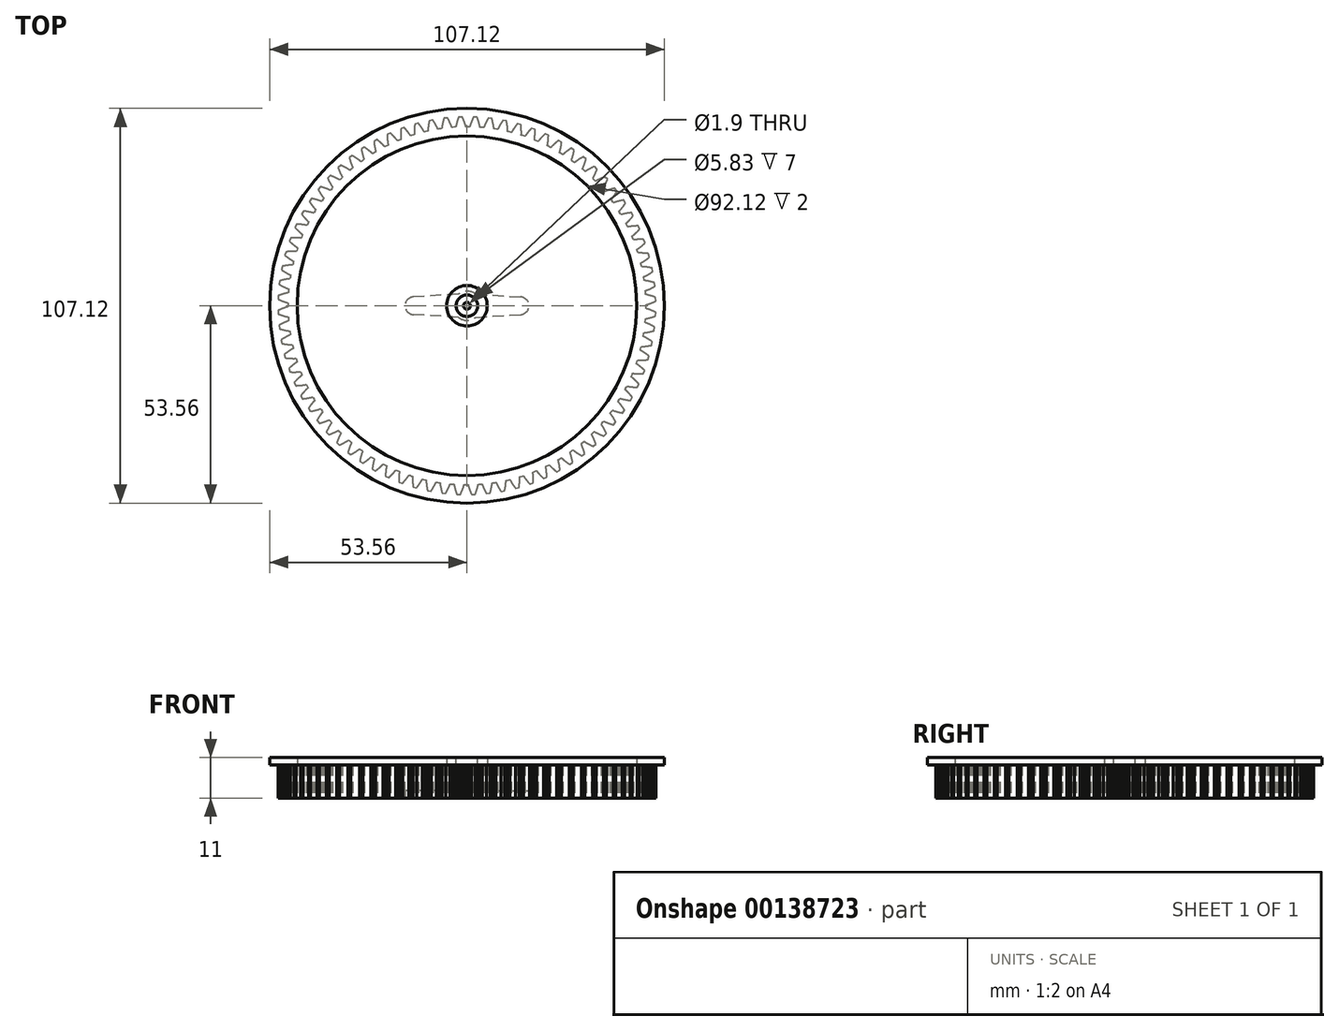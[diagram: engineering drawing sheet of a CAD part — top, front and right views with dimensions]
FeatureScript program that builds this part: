
annotation { "Feature Type Name" : "Feature", "Feature Type Description" : "" }
export const myFeature = defineFeature(function(context is Context, id is Id, definition is map)
    precondition{}
    {
        {
            var Q0;
            Q0=qCreatedBy(makeId("Top.planeOp"),FACE);
            var sketch = newSketch(context, id + "F0", { "sketchPlane" : qUnion([Q0])});
            skLineSegment(sketch, "E0", {"start": v(48.56, 0) * mm, "end": v(48.57, 0.28) * mm});
            skLineSegment(sketch, "E1", {"start": v(48.57, 0.28) * mm, "end": v(48.62, 0.3) * mm});
            skLineSegment(sketch, "E2", {"start": v(48.62, 0.3) * mm, "end": v(48.67, 0.3) * mm});
            skLineSegment(sketch, "E3", {"start": v(48.67, 0.3) * mm, "end": v(48.73, 0.32) * mm});
            skLineSegment(sketch, "E4", {"start": v(48.73, 0.32) * mm, "end": v(48.78, 0.34) * mm});
            skLineSegment(sketch, "E5", {"start": v(48.78, 0.34) * mm, "end": v(48.84, 0.35) * mm});
            skLineSegment(sketch, "E6", {"start": v(48.84, 0.35) * mm, "end": v(48.9, 0.37) * mm});
            skLineSegment(sketch, "E7", {"start": v(48.9, 0.37) * mm, "end": v(48.95, 0.39) * mm});
            skLineSegment(sketch, "E8", {"start": v(48.95, 0.39) * mm, "end": v(49, 0.4) * mm});
            skLineSegment(sketch, "E9", {"start": v(49, 0.4) * mm, "end": v(49.07, 0.42) * mm});
            skLineSegment(sketch, "E10", {"start": v(49.07, 0.42) * mm, "end": v(49.13, 0.44) * mm});
            skLineSegment(sketch, "E11", {"start": v(49.13, 0.44) * mm, "end": v(49.19, 0.46) * mm});
            skLineSegment(sketch, "E12", {"start": v(49.19, 0.46) * mm, "end": v(49.25, 0.48) * mm});
            skLineSegment(sketch, "E13", {"start": v(49.25, 0.48) * mm, "end": v(49.3, 0.5) * mm});
            skLineSegment(sketch, "E14", {"start": v(49.3, 0.5) * mm, "end": v(49.37, 0.52) * mm});
            skLineSegment(sketch, "E15", {"start": v(49.37, 0.52) * mm, "end": v(49.43, 0.54) * mm});
            skLineSegment(sketch, "E16", {"start": v(49.43, 0.54) * mm, "end": v(49.5, 0.56) * mm});
            skLineSegment(sketch, "E17", {"start": v(49.5, 0.56) * mm, "end": v(49.56, 0.59) * mm});
            skLineSegment(sketch, "E18", {"start": v(49.56, 0.59) * mm, "end": v(49.63, 0.61) * mm});
            skLineSegment(sketch, "E19", {"start": v(49.63, 0.61) * mm, "end": v(49.7, 0.63) * mm});
            skLineSegment(sketch, "E20", {"start": v(49.7, 0.63) * mm, "end": v(49.76, 0.66) * mm});
            skLineSegment(sketch, "E21", {"start": v(49.76, 0.66) * mm, "end": v(49.83, 0.68) * mm});
            skLineSegment(sketch, "E22", {"start": v(49.83, 0.68) * mm, "end": v(49.9, 0.7) * mm});
            skLineSegment(sketch, "E23", {"start": v(49.9, 0.7) * mm, "end": v(49.97, 0.73) * mm});
            skLineSegment(sketch, "E24", {"start": v(49.97, 0.73) * mm, "end": v(50.04, 0.76) * mm});
            skLineSegment(sketch, "E25", {"start": v(50.04, 0.76) * mm, "end": v(50.1, 0.79) * mm});
            skLineSegment(sketch, "E26", {"start": v(50.1, 0.79) * mm, "end": v(50.18, 0.82) * mm});
            skLineSegment(sketch, "E27", {"start": v(50.18, 0.82) * mm, "end": v(50.25, 0.84) * mm});
            skLineSegment(sketch, "E28", {"start": v(50.25, 0.84) * mm, "end": v(50.32, 0.87) * mm});
            skLineSegment(sketch, "E29", {"start": v(50.32, 0.87) * mm, "end": v(50.4, 0.9) * mm});
            skLineSegment(sketch, "E30", {"start": v(50.4, 0.9) * mm, "end": v(50.47, 0.93) * mm});
            skLineSegment(sketch, "E31", {"start": v(50.47, 0.93) * mm, "end": v(50.54, 0.97) * mm});
            skLineSegment(sketch, "E32", {"start": v(50.54, 0.97) * mm, "end": v(50.62, 1) * mm});
            skLineSegment(sketch, "E33", {"start": v(50.62, 1) * mm, "end": v(50.7, 1.03) * mm});
            skLineSegment(sketch, "E34", {"start": v(50.7, 1.03) * mm, "end": v(50.77, 1.06) * mm});
            skLineSegment(sketch, "E35", {"start": v(50.77, 1.06) * mm, "end": v(50.85, 1.1) * mm});
            skLineSegment(sketch, "E36", {"start": v(50.85, 1.1) * mm, "end": v(50.93, 1.13) * mm});
            skLineSegment(sketch, "E37", {"start": v(50.93, 1.13) * mm, "end": v(51, 1.17) * mm});
            skLineSegment(sketch, "E38", {"start": v(51, 1.17) * mm, "end": v(51.09, 1.2) * mm});
            skLineSegment(sketch, "E39", {"start": v(51.09, 1.2) * mm, "end": v(51.17, 1.24) * mm});
            skLineSegment(sketch, "E40", {"start": v(51.17, 1.24) * mm, "end": v(51.23, 1.28) * mm});
            skLineSegment(sketch, "E41", {"start": v(51.23, 1.28) * mm, "end": v(51.2, 2.24) * mm});
            skLineSegment(sketch, "E42", {"start": v(51.2, 2.24) * mm, "end": v(51.13, 2.27) * mm});
            skLineSegment(sketch, "E43", {"start": v(51.13, 2.27) * mm, "end": v(51.05, 2.3) * mm});
            skLineSegment(sketch, "E44", {"start": v(51.05, 2.3) * mm, "end": v(50.97, 2.34) * mm});
            skLineSegment(sketch, "E45", {"start": v(50.97, 2.34) * mm, "end": v(50.89, 2.37) * mm});
            skLineSegment(sketch, "E46", {"start": v(50.89, 2.37) * mm, "end": v(50.8, 2.4) * mm});
            skLineSegment(sketch, "E47", {"start": v(50.8, 2.4) * mm, "end": v(50.73, 2.42) * mm});
            skLineSegment(sketch, "E48", {"start": v(50.73, 2.42) * mm, "end": v(50.65, 2.45) * mm});
            skLineSegment(sketch, "E49", {"start": v(50.65, 2.45) * mm, "end": v(50.57, 2.48) * mm});
            skLineSegment(sketch, "E50", {"start": v(50.57, 2.48) * mm, "end": v(50.5, 2.5) * mm});
            skLineSegment(sketch, "E51", {"start": v(50.5, 2.5) * mm, "end": v(50.41, 2.53) * mm});
            skLineSegment(sketch, "E52", {"start": v(50.41, 2.53) * mm, "end": v(50.34, 2.56) * mm});
            skLineSegment(sketch, "E53", {"start": v(50.34, 2.56) * mm, "end": v(50.26, 2.58) * mm});
            skLineSegment(sketch, "E54", {"start": v(50.26, 2.58) * mm, "end": v(50.19, 2.6) * mm});
            skLineSegment(sketch, "E55", {"start": v(50.19, 2.6) * mm, "end": v(50.11, 2.63) * mm});
            skLineSegment(sketch, "E56", {"start": v(50.11, 2.63) * mm, "end": v(50.04, 2.65) * mm});
            skLineSegment(sketch, "E57", {"start": v(50.04, 2.65) * mm, "end": v(49.97, 2.67) * mm});
            skLineSegment(sketch, "E58", {"start": v(49.97, 2.67) * mm, "end": v(49.9, 2.7) * mm});
            skLineSegment(sketch, "E59", {"start": v(49.9, 2.7) * mm, "end": v(49.83, 2.72) * mm});
            skLineSegment(sketch, "E60", {"start": v(49.83, 2.72) * mm, "end": v(49.76, 2.74) * mm});
            skLineSegment(sketch, "E61", {"start": v(49.76, 2.74) * mm, "end": v(49.69, 2.76) * mm});
            skLineSegment(sketch, "E62", {"start": v(49.69, 2.76) * mm, "end": v(49.62, 2.78) * mm});
            skLineSegment(sketch, "E63", {"start": v(49.62, 2.78) * mm, "end": v(49.55, 2.8) * mm});
            skLineSegment(sketch, "E64", {"start": v(49.55, 2.8) * mm, "end": v(49.49, 2.81) * mm});
            skLineSegment(sketch, "E65", {"start": v(49.49, 2.81) * mm, "end": v(49.42, 2.83) * mm});
            skLineSegment(sketch, "E66", {"start": v(49.42, 2.83) * mm, "end": v(49.35, 2.85) * mm});
            skLineSegment(sketch, "E67", {"start": v(49.35, 2.85) * mm, "end": v(49.29, 2.87) * mm});
            skLineSegment(sketch, "E68", {"start": v(49.29, 2.87) * mm, "end": v(49.23, 2.88) * mm});
            skLineSegment(sketch, "E69", {"start": v(49.23, 2.88) * mm, "end": v(49.16, 2.9) * mm});
            skLineSegment(sketch, "E70", {"start": v(49.16, 2.9) * mm, "end": v(49.1, 2.91) * mm});
            skLineSegment(sketch, "E71", {"start": v(49.1, 2.91) * mm, "end": v(49.04, 2.93) * mm});
            skLineSegment(sketch, "E72", {"start": v(49.04, 2.93) * mm, "end": v(48.98, 2.94) * mm});
            skLineSegment(sketch, "E73", {"start": v(48.98, 2.94) * mm, "end": v(48.92, 2.96) * mm});
            skLineSegment(sketch, "E74", {"start": v(48.92, 2.96) * mm, "end": v(48.86, 2.97) * mm});
            skLineSegment(sketch, "E75", {"start": v(48.86, 2.97) * mm, "end": v(48.8, 2.98) * mm});
            skLineSegment(sketch, "E76", {"start": v(48.8, 2.98) * mm, "end": v(48.75, 3) * mm});
            skLineSegment(sketch, "E77", {"start": v(48.75, 3) * mm, "end": v(48.69, 3) * mm});
            skLineSegment(sketch, "E78", {"start": v(48.69, 3) * mm, "end": v(48.63, 3.02) * mm});
            skLineSegment(sketch, "E79", {"start": v(48.63, 3.02) * mm, "end": v(48.58, 3.03) * mm});
            skLineSegment(sketch, "E80", {"start": v(48.58, 3.03) * mm, "end": v(48.53, 3.04) * mm});
            skLineSegment(sketch, "E81", {"start": v(48.53, 3.04) * mm, "end": v(48.47, 3.05) * mm});
            skLineSegment(sketch, "E82", {"start": v(48.47, 3.05) * mm, "end": v(48.45, 3.33) * mm});
            skLineSegment(sketch, "E83", {"start": v(48.45, 3.33) * mm, "end": v(48.41, 3.81) * mm});
            skLineSegment(sketch, "E84", {"start": v(48.41, 3.81) * mm, "end": v(48.4, 4.09) * mm});
            skLineSegment(sketch, "E85", {"start": v(48.4, 4.09) * mm, "end": v(48.45, 4.1) * mm});
            skLineSegment(sketch, "E86", {"start": v(48.45, 4.1) * mm, "end": v(48.5, 4.13) * mm});
            skLineSegment(sketch, "E87", {"start": v(48.5, 4.13) * mm, "end": v(48.55, 4.14) * mm});
            skLineSegment(sketch, "E88", {"start": v(48.55, 4.14) * mm, "end": v(48.6, 4.16) * mm});
            skLineSegment(sketch, "E89", {"start": v(48.6, 4.16) * mm, "end": v(48.66, 4.19) * mm});
            skLineSegment(sketch, "E90", {"start": v(48.66, 4.19) * mm, "end": v(48.71, 4.2) * mm});
            skLineSegment(sketch, "E91", {"start": v(48.71, 4.2) * mm, "end": v(48.77, 4.23) * mm});
            skLineSegment(sketch, "E92", {"start": v(48.77, 4.23) * mm, "end": v(48.82, 4.25) * mm});
            skLineSegment(sketch, "E93", {"start": v(48.82, 4.25) * mm, "end": v(48.88, 4.27) * mm});
            skLineSegment(sketch, "E94", {"start": v(48.88, 4.27) * mm, "end": v(48.94, 4.3) * mm});
            skLineSegment(sketch, "E95", {"start": v(48.94, 4.3) * mm, "end": v(49, 4.32) * mm});
            skLineSegment(sketch, "E96", {"start": v(49, 4.32) * mm, "end": v(49.06, 4.34) * mm});
            skLineSegment(sketch, "E97", {"start": v(49.06, 4.34) * mm, "end": v(49.12, 4.37) * mm});
            skLineSegment(sketch, "E98", {"start": v(49.12, 4.37) * mm, "end": v(49.18, 4.4) * mm});
            skLineSegment(sketch, "E99", {"start": v(49.18, 4.4) * mm, "end": v(49.24, 4.42) * mm});
            skLineSegment(sketch, "E100", {"start": v(49.24, 4.42) * mm, "end": v(49.3, 4.45) * mm});
            skLineSegment(sketch, "E101", {"start": v(49.3, 4.45) * mm, "end": v(49.36, 4.47) * mm});
            skLineSegment(sketch, "E102", {"start": v(49.36, 4.47) * mm, "end": v(49.43, 4.5) * mm});
            skLineSegment(sketch, "E103", {"start": v(49.43, 4.5) * mm, "end": v(49.5, 4.53) * mm});
            skLineSegment(sketch, "E104", {"start": v(49.5, 4.53) * mm, "end": v(49.56, 4.56) * mm});
            skLineSegment(sketch, "E105", {"start": v(49.56, 4.56) * mm, "end": v(49.62, 4.6) * mm});
            skLineSegment(sketch, "E106", {"start": v(49.62, 4.6) * mm, "end": v(49.69, 4.62) * mm});
            skLineSegment(sketch, "E107", {"start": v(49.69, 4.62) * mm, "end": v(49.75, 4.65) * mm});
            skLineSegment(sketch, "E108", {"start": v(49.75, 4.65) * mm, "end": v(49.82, 4.68) * mm});
            skLineSegment(sketch, "E109", {"start": v(49.82, 4.68) * mm, "end": v(49.89, 4.72) * mm});
            skLineSegment(sketch, "E110", {"start": v(49.89, 4.72) * mm, "end": v(49.96, 4.75) * mm});
            skLineSegment(sketch, "E111", {"start": v(49.96, 4.75) * mm, "end": v(50.03, 4.78) * mm});
            skLineSegment(sketch, "E112", {"start": v(50.03, 4.78) * mm, "end": v(50.1, 4.82) * mm});
            skLineSegment(sketch, "E113", {"start": v(50.1, 4.82) * mm, "end": v(50.17, 4.85) * mm});
            skLineSegment(sketch, "E114", {"start": v(50.17, 4.85) * mm, "end": v(50.24, 4.9) * mm});
            skLineSegment(sketch, "E115", {"start": v(50.24, 4.9) * mm, "end": v(50.31, 4.93) * mm});
            skLineSegment(sketch, "E116", {"start": v(50.31, 4.93) * mm, "end": v(50.38, 4.97) * mm});
            skLineSegment(sketch, "E117", {"start": v(50.38, 4.97) * mm, "end": v(50.46, 5) * mm});
            skLineSegment(sketch, "E118", {"start": v(50.46, 5) * mm, "end": v(50.53, 5.04) * mm});
            skLineSegment(sketch, "E119", {"start": v(50.53, 5.04) * mm, "end": v(50.6, 5.08) * mm});
            skLineSegment(sketch, "E120", {"start": v(50.6, 5.08) * mm, "end": v(50.68, 5.12) * mm});
            skLineSegment(sketch, "E121", {"start": v(50.68, 5.12) * mm, "end": v(50.76, 5.16) * mm});
            skLineSegment(sketch, "E122", {"start": v(50.76, 5.16) * mm, "end": v(50.83, 5.2) * mm});
            skLineSegment(sketch, "E123", {"start": v(50.83, 5.2) * mm, "end": v(50.91, 5.25) * mm});
            skLineSegment(sketch, "E124", {"start": v(50.91, 5.25) * mm, "end": v(50.98, 5.3) * mm});
            skLineSegment(sketch, "E125", {"start": v(50.98, 5.3) * mm, "end": v(50.87, 6.25) * mm});
            skLineSegment(sketch, "E126", {"start": v(50.87, 6.25) * mm, "end": v(50.8, 6.28) * mm});
            skLineSegment(sketch, "E127", {"start": v(50.8, 6.28) * mm, "end": v(50.7, 6.3) * mm});
            skLineSegment(sketch, "E128", {"start": v(50.7, 6.3) * mm, "end": v(50.63, 6.33) * mm});
            skLineSegment(sketch, "E129", {"start": v(50.63, 6.33) * mm, "end": v(50.54, 6.35) * mm});
            skLineSegment(sketch, "E130", {"start": v(50.54, 6.35) * mm, "end": v(50.46, 6.37) * mm});
            skLineSegment(sketch, "E131", {"start": v(50.46, 6.37) * mm, "end": v(50.38, 6.4) * mm});
            skLineSegment(sketch, "E132", {"start": v(50.38, 6.4) * mm, "end": v(50.3, 6.42) * mm});
            skLineSegment(sketch, "E133", {"start": v(50.3, 6.42) * mm, "end": v(50.22, 6.44) * mm});
            skLineSegment(sketch, "E134", {"start": v(50.22, 6.44) * mm, "end": v(50.14, 6.46) * mm});
            skLineSegment(sketch, "E135", {"start": v(50.14, 6.46) * mm, "end": v(50.06, 6.48) * mm});
            skLineSegment(sketch, "E136", {"start": v(50.06, 6.48) * mm, "end": v(49.98, 6.5) * mm});
            skLineSegment(sketch, "E137", {"start": v(49.98, 6.5) * mm, "end": v(49.9, 6.52) * mm});
            skLineSegment(sketch, "E138", {"start": v(49.9, 6.52) * mm, "end": v(49.83, 6.53) * mm});
            skLineSegment(sketch, "E139", {"start": v(49.83, 6.53) * mm, "end": v(49.75, 6.55) * mm});
            skLineSegment(sketch, "E140", {"start": v(49.75, 6.55) * mm, "end": v(49.68, 6.57) * mm});
            skLineSegment(sketch, "E141", {"start": v(49.68, 6.57) * mm, "end": v(49.6, 6.59) * mm});
            skLineSegment(sketch, "E142", {"start": v(49.6, 6.59) * mm, "end": v(49.53, 6.6) * mm});
            skLineSegment(sketch, "E143", {"start": v(49.53, 6.6) * mm, "end": v(49.46, 6.62) * mm});
            skLineSegment(sketch, "E144", {"start": v(49.46, 6.62) * mm, "end": v(49.39, 6.63) * mm});
            skLineSegment(sketch, "E145", {"start": v(49.39, 6.63) * mm, "end": v(49.32, 6.65) * mm});
            skLineSegment(sketch, "E146", {"start": v(49.32, 6.65) * mm, "end": v(49.25, 6.66) * mm});
            skLineSegment(sketch, "E147", {"start": v(49.25, 6.66) * mm, "end": v(49.18, 6.67) * mm});
            skLineSegment(sketch, "E148", {"start": v(49.18, 6.67) * mm, "end": v(49.11, 6.69) * mm});
            skLineSegment(sketch, "E149", {"start": v(49.11, 6.69) * mm, "end": v(49.05, 6.7) * mm});
            skLineSegment(sketch, "E150", {"start": v(49.05, 6.7) * mm, "end": v(48.98, 6.71) * mm});
            skLineSegment(sketch, "E151", {"start": v(48.98, 6.71) * mm, "end": v(48.91, 6.72) * mm});
            skLineSegment(sketch, "E152", {"start": v(48.91, 6.72) * mm, "end": v(48.85, 6.74) * mm});
            skLineSegment(sketch, "E153", {"start": v(48.85, 6.74) * mm, "end": v(48.78, 6.75) * mm});
            skLineSegment(sketch, "E154", {"start": v(48.78, 6.75) * mm, "end": v(48.72, 6.76) * mm});
            skLineSegment(sketch, "E155", {"start": v(48.72, 6.76) * mm, "end": v(48.66, 6.77) * mm});
            skLineSegment(sketch, "E156", {"start": v(48.66, 6.77) * mm, "end": v(48.6, 6.78) * mm});
            skLineSegment(sketch, "E157", {"start": v(48.6, 6.78) * mm, "end": v(48.54, 6.79) * mm});
            skLineSegment(sketch, "E158", {"start": v(48.54, 6.79) * mm, "end": v(48.48, 6.8) * mm});
            skLineSegment(sketch, "E159", {"start": v(48.48, 6.8) * mm, "end": v(48.42, 6.8) * mm});
            skLineSegment(sketch, "E160", {"start": v(48.42, 6.8) * mm, "end": v(48.36, 6.81) * mm});
            skLineSegment(sketch, "E161", {"start": v(48.36, 6.81) * mm, "end": v(48.3, 6.82) * mm});
            skLineSegment(sketch, "E162", {"start": v(48.3, 6.82) * mm, "end": v(48.25, 6.83) * mm});
            skLineSegment(sketch, "E163", {"start": v(48.25, 6.83) * mm, "end": v(48.2, 6.83) * mm});
            skLineSegment(sketch, "E164", {"start": v(48.2, 6.83) * mm, "end": v(48.14, 6.84) * mm});
            skLineSegment(sketch, "E165", {"start": v(48.14, 6.84) * mm, "end": v(48.08, 6.85) * mm});
            skLineSegment(sketch, "E166", {"start": v(48.08, 6.85) * mm, "end": v(48.04, 7.12) * mm});
            skLineSegment(sketch, "E167", {"start": v(48.04, 7.12) * mm, "end": v(47.96, 7.6) * mm});
            skLineSegment(sketch, "E168", {"start": v(47.96, 7.6) * mm, "end": v(47.93, 7.87) * mm});
            skLineSegment(sketch, "E169", {"start": v(47.93, 7.87) * mm, "end": v(47.98, 7.9) * mm});
            skLineSegment(sketch, "E170", {"start": v(47.98, 7.9) * mm, "end": v(48.03, 7.92) * mm});
            skLineSegment(sketch, "E171", {"start": v(48.03, 7.92) * mm, "end": v(48.08, 7.94) * mm});
            skLineSegment(sketch, "E172", {"start": v(48.08, 7.94) * mm, "end": v(48.13, 7.97) * mm});
            skLineSegment(sketch, "E173", {"start": v(48.13, 7.97) * mm, "end": v(48.18, 7.99) * mm});
            skLineSegment(sketch, "E174", {"start": v(48.18, 7.99) * mm, "end": v(48.23, 8.01) * mm});
            skLineSegment(sketch, "E175", {"start": v(48.23, 8.01) * mm, "end": v(48.29, 8.04) * mm});
            skLineSegment(sketch, "E176", {"start": v(48.29, 8.04) * mm, "end": v(48.34, 8.07) * mm});
            skLineSegment(sketch, "E177", {"start": v(48.34, 8.07) * mm, "end": v(48.4, 8.1) * mm});
            skLineSegment(sketch, "E178", {"start": v(48.4, 8.1) * mm, "end": v(48.45, 8.12) * mm});
            skLineSegment(sketch, "E179", {"start": v(48.45, 8.12) * mm, "end": v(48.5, 8.15) * mm});
            skLineSegment(sketch, "E180", {"start": v(48.5, 8.15) * mm, "end": v(48.56, 8.18) * mm});
            skLineSegment(sketch, "E181", {"start": v(48.56, 8.18) * mm, "end": v(48.62, 8.2) * mm});
            skLineSegment(sketch, "E182", {"start": v(48.62, 8.2) * mm, "end": v(48.68, 8.24) * mm});
            skLineSegment(sketch, "E183", {"start": v(48.68, 8.24) * mm, "end": v(48.74, 8.27) * mm});
            skLineSegment(sketch, "E184", {"start": v(48.74, 8.27) * mm, "end": v(48.8, 8.3) * mm});
            skLineSegment(sketch, "E185", {"start": v(48.8, 8.3) * mm, "end": v(48.86, 8.33) * mm});
            skLineSegment(sketch, "E186", {"start": v(48.86, 8.33) * mm, "end": v(48.92, 8.37) * mm});
            skLineSegment(sketch, "E187", {"start": v(48.92, 8.37) * mm, "end": v(48.98, 8.4) * mm});
            skLineSegment(sketch, "E188", {"start": v(48.98, 8.4) * mm, "end": v(49.04, 8.43) * mm});
            skLineSegment(sketch, "E189", {"start": v(49.04, 8.43) * mm, "end": v(49.1, 8.47) * mm});
            skLineSegment(sketch, "E190", {"start": v(49.1, 8.47) * mm, "end": v(49.17, 8.5) * mm});
            skLineSegment(sketch, "E191", {"start": v(49.17, 8.5) * mm, "end": v(49.24, 8.54) * mm});
            skLineSegment(sketch, "E192", {"start": v(49.24, 8.54) * mm, "end": v(49.3, 8.58) * mm});
            skLineSegment(sketch, "E193", {"start": v(49.3, 8.58) * mm, "end": v(49.37, 8.62) * mm});
            skLineSegment(sketch, "E194", {"start": v(49.37, 8.62) * mm, "end": v(49.43, 8.66) * mm});
            skLineSegment(sketch, "E195", {"start": v(49.43, 8.66) * mm, "end": v(49.5, 8.7) * mm});
            skLineSegment(sketch, "E196", {"start": v(49.5, 8.7) * mm, "end": v(49.57, 8.73) * mm});
            skLineSegment(sketch, "E197", {"start": v(49.57, 8.73) * mm, "end": v(49.63, 8.78) * mm});
            skLineSegment(sketch, "E198", {"start": v(49.63, 8.78) * mm, "end": v(49.7, 8.82) * mm});
            skLineSegment(sketch, "E199", {"start": v(49.7, 8.82) * mm, "end": v(49.77, 8.86) * mm});
            skLineSegment(sketch, "E200", {"start": v(49.77, 8.86) * mm, "end": v(49.84, 8.9) * mm});
            skLineSegment(sketch, "E201", {"start": v(49.84, 8.9) * mm, "end": v(49.91, 8.95) * mm});
            skLineSegment(sketch, "E202", {"start": v(49.91, 8.95) * mm, "end": v(49.98, 9) * mm});
            skLineSegment(sketch, "E203", {"start": v(49.98, 9) * mm, "end": v(50.05, 9.04) * mm});
            skLineSegment(sketch, "E204", {"start": v(50.05, 9.04) * mm, "end": v(50.12, 9.08) * mm});
            skLineSegment(sketch, "E205", {"start": v(50.12, 9.08) * mm, "end": v(50.2, 9.13) * mm});
            skLineSegment(sketch, "E206", {"start": v(50.2, 9.13) * mm, "end": v(50.27, 9.18) * mm});
            skLineSegment(sketch, "E207", {"start": v(50.27, 9.18) * mm, "end": v(50.34, 9.23) * mm});
            skLineSegment(sketch, "E208", {"start": v(50.34, 9.23) * mm, "end": v(50.4, 9.28) * mm});
            skLineSegment(sketch, "E209", {"start": v(50.4, 9.28) * mm, "end": v(50.22, 10.22) * mm});
            skLineSegment(sketch, "E210", {"start": v(50.22, 10.22) * mm, "end": v(50.15, 10.24) * mm});
            skLineSegment(sketch, "E211", {"start": v(50.15, 10.24) * mm, "end": v(50.06, 10.26) * mm});
            skLineSegment(sketch, "E212", {"start": v(50.06, 10.26) * mm, "end": v(49.97, 10.28) * mm});
            skLineSegment(sketch, "E213", {"start": v(49.97, 10.28) * mm, "end": v(49.89, 10.3) * mm});
            skLineSegment(sketch, "E214", {"start": v(49.89, 10.3) * mm, "end": v(49.8, 10.31) * mm});
            skLineSegment(sketch, "E215", {"start": v(49.8, 10.31) * mm, "end": v(49.72, 10.33) * mm});
            skLineSegment(sketch, "E216", {"start": v(49.72, 10.33) * mm, "end": v(49.64, 10.34) * mm});
            skLineSegment(sketch, "E217", {"start": v(49.64, 10.34) * mm, "end": v(49.56, 10.36) * mm});
            skLineSegment(sketch, "E218", {"start": v(49.56, 10.36) * mm, "end": v(49.48, 10.37) * mm});
            skLineSegment(sketch, "E219", {"start": v(49.48, 10.37) * mm, "end": v(49.4, 10.39) * mm});
            skLineSegment(sketch, "E220", {"start": v(49.4, 10.39) * mm, "end": v(49.32, 10.4) * mm});
            skLineSegment(sketch, "E221", {"start": v(49.32, 10.4) * mm, "end": v(49.24, 10.41) * mm});
            skLineSegment(sketch, "E222", {"start": v(49.24, 10.41) * mm, "end": v(49.16, 10.42) * mm});
            skLineSegment(sketch, "E223", {"start": v(49.16, 10.42) * mm, "end": v(49.09, 10.44) * mm});
            skLineSegment(sketch, "E224", {"start": v(49.09, 10.44) * mm, "end": v(49.01, 10.45) * mm});
            skLineSegment(sketch, "E225", {"start": v(49.01, 10.45) * mm, "end": v(48.94, 10.46) * mm});
            skLineSegment(sketch, "E226", {"start": v(48.94, 10.46) * mm, "end": v(48.86, 10.47) * mm});
            skLineSegment(sketch, "E227", {"start": v(48.86, 10.47) * mm, "end": v(48.79, 10.48) * mm});
            skLineSegment(sketch, "E228", {"start": v(48.79, 10.48) * mm, "end": v(48.72, 10.49) * mm});
            skLineSegment(sketch, "E229", {"start": v(48.72, 10.49) * mm, "end": v(48.65, 10.5) * mm});
            skLineSegment(sketch, "E230", {"start": v(48.65, 10.5) * mm, "end": v(48.57, 10.5) * mm});
            skLineSegment(sketch, "E231", {"start": v(48.57, 10.5) * mm, "end": v(48.5, 10.51) * mm});
            skLineSegment(sketch, "E232", {"start": v(48.5, 10.51) * mm, "end": v(48.44, 10.52) * mm});
            skLineSegment(sketch, "E233", {"start": v(48.44, 10.52) * mm, "end": v(48.37, 10.53) * mm});
            skLineSegment(sketch, "E234", {"start": v(48.37, 10.53) * mm, "end": v(48.3, 10.54) * mm});
            skLineSegment(sketch, "E235", {"start": v(48.3, 10.54) * mm, "end": v(48.23, 10.54) * mm});
            skLineSegment(sketch, "E236", {"start": v(48.23, 10.54) * mm, "end": v(48.17, 10.55) * mm});
            skLineSegment(sketch, "E237", {"start": v(48.17, 10.55) * mm, "end": v(48.1, 10.55) * mm});
            skLineSegment(sketch, "E238", {"start": v(48.1, 10.55) * mm, "end": v(48.04, 10.56) * mm});
            skLineSegment(sketch, "E239", {"start": v(48.04, 10.56) * mm, "end": v(47.98, 10.56) * mm});
            skLineSegment(sketch, "E240", {"start": v(47.98, 10.56) * mm, "end": v(47.92, 10.57) * mm});
            skLineSegment(sketch, "E241", {"start": v(47.92, 10.57) * mm, "end": v(47.85, 10.57) * mm});
            skLineSegment(sketch, "E242", {"start": v(47.85, 10.57) * mm, "end": v(47.8, 10.58) * mm});
            skLineSegment(sketch, "E243", {"start": v(47.8, 10.58) * mm, "end": v(47.74, 10.58) * mm});
            skLineSegment(sketch, "E244", {"start": v(47.74, 10.58) * mm, "end": v(47.68, 10.59) * mm});
            skLineSegment(sketch, "E245", {"start": v(47.68, 10.59) * mm, "end": v(47.62, 10.59) * mm});
            skLineSegment(sketch, "E246", {"start": v(47.62, 10.59) * mm, "end": v(47.56, 10.6) * mm});
            skLineSegment(sketch, "E247", {"start": v(47.56, 10.6) * mm, "end": v(47.5, 10.6) * mm});
            skLineSegment(sketch, "E248", {"start": v(47.5, 10.6) * mm, "end": v(47.45, 10.6) * mm});
            skLineSegment(sketch, "E249", {"start": v(47.45, 10.6) * mm, "end": v(47.4, 10.6) * mm});
            skLineSegment(sketch, "E250", {"start": v(47.4, 10.6) * mm, "end": v(47.33, 10.87) * mm});
            skLineSegment(sketch, "E251", {"start": v(47.33, 10.87) * mm, "end": v(47.22, 11.34) * mm});
            skLineSegment(sketch, "E252", {"start": v(47.22, 11.34) * mm, "end": v(47.16, 11.6) * mm});
            skLineSegment(sketch, "E253", {"start": v(47.16, 11.6) * mm, "end": v(47.2, 11.64) * mm});
            skLineSegment(sketch, "E254", {"start": v(47.2, 11.64) * mm, "end": v(47.26, 11.66) * mm});
            skLineSegment(sketch, "E255", {"start": v(47.26, 11.66) * mm, "end": v(47.3, 11.69) * mm});
            skLineSegment(sketch, "E256", {"start": v(47.3, 11.69) * mm, "end": v(47.35, 11.72) * mm});
            skLineSegment(sketch, "E257", {"start": v(47.35, 11.72) * mm, "end": v(47.4, 11.75) * mm});
            skLineSegment(sketch, "E258", {"start": v(47.4, 11.75) * mm, "end": v(47.46, 11.77) * mm});
            skLineSegment(sketch, "E259", {"start": v(47.46, 11.77) * mm, "end": v(47.5, 11.8) * mm});
            skLineSegment(sketch, "E260", {"start": v(47.5, 11.8) * mm, "end": v(47.56, 11.83) * mm});
            skLineSegment(sketch, "E261", {"start": v(47.56, 11.83) * mm, "end": v(47.61, 11.87) * mm});
            skLineSegment(sketch, "E262", {"start": v(47.61, 11.87) * mm, "end": v(47.66, 11.9) * mm});
            skLineSegment(sketch, "E263", {"start": v(47.66, 11.9) * mm, "end": v(47.72, 11.93) * mm});
            skLineSegment(sketch, "E264", {"start": v(47.72, 11.93) * mm, "end": v(47.77, 11.96) * mm});
            skLineSegment(sketch, "E265", {"start": v(47.77, 11.96) * mm, "end": v(47.83, 12) * mm});
            skLineSegment(sketch, "E266", {"start": v(47.83, 12) * mm, "end": v(47.88, 12.03) * mm});
            skLineSegment(sketch, "E267", {"start": v(47.88, 12.03) * mm, "end": v(47.94, 12.07) * mm});
            skLineSegment(sketch, "E268", {"start": v(47.94, 12.07) * mm, "end": v(48, 12.1) * mm});
            skLineSegment(sketch, "E269", {"start": v(48, 12.1) * mm, "end": v(48.06, 12.14) * mm});
            skLineSegment(sketch, "E270", {"start": v(48.06, 12.14) * mm, "end": v(48.11, 12.18) * mm});
            skLineSegment(sketch, "E271", {"start": v(48.11, 12.18) * mm, "end": v(48.17, 12.22) * mm});
            skLineSegment(sketch, "E272", {"start": v(48.17, 12.22) * mm, "end": v(48.23, 12.26) * mm});
            skLineSegment(sketch, "E273", {"start": v(48.23, 12.26) * mm, "end": v(48.3, 12.3) * mm});
            skLineSegment(sketch, "E274", {"start": v(48.3, 12.3) * mm, "end": v(48.35, 12.34) * mm});
            skLineSegment(sketch, "E275", {"start": v(48.35, 12.34) * mm, "end": v(48.41, 12.38) * mm});
            skLineSegment(sketch, "E276", {"start": v(48.41, 12.38) * mm, "end": v(48.48, 12.42) * mm});
            skLineSegment(sketch, "E277", {"start": v(48.48, 12.42) * mm, "end": v(48.54, 12.46) * mm});
            skLineSegment(sketch, "E278", {"start": v(48.54, 12.46) * mm, "end": v(48.6, 12.5) * mm});
            skLineSegment(sketch, "E279", {"start": v(48.6, 12.5) * mm, "end": v(48.66, 12.55) * mm});
            skLineSegment(sketch, "E280", {"start": v(48.66, 12.55) * mm, "end": v(48.73, 12.6) * mm});
            skLineSegment(sketch, "E281", {"start": v(48.73, 12.6) * mm, "end": v(48.8, 12.64) * mm});
            skLineSegment(sketch, "E282", {"start": v(48.8, 12.64) * mm, "end": v(48.86, 12.69) * mm});
            skLineSegment(sketch, "E283", {"start": v(48.86, 12.69) * mm, "end": v(48.92, 12.74) * mm});
            skLineSegment(sketch, "E284", {"start": v(48.92, 12.74) * mm, "end": v(48.99, 12.79) * mm});
            skLineSegment(sketch, "E285", {"start": v(48.99, 12.79) * mm, "end": v(49.05, 12.84) * mm});
            skLineSegment(sketch, "E286", {"start": v(49.05, 12.84) * mm, "end": v(49.12, 12.89) * mm});
            skLineSegment(sketch, "E287", {"start": v(49.12, 12.89) * mm, "end": v(49.19, 12.94) * mm});
            skLineSegment(sketch, "E288", {"start": v(49.19, 12.94) * mm, "end": v(49.26, 12.99) * mm});
            skLineSegment(sketch, "E289", {"start": v(49.26, 12.99) * mm, "end": v(49.32, 13.04) * mm});
            skLineSegment(sketch, "E290", {"start": v(49.32, 13.04) * mm, "end": v(49.4, 13.1) * mm});
            skLineSegment(sketch, "E291", {"start": v(49.4, 13.1) * mm, "end": v(49.46, 13.15) * mm});
            skLineSegment(sketch, "E292", {"start": v(49.46, 13.15) * mm, "end": v(49.52, 13.2) * mm});
            skLineSegment(sketch, "E293", {"start": v(49.52, 13.2) * mm, "end": v(49.26, 14.13) * mm});
            skLineSegment(sketch, "E294", {"start": v(49.26, 14.13) * mm, "end": v(49.19, 14.15) * mm});
            skLineSegment(sketch, "E295", {"start": v(49.19, 14.15) * mm, "end": v(49.1, 14.16) * mm});
            skLineSegment(sketch, "E296", {"start": v(49.1, 14.16) * mm, "end": v(49.01, 14.17) * mm});
            skLineSegment(sketch, "E297", {"start": v(49.01, 14.17) * mm, "end": v(48.93, 14.18) * mm});
            skLineSegment(sketch, "E298", {"start": v(48.93, 14.18) * mm, "end": v(48.84, 14.19) * mm});
            skLineSegment(sketch, "E299", {"start": v(48.84, 14.19) * mm, "end": v(48.76, 14.2) * mm});
            skLineSegment(sketch, "E300", {"start": v(48.76, 14.2) * mm, "end": v(48.67, 14.2) * mm});
            skLineSegment(sketch, "E301", {"start": v(48.67, 14.2) * mm, "end": v(48.6, 14.21) * mm});
            skLineSegment(sketch, "E302", {"start": v(48.6, 14.21) * mm, "end": v(48.51, 14.22) * mm});
            skLineSegment(sketch, "E303", {"start": v(48.51, 14.22) * mm, "end": v(48.43, 14.23) * mm});
            skLineSegment(sketch, "E304", {"start": v(48.43, 14.23) * mm, "end": v(48.35, 14.24) * mm});
            skLineSegment(sketch, "E305", {"start": v(48.35, 14.24) * mm, "end": v(48.27, 14.24) * mm});
            skLineSegment(sketch, "E306", {"start": v(48.27, 14.24) * mm, "end": v(48.2, 14.25) * mm});
            skLineSegment(sketch, "E307", {"start": v(48.2, 14.25) * mm, "end": v(48.12, 14.25) * mm});
            skLineSegment(sketch, "E308", {"start": v(48.12, 14.25) * mm, "end": v(48.04, 14.26) * mm});
            skLineSegment(sketch, "E309", {"start": v(48.04, 14.26) * mm, "end": v(47.96, 14.26) * mm});
            skLineSegment(sketch, "E310", {"start": v(47.96, 14.26) * mm, "end": v(47.9, 14.27) * mm});
            skLineSegment(sketch, "E311", {"start": v(47.9, 14.27) * mm, "end": v(47.82, 14.27) * mm});
            skLineSegment(sketch, "E312", {"start": v(47.82, 14.27) * mm, "end": v(47.74, 14.28) * mm});
            skLineSegment(sketch, "E313", {"start": v(47.74, 14.28) * mm, "end": v(47.67, 14.28) * mm});
            skLineSegment(sketch, "E314", {"start": v(47.67, 14.28) * mm, "end": v(47.6, 14.28) * mm});
            skLineSegment(sketch, "E315", {"start": v(47.6, 14.28) * mm, "end": v(47.53, 14.29) * mm});
            skLineSegment(sketch, "E316", {"start": v(47.53, 14.29) * mm, "end": v(47.46, 14.29) * mm});
            skLineSegment(sketch, "E317", {"start": v(47.46, 14.29) * mm, "end": v(47.4, 14.3) * mm});
            skLineSegment(sketch, "E318", {"start": v(47.4, 14.3) * mm, "end": v(47.33, 14.3) * mm});
            skLineSegment(sketch, "E319", {"start": v(47.33, 14.3) * mm, "end": v(47.26, 14.3) * mm});
            skLineSegment(sketch, "E320", {"start": v(47.26, 14.3) * mm, "end": v(47.2, 14.3) * mm});
            skLineSegment(sketch, "E321", {"start": v(47.2, 14.3) * mm, "end": v(47.13, 14.3) * mm});
            skLineSegment(sketch, "E322", {"start": v(47.13, 14.3) * mm, "end": v(47.06, 14.3) * mm});
            skLineSegment(sketch, "E323", {"start": v(47.06, 14.3) * mm, "end": v(47, 14.3) * mm});
            skLineSegment(sketch, "E324", {"start": v(47, 14.3) * mm, "end": v(46.94, 14.3) * mm});
            skLineSegment(sketch, "E325", {"start": v(46.94, 14.3) * mm, "end": v(46.88, 14.3) * mm});
            skLineSegment(sketch, "E326", {"start": v(46.88, 14.3) * mm, "end": v(46.82, 14.3) * mm});
            skLineSegment(sketch, "E327", {"start": v(46.82, 14.3) * mm, "end": v(46.76, 14.3) * mm});
            skLineSegment(sketch, "E328", {"start": v(46.76, 14.3) * mm, "end": v(46.7, 14.3) * mm});
            skLineSegment(sketch, "E329", {"start": v(46.7, 14.3) * mm, "end": v(46.64, 14.3) * mm});
            skLineSegment(sketch, "E330", {"start": v(46.64, 14.3) * mm, "end": v(46.58, 14.3) * mm});
            skLineSegment(sketch, "E331", {"start": v(46.58, 14.3) * mm, "end": v(46.53, 14.29) * mm});
            skLineSegment(sketch, "E332", {"start": v(46.53, 14.29) * mm, "end": v(46.47, 14.29) * mm});
            skLineSegment(sketch, "E333", {"start": v(46.47, 14.29) * mm, "end": v(46.42, 14.28) * mm});
            skLineSegment(sketch, "E334", {"start": v(46.42, 14.28) * mm, "end": v(46.33, 14.55) * mm});
            skLineSegment(sketch, "E335", {"start": v(46.33, 14.55) * mm, "end": v(46.19, 15) * mm});
            skLineSegment(sketch, "E336", {"start": v(46.19, 15) * mm, "end": v(46.1, 15.27) * mm});
            skLineSegment(sketch, "E337", {"start": v(46.1, 15.27) * mm, "end": v(46.15, 15.3) * mm});
            skLineSegment(sketch, "E338", {"start": v(46.15, 15.3) * mm, "end": v(46.2, 15.33) * mm});
            skLineSegment(sketch, "E339", {"start": v(46.2, 15.33) * mm, "end": v(46.24, 15.36) * mm});
            skLineSegment(sketch, "E340", {"start": v(46.24, 15.36) * mm, "end": v(46.29, 15.4) * mm});
            skLineSegment(sketch, "E341", {"start": v(46.29, 15.4) * mm, "end": v(46.34, 15.43) * mm});
            skLineSegment(sketch, "E342", {"start": v(46.34, 15.43) * mm, "end": v(46.39, 15.46) * mm});
            skLineSegment(sketch, "E343", {"start": v(46.39, 15.46) * mm, "end": v(46.43, 15.5) * mm});
            skLineSegment(sketch, "E344", {"start": v(46.43, 15.5) * mm, "end": v(46.48, 15.53) * mm});
            skLineSegment(sketch, "E345", {"start": v(46.48, 15.53) * mm, "end": v(46.53, 15.57) * mm});
            skLineSegment(sketch, "E346", {"start": v(46.53, 15.57) * mm, "end": v(46.58, 15.6) * mm});
            skLineSegment(sketch, "E347", {"start": v(46.58, 15.6) * mm, "end": v(46.64, 15.64) * mm});
            skLineSegment(sketch, "E348", {"start": v(46.64, 15.64) * mm, "end": v(46.69, 15.68) * mm});
            skLineSegment(sketch, "E349", {"start": v(46.69, 15.68) * mm, "end": v(46.74, 15.71) * mm});
            skLineSegment(sketch, "E350", {"start": v(46.74, 15.71) * mm, "end": v(46.8, 15.75) * mm});
            skLineSegment(sketch, "E351", {"start": v(46.8, 15.75) * mm, "end": v(46.85, 15.8) * mm});
            skLineSegment(sketch, "E352", {"start": v(46.85, 15.8) * mm, "end": v(46.9, 15.83) * mm});
            skLineSegment(sketch, "E353", {"start": v(46.9, 15.83) * mm, "end": v(46.95, 15.87) * mm});
            skLineSegment(sketch, "E354", {"start": v(46.95, 15.87) * mm, "end": v(47.01, 15.92) * mm});
            skLineSegment(sketch, "E355", {"start": v(47.01, 15.92) * mm, "end": v(47.07, 15.96) * mm});
            skLineSegment(sketch, "E356", {"start": v(47.07, 15.96) * mm, "end": v(47.12, 16) * mm});
            skLineSegment(sketch, "E357", {"start": v(47.12, 16) * mm, "end": v(47.18, 16.05) * mm});
            skLineSegment(sketch, "E358", {"start": v(47.18, 16.05) * mm, "end": v(47.24, 16.1) * mm});
            skLineSegment(sketch, "E359", {"start": v(47.24, 16.1) * mm, "end": v(47.3, 16.14) * mm});
            skLineSegment(sketch, "E360", {"start": v(47.3, 16.14) * mm, "end": v(47.35, 16.19) * mm});
            skLineSegment(sketch, "E361", {"start": v(47.35, 16.19) * mm, "end": v(47.41, 16.23) * mm});
            skLineSegment(sketch, "E362", {"start": v(47.41, 16.23) * mm, "end": v(47.47, 16.28) * mm});
            skLineSegment(sketch, "E363", {"start": v(47.47, 16.28) * mm, "end": v(47.53, 16.33) * mm});
            skLineSegment(sketch, "E364", {"start": v(47.53, 16.33) * mm, "end": v(47.59, 16.38) * mm});
            skLineSegment(sketch, "E365", {"start": v(47.59, 16.38) * mm, "end": v(47.65, 16.43) * mm});
            skLineSegment(sketch, "E366", {"start": v(47.65, 16.43) * mm, "end": v(47.71, 16.48) * mm});
            skLineSegment(sketch, "E367", {"start": v(47.71, 16.48) * mm, "end": v(47.77, 16.54) * mm});
            skLineSegment(sketch, "E368", {"start": v(47.77, 16.54) * mm, "end": v(47.83, 16.6) * mm});
            skLineSegment(sketch, "E369", {"start": v(47.83, 16.6) * mm, "end": v(47.9, 16.64) * mm});
            skLineSegment(sketch, "E370", {"start": v(47.9, 16.64) * mm, "end": v(47.96, 16.7) * mm});
            skLineSegment(sketch, "E371", {"start": v(47.96, 16.7) * mm, "end": v(48.02, 16.76) * mm});
            skLineSegment(sketch, "E372", {"start": v(48.02, 16.76) * mm, "end": v(48.09, 16.81) * mm});
            skLineSegment(sketch, "E373", {"start": v(48.09, 16.81) * mm, "end": v(48.15, 16.87) * mm});
            skLineSegment(sketch, "E374", {"start": v(48.15, 16.87) * mm, "end": v(48.21, 16.93) * mm});
            skLineSegment(sketch, "E375", {"start": v(48.21, 16.93) * mm, "end": v(48.28, 16.99) * mm});
            skLineSegment(sketch, "E376", {"start": v(48.28, 16.99) * mm, "end": v(48.33, 17.05) * mm});
            skLineSegment(sketch, "E377", {"start": v(48.33, 17.05) * mm, "end": v(48, 17.95) * mm});
            skLineSegment(sketch, "E378", {"start": v(48, 17.95) * mm, "end": v(47.93, 17.96) * mm});
            skLineSegment(sketch, "E379", {"start": v(47.93, 17.96) * mm, "end": v(47.84, 17.97) * mm});
            skLineSegment(sketch, "E380", {"start": v(47.84, 17.97) * mm, "end": v(47.75, 17.97) * mm});
            skLineSegment(sketch, "E381", {"start": v(47.75, 17.97) * mm, "end": v(47.66, 17.97) * mm});
            skLineSegment(sketch, "E382", {"start": v(47.66, 17.97) * mm, "end": v(47.58, 17.98) * mm});
            skLineSegment(sketch, "E383", {"start": v(47.58, 17.98) * mm, "end": v(47.5, 17.98) * mm});
            skLineSegment(sketch, "E384", {"start": v(47.5, 17.98) * mm, "end": v(47.41, 17.98) * mm});
            skLineSegment(sketch, "E385", {"start": v(47.41, 17.98) * mm, "end": v(47.33, 17.98) * mm});
            skLineSegment(sketch, "E386", {"start": v(47.33, 17.98) * mm, "end": v(47.25, 17.98) * mm});
            skLineSegment(sketch, "E387", {"start": v(47.25, 17.98) * mm, "end": v(47.16, 17.99) * mm});
            skLineSegment(sketch, "E388", {"start": v(47.16, 17.99) * mm, "end": v(47.08, 17.99) * mm});
            skLineSegment(sketch, "E389", {"start": v(47.08, 17.99) * mm, "end": v(47, 17.99) * mm});
            skLineSegment(sketch, "E390", {"start": v(47, 17.99) * mm, "end": v(46.93, 17.99) * mm});
            skLineSegment(sketch, "E391", {"start": v(46.93, 17.99) * mm, "end": v(46.85, 17.99) * mm});
            skLineSegment(sketch, "E392", {"start": v(46.85, 17.99) * mm, "end": v(46.77, 17.99) * mm});
            skLineSegment(sketch, "E393", {"start": v(46.77, 17.99) * mm, "end": v(46.7, 17.98) * mm});
            skLineSegment(sketch, "E394", {"start": v(46.7, 17.98) * mm, "end": v(46.62, 17.98) * mm});
            skLineSegment(sketch, "E395", {"start": v(46.62, 17.98) * mm, "end": v(46.55, 17.98) * mm});
            skLineSegment(sketch, "E396", {"start": v(46.55, 17.98) * mm, "end": v(46.48, 17.98) * mm});
            skLineSegment(sketch, "E397", {"start": v(46.48, 17.98) * mm, "end": v(46.4, 17.98) * mm});
            skLineSegment(sketch, "E398", {"start": v(46.4, 17.98) * mm, "end": v(46.33, 17.97) * mm});
            skLineSegment(sketch, "E399", {"start": v(46.33, 17.97) * mm, "end": v(46.26, 17.97) * mm});
            skLineSegment(sketch, "E400", {"start": v(46.26, 17.97) * mm, "end": v(46.2, 17.97) * mm});
            skLineSegment(sketch, "E401", {"start": v(46.2, 17.97) * mm, "end": v(46.13, 17.96) * mm});
            skLineSegment(sketch, "E402", {"start": v(46.13, 17.96) * mm, "end": v(46.06, 17.96) * mm});
            skLineSegment(sketch, "E403", {"start": v(46.06, 17.96) * mm, "end": v(46, 17.96) * mm});
            skLineSegment(sketch, "E404", {"start": v(46, 17.96) * mm, "end": v(45.93, 17.95) * mm});
            skLineSegment(sketch, "E405", {"start": v(45.93, 17.95) * mm, "end": v(45.86, 17.95) * mm});
            skLineSegment(sketch, "E406", {"start": v(45.86, 17.95) * mm, "end": v(45.8, 17.94) * mm});
            skLineSegment(sketch, "E407", {"start": v(45.8, 17.94) * mm, "end": v(45.73, 17.94) * mm});
            skLineSegment(sketch, "E408", {"start": v(45.73, 17.94) * mm, "end": v(45.67, 17.93) * mm});
            skLineSegment(sketch, "E409", {"start": v(45.67, 17.93) * mm, "end": v(45.61, 17.93) * mm});
            skLineSegment(sketch, "E410", {"start": v(45.61, 17.93) * mm, "end": v(45.55, 17.92) * mm});
            skLineSegment(sketch, "E411", {"start": v(45.55, 17.92) * mm, "end": v(45.5, 17.92) * mm});
            skLineSegment(sketch, "E412", {"start": v(45.5, 17.92) * mm, "end": v(45.43, 17.91) * mm});
            skLineSegment(sketch, "E413", {"start": v(45.43, 17.91) * mm, "end": v(45.38, 17.9) * mm});
            skLineSegment(sketch, "E414", {"start": v(45.38, 17.9) * mm, "end": v(45.32, 17.9) * mm});
            skLineSegment(sketch, "E415", {"start": v(45.32, 17.9) * mm, "end": v(45.26, 17.9) * mm});
            skLineSegment(sketch, "E416", {"start": v(45.26, 17.9) * mm, "end": v(45.2, 17.89) * mm});
            skLineSegment(sketch, "E417", {"start": v(45.2, 17.89) * mm, "end": v(45.16, 17.88) * mm});
            skLineSegment(sketch, "E418", {"start": v(45.16, 17.88) * mm, "end": v(45.05, 18.14) * mm});
            skLineSegment(sketch, "E419", {"start": v(45.05, 18.14) * mm, "end": v(44.87, 18.58) * mm});
            skLineSegment(sketch, "E420", {"start": v(44.87, 18.58) * mm, "end": v(44.76, 18.84) * mm});
            skLineSegment(sketch, "E421", {"start": v(44.76, 18.84) * mm, "end": v(44.8, 18.88) * mm});
            skLineSegment(sketch, "E422", {"start": v(44.8, 18.88) * mm, "end": v(44.85, 18.91) * mm});
            skLineSegment(sketch, "E423", {"start": v(44.85, 18.91) * mm, "end": v(44.9, 18.95) * mm});
            skLineSegment(sketch, "E424", {"start": v(44.9, 18.95) * mm, "end": v(44.94, 18.98) * mm});
            skLineSegment(sketch, "E425", {"start": v(44.94, 18.98) * mm, "end": v(44.98, 19.02) * mm});
            skLineSegment(sketch, "E426", {"start": v(44.98, 19.02) * mm, "end": v(45.03, 19.05) * mm});
            skLineSegment(sketch, "E427", {"start": v(45.03, 19.05) * mm, "end": v(45.08, 19.1) * mm});
            skLineSegment(sketch, "E428", {"start": v(45.08, 19.1) * mm, "end": v(45.12, 19.13) * mm});
            skLineSegment(sketch, "E429", {"start": v(45.12, 19.13) * mm, "end": v(45.17, 19.17) * mm});
            skLineSegment(sketch, "E430", {"start": v(45.17, 19.17) * mm, "end": v(45.22, 19.2) * mm});
            skLineSegment(sketch, "E431", {"start": v(45.22, 19.2) * mm, "end": v(45.27, 19.25) * mm});
            skLineSegment(sketch, "E432", {"start": v(45.27, 19.25) * mm, "end": v(45.31, 19.3) * mm});
            skLineSegment(sketch, "E433", {"start": v(45.31, 19.3) * mm, "end": v(45.36, 19.33) * mm});
            skLineSegment(sketch, "E434", {"start": v(45.36, 19.33) * mm, "end": v(45.41, 19.38) * mm});
            skLineSegment(sketch, "E435", {"start": v(45.41, 19.38) * mm, "end": v(45.46, 19.42) * mm});
            skLineSegment(sketch, "E436", {"start": v(45.46, 19.42) * mm, "end": v(45.51, 19.46) * mm});
            skLineSegment(sketch, "E437", {"start": v(45.51, 19.46) * mm, "end": v(45.56, 19.5) * mm});
            skLineSegment(sketch, "E438", {"start": v(45.56, 19.5) * mm, "end": v(45.62, 19.56) * mm});
            skLineSegment(sketch, "E439", {"start": v(45.62, 19.56) * mm, "end": v(45.67, 19.6) * mm});
            skLineSegment(sketch, "E440", {"start": v(45.67, 19.6) * mm, "end": v(45.72, 19.65) * mm});
            skLineSegment(sketch, "E441", {"start": v(45.72, 19.65) * mm, "end": v(45.77, 19.7) * mm});
            skLineSegment(sketch, "E442", {"start": v(45.77, 19.7) * mm, "end": v(45.83, 19.75) * mm});
            skLineSegment(sketch, "E443", {"start": v(45.83, 19.75) * mm, "end": v(45.88, 19.8) * mm});
            skLineSegment(sketch, "E444", {"start": v(45.88, 19.8) * mm, "end": v(45.94, 19.85) * mm});
            skLineSegment(sketch, "E445", {"start": v(45.94, 19.85) * mm, "end": v(46, 19.9) * mm});
            skLineSegment(sketch, "E446", {"start": v(46, 19.9) * mm, "end": v(46.05, 19.96) * mm});
            skLineSegment(sketch, "E447", {"start": v(46.05, 19.96) * mm, "end": v(46.1, 20) * mm});
            skLineSegment(sketch, "E448", {"start": v(46.1, 20) * mm, "end": v(46.16, 20.06) * mm});
            skLineSegment(sketch, "E449", {"start": v(46.16, 20.06) * mm, "end": v(46.21, 20.12) * mm});
            skLineSegment(sketch, "E450", {"start": v(46.21, 20.12) * mm, "end": v(46.27, 20.18) * mm});
            skLineSegment(sketch, "E451", {"start": v(46.27, 20.18) * mm, "end": v(46.33, 20.23) * mm});
            skLineSegment(sketch, "E452", {"start": v(46.33, 20.23) * mm, "end": v(46.38, 20.3) * mm});
            skLineSegment(sketch, "E453", {"start": v(46.38, 20.3) * mm, "end": v(46.44, 20.35) * mm});
            skLineSegment(sketch, "E454", {"start": v(46.44, 20.35) * mm, "end": v(46.5, 20.41) * mm});
            skLineSegment(sketch, "E455", {"start": v(46.5, 20.41) * mm, "end": v(46.56, 20.47) * mm});
            skLineSegment(sketch, "E456", {"start": v(46.56, 20.47) * mm, "end": v(46.62, 20.53) * mm});
            skLineSegment(sketch, "E457", {"start": v(46.62, 20.53) * mm, "end": v(46.68, 20.6) * mm});
            skLineSegment(sketch, "E458", {"start": v(46.68, 20.6) * mm, "end": v(46.74, 20.66) * mm});
            skLineSegment(sketch, "E459", {"start": v(46.74, 20.66) * mm, "end": v(46.8, 20.73) * mm});
            skLineSegment(sketch, "E460", {"start": v(46.8, 20.73) * mm, "end": v(46.85, 20.79) * mm});
            skLineSegment(sketch, "E461", {"start": v(46.85, 20.79) * mm, "end": v(46.45, 21.66) * mm});
            skLineSegment(sketch, "E462", {"start": v(46.45, 21.66) * mm, "end": v(46.37, 21.67) * mm});
            skLineSegment(sketch, "E463", {"start": v(46.37, 21.67) * mm, "end": v(46.28, 21.66) * mm});
            skLineSegment(sketch, "E464", {"start": v(46.28, 21.66) * mm, "end": v(46.2, 21.66) * mm});
            skLineSegment(sketch, "E465", {"start": v(46.2, 21.66) * mm, "end": v(46.1, 21.66) * mm});
            skLineSegment(sketch, "E466", {"start": v(46.1, 21.66) * mm, "end": v(46.02, 21.65) * mm});
            skLineSegment(sketch, "E467", {"start": v(46.02, 21.65) * mm, "end": v(45.94, 21.65) * mm});
            skLineSegment(sketch, "E468", {"start": v(45.94, 21.65) * mm, "end": v(45.85, 21.65) * mm});
            skLineSegment(sketch, "E469", {"start": v(45.85, 21.65) * mm, "end": v(45.77, 21.64) * mm});
            skLineSegment(sketch, "E470", {"start": v(45.77, 21.64) * mm, "end": v(45.69, 21.64) * mm});
            skLineSegment(sketch, "E471", {"start": v(45.69, 21.64) * mm, "end": v(45.6, 21.63) * mm});
            skLineSegment(sketch, "E472", {"start": v(45.6, 21.63) * mm, "end": v(45.53, 21.62) * mm});
            skLineSegment(sketch, "E473", {"start": v(45.53, 21.62) * mm, "end": v(45.45, 21.62) * mm});
            skLineSegment(sketch, "E474", {"start": v(45.45, 21.62) * mm, "end": v(45.37, 21.61) * mm});
            skLineSegment(sketch, "E475", {"start": v(45.37, 21.61) * mm, "end": v(45.3, 21.6) * mm});
            skLineSegment(sketch, "E476", {"start": v(45.3, 21.6) * mm, "end": v(45.22, 21.6) * mm});
            skLineSegment(sketch, "E477", {"start": v(45.22, 21.6) * mm, "end": v(45.14, 21.6) * mm});
            skLineSegment(sketch, "E478", {"start": v(45.14, 21.6) * mm, "end": v(45.07, 21.59) * mm});
            skLineSegment(sketch, "E479", {"start": v(45.07, 21.59) * mm, "end": v(45, 21.58) * mm});
            skLineSegment(sketch, "E480", {"start": v(45, 21.58) * mm, "end": v(44.92, 21.57) * mm});
            skLineSegment(sketch, "E481", {"start": v(44.92, 21.57) * mm, "end": v(44.85, 21.56) * mm});
            skLineSegment(sketch, "E482", {"start": v(44.85, 21.56) * mm, "end": v(44.78, 21.55) * mm});
            skLineSegment(sketch, "E483", {"start": v(44.78, 21.55) * mm, "end": v(44.71, 21.55) * mm});
            skLineSegment(sketch, "E484", {"start": v(44.71, 21.55) * mm, "end": v(44.64, 21.54) * mm});
            skLineSegment(sketch, "E485", {"start": v(44.64, 21.54) * mm, "end": v(44.57, 21.53) * mm});
            skLineSegment(sketch, "E486", {"start": v(44.57, 21.53) * mm, "end": v(44.5, 21.52) * mm});
            skLineSegment(sketch, "E487", {"start": v(44.5, 21.52) * mm, "end": v(44.44, 21.51) * mm});
            skLineSegment(sketch, "E488", {"start": v(44.44, 21.51) * mm, "end": v(44.38, 21.5) * mm});
            skLineSegment(sketch, "E489", {"start": v(44.38, 21.5) * mm, "end": v(44.31, 21.5) * mm});
            skLineSegment(sketch, "E490", {"start": v(44.31, 21.5) * mm, "end": v(44.25, 21.48) * mm});
            skLineSegment(sketch, "E491", {"start": v(44.25, 21.48) * mm, "end": v(44.19, 21.47) * mm});
            skLineSegment(sketch, "E492", {"start": v(44.19, 21.47) * mm, "end": v(44.12, 21.46) * mm});
            skLineSegment(sketch, "E493", {"start": v(44.12, 21.46) * mm, "end": v(44.06, 21.45) * mm});
            skLineSegment(sketch, "E494", {"start": v(44.06, 21.45) * mm, "end": v(44, 21.44) * mm});
            skLineSegment(sketch, "E495", {"start": v(44, 21.44) * mm, "end": v(43.95, 21.43) * mm});
            skLineSegment(sketch, "E496", {"start": v(43.95, 21.43) * mm, "end": v(43.89, 21.42) * mm});
            skLineSegment(sketch, "E497", {"start": v(43.89, 21.42) * mm, "end": v(43.83, 21.41) * mm});
            skLineSegment(sketch, "E498", {"start": v(43.83, 21.41) * mm, "end": v(43.78, 21.4) * mm});
            skLineSegment(sketch, "E499", {"start": v(43.78, 21.4) * mm, "end": v(43.72, 21.4) * mm});
            skLineSegment(sketch, "E500", {"start": v(43.72, 21.4) * mm, "end": v(43.67, 21.38) * mm});
            skLineSegment(sketch, "E501", {"start": v(43.67, 21.38) * mm, "end": v(43.61, 21.37) * mm});
            skLineSegment(sketch, "E502", {"start": v(43.61, 21.37) * mm, "end": v(43.49, 21.62) * mm});
            skLineSegment(sketch, "E503", {"start": v(43.49, 21.62) * mm, "end": v(43.27, 22.05) * mm});
            skLineSegment(sketch, "E504", {"start": v(43.27, 22.05) * mm, "end": v(43.15, 22.3) * mm});
            skLineSegment(sketch, "E505", {"start": v(43.15, 22.3) * mm, "end": v(43.19, 22.33) * mm});
            skLineSegment(sketch, "E506", {"start": v(43.19, 22.33) * mm, "end": v(43.23, 22.37) * mm});
            skLineSegment(sketch, "E507", {"start": v(43.23, 22.37) * mm, "end": v(43.27, 22.4) * mm});
            skLineSegment(sketch, "E508", {"start": v(43.27, 22.4) * mm, "end": v(43.31, 22.45) * mm});
            skLineSegment(sketch, "E509", {"start": v(43.31, 22.45) * mm, "end": v(43.35, 22.49) * mm});
            skLineSegment(sketch, "E510", {"start": v(43.35, 22.49) * mm, "end": v(43.4, 22.53) * mm});
            skLineSegment(sketch, "E511", {"start": v(43.4, 22.53) * mm, "end": v(43.44, 22.57) * mm});
            skLineSegment(sketch, "E512", {"start": v(43.44, 22.57) * mm, "end": v(43.48, 22.61) * mm});
            skLineSegment(sketch, "E513", {"start": v(43.48, 22.61) * mm, "end": v(43.53, 22.65) * mm});
            skLineSegment(sketch, "E514", {"start": v(43.53, 22.65) * mm, "end": v(43.57, 22.7) * mm});
            skLineSegment(sketch, "E515", {"start": v(43.57, 22.7) * mm, "end": v(43.62, 22.74) * mm});
            skLineSegment(sketch, "E516", {"start": v(43.62, 22.74) * mm, "end": v(43.66, 22.79) * mm});
            skLineSegment(sketch, "E517", {"start": v(43.66, 22.79) * mm, "end": v(43.7, 22.83) * mm});
            skLineSegment(sketch, "E518", {"start": v(43.7, 22.83) * mm, "end": v(43.75, 22.88) * mm});
            skLineSegment(sketch, "E519", {"start": v(43.75, 22.88) * mm, "end": v(43.8, 22.93) * mm});
            skLineSegment(sketch, "E520", {"start": v(43.8, 22.93) * mm, "end": v(43.85, 22.97) * mm});
            skLineSegment(sketch, "E521", {"start": v(43.85, 22.97) * mm, "end": v(43.9, 23.02) * mm});
            skLineSegment(sketch, "E522", {"start": v(43.9, 23.02) * mm, "end": v(43.94, 23.07) * mm});
            skLineSegment(sketch, "E523", {"start": v(43.94, 23.07) * mm, "end": v(43.99, 23.13) * mm});
            skLineSegment(sketch, "E524", {"start": v(43.99, 23.13) * mm, "end": v(44.04, 23.18) * mm});
            skLineSegment(sketch, "E525", {"start": v(44.04, 23.18) * mm, "end": v(44.09, 23.23) * mm});
            skLineSegment(sketch, "E526", {"start": v(44.09, 23.23) * mm, "end": v(44.14, 23.28) * mm});
            skLineSegment(sketch, "E527", {"start": v(44.14, 23.28) * mm, "end": v(44.19, 23.34) * mm});
            skLineSegment(sketch, "E528", {"start": v(44.19, 23.34) * mm, "end": v(44.24, 23.4) * mm});
            skLineSegment(sketch, "E529", {"start": v(44.24, 23.4) * mm, "end": v(44.29, 23.45) * mm});
            skLineSegment(sketch, "E530", {"start": v(44.29, 23.45) * mm, "end": v(44.34, 23.5) * mm});
            skLineSegment(sketch, "E531", {"start": v(44.34, 23.5) * mm, "end": v(44.39, 23.56) * mm});
            skLineSegment(sketch, "E532", {"start": v(44.39, 23.56) * mm, "end": v(44.44, 23.62) * mm});
            skLineSegment(sketch, "E533", {"start": v(44.44, 23.62) * mm, "end": v(44.5, 23.68) * mm});
            skLineSegment(sketch, "E534", {"start": v(44.5, 23.68) * mm, "end": v(44.54, 23.74) * mm});
            skLineSegment(sketch, "E535", {"start": v(44.54, 23.74) * mm, "end": v(44.6, 23.8) * mm});
            skLineSegment(sketch, "E536", {"start": v(44.6, 23.8) * mm, "end": v(44.65, 23.87) * mm});
            skLineSegment(sketch, "E537", {"start": v(44.65, 23.87) * mm, "end": v(44.7, 23.93) * mm});
            skLineSegment(sketch, "E538", {"start": v(44.7, 23.93) * mm, "end": v(44.76, 24) * mm});
            skLineSegment(sketch, "E539", {"start": v(44.76, 24) * mm, "end": v(44.8, 24.06) * mm});
            skLineSegment(sketch, "E540", {"start": v(44.8, 24.06) * mm, "end": v(44.86, 24.13) * mm});
            skLineSegment(sketch, "E541", {"start": v(44.86, 24.13) * mm, "end": v(44.92, 24.2) * mm});
            skLineSegment(sketch, "E542", {"start": v(44.92, 24.2) * mm, "end": v(44.97, 24.26) * mm});
            skLineSegment(sketch, "E543", {"start": v(44.97, 24.26) * mm, "end": v(45.03, 24.33) * mm});
            skLineSegment(sketch, "E544", {"start": v(45.03, 24.33) * mm, "end": v(45.07, 24.4) * mm});
            skLineSegment(sketch, "E545", {"start": v(45.07, 24.4) * mm, "end": v(44.6, 25.24) * mm});
            skLineSegment(sketch, "E546", {"start": v(44.6, 25.24) * mm, "end": v(44.53, 25.24) * mm});
            skLineSegment(sketch, "E547", {"start": v(44.53, 25.24) * mm, "end": v(44.44, 25.23) * mm});
            skLineSegment(sketch, "E548", {"start": v(44.44, 25.23) * mm, "end": v(44.35, 25.22) * mm});
            skLineSegment(sketch, "E549", {"start": v(44.35, 25.22) * mm, "end": v(44.27, 25.2) * mm});
            skLineSegment(sketch, "E550", {"start": v(44.27, 25.2) * mm, "end": v(44.18, 25.2) * mm});
            skLineSegment(sketch, "E551", {"start": v(44.18, 25.2) * mm, "end": v(44.1, 25.19) * mm});
            skLineSegment(sketch, "E552", {"start": v(44.1, 25.19) * mm, "end": v(44.01, 25.18) * mm});
            skLineSegment(sketch, "E553", {"start": v(44.01, 25.18) * mm, "end": v(43.93, 25.17) * mm});
            skLineSegment(sketch, "E554", {"start": v(43.93, 25.17) * mm, "end": v(43.85, 25.15) * mm});
            skLineSegment(sketch, "E555", {"start": v(43.85, 25.15) * mm, "end": v(43.77, 25.14) * mm});
            skLineSegment(sketch, "E556", {"start": v(43.77, 25.14) * mm, "end": v(43.7, 25.13) * mm});
            skLineSegment(sketch, "E557", {"start": v(43.7, 25.13) * mm, "end": v(43.61, 25.12) * mm});
            skLineSegment(sketch, "E558", {"start": v(43.61, 25.12) * mm, "end": v(43.54, 25.1) * mm});
            skLineSegment(sketch, "E559", {"start": v(43.54, 25.1) * mm, "end": v(43.46, 25.1) * mm});
            skLineSegment(sketch, "E560", {"start": v(43.46, 25.1) * mm, "end": v(43.38, 25.08) * mm});
            skLineSegment(sketch, "E561", {"start": v(43.38, 25.08) * mm, "end": v(43.3, 25.07) * mm});
            skLineSegment(sketch, "E562", {"start": v(43.3, 25.07) * mm, "end": v(43.24, 25.05) * mm});
            skLineSegment(sketch, "E563", {"start": v(43.24, 25.05) * mm, "end": v(43.16, 25.04) * mm});
            skLineSegment(sketch, "E564", {"start": v(43.16, 25.04) * mm, "end": v(43.1, 25.03) * mm});
            skLineSegment(sketch, "E565", {"start": v(43.1, 25.03) * mm, "end": v(43.02, 25.01) * mm});
            skLineSegment(sketch, "E566", {"start": v(43.02, 25.01) * mm, "end": v(42.95, 25) * mm});
            skLineSegment(sketch, "E567", {"start": v(42.95, 25) * mm, "end": v(42.88, 24.99) * mm});
            skLineSegment(sketch, "E568", {"start": v(42.88, 24.99) * mm, "end": v(42.81, 24.97) * mm});
            skLineSegment(sketch, "E569", {"start": v(42.81, 24.97) * mm, "end": v(42.75, 24.96) * mm});
            skLineSegment(sketch, "E570", {"start": v(42.75, 24.96) * mm, "end": v(42.68, 24.95) * mm});
            skLineSegment(sketch, "E571", {"start": v(42.68, 24.95) * mm, "end": v(42.62, 24.93) * mm});
            skLineSegment(sketch, "E572", {"start": v(42.62, 24.93) * mm, "end": v(42.55, 24.92) * mm});
            skLineSegment(sketch, "E573", {"start": v(42.55, 24.92) * mm, "end": v(42.49, 24.9) * mm});
            skLineSegment(sketch, "E574", {"start": v(42.49, 24.9) * mm, "end": v(42.43, 24.89) * mm});
            skLineSegment(sketch, "E575", {"start": v(42.43, 24.89) * mm, "end": v(42.37, 24.87) * mm});
            skLineSegment(sketch, "E576", {"start": v(42.37, 24.87) * mm, "end": v(42.3, 24.86) * mm});
            skLineSegment(sketch, "E577", {"start": v(42.3, 24.86) * mm, "end": v(42.25, 24.84) * mm});
            skLineSegment(sketch, "E578", {"start": v(42.25, 24.84) * mm, "end": v(42.19, 24.83) * mm});
            skLineSegment(sketch, "E579", {"start": v(42.19, 24.83) * mm, "end": v(42.13, 24.81) * mm});
            skLineSegment(sketch, "E580", {"start": v(42.13, 24.81) * mm, "end": v(42.07, 24.8) * mm});
            skLineSegment(sketch, "E581", {"start": v(42.07, 24.8) * mm, "end": v(42.02, 24.79) * mm});
            skLineSegment(sketch, "E582", {"start": v(42.02, 24.79) * mm, "end": v(41.96, 24.77) * mm});
            skLineSegment(sketch, "E583", {"start": v(41.96, 24.77) * mm, "end": v(41.9, 24.76) * mm});
            skLineSegment(sketch, "E584", {"start": v(41.9, 24.76) * mm, "end": v(41.85, 24.74) * mm});
            skLineSegment(sketch, "E585", {"start": v(41.85, 24.74) * mm, "end": v(41.8, 24.73) * mm});
            skLineSegment(sketch, "E586", {"start": v(41.8, 24.73) * mm, "end": v(41.66, 24.96) * mm});
            skLineSegment(sketch, "E587", {"start": v(41.66, 24.96) * mm, "end": v(41.4, 25.37) * mm});
            skLineSegment(sketch, "E588", {"start": v(41.4, 25.37) * mm, "end": v(41.26, 25.61) * mm});
            skLineSegment(sketch, "E589", {"start": v(41.26, 25.61) * mm, "end": v(41.3, 25.65) * mm});
            skLineSegment(sketch, "E590", {"start": v(41.3, 25.65) * mm, "end": v(41.34, 25.7) * mm});
            skLineSegment(sketch, "E591", {"start": v(41.34, 25.7) * mm, "end": v(41.38, 25.73) * mm});
            skLineSegment(sketch, "E592", {"start": v(41.38, 25.73) * mm, "end": v(41.42, 25.78) * mm});
            skLineSegment(sketch, "E593", {"start": v(41.42, 25.78) * mm, "end": v(41.45, 25.82) * mm});
            skLineSegment(sketch, "E594", {"start": v(41.45, 25.82) * mm, "end": v(41.5, 25.86) * mm});
            skLineSegment(sketch, "E595", {"start": v(41.5, 25.86) * mm, "end": v(41.53, 25.9) * mm});
            skLineSegment(sketch, "E596", {"start": v(41.53, 25.9) * mm, "end": v(41.57, 25.95) * mm});
            skLineSegment(sketch, "E597", {"start": v(41.57, 25.95) * mm, "end": v(41.61, 26) * mm});
            skLineSegment(sketch, "E598", {"start": v(41.61, 26) * mm, "end": v(41.66, 26.04) * mm});
            skLineSegment(sketch, "E599", {"start": v(41.66, 26.04) * mm, "end": v(41.7, 26.1) * mm});
            skLineSegment(sketch, "E600", {"start": v(41.7, 26.1) * mm, "end": v(41.74, 26.14) * mm});
            skLineSegment(sketch, "E601", {"start": v(41.74, 26.14) * mm, "end": v(41.78, 26.2) * mm});
            skLineSegment(sketch, "E602", {"start": v(41.78, 26.2) * mm, "end": v(41.82, 26.24) * mm});
            skLineSegment(sketch, "E603", {"start": v(41.82, 26.24) * mm, "end": v(41.87, 26.3) * mm});
            skLineSegment(sketch, "E604", {"start": v(41.87, 26.3) * mm, "end": v(41.9, 26.34) * mm});
            skLineSegment(sketch, "E605", {"start": v(41.9, 26.34) * mm, "end": v(41.95, 26.4) * mm});
            skLineSegment(sketch, "E606", {"start": v(41.95, 26.4) * mm, "end": v(42, 26.45) * mm});
            skLineSegment(sketch, "E607", {"start": v(42, 26.45) * mm, "end": v(42.04, 26.5) * mm});
            skLineSegment(sketch, "E608", {"start": v(42.04, 26.5) * mm, "end": v(42.08, 26.56) * mm});
            skLineSegment(sketch, "E609", {"start": v(42.08, 26.56) * mm, "end": v(42.13, 26.62) * mm});
            skLineSegment(sketch, "E610", {"start": v(42.13, 26.62) * mm, "end": v(42.17, 26.67) * mm});
            skLineSegment(sketch, "E611", {"start": v(42.17, 26.67) * mm, "end": v(42.22, 26.73) * mm});
            skLineSegment(sketch, "E612", {"start": v(42.22, 26.73) * mm, "end": v(42.26, 26.8) * mm});
            skLineSegment(sketch, "E613", {"start": v(42.26, 26.8) * mm, "end": v(42.31, 26.85) * mm});
            skLineSegment(sketch, "E614", {"start": v(42.31, 26.85) * mm, "end": v(42.36, 26.91) * mm});
            skLineSegment(sketch, "E615", {"start": v(42.36, 26.91) * mm, "end": v(42.4, 26.98) * mm});
            skLineSegment(sketch, "E616", {"start": v(42.4, 26.98) * mm, "end": v(42.45, 27.04) * mm});
            skLineSegment(sketch, "E617", {"start": v(42.45, 27.04) * mm, "end": v(42.5, 27.1) * mm});
            skLineSegment(sketch, "E618", {"start": v(42.5, 27.1) * mm, "end": v(42.54, 27.17) * mm});
            skLineSegment(sketch, "E619", {"start": v(42.54, 27.17) * mm, "end": v(42.6, 27.23) * mm});
            skLineSegment(sketch, "E620", {"start": v(42.6, 27.23) * mm, "end": v(42.64, 27.3) * mm});
            skLineSegment(sketch, "E621", {"start": v(42.64, 27.3) * mm, "end": v(42.69, 27.37) * mm});
            skLineSegment(sketch, "E622", {"start": v(42.69, 27.37) * mm, "end": v(42.74, 27.43) * mm});
            skLineSegment(sketch, "E623", {"start": v(42.74, 27.43) * mm, "end": v(42.78, 27.5) * mm});
            skLineSegment(sketch, "E624", {"start": v(42.78, 27.5) * mm, "end": v(42.83, 27.57) * mm});
            skLineSegment(sketch, "E625", {"start": v(42.83, 27.57) * mm, "end": v(42.88, 27.65) * mm});
            skLineSegment(sketch, "E626", {"start": v(42.88, 27.65) * mm, "end": v(42.93, 27.72) * mm});
            skLineSegment(sketch, "E627", {"start": v(42.93, 27.72) * mm, "end": v(42.98, 27.8) * mm});
            skLineSegment(sketch, "E628", {"start": v(42.98, 27.8) * mm, "end": v(43.02, 27.86) * mm});
            skLineSegment(sketch, "E629", {"start": v(43.02, 27.86) * mm, "end": v(42.48, 28.66) * mm});
            skLineSegment(sketch, "E630", {"start": v(42.48, 28.66) * mm, "end": v(42.4, 28.65) * mm});
            skLineSegment(sketch, "E631", {"start": v(42.4, 28.65) * mm, "end": v(42.32, 28.64) * mm});
            skLineSegment(sketch, "E632", {"start": v(42.32, 28.64) * mm, "end": v(42.24, 28.62) * mm});
            skLineSegment(sketch, "E633", {"start": v(42.24, 28.62) * mm, "end": v(42.15, 28.6) * mm});
            skLineSegment(sketch, "E634", {"start": v(42.15, 28.6) * mm, "end": v(42.07, 28.59) * mm});
            skLineSegment(sketch, "E635", {"start": v(42.07, 28.59) * mm, "end": v(41.98, 28.57) * mm});
            skLineSegment(sketch, "E636", {"start": v(41.98, 28.57) * mm, "end": v(41.9, 28.55) * mm});
            skLineSegment(sketch, "E637", {"start": v(41.9, 28.55) * mm, "end": v(41.82, 28.53) * mm});
            skLineSegment(sketch, "E638", {"start": v(41.82, 28.53) * mm, "end": v(41.74, 28.52) * mm});
            skLineSegment(sketch, "E639", {"start": v(41.74, 28.52) * mm, "end": v(41.66, 28.5) * mm});
            skLineSegment(sketch, "E640", {"start": v(41.66, 28.5) * mm, "end": v(41.58, 28.48) * mm});
            skLineSegment(sketch, "E641", {"start": v(41.58, 28.48) * mm, "end": v(41.5, 28.46) * mm});
            skLineSegment(sketch, "E642", {"start": v(41.5, 28.46) * mm, "end": v(41.43, 28.44) * mm});
            skLineSegment(sketch, "E643", {"start": v(41.43, 28.44) * mm, "end": v(41.36, 28.43) * mm});
            skLineSegment(sketch, "E644", {"start": v(41.36, 28.43) * mm, "end": v(41.28, 28.4) * mm});
            skLineSegment(sketch, "E645", {"start": v(41.28, 28.4) * mm, "end": v(41.2, 28.39) * mm});
            skLineSegment(sketch, "E646", {"start": v(41.2, 28.39) * mm, "end": v(41.14, 28.37) * mm});
            skLineSegment(sketch, "E647", {"start": v(41.14, 28.37) * mm, "end": v(41.07, 28.35) * mm});
            skLineSegment(sketch, "E648", {"start": v(41.07, 28.35) * mm, "end": v(41, 28.33) * mm});
            skLineSegment(sketch, "E649", {"start": v(41, 28.33) * mm, "end": v(40.93, 28.31) * mm});
            skLineSegment(sketch, "E650", {"start": v(40.93, 28.31) * mm, "end": v(40.86, 28.3) * mm});
            skLineSegment(sketch, "E651", {"start": v(40.86, 28.3) * mm, "end": v(40.79, 28.27) * mm});
            skLineSegment(sketch, "E652", {"start": v(40.79, 28.27) * mm, "end": v(40.72, 28.26) * mm});
            skLineSegment(sketch, "E653", {"start": v(40.72, 28.26) * mm, "end": v(40.66, 28.24) * mm});
            skLineSegment(sketch, "E654", {"start": v(40.66, 28.24) * mm, "end": v(40.6, 28.22) * mm});
            skLineSegment(sketch, "E655", {"start": v(40.6, 28.22) * mm, "end": v(40.53, 28.2) * mm});
            skLineSegment(sketch, "E656", {"start": v(40.53, 28.2) * mm, "end": v(40.47, 28.18) * mm});
            skLineSegment(sketch, "E657", {"start": v(40.47, 28.18) * mm, "end": v(40.4, 28.16) * mm});
            skLineSegment(sketch, "E658", {"start": v(40.4, 28.16) * mm, "end": v(40.34, 28.14) * mm});
            skLineSegment(sketch, "E659", {"start": v(40.34, 28.14) * mm, "end": v(40.28, 28.12) * mm});
            skLineSegment(sketch, "E660", {"start": v(40.28, 28.12) * mm, "end": v(40.22, 28.1) * mm});
            skLineSegment(sketch, "E661", {"start": v(40.22, 28.1) * mm, "end": v(40.17, 28.08) * mm});
            skLineSegment(sketch, "E662", {"start": v(40.17, 28.08) * mm, "end": v(40.1, 28.06) * mm});
            skLineSegment(sketch, "E663", {"start": v(40.1, 28.06) * mm, "end": v(40.05, 28.04) * mm});
            skLineSegment(sketch, "E664", {"start": v(40.05, 28.04) * mm, "end": v(40, 28.02) * mm});
            skLineSegment(sketch, "E665", {"start": v(40, 28.02) * mm, "end": v(39.94, 28) * mm});
            skLineSegment(sketch, "E666", {"start": v(39.94, 28) * mm, "end": v(39.89, 27.99) * mm});
            skLineSegment(sketch, "E667", {"start": v(39.89, 27.99) * mm, "end": v(39.84, 27.97) * mm});
            skLineSegment(sketch, "E668", {"start": v(39.84, 27.97) * mm, "end": v(39.78, 27.95) * mm});
            skLineSegment(sketch, "E669", {"start": v(39.78, 27.95) * mm, "end": v(39.73, 27.93) * mm});
            skLineSegment(sketch, "E670", {"start": v(39.73, 27.93) * mm, "end": v(39.57, 28.15) * mm});
            skLineSegment(sketch, "E671", {"start": v(39.57, 28.15) * mm, "end": v(39.29, 28.54) * mm});
            skLineSegment(sketch, "E672", {"start": v(39.29, 28.54) * mm, "end": v(39.13, 28.77) * mm});
            skLineSegment(sketch, "E673", {"start": v(39.13, 28.77) * mm, "end": v(39.16, 28.82) * mm});
            skLineSegment(sketch, "E674", {"start": v(39.16, 28.82) * mm, "end": v(39.2, 28.86) * mm});
            skLineSegment(sketch, "E675", {"start": v(39.2, 28.86) * mm, "end": v(39.23, 28.9) * mm});
            skLineSegment(sketch, "E676", {"start": v(39.23, 28.9) * mm, "end": v(39.27, 28.95) * mm});
            skLineSegment(sketch, "E677", {"start": v(39.27, 28.95) * mm, "end": v(39.3, 29) * mm});
            skLineSegment(sketch, "E678", {"start": v(39.3, 29) * mm, "end": v(39.34, 29.04) * mm});
            skLineSegment(sketch, "E679", {"start": v(39.34, 29.04) * mm, "end": v(39.37, 29.09) * mm});
            skLineSegment(sketch, "E680", {"start": v(39.37, 29.09) * mm, "end": v(39.4, 29.13) * mm});
            skLineSegment(sketch, "E681", {"start": v(39.4, 29.13) * mm, "end": v(39.45, 29.18) * mm});
            skLineSegment(sketch, "E682", {"start": v(39.45, 29.18) * mm, "end": v(39.48, 29.23) * mm});
            skLineSegment(sketch, "E683", {"start": v(39.48, 29.23) * mm, "end": v(39.52, 29.28) * mm});
            skLineSegment(sketch, "E684", {"start": v(39.52, 29.28) * mm, "end": v(39.56, 29.34) * mm});
            skLineSegment(sketch, "E685", {"start": v(39.56, 29.34) * mm, "end": v(39.6, 29.39) * mm});
            skLineSegment(sketch, "E686", {"start": v(39.6, 29.39) * mm, "end": v(39.63, 29.44) * mm});
            skLineSegment(sketch, "E687", {"start": v(39.63, 29.44) * mm, "end": v(39.67, 29.5) * mm});
            skLineSegment(sketch, "E688", {"start": v(39.67, 29.5) * mm, "end": v(39.71, 29.55) * mm});
            skLineSegment(sketch, "E689", {"start": v(39.71, 29.55) * mm, "end": v(39.75, 29.6) * mm});
            skLineSegment(sketch, "E690", {"start": v(39.75, 29.6) * mm, "end": v(39.8, 29.66) * mm});
            skLineSegment(sketch, "E691", {"start": v(39.8, 29.66) * mm, "end": v(39.83, 29.72) * mm});
            skLineSegment(sketch, "E692", {"start": v(39.83, 29.72) * mm, "end": v(39.87, 29.78) * mm});
            skLineSegment(sketch, "E693", {"start": v(39.87, 29.78) * mm, "end": v(39.91, 29.84) * mm});
            skLineSegment(sketch, "E694", {"start": v(39.91, 29.84) * mm, "end": v(39.95, 29.9) * mm});
            skLineSegment(sketch, "E695", {"start": v(39.95, 29.9) * mm, "end": v(40, 29.96) * mm});
            skLineSegment(sketch, "E696", {"start": v(40, 29.96) * mm, "end": v(40.03, 30.03) * mm});
            skLineSegment(sketch, "E697", {"start": v(40.03, 30.03) * mm, "end": v(40.07, 30.09) * mm});
            skLineSegment(sketch, "E698", {"start": v(40.07, 30.09) * mm, "end": v(40.11, 30.15) * mm});
            skLineSegment(sketch, "E699", {"start": v(40.11, 30.15) * mm, "end": v(40.16, 30.22) * mm});
            skLineSegment(sketch, "E700", {"start": v(40.16, 30.22) * mm, "end": v(40.2, 30.29) * mm});
            skLineSegment(sketch, "E701", {"start": v(40.2, 30.29) * mm, "end": v(40.24, 30.35) * mm});
            skLineSegment(sketch, "E702", {"start": v(40.24, 30.35) * mm, "end": v(40.28, 30.42) * mm});
            skLineSegment(sketch, "E703", {"start": v(40.28, 30.42) * mm, "end": v(40.32, 30.49) * mm});
            skLineSegment(sketch, "E704", {"start": v(40.32, 30.49) * mm, "end": v(40.37, 30.56) * mm});
            skLineSegment(sketch, "E705", {"start": v(40.37, 30.56) * mm, "end": v(40.4, 30.63) * mm});
            skLineSegment(sketch, "E706", {"start": v(40.4, 30.63) * mm, "end": v(40.45, 30.7) * mm});
            skLineSegment(sketch, "E707", {"start": v(40.45, 30.7) * mm, "end": v(40.5, 30.78) * mm});
            skLineSegment(sketch, "E708", {"start": v(40.5, 30.78) * mm, "end": v(40.54, 30.85) * mm});
            skLineSegment(sketch, "E709", {"start": v(40.54, 30.85) * mm, "end": v(40.58, 30.92) * mm});
            skLineSegment(sketch, "E710", {"start": v(40.58, 30.92) * mm, "end": v(40.62, 31) * mm});
            skLineSegment(sketch, "E711", {"start": v(40.62, 31) * mm, "end": v(40.67, 31.08) * mm});
            skLineSegment(sketch, "E712", {"start": v(40.67, 31.08) * mm, "end": v(40.7, 31.15) * mm});
            skLineSegment(sketch, "E713", {"start": v(40.7, 31.15) * mm, "end": v(40.1, 31.9) * mm});
            skLineSegment(sketch, "E714", {"start": v(40.1, 31.9) * mm, "end": v(40.03, 31.9) * mm});
            skLineSegment(sketch, "E715", {"start": v(40.03, 31.9) * mm, "end": v(39.94, 31.87) * mm});
            skLineSegment(sketch, "E716", {"start": v(39.94, 31.87) * mm, "end": v(39.86, 31.85) * mm});
            skLineSegment(sketch, "E717", {"start": v(39.86, 31.85) * mm, "end": v(39.78, 31.82) * mm});
            skLineSegment(sketch, "E718", {"start": v(39.78, 31.82) * mm, "end": v(39.7, 31.8) * mm});
            skLineSegment(sketch, "E719", {"start": v(39.7, 31.8) * mm, "end": v(39.61, 31.78) * mm});
            skLineSegment(sketch, "E720", {"start": v(39.61, 31.78) * mm, "end": v(39.53, 31.75) * mm});
            skLineSegment(sketch, "E721", {"start": v(39.53, 31.75) * mm, "end": v(39.45, 31.73) * mm});
            skLineSegment(sketch, "E722", {"start": v(39.45, 31.73) * mm, "end": v(39.38, 31.7) * mm});
            skLineSegment(sketch, "E723", {"start": v(39.38, 31.7) * mm, "end": v(39.3, 31.68) * mm});
            skLineSegment(sketch, "E724", {"start": v(39.3, 31.68) * mm, "end": v(39.22, 31.66) * mm});
            skLineSegment(sketch, "E725", {"start": v(39.22, 31.66) * mm, "end": v(39.15, 31.63) * mm});
            skLineSegment(sketch, "E726", {"start": v(39.15, 31.63) * mm, "end": v(39.07, 31.6) * mm});
            skLineSegment(sketch, "E727", {"start": v(39.07, 31.6) * mm, "end": v(39, 31.58) * mm});
            skLineSegment(sketch, "E728", {"start": v(39, 31.58) * mm, "end": v(38.93, 31.56) * mm});
            skLineSegment(sketch, "E729", {"start": v(38.93, 31.56) * mm, "end": v(38.85, 31.53) * mm});
            skLineSegment(sketch, "E730", {"start": v(38.85, 31.53) * mm, "end": v(38.78, 31.5) * mm});
            skLineSegment(sketch, "E731", {"start": v(38.78, 31.5) * mm, "end": v(38.71, 31.49) * mm});
            skLineSegment(sketch, "E732", {"start": v(38.71, 31.49) * mm, "end": v(38.65, 31.46) * mm});
            skLineSegment(sketch, "E733", {"start": v(38.65, 31.46) * mm, "end": v(38.58, 31.44) * mm});
            skLineSegment(sketch, "E734", {"start": v(38.58, 31.44) * mm, "end": v(38.51, 31.41) * mm});
            skLineSegment(sketch, "E735", {"start": v(38.51, 31.41) * mm, "end": v(38.45, 31.39) * mm});
            skLineSegment(sketch, "E736", {"start": v(38.45, 31.39) * mm, "end": v(38.38, 31.36) * mm});
            skLineSegment(sketch, "E737", {"start": v(38.38, 31.36) * mm, "end": v(38.32, 31.34) * mm});
            skLineSegment(sketch, "E738", {"start": v(38.32, 31.34) * mm, "end": v(38.25, 31.32) * mm});
            skLineSegment(sketch, "E739", {"start": v(38.25, 31.32) * mm, "end": v(38.2, 31.3) * mm});
            skLineSegment(sketch, "E740", {"start": v(38.2, 31.3) * mm, "end": v(38.13, 31.27) * mm});
            skLineSegment(sketch, "E741", {"start": v(38.13, 31.27) * mm, "end": v(38.07, 31.24) * mm});
            skLineSegment(sketch, "E742", {"start": v(38.07, 31.24) * mm, "end": v(38.01, 31.22) * mm});
            skLineSegment(sketch, "E743", {"start": v(38.01, 31.22) * mm, "end": v(37.95, 31.2) * mm});
            skLineSegment(sketch, "E744", {"start": v(37.95, 31.2) * mm, "end": v(37.9, 31.17) * mm});
            skLineSegment(sketch, "E745", {"start": v(37.9, 31.17) * mm, "end": v(37.84, 31.15) * mm});
            skLineSegment(sketch, "E746", {"start": v(37.84, 31.15) * mm, "end": v(37.78, 31.12) * mm});
            skLineSegment(sketch, "E747", {"start": v(37.78, 31.12) * mm, "end": v(37.73, 31.1) * mm});
            skLineSegment(sketch, "E748", {"start": v(37.73, 31.1) * mm, "end": v(37.67, 31.08) * mm});
            skLineSegment(sketch, "E749", {"start": v(37.67, 31.08) * mm, "end": v(37.62, 31.05) * mm});
            skLineSegment(sketch, "E750", {"start": v(37.62, 31.05) * mm, "end": v(37.57, 31.03) * mm});
            skLineSegment(sketch, "E751", {"start": v(37.57, 31.03) * mm, "end": v(37.52, 31) * mm});
            skLineSegment(sketch, "E752", {"start": v(37.52, 31) * mm, "end": v(37.47, 30.98) * mm});
            skLineSegment(sketch, "E753", {"start": v(37.47, 30.98) * mm, "end": v(37.42, 30.96) * mm});
            skLineSegment(sketch, "E754", {"start": v(37.42, 30.96) * mm, "end": v(37.24, 31.17) * mm});
            skLineSegment(sketch, "E755", {"start": v(37.24, 31.17) * mm, "end": v(36.93, 31.54) * mm});
            skLineSegment(sketch, "E756", {"start": v(36.93, 31.54) * mm, "end": v(36.75, 31.75) * mm});
            skLineSegment(sketch, "E757", {"start": v(36.75, 31.75) * mm, "end": v(36.78, 31.8) * mm});
            skLineSegment(sketch, "E758", {"start": v(36.78, 31.8) * mm, "end": v(36.81, 31.84) * mm});
            skLineSegment(sketch, "E759", {"start": v(36.81, 31.84) * mm, "end": v(36.84, 31.9) * mm});
            skLineSegment(sketch, "E760", {"start": v(36.84, 31.9) * mm, "end": v(36.87, 31.94) * mm});
            skLineSegment(sketch, "E761", {"start": v(36.87, 31.94) * mm, "end": v(36.9, 31.99) * mm});
            skLineSegment(sketch, "E762", {"start": v(36.9, 31.99) * mm, "end": v(36.94, 32.04) * mm});
            skLineSegment(sketch, "E763", {"start": v(36.94, 32.04) * mm, "end": v(36.97, 32.09) * mm});
            skLineSegment(sketch, "E764", {"start": v(36.97, 32.09) * mm, "end": v(37, 32.14) * mm});
            skLineSegment(sketch, "E765", {"start": v(37, 32.14) * mm, "end": v(37.04, 32.19) * mm});
            skLineSegment(sketch, "E766", {"start": v(37.04, 32.19) * mm, "end": v(37.07, 32.24) * mm});
            skLineSegment(sketch, "E767", {"start": v(37.07, 32.24) * mm, "end": v(37.1, 32.3) * mm});
            skLineSegment(sketch, "E768", {"start": v(37.1, 32.3) * mm, "end": v(37.13, 32.35) * mm});
            skLineSegment(sketch, "E769", {"start": v(37.13, 32.35) * mm, "end": v(37.17, 32.4) * mm});
            skLineSegment(sketch, "E770", {"start": v(37.17, 32.4) * mm, "end": v(37.2, 32.46) * mm});
            skLineSegment(sketch, "E771", {"start": v(37.2, 32.46) * mm, "end": v(37.24, 32.52) * mm});
            skLineSegment(sketch, "E772", {"start": v(37.24, 32.52) * mm, "end": v(37.27, 32.58) * mm});
            skLineSegment(sketch, "E773", {"start": v(37.27, 32.58) * mm, "end": v(37.3, 32.63) * mm});
            skLineSegment(sketch, "E774", {"start": v(37.3, 32.63) * mm, "end": v(37.34, 32.7) * mm});
            skLineSegment(sketch, "E775", {"start": v(37.34, 32.7) * mm, "end": v(37.38, 32.76) * mm});
            skLineSegment(sketch, "E776", {"start": v(37.38, 32.76) * mm, "end": v(37.41, 32.82) * mm});
            skLineSegment(sketch, "E777", {"start": v(37.41, 32.82) * mm, "end": v(37.45, 32.88) * mm});
            skLineSegment(sketch, "E778", {"start": v(37.45, 32.88) * mm, "end": v(37.48, 32.94) * mm});
            skLineSegment(sketch, "E779", {"start": v(37.48, 32.94) * mm, "end": v(37.52, 33) * mm});
            skLineSegment(sketch, "E780", {"start": v(37.52, 33) * mm, "end": v(37.55, 33.07) * mm});
            skLineSegment(sketch, "E781", {"start": v(37.55, 33.07) * mm, "end": v(37.59, 33.14) * mm});
            skLineSegment(sketch, "E782", {"start": v(37.59, 33.14) * mm, "end": v(37.63, 33.2) * mm});
            skLineSegment(sketch, "E783", {"start": v(37.63, 33.2) * mm, "end": v(37.66, 33.28) * mm});
            skLineSegment(sketch, "E784", {"start": v(37.66, 33.28) * mm, "end": v(37.7, 33.35) * mm});
            skLineSegment(sketch, "E785", {"start": v(37.7, 33.35) * mm, "end": v(37.73, 33.42) * mm});
            skLineSegment(sketch, "E786", {"start": v(37.73, 33.42) * mm, "end": v(37.77, 33.49) * mm});
            skLineSegment(sketch, "E787", {"start": v(37.77, 33.49) * mm, "end": v(37.8, 33.56) * mm});
            skLineSegment(sketch, "E788", {"start": v(37.8, 33.56) * mm, "end": v(37.84, 33.63) * mm});
            skLineSegment(sketch, "E789", {"start": v(37.84, 33.63) * mm, "end": v(37.88, 33.7) * mm});
            skLineSegment(sketch, "E790", {"start": v(37.88, 33.7) * mm, "end": v(37.92, 33.78) * mm});
            skLineSegment(sketch, "E791", {"start": v(37.92, 33.78) * mm, "end": v(37.95, 33.86) * mm});
            skLineSegment(sketch, "E792", {"start": v(37.95, 33.86) * mm, "end": v(38, 33.93) * mm});
            skLineSegment(sketch, "E793", {"start": v(38, 33.93) * mm, "end": v(38.03, 34.01) * mm});
            skLineSegment(sketch, "E794", {"start": v(38.03, 34.01) * mm, "end": v(38.07, 34.1) * mm});
            skLineSegment(sketch, "E795", {"start": v(38.07, 34.1) * mm, "end": v(38.1, 34.17) * mm});
            skLineSegment(sketch, "E796", {"start": v(38.1, 34.17) * mm, "end": v(38.13, 34.24) * mm});
            skLineSegment(sketch, "E797", {"start": v(38.13, 34.24) * mm, "end": v(37.48, 34.96) * mm});
            skLineSegment(sketch, "E798", {"start": v(37.48, 34.96) * mm, "end": v(37.4, 34.94) * mm});
            skLineSegment(sketch, "E799", {"start": v(37.4, 34.94) * mm, "end": v(37.32, 34.9) * mm});
            skLineSegment(sketch, "E800", {"start": v(37.32, 34.9) * mm, "end": v(37.24, 34.88) * mm});
            skLineSegment(sketch, "E801", {"start": v(37.24, 34.88) * mm, "end": v(37.16, 34.85) * mm});
            skLineSegment(sketch, "E802", {"start": v(37.16, 34.85) * mm, "end": v(37.08, 34.82) * mm});
            skLineSegment(sketch, "E803", {"start": v(37.08, 34.82) * mm, "end": v(37, 34.79) * mm});
            skLineSegment(sketch, "E804", {"start": v(37, 34.79) * mm, "end": v(36.92, 34.76) * mm});
            skLineSegment(sketch, "E805", {"start": v(36.92, 34.76) * mm, "end": v(36.84, 34.73) * mm});
            skLineSegment(sketch, "E806", {"start": v(36.84, 34.73) * mm, "end": v(36.77, 34.7) * mm});
            skLineSegment(sketch, "E807", {"start": v(36.77, 34.7) * mm, "end": v(36.7, 34.67) * mm});
            skLineSegment(sketch, "E808", {"start": v(36.7, 34.67) * mm, "end": v(36.62, 34.64) * mm});
            skLineSegment(sketch, "E809", {"start": v(36.62, 34.64) * mm, "end": v(36.54, 34.6) * mm});
            skLineSegment(sketch, "E810", {"start": v(36.54, 34.6) * mm, "end": v(36.47, 34.58) * mm});
            skLineSegment(sketch, "E811", {"start": v(36.47, 34.58) * mm, "end": v(36.4, 34.55) * mm});
            skLineSegment(sketch, "E812", {"start": v(36.4, 34.55) * mm, "end": v(36.33, 34.52) * mm});
            skLineSegment(sketch, "E813", {"start": v(36.33, 34.52) * mm, "end": v(36.26, 34.49) * mm});
            skLineSegment(sketch, "E814", {"start": v(36.26, 34.49) * mm, "end": v(36.2, 34.46) * mm});
            skLineSegment(sketch, "E815", {"start": v(36.2, 34.46) * mm, "end": v(36.12, 34.43) * mm});
            skLineSegment(sketch, "E816", {"start": v(36.12, 34.43) * mm, "end": v(36.06, 34.4) * mm});
            skLineSegment(sketch, "E817", {"start": v(36.06, 34.4) * mm, "end": v(36, 34.37) * mm});
            skLineSegment(sketch, "E818", {"start": v(36, 34.37) * mm, "end": v(35.93, 34.34) * mm});
            skLineSegment(sketch, "E819", {"start": v(35.93, 34.34) * mm, "end": v(35.86, 34.3) * mm});
            skLineSegment(sketch, "E820", {"start": v(35.86, 34.3) * mm, "end": v(35.8, 34.28) * mm});
            skLineSegment(sketch, "E821", {"start": v(35.8, 34.28) * mm, "end": v(35.74, 34.25) * mm});
            skLineSegment(sketch, "E822", {"start": v(35.74, 34.25) * mm, "end": v(35.68, 34.22) * mm});
            skLineSegment(sketch, "E823", {"start": v(35.68, 34.22) * mm, "end": v(35.62, 34.2) * mm});
            skLineSegment(sketch, "E824", {"start": v(35.62, 34.2) * mm, "end": v(35.56, 34.16) * mm});
            skLineSegment(sketch, "E825", {"start": v(35.56, 34.16) * mm, "end": v(35.5, 34.13) * mm});
            skLineSegment(sketch, "E826", {"start": v(35.5, 34.13) * mm, "end": v(35.44, 34.1) * mm});
            skLineSegment(sketch, "E827", {"start": v(35.44, 34.1) * mm, "end": v(35.39, 34.08) * mm});
            skLineSegment(sketch, "E828", {"start": v(35.39, 34.08) * mm, "end": v(35.33, 34.05) * mm});
            skLineSegment(sketch, "E829", {"start": v(35.33, 34.05) * mm, "end": v(35.28, 34.02) * mm});
            skLineSegment(sketch, "E830", {"start": v(35.28, 34.02) * mm, "end": v(35.22, 34) * mm});
            skLineSegment(sketch, "E831", {"start": v(35.22, 34) * mm, "end": v(35.17, 33.96) * mm});
            skLineSegment(sketch, "E832", {"start": v(35.17, 33.96) * mm, "end": v(35.12, 33.94) * mm});
            skLineSegment(sketch, "E833", {"start": v(35.12, 33.94) * mm, "end": v(35.07, 33.9) * mm});
            skLineSegment(sketch, "E834", {"start": v(35.07, 33.9) * mm, "end": v(35.02, 33.88) * mm});
            skLineSegment(sketch, "E835", {"start": v(35.02, 33.88) * mm, "end": v(34.97, 33.86) * mm});
            skLineSegment(sketch, "E836", {"start": v(34.97, 33.86) * mm, "end": v(34.92, 33.83) * mm});
            skLineSegment(sketch, "E837", {"start": v(34.92, 33.83) * mm, "end": v(34.88, 33.8) * mm});
            skLineSegment(sketch, "E838", {"start": v(34.88, 33.8) * mm, "end": v(34.68, 34) * mm});
            skLineSegment(sketch, "E839", {"start": v(34.68, 34) * mm, "end": v(34.34, 34.34) * mm});
            skLineSegment(sketch, "E840", {"start": v(34.34, 34.34) * mm, "end": v(34.14, 34.54) * mm});
            skLineSegment(sketch, "E841", {"start": v(34.14, 34.54) * mm, "end": v(34.17, 34.59) * mm});
            skLineSegment(sketch, "E842", {"start": v(34.17, 34.59) * mm, "end": v(34.2, 34.63) * mm});
            skLineSegment(sketch, "E843", {"start": v(34.2, 34.63) * mm, "end": v(34.23, 34.68) * mm});
            skLineSegment(sketch, "E844", {"start": v(34.23, 34.68) * mm, "end": v(34.25, 34.73) * mm});
            skLineSegment(sketch, "E845", {"start": v(34.25, 34.73) * mm, "end": v(34.28, 34.78) * mm});
            skLineSegment(sketch, "E846", {"start": v(34.28, 34.78) * mm, "end": v(34.31, 34.83) * mm});
            skLineSegment(sketch, "E847", {"start": v(34.31, 34.83) * mm, "end": v(34.34, 34.89) * mm});
            skLineSegment(sketch, "E848", {"start": v(34.34, 34.89) * mm, "end": v(34.37, 34.94) * mm});
            skLineSegment(sketch, "E849", {"start": v(34.37, 34.94) * mm, "end": v(34.4, 35) * mm});
            skLineSegment(sketch, "E850", {"start": v(34.4, 35) * mm, "end": v(34.42, 35.05) * mm});
            skLineSegment(sketch, "E851", {"start": v(34.42, 35.05) * mm, "end": v(34.45, 35.1) * mm});
            skLineSegment(sketch, "E852", {"start": v(34.45, 35.1) * mm, "end": v(34.48, 35.16) * mm});
            skLineSegment(sketch, "E853", {"start": v(34.48, 35.16) * mm, "end": v(34.51, 35.22) * mm});
            skLineSegment(sketch, "E854", {"start": v(34.51, 35.22) * mm, "end": v(34.54, 35.28) * mm});
            skLineSegment(sketch, "E855", {"start": v(34.54, 35.28) * mm, "end": v(34.57, 35.34) * mm});
            skLineSegment(sketch, "E856", {"start": v(34.57, 35.34) * mm, "end": v(34.6, 35.4) * mm});
            skLineSegment(sketch, "E857", {"start": v(34.6, 35.4) * mm, "end": v(34.63, 35.46) * mm});
            skLineSegment(sketch, "E858", {"start": v(34.63, 35.46) * mm, "end": v(34.66, 35.52) * mm});
            skLineSegment(sketch, "E859", {"start": v(34.66, 35.52) * mm, "end": v(34.7, 35.59) * mm});
            skLineSegment(sketch, "E860", {"start": v(34.7, 35.59) * mm, "end": v(34.72, 35.65) * mm});
            skLineSegment(sketch, "E861", {"start": v(34.72, 35.65) * mm, "end": v(34.75, 35.72) * mm});
            skLineSegment(sketch, "E862", {"start": v(34.75, 35.72) * mm, "end": v(34.78, 35.78) * mm});
            skLineSegment(sketch, "E863", {"start": v(34.78, 35.78) * mm, "end": v(34.81, 35.85) * mm});
            skLineSegment(sketch, "E864", {"start": v(34.81, 35.85) * mm, "end": v(34.84, 35.92) * mm});
            skLineSegment(sketch, "E865", {"start": v(34.84, 35.92) * mm, "end": v(34.87, 35.99) * mm});
            skLineSegment(sketch, "E866", {"start": v(34.87, 35.99) * mm, "end": v(34.9, 36.06) * mm});
            skLineSegment(sketch, "E867", {"start": v(34.9, 36.06) * mm, "end": v(34.93, 36.13) * mm});
            skLineSegment(sketch, "E868", {"start": v(34.93, 36.13) * mm, "end": v(34.97, 36.2) * mm});
            skLineSegment(sketch, "E869", {"start": v(34.97, 36.2) * mm, "end": v(35, 36.27) * mm});
            skLineSegment(sketch, "E870", {"start": v(35, 36.27) * mm, "end": v(35.03, 36.35) * mm});
            skLineSegment(sketch, "E871", {"start": v(35.03, 36.35) * mm, "end": v(35.06, 36.42) * mm});
            skLineSegment(sketch, "E872", {"start": v(35.06, 36.42) * mm, "end": v(35.09, 36.5) * mm});
            skLineSegment(sketch, "E873", {"start": v(35.09, 36.5) * mm, "end": v(35.12, 36.57) * mm});
            skLineSegment(sketch, "E874", {"start": v(35.12, 36.57) * mm, "end": v(35.15, 36.65) * mm});
            skLineSegment(sketch, "E875", {"start": v(35.15, 36.65) * mm, "end": v(35.18, 36.73) * mm});
            skLineSegment(sketch, "E876", {"start": v(35.18, 36.73) * mm, "end": v(35.21, 36.81) * mm});
            skLineSegment(sketch, "E877", {"start": v(35.21, 36.81) * mm, "end": v(35.24, 36.9) * mm});
            skLineSegment(sketch, "E878", {"start": v(35.24, 36.9) * mm, "end": v(35.27, 36.97) * mm});
            skLineSegment(sketch, "E879", {"start": v(35.27, 36.97) * mm, "end": v(35.3, 37.06) * mm});
            skLineSegment(sketch, "E880", {"start": v(35.3, 37.06) * mm, "end": v(35.33, 37.13) * mm});
            skLineSegment(sketch, "E881", {"start": v(35.33, 37.13) * mm, "end": v(34.62, 37.79) * mm});
            skLineSegment(sketch, "E882", {"start": v(34.62, 37.79) * mm, "end": v(34.55, 37.76) * mm});
            skLineSegment(sketch, "E883", {"start": v(34.55, 37.76) * mm, "end": v(34.47, 37.73) * mm});
            skLineSegment(sketch, "E884", {"start": v(34.47, 37.73) * mm, "end": v(34.39, 37.7) * mm});
            skLineSegment(sketch, "E885", {"start": v(34.39, 37.7) * mm, "end": v(34.3, 37.65) * mm});
            skLineSegment(sketch, "E886", {"start": v(34.3, 37.65) * mm, "end": v(34.23, 37.62) * mm});
            skLineSegment(sketch, "E887", {"start": v(34.23, 37.62) * mm, "end": v(34.15, 37.58) * mm});
            skLineSegment(sketch, "E888", {"start": v(34.15, 37.58) * mm, "end": v(34.08, 37.55) * mm});
            skLineSegment(sketch, "E889", {"start": v(34.08, 37.55) * mm, "end": v(34, 37.5) * mm});
            skLineSegment(sketch, "E890", {"start": v(34, 37.5) * mm, "end": v(33.93, 37.47) * mm});
            skLineSegment(sketch, "E891", {"start": v(33.93, 37.47) * mm, "end": v(33.86, 37.44) * mm});
            skLineSegment(sketch, "E892", {"start": v(33.86, 37.44) * mm, "end": v(33.79, 37.4) * mm});
            skLineSegment(sketch, "E893", {"start": v(33.79, 37.4) * mm, "end": v(33.72, 37.37) * mm});
            skLineSegment(sketch, "E894", {"start": v(33.72, 37.37) * mm, "end": v(33.65, 37.33) * mm});
            skLineSegment(sketch, "E895", {"start": v(33.65, 37.33) * mm, "end": v(33.58, 37.3) * mm});
            skLineSegment(sketch, "E896", {"start": v(33.58, 37.3) * mm, "end": v(33.51, 37.26) * mm});
            skLineSegment(sketch, "E897", {"start": v(33.51, 37.26) * mm, "end": v(33.44, 37.22) * mm});
            skLineSegment(sketch, "E898", {"start": v(33.44, 37.22) * mm, "end": v(33.38, 37.19) * mm});
            skLineSegment(sketch, "E899", {"start": v(33.38, 37.19) * mm, "end": v(33.31, 37.15) * mm});
            skLineSegment(sketch, "E900", {"start": v(33.31, 37.15) * mm, "end": v(33.25, 37.12) * mm});
            skLineSegment(sketch, "E901", {"start": v(33.25, 37.12) * mm, "end": v(33.19, 37.08) * mm});
            skLineSegment(sketch, "E902", {"start": v(33.19, 37.08) * mm, "end": v(33.12, 37.05) * mm});
            skLineSegment(sketch, "E903", {"start": v(33.12, 37.05) * mm, "end": v(33.06, 37.02) * mm});
            skLineSegment(sketch, "E904", {"start": v(33.06, 37.02) * mm, "end": v(33, 36.98) * mm});
            skLineSegment(sketch, "E905", {"start": v(33, 36.98) * mm, "end": v(32.94, 36.95) * mm});
            skLineSegment(sketch, "E906", {"start": v(32.94, 36.95) * mm, "end": v(32.88, 36.91) * mm});
            skLineSegment(sketch, "E907", {"start": v(32.88, 36.91) * mm, "end": v(32.83, 36.88) * mm});
            skLineSegment(sketch, "E908", {"start": v(32.83, 36.88) * mm, "end": v(32.77, 36.85) * mm});
            skLineSegment(sketch, "E909", {"start": v(32.77, 36.85) * mm, "end": v(32.71, 36.81) * mm});
            skLineSegment(sketch, "E910", {"start": v(32.71, 36.81) * mm, "end": v(32.66, 36.78) * mm});
            skLineSegment(sketch, "E911", {"start": v(32.66, 36.78) * mm, "end": v(32.6, 36.75) * mm});
            skLineSegment(sketch, "E912", {"start": v(32.6, 36.75) * mm, "end": v(32.55, 36.72) * mm});
            skLineSegment(sketch, "E913", {"start": v(32.55, 36.72) * mm, "end": v(32.5, 36.68) * mm});
            skLineSegment(sketch, "E914", {"start": v(32.5, 36.68) * mm, "end": v(32.45, 36.65) * mm});
            skLineSegment(sketch, "E915", {"start": v(32.45, 36.65) * mm, "end": v(32.4, 36.62) * mm});
            skLineSegment(sketch, "E916", {"start": v(32.4, 36.62) * mm, "end": v(32.35, 36.59) * mm});
            skLineSegment(sketch, "E917", {"start": v(32.35, 36.59) * mm, "end": v(32.3, 36.56) * mm});
            skLineSegment(sketch, "E918", {"start": v(32.3, 36.56) * mm, "end": v(32.25, 36.53) * mm});
            skLineSegment(sketch, "E919", {"start": v(32.25, 36.53) * mm, "end": v(32.2, 36.5) * mm});
            skLineSegment(sketch, "E920", {"start": v(32.2, 36.5) * mm, "end": v(32.16, 36.46) * mm});
            skLineSegment(sketch, "E921", {"start": v(32.16, 36.46) * mm, "end": v(32.12, 36.43) * mm});
            skLineSegment(sketch, "E922", {"start": v(32.12, 36.43) * mm, "end": v(31.9, 36.61) * mm});
            skLineSegment(sketch, "E923", {"start": v(31.9, 36.61) * mm, "end": v(31.54, 36.93) * mm});
            skLineSegment(sketch, "E924", {"start": v(31.54, 36.93) * mm, "end": v(31.33, 37.11) * mm});
            skLineSegment(sketch, "E925", {"start": v(31.33, 37.11) * mm, "end": v(31.35, 37.16) * mm});
            skLineSegment(sketch, "E926", {"start": v(31.35, 37.16) * mm, "end": v(31.38, 37.21) * mm});
            skLineSegment(sketch, "E927", {"start": v(31.38, 37.21) * mm, "end": v(31.4, 37.26) * mm});
            skLineSegment(sketch, "E928", {"start": v(31.4, 37.26) * mm, "end": v(31.42, 37.31) * mm});
            skLineSegment(sketch, "E929", {"start": v(31.42, 37.31) * mm, "end": v(31.45, 37.37) * mm});
            skLineSegment(sketch, "E930", {"start": v(31.45, 37.37) * mm, "end": v(31.47, 37.42) * mm});
            skLineSegment(sketch, "E931", {"start": v(31.47, 37.42) * mm, "end": v(31.5, 37.47) * mm});
            skLineSegment(sketch, "E932", {"start": v(31.5, 37.47) * mm, "end": v(31.52, 37.53) * mm});
            skLineSegment(sketch, "E933", {"start": v(31.52, 37.53) * mm, "end": v(31.54, 37.59) * mm});
            skLineSegment(sketch, "E934", {"start": v(31.54, 37.59) * mm, "end": v(31.57, 37.64) * mm});
            skLineSegment(sketch, "E935", {"start": v(31.57, 37.64) * mm, "end": v(31.6, 37.7) * mm});
            skLineSegment(sketch, "E936", {"start": v(31.6, 37.7) * mm, "end": v(31.62, 37.76) * mm});
            skLineSegment(sketch, "E937", {"start": v(31.62, 37.76) * mm, "end": v(31.64, 37.82) * mm});
            skLineSegment(sketch, "E938", {"start": v(31.64, 37.82) * mm, "end": v(31.67, 37.88) * mm});
            skLineSegment(sketch, "E939", {"start": v(31.67, 37.88) * mm, "end": v(31.7, 37.94) * mm});
            skLineSegment(sketch, "E940", {"start": v(31.7, 37.94) * mm, "end": v(31.72, 38) * mm});
            skLineSegment(sketch, "E941", {"start": v(31.72, 38) * mm, "end": v(31.74, 38.07) * mm});
            skLineSegment(sketch, "E942", {"start": v(31.74, 38.07) * mm, "end": v(31.77, 38.13) * mm});
            skLineSegment(sketch, "E943", {"start": v(31.77, 38.13) * mm, "end": v(31.8, 38.2) * mm});
            skLineSegment(sketch, "E944", {"start": v(31.8, 38.2) * mm, "end": v(31.82, 38.27) * mm});
            skLineSegment(sketch, "E945", {"start": v(31.82, 38.27) * mm, "end": v(31.84, 38.33) * mm});
            skLineSegment(sketch, "E946", {"start": v(31.84, 38.33) * mm, "end": v(31.87, 38.4) * mm});
            skLineSegment(sketch, "E947", {"start": v(31.87, 38.4) * mm, "end": v(31.9, 38.47) * mm});
            skLineSegment(sketch, "E948", {"start": v(31.9, 38.47) * mm, "end": v(31.92, 38.54) * mm});
            skLineSegment(sketch, "E949", {"start": v(31.92, 38.54) * mm, "end": v(31.94, 38.61) * mm});
            skLineSegment(sketch, "E950", {"start": v(31.94, 38.61) * mm, "end": v(31.97, 38.68) * mm});
            skLineSegment(sketch, "E951", {"start": v(31.97, 38.68) * mm, "end": v(32, 38.76) * mm});
            skLineSegment(sketch, "E952", {"start": v(32, 38.76) * mm, "end": v(32.02, 38.83) * mm});
            skLineSegment(sketch, "E953", {"start": v(32.02, 38.83) * mm, "end": v(32.04, 38.9) * mm});
            skLineSegment(sketch, "E954", {"start": v(32.04, 38.9) * mm, "end": v(32.07, 38.98) * mm});
            skLineSegment(sketch, "E955", {"start": v(32.07, 38.98) * mm, "end": v(32.1, 39.06) * mm});
            skLineSegment(sketch, "E956", {"start": v(32.1, 39.06) * mm, "end": v(32.12, 39.14) * mm});
            skLineSegment(sketch, "E957", {"start": v(32.12, 39.14) * mm, "end": v(32.14, 39.22) * mm});
            skLineSegment(sketch, "E958", {"start": v(32.14, 39.22) * mm, "end": v(32.17, 39.3) * mm});
            skLineSegment(sketch, "E959", {"start": v(32.17, 39.3) * mm, "end": v(32.2, 39.38) * mm});
            skLineSegment(sketch, "E960", {"start": v(32.2, 39.38) * mm, "end": v(32.21, 39.46) * mm});
            skLineSegment(sketch, "E961", {"start": v(32.21, 39.46) * mm, "end": v(32.24, 39.54) * mm});
            skLineSegment(sketch, "E962", {"start": v(32.24, 39.54) * mm, "end": v(32.26, 39.63) * mm});
            skLineSegment(sketch, "E963", {"start": v(32.26, 39.63) * mm, "end": v(32.29, 39.71) * mm});
            skLineSegment(sketch, "E964", {"start": v(32.29, 39.71) * mm, "end": v(32.3, 39.79) * mm});
            skLineSegment(sketch, "E965", {"start": v(32.3, 39.79) * mm, "end": v(31.55, 40.39) * mm});
            skLineSegment(sketch, "E966", {"start": v(31.55, 40.39) * mm, "end": v(31.48, 40.36) * mm});
            skLineSegment(sketch, "E967", {"start": v(31.48, 40.36) * mm, "end": v(31.4, 40.31) * mm});
            skLineSegment(sketch, "E968", {"start": v(31.4, 40.31) * mm, "end": v(31.32, 40.27) * mm});
            skLineSegment(sketch, "E969", {"start": v(31.32, 40.27) * mm, "end": v(31.25, 40.23) * mm});
            skLineSegment(sketch, "E970", {"start": v(31.25, 40.23) * mm, "end": v(31.17, 40.19) * mm});
            skLineSegment(sketch, "E971", {"start": v(31.17, 40.19) * mm, "end": v(31.1, 40.15) * mm});
            skLineSegment(sketch, "E972", {"start": v(31.1, 40.15) * mm, "end": v(31.03, 40.1) * mm});
            skLineSegment(sketch, "E973", {"start": v(31.03, 40.1) * mm, "end": v(30.96, 40.06) * mm});
            skLineSegment(sketch, "E974", {"start": v(30.96, 40.06) * mm, "end": v(30.89, 40.02) * mm});
            skLineSegment(sketch, "E975", {"start": v(30.89, 40.02) * mm, "end": v(30.82, 39.98) * mm});
            skLineSegment(sketch, "E976", {"start": v(30.82, 39.98) * mm, "end": v(30.75, 39.94) * mm});
            skLineSegment(sketch, "E977", {"start": v(30.75, 39.94) * mm, "end": v(30.68, 39.9) * mm});
            skLineSegment(sketch, "E978", {"start": v(30.68, 39.9) * mm, "end": v(30.61, 39.86) * mm});
            skLineSegment(sketch, "E979", {"start": v(30.61, 39.86) * mm, "end": v(30.55, 39.81) * mm});
            skLineSegment(sketch, "E980", {"start": v(30.55, 39.81) * mm, "end": v(30.48, 39.77) * mm});
            skLineSegment(sketch, "E981", {"start": v(30.48, 39.77) * mm, "end": v(30.42, 39.73) * mm});
            skLineSegment(sketch, "E982", {"start": v(30.42, 39.73) * mm, "end": v(30.36, 39.7) * mm});
            skLineSegment(sketch, "E983", {"start": v(30.36, 39.7) * mm, "end": v(30.3, 39.65) * mm});
            skLineSegment(sketch, "E984", {"start": v(30.3, 39.65) * mm, "end": v(30.23, 39.61) * mm});
            skLineSegment(sketch, "E985", {"start": v(30.23, 39.61) * mm, "end": v(30.17, 39.57) * mm});
            skLineSegment(sketch, "E986", {"start": v(30.17, 39.57) * mm, "end": v(30.11, 39.53) * mm});
            skLineSegment(sketch, "E987", {"start": v(30.11, 39.53) * mm, "end": v(30.06, 39.5) * mm});
            skLineSegment(sketch, "E988", {"start": v(30.06, 39.5) * mm, "end": v(30, 39.46) * mm});
            skLineSegment(sketch, "E989", {"start": v(30, 39.46) * mm, "end": v(29.94, 39.42) * mm});
            skLineSegment(sketch, "E990", {"start": v(29.94, 39.42) * mm, "end": v(29.89, 39.38) * mm});
            skLineSegment(sketch, "E991", {"start": v(29.89, 39.38) * mm, "end": v(29.83, 39.34) * mm});
            skLineSegment(sketch, "E992", {"start": v(29.83, 39.34) * mm, "end": v(29.78, 39.3) * mm});
            skLineSegment(sketch, "E993", {"start": v(29.78, 39.3) * mm, "end": v(29.72, 39.27) * mm});
            skLineSegment(sketch, "E994", {"start": v(29.72, 39.27) * mm, "end": v(29.67, 39.23) * mm});
            skLineSegment(sketch, "E995", {"start": v(29.67, 39.23) * mm, "end": v(29.62, 39.2) * mm});
            skLineSegment(sketch, "E996", {"start": v(29.62, 39.2) * mm, "end": v(29.57, 39.16) * mm});
            skLineSegment(sketch, "E997", {"start": v(29.57, 39.16) * mm, "end": v(29.52, 39.12) * mm});
            skLineSegment(sketch, "E998", {"start": v(29.52, 39.12) * mm, "end": v(29.47, 39.08) * mm});
            skLineSegment(sketch, "E999", {"start": v(29.47, 39.08) * mm, "end": v(29.43, 39.05) * mm});
            skLineSegment(sketch, "E1000", {"start": v(29.43, 39.05) * mm, "end": v(29.38, 39.01) * mm});
            skLineSegment(sketch, "E1001", {"start": v(29.38, 39.01) * mm, "end": v(29.33, 38.98) * mm});
            skLineSegment(sketch, "E1002", {"start": v(29.33, 38.98) * mm, "end": v(29.29, 38.94) * mm});
            skLineSegment(sketch, "E1003", {"start": v(29.29, 38.94) * mm, "end": v(29.24, 38.9) * mm});
            skLineSegment(sketch, "E1004", {"start": v(29.24, 38.9) * mm, "end": v(29.2, 38.88) * mm});
            skLineSegment(sketch, "E1005", {"start": v(29.2, 38.88) * mm, "end": v(29.16, 38.84) * mm});
            skLineSegment(sketch, "E1006", {"start": v(29.16, 38.84) * mm, "end": v(28.93, 39) * mm});
            skLineSegment(sketch, "E1007", {"start": v(28.93, 39) * mm, "end": v(28.54, 39.29) * mm});
            skLineSegment(sketch, "E1008", {"start": v(28.54, 39.29) * mm, "end": v(28.32, 39.46) * mm});
            skLineSegment(sketch, "E1009", {"start": v(28.32, 39.46) * mm, "end": v(28.34, 39.5) * mm});
            skLineSegment(sketch, "E1010", {"start": v(28.34, 39.5) * mm, "end": v(28.36, 39.56) * mm});
            skLineSegment(sketch, "E1011", {"start": v(28.36, 39.56) * mm, "end": v(28.38, 39.61) * mm});
            skLineSegment(sketch, "E1012", {"start": v(28.38, 39.61) * mm, "end": v(28.4, 39.66) * mm});
            skLineSegment(sketch, "E1013", {"start": v(28.4, 39.66) * mm, "end": v(28.42, 39.72) * mm});
            skLineSegment(sketch, "E1014", {"start": v(28.42, 39.72) * mm, "end": v(28.44, 39.77) * mm});
            skLineSegment(sketch, "E1015", {"start": v(28.44, 39.77) * mm, "end": v(28.46, 39.83) * mm});
            skLineSegment(sketch, "E1016", {"start": v(28.46, 39.83) * mm, "end": v(28.48, 39.89) * mm});
            skLineSegment(sketch, "E1017", {"start": v(28.48, 39.89) * mm, "end": v(28.5, 39.94) * mm});
            skLineSegment(sketch, "E1018", {"start": v(28.5, 39.94) * mm, "end": v(28.52, 40) * mm});
            skLineSegment(sketch, "E1019", {"start": v(28.52, 40) * mm, "end": v(28.54, 40.06) * mm});
            skLineSegment(sketch, "E1020", {"start": v(28.54, 40.06) * mm, "end": v(28.56, 40.12) * mm});
            skLineSegment(sketch, "E1021", {"start": v(28.56, 40.12) * mm, "end": v(28.58, 40.19) * mm});
            skLineSegment(sketch, "E1022", {"start": v(28.58, 40.19) * mm, "end": v(28.6, 40.25) * mm});
            skLineSegment(sketch, "E1023", {"start": v(28.6, 40.25) * mm, "end": v(28.62, 40.31) * mm});
            skLineSegment(sketch, "E1024", {"start": v(28.62, 40.31) * mm, "end": v(28.64, 40.38) * mm});
            skLineSegment(sketch, "E1025", {"start": v(28.64, 40.38) * mm, "end": v(28.66, 40.44) * mm});
            skLineSegment(sketch, "E1026", {"start": v(28.66, 40.44) * mm, "end": v(28.68, 40.5) * mm});
            skLineSegment(sketch, "E1027", {"start": v(28.68, 40.5) * mm, "end": v(28.7, 40.58) * mm});
            skLineSegment(sketch, "E1028", {"start": v(28.7, 40.58) * mm, "end": v(28.72, 40.64) * mm});
            skLineSegment(sketch, "E1029", {"start": v(28.72, 40.64) * mm, "end": v(28.74, 40.71) * mm});
            skLineSegment(sketch, "E1030", {"start": v(28.74, 40.71) * mm, "end": v(28.76, 40.78) * mm});
            skLineSegment(sketch, "E1031", {"start": v(28.76, 40.78) * mm, "end": v(28.78, 40.85) * mm});
            skLineSegment(sketch, "E1032", {"start": v(28.78, 40.85) * mm, "end": v(28.8, 40.93) * mm});
            skLineSegment(sketch, "E1033", {"start": v(28.8, 40.93) * mm, "end": v(28.81, 41) * mm});
            skLineSegment(sketch, "E1034", {"start": v(28.81, 41) * mm, "end": v(28.83, 41.07) * mm});
            skLineSegment(sketch, "E1035", {"start": v(28.83, 41.07) * mm, "end": v(28.85, 41.15) * mm});
            skLineSegment(sketch, "E1036", {"start": v(28.85, 41.15) * mm, "end": v(28.87, 41.22) * mm});
            skLineSegment(sketch, "E1037", {"start": v(28.87, 41.22) * mm, "end": v(28.9, 41.3) * mm});
            skLineSegment(sketch, "E1038", {"start": v(28.9, 41.3) * mm, "end": v(28.9, 41.38) * mm});
            skLineSegment(sketch, "E1039", {"start": v(28.9, 41.38) * mm, "end": v(28.93, 41.46) * mm});
            skLineSegment(sketch, "E1040", {"start": v(28.93, 41.46) * mm, "end": v(28.95, 41.54) * mm});
            skLineSegment(sketch, "E1041", {"start": v(28.95, 41.54) * mm, "end": v(28.97, 41.62) * mm});
            skLineSegment(sketch, "E1042", {"start": v(28.97, 41.62) * mm, "end": v(28.98, 41.7) * mm});
            skLineSegment(sketch, "E1043", {"start": v(28.98, 41.7) * mm, "end": v(29, 41.78) * mm});
            skLineSegment(sketch, "E1044", {"start": v(29, 41.78) * mm, "end": v(29.02, 41.87) * mm});
            skLineSegment(sketch, "E1045", {"start": v(29.02, 41.87) * mm, "end": v(29.04, 41.95) * mm});
            skLineSegment(sketch, "E1046", {"start": v(29.04, 41.95) * mm, "end": v(29.05, 42.04) * mm});
            skLineSegment(sketch, "E1047", {"start": v(29.05, 42.04) * mm, "end": v(29.07, 42.12) * mm});
            skLineSegment(sketch, "E1048", {"start": v(29.07, 42.12) * mm, "end": v(29.08, 42.2) * mm});
            skLineSegment(sketch, "E1049", {"start": v(29.08, 42.2) * mm, "end": v(28.28, 42.74) * mm});
            skLineSegment(sketch, "E1050", {"start": v(28.28, 42.74) * mm, "end": v(28.21, 42.7) * mm});
            skLineSegment(sketch, "E1051", {"start": v(28.21, 42.7) * mm, "end": v(28.14, 42.65) * mm});
            skLineSegment(sketch, "E1052", {"start": v(28.14, 42.65) * mm, "end": v(28.07, 42.6) * mm});
            skLineSegment(sketch, "E1053", {"start": v(28.07, 42.6) * mm, "end": v(28, 42.56) * mm});
            skLineSegment(sketch, "E1054", {"start": v(28, 42.56) * mm, "end": v(27.93, 42.5) * mm});
            skLineSegment(sketch, "E1055", {"start": v(27.93, 42.5) * mm, "end": v(27.86, 42.46) * mm});
            skLineSegment(sketch, "E1056", {"start": v(27.86, 42.46) * mm, "end": v(27.79, 42.41) * mm});
            skLineSegment(sketch, "E1057", {"start": v(27.79, 42.41) * mm, "end": v(27.72, 42.37) * mm});
            skLineSegment(sketch, "E1058", {"start": v(27.72, 42.37) * mm, "end": v(27.65, 42.32) * mm});
            skLineSegment(sketch, "E1059", {"start": v(27.65, 42.32) * mm, "end": v(27.59, 42.27) * mm});
            skLineSegment(sketch, "E1060", {"start": v(27.59, 42.27) * mm, "end": v(27.52, 42.23) * mm});
            skLineSegment(sketch, "E1061", {"start": v(27.52, 42.23) * mm, "end": v(27.46, 42.18) * mm});
            skLineSegment(sketch, "E1062", {"start": v(27.46, 42.18) * mm, "end": v(27.4, 42.13) * mm});
            skLineSegment(sketch, "E1063", {"start": v(27.4, 42.13) * mm, "end": v(27.33, 42.09) * mm});
            skLineSegment(sketch, "E1064", {"start": v(27.33, 42.09) * mm, "end": v(27.27, 42.04) * mm});
            skLineSegment(sketch, "E1065", {"start": v(27.27, 42.04) * mm, "end": v(27.2, 42) * mm});
            skLineSegment(sketch, "E1066", {"start": v(27.2, 42) * mm, "end": v(27.15, 41.95) * mm});
            skLineSegment(sketch, "E1067", {"start": v(27.15, 41.95) * mm, "end": v(27.1, 41.9) * mm});
            skLineSegment(sketch, "E1068", {"start": v(27.1, 41.9) * mm, "end": v(27.03, 41.86) * mm});
            skLineSegment(sketch, "E1069", {"start": v(27.03, 41.86) * mm, "end": v(26.98, 41.82) * mm});
            skLineSegment(sketch, "E1070", {"start": v(26.98, 41.82) * mm, "end": v(26.92, 41.78) * mm});
            skLineSegment(sketch, "E1071", {"start": v(26.92, 41.78) * mm, "end": v(26.86, 41.73) * mm});
            skLineSegment(sketch, "E1072", {"start": v(26.86, 41.73) * mm, "end": v(26.81, 41.69) * mm});
            skLineSegment(sketch, "E1073", {"start": v(26.81, 41.69) * mm, "end": v(26.76, 41.65) * mm});
            skLineSegment(sketch, "E1074", {"start": v(26.76, 41.65) * mm, "end": v(26.7, 41.6) * mm});
            skLineSegment(sketch, "E1075", {"start": v(26.7, 41.6) * mm, "end": v(26.65, 41.56) * mm});
            skLineSegment(sketch, "E1076", {"start": v(26.65, 41.56) * mm, "end": v(26.6, 41.52) * mm});
            skLineSegment(sketch, "E1077", {"start": v(26.6, 41.52) * mm, "end": v(26.55, 41.48) * mm});
            skLineSegment(sketch, "E1078", {"start": v(26.55, 41.48) * mm, "end": v(26.5, 41.44) * mm});
            skLineSegment(sketch, "E1079", {"start": v(26.5, 41.44) * mm, "end": v(26.46, 41.4) * mm});
            skLineSegment(sketch, "E1080", {"start": v(26.46, 41.4) * mm, "end": v(26.4, 41.36) * mm});
            skLineSegment(sketch, "E1081", {"start": v(26.4, 41.36) * mm, "end": v(26.36, 41.32) * mm});
            skLineSegment(sketch, "E1082", {"start": v(26.36, 41.32) * mm, "end": v(26.32, 41.28) * mm});
            skLineSegment(sketch, "E1083", {"start": v(26.32, 41.28) * mm, "end": v(26.27, 41.24) * mm});
            skLineSegment(sketch, "E1084", {"start": v(26.27, 41.24) * mm, "end": v(26.23, 41.2) * mm});
            skLineSegment(sketch, "E1085", {"start": v(26.23, 41.2) * mm, "end": v(26.18, 41.16) * mm});
            skLineSegment(sketch, "E1086", {"start": v(26.18, 41.16) * mm, "end": v(26.14, 41.12) * mm});
            skLineSegment(sketch, "E1087", {"start": v(26.14, 41.12) * mm, "end": v(26.1, 41.08) * mm});
            skLineSegment(sketch, "E1088", {"start": v(26.1, 41.08) * mm, "end": v(26.06, 41.05) * mm});
            skLineSegment(sketch, "E1089", {"start": v(26.06, 41.05) * mm, "end": v(26.02, 41) * mm});
            skLineSegment(sketch, "E1090", {"start": v(26.02, 41) * mm, "end": v(25.78, 41.15) * mm});
            skLineSegment(sketch, "E1091", {"start": v(25.78, 41.15) * mm, "end": v(25.37, 41.4) * mm});
            skLineSegment(sketch, "E1092", {"start": v(25.37, 41.4) * mm, "end": v(25.14, 41.56) * mm});
            skLineSegment(sketch, "E1093", {"start": v(25.14, 41.56) * mm, "end": v(25.15, 41.6) * mm});
            skLineSegment(sketch, "E1094", {"start": v(25.15, 41.6) * mm, "end": v(25.17, 41.66) * mm});
            skLineSegment(sketch, "E1095", {"start": v(25.17, 41.66) * mm, "end": v(25.18, 41.71) * mm});
            skLineSegment(sketch, "E1096", {"start": v(25.18, 41.71) * mm, "end": v(25.2, 41.77) * mm});
            skLineSegment(sketch, "E1097", {"start": v(25.2, 41.77) * mm, "end": v(25.21, 41.83) * mm});
            skLineSegment(sketch, "E1098", {"start": v(25.21, 41.83) * mm, "end": v(25.23, 41.88) * mm});
            skLineSegment(sketch, "E1099", {"start": v(25.23, 41.88) * mm, "end": v(25.25, 41.94) * mm});
            skLineSegment(sketch, "E1100", {"start": v(25.25, 41.94) * mm, "end": v(25.26, 42) * mm});
            skLineSegment(sketch, "E1101", {"start": v(25.26, 42) * mm, "end": v(25.28, 42.06) * mm});
            skLineSegment(sketch, "E1102", {"start": v(25.28, 42.06) * mm, "end": v(25.3, 42.12) * mm});
            skLineSegment(sketch, "E1103", {"start": v(25.3, 42.12) * mm, "end": v(25.3, 42.18) * mm});
            skLineSegment(sketch, "E1104", {"start": v(25.3, 42.18) * mm, "end": v(25.32, 42.24) * mm});
            skLineSegment(sketch, "E1105", {"start": v(25.32, 42.24) * mm, "end": v(25.34, 42.3) * mm});
            skLineSegment(sketch, "E1106", {"start": v(25.34, 42.3) * mm, "end": v(25.35, 42.37) * mm});
            skLineSegment(sketch, "E1107", {"start": v(25.35, 42.37) * mm, "end": v(25.37, 42.43) * mm});
            skLineSegment(sketch, "E1108", {"start": v(25.37, 42.43) * mm, "end": v(25.38, 42.5) * mm});
            skLineSegment(sketch, "E1109", {"start": v(25.38, 42.5) * mm, "end": v(25.4, 42.57) * mm});
            skLineSegment(sketch, "E1110", {"start": v(25.4, 42.57) * mm, "end": v(25.4, 42.63) * mm});
            skLineSegment(sketch, "E1111", {"start": v(25.4, 42.63) * mm, "end": v(25.42, 42.7) * mm});
            skLineSegment(sketch, "E1112", {"start": v(25.42, 42.7) * mm, "end": v(25.44, 42.77) * mm});
            skLineSegment(sketch, "E1113", {"start": v(25.44, 42.77) * mm, "end": v(25.45, 42.84) * mm});
            skLineSegment(sketch, "E1114", {"start": v(25.45, 42.84) * mm, "end": v(25.47, 42.91) * mm});
            skLineSegment(sketch, "E1115", {"start": v(25.47, 42.91) * mm, "end": v(25.48, 42.99) * mm});
            skLineSegment(sketch, "E1116", {"start": v(25.48, 42.99) * mm, "end": v(25.5, 43.06) * mm});
            skLineSegment(sketch, "E1117", {"start": v(25.5, 43.06) * mm, "end": v(25.5, 43.13) * mm});
            skLineSegment(sketch, "E1118", {"start": v(25.5, 43.13) * mm, "end": v(25.52, 43.2) * mm});
            skLineSegment(sketch, "E1119", {"start": v(25.52, 43.2) * mm, "end": v(25.54, 43.29) * mm});
            skLineSegment(sketch, "E1120", {"start": v(25.54, 43.29) * mm, "end": v(25.55, 43.36) * mm});
            skLineSegment(sketch, "E1121", {"start": v(25.55, 43.36) * mm, "end": v(25.56, 43.44) * mm});
            skLineSegment(sketch, "E1122", {"start": v(25.56, 43.44) * mm, "end": v(25.57, 43.52) * mm});
            skLineSegment(sketch, "E1123", {"start": v(25.57, 43.52) * mm, "end": v(25.59, 43.6) * mm});
            skLineSegment(sketch, "E1124", {"start": v(25.59, 43.6) * mm, "end": v(25.6, 43.68) * mm});
            skLineSegment(sketch, "E1125", {"start": v(25.6, 43.68) * mm, "end": v(25.61, 43.76) * mm});
            skLineSegment(sketch, "E1126", {"start": v(25.61, 43.76) * mm, "end": v(25.62, 43.85) * mm});
            skLineSegment(sketch, "E1127", {"start": v(25.62, 43.85) * mm, "end": v(25.63, 43.93) * mm});
            skLineSegment(sketch, "E1128", {"start": v(25.63, 43.93) * mm, "end": v(25.65, 44.01) * mm});
            skLineSegment(sketch, "E1129", {"start": v(25.65, 44.01) * mm, "end": v(25.66, 44.1) * mm});
            skLineSegment(sketch, "E1130", {"start": v(25.66, 44.1) * mm, "end": v(25.67, 44.19) * mm});
            skLineSegment(sketch, "E1131", {"start": v(25.67, 44.19) * mm, "end": v(25.68, 44.27) * mm});
            skLineSegment(sketch, "E1132", {"start": v(25.68, 44.27) * mm, "end": v(25.68, 44.35) * mm});
            skLineSegment(sketch, "E1133", {"start": v(25.68, 44.35) * mm, "end": v(24.84, 44.83) * mm});
            skLineSegment(sketch, "E1134", {"start": v(24.84, 44.83) * mm, "end": v(24.78, 44.78) * mm});
            skLineSegment(sketch, "E1135", {"start": v(24.78, 44.78) * mm, "end": v(24.7, 44.73) * mm});
            skLineSegment(sketch, "E1136", {"start": v(24.7, 44.73) * mm, "end": v(24.64, 44.68) * mm});
            skLineSegment(sketch, "E1137", {"start": v(24.64, 44.68) * mm, "end": v(24.57, 44.62) * mm});
            skLineSegment(sketch, "E1138", {"start": v(24.57, 44.62) * mm, "end": v(24.5, 44.57) * mm});
            skLineSegment(sketch, "E1139", {"start": v(24.5, 44.57) * mm, "end": v(24.44, 44.52) * mm});
            skLineSegment(sketch, "E1140", {"start": v(24.44, 44.52) * mm, "end": v(24.37, 44.46) * mm});
            skLineSegment(sketch, "E1141", {"start": v(24.37, 44.46) * mm, "end": v(24.3, 44.41) * mm});
            skLineSegment(sketch, "E1142", {"start": v(24.3, 44.41) * mm, "end": v(24.25, 44.36) * mm});
            skLineSegment(sketch, "E1143", {"start": v(24.25, 44.36) * mm, "end": v(24.18, 44.3) * mm});
            skLineSegment(sketch, "E1144", {"start": v(24.18, 44.3) * mm, "end": v(24.12, 44.26) * mm});
            skLineSegment(sketch, "E1145", {"start": v(24.12, 44.26) * mm, "end": v(24.06, 44.2) * mm});
            skLineSegment(sketch, "E1146", {"start": v(24.06, 44.2) * mm, "end": v(24, 44.15) * mm});
            skLineSegment(sketch, "E1147", {"start": v(24, 44.15) * mm, "end": v(23.94, 44.1) * mm});
            skLineSegment(sketch, "E1148", {"start": v(23.94, 44.1) * mm, "end": v(23.89, 44.05) * mm});
            skLineSegment(sketch, "E1149", {"start": v(23.89, 44.05) * mm, "end": v(23.83, 44) * mm});
            skLineSegment(sketch, "E1150", {"start": v(23.83, 44) * mm, "end": v(23.77, 43.95) * mm});
            skLineSegment(sketch, "E1151", {"start": v(23.77, 43.95) * mm, "end": v(23.72, 43.9) * mm});
            skLineSegment(sketch, "E1152", {"start": v(23.72, 43.9) * mm, "end": v(23.66, 43.86) * mm});
            skLineSegment(sketch, "E1153", {"start": v(23.66, 43.86) * mm, "end": v(23.61, 43.8) * mm});
            skLineSegment(sketch, "E1154", {"start": v(23.61, 43.8) * mm, "end": v(23.56, 43.76) * mm});
            skLineSegment(sketch, "E1155", {"start": v(23.56, 43.76) * mm, "end": v(23.5, 43.71) * mm});
            skLineSegment(sketch, "E1156", {"start": v(23.5, 43.71) * mm, "end": v(23.46, 43.66) * mm});
            skLineSegment(sketch, "E1157", {"start": v(23.46, 43.66) * mm, "end": v(23.4, 43.62) * mm});
            skLineSegment(sketch, "E1158", {"start": v(23.4, 43.62) * mm, "end": v(23.36, 43.57) * mm});
            skLineSegment(sketch, "E1159", {"start": v(23.36, 43.57) * mm, "end": v(23.3, 43.52) * mm});
            skLineSegment(sketch, "E1160", {"start": v(23.3, 43.52) * mm, "end": v(23.26, 43.48) * mm});
            skLineSegment(sketch, "E1161", {"start": v(23.26, 43.48) * mm, "end": v(23.22, 43.43) * mm});
            skLineSegment(sketch, "E1162", {"start": v(23.22, 43.43) * mm, "end": v(23.17, 43.39) * mm});
            skLineSegment(sketch, "E1163", {"start": v(23.17, 43.39) * mm, "end": v(23.13, 43.34) * mm});
            skLineSegment(sketch, "E1164", {"start": v(23.13, 43.34) * mm, "end": v(23.08, 43.3) * mm});
            skLineSegment(sketch, "E1165", {"start": v(23.08, 43.3) * mm, "end": v(23.04, 43.26) * mm});
            skLineSegment(sketch, "E1166", {"start": v(23.04, 43.26) * mm, "end": v(23, 43.21) * mm});
            skLineSegment(sketch, "E1167", {"start": v(23, 43.21) * mm, "end": v(22.96, 43.17) * mm});
            skLineSegment(sketch, "E1168", {"start": v(22.96, 43.17) * mm, "end": v(22.91, 43.13) * mm});
            skLineSegment(sketch, "E1169", {"start": v(22.91, 43.13) * mm, "end": v(22.87, 43.09) * mm});
            skLineSegment(sketch, "E1170", {"start": v(22.87, 43.09) * mm, "end": v(22.84, 43.05) * mm});
            skLineSegment(sketch, "E1171", {"start": v(22.84, 43.05) * mm, "end": v(22.8, 43) * mm});
            skLineSegment(sketch, "E1172", {"start": v(22.8, 43) * mm, "end": v(22.76, 42.96) * mm});
            skLineSegment(sketch, "E1173", {"start": v(22.76, 42.96) * mm, "end": v(22.72, 42.92) * mm});
            skLineSegment(sketch, "E1174", {"start": v(22.72, 42.92) * mm, "end": v(22.47, 43.05) * mm});
            skLineSegment(sketch, "E1175", {"start": v(22.47, 43.05) * mm, "end": v(22.05, 43.27) * mm});
            skLineSegment(sketch, "E1176", {"start": v(22.05, 43.27) * mm, "end": v(21.8, 43.4) * mm});
            skLineSegment(sketch, "E1177", {"start": v(21.8, 43.4) * mm, "end": v(21.81, 43.45) * mm});
            skLineSegment(sketch, "E1178", {"start": v(21.81, 43.45) * mm, "end": v(21.82, 43.5) * mm});
            skLineSegment(sketch, "E1179", {"start": v(21.82, 43.5) * mm, "end": v(21.83, 43.56) * mm});
            skLineSegment(sketch, "E1180", {"start": v(21.83, 43.56) * mm, "end": v(21.84, 43.62) * mm});
            skLineSegment(sketch, "E1181", {"start": v(21.84, 43.62) * mm, "end": v(21.86, 43.67) * mm});
            skLineSegment(sketch, "E1182", {"start": v(21.86, 43.67) * mm, "end": v(21.87, 43.73) * mm});
            skLineSegment(sketch, "E1183", {"start": v(21.87, 43.73) * mm, "end": v(21.88, 43.8) * mm});
            skLineSegment(sketch, "E1184", {"start": v(21.88, 43.8) * mm, "end": v(21.89, 43.85) * mm});
            skLineSegment(sketch, "E1185", {"start": v(21.89, 43.85) * mm, "end": v(21.9, 43.91) * mm});
            skLineSegment(sketch, "E1186", {"start": v(21.9, 43.91) * mm, "end": v(21.9, 43.97) * mm});
            skLineSegment(sketch, "E1187", {"start": v(21.9, 43.97) * mm, "end": v(21.92, 44.03) * mm});
            skLineSegment(sketch, "E1188", {"start": v(21.92, 44.03) * mm, "end": v(21.93, 44.1) * mm});
            skLineSegment(sketch, "E1189", {"start": v(21.93, 44.1) * mm, "end": v(21.94, 44.16) * mm});
            skLineSegment(sketch, "E1190", {"start": v(21.94, 44.16) * mm, "end": v(21.95, 44.23) * mm});
            skLineSegment(sketch, "E1191", {"start": v(21.95, 44.23) * mm, "end": v(21.96, 44.3) * mm});
            skLineSegment(sketch, "E1192", {"start": v(21.96, 44.3) * mm, "end": v(21.97, 44.36) * mm});
            skLineSegment(sketch, "E1193", {"start": v(21.97, 44.36) * mm, "end": v(21.98, 44.43) * mm});
            skLineSegment(sketch, "E1194", {"start": v(21.98, 44.43) * mm, "end": v(21.99, 44.5) * mm});
            skLineSegment(sketch, "E1195", {"start": v(21.99, 44.5) * mm, "end": v(22, 44.57) * mm});
            skLineSegment(sketch, "E1196", {"start": v(22, 44.57) * mm, "end": v(22, 44.64) * mm});
            skLineSegment(sketch, "E1197", {"start": v(22, 44.64) * mm, "end": v(22.01, 44.7) * mm});
            skLineSegment(sketch, "E1198", {"start": v(22.01, 44.7) * mm, "end": v(22.02, 44.78) * mm});
            skLineSegment(sketch, "E1199", {"start": v(22.02, 44.78) * mm, "end": v(22.03, 44.85) * mm});
            skLineSegment(sketch, "E1200", {"start": v(22.03, 44.85) * mm, "end": v(22.04, 44.93) * mm});
            skLineSegment(sketch, "E1201", {"start": v(22.04, 44.93) * mm, "end": v(22.05, 45) * mm});
            skLineSegment(sketch, "E1202", {"start": v(22.05, 45) * mm, "end": v(22.05, 45.08) * mm});
            skLineSegment(sketch, "E1203", {"start": v(22.05, 45.08) * mm, "end": v(22.06, 45.16) * mm});
            skLineSegment(sketch, "E1204", {"start": v(22.06, 45.16) * mm, "end": v(22.07, 45.23) * mm});
            skLineSegment(sketch, "E1205", {"start": v(22.07, 45.23) * mm, "end": v(22.07, 45.31) * mm});
            skLineSegment(sketch, "E1206", {"start": v(22.07, 45.31) * mm, "end": v(22.08, 45.4) * mm});
            skLineSegment(sketch, "E1207", {"start": v(22.08, 45.4) * mm, "end": v(22.09, 45.47) * mm});
            skLineSegment(sketch, "E1208", {"start": v(22.09, 45.47) * mm, "end": v(22.1, 45.55) * mm});
            skLineSegment(sketch, "E1209", {"start": v(22.1, 45.55) * mm, "end": v(22.1, 45.64) * mm});
            skLineSegment(sketch, "E1210", {"start": v(22.1, 45.64) * mm, "end": v(22.1, 45.72) * mm});
            skLineSegment(sketch, "E1211", {"start": v(22.1, 45.72) * mm, "end": v(22.1, 45.8) * mm});
            skLineSegment(sketch, "E1212", {"start": v(22.1, 45.8) * mm, "end": v(22.11, 45.9) * mm});
            skLineSegment(sketch, "E1213", {"start": v(22.11, 45.9) * mm, "end": v(22.12, 45.98) * mm});
            skLineSegment(sketch, "E1214", {"start": v(22.12, 45.98) * mm, "end": v(22.12, 46.06) * mm});
            skLineSegment(sketch, "E1215", {"start": v(22.12, 46.06) * mm, "end": v(22.12, 46.15) * mm});
            skLineSegment(sketch, "E1216", {"start": v(22.12, 46.15) * mm, "end": v(22.12, 46.23) * mm});
            skLineSegment(sketch, "E1217", {"start": v(22.12, 46.23) * mm, "end": v(21.25, 46.64) * mm});
            skLineSegment(sketch, "E1218", {"start": v(21.25, 46.64) * mm, "end": v(21.19, 46.59) * mm});
            skLineSegment(sketch, "E1219", {"start": v(21.19, 46.59) * mm, "end": v(21.12, 46.53) * mm});
            skLineSegment(sketch, "E1220", {"start": v(21.12, 46.53) * mm, "end": v(21.06, 46.47) * mm});
            skLineSegment(sketch, "E1221", {"start": v(21.06, 46.47) * mm, "end": v(21, 46.41) * mm});
            skLineSegment(sketch, "E1222", {"start": v(21, 46.41) * mm, "end": v(20.93, 46.35) * mm});
            skLineSegment(sketch, "E1223", {"start": v(20.93, 46.35) * mm, "end": v(20.87, 46.3) * mm});
            skLineSegment(sketch, "E1224", {"start": v(20.87, 46.3) * mm, "end": v(20.8, 46.24) * mm});
            skLineSegment(sketch, "E1225", {"start": v(20.8, 46.24) * mm, "end": v(20.75, 46.18) * mm});
            skLineSegment(sketch, "E1226", {"start": v(20.75, 46.18) * mm, "end": v(20.7, 46.12) * mm});
            skLineSegment(sketch, "E1227", {"start": v(20.7, 46.12) * mm, "end": v(20.63, 46.07) * mm});
            skLineSegment(sketch, "E1228", {"start": v(20.63, 46.07) * mm, "end": v(20.58, 46.01) * mm});
            skLineSegment(sketch, "E1229", {"start": v(20.58, 46.01) * mm, "end": v(20.52, 45.96) * mm});
            skLineSegment(sketch, "E1230", {"start": v(20.52, 45.96) * mm, "end": v(20.46, 45.9) * mm});
            skLineSegment(sketch, "E1231", {"start": v(20.46, 45.9) * mm, "end": v(20.4, 45.85) * mm});
            skLineSegment(sketch, "E1232", {"start": v(20.4, 45.85) * mm, "end": v(20.36, 45.8) * mm});
            skLineSegment(sketch, "E1233", {"start": v(20.36, 45.8) * mm, "end": v(20.3, 45.74) * mm});
            skLineSegment(sketch, "E1234", {"start": v(20.3, 45.74) * mm, "end": v(20.25, 45.68) * mm});
            skLineSegment(sketch, "E1235", {"start": v(20.25, 45.68) * mm, "end": v(20.2, 45.63) * mm});
            skLineSegment(sketch, "E1236", {"start": v(20.2, 45.63) * mm, "end": v(20.15, 45.58) * mm});
            skLineSegment(sketch, "E1237", {"start": v(20.15, 45.58) * mm, "end": v(20.1, 45.52) * mm});
            skLineSegment(sketch, "E1238", {"start": v(20.1, 45.52) * mm, "end": v(20.05, 45.47) * mm});
            skLineSegment(sketch, "E1239", {"start": v(20.05, 45.47) * mm, "end": v(20, 45.42) * mm});
            skLineSegment(sketch, "E1240", {"start": v(20, 45.42) * mm, "end": v(19.96, 45.37) * mm});
            skLineSegment(sketch, "E1241", {"start": v(19.96, 45.37) * mm, "end": v(19.91, 45.32) * mm});
            skLineSegment(sketch, "E1242", {"start": v(19.91, 45.32) * mm, "end": v(19.87, 45.27) * mm});
            skLineSegment(sketch, "E1243", {"start": v(19.87, 45.27) * mm, "end": v(19.82, 45.22) * mm});
            skLineSegment(sketch, "E1244", {"start": v(19.82, 45.22) * mm, "end": v(19.78, 45.17) * mm});
            skLineSegment(sketch, "E1245", {"start": v(19.78, 45.17) * mm, "end": v(19.74, 45.12) * mm});
            skLineSegment(sketch, "E1246", {"start": v(19.74, 45.12) * mm, "end": v(19.7, 45.07) * mm});
            skLineSegment(sketch, "E1247", {"start": v(19.7, 45.07) * mm, "end": v(19.65, 45.02) * mm});
            skLineSegment(sketch, "E1248", {"start": v(19.65, 45.02) * mm, "end": v(19.61, 44.98) * mm});
            skLineSegment(sketch, "E1249", {"start": v(19.61, 44.98) * mm, "end": v(19.57, 44.93) * mm});
            skLineSegment(sketch, "E1250", {"start": v(19.57, 44.93) * mm, "end": v(19.54, 44.88) * mm});
            skLineSegment(sketch, "E1251", {"start": v(19.54, 44.88) * mm, "end": v(19.5, 44.84) * mm});
            skLineSegment(sketch, "E1252", {"start": v(19.5, 44.84) * mm, "end": v(19.46, 44.8) * mm});
            skLineSegment(sketch, "E1253", {"start": v(19.46, 44.8) * mm, "end": v(19.42, 44.75) * mm});
            skLineSegment(sketch, "E1254", {"start": v(19.42, 44.75) * mm, "end": v(19.39, 44.7) * mm});
            skLineSegment(sketch, "E1255", {"start": v(19.39, 44.7) * mm, "end": v(19.35, 44.66) * mm});
            skLineSegment(sketch, "E1256", {"start": v(19.35, 44.66) * mm, "end": v(19.32, 44.62) * mm});
            skLineSegment(sketch, "E1257", {"start": v(19.32, 44.62) * mm, "end": v(19.29, 44.58) * mm});
            skLineSegment(sketch, "E1258", {"start": v(19.29, 44.58) * mm, "end": v(19.03, 44.68) * mm});
            skLineSegment(sketch, "E1259", {"start": v(19.03, 44.68) * mm, "end": v(18.58, 44.87) * mm});
            skLineSegment(sketch, "E1260", {"start": v(18.58, 44.87) * mm, "end": v(18.33, 44.98) * mm});
            skLineSegment(sketch, "E1261", {"start": v(18.33, 44.98) * mm, "end": v(18.34, 45.03) * mm});
            skLineSegment(sketch, "E1262", {"start": v(18.34, 45.03) * mm, "end": v(18.34, 45.09) * mm});
            skLineSegment(sketch, "E1263", {"start": v(18.34, 45.09) * mm, "end": v(18.35, 45.14) * mm});
            skLineSegment(sketch, "E1264", {"start": v(18.35, 45.14) * mm, "end": v(18.36, 45.2) * mm});
            skLineSegment(sketch, "E1265", {"start": v(18.36, 45.2) * mm, "end": v(18.36, 45.25) * mm});
            skLineSegment(sketch, "E1266", {"start": v(18.36, 45.25) * mm, "end": v(18.37, 45.31) * mm});
            skLineSegment(sketch, "E1267", {"start": v(18.37, 45.31) * mm, "end": v(18.37, 45.37) * mm});
            skLineSegment(sketch, "E1268", {"start": v(18.37, 45.37) * mm, "end": v(18.38, 45.43) * mm});
            skLineSegment(sketch, "E1269", {"start": v(18.38, 45.43) * mm, "end": v(18.39, 45.5) * mm});
            skLineSegment(sketch, "E1270", {"start": v(18.39, 45.5) * mm, "end": v(18.4, 45.56) * mm});
            skLineSegment(sketch, "E1271", {"start": v(18.4, 45.56) * mm, "end": v(18.4, 45.62) * mm});
            skLineSegment(sketch, "E1272", {"start": v(18.4, 45.62) * mm, "end": v(18.4, 45.68) * mm});
            skLineSegment(sketch, "E1273", {"start": v(18.4, 45.68) * mm, "end": v(18.4, 45.75) * mm});
            skLineSegment(sketch, "E1274", {"start": v(18.4, 45.75) * mm, "end": v(18.41, 45.81) * mm});
            skLineSegment(sketch, "E1275", {"start": v(18.41, 45.81) * mm, "end": v(18.42, 45.88) * mm});
            skLineSegment(sketch, "E1276", {"start": v(18.42, 45.88) * mm, "end": v(18.42, 45.95) * mm});
            skLineSegment(sketch, "E1277", {"start": v(18.42, 45.95) * mm, "end": v(18.42, 46.01) * mm});
            skLineSegment(sketch, "E1278", {"start": v(18.42, 46.01) * mm, "end": v(18.43, 46.08) * mm});
            skLineSegment(sketch, "E1279", {"start": v(18.43, 46.08) * mm, "end": v(18.43, 46.15) * mm});
            skLineSegment(sketch, "E1280", {"start": v(18.43, 46.15) * mm, "end": v(18.43, 46.22) * mm});
            skLineSegment(sketch, "E1281", {"start": v(18.43, 46.22) * mm, "end": v(18.44, 46.3) * mm});
            skLineSegment(sketch, "E1282", {"start": v(18.44, 46.3) * mm, "end": v(18.44, 46.37) * mm});
            skLineSegment(sketch, "E1283", {"start": v(18.44, 46.37) * mm, "end": v(18.44, 46.44) * mm});
            skLineSegment(sketch, "E1284", {"start": v(18.44, 46.44) * mm, "end": v(18.44, 46.52) * mm});
            skLineSegment(sketch, "E1285", {"start": v(18.44, 46.52) * mm, "end": v(18.45, 46.6) * mm});
            skLineSegment(sketch, "E1286", {"start": v(18.45, 46.6) * mm, "end": v(18.45, 46.67) * mm});
            skLineSegment(sketch, "E1287", {"start": v(18.45, 46.67) * mm, "end": v(18.45, 46.75) * mm});
            skLineSegment(sketch, "E1288", {"start": v(18.45, 46.75) * mm, "end": v(18.45, 46.83) * mm});
            skLineSegment(sketch, "E1289", {"start": v(18.45, 46.83) * mm, "end": v(18.45, 46.9) * mm});
            skLineSegment(sketch, "E1290", {"start": v(18.45, 46.9) * mm, "end": v(18.45, 46.98) * mm});
            skLineSegment(sketch, "E1291", {"start": v(18.45, 46.98) * mm, "end": v(18.45, 47.07) * mm});
            skLineSegment(sketch, "E1292", {"start": v(18.45, 47.07) * mm, "end": v(18.45, 47.15) * mm});
            skLineSegment(sketch, "E1293", {"start": v(18.45, 47.15) * mm, "end": v(18.45, 47.23) * mm});
            skLineSegment(sketch, "E1294", {"start": v(18.45, 47.23) * mm, "end": v(18.45, 47.31) * mm});
            skLineSegment(sketch, "E1295", {"start": v(18.45, 47.31) * mm, "end": v(18.45, 47.4) * mm});
            skLineSegment(sketch, "E1296", {"start": v(18.45, 47.4) * mm, "end": v(18.44, 47.48) * mm});
            skLineSegment(sketch, "E1297", {"start": v(18.44, 47.48) * mm, "end": v(18.44, 47.57) * mm});
            skLineSegment(sketch, "E1298", {"start": v(18.44, 47.57) * mm, "end": v(18.44, 47.66) * mm});
            skLineSegment(sketch, "E1299", {"start": v(18.44, 47.66) * mm, "end": v(18.44, 47.75) * mm});
            skLineSegment(sketch, "E1300", {"start": v(18.44, 47.75) * mm, "end": v(18.43, 47.82) * mm});
            skLineSegment(sketch, "E1301", {"start": v(18.43, 47.82) * mm, "end": v(17.52, 48.16) * mm});
            skLineSegment(sketch, "E1302", {"start": v(17.52, 48.16) * mm, "end": v(17.47, 48.1) * mm});
            skLineSegment(sketch, "E1303", {"start": v(17.47, 48.1) * mm, "end": v(17.4, 48.04) * mm});
            skLineSegment(sketch, "E1304", {"start": v(17.4, 48.04) * mm, "end": v(17.35, 47.98) * mm});
            skLineSegment(sketch, "E1305", {"start": v(17.35, 47.98) * mm, "end": v(17.29, 47.92) * mm});
            skLineSegment(sketch, "E1306", {"start": v(17.29, 47.92) * mm, "end": v(17.23, 47.85) * mm});
            skLineSegment(sketch, "E1307", {"start": v(17.23, 47.85) * mm, "end": v(17.17, 47.8) * mm});
            skLineSegment(sketch, "E1308", {"start": v(17.17, 47.8) * mm, "end": v(17.12, 47.73) * mm});
            skLineSegment(sketch, "E1309", {"start": v(17.12, 47.73) * mm, "end": v(17.06, 47.67) * mm});
            skLineSegment(sketch, "E1310", {"start": v(17.06, 47.67) * mm, "end": v(17, 47.6) * mm});
            skLineSegment(sketch, "E1311", {"start": v(17, 47.6) * mm, "end": v(16.95, 47.55) * mm});
            skLineSegment(sketch, "E1312", {"start": v(16.95, 47.55) * mm, "end": v(16.9, 47.48) * mm});
            skLineSegment(sketch, "E1313", {"start": v(16.9, 47.48) * mm, "end": v(16.85, 47.42) * mm});
            skLineSegment(sketch, "E1314", {"start": v(16.85, 47.42) * mm, "end": v(16.8, 47.36) * mm});
            skLineSegment(sketch, "E1315", {"start": v(16.8, 47.36) * mm, "end": v(16.75, 47.3) * mm});
            skLineSegment(sketch, "E1316", {"start": v(16.75, 47.3) * mm, "end": v(16.7, 47.25) * mm});
            skLineSegment(sketch, "E1317", {"start": v(16.7, 47.25) * mm, "end": v(16.65, 47.19) * mm});
            skLineSegment(sketch, "E1318", {"start": v(16.65, 47.19) * mm, "end": v(16.6, 47.13) * mm});
            skLineSegment(sketch, "E1319", {"start": v(16.6, 47.13) * mm, "end": v(16.56, 47.07) * mm});
            skLineSegment(sketch, "E1320", {"start": v(16.56, 47.07) * mm, "end": v(16.51, 47.02) * mm});
            skLineSegment(sketch, "E1321", {"start": v(16.51, 47.02) * mm, "end": v(16.47, 46.96) * mm});
            skLineSegment(sketch, "E1322", {"start": v(16.47, 46.96) * mm, "end": v(16.42, 46.9) * mm});
            skLineSegment(sketch, "E1323", {"start": v(16.42, 46.9) * mm, "end": v(16.38, 46.85) * mm});
            skLineSegment(sketch, "E1324", {"start": v(16.38, 46.85) * mm, "end": v(16.34, 46.8) * mm});
            skLineSegment(sketch, "E1325", {"start": v(16.34, 46.8) * mm, "end": v(16.3, 46.74) * mm});
            skLineSegment(sketch, "E1326", {"start": v(16.3, 46.74) * mm, "end": v(16.25, 46.69) * mm});
            skLineSegment(sketch, "E1327", {"start": v(16.25, 46.69) * mm, "end": v(16.21, 46.63) * mm});
            skLineSegment(sketch, "E1328", {"start": v(16.21, 46.63) * mm, "end": v(16.17, 46.58) * mm});
            skLineSegment(sketch, "E1329", {"start": v(16.17, 46.58) * mm, "end": v(16.14, 46.53) * mm});
            skLineSegment(sketch, "E1330", {"start": v(16.14, 46.53) * mm, "end": v(16.1, 46.48) * mm});
            skLineSegment(sketch, "E1331", {"start": v(16.1, 46.48) * mm, "end": v(16.06, 46.43) * mm});
            skLineSegment(sketch, "E1332", {"start": v(16.06, 46.43) * mm, "end": v(16.02, 46.38) * mm});
            skLineSegment(sketch, "E1333", {"start": v(16.02, 46.38) * mm, "end": v(15.99, 46.33) * mm});
            skLineSegment(sketch, "E1334", {"start": v(15.99, 46.33) * mm, "end": v(15.95, 46.28) * mm});
            skLineSegment(sketch, "E1335", {"start": v(15.95, 46.28) * mm, "end": v(15.92, 46.23) * mm});
            skLineSegment(sketch, "E1336", {"start": v(15.92, 46.23) * mm, "end": v(15.89, 46.18) * mm});
            skLineSegment(sketch, "E1337", {"start": v(15.89, 46.18) * mm, "end": v(15.85, 46.13) * mm});
            skLineSegment(sketch, "E1338", {"start": v(15.85, 46.13) * mm, "end": v(15.82, 46.09) * mm});
            skLineSegment(sketch, "E1339", {"start": v(15.82, 46.09) * mm, "end": v(15.79, 46.04) * mm});
            skLineSegment(sketch, "E1340", {"start": v(15.79, 46.04) * mm, "end": v(15.76, 46) * mm});
            skLineSegment(sketch, "E1341", {"start": v(15.76, 46) * mm, "end": v(15.73, 45.95) * mm});
            skLineSegment(sketch, "E1342", {"start": v(15.73, 45.95) * mm, "end": v(15.46, 46.04) * mm});
            skLineSegment(sketch, "E1343", {"start": v(15.46, 46.04) * mm, "end": v(15, 46.19) * mm});
            skLineSegment(sketch, "E1344", {"start": v(15, 46.19) * mm, "end": v(14.74, 46.28) * mm});
            skLineSegment(sketch, "E1345", {"start": v(14.74, 46.28) * mm, "end": v(14.75, 46.33) * mm});
            skLineSegment(sketch, "E1346", {"start": v(14.75, 46.33) * mm, "end": v(14.75, 46.39) * mm});
            skLineSegment(sketch, "E1347", {"start": v(14.75, 46.39) * mm, "end": v(14.75, 46.44) * mm});
            skLineSegment(sketch, "E1348", {"start": v(14.75, 46.44) * mm, "end": v(14.75, 46.5) * mm});
            skLineSegment(sketch, "E1349", {"start": v(14.75, 46.5) * mm, "end": v(14.75, 46.56) * mm});
            skLineSegment(sketch, "E1350", {"start": v(14.75, 46.56) * mm, "end": v(14.76, 46.61) * mm});
            skLineSegment(sketch, "E1351", {"start": v(14.76, 46.61) * mm, "end": v(14.76, 46.67) * mm});
            skLineSegment(sketch, "E1352", {"start": v(14.76, 46.67) * mm, "end": v(14.76, 46.73) * mm});
            skLineSegment(sketch, "E1353", {"start": v(14.76, 46.73) * mm, "end": v(14.76, 46.8) * mm});
            skLineSegment(sketch, "E1354", {"start": v(14.76, 46.8) * mm, "end": v(14.76, 46.86) * mm});
            skLineSegment(sketch, "E1355", {"start": v(14.76, 46.86) * mm, "end": v(14.76, 46.92) * mm});
            skLineSegment(sketch, "E1356", {"start": v(14.76, 46.92) * mm, "end": v(14.76, 46.98) * mm});
            skLineSegment(sketch, "E1357", {"start": v(14.76, 46.98) * mm, "end": v(14.76, 47.05) * mm});
            skLineSegment(sketch, "E1358", {"start": v(14.76, 47.05) * mm, "end": v(14.76, 47.12) * mm});
            skLineSegment(sketch, "E1359", {"start": v(14.76, 47.12) * mm, "end": v(14.76, 47.18) * mm});
            skLineSegment(sketch, "E1360", {"start": v(14.76, 47.18) * mm, "end": v(14.76, 47.25) * mm});
            skLineSegment(sketch, "E1361", {"start": v(14.76, 47.25) * mm, "end": v(14.76, 47.32) * mm});
            skLineSegment(sketch, "E1362", {"start": v(14.76, 47.32) * mm, "end": v(14.76, 47.39) * mm});
            skLineSegment(sketch, "E1363", {"start": v(14.76, 47.39) * mm, "end": v(14.75, 47.46) * mm});
            skLineSegment(sketch, "E1364", {"start": v(14.75, 47.46) * mm, "end": v(14.75, 47.53) * mm});
            skLineSegment(sketch, "E1365", {"start": v(14.75, 47.53) * mm, "end": v(14.75, 47.6) * mm});
            skLineSegment(sketch, "E1366", {"start": v(14.75, 47.6) * mm, "end": v(14.75, 47.67) * mm});
            skLineSegment(sketch, "E1367", {"start": v(14.75, 47.67) * mm, "end": v(14.74, 47.75) * mm});
            skLineSegment(sketch, "E1368", {"start": v(14.74, 47.75) * mm, "end": v(14.74, 47.82) * mm});
            skLineSegment(sketch, "E1369", {"start": v(14.74, 47.82) * mm, "end": v(14.73, 47.9) * mm});
            skLineSegment(sketch, "E1370", {"start": v(14.73, 47.9) * mm, "end": v(14.73, 47.97) * mm});
            skLineSegment(sketch, "E1371", {"start": v(14.73, 47.97) * mm, "end": v(14.72, 48.05) * mm});
            skLineSegment(sketch, "E1372", {"start": v(14.72, 48.05) * mm, "end": v(14.72, 48.13) * mm});
            skLineSegment(sketch, "E1373", {"start": v(14.72, 48.13) * mm, "end": v(14.71, 48.2) * mm});
            skLineSegment(sketch, "E1374", {"start": v(14.71, 48.2) * mm, "end": v(14.7, 48.29) * mm});
            skLineSegment(sketch, "E1375", {"start": v(14.7, 48.29) * mm, "end": v(14.7, 48.37) * mm});
            skLineSegment(sketch, "E1376", {"start": v(14.7, 48.37) * mm, "end": v(14.7, 48.45) * mm});
            skLineSegment(sketch, "E1377", {"start": v(14.7, 48.45) * mm, "end": v(14.69, 48.53) * mm});
            skLineSegment(sketch, "E1378", {"start": v(14.69, 48.53) * mm, "end": v(14.68, 48.62) * mm});
            skLineSegment(sketch, "E1379", {"start": v(14.68, 48.62) * mm, "end": v(14.67, 48.7) * mm});
            skLineSegment(sketch, "E1380", {"start": v(14.67, 48.7) * mm, "end": v(14.66, 48.78) * mm});
            skLineSegment(sketch, "E1381", {"start": v(14.66, 48.78) * mm, "end": v(14.65, 48.87) * mm});
            skLineSegment(sketch, "E1382", {"start": v(14.65, 48.87) * mm, "end": v(14.64, 48.96) * mm});
            skLineSegment(sketch, "E1383", {"start": v(14.64, 48.96) * mm, "end": v(14.63, 49.04) * mm});
            skLineSegment(sketch, "E1384", {"start": v(14.63, 49.04) * mm, "end": v(14.62, 49.12) * mm});
            skLineSegment(sketch, "E1385", {"start": v(14.62, 49.12) * mm, "end": v(13.7, 49.39) * mm});
            skLineSegment(sketch, "E1386", {"start": v(13.7, 49.39) * mm, "end": v(13.64, 49.33) * mm});
            skLineSegment(sketch, "E1387", {"start": v(13.64, 49.33) * mm, "end": v(13.58, 49.26) * mm});
            skLineSegment(sketch, "E1388", {"start": v(13.58, 49.26) * mm, "end": v(13.53, 49.2) * mm});
            skLineSegment(sketch, "E1389", {"start": v(13.53, 49.2) * mm, "end": v(13.47, 49.13) * mm});
            skLineSegment(sketch, "E1390", {"start": v(13.47, 49.13) * mm, "end": v(13.42, 49.06) * mm});
            skLineSegment(sketch, "E1391", {"start": v(13.42, 49.06) * mm, "end": v(13.37, 49) * mm});
            skLineSegment(sketch, "E1392", {"start": v(13.37, 49) * mm, "end": v(13.32, 48.92) * mm});
            skLineSegment(sketch, "E1393", {"start": v(13.32, 48.92) * mm, "end": v(13.27, 48.86) * mm});
            skLineSegment(sketch, "E1394", {"start": v(13.27, 48.86) * mm, "end": v(13.22, 48.8) * mm});
            skLineSegment(sketch, "E1395", {"start": v(13.22, 48.8) * mm, "end": v(13.17, 48.73) * mm});
            skLineSegment(sketch, "E1396", {"start": v(13.17, 48.73) * mm, "end": v(13.12, 48.66) * mm});
            skLineSegment(sketch, "E1397", {"start": v(13.12, 48.66) * mm, "end": v(13.08, 48.6) * mm});
            skLineSegment(sketch, "E1398", {"start": v(13.08, 48.6) * mm, "end": v(13.03, 48.54) * mm});
            skLineSegment(sketch, "E1399", {"start": v(13.03, 48.54) * mm, "end": v(12.99, 48.47) * mm});
            skLineSegment(sketch, "E1400", {"start": v(12.99, 48.47) * mm, "end": v(12.94, 48.41) * mm});
            skLineSegment(sketch, "E1401", {"start": v(12.94, 48.41) * mm, "end": v(12.9, 48.35) * mm});
            skLineSegment(sketch, "E1402", {"start": v(12.9, 48.35) * mm, "end": v(12.86, 48.29) * mm});
            skLineSegment(sketch, "E1403", {"start": v(12.86, 48.29) * mm, "end": v(12.81, 48.23) * mm});
            skLineSegment(sketch, "E1404", {"start": v(12.81, 48.23) * mm, "end": v(12.77, 48.17) * mm});
            skLineSegment(sketch, "E1405", {"start": v(12.77, 48.17) * mm, "end": v(12.73, 48.1) * mm});
            skLineSegment(sketch, "E1406", {"start": v(12.73, 48.1) * mm, "end": v(12.7, 48.05) * mm});
            skLineSegment(sketch, "E1407", {"start": v(12.7, 48.05) * mm, "end": v(12.65, 48) * mm});
            skLineSegment(sketch, "E1408", {"start": v(12.65, 48) * mm, "end": v(12.62, 47.93) * mm});
            skLineSegment(sketch, "E1409", {"start": v(12.62, 47.93) * mm, "end": v(12.58, 47.88) * mm});
            skLineSegment(sketch, "E1410", {"start": v(12.58, 47.88) * mm, "end": v(12.54, 47.82) * mm});
            skLineSegment(sketch, "E1411", {"start": v(12.54, 47.82) * mm, "end": v(12.5, 47.76) * mm});
            skLineSegment(sketch, "E1412", {"start": v(12.5, 47.76) * mm, "end": v(12.47, 47.7) * mm});
            skLineSegment(sketch, "E1413", {"start": v(12.47, 47.7) * mm, "end": v(12.44, 47.65) * mm});
            skLineSegment(sketch, "E1414", {"start": v(12.44, 47.65) * mm, "end": v(12.4, 47.6) * mm});
            skLineSegment(sketch, "E1415", {"start": v(12.4, 47.6) * mm, "end": v(12.37, 47.54) * mm});
            skLineSegment(sketch, "E1416", {"start": v(12.37, 47.54) * mm, "end": v(12.34, 47.5) * mm});
            skLineSegment(sketch, "E1417", {"start": v(12.34, 47.5) * mm, "end": v(12.3, 47.44) * mm});
            skLineSegment(sketch, "E1418", {"start": v(12.3, 47.44) * mm, "end": v(12.27, 47.39) * mm});
            skLineSegment(sketch, "E1419", {"start": v(12.27, 47.39) * mm, "end": v(12.24, 47.34) * mm});
            skLineSegment(sketch, "E1420", {"start": v(12.24, 47.34) * mm, "end": v(12.21, 47.29) * mm});
            skLineSegment(sketch, "E1421", {"start": v(12.21, 47.29) * mm, "end": v(12.18, 47.24) * mm});
            skLineSegment(sketch, "E1422", {"start": v(12.18, 47.24) * mm, "end": v(12.16, 47.19) * mm});
            skLineSegment(sketch, "E1423", {"start": v(12.16, 47.19) * mm, "end": v(12.13, 47.14) * mm});
            skLineSegment(sketch, "E1424", {"start": v(12.13, 47.14) * mm, "end": v(12.1, 47.1) * mm});
            skLineSegment(sketch, "E1425", {"start": v(12.1, 47.1) * mm, "end": v(12.07, 47.04) * mm});
            skLineSegment(sketch, "E1426", {"start": v(12.07, 47.04) * mm, "end": v(11.8, 47.1) * mm});
            skLineSegment(sketch, "E1427", {"start": v(11.8, 47.1) * mm, "end": v(11.34, 47.22) * mm});
            skLineSegment(sketch, "E1428", {"start": v(11.34, 47.22) * mm, "end": v(11.07, 47.3) * mm});
            skLineSegment(sketch, "E1429", {"start": v(11.07, 47.3) * mm, "end": v(11.06, 47.34) * mm});
            skLineSegment(sketch, "E1430", {"start": v(11.06, 47.34) * mm, "end": v(11.06, 47.4) * mm});
            skLineSegment(sketch, "E1431", {"start": v(11.06, 47.4) * mm, "end": v(11.06, 47.46) * mm});
            skLineSegment(sketch, "E1432", {"start": v(11.06, 47.46) * mm, "end": v(11.06, 47.51) * mm});
            skLineSegment(sketch, "E1433", {"start": v(11.06, 47.51) * mm, "end": v(11.06, 47.57) * mm});
            skLineSegment(sketch, "E1434", {"start": v(11.06, 47.57) * mm, "end": v(11.05, 47.63) * mm});
            skLineSegment(sketch, "E1435", {"start": v(11.05, 47.63) * mm, "end": v(11.05, 47.69) * mm});
            skLineSegment(sketch, "E1436", {"start": v(11.05, 47.69) * mm, "end": v(11.05, 47.75) * mm});
            skLineSegment(sketch, "E1437", {"start": v(11.05, 47.75) * mm, "end": v(11.04, 47.8) * mm});
            skLineSegment(sketch, "E1438", {"start": v(11.04, 47.8) * mm, "end": v(11.04, 47.87) * mm});
            skLineSegment(sketch, "E1439", {"start": v(11.04, 47.87) * mm, "end": v(11.03, 47.93) * mm});
            skLineSegment(sketch, "E1440", {"start": v(11.03, 47.93) * mm, "end": v(11.03, 48) * mm});
            skLineSegment(sketch, "E1441", {"start": v(11.03, 48) * mm, "end": v(11.02, 48.06) * mm});
            skLineSegment(sketch, "E1442", {"start": v(11.02, 48.06) * mm, "end": v(11.02, 48.13) * mm});
            skLineSegment(sketch, "E1443", {"start": v(11.02, 48.13) * mm, "end": v(11.01, 48.2) * mm});
            skLineSegment(sketch, "E1444", {"start": v(11.01, 48.2) * mm, "end": v(11, 48.26) * mm});
            skLineSegment(sketch, "E1445", {"start": v(11, 48.26) * mm, "end": v(11, 48.33) * mm});
            skLineSegment(sketch, "E1446", {"start": v(11, 48.33) * mm, "end": v(11, 48.4) * mm});
            skLineSegment(sketch, "E1447", {"start": v(11, 48.4) * mm, "end": v(10.98, 48.47) * mm});
            skLineSegment(sketch, "E1448", {"start": v(10.98, 48.47) * mm, "end": v(10.98, 48.54) * mm});
            skLineSegment(sketch, "E1449", {"start": v(10.98, 48.54) * mm, "end": v(10.97, 48.61) * mm});
            skLineSegment(sketch, "E1450", {"start": v(10.97, 48.61) * mm, "end": v(10.96, 48.68) * mm});
            skLineSegment(sketch, "E1451", {"start": v(10.96, 48.68) * mm, "end": v(10.95, 48.76) * mm});
            skLineSegment(sketch, "E1452", {"start": v(10.95, 48.76) * mm, "end": v(10.94, 48.83) * mm});
            skLineSegment(sketch, "E1453", {"start": v(10.94, 48.83) * mm, "end": v(10.93, 48.9) * mm});
            skLineSegment(sketch, "E1454", {"start": v(10.93, 48.9) * mm, "end": v(10.92, 48.98) * mm});
            skLineSegment(sketch, "E1455", {"start": v(10.92, 48.98) * mm, "end": v(10.9, 49.06) * mm});
            skLineSegment(sketch, "E1456", {"start": v(10.9, 49.06) * mm, "end": v(10.9, 49.14) * mm});
            skLineSegment(sketch, "E1457", {"start": v(10.9, 49.14) * mm, "end": v(10.89, 49.21) * mm});
            skLineSegment(sketch, "E1458", {"start": v(10.89, 49.21) * mm, "end": v(10.87, 49.3) * mm});
            skLineSegment(sketch, "E1459", {"start": v(10.87, 49.3) * mm, "end": v(10.86, 49.37) * mm});
            skLineSegment(sketch, "E1460", {"start": v(10.86, 49.37) * mm, "end": v(10.85, 49.45) * mm});
            skLineSegment(sketch, "E1461", {"start": v(10.85, 49.45) * mm, "end": v(10.83, 49.53) * mm});
            skLineSegment(sketch, "E1462", {"start": v(10.83, 49.53) * mm, "end": v(10.82, 49.62) * mm});
            skLineSegment(sketch, "E1463", {"start": v(10.82, 49.62) * mm, "end": v(10.8, 49.7) * mm});
            skLineSegment(sketch, "E1464", {"start": v(10.8, 49.7) * mm, "end": v(10.79, 49.78) * mm});
            skLineSegment(sketch, "E1465", {"start": v(10.79, 49.78) * mm, "end": v(10.77, 49.87) * mm});
            skLineSegment(sketch, "E1466", {"start": v(10.77, 49.87) * mm, "end": v(10.76, 49.95) * mm});
            skLineSegment(sketch, "E1467", {"start": v(10.76, 49.95) * mm, "end": v(10.74, 50.04) * mm});
            skLineSegment(sketch, "E1468", {"start": v(10.74, 50.04) * mm, "end": v(10.72, 50.12) * mm});
            skLineSegment(sketch, "E1469", {"start": v(10.72, 50.12) * mm, "end": v(9.77, 50.3) * mm});
            skLineSegment(sketch, "E1470", {"start": v(9.77, 50.3) * mm, "end": v(9.72, 50.25) * mm});
            skLineSegment(sketch, "E1471", {"start": v(9.72, 50.25) * mm, "end": v(9.68, 50.18) * mm});
            skLineSegment(sketch, "E1472", {"start": v(9.68, 50.18) * mm, "end": v(9.63, 50.1) * mm});
            skLineSegment(sketch, "E1473", {"start": v(9.63, 50.1) * mm, "end": v(9.58, 50.03) * mm});
            skLineSegment(sketch, "E1474", {"start": v(9.58, 50.03) * mm, "end": v(9.53, 49.96) * mm});
            skLineSegment(sketch, "E1475", {"start": v(9.53, 49.96) * mm, "end": v(9.49, 49.89) * mm});
            skLineSegment(sketch, "E1476", {"start": v(9.49, 49.89) * mm, "end": v(9.44, 49.82) * mm});
            skLineSegment(sketch, "E1477", {"start": v(9.44, 49.82) * mm, "end": v(9.4, 49.75) * mm});
            skLineSegment(sketch, "E1478", {"start": v(9.4, 49.75) * mm, "end": v(9.35, 49.68) * mm});
            skLineSegment(sketch, "E1479", {"start": v(9.35, 49.68) * mm, "end": v(9.3, 49.61) * mm});
            skLineSegment(sketch, "E1480", {"start": v(9.3, 49.61) * mm, "end": v(9.27, 49.54) * mm});
            skLineSegment(sketch, "E1481", {"start": v(9.27, 49.54) * mm, "end": v(9.22, 49.48) * mm});
            skLineSegment(sketch, "E1482", {"start": v(9.22, 49.48) * mm, "end": v(9.18, 49.4) * mm});
            skLineSegment(sketch, "E1483", {"start": v(9.18, 49.4) * mm, "end": v(9.14, 49.34) * mm});
            skLineSegment(sketch, "E1484", {"start": v(9.14, 49.34) * mm, "end": v(9.1, 49.28) * mm});
            skLineSegment(sketch, "E1485", {"start": v(9.1, 49.28) * mm, "end": v(9.07, 49.21) * mm});
            skLineSegment(sketch, "E1486", {"start": v(9.07, 49.21) * mm, "end": v(9.03, 49.15) * mm});
            skLineSegment(sketch, "E1487", {"start": v(9.03, 49.15) * mm, "end": v(9, 49.08) * mm});
            skLineSegment(sketch, "E1488", {"start": v(9, 49.08) * mm, "end": v(8.95, 49.02) * mm});
            skLineSegment(sketch, "E1489", {"start": v(8.95, 49.02) * mm, "end": v(8.92, 48.96) * mm});
            skLineSegment(sketch, "E1490", {"start": v(8.92, 48.96) * mm, "end": v(8.88, 48.9) * mm});
            skLineSegment(sketch, "E1491", {"start": v(8.88, 48.9) * mm, "end": v(8.85, 48.84) * mm});
            skLineSegment(sketch, "E1492", {"start": v(8.85, 48.84) * mm, "end": v(8.82, 48.78) * mm});
            skLineSegment(sketch, "E1493", {"start": v(8.82, 48.78) * mm, "end": v(8.78, 48.72) * mm});
            skLineSegment(sketch, "E1494", {"start": v(8.78, 48.72) * mm, "end": v(8.75, 48.66) * mm});
            skLineSegment(sketch, "E1495", {"start": v(8.75, 48.66) * mm, "end": v(8.72, 48.6) * mm});
            skLineSegment(sketch, "E1496", {"start": v(8.72, 48.6) * mm, "end": v(8.69, 48.54) * mm});
            skLineSegment(sketch, "E1497", {"start": v(8.69, 48.54) * mm, "end": v(8.66, 48.48) * mm});
            skLineSegment(sketch, "E1498", {"start": v(8.66, 48.48) * mm, "end": v(8.63, 48.42) * mm});
            skLineSegment(sketch, "E1499", {"start": v(8.63, 48.42) * mm, "end": v(8.6, 48.37) * mm});
            skLineSegment(sketch, "E1500", {"start": v(8.6, 48.37) * mm, "end": v(8.57, 48.31) * mm});
            skLineSegment(sketch, "E1501", {"start": v(8.57, 48.31) * mm, "end": v(8.54, 48.26) * mm});
            skLineSegment(sketch, "E1502", {"start": v(8.54, 48.26) * mm, "end": v(8.52, 48.2) * mm});
            skLineSegment(sketch, "E1503", {"start": v(8.52, 48.2) * mm, "end": v(8.5, 48.15) * mm});
            skLineSegment(sketch, "E1504", {"start": v(8.5, 48.15) * mm, "end": v(8.47, 48.1) * mm});
            skLineSegment(sketch, "E1505", {"start": v(8.47, 48.1) * mm, "end": v(8.44, 48.05) * mm});
            skLineSegment(sketch, "E1506", {"start": v(8.44, 48.05) * mm, "end": v(8.42, 48) * mm});
            skLineSegment(sketch, "E1507", {"start": v(8.42, 48) * mm, "end": v(8.4, 47.94) * mm});
            skLineSegment(sketch, "E1508", {"start": v(8.4, 47.94) * mm, "end": v(8.37, 47.9) * mm});
            skLineSegment(sketch, "E1509", {"start": v(8.37, 47.9) * mm, "end": v(8.35, 47.85) * mm});
            skLineSegment(sketch, "E1510", {"start": v(8.35, 47.85) * mm, "end": v(8.07, 47.89) * mm});
            skLineSegment(sketch, "E1511", {"start": v(8.07, 47.89) * mm, "end": v(7.6, 47.96) * mm});
            skLineSegment(sketch, "E1512", {"start": v(7.6, 47.96) * mm, "end": v(7.32, 48.01) * mm});
            skLineSegment(sketch, "E1513", {"start": v(7.32, 48.01) * mm, "end": v(7.32, 48.07) * mm});
            skLineSegment(sketch, "E1514", {"start": v(7.32, 48.07) * mm, "end": v(7.31, 48.12) * mm});
            skLineSegment(sketch, "E1515", {"start": v(7.31, 48.12) * mm, "end": v(7.3, 48.18) * mm});
            skLineSegment(sketch, "E1516", {"start": v(7.3, 48.18) * mm, "end": v(7.3, 48.23) * mm});
            skLineSegment(sketch, "E1517", {"start": v(7.3, 48.23) * mm, "end": v(7.29, 48.3) * mm});
            skLineSegment(sketch, "E1518", {"start": v(7.29, 48.3) * mm, "end": v(7.28, 48.35) * mm});
            skLineSegment(sketch, "E1519", {"start": v(7.28, 48.35) * mm, "end": v(7.27, 48.4) * mm});
            skLineSegment(sketch, "E1520", {"start": v(7.27, 48.4) * mm, "end": v(7.27, 48.47) * mm});
            skLineSegment(sketch, "E1521", {"start": v(7.27, 48.47) * mm, "end": v(7.26, 48.53) * mm});
            skLineSegment(sketch, "E1522", {"start": v(7.26, 48.53) * mm, "end": v(7.25, 48.59) * mm});
            skLineSegment(sketch, "E1523", {"start": v(7.25, 48.59) * mm, "end": v(7.24, 48.65) * mm});
            skLineSegment(sketch, "E1524", {"start": v(7.24, 48.65) * mm, "end": v(7.23, 48.72) * mm});
            skLineSegment(sketch, "E1525", {"start": v(7.23, 48.72) * mm, "end": v(7.22, 48.78) * mm});
            skLineSegment(sketch, "E1526", {"start": v(7.22, 48.78) * mm, "end": v(7.2, 48.84) * mm});
            skLineSegment(sketch, "E1527", {"start": v(7.2, 48.84) * mm, "end": v(7.2, 48.9) * mm});
            skLineSegment(sketch, "E1528", {"start": v(7.2, 48.9) * mm, "end": v(7.19, 48.98) * mm});
            skLineSegment(sketch, "E1529", {"start": v(7.19, 48.98) * mm, "end": v(7.17, 49.04) * mm});
            skLineSegment(sketch, "E1530", {"start": v(7.17, 49.04) * mm, "end": v(7.16, 49.11) * mm});
            skLineSegment(sketch, "E1531", {"start": v(7.16, 49.11) * mm, "end": v(7.15, 49.18) * mm});
            skLineSegment(sketch, "E1532", {"start": v(7.15, 49.18) * mm, "end": v(7.13, 49.25) * mm});
            skLineSegment(sketch, "E1533", {"start": v(7.13, 49.25) * mm, "end": v(7.12, 49.32) * mm});
            skLineSegment(sketch, "E1534", {"start": v(7.12, 49.32) * mm, "end": v(7.1, 49.4) * mm});
            skLineSegment(sketch, "E1535", {"start": v(7.1, 49.4) * mm, "end": v(7.1, 49.47) * mm});
            skLineSegment(sketch, "E1536", {"start": v(7.1, 49.47) * mm, "end": v(7.08, 49.54) * mm});
            skLineSegment(sketch, "E1537", {"start": v(7.08, 49.54) * mm, "end": v(7.06, 49.61) * mm});
            skLineSegment(sketch, "E1538", {"start": v(7.06, 49.61) * mm, "end": v(7.04, 49.69) * mm});
            skLineSegment(sketch, "E1539", {"start": v(7.04, 49.69) * mm, "end": v(7.03, 49.76) * mm});
            skLineSegment(sketch, "E1540", {"start": v(7.03, 49.76) * mm, "end": v(7, 49.84) * mm});
            skLineSegment(sketch, "E1541", {"start": v(7, 49.84) * mm, "end": v(7, 49.92) * mm});
            skLineSegment(sketch, "E1542", {"start": v(7, 49.92) * mm, "end": v(6.97, 50) * mm});
            skLineSegment(sketch, "E1543", {"start": v(6.97, 50) * mm, "end": v(6.95, 50.07) * mm});
            skLineSegment(sketch, "E1544", {"start": v(6.95, 50.07) * mm, "end": v(6.93, 50.15) * mm});
            skLineSegment(sketch, "E1545", {"start": v(6.93, 50.15) * mm, "end": v(6.91, 50.23) * mm});
            skLineSegment(sketch, "E1546", {"start": v(6.91, 50.23) * mm, "end": v(6.9, 50.31) * mm});
            skLineSegment(sketch, "E1547", {"start": v(6.9, 50.31) * mm, "end": v(6.87, 50.4) * mm});
            skLineSegment(sketch, "E1548", {"start": v(6.87, 50.4) * mm, "end": v(6.85, 50.48) * mm});
            skLineSegment(sketch, "E1549", {"start": v(6.85, 50.48) * mm, "end": v(6.83, 50.56) * mm});
            skLineSegment(sketch, "E1550", {"start": v(6.83, 50.56) * mm, "end": v(6.8, 50.64) * mm});
            skLineSegment(sketch, "E1551", {"start": v(6.8, 50.64) * mm, "end": v(6.78, 50.73) * mm});
            skLineSegment(sketch, "E1552", {"start": v(6.78, 50.73) * mm, "end": v(6.75, 50.8) * mm});
            skLineSegment(sketch, "E1553", {"start": v(6.75, 50.8) * mm, "end": v(5.8, 50.92) * mm});
            skLineSegment(sketch, "E1554", {"start": v(5.8, 50.92) * mm, "end": v(5.75, 50.86) * mm});
            skLineSegment(sketch, "E1555", {"start": v(5.75, 50.86) * mm, "end": v(5.7, 50.78) * mm});
            skLineSegment(sketch, "E1556", {"start": v(5.7, 50.78) * mm, "end": v(5.67, 50.7) * mm});
            skLineSegment(sketch, "E1557", {"start": v(5.67, 50.7) * mm, "end": v(5.62, 50.63) * mm});
            skLineSegment(sketch, "E1558", {"start": v(5.62, 50.63) * mm, "end": v(5.58, 50.55) * mm});
            skLineSegment(sketch, "E1559", {"start": v(5.58, 50.55) * mm, "end": v(5.54, 50.48) * mm});
            skLineSegment(sketch, "E1560", {"start": v(5.54, 50.48) * mm, "end": v(5.5, 50.4) * mm});
            skLineSegment(sketch, "E1561", {"start": v(5.5, 50.4) * mm, "end": v(5.46, 50.33) * mm});
            skLineSegment(sketch, "E1562", {"start": v(5.46, 50.33) * mm, "end": v(5.42, 50.26) * mm});
            skLineSegment(sketch, "E1563", {"start": v(5.42, 50.26) * mm, "end": v(5.39, 50.19) * mm});
            skLineSegment(sketch, "E1564", {"start": v(5.39, 50.19) * mm, "end": v(5.35, 50.12) * mm});
            skLineSegment(sketch, "E1565", {"start": v(5.35, 50.12) * mm, "end": v(5.31, 50.05) * mm});
            skLineSegment(sketch, "E1566", {"start": v(5.31, 50.05) * mm, "end": v(5.28, 49.98) * mm});
            skLineSegment(sketch, "E1567", {"start": v(5.28, 49.98) * mm, "end": v(5.24, 49.9) * mm});
            skLineSegment(sketch, "E1568", {"start": v(5.24, 49.9) * mm, "end": v(5.2, 49.84) * mm});
            skLineSegment(sketch, "E1569", {"start": v(5.2, 49.84) * mm, "end": v(5.18, 49.77) * mm});
            skLineSegment(sketch, "E1570", {"start": v(5.18, 49.77) * mm, "end": v(5.14, 49.7) * mm});
            skLineSegment(sketch, "E1571", {"start": v(5.14, 49.7) * mm, "end": v(5.11, 49.64) * mm});
            skLineSegment(sketch, "E1572", {"start": v(5.11, 49.64) * mm, "end": v(5.08, 49.57) * mm});
            skLineSegment(sketch, "E1573", {"start": v(5.08, 49.57) * mm, "end": v(5.05, 49.5) * mm});
            skLineSegment(sketch, "E1574", {"start": v(5.05, 49.5) * mm, "end": v(5.02, 49.44) * mm});
            skLineSegment(sketch, "E1575", {"start": v(5.02, 49.44) * mm, "end": v(5, 49.38) * mm});
            skLineSegment(sketch, "E1576", {"start": v(5, 49.38) * mm, "end": v(4.96, 49.32) * mm});
            skLineSegment(sketch, "E1577", {"start": v(4.96, 49.32) * mm, "end": v(4.93, 49.25) * mm});
            skLineSegment(sketch, "E1578", {"start": v(4.93, 49.25) * mm, "end": v(4.9, 49.2) * mm});
            skLineSegment(sketch, "E1579", {"start": v(4.9, 49.2) * mm, "end": v(4.88, 49.13) * mm});
            skLineSegment(sketch, "E1580", {"start": v(4.88, 49.13) * mm, "end": v(4.85, 49.07) * mm});
            skLineSegment(sketch, "E1581", {"start": v(4.85, 49.07) * mm, "end": v(4.83, 49.01) * mm});
            skLineSegment(sketch, "E1582", {"start": v(4.83, 49.01) * mm, "end": v(4.8, 48.95) * mm});
            skLineSegment(sketch, "E1583", {"start": v(4.8, 48.95) * mm, "end": v(4.78, 48.9) * mm});
            skLineSegment(sketch, "E1584", {"start": v(4.78, 48.9) * mm, "end": v(4.75, 48.84) * mm});
            skLineSegment(sketch, "E1585", {"start": v(4.75, 48.84) * mm, "end": v(4.73, 48.78) * mm});
            skLineSegment(sketch, "E1586", {"start": v(4.73, 48.78) * mm, "end": v(4.7, 48.72) * mm});
            skLineSegment(sketch, "E1587", {"start": v(4.7, 48.72) * mm, "end": v(4.69, 48.67) * mm});
            skLineSegment(sketch, "E1588", {"start": v(4.69, 48.67) * mm, "end": v(4.67, 48.61) * mm});
            skLineSegment(sketch, "E1589", {"start": v(4.67, 48.61) * mm, "end": v(4.64, 48.56) * mm});
            skLineSegment(sketch, "E1590", {"start": v(4.64, 48.56) * mm, "end": v(4.62, 48.5) * mm});
            skLineSegment(sketch, "E1591", {"start": v(4.62, 48.5) * mm, "end": v(4.6, 48.46) * mm});
            skLineSegment(sketch, "E1592", {"start": v(4.6, 48.46) * mm, "end": v(4.59, 48.4) * mm});
            skLineSegment(sketch, "E1593", {"start": v(4.59, 48.4) * mm, "end": v(4.57, 48.35) * mm});
            skLineSegment(sketch, "E1594", {"start": v(4.57, 48.35) * mm, "end": v(4.29, 48.37) * mm});
            skLineSegment(sketch, "E1595", {"start": v(4.29, 48.37) * mm, "end": v(3.81, 48.41) * mm});
            skLineSegment(sketch, "E1596", {"start": v(3.81, 48.41) * mm, "end": v(3.53, 48.44) * mm});
            skLineSegment(sketch, "E1597", {"start": v(3.53, 48.44) * mm, "end": v(3.52, 48.5) * mm});
            skLineSegment(sketch, "E1598", {"start": v(3.52, 48.5) * mm, "end": v(3.51, 48.55) * mm});
            skLineSegment(sketch, "E1599", {"start": v(3.51, 48.55) * mm, "end": v(3.5, 48.6) * mm});
            skLineSegment(sketch, "E1600", {"start": v(3.5, 48.6) * mm, "end": v(3.49, 48.66) * mm});
            skLineSegment(sketch, "E1601", {"start": v(3.49, 48.66) * mm, "end": v(3.48, 48.71) * mm});
            skLineSegment(sketch, "E1602", {"start": v(3.48, 48.71) * mm, "end": v(3.47, 48.77) * mm});
            skLineSegment(sketch, "E1603", {"start": v(3.47, 48.77) * mm, "end": v(3.45, 48.83) * mm});
            skLineSegment(sketch, "E1604", {"start": v(3.45, 48.83) * mm, "end": v(3.44, 48.89) * mm});
            skLineSegment(sketch, "E1605", {"start": v(3.44, 48.89) * mm, "end": v(3.43, 48.95) * mm});
            skLineSegment(sketch, "E1606", {"start": v(3.43, 48.95) * mm, "end": v(3.41, 49) * mm});
            skLineSegment(sketch, "E1607", {"start": v(3.41, 49) * mm, "end": v(3.4, 49.07) * mm});
            skLineSegment(sketch, "E1608", {"start": v(3.4, 49.07) * mm, "end": v(3.38, 49.13) * mm});
            skLineSegment(sketch, "E1609", {"start": v(3.38, 49.13) * mm, "end": v(3.37, 49.2) * mm});
            skLineSegment(sketch, "E1610", {"start": v(3.37, 49.2) * mm, "end": v(3.35, 49.26) * mm});
            skLineSegment(sketch, "E1611", {"start": v(3.35, 49.26) * mm, "end": v(3.34, 49.32) * mm});
            skLineSegment(sketch, "E1612", {"start": v(3.34, 49.32) * mm, "end": v(3.32, 49.39) * mm});
            skLineSegment(sketch, "E1613", {"start": v(3.32, 49.39) * mm, "end": v(3.3, 49.46) * mm});
            skLineSegment(sketch, "E1614", {"start": v(3.3, 49.46) * mm, "end": v(3.29, 49.52) * mm});
            skLineSegment(sketch, "E1615", {"start": v(3.29, 49.52) * mm, "end": v(3.27, 49.6) * mm});
            skLineSegment(sketch, "E1616", {"start": v(3.27, 49.6) * mm, "end": v(3.25, 49.66) * mm});
            skLineSegment(sketch, "E1617", {"start": v(3.25, 49.66) * mm, "end": v(3.23, 49.73) * mm});
            skLineSegment(sketch, "E1618", {"start": v(3.23, 49.73) * mm, "end": v(3.2, 49.8) * mm});
            skLineSegment(sketch, "E1619", {"start": v(3.2, 49.8) * mm, "end": v(3.19, 49.87) * mm});
            skLineSegment(sketch, "E1620", {"start": v(3.19, 49.87) * mm, "end": v(3.17, 49.94) * mm});
            skLineSegment(sketch, "E1621", {"start": v(3.17, 49.94) * mm, "end": v(3.15, 50.01) * mm});
            skLineSegment(sketch, "E1622", {"start": v(3.15, 50.01) * mm, "end": v(3.12, 50.09) * mm});
            skLineSegment(sketch, "E1623", {"start": v(3.12, 50.09) * mm, "end": v(3.1, 50.16) * mm});
            skLineSegment(sketch, "E1624", {"start": v(3.1, 50.16) * mm, "end": v(3.08, 50.24) * mm});
            skLineSegment(sketch, "E1625", {"start": v(3.08, 50.24) * mm, "end": v(3.05, 50.31) * mm});
            skLineSegment(sketch, "E1626", {"start": v(3.05, 50.31) * mm, "end": v(3.03, 50.39) * mm});
            skLineSegment(sketch, "E1627", {"start": v(3.03, 50.39) * mm, "end": v(3, 50.46) * mm});
            skLineSegment(sketch, "E1628", {"start": v(3, 50.46) * mm, "end": v(2.98, 50.54) * mm});
            skLineSegment(sketch, "E1629", {"start": v(2.98, 50.54) * mm, "end": v(2.95, 50.62) * mm});
            skLineSegment(sketch, "E1630", {"start": v(2.95, 50.62) * mm, "end": v(2.92, 50.7) * mm});
            skLineSegment(sketch, "E1631", {"start": v(2.92, 50.7) * mm, "end": v(2.9, 50.78) * mm});
            skLineSegment(sketch, "E1632", {"start": v(2.9, 50.78) * mm, "end": v(2.87, 50.86) * mm});
            skLineSegment(sketch, "E1633", {"start": v(2.87, 50.86) * mm, "end": v(2.84, 50.94) * mm});
            skLineSegment(sketch, "E1634", {"start": v(2.84, 50.94) * mm, "end": v(2.8, 51.02) * mm});
            skLineSegment(sketch, "E1635", {"start": v(2.8, 51.02) * mm, "end": v(2.78, 51.1) * mm});
            skLineSegment(sketch, "E1636", {"start": v(2.78, 51.1) * mm, "end": v(2.75, 51.18) * mm});
            skLineSegment(sketch, "E1637", {"start": v(2.75, 51.18) * mm, "end": v(1.78, 51.22) * mm});
            skLineSegment(sketch, "E1638", {"start": v(1.78, 51.22) * mm, "end": v(1.74, 51.15) * mm});
            skLineSegment(sketch, "E1639", {"start": v(1.74, 51.15) * mm, "end": v(1.7, 51.07) * mm});
            skLineSegment(sketch, "E1640", {"start": v(1.7, 51.07) * mm, "end": v(1.67, 51) * mm});
            skLineSegment(sketch, "E1641", {"start": v(1.67, 51) * mm, "end": v(1.63, 50.91) * mm});
            skLineSegment(sketch, "E1642", {"start": v(1.63, 50.91) * mm, "end": v(1.6, 50.84) * mm});
            skLineSegment(sketch, "E1643", {"start": v(1.6, 50.84) * mm, "end": v(1.56, 50.76) * mm});
            skLineSegment(sketch, "E1644", {"start": v(1.56, 50.76) * mm, "end": v(1.53, 50.68) * mm});
            skLineSegment(sketch, "E1645", {"start": v(1.53, 50.68) * mm, "end": v(1.5, 50.6) * mm});
            skLineSegment(sketch, "E1646", {"start": v(1.5, 50.6) * mm, "end": v(1.46, 50.53) * mm});
            skLineSegment(sketch, "E1647", {"start": v(1.46, 50.53) * mm, "end": v(1.43, 50.46) * mm});
            skLineSegment(sketch, "E1648", {"start": v(1.43, 50.46) * mm, "end": v(1.4, 50.38) * mm});
            skLineSegment(sketch, "E1649", {"start": v(1.4, 50.38) * mm, "end": v(1.37, 50.31) * mm});
            skLineSegment(sketch, "E1650", {"start": v(1.37, 50.31) * mm, "end": v(1.34, 50.24) * mm});
            skLineSegment(sketch, "E1651", {"start": v(1.34, 50.24) * mm, "end": v(1.31, 50.17) * mm});
            skLineSegment(sketch, "E1652", {"start": v(1.31, 50.17) * mm, "end": v(1.28, 50.1) * mm});
            skLineSegment(sketch, "E1653", {"start": v(1.28, 50.1) * mm, "end": v(1.26, 50.03) * mm});
            skLineSegment(sketch, "E1654", {"start": v(1.26, 50.03) * mm, "end": v(1.23, 49.96) * mm});
            skLineSegment(sketch, "E1655", {"start": v(1.23, 49.96) * mm, "end": v(1.2, 49.89) * mm});
            skLineSegment(sketch, "E1656", {"start": v(1.2, 49.89) * mm, "end": v(1.18, 49.82) * mm});
            skLineSegment(sketch, "E1657", {"start": v(1.18, 49.82) * mm, "end": v(1.15, 49.75) * mm});
            skLineSegment(sketch, "E1658", {"start": v(1.15, 49.75) * mm, "end": v(1.12, 49.68) * mm});
            skLineSegment(sketch, "E1659", {"start": v(1.12, 49.68) * mm, "end": v(1.1, 49.62) * mm});
            skLineSegment(sketch, "E1660", {"start": v(1.1, 49.62) * mm, "end": v(1.08, 49.55) * mm});
            skLineSegment(sketch, "E1661", {"start": v(1.08, 49.55) * mm, "end": v(1.05, 49.49) * mm});
            skLineSegment(sketch, "E1662", {"start": v(1.05, 49.49) * mm, "end": v(1.03, 49.43) * mm});
            skLineSegment(sketch, "E1663", {"start": v(1.03, 49.43) * mm, "end": v(1, 49.36) * mm});
            skLineSegment(sketch, "E1664", {"start": v(1, 49.36) * mm, "end": v(0.99, 49.3) * mm});
            skLineSegment(sketch, "E1665", {"start": v(0.99, 49.3) * mm, "end": v(0.97, 49.24) * mm});
            skLineSegment(sketch, "E1666", {"start": v(0.97, 49.24) * mm, "end": v(0.95, 49.18) * mm});
            skLineSegment(sketch, "E1667", {"start": v(0.95, 49.18) * mm, "end": v(0.93, 49.12) * mm});
            skLineSegment(sketch, "E1668", {"start": v(0.93, 49.12) * mm, "end": v(0.9, 49.06) * mm});
            skLineSegment(sketch, "E1669", {"start": v(0.9, 49.06) * mm, "end": v(0.89, 49) * mm});
            skLineSegment(sketch, "E1670", {"start": v(0.89, 49) * mm, "end": v(0.87, 48.94) * mm});
            skLineSegment(sketch, "E1671", {"start": v(0.87, 48.94) * mm, "end": v(0.85, 48.89) * mm});
            skLineSegment(sketch, "E1672", {"start": v(0.85, 48.89) * mm, "end": v(0.84, 48.83) * mm});
            skLineSegment(sketch, "E1673", {"start": v(0.84, 48.83) * mm, "end": v(0.82, 48.78) * mm});
            skLineSegment(sketch, "E1674", {"start": v(0.82, 48.78) * mm, "end": v(0.8, 48.72) * mm});
            skLineSegment(sketch, "E1675", {"start": v(0.8, 48.72) * mm, "end": v(0.79, 48.67) * mm});
            skLineSegment(sketch, "E1676", {"start": v(0.79, 48.67) * mm, "end": v(0.77, 48.61) * mm});
            skLineSegment(sketch, "E1677", {"start": v(0.77, 48.61) * mm, "end": v(0.76, 48.56) * mm});
            skLineSegment(sketch, "E1678", {"start": v(0.76, 48.56) * mm, "end": v(0.48, 48.56) * mm});
            skLineSegment(sketch, "E1679", {"start": v(0.48, 48.56) * mm, "end": v(0, 48.56) * mm});
            skLineSegment(sketch, "E1680", {"start": v(0, 48.56) * mm, "end": v(-0.28, 48.57) * mm});
            skLineSegment(sketch, "E1681", {"start": v(-0.28, 48.57) * mm, "end": v(-0.3, 48.62) * mm});
            skLineSegment(sketch, "E1682", {"start": v(-0.3, 48.62) * mm, "end": v(-0.3, 48.67) * mm});
            skLineSegment(sketch, "E1683", {"start": v(-0.3, 48.67) * mm, "end": v(-0.32, 48.73) * mm});
            skLineSegment(sketch, "E1684", {"start": v(-0.32, 48.73) * mm, "end": v(-0.34, 48.78) * mm});
            skLineSegment(sketch, "E1685", {"start": v(-0.34, 48.78) * mm, "end": v(-0.35, 48.84) * mm});
            skLineSegment(sketch, "E1686", {"start": v(-0.35, 48.84) * mm, "end": v(-0.37, 48.9) * mm});
            skLineSegment(sketch, "E1687", {"start": v(-0.37, 48.9) * mm, "end": v(-0.39, 48.95) * mm});
            skLineSegment(sketch, "E1688", {"start": v(-0.39, 48.95) * mm, "end": v(-0.4, 49) * mm});
            skLineSegment(sketch, "E1689", {"start": v(-0.4, 49) * mm, "end": v(-0.42, 49.07) * mm});
            skLineSegment(sketch, "E1690", {"start": v(-0.42, 49.07) * mm, "end": v(-0.44, 49.13) * mm});
            skLineSegment(sketch, "E1691", {"start": v(-0.44, 49.13) * mm, "end": v(-0.46, 49.19) * mm});
            skLineSegment(sketch, "E1692", {"start": v(-0.46, 49.19) * mm, "end": v(-0.48, 49.25) * mm});
            skLineSegment(sketch, "E1693", {"start": v(-0.48, 49.25) * mm, "end": v(-0.5, 49.3) * mm});
            skLineSegment(sketch, "E1694", {"start": v(-0.5, 49.3) * mm, "end": v(-0.52, 49.37) * mm});
            skLineSegment(sketch, "E1695", {"start": v(-0.52, 49.37) * mm, "end": v(-0.54, 49.43) * mm});
            skLineSegment(sketch, "E1696", {"start": v(-0.54, 49.43) * mm, "end": v(-0.56, 49.5) * mm});
            skLineSegment(sketch, "E1697", {"start": v(-0.56, 49.5) * mm, "end": v(-0.59, 49.56) * mm});
            skLineSegment(sketch, "E1698", {"start": v(-0.59, 49.56) * mm, "end": v(-0.61, 49.63) * mm});
            skLineSegment(sketch, "E1699", {"start": v(-0.61, 49.63) * mm, "end": v(-0.63, 49.7) * mm});
            skLineSegment(sketch, "E1700", {"start": v(-0.63, 49.7) * mm, "end": v(-0.66, 49.76) * mm});
            skLineSegment(sketch, "E1701", {"start": v(-0.66, 49.76) * mm, "end": v(-0.68, 49.83) * mm});
            skLineSegment(sketch, "E1702", {"start": v(-0.68, 49.83) * mm, "end": v(-0.7, 49.9) * mm});
            skLineSegment(sketch, "E1703", {"start": v(-0.7, 49.9) * mm, "end": v(-0.73, 49.97) * mm});
            skLineSegment(sketch, "E1704", {"start": v(-0.73, 49.97) * mm, "end": v(-0.76, 50.04) * mm});
            skLineSegment(sketch, "E1705", {"start": v(-0.76, 50.04) * mm, "end": v(-0.79, 50.1) * mm});
            skLineSegment(sketch, "E1706", {"start": v(-0.79, 50.1) * mm, "end": v(-0.82, 50.18) * mm});
            skLineSegment(sketch, "E1707", {"start": v(-0.82, 50.18) * mm, "end": v(-0.84, 50.25) * mm});
            skLineSegment(sketch, "E1708", {"start": v(-0.84, 50.25) * mm, "end": v(-0.87, 50.32) * mm});
            skLineSegment(sketch, "E1709", {"start": v(-0.87, 50.32) * mm, "end": v(-0.9, 50.4) * mm});
            skLineSegment(sketch, "E1710", {"start": v(-0.9, 50.4) * mm, "end": v(-0.93, 50.47) * mm});
            skLineSegment(sketch, "E1711", {"start": v(-0.93, 50.47) * mm, "end": v(-0.97, 50.54) * mm});
            skLineSegment(sketch, "E1712", {"start": v(-0.97, 50.54) * mm, "end": v(-1, 50.62) * mm});
            skLineSegment(sketch, "E1713", {"start": v(-1, 50.62) * mm, "end": v(-1.03, 50.7) * mm});
            skLineSegment(sketch, "E1714", {"start": v(-1.03, 50.7) * mm, "end": v(-1.06, 50.77) * mm});
            skLineSegment(sketch, "E1715", {"start": v(-1.06, 50.77) * mm, "end": v(-1.1, 50.85) * mm});
            skLineSegment(sketch, "E1716", {"start": v(-1.1, 50.85) * mm, "end": v(-1.13, 50.93) * mm});
            skLineSegment(sketch, "E1717", {"start": v(-1.13, 50.93) * mm, "end": v(-1.17, 51) * mm});
            skLineSegment(sketch, "E1718", {"start": v(-1.17, 51) * mm, "end": v(-1.2, 51.09) * mm});
            skLineSegment(sketch, "E1719", {"start": v(-1.2, 51.09) * mm, "end": v(-1.24, 51.17) * mm});
            skLineSegment(sketch, "E1720", {"start": v(-1.24, 51.17) * mm, "end": v(-1.28, 51.23) * mm});
            skLineSegment(sketch, "E1721", {"start": v(-1.28, 51.23) * mm, "end": v(-2.24, 51.2) * mm});
            skLineSegment(sketch, "E1722", {"start": v(-2.24, 51.2) * mm, "end": v(-2.27, 51.13) * mm});
            skLineSegment(sketch, "E1723", {"start": v(-2.27, 51.13) * mm, "end": v(-2.3, 51.05) * mm});
            skLineSegment(sketch, "E1724", {"start": v(-2.3, 51.05) * mm, "end": v(-2.34, 50.97) * mm});
            skLineSegment(sketch, "E1725", {"start": v(-2.34, 50.97) * mm, "end": v(-2.37, 50.89) * mm});
            skLineSegment(sketch, "E1726", {"start": v(-2.37, 50.89) * mm, "end": v(-2.4, 50.8) * mm});
            skLineSegment(sketch, "E1727", {"start": v(-2.4, 50.8) * mm, "end": v(-2.42, 50.73) * mm});
            skLineSegment(sketch, "E1728", {"start": v(-2.42, 50.73) * mm, "end": v(-2.45, 50.65) * mm});
            skLineSegment(sketch, "E1729", {"start": v(-2.45, 50.65) * mm, "end": v(-2.48, 50.57) * mm});
            skLineSegment(sketch, "E1730", {"start": v(-2.48, 50.57) * mm, "end": v(-2.5, 50.5) * mm});
            skLineSegment(sketch, "E1731", {"start": v(-2.5, 50.5) * mm, "end": v(-2.53, 50.41) * mm});
            skLineSegment(sketch, "E1732", {"start": v(-2.53, 50.41) * mm, "end": v(-2.56, 50.34) * mm});
            skLineSegment(sketch, "E1733", {"start": v(-2.56, 50.34) * mm, "end": v(-2.58, 50.26) * mm});
            skLineSegment(sketch, "E1734", {"start": v(-2.58, 50.26) * mm, "end": v(-2.6, 50.19) * mm});
            skLineSegment(sketch, "E1735", {"start": v(-2.6, 50.19) * mm, "end": v(-2.63, 50.11) * mm});
            skLineSegment(sketch, "E1736", {"start": v(-2.63, 50.11) * mm, "end": v(-2.65, 50.04) * mm});
            skLineSegment(sketch, "E1737", {"start": v(-2.65, 50.04) * mm, "end": v(-2.67, 49.97) * mm});
            skLineSegment(sketch, "E1738", {"start": v(-2.67, 49.97) * mm, "end": v(-2.7, 49.9) * mm});
            skLineSegment(sketch, "E1739", {"start": v(-2.7, 49.9) * mm, "end": v(-2.72, 49.83) * mm});
            skLineSegment(sketch, "E1740", {"start": v(-2.72, 49.83) * mm, "end": v(-2.74, 49.76) * mm});
            skLineSegment(sketch, "E1741", {"start": v(-2.74, 49.76) * mm, "end": v(-2.76, 49.69) * mm});
            skLineSegment(sketch, "E1742", {"start": v(-2.76, 49.69) * mm, "end": v(-2.78, 49.62) * mm});
            skLineSegment(sketch, "E1743", {"start": v(-2.78, 49.62) * mm, "end": v(-2.8, 49.55) * mm});
            skLineSegment(sketch, "E1744", {"start": v(-2.8, 49.55) * mm, "end": v(-2.81, 49.49) * mm});
            skLineSegment(sketch, "E1745", {"start": v(-2.81, 49.49) * mm, "end": v(-2.83, 49.42) * mm});
            skLineSegment(sketch, "E1746", {"start": v(-2.83, 49.42) * mm, "end": v(-2.85, 49.35) * mm});
            skLineSegment(sketch, "E1747", {"start": v(-2.85, 49.35) * mm, "end": v(-2.87, 49.29) * mm});
            skLineSegment(sketch, "E1748", {"start": v(-2.87, 49.29) * mm, "end": v(-2.88, 49.23) * mm});
            skLineSegment(sketch, "E1749", {"start": v(-2.88, 49.23) * mm, "end": v(-2.9, 49.16) * mm});
            skLineSegment(sketch, "E1750", {"start": v(-2.9, 49.16) * mm, "end": v(-2.91, 49.1) * mm});
            skLineSegment(sketch, "E1751", {"start": v(-2.91, 49.1) * mm, "end": v(-2.93, 49.04) * mm});
            skLineSegment(sketch, "E1752", {"start": v(-2.93, 49.04) * mm, "end": v(-2.94, 48.98) * mm});
            skLineSegment(sketch, "E1753", {"start": v(-2.94, 48.98) * mm, "end": v(-2.96, 48.92) * mm});
            skLineSegment(sketch, "E1754", {"start": v(-2.96, 48.92) * mm, "end": v(-2.97, 48.86) * mm});
            skLineSegment(sketch, "E1755", {"start": v(-2.97, 48.86) * mm, "end": v(-2.98, 48.8) * mm});
            skLineSegment(sketch, "E1756", {"start": v(-2.98, 48.8) * mm, "end": v(-3, 48.75) * mm});
            skLineSegment(sketch, "E1757", {"start": v(-3, 48.75) * mm, "end": v(-3, 48.69) * mm});
            skLineSegment(sketch, "E1758", {"start": v(-3, 48.69) * mm, "end": v(-3.02, 48.63) * mm});
            skLineSegment(sketch, "E1759", {"start": v(-3.02, 48.63) * mm, "end": v(-3.03, 48.58) * mm});
            skLineSegment(sketch, "E1760", {"start": v(-3.03, 48.58) * mm, "end": v(-3.04, 48.53) * mm});
            skLineSegment(sketch, "E1761", {"start": v(-3.04, 48.53) * mm, "end": v(-3.05, 48.47) * mm});
            skLineSegment(sketch, "E1762", {"start": v(-3.05, 48.47) * mm, "end": v(-3.33, 48.45) * mm});
            skLineSegment(sketch, "E1763", {"start": v(-3.33, 48.45) * mm, "end": v(-3.81, 48.41) * mm});
            skLineSegment(sketch, "E1764", {"start": v(-3.81, 48.41) * mm, "end": v(-4.09, 48.4) * mm});
            skLineSegment(sketch, "E1765", {"start": v(-4.09, 48.4) * mm, "end": v(-4.1, 48.45) * mm});
            skLineSegment(sketch, "E1766", {"start": v(-4.1, 48.45) * mm, "end": v(-4.13, 48.5) * mm});
            skLineSegment(sketch, "E1767", {"start": v(-4.13, 48.5) * mm, "end": v(-4.14, 48.55) * mm});
            skLineSegment(sketch, "E1768", {"start": v(-4.14, 48.55) * mm, "end": v(-4.16, 48.6) * mm});
            skLineSegment(sketch, "E1769", {"start": v(-4.16, 48.6) * mm, "end": v(-4.19, 48.66) * mm});
            skLineSegment(sketch, "E1770", {"start": v(-4.19, 48.66) * mm, "end": v(-4.2, 48.71) * mm});
            skLineSegment(sketch, "E1771", {"start": v(-4.2, 48.71) * mm, "end": v(-4.23, 48.77) * mm});
            skLineSegment(sketch, "E1772", {"start": v(-4.23, 48.77) * mm, "end": v(-4.25, 48.82) * mm});
            skLineSegment(sketch, "E1773", {"start": v(-4.25, 48.82) * mm, "end": v(-4.27, 48.88) * mm});
            skLineSegment(sketch, "E1774", {"start": v(-4.27, 48.88) * mm, "end": v(-4.3, 48.94) * mm});
            skLineSegment(sketch, "E1775", {"start": v(-4.3, 48.94) * mm, "end": v(-4.32, 49) * mm});
            skLineSegment(sketch, "E1776", {"start": v(-4.32, 49) * mm, "end": v(-4.34, 49.06) * mm});
            skLineSegment(sketch, "E1777", {"start": v(-4.34, 49.06) * mm, "end": v(-4.37, 49.12) * mm});
            skLineSegment(sketch, "E1778", {"start": v(-4.37, 49.12) * mm, "end": v(-4.4, 49.18) * mm});
            skLineSegment(sketch, "E1779", {"start": v(-4.4, 49.18) * mm, "end": v(-4.42, 49.24) * mm});
            skLineSegment(sketch, "E1780", {"start": v(-4.42, 49.24) * mm, "end": v(-4.45, 49.3) * mm});
            skLineSegment(sketch, "E1781", {"start": v(-4.45, 49.3) * mm, "end": v(-4.47, 49.36) * mm});
            skLineSegment(sketch, "E1782", {"start": v(-4.47, 49.36) * mm, "end": v(-4.5, 49.43) * mm});
            skLineSegment(sketch, "E1783", {"start": v(-4.5, 49.43) * mm, "end": v(-4.53, 49.5) * mm});
            skLineSegment(sketch, "E1784", {"start": v(-4.53, 49.5) * mm, "end": v(-4.56, 49.56) * mm});
            skLineSegment(sketch, "E1785", {"start": v(-4.56, 49.56) * mm, "end": v(-4.6, 49.62) * mm});
            skLineSegment(sketch, "E1786", {"start": v(-4.6, 49.62) * mm, "end": v(-4.62, 49.69) * mm});
            skLineSegment(sketch, "E1787", {"start": v(-4.62, 49.69) * mm, "end": v(-4.65, 49.75) * mm});
            skLineSegment(sketch, "E1788", {"start": v(-4.65, 49.75) * mm, "end": v(-4.68, 49.82) * mm});
            skLineSegment(sketch, "E1789", {"start": v(-4.68, 49.82) * mm, "end": v(-4.72, 49.89) * mm});
            skLineSegment(sketch, "E1790", {"start": v(-4.72, 49.89) * mm, "end": v(-4.75, 49.96) * mm});
            skLineSegment(sketch, "E1791", {"start": v(-4.75, 49.96) * mm, "end": v(-4.78, 50.03) * mm});
            skLineSegment(sketch, "E1792", {"start": v(-4.78, 50.03) * mm, "end": v(-4.82, 50.1) * mm});
            skLineSegment(sketch, "E1793", {"start": v(-4.82, 50.1) * mm, "end": v(-4.85, 50.17) * mm});
            skLineSegment(sketch, "E1794", {"start": v(-4.85, 50.17) * mm, "end": v(-4.9, 50.24) * mm});
            skLineSegment(sketch, "E1795", {"start": v(-4.9, 50.24) * mm, "end": v(-4.93, 50.31) * mm});
            skLineSegment(sketch, "E1796", {"start": v(-4.93, 50.31) * mm, "end": v(-4.97, 50.38) * mm});
            skLineSegment(sketch, "E1797", {"start": v(-4.97, 50.38) * mm, "end": v(-5, 50.46) * mm});
            skLineSegment(sketch, "E1798", {"start": v(-5, 50.46) * mm, "end": v(-5.04, 50.53) * mm});
            skLineSegment(sketch, "E1799", {"start": v(-5.04, 50.53) * mm, "end": v(-5.08, 50.6) * mm});
            skLineSegment(sketch, "E1800", {"start": v(-5.08, 50.6) * mm, "end": v(-5.12, 50.68) * mm});
            skLineSegment(sketch, "E1801", {"start": v(-5.12, 50.68) * mm, "end": v(-5.16, 50.76) * mm});
            skLineSegment(sketch, "E1802", {"start": v(-5.16, 50.76) * mm, "end": v(-5.2, 50.83) * mm});
            skLineSegment(sketch, "E1803", {"start": v(-5.2, 50.83) * mm, "end": v(-5.25, 50.91) * mm});
            skLineSegment(sketch, "E1804", {"start": v(-5.25, 50.91) * mm, "end": v(-5.3, 50.98) * mm});
            skLineSegment(sketch, "E1805", {"start": v(-5.3, 50.98) * mm, "end": v(-6.25, 50.87) * mm});
            skLineSegment(sketch, "E1806", {"start": v(-6.25, 50.87) * mm, "end": v(-6.28, 50.8) * mm});
            skLineSegment(sketch, "E1807", {"start": v(-6.28, 50.8) * mm, "end": v(-6.3, 50.7) * mm});
            skLineSegment(sketch, "E1808", {"start": v(-6.3, 50.7) * mm, "end": v(-6.33, 50.63) * mm});
            skLineSegment(sketch, "E1809", {"start": v(-6.33, 50.63) * mm, "end": v(-6.35, 50.54) * mm});
            skLineSegment(sketch, "E1810", {"start": v(-6.35, 50.54) * mm, "end": v(-6.37, 50.46) * mm});
            skLineSegment(sketch, "E1811", {"start": v(-6.37, 50.46) * mm, "end": v(-6.4, 50.38) * mm});
            skLineSegment(sketch, "E1812", {"start": v(-6.4, 50.38) * mm, "end": v(-6.42, 50.3) * mm});
            skLineSegment(sketch, "E1813", {"start": v(-6.42, 50.3) * mm, "end": v(-6.44, 50.22) * mm});
            skLineSegment(sketch, "E1814", {"start": v(-6.44, 50.22) * mm, "end": v(-6.46, 50.14) * mm});
            skLineSegment(sketch, "E1815", {"start": v(-6.46, 50.14) * mm, "end": v(-6.48, 50.06) * mm});
            skLineSegment(sketch, "E1816", {"start": v(-6.48, 50.06) * mm, "end": v(-6.5, 49.98) * mm});
            skLineSegment(sketch, "E1817", {"start": v(-6.5, 49.98) * mm, "end": v(-6.52, 49.9) * mm});
            skLineSegment(sketch, "E1818", {"start": v(-6.52, 49.9) * mm, "end": v(-6.53, 49.83) * mm});
            skLineSegment(sketch, "E1819", {"start": v(-6.53, 49.83) * mm, "end": v(-6.55, 49.75) * mm});
            skLineSegment(sketch, "E1820", {"start": v(-6.55, 49.75) * mm, "end": v(-6.57, 49.68) * mm});
            skLineSegment(sketch, "E1821", {"start": v(-6.57, 49.68) * mm, "end": v(-6.59, 49.6) * mm});
            skLineSegment(sketch, "E1822", {"start": v(-6.59, 49.6) * mm, "end": v(-6.6, 49.53) * mm});
            skLineSegment(sketch, "E1823", {"start": v(-6.6, 49.53) * mm, "end": v(-6.62, 49.46) * mm});
            skLineSegment(sketch, "E1824", {"start": v(-6.62, 49.46) * mm, "end": v(-6.63, 49.39) * mm});
            skLineSegment(sketch, "E1825", {"start": v(-6.63, 49.39) * mm, "end": v(-6.65, 49.32) * mm});
            skLineSegment(sketch, "E1826", {"start": v(-6.65, 49.32) * mm, "end": v(-6.66, 49.25) * mm});
            skLineSegment(sketch, "E1827", {"start": v(-6.66, 49.25) * mm, "end": v(-6.67, 49.18) * mm});
            skLineSegment(sketch, "E1828", {"start": v(-6.67, 49.18) * mm, "end": v(-6.69, 49.11) * mm});
            skLineSegment(sketch, "E1829", {"start": v(-6.69, 49.11) * mm, "end": v(-6.7, 49.05) * mm});
            skLineSegment(sketch, "E1830", {"start": v(-6.7, 49.05) * mm, "end": v(-6.71, 48.98) * mm});
            skLineSegment(sketch, "E1831", {"start": v(-6.71, 48.98) * mm, "end": v(-6.72, 48.91) * mm});
            skLineSegment(sketch, "E1832", {"start": v(-6.72, 48.91) * mm, "end": v(-6.74, 48.85) * mm});
            skLineSegment(sketch, "E1833", {"start": v(-6.74, 48.85) * mm, "end": v(-6.75, 48.78) * mm});
            skLineSegment(sketch, "E1834", {"start": v(-6.75, 48.78) * mm, "end": v(-6.76, 48.72) * mm});
            skLineSegment(sketch, "E1835", {"start": v(-6.76, 48.72) * mm, "end": v(-6.77, 48.66) * mm});
            skLineSegment(sketch, "E1836", {"start": v(-6.77, 48.66) * mm, "end": v(-6.78, 48.6) * mm});
            skLineSegment(sketch, "E1837", {"start": v(-6.78, 48.6) * mm, "end": v(-6.79, 48.54) * mm});
            skLineSegment(sketch, "E1838", {"start": v(-6.79, 48.54) * mm, "end": v(-6.8, 48.48) * mm});
            skLineSegment(sketch, "E1839", {"start": v(-6.8, 48.48) * mm, "end": v(-6.8, 48.42) * mm});
            skLineSegment(sketch, "E1840", {"start": v(-6.8, 48.42) * mm, "end": v(-6.81, 48.36) * mm});
            skLineSegment(sketch, "E1841", {"start": v(-6.81, 48.36) * mm, "end": v(-6.82, 48.3) * mm});
            skLineSegment(sketch, "E1842", {"start": v(-6.82, 48.3) * mm, "end": v(-6.83, 48.25) * mm});
            skLineSegment(sketch, "E1843", {"start": v(-6.83, 48.25) * mm, "end": v(-6.83, 48.2) * mm});
            skLineSegment(sketch, "E1844", {"start": v(-6.83, 48.2) * mm, "end": v(-6.84, 48.14) * mm});
            skLineSegment(sketch, "E1845", {"start": v(-6.84, 48.14) * mm, "end": v(-6.85, 48.08) * mm});
            skLineSegment(sketch, "E1846", {"start": v(-6.85, 48.08) * mm, "end": v(-7.12, 48.04) * mm});
            skLineSegment(sketch, "E1847", {"start": v(-7.12, 48.04) * mm, "end": v(-7.6, 47.96) * mm});
            skLineSegment(sketch, "E1848", {"start": v(-7.6, 47.96) * mm, "end": v(-7.87, 47.93) * mm});
            skLineSegment(sketch, "E1849", {"start": v(-7.87, 47.93) * mm, "end": v(-7.9, 47.98) * mm});
            skLineSegment(sketch, "E1850", {"start": v(-7.9, 47.98) * mm, "end": v(-7.92, 48.03) * mm});
            skLineSegment(sketch, "E1851", {"start": v(-7.92, 48.03) * mm, "end": v(-7.94, 48.08) * mm});
            skLineSegment(sketch, "E1852", {"start": v(-7.94, 48.08) * mm, "end": v(-7.97, 48.13) * mm});
            skLineSegment(sketch, "E1853", {"start": v(-7.97, 48.13) * mm, "end": v(-7.99, 48.18) * mm});
            skLineSegment(sketch, "E1854", {"start": v(-7.99, 48.18) * mm, "end": v(-8.01, 48.23) * mm});
            skLineSegment(sketch, "E1855", {"start": v(-8.01, 48.23) * mm, "end": v(-8.04, 48.29) * mm});
            skLineSegment(sketch, "E1856", {"start": v(-8.04, 48.29) * mm, "end": v(-8.07, 48.34) * mm});
            skLineSegment(sketch, "E1857", {"start": v(-8.07, 48.34) * mm, "end": v(-8.1, 48.4) * mm});
            skLineSegment(sketch, "E1858", {"start": v(-8.1, 48.4) * mm, "end": v(-8.12, 48.45) * mm});
            skLineSegment(sketch, "E1859", {"start": v(-8.12, 48.45) * mm, "end": v(-8.15, 48.5) * mm});
            skLineSegment(sketch, "E1860", {"start": v(-8.15, 48.5) * mm, "end": v(-8.18, 48.56) * mm});
            skLineSegment(sketch, "E1861", {"start": v(-8.18, 48.56) * mm, "end": v(-8.2, 48.62) * mm});
            skLineSegment(sketch, "E1862", {"start": v(-8.2, 48.62) * mm, "end": v(-8.24, 48.68) * mm});
            skLineSegment(sketch, "E1863", {"start": v(-8.24, 48.68) * mm, "end": v(-8.27, 48.74) * mm});
            skLineSegment(sketch, "E1864", {"start": v(-8.27, 48.74) * mm, "end": v(-8.3, 48.8) * mm});
            skLineSegment(sketch, "E1865", {"start": v(-8.3, 48.8) * mm, "end": v(-8.33, 48.86) * mm});
            skLineSegment(sketch, "E1866", {"start": v(-8.33, 48.86) * mm, "end": v(-8.37, 48.92) * mm});
            skLineSegment(sketch, "E1867", {"start": v(-8.37, 48.92) * mm, "end": v(-8.4, 48.98) * mm});
            skLineSegment(sketch, "E1868", {"start": v(-8.4, 48.98) * mm, "end": v(-8.43, 49.04) * mm});
            skLineSegment(sketch, "E1869", {"start": v(-8.43, 49.04) * mm, "end": v(-8.47, 49.1) * mm});
            skLineSegment(sketch, "E1870", {"start": v(-8.47, 49.1) * mm, "end": v(-8.5, 49.17) * mm});
            skLineSegment(sketch, "E1871", {"start": v(-8.5, 49.17) * mm, "end": v(-8.54, 49.24) * mm});
            skLineSegment(sketch, "E1872", {"start": v(-8.54, 49.24) * mm, "end": v(-8.58, 49.3) * mm});
            skLineSegment(sketch, "E1873", {"start": v(-8.58, 49.3) * mm, "end": v(-8.62, 49.37) * mm});
            skLineSegment(sketch, "E1874", {"start": v(-8.62, 49.37) * mm, "end": v(-8.66, 49.43) * mm});
            skLineSegment(sketch, "E1875", {"start": v(-8.66, 49.43) * mm, "end": v(-8.7, 49.5) * mm});
            skLineSegment(sketch, "E1876", {"start": v(-8.7, 49.5) * mm, "end": v(-8.73, 49.57) * mm});
            skLineSegment(sketch, "E1877", {"start": v(-8.73, 49.57) * mm, "end": v(-8.78, 49.63) * mm});
            skLineSegment(sketch, "E1878", {"start": v(-8.78, 49.63) * mm, "end": v(-8.82, 49.7) * mm});
            skLineSegment(sketch, "E1879", {"start": v(-8.82, 49.7) * mm, "end": v(-8.86, 49.77) * mm});
            skLineSegment(sketch, "E1880", {"start": v(-8.86, 49.77) * mm, "end": v(-8.9, 49.84) * mm});
            skLineSegment(sketch, "E1881", {"start": v(-8.9, 49.84) * mm, "end": v(-8.95, 49.91) * mm});
            skLineSegment(sketch, "E1882", {"start": v(-8.95, 49.91) * mm, "end": v(-9, 49.98) * mm});
            skLineSegment(sketch, "E1883", {"start": v(-9, 49.98) * mm, "end": v(-9.04, 50.05) * mm});
            skLineSegment(sketch, "E1884", {"start": v(-9.04, 50.05) * mm, "end": v(-9.08, 50.12) * mm});
            skLineSegment(sketch, "E1885", {"start": v(-9.08, 50.12) * mm, "end": v(-9.13, 50.2) * mm});
            skLineSegment(sketch, "E1886", {"start": v(-9.13, 50.2) * mm, "end": v(-9.18, 50.27) * mm});
            skLineSegment(sketch, "E1887", {"start": v(-9.18, 50.27) * mm, "end": v(-9.23, 50.34) * mm});
            skLineSegment(sketch, "E1888", {"start": v(-9.23, 50.34) * mm, "end": v(-9.28, 50.4) * mm});
            skLineSegment(sketch, "E1889", {"start": v(-9.28, 50.4) * mm, "end": v(-10.22, 50.22) * mm});
            skLineSegment(sketch, "E1890", {"start": v(-10.22, 50.22) * mm, "end": v(-10.24, 50.15) * mm});
            skLineSegment(sketch, "E1891", {"start": v(-10.24, 50.15) * mm, "end": v(-10.26, 50.06) * mm});
            skLineSegment(sketch, "E1892", {"start": v(-10.26, 50.06) * mm, "end": v(-10.28, 49.97) * mm});
            skLineSegment(sketch, "E1893", {"start": v(-10.28, 49.97) * mm, "end": v(-10.3, 49.89) * mm});
            skLineSegment(sketch, "E1894", {"start": v(-10.3, 49.89) * mm, "end": v(-10.31, 49.8) * mm});
            skLineSegment(sketch, "E1895", {"start": v(-10.31, 49.8) * mm, "end": v(-10.33, 49.72) * mm});
            skLineSegment(sketch, "E1896", {"start": v(-10.33, 49.72) * mm, "end": v(-10.34, 49.64) * mm});
            skLineSegment(sketch, "E1897", {"start": v(-10.34, 49.64) * mm, "end": v(-10.36, 49.56) * mm});
            skLineSegment(sketch, "E1898", {"start": v(-10.36, 49.56) * mm, "end": v(-10.37, 49.48) * mm});
            skLineSegment(sketch, "E1899", {"start": v(-10.37, 49.48) * mm, "end": v(-10.39, 49.4) * mm});
            skLineSegment(sketch, "E1900", {"start": v(-10.39, 49.4) * mm, "end": v(-10.4, 49.32) * mm});
            skLineSegment(sketch, "E1901", {"start": v(-10.4, 49.32) * mm, "end": v(-10.41, 49.24) * mm});
            skLineSegment(sketch, "E1902", {"start": v(-10.41, 49.24) * mm, "end": v(-10.42, 49.16) * mm});
            skLineSegment(sketch, "E1903", {"start": v(-10.42, 49.16) * mm, "end": v(-10.44, 49.09) * mm});
            skLineSegment(sketch, "E1904", {"start": v(-10.44, 49.09) * mm, "end": v(-10.45, 49.01) * mm});
            skLineSegment(sketch, "E1905", {"start": v(-10.45, 49.01) * mm, "end": v(-10.46, 48.94) * mm});
            skLineSegment(sketch, "E1906", {"start": v(-10.46, 48.94) * mm, "end": v(-10.47, 48.86) * mm});
            skLineSegment(sketch, "E1907", {"start": v(-10.47, 48.86) * mm, "end": v(-10.48, 48.79) * mm});
            skLineSegment(sketch, "E1908", {"start": v(-10.48, 48.79) * mm, "end": v(-10.49, 48.72) * mm});
            skLineSegment(sketch, "E1909", {"start": v(-10.49, 48.72) * mm, "end": v(-10.5, 48.65) * mm});
            skLineSegment(sketch, "E1910", {"start": v(-10.5, 48.65) * mm, "end": v(-10.5, 48.57) * mm});
            skLineSegment(sketch, "E1911", {"start": v(-10.5, 48.57) * mm, "end": v(-10.51, 48.5) * mm});
            skLineSegment(sketch, "E1912", {"start": v(-10.51, 48.5) * mm, "end": v(-10.52, 48.44) * mm});
            skLineSegment(sketch, "E1913", {"start": v(-10.52, 48.44) * mm, "end": v(-10.53, 48.37) * mm});
            skLineSegment(sketch, "E1914", {"start": v(-10.53, 48.37) * mm, "end": v(-10.54, 48.3) * mm});
            skLineSegment(sketch, "E1915", {"start": v(-10.54, 48.3) * mm, "end": v(-10.54, 48.23) * mm});
            skLineSegment(sketch, "E1916", {"start": v(-10.54, 48.23) * mm, "end": v(-10.55, 48.17) * mm});
            skLineSegment(sketch, "E1917", {"start": v(-10.55, 48.17) * mm, "end": v(-10.55, 48.1) * mm});
            skLineSegment(sketch, "E1918", {"start": v(-10.55, 48.1) * mm, "end": v(-10.56, 48.04) * mm});
            skLineSegment(sketch, "E1919", {"start": v(-10.56, 48.04) * mm, "end": v(-10.56, 47.98) * mm});
            skLineSegment(sketch, "E1920", {"start": v(-10.56, 47.98) * mm, "end": v(-10.57, 47.92) * mm});
            skLineSegment(sketch, "E1921", {"start": v(-10.57, 47.92) * mm, "end": v(-10.57, 47.85) * mm});
            skLineSegment(sketch, "E1922", {"start": v(-10.57, 47.85) * mm, "end": v(-10.58, 47.8) * mm});
            skLineSegment(sketch, "E1923", {"start": v(-10.58, 47.8) * mm, "end": v(-10.58, 47.74) * mm});
            skLineSegment(sketch, "E1924", {"start": v(-10.58, 47.74) * mm, "end": v(-10.59, 47.68) * mm});
            skLineSegment(sketch, "E1925", {"start": v(-10.59, 47.68) * mm, "end": v(-10.59, 47.62) * mm});
            skLineSegment(sketch, "E1926", {"start": v(-10.59, 47.62) * mm, "end": v(-10.6, 47.56) * mm});
            skLineSegment(sketch, "E1927", {"start": v(-10.6, 47.56) * mm, "end": v(-10.6, 47.5) * mm});
            skLineSegment(sketch, "E1928", {"start": v(-10.6, 47.5) * mm, "end": v(-10.6, 47.45) * mm});
            skLineSegment(sketch, "E1929", {"start": v(-10.6, 47.45) * mm, "end": v(-10.6, 47.4) * mm});
            skLineSegment(sketch, "E1930", {"start": v(-10.6, 47.4) * mm, "end": v(-10.87, 47.33) * mm});
            skLineSegment(sketch, "E1931", {"start": v(-10.87, 47.33) * mm, "end": v(-11.34, 47.22) * mm});
            skLineSegment(sketch, "E1932", {"start": v(-11.34, 47.22) * mm, "end": v(-11.6, 47.16) * mm});
            skLineSegment(sketch, "E1933", {"start": v(-11.6, 47.16) * mm, "end": v(-11.64, 47.2) * mm});
            skLineSegment(sketch, "E1934", {"start": v(-11.64, 47.2) * mm, "end": v(-11.66, 47.26) * mm});
            skLineSegment(sketch, "E1935", {"start": v(-11.66, 47.26) * mm, "end": v(-11.69, 47.3) * mm});
            skLineSegment(sketch, "E1936", {"start": v(-11.69, 47.3) * mm, "end": v(-11.72, 47.35) * mm});
            skLineSegment(sketch, "E1937", {"start": v(-11.72, 47.35) * mm, "end": v(-11.75, 47.4) * mm});
            skLineSegment(sketch, "E1938", {"start": v(-11.75, 47.4) * mm, "end": v(-11.77, 47.46) * mm});
            skLineSegment(sketch, "E1939", {"start": v(-11.77, 47.46) * mm, "end": v(-11.8, 47.5) * mm});
            skLineSegment(sketch, "E1940", {"start": v(-11.8, 47.5) * mm, "end": v(-11.83, 47.56) * mm});
            skLineSegment(sketch, "E1941", {"start": v(-11.83, 47.56) * mm, "end": v(-11.87, 47.61) * mm});
            skLineSegment(sketch, "E1942", {"start": v(-11.87, 47.61) * mm, "end": v(-11.9, 47.66) * mm});
            skLineSegment(sketch, "E1943", {"start": v(-11.9, 47.66) * mm, "end": v(-11.93, 47.72) * mm});
            skLineSegment(sketch, "E1944", {"start": v(-11.93, 47.72) * mm, "end": v(-11.96, 47.77) * mm});
            skLineSegment(sketch, "E1945", {"start": v(-11.96, 47.77) * mm, "end": v(-12, 47.83) * mm});
            skLineSegment(sketch, "E1946", {"start": v(-12, 47.83) * mm, "end": v(-12.03, 47.88) * mm});
            skLineSegment(sketch, "E1947", {"start": v(-12.03, 47.88) * mm, "end": v(-12.07, 47.94) * mm});
            skLineSegment(sketch, "E1948", {"start": v(-12.07, 47.94) * mm, "end": v(-12.1, 48) * mm});
            skLineSegment(sketch, "E1949", {"start": v(-12.1, 48) * mm, "end": v(-12.14, 48.06) * mm});
            skLineSegment(sketch, "E1950", {"start": v(-12.14, 48.06) * mm, "end": v(-12.18, 48.11) * mm});
            skLineSegment(sketch, "E1951", {"start": v(-12.18, 48.11) * mm, "end": v(-12.22, 48.17) * mm});
            skLineSegment(sketch, "E1952", {"start": v(-12.22, 48.17) * mm, "end": v(-12.26, 48.23) * mm});
            skLineSegment(sketch, "E1953", {"start": v(-12.26, 48.23) * mm, "end": v(-12.3, 48.3) * mm});
            skLineSegment(sketch, "E1954", {"start": v(-12.3, 48.3) * mm, "end": v(-12.34, 48.35) * mm});
            skLineSegment(sketch, "E1955", {"start": v(-12.34, 48.35) * mm, "end": v(-12.38, 48.41) * mm});
            skLineSegment(sketch, "E1956", {"start": v(-12.38, 48.41) * mm, "end": v(-12.42, 48.48) * mm});
            skLineSegment(sketch, "E1957", {"start": v(-12.42, 48.48) * mm, "end": v(-12.46, 48.54) * mm});
            skLineSegment(sketch, "E1958", {"start": v(-12.46, 48.54) * mm, "end": v(-12.5, 48.6) * mm});
            skLineSegment(sketch, "E1959", {"start": v(-12.5, 48.6) * mm, "end": v(-12.55, 48.66) * mm});
            skLineSegment(sketch, "E1960", {"start": v(-12.55, 48.66) * mm, "end": v(-12.6, 48.73) * mm});
            skLineSegment(sketch, "E1961", {"start": v(-12.6, 48.73) * mm, "end": v(-12.64, 48.8) * mm});
            skLineSegment(sketch, "E1962", {"start": v(-12.64, 48.8) * mm, "end": v(-12.69, 48.86) * mm});
            skLineSegment(sketch, "E1963", {"start": v(-12.69, 48.86) * mm, "end": v(-12.74, 48.92) * mm});
            skLineSegment(sketch, "E1964", {"start": v(-12.74, 48.92) * mm, "end": v(-12.79, 48.99) * mm});
            skLineSegment(sketch, "E1965", {"start": v(-12.79, 48.99) * mm, "end": v(-12.84, 49.05) * mm});
            skLineSegment(sketch, "E1966", {"start": v(-12.84, 49.05) * mm, "end": v(-12.89, 49.12) * mm});
            skLineSegment(sketch, "E1967", {"start": v(-12.89, 49.12) * mm, "end": v(-12.94, 49.19) * mm});
            skLineSegment(sketch, "E1968", {"start": v(-12.94, 49.19) * mm, "end": v(-12.99, 49.26) * mm});
            skLineSegment(sketch, "E1969", {"start": v(-12.99, 49.26) * mm, "end": v(-13.04, 49.32) * mm});
            skLineSegment(sketch, "E1970", {"start": v(-13.04, 49.32) * mm, "end": v(-13.1, 49.4) * mm});
            skLineSegment(sketch, "E1971", {"start": v(-13.1, 49.4) * mm, "end": v(-13.15, 49.46) * mm});
            skLineSegment(sketch, "E1972", {"start": v(-13.15, 49.46) * mm, "end": v(-13.2, 49.52) * mm});
            skLineSegment(sketch, "E1973", {"start": v(-13.2, 49.52) * mm, "end": v(-14.13, 49.26) * mm});
            skLineSegment(sketch, "E1974", {"start": v(-14.13, 49.26) * mm, "end": v(-14.15, 49.19) * mm});
            skLineSegment(sketch, "E1975", {"start": v(-14.15, 49.19) * mm, "end": v(-14.16, 49.1) * mm});
            skLineSegment(sketch, "E1976", {"start": v(-14.16, 49.1) * mm, "end": v(-14.17, 49.01) * mm});
            skLineSegment(sketch, "E1977", {"start": v(-14.17, 49.01) * mm, "end": v(-14.18, 48.93) * mm});
            skLineSegment(sketch, "E1978", {"start": v(-14.18, 48.93) * mm, "end": v(-14.19, 48.84) * mm});
            skLineSegment(sketch, "E1979", {"start": v(-14.19, 48.84) * mm, "end": v(-14.2, 48.76) * mm});
            skLineSegment(sketch, "E1980", {"start": v(-14.2, 48.76) * mm, "end": v(-14.2, 48.67) * mm});
            skLineSegment(sketch, "E1981", {"start": v(-14.2, 48.67) * mm, "end": v(-14.21, 48.6) * mm});
            skLineSegment(sketch, "E1982", {"start": v(-14.21, 48.6) * mm, "end": v(-14.22, 48.51) * mm});
            skLineSegment(sketch, "E1983", {"start": v(-14.22, 48.51) * mm, "end": v(-14.23, 48.43) * mm});
            skLineSegment(sketch, "E1984", {"start": v(-14.23, 48.43) * mm, "end": v(-14.24, 48.35) * mm});
            skLineSegment(sketch, "E1985", {"start": v(-14.24, 48.35) * mm, "end": v(-14.24, 48.27) * mm});
            skLineSegment(sketch, "E1986", {"start": v(-14.24, 48.27) * mm, "end": v(-14.25, 48.2) * mm});
            skLineSegment(sketch, "E1987", {"start": v(-14.25, 48.2) * mm, "end": v(-14.25, 48.12) * mm});
            skLineSegment(sketch, "E1988", {"start": v(-14.25, 48.12) * mm, "end": v(-14.26, 48.04) * mm});
            skLineSegment(sketch, "E1989", {"start": v(-14.26, 48.04) * mm, "end": v(-14.26, 47.96) * mm});
            skLineSegment(sketch, "E1990", {"start": v(-14.26, 47.96) * mm, "end": v(-14.27, 47.9) * mm});
            skLineSegment(sketch, "E1991", {"start": v(-14.27, 47.9) * mm, "end": v(-14.27, 47.82) * mm});
            skLineSegment(sketch, "E1992", {"start": v(-14.27, 47.82) * mm, "end": v(-14.28, 47.74) * mm});
            skLineSegment(sketch, "E1993", {"start": v(-14.28, 47.74) * mm, "end": v(-14.28, 47.67) * mm});
            skLineSegment(sketch, "E1994", {"start": v(-14.28, 47.67) * mm, "end": v(-14.28, 47.6) * mm});
            skLineSegment(sketch, "E1995", {"start": v(-14.28, 47.6) * mm, "end": v(-14.29, 47.53) * mm});
            skLineSegment(sketch, "E1996", {"start": v(-14.29, 47.53) * mm, "end": v(-14.29, 47.46) * mm});
            skLineSegment(sketch, "E1997", {"start": v(-14.29, 47.46) * mm, "end": v(-14.3, 47.4) * mm});
            skLineSegment(sketch, "E1998", {"start": v(-14.3, 47.4) * mm, "end": v(-14.3, 47.33) * mm});
            skLineSegment(sketch, "E1999", {"start": v(-14.3, 47.33) * mm, "end": v(-14.3, 47.26) * mm});
            skLineSegment(sketch, "E2000", {"start": v(-14.3, 47.26) * mm, "end": v(-14.3, 47.2) * mm});
            skLineSegment(sketch, "E2001", {"start": v(-14.3, 47.2) * mm, "end": v(-14.3, 47.13) * mm});
            skLineSegment(sketch, "E2002", {"start": v(-14.3, 47.13) * mm, "end": v(-14.3, 47.06) * mm});
            skLineSegment(sketch, "E2003", {"start": v(-14.3, 47.06) * mm, "end": v(-14.3, 47) * mm});
            skLineSegment(sketch, "E2004", {"start": v(-14.3, 47) * mm, "end": v(-14.3, 46.94) * mm});
            skLineSegment(sketch, "E2005", {"start": v(-14.3, 46.94) * mm, "end": v(-14.3, 46.88) * mm});
            skLineSegment(sketch, "E2006", {"start": v(-14.3, 46.88) * mm, "end": v(-14.3, 46.82) * mm});
            skLineSegment(sketch, "E2007", {"start": v(-14.3, 46.82) * mm, "end": v(-14.3, 46.76) * mm});
            skLineSegment(sketch, "E2008", {"start": v(-14.3, 46.76) * mm, "end": v(-14.3, 46.7) * mm});
            skLineSegment(sketch, "E2009", {"start": v(-14.3, 46.7) * mm, "end": v(-14.3, 46.64) * mm});
            skLineSegment(sketch, "E2010", {"start": v(-14.3, 46.64) * mm, "end": v(-14.3, 46.58) * mm});
            skLineSegment(sketch, "E2011", {"start": v(-14.3, 46.58) * mm, "end": v(-14.29, 46.53) * mm});
            skLineSegment(sketch, "E2012", {"start": v(-14.29, 46.53) * mm, "end": v(-14.29, 46.47) * mm});
            skLineSegment(sketch, "E2013", {"start": v(-14.29, 46.47) * mm, "end": v(-14.28, 46.42) * mm});
            skLineSegment(sketch, "E2014", {"start": v(-14.28, 46.42) * mm, "end": v(-14.55, 46.33) * mm});
            skLineSegment(sketch, "E2015", {"start": v(-14.55, 46.33) * mm, "end": v(-15, 46.19) * mm});
            skLineSegment(sketch, "E2016", {"start": v(-15, 46.19) * mm, "end": v(-15.27, 46.1) * mm});
            skLineSegment(sketch, "E2017", {"start": v(-15.27, 46.1) * mm, "end": v(-15.3, 46.15) * mm});
            skLineSegment(sketch, "E2018", {"start": v(-15.3, 46.15) * mm, "end": v(-15.33, 46.2) * mm});
            skLineSegment(sketch, "E2019", {"start": v(-15.33, 46.2) * mm, "end": v(-15.36, 46.24) * mm});
            skLineSegment(sketch, "E2020", {"start": v(-15.36, 46.24) * mm, "end": v(-15.4, 46.29) * mm});
            skLineSegment(sketch, "E2021", {"start": v(-15.4, 46.29) * mm, "end": v(-15.43, 46.34) * mm});
            skLineSegment(sketch, "E2022", {"start": v(-15.43, 46.34) * mm, "end": v(-15.46, 46.39) * mm});
            skLineSegment(sketch, "E2023", {"start": v(-15.46, 46.39) * mm, "end": v(-15.5, 46.43) * mm});
            skLineSegment(sketch, "E2024", {"start": v(-15.5, 46.43) * mm, "end": v(-15.53, 46.48) * mm});
            skLineSegment(sketch, "E2025", {"start": v(-15.53, 46.48) * mm, "end": v(-15.57, 46.53) * mm});
            skLineSegment(sketch, "E2026", {"start": v(-15.57, 46.53) * mm, "end": v(-15.6, 46.58) * mm});
            skLineSegment(sketch, "E2027", {"start": v(-15.6, 46.58) * mm, "end": v(-15.64, 46.64) * mm});
            skLineSegment(sketch, "E2028", {"start": v(-15.64, 46.64) * mm, "end": v(-15.68, 46.69) * mm});
            skLineSegment(sketch, "E2029", {"start": v(-15.68, 46.69) * mm, "end": v(-15.71, 46.74) * mm});
            skLineSegment(sketch, "E2030", {"start": v(-15.71, 46.74) * mm, "end": v(-15.75, 46.8) * mm});
            skLineSegment(sketch, "E2031", {"start": v(-15.75, 46.8) * mm, "end": v(-15.8, 46.85) * mm});
            skLineSegment(sketch, "E2032", {"start": v(-15.8, 46.85) * mm, "end": v(-15.83, 46.9) * mm});
            skLineSegment(sketch, "E2033", {"start": v(-15.83, 46.9) * mm, "end": v(-15.87, 46.95) * mm});
            skLineSegment(sketch, "E2034", {"start": v(-15.87, 46.95) * mm, "end": v(-15.92, 47.01) * mm});
            skLineSegment(sketch, "E2035", {"start": v(-15.92, 47.01) * mm, "end": v(-15.96, 47.07) * mm});
            skLineSegment(sketch, "E2036", {"start": v(-15.96, 47.07) * mm, "end": v(-16, 47.12) * mm});
            skLineSegment(sketch, "E2037", {"start": v(-16, 47.12) * mm, "end": v(-16.05, 47.18) * mm});
            skLineSegment(sketch, "E2038", {"start": v(-16.05, 47.18) * mm, "end": v(-16.1, 47.24) * mm});
            skLineSegment(sketch, "E2039", {"start": v(-16.1, 47.24) * mm, "end": v(-16.14, 47.3) * mm});
            skLineSegment(sketch, "E2040", {"start": v(-16.14, 47.3) * mm, "end": v(-16.19, 47.35) * mm});
            skLineSegment(sketch, "E2041", {"start": v(-16.19, 47.35) * mm, "end": v(-16.23, 47.41) * mm});
            skLineSegment(sketch, "E2042", {"start": v(-16.23, 47.41) * mm, "end": v(-16.28, 47.47) * mm});
            skLineSegment(sketch, "E2043", {"start": v(-16.28, 47.47) * mm, "end": v(-16.33, 47.53) * mm});
            skLineSegment(sketch, "E2044", {"start": v(-16.33, 47.53) * mm, "end": v(-16.38, 47.59) * mm});
            skLineSegment(sketch, "E2045", {"start": v(-16.38, 47.59) * mm, "end": v(-16.43, 47.65) * mm});
            skLineSegment(sketch, "E2046", {"start": v(-16.43, 47.65) * mm, "end": v(-16.48, 47.71) * mm});
            skLineSegment(sketch, "E2047", {"start": v(-16.48, 47.71) * mm, "end": v(-16.54, 47.77) * mm});
            skLineSegment(sketch, "E2048", {"start": v(-16.54, 47.77) * mm, "end": v(-16.6, 47.83) * mm});
            skLineSegment(sketch, "E2049", {"start": v(-16.6, 47.83) * mm, "end": v(-16.64, 47.9) * mm});
            skLineSegment(sketch, "E2050", {"start": v(-16.64, 47.9) * mm, "end": v(-16.7, 47.96) * mm});
            skLineSegment(sketch, "E2051", {"start": v(-16.7, 47.96) * mm, "end": v(-16.76, 48.02) * mm});
            skLineSegment(sketch, "E2052", {"start": v(-16.76, 48.02) * mm, "end": v(-16.81, 48.09) * mm});
            skLineSegment(sketch, "E2053", {"start": v(-16.81, 48.09) * mm, "end": v(-16.87, 48.15) * mm});
            skLineSegment(sketch, "E2054", {"start": v(-16.87, 48.15) * mm, "end": v(-16.93, 48.21) * mm});
            skLineSegment(sketch, "E2055", {"start": v(-16.93, 48.21) * mm, "end": v(-16.99, 48.28) * mm});
            skLineSegment(sketch, "E2056", {"start": v(-16.99, 48.28) * mm, "end": v(-17.05, 48.33) * mm});
            skLineSegment(sketch, "E2057", {"start": v(-17.05, 48.33) * mm, "end": v(-17.95, 48) * mm});
            skLineSegment(sketch, "E2058", {"start": v(-17.95, 48) * mm, "end": v(-17.96, 47.93) * mm});
            skLineSegment(sketch, "E2059", {"start": v(-17.96, 47.93) * mm, "end": v(-17.97, 47.84) * mm});
            skLineSegment(sketch, "E2060", {"start": v(-17.97, 47.84) * mm, "end": v(-17.97, 47.75) * mm});
            skLineSegment(sketch, "E2061", {"start": v(-17.97, 47.75) * mm, "end": v(-17.97, 47.66) * mm});
            skLineSegment(sketch, "E2062", {"start": v(-17.97, 47.66) * mm, "end": v(-17.98, 47.58) * mm});
            skLineSegment(sketch, "E2063", {"start": v(-17.98, 47.58) * mm, "end": v(-17.98, 47.5) * mm});
            skLineSegment(sketch, "E2064", {"start": v(-17.98, 47.5) * mm, "end": v(-17.98, 47.41) * mm});
            skLineSegment(sketch, "E2065", {"start": v(-17.98, 47.41) * mm, "end": v(-17.98, 47.33) * mm});
            skLineSegment(sketch, "E2066", {"start": v(-17.98, 47.33) * mm, "end": v(-17.98, 47.25) * mm});
            skLineSegment(sketch, "E2067", {"start": v(-17.98, 47.25) * mm, "end": v(-17.99, 47.16) * mm});
            skLineSegment(sketch, "E2068", {"start": v(-17.99, 47.16) * mm, "end": v(-17.99, 47.08) * mm});
            skLineSegment(sketch, "E2069", {"start": v(-17.99, 47.08) * mm, "end": v(-17.99, 47) * mm});
            skLineSegment(sketch, "E2070", {"start": v(-17.99, 47) * mm, "end": v(-17.99, 46.93) * mm});
            skLineSegment(sketch, "E2071", {"start": v(-17.99, 46.93) * mm, "end": v(-17.99, 46.85) * mm});
            skLineSegment(sketch, "E2072", {"start": v(-17.99, 46.85) * mm, "end": v(-17.99, 46.77) * mm});
            skLineSegment(sketch, "E2073", {"start": v(-17.99, 46.77) * mm, "end": v(-17.98, 46.7) * mm});
            skLineSegment(sketch, "E2074", {"start": v(-17.98, 46.7) * mm, "end": v(-17.98, 46.62) * mm});
            skLineSegment(sketch, "E2075", {"start": v(-17.98, 46.62) * mm, "end": v(-17.98, 46.55) * mm});
            skLineSegment(sketch, "E2076", {"start": v(-17.98, 46.55) * mm, "end": v(-17.98, 46.48) * mm});
            skLineSegment(sketch, "E2077", {"start": v(-17.98, 46.48) * mm, "end": v(-17.98, 46.4) * mm});
            skLineSegment(sketch, "E2078", {"start": v(-17.98, 46.4) * mm, "end": v(-17.97, 46.33) * mm});
            skLineSegment(sketch, "E2079", {"start": v(-17.97, 46.33) * mm, "end": v(-17.97, 46.26) * mm});
            skLineSegment(sketch, "E2080", {"start": v(-17.97, 46.26) * mm, "end": v(-17.97, 46.2) * mm});
            skLineSegment(sketch, "E2081", {"start": v(-17.97, 46.2) * mm, "end": v(-17.96, 46.13) * mm});
            skLineSegment(sketch, "E2082", {"start": v(-17.96, 46.13) * mm, "end": v(-17.96, 46.06) * mm});
            skLineSegment(sketch, "E2083", {"start": v(-17.96, 46.06) * mm, "end": v(-17.96, 46) * mm});
            skLineSegment(sketch, "E2084", {"start": v(-17.96, 46) * mm, "end": v(-17.95, 45.93) * mm});
            skLineSegment(sketch, "E2085", {"start": v(-17.95, 45.93) * mm, "end": v(-17.95, 45.86) * mm});
            skLineSegment(sketch, "E2086", {"start": v(-17.95, 45.86) * mm, "end": v(-17.94, 45.8) * mm});
            skLineSegment(sketch, "E2087", {"start": v(-17.94, 45.8) * mm, "end": v(-17.94, 45.73) * mm});
            skLineSegment(sketch, "E2088", {"start": v(-17.94, 45.73) * mm, "end": v(-17.93, 45.67) * mm});
            skLineSegment(sketch, "E2089", {"start": v(-17.93, 45.67) * mm, "end": v(-17.93, 45.61) * mm});
            skLineSegment(sketch, "E2090", {"start": v(-17.93, 45.61) * mm, "end": v(-17.92, 45.55) * mm});
            skLineSegment(sketch, "E2091", {"start": v(-17.92, 45.55) * mm, "end": v(-17.92, 45.5) * mm});
            skLineSegment(sketch, "E2092", {"start": v(-17.92, 45.5) * mm, "end": v(-17.91, 45.43) * mm});
            skLineSegment(sketch, "E2093", {"start": v(-17.91, 45.43) * mm, "end": v(-17.9, 45.38) * mm});
            skLineSegment(sketch, "E2094", {"start": v(-17.9, 45.38) * mm, "end": v(-17.9, 45.32) * mm});
            skLineSegment(sketch, "E2095", {"start": v(-17.9, 45.32) * mm, "end": v(-17.9, 45.26) * mm});
            skLineSegment(sketch, "E2096", {"start": v(-17.9, 45.26) * mm, "end": v(-17.89, 45.2) * mm});
            skLineSegment(sketch, "E2097", {"start": v(-17.89, 45.2) * mm, "end": v(-17.88, 45.16) * mm});
            skLineSegment(sketch, "E2098", {"start": v(-17.88, 45.16) * mm, "end": v(-18.14, 45.05) * mm});
            skLineSegment(sketch, "E2099", {"start": v(-18.14, 45.05) * mm, "end": v(-18.58, 44.87) * mm});
            skLineSegment(sketch, "E2100", {"start": v(-18.58, 44.87) * mm, "end": v(-18.84, 44.76) * mm});
            skLineSegment(sketch, "E2101", {"start": v(-18.84, 44.76) * mm, "end": v(-18.88, 44.8) * mm});
            skLineSegment(sketch, "E2102", {"start": v(-18.88, 44.8) * mm, "end": v(-18.91, 44.85) * mm});
            skLineSegment(sketch, "E2103", {"start": v(-18.91, 44.85) * mm, "end": v(-18.95, 44.9) * mm});
            skLineSegment(sketch, "E2104", {"start": v(-18.95, 44.9) * mm, "end": v(-18.98, 44.94) * mm});
            skLineSegment(sketch, "E2105", {"start": v(-18.98, 44.94) * mm, "end": v(-19.02, 44.98) * mm});
            skLineSegment(sketch, "E2106", {"start": v(-19.02, 44.98) * mm, "end": v(-19.05, 45.03) * mm});
            skLineSegment(sketch, "E2107", {"start": v(-19.05, 45.03) * mm, "end": v(-19.1, 45.08) * mm});
            skLineSegment(sketch, "E2108", {"start": v(-19.1, 45.08) * mm, "end": v(-19.13, 45.12) * mm});
            skLineSegment(sketch, "E2109", {"start": v(-19.13, 45.12) * mm, "end": v(-19.17, 45.17) * mm});
            skLineSegment(sketch, "E2110", {"start": v(-19.17, 45.17) * mm, "end": v(-19.2, 45.22) * mm});
            skLineSegment(sketch, "E2111", {"start": v(-19.2, 45.22) * mm, "end": v(-19.25, 45.27) * mm});
            skLineSegment(sketch, "E2112", {"start": v(-19.25, 45.27) * mm, "end": v(-19.3, 45.31) * mm});
            skLineSegment(sketch, "E2113", {"start": v(-19.3, 45.31) * mm, "end": v(-19.33, 45.36) * mm});
            skLineSegment(sketch, "E2114", {"start": v(-19.33, 45.36) * mm, "end": v(-19.38, 45.41) * mm});
            skLineSegment(sketch, "E2115", {"start": v(-19.38, 45.41) * mm, "end": v(-19.42, 45.46) * mm});
            skLineSegment(sketch, "E2116", {"start": v(-19.42, 45.46) * mm, "end": v(-19.46, 45.51) * mm});
            skLineSegment(sketch, "E2117", {"start": v(-19.46, 45.51) * mm, "end": v(-19.5, 45.56) * mm});
            skLineSegment(sketch, "E2118", {"start": v(-19.5, 45.56) * mm, "end": v(-19.56, 45.62) * mm});
            skLineSegment(sketch, "E2119", {"start": v(-19.56, 45.62) * mm, "end": v(-19.6, 45.67) * mm});
            skLineSegment(sketch, "E2120", {"start": v(-19.6, 45.67) * mm, "end": v(-19.65, 45.72) * mm});
            skLineSegment(sketch, "E2121", {"start": v(-19.65, 45.72) * mm, "end": v(-19.7, 45.77) * mm});
            skLineSegment(sketch, "E2122", {"start": v(-19.7, 45.77) * mm, "end": v(-19.75, 45.83) * mm});
            skLineSegment(sketch, "E2123", {"start": v(-19.75, 45.83) * mm, "end": v(-19.8, 45.88) * mm});
            skLineSegment(sketch, "E2124", {"start": v(-19.8, 45.88) * mm, "end": v(-19.85, 45.94) * mm});
            skLineSegment(sketch, "E2125", {"start": v(-19.85, 45.94) * mm, "end": v(-19.9, 46) * mm});
            skLineSegment(sketch, "E2126", {"start": v(-19.9, 46) * mm, "end": v(-19.96, 46.05) * mm});
            skLineSegment(sketch, "E2127", {"start": v(-19.96, 46.05) * mm, "end": v(-20, 46.1) * mm});
            skLineSegment(sketch, "E2128", {"start": v(-20, 46.1) * mm, "end": v(-20.06, 46.16) * mm});
            skLineSegment(sketch, "E2129", {"start": v(-20.06, 46.16) * mm, "end": v(-20.12, 46.21) * mm});
            skLineSegment(sketch, "E2130", {"start": v(-20.12, 46.21) * mm, "end": v(-20.18, 46.27) * mm});
            skLineSegment(sketch, "E2131", {"start": v(-20.18, 46.27) * mm, "end": v(-20.23, 46.33) * mm});
            skLineSegment(sketch, "E2132", {"start": v(-20.23, 46.33) * mm, "end": v(-20.3, 46.38) * mm});
            skLineSegment(sketch, "E2133", {"start": v(-20.3, 46.38) * mm, "end": v(-20.35, 46.44) * mm});
            skLineSegment(sketch, "E2134", {"start": v(-20.35, 46.44) * mm, "end": v(-20.41, 46.5) * mm});
            skLineSegment(sketch, "E2135", {"start": v(-20.41, 46.5) * mm, "end": v(-20.47, 46.56) * mm});
            skLineSegment(sketch, "E2136", {"start": v(-20.47, 46.56) * mm, "end": v(-20.53, 46.62) * mm});
            skLineSegment(sketch, "E2137", {"start": v(-20.53, 46.62) * mm, "end": v(-20.6, 46.68) * mm});
            skLineSegment(sketch, "E2138", {"start": v(-20.6, 46.68) * mm, "end": v(-20.66, 46.74) * mm});
            skLineSegment(sketch, "E2139", {"start": v(-20.66, 46.74) * mm, "end": v(-20.73, 46.8) * mm});
            skLineSegment(sketch, "E2140", {"start": v(-20.73, 46.8) * mm, "end": v(-20.79, 46.85) * mm});
            skLineSegment(sketch, "E2141", {"start": v(-20.79, 46.85) * mm, "end": v(-21.66, 46.45) * mm});
            skLineSegment(sketch, "E2142", {"start": v(-21.66, 46.45) * mm, "end": v(-21.67, 46.37) * mm});
            skLineSegment(sketch, "E2143", {"start": v(-21.67, 46.37) * mm, "end": v(-21.66, 46.28) * mm});
            skLineSegment(sketch, "E2144", {"start": v(-21.66, 46.28) * mm, "end": v(-21.66, 46.2) * mm});
            skLineSegment(sketch, "E2145", {"start": v(-21.66, 46.2) * mm, "end": v(-21.66, 46.1) * mm});
            skLineSegment(sketch, "E2146", {"start": v(-21.66, 46.1) * mm, "end": v(-21.65, 46.02) * mm});
            skLineSegment(sketch, "E2147", {"start": v(-21.65, 46.02) * mm, "end": v(-21.65, 45.94) * mm});
            skLineSegment(sketch, "E2148", {"start": v(-21.65, 45.94) * mm, "end": v(-21.65, 45.85) * mm});
            skLineSegment(sketch, "E2149", {"start": v(-21.65, 45.85) * mm, "end": v(-21.64, 45.77) * mm});
            skLineSegment(sketch, "E2150", {"start": v(-21.64, 45.77) * mm, "end": v(-21.64, 45.69) * mm});
            skLineSegment(sketch, "E2151", {"start": v(-21.64, 45.69) * mm, "end": v(-21.63, 45.6) * mm});
            skLineSegment(sketch, "E2152", {"start": v(-21.63, 45.6) * mm, "end": v(-21.62, 45.53) * mm});
            skLineSegment(sketch, "E2153", {"start": v(-21.62, 45.53) * mm, "end": v(-21.62, 45.45) * mm});
            skLineSegment(sketch, "E2154", {"start": v(-21.62, 45.45) * mm, "end": v(-21.61, 45.37) * mm});
            skLineSegment(sketch, "E2155", {"start": v(-21.61, 45.37) * mm, "end": v(-21.6, 45.3) * mm});
            skLineSegment(sketch, "E2156", {"start": v(-21.6, 45.3) * mm, "end": v(-21.6, 45.22) * mm});
            skLineSegment(sketch, "E2157", {"start": v(-21.6, 45.22) * mm, "end": v(-21.6, 45.14) * mm});
            skLineSegment(sketch, "E2158", {"start": v(-21.6, 45.14) * mm, "end": v(-21.59, 45.07) * mm});
            skLineSegment(sketch, "E2159", {"start": v(-21.59, 45.07) * mm, "end": v(-21.58, 45) * mm});
            skLineSegment(sketch, "E2160", {"start": v(-21.58, 45) * mm, "end": v(-21.57, 44.92) * mm});
            skLineSegment(sketch, "E2161", {"start": v(-21.57, 44.92) * mm, "end": v(-21.56, 44.85) * mm});
            skLineSegment(sketch, "E2162", {"start": v(-21.56, 44.85) * mm, "end": v(-21.55, 44.78) * mm});
            skLineSegment(sketch, "E2163", {"start": v(-21.55, 44.78) * mm, "end": v(-21.55, 44.71) * mm});
            skLineSegment(sketch, "E2164", {"start": v(-21.55, 44.71) * mm, "end": v(-21.54, 44.64) * mm});
            skLineSegment(sketch, "E2165", {"start": v(-21.54, 44.64) * mm, "end": v(-21.53, 44.57) * mm});
            skLineSegment(sketch, "E2166", {"start": v(-21.53, 44.57) * mm, "end": v(-21.52, 44.5) * mm});
            skLineSegment(sketch, "E2167", {"start": v(-21.52, 44.5) * mm, "end": v(-21.51, 44.44) * mm});
            skLineSegment(sketch, "E2168", {"start": v(-21.51, 44.44) * mm, "end": v(-21.5, 44.38) * mm});
            skLineSegment(sketch, "E2169", {"start": v(-21.5, 44.38) * mm, "end": v(-21.5, 44.31) * mm});
            skLineSegment(sketch, "E2170", {"start": v(-21.5, 44.31) * mm, "end": v(-21.48, 44.25) * mm});
            skLineSegment(sketch, "E2171", {"start": v(-21.48, 44.25) * mm, "end": v(-21.47, 44.19) * mm});
            skLineSegment(sketch, "E2172", {"start": v(-21.47, 44.19) * mm, "end": v(-21.46, 44.12) * mm});
            skLineSegment(sketch, "E2173", {"start": v(-21.46, 44.12) * mm, "end": v(-21.45, 44.06) * mm});
            skLineSegment(sketch, "E2174", {"start": v(-21.45, 44.06) * mm, "end": v(-21.44, 44) * mm});
            skLineSegment(sketch, "E2175", {"start": v(-21.44, 44) * mm, "end": v(-21.43, 43.95) * mm});
            skLineSegment(sketch, "E2176", {"start": v(-21.43, 43.95) * mm, "end": v(-21.42, 43.89) * mm});
            skLineSegment(sketch, "E2177", {"start": v(-21.42, 43.89) * mm, "end": v(-21.41, 43.83) * mm});
            skLineSegment(sketch, "E2178", {"start": v(-21.41, 43.83) * mm, "end": v(-21.4, 43.78) * mm});
            skLineSegment(sketch, "E2179", {"start": v(-21.4, 43.78) * mm, "end": v(-21.4, 43.72) * mm});
            skLineSegment(sketch, "E2180", {"start": v(-21.4, 43.72) * mm, "end": v(-21.38, 43.67) * mm});
            skLineSegment(sketch, "E2181", {"start": v(-21.38, 43.67) * mm, "end": v(-21.37, 43.61) * mm});
            skLineSegment(sketch, "E2182", {"start": v(-21.37, 43.61) * mm, "end": v(-21.62, 43.49) * mm});
            skLineSegment(sketch, "E2183", {"start": v(-21.62, 43.49) * mm, "end": v(-22.05, 43.27) * mm});
            skLineSegment(sketch, "E2184", {"start": v(-22.05, 43.27) * mm, "end": v(-22.3, 43.15) * mm});
            skLineSegment(sketch, "E2185", {"start": v(-22.3, 43.15) * mm, "end": v(-22.33, 43.19) * mm});
            skLineSegment(sketch, "E2186", {"start": v(-22.33, 43.19) * mm, "end": v(-22.37, 43.23) * mm});
            skLineSegment(sketch, "E2187", {"start": v(-22.37, 43.23) * mm, "end": v(-22.4, 43.27) * mm});
            skLineSegment(sketch, "E2188", {"start": v(-22.4, 43.27) * mm, "end": v(-22.45, 43.31) * mm});
            skLineSegment(sketch, "E2189", {"start": v(-22.45, 43.31) * mm, "end": v(-22.49, 43.35) * mm});
            skLineSegment(sketch, "E2190", {"start": v(-22.49, 43.35) * mm, "end": v(-22.53, 43.4) * mm});
            skLineSegment(sketch, "E2191", {"start": v(-22.53, 43.4) * mm, "end": v(-22.57, 43.44) * mm});
            skLineSegment(sketch, "E2192", {"start": v(-22.57, 43.44) * mm, "end": v(-22.61, 43.48) * mm});
            skLineSegment(sketch, "E2193", {"start": v(-22.61, 43.48) * mm, "end": v(-22.65, 43.53) * mm});
            skLineSegment(sketch, "E2194", {"start": v(-22.65, 43.53) * mm, "end": v(-22.7, 43.57) * mm});
            skLineSegment(sketch, "E2195", {"start": v(-22.7, 43.57) * mm, "end": v(-22.74, 43.62) * mm});
            skLineSegment(sketch, "E2196", {"start": v(-22.74, 43.62) * mm, "end": v(-22.79, 43.66) * mm});
            skLineSegment(sketch, "E2197", {"start": v(-22.79, 43.66) * mm, "end": v(-22.83, 43.7) * mm});
            skLineSegment(sketch, "E2198", {"start": v(-22.83, 43.7) * mm, "end": v(-22.88, 43.75) * mm});
            skLineSegment(sketch, "E2199", {"start": v(-22.88, 43.75) * mm, "end": v(-22.93, 43.8) * mm});
            skLineSegment(sketch, "E2200", {"start": v(-22.93, 43.8) * mm, "end": v(-22.97, 43.85) * mm});
            skLineSegment(sketch, "E2201", {"start": v(-22.97, 43.85) * mm, "end": v(-23.02, 43.9) * mm});
            skLineSegment(sketch, "E2202", {"start": v(-23.02, 43.9) * mm, "end": v(-23.07, 43.94) * mm});
            skLineSegment(sketch, "E2203", {"start": v(-23.07, 43.94) * mm, "end": v(-23.13, 43.99) * mm});
            skLineSegment(sketch, "E2204", {"start": v(-23.13, 43.99) * mm, "end": v(-23.18, 44.04) * mm});
            skLineSegment(sketch, "E2205", {"start": v(-23.18, 44.04) * mm, "end": v(-23.23, 44.09) * mm});
            skLineSegment(sketch, "E2206", {"start": v(-23.23, 44.09) * mm, "end": v(-23.28, 44.14) * mm});
            skLineSegment(sketch, "E2207", {"start": v(-23.28, 44.14) * mm, "end": v(-23.34, 44.19) * mm});
            skLineSegment(sketch, "E2208", {"start": v(-23.34, 44.19) * mm, "end": v(-23.4, 44.24) * mm});
            skLineSegment(sketch, "E2209", {"start": v(-23.4, 44.24) * mm, "end": v(-23.45, 44.29) * mm});
            skLineSegment(sketch, "E2210", {"start": v(-23.45, 44.29) * mm, "end": v(-23.5, 44.34) * mm});
            skLineSegment(sketch, "E2211", {"start": v(-23.5, 44.34) * mm, "end": v(-23.56, 44.39) * mm});
            skLineSegment(sketch, "E2212", {"start": v(-23.56, 44.39) * mm, "end": v(-23.62, 44.44) * mm});
            skLineSegment(sketch, "E2213", {"start": v(-23.62, 44.44) * mm, "end": v(-23.68, 44.5) * mm});
            skLineSegment(sketch, "E2214", {"start": v(-23.68, 44.5) * mm, "end": v(-23.74, 44.54) * mm});
            skLineSegment(sketch, "E2215", {"start": v(-23.74, 44.54) * mm, "end": v(-23.8, 44.6) * mm});
            skLineSegment(sketch, "E2216", {"start": v(-23.8, 44.6) * mm, "end": v(-23.87, 44.65) * mm});
            skLineSegment(sketch, "E2217", {"start": v(-23.87, 44.65) * mm, "end": v(-23.93, 44.7) * mm});
            skLineSegment(sketch, "E2218", {"start": v(-23.93, 44.7) * mm, "end": v(-24, 44.76) * mm});
            skLineSegment(sketch, "E2219", {"start": v(-24, 44.76) * mm, "end": v(-24.06, 44.8) * mm});
            skLineSegment(sketch, "E2220", {"start": v(-24.06, 44.8) * mm, "end": v(-24.13, 44.86) * mm});
            skLineSegment(sketch, "E2221", {"start": v(-24.13, 44.86) * mm, "end": v(-24.2, 44.92) * mm});
            skLineSegment(sketch, "E2222", {"start": v(-24.2, 44.92) * mm, "end": v(-24.26, 44.97) * mm});
            skLineSegment(sketch, "E2223", {"start": v(-24.26, 44.97) * mm, "end": v(-24.33, 45.03) * mm});
            skLineSegment(sketch, "E2224", {"start": v(-24.33, 45.03) * mm, "end": v(-24.4, 45.07) * mm});
            skLineSegment(sketch, "E2225", {"start": v(-24.4, 45.07) * mm, "end": v(-25.24, 44.6) * mm});
            skLineSegment(sketch, "E2226", {"start": v(-25.24, 44.6) * mm, "end": v(-25.24, 44.53) * mm});
            skLineSegment(sketch, "E2227", {"start": v(-25.24, 44.53) * mm, "end": v(-25.23, 44.44) * mm});
            skLineSegment(sketch, "E2228", {"start": v(-25.23, 44.44) * mm, "end": v(-25.22, 44.35) * mm});
            skLineSegment(sketch, "E2229", {"start": v(-25.22, 44.35) * mm, "end": v(-25.2, 44.27) * mm});
            skLineSegment(sketch, "E2230", {"start": v(-25.2, 44.27) * mm, "end": v(-25.2, 44.18) * mm});
            skLineSegment(sketch, "E2231", {"start": v(-25.2, 44.18) * mm, "end": v(-25.19, 44.1) * mm});
            skLineSegment(sketch, "E2232", {"start": v(-25.19, 44.1) * mm, "end": v(-25.18, 44.01) * mm});
            skLineSegment(sketch, "E2233", {"start": v(-25.18, 44.01) * mm, "end": v(-25.17, 43.93) * mm});
            skLineSegment(sketch, "E2234", {"start": v(-25.17, 43.93) * mm, "end": v(-25.15, 43.85) * mm});
            skLineSegment(sketch, "E2235", {"start": v(-25.15, 43.85) * mm, "end": v(-25.14, 43.77) * mm});
            skLineSegment(sketch, "E2236", {"start": v(-25.14, 43.77) * mm, "end": v(-25.13, 43.7) * mm});
            skLineSegment(sketch, "E2237", {"start": v(-25.13, 43.7) * mm, "end": v(-25.12, 43.61) * mm});
            skLineSegment(sketch, "E2238", {"start": v(-25.12, 43.61) * mm, "end": v(-25.1, 43.54) * mm});
            skLineSegment(sketch, "E2239", {"start": v(-25.1, 43.54) * mm, "end": v(-25.1, 43.46) * mm});
            skLineSegment(sketch, "E2240", {"start": v(-25.1, 43.46) * mm, "end": v(-25.08, 43.38) * mm});
            skLineSegment(sketch, "E2241", {"start": v(-25.08, 43.38) * mm, "end": v(-25.07, 43.3) * mm});
            skLineSegment(sketch, "E2242", {"start": v(-25.07, 43.3) * mm, "end": v(-25.05, 43.24) * mm});
            skLineSegment(sketch, "E2243", {"start": v(-25.05, 43.24) * mm, "end": v(-25.04, 43.16) * mm});
            skLineSegment(sketch, "E2244", {"start": v(-25.04, 43.16) * mm, "end": v(-25.03, 43.1) * mm});
            skLineSegment(sketch, "E2245", {"start": v(-25.03, 43.1) * mm, "end": v(-25.01, 43.02) * mm});
            skLineSegment(sketch, "E2246", {"start": v(-25.01, 43.02) * mm, "end": v(-25, 42.95) * mm});
            skLineSegment(sketch, "E2247", {"start": v(-25, 42.95) * mm, "end": v(-24.99, 42.88) * mm});
            skLineSegment(sketch, "E2248", {"start": v(-24.99, 42.88) * mm, "end": v(-24.97, 42.81) * mm});
            skLineSegment(sketch, "E2249", {"start": v(-24.97, 42.81) * mm, "end": v(-24.96, 42.75) * mm});
            skLineSegment(sketch, "E2250", {"start": v(-24.96, 42.75) * mm, "end": v(-24.95, 42.68) * mm});
            skLineSegment(sketch, "E2251", {"start": v(-24.95, 42.68) * mm, "end": v(-24.93, 42.62) * mm});
            skLineSegment(sketch, "E2252", {"start": v(-24.93, 42.62) * mm, "end": v(-24.92, 42.55) * mm});
            skLineSegment(sketch, "E2253", {"start": v(-24.92, 42.55) * mm, "end": v(-24.9, 42.49) * mm});
            skLineSegment(sketch, "E2254", {"start": v(-24.9, 42.49) * mm, "end": v(-24.89, 42.43) * mm});
            skLineSegment(sketch, "E2255", {"start": v(-24.89, 42.43) * mm, "end": v(-24.87, 42.37) * mm});
            skLineSegment(sketch, "E2256", {"start": v(-24.87, 42.37) * mm, "end": v(-24.86, 42.3) * mm});
            skLineSegment(sketch, "E2257", {"start": v(-24.86, 42.3) * mm, "end": v(-24.84, 42.25) * mm});
            skLineSegment(sketch, "E2258", {"start": v(-24.84, 42.25) * mm, "end": v(-24.83, 42.19) * mm});
            skLineSegment(sketch, "E2259", {"start": v(-24.83, 42.19) * mm, "end": v(-24.81, 42.13) * mm});
            skLineSegment(sketch, "E2260", {"start": v(-24.81, 42.13) * mm, "end": v(-24.8, 42.07) * mm});
            skLineSegment(sketch, "E2261", {"start": v(-24.8, 42.07) * mm, "end": v(-24.79, 42.02) * mm});
            skLineSegment(sketch, "E2262", {"start": v(-24.79, 42.02) * mm, "end": v(-24.77, 41.96) * mm});
            skLineSegment(sketch, "E2263", {"start": v(-24.77, 41.96) * mm, "end": v(-24.76, 41.9) * mm});
            skLineSegment(sketch, "E2264", {"start": v(-24.76, 41.9) * mm, "end": v(-24.74, 41.85) * mm});
            skLineSegment(sketch, "E2265", {"start": v(-24.74, 41.85) * mm, "end": v(-24.73, 41.8) * mm});
            skLineSegment(sketch, "E2266", {"start": v(-24.73, 41.8) * mm, "end": v(-24.96, 41.66) * mm});
            skLineSegment(sketch, "E2267", {"start": v(-24.96, 41.66) * mm, "end": v(-25.37, 41.4) * mm});
            skLineSegment(sketch, "E2268", {"start": v(-25.37, 41.4) * mm, "end": v(-25.61, 41.26) * mm});
            skLineSegment(sketch, "E2269", {"start": v(-25.61, 41.26) * mm, "end": v(-25.65, 41.3) * mm});
            skLineSegment(sketch, "E2270", {"start": v(-25.65, 41.3) * mm, "end": v(-25.7, 41.34) * mm});
            skLineSegment(sketch, "E2271", {"start": v(-25.7, 41.34) * mm, "end": v(-25.73, 41.38) * mm});
            skLineSegment(sketch, "E2272", {"start": v(-25.73, 41.38) * mm, "end": v(-25.78, 41.42) * mm});
            skLineSegment(sketch, "E2273", {"start": v(-25.78, 41.42) * mm, "end": v(-25.82, 41.45) * mm});
            skLineSegment(sketch, "E2274", {"start": v(-25.82, 41.45) * mm, "end": v(-25.86, 41.5) * mm});
            skLineSegment(sketch, "E2275", {"start": v(-25.86, 41.5) * mm, "end": v(-25.9, 41.53) * mm});
            skLineSegment(sketch, "E2276", {"start": v(-25.9, 41.53) * mm, "end": v(-25.95, 41.57) * mm});
            skLineSegment(sketch, "E2277", {"start": v(-25.95, 41.57) * mm, "end": v(-26, 41.61) * mm});
            skLineSegment(sketch, "E2278", {"start": v(-26, 41.61) * mm, "end": v(-26.04, 41.66) * mm});
            skLineSegment(sketch, "E2279", {"start": v(-26.04, 41.66) * mm, "end": v(-26.1, 41.7) * mm});
            skLineSegment(sketch, "E2280", {"start": v(-26.1, 41.7) * mm, "end": v(-26.14, 41.74) * mm});
            skLineSegment(sketch, "E2281", {"start": v(-26.14, 41.74) * mm, "end": v(-26.2, 41.78) * mm});
            skLineSegment(sketch, "E2282", {"start": v(-26.2, 41.78) * mm, "end": v(-26.24, 41.82) * mm});
            skLineSegment(sketch, "E2283", {"start": v(-26.24, 41.82) * mm, "end": v(-26.3, 41.87) * mm});
            skLineSegment(sketch, "E2284", {"start": v(-26.3, 41.87) * mm, "end": v(-26.34, 41.9) * mm});
            skLineSegment(sketch, "E2285", {"start": v(-26.34, 41.9) * mm, "end": v(-26.4, 41.95) * mm});
            skLineSegment(sketch, "E2286", {"start": v(-26.4, 41.95) * mm, "end": v(-26.45, 42) * mm});
            skLineSegment(sketch, "E2287", {"start": v(-26.45, 42) * mm, "end": v(-26.5, 42.04) * mm});
            skLineSegment(sketch, "E2288", {"start": v(-26.5, 42.04) * mm, "end": v(-26.56, 42.08) * mm});
            skLineSegment(sketch, "E2289", {"start": v(-26.56, 42.08) * mm, "end": v(-26.62, 42.13) * mm});
            skLineSegment(sketch, "E2290", {"start": v(-26.62, 42.13) * mm, "end": v(-26.67, 42.17) * mm});
            skLineSegment(sketch, "E2291", {"start": v(-26.67, 42.17) * mm, "end": v(-26.73, 42.22) * mm});
            skLineSegment(sketch, "E2292", {"start": v(-26.73, 42.22) * mm, "end": v(-26.8, 42.26) * mm});
            skLineSegment(sketch, "E2293", {"start": v(-26.8, 42.26) * mm, "end": v(-26.85, 42.31) * mm});
            skLineSegment(sketch, "E2294", {"start": v(-26.85, 42.31) * mm, "end": v(-26.91, 42.36) * mm});
            skLineSegment(sketch, "E2295", {"start": v(-26.91, 42.36) * mm, "end": v(-26.98, 42.4) * mm});
            skLineSegment(sketch, "E2296", {"start": v(-26.98, 42.4) * mm, "end": v(-27.04, 42.45) * mm});
            skLineSegment(sketch, "E2297", {"start": v(-27.04, 42.45) * mm, "end": v(-27.1, 42.5) * mm});
            skLineSegment(sketch, "E2298", {"start": v(-27.1, 42.5) * mm, "end": v(-27.17, 42.54) * mm});
            skLineSegment(sketch, "E2299", {"start": v(-27.17, 42.54) * mm, "end": v(-27.23, 42.6) * mm});
            skLineSegment(sketch, "E2300", {"start": v(-27.23, 42.6) * mm, "end": v(-27.3, 42.64) * mm});
            skLineSegment(sketch, "E2301", {"start": v(-27.3, 42.64) * mm, "end": v(-27.37, 42.69) * mm});
            skLineSegment(sketch, "E2302", {"start": v(-27.37, 42.69) * mm, "end": v(-27.43, 42.74) * mm});
            skLineSegment(sketch, "E2303", {"start": v(-27.43, 42.74) * mm, "end": v(-27.5, 42.78) * mm});
            skLineSegment(sketch, "E2304", {"start": v(-27.5, 42.78) * mm, "end": v(-27.57, 42.83) * mm});
            skLineSegment(sketch, "E2305", {"start": v(-27.57, 42.83) * mm, "end": v(-27.65, 42.88) * mm});
            skLineSegment(sketch, "E2306", {"start": v(-27.65, 42.88) * mm, "end": v(-27.72, 42.93) * mm});
            skLineSegment(sketch, "E2307", {"start": v(-27.72, 42.93) * mm, "end": v(-27.8, 42.98) * mm});
            skLineSegment(sketch, "E2308", {"start": v(-27.8, 42.98) * mm, "end": v(-27.86, 43.02) * mm});
            skLineSegment(sketch, "E2309", {"start": v(-27.86, 43.02) * mm, "end": v(-28.66, 42.48) * mm});
            skLineSegment(sketch, "E2310", {"start": v(-28.66, 42.48) * mm, "end": v(-28.65, 42.4) * mm});
            skLineSegment(sketch, "E2311", {"start": v(-28.65, 42.4) * mm, "end": v(-28.64, 42.32) * mm});
            skLineSegment(sketch, "E2312", {"start": v(-28.64, 42.32) * mm, "end": v(-28.62, 42.24) * mm});
            skLineSegment(sketch, "E2313", {"start": v(-28.62, 42.24) * mm, "end": v(-28.6, 42.15) * mm});
            skLineSegment(sketch, "E2314", {"start": v(-28.6, 42.15) * mm, "end": v(-28.59, 42.07) * mm});
            skLineSegment(sketch, "E2315", {"start": v(-28.59, 42.07) * mm, "end": v(-28.57, 41.98) * mm});
            skLineSegment(sketch, "E2316", {"start": v(-28.57, 41.98) * mm, "end": v(-28.55, 41.9) * mm});
            skLineSegment(sketch, "E2317", {"start": v(-28.55, 41.9) * mm, "end": v(-28.53, 41.82) * mm});
            skLineSegment(sketch, "E2318", {"start": v(-28.53, 41.82) * mm, "end": v(-28.52, 41.74) * mm});
            skLineSegment(sketch, "E2319", {"start": v(-28.52, 41.74) * mm, "end": v(-28.5, 41.66) * mm});
            skLineSegment(sketch, "E2320", {"start": v(-28.5, 41.66) * mm, "end": v(-28.48, 41.58) * mm});
            skLineSegment(sketch, "E2321", {"start": v(-28.48, 41.58) * mm, "end": v(-28.46, 41.5) * mm});
            skLineSegment(sketch, "E2322", {"start": v(-28.46, 41.5) * mm, "end": v(-28.44, 41.43) * mm});
            skLineSegment(sketch, "E2323", {"start": v(-28.44, 41.43) * mm, "end": v(-28.43, 41.36) * mm});
            skLineSegment(sketch, "E2324", {"start": v(-28.43, 41.36) * mm, "end": v(-28.4, 41.28) * mm});
            skLineSegment(sketch, "E2325", {"start": v(-28.4, 41.28) * mm, "end": v(-28.39, 41.2) * mm});
            skLineSegment(sketch, "E2326", {"start": v(-28.39, 41.2) * mm, "end": v(-28.37, 41.14) * mm});
            skLineSegment(sketch, "E2327", {"start": v(-28.37, 41.14) * mm, "end": v(-28.35, 41.07) * mm});
            skLineSegment(sketch, "E2328", {"start": v(-28.35, 41.07) * mm, "end": v(-28.33, 41) * mm});
            skLineSegment(sketch, "E2329", {"start": v(-28.33, 41) * mm, "end": v(-28.31, 40.93) * mm});
            skLineSegment(sketch, "E2330", {"start": v(-28.31, 40.93) * mm, "end": v(-28.3, 40.86) * mm});
            skLineSegment(sketch, "E2331", {"start": v(-28.3, 40.86) * mm, "end": v(-28.27, 40.79) * mm});
            skLineSegment(sketch, "E2332", {"start": v(-28.27, 40.79) * mm, "end": v(-28.26, 40.72) * mm});
            skLineSegment(sketch, "E2333", {"start": v(-28.26, 40.72) * mm, "end": v(-28.24, 40.66) * mm});
            skLineSegment(sketch, "E2334", {"start": v(-28.24, 40.66) * mm, "end": v(-28.22, 40.6) * mm});
            skLineSegment(sketch, "E2335", {"start": v(-28.22, 40.6) * mm, "end": v(-28.2, 40.53) * mm});
            skLineSegment(sketch, "E2336", {"start": v(-28.2, 40.53) * mm, "end": v(-28.18, 40.47) * mm});
            skLineSegment(sketch, "E2337", {"start": v(-28.18, 40.47) * mm, "end": v(-28.16, 40.4) * mm});
            skLineSegment(sketch, "E2338", {"start": v(-28.16, 40.4) * mm, "end": v(-28.14, 40.34) * mm});
            skLineSegment(sketch, "E2339", {"start": v(-28.14, 40.34) * mm, "end": v(-28.12, 40.28) * mm});
            skLineSegment(sketch, "E2340", {"start": v(-28.12, 40.28) * mm, "end": v(-28.1, 40.22) * mm});
            skLineSegment(sketch, "E2341", {"start": v(-28.1, 40.22) * mm, "end": v(-28.08, 40.17) * mm});
            skLineSegment(sketch, "E2342", {"start": v(-28.08, 40.17) * mm, "end": v(-28.06, 40.1) * mm});
            skLineSegment(sketch, "E2343", {"start": v(-28.06, 40.1) * mm, "end": v(-28.04, 40.05) * mm});
            skLineSegment(sketch, "E2344", {"start": v(-28.04, 40.05) * mm, "end": v(-28.02, 40) * mm});
            skLineSegment(sketch, "E2345", {"start": v(-28.02, 40) * mm, "end": v(-28, 39.94) * mm});
            skLineSegment(sketch, "E2346", {"start": v(-28, 39.94) * mm, "end": v(-27.99, 39.89) * mm});
            skLineSegment(sketch, "E2347", {"start": v(-27.99, 39.89) * mm, "end": v(-27.97, 39.84) * mm});
            skLineSegment(sketch, "E2348", {"start": v(-27.97, 39.84) * mm, "end": v(-27.95, 39.78) * mm});
            skLineSegment(sketch, "E2349", {"start": v(-27.95, 39.78) * mm, "end": v(-27.93, 39.73) * mm});
            skLineSegment(sketch, "E2350", {"start": v(-27.93, 39.73) * mm, "end": v(-28.15, 39.57) * mm});
            skLineSegment(sketch, "E2351", {"start": v(-28.15, 39.57) * mm, "end": v(-28.54, 39.29) * mm});
            skLineSegment(sketch, "E2352", {"start": v(-28.54, 39.29) * mm, "end": v(-28.77, 39.13) * mm});
            skLineSegment(sketch, "E2353", {"start": v(-28.77, 39.13) * mm, "end": v(-28.82, 39.16) * mm});
            skLineSegment(sketch, "E2354", {"start": v(-28.82, 39.16) * mm, "end": v(-28.86, 39.2) * mm});
            skLineSegment(sketch, "E2355", {"start": v(-28.86, 39.2) * mm, "end": v(-28.9, 39.23) * mm});
            skLineSegment(sketch, "E2356", {"start": v(-28.9, 39.23) * mm, "end": v(-28.95, 39.27) * mm});
            skLineSegment(sketch, "E2357", {"start": v(-28.95, 39.27) * mm, "end": v(-29, 39.3) * mm});
            skLineSegment(sketch, "E2358", {"start": v(-29, 39.3) * mm, "end": v(-29.04, 39.34) * mm});
            skLineSegment(sketch, "E2359", {"start": v(-29.04, 39.34) * mm, "end": v(-29.09, 39.37) * mm});
            skLineSegment(sketch, "E2360", {"start": v(-29.09, 39.37) * mm, "end": v(-29.13, 39.4) * mm});
            skLineSegment(sketch, "E2361", {"start": v(-29.13, 39.4) * mm, "end": v(-29.18, 39.45) * mm});
            skLineSegment(sketch, "E2362", {"start": v(-29.18, 39.45) * mm, "end": v(-29.23, 39.48) * mm});
            skLineSegment(sketch, "E2363", {"start": v(-29.23, 39.48) * mm, "end": v(-29.28, 39.52) * mm});
            skLineSegment(sketch, "E2364", {"start": v(-29.28, 39.52) * mm, "end": v(-29.34, 39.56) * mm});
            skLineSegment(sketch, "E2365", {"start": v(-29.34, 39.56) * mm, "end": v(-29.39, 39.6) * mm});
            skLineSegment(sketch, "E2366", {"start": v(-29.39, 39.6) * mm, "end": v(-29.44, 39.63) * mm});
            skLineSegment(sketch, "E2367", {"start": v(-29.44, 39.63) * mm, "end": v(-29.5, 39.67) * mm});
            skLineSegment(sketch, "E2368", {"start": v(-29.5, 39.67) * mm, "end": v(-29.55, 39.71) * mm});
            skLineSegment(sketch, "E2369", {"start": v(-29.55, 39.71) * mm, "end": v(-29.6, 39.75) * mm});
            skLineSegment(sketch, "E2370", {"start": v(-29.6, 39.75) * mm, "end": v(-29.66, 39.8) * mm});
            skLineSegment(sketch, "E2371", {"start": v(-29.66, 39.8) * mm, "end": v(-29.72, 39.83) * mm});
            skLineSegment(sketch, "E2372", {"start": v(-29.72, 39.83) * mm, "end": v(-29.78, 39.87) * mm});
            skLineSegment(sketch, "E2373", {"start": v(-29.78, 39.87) * mm, "end": v(-29.84, 39.91) * mm});
            skLineSegment(sketch, "E2374", {"start": v(-29.84, 39.91) * mm, "end": v(-29.9, 39.95) * mm});
            skLineSegment(sketch, "E2375", {"start": v(-29.9, 39.95) * mm, "end": v(-29.96, 40) * mm});
            skLineSegment(sketch, "E2376", {"start": v(-29.96, 40) * mm, "end": v(-30.03, 40.03) * mm});
            skLineSegment(sketch, "E2377", {"start": v(-30.03, 40.03) * mm, "end": v(-30.09, 40.07) * mm});
            skLineSegment(sketch, "E2378", {"start": v(-30.09, 40.07) * mm, "end": v(-30.15, 40.11) * mm});
            skLineSegment(sketch, "E2379", {"start": v(-30.15, 40.11) * mm, "end": v(-30.22, 40.16) * mm});
            skLineSegment(sketch, "E2380", {"start": v(-30.22, 40.16) * mm, "end": v(-30.29, 40.2) * mm});
            skLineSegment(sketch, "E2381", {"start": v(-30.29, 40.2) * mm, "end": v(-30.35, 40.24) * mm});
            skLineSegment(sketch, "E2382", {"start": v(-30.35, 40.24) * mm, "end": v(-30.42, 40.28) * mm});
            skLineSegment(sketch, "E2383", {"start": v(-30.42, 40.28) * mm, "end": v(-30.49, 40.32) * mm});
            skLineSegment(sketch, "E2384", {"start": v(-30.49, 40.32) * mm, "end": v(-30.56, 40.37) * mm});
            skLineSegment(sketch, "E2385", {"start": v(-30.56, 40.37) * mm, "end": v(-30.63, 40.4) * mm});
            skLineSegment(sketch, "E2386", {"start": v(-30.63, 40.4) * mm, "end": v(-30.7, 40.45) * mm});
            skLineSegment(sketch, "E2387", {"start": v(-30.7, 40.45) * mm, "end": v(-30.78, 40.5) * mm});
            skLineSegment(sketch, "E2388", {"start": v(-30.78, 40.5) * mm, "end": v(-30.85, 40.54) * mm});
            skLineSegment(sketch, "E2389", {"start": v(-30.85, 40.54) * mm, "end": v(-30.92, 40.58) * mm});
            skLineSegment(sketch, "E2390", {"start": v(-30.92, 40.58) * mm, "end": v(-31, 40.62) * mm});
            skLineSegment(sketch, "E2391", {"start": v(-31, 40.62) * mm, "end": v(-31.08, 40.67) * mm});
            skLineSegment(sketch, "E2392", {"start": v(-31.08, 40.67) * mm, "end": v(-31.15, 40.7) * mm});
            skLineSegment(sketch, "E2393", {"start": v(-31.15, 40.7) * mm, "end": v(-31.9, 40.1) * mm});
            skLineSegment(sketch, "E2394", {"start": v(-31.9, 40.1) * mm, "end": v(-31.9, 40.03) * mm});
            skLineSegment(sketch, "E2395", {"start": v(-31.9, 40.03) * mm, "end": v(-31.87, 39.94) * mm});
            skLineSegment(sketch, "E2396", {"start": v(-31.87, 39.94) * mm, "end": v(-31.85, 39.86) * mm});
            skLineSegment(sketch, "E2397", {"start": v(-31.85, 39.86) * mm, "end": v(-31.82, 39.78) * mm});
            skLineSegment(sketch, "E2398", {"start": v(-31.82, 39.78) * mm, "end": v(-31.8, 39.7) * mm});
            skLineSegment(sketch, "E2399", {"start": v(-31.8, 39.7) * mm, "end": v(-31.78, 39.61) * mm});
            skLineSegment(sketch, "E2400", {"start": v(-31.78, 39.61) * mm, "end": v(-31.75, 39.53) * mm});
            skLineSegment(sketch, "E2401", {"start": v(-31.75, 39.53) * mm, "end": v(-31.73, 39.45) * mm});
            skLineSegment(sketch, "E2402", {"start": v(-31.73, 39.45) * mm, "end": v(-31.7, 39.38) * mm});
            skLineSegment(sketch, "E2403", {"start": v(-31.7, 39.38) * mm, "end": v(-31.68, 39.3) * mm});
            skLineSegment(sketch, "E2404", {"start": v(-31.68, 39.3) * mm, "end": v(-31.66, 39.22) * mm});
            skLineSegment(sketch, "E2405", {"start": v(-31.66, 39.22) * mm, "end": v(-31.63, 39.15) * mm});
            skLineSegment(sketch, "E2406", {"start": v(-31.63, 39.15) * mm, "end": v(-31.6, 39.07) * mm});
            skLineSegment(sketch, "E2407", {"start": v(-31.6, 39.07) * mm, "end": v(-31.58, 39) * mm});
            skLineSegment(sketch, "E2408", {"start": v(-31.58, 39) * mm, "end": v(-31.56, 38.93) * mm});
            skLineSegment(sketch, "E2409", {"start": v(-31.56, 38.93) * mm, "end": v(-31.53, 38.85) * mm});
            skLineSegment(sketch, "E2410", {"start": v(-31.53, 38.85) * mm, "end": v(-31.5, 38.78) * mm});
            skLineSegment(sketch, "E2411", {"start": v(-31.5, 38.78) * mm, "end": v(-31.49, 38.71) * mm});
            skLineSegment(sketch, "E2412", {"start": v(-31.49, 38.71) * mm, "end": v(-31.46, 38.65) * mm});
            skLineSegment(sketch, "E2413", {"start": v(-31.46, 38.65) * mm, "end": v(-31.44, 38.58) * mm});
            skLineSegment(sketch, "E2414", {"start": v(-31.44, 38.58) * mm, "end": v(-31.41, 38.51) * mm});
            skLineSegment(sketch, "E2415", {"start": v(-31.41, 38.51) * mm, "end": v(-31.39, 38.45) * mm});
            skLineSegment(sketch, "E2416", {"start": v(-31.39, 38.45) * mm, "end": v(-31.36, 38.38) * mm});
            skLineSegment(sketch, "E2417", {"start": v(-31.36, 38.38) * mm, "end": v(-31.34, 38.32) * mm});
            skLineSegment(sketch, "E2418", {"start": v(-31.34, 38.32) * mm, "end": v(-31.32, 38.25) * mm});
            skLineSegment(sketch, "E2419", {"start": v(-31.32, 38.25) * mm, "end": v(-31.3, 38.2) * mm});
            skLineSegment(sketch, "E2420", {"start": v(-31.3, 38.2) * mm, "end": v(-31.27, 38.13) * mm});
            skLineSegment(sketch, "E2421", {"start": v(-31.27, 38.13) * mm, "end": v(-31.24, 38.07) * mm});
            skLineSegment(sketch, "E2422", {"start": v(-31.24, 38.07) * mm, "end": v(-31.22, 38.01) * mm});
            skLineSegment(sketch, "E2423", {"start": v(-31.22, 38.01) * mm, "end": v(-31.2, 37.95) * mm});
            skLineSegment(sketch, "E2424", {"start": v(-31.2, 37.95) * mm, "end": v(-31.17, 37.9) * mm});
            skLineSegment(sketch, "E2425", {"start": v(-31.17, 37.9) * mm, "end": v(-31.15, 37.84) * mm});
            skLineSegment(sketch, "E2426", {"start": v(-31.15, 37.84) * mm, "end": v(-31.12, 37.78) * mm});
            skLineSegment(sketch, "E2427", {"start": v(-31.12, 37.78) * mm, "end": v(-31.1, 37.73) * mm});
            skLineSegment(sketch, "E2428", {"start": v(-31.1, 37.73) * mm, "end": v(-31.08, 37.67) * mm});
            skLineSegment(sketch, "E2429", {"start": v(-31.08, 37.67) * mm, "end": v(-31.05, 37.62) * mm});
            skLineSegment(sketch, "E2430", {"start": v(-31.05, 37.62) * mm, "end": v(-31.03, 37.57) * mm});
            skLineSegment(sketch, "E2431", {"start": v(-31.03, 37.57) * mm, "end": v(-31, 37.52) * mm});
            skLineSegment(sketch, "E2432", {"start": v(-31, 37.52) * mm, "end": v(-30.98, 37.47) * mm});
            skLineSegment(sketch, "E2433", {"start": v(-30.98, 37.47) * mm, "end": v(-30.96, 37.42) * mm});
            skLineSegment(sketch, "E2434", {"start": v(-30.96, 37.42) * mm, "end": v(-31.17, 37.24) * mm});
            skLineSegment(sketch, "E2435", {"start": v(-31.17, 37.24) * mm, "end": v(-31.54, 36.93) * mm});
            skLineSegment(sketch, "E2436", {"start": v(-31.54, 36.93) * mm, "end": v(-31.75, 36.75) * mm});
            skLineSegment(sketch, "E2437", {"start": v(-31.75, 36.75) * mm, "end": v(-31.8, 36.78) * mm});
            skLineSegment(sketch, "E2438", {"start": v(-31.8, 36.78) * mm, "end": v(-31.84, 36.81) * mm});
            skLineSegment(sketch, "E2439", {"start": v(-31.84, 36.81) * mm, "end": v(-31.9, 36.84) * mm});
            skLineSegment(sketch, "E2440", {"start": v(-31.9, 36.84) * mm, "end": v(-31.94, 36.87) * mm});
            skLineSegment(sketch, "E2441", {"start": v(-31.94, 36.87) * mm, "end": v(-31.99, 36.9) * mm});
            skLineSegment(sketch, "E2442", {"start": v(-31.99, 36.9) * mm, "end": v(-32.04, 36.94) * mm});
            skLineSegment(sketch, "E2443", {"start": v(-32.04, 36.94) * mm, "end": v(-32.09, 36.97) * mm});
            skLineSegment(sketch, "E2444", {"start": v(-32.09, 36.97) * mm, "end": v(-32.14, 37) * mm});
            skLineSegment(sketch, "E2445", {"start": v(-32.14, 37) * mm, "end": v(-32.19, 37.04) * mm});
            skLineSegment(sketch, "E2446", {"start": v(-32.19, 37.04) * mm, "end": v(-32.24, 37.07) * mm});
            skLineSegment(sketch, "E2447", {"start": v(-32.24, 37.07) * mm, "end": v(-32.3, 37.1) * mm});
            skLineSegment(sketch, "E2448", {"start": v(-32.3, 37.1) * mm, "end": v(-32.35, 37.13) * mm});
            skLineSegment(sketch, "E2449", {"start": v(-32.35, 37.13) * mm, "end": v(-32.4, 37.17) * mm});
            skLineSegment(sketch, "E2450", {"start": v(-32.4, 37.17) * mm, "end": v(-32.46, 37.2) * mm});
            skLineSegment(sketch, "E2451", {"start": v(-32.46, 37.2) * mm, "end": v(-32.52, 37.24) * mm});
            skLineSegment(sketch, "E2452", {"start": v(-32.52, 37.24) * mm, "end": v(-32.58, 37.27) * mm});
            skLineSegment(sketch, "E2453", {"start": v(-32.58, 37.27) * mm, "end": v(-32.63, 37.3) * mm});
            skLineSegment(sketch, "E2454", {"start": v(-32.63, 37.3) * mm, "end": v(-32.7, 37.34) * mm});
            skLineSegment(sketch, "E2455", {"start": v(-32.7, 37.34) * mm, "end": v(-32.76, 37.38) * mm});
            skLineSegment(sketch, "E2456", {"start": v(-32.76, 37.38) * mm, "end": v(-32.82, 37.41) * mm});
            skLineSegment(sketch, "E2457", {"start": v(-32.82, 37.41) * mm, "end": v(-32.88, 37.45) * mm});
            skLineSegment(sketch, "E2458", {"start": v(-32.88, 37.45) * mm, "end": v(-32.94, 37.48) * mm});
            skLineSegment(sketch, "E2459", {"start": v(-32.94, 37.48) * mm, "end": v(-33, 37.52) * mm});
            skLineSegment(sketch, "E2460", {"start": v(-33, 37.52) * mm, "end": v(-33.07, 37.55) * mm});
            skLineSegment(sketch, "E2461", {"start": v(-33.07, 37.55) * mm, "end": v(-33.14, 37.59) * mm});
            skLineSegment(sketch, "E2462", {"start": v(-33.14, 37.59) * mm, "end": v(-33.2, 37.63) * mm});
            skLineSegment(sketch, "E2463", {"start": v(-33.2, 37.63) * mm, "end": v(-33.28, 37.66) * mm});
            skLineSegment(sketch, "E2464", {"start": v(-33.28, 37.66) * mm, "end": v(-33.35, 37.7) * mm});
            skLineSegment(sketch, "E2465", {"start": v(-33.35, 37.7) * mm, "end": v(-33.42, 37.73) * mm});
            skLineSegment(sketch, "E2466", {"start": v(-33.42, 37.73) * mm, "end": v(-33.49, 37.77) * mm});
            skLineSegment(sketch, "E2467", {"start": v(-33.49, 37.77) * mm, "end": v(-33.56, 37.8) * mm});
            skLineSegment(sketch, "E2468", {"start": v(-33.56, 37.8) * mm, "end": v(-33.63, 37.84) * mm});
            skLineSegment(sketch, "E2469", {"start": v(-33.63, 37.84) * mm, "end": v(-33.7, 37.88) * mm});
            skLineSegment(sketch, "E2470", {"start": v(-33.7, 37.88) * mm, "end": v(-33.78, 37.92) * mm});
            skLineSegment(sketch, "E2471", {"start": v(-33.78, 37.92) * mm, "end": v(-33.86, 37.95) * mm});
            skLineSegment(sketch, "E2472", {"start": v(-33.86, 37.95) * mm, "end": v(-33.93, 38) * mm});
            skLineSegment(sketch, "E2473", {"start": v(-33.93, 38) * mm, "end": v(-34.01, 38.03) * mm});
            skLineSegment(sketch, "E2474", {"start": v(-34.01, 38.03) * mm, "end": v(-34.1, 38.07) * mm});
            skLineSegment(sketch, "E2475", {"start": v(-34.1, 38.07) * mm, "end": v(-34.17, 38.1) * mm});
            skLineSegment(sketch, "E2476", {"start": v(-34.17, 38.1) * mm, "end": v(-34.24, 38.13) * mm});
            skLineSegment(sketch, "E2477", {"start": v(-34.24, 38.13) * mm, "end": v(-34.96, 37.48) * mm});
            skLineSegment(sketch, "E2478", {"start": v(-34.96, 37.48) * mm, "end": v(-34.94, 37.4) * mm});
            skLineSegment(sketch, "E2479", {"start": v(-34.94, 37.4) * mm, "end": v(-34.9, 37.32) * mm});
            skLineSegment(sketch, "E2480", {"start": v(-34.9, 37.32) * mm, "end": v(-34.88, 37.24) * mm});
            skLineSegment(sketch, "E2481", {"start": v(-34.88, 37.24) * mm, "end": v(-34.85, 37.16) * mm});
            skLineSegment(sketch, "E2482", {"start": v(-34.85, 37.16) * mm, "end": v(-34.82, 37.08) * mm});
            skLineSegment(sketch, "E2483", {"start": v(-34.82, 37.08) * mm, "end": v(-34.79, 37) * mm});
            skLineSegment(sketch, "E2484", {"start": v(-34.79, 37) * mm, "end": v(-34.76, 36.92) * mm});
            skLineSegment(sketch, "E2485", {"start": v(-34.76, 36.92) * mm, "end": v(-34.73, 36.84) * mm});
            skLineSegment(sketch, "E2486", {"start": v(-34.73, 36.84) * mm, "end": v(-34.7, 36.77) * mm});
            skLineSegment(sketch, "E2487", {"start": v(-34.7, 36.77) * mm, "end": v(-34.67, 36.7) * mm});
            skLineSegment(sketch, "E2488", {"start": v(-34.67, 36.7) * mm, "end": v(-34.64, 36.62) * mm});
            skLineSegment(sketch, "E2489", {"start": v(-34.64, 36.62) * mm, "end": v(-34.6, 36.54) * mm});
            skLineSegment(sketch, "E2490", {"start": v(-34.6, 36.54) * mm, "end": v(-34.58, 36.47) * mm});
            skLineSegment(sketch, "E2491", {"start": v(-34.58, 36.47) * mm, "end": v(-34.55, 36.4) * mm});
            skLineSegment(sketch, "E2492", {"start": v(-34.55, 36.4) * mm, "end": v(-34.52, 36.33) * mm});
            skLineSegment(sketch, "E2493", {"start": v(-34.52, 36.33) * mm, "end": v(-34.49, 36.26) * mm});
            skLineSegment(sketch, "E2494", {"start": v(-34.49, 36.26) * mm, "end": v(-34.46, 36.2) * mm});
            skLineSegment(sketch, "E2495", {"start": v(-34.46, 36.2) * mm, "end": v(-34.43, 36.12) * mm});
            skLineSegment(sketch, "E2496", {"start": v(-34.43, 36.12) * mm, "end": v(-34.4, 36.06) * mm});
            skLineSegment(sketch, "E2497", {"start": v(-34.4, 36.06) * mm, "end": v(-34.37, 36) * mm});
            skLineSegment(sketch, "E2498", {"start": v(-34.37, 36) * mm, "end": v(-34.34, 35.93) * mm});
            skLineSegment(sketch, "E2499", {"start": v(-34.34, 35.93) * mm, "end": v(-34.3, 35.86) * mm});
            skLineSegment(sketch, "E2500", {"start": v(-34.3, 35.86) * mm, "end": v(-34.28, 35.8) * mm});
            skLineSegment(sketch, "E2501", {"start": v(-34.28, 35.8) * mm, "end": v(-34.25, 35.74) * mm});
            skLineSegment(sketch, "E2502", {"start": v(-34.25, 35.74) * mm, "end": v(-34.22, 35.68) * mm});
            skLineSegment(sketch, "E2503", {"start": v(-34.22, 35.68) * mm, "end": v(-34.2, 35.62) * mm});
            skLineSegment(sketch, "E2504", {"start": v(-34.2, 35.62) * mm, "end": v(-34.16, 35.56) * mm});
            skLineSegment(sketch, "E2505", {"start": v(-34.16, 35.56) * mm, "end": v(-34.13, 35.5) * mm});
            skLineSegment(sketch, "E2506", {"start": v(-34.13, 35.5) * mm, "end": v(-34.1, 35.44) * mm});
            skLineSegment(sketch, "E2507", {"start": v(-34.1, 35.44) * mm, "end": v(-34.08, 35.39) * mm});
            skLineSegment(sketch, "E2508", {"start": v(-34.08, 35.39) * mm, "end": v(-34.05, 35.33) * mm});
            skLineSegment(sketch, "E2509", {"start": v(-34.05, 35.33) * mm, "end": v(-34.02, 35.28) * mm});
            skLineSegment(sketch, "E2510", {"start": v(-34.02, 35.28) * mm, "end": v(-34, 35.22) * mm});
            skLineSegment(sketch, "E2511", {"start": v(-34, 35.22) * mm, "end": v(-33.96, 35.17) * mm});
            skLineSegment(sketch, "E2512", {"start": v(-33.96, 35.17) * mm, "end": v(-33.94, 35.12) * mm});
            skLineSegment(sketch, "E2513", {"start": v(-33.94, 35.12) * mm, "end": v(-33.9, 35.07) * mm});
            skLineSegment(sketch, "E2514", {"start": v(-33.9, 35.07) * mm, "end": v(-33.88, 35.02) * mm});
            skLineSegment(sketch, "E2515", {"start": v(-33.88, 35.02) * mm, "end": v(-33.86, 34.97) * mm});
            skLineSegment(sketch, "E2516", {"start": v(-33.86, 34.97) * mm, "end": v(-33.83, 34.92) * mm});
            skLineSegment(sketch, "E2517", {"start": v(-33.83, 34.92) * mm, "end": v(-33.8, 34.88) * mm});
            skLineSegment(sketch, "E2518", {"start": v(-33.8, 34.88) * mm, "end": v(-34, 34.68) * mm});
            skLineSegment(sketch, "E2519", {"start": v(-34, 34.68) * mm, "end": v(-34.34, 34.34) * mm});
            skLineSegment(sketch, "E2520", {"start": v(-34.34, 34.34) * mm, "end": v(-34.54, 34.14) * mm});
            skLineSegment(sketch, "E2521", {"start": v(-34.54, 34.14) * mm, "end": v(-34.59, 34.17) * mm});
            skLineSegment(sketch, "E2522", {"start": v(-34.59, 34.17) * mm, "end": v(-34.63, 34.2) * mm});
            skLineSegment(sketch, "E2523", {"start": v(-34.63, 34.2) * mm, "end": v(-34.68, 34.23) * mm});
            skLineSegment(sketch, "E2524", {"start": v(-34.68, 34.23) * mm, "end": v(-34.73, 34.25) * mm});
            skLineSegment(sketch, "E2525", {"start": v(-34.73, 34.25) * mm, "end": v(-34.78, 34.28) * mm});
            skLineSegment(sketch, "E2526", {"start": v(-34.78, 34.28) * mm, "end": v(-34.83, 34.31) * mm});
            skLineSegment(sketch, "E2527", {"start": v(-34.83, 34.31) * mm, "end": v(-34.89, 34.34) * mm});
            skLineSegment(sketch, "E2528", {"start": v(-34.89, 34.34) * mm, "end": v(-34.94, 34.37) * mm});
            skLineSegment(sketch, "E2529", {"start": v(-34.94, 34.37) * mm, "end": v(-35, 34.4) * mm});
            skLineSegment(sketch, "E2530", {"start": v(-35, 34.4) * mm, "end": v(-35.05, 34.42) * mm});
            skLineSegment(sketch, "E2531", {"start": v(-35.05, 34.42) * mm, "end": v(-35.1, 34.45) * mm});
            skLineSegment(sketch, "E2532", {"start": v(-35.1, 34.45) * mm, "end": v(-35.16, 34.48) * mm});
            skLineSegment(sketch, "E2533", {"start": v(-35.16, 34.48) * mm, "end": v(-35.22, 34.51) * mm});
            skLineSegment(sketch, "E2534", {"start": v(-35.22, 34.51) * mm, "end": v(-35.28, 34.54) * mm});
            skLineSegment(sketch, "E2535", {"start": v(-35.28, 34.54) * mm, "end": v(-35.34, 34.57) * mm});
            skLineSegment(sketch, "E2536", {"start": v(-35.34, 34.57) * mm, "end": v(-35.4, 34.6) * mm});
            skLineSegment(sketch, "E2537", {"start": v(-35.4, 34.6) * mm, "end": v(-35.46, 34.63) * mm});
            skLineSegment(sketch, "E2538", {"start": v(-35.46, 34.63) * mm, "end": v(-35.52, 34.66) * mm});
            skLineSegment(sketch, "E2539", {"start": v(-35.52, 34.66) * mm, "end": v(-35.59, 34.7) * mm});
            skLineSegment(sketch, "E2540", {"start": v(-35.59, 34.7) * mm, "end": v(-35.65, 34.72) * mm});
            skLineSegment(sketch, "E2541", {"start": v(-35.65, 34.72) * mm, "end": v(-35.72, 34.75) * mm});
            skLineSegment(sketch, "E2542", {"start": v(-35.72, 34.75) * mm, "end": v(-35.78, 34.78) * mm});
            skLineSegment(sketch, "E2543", {"start": v(-35.78, 34.78) * mm, "end": v(-35.85, 34.81) * mm});
            skLineSegment(sketch, "E2544", {"start": v(-35.85, 34.81) * mm, "end": v(-35.92, 34.84) * mm});
            skLineSegment(sketch, "E2545", {"start": v(-35.92, 34.84) * mm, "end": v(-35.99, 34.87) * mm});
            skLineSegment(sketch, "E2546", {"start": v(-35.99, 34.87) * mm, "end": v(-36.06, 34.9) * mm});
            skLineSegment(sketch, "E2547", {"start": v(-36.06, 34.9) * mm, "end": v(-36.13, 34.93) * mm});
            skLineSegment(sketch, "E2548", {"start": v(-36.13, 34.93) * mm, "end": v(-36.2, 34.97) * mm});
            skLineSegment(sketch, "E2549", {"start": v(-36.2, 34.97) * mm, "end": v(-36.27, 35) * mm});
            skLineSegment(sketch, "E2550", {"start": v(-36.27, 35) * mm, "end": v(-36.35, 35.03) * mm});
            skLineSegment(sketch, "E2551", {"start": v(-36.35, 35.03) * mm, "end": v(-36.42, 35.06) * mm});
            skLineSegment(sketch, "E2552", {"start": v(-36.42, 35.06) * mm, "end": v(-36.5, 35.09) * mm});
            skLineSegment(sketch, "E2553", {"start": v(-36.5, 35.09) * mm, "end": v(-36.57, 35.12) * mm});
            skLineSegment(sketch, "E2554", {"start": v(-36.57, 35.12) * mm, "end": v(-36.65, 35.15) * mm});
            skLineSegment(sketch, "E2555", {"start": v(-36.65, 35.15) * mm, "end": v(-36.73, 35.18) * mm});
            skLineSegment(sketch, "E2556", {"start": v(-36.73, 35.18) * mm, "end": v(-36.81, 35.21) * mm});
            skLineSegment(sketch, "E2557", {"start": v(-36.81, 35.21) * mm, "end": v(-36.9, 35.24) * mm});
            skLineSegment(sketch, "E2558", {"start": v(-36.9, 35.24) * mm, "end": v(-36.97, 35.27) * mm});
            skLineSegment(sketch, "E2559", {"start": v(-36.97, 35.27) * mm, "end": v(-37.06, 35.3) * mm});
            skLineSegment(sketch, "E2560", {"start": v(-37.06, 35.3) * mm, "end": v(-37.13, 35.33) * mm});
            skLineSegment(sketch, "E2561", {"start": v(-37.13, 35.33) * mm, "end": v(-37.79, 34.62) * mm});
            skLineSegment(sketch, "E2562", {"start": v(-37.79, 34.62) * mm, "end": v(-37.76, 34.55) * mm});
            skLineSegment(sketch, "E2563", {"start": v(-37.76, 34.55) * mm, "end": v(-37.73, 34.47) * mm});
            skLineSegment(sketch, "E2564", {"start": v(-37.73, 34.47) * mm, "end": v(-37.7, 34.39) * mm});
            skLineSegment(sketch, "E2565", {"start": v(-37.7, 34.39) * mm, "end": v(-37.65, 34.3) * mm});
            skLineSegment(sketch, "E2566", {"start": v(-37.65, 34.3) * mm, "end": v(-37.62, 34.23) * mm});
            skLineSegment(sketch, "E2567", {"start": v(-37.62, 34.23) * mm, "end": v(-37.58, 34.15) * mm});
            skLineSegment(sketch, "E2568", {"start": v(-37.58, 34.15) * mm, "end": v(-37.55, 34.08) * mm});
            skLineSegment(sketch, "E2569", {"start": v(-37.55, 34.08) * mm, "end": v(-37.5, 34) * mm});
            skLineSegment(sketch, "E2570", {"start": v(-37.5, 34) * mm, "end": v(-37.47, 33.93) * mm});
            skLineSegment(sketch, "E2571", {"start": v(-37.47, 33.93) * mm, "end": v(-37.44, 33.86) * mm});
            skLineSegment(sketch, "E2572", {"start": v(-37.44, 33.86) * mm, "end": v(-37.4, 33.79) * mm});
            skLineSegment(sketch, "E2573", {"start": v(-37.4, 33.79) * mm, "end": v(-37.37, 33.72) * mm});
            skLineSegment(sketch, "E2574", {"start": v(-37.37, 33.72) * mm, "end": v(-37.33, 33.65) * mm});
            skLineSegment(sketch, "E2575", {"start": v(-37.33, 33.65) * mm, "end": v(-37.3, 33.58) * mm});
            skLineSegment(sketch, "E2576", {"start": v(-37.3, 33.58) * mm, "end": v(-37.26, 33.51) * mm});
            skLineSegment(sketch, "E2577", {"start": v(-37.26, 33.51) * mm, "end": v(-37.22, 33.44) * mm});
            skLineSegment(sketch, "E2578", {"start": v(-37.22, 33.44) * mm, "end": v(-37.19, 33.38) * mm});
            skLineSegment(sketch, "E2579", {"start": v(-37.19, 33.38) * mm, "end": v(-37.15, 33.31) * mm});
            skLineSegment(sketch, "E2580", {"start": v(-37.15, 33.31) * mm, "end": v(-37.12, 33.25) * mm});
            skLineSegment(sketch, "E2581", {"start": v(-37.12, 33.25) * mm, "end": v(-37.08, 33.19) * mm});
            skLineSegment(sketch, "E2582", {"start": v(-37.08, 33.19) * mm, "end": v(-37.05, 33.12) * mm});
            skLineSegment(sketch, "E2583", {"start": v(-37.05, 33.12) * mm, "end": v(-37.02, 33.06) * mm});
            skLineSegment(sketch, "E2584", {"start": v(-37.02, 33.06) * mm, "end": v(-36.98, 33) * mm});
            skLineSegment(sketch, "E2585", {"start": v(-36.98, 33) * mm, "end": v(-36.95, 32.94) * mm});
            skLineSegment(sketch, "E2586", {"start": v(-36.95, 32.94) * mm, "end": v(-36.91, 32.88) * mm});
            skLineSegment(sketch, "E2587", {"start": v(-36.91, 32.88) * mm, "end": v(-36.88, 32.83) * mm});
            skLineSegment(sketch, "E2588", {"start": v(-36.88, 32.83) * mm, "end": v(-36.85, 32.77) * mm});
            skLineSegment(sketch, "E2589", {"start": v(-36.85, 32.77) * mm, "end": v(-36.81, 32.71) * mm});
            skLineSegment(sketch, "E2590", {"start": v(-36.81, 32.71) * mm, "end": v(-36.78, 32.66) * mm});
            skLineSegment(sketch, "E2591", {"start": v(-36.78, 32.66) * mm, "end": v(-36.75, 32.6) * mm});
            skLineSegment(sketch, "E2592", {"start": v(-36.75, 32.6) * mm, "end": v(-36.72, 32.55) * mm});
            skLineSegment(sketch, "E2593", {"start": v(-36.72, 32.55) * mm, "end": v(-36.68, 32.5) * mm});
            skLineSegment(sketch, "E2594", {"start": v(-36.68, 32.5) * mm, "end": v(-36.65, 32.45) * mm});
            skLineSegment(sketch, "E2595", {"start": v(-36.65, 32.45) * mm, "end": v(-36.62, 32.4) * mm});
            skLineSegment(sketch, "E2596", {"start": v(-36.62, 32.4) * mm, "end": v(-36.59, 32.35) * mm});
            skLineSegment(sketch, "E2597", {"start": v(-36.59, 32.35) * mm, "end": v(-36.56, 32.3) * mm});
            skLineSegment(sketch, "E2598", {"start": v(-36.56, 32.3) * mm, "end": v(-36.53, 32.25) * mm});
            skLineSegment(sketch, "E2599", {"start": v(-36.53, 32.25) * mm, "end": v(-36.5, 32.2) * mm});
            skLineSegment(sketch, "E2600", {"start": v(-36.5, 32.2) * mm, "end": v(-36.46, 32.16) * mm});
            skLineSegment(sketch, "E2601", {"start": v(-36.46, 32.16) * mm, "end": v(-36.43, 32.12) * mm});
            skLineSegment(sketch, "E2602", {"start": v(-36.43, 32.12) * mm, "end": v(-36.61, 31.9) * mm});
            skLineSegment(sketch, "E2603", {"start": v(-36.61, 31.9) * mm, "end": v(-36.93, 31.54) * mm});
            skLineSegment(sketch, "E2604", {"start": v(-36.93, 31.54) * mm, "end": v(-37.11, 31.33) * mm});
            skLineSegment(sketch, "E2605", {"start": v(-37.11, 31.33) * mm, "end": v(-37.16, 31.35) * mm});
            skLineSegment(sketch, "E2606", {"start": v(-37.16, 31.35) * mm, "end": v(-37.21, 31.38) * mm});
            skLineSegment(sketch, "E2607", {"start": v(-37.21, 31.38) * mm, "end": v(-37.26, 31.4) * mm});
            skLineSegment(sketch, "E2608", {"start": v(-37.26, 31.4) * mm, "end": v(-37.31, 31.42) * mm});
            skLineSegment(sketch, "E2609", {"start": v(-37.31, 31.42) * mm, "end": v(-37.37, 31.45) * mm});
            skLineSegment(sketch, "E2610", {"start": v(-37.37, 31.45) * mm, "end": v(-37.42, 31.47) * mm});
            skLineSegment(sketch, "E2611", {"start": v(-37.42, 31.47) * mm, "end": v(-37.47, 31.5) * mm});
            skLineSegment(sketch, "E2612", {"start": v(-37.47, 31.5) * mm, "end": v(-37.53, 31.52) * mm});
            skLineSegment(sketch, "E2613", {"start": v(-37.53, 31.52) * mm, "end": v(-37.59, 31.54) * mm});
            skLineSegment(sketch, "E2614", {"start": v(-37.59, 31.54) * mm, "end": v(-37.64, 31.57) * mm});
            skLineSegment(sketch, "E2615", {"start": v(-37.64, 31.57) * mm, "end": v(-37.7, 31.6) * mm});
            skLineSegment(sketch, "E2616", {"start": v(-37.7, 31.6) * mm, "end": v(-37.76, 31.62) * mm});
            skLineSegment(sketch, "E2617", {"start": v(-37.76, 31.62) * mm, "end": v(-37.82, 31.64) * mm});
            skLineSegment(sketch, "E2618", {"start": v(-37.82, 31.64) * mm, "end": v(-37.88, 31.67) * mm});
            skLineSegment(sketch, "E2619", {"start": v(-37.88, 31.67) * mm, "end": v(-37.94, 31.7) * mm});
            skLineSegment(sketch, "E2620", {"start": v(-37.94, 31.7) * mm, "end": v(-38, 31.72) * mm});
            skLineSegment(sketch, "E2621", {"start": v(-38, 31.72) * mm, "end": v(-38.07, 31.74) * mm});
            skLineSegment(sketch, "E2622", {"start": v(-38.07, 31.74) * mm, "end": v(-38.13, 31.77) * mm});
            skLineSegment(sketch, "E2623", {"start": v(-38.13, 31.77) * mm, "end": v(-38.2, 31.8) * mm});
            skLineSegment(sketch, "E2624", {"start": v(-38.2, 31.8) * mm, "end": v(-38.27, 31.82) * mm});
            skLineSegment(sketch, "E2625", {"start": v(-38.27, 31.82) * mm, "end": v(-38.33, 31.84) * mm});
            skLineSegment(sketch, "E2626", {"start": v(-38.33, 31.84) * mm, "end": v(-38.4, 31.87) * mm});
            skLineSegment(sketch, "E2627", {"start": v(-38.4, 31.87) * mm, "end": v(-38.47, 31.9) * mm});
            skLineSegment(sketch, "E2628", {"start": v(-38.47, 31.9) * mm, "end": v(-38.54, 31.92) * mm});
            skLineSegment(sketch, "E2629", {"start": v(-38.54, 31.92) * mm, "end": v(-38.61, 31.94) * mm});
            skLineSegment(sketch, "E2630", {"start": v(-38.61, 31.94) * mm, "end": v(-38.68, 31.97) * mm});
            skLineSegment(sketch, "E2631", {"start": v(-38.68, 31.97) * mm, "end": v(-38.76, 32) * mm});
            skLineSegment(sketch, "E2632", {"start": v(-38.76, 32) * mm, "end": v(-38.83, 32.02) * mm});
            skLineSegment(sketch, "E2633", {"start": v(-38.83, 32.02) * mm, "end": v(-38.9, 32.04) * mm});
            skLineSegment(sketch, "E2634", {"start": v(-38.9, 32.04) * mm, "end": v(-38.98, 32.07) * mm});
            skLineSegment(sketch, "E2635", {"start": v(-38.98, 32.07) * mm, "end": v(-39.06, 32.1) * mm});
            skLineSegment(sketch, "E2636", {"start": v(-39.06, 32.1) * mm, "end": v(-39.14, 32.12) * mm});
            skLineSegment(sketch, "E2637", {"start": v(-39.14, 32.12) * mm, "end": v(-39.22, 32.14) * mm});
            skLineSegment(sketch, "E2638", {"start": v(-39.22, 32.14) * mm, "end": v(-39.3, 32.17) * mm});
            skLineSegment(sketch, "E2639", {"start": v(-39.3, 32.17) * mm, "end": v(-39.38, 32.2) * mm});
            skLineSegment(sketch, "E2640", {"start": v(-39.38, 32.2) * mm, "end": v(-39.46, 32.21) * mm});
            skLineSegment(sketch, "E2641", {"start": v(-39.46, 32.21) * mm, "end": v(-39.54, 32.24) * mm});
            skLineSegment(sketch, "E2642", {"start": v(-39.54, 32.24) * mm, "end": v(-39.63, 32.26) * mm});
            skLineSegment(sketch, "E2643", {"start": v(-39.63, 32.26) * mm, "end": v(-39.71, 32.29) * mm});
            skLineSegment(sketch, "E2644", {"start": v(-39.71, 32.29) * mm, "end": v(-39.79, 32.3) * mm});
            skLineSegment(sketch, "E2645", {"start": v(-39.79, 32.3) * mm, "end": v(-40.39, 31.55) * mm});
            skLineSegment(sketch, "E2646", {"start": v(-40.39, 31.55) * mm, "end": v(-40.36, 31.48) * mm});
            skLineSegment(sketch, "E2647", {"start": v(-40.36, 31.48) * mm, "end": v(-40.31, 31.4) * mm});
            skLineSegment(sketch, "E2648", {"start": v(-40.31, 31.4) * mm, "end": v(-40.27, 31.32) * mm});
            skLineSegment(sketch, "E2649", {"start": v(-40.27, 31.32) * mm, "end": v(-40.23, 31.25) * mm});
            skLineSegment(sketch, "E2650", {"start": v(-40.23, 31.25) * mm, "end": v(-40.19, 31.17) * mm});
            skLineSegment(sketch, "E2651", {"start": v(-40.19, 31.17) * mm, "end": v(-40.15, 31.1) * mm});
            skLineSegment(sketch, "E2652", {"start": v(-40.15, 31.1) * mm, "end": v(-40.1, 31.03) * mm});
            skLineSegment(sketch, "E2653", {"start": v(-40.1, 31.03) * mm, "end": v(-40.06, 30.96) * mm});
            skLineSegment(sketch, "E2654", {"start": v(-40.06, 30.96) * mm, "end": v(-40.02, 30.89) * mm});
            skLineSegment(sketch, "E2655", {"start": v(-40.02, 30.89) * mm, "end": v(-39.98, 30.82) * mm});
            skLineSegment(sketch, "E2656", {"start": v(-39.98, 30.82) * mm, "end": v(-39.94, 30.75) * mm});
            skLineSegment(sketch, "E2657", {"start": v(-39.94, 30.75) * mm, "end": v(-39.9, 30.68) * mm});
            skLineSegment(sketch, "E2658", {"start": v(-39.9, 30.68) * mm, "end": v(-39.86, 30.61) * mm});
            skLineSegment(sketch, "E2659", {"start": v(-39.86, 30.61) * mm, "end": v(-39.81, 30.55) * mm});
            skLineSegment(sketch, "E2660", {"start": v(-39.81, 30.55) * mm, "end": v(-39.77, 30.48) * mm});
            skLineSegment(sketch, "E2661", {"start": v(-39.77, 30.48) * mm, "end": v(-39.73, 30.42) * mm});
            skLineSegment(sketch, "E2662", {"start": v(-39.73, 30.42) * mm, "end": v(-39.7, 30.36) * mm});
            skLineSegment(sketch, "E2663", {"start": v(-39.7, 30.36) * mm, "end": v(-39.65, 30.3) * mm});
            skLineSegment(sketch, "E2664", {"start": v(-39.65, 30.3) * mm, "end": v(-39.61, 30.23) * mm});
            skLineSegment(sketch, "E2665", {"start": v(-39.61, 30.23) * mm, "end": v(-39.57, 30.17) * mm});
            skLineSegment(sketch, "E2666", {"start": v(-39.57, 30.17) * mm, "end": v(-39.53, 30.11) * mm});
            skLineSegment(sketch, "E2667", {"start": v(-39.53, 30.11) * mm, "end": v(-39.5, 30.06) * mm});
            skLineSegment(sketch, "E2668", {"start": v(-39.5, 30.06) * mm, "end": v(-39.46, 30) * mm});
            skLineSegment(sketch, "E2669", {"start": v(-39.46, 30) * mm, "end": v(-39.42, 29.94) * mm});
            skLineSegment(sketch, "E2670", {"start": v(-39.42, 29.94) * mm, "end": v(-39.38, 29.89) * mm});
            skLineSegment(sketch, "E2671", {"start": v(-39.38, 29.89) * mm, "end": v(-39.34, 29.83) * mm});
            skLineSegment(sketch, "E2672", {"start": v(-39.34, 29.83) * mm, "end": v(-39.3, 29.78) * mm});
            skLineSegment(sketch, "E2673", {"start": v(-39.3, 29.78) * mm, "end": v(-39.27, 29.72) * mm});
            skLineSegment(sketch, "E2674", {"start": v(-39.27, 29.72) * mm, "end": v(-39.23, 29.67) * mm});
            skLineSegment(sketch, "E2675", {"start": v(-39.23, 29.67) * mm, "end": v(-39.2, 29.62) * mm});
            skLineSegment(sketch, "E2676", {"start": v(-39.2, 29.62) * mm, "end": v(-39.16, 29.57) * mm});
            skLineSegment(sketch, "E2677", {"start": v(-39.16, 29.57) * mm, "end": v(-39.12, 29.52) * mm});
            skLineSegment(sketch, "E2678", {"start": v(-39.12, 29.52) * mm, "end": v(-39.08, 29.47) * mm});
            skLineSegment(sketch, "E2679", {"start": v(-39.08, 29.47) * mm, "end": v(-39.05, 29.43) * mm});
            skLineSegment(sketch, "E2680", {"start": v(-39.05, 29.43) * mm, "end": v(-39.01, 29.38) * mm});
            skLineSegment(sketch, "E2681", {"start": v(-39.01, 29.38) * mm, "end": v(-38.98, 29.33) * mm});
            skLineSegment(sketch, "E2682", {"start": v(-38.98, 29.33) * mm, "end": v(-38.94, 29.29) * mm});
            skLineSegment(sketch, "E2683", {"start": v(-38.94, 29.29) * mm, "end": v(-38.9, 29.24) * mm});
            skLineSegment(sketch, "E2684", {"start": v(-38.9, 29.24) * mm, "end": v(-38.88, 29.2) * mm});
            skLineSegment(sketch, "E2685", {"start": v(-38.88, 29.2) * mm, "end": v(-38.84, 29.16) * mm});
            skLineSegment(sketch, "E2686", {"start": v(-38.84, 29.16) * mm, "end": v(-39, 28.93) * mm});
            skLineSegment(sketch, "E2687", {"start": v(-39, 28.93) * mm, "end": v(-39.29, 28.54) * mm});
            skLineSegment(sketch, "E2688", {"start": v(-39.29, 28.54) * mm, "end": v(-39.46, 28.32) * mm});
            skLineSegment(sketch, "E2689", {"start": v(-39.46, 28.32) * mm, "end": v(-39.5, 28.34) * mm});
            skLineSegment(sketch, "E2690", {"start": v(-39.5, 28.34) * mm, "end": v(-39.56, 28.36) * mm});
            skLineSegment(sketch, "E2691", {"start": v(-39.56, 28.36) * mm, "end": v(-39.61, 28.38) * mm});
            skLineSegment(sketch, "E2692", {"start": v(-39.61, 28.38) * mm, "end": v(-39.66, 28.4) * mm});
            skLineSegment(sketch, "E2693", {"start": v(-39.66, 28.4) * mm, "end": v(-39.72, 28.42) * mm});
            skLineSegment(sketch, "E2694", {"start": v(-39.72, 28.42) * mm, "end": v(-39.77, 28.44) * mm});
            skLineSegment(sketch, "E2695", {"start": v(-39.77, 28.44) * mm, "end": v(-39.83, 28.46) * mm});
            skLineSegment(sketch, "E2696", {"start": v(-39.83, 28.46) * mm, "end": v(-39.89, 28.48) * mm});
            skLineSegment(sketch, "E2697", {"start": v(-39.89, 28.48) * mm, "end": v(-39.94, 28.5) * mm});
            skLineSegment(sketch, "E2698", {"start": v(-39.94, 28.5) * mm, "end": v(-40, 28.52) * mm});
            skLineSegment(sketch, "E2699", {"start": v(-40, 28.52) * mm, "end": v(-40.06, 28.54) * mm});
            skLineSegment(sketch, "E2700", {"start": v(-40.06, 28.54) * mm, "end": v(-40.12, 28.56) * mm});
            skLineSegment(sketch, "E2701", {"start": v(-40.12, 28.56) * mm, "end": v(-40.19, 28.58) * mm});
            skLineSegment(sketch, "E2702", {"start": v(-40.19, 28.58) * mm, "end": v(-40.25, 28.6) * mm});
            skLineSegment(sketch, "E2703", {"start": v(-40.25, 28.6) * mm, "end": v(-40.31, 28.62) * mm});
            skLineSegment(sketch, "E2704", {"start": v(-40.31, 28.62) * mm, "end": v(-40.38, 28.64) * mm});
            skLineSegment(sketch, "E2705", {"start": v(-40.38, 28.64) * mm, "end": v(-40.44, 28.66) * mm});
            skLineSegment(sketch, "E2706", {"start": v(-40.44, 28.66) * mm, "end": v(-40.5, 28.68) * mm});
            skLineSegment(sketch, "E2707", {"start": v(-40.5, 28.68) * mm, "end": v(-40.58, 28.7) * mm});
            skLineSegment(sketch, "E2708", {"start": v(-40.58, 28.7) * mm, "end": v(-40.64, 28.72) * mm});
            skLineSegment(sketch, "E2709", {"start": v(-40.64, 28.72) * mm, "end": v(-40.71, 28.74) * mm});
            skLineSegment(sketch, "E2710", {"start": v(-40.71, 28.74) * mm, "end": v(-40.78, 28.76) * mm});
            skLineSegment(sketch, "E2711", {"start": v(-40.78, 28.76) * mm, "end": v(-40.85, 28.78) * mm});
            skLineSegment(sketch, "E2712", {"start": v(-40.85, 28.78) * mm, "end": v(-40.93, 28.8) * mm});
            skLineSegment(sketch, "E2713", {"start": v(-40.93, 28.8) * mm, "end": v(-41, 28.81) * mm});
            skLineSegment(sketch, "E2714", {"start": v(-41, 28.81) * mm, "end": v(-41.07, 28.83) * mm});
            skLineSegment(sketch, "E2715", {"start": v(-41.07, 28.83) * mm, "end": v(-41.15, 28.85) * mm});
            skLineSegment(sketch, "E2716", {"start": v(-41.15, 28.85) * mm, "end": v(-41.22, 28.87) * mm});
            skLineSegment(sketch, "E2717", {"start": v(-41.22, 28.87) * mm, "end": v(-41.3, 28.9) * mm});
            skLineSegment(sketch, "E2718", {"start": v(-41.3, 28.9) * mm, "end": v(-41.38, 28.9) * mm});
            skLineSegment(sketch, "E2719", {"start": v(-41.38, 28.9) * mm, "end": v(-41.46, 28.93) * mm});
            skLineSegment(sketch, "E2720", {"start": v(-41.46, 28.93) * mm, "end": v(-41.54, 28.95) * mm});
            skLineSegment(sketch, "E2721", {"start": v(-41.54, 28.95) * mm, "end": v(-41.62, 28.97) * mm});
            skLineSegment(sketch, "E2722", {"start": v(-41.62, 28.97) * mm, "end": v(-41.7, 28.98) * mm});
            skLineSegment(sketch, "E2723", {"start": v(-41.7, 28.98) * mm, "end": v(-41.78, 29) * mm});
            skLineSegment(sketch, "E2724", {"start": v(-41.78, 29) * mm, "end": v(-41.87, 29.02) * mm});
            skLineSegment(sketch, "E2725", {"start": v(-41.87, 29.02) * mm, "end": v(-41.95, 29.04) * mm});
            skLineSegment(sketch, "E2726", {"start": v(-41.95, 29.04) * mm, "end": v(-42.04, 29.05) * mm});
            skLineSegment(sketch, "E2727", {"start": v(-42.04, 29.05) * mm, "end": v(-42.12, 29.07) * mm});
            skLineSegment(sketch, "E2728", {"start": v(-42.12, 29.07) * mm, "end": v(-42.2, 29.08) * mm});
            skLineSegment(sketch, "E2729", {"start": v(-42.2, 29.08) * mm, "end": v(-42.74, 28.28) * mm});
            skLineSegment(sketch, "E2730", {"start": v(-42.74, 28.28) * mm, "end": v(-42.7, 28.21) * mm});
            skLineSegment(sketch, "E2731", {"start": v(-42.7, 28.21) * mm, "end": v(-42.65, 28.14) * mm});
            skLineSegment(sketch, "E2732", {"start": v(-42.65, 28.14) * mm, "end": v(-42.6, 28.07) * mm});
            skLineSegment(sketch, "E2733", {"start": v(-42.6, 28.07) * mm, "end": v(-42.56, 28) * mm});
            skLineSegment(sketch, "E2734", {"start": v(-42.56, 28) * mm, "end": v(-42.5, 27.93) * mm});
            skLineSegment(sketch, "E2735", {"start": v(-42.5, 27.93) * mm, "end": v(-42.46, 27.86) * mm});
            skLineSegment(sketch, "E2736", {"start": v(-42.46, 27.86) * mm, "end": v(-42.41, 27.79) * mm});
            skLineSegment(sketch, "E2737", {"start": v(-42.41, 27.79) * mm, "end": v(-42.37, 27.72) * mm});
            skLineSegment(sketch, "E2738", {"start": v(-42.37, 27.72) * mm, "end": v(-42.32, 27.65) * mm});
            skLineSegment(sketch, "E2739", {"start": v(-42.32, 27.65) * mm, "end": v(-42.27, 27.59) * mm});
            skLineSegment(sketch, "E2740", {"start": v(-42.27, 27.59) * mm, "end": v(-42.23, 27.52) * mm});
            skLineSegment(sketch, "E2741", {"start": v(-42.23, 27.52) * mm, "end": v(-42.18, 27.46) * mm});
            skLineSegment(sketch, "E2742", {"start": v(-42.18, 27.46) * mm, "end": v(-42.13, 27.4) * mm});
            skLineSegment(sketch, "E2743", {"start": v(-42.13, 27.4) * mm, "end": v(-42.09, 27.33) * mm});
            skLineSegment(sketch, "E2744", {"start": v(-42.09, 27.33) * mm, "end": v(-42.04, 27.27) * mm});
            skLineSegment(sketch, "E2745", {"start": v(-42.04, 27.27) * mm, "end": v(-42, 27.2) * mm});
            skLineSegment(sketch, "E2746", {"start": v(-42, 27.2) * mm, "end": v(-41.95, 27.15) * mm});
            skLineSegment(sketch, "E2747", {"start": v(-41.95, 27.15) * mm, "end": v(-41.9, 27.1) * mm});
            skLineSegment(sketch, "E2748", {"start": v(-41.9, 27.1) * mm, "end": v(-41.86, 27.03) * mm});
            skLineSegment(sketch, "E2749", {"start": v(-41.86, 27.03) * mm, "end": v(-41.82, 26.98) * mm});
            skLineSegment(sketch, "E2750", {"start": v(-41.82, 26.98) * mm, "end": v(-41.78, 26.92) * mm});
            skLineSegment(sketch, "E2751", {"start": v(-41.78, 26.92) * mm, "end": v(-41.73, 26.86) * mm});
            skLineSegment(sketch, "E2752", {"start": v(-41.73, 26.86) * mm, "end": v(-41.69, 26.81) * mm});
            skLineSegment(sketch, "E2753", {"start": v(-41.69, 26.81) * mm, "end": v(-41.65, 26.76) * mm});
            skLineSegment(sketch, "E2754", {"start": v(-41.65, 26.76) * mm, "end": v(-41.6, 26.7) * mm});
            skLineSegment(sketch, "E2755", {"start": v(-41.6, 26.7) * mm, "end": v(-41.56, 26.65) * mm});
            skLineSegment(sketch, "E2756", {"start": v(-41.56, 26.65) * mm, "end": v(-41.52, 26.6) * mm});
            skLineSegment(sketch, "E2757", {"start": v(-41.52, 26.6) * mm, "end": v(-41.48, 26.55) * mm});
            skLineSegment(sketch, "E2758", {"start": v(-41.48, 26.55) * mm, "end": v(-41.44, 26.5) * mm});
            skLineSegment(sketch, "E2759", {"start": v(-41.44, 26.5) * mm, "end": v(-41.4, 26.46) * mm});
            skLineSegment(sketch, "E2760", {"start": v(-41.4, 26.46) * mm, "end": v(-41.36, 26.4) * mm});
            skLineSegment(sketch, "E2761", {"start": v(-41.36, 26.4) * mm, "end": v(-41.32, 26.36) * mm});
            skLineSegment(sketch, "E2762", {"start": v(-41.32, 26.36) * mm, "end": v(-41.28, 26.32) * mm});
            skLineSegment(sketch, "E2763", {"start": v(-41.28, 26.32) * mm, "end": v(-41.24, 26.27) * mm});
            skLineSegment(sketch, "E2764", {"start": v(-41.24, 26.27) * mm, "end": v(-41.2, 26.23) * mm});
            skLineSegment(sketch, "E2765", {"start": v(-41.2, 26.23) * mm, "end": v(-41.16, 26.18) * mm});
            skLineSegment(sketch, "E2766", {"start": v(-41.16, 26.18) * mm, "end": v(-41.12, 26.14) * mm});
            skLineSegment(sketch, "E2767", {"start": v(-41.12, 26.14) * mm, "end": v(-41.08, 26.1) * mm});
            skLineSegment(sketch, "E2768", {"start": v(-41.08, 26.1) * mm, "end": v(-41.05, 26.06) * mm});
            skLineSegment(sketch, "E2769", {"start": v(-41.05, 26.06) * mm, "end": v(-41, 26.02) * mm});
            skLineSegment(sketch, "E2770", {"start": v(-41, 26.02) * mm, "end": v(-41.15, 25.78) * mm});
            skLineSegment(sketch, "E2771", {"start": v(-41.15, 25.78) * mm, "end": v(-41.4, 25.37) * mm});
            skLineSegment(sketch, "E2772", {"start": v(-41.4, 25.37) * mm, "end": v(-41.56, 25.14) * mm});
            skLineSegment(sketch, "E2773", {"start": v(-41.56, 25.14) * mm, "end": v(-41.6, 25.15) * mm});
            skLineSegment(sketch, "E2774", {"start": v(-41.6, 25.15) * mm, "end": v(-41.66, 25.17) * mm});
            skLineSegment(sketch, "E2775", {"start": v(-41.66, 25.17) * mm, "end": v(-41.71, 25.18) * mm});
            skLineSegment(sketch, "E2776", {"start": v(-41.71, 25.18) * mm, "end": v(-41.77, 25.2) * mm});
            skLineSegment(sketch, "E2777", {"start": v(-41.77, 25.2) * mm, "end": v(-41.83, 25.21) * mm});
            skLineSegment(sketch, "E2778", {"start": v(-41.83, 25.21) * mm, "end": v(-41.88, 25.23) * mm});
            skLineSegment(sketch, "E2779", {"start": v(-41.88, 25.23) * mm, "end": v(-41.94, 25.25) * mm});
            skLineSegment(sketch, "E2780", {"start": v(-41.94, 25.25) * mm, "end": v(-42, 25.26) * mm});
            skLineSegment(sketch, "E2781", {"start": v(-42, 25.26) * mm, "end": v(-42.06, 25.28) * mm});
            skLineSegment(sketch, "E2782", {"start": v(-42.06, 25.28) * mm, "end": v(-42.12, 25.3) * mm});
            skLineSegment(sketch, "E2783", {"start": v(-42.12, 25.3) * mm, "end": v(-42.18, 25.3) * mm});
            skLineSegment(sketch, "E2784", {"start": v(-42.18, 25.3) * mm, "end": v(-42.24, 25.32) * mm});
            skLineSegment(sketch, "E2785", {"start": v(-42.24, 25.32) * mm, "end": v(-42.3, 25.34) * mm});
            skLineSegment(sketch, "E2786", {"start": v(-42.3, 25.34) * mm, "end": v(-42.37, 25.35) * mm});
            skLineSegment(sketch, "E2787", {"start": v(-42.37, 25.35) * mm, "end": v(-42.43, 25.37) * mm});
            skLineSegment(sketch, "E2788", {"start": v(-42.43, 25.37) * mm, "end": v(-42.5, 25.38) * mm});
            skLineSegment(sketch, "E2789", {"start": v(-42.5, 25.38) * mm, "end": v(-42.57, 25.4) * mm});
            skLineSegment(sketch, "E2790", {"start": v(-42.57, 25.4) * mm, "end": v(-42.63, 25.4) * mm});
            skLineSegment(sketch, "E2791", {"start": v(-42.63, 25.4) * mm, "end": v(-42.7, 25.42) * mm});
            skLineSegment(sketch, "E2792", {"start": v(-42.7, 25.42) * mm, "end": v(-42.77, 25.44) * mm});
            skLineSegment(sketch, "E2793", {"start": v(-42.77, 25.44) * mm, "end": v(-42.84, 25.45) * mm});
            skLineSegment(sketch, "E2794", {"start": v(-42.84, 25.45) * mm, "end": v(-42.91, 25.47) * mm});
            skLineSegment(sketch, "E2795", {"start": v(-42.91, 25.47) * mm, "end": v(-42.99, 25.48) * mm});
            skLineSegment(sketch, "E2796", {"start": v(-42.99, 25.48) * mm, "end": v(-43.06, 25.5) * mm});
            skLineSegment(sketch, "E2797", {"start": v(-43.06, 25.5) * mm, "end": v(-43.13, 25.5) * mm});
            skLineSegment(sketch, "E2798", {"start": v(-43.13, 25.5) * mm, "end": v(-43.2, 25.52) * mm});
            skLineSegment(sketch, "E2799", {"start": v(-43.2, 25.52) * mm, "end": v(-43.29, 25.54) * mm});
            skLineSegment(sketch, "E2800", {"start": v(-43.29, 25.54) * mm, "end": v(-43.36, 25.55) * mm});
            skLineSegment(sketch, "E2801", {"start": v(-43.36, 25.55) * mm, "end": v(-43.44, 25.56) * mm});
            skLineSegment(sketch, "E2802", {"start": v(-43.44, 25.56) * mm, "end": v(-43.52, 25.57) * mm});
            skLineSegment(sketch, "E2803", {"start": v(-43.52, 25.57) * mm, "end": v(-43.6, 25.59) * mm});
            skLineSegment(sketch, "E2804", {"start": v(-43.6, 25.59) * mm, "end": v(-43.68, 25.6) * mm});
            skLineSegment(sketch, "E2805", {"start": v(-43.68, 25.6) * mm, "end": v(-43.76, 25.61) * mm});
            skLineSegment(sketch, "E2806", {"start": v(-43.76, 25.61) * mm, "end": v(-43.85, 25.62) * mm});
            skLineSegment(sketch, "E2807", {"start": v(-43.85, 25.62) * mm, "end": v(-43.93, 25.63) * mm});
            skLineSegment(sketch, "E2808", {"start": v(-43.93, 25.63) * mm, "end": v(-44.01, 25.65) * mm});
            skLineSegment(sketch, "E2809", {"start": v(-44.01, 25.65) * mm, "end": v(-44.1, 25.66) * mm});
            skLineSegment(sketch, "E2810", {"start": v(-44.1, 25.66) * mm, "end": v(-44.19, 25.67) * mm});
            skLineSegment(sketch, "E2811", {"start": v(-44.19, 25.67) * mm, "end": v(-44.27, 25.68) * mm});
            skLineSegment(sketch, "E2812", {"start": v(-44.27, 25.68) * mm, "end": v(-44.35, 25.68) * mm});
            skLineSegment(sketch, "E2813", {"start": v(-44.35, 25.68) * mm, "end": v(-44.83, 24.84) * mm});
            skLineSegment(sketch, "E2814", {"start": v(-44.83, 24.84) * mm, "end": v(-44.78, 24.78) * mm});
            skLineSegment(sketch, "E2815", {"start": v(-44.78, 24.78) * mm, "end": v(-44.73, 24.7) * mm});
            skLineSegment(sketch, "E2816", {"start": v(-44.73, 24.7) * mm, "end": v(-44.68, 24.64) * mm});
            skLineSegment(sketch, "E2817", {"start": v(-44.68, 24.64) * mm, "end": v(-44.62, 24.57) * mm});
            skLineSegment(sketch, "E2818", {"start": v(-44.62, 24.57) * mm, "end": v(-44.57, 24.5) * mm});
            skLineSegment(sketch, "E2819", {"start": v(-44.57, 24.5) * mm, "end": v(-44.52, 24.44) * mm});
            skLineSegment(sketch, "E2820", {"start": v(-44.52, 24.44) * mm, "end": v(-44.46, 24.37) * mm});
            skLineSegment(sketch, "E2821", {"start": v(-44.46, 24.37) * mm, "end": v(-44.41, 24.3) * mm});
            skLineSegment(sketch, "E2822", {"start": v(-44.41, 24.3) * mm, "end": v(-44.36, 24.25) * mm});
            skLineSegment(sketch, "E2823", {"start": v(-44.36, 24.25) * mm, "end": v(-44.3, 24.18) * mm});
            skLineSegment(sketch, "E2824", {"start": v(-44.3, 24.18) * mm, "end": v(-44.26, 24.12) * mm});
            skLineSegment(sketch, "E2825", {"start": v(-44.26, 24.12) * mm, "end": v(-44.2, 24.06) * mm});
            skLineSegment(sketch, "E2826", {"start": v(-44.2, 24.06) * mm, "end": v(-44.15, 24) * mm});
            skLineSegment(sketch, "E2827", {"start": v(-44.15, 24) * mm, "end": v(-44.1, 23.94) * mm});
            skLineSegment(sketch, "E2828", {"start": v(-44.1, 23.94) * mm, "end": v(-44.05, 23.89) * mm});
            skLineSegment(sketch, "E2829", {"start": v(-44.05, 23.89) * mm, "end": v(-44, 23.83) * mm});
            skLineSegment(sketch, "E2830", {"start": v(-44, 23.83) * mm, "end": v(-43.95, 23.77) * mm});
            skLineSegment(sketch, "E2831", {"start": v(-43.95, 23.77) * mm, "end": v(-43.9, 23.72) * mm});
            skLineSegment(sketch, "E2832", {"start": v(-43.9, 23.72) * mm, "end": v(-43.86, 23.66) * mm});
            skLineSegment(sketch, "E2833", {"start": v(-43.86, 23.66) * mm, "end": v(-43.8, 23.61) * mm});
            skLineSegment(sketch, "E2834", {"start": v(-43.8, 23.61) * mm, "end": v(-43.76, 23.56) * mm});
            skLineSegment(sketch, "E2835", {"start": v(-43.76, 23.56) * mm, "end": v(-43.71, 23.5) * mm});
            skLineSegment(sketch, "E2836", {"start": v(-43.71, 23.5) * mm, "end": v(-43.66, 23.46) * mm});
            skLineSegment(sketch, "E2837", {"start": v(-43.66, 23.46) * mm, "end": v(-43.62, 23.4) * mm});
            skLineSegment(sketch, "E2838", {"start": v(-43.62, 23.4) * mm, "end": v(-43.57, 23.36) * mm});
            skLineSegment(sketch, "E2839", {"start": v(-43.57, 23.36) * mm, "end": v(-43.52, 23.3) * mm});
            skLineSegment(sketch, "E2840", {"start": v(-43.52, 23.3) * mm, "end": v(-43.48, 23.26) * mm});
            skLineSegment(sketch, "E2841", {"start": v(-43.48, 23.26) * mm, "end": v(-43.43, 23.22) * mm});
            skLineSegment(sketch, "E2842", {"start": v(-43.43, 23.22) * mm, "end": v(-43.39, 23.17) * mm});
            skLineSegment(sketch, "E2843", {"start": v(-43.39, 23.17) * mm, "end": v(-43.34, 23.13) * mm});
            skLineSegment(sketch, "E2844", {"start": v(-43.34, 23.13) * mm, "end": v(-43.3, 23.08) * mm});
            skLineSegment(sketch, "E2845", {"start": v(-43.3, 23.08) * mm, "end": v(-43.26, 23.04) * mm});
            skLineSegment(sketch, "E2846", {"start": v(-43.26, 23.04) * mm, "end": v(-43.21, 23) * mm});
            skLineSegment(sketch, "E2847", {"start": v(-43.21, 23) * mm, "end": v(-43.17, 22.96) * mm});
            skLineSegment(sketch, "E2848", {"start": v(-43.17, 22.96) * mm, "end": v(-43.13, 22.91) * mm});
            skLineSegment(sketch, "E2849", {"start": v(-43.13, 22.91) * mm, "end": v(-43.09, 22.87) * mm});
            skLineSegment(sketch, "E2850", {"start": v(-43.09, 22.87) * mm, "end": v(-43.05, 22.84) * mm});
            skLineSegment(sketch, "E2851", {"start": v(-43.05, 22.84) * mm, "end": v(-43, 22.8) * mm});
            skLineSegment(sketch, "E2852", {"start": v(-43, 22.8) * mm, "end": v(-42.96, 22.76) * mm});
            skLineSegment(sketch, "E2853", {"start": v(-42.96, 22.76) * mm, "end": v(-42.92, 22.72) * mm});
            skLineSegment(sketch, "E2854", {"start": v(-42.92, 22.72) * mm, "end": v(-43.05, 22.47) * mm});
            skLineSegment(sketch, "E2855", {"start": v(-43.05, 22.47) * mm, "end": v(-43.27, 22.05) * mm});
            skLineSegment(sketch, "E2856", {"start": v(-43.27, 22.05) * mm, "end": v(-43.4, 21.8) * mm});
            skLineSegment(sketch, "E2857", {"start": v(-43.4, 21.8) * mm, "end": v(-43.45, 21.81) * mm});
            skLineSegment(sketch, "E2858", {"start": v(-43.45, 21.81) * mm, "end": v(-43.5, 21.82) * mm});
            skLineSegment(sketch, "E2859", {"start": v(-43.5, 21.82) * mm, "end": v(-43.56, 21.83) * mm});
            skLineSegment(sketch, "E2860", {"start": v(-43.56, 21.83) * mm, "end": v(-43.62, 21.84) * mm});
            skLineSegment(sketch, "E2861", {"start": v(-43.62, 21.84) * mm, "end": v(-43.67, 21.86) * mm});
            skLineSegment(sketch, "E2862", {"start": v(-43.67, 21.86) * mm, "end": v(-43.73, 21.87) * mm});
            skLineSegment(sketch, "E2863", {"start": v(-43.73, 21.87) * mm, "end": v(-43.8, 21.88) * mm});
            skLineSegment(sketch, "E2864", {"start": v(-43.8, 21.88) * mm, "end": v(-43.85, 21.89) * mm});
            skLineSegment(sketch, "E2865", {"start": v(-43.85, 21.89) * mm, "end": v(-43.91, 21.9) * mm});
            skLineSegment(sketch, "E2866", {"start": v(-43.91, 21.9) * mm, "end": v(-43.97, 21.9) * mm});
            skLineSegment(sketch, "E2867", {"start": v(-43.97, 21.9) * mm, "end": v(-44.03, 21.92) * mm});
            skLineSegment(sketch, "E2868", {"start": v(-44.03, 21.92) * mm, "end": v(-44.1, 21.93) * mm});
            skLineSegment(sketch, "E2869", {"start": v(-44.1, 21.93) * mm, "end": v(-44.16, 21.94) * mm});
            skLineSegment(sketch, "E2870", {"start": v(-44.16, 21.94) * mm, "end": v(-44.23, 21.95) * mm});
            skLineSegment(sketch, "E2871", {"start": v(-44.23, 21.95) * mm, "end": v(-44.3, 21.96) * mm});
            skLineSegment(sketch, "E2872", {"start": v(-44.3, 21.96) * mm, "end": v(-44.36, 21.97) * mm});
            skLineSegment(sketch, "E2873", {"start": v(-44.36, 21.97) * mm, "end": v(-44.43, 21.98) * mm});
            skLineSegment(sketch, "E2874", {"start": v(-44.43, 21.98) * mm, "end": v(-44.5, 21.99) * mm});
            skLineSegment(sketch, "E2875", {"start": v(-44.5, 21.99) * mm, "end": v(-44.57, 22) * mm});
            skLineSegment(sketch, "E2876", {"start": v(-44.57, 22) * mm, "end": v(-44.64, 22) * mm});
            skLineSegment(sketch, "E2877", {"start": v(-44.64, 22) * mm, "end": v(-44.7, 22.01) * mm});
            skLineSegment(sketch, "E2878", {"start": v(-44.7, 22.01) * mm, "end": v(-44.78, 22.02) * mm});
            skLineSegment(sketch, "E2879", {"start": v(-44.78, 22.02) * mm, "end": v(-44.85, 22.03) * mm});
            skLineSegment(sketch, "E2880", {"start": v(-44.85, 22.03) * mm, "end": v(-44.93, 22.04) * mm});
            skLineSegment(sketch, "E2881", {"start": v(-44.93, 22.04) * mm, "end": v(-45, 22.05) * mm});
            skLineSegment(sketch, "E2882", {"start": v(-45, 22.05) * mm, "end": v(-45.08, 22.05) * mm});
            skLineSegment(sketch, "E2883", {"start": v(-45.08, 22.05) * mm, "end": v(-45.16, 22.06) * mm});
            skLineSegment(sketch, "E2884", {"start": v(-45.16, 22.06) * mm, "end": v(-45.23, 22.07) * mm});
            skLineSegment(sketch, "E2885", {"start": v(-45.23, 22.07) * mm, "end": v(-45.31, 22.07) * mm});
            skLineSegment(sketch, "E2886", {"start": v(-45.31, 22.07) * mm, "end": v(-45.4, 22.08) * mm});
            skLineSegment(sketch, "E2887", {"start": v(-45.4, 22.08) * mm, "end": v(-45.47, 22.09) * mm});
            skLineSegment(sketch, "E2888", {"start": v(-45.47, 22.09) * mm, "end": v(-45.55, 22.1) * mm});
            skLineSegment(sketch, "E2889", {"start": v(-45.55, 22.1) * mm, "end": v(-45.64, 22.1) * mm});
            skLineSegment(sketch, "E2890", {"start": v(-45.64, 22.1) * mm, "end": v(-45.72, 22.1) * mm});
            skLineSegment(sketch, "E2891", {"start": v(-45.72, 22.1) * mm, "end": v(-45.8, 22.1) * mm});
            skLineSegment(sketch, "E2892", {"start": v(-45.8, 22.1) * mm, "end": v(-45.9, 22.11) * mm});
            skLineSegment(sketch, "E2893", {"start": v(-45.9, 22.11) * mm, "end": v(-45.98, 22.12) * mm});
            skLineSegment(sketch, "E2894", {"start": v(-45.98, 22.12) * mm, "end": v(-46.06, 22.12) * mm});
            skLineSegment(sketch, "E2895", {"start": v(-46.06, 22.12) * mm, "end": v(-46.15, 22.12) * mm});
            skLineSegment(sketch, "E2896", {"start": v(-46.15, 22.12) * mm, "end": v(-46.23, 22.12) * mm});
            skLineSegment(sketch, "E2897", {"start": v(-46.23, 22.12) * mm, "end": v(-46.64, 21.25) * mm});
            skLineSegment(sketch, "E2898", {"start": v(-46.64, 21.25) * mm, "end": v(-46.59, 21.19) * mm});
            skLineSegment(sketch, "E2899", {"start": v(-46.59, 21.19) * mm, "end": v(-46.53, 21.12) * mm});
            skLineSegment(sketch, "E2900", {"start": v(-46.53, 21.12) * mm, "end": v(-46.47, 21.06) * mm});
            skLineSegment(sketch, "E2901", {"start": v(-46.47, 21.06) * mm, "end": v(-46.41, 21) * mm});
            skLineSegment(sketch, "E2902", {"start": v(-46.41, 21) * mm, "end": v(-46.35, 20.93) * mm});
            skLineSegment(sketch, "E2903", {"start": v(-46.35, 20.93) * mm, "end": v(-46.3, 20.87) * mm});
            skLineSegment(sketch, "E2904", {"start": v(-46.3, 20.87) * mm, "end": v(-46.24, 20.8) * mm});
            skLineSegment(sketch, "E2905", {"start": v(-46.24, 20.8) * mm, "end": v(-46.18, 20.75) * mm});
            skLineSegment(sketch, "E2906", {"start": v(-46.18, 20.75) * mm, "end": v(-46.12, 20.7) * mm});
            skLineSegment(sketch, "E2907", {"start": v(-46.12, 20.7) * mm, "end": v(-46.07, 20.63) * mm});
            skLineSegment(sketch, "E2908", {"start": v(-46.07, 20.63) * mm, "end": v(-46.01, 20.58) * mm});
            skLineSegment(sketch, "E2909", {"start": v(-46.01, 20.58) * mm, "end": v(-45.96, 20.52) * mm});
            skLineSegment(sketch, "E2910", {"start": v(-45.96, 20.52) * mm, "end": v(-45.9, 20.46) * mm});
            skLineSegment(sketch, "E2911", {"start": v(-45.9, 20.46) * mm, "end": v(-45.85, 20.4) * mm});
            skLineSegment(sketch, "E2912", {"start": v(-45.85, 20.4) * mm, "end": v(-45.8, 20.36) * mm});
            skLineSegment(sketch, "E2913", {"start": v(-45.8, 20.36) * mm, "end": v(-45.74, 20.3) * mm});
            skLineSegment(sketch, "E2914", {"start": v(-45.74, 20.3) * mm, "end": v(-45.68, 20.25) * mm});
            skLineSegment(sketch, "E2915", {"start": v(-45.68, 20.25) * mm, "end": v(-45.63, 20.2) * mm});
            skLineSegment(sketch, "E2916", {"start": v(-45.63, 20.2) * mm, "end": v(-45.58, 20.15) * mm});
            skLineSegment(sketch, "E2917", {"start": v(-45.58, 20.15) * mm, "end": v(-45.52, 20.1) * mm});
            skLineSegment(sketch, "E2918", {"start": v(-45.52, 20.1) * mm, "end": v(-45.47, 20.05) * mm});
            skLineSegment(sketch, "E2919", {"start": v(-45.47, 20.05) * mm, "end": v(-45.42, 20) * mm});
            skLineSegment(sketch, "E2920", {"start": v(-45.42, 20) * mm, "end": v(-45.37, 19.96) * mm});
            skLineSegment(sketch, "E2921", {"start": v(-45.37, 19.96) * mm, "end": v(-45.32, 19.91) * mm});
            skLineSegment(sketch, "E2922", {"start": v(-45.32, 19.91) * mm, "end": v(-45.27, 19.87) * mm});
            skLineSegment(sketch, "E2923", {"start": v(-45.27, 19.87) * mm, "end": v(-45.22, 19.82) * mm});
            skLineSegment(sketch, "E2924", {"start": v(-45.22, 19.82) * mm, "end": v(-45.17, 19.78) * mm});
            skLineSegment(sketch, "E2925", {"start": v(-45.17, 19.78) * mm, "end": v(-45.12, 19.74) * mm});
            skLineSegment(sketch, "E2926", {"start": v(-45.12, 19.74) * mm, "end": v(-45.07, 19.7) * mm});
            skLineSegment(sketch, "E2927", {"start": v(-45.07, 19.7) * mm, "end": v(-45.02, 19.65) * mm});
            skLineSegment(sketch, "E2928", {"start": v(-45.02, 19.65) * mm, "end": v(-44.98, 19.61) * mm});
            skLineSegment(sketch, "E2929", {"start": v(-44.98, 19.61) * mm, "end": v(-44.93, 19.57) * mm});
            skLineSegment(sketch, "E2930", {"start": v(-44.93, 19.57) * mm, "end": v(-44.88, 19.54) * mm});
            skLineSegment(sketch, "E2931", {"start": v(-44.88, 19.54) * mm, "end": v(-44.84, 19.5) * mm});
            skLineSegment(sketch, "E2932", {"start": v(-44.84, 19.5) * mm, "end": v(-44.8, 19.46) * mm});
            skLineSegment(sketch, "E2933", {"start": v(-44.8, 19.46) * mm, "end": v(-44.75, 19.42) * mm});
            skLineSegment(sketch, "E2934", {"start": v(-44.75, 19.42) * mm, "end": v(-44.7, 19.39) * mm});
            skLineSegment(sketch, "E2935", {"start": v(-44.7, 19.39) * mm, "end": v(-44.66, 19.35) * mm});
            skLineSegment(sketch, "E2936", {"start": v(-44.66, 19.35) * mm, "end": v(-44.62, 19.32) * mm});
            skLineSegment(sketch, "E2937", {"start": v(-44.62, 19.32) * mm, "end": v(-44.58, 19.29) * mm});
            skLineSegment(sketch, "E2938", {"start": v(-44.58, 19.29) * mm, "end": v(-44.68, 19.03) * mm});
            skLineSegment(sketch, "E2939", {"start": v(-44.68, 19.03) * mm, "end": v(-44.87, 18.58) * mm});
            skLineSegment(sketch, "E2940", {"start": v(-44.87, 18.58) * mm, "end": v(-44.98, 18.33) * mm});
            skLineSegment(sketch, "E2941", {"start": v(-44.98, 18.33) * mm, "end": v(-45.03, 18.34) * mm});
            skLineSegment(sketch, "E2942", {"start": v(-45.03, 18.34) * mm, "end": v(-45.09, 18.34) * mm});
            skLineSegment(sketch, "E2943", {"start": v(-45.09, 18.34) * mm, "end": v(-45.14, 18.35) * mm});
            skLineSegment(sketch, "E2944", {"start": v(-45.14, 18.35) * mm, "end": v(-45.2, 18.36) * mm});
            skLineSegment(sketch, "E2945", {"start": v(-45.2, 18.36) * mm, "end": v(-45.25, 18.36) * mm});
            skLineSegment(sketch, "E2946", {"start": v(-45.25, 18.36) * mm, "end": v(-45.31, 18.37) * mm});
            skLineSegment(sketch, "E2947", {"start": v(-45.31, 18.37) * mm, "end": v(-45.37, 18.37) * mm});
            skLineSegment(sketch, "E2948", {"start": v(-45.37, 18.37) * mm, "end": v(-45.43, 18.38) * mm});
            skLineSegment(sketch, "E2949", {"start": v(-45.43, 18.38) * mm, "end": v(-45.5, 18.39) * mm});
            skLineSegment(sketch, "E2950", {"start": v(-45.5, 18.39) * mm, "end": v(-45.56, 18.4) * mm});
            skLineSegment(sketch, "E2951", {"start": v(-45.56, 18.4) * mm, "end": v(-45.62, 18.4) * mm});
            skLineSegment(sketch, "E2952", {"start": v(-45.62, 18.4) * mm, "end": v(-45.68, 18.4) * mm});
            skLineSegment(sketch, "E2953", {"start": v(-45.68, 18.4) * mm, "end": v(-45.75, 18.4) * mm});
            skLineSegment(sketch, "E2954", {"start": v(-45.75, 18.4) * mm, "end": v(-45.81, 18.41) * mm});
            skLineSegment(sketch, "E2955", {"start": v(-45.81, 18.41) * mm, "end": v(-45.88, 18.42) * mm});
            skLineSegment(sketch, "E2956", {"start": v(-45.88, 18.42) * mm, "end": v(-45.95, 18.42) * mm});
            skLineSegment(sketch, "E2957", {"start": v(-45.95, 18.42) * mm, "end": v(-46.01, 18.42) * mm});
            skLineSegment(sketch, "E2958", {"start": v(-46.01, 18.42) * mm, "end": v(-46.08, 18.43) * mm});
            skLineSegment(sketch, "E2959", {"start": v(-46.08, 18.43) * mm, "end": v(-46.15, 18.43) * mm});
            skLineSegment(sketch, "E2960", {"start": v(-46.15, 18.43) * mm, "end": v(-46.22, 18.43) * mm});
            skLineSegment(sketch, "E2961", {"start": v(-46.22, 18.43) * mm, "end": v(-46.3, 18.44) * mm});
            skLineSegment(sketch, "E2962", {"start": v(-46.3, 18.44) * mm, "end": v(-46.37, 18.44) * mm});
            skLineSegment(sketch, "E2963", {"start": v(-46.37, 18.44) * mm, "end": v(-46.44, 18.44) * mm});
            skLineSegment(sketch, "E2964", {"start": v(-46.44, 18.44) * mm, "end": v(-46.52, 18.44) * mm});
            skLineSegment(sketch, "E2965", {"start": v(-46.52, 18.44) * mm, "end": v(-46.6, 18.45) * mm});
            skLineSegment(sketch, "E2966", {"start": v(-46.6, 18.45) * mm, "end": v(-46.67, 18.45) * mm});
            skLineSegment(sketch, "E2967", {"start": v(-46.67, 18.45) * mm, "end": v(-46.75, 18.45) * mm});
            skLineSegment(sketch, "E2968", {"start": v(-46.75, 18.45) * mm, "end": v(-46.83, 18.45) * mm});
            skLineSegment(sketch, "E2969", {"start": v(-46.83, 18.45) * mm, "end": v(-46.9, 18.45) * mm});
            skLineSegment(sketch, "E2970", {"start": v(-46.9, 18.45) * mm, "end": v(-46.98, 18.45) * mm});
            skLineSegment(sketch, "E2971", {"start": v(-46.98, 18.45) * mm, "end": v(-47.07, 18.45) * mm});
            skLineSegment(sketch, "E2972", {"start": v(-47.07, 18.45) * mm, "end": v(-47.15, 18.45) * mm});
            skLineSegment(sketch, "E2973", {"start": v(-47.15, 18.45) * mm, "end": v(-47.23, 18.45) * mm});
            skLineSegment(sketch, "E2974", {"start": v(-47.23, 18.45) * mm, "end": v(-47.31, 18.45) * mm});
            skLineSegment(sketch, "E2975", {"start": v(-47.31, 18.45) * mm, "end": v(-47.4, 18.45) * mm});
            skLineSegment(sketch, "E2976", {"start": v(-47.4, 18.45) * mm, "end": v(-47.48, 18.44) * mm});
            skLineSegment(sketch, "E2977", {"start": v(-47.48, 18.44) * mm, "end": v(-47.57, 18.44) * mm});
            skLineSegment(sketch, "E2978", {"start": v(-47.57, 18.44) * mm, "end": v(-47.66, 18.44) * mm});
            skLineSegment(sketch, "E2979", {"start": v(-47.66, 18.44) * mm, "end": v(-47.75, 18.44) * mm});
            skLineSegment(sketch, "E2980", {"start": v(-47.75, 18.44) * mm, "end": v(-47.82, 18.43) * mm});
            skLineSegment(sketch, "E2981", {"start": v(-47.82, 18.43) * mm, "end": v(-48.16, 17.52) * mm});
            skLineSegment(sketch, "E2982", {"start": v(-48.16, 17.52) * mm, "end": v(-48.1, 17.47) * mm});
            skLineSegment(sketch, "E2983", {"start": v(-48.1, 17.47) * mm, "end": v(-48.04, 17.4) * mm});
            skLineSegment(sketch, "E2984", {"start": v(-48.04, 17.4) * mm, "end": v(-47.98, 17.35) * mm});
            skLineSegment(sketch, "E2985", {"start": v(-47.98, 17.35) * mm, "end": v(-47.92, 17.29) * mm});
            skLineSegment(sketch, "E2986", {"start": v(-47.92, 17.29) * mm, "end": v(-47.85, 17.23) * mm});
            skLineSegment(sketch, "E2987", {"start": v(-47.85, 17.23) * mm, "end": v(-47.8, 17.17) * mm});
            skLineSegment(sketch, "E2988", {"start": v(-47.8, 17.17) * mm, "end": v(-47.73, 17.12) * mm});
            skLineSegment(sketch, "E2989", {"start": v(-47.73, 17.12) * mm, "end": v(-47.67, 17.06) * mm});
            skLineSegment(sketch, "E2990", {"start": v(-47.67, 17.06) * mm, "end": v(-47.6, 17) * mm});
            skLineSegment(sketch, "E2991", {"start": v(-47.6, 17) * mm, "end": v(-47.55, 16.95) * mm});
            skLineSegment(sketch, "E2992", {"start": v(-47.55, 16.95) * mm, "end": v(-47.48, 16.9) * mm});
            skLineSegment(sketch, "E2993", {"start": v(-47.48, 16.9) * mm, "end": v(-47.42, 16.85) * mm});
            skLineSegment(sketch, "E2994", {"start": v(-47.42, 16.85) * mm, "end": v(-47.36, 16.8) * mm});
            skLineSegment(sketch, "E2995", {"start": v(-47.36, 16.8) * mm, "end": v(-47.3, 16.75) * mm});
            skLineSegment(sketch, "E2996", {"start": v(-47.3, 16.75) * mm, "end": v(-47.25, 16.7) * mm});
            skLineSegment(sketch, "E2997", {"start": v(-47.25, 16.7) * mm, "end": v(-47.19, 16.65) * mm});
            skLineSegment(sketch, "E2998", {"start": v(-47.19, 16.65) * mm, "end": v(-47.13, 16.6) * mm});
            skLineSegment(sketch, "E2999", {"start": v(-47.13, 16.6) * mm, "end": v(-47.07, 16.56) * mm});
            skLineSegment(sketch, "E3000", {"start": v(-47.07, 16.56) * mm, "end": v(-47.02, 16.51) * mm});
            skLineSegment(sketch, "E3001", {"start": v(-47.02, 16.51) * mm, "end": v(-46.96, 16.47) * mm});
            skLineSegment(sketch, "E3002", {"start": v(-46.96, 16.47) * mm, "end": v(-46.9, 16.42) * mm});
            skLineSegment(sketch, "E3003", {"start": v(-46.9, 16.42) * mm, "end": v(-46.85, 16.38) * mm});
            skLineSegment(sketch, "E3004", {"start": v(-46.85, 16.38) * mm, "end": v(-46.8, 16.34) * mm});
            skLineSegment(sketch, "E3005", {"start": v(-46.8, 16.34) * mm, "end": v(-46.74, 16.3) * mm});
            skLineSegment(sketch, "E3006", {"start": v(-46.74, 16.3) * mm, "end": v(-46.69, 16.25) * mm});
            skLineSegment(sketch, "E3007", {"start": v(-46.69, 16.25) * mm, "end": v(-46.63, 16.21) * mm});
            skLineSegment(sketch, "E3008", {"start": v(-46.63, 16.21) * mm, "end": v(-46.58, 16.17) * mm});
            skLineSegment(sketch, "E3009", {"start": v(-46.58, 16.17) * mm, "end": v(-46.53, 16.14) * mm});
            skLineSegment(sketch, "E3010", {"start": v(-46.53, 16.14) * mm, "end": v(-46.48, 16.1) * mm});
            skLineSegment(sketch, "E3011", {"start": v(-46.48, 16.1) * mm, "end": v(-46.43, 16.06) * mm});
            skLineSegment(sketch, "E3012", {"start": v(-46.43, 16.06) * mm, "end": v(-46.38, 16.02) * mm});
            skLineSegment(sketch, "E3013", {"start": v(-46.38, 16.02) * mm, "end": v(-46.33, 15.99) * mm});
            skLineSegment(sketch, "E3014", {"start": v(-46.33, 15.99) * mm, "end": v(-46.28, 15.95) * mm});
            skLineSegment(sketch, "E3015", {"start": v(-46.28, 15.95) * mm, "end": v(-46.23, 15.92) * mm});
            skLineSegment(sketch, "E3016", {"start": v(-46.23, 15.92) * mm, "end": v(-46.18, 15.89) * mm});
            skLineSegment(sketch, "E3017", {"start": v(-46.18, 15.89) * mm, "end": v(-46.13, 15.85) * mm});
            skLineSegment(sketch, "E3018", {"start": v(-46.13, 15.85) * mm, "end": v(-46.09, 15.82) * mm});
            skLineSegment(sketch, "E3019", {"start": v(-46.09, 15.82) * mm, "end": v(-46.04, 15.79) * mm});
            skLineSegment(sketch, "E3020", {"start": v(-46.04, 15.79) * mm, "end": v(-46, 15.76) * mm});
            skLineSegment(sketch, "E3021", {"start": v(-46, 15.76) * mm, "end": v(-45.95, 15.73) * mm});
            skLineSegment(sketch, "E3022", {"start": v(-45.95, 15.73) * mm, "end": v(-46.04, 15.46) * mm});
            skLineSegment(sketch, "E3023", {"start": v(-46.04, 15.46) * mm, "end": v(-46.19, 15) * mm});
            skLineSegment(sketch, "E3024", {"start": v(-46.19, 15) * mm, "end": v(-46.28, 14.74) * mm});
            skLineSegment(sketch, "E3025", {"start": v(-46.28, 14.74) * mm, "end": v(-46.33, 14.75) * mm});
            skLineSegment(sketch, "E3026", {"start": v(-46.33, 14.75) * mm, "end": v(-46.39, 14.75) * mm});
            skLineSegment(sketch, "E3027", {"start": v(-46.39, 14.75) * mm, "end": v(-46.44, 14.75) * mm});
            skLineSegment(sketch, "E3028", {"start": v(-46.44, 14.75) * mm, "end": v(-46.5, 14.75) * mm});
            skLineSegment(sketch, "E3029", {"start": v(-46.5, 14.75) * mm, "end": v(-46.56, 14.75) * mm});
            skLineSegment(sketch, "E3030", {"start": v(-46.56, 14.75) * mm, "end": v(-46.61, 14.76) * mm});
            skLineSegment(sketch, "E3031", {"start": v(-46.61, 14.76) * mm, "end": v(-46.67, 14.76) * mm});
            skLineSegment(sketch, "E3032", {"start": v(-46.67, 14.76) * mm, "end": v(-46.73, 14.76) * mm});
            skLineSegment(sketch, "E3033", {"start": v(-46.73, 14.76) * mm, "end": v(-46.8, 14.76) * mm});
            skLineSegment(sketch, "E3034", {"start": v(-46.8, 14.76) * mm, "end": v(-46.86, 14.76) * mm});
            skLineSegment(sketch, "E3035", {"start": v(-46.86, 14.76) * mm, "end": v(-46.92, 14.76) * mm});
            skLineSegment(sketch, "E3036", {"start": v(-46.92, 14.76) * mm, "end": v(-46.98, 14.76) * mm});
            skLineSegment(sketch, "E3037", {"start": v(-46.98, 14.76) * mm, "end": v(-47.05, 14.76) * mm});
            skLineSegment(sketch, "E3038", {"start": v(-47.05, 14.76) * mm, "end": v(-47.12, 14.76) * mm});
            skLineSegment(sketch, "E3039", {"start": v(-47.12, 14.76) * mm, "end": v(-47.18, 14.76) * mm});
            skLineSegment(sketch, "E3040", {"start": v(-47.18, 14.76) * mm, "end": v(-47.25, 14.76) * mm});
            skLineSegment(sketch, "E3041", {"start": v(-47.25, 14.76) * mm, "end": v(-47.32, 14.76) * mm});
            skLineSegment(sketch, "E3042", {"start": v(-47.32, 14.76) * mm, "end": v(-47.39, 14.76) * mm});
            skLineSegment(sketch, "E3043", {"start": v(-47.39, 14.76) * mm, "end": v(-47.46, 14.75) * mm});
            skLineSegment(sketch, "E3044", {"start": v(-47.46, 14.75) * mm, "end": v(-47.53, 14.75) * mm});
            skLineSegment(sketch, "E3045", {"start": v(-47.53, 14.75) * mm, "end": v(-47.6, 14.75) * mm});
            skLineSegment(sketch, "E3046", {"start": v(-47.6, 14.75) * mm, "end": v(-47.67, 14.75) * mm});
            skLineSegment(sketch, "E3047", {"start": v(-47.67, 14.75) * mm, "end": v(-47.75, 14.74) * mm});
            skLineSegment(sketch, "E3048", {"start": v(-47.75, 14.74) * mm, "end": v(-47.82, 14.74) * mm});
            skLineSegment(sketch, "E3049", {"start": v(-47.82, 14.74) * mm, "end": v(-47.9, 14.73) * mm});
            skLineSegment(sketch, "E3050", {"start": v(-47.9, 14.73) * mm, "end": v(-47.97, 14.73) * mm});
            skLineSegment(sketch, "E3051", {"start": v(-47.97, 14.73) * mm, "end": v(-48.05, 14.72) * mm});
            skLineSegment(sketch, "E3052", {"start": v(-48.05, 14.72) * mm, "end": v(-48.13, 14.72) * mm});
            skLineSegment(sketch, "E3053", {"start": v(-48.13, 14.72) * mm, "end": v(-48.2, 14.71) * mm});
            skLineSegment(sketch, "E3054", {"start": v(-48.2, 14.71) * mm, "end": v(-48.29, 14.7) * mm});
            skLineSegment(sketch, "E3055", {"start": v(-48.29, 14.7) * mm, "end": v(-48.37, 14.7) * mm});
            skLineSegment(sketch, "E3056", {"start": v(-48.37, 14.7) * mm, "end": v(-48.45, 14.7) * mm});
            skLineSegment(sketch, "E3057", {"start": v(-48.45, 14.7) * mm, "end": v(-48.53, 14.69) * mm});
            skLineSegment(sketch, "E3058", {"start": v(-48.53, 14.69) * mm, "end": v(-48.62, 14.68) * mm});
            skLineSegment(sketch, "E3059", {"start": v(-48.62, 14.68) * mm, "end": v(-48.7, 14.67) * mm});
            skLineSegment(sketch, "E3060", {"start": v(-48.7, 14.67) * mm, "end": v(-48.78, 14.66) * mm});
            skLineSegment(sketch, "E3061", {"start": v(-48.78, 14.66) * mm, "end": v(-48.87, 14.65) * mm});
            skLineSegment(sketch, "E3062", {"start": v(-48.87, 14.65) * mm, "end": v(-48.96, 14.64) * mm});
            skLineSegment(sketch, "E3063", {"start": v(-48.96, 14.64) * mm, "end": v(-49.04, 14.63) * mm});
            skLineSegment(sketch, "E3064", {"start": v(-49.04, 14.63) * mm, "end": v(-49.12, 14.62) * mm});
            skLineSegment(sketch, "E3065", {"start": v(-49.12, 14.62) * mm, "end": v(-49.39, 13.7) * mm});
            skLineSegment(sketch, "E3066", {"start": v(-49.39, 13.7) * mm, "end": v(-49.33, 13.64) * mm});
            skLineSegment(sketch, "E3067", {"start": v(-49.33, 13.64) * mm, "end": v(-49.26, 13.58) * mm});
            skLineSegment(sketch, "E3068", {"start": v(-49.26, 13.58) * mm, "end": v(-49.2, 13.53) * mm});
            skLineSegment(sketch, "E3069", {"start": v(-49.2, 13.53) * mm, "end": v(-49.13, 13.47) * mm});
            skLineSegment(sketch, "E3070", {"start": v(-49.13, 13.47) * mm, "end": v(-49.06, 13.42) * mm});
            skLineSegment(sketch, "E3071", {"start": v(-49.06, 13.42) * mm, "end": v(-49, 13.37) * mm});
            skLineSegment(sketch, "E3072", {"start": v(-49, 13.37) * mm, "end": v(-48.92, 13.32) * mm});
            skLineSegment(sketch, "E3073", {"start": v(-48.92, 13.32) * mm, "end": v(-48.86, 13.27) * mm});
            skLineSegment(sketch, "E3074", {"start": v(-48.86, 13.27) * mm, "end": v(-48.8, 13.22) * mm});
            skLineSegment(sketch, "E3075", {"start": v(-48.8, 13.22) * mm, "end": v(-48.73, 13.17) * mm});
            skLineSegment(sketch, "E3076", {"start": v(-48.73, 13.17) * mm, "end": v(-48.66, 13.12) * mm});
            skLineSegment(sketch, "E3077", {"start": v(-48.66, 13.12) * mm, "end": v(-48.6, 13.08) * mm});
            skLineSegment(sketch, "E3078", {"start": v(-48.6, 13.08) * mm, "end": v(-48.54, 13.03) * mm});
            skLineSegment(sketch, "E3079", {"start": v(-48.54, 13.03) * mm, "end": v(-48.47, 12.99) * mm});
            skLineSegment(sketch, "E3080", {"start": v(-48.47, 12.99) * mm, "end": v(-48.41, 12.94) * mm});
            skLineSegment(sketch, "E3081", {"start": v(-48.41, 12.94) * mm, "end": v(-48.35, 12.9) * mm});
            skLineSegment(sketch, "E3082", {"start": v(-48.35, 12.9) * mm, "end": v(-48.29, 12.86) * mm});
            skLineSegment(sketch, "E3083", {"start": v(-48.29, 12.86) * mm, "end": v(-48.23, 12.81) * mm});
            skLineSegment(sketch, "E3084", {"start": v(-48.23, 12.81) * mm, "end": v(-48.17, 12.77) * mm});
            skLineSegment(sketch, "E3085", {"start": v(-48.17, 12.77) * mm, "end": v(-48.1, 12.73) * mm});
            skLineSegment(sketch, "E3086", {"start": v(-48.1, 12.73) * mm, "end": v(-48.05, 12.7) * mm});
            skLineSegment(sketch, "E3087", {"start": v(-48.05, 12.7) * mm, "end": v(-48, 12.65) * mm});
            skLineSegment(sketch, "E3088", {"start": v(-48, 12.65) * mm, "end": v(-47.93, 12.62) * mm});
            skLineSegment(sketch, "E3089", {"start": v(-47.93, 12.62) * mm, "end": v(-47.88, 12.58) * mm});
            skLineSegment(sketch, "E3090", {"start": v(-47.88, 12.58) * mm, "end": v(-47.82, 12.54) * mm});
            skLineSegment(sketch, "E3091", {"start": v(-47.82, 12.54) * mm, "end": v(-47.76, 12.5) * mm});
            skLineSegment(sketch, "E3092", {"start": v(-47.76, 12.5) * mm, "end": v(-47.7, 12.47) * mm});
            skLineSegment(sketch, "E3093", {"start": v(-47.7, 12.47) * mm, "end": v(-47.65, 12.44) * mm});
            skLineSegment(sketch, "E3094", {"start": v(-47.65, 12.44) * mm, "end": v(-47.6, 12.4) * mm});
            skLineSegment(sketch, "E3095", {"start": v(-47.6, 12.4) * mm, "end": v(-47.54, 12.37) * mm});
            skLineSegment(sketch, "E3096", {"start": v(-47.54, 12.37) * mm, "end": v(-47.5, 12.34) * mm});
            skLineSegment(sketch, "E3097", {"start": v(-47.5, 12.34) * mm, "end": v(-47.44, 12.3) * mm});
            skLineSegment(sketch, "E3098", {"start": v(-47.44, 12.3) * mm, "end": v(-47.39, 12.27) * mm});
            skLineSegment(sketch, "E3099", {"start": v(-47.39, 12.27) * mm, "end": v(-47.34, 12.24) * mm});
            skLineSegment(sketch, "E3100", {"start": v(-47.34, 12.24) * mm, "end": v(-47.29, 12.21) * mm});
            skLineSegment(sketch, "E3101", {"start": v(-47.29, 12.21) * mm, "end": v(-47.24, 12.18) * mm});
            skLineSegment(sketch, "E3102", {"start": v(-47.24, 12.18) * mm, "end": v(-47.19, 12.16) * mm});
            skLineSegment(sketch, "E3103", {"start": v(-47.19, 12.16) * mm, "end": v(-47.14, 12.13) * mm});
            skLineSegment(sketch, "E3104", {"start": v(-47.14, 12.13) * mm, "end": v(-47.1, 12.1) * mm});
            skLineSegment(sketch, "E3105", {"start": v(-47.1, 12.1) * mm, "end": v(-47.04, 12.07) * mm});
            skLineSegment(sketch, "E3106", {"start": v(-47.04, 12.07) * mm, "end": v(-47.1, 11.8) * mm});
            skLineSegment(sketch, "E3107", {"start": v(-47.1, 11.8) * mm, "end": v(-47.22, 11.34) * mm});
            skLineSegment(sketch, "E3108", {"start": v(-47.22, 11.34) * mm, "end": v(-47.3, 11.07) * mm});
            skLineSegment(sketch, "E3109", {"start": v(-47.3, 11.07) * mm, "end": v(-47.34, 11.06) * mm});
            skLineSegment(sketch, "E3110", {"start": v(-47.34, 11.06) * mm, "end": v(-47.4, 11.06) * mm});
            skLineSegment(sketch, "E3111", {"start": v(-47.4, 11.06) * mm, "end": v(-47.46, 11.06) * mm});
            skLineSegment(sketch, "E3112", {"start": v(-47.46, 11.06) * mm, "end": v(-47.51, 11.06) * mm});
            skLineSegment(sketch, "E3113", {"start": v(-47.51, 11.06) * mm, "end": v(-47.57, 11.06) * mm});
            skLineSegment(sketch, "E3114", {"start": v(-47.57, 11.06) * mm, "end": v(-47.63, 11.05) * mm});
            skLineSegment(sketch, "E3115", {"start": v(-47.63, 11.05) * mm, "end": v(-47.69, 11.05) * mm});
            skLineSegment(sketch, "E3116", {"start": v(-47.69, 11.05) * mm, "end": v(-47.75, 11.05) * mm});
            skLineSegment(sketch, "E3117", {"start": v(-47.75, 11.05) * mm, "end": v(-47.8, 11.04) * mm});
            skLineSegment(sketch, "E3118", {"start": v(-47.8, 11.04) * mm, "end": v(-47.87, 11.04) * mm});
            skLineSegment(sketch, "E3119", {"start": v(-47.87, 11.04) * mm, "end": v(-47.93, 11.03) * mm});
            skLineSegment(sketch, "E3120", {"start": v(-47.93, 11.03) * mm, "end": v(-48, 11.03) * mm});
            skLineSegment(sketch, "E3121", {"start": v(-48, 11.03) * mm, "end": v(-48.06, 11.02) * mm});
            skLineSegment(sketch, "E3122", {"start": v(-48.06, 11.02) * mm, "end": v(-48.13, 11.02) * mm});
            skLineSegment(sketch, "E3123", {"start": v(-48.13, 11.02) * mm, "end": v(-48.2, 11.01) * mm});
            skLineSegment(sketch, "E3124", {"start": v(-48.2, 11.01) * mm, "end": v(-48.26, 11) * mm});
            skLineSegment(sketch, "E3125", {"start": v(-48.26, 11) * mm, "end": v(-48.33, 11) * mm});
            skLineSegment(sketch, "E3126", {"start": v(-48.33, 11) * mm, "end": v(-48.4, 11) * mm});
            skLineSegment(sketch, "E3127", {"start": v(-48.4, 11) * mm, "end": v(-48.47, 10.98) * mm});
            skLineSegment(sketch, "E3128", {"start": v(-48.47, 10.98) * mm, "end": v(-48.54, 10.98) * mm});
            skLineSegment(sketch, "E3129", {"start": v(-48.54, 10.98) * mm, "end": v(-48.61, 10.97) * mm});
            skLineSegment(sketch, "E3130", {"start": v(-48.61, 10.97) * mm, "end": v(-48.68, 10.96) * mm});
            skLineSegment(sketch, "E3131", {"start": v(-48.68, 10.96) * mm, "end": v(-48.76, 10.95) * mm});
            skLineSegment(sketch, "E3132", {"start": v(-48.76, 10.95) * mm, "end": v(-48.83, 10.94) * mm});
            skLineSegment(sketch, "E3133", {"start": v(-48.83, 10.94) * mm, "end": v(-48.9, 10.93) * mm});
            skLineSegment(sketch, "E3134", {"start": v(-48.9, 10.93) * mm, "end": v(-48.98, 10.92) * mm});
            skLineSegment(sketch, "E3135", {"start": v(-48.98, 10.92) * mm, "end": v(-49.06, 10.9) * mm});
            skLineSegment(sketch, "E3136", {"start": v(-49.06, 10.9) * mm, "end": v(-49.14, 10.9) * mm});
            skLineSegment(sketch, "E3137", {"start": v(-49.14, 10.9) * mm, "end": v(-49.21, 10.89) * mm});
            skLineSegment(sketch, "E3138", {"start": v(-49.21, 10.89) * mm, "end": v(-49.3, 10.87) * mm});
            skLineSegment(sketch, "E3139", {"start": v(-49.3, 10.87) * mm, "end": v(-49.37, 10.86) * mm});
            skLineSegment(sketch, "E3140", {"start": v(-49.37, 10.86) * mm, "end": v(-49.45, 10.85) * mm});
            skLineSegment(sketch, "E3141", {"start": v(-49.45, 10.85) * mm, "end": v(-49.53, 10.83) * mm});
            skLineSegment(sketch, "E3142", {"start": v(-49.53, 10.83) * mm, "end": v(-49.62, 10.82) * mm});
            skLineSegment(sketch, "E3143", {"start": v(-49.62, 10.82) * mm, "end": v(-49.7, 10.8) * mm});
            skLineSegment(sketch, "E3144", {"start": v(-49.7, 10.8) * mm, "end": v(-49.78, 10.79) * mm});
            skLineSegment(sketch, "E3145", {"start": v(-49.78, 10.79) * mm, "end": v(-49.87, 10.77) * mm});
            skLineSegment(sketch, "E3146", {"start": v(-49.87, 10.77) * mm, "end": v(-49.95, 10.76) * mm});
            skLineSegment(sketch, "E3147", {"start": v(-49.95, 10.76) * mm, "end": v(-50.04, 10.74) * mm});
            skLineSegment(sketch, "E3148", {"start": v(-50.04, 10.74) * mm, "end": v(-50.12, 10.72) * mm});
            skLineSegment(sketch, "E3149", {"start": v(-50.12, 10.72) * mm, "end": v(-50.3, 9.77) * mm});
            skLineSegment(sketch, "E3150", {"start": v(-50.3, 9.77) * mm, "end": v(-50.25, 9.72) * mm});
            skLineSegment(sketch, "E3151", {"start": v(-50.25, 9.72) * mm, "end": v(-50.18, 9.68) * mm});
            skLineSegment(sketch, "E3152", {"start": v(-50.18, 9.68) * mm, "end": v(-50.1, 9.63) * mm});
            skLineSegment(sketch, "E3153", {"start": v(-50.1, 9.63) * mm, "end": v(-50.03, 9.58) * mm});
            skLineSegment(sketch, "E3154", {"start": v(-50.03, 9.58) * mm, "end": v(-49.96, 9.53) * mm});
            skLineSegment(sketch, "E3155", {"start": v(-49.96, 9.53) * mm, "end": v(-49.89, 9.49) * mm});
            skLineSegment(sketch, "E3156", {"start": v(-49.89, 9.49) * mm, "end": v(-49.82, 9.44) * mm});
            skLineSegment(sketch, "E3157", {"start": v(-49.82, 9.44) * mm, "end": v(-49.75, 9.4) * mm});
            skLineSegment(sketch, "E3158", {"start": v(-49.75, 9.4) * mm, "end": v(-49.68, 9.35) * mm});
            skLineSegment(sketch, "E3159", {"start": v(-49.68, 9.35) * mm, "end": v(-49.61, 9.3) * mm});
            skLineSegment(sketch, "E3160", {"start": v(-49.61, 9.3) * mm, "end": v(-49.54, 9.27) * mm});
            skLineSegment(sketch, "E3161", {"start": v(-49.54, 9.27) * mm, "end": v(-49.48, 9.22) * mm});
            skLineSegment(sketch, "E3162", {"start": v(-49.48, 9.22) * mm, "end": v(-49.4, 9.18) * mm});
            skLineSegment(sketch, "E3163", {"start": v(-49.4, 9.18) * mm, "end": v(-49.34, 9.14) * mm});
            skLineSegment(sketch, "E3164", {"start": v(-49.34, 9.14) * mm, "end": v(-49.28, 9.1) * mm});
            skLineSegment(sketch, "E3165", {"start": v(-49.28, 9.1) * mm, "end": v(-49.21, 9.07) * mm});
            skLineSegment(sketch, "E3166", {"start": v(-49.21, 9.07) * mm, "end": v(-49.15, 9.03) * mm});
            skLineSegment(sketch, "E3167", {"start": v(-49.15, 9.03) * mm, "end": v(-49.08, 9) * mm});
            skLineSegment(sketch, "E3168", {"start": v(-49.08, 9) * mm, "end": v(-49.02, 8.95) * mm});
            skLineSegment(sketch, "E3169", {"start": v(-49.02, 8.95) * mm, "end": v(-48.96, 8.92) * mm});
            skLineSegment(sketch, "E3170", {"start": v(-48.96, 8.92) * mm, "end": v(-48.9, 8.88) * mm});
            skLineSegment(sketch, "E3171", {"start": v(-48.9, 8.88) * mm, "end": v(-48.84, 8.85) * mm});
            skLineSegment(sketch, "E3172", {"start": v(-48.84, 8.85) * mm, "end": v(-48.78, 8.82) * mm});
            skLineSegment(sketch, "E3173", {"start": v(-48.78, 8.82) * mm, "end": v(-48.72, 8.78) * mm});
            skLineSegment(sketch, "E3174", {"start": v(-48.72, 8.78) * mm, "end": v(-48.66, 8.75) * mm});
            skLineSegment(sketch, "E3175", {"start": v(-48.66, 8.75) * mm, "end": v(-48.6, 8.72) * mm});
            skLineSegment(sketch, "E3176", {"start": v(-48.6, 8.72) * mm, "end": v(-48.54, 8.69) * mm});
            skLineSegment(sketch, "E3177", {"start": v(-48.54, 8.69) * mm, "end": v(-48.48, 8.66) * mm});
            skLineSegment(sketch, "E3178", {"start": v(-48.48, 8.66) * mm, "end": v(-48.42, 8.63) * mm});
            skLineSegment(sketch, "E3179", {"start": v(-48.42, 8.63) * mm, "end": v(-48.37, 8.6) * mm});
            skLineSegment(sketch, "E3180", {"start": v(-48.37, 8.6) * mm, "end": v(-48.31, 8.57) * mm});
            skLineSegment(sketch, "E3181", {"start": v(-48.31, 8.57) * mm, "end": v(-48.26, 8.54) * mm});
            skLineSegment(sketch, "E3182", {"start": v(-48.26, 8.54) * mm, "end": v(-48.2, 8.52) * mm});
            skLineSegment(sketch, "E3183", {"start": v(-48.2, 8.52) * mm, "end": v(-48.15, 8.5) * mm});
            skLineSegment(sketch, "E3184", {"start": v(-48.15, 8.5) * mm, "end": v(-48.1, 8.47) * mm});
            skLineSegment(sketch, "E3185", {"start": v(-48.1, 8.47) * mm, "end": v(-48.05, 8.44) * mm});
            skLineSegment(sketch, "E3186", {"start": v(-48.05, 8.44) * mm, "end": v(-48, 8.42) * mm});
            skLineSegment(sketch, "E3187", {"start": v(-48, 8.42) * mm, "end": v(-47.94, 8.4) * mm});
            skLineSegment(sketch, "E3188", {"start": v(-47.94, 8.4) * mm, "end": v(-47.9, 8.37) * mm});
            skLineSegment(sketch, "E3189", {"start": v(-47.9, 8.37) * mm, "end": v(-47.85, 8.35) * mm});
            skLineSegment(sketch, "E3190", {"start": v(-47.85, 8.35) * mm, "end": v(-47.89, 8.07) * mm});
            skLineSegment(sketch, "E3191", {"start": v(-47.89, 8.07) * mm, "end": v(-47.96, 7.6) * mm});
            skLineSegment(sketch, "E3192", {"start": v(-47.96, 7.6) * mm, "end": v(-48.01, 7.32) * mm});
            skLineSegment(sketch, "E3193", {"start": v(-48.01, 7.32) * mm, "end": v(-48.07, 7.32) * mm});
            skLineSegment(sketch, "E3194", {"start": v(-48.07, 7.32) * mm, "end": v(-48.12, 7.31) * mm});
            skLineSegment(sketch, "E3195", {"start": v(-48.12, 7.31) * mm, "end": v(-48.18, 7.3) * mm});
            skLineSegment(sketch, "E3196", {"start": v(-48.18, 7.3) * mm, "end": v(-48.23, 7.3) * mm});
            skLineSegment(sketch, "E3197", {"start": v(-48.23, 7.3) * mm, "end": v(-48.3, 7.29) * mm});
            skLineSegment(sketch, "E3198", {"start": v(-48.3, 7.29) * mm, "end": v(-48.35, 7.28) * mm});
            skLineSegment(sketch, "E3199", {"start": v(-48.35, 7.28) * mm, "end": v(-48.4, 7.27) * mm});
            skLineSegment(sketch, "E3200", {"start": v(-48.4, 7.27) * mm, "end": v(-48.47, 7.27) * mm});
            skLineSegment(sketch, "E3201", {"start": v(-48.47, 7.27) * mm, "end": v(-48.53, 7.26) * mm});
            skLineSegment(sketch, "E3202", {"start": v(-48.53, 7.26) * mm, "end": v(-48.59, 7.25) * mm});
            skLineSegment(sketch, "E3203", {"start": v(-48.59, 7.25) * mm, "end": v(-48.65, 7.24) * mm});
            skLineSegment(sketch, "E3204", {"start": v(-48.65, 7.24) * mm, "end": v(-48.72, 7.23) * mm});
            skLineSegment(sketch, "E3205", {"start": v(-48.72, 7.23) * mm, "end": v(-48.78, 7.22) * mm});
            skLineSegment(sketch, "E3206", {"start": v(-48.78, 7.22) * mm, "end": v(-48.84, 7.2) * mm});
            skLineSegment(sketch, "E3207", {"start": v(-48.84, 7.2) * mm, "end": v(-48.9, 7.2) * mm});
            skLineSegment(sketch, "E3208", {"start": v(-48.9, 7.2) * mm, "end": v(-48.98, 7.19) * mm});
            skLineSegment(sketch, "E3209", {"start": v(-48.98, 7.19) * mm, "end": v(-49.04, 7.17) * mm});
            skLineSegment(sketch, "E3210", {"start": v(-49.04, 7.17) * mm, "end": v(-49.11, 7.16) * mm});
            skLineSegment(sketch, "E3211", {"start": v(-49.11, 7.16) * mm, "end": v(-49.18, 7.15) * mm});
            skLineSegment(sketch, "E3212", {"start": v(-49.18, 7.15) * mm, "end": v(-49.25, 7.13) * mm});
            skLineSegment(sketch, "E3213", {"start": v(-49.25, 7.13) * mm, "end": v(-49.32, 7.12) * mm});
            skLineSegment(sketch, "E3214", {"start": v(-49.32, 7.12) * mm, "end": v(-49.4, 7.1) * mm});
            skLineSegment(sketch, "E3215", {"start": v(-49.4, 7.1) * mm, "end": v(-49.47, 7.1) * mm});
            skLineSegment(sketch, "E3216", {"start": v(-49.47, 7.1) * mm, "end": v(-49.54, 7.08) * mm});
            skLineSegment(sketch, "E3217", {"start": v(-49.54, 7.08) * mm, "end": v(-49.61, 7.06) * mm});
            skLineSegment(sketch, "E3218", {"start": v(-49.61, 7.06) * mm, "end": v(-49.69, 7.04) * mm});
            skLineSegment(sketch, "E3219", {"start": v(-49.69, 7.04) * mm, "end": v(-49.76, 7.03) * mm});
            skLineSegment(sketch, "E3220", {"start": v(-49.76, 7.03) * mm, "end": v(-49.84, 7) * mm});
            skLineSegment(sketch, "E3221", {"start": v(-49.84, 7) * mm, "end": v(-49.92, 7) * mm});
            skLineSegment(sketch, "E3222", {"start": v(-49.92, 7) * mm, "end": v(-50, 6.97) * mm});
            skLineSegment(sketch, "E3223", {"start": v(-50, 6.97) * mm, "end": v(-50.07, 6.95) * mm});
            skLineSegment(sketch, "E3224", {"start": v(-50.07, 6.95) * mm, "end": v(-50.15, 6.93) * mm});
            skLineSegment(sketch, "E3225", {"start": v(-50.15, 6.93) * mm, "end": v(-50.23, 6.91) * mm});
            skLineSegment(sketch, "E3226", {"start": v(-50.23, 6.91) * mm, "end": v(-50.31, 6.9) * mm});
            skLineSegment(sketch, "E3227", {"start": v(-50.31, 6.9) * mm, "end": v(-50.4, 6.87) * mm});
            skLineSegment(sketch, "E3228", {"start": v(-50.4, 6.87) * mm, "end": v(-50.48, 6.85) * mm});
            skLineSegment(sketch, "E3229", {"start": v(-50.48, 6.85) * mm, "end": v(-50.56, 6.83) * mm});
            skLineSegment(sketch, "E3230", {"start": v(-50.56, 6.83) * mm, "end": v(-50.64, 6.8) * mm});
            skLineSegment(sketch, "E3231", {"start": v(-50.64, 6.8) * mm, "end": v(-50.73, 6.78) * mm});
            skLineSegment(sketch, "E3232", {"start": v(-50.73, 6.78) * mm, "end": v(-50.8, 6.75) * mm});
            skLineSegment(sketch, "E3233", {"start": v(-50.8, 6.75) * mm, "end": v(-50.92, 5.8) * mm});
            skLineSegment(sketch, "E3234", {"start": v(-50.92, 5.8) * mm, "end": v(-50.86, 5.75) * mm});
            skLineSegment(sketch, "E3235", {"start": v(-50.86, 5.75) * mm, "end": v(-50.78, 5.7) * mm});
            skLineSegment(sketch, "E3236", {"start": v(-50.78, 5.7) * mm, "end": v(-50.7, 5.67) * mm});
            skLineSegment(sketch, "E3237", {"start": v(-50.7, 5.67) * mm, "end": v(-50.63, 5.62) * mm});
            skLineSegment(sketch, "E3238", {"start": v(-50.63, 5.62) * mm, "end": v(-50.55, 5.58) * mm});
            skLineSegment(sketch, "E3239", {"start": v(-50.55, 5.58) * mm, "end": v(-50.48, 5.54) * mm});
            skLineSegment(sketch, "E3240", {"start": v(-50.48, 5.54) * mm, "end": v(-50.4, 5.5) * mm});
            skLineSegment(sketch, "E3241", {"start": v(-50.4, 5.5) * mm, "end": v(-50.33, 5.46) * mm});
            skLineSegment(sketch, "E3242", {"start": v(-50.33, 5.46) * mm, "end": v(-50.26, 5.42) * mm});
            skLineSegment(sketch, "E3243", {"start": v(-50.26, 5.42) * mm, "end": v(-50.19, 5.39) * mm});
            skLineSegment(sketch, "E3244", {"start": v(-50.19, 5.39) * mm, "end": v(-50.12, 5.35) * mm});
            skLineSegment(sketch, "E3245", {"start": v(-50.12, 5.35) * mm, "end": v(-50.05, 5.31) * mm});
            skLineSegment(sketch, "E3246", {"start": v(-50.05, 5.31) * mm, "end": v(-49.98, 5.28) * mm});
            skLineSegment(sketch, "E3247", {"start": v(-49.98, 5.28) * mm, "end": v(-49.9, 5.24) * mm});
            skLineSegment(sketch, "E3248", {"start": v(-49.9, 5.24) * mm, "end": v(-49.84, 5.2) * mm});
            skLineSegment(sketch, "E3249", {"start": v(-49.84, 5.2) * mm, "end": v(-49.77, 5.18) * mm});
            skLineSegment(sketch, "E3250", {"start": v(-49.77, 5.18) * mm, "end": v(-49.7, 5.14) * mm});
            skLineSegment(sketch, "E3251", {"start": v(-49.7, 5.14) * mm, "end": v(-49.64, 5.11) * mm});
            skLineSegment(sketch, "E3252", {"start": v(-49.64, 5.11) * mm, "end": v(-49.57, 5.08) * mm});
            skLineSegment(sketch, "E3253", {"start": v(-49.57, 5.08) * mm, "end": v(-49.5, 5.05) * mm});
            skLineSegment(sketch, "E3254", {"start": v(-49.5, 5.05) * mm, "end": v(-49.44, 5.02) * mm});
            skLineSegment(sketch, "E3255", {"start": v(-49.44, 5.02) * mm, "end": v(-49.38, 5) * mm});
            skLineSegment(sketch, "E3256", {"start": v(-49.38, 5) * mm, "end": v(-49.32, 4.96) * mm});
            skLineSegment(sketch, "E3257", {"start": v(-49.32, 4.96) * mm, "end": v(-49.25, 4.93) * mm});
            skLineSegment(sketch, "E3258", {"start": v(-49.25, 4.93) * mm, "end": v(-49.2, 4.9) * mm});
            skLineSegment(sketch, "E3259", {"start": v(-49.2, 4.9) * mm, "end": v(-49.13, 4.88) * mm});
            skLineSegment(sketch, "E3260", {"start": v(-49.13, 4.88) * mm, "end": v(-49.07, 4.85) * mm});
            skLineSegment(sketch, "E3261", {"start": v(-49.07, 4.85) * mm, "end": v(-49.01, 4.83) * mm});
            skLineSegment(sketch, "E3262", {"start": v(-49.01, 4.83) * mm, "end": v(-48.95, 4.8) * mm});
            skLineSegment(sketch, "E3263", {"start": v(-48.95, 4.8) * mm, "end": v(-48.9, 4.78) * mm});
            skLineSegment(sketch, "E3264", {"start": v(-48.9, 4.78) * mm, "end": v(-48.84, 4.75) * mm});
            skLineSegment(sketch, "E3265", {"start": v(-48.84, 4.75) * mm, "end": v(-48.78, 4.73) * mm});
            skLineSegment(sketch, "E3266", {"start": v(-48.78, 4.73) * mm, "end": v(-48.72, 4.7) * mm});
            skLineSegment(sketch, "E3267", {"start": v(-48.72, 4.7) * mm, "end": v(-48.67, 4.69) * mm});
            skLineSegment(sketch, "E3268", {"start": v(-48.67, 4.69) * mm, "end": v(-48.61, 4.67) * mm});
            skLineSegment(sketch, "E3269", {"start": v(-48.61, 4.67) * mm, "end": v(-48.56, 4.64) * mm});
            skLineSegment(sketch, "E3270", {"start": v(-48.56, 4.64) * mm, "end": v(-48.5, 4.62) * mm});
            skLineSegment(sketch, "E3271", {"start": v(-48.5, 4.62) * mm, "end": v(-48.46, 4.6) * mm});
            skLineSegment(sketch, "E3272", {"start": v(-48.46, 4.6) * mm, "end": v(-48.4, 4.59) * mm});
            skLineSegment(sketch, "E3273", {"start": v(-48.4, 4.59) * mm, "end": v(-48.35, 4.57) * mm});
            skLineSegment(sketch, "E3274", {"start": v(-48.35, 4.57) * mm, "end": v(-48.37, 4.29) * mm});
            skLineSegment(sketch, "E3275", {"start": v(-48.37, 4.29) * mm, "end": v(-48.41, 3.81) * mm});
            skLineSegment(sketch, "E3276", {"start": v(-48.41, 3.81) * mm, "end": v(-48.44, 3.53) * mm});
            skLineSegment(sketch, "E3277", {"start": v(-48.44, 3.53) * mm, "end": v(-48.5, 3.52) * mm});
            skLineSegment(sketch, "E3278", {"start": v(-48.5, 3.52) * mm, "end": v(-48.55, 3.51) * mm});
            skLineSegment(sketch, "E3279", {"start": v(-48.55, 3.51) * mm, "end": v(-48.6, 3.5) * mm});
            skLineSegment(sketch, "E3280", {"start": v(-48.6, 3.5) * mm, "end": v(-48.66, 3.49) * mm});
            skLineSegment(sketch, "E3281", {"start": v(-48.66, 3.49) * mm, "end": v(-48.71, 3.48) * mm});
            skLineSegment(sketch, "E3282", {"start": v(-48.71, 3.48) * mm, "end": v(-48.77, 3.47) * mm});
            skLineSegment(sketch, "E3283", {"start": v(-48.77, 3.47) * mm, "end": v(-48.83, 3.45) * mm});
            skLineSegment(sketch, "E3284", {"start": v(-48.83, 3.45) * mm, "end": v(-48.89, 3.44) * mm});
            skLineSegment(sketch, "E3285", {"start": v(-48.89, 3.44) * mm, "end": v(-48.95, 3.43) * mm});
            skLineSegment(sketch, "E3286", {"start": v(-48.95, 3.43) * mm, "end": v(-49, 3.41) * mm});
            skLineSegment(sketch, "E3287", {"start": v(-49, 3.41) * mm, "end": v(-49.07, 3.4) * mm});
            skLineSegment(sketch, "E3288", {"start": v(-49.07, 3.4) * mm, "end": v(-49.13, 3.38) * mm});
            skLineSegment(sketch, "E3289", {"start": v(-49.13, 3.38) * mm, "end": v(-49.2, 3.37) * mm});
            skLineSegment(sketch, "E3290", {"start": v(-49.2, 3.37) * mm, "end": v(-49.26, 3.35) * mm});
            skLineSegment(sketch, "E3291", {"start": v(-49.26, 3.35) * mm, "end": v(-49.32, 3.34) * mm});
            skLineSegment(sketch, "E3292", {"start": v(-49.32, 3.34) * mm, "end": v(-49.39, 3.32) * mm});
            skLineSegment(sketch, "E3293", {"start": v(-49.39, 3.32) * mm, "end": v(-49.46, 3.3) * mm});
            skLineSegment(sketch, "E3294", {"start": v(-49.46, 3.3) * mm, "end": v(-49.52, 3.29) * mm});
            skLineSegment(sketch, "E3295", {"start": v(-49.52, 3.29) * mm, "end": v(-49.6, 3.27) * mm});
            skLineSegment(sketch, "E3296", {"start": v(-49.6, 3.27) * mm, "end": v(-49.66, 3.25) * mm});
            skLineSegment(sketch, "E3297", {"start": v(-49.66, 3.25) * mm, "end": v(-49.73, 3.23) * mm});
            skLineSegment(sketch, "E3298", {"start": v(-49.73, 3.23) * mm, "end": v(-49.8, 3.2) * mm});
            skLineSegment(sketch, "E3299", {"start": v(-49.8, 3.2) * mm, "end": v(-49.87, 3.19) * mm});
            skLineSegment(sketch, "E3300", {"start": v(-49.87, 3.19) * mm, "end": v(-49.94, 3.17) * mm});
            skLineSegment(sketch, "E3301", {"start": v(-49.94, 3.17) * mm, "end": v(-50.01, 3.15) * mm});
            skLineSegment(sketch, "E3302", {"start": v(-50.01, 3.15) * mm, "end": v(-50.09, 3.12) * mm});
            skLineSegment(sketch, "E3303", {"start": v(-50.09, 3.12) * mm, "end": v(-50.16, 3.1) * mm});
            skLineSegment(sketch, "E3304", {"start": v(-50.16, 3.1) * mm, "end": v(-50.24, 3.08) * mm});
            skLineSegment(sketch, "E3305", {"start": v(-50.24, 3.08) * mm, "end": v(-50.31, 3.05) * mm});
            skLineSegment(sketch, "E3306", {"start": v(-50.31, 3.05) * mm, "end": v(-50.39, 3.03) * mm});
            skLineSegment(sketch, "E3307", {"start": v(-50.39, 3.03) * mm, "end": v(-50.46, 3) * mm});
            skLineSegment(sketch, "E3308", {"start": v(-50.46, 3) * mm, "end": v(-50.54, 2.98) * mm});
            skLineSegment(sketch, "E3309", {"start": v(-50.54, 2.98) * mm, "end": v(-50.62, 2.95) * mm});
            skLineSegment(sketch, "E3310", {"start": v(-50.62, 2.95) * mm, "end": v(-50.7, 2.92) * mm});
            skLineSegment(sketch, "E3311", {"start": v(-50.7, 2.92) * mm, "end": v(-50.78, 2.9) * mm});
            skLineSegment(sketch, "E3312", {"start": v(-50.78, 2.9) * mm, "end": v(-50.86, 2.87) * mm});
            skLineSegment(sketch, "E3313", {"start": v(-50.86, 2.87) * mm, "end": v(-50.94, 2.84) * mm});
            skLineSegment(sketch, "E3314", {"start": v(-50.94, 2.84) * mm, "end": v(-51.02, 2.8) * mm});
            skLineSegment(sketch, "E3315", {"start": v(-51.02, 2.8) * mm, "end": v(-51.1, 2.78) * mm});
            skLineSegment(sketch, "E3316", {"start": v(-51.1, 2.78) * mm, "end": v(-51.18, 2.75) * mm});
            skLineSegment(sketch, "E3317", {"start": v(-51.18, 2.75) * mm, "end": v(-51.22, 1.78) * mm});
            skLineSegment(sketch, "E3318", {"start": v(-51.22, 1.78) * mm, "end": v(-51.15, 1.74) * mm});
            skLineSegment(sketch, "E3319", {"start": v(-51.15, 1.74) * mm, "end": v(-51.07, 1.7) * mm});
            skLineSegment(sketch, "E3320", {"start": v(-51.07, 1.7) * mm, "end": v(-51, 1.67) * mm});
            skLineSegment(sketch, "E3321", {"start": v(-51, 1.67) * mm, "end": v(-50.91, 1.63) * mm});
            skLineSegment(sketch, "E3322", {"start": v(-50.91, 1.63) * mm, "end": v(-50.84, 1.6) * mm});
            skLineSegment(sketch, "E3323", {"start": v(-50.84, 1.6) * mm, "end": v(-50.76, 1.56) * mm});
            skLineSegment(sketch, "E3324", {"start": v(-50.76, 1.56) * mm, "end": v(-50.68, 1.53) * mm});
            skLineSegment(sketch, "E3325", {"start": v(-50.68, 1.53) * mm, "end": v(-50.6, 1.5) * mm});
            skLineSegment(sketch, "E3326", {"start": v(-50.6, 1.5) * mm, "end": v(-50.53, 1.46) * mm});
            skLineSegment(sketch, "E3327", {"start": v(-50.53, 1.46) * mm, "end": v(-50.46, 1.43) * mm});
            skLineSegment(sketch, "E3328", {"start": v(-50.46, 1.43) * mm, "end": v(-50.38, 1.4) * mm});
            skLineSegment(sketch, "E3329", {"start": v(-50.38, 1.4) * mm, "end": v(-50.31, 1.37) * mm});
            skLineSegment(sketch, "E3330", {"start": v(-50.31, 1.37) * mm, "end": v(-50.24, 1.34) * mm});
            skLineSegment(sketch, "E3331", {"start": v(-50.24, 1.34) * mm, "end": v(-50.17, 1.31) * mm});
            skLineSegment(sketch, "E3332", {"start": v(-50.17, 1.31) * mm, "end": v(-50.1, 1.28) * mm});
            skLineSegment(sketch, "E3333", {"start": v(-50.1, 1.28) * mm, "end": v(-50.03, 1.26) * mm});
            skLineSegment(sketch, "E3334", {"start": v(-50.03, 1.26) * mm, "end": v(-49.96, 1.23) * mm});
            skLineSegment(sketch, "E3335", {"start": v(-49.96, 1.23) * mm, "end": v(-49.89, 1.2) * mm});
            skLineSegment(sketch, "E3336", {"start": v(-49.89, 1.2) * mm, "end": v(-49.82, 1.18) * mm});
            skLineSegment(sketch, "E3337", {"start": v(-49.82, 1.18) * mm, "end": v(-49.75, 1.15) * mm});
            skLineSegment(sketch, "E3338", {"start": v(-49.75, 1.15) * mm, "end": v(-49.68, 1.12) * mm});
            skLineSegment(sketch, "E3339", {"start": v(-49.68, 1.12) * mm, "end": v(-49.62, 1.1) * mm});
            skLineSegment(sketch, "E3340", {"start": v(-49.62, 1.1) * mm, "end": v(-49.55, 1.08) * mm});
            skLineSegment(sketch, "E3341", {"start": v(-49.55, 1.08) * mm, "end": v(-49.49, 1.05) * mm});
            skLineSegment(sketch, "E3342", {"start": v(-49.49, 1.05) * mm, "end": v(-49.43, 1.03) * mm});
            skLineSegment(sketch, "E3343", {"start": v(-49.43, 1.03) * mm, "end": v(-49.36, 1) * mm});
            skLineSegment(sketch, "E3344", {"start": v(-49.36, 1) * mm, "end": v(-49.3, 0.99) * mm});
            skLineSegment(sketch, "E3345", {"start": v(-49.3, 0.99) * mm, "end": v(-49.24, 0.97) * mm});
            skLineSegment(sketch, "E3346", {"start": v(-49.24, 0.97) * mm, "end": v(-49.18, 0.95) * mm});
            skLineSegment(sketch, "E3347", {"start": v(-49.18, 0.95) * mm, "end": v(-49.12, 0.93) * mm});
            skLineSegment(sketch, "E3348", {"start": v(-49.12, 0.93) * mm, "end": v(-49.06, 0.9) * mm});
            skLineSegment(sketch, "E3349", {"start": v(-49.06, 0.9) * mm, "end": v(-49, 0.89) * mm});
            skLineSegment(sketch, "E3350", {"start": v(-49, 0.89) * mm, "end": v(-48.94, 0.87) * mm});
            skLineSegment(sketch, "E3351", {"start": v(-48.94, 0.87) * mm, "end": v(-48.89, 0.85) * mm});
            skLineSegment(sketch, "E3352", {"start": v(-48.89, 0.85) * mm, "end": v(-48.83, 0.84) * mm});
            skLineSegment(sketch, "E3353", {"start": v(-48.83, 0.84) * mm, "end": v(-48.78, 0.82) * mm});
            skLineSegment(sketch, "E3354", {"start": v(-48.78, 0.82) * mm, "end": v(-48.72, 0.8) * mm});
            skLineSegment(sketch, "E3355", {"start": v(-48.72, 0.8) * mm, "end": v(-48.67, 0.79) * mm});
            skLineSegment(sketch, "E3356", {"start": v(-48.67, 0.79) * mm, "end": v(-48.61, 0.77) * mm});
            skLineSegment(sketch, "E3357", {"start": v(-48.61, 0.77) * mm, "end": v(-48.56, 0.76) * mm});
            skLineSegment(sketch, "E3358", {"start": v(-48.56, 0.76) * mm, "end": v(-48.56, 0.48) * mm});
            skLineSegment(sketch, "E3359", {"start": v(-48.56, 0.48) * mm, "end": v(-48.56, 0) * mm});
            skLineSegment(sketch, "E3360", {"start": v(-48.56, 0) * mm, "end": v(-48.57, -0.28) * mm});
            skLineSegment(sketch, "E3361", {"start": v(-48.57, -0.28) * mm, "end": v(-48.62, -0.3) * mm});
            skLineSegment(sketch, "E3362", {"start": v(-48.62, -0.3) * mm, "end": v(-48.67, -0.3) * mm});
            skLineSegment(sketch, "E3363", {"start": v(-48.67, -0.3) * mm, "end": v(-48.73, -0.32) * mm});
            skLineSegment(sketch, "E3364", {"start": v(-48.73, -0.32) * mm, "end": v(-48.78, -0.34) * mm});
            skLineSegment(sketch, "E3365", {"start": v(-48.78, -0.34) * mm, "end": v(-48.84, -0.35) * mm});
            skLineSegment(sketch, "E3366", {"start": v(-48.84, -0.35) * mm, "end": v(-48.9, -0.37) * mm});
            skLineSegment(sketch, "E3367", {"start": v(-48.9, -0.37) * mm, "end": v(-48.95, -0.39) * mm});
            skLineSegment(sketch, "E3368", {"start": v(-48.95, -0.39) * mm, "end": v(-49, -0.4) * mm});
            skLineSegment(sketch, "E3369", {"start": v(-49, -0.4) * mm, "end": v(-49.07, -0.42) * mm});
            skLineSegment(sketch, "E3370", {"start": v(-49.07, -0.42) * mm, "end": v(-49.13, -0.44) * mm});
            skLineSegment(sketch, "E3371", {"start": v(-49.13, -0.44) * mm, "end": v(-49.19, -0.46) * mm});
            skLineSegment(sketch, "E3372", {"start": v(-49.19, -0.46) * mm, "end": v(-49.25, -0.48) * mm});
            skLineSegment(sketch, "E3373", {"start": v(-49.25, -0.48) * mm, "end": v(-49.3, -0.5) * mm});
            skLineSegment(sketch, "E3374", {"start": v(-49.3, -0.5) * mm, "end": v(-49.37, -0.52) * mm});
            skLineSegment(sketch, "E3375", {"start": v(-49.37, -0.52) * mm, "end": v(-49.43, -0.54) * mm});
            skLineSegment(sketch, "E3376", {"start": v(-49.43, -0.54) * mm, "end": v(-49.5, -0.56) * mm});
            skLineSegment(sketch, "E3377", {"start": v(-49.5, -0.56) * mm, "end": v(-49.56, -0.59) * mm});
            skLineSegment(sketch, "E3378", {"start": v(-49.56, -0.59) * mm, "end": v(-49.63, -0.61) * mm});
            skLineSegment(sketch, "E3379", {"start": v(-49.63, -0.61) * mm, "end": v(-49.7, -0.63) * mm});
            skLineSegment(sketch, "E3380", {"start": v(-49.7, -0.63) * mm, "end": v(-49.76, -0.66) * mm});
            skLineSegment(sketch, "E3381", {"start": v(-49.76, -0.66) * mm, "end": v(-49.83, -0.68) * mm});
            skLineSegment(sketch, "E3382", {"start": v(-49.83, -0.68) * mm, "end": v(-49.9, -0.7) * mm});
            skLineSegment(sketch, "E3383", {"start": v(-49.9, -0.7) * mm, "end": v(-49.97, -0.73) * mm});
            skLineSegment(sketch, "E3384", {"start": v(-49.97, -0.73) * mm, "end": v(-50.04, -0.76) * mm});
            skLineSegment(sketch, "E3385", {"start": v(-50.04, -0.76) * mm, "end": v(-50.1, -0.79) * mm});
            skLineSegment(sketch, "E3386", {"start": v(-50.1, -0.79) * mm, "end": v(-50.18, -0.82) * mm});
            skLineSegment(sketch, "E3387", {"start": v(-50.18, -0.82) * mm, "end": v(-50.25, -0.84) * mm});
            skLineSegment(sketch, "E3388", {"start": v(-50.25, -0.84) * mm, "end": v(-50.32, -0.87) * mm});
            skLineSegment(sketch, "E3389", {"start": v(-50.32, -0.87) * mm, "end": v(-50.4, -0.9) * mm});
            skLineSegment(sketch, "E3390", {"start": v(-50.4, -0.9) * mm, "end": v(-50.47, -0.93) * mm});
            skLineSegment(sketch, "E3391", {"start": v(-50.47, -0.93) * mm, "end": v(-50.54, -0.97) * mm});
            skLineSegment(sketch, "E3392", {"start": v(-50.54, -0.97) * mm, "end": v(-50.62, -1) * mm});
            skLineSegment(sketch, "E3393", {"start": v(-50.62, -1) * mm, "end": v(-50.7, -1.03) * mm});
            skLineSegment(sketch, "E3394", {"start": v(-50.7, -1.03) * mm, "end": v(-50.77, -1.06) * mm});
            skLineSegment(sketch, "E3395", {"start": v(-50.77, -1.06) * mm, "end": v(-50.85, -1.1) * mm});
            skLineSegment(sketch, "E3396", {"start": v(-50.85, -1.1) * mm, "end": v(-50.93, -1.13) * mm});
            skLineSegment(sketch, "E3397", {"start": v(-50.93, -1.13) * mm, "end": v(-51, -1.17) * mm});
            skLineSegment(sketch, "E3398", {"start": v(-51, -1.17) * mm, "end": v(-51.09, -1.2) * mm});
            skLineSegment(sketch, "E3399", {"start": v(-51.09, -1.2) * mm, "end": v(-51.17, -1.24) * mm});
            skLineSegment(sketch, "E3400", {"start": v(-51.17, -1.24) * mm, "end": v(-51.23, -1.28) * mm});
            skLineSegment(sketch, "E3401", {"start": v(-51.23, -1.28) * mm, "end": v(-51.2, -2.24) * mm});
            skLineSegment(sketch, "E3402", {"start": v(-51.2, -2.24) * mm, "end": v(-51.13, -2.27) * mm});
            skLineSegment(sketch, "E3403", {"start": v(-51.13, -2.27) * mm, "end": v(-51.05, -2.3) * mm});
            skLineSegment(sketch, "E3404", {"start": v(-51.05, -2.3) * mm, "end": v(-50.97, -2.34) * mm});
            skLineSegment(sketch, "E3405", {"start": v(-50.97, -2.34) * mm, "end": v(-50.89, -2.37) * mm});
            skLineSegment(sketch, "E3406", {"start": v(-50.89, -2.37) * mm, "end": v(-50.8, -2.4) * mm});
            skLineSegment(sketch, "E3407", {"start": v(-50.8, -2.4) * mm, "end": v(-50.73, -2.42) * mm});
            skLineSegment(sketch, "E3408", {"start": v(-50.73, -2.42) * mm, "end": v(-50.65, -2.45) * mm});
            skLineSegment(sketch, "E3409", {"start": v(-50.65, -2.45) * mm, "end": v(-50.57, -2.48) * mm});
            skLineSegment(sketch, "E3410", {"start": v(-50.57, -2.48) * mm, "end": v(-50.5, -2.5) * mm});
            skLineSegment(sketch, "E3411", {"start": v(-50.5, -2.5) * mm, "end": v(-50.41, -2.53) * mm});
            skLineSegment(sketch, "E3412", {"start": v(-50.41, -2.53) * mm, "end": v(-50.34, -2.56) * mm});
            skLineSegment(sketch, "E3413", {"start": v(-50.34, -2.56) * mm, "end": v(-50.26, -2.58) * mm});
            skLineSegment(sketch, "E3414", {"start": v(-50.26, -2.58) * mm, "end": v(-50.19, -2.6) * mm});
            skLineSegment(sketch, "E3415", {"start": v(-50.19, -2.6) * mm, "end": v(-50.11, -2.63) * mm});
            skLineSegment(sketch, "E3416", {"start": v(-50.11, -2.63) * mm, "end": v(-50.04, -2.65) * mm});
            skLineSegment(sketch, "E3417", {"start": v(-50.04, -2.65) * mm, "end": v(-49.97, -2.67) * mm});
            skLineSegment(sketch, "E3418", {"start": v(-49.97, -2.67) * mm, "end": v(-49.9, -2.7) * mm});
            skLineSegment(sketch, "E3419", {"start": v(-49.9, -2.7) * mm, "end": v(-49.83, -2.72) * mm});
            skLineSegment(sketch, "E3420", {"start": v(-49.83, -2.72) * mm, "end": v(-49.76, -2.74) * mm});
            skLineSegment(sketch, "E3421", {"start": v(-49.76, -2.74) * mm, "end": v(-49.69, -2.76) * mm});
            skLineSegment(sketch, "E3422", {"start": v(-49.69, -2.76) * mm, "end": v(-49.62, -2.78) * mm});
            skLineSegment(sketch, "E3423", {"start": v(-49.62, -2.78) * mm, "end": v(-49.55, -2.8) * mm});
            skLineSegment(sketch, "E3424", {"start": v(-49.55, -2.8) * mm, "end": v(-49.49, -2.81) * mm});
            skLineSegment(sketch, "E3425", {"start": v(-49.49, -2.81) * mm, "end": v(-49.42, -2.83) * mm});
            skLineSegment(sketch, "E3426", {"start": v(-49.42, -2.83) * mm, "end": v(-49.35, -2.85) * mm});
            skLineSegment(sketch, "E3427", {"start": v(-49.35, -2.85) * mm, "end": v(-49.29, -2.87) * mm});
            skLineSegment(sketch, "E3428", {"start": v(-49.29, -2.87) * mm, "end": v(-49.23, -2.88) * mm});
            skLineSegment(sketch, "E3429", {"start": v(-49.23, -2.88) * mm, "end": v(-49.16, -2.9) * mm});
            skLineSegment(sketch, "E3430", {"start": v(-49.16, -2.9) * mm, "end": v(-49.1, -2.91) * mm});
            skLineSegment(sketch, "E3431", {"start": v(-49.1, -2.91) * mm, "end": v(-49.04, -2.93) * mm});
            skLineSegment(sketch, "E3432", {"start": v(-49.04, -2.93) * mm, "end": v(-48.98, -2.94) * mm});
            skLineSegment(sketch, "E3433", {"start": v(-48.98, -2.94) * mm, "end": v(-48.92, -2.96) * mm});
            skLineSegment(sketch, "E3434", {"start": v(-48.92, -2.96) * mm, "end": v(-48.86, -2.97) * mm});
            skLineSegment(sketch, "E3435", {"start": v(-48.86, -2.97) * mm, "end": v(-48.8, -2.98) * mm});
            skLineSegment(sketch, "E3436", {"start": v(-48.8, -2.98) * mm, "end": v(-48.75, -3) * mm});
            skLineSegment(sketch, "E3437", {"start": v(-48.75, -3) * mm, "end": v(-48.69, -3) * mm});
            skLineSegment(sketch, "E3438", {"start": v(-48.69, -3) * mm, "end": v(-48.63, -3.02) * mm});
            skLineSegment(sketch, "E3439", {"start": v(-48.63, -3.02) * mm, "end": v(-48.58, -3.03) * mm});
            skLineSegment(sketch, "E3440", {"start": v(-48.58, -3.03) * mm, "end": v(-48.53, -3.04) * mm});
            skLineSegment(sketch, "E3441", {"start": v(-48.53, -3.04) * mm, "end": v(-48.47, -3.05) * mm});
            skLineSegment(sketch, "E3442", {"start": v(-48.47, -3.05) * mm, "end": v(-48.45, -3.33) * mm});
            skLineSegment(sketch, "E3443", {"start": v(-48.45, -3.33) * mm, "end": v(-48.41, -3.81) * mm});
            skLineSegment(sketch, "E3444", {"start": v(-48.41, -3.81) * mm, "end": v(-48.4, -4.09) * mm});
            skLineSegment(sketch, "E3445", {"start": v(-48.4, -4.09) * mm, "end": v(-48.45, -4.1) * mm});
            skLineSegment(sketch, "E3446", {"start": v(-48.45, -4.1) * mm, "end": v(-48.5, -4.13) * mm});
            skLineSegment(sketch, "E3447", {"start": v(-48.5, -4.13) * mm, "end": v(-48.55, -4.14) * mm});
            skLineSegment(sketch, "E3448", {"start": v(-48.55, -4.14) * mm, "end": v(-48.6, -4.16) * mm});
            skLineSegment(sketch, "E3449", {"start": v(-48.6, -4.16) * mm, "end": v(-48.66, -4.19) * mm});
            skLineSegment(sketch, "E3450", {"start": v(-48.66, -4.19) * mm, "end": v(-48.71, -4.2) * mm});
            skLineSegment(sketch, "E3451", {"start": v(-48.71, -4.2) * mm, "end": v(-48.77, -4.23) * mm});
            skLineSegment(sketch, "E3452", {"start": v(-48.77, -4.23) * mm, "end": v(-48.82, -4.25) * mm});
            skLineSegment(sketch, "E3453", {"start": v(-48.82, -4.25) * mm, "end": v(-48.88, -4.27) * mm});
            skLineSegment(sketch, "E3454", {"start": v(-48.88, -4.27) * mm, "end": v(-48.94, -4.3) * mm});
            skLineSegment(sketch, "E3455", {"start": v(-48.94, -4.3) * mm, "end": v(-49, -4.32) * mm});
            skLineSegment(sketch, "E3456", {"start": v(-49, -4.32) * mm, "end": v(-49.06, -4.34) * mm});
            skLineSegment(sketch, "E3457", {"start": v(-49.06, -4.34) * mm, "end": v(-49.12, -4.37) * mm});
            skLineSegment(sketch, "E3458", {"start": v(-49.12, -4.37) * mm, "end": v(-49.18, -4.4) * mm});
            skLineSegment(sketch, "E3459", {"start": v(-49.18, -4.4) * mm, "end": v(-49.24, -4.42) * mm});
            skLineSegment(sketch, "E3460", {"start": v(-49.24, -4.42) * mm, "end": v(-49.3, -4.45) * mm});
            skLineSegment(sketch, "E3461", {"start": v(-49.3, -4.45) * mm, "end": v(-49.36, -4.47) * mm});
            skLineSegment(sketch, "E3462", {"start": v(-49.36, -4.47) * mm, "end": v(-49.43, -4.5) * mm});
            skLineSegment(sketch, "E3463", {"start": v(-49.43, -4.5) * mm, "end": v(-49.5, -4.53) * mm});
            skLineSegment(sketch, "E3464", {"start": v(-49.5, -4.53) * mm, "end": v(-49.56, -4.56) * mm});
            skLineSegment(sketch, "E3465", {"start": v(-49.56, -4.56) * mm, "end": v(-49.62, -4.6) * mm});
            skLineSegment(sketch, "E3466", {"start": v(-49.62, -4.6) * mm, "end": v(-49.69, -4.62) * mm});
            skLineSegment(sketch, "E3467", {"start": v(-49.69, -4.62) * mm, "end": v(-49.75, -4.65) * mm});
            skLineSegment(sketch, "E3468", {"start": v(-49.75, -4.65) * mm, "end": v(-49.82, -4.68) * mm});
            skLineSegment(sketch, "E3469", {"start": v(-49.82, -4.68) * mm, "end": v(-49.89, -4.72) * mm});
            skLineSegment(sketch, "E3470", {"start": v(-49.89, -4.72) * mm, "end": v(-49.96, -4.75) * mm});
            skLineSegment(sketch, "E3471", {"start": v(-49.96, -4.75) * mm, "end": v(-50.03, -4.78) * mm});
            skLineSegment(sketch, "E3472", {"start": v(-50.03, -4.78) * mm, "end": v(-50.1, -4.82) * mm});
            skLineSegment(sketch, "E3473", {"start": v(-50.1, -4.82) * mm, "end": v(-50.17, -4.85) * mm});
            skLineSegment(sketch, "E3474", {"start": v(-50.17, -4.85) * mm, "end": v(-50.24, -4.9) * mm});
            skLineSegment(sketch, "E3475", {"start": v(-50.24, -4.9) * mm, "end": v(-50.31, -4.93) * mm});
            skLineSegment(sketch, "E3476", {"start": v(-50.31, -4.93) * mm, "end": v(-50.38, -4.97) * mm});
            skLineSegment(sketch, "E3477", {"start": v(-50.38, -4.97) * mm, "end": v(-50.46, -5) * mm});
            skLineSegment(sketch, "E3478", {"start": v(-50.46, -5) * mm, "end": v(-50.53, -5.04) * mm});
            skLineSegment(sketch, "E3479", {"start": v(-50.53, -5.04) * mm, "end": v(-50.6, -5.08) * mm});
            skLineSegment(sketch, "E3480", {"start": v(-50.6, -5.08) * mm, "end": v(-50.68, -5.12) * mm});
            skLineSegment(sketch, "E3481", {"start": v(-50.68, -5.12) * mm, "end": v(-50.76, -5.16) * mm});
            skLineSegment(sketch, "E3482", {"start": v(-50.76, -5.16) * mm, "end": v(-50.83, -5.2) * mm});
            skLineSegment(sketch, "E3483", {"start": v(-50.83, -5.2) * mm, "end": v(-50.91, -5.25) * mm});
            skLineSegment(sketch, "E3484", {"start": v(-50.91, -5.25) * mm, "end": v(-50.98, -5.3) * mm});
            skLineSegment(sketch, "E3485", {"start": v(-50.98, -5.3) * mm, "end": v(-50.87, -6.25) * mm});
            skLineSegment(sketch, "E3486", {"start": v(-50.87, -6.25) * mm, "end": v(-50.8, -6.28) * mm});
            skLineSegment(sketch, "E3487", {"start": v(-50.8, -6.28) * mm, "end": v(-50.7, -6.3) * mm});
            skLineSegment(sketch, "E3488", {"start": v(-50.7, -6.3) * mm, "end": v(-50.63, -6.33) * mm});
            skLineSegment(sketch, "E3489", {"start": v(-50.63, -6.33) * mm, "end": v(-50.54, -6.35) * mm});
            skLineSegment(sketch, "E3490", {"start": v(-50.54, -6.35) * mm, "end": v(-50.46, -6.37) * mm});
            skLineSegment(sketch, "E3491", {"start": v(-50.46, -6.37) * mm, "end": v(-50.38, -6.4) * mm});
            skLineSegment(sketch, "E3492", {"start": v(-50.38, -6.4) * mm, "end": v(-50.3, -6.42) * mm});
            skLineSegment(sketch, "E3493", {"start": v(-50.3, -6.42) * mm, "end": v(-50.22, -6.44) * mm});
            skLineSegment(sketch, "E3494", {"start": v(-50.22, -6.44) * mm, "end": v(-50.14, -6.46) * mm});
            skLineSegment(sketch, "E3495", {"start": v(-50.14, -6.46) * mm, "end": v(-50.06, -6.48) * mm});
            skLineSegment(sketch, "E3496", {"start": v(-50.06, -6.48) * mm, "end": v(-49.98, -6.5) * mm});
            skLineSegment(sketch, "E3497", {"start": v(-49.98, -6.5) * mm, "end": v(-49.9, -6.52) * mm});
            skLineSegment(sketch, "E3498", {"start": v(-49.9, -6.52) * mm, "end": v(-49.83, -6.53) * mm});
            skLineSegment(sketch, "E3499", {"start": v(-49.83, -6.53) * mm, "end": v(-49.75, -6.55) * mm});
            skLineSegment(sketch, "E3500", {"start": v(-49.75, -6.55) * mm, "end": v(-49.68, -6.57) * mm});
            skLineSegment(sketch, "E3501", {"start": v(-49.68, -6.57) * mm, "end": v(-49.6, -6.59) * mm});
            skLineSegment(sketch, "E3502", {"start": v(-49.6, -6.59) * mm, "end": v(-49.53, -6.6) * mm});
            skLineSegment(sketch, "E3503", {"start": v(-49.53, -6.6) * mm, "end": v(-49.46, -6.62) * mm});
            skLineSegment(sketch, "E3504", {"start": v(-49.46, -6.62) * mm, "end": v(-49.39, -6.63) * mm});
            skLineSegment(sketch, "E3505", {"start": v(-49.39, -6.63) * mm, "end": v(-49.32, -6.65) * mm});
            skLineSegment(sketch, "E3506", {"start": v(-49.32, -6.65) * mm, "end": v(-49.25, -6.66) * mm});
            skLineSegment(sketch, "E3507", {"start": v(-49.25, -6.66) * mm, "end": v(-49.18, -6.67) * mm});
            skLineSegment(sketch, "E3508", {"start": v(-49.18, -6.67) * mm, "end": v(-49.11, -6.69) * mm});
            skLineSegment(sketch, "E3509", {"start": v(-49.11, -6.69) * mm, "end": v(-49.05, -6.7) * mm});
            skLineSegment(sketch, "E3510", {"start": v(-49.05, -6.7) * mm, "end": v(-48.98, -6.71) * mm});
            skLineSegment(sketch, "E3511", {"start": v(-48.98, -6.71) * mm, "end": v(-48.91, -6.72) * mm});
            skLineSegment(sketch, "E3512", {"start": v(-48.91, -6.72) * mm, "end": v(-48.85, -6.74) * mm});
            skLineSegment(sketch, "E3513", {"start": v(-48.85, -6.74) * mm, "end": v(-48.78, -6.75) * mm});
            skLineSegment(sketch, "E3514", {"start": v(-48.78, -6.75) * mm, "end": v(-48.72, -6.76) * mm});
            skLineSegment(sketch, "E3515", {"start": v(-48.72, -6.76) * mm, "end": v(-48.66, -6.77) * mm});
            skLineSegment(sketch, "E3516", {"start": v(-48.66, -6.77) * mm, "end": v(-48.6, -6.78) * mm});
            skLineSegment(sketch, "E3517", {"start": v(-48.6, -6.78) * mm, "end": v(-48.54, -6.79) * mm});
            skLineSegment(sketch, "E3518", {"start": v(-48.54, -6.79) * mm, "end": v(-48.48, -6.8) * mm});
            skLineSegment(sketch, "E3519", {"start": v(-48.48, -6.8) * mm, "end": v(-48.42, -6.8) * mm});
            skLineSegment(sketch, "E3520", {"start": v(-48.42, -6.8) * mm, "end": v(-48.36, -6.81) * mm});
            skLineSegment(sketch, "E3521", {"start": v(-48.36, -6.81) * mm, "end": v(-48.3, -6.82) * mm});
            skLineSegment(sketch, "E3522", {"start": v(-48.3, -6.82) * mm, "end": v(-48.25, -6.83) * mm});
            skLineSegment(sketch, "E3523", {"start": v(-48.25, -6.83) * mm, "end": v(-48.2, -6.83) * mm});
            skLineSegment(sketch, "E3524", {"start": v(-48.2, -6.83) * mm, "end": v(-48.14, -6.84) * mm});
            skLineSegment(sketch, "E3525", {"start": v(-48.14, -6.84) * mm, "end": v(-48.08, -6.85) * mm});
            skLineSegment(sketch, "E3526", {"start": v(-48.08, -6.85) * mm, "end": v(-48.04, -7.12) * mm});
            skLineSegment(sketch, "E3527", {"start": v(-48.04, -7.12) * mm, "end": v(-47.96, -7.6) * mm});
            skLineSegment(sketch, "E3528", {"start": v(-47.96, -7.6) * mm, "end": v(-47.93, -7.87) * mm});
            skLineSegment(sketch, "E3529", {"start": v(-47.93, -7.87) * mm, "end": v(-47.98, -7.9) * mm});
            skLineSegment(sketch, "E3530", {"start": v(-47.98, -7.9) * mm, "end": v(-48.03, -7.92) * mm});
            skLineSegment(sketch, "E3531", {"start": v(-48.03, -7.92) * mm, "end": v(-48.08, -7.94) * mm});
            skLineSegment(sketch, "E3532", {"start": v(-48.08, -7.94) * mm, "end": v(-48.13, -7.97) * mm});
            skLineSegment(sketch, "E3533", {"start": v(-48.13, -7.97) * mm, "end": v(-48.18, -7.99) * mm});
            skLineSegment(sketch, "E3534", {"start": v(-48.18, -7.99) * mm, "end": v(-48.23, -8.01) * mm});
            skLineSegment(sketch, "E3535", {"start": v(-48.23, -8.01) * mm, "end": v(-48.29, -8.04) * mm});
            skLineSegment(sketch, "E3536", {"start": v(-48.29, -8.04) * mm, "end": v(-48.34, -8.07) * mm});
            skLineSegment(sketch, "E3537", {"start": v(-48.34, -8.07) * mm, "end": v(-48.4, -8.1) * mm});
            skLineSegment(sketch, "E3538", {"start": v(-48.4, -8.1) * mm, "end": v(-48.45, -8.12) * mm});
            skLineSegment(sketch, "E3539", {"start": v(-48.45, -8.12) * mm, "end": v(-48.5, -8.15) * mm});
            skLineSegment(sketch, "E3540", {"start": v(-48.5, -8.15) * mm, "end": v(-48.56, -8.18) * mm});
            skLineSegment(sketch, "E3541", {"start": v(-48.56, -8.18) * mm, "end": v(-48.62, -8.2) * mm});
            skLineSegment(sketch, "E3542", {"start": v(-48.62, -8.2) * mm, "end": v(-48.68, -8.24) * mm});
            skLineSegment(sketch, "E3543", {"start": v(-48.68, -8.24) * mm, "end": v(-48.74, -8.27) * mm});
            skLineSegment(sketch, "E3544", {"start": v(-48.74, -8.27) * mm, "end": v(-48.8, -8.3) * mm});
            skLineSegment(sketch, "E3545", {"start": v(-48.8, -8.3) * mm, "end": v(-48.86, -8.33) * mm});
            skLineSegment(sketch, "E3546", {"start": v(-48.86, -8.33) * mm, "end": v(-48.92, -8.37) * mm});
            skLineSegment(sketch, "E3547", {"start": v(-48.92, -8.37) * mm, "end": v(-48.98, -8.4) * mm});
            skLineSegment(sketch, "E3548", {"start": v(-48.98, -8.4) * mm, "end": v(-49.04, -8.43) * mm});
            skLineSegment(sketch, "E3549", {"start": v(-49.04, -8.43) * mm, "end": v(-49.1, -8.47) * mm});
            skLineSegment(sketch, "E3550", {"start": v(-49.1, -8.47) * mm, "end": v(-49.17, -8.5) * mm});
            skLineSegment(sketch, "E3551", {"start": v(-49.17, -8.5) * mm, "end": v(-49.24, -8.54) * mm});
            skLineSegment(sketch, "E3552", {"start": v(-49.24, -8.54) * mm, "end": v(-49.3, -8.58) * mm});
            skLineSegment(sketch, "E3553", {"start": v(-49.3, -8.58) * mm, "end": v(-49.37, -8.62) * mm});
            skLineSegment(sketch, "E3554", {"start": v(-49.37, -8.62) * mm, "end": v(-49.43, -8.66) * mm});
            skLineSegment(sketch, "E3555", {"start": v(-49.43, -8.66) * mm, "end": v(-49.5, -8.7) * mm});
            skLineSegment(sketch, "E3556", {"start": v(-49.5, -8.7) * mm, "end": v(-49.57, -8.73) * mm});
            skLineSegment(sketch, "E3557", {"start": v(-49.57, -8.73) * mm, "end": v(-49.63, -8.78) * mm});
            skLineSegment(sketch, "E3558", {"start": v(-49.63, -8.78) * mm, "end": v(-49.7, -8.82) * mm});
            skLineSegment(sketch, "E3559", {"start": v(-49.7, -8.82) * mm, "end": v(-49.77, -8.86) * mm});
            skLineSegment(sketch, "E3560", {"start": v(-49.77, -8.86) * mm, "end": v(-49.84, -8.9) * mm});
            skLineSegment(sketch, "E3561", {"start": v(-49.84, -8.9) * mm, "end": v(-49.91, -8.95) * mm});
            skLineSegment(sketch, "E3562", {"start": v(-49.91, -8.95) * mm, "end": v(-49.98, -9) * mm});
            skLineSegment(sketch, "E3563", {"start": v(-49.98, -9) * mm, "end": v(-50.05, -9.04) * mm});
            skLineSegment(sketch, "E3564", {"start": v(-50.05, -9.04) * mm, "end": v(-50.12, -9.08) * mm});
            skLineSegment(sketch, "E3565", {"start": v(-50.12, -9.08) * mm, "end": v(-50.2, -9.13) * mm});
            skLineSegment(sketch, "E3566", {"start": v(-50.2, -9.13) * mm, "end": v(-50.27, -9.18) * mm});
            skLineSegment(sketch, "E3567", {"start": v(-50.27, -9.18) * mm, "end": v(-50.34, -9.23) * mm});
            skLineSegment(sketch, "E3568", {"start": v(-50.34, -9.23) * mm, "end": v(-50.4, -9.28) * mm});
            skLineSegment(sketch, "E3569", {"start": v(-50.4, -9.28) * mm, "end": v(-50.22, -10.22) * mm});
            skLineSegment(sketch, "E3570", {"start": v(-50.22, -10.22) * mm, "end": v(-50.15, -10.24) * mm});
            skLineSegment(sketch, "E3571", {"start": v(-50.15, -10.24) * mm, "end": v(-50.06, -10.26) * mm});
            skLineSegment(sketch, "E3572", {"start": v(-50.06, -10.26) * mm, "end": v(-49.97, -10.28) * mm});
            skLineSegment(sketch, "E3573", {"start": v(-49.97, -10.28) * mm, "end": v(-49.89, -10.3) * mm});
            skLineSegment(sketch, "E3574", {"start": v(-49.89, -10.3) * mm, "end": v(-49.8, -10.31) * mm});
            skLineSegment(sketch, "E3575", {"start": v(-49.8, -10.31) * mm, "end": v(-49.72, -10.33) * mm});
            skLineSegment(sketch, "E3576", {"start": v(-49.72, -10.33) * mm, "end": v(-49.64, -10.34) * mm});
            skLineSegment(sketch, "E3577", {"start": v(-49.64, -10.34) * mm, "end": v(-49.56, -10.36) * mm});
            skLineSegment(sketch, "E3578", {"start": v(-49.56, -10.36) * mm, "end": v(-49.48, -10.37) * mm});
            skLineSegment(sketch, "E3579", {"start": v(-49.48, -10.37) * mm, "end": v(-49.4, -10.39) * mm});
            skLineSegment(sketch, "E3580", {"start": v(-49.4, -10.39) * mm, "end": v(-49.32, -10.4) * mm});
            skLineSegment(sketch, "E3581", {"start": v(-49.32, -10.4) * mm, "end": v(-49.24, -10.41) * mm});
            skLineSegment(sketch, "E3582", {"start": v(-49.24, -10.41) * mm, "end": v(-49.16, -10.42) * mm});
            skLineSegment(sketch, "E3583", {"start": v(-49.16, -10.42) * mm, "end": v(-49.09, -10.44) * mm});
            skLineSegment(sketch, "E3584", {"start": v(-49.09, -10.44) * mm, "end": v(-49.01, -10.45) * mm});
            skLineSegment(sketch, "E3585", {"start": v(-49.01, -10.45) * mm, "end": v(-48.94, -10.46) * mm});
            skLineSegment(sketch, "E3586", {"start": v(-48.94, -10.46) * mm, "end": v(-48.86, -10.47) * mm});
            skLineSegment(sketch, "E3587", {"start": v(-48.86, -10.47) * mm, "end": v(-48.79, -10.48) * mm});
            skLineSegment(sketch, "E3588", {"start": v(-48.79, -10.48) * mm, "end": v(-48.72, -10.49) * mm});
            skLineSegment(sketch, "E3589", {"start": v(-48.72, -10.49) * mm, "end": v(-48.65, -10.5) * mm});
            skLineSegment(sketch, "E3590", {"start": v(-48.65, -10.5) * mm, "end": v(-48.57, -10.5) * mm});
            skLineSegment(sketch, "E3591", {"start": v(-48.57, -10.5) * mm, "end": v(-48.5, -10.51) * mm});
            skLineSegment(sketch, "E3592", {"start": v(-48.5, -10.51) * mm, "end": v(-48.44, -10.52) * mm});
            skLineSegment(sketch, "E3593", {"start": v(-48.44, -10.52) * mm, "end": v(-48.37, -10.53) * mm});
            skLineSegment(sketch, "E3594", {"start": v(-48.37, -10.53) * mm, "end": v(-48.3, -10.54) * mm});
            skLineSegment(sketch, "E3595", {"start": v(-48.3, -10.54) * mm, "end": v(-48.23, -10.54) * mm});
            skLineSegment(sketch, "E3596", {"start": v(-48.23, -10.54) * mm, "end": v(-48.17, -10.55) * mm});
            skLineSegment(sketch, "E3597", {"start": v(-48.17, -10.55) * mm, "end": v(-48.1, -10.55) * mm});
            skLineSegment(sketch, "E3598", {"start": v(-48.1, -10.55) * mm, "end": v(-48.04, -10.56) * mm});
            skLineSegment(sketch, "E3599", {"start": v(-48.04, -10.56) * mm, "end": v(-47.98, -10.56) * mm});
            skLineSegment(sketch, "E3600", {"start": v(-47.98, -10.56) * mm, "end": v(-47.92, -10.57) * mm});
            skLineSegment(sketch, "E3601", {"start": v(-47.92, -10.57) * mm, "end": v(-47.85, -10.57) * mm});
            skLineSegment(sketch, "E3602", {"start": v(-47.85, -10.57) * mm, "end": v(-47.8, -10.58) * mm});
            skLineSegment(sketch, "E3603", {"start": v(-47.8, -10.58) * mm, "end": v(-47.74, -10.58) * mm});
            skLineSegment(sketch, "E3604", {"start": v(-47.74, -10.58) * mm, "end": v(-47.68, -10.59) * mm});
            skLineSegment(sketch, "E3605", {"start": v(-47.68, -10.59) * mm, "end": v(-47.62, -10.59) * mm});
            skLineSegment(sketch, "E3606", {"start": v(-47.62, -10.59) * mm, "end": v(-47.56, -10.6) * mm});
            skLineSegment(sketch, "E3607", {"start": v(-47.56, -10.6) * mm, "end": v(-47.5, -10.6) * mm});
            skLineSegment(sketch, "E3608", {"start": v(-47.5, -10.6) * mm, "end": v(-47.45, -10.6) * mm});
            skLineSegment(sketch, "E3609", {"start": v(-47.45, -10.6) * mm, "end": v(-47.4, -10.6) * mm});
            skLineSegment(sketch, "E3610", {"start": v(-47.4, -10.6) * mm, "end": v(-47.33, -10.87) * mm});
            skLineSegment(sketch, "E3611", {"start": v(-47.33, -10.87) * mm, "end": v(-47.22, -11.34) * mm});
            skLineSegment(sketch, "E3612", {"start": v(-47.22, -11.34) * mm, "end": v(-47.16, -11.6) * mm});
            skLineSegment(sketch, "E3613", {"start": v(-47.16, -11.6) * mm, "end": v(-47.2, -11.64) * mm});
            skLineSegment(sketch, "E3614", {"start": v(-47.2, -11.64) * mm, "end": v(-47.26, -11.66) * mm});
            skLineSegment(sketch, "E3615", {"start": v(-47.26, -11.66) * mm, "end": v(-47.3, -11.69) * mm});
            skLineSegment(sketch, "E3616", {"start": v(-47.3, -11.69) * mm, "end": v(-47.35, -11.72) * mm});
            skLineSegment(sketch, "E3617", {"start": v(-47.35, -11.72) * mm, "end": v(-47.4, -11.75) * mm});
            skLineSegment(sketch, "E3618", {"start": v(-47.4, -11.75) * mm, "end": v(-47.46, -11.77) * mm});
            skLineSegment(sketch, "E3619", {"start": v(-47.46, -11.77) * mm, "end": v(-47.5, -11.8) * mm});
            skLineSegment(sketch, "E3620", {"start": v(-47.5, -11.8) * mm, "end": v(-47.56, -11.83) * mm});
            skLineSegment(sketch, "E3621", {"start": v(-47.56, -11.83) * mm, "end": v(-47.61, -11.87) * mm});
            skLineSegment(sketch, "E3622", {"start": v(-47.61, -11.87) * mm, "end": v(-47.66, -11.9) * mm});
            skLineSegment(sketch, "E3623", {"start": v(-47.66, -11.9) * mm, "end": v(-47.72, -11.93) * mm});
            skLineSegment(sketch, "E3624", {"start": v(-47.72, -11.93) * mm, "end": v(-47.77, -11.96) * mm});
            skLineSegment(sketch, "E3625", {"start": v(-47.77, -11.96) * mm, "end": v(-47.83, -12) * mm});
            skLineSegment(sketch, "E3626", {"start": v(-47.83, -12) * mm, "end": v(-47.88, -12.03) * mm});
            skLineSegment(sketch, "E3627", {"start": v(-47.88, -12.03) * mm, "end": v(-47.94, -12.07) * mm});
            skLineSegment(sketch, "E3628", {"start": v(-47.94, -12.07) * mm, "end": v(-48, -12.1) * mm});
            skLineSegment(sketch, "E3629", {"start": v(-48, -12.1) * mm, "end": v(-48.06, -12.14) * mm});
            skLineSegment(sketch, "E3630", {"start": v(-48.06, -12.14) * mm, "end": v(-48.11, -12.18) * mm});
            skLineSegment(sketch, "E3631", {"start": v(-48.11, -12.18) * mm, "end": v(-48.17, -12.22) * mm});
            skLineSegment(sketch, "E3632", {"start": v(-48.17, -12.22) * mm, "end": v(-48.23, -12.26) * mm});
            skLineSegment(sketch, "E3633", {"start": v(-48.23, -12.26) * mm, "end": v(-48.3, -12.3) * mm});
            skLineSegment(sketch, "E3634", {"start": v(-48.3, -12.3) * mm, "end": v(-48.35, -12.34) * mm});
            skLineSegment(sketch, "E3635", {"start": v(-48.35, -12.34) * mm, "end": v(-48.41, -12.38) * mm});
            skLineSegment(sketch, "E3636", {"start": v(-48.41, -12.38) * mm, "end": v(-48.48, -12.42) * mm});
            skLineSegment(sketch, "E3637", {"start": v(-48.48, -12.42) * mm, "end": v(-48.54, -12.46) * mm});
            skLineSegment(sketch, "E3638", {"start": v(-48.54, -12.46) * mm, "end": v(-48.6, -12.5) * mm});
            skLineSegment(sketch, "E3639", {"start": v(-48.6, -12.5) * mm, "end": v(-48.66, -12.55) * mm});
            skLineSegment(sketch, "E3640", {"start": v(-48.66, -12.55) * mm, "end": v(-48.73, -12.6) * mm});
            skLineSegment(sketch, "E3641", {"start": v(-48.73, -12.6) * mm, "end": v(-48.8, -12.64) * mm});
            skLineSegment(sketch, "E3642", {"start": v(-48.8, -12.64) * mm, "end": v(-48.86, -12.69) * mm});
            skLineSegment(sketch, "E3643", {"start": v(-48.86, -12.69) * mm, "end": v(-48.92, -12.74) * mm});
            skLineSegment(sketch, "E3644", {"start": v(-48.92, -12.74) * mm, "end": v(-48.99, -12.79) * mm});
            skLineSegment(sketch, "E3645", {"start": v(-48.99, -12.79) * mm, "end": v(-49.05, -12.84) * mm});
            skLineSegment(sketch, "E3646", {"start": v(-49.05, -12.84) * mm, "end": v(-49.12, -12.89) * mm});
            skLineSegment(sketch, "E3647", {"start": v(-49.12, -12.89) * mm, "end": v(-49.19, -12.94) * mm});
            skLineSegment(sketch, "E3648", {"start": v(-49.19, -12.94) * mm, "end": v(-49.26, -12.99) * mm});
            skLineSegment(sketch, "E3649", {"start": v(-49.26, -12.99) * mm, "end": v(-49.32, -13.04) * mm});
            skLineSegment(sketch, "E3650", {"start": v(-49.32, -13.04) * mm, "end": v(-49.4, -13.1) * mm});
            skLineSegment(sketch, "E3651", {"start": v(-49.4, -13.1) * mm, "end": v(-49.46, -13.15) * mm});
            skLineSegment(sketch, "E3652", {"start": v(-49.46, -13.15) * mm, "end": v(-49.52, -13.2) * mm});
            skLineSegment(sketch, "E3653", {"start": v(-49.52, -13.2) * mm, "end": v(-49.26, -14.13) * mm});
            skLineSegment(sketch, "E3654", {"start": v(-49.26, -14.13) * mm, "end": v(-49.19, -14.15) * mm});
            skLineSegment(sketch, "E3655", {"start": v(-49.19, -14.15) * mm, "end": v(-49.1, -14.16) * mm});
            skLineSegment(sketch, "E3656", {"start": v(-49.1, -14.16) * mm, "end": v(-49.01, -14.17) * mm});
            skLineSegment(sketch, "E3657", {"start": v(-49.01, -14.17) * mm, "end": v(-48.93, -14.18) * mm});
            skLineSegment(sketch, "E3658", {"start": v(-48.93, -14.18) * mm, "end": v(-48.84, -14.19) * mm});
            skLineSegment(sketch, "E3659", {"start": v(-48.84, -14.19) * mm, "end": v(-48.76, -14.2) * mm});
            skLineSegment(sketch, "E3660", {"start": v(-48.76, -14.2) * mm, "end": v(-48.67, -14.2) * mm});
            skLineSegment(sketch, "E3661", {"start": v(-48.67, -14.2) * mm, "end": v(-48.6, -14.21) * mm});
            skLineSegment(sketch, "E3662", {"start": v(-48.6, -14.21) * mm, "end": v(-48.51, -14.22) * mm});
            skLineSegment(sketch, "E3663", {"start": v(-48.51, -14.22) * mm, "end": v(-48.43, -14.23) * mm});
            skLineSegment(sketch, "E3664", {"start": v(-48.43, -14.23) * mm, "end": v(-48.35, -14.24) * mm});
            skLineSegment(sketch, "E3665", {"start": v(-48.35, -14.24) * mm, "end": v(-48.27, -14.24) * mm});
            skLineSegment(sketch, "E3666", {"start": v(-48.27, -14.24) * mm, "end": v(-48.2, -14.25) * mm});
            skLineSegment(sketch, "E3667", {"start": v(-48.2, -14.25) * mm, "end": v(-48.12, -14.25) * mm});
            skLineSegment(sketch, "E3668", {"start": v(-48.12, -14.25) * mm, "end": v(-48.04, -14.26) * mm});
            skLineSegment(sketch, "E3669", {"start": v(-48.04, -14.26) * mm, "end": v(-47.96, -14.26) * mm});
            skLineSegment(sketch, "E3670", {"start": v(-47.96, -14.26) * mm, "end": v(-47.9, -14.27) * mm});
            skLineSegment(sketch, "E3671", {"start": v(-47.9, -14.27) * mm, "end": v(-47.82, -14.27) * mm});
            skLineSegment(sketch, "E3672", {"start": v(-47.82, -14.27) * mm, "end": v(-47.74, -14.28) * mm});
            skLineSegment(sketch, "E3673", {"start": v(-47.74, -14.28) * mm, "end": v(-47.67, -14.28) * mm});
            skLineSegment(sketch, "E3674", {"start": v(-47.67, -14.28) * mm, "end": v(-47.6, -14.28) * mm});
            skLineSegment(sketch, "E3675", {"start": v(-47.6, -14.28) * mm, "end": v(-47.53, -14.29) * mm});
            skLineSegment(sketch, "E3676", {"start": v(-47.53, -14.29) * mm, "end": v(-47.46, -14.29) * mm});
            skLineSegment(sketch, "E3677", {"start": v(-47.46, -14.29) * mm, "end": v(-47.4, -14.3) * mm});
            skLineSegment(sketch, "E3678", {"start": v(-47.4, -14.3) * mm, "end": v(-47.33, -14.3) * mm});
            skLineSegment(sketch, "E3679", {"start": v(-47.33, -14.3) * mm, "end": v(-47.26, -14.3) * mm});
            skLineSegment(sketch, "E3680", {"start": v(-47.26, -14.3) * mm, "end": v(-47.2, -14.3) * mm});
            skLineSegment(sketch, "E3681", {"start": v(-47.2, -14.3) * mm, "end": v(-47.13, -14.3) * mm});
            skLineSegment(sketch, "E3682", {"start": v(-47.13, -14.3) * mm, "end": v(-47.06, -14.3) * mm});
            skLineSegment(sketch, "E3683", {"start": v(-47.06, -14.3) * mm, "end": v(-47, -14.3) * mm});
            skLineSegment(sketch, "E3684", {"start": v(-47, -14.3) * mm, "end": v(-46.94, -14.3) * mm});
            skLineSegment(sketch, "E3685", {"start": v(-46.94, -14.3) * mm, "end": v(-46.88, -14.3) * mm});
            skLineSegment(sketch, "E3686", {"start": v(-46.88, -14.3) * mm, "end": v(-46.82, -14.3) * mm});
            skLineSegment(sketch, "E3687", {"start": v(-46.82, -14.3) * mm, "end": v(-46.76, -14.3) * mm});
            skLineSegment(sketch, "E3688", {"start": v(-46.76, -14.3) * mm, "end": v(-46.7, -14.3) * mm});
            skLineSegment(sketch, "E3689", {"start": v(-46.7, -14.3) * mm, "end": v(-46.64, -14.3) * mm});
            skLineSegment(sketch, "E3690", {"start": v(-46.64, -14.3) * mm, "end": v(-46.58, -14.3) * mm});
            skLineSegment(sketch, "E3691", {"start": v(-46.58, -14.3) * mm, "end": v(-46.53, -14.29) * mm});
            skLineSegment(sketch, "E3692", {"start": v(-46.53, -14.29) * mm, "end": v(-46.47, -14.29) * mm});
            skLineSegment(sketch, "E3693", {"start": v(-46.47, -14.29) * mm, "end": v(-46.42, -14.28) * mm});
            skLineSegment(sketch, "E3694", {"start": v(-46.42, -14.28) * mm, "end": v(-46.33, -14.55) * mm});
            skLineSegment(sketch, "E3695", {"start": v(-46.33, -14.55) * mm, "end": v(-46.19, -15) * mm});
            skLineSegment(sketch, "E3696", {"start": v(-46.19, -15) * mm, "end": v(-46.1, -15.27) * mm});
            skLineSegment(sketch, "E3697", {"start": v(-46.1, -15.27) * mm, "end": v(-46.15, -15.3) * mm});
            skLineSegment(sketch, "E3698", {"start": v(-46.15, -15.3) * mm, "end": v(-46.2, -15.33) * mm});
            skLineSegment(sketch, "E3699", {"start": v(-46.2, -15.33) * mm, "end": v(-46.24, -15.36) * mm});
            skLineSegment(sketch, "E3700", {"start": v(-46.24, -15.36) * mm, "end": v(-46.29, -15.4) * mm});
            skLineSegment(sketch, "E3701", {"start": v(-46.29, -15.4) * mm, "end": v(-46.34, -15.43) * mm});
            skLineSegment(sketch, "E3702", {"start": v(-46.34, -15.43) * mm, "end": v(-46.39, -15.46) * mm});
            skLineSegment(sketch, "E3703", {"start": v(-46.39, -15.46) * mm, "end": v(-46.43, -15.5) * mm});
            skLineSegment(sketch, "E3704", {"start": v(-46.43, -15.5) * mm, "end": v(-46.48, -15.53) * mm});
            skLineSegment(sketch, "E3705", {"start": v(-46.48, -15.53) * mm, "end": v(-46.53, -15.57) * mm});
            skLineSegment(sketch, "E3706", {"start": v(-46.53, -15.57) * mm, "end": v(-46.58, -15.6) * mm});
            skLineSegment(sketch, "E3707", {"start": v(-46.58, -15.6) * mm, "end": v(-46.64, -15.64) * mm});
            skLineSegment(sketch, "E3708", {"start": v(-46.64, -15.64) * mm, "end": v(-46.69, -15.68) * mm});
            skLineSegment(sketch, "E3709", {"start": v(-46.69, -15.68) * mm, "end": v(-46.74, -15.71) * mm});
            skLineSegment(sketch, "E3710", {"start": v(-46.74, -15.71) * mm, "end": v(-46.8, -15.75) * mm});
            skLineSegment(sketch, "E3711", {"start": v(-46.8, -15.75) * mm, "end": v(-46.85, -15.8) * mm});
            skLineSegment(sketch, "E3712", {"start": v(-46.85, -15.8) * mm, "end": v(-46.9, -15.83) * mm});
            skLineSegment(sketch, "E3713", {"start": v(-46.9, -15.83) * mm, "end": v(-46.95, -15.87) * mm});
            skLineSegment(sketch, "E3714", {"start": v(-46.95, -15.87) * mm, "end": v(-47.01, -15.92) * mm});
            skLineSegment(sketch, "E3715", {"start": v(-47.01, -15.92) * mm, "end": v(-47.07, -15.96) * mm});
            skLineSegment(sketch, "E3716", {"start": v(-47.07, -15.96) * mm, "end": v(-47.12, -16) * mm});
            skLineSegment(sketch, "E3717", {"start": v(-47.12, -16) * mm, "end": v(-47.18, -16.05) * mm});
            skLineSegment(sketch, "E3718", {"start": v(-47.18, -16.05) * mm, "end": v(-47.24, -16.1) * mm});
            skLineSegment(sketch, "E3719", {"start": v(-47.24, -16.1) * mm, "end": v(-47.3, -16.14) * mm});
            skLineSegment(sketch, "E3720", {"start": v(-47.3, -16.14) * mm, "end": v(-47.35, -16.19) * mm});
            skLineSegment(sketch, "E3721", {"start": v(-47.35, -16.19) * mm, "end": v(-47.41, -16.23) * mm});
            skLineSegment(sketch, "E3722", {"start": v(-47.41, -16.23) * mm, "end": v(-47.47, -16.28) * mm});
            skLineSegment(sketch, "E3723", {"start": v(-47.47, -16.28) * mm, "end": v(-47.53, -16.33) * mm});
            skLineSegment(sketch, "E3724", {"start": v(-47.53, -16.33) * mm, "end": v(-47.59, -16.38) * mm});
            skLineSegment(sketch, "E3725", {"start": v(-47.59, -16.38) * mm, "end": v(-47.65, -16.43) * mm});
            skLineSegment(sketch, "E3726", {"start": v(-47.65, -16.43) * mm, "end": v(-47.71, -16.48) * mm});
            skLineSegment(sketch, "E3727", {"start": v(-47.71, -16.48) * mm, "end": v(-47.77, -16.54) * mm});
            skLineSegment(sketch, "E3728", {"start": v(-47.77, -16.54) * mm, "end": v(-47.83, -16.6) * mm});
            skLineSegment(sketch, "E3729", {"start": v(-47.83, -16.6) * mm, "end": v(-47.9, -16.64) * mm});
            skLineSegment(sketch, "E3730", {"start": v(-47.9, -16.64) * mm, "end": v(-47.96, -16.7) * mm});
            skLineSegment(sketch, "E3731", {"start": v(-47.96, -16.7) * mm, "end": v(-48.02, -16.76) * mm});
            skLineSegment(sketch, "E3732", {"start": v(-48.02, -16.76) * mm, "end": v(-48.09, -16.81) * mm});
            skLineSegment(sketch, "E3733", {"start": v(-48.09, -16.81) * mm, "end": v(-48.15, -16.87) * mm});
            skLineSegment(sketch, "E3734", {"start": v(-48.15, -16.87) * mm, "end": v(-48.21, -16.93) * mm});
            skLineSegment(sketch, "E3735", {"start": v(-48.21, -16.93) * mm, "end": v(-48.28, -16.99) * mm});
            skLineSegment(sketch, "E3736", {"start": v(-48.28, -16.99) * mm, "end": v(-48.33, -17.05) * mm});
            skLineSegment(sketch, "E3737", {"start": v(-48.33, -17.05) * mm, "end": v(-48, -17.95) * mm});
            skLineSegment(sketch, "E3738", {"start": v(-48, -17.95) * mm, "end": v(-47.93, -17.96) * mm});
            skLineSegment(sketch, "E3739", {"start": v(-47.93, -17.96) * mm, "end": v(-47.84, -17.97) * mm});
            skLineSegment(sketch, "E3740", {"start": v(-47.84, -17.97) * mm, "end": v(-47.75, -17.97) * mm});
            skLineSegment(sketch, "E3741", {"start": v(-47.75, -17.97) * mm, "end": v(-47.66, -17.97) * mm});
            skLineSegment(sketch, "E3742", {"start": v(-47.66, -17.97) * mm, "end": v(-47.58, -17.98) * mm});
            skLineSegment(sketch, "E3743", {"start": v(-47.58, -17.98) * mm, "end": v(-47.5, -17.98) * mm});
            skLineSegment(sketch, "E3744", {"start": v(-47.5, -17.98) * mm, "end": v(-47.41, -17.98) * mm});
            skLineSegment(sketch, "E3745", {"start": v(-47.41, -17.98) * mm, "end": v(-47.33, -17.98) * mm});
            skLineSegment(sketch, "E3746", {"start": v(-47.33, -17.98) * mm, "end": v(-47.25, -17.98) * mm});
            skLineSegment(sketch, "E3747", {"start": v(-47.25, -17.98) * mm, "end": v(-47.16, -17.99) * mm});
            skLineSegment(sketch, "E3748", {"start": v(-47.16, -17.99) * mm, "end": v(-47.08, -17.99) * mm});
            skLineSegment(sketch, "E3749", {"start": v(-47.08, -17.99) * mm, "end": v(-47, -17.99) * mm});
            skLineSegment(sketch, "E3750", {"start": v(-47, -17.99) * mm, "end": v(-46.93, -17.99) * mm});
            skLineSegment(sketch, "E3751", {"start": v(-46.93, -17.99) * mm, "end": v(-46.85, -17.99) * mm});
            skLineSegment(sketch, "E3752", {"start": v(-46.85, -17.99) * mm, "end": v(-46.77, -17.99) * mm});
            skLineSegment(sketch, "E3753", {"start": v(-46.77, -17.99) * mm, "end": v(-46.7, -17.98) * mm});
            skLineSegment(sketch, "E3754", {"start": v(-46.7, -17.98) * mm, "end": v(-46.62, -17.98) * mm});
            skLineSegment(sketch, "E3755", {"start": v(-46.62, -17.98) * mm, "end": v(-46.55, -17.98) * mm});
            skLineSegment(sketch, "E3756", {"start": v(-46.55, -17.98) * mm, "end": v(-46.48, -17.98) * mm});
            skLineSegment(sketch, "E3757", {"start": v(-46.48, -17.98) * mm, "end": v(-46.4, -17.98) * mm});
            skLineSegment(sketch, "E3758", {"start": v(-46.4, -17.98) * mm, "end": v(-46.33, -17.97) * mm});
            skLineSegment(sketch, "E3759", {"start": v(-46.33, -17.97) * mm, "end": v(-46.26, -17.97) * mm});
            skLineSegment(sketch, "E3760", {"start": v(-46.26, -17.97) * mm, "end": v(-46.2, -17.97) * mm});
            skLineSegment(sketch, "E3761", {"start": v(-46.2, -17.97) * mm, "end": v(-46.13, -17.96) * mm});
            skLineSegment(sketch, "E3762", {"start": v(-46.13, -17.96) * mm, "end": v(-46.06, -17.96) * mm});
            skLineSegment(sketch, "E3763", {"start": v(-46.06, -17.96) * mm, "end": v(-46, -17.96) * mm});
            skLineSegment(sketch, "E3764", {"start": v(-46, -17.96) * mm, "end": v(-45.93, -17.95) * mm});
            skLineSegment(sketch, "E3765", {"start": v(-45.93, -17.95) * mm, "end": v(-45.86, -17.95) * mm});
            skLineSegment(sketch, "E3766", {"start": v(-45.86, -17.95) * mm, "end": v(-45.8, -17.94) * mm});
            skLineSegment(sketch, "E3767", {"start": v(-45.8, -17.94) * mm, "end": v(-45.73, -17.94) * mm});
            skLineSegment(sketch, "E3768", {"start": v(-45.73, -17.94) * mm, "end": v(-45.67, -17.93) * mm});
            skLineSegment(sketch, "E3769", {"start": v(-45.67, -17.93) * mm, "end": v(-45.61, -17.93) * mm});
            skLineSegment(sketch, "E3770", {"start": v(-45.61, -17.93) * mm, "end": v(-45.55, -17.92) * mm});
            skLineSegment(sketch, "E3771", {"start": v(-45.55, -17.92) * mm, "end": v(-45.5, -17.92) * mm});
            skLineSegment(sketch, "E3772", {"start": v(-45.5, -17.92) * mm, "end": v(-45.43, -17.91) * mm});
            skLineSegment(sketch, "E3773", {"start": v(-45.43, -17.91) * mm, "end": v(-45.38, -17.9) * mm});
            skLineSegment(sketch, "E3774", {"start": v(-45.38, -17.9) * mm, "end": v(-45.32, -17.9) * mm});
            skLineSegment(sketch, "E3775", {"start": v(-45.32, -17.9) * mm, "end": v(-45.26, -17.9) * mm});
            skLineSegment(sketch, "E3776", {"start": v(-45.26, -17.9) * mm, "end": v(-45.2, -17.89) * mm});
            skLineSegment(sketch, "E3777", {"start": v(-45.2, -17.89) * mm, "end": v(-45.16, -17.88) * mm});
            skLineSegment(sketch, "E3778", {"start": v(-45.16, -17.88) * mm, "end": v(-45.05, -18.14) * mm});
            skLineSegment(sketch, "E3779", {"start": v(-45.05, -18.14) * mm, "end": v(-44.87, -18.58) * mm});
            skLineSegment(sketch, "E3780", {"start": v(-44.87, -18.58) * mm, "end": v(-44.76, -18.84) * mm});
            skLineSegment(sketch, "E3781", {"start": v(-44.76, -18.84) * mm, "end": v(-44.8, -18.88) * mm});
            skLineSegment(sketch, "E3782", {"start": v(-44.8, -18.88) * mm, "end": v(-44.85, -18.91) * mm});
            skLineSegment(sketch, "E3783", {"start": v(-44.85, -18.91) * mm, "end": v(-44.9, -18.95) * mm});
            skLineSegment(sketch, "E3784", {"start": v(-44.9, -18.95) * mm, "end": v(-44.94, -18.98) * mm});
            skLineSegment(sketch, "E3785", {"start": v(-44.94, -18.98) * mm, "end": v(-44.98, -19.02) * mm});
            skLineSegment(sketch, "E3786", {"start": v(-44.98, -19.02) * mm, "end": v(-45.03, -19.05) * mm});
            skLineSegment(sketch, "E3787", {"start": v(-45.03, -19.05) * mm, "end": v(-45.08, -19.1) * mm});
            skLineSegment(sketch, "E3788", {"start": v(-45.08, -19.1) * mm, "end": v(-45.12, -19.13) * mm});
            skLineSegment(sketch, "E3789", {"start": v(-45.12, -19.13) * mm, "end": v(-45.17, -19.17) * mm});
            skLineSegment(sketch, "E3790", {"start": v(-45.17, -19.17) * mm, "end": v(-45.22, -19.2) * mm});
            skLineSegment(sketch, "E3791", {"start": v(-45.22, -19.2) * mm, "end": v(-45.27, -19.25) * mm});
            skLineSegment(sketch, "E3792", {"start": v(-45.27, -19.25) * mm, "end": v(-45.31, -19.3) * mm});
            skLineSegment(sketch, "E3793", {"start": v(-45.31, -19.3) * mm, "end": v(-45.36, -19.33) * mm});
            skLineSegment(sketch, "E3794", {"start": v(-45.36, -19.33) * mm, "end": v(-45.41, -19.38) * mm});
            skLineSegment(sketch, "E3795", {"start": v(-45.41, -19.38) * mm, "end": v(-45.46, -19.42) * mm});
            skLineSegment(sketch, "E3796", {"start": v(-45.46, -19.42) * mm, "end": v(-45.51, -19.46) * mm});
            skLineSegment(sketch, "E3797", {"start": v(-45.51, -19.46) * mm, "end": v(-45.56, -19.5) * mm});
            skLineSegment(sketch, "E3798", {"start": v(-45.56, -19.5) * mm, "end": v(-45.62, -19.56) * mm});
            skLineSegment(sketch, "E3799", {"start": v(-45.62, -19.56) * mm, "end": v(-45.67, -19.6) * mm});
            skLineSegment(sketch, "E3800", {"start": v(-45.67, -19.6) * mm, "end": v(-45.72, -19.65) * mm});
            skLineSegment(sketch, "E3801", {"start": v(-45.72, -19.65) * mm, "end": v(-45.77, -19.7) * mm});
            skLineSegment(sketch, "E3802", {"start": v(-45.77, -19.7) * mm, "end": v(-45.83, -19.75) * mm});
            skLineSegment(sketch, "E3803", {"start": v(-45.83, -19.75) * mm, "end": v(-45.88, -19.8) * mm});
            skLineSegment(sketch, "E3804", {"start": v(-45.88, -19.8) * mm, "end": v(-45.94, -19.85) * mm});
            skLineSegment(sketch, "E3805", {"start": v(-45.94, -19.85) * mm, "end": v(-46, -19.9) * mm});
            skLineSegment(sketch, "E3806", {"start": v(-46, -19.9) * mm, "end": v(-46.05, -19.96) * mm});
            skLineSegment(sketch, "E3807", {"start": v(-46.05, -19.96) * mm, "end": v(-46.1, -20) * mm});
            skLineSegment(sketch, "E3808", {"start": v(-46.1, -20) * mm, "end": v(-46.16, -20.06) * mm});
            skLineSegment(sketch, "E3809", {"start": v(-46.16, -20.06) * mm, "end": v(-46.21, -20.12) * mm});
            skLineSegment(sketch, "E3810", {"start": v(-46.21, -20.12) * mm, "end": v(-46.27, -20.18) * mm});
            skLineSegment(sketch, "E3811", {"start": v(-46.27, -20.18) * mm, "end": v(-46.33, -20.23) * mm});
            skLineSegment(sketch, "E3812", {"start": v(-46.33, -20.23) * mm, "end": v(-46.38, -20.3) * mm});
            skLineSegment(sketch, "E3813", {"start": v(-46.38, -20.3) * mm, "end": v(-46.44, -20.35) * mm});
            skLineSegment(sketch, "E3814", {"start": v(-46.44, -20.35) * mm, "end": v(-46.5, -20.41) * mm});
            skLineSegment(sketch, "E3815", {"start": v(-46.5, -20.41) * mm, "end": v(-46.56, -20.47) * mm});
            skLineSegment(sketch, "E3816", {"start": v(-46.56, -20.47) * mm, "end": v(-46.62, -20.53) * mm});
            skLineSegment(sketch, "E3817", {"start": v(-46.62, -20.53) * mm, "end": v(-46.68, -20.6) * mm});
            skLineSegment(sketch, "E3818", {"start": v(-46.68, -20.6) * mm, "end": v(-46.74, -20.66) * mm});
            skLineSegment(sketch, "E3819", {"start": v(-46.74, -20.66) * mm, "end": v(-46.8, -20.73) * mm});
            skLineSegment(sketch, "E3820", {"start": v(-46.8, -20.73) * mm, "end": v(-46.85, -20.79) * mm});
            skLineSegment(sketch, "E3821", {"start": v(-46.85, -20.79) * mm, "end": v(-46.45, -21.66) * mm});
            skLineSegment(sketch, "E3822", {"start": v(-46.45, -21.66) * mm, "end": v(-46.37, -21.67) * mm});
            skLineSegment(sketch, "E3823", {"start": v(-46.37, -21.67) * mm, "end": v(-46.28, -21.66) * mm});
            skLineSegment(sketch, "E3824", {"start": v(-46.28, -21.66) * mm, "end": v(-46.2, -21.66) * mm});
            skLineSegment(sketch, "E3825", {"start": v(-46.2, -21.66) * mm, "end": v(-46.1, -21.66) * mm});
            skLineSegment(sketch, "E3826", {"start": v(-46.1, -21.66) * mm, "end": v(-46.02, -21.65) * mm});
            skLineSegment(sketch, "E3827", {"start": v(-46.02, -21.65) * mm, "end": v(-45.94, -21.65) * mm});
            skLineSegment(sketch, "E3828", {"start": v(-45.94, -21.65) * mm, "end": v(-45.85, -21.65) * mm});
            skLineSegment(sketch, "E3829", {"start": v(-45.85, -21.65) * mm, "end": v(-45.77, -21.64) * mm});
            skLineSegment(sketch, "E3830", {"start": v(-45.77, -21.64) * mm, "end": v(-45.69, -21.64) * mm});
            skLineSegment(sketch, "E3831", {"start": v(-45.69, -21.64) * mm, "end": v(-45.6, -21.63) * mm});
            skLineSegment(sketch, "E3832", {"start": v(-45.6, -21.63) * mm, "end": v(-45.53, -21.62) * mm});
            skLineSegment(sketch, "E3833", {"start": v(-45.53, -21.62) * mm, "end": v(-45.45, -21.62) * mm});
            skLineSegment(sketch, "E3834", {"start": v(-45.45, -21.62) * mm, "end": v(-45.37, -21.61) * mm});
            skLineSegment(sketch, "E3835", {"start": v(-45.37, -21.61) * mm, "end": v(-45.3, -21.6) * mm});
            skLineSegment(sketch, "E3836", {"start": v(-45.3, -21.6) * mm, "end": v(-45.22, -21.6) * mm});
            skLineSegment(sketch, "E3837", {"start": v(-45.22, -21.6) * mm, "end": v(-45.14, -21.6) * mm});
            skLineSegment(sketch, "E3838", {"start": v(-45.14, -21.6) * mm, "end": v(-45.07, -21.59) * mm});
            skLineSegment(sketch, "E3839", {"start": v(-45.07, -21.59) * mm, "end": v(-45, -21.58) * mm});
            skLineSegment(sketch, "E3840", {"start": v(-45, -21.58) * mm, "end": v(-44.92, -21.57) * mm});
            skLineSegment(sketch, "E3841", {"start": v(-44.92, -21.57) * mm, "end": v(-44.85, -21.56) * mm});
            skLineSegment(sketch, "E3842", {"start": v(-44.85, -21.56) * mm, "end": v(-44.78, -21.55) * mm});
            skLineSegment(sketch, "E3843", {"start": v(-44.78, -21.55) * mm, "end": v(-44.71, -21.55) * mm});
            skLineSegment(sketch, "E3844", {"start": v(-44.71, -21.55) * mm, "end": v(-44.64, -21.54) * mm});
            skLineSegment(sketch, "E3845", {"start": v(-44.64, -21.54) * mm, "end": v(-44.57, -21.53) * mm});
            skLineSegment(sketch, "E3846", {"start": v(-44.57, -21.53) * mm, "end": v(-44.5, -21.52) * mm});
            skLineSegment(sketch, "E3847", {"start": v(-44.5, -21.52) * mm, "end": v(-44.44, -21.51) * mm});
            skLineSegment(sketch, "E3848", {"start": v(-44.44, -21.51) * mm, "end": v(-44.38, -21.5) * mm});
            skLineSegment(sketch, "E3849", {"start": v(-44.38, -21.5) * mm, "end": v(-44.31, -21.5) * mm});
            skLineSegment(sketch, "E3850", {"start": v(-44.31, -21.5) * mm, "end": v(-44.25, -21.48) * mm});
            skLineSegment(sketch, "E3851", {"start": v(-44.25, -21.48) * mm, "end": v(-44.19, -21.47) * mm});
            skLineSegment(sketch, "E3852", {"start": v(-44.19, -21.47) * mm, "end": v(-44.12, -21.46) * mm});
            skLineSegment(sketch, "E3853", {"start": v(-44.12, -21.46) * mm, "end": v(-44.06, -21.45) * mm});
            skLineSegment(sketch, "E3854", {"start": v(-44.06, -21.45) * mm, "end": v(-44, -21.44) * mm});
            skLineSegment(sketch, "E3855", {"start": v(-44, -21.44) * mm, "end": v(-43.95, -21.43) * mm});
            skLineSegment(sketch, "E3856", {"start": v(-43.95, -21.43) * mm, "end": v(-43.89, -21.42) * mm});
            skLineSegment(sketch, "E3857", {"start": v(-43.89, -21.42) * mm, "end": v(-43.83, -21.41) * mm});
            skLineSegment(sketch, "E3858", {"start": v(-43.83, -21.41) * mm, "end": v(-43.78, -21.4) * mm});
            skLineSegment(sketch, "E3859", {"start": v(-43.78, -21.4) * mm, "end": v(-43.72, -21.4) * mm});
            skLineSegment(sketch, "E3860", {"start": v(-43.72, -21.4) * mm, "end": v(-43.67, -21.38) * mm});
            skLineSegment(sketch, "E3861", {"start": v(-43.67, -21.38) * mm, "end": v(-43.61, -21.37) * mm});
            skLineSegment(sketch, "E3862", {"start": v(-43.61, -21.37) * mm, "end": v(-43.49, -21.62) * mm});
            skLineSegment(sketch, "E3863", {"start": v(-43.49, -21.62) * mm, "end": v(-43.27, -22.05) * mm});
            skLineSegment(sketch, "E3864", {"start": v(-43.27, -22.05) * mm, "end": v(-43.15, -22.3) * mm});
            skLineSegment(sketch, "E3865", {"start": v(-43.15, -22.3) * mm, "end": v(-43.19, -22.33) * mm});
            skLineSegment(sketch, "E3866", {"start": v(-43.19, -22.33) * mm, "end": v(-43.23, -22.37) * mm});
            skLineSegment(sketch, "E3867", {"start": v(-43.23, -22.37) * mm, "end": v(-43.27, -22.4) * mm});
            skLineSegment(sketch, "E3868", {"start": v(-43.27, -22.4) * mm, "end": v(-43.31, -22.45) * mm});
            skLineSegment(sketch, "E3869", {"start": v(-43.31, -22.45) * mm, "end": v(-43.35, -22.49) * mm});
            skLineSegment(sketch, "E3870", {"start": v(-43.35, -22.49) * mm, "end": v(-43.4, -22.53) * mm});
            skLineSegment(sketch, "E3871", {"start": v(-43.4, -22.53) * mm, "end": v(-43.44, -22.57) * mm});
            skLineSegment(sketch, "E3872", {"start": v(-43.44, -22.57) * mm, "end": v(-43.48, -22.61) * mm});
            skLineSegment(sketch, "E3873", {"start": v(-43.48, -22.61) * mm, "end": v(-43.53, -22.65) * mm});
            skLineSegment(sketch, "E3874", {"start": v(-43.53, -22.65) * mm, "end": v(-43.57, -22.7) * mm});
            skLineSegment(sketch, "E3875", {"start": v(-43.57, -22.7) * mm, "end": v(-43.62, -22.74) * mm});
            skLineSegment(sketch, "E3876", {"start": v(-43.62, -22.74) * mm, "end": v(-43.66, -22.79) * mm});
            skLineSegment(sketch, "E3877", {"start": v(-43.66, -22.79) * mm, "end": v(-43.7, -22.83) * mm});
            skLineSegment(sketch, "E3878", {"start": v(-43.7, -22.83) * mm, "end": v(-43.75, -22.88) * mm});
            skLineSegment(sketch, "E3879", {"start": v(-43.75, -22.88) * mm, "end": v(-43.8, -22.93) * mm});
            skLineSegment(sketch, "E3880", {"start": v(-43.8, -22.93) * mm, "end": v(-43.85, -22.97) * mm});
            skLineSegment(sketch, "E3881", {"start": v(-43.85, -22.97) * mm, "end": v(-43.9, -23.02) * mm});
            skLineSegment(sketch, "E3882", {"start": v(-43.9, -23.02) * mm, "end": v(-43.94, -23.07) * mm});
            skLineSegment(sketch, "E3883", {"start": v(-43.94, -23.07) * mm, "end": v(-43.99, -23.13) * mm});
            skLineSegment(sketch, "E3884", {"start": v(-43.99, -23.13) * mm, "end": v(-44.04, -23.18) * mm});
            skLineSegment(sketch, "E3885", {"start": v(-44.04, -23.18) * mm, "end": v(-44.09, -23.23) * mm});
            skLineSegment(sketch, "E3886", {"start": v(-44.09, -23.23) * mm, "end": v(-44.14, -23.28) * mm});
            skLineSegment(sketch, "E3887", {"start": v(-44.14, -23.28) * mm, "end": v(-44.19, -23.34) * mm});
            skLineSegment(sketch, "E3888", {"start": v(-44.19, -23.34) * mm, "end": v(-44.24, -23.4) * mm});
            skLineSegment(sketch, "E3889", {"start": v(-44.24, -23.4) * mm, "end": v(-44.29, -23.45) * mm});
            skLineSegment(sketch, "E3890", {"start": v(-44.29, -23.45) * mm, "end": v(-44.34, -23.5) * mm});
            skLineSegment(sketch, "E3891", {"start": v(-44.34, -23.5) * mm, "end": v(-44.39, -23.56) * mm});
            skLineSegment(sketch, "E3892", {"start": v(-44.39, -23.56) * mm, "end": v(-44.44, -23.62) * mm});
            skLineSegment(sketch, "E3893", {"start": v(-44.44, -23.62) * mm, "end": v(-44.5, -23.68) * mm});
            skLineSegment(sketch, "E3894", {"start": v(-44.5, -23.68) * mm, "end": v(-44.54, -23.74) * mm});
            skLineSegment(sketch, "E3895", {"start": v(-44.54, -23.74) * mm, "end": v(-44.6, -23.8) * mm});
            skLineSegment(sketch, "E3896", {"start": v(-44.6, -23.8) * mm, "end": v(-44.65, -23.87) * mm});
            skLineSegment(sketch, "E3897", {"start": v(-44.65, -23.87) * mm, "end": v(-44.7, -23.93) * mm});
            skLineSegment(sketch, "E3898", {"start": v(-44.7, -23.93) * mm, "end": v(-44.76, -24) * mm});
            skLineSegment(sketch, "E3899", {"start": v(-44.76, -24) * mm, "end": v(-44.8, -24.06) * mm});
            skLineSegment(sketch, "E3900", {"start": v(-44.8, -24.06) * mm, "end": v(-44.86, -24.13) * mm});
            skLineSegment(sketch, "E3901", {"start": v(-44.86, -24.13) * mm, "end": v(-44.92, -24.2) * mm});
            skLineSegment(sketch, "E3902", {"start": v(-44.92, -24.2) * mm, "end": v(-44.97, -24.26) * mm});
            skLineSegment(sketch, "E3903", {"start": v(-44.97, -24.26) * mm, "end": v(-45.03, -24.33) * mm});
            skLineSegment(sketch, "E3904", {"start": v(-45.03, -24.33) * mm, "end": v(-45.07, -24.4) * mm});
            skLineSegment(sketch, "E3905", {"start": v(-45.07, -24.4) * mm, "end": v(-44.6, -25.24) * mm});
            skLineSegment(sketch, "E3906", {"start": v(-44.6, -25.24) * mm, "end": v(-44.53, -25.24) * mm});
            skLineSegment(sketch, "E3907", {"start": v(-44.53, -25.24) * mm, "end": v(-44.44, -25.23) * mm});
            skLineSegment(sketch, "E3908", {"start": v(-44.44, -25.23) * mm, "end": v(-44.35, -25.22) * mm});
            skLineSegment(sketch, "E3909", {"start": v(-44.35, -25.22) * mm, "end": v(-44.27, -25.2) * mm});
            skLineSegment(sketch, "E3910", {"start": v(-44.27, -25.2) * mm, "end": v(-44.18, -25.2) * mm});
            skLineSegment(sketch, "E3911", {"start": v(-44.18, -25.2) * mm, "end": v(-44.1, -25.19) * mm});
            skLineSegment(sketch, "E3912", {"start": v(-44.1, -25.19) * mm, "end": v(-44.01, -25.18) * mm});
            skLineSegment(sketch, "E3913", {"start": v(-44.01, -25.18) * mm, "end": v(-43.93, -25.17) * mm});
            skLineSegment(sketch, "E3914", {"start": v(-43.93, -25.17) * mm, "end": v(-43.85, -25.15) * mm});
            skLineSegment(sketch, "E3915", {"start": v(-43.85, -25.15) * mm, "end": v(-43.77, -25.14) * mm});
            skLineSegment(sketch, "E3916", {"start": v(-43.77, -25.14) * mm, "end": v(-43.7, -25.13) * mm});
            skLineSegment(sketch, "E3917", {"start": v(-43.7, -25.13) * mm, "end": v(-43.61, -25.12) * mm});
            skLineSegment(sketch, "E3918", {"start": v(-43.61, -25.12) * mm, "end": v(-43.54, -25.1) * mm});
            skLineSegment(sketch, "E3919", {"start": v(-43.54, -25.1) * mm, "end": v(-43.46, -25.1) * mm});
            skLineSegment(sketch, "E3920", {"start": v(-43.46, -25.1) * mm, "end": v(-43.38, -25.08) * mm});
            skLineSegment(sketch, "E3921", {"start": v(-43.38, -25.08) * mm, "end": v(-43.3, -25.07) * mm});
            skLineSegment(sketch, "E3922", {"start": v(-43.3, -25.07) * mm, "end": v(-43.24, -25.05) * mm});
            skLineSegment(sketch, "E3923", {"start": v(-43.24, -25.05) * mm, "end": v(-43.16, -25.04) * mm});
            skLineSegment(sketch, "E3924", {"start": v(-43.16, -25.04) * mm, "end": v(-43.1, -25.03) * mm});
            skLineSegment(sketch, "E3925", {"start": v(-43.1, -25.03) * mm, "end": v(-43.02, -25.01) * mm});
            skLineSegment(sketch, "E3926", {"start": v(-43.02, -25.01) * mm, "end": v(-42.95, -25) * mm});
            skLineSegment(sketch, "E3927", {"start": v(-42.95, -25) * mm, "end": v(-42.88, -24.99) * mm});
            skLineSegment(sketch, "E3928", {"start": v(-42.88, -24.99) * mm, "end": v(-42.81, -24.97) * mm});
            skLineSegment(sketch, "E3929", {"start": v(-42.81, -24.97) * mm, "end": v(-42.75, -24.96) * mm});
            skLineSegment(sketch, "E3930", {"start": v(-42.75, -24.96) * mm, "end": v(-42.68, -24.95) * mm});
            skLineSegment(sketch, "E3931", {"start": v(-42.68, -24.95) * mm, "end": v(-42.62, -24.93) * mm});
            skLineSegment(sketch, "E3932", {"start": v(-42.62, -24.93) * mm, "end": v(-42.55, -24.92) * mm});
            skLineSegment(sketch, "E3933", {"start": v(-42.55, -24.92) * mm, "end": v(-42.49, -24.9) * mm});
            skLineSegment(sketch, "E3934", {"start": v(-42.49, -24.9) * mm, "end": v(-42.43, -24.89) * mm});
            skLineSegment(sketch, "E3935", {"start": v(-42.43, -24.89) * mm, "end": v(-42.37, -24.87) * mm});
            skLineSegment(sketch, "E3936", {"start": v(-42.37, -24.87) * mm, "end": v(-42.3, -24.86) * mm});
            skLineSegment(sketch, "E3937", {"start": v(-42.3, -24.86) * mm, "end": v(-42.25, -24.84) * mm});
            skLineSegment(sketch, "E3938", {"start": v(-42.25, -24.84) * mm, "end": v(-42.19, -24.83) * mm});
            skLineSegment(sketch, "E3939", {"start": v(-42.19, -24.83) * mm, "end": v(-42.13, -24.81) * mm});
            skLineSegment(sketch, "E3940", {"start": v(-42.13, -24.81) * mm, "end": v(-42.07, -24.8) * mm});
            skLineSegment(sketch, "E3941", {"start": v(-42.07, -24.8) * mm, "end": v(-42.02, -24.79) * mm});
            skLineSegment(sketch, "E3942", {"start": v(-42.02, -24.79) * mm, "end": v(-41.96, -24.77) * mm});
            skLineSegment(sketch, "E3943", {"start": v(-41.96, -24.77) * mm, "end": v(-41.9, -24.76) * mm});
            skLineSegment(sketch, "E3944", {"start": v(-41.9, -24.76) * mm, "end": v(-41.85, -24.74) * mm});
            skLineSegment(sketch, "E3945", {"start": v(-41.85, -24.74) * mm, "end": v(-41.8, -24.73) * mm});
            skLineSegment(sketch, "E3946", {"start": v(-41.8, -24.73) * mm, "end": v(-41.66, -24.96) * mm});
            skLineSegment(sketch, "E3947", {"start": v(-41.66, -24.96) * mm, "end": v(-41.4, -25.37) * mm});
            skLineSegment(sketch, "E3948", {"start": v(-41.4, -25.37) * mm, "end": v(-41.26, -25.61) * mm});
            skLineSegment(sketch, "E3949", {"start": v(-41.26, -25.61) * mm, "end": v(-41.3, -25.65) * mm});
            skLineSegment(sketch, "E3950", {"start": v(-41.3, -25.65) * mm, "end": v(-41.34, -25.7) * mm});
            skLineSegment(sketch, "E3951", {"start": v(-41.34, -25.7) * mm, "end": v(-41.38, -25.73) * mm});
            skLineSegment(sketch, "E3952", {"start": v(-41.38, -25.73) * mm, "end": v(-41.42, -25.78) * mm});
            skLineSegment(sketch, "E3953", {"start": v(-41.42, -25.78) * mm, "end": v(-41.45, -25.82) * mm});
            skLineSegment(sketch, "E3954", {"start": v(-41.45, -25.82) * mm, "end": v(-41.5, -25.86) * mm});
            skLineSegment(sketch, "E3955", {"start": v(-41.5, -25.86) * mm, "end": v(-41.53, -25.9) * mm});
            skLineSegment(sketch, "E3956", {"start": v(-41.53, -25.9) * mm, "end": v(-41.57, -25.95) * mm});
            skLineSegment(sketch, "E3957", {"start": v(-41.57, -25.95) * mm, "end": v(-41.61, -26) * mm});
            skLineSegment(sketch, "E3958", {"start": v(-41.61, -26) * mm, "end": v(-41.66, -26.04) * mm});
            skLineSegment(sketch, "E3959", {"start": v(-41.66, -26.04) * mm, "end": v(-41.7, -26.1) * mm});
            skLineSegment(sketch, "E3960", {"start": v(-41.7, -26.1) * mm, "end": v(-41.74, -26.14) * mm});
            skLineSegment(sketch, "E3961", {"start": v(-41.74, -26.14) * mm, "end": v(-41.78, -26.2) * mm});
            skLineSegment(sketch, "E3962", {"start": v(-41.78, -26.2) * mm, "end": v(-41.82, -26.24) * mm});
            skLineSegment(sketch, "E3963", {"start": v(-41.82, -26.24) * mm, "end": v(-41.87, -26.3) * mm});
            skLineSegment(sketch, "E3964", {"start": v(-41.87, -26.3) * mm, "end": v(-41.9, -26.34) * mm});
            skLineSegment(sketch, "E3965", {"start": v(-41.9, -26.34) * mm, "end": v(-41.95, -26.4) * mm});
            skLineSegment(sketch, "E3966", {"start": v(-41.95, -26.4) * mm, "end": v(-42, -26.45) * mm});
            skLineSegment(sketch, "E3967", {"start": v(-42, -26.45) * mm, "end": v(-42.04, -26.5) * mm});
            skLineSegment(sketch, "E3968", {"start": v(-42.04, -26.5) * mm, "end": v(-42.08, -26.56) * mm});
            skLineSegment(sketch, "E3969", {"start": v(-42.08, -26.56) * mm, "end": v(-42.13, -26.62) * mm});
            skLineSegment(sketch, "E3970", {"start": v(-42.13, -26.62) * mm, "end": v(-42.17, -26.67) * mm});
            skLineSegment(sketch, "E3971", {"start": v(-42.17, -26.67) * mm, "end": v(-42.22, -26.73) * mm});
            skLineSegment(sketch, "E3972", {"start": v(-42.22, -26.73) * mm, "end": v(-42.26, -26.8) * mm});
            skLineSegment(sketch, "E3973", {"start": v(-42.26, -26.8) * mm, "end": v(-42.31, -26.85) * mm});
            skLineSegment(sketch, "E3974", {"start": v(-42.31, -26.85) * mm, "end": v(-42.36, -26.91) * mm});
            skLineSegment(sketch, "E3975", {"start": v(-42.36, -26.91) * mm, "end": v(-42.4, -26.98) * mm});
            skLineSegment(sketch, "E3976", {"start": v(-42.4, -26.98) * mm, "end": v(-42.45, -27.04) * mm});
            skLineSegment(sketch, "E3977", {"start": v(-42.45, -27.04) * mm, "end": v(-42.5, -27.1) * mm});
            skLineSegment(sketch, "E3978", {"start": v(-42.5, -27.1) * mm, "end": v(-42.54, -27.17) * mm});
            skLineSegment(sketch, "E3979", {"start": v(-42.54, -27.17) * mm, "end": v(-42.6, -27.23) * mm});
            skLineSegment(sketch, "E3980", {"start": v(-42.6, -27.23) * mm, "end": v(-42.64, -27.3) * mm});
            skLineSegment(sketch, "E3981", {"start": v(-42.64, -27.3) * mm, "end": v(-42.69, -27.37) * mm});
            skLineSegment(sketch, "E3982", {"start": v(-42.69, -27.37) * mm, "end": v(-42.74, -27.43) * mm});
            skLineSegment(sketch, "E3983", {"start": v(-42.74, -27.43) * mm, "end": v(-42.78, -27.5) * mm});
            skLineSegment(sketch, "E3984", {"start": v(-42.78, -27.5) * mm, "end": v(-42.83, -27.57) * mm});
            skLineSegment(sketch, "E3985", {"start": v(-42.83, -27.57) * mm, "end": v(-42.88, -27.65) * mm});
            skLineSegment(sketch, "E3986", {"start": v(-42.88, -27.65) * mm, "end": v(-42.93, -27.72) * mm});
            skLineSegment(sketch, "E3987", {"start": v(-42.93, -27.72) * mm, "end": v(-42.98, -27.8) * mm});
            skLineSegment(sketch, "E3988", {"start": v(-42.98, -27.8) * mm, "end": v(-43.02, -27.86) * mm});
            skLineSegment(sketch, "E3989", {"start": v(-43.02, -27.86) * mm, "end": v(-42.48, -28.66) * mm});
            skLineSegment(sketch, "E3990", {"start": v(-42.48, -28.66) * mm, "end": v(-42.4, -28.65) * mm});
            skLineSegment(sketch, "E3991", {"start": v(-42.4, -28.65) * mm, "end": v(-42.32, -28.64) * mm});
            skLineSegment(sketch, "E3992", {"start": v(-42.32, -28.64) * mm, "end": v(-42.24, -28.62) * mm});
            skLineSegment(sketch, "E3993", {"start": v(-42.24, -28.62) * mm, "end": v(-42.15, -28.6) * mm});
            skLineSegment(sketch, "E3994", {"start": v(-42.15, -28.6) * mm, "end": v(-42.07, -28.59) * mm});
            skLineSegment(sketch, "E3995", {"start": v(-42.07, -28.59) * mm, "end": v(-41.98, -28.57) * mm});
            skLineSegment(sketch, "E3996", {"start": v(-41.98, -28.57) * mm, "end": v(-41.9, -28.55) * mm});
            skLineSegment(sketch, "E3997", {"start": v(-41.9, -28.55) * mm, "end": v(-41.82, -28.53) * mm});
            skLineSegment(sketch, "E3998", {"start": v(-41.82, -28.53) * mm, "end": v(-41.74, -28.52) * mm});
            skLineSegment(sketch, "E3999", {"start": v(-41.74, -28.52) * mm, "end": v(-41.66, -28.5) * mm});
            skLineSegment(sketch, "E4000", {"start": v(-41.66, -28.5) * mm, "end": v(-41.58, -28.48) * mm});
            skLineSegment(sketch, "E4001", {"start": v(-41.58, -28.48) * mm, "end": v(-41.5, -28.46) * mm});
            skLineSegment(sketch, "E4002", {"start": v(-41.5, -28.46) * mm, "end": v(-41.43, -28.44) * mm});
            skLineSegment(sketch, "E4003", {"start": v(-41.43, -28.44) * mm, "end": v(-41.36, -28.43) * mm});
            skLineSegment(sketch, "E4004", {"start": v(-41.36, -28.43) * mm, "end": v(-41.28, -28.4) * mm});
            skLineSegment(sketch, "E4005", {"start": v(-41.28, -28.4) * mm, "end": v(-41.2, -28.39) * mm});
            skLineSegment(sketch, "E4006", {"start": v(-41.2, -28.39) * mm, "end": v(-41.14, -28.37) * mm});
            skLineSegment(sketch, "E4007", {"start": v(-41.14, -28.37) * mm, "end": v(-41.07, -28.35) * mm});
            skLineSegment(sketch, "E4008", {"start": v(-41.07, -28.35) * mm, "end": v(-41, -28.33) * mm});
            skLineSegment(sketch, "E4009", {"start": v(-41, -28.33) * mm, "end": v(-40.93, -28.31) * mm});
            skLineSegment(sketch, "E4010", {"start": v(-40.93, -28.31) * mm, "end": v(-40.86, -28.3) * mm});
            skLineSegment(sketch, "E4011", {"start": v(-40.86, -28.3) * mm, "end": v(-40.79, -28.27) * mm});
            skLineSegment(sketch, "E4012", {"start": v(-40.79, -28.27) * mm, "end": v(-40.72, -28.26) * mm});
            skLineSegment(sketch, "E4013", {"start": v(-40.72, -28.26) * mm, "end": v(-40.66, -28.24) * mm});
            skLineSegment(sketch, "E4014", {"start": v(-40.66, -28.24) * mm, "end": v(-40.6, -28.22) * mm});
            skLineSegment(sketch, "E4015", {"start": v(-40.6, -28.22) * mm, "end": v(-40.53, -28.2) * mm});
            skLineSegment(sketch, "E4016", {"start": v(-40.53, -28.2) * mm, "end": v(-40.47, -28.18) * mm});
            skLineSegment(sketch, "E4017", {"start": v(-40.47, -28.18) * mm, "end": v(-40.4, -28.16) * mm});
            skLineSegment(sketch, "E4018", {"start": v(-40.4, -28.16) * mm, "end": v(-40.34, -28.14) * mm});
            skLineSegment(sketch, "E4019", {"start": v(-40.34, -28.14) * mm, "end": v(-40.28, -28.12) * mm});
            skLineSegment(sketch, "E4020", {"start": v(-40.28, -28.12) * mm, "end": v(-40.22, -28.1) * mm});
            skLineSegment(sketch, "E4021", {"start": v(-40.22, -28.1) * mm, "end": v(-40.17, -28.08) * mm});
            skLineSegment(sketch, "E4022", {"start": v(-40.17, -28.08) * mm, "end": v(-40.1, -28.06) * mm});
            skLineSegment(sketch, "E4023", {"start": v(-40.1, -28.06) * mm, "end": v(-40.05, -28.04) * mm});
            skLineSegment(sketch, "E4024", {"start": v(-40.05, -28.04) * mm, "end": v(-40, -28.02) * mm});
            skLineSegment(sketch, "E4025", {"start": v(-40, -28.02) * mm, "end": v(-39.94, -28) * mm});
            skLineSegment(sketch, "E4026", {"start": v(-39.94, -28) * mm, "end": v(-39.89, -27.99) * mm});
            skLineSegment(sketch, "E4027", {"start": v(-39.89, -27.99) * mm, "end": v(-39.84, -27.97) * mm});
            skLineSegment(sketch, "E4028", {"start": v(-39.84, -27.97) * mm, "end": v(-39.78, -27.95) * mm});
            skLineSegment(sketch, "E4029", {"start": v(-39.78, -27.95) * mm, "end": v(-39.73, -27.93) * mm});
            skLineSegment(sketch, "E4030", {"start": v(-39.73, -27.93) * mm, "end": v(-39.57, -28.15) * mm});
            skLineSegment(sketch, "E4031", {"start": v(-39.57, -28.15) * mm, "end": v(-39.29, -28.54) * mm});
            skLineSegment(sketch, "E4032", {"start": v(-39.29, -28.54) * mm, "end": v(-39.13, -28.77) * mm});
            skLineSegment(sketch, "E4033", {"start": v(-39.13, -28.77) * mm, "end": v(-39.16, -28.82) * mm});
            skLineSegment(sketch, "E4034", {"start": v(-39.16, -28.82) * mm, "end": v(-39.2, -28.86) * mm});
            skLineSegment(sketch, "E4035", {"start": v(-39.2, -28.86) * mm, "end": v(-39.23, -28.9) * mm});
            skLineSegment(sketch, "E4036", {"start": v(-39.23, -28.9) * mm, "end": v(-39.27, -28.95) * mm});
            skLineSegment(sketch, "E4037", {"start": v(-39.27, -28.95) * mm, "end": v(-39.3, -29) * mm});
            skLineSegment(sketch, "E4038", {"start": v(-39.3, -29) * mm, "end": v(-39.34, -29.04) * mm});
            skLineSegment(sketch, "E4039", {"start": v(-39.34, -29.04) * mm, "end": v(-39.37, -29.09) * mm});
            skLineSegment(sketch, "E4040", {"start": v(-39.37, -29.09) * mm, "end": v(-39.4, -29.13) * mm});
            skLineSegment(sketch, "E4041", {"start": v(-39.4, -29.13) * mm, "end": v(-39.45, -29.18) * mm});
            skLineSegment(sketch, "E4042", {"start": v(-39.45, -29.18) * mm, "end": v(-39.48, -29.23) * mm});
            skLineSegment(sketch, "E4043", {"start": v(-39.48, -29.23) * mm, "end": v(-39.52, -29.28) * mm});
            skLineSegment(sketch, "E4044", {"start": v(-39.52, -29.28) * mm, "end": v(-39.56, -29.34) * mm});
            skLineSegment(sketch, "E4045", {"start": v(-39.56, -29.34) * mm, "end": v(-39.6, -29.39) * mm});
            skLineSegment(sketch, "E4046", {"start": v(-39.6, -29.39) * mm, "end": v(-39.63, -29.44) * mm});
            skLineSegment(sketch, "E4047", {"start": v(-39.63, -29.44) * mm, "end": v(-39.67, -29.5) * mm});
            skLineSegment(sketch, "E4048", {"start": v(-39.67, -29.5) * mm, "end": v(-39.71, -29.55) * mm});
            skLineSegment(sketch, "E4049", {"start": v(-39.71, -29.55) * mm, "end": v(-39.75, -29.6) * mm});
            skLineSegment(sketch, "E4050", {"start": v(-39.75, -29.6) * mm, "end": v(-39.8, -29.66) * mm});
            skLineSegment(sketch, "E4051", {"start": v(-39.8, -29.66) * mm, "end": v(-39.83, -29.72) * mm});
            skLineSegment(sketch, "E4052", {"start": v(-39.83, -29.72) * mm, "end": v(-39.87, -29.78) * mm});
            skLineSegment(sketch, "E4053", {"start": v(-39.87, -29.78) * mm, "end": v(-39.91, -29.84) * mm});
            skLineSegment(sketch, "E4054", {"start": v(-39.91, -29.84) * mm, "end": v(-39.95, -29.9) * mm});
            skLineSegment(sketch, "E4055", {"start": v(-39.95, -29.9) * mm, "end": v(-40, -29.96) * mm});
            skLineSegment(sketch, "E4056", {"start": v(-40, -29.96) * mm, "end": v(-40.03, -30.03) * mm});
            skLineSegment(sketch, "E4057", {"start": v(-40.03, -30.03) * mm, "end": v(-40.07, -30.09) * mm});
            skLineSegment(sketch, "E4058", {"start": v(-40.07, -30.09) * mm, "end": v(-40.11, -30.15) * mm});
            skLineSegment(sketch, "E4059", {"start": v(-40.11, -30.15) * mm, "end": v(-40.16, -30.22) * mm});
            skLineSegment(sketch, "E4060", {"start": v(-40.16, -30.22) * mm, "end": v(-40.2, -30.29) * mm});
            skLineSegment(sketch, "E4061", {"start": v(-40.2, -30.29) * mm, "end": v(-40.24, -30.35) * mm});
            skLineSegment(sketch, "E4062", {"start": v(-40.24, -30.35) * mm, "end": v(-40.28, -30.42) * mm});
            skLineSegment(sketch, "E4063", {"start": v(-40.28, -30.42) * mm, "end": v(-40.32, -30.49) * mm});
            skLineSegment(sketch, "E4064", {"start": v(-40.32, -30.49) * mm, "end": v(-40.37, -30.56) * mm});
            skLineSegment(sketch, "E4065", {"start": v(-40.37, -30.56) * mm, "end": v(-40.4, -30.63) * mm});
            skLineSegment(sketch, "E4066", {"start": v(-40.4, -30.63) * mm, "end": v(-40.45, -30.7) * mm});
            skLineSegment(sketch, "E4067", {"start": v(-40.45, -30.7) * mm, "end": v(-40.5, -30.78) * mm});
            skLineSegment(sketch, "E4068", {"start": v(-40.5, -30.78) * mm, "end": v(-40.54, -30.85) * mm});
            skLineSegment(sketch, "E4069", {"start": v(-40.54, -30.85) * mm, "end": v(-40.58, -30.92) * mm});
            skLineSegment(sketch, "E4070", {"start": v(-40.58, -30.92) * mm, "end": v(-40.62, -31) * mm});
            skLineSegment(sketch, "E4071", {"start": v(-40.62, -31) * mm, "end": v(-40.67, -31.08) * mm});
            skLineSegment(sketch, "E4072", {"start": v(-40.67, -31.08) * mm, "end": v(-40.7, -31.15) * mm});
            skLineSegment(sketch, "E4073", {"start": v(-40.7, -31.15) * mm, "end": v(-40.1, -31.9) * mm});
            skLineSegment(sketch, "E4074", {"start": v(-40.1, -31.9) * mm, "end": v(-40.03, -31.9) * mm});
            skLineSegment(sketch, "E4075", {"start": v(-40.03, -31.9) * mm, "end": v(-39.94, -31.87) * mm});
            skLineSegment(sketch, "E4076", {"start": v(-39.94, -31.87) * mm, "end": v(-39.86, -31.85) * mm});
            skLineSegment(sketch, "E4077", {"start": v(-39.86, -31.85) * mm, "end": v(-39.78, -31.82) * mm});
            skLineSegment(sketch, "E4078", {"start": v(-39.78, -31.82) * mm, "end": v(-39.7, -31.8) * mm});
            skLineSegment(sketch, "E4079", {"start": v(-39.7, -31.8) * mm, "end": v(-39.61, -31.78) * mm});
            skLineSegment(sketch, "E4080", {"start": v(-39.61, -31.78) * mm, "end": v(-39.53, -31.75) * mm});
            skLineSegment(sketch, "E4081", {"start": v(-39.53, -31.75) * mm, "end": v(-39.45, -31.73) * mm});
            skLineSegment(sketch, "E4082", {"start": v(-39.45, -31.73) * mm, "end": v(-39.38, -31.7) * mm});
            skLineSegment(sketch, "E4083", {"start": v(-39.38, -31.7) * mm, "end": v(-39.3, -31.68) * mm});
            skLineSegment(sketch, "E4084", {"start": v(-39.3, -31.68) * mm, "end": v(-39.22, -31.66) * mm});
            skLineSegment(sketch, "E4085", {"start": v(-39.22, -31.66) * mm, "end": v(-39.15, -31.63) * mm});
            skLineSegment(sketch, "E4086", {"start": v(-39.15, -31.63) * mm, "end": v(-39.07, -31.6) * mm});
            skLineSegment(sketch, "E4087", {"start": v(-39.07, -31.6) * mm, "end": v(-39, -31.58) * mm});
            skLineSegment(sketch, "E4088", {"start": v(-39, -31.58) * mm, "end": v(-38.93, -31.56) * mm});
            skLineSegment(sketch, "E4089", {"start": v(-38.93, -31.56) * mm, "end": v(-38.85, -31.53) * mm});
            skLineSegment(sketch, "E4090", {"start": v(-38.85, -31.53) * mm, "end": v(-38.78, -31.5) * mm});
            skLineSegment(sketch, "E4091", {"start": v(-38.78, -31.5) * mm, "end": v(-38.71, -31.49) * mm});
            skLineSegment(sketch, "E4092", {"start": v(-38.71, -31.49) * mm, "end": v(-38.65, -31.46) * mm});
            skLineSegment(sketch, "E4093", {"start": v(-38.65, -31.46) * mm, "end": v(-38.58, -31.44) * mm});
            skLineSegment(sketch, "E4094", {"start": v(-38.58, -31.44) * mm, "end": v(-38.51, -31.41) * mm});
            skLineSegment(sketch, "E4095", {"start": v(-38.51, -31.41) * mm, "end": v(-38.45, -31.39) * mm});
            skLineSegment(sketch, "E4096", {"start": v(-38.45, -31.39) * mm, "end": v(-38.38, -31.36) * mm});
            skLineSegment(sketch, "E4097", {"start": v(-38.38, -31.36) * mm, "end": v(-38.32, -31.34) * mm});
            skLineSegment(sketch, "E4098", {"start": v(-38.32, -31.34) * mm, "end": v(-38.25, -31.32) * mm});
            skLineSegment(sketch, "E4099", {"start": v(-38.25, -31.32) * mm, "end": v(-38.2, -31.3) * mm});
            skLineSegment(sketch, "E4100", {"start": v(-38.2, -31.3) * mm, "end": v(-38.13, -31.27) * mm});
            skLineSegment(sketch, "E4101", {"start": v(-38.13, -31.27) * mm, "end": v(-38.07, -31.24) * mm});
            skLineSegment(sketch, "E4102", {"start": v(-38.07, -31.24) * mm, "end": v(-38.01, -31.22) * mm});
            skLineSegment(sketch, "E4103", {"start": v(-38.01, -31.22) * mm, "end": v(-37.95, -31.2) * mm});
            skLineSegment(sketch, "E4104", {"start": v(-37.95, -31.2) * mm, "end": v(-37.9, -31.17) * mm});
            skLineSegment(sketch, "E4105", {"start": v(-37.9, -31.17) * mm, "end": v(-37.84, -31.15) * mm});
            skLineSegment(sketch, "E4106", {"start": v(-37.84, -31.15) * mm, "end": v(-37.78, -31.12) * mm});
            skLineSegment(sketch, "E4107", {"start": v(-37.78, -31.12) * mm, "end": v(-37.73, -31.1) * mm});
            skLineSegment(sketch, "E4108", {"start": v(-37.73, -31.1) * mm, "end": v(-37.67, -31.08) * mm});
            skLineSegment(sketch, "E4109", {"start": v(-37.67, -31.08) * mm, "end": v(-37.62, -31.05) * mm});
            skLineSegment(sketch, "E4110", {"start": v(-37.62, -31.05) * mm, "end": v(-37.57, -31.03) * mm});
            skLineSegment(sketch, "E4111", {"start": v(-37.57, -31.03) * mm, "end": v(-37.52, -31) * mm});
            skLineSegment(sketch, "E4112", {"start": v(-37.52, -31) * mm, "end": v(-37.47, -30.98) * mm});
            skLineSegment(sketch, "E4113", {"start": v(-37.47, -30.98) * mm, "end": v(-37.42, -30.96) * mm});
            skLineSegment(sketch, "E4114", {"start": v(-37.42, -30.96) * mm, "end": v(-37.24, -31.17) * mm});
            skLineSegment(sketch, "E4115", {"start": v(-37.24, -31.17) * mm, "end": v(-36.93, -31.54) * mm});
            skLineSegment(sketch, "E4116", {"start": v(-36.93, -31.54) * mm, "end": v(-36.75, -31.75) * mm});
            skLineSegment(sketch, "E4117", {"start": v(-36.75, -31.75) * mm, "end": v(-36.78, -31.8) * mm});
            skLineSegment(sketch, "E4118", {"start": v(-36.78, -31.8) * mm, "end": v(-36.81, -31.84) * mm});
            skLineSegment(sketch, "E4119", {"start": v(-36.81, -31.84) * mm, "end": v(-36.84, -31.9) * mm});
            skLineSegment(sketch, "E4120", {"start": v(-36.84, -31.9) * mm, "end": v(-36.87, -31.94) * mm});
            skLineSegment(sketch, "E4121", {"start": v(-36.87, -31.94) * mm, "end": v(-36.9, -31.99) * mm});
            skLineSegment(sketch, "E4122", {"start": v(-36.9, -31.99) * mm, "end": v(-36.94, -32.04) * mm});
            skLineSegment(sketch, "E4123", {"start": v(-36.94, -32.04) * mm, "end": v(-36.97, -32.09) * mm});
            skLineSegment(sketch, "E4124", {"start": v(-36.97, -32.09) * mm, "end": v(-37, -32.14) * mm});
            skLineSegment(sketch, "E4125", {"start": v(-37, -32.14) * mm, "end": v(-37.04, -32.19) * mm});
            skLineSegment(sketch, "E4126", {"start": v(-37.04, -32.19) * mm, "end": v(-37.07, -32.24) * mm});
            skLineSegment(sketch, "E4127", {"start": v(-37.07, -32.24) * mm, "end": v(-37.1, -32.3) * mm});
            skLineSegment(sketch, "E4128", {"start": v(-37.1, -32.3) * mm, "end": v(-37.13, -32.35) * mm});
            skLineSegment(sketch, "E4129", {"start": v(-37.13, -32.35) * mm, "end": v(-37.17, -32.4) * mm});
            skLineSegment(sketch, "E4130", {"start": v(-37.17, -32.4) * mm, "end": v(-37.2, -32.46) * mm});
            skLineSegment(sketch, "E4131", {"start": v(-37.2, -32.46) * mm, "end": v(-37.24, -32.52) * mm});
            skLineSegment(sketch, "E4132", {"start": v(-37.24, -32.52) * mm, "end": v(-37.27, -32.58) * mm});
            skLineSegment(sketch, "E4133", {"start": v(-37.27, -32.58) * mm, "end": v(-37.3, -32.63) * mm});
            skLineSegment(sketch, "E4134", {"start": v(-37.3, -32.63) * mm, "end": v(-37.34, -32.7) * mm});
            skLineSegment(sketch, "E4135", {"start": v(-37.34, -32.7) * mm, "end": v(-37.38, -32.76) * mm});
            skLineSegment(sketch, "E4136", {"start": v(-37.38, -32.76) * mm, "end": v(-37.41, -32.82) * mm});
            skLineSegment(sketch, "E4137", {"start": v(-37.41, -32.82) * mm, "end": v(-37.45, -32.88) * mm});
            skLineSegment(sketch, "E4138", {"start": v(-37.45, -32.88) * mm, "end": v(-37.48, -32.94) * mm});
            skLineSegment(sketch, "E4139", {"start": v(-37.48, -32.94) * mm, "end": v(-37.52, -33) * mm});
            skLineSegment(sketch, "E4140", {"start": v(-37.52, -33) * mm, "end": v(-37.55, -33.07) * mm});
            skLineSegment(sketch, "E4141", {"start": v(-37.55, -33.07) * mm, "end": v(-37.59, -33.14) * mm});
            skLineSegment(sketch, "E4142", {"start": v(-37.59, -33.14) * mm, "end": v(-37.63, -33.2) * mm});
            skLineSegment(sketch, "E4143", {"start": v(-37.63, -33.2) * mm, "end": v(-37.66, -33.28) * mm});
            skLineSegment(sketch, "E4144", {"start": v(-37.66, -33.28) * mm, "end": v(-37.7, -33.35) * mm});
            skLineSegment(sketch, "E4145", {"start": v(-37.7, -33.35) * mm, "end": v(-37.73, -33.42) * mm});
            skLineSegment(sketch, "E4146", {"start": v(-37.73, -33.42) * mm, "end": v(-37.77, -33.49) * mm});
            skLineSegment(sketch, "E4147", {"start": v(-37.77, -33.49) * mm, "end": v(-37.8, -33.56) * mm});
            skLineSegment(sketch, "E4148", {"start": v(-37.8, -33.56) * mm, "end": v(-37.84, -33.63) * mm});
            skLineSegment(sketch, "E4149", {"start": v(-37.84, -33.63) * mm, "end": v(-37.88, -33.7) * mm});
            skLineSegment(sketch, "E4150", {"start": v(-37.88, -33.7) * mm, "end": v(-37.92, -33.78) * mm});
            skLineSegment(sketch, "E4151", {"start": v(-37.92, -33.78) * mm, "end": v(-37.95, -33.86) * mm});
            skLineSegment(sketch, "E4152", {"start": v(-37.95, -33.86) * mm, "end": v(-38, -33.93) * mm});
            skLineSegment(sketch, "E4153", {"start": v(-38, -33.93) * mm, "end": v(-38.03, -34.01) * mm});
            skLineSegment(sketch, "E4154", {"start": v(-38.03, -34.01) * mm, "end": v(-38.07, -34.1) * mm});
            skLineSegment(sketch, "E4155", {"start": v(-38.07, -34.1) * mm, "end": v(-38.1, -34.17) * mm});
            skLineSegment(sketch, "E4156", {"start": v(-38.1, -34.17) * mm, "end": v(-38.13, -34.24) * mm});
            skLineSegment(sketch, "E4157", {"start": v(-38.13, -34.24) * mm, "end": v(-37.48, -34.96) * mm});
            skLineSegment(sketch, "E4158", {"start": v(-37.48, -34.96) * mm, "end": v(-37.4, -34.94) * mm});
            skLineSegment(sketch, "E4159", {"start": v(-37.4, -34.94) * mm, "end": v(-37.32, -34.9) * mm});
            skLineSegment(sketch, "E4160", {"start": v(-37.32, -34.9) * mm, "end": v(-37.24, -34.88) * mm});
            skLineSegment(sketch, "E4161", {"start": v(-37.24, -34.88) * mm, "end": v(-37.16, -34.85) * mm});
            skLineSegment(sketch, "E4162", {"start": v(-37.16, -34.85) * mm, "end": v(-37.08, -34.82) * mm});
            skLineSegment(sketch, "E4163", {"start": v(-37.08, -34.82) * mm, "end": v(-37, -34.79) * mm});
            skLineSegment(sketch, "E4164", {"start": v(-37, -34.79) * mm, "end": v(-36.92, -34.76) * mm});
            skLineSegment(sketch, "E4165", {"start": v(-36.92, -34.76) * mm, "end": v(-36.84, -34.73) * mm});
            skLineSegment(sketch, "E4166", {"start": v(-36.84, -34.73) * mm, "end": v(-36.77, -34.7) * mm});
            skLineSegment(sketch, "E4167", {"start": v(-36.77, -34.7) * mm, "end": v(-36.7, -34.67) * mm});
            skLineSegment(sketch, "E4168", {"start": v(-36.7, -34.67) * mm, "end": v(-36.62, -34.64) * mm});
            skLineSegment(sketch, "E4169", {"start": v(-36.62, -34.64) * mm, "end": v(-36.54, -34.6) * mm});
            skLineSegment(sketch, "E4170", {"start": v(-36.54, -34.6) * mm, "end": v(-36.47, -34.58) * mm});
            skLineSegment(sketch, "E4171", {"start": v(-36.47, -34.58) * mm, "end": v(-36.4, -34.55) * mm});
            skLineSegment(sketch, "E4172", {"start": v(-36.4, -34.55) * mm, "end": v(-36.33, -34.52) * mm});
            skLineSegment(sketch, "E4173", {"start": v(-36.33, -34.52) * mm, "end": v(-36.26, -34.49) * mm});
            skLineSegment(sketch, "E4174", {"start": v(-36.26, -34.49) * mm, "end": v(-36.2, -34.46) * mm});
            skLineSegment(sketch, "E4175", {"start": v(-36.2, -34.46) * mm, "end": v(-36.12, -34.43) * mm});
            skLineSegment(sketch, "E4176", {"start": v(-36.12, -34.43) * mm, "end": v(-36.06, -34.4) * mm});
            skLineSegment(sketch, "E4177", {"start": v(-36.06, -34.4) * mm, "end": v(-36, -34.37) * mm});
            skLineSegment(sketch, "E4178", {"start": v(-36, -34.37) * mm, "end": v(-35.93, -34.34) * mm});
            skLineSegment(sketch, "E4179", {"start": v(-35.93, -34.34) * mm, "end": v(-35.86, -34.3) * mm});
            skLineSegment(sketch, "E4180", {"start": v(-35.86, -34.3) * mm, "end": v(-35.8, -34.28) * mm});
            skLineSegment(sketch, "E4181", {"start": v(-35.8, -34.28) * mm, "end": v(-35.74, -34.25) * mm});
            skLineSegment(sketch, "E4182", {"start": v(-35.74, -34.25) * mm, "end": v(-35.68, -34.22) * mm});
            skLineSegment(sketch, "E4183", {"start": v(-35.68, -34.22) * mm, "end": v(-35.62, -34.2) * mm});
            skLineSegment(sketch, "E4184", {"start": v(-35.62, -34.2) * mm, "end": v(-35.56, -34.16) * mm});
            skLineSegment(sketch, "E4185", {"start": v(-35.56, -34.16) * mm, "end": v(-35.5, -34.13) * mm});
            skLineSegment(sketch, "E4186", {"start": v(-35.5, -34.13) * mm, "end": v(-35.44, -34.1) * mm});
            skLineSegment(sketch, "E4187", {"start": v(-35.44, -34.1) * mm, "end": v(-35.39, -34.08) * mm});
            skLineSegment(sketch, "E4188", {"start": v(-35.39, -34.08) * mm, "end": v(-35.33, -34.05) * mm});
            skLineSegment(sketch, "E4189", {"start": v(-35.33, -34.05) * mm, "end": v(-35.28, -34.02) * mm});
            skLineSegment(sketch, "E4190", {"start": v(-35.28, -34.02) * mm, "end": v(-35.22, -34) * mm});
            skLineSegment(sketch, "E4191", {"start": v(-35.22, -34) * mm, "end": v(-35.17, -33.96) * mm});
            skLineSegment(sketch, "E4192", {"start": v(-35.17, -33.96) * mm, "end": v(-35.12, -33.94) * mm});
            skLineSegment(sketch, "E4193", {"start": v(-35.12, -33.94) * mm, "end": v(-35.07, -33.9) * mm});
            skLineSegment(sketch, "E4194", {"start": v(-35.07, -33.9) * mm, "end": v(-35.02, -33.88) * mm});
            skLineSegment(sketch, "E4195", {"start": v(-35.02, -33.88) * mm, "end": v(-34.97, -33.86) * mm});
            skLineSegment(sketch, "E4196", {"start": v(-34.97, -33.86) * mm, "end": v(-34.92, -33.83) * mm});
            skLineSegment(sketch, "E4197", {"start": v(-34.92, -33.83) * mm, "end": v(-34.88, -33.8) * mm});
            skLineSegment(sketch, "E4198", {"start": v(-34.88, -33.8) * mm, "end": v(-34.68, -34) * mm});
            skLineSegment(sketch, "E4199", {"start": v(-34.68, -34) * mm, "end": v(-34.34, -34.34) * mm});
            skLineSegment(sketch, "E4200", {"start": v(-34.34, -34.34) * mm, "end": v(-34.14, -34.54) * mm});
            skLineSegment(sketch, "E4201", {"start": v(-34.14, -34.54) * mm, "end": v(-34.17, -34.59) * mm});
            skLineSegment(sketch, "E4202", {"start": v(-34.17, -34.59) * mm, "end": v(-34.2, -34.63) * mm});
            skLineSegment(sketch, "E4203", {"start": v(-34.2, -34.63) * mm, "end": v(-34.23, -34.68) * mm});
            skLineSegment(sketch, "E4204", {"start": v(-34.23, -34.68) * mm, "end": v(-34.25, -34.73) * mm});
            skLineSegment(sketch, "E4205", {"start": v(-34.25, -34.73) * mm, "end": v(-34.28, -34.78) * mm});
            skLineSegment(sketch, "E4206", {"start": v(-34.28, -34.78) * mm, "end": v(-34.31, -34.83) * mm});
            skLineSegment(sketch, "E4207", {"start": v(-34.31, -34.83) * mm, "end": v(-34.34, -34.89) * mm});
            skLineSegment(sketch, "E4208", {"start": v(-34.34, -34.89) * mm, "end": v(-34.37, -34.94) * mm});
            skLineSegment(sketch, "E4209", {"start": v(-34.37, -34.94) * mm, "end": v(-34.4, -35) * mm});
            skLineSegment(sketch, "E4210", {"start": v(-34.4, -35) * mm, "end": v(-34.42, -35.05) * mm});
            skLineSegment(sketch, "E4211", {"start": v(-34.42, -35.05) * mm, "end": v(-34.45, -35.1) * mm});
            skLineSegment(sketch, "E4212", {"start": v(-34.45, -35.1) * mm, "end": v(-34.48, -35.16) * mm});
            skLineSegment(sketch, "E4213", {"start": v(-34.48, -35.16) * mm, "end": v(-34.51, -35.22) * mm});
            skLineSegment(sketch, "E4214", {"start": v(-34.51, -35.22) * mm, "end": v(-34.54, -35.28) * mm});
            skLineSegment(sketch, "E4215", {"start": v(-34.54, -35.28) * mm, "end": v(-34.57, -35.34) * mm});
            skLineSegment(sketch, "E4216", {"start": v(-34.57, -35.34) * mm, "end": v(-34.6, -35.4) * mm});
            skLineSegment(sketch, "E4217", {"start": v(-34.6, -35.4) * mm, "end": v(-34.63, -35.46) * mm});
            skLineSegment(sketch, "E4218", {"start": v(-34.63, -35.46) * mm, "end": v(-34.66, -35.52) * mm});
            skLineSegment(sketch, "E4219", {"start": v(-34.66, -35.52) * mm, "end": v(-34.7, -35.59) * mm});
            skLineSegment(sketch, "E4220", {"start": v(-34.7, -35.59) * mm, "end": v(-34.72, -35.65) * mm});
            skLineSegment(sketch, "E4221", {"start": v(-34.72, -35.65) * mm, "end": v(-34.75, -35.72) * mm});
            skLineSegment(sketch, "E4222", {"start": v(-34.75, -35.72) * mm, "end": v(-34.78, -35.78) * mm});
            skLineSegment(sketch, "E4223", {"start": v(-34.78, -35.78) * mm, "end": v(-34.81, -35.85) * mm});
            skLineSegment(sketch, "E4224", {"start": v(-34.81, -35.85) * mm, "end": v(-34.84, -35.92) * mm});
            skLineSegment(sketch, "E4225", {"start": v(-34.84, -35.92) * mm, "end": v(-34.87, -35.99) * mm});
            skLineSegment(sketch, "E4226", {"start": v(-34.87, -35.99) * mm, "end": v(-34.9, -36.06) * mm});
            skLineSegment(sketch, "E4227", {"start": v(-34.9, -36.06) * mm, "end": v(-34.93, -36.13) * mm});
            skLineSegment(sketch, "E4228", {"start": v(-34.93, -36.13) * mm, "end": v(-34.97, -36.2) * mm});
            skLineSegment(sketch, "E4229", {"start": v(-34.97, -36.2) * mm, "end": v(-35, -36.27) * mm});
            skLineSegment(sketch, "E4230", {"start": v(-35, -36.27) * mm, "end": v(-35.03, -36.35) * mm});
            skLineSegment(sketch, "E4231", {"start": v(-35.03, -36.35) * mm, "end": v(-35.06, -36.42) * mm});
            skLineSegment(sketch, "E4232", {"start": v(-35.06, -36.42) * mm, "end": v(-35.09, -36.5) * mm});
            skLineSegment(sketch, "E4233", {"start": v(-35.09, -36.5) * mm, "end": v(-35.12, -36.57) * mm});
            skLineSegment(sketch, "E4234", {"start": v(-35.12, -36.57) * mm, "end": v(-35.15, -36.65) * mm});
            skLineSegment(sketch, "E4235", {"start": v(-35.15, -36.65) * mm, "end": v(-35.18, -36.73) * mm});
            skLineSegment(sketch, "E4236", {"start": v(-35.18, -36.73) * mm, "end": v(-35.21, -36.81) * mm});
            skLineSegment(sketch, "E4237", {"start": v(-35.21, -36.81) * mm, "end": v(-35.24, -36.9) * mm});
            skLineSegment(sketch, "E4238", {"start": v(-35.24, -36.9) * mm, "end": v(-35.27, -36.97) * mm});
            skLineSegment(sketch, "E4239", {"start": v(-35.27, -36.97) * mm, "end": v(-35.3, -37.06) * mm});
            skLineSegment(sketch, "E4240", {"start": v(-35.3, -37.06) * mm, "end": v(-35.33, -37.13) * mm});
            skLineSegment(sketch, "E4241", {"start": v(-35.33, -37.13) * mm, "end": v(-34.62, -37.79) * mm});
            skLineSegment(sketch, "E4242", {"start": v(-34.62, -37.79) * mm, "end": v(-34.55, -37.76) * mm});
            skLineSegment(sketch, "E4243", {"start": v(-34.55, -37.76) * mm, "end": v(-34.47, -37.73) * mm});
            skLineSegment(sketch, "E4244", {"start": v(-34.47, -37.73) * mm, "end": v(-34.39, -37.7) * mm});
            skLineSegment(sketch, "E4245", {"start": v(-34.39, -37.7) * mm, "end": v(-34.3, -37.65) * mm});
            skLineSegment(sketch, "E4246", {"start": v(-34.3, -37.65) * mm, "end": v(-34.23, -37.62) * mm});
            skLineSegment(sketch, "E4247", {"start": v(-34.23, -37.62) * mm, "end": v(-34.15, -37.58) * mm});
            skLineSegment(sketch, "E4248", {"start": v(-34.15, -37.58) * mm, "end": v(-34.08, -37.55) * mm});
            skLineSegment(sketch, "E4249", {"start": v(-34.08, -37.55) * mm, "end": v(-34, -37.5) * mm});
            skLineSegment(sketch, "E4250", {"start": v(-34, -37.5) * mm, "end": v(-33.93, -37.47) * mm});
            skLineSegment(sketch, "E4251", {"start": v(-33.93, -37.47) * mm, "end": v(-33.86, -37.44) * mm});
            skLineSegment(sketch, "E4252", {"start": v(-33.86, -37.44) * mm, "end": v(-33.79, -37.4) * mm});
            skLineSegment(sketch, "E4253", {"start": v(-33.79, -37.4) * mm, "end": v(-33.72, -37.37) * mm});
            skLineSegment(sketch, "E4254", {"start": v(-33.72, -37.37) * mm, "end": v(-33.65, -37.33) * mm});
            skLineSegment(sketch, "E4255", {"start": v(-33.65, -37.33) * mm, "end": v(-33.58, -37.3) * mm});
            skLineSegment(sketch, "E4256", {"start": v(-33.58, -37.3) * mm, "end": v(-33.51, -37.26) * mm});
            skLineSegment(sketch, "E4257", {"start": v(-33.51, -37.26) * mm, "end": v(-33.44, -37.22) * mm});
            skLineSegment(sketch, "E4258", {"start": v(-33.44, -37.22) * mm, "end": v(-33.38, -37.19) * mm});
            skLineSegment(sketch, "E4259", {"start": v(-33.38, -37.19) * mm, "end": v(-33.31, -37.15) * mm});
            skLineSegment(sketch, "E4260", {"start": v(-33.31, -37.15) * mm, "end": v(-33.25, -37.12) * mm});
            skLineSegment(sketch, "E4261", {"start": v(-33.25, -37.12) * mm, "end": v(-33.19, -37.08) * mm});
            skLineSegment(sketch, "E4262", {"start": v(-33.19, -37.08) * mm, "end": v(-33.12, -37.05) * mm});
            skLineSegment(sketch, "E4263", {"start": v(-33.12, -37.05) * mm, "end": v(-33.06, -37.02) * mm});
            skLineSegment(sketch, "E4264", {"start": v(-33.06, -37.02) * mm, "end": v(-33, -36.98) * mm});
            skLineSegment(sketch, "E4265", {"start": v(-33, -36.98) * mm, "end": v(-32.94, -36.95) * mm});
            skLineSegment(sketch, "E4266", {"start": v(-32.94, -36.95) * mm, "end": v(-32.88, -36.91) * mm});
            skLineSegment(sketch, "E4267", {"start": v(-32.88, -36.91) * mm, "end": v(-32.83, -36.88) * mm});
            skLineSegment(sketch, "E4268", {"start": v(-32.83, -36.88) * mm, "end": v(-32.77, -36.85) * mm});
            skLineSegment(sketch, "E4269", {"start": v(-32.77, -36.85) * mm, "end": v(-32.71, -36.81) * mm});
            skLineSegment(sketch, "E4270", {"start": v(-32.71, -36.81) * mm, "end": v(-32.66, -36.78) * mm});
            skLineSegment(sketch, "E4271", {"start": v(-32.66, -36.78) * mm, "end": v(-32.6, -36.75) * mm});
            skLineSegment(sketch, "E4272", {"start": v(-32.6, -36.75) * mm, "end": v(-32.55, -36.72) * mm});
            skLineSegment(sketch, "E4273", {"start": v(-32.55, -36.72) * mm, "end": v(-32.5, -36.68) * mm});
            skLineSegment(sketch, "E4274", {"start": v(-32.5, -36.68) * mm, "end": v(-32.45, -36.65) * mm});
            skLineSegment(sketch, "E4275", {"start": v(-32.45, -36.65) * mm, "end": v(-32.4, -36.62) * mm});
            skLineSegment(sketch, "E4276", {"start": v(-32.4, -36.62) * mm, "end": v(-32.35, -36.59) * mm});
            skLineSegment(sketch, "E4277", {"start": v(-32.35, -36.59) * mm, "end": v(-32.3, -36.56) * mm});
            skLineSegment(sketch, "E4278", {"start": v(-32.3, -36.56) * mm, "end": v(-32.25, -36.53) * mm});
            skLineSegment(sketch, "E4279", {"start": v(-32.25, -36.53) * mm, "end": v(-32.2, -36.5) * mm});
            skLineSegment(sketch, "E4280", {"start": v(-32.2, -36.5) * mm, "end": v(-32.16, -36.46) * mm});
            skLineSegment(sketch, "E4281", {"start": v(-32.16, -36.46) * mm, "end": v(-32.12, -36.43) * mm});
            skLineSegment(sketch, "E4282", {"start": v(-32.12, -36.43) * mm, "end": v(-31.9, -36.61) * mm});
            skLineSegment(sketch, "E4283", {"start": v(-31.9, -36.61) * mm, "end": v(-31.54, -36.93) * mm});
            skLineSegment(sketch, "E4284", {"start": v(-31.54, -36.93) * mm, "end": v(-31.33, -37.11) * mm});
            skLineSegment(sketch, "E4285", {"start": v(-31.33, -37.11) * mm, "end": v(-31.35, -37.16) * mm});
            skLineSegment(sketch, "E4286", {"start": v(-31.35, -37.16) * mm, "end": v(-31.38, -37.21) * mm});
            skLineSegment(sketch, "E4287", {"start": v(-31.38, -37.21) * mm, "end": v(-31.4, -37.26) * mm});
            skLineSegment(sketch, "E4288", {"start": v(-31.4, -37.26) * mm, "end": v(-31.42, -37.31) * mm});
            skLineSegment(sketch, "E4289", {"start": v(-31.42, -37.31) * mm, "end": v(-31.45, -37.37) * mm});
            skLineSegment(sketch, "E4290", {"start": v(-31.45, -37.37) * mm, "end": v(-31.47, -37.42) * mm});
            skLineSegment(sketch, "E4291", {"start": v(-31.47, -37.42) * mm, "end": v(-31.5, -37.47) * mm});
            skLineSegment(sketch, "E4292", {"start": v(-31.5, -37.47) * mm, "end": v(-31.52, -37.53) * mm});
            skLineSegment(sketch, "E4293", {"start": v(-31.52, -37.53) * mm, "end": v(-31.54, -37.59) * mm});
            skLineSegment(sketch, "E4294", {"start": v(-31.54, -37.59) * mm, "end": v(-31.57, -37.64) * mm});
            skLineSegment(sketch, "E4295", {"start": v(-31.57, -37.64) * mm, "end": v(-31.6, -37.7) * mm});
            skLineSegment(sketch, "E4296", {"start": v(-31.6, -37.7) * mm, "end": v(-31.62, -37.76) * mm});
            skLineSegment(sketch, "E4297", {"start": v(-31.62, -37.76) * mm, "end": v(-31.64, -37.82) * mm});
            skLineSegment(sketch, "E4298", {"start": v(-31.64, -37.82) * mm, "end": v(-31.67, -37.88) * mm});
            skLineSegment(sketch, "E4299", {"start": v(-31.67, -37.88) * mm, "end": v(-31.7, -37.94) * mm});
            skLineSegment(sketch, "E4300", {"start": v(-31.7, -37.94) * mm, "end": v(-31.72, -38) * mm});
            skLineSegment(sketch, "E4301", {"start": v(-31.72, -38) * mm, "end": v(-31.74, -38.07) * mm});
            skLineSegment(sketch, "E4302", {"start": v(-31.74, -38.07) * mm, "end": v(-31.77, -38.13) * mm});
            skLineSegment(sketch, "E4303", {"start": v(-31.77, -38.13) * mm, "end": v(-31.8, -38.2) * mm});
            skLineSegment(sketch, "E4304", {"start": v(-31.8, -38.2) * mm, "end": v(-31.82, -38.27) * mm});
            skLineSegment(sketch, "E4305", {"start": v(-31.82, -38.27) * mm, "end": v(-31.84, -38.33) * mm});
            skLineSegment(sketch, "E4306", {"start": v(-31.84, -38.33) * mm, "end": v(-31.87, -38.4) * mm});
            skLineSegment(sketch, "E4307", {"start": v(-31.87, -38.4) * mm, "end": v(-31.9, -38.47) * mm});
            skLineSegment(sketch, "E4308", {"start": v(-31.9, -38.47) * mm, "end": v(-31.92, -38.54) * mm});
            skLineSegment(sketch, "E4309", {"start": v(-31.92, -38.54) * mm, "end": v(-31.94, -38.61) * mm});
            skLineSegment(sketch, "E4310", {"start": v(-31.94, -38.61) * mm, "end": v(-31.97, -38.68) * mm});
            skLineSegment(sketch, "E4311", {"start": v(-31.97, -38.68) * mm, "end": v(-32, -38.76) * mm});
            skLineSegment(sketch, "E4312", {"start": v(-32, -38.76) * mm, "end": v(-32.02, -38.83) * mm});
            skLineSegment(sketch, "E4313", {"start": v(-32.02, -38.83) * mm, "end": v(-32.04, -38.9) * mm});
            skLineSegment(sketch, "E4314", {"start": v(-32.04, -38.9) * mm, "end": v(-32.07, -38.98) * mm});
            skLineSegment(sketch, "E4315", {"start": v(-32.07, -38.98) * mm, "end": v(-32.1, -39.06) * mm});
            skLineSegment(sketch, "E4316", {"start": v(-32.1, -39.06) * mm, "end": v(-32.12, -39.14) * mm});
            skLineSegment(sketch, "E4317", {"start": v(-32.12, -39.14) * mm, "end": v(-32.14, -39.22) * mm});
            skLineSegment(sketch, "E4318", {"start": v(-32.14, -39.22) * mm, "end": v(-32.17, -39.3) * mm});
            skLineSegment(sketch, "E4319", {"start": v(-32.17, -39.3) * mm, "end": v(-32.2, -39.38) * mm});
            skLineSegment(sketch, "E4320", {"start": v(-32.2, -39.38) * mm, "end": v(-32.21, -39.46) * mm});
            skLineSegment(sketch, "E4321", {"start": v(-32.21, -39.46) * mm, "end": v(-32.24, -39.54) * mm});
            skLineSegment(sketch, "E4322", {"start": v(-32.24, -39.54) * mm, "end": v(-32.26, -39.63) * mm});
            skLineSegment(sketch, "E4323", {"start": v(-32.26, -39.63) * mm, "end": v(-32.29, -39.71) * mm});
            skLineSegment(sketch, "E4324", {"start": v(-32.29, -39.71) * mm, "end": v(-32.3, -39.79) * mm});
            skLineSegment(sketch, "E4325", {"start": v(-32.3, -39.79) * mm, "end": v(-31.55, -40.39) * mm});
            skLineSegment(sketch, "E4326", {"start": v(-31.55, -40.39) * mm, "end": v(-31.48, -40.36) * mm});
            skLineSegment(sketch, "E4327", {"start": v(-31.48, -40.36) * mm, "end": v(-31.4, -40.31) * mm});
            skLineSegment(sketch, "E4328", {"start": v(-31.4, -40.31) * mm, "end": v(-31.32, -40.27) * mm});
            skLineSegment(sketch, "E4329", {"start": v(-31.32, -40.27) * mm, "end": v(-31.25, -40.23) * mm});
            skLineSegment(sketch, "E4330", {"start": v(-31.25, -40.23) * mm, "end": v(-31.17, -40.19) * mm});
            skLineSegment(sketch, "E4331", {"start": v(-31.17, -40.19) * mm, "end": v(-31.1, -40.15) * mm});
            skLineSegment(sketch, "E4332", {"start": v(-31.1, -40.15) * mm, "end": v(-31.03, -40.1) * mm});
            skLineSegment(sketch, "E4333", {"start": v(-31.03, -40.1) * mm, "end": v(-30.96, -40.06) * mm});
            skLineSegment(sketch, "E4334", {"start": v(-30.96, -40.06) * mm, "end": v(-30.89, -40.02) * mm});
            skLineSegment(sketch, "E4335", {"start": v(-30.89, -40.02) * mm, "end": v(-30.82, -39.98) * mm});
            skLineSegment(sketch, "E4336", {"start": v(-30.82, -39.98) * mm, "end": v(-30.75, -39.94) * mm});
            skLineSegment(sketch, "E4337", {"start": v(-30.75, -39.94) * mm, "end": v(-30.68, -39.9) * mm});
            skLineSegment(sketch, "E4338", {"start": v(-30.68, -39.9) * mm, "end": v(-30.61, -39.86) * mm});
            skLineSegment(sketch, "E4339", {"start": v(-30.61, -39.86) * mm, "end": v(-30.55, -39.81) * mm});
            skLineSegment(sketch, "E4340", {"start": v(-30.55, -39.81) * mm, "end": v(-30.48, -39.77) * mm});
            skLineSegment(sketch, "E4341", {"start": v(-30.48, -39.77) * mm, "end": v(-30.42, -39.73) * mm});
            skLineSegment(sketch, "E4342", {"start": v(-30.42, -39.73) * mm, "end": v(-30.36, -39.7) * mm});
            skLineSegment(sketch, "E4343", {"start": v(-30.36, -39.7) * mm, "end": v(-30.3, -39.65) * mm});
            skLineSegment(sketch, "E4344", {"start": v(-30.3, -39.65) * mm, "end": v(-30.23, -39.61) * mm});
            skLineSegment(sketch, "E4345", {"start": v(-30.23, -39.61) * mm, "end": v(-30.17, -39.57) * mm});
            skLineSegment(sketch, "E4346", {"start": v(-30.17, -39.57) * mm, "end": v(-30.11, -39.53) * mm});
            skLineSegment(sketch, "E4347", {"start": v(-30.11, -39.53) * mm, "end": v(-30.06, -39.5) * mm});
            skLineSegment(sketch, "E4348", {"start": v(-30.06, -39.5) * mm, "end": v(-30, -39.46) * mm});
            skLineSegment(sketch, "E4349", {"start": v(-30, -39.46) * mm, "end": v(-29.94, -39.42) * mm});
            skLineSegment(sketch, "E4350", {"start": v(-29.94, -39.42) * mm, "end": v(-29.89, -39.38) * mm});
            skLineSegment(sketch, "E4351", {"start": v(-29.89, -39.38) * mm, "end": v(-29.83, -39.34) * mm});
            skLineSegment(sketch, "E4352", {"start": v(-29.83, -39.34) * mm, "end": v(-29.78, -39.3) * mm});
            skLineSegment(sketch, "E4353", {"start": v(-29.78, -39.3) * mm, "end": v(-29.72, -39.27) * mm});
            skLineSegment(sketch, "E4354", {"start": v(-29.72, -39.27) * mm, "end": v(-29.67, -39.23) * mm});
            skLineSegment(sketch, "E4355", {"start": v(-29.67, -39.23) * mm, "end": v(-29.62, -39.2) * mm});
            skLineSegment(sketch, "E4356", {"start": v(-29.62, -39.2) * mm, "end": v(-29.57, -39.16) * mm});
            skLineSegment(sketch, "E4357", {"start": v(-29.57, -39.16) * mm, "end": v(-29.52, -39.12) * mm});
            skLineSegment(sketch, "E4358", {"start": v(-29.52, -39.12) * mm, "end": v(-29.47, -39.08) * mm});
            skLineSegment(sketch, "E4359", {"start": v(-29.47, -39.08) * mm, "end": v(-29.43, -39.05) * mm});
            skLineSegment(sketch, "E4360", {"start": v(-29.43, -39.05) * mm, "end": v(-29.38, -39.01) * mm});
            skLineSegment(sketch, "E4361", {"start": v(-29.38, -39.01) * mm, "end": v(-29.33, -38.98) * mm});
            skLineSegment(sketch, "E4362", {"start": v(-29.33, -38.98) * mm, "end": v(-29.29, -38.94) * mm});
            skLineSegment(sketch, "E4363", {"start": v(-29.29, -38.94) * mm, "end": v(-29.24, -38.9) * mm});
            skLineSegment(sketch, "E4364", {"start": v(-29.24, -38.9) * mm, "end": v(-29.2, -38.88) * mm});
            skLineSegment(sketch, "E4365", {"start": v(-29.2, -38.88) * mm, "end": v(-29.16, -38.84) * mm});
            skLineSegment(sketch, "E4366", {"start": v(-29.16, -38.84) * mm, "end": v(-28.93, -39) * mm});
            skLineSegment(sketch, "E4367", {"start": v(-28.93, -39) * mm, "end": v(-28.54, -39.29) * mm});
            skLineSegment(sketch, "E4368", {"start": v(-28.54, -39.29) * mm, "end": v(-28.32, -39.46) * mm});
            skLineSegment(sketch, "E4369", {"start": v(-28.32, -39.46) * mm, "end": v(-28.34, -39.5) * mm});
            skLineSegment(sketch, "E4370", {"start": v(-28.34, -39.5) * mm, "end": v(-28.36, -39.56) * mm});
            skLineSegment(sketch, "E4371", {"start": v(-28.36, -39.56) * mm, "end": v(-28.38, -39.61) * mm});
            skLineSegment(sketch, "E4372", {"start": v(-28.38, -39.61) * mm, "end": v(-28.4, -39.66) * mm});
            skLineSegment(sketch, "E4373", {"start": v(-28.4, -39.66) * mm, "end": v(-28.42, -39.72) * mm});
            skLineSegment(sketch, "E4374", {"start": v(-28.42, -39.72) * mm, "end": v(-28.44, -39.77) * mm});
            skLineSegment(sketch, "E4375", {"start": v(-28.44, -39.77) * mm, "end": v(-28.46, -39.83) * mm});
            skLineSegment(sketch, "E4376", {"start": v(-28.46, -39.83) * mm, "end": v(-28.48, -39.89) * mm});
            skLineSegment(sketch, "E4377", {"start": v(-28.48, -39.89) * mm, "end": v(-28.5, -39.94) * mm});
            skLineSegment(sketch, "E4378", {"start": v(-28.5, -39.94) * mm, "end": v(-28.52, -40) * mm});
            skLineSegment(sketch, "E4379", {"start": v(-28.52, -40) * mm, "end": v(-28.54, -40.06) * mm});
            skLineSegment(sketch, "E4380", {"start": v(-28.54, -40.06) * mm, "end": v(-28.56, -40.12) * mm});
            skLineSegment(sketch, "E4381", {"start": v(-28.56, -40.12) * mm, "end": v(-28.58, -40.19) * mm});
            skLineSegment(sketch, "E4382", {"start": v(-28.58, -40.19) * mm, "end": v(-28.6, -40.25) * mm});
            skLineSegment(sketch, "E4383", {"start": v(-28.6, -40.25) * mm, "end": v(-28.62, -40.31) * mm});
            skLineSegment(sketch, "E4384", {"start": v(-28.62, -40.31) * mm, "end": v(-28.64, -40.38) * mm});
            skLineSegment(sketch, "E4385", {"start": v(-28.64, -40.38) * mm, "end": v(-28.66, -40.44) * mm});
            skLineSegment(sketch, "E4386", {"start": v(-28.66, -40.44) * mm, "end": v(-28.68, -40.5) * mm});
            skLineSegment(sketch, "E4387", {"start": v(-28.68, -40.5) * mm, "end": v(-28.7, -40.58) * mm});
            skLineSegment(sketch, "E4388", {"start": v(-28.7, -40.58) * mm, "end": v(-28.72, -40.64) * mm});
            skLineSegment(sketch, "E4389", {"start": v(-28.72, -40.64) * mm, "end": v(-28.74, -40.71) * mm});
            skLineSegment(sketch, "E4390", {"start": v(-28.74, -40.71) * mm, "end": v(-28.76, -40.78) * mm});
            skLineSegment(sketch, "E4391", {"start": v(-28.76, -40.78) * mm, "end": v(-28.78, -40.85) * mm});
            skLineSegment(sketch, "E4392", {"start": v(-28.78, -40.85) * mm, "end": v(-28.8, -40.93) * mm});
            skLineSegment(sketch, "E4393", {"start": v(-28.8, -40.93) * mm, "end": v(-28.81, -41) * mm});
            skLineSegment(sketch, "E4394", {"start": v(-28.81, -41) * mm, "end": v(-28.83, -41.07) * mm});
            skLineSegment(sketch, "E4395", {"start": v(-28.83, -41.07) * mm, "end": v(-28.85, -41.15) * mm});
            skLineSegment(sketch, "E4396", {"start": v(-28.85, -41.15) * mm, "end": v(-28.87, -41.22) * mm});
            skLineSegment(sketch, "E4397", {"start": v(-28.87, -41.22) * mm, "end": v(-28.9, -41.3) * mm});
            skLineSegment(sketch, "E4398", {"start": v(-28.9, -41.3) * mm, "end": v(-28.9, -41.38) * mm});
            skLineSegment(sketch, "E4399", {"start": v(-28.9, -41.38) * mm, "end": v(-28.93, -41.46) * mm});
            skLineSegment(sketch, "E4400", {"start": v(-28.93, -41.46) * mm, "end": v(-28.95, -41.54) * mm});
            skLineSegment(sketch, "E4401", {"start": v(-28.95, -41.54) * mm, "end": v(-28.97, -41.62) * mm});
            skLineSegment(sketch, "E4402", {"start": v(-28.97, -41.62) * mm, "end": v(-28.98, -41.7) * mm});
            skLineSegment(sketch, "E4403", {"start": v(-28.98, -41.7) * mm, "end": v(-29, -41.78) * mm});
            skLineSegment(sketch, "E4404", {"start": v(-29, -41.78) * mm, "end": v(-29.02, -41.87) * mm});
            skLineSegment(sketch, "E4405", {"start": v(-29.02, -41.87) * mm, "end": v(-29.04, -41.95) * mm});
            skLineSegment(sketch, "E4406", {"start": v(-29.04, -41.95) * mm, "end": v(-29.05, -42.04) * mm});
            skLineSegment(sketch, "E4407", {"start": v(-29.05, -42.04) * mm, "end": v(-29.07, -42.12) * mm});
            skLineSegment(sketch, "E4408", {"start": v(-29.07, -42.12) * mm, "end": v(-29.08, -42.2) * mm});
            skLineSegment(sketch, "E4409", {"start": v(-29.08, -42.2) * mm, "end": v(-28.28, -42.74) * mm});
            skLineSegment(sketch, "E4410", {"start": v(-28.28, -42.74) * mm, "end": v(-28.21, -42.7) * mm});
            skLineSegment(sketch, "E4411", {"start": v(-28.21, -42.7) * mm, "end": v(-28.14, -42.65) * mm});
            skLineSegment(sketch, "E4412", {"start": v(-28.14, -42.65) * mm, "end": v(-28.07, -42.6) * mm});
            skLineSegment(sketch, "E4413", {"start": v(-28.07, -42.6) * mm, "end": v(-28, -42.56) * mm});
            skLineSegment(sketch, "E4414", {"start": v(-28, -42.56) * mm, "end": v(-27.93, -42.5) * mm});
            skLineSegment(sketch, "E4415", {"start": v(-27.93, -42.5) * mm, "end": v(-27.86, -42.46) * mm});
            skLineSegment(sketch, "E4416", {"start": v(-27.86, -42.46) * mm, "end": v(-27.79, -42.41) * mm});
            skLineSegment(sketch, "E4417", {"start": v(-27.79, -42.41) * mm, "end": v(-27.72, -42.37) * mm});
            skLineSegment(sketch, "E4418", {"start": v(-27.72, -42.37) * mm, "end": v(-27.65, -42.32) * mm});
            skLineSegment(sketch, "E4419", {"start": v(-27.65, -42.32) * mm, "end": v(-27.59, -42.27) * mm});
            skLineSegment(sketch, "E4420", {"start": v(-27.59, -42.27) * mm, "end": v(-27.52, -42.23) * mm});
            skLineSegment(sketch, "E4421", {"start": v(-27.52, -42.23) * mm, "end": v(-27.46, -42.18) * mm});
            skLineSegment(sketch, "E4422", {"start": v(-27.46, -42.18) * mm, "end": v(-27.4, -42.13) * mm});
            skLineSegment(sketch, "E4423", {"start": v(-27.4, -42.13) * mm, "end": v(-27.33, -42.09) * mm});
            skLineSegment(sketch, "E4424", {"start": v(-27.33, -42.09) * mm, "end": v(-27.27, -42.04) * mm});
            skLineSegment(sketch, "E4425", {"start": v(-27.27, -42.04) * mm, "end": v(-27.2, -42) * mm});
            skLineSegment(sketch, "E4426", {"start": v(-27.2, -42) * mm, "end": v(-27.15, -41.95) * mm});
            skLineSegment(sketch, "E4427", {"start": v(-27.15, -41.95) * mm, "end": v(-27.1, -41.9) * mm});
            skLineSegment(sketch, "E4428", {"start": v(-27.1, -41.9) * mm, "end": v(-27.03, -41.86) * mm});
            skLineSegment(sketch, "E4429", {"start": v(-27.03, -41.86) * mm, "end": v(-26.98, -41.82) * mm});
            skLineSegment(sketch, "E4430", {"start": v(-26.98, -41.82) * mm, "end": v(-26.92, -41.78) * mm});
            skLineSegment(sketch, "E4431", {"start": v(-26.92, -41.78) * mm, "end": v(-26.86, -41.73) * mm});
            skLineSegment(sketch, "E4432", {"start": v(-26.86, -41.73) * mm, "end": v(-26.81, -41.69) * mm});
            skLineSegment(sketch, "E4433", {"start": v(-26.81, -41.69) * mm, "end": v(-26.76, -41.65) * mm});
            skLineSegment(sketch, "E4434", {"start": v(-26.76, -41.65) * mm, "end": v(-26.7, -41.6) * mm});
            skLineSegment(sketch, "E4435", {"start": v(-26.7, -41.6) * mm, "end": v(-26.65, -41.56) * mm});
            skLineSegment(sketch, "E4436", {"start": v(-26.65, -41.56) * mm, "end": v(-26.6, -41.52) * mm});
            skLineSegment(sketch, "E4437", {"start": v(-26.6, -41.52) * mm, "end": v(-26.55, -41.48) * mm});
            skLineSegment(sketch, "E4438", {"start": v(-26.55, -41.48) * mm, "end": v(-26.5, -41.44) * mm});
            skLineSegment(sketch, "E4439", {"start": v(-26.5, -41.44) * mm, "end": v(-26.46, -41.4) * mm});
            skLineSegment(sketch, "E4440", {"start": v(-26.46, -41.4) * mm, "end": v(-26.4, -41.36) * mm});
            skLineSegment(sketch, "E4441", {"start": v(-26.4, -41.36) * mm, "end": v(-26.36, -41.32) * mm});
            skLineSegment(sketch, "E4442", {"start": v(-26.36, -41.32) * mm, "end": v(-26.32, -41.28) * mm});
            skLineSegment(sketch, "E4443", {"start": v(-26.32, -41.28) * mm, "end": v(-26.27, -41.24) * mm});
            skLineSegment(sketch, "E4444", {"start": v(-26.27, -41.24) * mm, "end": v(-26.23, -41.2) * mm});
            skLineSegment(sketch, "E4445", {"start": v(-26.23, -41.2) * mm, "end": v(-26.18, -41.16) * mm});
            skLineSegment(sketch, "E4446", {"start": v(-26.18, -41.16) * mm, "end": v(-26.14, -41.12) * mm});
            skLineSegment(sketch, "E4447", {"start": v(-26.14, -41.12) * mm, "end": v(-26.1, -41.08) * mm});
            skLineSegment(sketch, "E4448", {"start": v(-26.1, -41.08) * mm, "end": v(-26.06, -41.05) * mm});
            skLineSegment(sketch, "E4449", {"start": v(-26.06, -41.05) * mm, "end": v(-26.02, -41) * mm});
            skLineSegment(sketch, "E4450", {"start": v(-26.02, -41) * mm, "end": v(-25.78, -41.15) * mm});
            skLineSegment(sketch, "E4451", {"start": v(-25.78, -41.15) * mm, "end": v(-25.37, -41.4) * mm});
            skLineSegment(sketch, "E4452", {"start": v(-25.37, -41.4) * mm, "end": v(-25.14, -41.56) * mm});
            skLineSegment(sketch, "E4453", {"start": v(-25.14, -41.56) * mm, "end": v(-25.15, -41.6) * mm});
            skLineSegment(sketch, "E4454", {"start": v(-25.15, -41.6) * mm, "end": v(-25.17, -41.66) * mm});
            skLineSegment(sketch, "E4455", {"start": v(-25.17, -41.66) * mm, "end": v(-25.18, -41.71) * mm});
            skLineSegment(sketch, "E4456", {"start": v(-25.18, -41.71) * mm, "end": v(-25.2, -41.77) * mm});
            skLineSegment(sketch, "E4457", {"start": v(-25.2, -41.77) * mm, "end": v(-25.21, -41.83) * mm});
            skLineSegment(sketch, "E4458", {"start": v(-25.21, -41.83) * mm, "end": v(-25.23, -41.88) * mm});
            skLineSegment(sketch, "E4459", {"start": v(-25.23, -41.88) * mm, "end": v(-25.25, -41.94) * mm});
            skLineSegment(sketch, "E4460", {"start": v(-25.25, -41.94) * mm, "end": v(-25.26, -42) * mm});
            skLineSegment(sketch, "E4461", {"start": v(-25.26, -42) * mm, "end": v(-25.28, -42.06) * mm});
            skLineSegment(sketch, "E4462", {"start": v(-25.28, -42.06) * mm, "end": v(-25.3, -42.12) * mm});
            skLineSegment(sketch, "E4463", {"start": v(-25.3, -42.12) * mm, "end": v(-25.3, -42.18) * mm});
            skLineSegment(sketch, "E4464", {"start": v(-25.3, -42.18) * mm, "end": v(-25.32, -42.24) * mm});
            skLineSegment(sketch, "E4465", {"start": v(-25.32, -42.24) * mm, "end": v(-25.34, -42.3) * mm});
            skLineSegment(sketch, "E4466", {"start": v(-25.34, -42.3) * mm, "end": v(-25.35, -42.37) * mm});
            skLineSegment(sketch, "E4467", {"start": v(-25.35, -42.37) * mm, "end": v(-25.37, -42.43) * mm});
            skLineSegment(sketch, "E4468", {"start": v(-25.37, -42.43) * mm, "end": v(-25.38, -42.5) * mm});
            skLineSegment(sketch, "E4469", {"start": v(-25.38, -42.5) * mm, "end": v(-25.4, -42.57) * mm});
            skLineSegment(sketch, "E4470", {"start": v(-25.4, -42.57) * mm, "end": v(-25.4, -42.63) * mm});
            skLineSegment(sketch, "E4471", {"start": v(-25.4, -42.63) * mm, "end": v(-25.42, -42.7) * mm});
            skLineSegment(sketch, "E4472", {"start": v(-25.42, -42.7) * mm, "end": v(-25.44, -42.77) * mm});
            skLineSegment(sketch, "E4473", {"start": v(-25.44, -42.77) * mm, "end": v(-25.45, -42.84) * mm});
            skLineSegment(sketch, "E4474", {"start": v(-25.45, -42.84) * mm, "end": v(-25.47, -42.91) * mm});
            skLineSegment(sketch, "E4475", {"start": v(-25.47, -42.91) * mm, "end": v(-25.48, -42.99) * mm});
            skLineSegment(sketch, "E4476", {"start": v(-25.48, -42.99) * mm, "end": v(-25.5, -43.06) * mm});
            skLineSegment(sketch, "E4477", {"start": v(-25.5, -43.06) * mm, "end": v(-25.5, -43.13) * mm});
            skLineSegment(sketch, "E4478", {"start": v(-25.5, -43.13) * mm, "end": v(-25.52, -43.2) * mm});
            skLineSegment(sketch, "E4479", {"start": v(-25.52, -43.2) * mm, "end": v(-25.54, -43.29) * mm});
            skLineSegment(sketch, "E4480", {"start": v(-25.54, -43.29) * mm, "end": v(-25.55, -43.36) * mm});
            skLineSegment(sketch, "E4481", {"start": v(-25.55, -43.36) * mm, "end": v(-25.56, -43.44) * mm});
            skLineSegment(sketch, "E4482", {"start": v(-25.56, -43.44) * mm, "end": v(-25.57, -43.52) * mm});
            skLineSegment(sketch, "E4483", {"start": v(-25.57, -43.52) * mm, "end": v(-25.59, -43.6) * mm});
            skLineSegment(sketch, "E4484", {"start": v(-25.59, -43.6) * mm, "end": v(-25.6, -43.68) * mm});
            skLineSegment(sketch, "E4485", {"start": v(-25.6, -43.68) * mm, "end": v(-25.61, -43.76) * mm});
            skLineSegment(sketch, "E4486", {"start": v(-25.61, -43.76) * mm, "end": v(-25.62, -43.85) * mm});
            skLineSegment(sketch, "E4487", {"start": v(-25.62, -43.85) * mm, "end": v(-25.63, -43.93) * mm});
            skLineSegment(sketch, "E4488", {"start": v(-25.63, -43.93) * mm, "end": v(-25.65, -44.01) * mm});
            skLineSegment(sketch, "E4489", {"start": v(-25.65, -44.01) * mm, "end": v(-25.66, -44.1) * mm});
            skLineSegment(sketch, "E4490", {"start": v(-25.66, -44.1) * mm, "end": v(-25.67, -44.19) * mm});
            skLineSegment(sketch, "E4491", {"start": v(-25.67, -44.19) * mm, "end": v(-25.68, -44.27) * mm});
            skLineSegment(sketch, "E4492", {"start": v(-25.68, -44.27) * mm, "end": v(-25.68, -44.35) * mm});
            skLineSegment(sketch, "E4493", {"start": v(-25.68, -44.35) * mm, "end": v(-24.84, -44.83) * mm});
            skLineSegment(sketch, "E4494", {"start": v(-24.84, -44.83) * mm, "end": v(-24.78, -44.78) * mm});
            skLineSegment(sketch, "E4495", {"start": v(-24.78, -44.78) * mm, "end": v(-24.7, -44.73) * mm});
            skLineSegment(sketch, "E4496", {"start": v(-24.7, -44.73) * mm, "end": v(-24.64, -44.68) * mm});
            skLineSegment(sketch, "E4497", {"start": v(-24.64, -44.68) * mm, "end": v(-24.57, -44.62) * mm});
            skLineSegment(sketch, "E4498", {"start": v(-24.57, -44.62) * mm, "end": v(-24.5, -44.57) * mm});
            skLineSegment(sketch, "E4499", {"start": v(-24.5, -44.57) * mm, "end": v(-24.44, -44.52) * mm});
            skLineSegment(sketch, "E4500", {"start": v(-24.44, -44.52) * mm, "end": v(-24.37, -44.46) * mm});
            skLineSegment(sketch, "E4501", {"start": v(-24.37, -44.46) * mm, "end": v(-24.3, -44.41) * mm});
            skLineSegment(sketch, "E4502", {"start": v(-24.3, -44.41) * mm, "end": v(-24.25, -44.36) * mm});
            skLineSegment(sketch, "E4503", {"start": v(-24.25, -44.36) * mm, "end": v(-24.18, -44.3) * mm});
            skLineSegment(sketch, "E4504", {"start": v(-24.18, -44.3) * mm, "end": v(-24.12, -44.26) * mm});
            skLineSegment(sketch, "E4505", {"start": v(-24.12, -44.26) * mm, "end": v(-24.06, -44.2) * mm});
            skLineSegment(sketch, "E4506", {"start": v(-24.06, -44.2) * mm, "end": v(-24, -44.15) * mm});
            skLineSegment(sketch, "E4507", {"start": v(-24, -44.15) * mm, "end": v(-23.94, -44.1) * mm});
            skLineSegment(sketch, "E4508", {"start": v(-23.94, -44.1) * mm, "end": v(-23.89, -44.05) * mm});
            skLineSegment(sketch, "E4509", {"start": v(-23.89, -44.05) * mm, "end": v(-23.83, -44) * mm});
            skLineSegment(sketch, "E4510", {"start": v(-23.83, -44) * mm, "end": v(-23.77, -43.95) * mm});
            skLineSegment(sketch, "E4511", {"start": v(-23.77, -43.95) * mm, "end": v(-23.72, -43.9) * mm});
            skLineSegment(sketch, "E4512", {"start": v(-23.72, -43.9) * mm, "end": v(-23.66, -43.86) * mm});
            skLineSegment(sketch, "E4513", {"start": v(-23.66, -43.86) * mm, "end": v(-23.61, -43.8) * mm});
            skLineSegment(sketch, "E4514", {"start": v(-23.61, -43.8) * mm, "end": v(-23.56, -43.76) * mm});
            skLineSegment(sketch, "E4515", {"start": v(-23.56, -43.76) * mm, "end": v(-23.5, -43.71) * mm});
            skLineSegment(sketch, "E4516", {"start": v(-23.5, -43.71) * mm, "end": v(-23.46, -43.66) * mm});
            skLineSegment(sketch, "E4517", {"start": v(-23.46, -43.66) * mm, "end": v(-23.4, -43.62) * mm});
            skLineSegment(sketch, "E4518", {"start": v(-23.4, -43.62) * mm, "end": v(-23.36, -43.57) * mm});
            skLineSegment(sketch, "E4519", {"start": v(-23.36, -43.57) * mm, "end": v(-23.3, -43.52) * mm});
            skLineSegment(sketch, "E4520", {"start": v(-23.3, -43.52) * mm, "end": v(-23.26, -43.48) * mm});
            skLineSegment(sketch, "E4521", {"start": v(-23.26, -43.48) * mm, "end": v(-23.22, -43.43) * mm});
            skLineSegment(sketch, "E4522", {"start": v(-23.22, -43.43) * mm, "end": v(-23.17, -43.39) * mm});
            skLineSegment(sketch, "E4523", {"start": v(-23.17, -43.39) * mm, "end": v(-23.13, -43.34) * mm});
            skLineSegment(sketch, "E4524", {"start": v(-23.13, -43.34) * mm, "end": v(-23.08, -43.3) * mm});
            skLineSegment(sketch, "E4525", {"start": v(-23.08, -43.3) * mm, "end": v(-23.04, -43.26) * mm});
            skLineSegment(sketch, "E4526", {"start": v(-23.04, -43.26) * mm, "end": v(-23, -43.21) * mm});
            skLineSegment(sketch, "E4527", {"start": v(-23, -43.21) * mm, "end": v(-22.96, -43.17) * mm});
            skLineSegment(sketch, "E4528", {"start": v(-22.96, -43.17) * mm, "end": v(-22.91, -43.13) * mm});
            skLineSegment(sketch, "E4529", {"start": v(-22.91, -43.13) * mm, "end": v(-22.87, -43.09) * mm});
            skLineSegment(sketch, "E4530", {"start": v(-22.87, -43.09) * mm, "end": v(-22.84, -43.05) * mm});
            skLineSegment(sketch, "E4531", {"start": v(-22.84, -43.05) * mm, "end": v(-22.8, -43) * mm});
            skLineSegment(sketch, "E4532", {"start": v(-22.8, -43) * mm, "end": v(-22.76, -42.96) * mm});
            skLineSegment(sketch, "E4533", {"start": v(-22.76, -42.96) * mm, "end": v(-22.72, -42.92) * mm});
            skLineSegment(sketch, "E4534", {"start": v(-22.72, -42.92) * mm, "end": v(-22.47, -43.05) * mm});
            skLineSegment(sketch, "E4535", {"start": v(-22.47, -43.05) * mm, "end": v(-22.05, -43.27) * mm});
            skLineSegment(sketch, "E4536", {"start": v(-22.05, -43.27) * mm, "end": v(-21.8, -43.4) * mm});
            skLineSegment(sketch, "E4537", {"start": v(-21.8, -43.4) * mm, "end": v(-21.81, -43.45) * mm});
            skLineSegment(sketch, "E4538", {"start": v(-21.81, -43.45) * mm, "end": v(-21.82, -43.5) * mm});
            skLineSegment(sketch, "E4539", {"start": v(-21.82, -43.5) * mm, "end": v(-21.83, -43.56) * mm});
            skLineSegment(sketch, "E4540", {"start": v(-21.83, -43.56) * mm, "end": v(-21.84, -43.62) * mm});
            skLineSegment(sketch, "E4541", {"start": v(-21.84, -43.62) * mm, "end": v(-21.86, -43.67) * mm});
            skLineSegment(sketch, "E4542", {"start": v(-21.86, -43.67) * mm, "end": v(-21.87, -43.73) * mm});
            skLineSegment(sketch, "E4543", {"start": v(-21.87, -43.73) * mm, "end": v(-21.88, -43.8) * mm});
            skLineSegment(sketch, "E4544", {"start": v(-21.88, -43.8) * mm, "end": v(-21.89, -43.85) * mm});
            skLineSegment(sketch, "E4545", {"start": v(-21.89, -43.85) * mm, "end": v(-21.9, -43.91) * mm});
            skLineSegment(sketch, "E4546", {"start": v(-21.9, -43.91) * mm, "end": v(-21.9, -43.97) * mm});
            skLineSegment(sketch, "E4547", {"start": v(-21.9, -43.97) * mm, "end": v(-21.92, -44.03) * mm});
            skLineSegment(sketch, "E4548", {"start": v(-21.92, -44.03) * mm, "end": v(-21.93, -44.1) * mm});
            skLineSegment(sketch, "E4549", {"start": v(-21.93, -44.1) * mm, "end": v(-21.94, -44.16) * mm});
            skLineSegment(sketch, "E4550", {"start": v(-21.94, -44.16) * mm, "end": v(-21.95, -44.23) * mm});
            skLineSegment(sketch, "E4551", {"start": v(-21.95, -44.23) * mm, "end": v(-21.96, -44.3) * mm});
            skLineSegment(sketch, "E4552", {"start": v(-21.96, -44.3) * mm, "end": v(-21.97, -44.36) * mm});
            skLineSegment(sketch, "E4553", {"start": v(-21.97, -44.36) * mm, "end": v(-21.98, -44.43) * mm});
            skLineSegment(sketch, "E4554", {"start": v(-21.98, -44.43) * mm, "end": v(-21.99, -44.5) * mm});
            skLineSegment(sketch, "E4555", {"start": v(-21.99, -44.5) * mm, "end": v(-22, -44.57) * mm});
            skLineSegment(sketch, "E4556", {"start": v(-22, -44.57) * mm, "end": v(-22, -44.64) * mm});
            skLineSegment(sketch, "E4557", {"start": v(-22, -44.64) * mm, "end": v(-22.01, -44.7) * mm});
            skLineSegment(sketch, "E4558", {"start": v(-22.01, -44.7) * mm, "end": v(-22.02, -44.78) * mm});
            skLineSegment(sketch, "E4559", {"start": v(-22.02, -44.78) * mm, "end": v(-22.03, -44.85) * mm});
            skLineSegment(sketch, "E4560", {"start": v(-22.03, -44.85) * mm, "end": v(-22.04, -44.93) * mm});
            skLineSegment(sketch, "E4561", {"start": v(-22.04, -44.93) * mm, "end": v(-22.05, -45) * mm});
            skLineSegment(sketch, "E4562", {"start": v(-22.05, -45) * mm, "end": v(-22.05, -45.08) * mm});
            skLineSegment(sketch, "E4563", {"start": v(-22.05, -45.08) * mm, "end": v(-22.06, -45.16) * mm});
            skLineSegment(sketch, "E4564", {"start": v(-22.06, -45.16) * mm, "end": v(-22.07, -45.23) * mm});
            skLineSegment(sketch, "E4565", {"start": v(-22.07, -45.23) * mm, "end": v(-22.07, -45.31) * mm});
            skLineSegment(sketch, "E4566", {"start": v(-22.07, -45.31) * mm, "end": v(-22.08, -45.4) * mm});
            skLineSegment(sketch, "E4567", {"start": v(-22.08, -45.4) * mm, "end": v(-22.09, -45.47) * mm});
            skLineSegment(sketch, "E4568", {"start": v(-22.09, -45.47) * mm, "end": v(-22.1, -45.55) * mm});
            skLineSegment(sketch, "E4569", {"start": v(-22.1, -45.55) * mm, "end": v(-22.1, -45.64) * mm});
            skLineSegment(sketch, "E4570", {"start": v(-22.1, -45.64) * mm, "end": v(-22.1, -45.72) * mm});
            skLineSegment(sketch, "E4571", {"start": v(-22.1, -45.72) * mm, "end": v(-22.1, -45.8) * mm});
            skLineSegment(sketch, "E4572", {"start": v(-22.1, -45.8) * mm, "end": v(-22.11, -45.9) * mm});
            skLineSegment(sketch, "E4573", {"start": v(-22.11, -45.9) * mm, "end": v(-22.12, -45.98) * mm});
            skLineSegment(sketch, "E4574", {"start": v(-22.12, -45.98) * mm, "end": v(-22.12, -46.06) * mm});
            skLineSegment(sketch, "E4575", {"start": v(-22.12, -46.06) * mm, "end": v(-22.12, -46.15) * mm});
            skLineSegment(sketch, "E4576", {"start": v(-22.12, -46.15) * mm, "end": v(-22.12, -46.23) * mm});
            skLineSegment(sketch, "E4577", {"start": v(-22.12, -46.23) * mm, "end": v(-21.25, -46.64) * mm});
            skLineSegment(sketch, "E4578", {"start": v(-21.25, -46.64) * mm, "end": v(-21.19, -46.59) * mm});
            skLineSegment(sketch, "E4579", {"start": v(-21.19, -46.59) * mm, "end": v(-21.12, -46.53) * mm});
            skLineSegment(sketch, "E4580", {"start": v(-21.12, -46.53) * mm, "end": v(-21.06, -46.47) * mm});
            skLineSegment(sketch, "E4581", {"start": v(-21.06, -46.47) * mm, "end": v(-21, -46.41) * mm});
            skLineSegment(sketch, "E4582", {"start": v(-21, -46.41) * mm, "end": v(-20.93, -46.35) * mm});
            skLineSegment(sketch, "E4583", {"start": v(-20.93, -46.35) * mm, "end": v(-20.87, -46.3) * mm});
            skLineSegment(sketch, "E4584", {"start": v(-20.87, -46.3) * mm, "end": v(-20.8, -46.24) * mm});
            skLineSegment(sketch, "E4585", {"start": v(-20.8, -46.24) * mm, "end": v(-20.75, -46.18) * mm});
            skLineSegment(sketch, "E4586", {"start": v(-20.75, -46.18) * mm, "end": v(-20.7, -46.12) * mm});
            skLineSegment(sketch, "E4587", {"start": v(-20.7, -46.12) * mm, "end": v(-20.63, -46.07) * mm});
            skLineSegment(sketch, "E4588", {"start": v(-20.63, -46.07) * mm, "end": v(-20.58, -46.01) * mm});
            skLineSegment(sketch, "E4589", {"start": v(-20.58, -46.01) * mm, "end": v(-20.52, -45.96) * mm});
            skLineSegment(sketch, "E4590", {"start": v(-20.52, -45.96) * mm, "end": v(-20.46, -45.9) * mm});
            skLineSegment(sketch, "E4591", {"start": v(-20.46, -45.9) * mm, "end": v(-20.4, -45.85) * mm});
            skLineSegment(sketch, "E4592", {"start": v(-20.4, -45.85) * mm, "end": v(-20.36, -45.8) * mm});
            skLineSegment(sketch, "E4593", {"start": v(-20.36, -45.8) * mm, "end": v(-20.3, -45.74) * mm});
            skLineSegment(sketch, "E4594", {"start": v(-20.3, -45.74) * mm, "end": v(-20.25, -45.68) * mm});
            skLineSegment(sketch, "E4595", {"start": v(-20.25, -45.68) * mm, "end": v(-20.2, -45.63) * mm});
            skLineSegment(sketch, "E4596", {"start": v(-20.2, -45.63) * mm, "end": v(-20.15, -45.58) * mm});
            skLineSegment(sketch, "E4597", {"start": v(-20.15, -45.58) * mm, "end": v(-20.1, -45.52) * mm});
            skLineSegment(sketch, "E4598", {"start": v(-20.1, -45.52) * mm, "end": v(-20.05, -45.47) * mm});
            skLineSegment(sketch, "E4599", {"start": v(-20.05, -45.47) * mm, "end": v(-20, -45.42) * mm});
            skLineSegment(sketch, "E4600", {"start": v(-20, -45.42) * mm, "end": v(-19.96, -45.37) * mm});
            skLineSegment(sketch, "E4601", {"start": v(-19.96, -45.37) * mm, "end": v(-19.91, -45.32) * mm});
            skLineSegment(sketch, "E4602", {"start": v(-19.91, -45.32) * mm, "end": v(-19.87, -45.27) * mm});
            skLineSegment(sketch, "E4603", {"start": v(-19.87, -45.27) * mm, "end": v(-19.82, -45.22) * mm});
            skLineSegment(sketch, "E4604", {"start": v(-19.82, -45.22) * mm, "end": v(-19.78, -45.17) * mm});
            skLineSegment(sketch, "E4605", {"start": v(-19.78, -45.17) * mm, "end": v(-19.74, -45.12) * mm});
            skLineSegment(sketch, "E4606", {"start": v(-19.74, -45.12) * mm, "end": v(-19.7, -45.07) * mm});
            skLineSegment(sketch, "E4607", {"start": v(-19.7, -45.07) * mm, "end": v(-19.65, -45.02) * mm});
            skLineSegment(sketch, "E4608", {"start": v(-19.65, -45.02) * mm, "end": v(-19.61, -44.98) * mm});
            skLineSegment(sketch, "E4609", {"start": v(-19.61, -44.98) * mm, "end": v(-19.57, -44.93) * mm});
            skLineSegment(sketch, "E4610", {"start": v(-19.57, -44.93) * mm, "end": v(-19.54, -44.88) * mm});
            skLineSegment(sketch, "E4611", {"start": v(-19.54, -44.88) * mm, "end": v(-19.5, -44.84) * mm});
            skLineSegment(sketch, "E4612", {"start": v(-19.5, -44.84) * mm, "end": v(-19.46, -44.8) * mm});
            skLineSegment(sketch, "E4613", {"start": v(-19.46, -44.8) * mm, "end": v(-19.42, -44.75) * mm});
            skLineSegment(sketch, "E4614", {"start": v(-19.42, -44.75) * mm, "end": v(-19.39, -44.7) * mm});
            skLineSegment(sketch, "E4615", {"start": v(-19.39, -44.7) * mm, "end": v(-19.35, -44.66) * mm});
            skLineSegment(sketch, "E4616", {"start": v(-19.35, -44.66) * mm, "end": v(-19.32, -44.62) * mm});
            skLineSegment(sketch, "E4617", {"start": v(-19.32, -44.62) * mm, "end": v(-19.29, -44.58) * mm});
            skLineSegment(sketch, "E4618", {"start": v(-19.29, -44.58) * mm, "end": v(-19.03, -44.68) * mm});
            skLineSegment(sketch, "E4619", {"start": v(-19.03, -44.68) * mm, "end": v(-18.58, -44.87) * mm});
            skLineSegment(sketch, "E4620", {"start": v(-18.58, -44.87) * mm, "end": v(-18.33, -44.98) * mm});
            skLineSegment(sketch, "E4621", {"start": v(-18.33, -44.98) * mm, "end": v(-18.34, -45.03) * mm});
            skLineSegment(sketch, "E4622", {"start": v(-18.34, -45.03) * mm, "end": v(-18.34, -45.09) * mm});
            skLineSegment(sketch, "E4623", {"start": v(-18.34, -45.09) * mm, "end": v(-18.35, -45.14) * mm});
            skLineSegment(sketch, "E4624", {"start": v(-18.35, -45.14) * mm, "end": v(-18.36, -45.2) * mm});
            skLineSegment(sketch, "E4625", {"start": v(-18.36, -45.2) * mm, "end": v(-18.36, -45.25) * mm});
            skLineSegment(sketch, "E4626", {"start": v(-18.36, -45.25) * mm, "end": v(-18.37, -45.31) * mm});
            skLineSegment(sketch, "E4627", {"start": v(-18.37, -45.31) * mm, "end": v(-18.37, -45.37) * mm});
            skLineSegment(sketch, "E4628", {"start": v(-18.37, -45.37) * mm, "end": v(-18.38, -45.43) * mm});
            skLineSegment(sketch, "E4629", {"start": v(-18.38, -45.43) * mm, "end": v(-18.39, -45.5) * mm});
            skLineSegment(sketch, "E4630", {"start": v(-18.39, -45.5) * mm, "end": v(-18.4, -45.56) * mm});
            skLineSegment(sketch, "E4631", {"start": v(-18.4, -45.56) * mm, "end": v(-18.4, -45.62) * mm});
            skLineSegment(sketch, "E4632", {"start": v(-18.4, -45.62) * mm, "end": v(-18.4, -45.68) * mm});
            skLineSegment(sketch, "E4633", {"start": v(-18.4, -45.68) * mm, "end": v(-18.4, -45.75) * mm});
            skLineSegment(sketch, "E4634", {"start": v(-18.4, -45.75) * mm, "end": v(-18.41, -45.81) * mm});
            skLineSegment(sketch, "E4635", {"start": v(-18.41, -45.81) * mm, "end": v(-18.42, -45.88) * mm});
            skLineSegment(sketch, "E4636", {"start": v(-18.42, -45.88) * mm, "end": v(-18.42, -45.95) * mm});
            skLineSegment(sketch, "E4637", {"start": v(-18.42, -45.95) * mm, "end": v(-18.42, -46.01) * mm});
            skLineSegment(sketch, "E4638", {"start": v(-18.42, -46.01) * mm, "end": v(-18.43, -46.08) * mm});
            skLineSegment(sketch, "E4639", {"start": v(-18.43, -46.08) * mm, "end": v(-18.43, -46.15) * mm});
            skLineSegment(sketch, "E4640", {"start": v(-18.43, -46.15) * mm, "end": v(-18.43, -46.22) * mm});
            skLineSegment(sketch, "E4641", {"start": v(-18.43, -46.22) * mm, "end": v(-18.44, -46.3) * mm});
            skLineSegment(sketch, "E4642", {"start": v(-18.44, -46.3) * mm, "end": v(-18.44, -46.37) * mm});
            skLineSegment(sketch, "E4643", {"start": v(-18.44, -46.37) * mm, "end": v(-18.44, -46.44) * mm});
            skLineSegment(sketch, "E4644", {"start": v(-18.44, -46.44) * mm, "end": v(-18.44, -46.52) * mm});
            skLineSegment(sketch, "E4645", {"start": v(-18.44, -46.52) * mm, "end": v(-18.45, -46.6) * mm});
            skLineSegment(sketch, "E4646", {"start": v(-18.45, -46.6) * mm, "end": v(-18.45, -46.67) * mm});
            skLineSegment(sketch, "E4647", {"start": v(-18.45, -46.67) * mm, "end": v(-18.45, -46.75) * mm});
            skLineSegment(sketch, "E4648", {"start": v(-18.45, -46.75) * mm, "end": v(-18.45, -46.83) * mm});
            skLineSegment(sketch, "E4649", {"start": v(-18.45, -46.83) * mm, "end": v(-18.45, -46.9) * mm});
            skLineSegment(sketch, "E4650", {"start": v(-18.45, -46.9) * mm, "end": v(-18.45, -46.98) * mm});
            skLineSegment(sketch, "E4651", {"start": v(-18.45, -46.98) * mm, "end": v(-18.45, -47.07) * mm});
            skLineSegment(sketch, "E4652", {"start": v(-18.45, -47.07) * mm, "end": v(-18.45, -47.15) * mm});
            skLineSegment(sketch, "E4653", {"start": v(-18.45, -47.15) * mm, "end": v(-18.45, -47.23) * mm});
            skLineSegment(sketch, "E4654", {"start": v(-18.45, -47.23) * mm, "end": v(-18.45, -47.31) * mm});
            skLineSegment(sketch, "E4655", {"start": v(-18.45, -47.31) * mm, "end": v(-18.45, -47.4) * mm});
            skLineSegment(sketch, "E4656", {"start": v(-18.45, -47.4) * mm, "end": v(-18.44, -47.48) * mm});
            skLineSegment(sketch, "E4657", {"start": v(-18.44, -47.48) * mm, "end": v(-18.44, -47.57) * mm});
            skLineSegment(sketch, "E4658", {"start": v(-18.44, -47.57) * mm, "end": v(-18.44, -47.66) * mm});
            skLineSegment(sketch, "E4659", {"start": v(-18.44, -47.66) * mm, "end": v(-18.44, -47.75) * mm});
            skLineSegment(sketch, "E4660", {"start": v(-18.44, -47.75) * mm, "end": v(-18.43, -47.82) * mm});
            skLineSegment(sketch, "E4661", {"start": v(-18.43, -47.82) * mm, "end": v(-17.52, -48.16) * mm});
            skLineSegment(sketch, "E4662", {"start": v(-17.52, -48.16) * mm, "end": v(-17.47, -48.1) * mm});
            skLineSegment(sketch, "E4663", {"start": v(-17.47, -48.1) * mm, "end": v(-17.4, -48.04) * mm});
            skLineSegment(sketch, "E4664", {"start": v(-17.4, -48.04) * mm, "end": v(-17.35, -47.98) * mm});
            skLineSegment(sketch, "E4665", {"start": v(-17.35, -47.98) * mm, "end": v(-17.29, -47.92) * mm});
            skLineSegment(sketch, "E4666", {"start": v(-17.29, -47.92) * mm, "end": v(-17.23, -47.85) * mm});
            skLineSegment(sketch, "E4667", {"start": v(-17.23, -47.85) * mm, "end": v(-17.17, -47.8) * mm});
            skLineSegment(sketch, "E4668", {"start": v(-17.17, -47.8) * mm, "end": v(-17.12, -47.73) * mm});
            skLineSegment(sketch, "E4669", {"start": v(-17.12, -47.73) * mm, "end": v(-17.06, -47.67) * mm});
            skLineSegment(sketch, "E4670", {"start": v(-17.06, -47.67) * mm, "end": v(-17, -47.6) * mm});
            skLineSegment(sketch, "E4671", {"start": v(-17, -47.6) * mm, "end": v(-16.95, -47.55) * mm});
            skLineSegment(sketch, "E4672", {"start": v(-16.95, -47.55) * mm, "end": v(-16.9, -47.48) * mm});
            skLineSegment(sketch, "E4673", {"start": v(-16.9, -47.48) * mm, "end": v(-16.85, -47.42) * mm});
            skLineSegment(sketch, "E4674", {"start": v(-16.85, -47.42) * mm, "end": v(-16.8, -47.36) * mm});
            skLineSegment(sketch, "E4675", {"start": v(-16.8, -47.36) * mm, "end": v(-16.75, -47.3) * mm});
            skLineSegment(sketch, "E4676", {"start": v(-16.75, -47.3) * mm, "end": v(-16.7, -47.25) * mm});
            skLineSegment(sketch, "E4677", {"start": v(-16.7, -47.25) * mm, "end": v(-16.65, -47.19) * mm});
            skLineSegment(sketch, "E4678", {"start": v(-16.65, -47.19) * mm, "end": v(-16.6, -47.13) * mm});
            skLineSegment(sketch, "E4679", {"start": v(-16.6, -47.13) * mm, "end": v(-16.56, -47.07) * mm});
            skLineSegment(sketch, "E4680", {"start": v(-16.56, -47.07) * mm, "end": v(-16.51, -47.02) * mm});
            skLineSegment(sketch, "E4681", {"start": v(-16.51, -47.02) * mm, "end": v(-16.47, -46.96) * mm});
            skLineSegment(sketch, "E4682", {"start": v(-16.47, -46.96) * mm, "end": v(-16.42, -46.9) * mm});
            skLineSegment(sketch, "E4683", {"start": v(-16.42, -46.9) * mm, "end": v(-16.38, -46.85) * mm});
            skLineSegment(sketch, "E4684", {"start": v(-16.38, -46.85) * mm, "end": v(-16.34, -46.8) * mm});
            skLineSegment(sketch, "E4685", {"start": v(-16.34, -46.8) * mm, "end": v(-16.3, -46.74) * mm});
            skLineSegment(sketch, "E4686", {"start": v(-16.3, -46.74) * mm, "end": v(-16.25, -46.69) * mm});
            skLineSegment(sketch, "E4687", {"start": v(-16.25, -46.69) * mm, "end": v(-16.21, -46.63) * mm});
            skLineSegment(sketch, "E4688", {"start": v(-16.21, -46.63) * mm, "end": v(-16.17, -46.58) * mm});
            skLineSegment(sketch, "E4689", {"start": v(-16.17, -46.58) * mm, "end": v(-16.14, -46.53) * mm});
            skLineSegment(sketch, "E4690", {"start": v(-16.14, -46.53) * mm, "end": v(-16.1, -46.48) * mm});
            skLineSegment(sketch, "E4691", {"start": v(-16.1, -46.48) * mm, "end": v(-16.06, -46.43) * mm});
            skLineSegment(sketch, "E4692", {"start": v(-16.06, -46.43) * mm, "end": v(-16.02, -46.38) * mm});
            skLineSegment(sketch, "E4693", {"start": v(-16.02, -46.38) * mm, "end": v(-15.99, -46.33) * mm});
            skLineSegment(sketch, "E4694", {"start": v(-15.99, -46.33) * mm, "end": v(-15.95, -46.28) * mm});
            skLineSegment(sketch, "E4695", {"start": v(-15.95, -46.28) * mm, "end": v(-15.92, -46.23) * mm});
            skLineSegment(sketch, "E4696", {"start": v(-15.92, -46.23) * mm, "end": v(-15.89, -46.18) * mm});
            skLineSegment(sketch, "E4697", {"start": v(-15.89, -46.18) * mm, "end": v(-15.85, -46.13) * mm});
            skLineSegment(sketch, "E4698", {"start": v(-15.85, -46.13) * mm, "end": v(-15.82, -46.09) * mm});
            skLineSegment(sketch, "E4699", {"start": v(-15.82, -46.09) * mm, "end": v(-15.79, -46.04) * mm});
            skLineSegment(sketch, "E4700", {"start": v(-15.79, -46.04) * mm, "end": v(-15.76, -46) * mm});
            skLineSegment(sketch, "E4701", {"start": v(-15.76, -46) * mm, "end": v(-15.73, -45.95) * mm});
            skLineSegment(sketch, "E4702", {"start": v(-15.73, -45.95) * mm, "end": v(-15.46, -46.04) * mm});
            skLineSegment(sketch, "E4703", {"start": v(-15.46, -46.04) * mm, "end": v(-15, -46.19) * mm});
            skLineSegment(sketch, "E4704", {"start": v(-15, -46.19) * mm, "end": v(-14.74, -46.28) * mm});
            skLineSegment(sketch, "E4705", {"start": v(-14.74, -46.28) * mm, "end": v(-14.75, -46.33) * mm});
            skLineSegment(sketch, "E4706", {"start": v(-14.75, -46.33) * mm, "end": v(-14.75, -46.39) * mm});
            skLineSegment(sketch, "E4707", {"start": v(-14.75, -46.39) * mm, "end": v(-14.75, -46.44) * mm});
            skLineSegment(sketch, "E4708", {"start": v(-14.75, -46.44) * mm, "end": v(-14.75, -46.5) * mm});
            skLineSegment(sketch, "E4709", {"start": v(-14.75, -46.5) * mm, "end": v(-14.75, -46.56) * mm});
            skLineSegment(sketch, "E4710", {"start": v(-14.75, -46.56) * mm, "end": v(-14.76, -46.61) * mm});
            skLineSegment(sketch, "E4711", {"start": v(-14.76, -46.61) * mm, "end": v(-14.76, -46.67) * mm});
            skLineSegment(sketch, "E4712", {"start": v(-14.76, -46.67) * mm, "end": v(-14.76, -46.73) * mm});
            skLineSegment(sketch, "E4713", {"start": v(-14.76, -46.73) * mm, "end": v(-14.76, -46.8) * mm});
            skLineSegment(sketch, "E4714", {"start": v(-14.76, -46.8) * mm, "end": v(-14.76, -46.86) * mm});
            skLineSegment(sketch, "E4715", {"start": v(-14.76, -46.86) * mm, "end": v(-14.76, -46.92) * mm});
            skLineSegment(sketch, "E4716", {"start": v(-14.76, -46.92) * mm, "end": v(-14.76, -46.98) * mm});
            skLineSegment(sketch, "E4717", {"start": v(-14.76, -46.98) * mm, "end": v(-14.76, -47.05) * mm});
            skLineSegment(sketch, "E4718", {"start": v(-14.76, -47.05) * mm, "end": v(-14.76, -47.12) * mm});
            skLineSegment(sketch, "E4719", {"start": v(-14.76, -47.12) * mm, "end": v(-14.76, -47.18) * mm});
            skLineSegment(sketch, "E4720", {"start": v(-14.76, -47.18) * mm, "end": v(-14.76, -47.25) * mm});
            skLineSegment(sketch, "E4721", {"start": v(-14.76, -47.25) * mm, "end": v(-14.76, -47.32) * mm});
            skLineSegment(sketch, "E4722", {"start": v(-14.76, -47.32) * mm, "end": v(-14.76, -47.39) * mm});
            skLineSegment(sketch, "E4723", {"start": v(-14.76, -47.39) * mm, "end": v(-14.75, -47.46) * mm});
            skLineSegment(sketch, "E4724", {"start": v(-14.75, -47.46) * mm, "end": v(-14.75, -47.53) * mm});
            skLineSegment(sketch, "E4725", {"start": v(-14.75, -47.53) * mm, "end": v(-14.75, -47.6) * mm});
            skLineSegment(sketch, "E4726", {"start": v(-14.75, -47.6) * mm, "end": v(-14.75, -47.67) * mm});
            skLineSegment(sketch, "E4727", {"start": v(-14.75, -47.67) * mm, "end": v(-14.74, -47.75) * mm});
            skLineSegment(sketch, "E4728", {"start": v(-14.74, -47.75) * mm, "end": v(-14.74, -47.82) * mm});
            skLineSegment(sketch, "E4729", {"start": v(-14.74, -47.82) * mm, "end": v(-14.73, -47.9) * mm});
            skLineSegment(sketch, "E4730", {"start": v(-14.73, -47.9) * mm, "end": v(-14.73, -47.97) * mm});
            skLineSegment(sketch, "E4731", {"start": v(-14.73, -47.97) * mm, "end": v(-14.72, -48.05) * mm});
            skLineSegment(sketch, "E4732", {"start": v(-14.72, -48.05) * mm, "end": v(-14.72, -48.13) * mm});
            skLineSegment(sketch, "E4733", {"start": v(-14.72, -48.13) * mm, "end": v(-14.71, -48.2) * mm});
            skLineSegment(sketch, "E4734", {"start": v(-14.71, -48.2) * mm, "end": v(-14.7, -48.29) * mm});
            skLineSegment(sketch, "E4735", {"start": v(-14.7, -48.29) * mm, "end": v(-14.7, -48.37) * mm});
            skLineSegment(sketch, "E4736", {"start": v(-14.7, -48.37) * mm, "end": v(-14.7, -48.45) * mm});
            skLineSegment(sketch, "E4737", {"start": v(-14.7, -48.45) * mm, "end": v(-14.69, -48.53) * mm});
            skLineSegment(sketch, "E4738", {"start": v(-14.69, -48.53) * mm, "end": v(-14.68, -48.62) * mm});
            skLineSegment(sketch, "E4739", {"start": v(-14.68, -48.62) * mm, "end": v(-14.67, -48.7) * mm});
            skLineSegment(sketch, "E4740", {"start": v(-14.67, -48.7) * mm, "end": v(-14.66, -48.78) * mm});
            skLineSegment(sketch, "E4741", {"start": v(-14.66, -48.78) * mm, "end": v(-14.65, -48.87) * mm});
            skLineSegment(sketch, "E4742", {"start": v(-14.65, -48.87) * mm, "end": v(-14.64, -48.96) * mm});
            skLineSegment(sketch, "E4743", {"start": v(-14.64, -48.96) * mm, "end": v(-14.63, -49.04) * mm});
            skLineSegment(sketch, "E4744", {"start": v(-14.63, -49.04) * mm, "end": v(-14.62, -49.12) * mm});
            skLineSegment(sketch, "E4745", {"start": v(-14.62, -49.12) * mm, "end": v(-13.7, -49.39) * mm});
            skLineSegment(sketch, "E4746", {"start": v(-13.7, -49.39) * mm, "end": v(-13.64, -49.33) * mm});
            skLineSegment(sketch, "E4747", {"start": v(-13.64, -49.33) * mm, "end": v(-13.58, -49.26) * mm});
            skLineSegment(sketch, "E4748", {"start": v(-13.58, -49.26) * mm, "end": v(-13.53, -49.2) * mm});
            skLineSegment(sketch, "E4749", {"start": v(-13.53, -49.2) * mm, "end": v(-13.47, -49.13) * mm});
            skLineSegment(sketch, "E4750", {"start": v(-13.47, -49.13) * mm, "end": v(-13.42, -49.06) * mm});
            skLineSegment(sketch, "E4751", {"start": v(-13.42, -49.06) * mm, "end": v(-13.37, -49) * mm});
            skLineSegment(sketch, "E4752", {"start": v(-13.37, -49) * mm, "end": v(-13.32, -48.92) * mm});
            skLineSegment(sketch, "E4753", {"start": v(-13.32, -48.92) * mm, "end": v(-13.27, -48.86) * mm});
            skLineSegment(sketch, "E4754", {"start": v(-13.27, -48.86) * mm, "end": v(-13.22, -48.8) * mm});
            skLineSegment(sketch, "E4755", {"start": v(-13.22, -48.8) * mm, "end": v(-13.17, -48.73) * mm});
            skLineSegment(sketch, "E4756", {"start": v(-13.17, -48.73) * mm, "end": v(-13.12, -48.66) * mm});
            skLineSegment(sketch, "E4757", {"start": v(-13.12, -48.66) * mm, "end": v(-13.08, -48.6) * mm});
            skLineSegment(sketch, "E4758", {"start": v(-13.08, -48.6) * mm, "end": v(-13.03, -48.54) * mm});
            skLineSegment(sketch, "E4759", {"start": v(-13.03, -48.54) * mm, "end": v(-12.99, -48.47) * mm});
            skLineSegment(sketch, "E4760", {"start": v(-12.99, -48.47) * mm, "end": v(-12.94, -48.41) * mm});
            skLineSegment(sketch, "E4761", {"start": v(-12.94, -48.41) * mm, "end": v(-12.9, -48.35) * mm});
            skLineSegment(sketch, "E4762", {"start": v(-12.9, -48.35) * mm, "end": v(-12.86, -48.29) * mm});
            skLineSegment(sketch, "E4763", {"start": v(-12.86, -48.29) * mm, "end": v(-12.81, -48.23) * mm});
            skLineSegment(sketch, "E4764", {"start": v(-12.81, -48.23) * mm, "end": v(-12.77, -48.17) * mm});
            skLineSegment(sketch, "E4765", {"start": v(-12.77, -48.17) * mm, "end": v(-12.73, -48.1) * mm});
            skLineSegment(sketch, "E4766", {"start": v(-12.73, -48.1) * mm, "end": v(-12.7, -48.05) * mm});
            skLineSegment(sketch, "E4767", {"start": v(-12.7, -48.05) * mm, "end": v(-12.65, -48) * mm});
            skLineSegment(sketch, "E4768", {"start": v(-12.65, -48) * mm, "end": v(-12.62, -47.93) * mm});
            skLineSegment(sketch, "E4769", {"start": v(-12.62, -47.93) * mm, "end": v(-12.58, -47.88) * mm});
            skLineSegment(sketch, "E4770", {"start": v(-12.58, -47.88) * mm, "end": v(-12.54, -47.82) * mm});
            skLineSegment(sketch, "E4771", {"start": v(-12.54, -47.82) * mm, "end": v(-12.5, -47.76) * mm});
            skLineSegment(sketch, "E4772", {"start": v(-12.5, -47.76) * mm, "end": v(-12.47, -47.7) * mm});
            skLineSegment(sketch, "E4773", {"start": v(-12.47, -47.7) * mm, "end": v(-12.44, -47.65) * mm});
            skLineSegment(sketch, "E4774", {"start": v(-12.44, -47.65) * mm, "end": v(-12.4, -47.6) * mm});
            skLineSegment(sketch, "E4775", {"start": v(-12.4, -47.6) * mm, "end": v(-12.37, -47.54) * mm});
            skLineSegment(sketch, "E4776", {"start": v(-12.37, -47.54) * mm, "end": v(-12.34, -47.5) * mm});
            skLineSegment(sketch, "E4777", {"start": v(-12.34, -47.5) * mm, "end": v(-12.3, -47.44) * mm});
            skLineSegment(sketch, "E4778", {"start": v(-12.3, -47.44) * mm, "end": v(-12.27, -47.39) * mm});
            skLineSegment(sketch, "E4779", {"start": v(-12.27, -47.39) * mm, "end": v(-12.24, -47.34) * mm});
            skLineSegment(sketch, "E4780", {"start": v(-12.24, -47.34) * mm, "end": v(-12.21, -47.29) * mm});
            skLineSegment(sketch, "E4781", {"start": v(-12.21, -47.29) * mm, "end": v(-12.18, -47.24) * mm});
            skLineSegment(sketch, "E4782", {"start": v(-12.18, -47.24) * mm, "end": v(-12.16, -47.19) * mm});
            skLineSegment(sketch, "E4783", {"start": v(-12.16, -47.19) * mm, "end": v(-12.13, -47.14) * mm});
            skLineSegment(sketch, "E4784", {"start": v(-12.13, -47.14) * mm, "end": v(-12.1, -47.1) * mm});
            skLineSegment(sketch, "E4785", {"start": v(-12.1, -47.1) * mm, "end": v(-12.07, -47.04) * mm});
            skLineSegment(sketch, "E4786", {"start": v(-12.07, -47.04) * mm, "end": v(-11.8, -47.1) * mm});
            skLineSegment(sketch, "E4787", {"start": v(-11.8, -47.1) * mm, "end": v(-11.34, -47.22) * mm});
            skLineSegment(sketch, "E4788", {"start": v(-11.34, -47.22) * mm, "end": v(-11.07, -47.3) * mm});
            skLineSegment(sketch, "E4789", {"start": v(-11.07, -47.3) * mm, "end": v(-11.06, -47.34) * mm});
            skLineSegment(sketch, "E4790", {"start": v(-11.06, -47.34) * mm, "end": v(-11.06, -47.4) * mm});
            skLineSegment(sketch, "E4791", {"start": v(-11.06, -47.4) * mm, "end": v(-11.06, -47.46) * mm});
            skLineSegment(sketch, "E4792", {"start": v(-11.06, -47.46) * mm, "end": v(-11.06, -47.51) * mm});
            skLineSegment(sketch, "E4793", {"start": v(-11.06, -47.51) * mm, "end": v(-11.06, -47.57) * mm});
            skLineSegment(sketch, "E4794", {"start": v(-11.06, -47.57) * mm, "end": v(-11.05, -47.63) * mm});
            skLineSegment(sketch, "E4795", {"start": v(-11.05, -47.63) * mm, "end": v(-11.05, -47.69) * mm});
            skLineSegment(sketch, "E4796", {"start": v(-11.05, -47.69) * mm, "end": v(-11.05, -47.75) * mm});
            skLineSegment(sketch, "E4797", {"start": v(-11.05, -47.75) * mm, "end": v(-11.04, -47.8) * mm});
            skLineSegment(sketch, "E4798", {"start": v(-11.04, -47.8) * mm, "end": v(-11.04, -47.87) * mm});
            skLineSegment(sketch, "E4799", {"start": v(-11.04, -47.87) * mm, "end": v(-11.03, -47.93) * mm});
            skLineSegment(sketch, "E4800", {"start": v(-11.03, -47.93) * mm, "end": v(-11.03, -48) * mm});
            skLineSegment(sketch, "E4801", {"start": v(-11.03, -48) * mm, "end": v(-11.02, -48.06) * mm});
            skLineSegment(sketch, "E4802", {"start": v(-11.02, -48.06) * mm, "end": v(-11.02, -48.13) * mm});
            skLineSegment(sketch, "E4803", {"start": v(-11.02, -48.13) * mm, "end": v(-11.01, -48.2) * mm});
            skLineSegment(sketch, "E4804", {"start": v(-11.01, -48.2) * mm, "end": v(-11, -48.26) * mm});
            skLineSegment(sketch, "E4805", {"start": v(-11, -48.26) * mm, "end": v(-11, -48.33) * mm});
            skLineSegment(sketch, "E4806", {"start": v(-11, -48.33) * mm, "end": v(-11, -48.4) * mm});
            skLineSegment(sketch, "E4807", {"start": v(-11, -48.4) * mm, "end": v(-10.98, -48.47) * mm});
            skLineSegment(sketch, "E4808", {"start": v(-10.98, -48.47) * mm, "end": v(-10.98, -48.54) * mm});
            skLineSegment(sketch, "E4809", {"start": v(-10.98, -48.54) * mm, "end": v(-10.97, -48.61) * mm});
            skLineSegment(sketch, "E4810", {"start": v(-10.97, -48.61) * mm, "end": v(-10.96, -48.68) * mm});
            skLineSegment(sketch, "E4811", {"start": v(-10.96, -48.68) * mm, "end": v(-10.95, -48.76) * mm});
            skLineSegment(sketch, "E4812", {"start": v(-10.95, -48.76) * mm, "end": v(-10.94, -48.83) * mm});
            skLineSegment(sketch, "E4813", {"start": v(-10.94, -48.83) * mm, "end": v(-10.93, -48.9) * mm});
            skLineSegment(sketch, "E4814", {"start": v(-10.93, -48.9) * mm, "end": v(-10.92, -48.98) * mm});
            skLineSegment(sketch, "E4815", {"start": v(-10.92, -48.98) * mm, "end": v(-10.9, -49.06) * mm});
            skLineSegment(sketch, "E4816", {"start": v(-10.9, -49.06) * mm, "end": v(-10.9, -49.14) * mm});
            skLineSegment(sketch, "E4817", {"start": v(-10.9, -49.14) * mm, "end": v(-10.89, -49.21) * mm});
            skLineSegment(sketch, "E4818", {"start": v(-10.89, -49.21) * mm, "end": v(-10.87, -49.3) * mm});
            skLineSegment(sketch, "E4819", {"start": v(-10.87, -49.3) * mm, "end": v(-10.86, -49.37) * mm});
            skLineSegment(sketch, "E4820", {"start": v(-10.86, -49.37) * mm, "end": v(-10.85, -49.45) * mm});
            skLineSegment(sketch, "E4821", {"start": v(-10.85, -49.45) * mm, "end": v(-10.83, -49.53) * mm});
            skLineSegment(sketch, "E4822", {"start": v(-10.83, -49.53) * mm, "end": v(-10.82, -49.62) * mm});
            skLineSegment(sketch, "E4823", {"start": v(-10.82, -49.62) * mm, "end": v(-10.8, -49.7) * mm});
            skLineSegment(sketch, "E4824", {"start": v(-10.8, -49.7) * mm, "end": v(-10.79, -49.78) * mm});
            skLineSegment(sketch, "E4825", {"start": v(-10.79, -49.78) * mm, "end": v(-10.77, -49.87) * mm});
            skLineSegment(sketch, "E4826", {"start": v(-10.77, -49.87) * mm, "end": v(-10.76, -49.95) * mm});
            skLineSegment(sketch, "E4827", {"start": v(-10.76, -49.95) * mm, "end": v(-10.74, -50.04) * mm});
            skLineSegment(sketch, "E4828", {"start": v(-10.74, -50.04) * mm, "end": v(-10.72, -50.12) * mm});
            skLineSegment(sketch, "E4829", {"start": v(-10.72, -50.12) * mm, "end": v(-9.77, -50.3) * mm});
            skLineSegment(sketch, "E4830", {"start": v(-9.77, -50.3) * mm, "end": v(-9.72, -50.25) * mm});
            skLineSegment(sketch, "E4831", {"start": v(-9.72, -50.25) * mm, "end": v(-9.68, -50.18) * mm});
            skLineSegment(sketch, "E4832", {"start": v(-9.68, -50.18) * mm, "end": v(-9.63, -50.1) * mm});
            skLineSegment(sketch, "E4833", {"start": v(-9.63, -50.1) * mm, "end": v(-9.58, -50.03) * mm});
            skLineSegment(sketch, "E4834", {"start": v(-9.58, -50.03) * mm, "end": v(-9.53, -49.96) * mm});
            skLineSegment(sketch, "E4835", {"start": v(-9.53, -49.96) * mm, "end": v(-9.49, -49.89) * mm});
            skLineSegment(sketch, "E4836", {"start": v(-9.49, -49.89) * mm, "end": v(-9.44, -49.82) * mm});
            skLineSegment(sketch, "E4837", {"start": v(-9.44, -49.82) * mm, "end": v(-9.4, -49.75) * mm});
            skLineSegment(sketch, "E4838", {"start": v(-9.4, -49.75) * mm, "end": v(-9.35, -49.68) * mm});
            skLineSegment(sketch, "E4839", {"start": v(-9.35, -49.68) * mm, "end": v(-9.3, -49.61) * mm});
            skLineSegment(sketch, "E4840", {"start": v(-9.3, -49.61) * mm, "end": v(-9.27, -49.54) * mm});
            skLineSegment(sketch, "E4841", {"start": v(-9.27, -49.54) * mm, "end": v(-9.22, -49.48) * mm});
            skLineSegment(sketch, "E4842", {"start": v(-9.22, -49.48) * mm, "end": v(-9.18, -49.4) * mm});
            skLineSegment(sketch, "E4843", {"start": v(-9.18, -49.4) * mm, "end": v(-9.14, -49.34) * mm});
            skLineSegment(sketch, "E4844", {"start": v(-9.14, -49.34) * mm, "end": v(-9.1, -49.28) * mm});
            skLineSegment(sketch, "E4845", {"start": v(-9.1, -49.28) * mm, "end": v(-9.07, -49.21) * mm});
            skLineSegment(sketch, "E4846", {"start": v(-9.07, -49.21) * mm, "end": v(-9.03, -49.15) * mm});
            skLineSegment(sketch, "E4847", {"start": v(-9.03, -49.15) * mm, "end": v(-9, -49.08) * mm});
            skLineSegment(sketch, "E4848", {"start": v(-9, -49.08) * mm, "end": v(-8.95, -49.02) * mm});
            skLineSegment(sketch, "E4849", {"start": v(-8.95, -49.02) * mm, "end": v(-8.92, -48.96) * mm});
            skLineSegment(sketch, "E4850", {"start": v(-8.92, -48.96) * mm, "end": v(-8.88, -48.9) * mm});
            skLineSegment(sketch, "E4851", {"start": v(-8.88, -48.9) * mm, "end": v(-8.85, -48.84) * mm});
            skLineSegment(sketch, "E4852", {"start": v(-8.85, -48.84) * mm, "end": v(-8.82, -48.78) * mm});
            skLineSegment(sketch, "E4853", {"start": v(-8.82, -48.78) * mm, "end": v(-8.78, -48.72) * mm});
            skLineSegment(sketch, "E4854", {"start": v(-8.78, -48.72) * mm, "end": v(-8.75, -48.66) * mm});
            skLineSegment(sketch, "E4855", {"start": v(-8.75, -48.66) * mm, "end": v(-8.72, -48.6) * mm});
            skLineSegment(sketch, "E4856", {"start": v(-8.72, -48.6) * mm, "end": v(-8.69, -48.54) * mm});
            skLineSegment(sketch, "E4857", {"start": v(-8.69, -48.54) * mm, "end": v(-8.66, -48.48) * mm});
            skLineSegment(sketch, "E4858", {"start": v(-8.66, -48.48) * mm, "end": v(-8.63, -48.42) * mm});
            skLineSegment(sketch, "E4859", {"start": v(-8.63, -48.42) * mm, "end": v(-8.6, -48.37) * mm});
            skLineSegment(sketch, "E4860", {"start": v(-8.6, -48.37) * mm, "end": v(-8.57, -48.31) * mm});
            skLineSegment(sketch, "E4861", {"start": v(-8.57, -48.31) * mm, "end": v(-8.54, -48.26) * mm});
            skLineSegment(sketch, "E4862", {"start": v(-8.54, -48.26) * mm, "end": v(-8.52, -48.2) * mm});
            skLineSegment(sketch, "E4863", {"start": v(-8.52, -48.2) * mm, "end": v(-8.5, -48.15) * mm});
            skLineSegment(sketch, "E4864", {"start": v(-8.5, -48.15) * mm, "end": v(-8.47, -48.1) * mm});
            skLineSegment(sketch, "E4865", {"start": v(-8.47, -48.1) * mm, "end": v(-8.44, -48.05) * mm});
            skLineSegment(sketch, "E4866", {"start": v(-8.44, -48.05) * mm, "end": v(-8.42, -48) * mm});
            skLineSegment(sketch, "E4867", {"start": v(-8.42, -48) * mm, "end": v(-8.4, -47.94) * mm});
            skLineSegment(sketch, "E4868", {"start": v(-8.4, -47.94) * mm, "end": v(-8.37, -47.9) * mm});
            skLineSegment(sketch, "E4869", {"start": v(-8.37, -47.9) * mm, "end": v(-8.35, -47.85) * mm});
            skLineSegment(sketch, "E4870", {"start": v(-8.35, -47.85) * mm, "end": v(-8.07, -47.89) * mm});
            skLineSegment(sketch, "E4871", {"start": v(-8.07, -47.89) * mm, "end": v(-7.6, -47.96) * mm});
            skLineSegment(sketch, "E4872", {"start": v(-7.6, -47.96) * mm, "end": v(-7.32, -48.01) * mm});
            skLineSegment(sketch, "E4873", {"start": v(-7.32, -48.01) * mm, "end": v(-7.32, -48.07) * mm});
            skLineSegment(sketch, "E4874", {"start": v(-7.32, -48.07) * mm, "end": v(-7.31, -48.12) * mm});
            skLineSegment(sketch, "E4875", {"start": v(-7.31, -48.12) * mm, "end": v(-7.3, -48.18) * mm});
            skLineSegment(sketch, "E4876", {"start": v(-7.3, -48.18) * mm, "end": v(-7.3, -48.23) * mm});
            skLineSegment(sketch, "E4877", {"start": v(-7.3, -48.23) * mm, "end": v(-7.29, -48.3) * mm});
            skLineSegment(sketch, "E4878", {"start": v(-7.29, -48.3) * mm, "end": v(-7.28, -48.35) * mm});
            skLineSegment(sketch, "E4879", {"start": v(-7.28, -48.35) * mm, "end": v(-7.27, -48.4) * mm});
            skLineSegment(sketch, "E4880", {"start": v(-7.27, -48.4) * mm, "end": v(-7.27, -48.47) * mm});
            skLineSegment(sketch, "E4881", {"start": v(-7.27, -48.47) * mm, "end": v(-7.26, -48.53) * mm});
            skLineSegment(sketch, "E4882", {"start": v(-7.26, -48.53) * mm, "end": v(-7.25, -48.59) * mm});
            skLineSegment(sketch, "E4883", {"start": v(-7.25, -48.59) * mm, "end": v(-7.24, -48.65) * mm});
            skLineSegment(sketch, "E4884", {"start": v(-7.24, -48.65) * mm, "end": v(-7.23, -48.72) * mm});
            skLineSegment(sketch, "E4885", {"start": v(-7.23, -48.72) * mm, "end": v(-7.22, -48.78) * mm});
            skLineSegment(sketch, "E4886", {"start": v(-7.22, -48.78) * mm, "end": v(-7.2, -48.84) * mm});
            skLineSegment(sketch, "E4887", {"start": v(-7.2, -48.84) * mm, "end": v(-7.2, -48.9) * mm});
            skLineSegment(sketch, "E4888", {"start": v(-7.2, -48.9) * mm, "end": v(-7.19, -48.98) * mm});
            skLineSegment(sketch, "E4889", {"start": v(-7.19, -48.98) * mm, "end": v(-7.17, -49.04) * mm});
            skLineSegment(sketch, "E4890", {"start": v(-7.17, -49.04) * mm, "end": v(-7.16, -49.11) * mm});
            skLineSegment(sketch, "E4891", {"start": v(-7.16, -49.11) * mm, "end": v(-7.15, -49.18) * mm});
            skLineSegment(sketch, "E4892", {"start": v(-7.15, -49.18) * mm, "end": v(-7.13, -49.25) * mm});
            skLineSegment(sketch, "E4893", {"start": v(-7.13, -49.25) * mm, "end": v(-7.12, -49.32) * mm});
            skLineSegment(sketch, "E4894", {"start": v(-7.12, -49.32) * mm, "end": v(-7.1, -49.4) * mm});
            skLineSegment(sketch, "E4895", {"start": v(-7.1, -49.4) * mm, "end": v(-7.1, -49.47) * mm});
            skLineSegment(sketch, "E4896", {"start": v(-7.1, -49.47) * mm, "end": v(-7.08, -49.54) * mm});
            skLineSegment(sketch, "E4897", {"start": v(-7.08, -49.54) * mm, "end": v(-7.06, -49.61) * mm});
            skLineSegment(sketch, "E4898", {"start": v(-7.06, -49.61) * mm, "end": v(-7.04, -49.69) * mm});
            skLineSegment(sketch, "E4899", {"start": v(-7.04, -49.69) * mm, "end": v(-7.03, -49.76) * mm});
            skLineSegment(sketch, "E4900", {"start": v(-7.03, -49.76) * mm, "end": v(-7, -49.84) * mm});
            skLineSegment(sketch, "E4901", {"start": v(-7, -49.84) * mm, "end": v(-7, -49.92) * mm});
            skLineSegment(sketch, "E4902", {"start": v(-7, -49.92) * mm, "end": v(-6.97, -50) * mm});
            skLineSegment(sketch, "E4903", {"start": v(-6.97, -50) * mm, "end": v(-6.95, -50.07) * mm});
            skLineSegment(sketch, "E4904", {"start": v(-6.95, -50.07) * mm, "end": v(-6.93, -50.15) * mm});
            skLineSegment(sketch, "E4905", {"start": v(-6.93, -50.15) * mm, "end": v(-6.91, -50.23) * mm});
            skLineSegment(sketch, "E4906", {"start": v(-6.91, -50.23) * mm, "end": v(-6.9, -50.31) * mm});
            skLineSegment(sketch, "E4907", {"start": v(-6.9, -50.31) * mm, "end": v(-6.87, -50.4) * mm});
            skLineSegment(sketch, "E4908", {"start": v(-6.87, -50.4) * mm, "end": v(-6.85, -50.48) * mm});
            skLineSegment(sketch, "E4909", {"start": v(-6.85, -50.48) * mm, "end": v(-6.83, -50.56) * mm});
            skLineSegment(sketch, "E4910", {"start": v(-6.83, -50.56) * mm, "end": v(-6.8, -50.64) * mm});
            skLineSegment(sketch, "E4911", {"start": v(-6.8, -50.64) * mm, "end": v(-6.78, -50.73) * mm});
            skLineSegment(sketch, "E4912", {"start": v(-6.78, -50.73) * mm, "end": v(-6.75, -50.8) * mm});
            skLineSegment(sketch, "E4913", {"start": v(-6.75, -50.8) * mm, "end": v(-5.8, -50.92) * mm});
            skLineSegment(sketch, "E4914", {"start": v(-5.8, -50.92) * mm, "end": v(-5.75, -50.86) * mm});
            skLineSegment(sketch, "E4915", {"start": v(-5.75, -50.86) * mm, "end": v(-5.7, -50.78) * mm});
            skLineSegment(sketch, "E4916", {"start": v(-5.7, -50.78) * mm, "end": v(-5.67, -50.7) * mm});
            skLineSegment(sketch, "E4917", {"start": v(-5.67, -50.7) * mm, "end": v(-5.62, -50.63) * mm});
            skLineSegment(sketch, "E4918", {"start": v(-5.62, -50.63) * mm, "end": v(-5.58, -50.55) * mm});
            skLineSegment(sketch, "E4919", {"start": v(-5.58, -50.55) * mm, "end": v(-5.54, -50.48) * mm});
            skLineSegment(sketch, "E4920", {"start": v(-5.54, -50.48) * mm, "end": v(-5.5, -50.4) * mm});
            skLineSegment(sketch, "E4921", {"start": v(-5.5, -50.4) * mm, "end": v(-5.46, -50.33) * mm});
            skLineSegment(sketch, "E4922", {"start": v(-5.46, -50.33) * mm, "end": v(-5.42, -50.26) * mm});
            skLineSegment(sketch, "E4923", {"start": v(-5.42, -50.26) * mm, "end": v(-5.39, -50.19) * mm});
            skLineSegment(sketch, "E4924", {"start": v(-5.39, -50.19) * mm, "end": v(-5.35, -50.12) * mm});
            skLineSegment(sketch, "E4925", {"start": v(-5.35, -50.12) * mm, "end": v(-5.31, -50.05) * mm});
            skLineSegment(sketch, "E4926", {"start": v(-5.31, -50.05) * mm, "end": v(-5.28, -49.98) * mm});
            skLineSegment(sketch, "E4927", {"start": v(-5.28, -49.98) * mm, "end": v(-5.24, -49.9) * mm});
            skLineSegment(sketch, "E4928", {"start": v(-5.24, -49.9) * mm, "end": v(-5.2, -49.84) * mm});
            skLineSegment(sketch, "E4929", {"start": v(-5.2, -49.84) * mm, "end": v(-5.18, -49.77) * mm});
            skLineSegment(sketch, "E4930", {"start": v(-5.18, -49.77) * mm, "end": v(-5.14, -49.7) * mm});
            skLineSegment(sketch, "E4931", {"start": v(-5.14, -49.7) * mm, "end": v(-5.11, -49.64) * mm});
            skLineSegment(sketch, "E4932", {"start": v(-5.11, -49.64) * mm, "end": v(-5.08, -49.57) * mm});
            skLineSegment(sketch, "E4933", {"start": v(-5.08, -49.57) * mm, "end": v(-5.05, -49.5) * mm});
            skLineSegment(sketch, "E4934", {"start": v(-5.05, -49.5) * mm, "end": v(-5.02, -49.44) * mm});
            skLineSegment(sketch, "E4935", {"start": v(-5.02, -49.44) * mm, "end": v(-5, -49.38) * mm});
            skLineSegment(sketch, "E4936", {"start": v(-5, -49.38) * mm, "end": v(-4.96, -49.32) * mm});
            skLineSegment(sketch, "E4937", {"start": v(-4.96, -49.32) * mm, "end": v(-4.93, -49.25) * mm});
            skLineSegment(sketch, "E4938", {"start": v(-4.93, -49.25) * mm, "end": v(-4.9, -49.2) * mm});
            skLineSegment(sketch, "E4939", {"start": v(-4.9, -49.2) * mm, "end": v(-4.88, -49.13) * mm});
            skLineSegment(sketch, "E4940", {"start": v(-4.88, -49.13) * mm, "end": v(-4.85, -49.07) * mm});
            skLineSegment(sketch, "E4941", {"start": v(-4.85, -49.07) * mm, "end": v(-4.83, -49.01) * mm});
            skLineSegment(sketch, "E4942", {"start": v(-4.83, -49.01) * mm, "end": v(-4.8, -48.95) * mm});
            skLineSegment(sketch, "E4943", {"start": v(-4.8, -48.95) * mm, "end": v(-4.78, -48.9) * mm});
            skLineSegment(sketch, "E4944", {"start": v(-4.78, -48.9) * mm, "end": v(-4.75, -48.84) * mm});
            skLineSegment(sketch, "E4945", {"start": v(-4.75, -48.84) * mm, "end": v(-4.73, -48.78) * mm});
            skLineSegment(sketch, "E4946", {"start": v(-4.73, -48.78) * mm, "end": v(-4.7, -48.72) * mm});
            skLineSegment(sketch, "E4947", {"start": v(-4.7, -48.72) * mm, "end": v(-4.69, -48.67) * mm});
            skLineSegment(sketch, "E4948", {"start": v(-4.69, -48.67) * mm, "end": v(-4.67, -48.61) * mm});
            skLineSegment(sketch, "E4949", {"start": v(-4.67, -48.61) * mm, "end": v(-4.64, -48.56) * mm});
            skLineSegment(sketch, "E4950", {"start": v(-4.64, -48.56) * mm, "end": v(-4.62, -48.5) * mm});
            skLineSegment(sketch, "E4951", {"start": v(-4.62, -48.5) * mm, "end": v(-4.6, -48.46) * mm});
            skLineSegment(sketch, "E4952", {"start": v(-4.6, -48.46) * mm, "end": v(-4.59, -48.4) * mm});
            skLineSegment(sketch, "E4953", {"start": v(-4.59, -48.4) * mm, "end": v(-4.57, -48.35) * mm});
            skLineSegment(sketch, "E4954", {"start": v(-4.57, -48.35) * mm, "end": v(-4.29, -48.37) * mm});
            skLineSegment(sketch, "E4955", {"start": v(-4.29, -48.37) * mm, "end": v(-3.81, -48.41) * mm});
            skLineSegment(sketch, "E4956", {"start": v(-3.81, -48.41) * mm, "end": v(-3.53, -48.44) * mm});
            skLineSegment(sketch, "E4957", {"start": v(-3.53, -48.44) * mm, "end": v(-3.52, -48.5) * mm});
            skLineSegment(sketch, "E4958", {"start": v(-3.52, -48.5) * mm, "end": v(-3.51, -48.55) * mm});
            skLineSegment(sketch, "E4959", {"start": v(-3.51, -48.55) * mm, "end": v(-3.5, -48.6) * mm});
            skLineSegment(sketch, "E4960", {"start": v(-3.5, -48.6) * mm, "end": v(-3.49, -48.66) * mm});
            skLineSegment(sketch, "E4961", {"start": v(-3.49, -48.66) * mm, "end": v(-3.48, -48.71) * mm});
            skLineSegment(sketch, "E4962", {"start": v(-3.48, -48.71) * mm, "end": v(-3.47, -48.77) * mm});
            skLineSegment(sketch, "E4963", {"start": v(-3.47, -48.77) * mm, "end": v(-3.45, -48.83) * mm});
            skLineSegment(sketch, "E4964", {"start": v(-3.45, -48.83) * mm, "end": v(-3.44, -48.89) * mm});
            skLineSegment(sketch, "E4965", {"start": v(-3.44, -48.89) * mm, "end": v(-3.43, -48.95) * mm});
            skLineSegment(sketch, "E4966", {"start": v(-3.43, -48.95) * mm, "end": v(-3.41, -49) * mm});
            skLineSegment(sketch, "E4967", {"start": v(-3.41, -49) * mm, "end": v(-3.4, -49.07) * mm});
            skLineSegment(sketch, "E4968", {"start": v(-3.4, -49.07) * mm, "end": v(-3.38, -49.13) * mm});
            skLineSegment(sketch, "E4969", {"start": v(-3.38, -49.13) * mm, "end": v(-3.37, -49.2) * mm});
            skLineSegment(sketch, "E4970", {"start": v(-3.37, -49.2) * mm, "end": v(-3.35, -49.26) * mm});
            skLineSegment(sketch, "E4971", {"start": v(-3.35, -49.26) * mm, "end": v(-3.34, -49.32) * mm});
            skLineSegment(sketch, "E4972", {"start": v(-3.34, -49.32) * mm, "end": v(-3.32, -49.39) * mm});
            skLineSegment(sketch, "E4973", {"start": v(-3.32, -49.39) * mm, "end": v(-3.3, -49.46) * mm});
            skLineSegment(sketch, "E4974", {"start": v(-3.3, -49.46) * mm, "end": v(-3.29, -49.52) * mm});
            skLineSegment(sketch, "E4975", {"start": v(-3.29, -49.52) * mm, "end": v(-3.27, -49.6) * mm});
            skLineSegment(sketch, "E4976", {"start": v(-3.27, -49.6) * mm, "end": v(-3.25, -49.66) * mm});
            skLineSegment(sketch, "E4977", {"start": v(-3.25, -49.66) * mm, "end": v(-3.23, -49.73) * mm});
            skLineSegment(sketch, "E4978", {"start": v(-3.23, -49.73) * mm, "end": v(-3.2, -49.8) * mm});
            skLineSegment(sketch, "E4979", {"start": v(-3.2, -49.8) * mm, "end": v(-3.19, -49.87) * mm});
            skLineSegment(sketch, "E4980", {"start": v(-3.19, -49.87) * mm, "end": v(-3.17, -49.94) * mm});
            skLineSegment(sketch, "E4981", {"start": v(-3.17, -49.94) * mm, "end": v(-3.15, -50.01) * mm});
            skLineSegment(sketch, "E4982", {"start": v(-3.15, -50.01) * mm, "end": v(-3.12, -50.09) * mm});
            skLineSegment(sketch, "E4983", {"start": v(-3.12, -50.09) * mm, "end": v(-3.1, -50.16) * mm});
            skLineSegment(sketch, "E4984", {"start": v(-3.1, -50.16) * mm, "end": v(-3.08, -50.24) * mm});
            skLineSegment(sketch, "E4985", {"start": v(-3.08, -50.24) * mm, "end": v(-3.05, -50.31) * mm});
            skLineSegment(sketch, "E4986", {"start": v(-3.05, -50.31) * mm, "end": v(-3.03, -50.39) * mm});
            skLineSegment(sketch, "E4987", {"start": v(-3.03, -50.39) * mm, "end": v(-3, -50.46) * mm});
            skLineSegment(sketch, "E4988", {"start": v(-3, -50.46) * mm, "end": v(-2.98, -50.54) * mm});
            skLineSegment(sketch, "E4989", {"start": v(-2.98, -50.54) * mm, "end": v(-2.95, -50.62) * mm});
            skLineSegment(sketch, "E4990", {"start": v(-2.95, -50.62) * mm, "end": v(-2.92, -50.7) * mm});
            skLineSegment(sketch, "E4991", {"start": v(-2.92, -50.7) * mm, "end": v(-2.9, -50.78) * mm});
            skLineSegment(sketch, "E4992", {"start": v(-2.9, -50.78) * mm, "end": v(-2.87, -50.86) * mm});
            skLineSegment(sketch, "E4993", {"start": v(-2.87, -50.86) * mm, "end": v(-2.84, -50.94) * mm});
            skLineSegment(sketch, "E4994", {"start": v(-2.84, -50.94) * mm, "end": v(-2.8, -51.02) * mm});
            skLineSegment(sketch, "E4995", {"start": v(-2.8, -51.02) * mm, "end": v(-2.78, -51.1) * mm});
            skLineSegment(sketch, "E4996", {"start": v(-2.78, -51.1) * mm, "end": v(-2.75, -51.18) * mm});
            skLineSegment(sketch, "E4997", {"start": v(-2.75, -51.18) * mm, "end": v(-1.78, -51.22) * mm});
            skLineSegment(sketch, "E4998", {"start": v(-1.78, -51.22) * mm, "end": v(-1.74, -51.15) * mm});
            skLineSegment(sketch, "E4999", {"start": v(-1.74, -51.15) * mm, "end": v(-1.7, -51.07) * mm});
            skLineSegment(sketch, "E5000", {"start": v(-1.7, -51.07) * mm, "end": v(-1.67, -51) * mm});
            skLineSegment(sketch, "E5001", {"start": v(-1.67, -51) * mm, "end": v(-1.63, -50.91) * mm});
            skLineSegment(sketch, "E5002", {"start": v(-1.63, -50.91) * mm, "end": v(-1.6, -50.84) * mm});
            skLineSegment(sketch, "E5003", {"start": v(-1.6, -50.84) * mm, "end": v(-1.56, -50.76) * mm});
            skLineSegment(sketch, "E5004", {"start": v(-1.56, -50.76) * mm, "end": v(-1.53, -50.68) * mm});
            skLineSegment(sketch, "E5005", {"start": v(-1.53, -50.68) * mm, "end": v(-1.5, -50.6) * mm});
            skLineSegment(sketch, "E5006", {"start": v(-1.5, -50.6) * mm, "end": v(-1.46, -50.53) * mm});
            skLineSegment(sketch, "E5007", {"start": v(-1.46, -50.53) * mm, "end": v(-1.43, -50.46) * mm});
            skLineSegment(sketch, "E5008", {"start": v(-1.43, -50.46) * mm, "end": v(-1.4, -50.38) * mm});
            skLineSegment(sketch, "E5009", {"start": v(-1.4, -50.38) * mm, "end": v(-1.37, -50.31) * mm});
            skLineSegment(sketch, "E5010", {"start": v(-1.37, -50.31) * mm, "end": v(-1.34, -50.24) * mm});
            skLineSegment(sketch, "E5011", {"start": v(-1.34, -50.24) * mm, "end": v(-1.31, -50.17) * mm});
            skLineSegment(sketch, "E5012", {"start": v(-1.31, -50.17) * mm, "end": v(-1.28, -50.1) * mm});
            skLineSegment(sketch, "E5013", {"start": v(-1.28, -50.1) * mm, "end": v(-1.26, -50.03) * mm});
            skLineSegment(sketch, "E5014", {"start": v(-1.26, -50.03) * mm, "end": v(-1.23, -49.96) * mm});
            skLineSegment(sketch, "E5015", {"start": v(-1.23, -49.96) * mm, "end": v(-1.2, -49.89) * mm});
            skLineSegment(sketch, "E5016", {"start": v(-1.2, -49.89) * mm, "end": v(-1.18, -49.82) * mm});
            skLineSegment(sketch, "E5017", {"start": v(-1.18, -49.82) * mm, "end": v(-1.15, -49.75) * mm});
            skLineSegment(sketch, "E5018", {"start": v(-1.15, -49.75) * mm, "end": v(-1.12, -49.68) * mm});
            skLineSegment(sketch, "E5019", {"start": v(-1.12, -49.68) * mm, "end": v(-1.1, -49.62) * mm});
            skLineSegment(sketch, "E5020", {"start": v(-1.1, -49.62) * mm, "end": v(-1.08, -49.55) * mm});
            skLineSegment(sketch, "E5021", {"start": v(-1.08, -49.55) * mm, "end": v(-1.05, -49.49) * mm});
            skLineSegment(sketch, "E5022", {"start": v(-1.05, -49.49) * mm, "end": v(-1.03, -49.43) * mm});
            skLineSegment(sketch, "E5023", {"start": v(-1.03, -49.43) * mm, "end": v(-1, -49.36) * mm});
            skLineSegment(sketch, "E5024", {"start": v(-1, -49.36) * mm, "end": v(-0.99, -49.3) * mm});
            skLineSegment(sketch, "E5025", {"start": v(-0.99, -49.3) * mm, "end": v(-0.97, -49.24) * mm});
            skLineSegment(sketch, "E5026", {"start": v(-0.97, -49.24) * mm, "end": v(-0.95, -49.18) * mm});
            skLineSegment(sketch, "E5027", {"start": v(-0.95, -49.18) * mm, "end": v(-0.93, -49.12) * mm});
            skLineSegment(sketch, "E5028", {"start": v(-0.93, -49.12) * mm, "end": v(-0.9, -49.06) * mm});
            skLineSegment(sketch, "E5029", {"start": v(-0.9, -49.06) * mm, "end": v(-0.89, -49) * mm});
            skLineSegment(sketch, "E5030", {"start": v(-0.89, -49) * mm, "end": v(-0.87, -48.94) * mm});
            skLineSegment(sketch, "E5031", {"start": v(-0.87, -48.94) * mm, "end": v(-0.85, -48.89) * mm});
            skLineSegment(sketch, "E5032", {"start": v(-0.85, -48.89) * mm, "end": v(-0.84, -48.83) * mm});
            skLineSegment(sketch, "E5033", {"start": v(-0.84, -48.83) * mm, "end": v(-0.82, -48.78) * mm});
            skLineSegment(sketch, "E5034", {"start": v(-0.82, -48.78) * mm, "end": v(-0.8, -48.72) * mm});
            skLineSegment(sketch, "E5035", {"start": v(-0.8, -48.72) * mm, "end": v(-0.79, -48.67) * mm});
            skLineSegment(sketch, "E5036", {"start": v(-0.79, -48.67) * mm, "end": v(-0.77, -48.61) * mm});
            skLineSegment(sketch, "E5037", {"start": v(-0.77, -48.61) * mm, "end": v(-0.76, -48.56) * mm});
            skLineSegment(sketch, "E5038", {"start": v(-0.76, -48.56) * mm, "end": v(-0.48, -48.56) * mm});
            skLineSegment(sketch, "E5039", {"start": v(-0.48, -48.56) * mm, "end": v(0, -48.56) * mm});
            skLineSegment(sketch, "E5040", {"start": v(0, -48.56) * mm, "end": v(0.28, -48.57) * mm});
            skLineSegment(sketch, "E5041", {"start": v(0.28, -48.57) * mm, "end": v(0.3, -48.62) * mm});
            skLineSegment(sketch, "E5042", {"start": v(0.3, -48.62) * mm, "end": v(0.3, -48.67) * mm});
            skLineSegment(sketch, "E5043", {"start": v(0.3, -48.67) * mm, "end": v(0.32, -48.73) * mm});
            skLineSegment(sketch, "E5044", {"start": v(0.32, -48.73) * mm, "end": v(0.34, -48.78) * mm});
            skLineSegment(sketch, "E5045", {"start": v(0.34, -48.78) * mm, "end": v(0.35, -48.84) * mm});
            skLineSegment(sketch, "E5046", {"start": v(0.35, -48.84) * mm, "end": v(0.37, -48.9) * mm});
            skLineSegment(sketch, "E5047", {"start": v(0.37, -48.9) * mm, "end": v(0.39, -48.95) * mm});
            skLineSegment(sketch, "E5048", {"start": v(0.39, -48.95) * mm, "end": v(0.4, -49) * mm});
            skLineSegment(sketch, "E5049", {"start": v(0.4, -49) * mm, "end": v(0.42, -49.07) * mm});
            skLineSegment(sketch, "E5050", {"start": v(0.42, -49.07) * mm, "end": v(0.44, -49.13) * mm});
            skLineSegment(sketch, "E5051", {"start": v(0.44, -49.13) * mm, "end": v(0.46, -49.19) * mm});
            skLineSegment(sketch, "E5052", {"start": v(0.46, -49.19) * mm, "end": v(0.48, -49.25) * mm});
            skLineSegment(sketch, "E5053", {"start": v(0.48, -49.25) * mm, "end": v(0.5, -49.3) * mm});
            skLineSegment(sketch, "E5054", {"start": v(0.5, -49.3) * mm, "end": v(0.52, -49.37) * mm});
            skLineSegment(sketch, "E5055", {"start": v(0.52, -49.37) * mm, "end": v(0.54, -49.43) * mm});
            skLineSegment(sketch, "E5056", {"start": v(0.54, -49.43) * mm, "end": v(0.56, -49.5) * mm});
            skLineSegment(sketch, "E5057", {"start": v(0.56, -49.5) * mm, "end": v(0.59, -49.56) * mm});
            skLineSegment(sketch, "E5058", {"start": v(0.59, -49.56) * mm, "end": v(0.61, -49.63) * mm});
            skLineSegment(sketch, "E5059", {"start": v(0.61, -49.63) * mm, "end": v(0.63, -49.7) * mm});
            skLineSegment(sketch, "E5060", {"start": v(0.63, -49.7) * mm, "end": v(0.66, -49.76) * mm});
            skLineSegment(sketch, "E5061", {"start": v(0.66, -49.76) * mm, "end": v(0.68, -49.83) * mm});
            skLineSegment(sketch, "E5062", {"start": v(0.68, -49.83) * mm, "end": v(0.7, -49.9) * mm});
            skLineSegment(sketch, "E5063", {"start": v(0.7, -49.9) * mm, "end": v(0.73, -49.97) * mm});
            skLineSegment(sketch, "E5064", {"start": v(0.73, -49.97) * mm, "end": v(0.76, -50.04) * mm});
            skLineSegment(sketch, "E5065", {"start": v(0.76, -50.04) * mm, "end": v(0.79, -50.1) * mm});
            skLineSegment(sketch, "E5066", {"start": v(0.79, -50.1) * mm, "end": v(0.82, -50.18) * mm});
            skLineSegment(sketch, "E5067", {"start": v(0.82, -50.18) * mm, "end": v(0.84, -50.25) * mm});
            skLineSegment(sketch, "E5068", {"start": v(0.84, -50.25) * mm, "end": v(0.87, -50.32) * mm});
            skLineSegment(sketch, "E5069", {"start": v(0.87, -50.32) * mm, "end": v(0.9, -50.4) * mm});
            skLineSegment(sketch, "E5070", {"start": v(0.9, -50.4) * mm, "end": v(0.93, -50.47) * mm});
            skLineSegment(sketch, "E5071", {"start": v(0.93, -50.47) * mm, "end": v(0.97, -50.54) * mm});
            skLineSegment(sketch, "E5072", {"start": v(0.97, -50.54) * mm, "end": v(1, -50.62) * mm});
            skLineSegment(sketch, "E5073", {"start": v(1, -50.62) * mm, "end": v(1.03, -50.7) * mm});
            skLineSegment(sketch, "E5074", {"start": v(1.03, -50.7) * mm, "end": v(1.06, -50.77) * mm});
            skLineSegment(sketch, "E5075", {"start": v(1.06, -50.77) * mm, "end": v(1.1, -50.85) * mm});
            skLineSegment(sketch, "E5076", {"start": v(1.1, -50.85) * mm, "end": v(1.13, -50.93) * mm});
            skLineSegment(sketch, "E5077", {"start": v(1.13, -50.93) * mm, "end": v(1.17, -51) * mm});
            skLineSegment(sketch, "E5078", {"start": v(1.17, -51) * mm, "end": v(1.2, -51.09) * mm});
            skLineSegment(sketch, "E5079", {"start": v(1.2, -51.09) * mm, "end": v(1.24, -51.17) * mm});
            skLineSegment(sketch, "E5080", {"start": v(1.24, -51.17) * mm, "end": v(1.28, -51.23) * mm});
            skLineSegment(sketch, "E5081", {"start": v(1.28, -51.23) * mm, "end": v(2.24, -51.2) * mm});
            skLineSegment(sketch, "E5082", {"start": v(2.24, -51.2) * mm, "end": v(2.27, -51.13) * mm});
            skLineSegment(sketch, "E5083", {"start": v(2.27, -51.13) * mm, "end": v(2.3, -51.05) * mm});
            skLineSegment(sketch, "E5084", {"start": v(2.3, -51.05) * mm, "end": v(2.34, -50.97) * mm});
            skLineSegment(sketch, "E5085", {"start": v(2.34, -50.97) * mm, "end": v(2.37, -50.89) * mm});
            skLineSegment(sketch, "E5086", {"start": v(2.37, -50.89) * mm, "end": v(2.4, -50.8) * mm});
            skLineSegment(sketch, "E5087", {"start": v(2.4, -50.8) * mm, "end": v(2.42, -50.73) * mm});
            skLineSegment(sketch, "E5088", {"start": v(2.42, -50.73) * mm, "end": v(2.45, -50.65) * mm});
            skLineSegment(sketch, "E5089", {"start": v(2.45, -50.65) * mm, "end": v(2.48, -50.57) * mm});
            skLineSegment(sketch, "E5090", {"start": v(2.48, -50.57) * mm, "end": v(2.5, -50.5) * mm});
            skLineSegment(sketch, "E5091", {"start": v(2.5, -50.5) * mm, "end": v(2.53, -50.41) * mm});
            skLineSegment(sketch, "E5092", {"start": v(2.53, -50.41) * mm, "end": v(2.56, -50.34) * mm});
            skLineSegment(sketch, "E5093", {"start": v(2.56, -50.34) * mm, "end": v(2.58, -50.26) * mm});
            skLineSegment(sketch, "E5094", {"start": v(2.58, -50.26) * mm, "end": v(2.6, -50.19) * mm});
            skLineSegment(sketch, "E5095", {"start": v(2.6, -50.19) * mm, "end": v(2.63, -50.11) * mm});
            skLineSegment(sketch, "E5096", {"start": v(2.63, -50.11) * mm, "end": v(2.65, -50.04) * mm});
            skLineSegment(sketch, "E5097", {"start": v(2.65, -50.04) * mm, "end": v(2.67, -49.97) * mm});
            skLineSegment(sketch, "E5098", {"start": v(2.67, -49.97) * mm, "end": v(2.7, -49.9) * mm});
            skLineSegment(sketch, "E5099", {"start": v(2.7, -49.9) * mm, "end": v(2.72, -49.83) * mm});
            skLineSegment(sketch, "E5100", {"start": v(2.72, -49.83) * mm, "end": v(2.74, -49.76) * mm});
            skLineSegment(sketch, "E5101", {"start": v(2.74, -49.76) * mm, "end": v(2.76, -49.69) * mm});
            skLineSegment(sketch, "E5102", {"start": v(2.76, -49.69) * mm, "end": v(2.78, -49.62) * mm});
            skLineSegment(sketch, "E5103", {"start": v(2.78, -49.62) * mm, "end": v(2.8, -49.55) * mm});
            skLineSegment(sketch, "E5104", {"start": v(2.8, -49.55) * mm, "end": v(2.81, -49.49) * mm});
            skLineSegment(sketch, "E5105", {"start": v(2.81, -49.49) * mm, "end": v(2.83, -49.42) * mm});
            skLineSegment(sketch, "E5106", {"start": v(2.83, -49.42) * mm, "end": v(2.85, -49.35) * mm});
            skLineSegment(sketch, "E5107", {"start": v(2.85, -49.35) * mm, "end": v(2.87, -49.29) * mm});
            skLineSegment(sketch, "E5108", {"start": v(2.87, -49.29) * mm, "end": v(2.88, -49.23) * mm});
            skLineSegment(sketch, "E5109", {"start": v(2.88, -49.23) * mm, "end": v(2.9, -49.16) * mm});
            skLineSegment(sketch, "E5110", {"start": v(2.9, -49.16) * mm, "end": v(2.91, -49.1) * mm});
            skLineSegment(sketch, "E5111", {"start": v(2.91, -49.1) * mm, "end": v(2.93, -49.04) * mm});
            skLineSegment(sketch, "E5112", {"start": v(2.93, -49.04) * mm, "end": v(2.94, -48.98) * mm});
            skLineSegment(sketch, "E5113", {"start": v(2.94, -48.98) * mm, "end": v(2.96, -48.92) * mm});
            skLineSegment(sketch, "E5114", {"start": v(2.96, -48.92) * mm, "end": v(2.97, -48.86) * mm});
            skLineSegment(sketch, "E5115", {"start": v(2.97, -48.86) * mm, "end": v(2.98, -48.8) * mm});
            skLineSegment(sketch, "E5116", {"start": v(2.98, -48.8) * mm, "end": v(3, -48.75) * mm});
            skLineSegment(sketch, "E5117", {"start": v(3, -48.75) * mm, "end": v(3, -48.69) * mm});
            skLineSegment(sketch, "E5118", {"start": v(3, -48.69) * mm, "end": v(3.02, -48.63) * mm});
            skLineSegment(sketch, "E5119", {"start": v(3.02, -48.63) * mm, "end": v(3.03, -48.58) * mm});
            skLineSegment(sketch, "E5120", {"start": v(3.03, -48.58) * mm, "end": v(3.04, -48.53) * mm});
            skLineSegment(sketch, "E5121", {"start": v(3.04, -48.53) * mm, "end": v(3.05, -48.47) * mm});
            skLineSegment(sketch, "E5122", {"start": v(3.05, -48.47) * mm, "end": v(3.33, -48.45) * mm});
            skLineSegment(sketch, "E5123", {"start": v(3.33, -48.45) * mm, "end": v(3.81, -48.41) * mm});
            skLineSegment(sketch, "E5124", {"start": v(3.81, -48.41) * mm, "end": v(4.09, -48.4) * mm});
            skLineSegment(sketch, "E5125", {"start": v(4.09, -48.4) * mm, "end": v(4.1, -48.45) * mm});
            skLineSegment(sketch, "E5126", {"start": v(4.1, -48.45) * mm, "end": v(4.13, -48.5) * mm});
            skLineSegment(sketch, "E5127", {"start": v(4.13, -48.5) * mm, "end": v(4.14, -48.55) * mm});
            skLineSegment(sketch, "E5128", {"start": v(4.14, -48.55) * mm, "end": v(4.16, -48.6) * mm});
            skLineSegment(sketch, "E5129", {"start": v(4.16, -48.6) * mm, "end": v(4.19, -48.66) * mm});
            skLineSegment(sketch, "E5130", {"start": v(4.19, -48.66) * mm, "end": v(4.2, -48.71) * mm});
            skLineSegment(sketch, "E5131", {"start": v(4.2, -48.71) * mm, "end": v(4.23, -48.77) * mm});
            skLineSegment(sketch, "E5132", {"start": v(4.23, -48.77) * mm, "end": v(4.25, -48.82) * mm});
            skLineSegment(sketch, "E5133", {"start": v(4.25, -48.82) * mm, "end": v(4.27, -48.88) * mm});
            skLineSegment(sketch, "E5134", {"start": v(4.27, -48.88) * mm, "end": v(4.3, -48.94) * mm});
            skLineSegment(sketch, "E5135", {"start": v(4.3, -48.94) * mm, "end": v(4.32, -49) * mm});
            skLineSegment(sketch, "E5136", {"start": v(4.32, -49) * mm, "end": v(4.34, -49.06) * mm});
            skLineSegment(sketch, "E5137", {"start": v(4.34, -49.06) * mm, "end": v(4.37, -49.12) * mm});
            skLineSegment(sketch, "E5138", {"start": v(4.37, -49.12) * mm, "end": v(4.4, -49.18) * mm});
            skLineSegment(sketch, "E5139", {"start": v(4.4, -49.18) * mm, "end": v(4.42, -49.24) * mm});
            skLineSegment(sketch, "E5140", {"start": v(4.42, -49.24) * mm, "end": v(4.45, -49.3) * mm});
            skLineSegment(sketch, "E5141", {"start": v(4.45, -49.3) * mm, "end": v(4.47, -49.36) * mm});
            skLineSegment(sketch, "E5142", {"start": v(4.47, -49.36) * mm, "end": v(4.5, -49.43) * mm});
            skLineSegment(sketch, "E5143", {"start": v(4.5, -49.43) * mm, "end": v(4.53, -49.5) * mm});
            skLineSegment(sketch, "E5144", {"start": v(4.53, -49.5) * mm, "end": v(4.56, -49.56) * mm});
            skLineSegment(sketch, "E5145", {"start": v(4.56, -49.56) * mm, "end": v(4.6, -49.62) * mm});
            skLineSegment(sketch, "E5146", {"start": v(4.6, -49.62) * mm, "end": v(4.62, -49.69) * mm});
            skLineSegment(sketch, "E5147", {"start": v(4.62, -49.69) * mm, "end": v(4.65, -49.75) * mm});
            skLineSegment(sketch, "E5148", {"start": v(4.65, -49.75) * mm, "end": v(4.68, -49.82) * mm});
            skLineSegment(sketch, "E5149", {"start": v(4.68, -49.82) * mm, "end": v(4.72, -49.89) * mm});
            skLineSegment(sketch, "E5150", {"start": v(4.72, -49.89) * mm, "end": v(4.75, -49.96) * mm});
            skLineSegment(sketch, "E5151", {"start": v(4.75, -49.96) * mm, "end": v(4.78, -50.03) * mm});
            skLineSegment(sketch, "E5152", {"start": v(4.78, -50.03) * mm, "end": v(4.82, -50.1) * mm});
            skLineSegment(sketch, "E5153", {"start": v(4.82, -50.1) * mm, "end": v(4.85, -50.17) * mm});
            skLineSegment(sketch, "E5154", {"start": v(4.85, -50.17) * mm, "end": v(4.9, -50.24) * mm});
            skLineSegment(sketch, "E5155", {"start": v(4.9, -50.24) * mm, "end": v(4.93, -50.31) * mm});
            skLineSegment(sketch, "E5156", {"start": v(4.93, -50.31) * mm, "end": v(4.97, -50.38) * mm});
            skLineSegment(sketch, "E5157", {"start": v(4.97, -50.38) * mm, "end": v(5, -50.46) * mm});
            skLineSegment(sketch, "E5158", {"start": v(5, -50.46) * mm, "end": v(5.04, -50.53) * mm});
            skLineSegment(sketch, "E5159", {"start": v(5.04, -50.53) * mm, "end": v(5.08, -50.6) * mm});
            skLineSegment(sketch, "E5160", {"start": v(5.08, -50.6) * mm, "end": v(5.12, -50.68) * mm});
            skLineSegment(sketch, "E5161", {"start": v(5.12, -50.68) * mm, "end": v(5.16, -50.76) * mm});
            skLineSegment(sketch, "E5162", {"start": v(5.16, -50.76) * mm, "end": v(5.2, -50.83) * mm});
            skLineSegment(sketch, "E5163", {"start": v(5.2, -50.83) * mm, "end": v(5.25, -50.91) * mm});
            skLineSegment(sketch, "E5164", {"start": v(5.25, -50.91) * mm, "end": v(5.3, -50.98) * mm});
            skLineSegment(sketch, "E5165", {"start": v(5.3, -50.98) * mm, "end": v(6.25, -50.87) * mm});
            skLineSegment(sketch, "E5166", {"start": v(6.25, -50.87) * mm, "end": v(6.28, -50.8) * mm});
            skLineSegment(sketch, "E5167", {"start": v(6.28, -50.8) * mm, "end": v(6.3, -50.7) * mm});
            skLineSegment(sketch, "E5168", {"start": v(6.3, -50.7) * mm, "end": v(6.33, -50.63) * mm});
            skLineSegment(sketch, "E5169", {"start": v(6.33, -50.63) * mm, "end": v(6.35, -50.54) * mm});
            skLineSegment(sketch, "E5170", {"start": v(6.35, -50.54) * mm, "end": v(6.37, -50.46) * mm});
            skLineSegment(sketch, "E5171", {"start": v(6.37, -50.46) * mm, "end": v(6.4, -50.38) * mm});
            skLineSegment(sketch, "E5172", {"start": v(6.4, -50.38) * mm, "end": v(6.42, -50.3) * mm});
            skLineSegment(sketch, "E5173", {"start": v(6.42, -50.3) * mm, "end": v(6.44, -50.22) * mm});
            skLineSegment(sketch, "E5174", {"start": v(6.44, -50.22) * mm, "end": v(6.46, -50.14) * mm});
            skLineSegment(sketch, "E5175", {"start": v(6.46, -50.14) * mm, "end": v(6.48, -50.06) * mm});
            skLineSegment(sketch, "E5176", {"start": v(6.48, -50.06) * mm, "end": v(6.5, -49.98) * mm});
            skLineSegment(sketch, "E5177", {"start": v(6.5, -49.98) * mm, "end": v(6.52, -49.9) * mm});
            skLineSegment(sketch, "E5178", {"start": v(6.52, -49.9) * mm, "end": v(6.53, -49.83) * mm});
            skLineSegment(sketch, "E5179", {"start": v(6.53, -49.83) * mm, "end": v(6.55, -49.75) * mm});
            skLineSegment(sketch, "E5180", {"start": v(6.55, -49.75) * mm, "end": v(6.57, -49.68) * mm});
            skLineSegment(sketch, "E5181", {"start": v(6.57, -49.68) * mm, "end": v(6.59, -49.6) * mm});
            skLineSegment(sketch, "E5182", {"start": v(6.59, -49.6) * mm, "end": v(6.6, -49.53) * mm});
            skLineSegment(sketch, "E5183", {"start": v(6.6, -49.53) * mm, "end": v(6.62, -49.46) * mm});
            skLineSegment(sketch, "E5184", {"start": v(6.62, -49.46) * mm, "end": v(6.63, -49.39) * mm});
            skLineSegment(sketch, "E5185", {"start": v(6.63, -49.39) * mm, "end": v(6.65, -49.32) * mm});
            skLineSegment(sketch, "E5186", {"start": v(6.65, -49.32) * mm, "end": v(6.66, -49.25) * mm});
            skLineSegment(sketch, "E5187", {"start": v(6.66, -49.25) * mm, "end": v(6.67, -49.18) * mm});
            skLineSegment(sketch, "E5188", {"start": v(6.67, -49.18) * mm, "end": v(6.69, -49.11) * mm});
            skLineSegment(sketch, "E5189", {"start": v(6.69, -49.11) * mm, "end": v(6.7, -49.05) * mm});
            skLineSegment(sketch, "E5190", {"start": v(6.7, -49.05) * mm, "end": v(6.71, -48.98) * mm});
            skLineSegment(sketch, "E5191", {"start": v(6.71, -48.98) * mm, "end": v(6.72, -48.91) * mm});
            skLineSegment(sketch, "E5192", {"start": v(6.72, -48.91) * mm, "end": v(6.74, -48.85) * mm});
            skLineSegment(sketch, "E5193", {"start": v(6.74, -48.85) * mm, "end": v(6.75, -48.78) * mm});
            skLineSegment(sketch, "E5194", {"start": v(6.75, -48.78) * mm, "end": v(6.76, -48.72) * mm});
            skLineSegment(sketch, "E5195", {"start": v(6.76, -48.72) * mm, "end": v(6.77, -48.66) * mm});
            skLineSegment(sketch, "E5196", {"start": v(6.77, -48.66) * mm, "end": v(6.78, -48.6) * mm});
            skLineSegment(sketch, "E5197", {"start": v(6.78, -48.6) * mm, "end": v(6.79, -48.54) * mm});
            skLineSegment(sketch, "E5198", {"start": v(6.79, -48.54) * mm, "end": v(6.8, -48.48) * mm});
            skLineSegment(sketch, "E5199", {"start": v(6.8, -48.48) * mm, "end": v(6.8, -48.42) * mm});
            skLineSegment(sketch, "E5200", {"start": v(6.8, -48.42) * mm, "end": v(6.81, -48.36) * mm});
            skLineSegment(sketch, "E5201", {"start": v(6.81, -48.36) * mm, "end": v(6.82, -48.3) * mm});
            skLineSegment(sketch, "E5202", {"start": v(6.82, -48.3) * mm, "end": v(6.83, -48.25) * mm});
            skLineSegment(sketch, "E5203", {"start": v(6.83, -48.25) * mm, "end": v(6.83, -48.2) * mm});
            skLineSegment(sketch, "E5204", {"start": v(6.83, -48.2) * mm, "end": v(6.84, -48.14) * mm});
            skLineSegment(sketch, "E5205", {"start": v(6.84, -48.14) * mm, "end": v(6.85, -48.08) * mm});
            skLineSegment(sketch, "E5206", {"start": v(6.85, -48.08) * mm, "end": v(7.12, -48.04) * mm});
            skLineSegment(sketch, "E5207", {"start": v(7.12, -48.04) * mm, "end": v(7.6, -47.96) * mm});
            skLineSegment(sketch, "E5208", {"start": v(7.6, -47.96) * mm, "end": v(7.87, -47.93) * mm});
            skLineSegment(sketch, "E5209", {"start": v(7.87, -47.93) * mm, "end": v(7.9, -47.98) * mm});
            skLineSegment(sketch, "E5210", {"start": v(7.9, -47.98) * mm, "end": v(7.92, -48.03) * mm});
            skLineSegment(sketch, "E5211", {"start": v(7.92, -48.03) * mm, "end": v(7.94, -48.08) * mm});
            skLineSegment(sketch, "E5212", {"start": v(7.94, -48.08) * mm, "end": v(7.97, -48.13) * mm});
            skLineSegment(sketch, "E5213", {"start": v(7.97, -48.13) * mm, "end": v(7.99, -48.18) * mm});
            skLineSegment(sketch, "E5214", {"start": v(7.99, -48.18) * mm, "end": v(8.01, -48.23) * mm});
            skLineSegment(sketch, "E5215", {"start": v(8.01, -48.23) * mm, "end": v(8.04, -48.29) * mm});
            skLineSegment(sketch, "E5216", {"start": v(8.04, -48.29) * mm, "end": v(8.07, -48.34) * mm});
            skLineSegment(sketch, "E5217", {"start": v(8.07, -48.34) * mm, "end": v(8.1, -48.4) * mm});
            skLineSegment(sketch, "E5218", {"start": v(8.1, -48.4) * mm, "end": v(8.12, -48.45) * mm});
            skLineSegment(sketch, "E5219", {"start": v(8.12, -48.45) * mm, "end": v(8.15, -48.5) * mm});
            skLineSegment(sketch, "E5220", {"start": v(8.15, -48.5) * mm, "end": v(8.18, -48.56) * mm});
            skLineSegment(sketch, "E5221", {"start": v(8.18, -48.56) * mm, "end": v(8.2, -48.62) * mm});
            skLineSegment(sketch, "E5222", {"start": v(8.2, -48.62) * mm, "end": v(8.24, -48.68) * mm});
            skLineSegment(sketch, "E5223", {"start": v(8.24, -48.68) * mm, "end": v(8.27, -48.74) * mm});
            skLineSegment(sketch, "E5224", {"start": v(8.27, -48.74) * mm, "end": v(8.3, -48.8) * mm});
            skLineSegment(sketch, "E5225", {"start": v(8.3, -48.8) * mm, "end": v(8.33, -48.86) * mm});
            skLineSegment(sketch, "E5226", {"start": v(8.33, -48.86) * mm, "end": v(8.37, -48.92) * mm});
            skLineSegment(sketch, "E5227", {"start": v(8.37, -48.92) * mm, "end": v(8.4, -48.98) * mm});
            skLineSegment(sketch, "E5228", {"start": v(8.4, -48.98) * mm, "end": v(8.43, -49.04) * mm});
            skLineSegment(sketch, "E5229", {"start": v(8.43, -49.04) * mm, "end": v(8.47, -49.1) * mm});
            skLineSegment(sketch, "E5230", {"start": v(8.47, -49.1) * mm, "end": v(8.5, -49.17) * mm});
            skLineSegment(sketch, "E5231", {"start": v(8.5, -49.17) * mm, "end": v(8.54, -49.24) * mm});
            skLineSegment(sketch, "E5232", {"start": v(8.54, -49.24) * mm, "end": v(8.58, -49.3) * mm});
            skLineSegment(sketch, "E5233", {"start": v(8.58, -49.3) * mm, "end": v(8.62, -49.37) * mm});
            skLineSegment(sketch, "E5234", {"start": v(8.62, -49.37) * mm, "end": v(8.66, -49.43) * mm});
            skLineSegment(sketch, "E5235", {"start": v(8.66, -49.43) * mm, "end": v(8.7, -49.5) * mm});
            skLineSegment(sketch, "E5236", {"start": v(8.7, -49.5) * mm, "end": v(8.73, -49.57) * mm});
            skLineSegment(sketch, "E5237", {"start": v(8.73, -49.57) * mm, "end": v(8.78, -49.63) * mm});
            skLineSegment(sketch, "E5238", {"start": v(8.78, -49.63) * mm, "end": v(8.82, -49.7) * mm});
            skLineSegment(sketch, "E5239", {"start": v(8.82, -49.7) * mm, "end": v(8.86, -49.77) * mm});
            skLineSegment(sketch, "E5240", {"start": v(8.86, -49.77) * mm, "end": v(8.9, -49.84) * mm});
            skLineSegment(sketch, "E5241", {"start": v(8.9, -49.84) * mm, "end": v(8.95, -49.91) * mm});
            skLineSegment(sketch, "E5242", {"start": v(8.95, -49.91) * mm, "end": v(9, -49.98) * mm});
            skLineSegment(sketch, "E5243", {"start": v(9, -49.98) * mm, "end": v(9.04, -50.05) * mm});
            skLineSegment(sketch, "E5244", {"start": v(9.04, -50.05) * mm, "end": v(9.08, -50.12) * mm});
            skLineSegment(sketch, "E5245", {"start": v(9.08, -50.12) * mm, "end": v(9.13, -50.2) * mm});
            skLineSegment(sketch, "E5246", {"start": v(9.13, -50.2) * mm, "end": v(9.18, -50.27) * mm});
            skLineSegment(sketch, "E5247", {"start": v(9.18, -50.27) * mm, "end": v(9.23, -50.34) * mm});
            skLineSegment(sketch, "E5248", {"start": v(9.23, -50.34) * mm, "end": v(9.28, -50.4) * mm});
            skLineSegment(sketch, "E5249", {"start": v(9.28, -50.4) * mm, "end": v(10.22, -50.22) * mm});
            skLineSegment(sketch, "E5250", {"start": v(10.22, -50.22) * mm, "end": v(10.24, -50.15) * mm});
            skLineSegment(sketch, "E5251", {"start": v(10.24, -50.15) * mm, "end": v(10.26, -50.06) * mm});
            skLineSegment(sketch, "E5252", {"start": v(10.26, -50.06) * mm, "end": v(10.28, -49.97) * mm});
            skLineSegment(sketch, "E5253", {"start": v(10.28, -49.97) * mm, "end": v(10.3, -49.89) * mm});
            skLineSegment(sketch, "E5254", {"start": v(10.3, -49.89) * mm, "end": v(10.31, -49.8) * mm});
            skLineSegment(sketch, "E5255", {"start": v(10.31, -49.8) * mm, "end": v(10.33, -49.72) * mm});
            skLineSegment(sketch, "E5256", {"start": v(10.33, -49.72) * mm, "end": v(10.34, -49.64) * mm});
            skLineSegment(sketch, "E5257", {"start": v(10.34, -49.64) * mm, "end": v(10.36, -49.56) * mm});
            skLineSegment(sketch, "E5258", {"start": v(10.36, -49.56) * mm, "end": v(10.37, -49.48) * mm});
            skLineSegment(sketch, "E5259", {"start": v(10.37, -49.48) * mm, "end": v(10.39, -49.4) * mm});
            skLineSegment(sketch, "E5260", {"start": v(10.39, -49.4) * mm, "end": v(10.4, -49.32) * mm});
            skLineSegment(sketch, "E5261", {"start": v(10.4, -49.32) * mm, "end": v(10.41, -49.24) * mm});
            skLineSegment(sketch, "E5262", {"start": v(10.41, -49.24) * mm, "end": v(10.42, -49.16) * mm});
            skLineSegment(sketch, "E5263", {"start": v(10.42, -49.16) * mm, "end": v(10.44, -49.09) * mm});
            skLineSegment(sketch, "E5264", {"start": v(10.44, -49.09) * mm, "end": v(10.45, -49.01) * mm});
            skLineSegment(sketch, "E5265", {"start": v(10.45, -49.01) * mm, "end": v(10.46, -48.94) * mm});
            skLineSegment(sketch, "E5266", {"start": v(10.46, -48.94) * mm, "end": v(10.47, -48.86) * mm});
            skLineSegment(sketch, "E5267", {"start": v(10.47, -48.86) * mm, "end": v(10.48, -48.79) * mm});
            skLineSegment(sketch, "E5268", {"start": v(10.48, -48.79) * mm, "end": v(10.49, -48.72) * mm});
            skLineSegment(sketch, "E5269", {"start": v(10.49, -48.72) * mm, "end": v(10.5, -48.65) * mm});
            skLineSegment(sketch, "E5270", {"start": v(10.5, -48.65) * mm, "end": v(10.5, -48.57) * mm});
            skLineSegment(sketch, "E5271", {"start": v(10.5, -48.57) * mm, "end": v(10.51, -48.5) * mm});
            skLineSegment(sketch, "E5272", {"start": v(10.51, -48.5) * mm, "end": v(10.52, -48.44) * mm});
            skLineSegment(sketch, "E5273", {"start": v(10.52, -48.44) * mm, "end": v(10.53, -48.37) * mm});
            skLineSegment(sketch, "E5274", {"start": v(10.53, -48.37) * mm, "end": v(10.54, -48.3) * mm});
            skLineSegment(sketch, "E5275", {"start": v(10.54, -48.3) * mm, "end": v(10.54, -48.23) * mm});
            skLineSegment(sketch, "E5276", {"start": v(10.54, -48.23) * mm, "end": v(10.55, -48.17) * mm});
            skLineSegment(sketch, "E5277", {"start": v(10.55, -48.17) * mm, "end": v(10.55, -48.1) * mm});
            skLineSegment(sketch, "E5278", {"start": v(10.55, -48.1) * mm, "end": v(10.56, -48.04) * mm});
            skLineSegment(sketch, "E5279", {"start": v(10.56, -48.04) * mm, "end": v(10.56, -47.98) * mm});
            skLineSegment(sketch, "E5280", {"start": v(10.56, -47.98) * mm, "end": v(10.57, -47.92) * mm});
            skLineSegment(sketch, "E5281", {"start": v(10.57, -47.92) * mm, "end": v(10.57, -47.85) * mm});
            skLineSegment(sketch, "E5282", {"start": v(10.57, -47.85) * mm, "end": v(10.58, -47.8) * mm});
            skLineSegment(sketch, "E5283", {"start": v(10.58, -47.8) * mm, "end": v(10.58, -47.74) * mm});
            skLineSegment(sketch, "E5284", {"start": v(10.58, -47.74) * mm, "end": v(10.59, -47.68) * mm});
            skLineSegment(sketch, "E5285", {"start": v(10.59, -47.68) * mm, "end": v(10.59, -47.62) * mm});
            skLineSegment(sketch, "E5286", {"start": v(10.59, -47.62) * mm, "end": v(10.6, -47.56) * mm});
            skLineSegment(sketch, "E5287", {"start": v(10.6, -47.56) * mm, "end": v(10.6, -47.5) * mm});
            skLineSegment(sketch, "E5288", {"start": v(10.6, -47.5) * mm, "end": v(10.6, -47.45) * mm});
            skLineSegment(sketch, "E5289", {"start": v(10.6, -47.45) * mm, "end": v(10.6, -47.4) * mm});
            skLineSegment(sketch, "E5290", {"start": v(10.6, -47.4) * mm, "end": v(10.87, -47.33) * mm});
            skLineSegment(sketch, "E5291", {"start": v(10.87, -47.33) * mm, "end": v(11.34, -47.22) * mm});
            skLineSegment(sketch, "E5292", {"start": v(11.34, -47.22) * mm, "end": v(11.6, -47.16) * mm});
            skLineSegment(sketch, "E5293", {"start": v(11.6, -47.16) * mm, "end": v(11.64, -47.2) * mm});
            skLineSegment(sketch, "E5294", {"start": v(11.64, -47.2) * mm, "end": v(11.66, -47.26) * mm});
            skLineSegment(sketch, "E5295", {"start": v(11.66, -47.26) * mm, "end": v(11.69, -47.3) * mm});
            skLineSegment(sketch, "E5296", {"start": v(11.69, -47.3) * mm, "end": v(11.72, -47.35) * mm});
            skLineSegment(sketch, "E5297", {"start": v(11.72, -47.35) * mm, "end": v(11.75, -47.4) * mm});
            skLineSegment(sketch, "E5298", {"start": v(11.75, -47.4) * mm, "end": v(11.77, -47.46) * mm});
            skLineSegment(sketch, "E5299", {"start": v(11.77, -47.46) * mm, "end": v(11.8, -47.5) * mm});
            skLineSegment(sketch, "E5300", {"start": v(11.8, -47.5) * mm, "end": v(11.83, -47.56) * mm});
            skLineSegment(sketch, "E5301", {"start": v(11.83, -47.56) * mm, "end": v(11.87, -47.61) * mm});
            skLineSegment(sketch, "E5302", {"start": v(11.87, -47.61) * mm, "end": v(11.9, -47.66) * mm});
            skLineSegment(sketch, "E5303", {"start": v(11.9, -47.66) * mm, "end": v(11.93, -47.72) * mm});
            skLineSegment(sketch, "E5304", {"start": v(11.93, -47.72) * mm, "end": v(11.96, -47.77) * mm});
            skLineSegment(sketch, "E5305", {"start": v(11.96, -47.77) * mm, "end": v(12, -47.83) * mm});
            skLineSegment(sketch, "E5306", {"start": v(12, -47.83) * mm, "end": v(12.03, -47.88) * mm});
            skLineSegment(sketch, "E5307", {"start": v(12.03, -47.88) * mm, "end": v(12.07, -47.94) * mm});
            skLineSegment(sketch, "E5308", {"start": v(12.07, -47.94) * mm, "end": v(12.1, -48) * mm});
            skLineSegment(sketch, "E5309", {"start": v(12.1, -48) * mm, "end": v(12.14, -48.06) * mm});
            skLineSegment(sketch, "E5310", {"start": v(12.14, -48.06) * mm, "end": v(12.18, -48.11) * mm});
            skLineSegment(sketch, "E5311", {"start": v(12.18, -48.11) * mm, "end": v(12.22, -48.17) * mm});
            skLineSegment(sketch, "E5312", {"start": v(12.22, -48.17) * mm, "end": v(12.26, -48.23) * mm});
            skLineSegment(sketch, "E5313", {"start": v(12.26, -48.23) * mm, "end": v(12.3, -48.3) * mm});
            skLineSegment(sketch, "E5314", {"start": v(12.3, -48.3) * mm, "end": v(12.34, -48.35) * mm});
            skLineSegment(sketch, "E5315", {"start": v(12.34, -48.35) * mm, "end": v(12.38, -48.41) * mm});
            skLineSegment(sketch, "E5316", {"start": v(12.38, -48.41) * mm, "end": v(12.42, -48.48) * mm});
            skLineSegment(sketch, "E5317", {"start": v(12.42, -48.48) * mm, "end": v(12.46, -48.54) * mm});
            skLineSegment(sketch, "E5318", {"start": v(12.46, -48.54) * mm, "end": v(12.5, -48.6) * mm});
            skLineSegment(sketch, "E5319", {"start": v(12.5, -48.6) * mm, "end": v(12.55, -48.66) * mm});
            skLineSegment(sketch, "E5320", {"start": v(12.55, -48.66) * mm, "end": v(12.6, -48.73) * mm});
            skLineSegment(sketch, "E5321", {"start": v(12.6, -48.73) * mm, "end": v(12.64, -48.8) * mm});
            skLineSegment(sketch, "E5322", {"start": v(12.64, -48.8) * mm, "end": v(12.69, -48.86) * mm});
            skLineSegment(sketch, "E5323", {"start": v(12.69, -48.86) * mm, "end": v(12.74, -48.92) * mm});
            skLineSegment(sketch, "E5324", {"start": v(12.74, -48.92) * mm, "end": v(12.79, -48.99) * mm});
            skLineSegment(sketch, "E5325", {"start": v(12.79, -48.99) * mm, "end": v(12.84, -49.05) * mm});
            skLineSegment(sketch, "E5326", {"start": v(12.84, -49.05) * mm, "end": v(12.89, -49.12) * mm});
            skLineSegment(sketch, "E5327", {"start": v(12.89, -49.12) * mm, "end": v(12.94, -49.19) * mm});
            skLineSegment(sketch, "E5328", {"start": v(12.94, -49.19) * mm, "end": v(12.99, -49.26) * mm});
            skLineSegment(sketch, "E5329", {"start": v(12.99, -49.26) * mm, "end": v(13.04, -49.32) * mm});
            skLineSegment(sketch, "E5330", {"start": v(13.04, -49.32) * mm, "end": v(13.1, -49.4) * mm});
            skLineSegment(sketch, "E5331", {"start": v(13.1, -49.4) * mm, "end": v(13.15, -49.46) * mm});
            skLineSegment(sketch, "E5332", {"start": v(13.15, -49.46) * mm, "end": v(13.2, -49.52) * mm});
            skLineSegment(sketch, "E5333", {"start": v(13.2, -49.52) * mm, "end": v(14.13, -49.26) * mm});
            skLineSegment(sketch, "E5334", {"start": v(14.13, -49.26) * mm, "end": v(14.15, -49.19) * mm});
            skLineSegment(sketch, "E5335", {"start": v(14.15, -49.19) * mm, "end": v(14.16, -49.1) * mm});
            skLineSegment(sketch, "E5336", {"start": v(14.16, -49.1) * mm, "end": v(14.17, -49.01) * mm});
            skLineSegment(sketch, "E5337", {"start": v(14.17, -49.01) * mm, "end": v(14.18, -48.93) * mm});
            skLineSegment(sketch, "E5338", {"start": v(14.18, -48.93) * mm, "end": v(14.19, -48.84) * mm});
            skLineSegment(sketch, "E5339", {"start": v(14.19, -48.84) * mm, "end": v(14.2, -48.76) * mm});
            skLineSegment(sketch, "E5340", {"start": v(14.2, -48.76) * mm, "end": v(14.2, -48.67) * mm});
            skLineSegment(sketch, "E5341", {"start": v(14.2, -48.67) * mm, "end": v(14.21, -48.6) * mm});
            skLineSegment(sketch, "E5342", {"start": v(14.21, -48.6) * mm, "end": v(14.22, -48.51) * mm});
            skLineSegment(sketch, "E5343", {"start": v(14.22, -48.51) * mm, "end": v(14.23, -48.43) * mm});
            skLineSegment(sketch, "E5344", {"start": v(14.23, -48.43) * mm, "end": v(14.24, -48.35) * mm});
            skLineSegment(sketch, "E5345", {"start": v(14.24, -48.35) * mm, "end": v(14.24, -48.27) * mm});
            skLineSegment(sketch, "E5346", {"start": v(14.24, -48.27) * mm, "end": v(14.25, -48.2) * mm});
            skLineSegment(sketch, "E5347", {"start": v(14.25, -48.2) * mm, "end": v(14.25, -48.12) * mm});
            skLineSegment(sketch, "E5348", {"start": v(14.25, -48.12) * mm, "end": v(14.26, -48.04) * mm});
            skLineSegment(sketch, "E5349", {"start": v(14.26, -48.04) * mm, "end": v(14.26, -47.96) * mm});
            skLineSegment(sketch, "E5350", {"start": v(14.26, -47.96) * mm, "end": v(14.27, -47.9) * mm});
            skLineSegment(sketch, "E5351", {"start": v(14.27, -47.9) * mm, "end": v(14.27, -47.82) * mm});
            skLineSegment(sketch, "E5352", {"start": v(14.27, -47.82) * mm, "end": v(14.28, -47.74) * mm});
            skLineSegment(sketch, "E5353", {"start": v(14.28, -47.74) * mm, "end": v(14.28, -47.67) * mm});
            skLineSegment(sketch, "E5354", {"start": v(14.28, -47.67) * mm, "end": v(14.28, -47.6) * mm});
            skLineSegment(sketch, "E5355", {"start": v(14.28, -47.6) * mm, "end": v(14.29, -47.53) * mm});
            skLineSegment(sketch, "E5356", {"start": v(14.29, -47.53) * mm, "end": v(14.29, -47.46) * mm});
            skLineSegment(sketch, "E5357", {"start": v(14.29, -47.46) * mm, "end": v(14.3, -47.4) * mm});
            skLineSegment(sketch, "E5358", {"start": v(14.3, -47.4) * mm, "end": v(14.3, -47.33) * mm});
            skLineSegment(sketch, "E5359", {"start": v(14.3, -47.33) * mm, "end": v(14.3, -47.26) * mm});
            skLineSegment(sketch, "E5360", {"start": v(14.3, -47.26) * mm, "end": v(14.3, -47.2) * mm});
            skLineSegment(sketch, "E5361", {"start": v(14.3, -47.2) * mm, "end": v(14.3, -47.13) * mm});
            skLineSegment(sketch, "E5362", {"start": v(14.3, -47.13) * mm, "end": v(14.3, -47.06) * mm});
            skLineSegment(sketch, "E5363", {"start": v(14.3, -47.06) * mm, "end": v(14.3, -47) * mm});
            skLineSegment(sketch, "E5364", {"start": v(14.3, -47) * mm, "end": v(14.3, -46.94) * mm});
            skLineSegment(sketch, "E5365", {"start": v(14.3, -46.94) * mm, "end": v(14.3, -46.88) * mm});
            skLineSegment(sketch, "E5366", {"start": v(14.3, -46.88) * mm, "end": v(14.3, -46.82) * mm});
            skLineSegment(sketch, "E5367", {"start": v(14.3, -46.82) * mm, "end": v(14.3, -46.76) * mm});
            skLineSegment(sketch, "E5368", {"start": v(14.3, -46.76) * mm, "end": v(14.3, -46.7) * mm});
            skLineSegment(sketch, "E5369", {"start": v(14.3, -46.7) * mm, "end": v(14.3, -46.64) * mm});
            skLineSegment(sketch, "E5370", {"start": v(14.3, -46.64) * mm, "end": v(14.3, -46.58) * mm});
            skLineSegment(sketch, "E5371", {"start": v(14.3, -46.58) * mm, "end": v(14.29, -46.53) * mm});
            skLineSegment(sketch, "E5372", {"start": v(14.29, -46.53) * mm, "end": v(14.29, -46.47) * mm});
            skLineSegment(sketch, "E5373", {"start": v(14.29, -46.47) * mm, "end": v(14.28, -46.42) * mm});
            skLineSegment(sketch, "E5374", {"start": v(14.28, -46.42) * mm, "end": v(14.55, -46.33) * mm});
            skLineSegment(sketch, "E5375", {"start": v(14.55, -46.33) * mm, "end": v(15, -46.19) * mm});
            skLineSegment(sketch, "E5376", {"start": v(15, -46.19) * mm, "end": v(15.27, -46.1) * mm});
            skLineSegment(sketch, "E5377", {"start": v(15.27, -46.1) * mm, "end": v(15.3, -46.15) * mm});
            skLineSegment(sketch, "E5378", {"start": v(15.3, -46.15) * mm, "end": v(15.33, -46.2) * mm});
            skLineSegment(sketch, "E5379", {"start": v(15.33, -46.2) * mm, "end": v(15.36, -46.24) * mm});
            skLineSegment(sketch, "E5380", {"start": v(15.36, -46.24) * mm, "end": v(15.4, -46.29) * mm});
            skLineSegment(sketch, "E5381", {"start": v(15.4, -46.29) * mm, "end": v(15.43, -46.34) * mm});
            skLineSegment(sketch, "E5382", {"start": v(15.43, -46.34) * mm, "end": v(15.46, -46.39) * mm});
            skLineSegment(sketch, "E5383", {"start": v(15.46, -46.39) * mm, "end": v(15.5, -46.43) * mm});
            skLineSegment(sketch, "E5384", {"start": v(15.5, -46.43) * mm, "end": v(15.53, -46.48) * mm});
            skLineSegment(sketch, "E5385", {"start": v(15.53, -46.48) * mm, "end": v(15.57, -46.53) * mm});
            skLineSegment(sketch, "E5386", {"start": v(15.57, -46.53) * mm, "end": v(15.6, -46.58) * mm});
            skLineSegment(sketch, "E5387", {"start": v(15.6, -46.58) * mm, "end": v(15.64, -46.64) * mm});
            skLineSegment(sketch, "E5388", {"start": v(15.64, -46.64) * mm, "end": v(15.68, -46.69) * mm});
            skLineSegment(sketch, "E5389", {"start": v(15.68, -46.69) * mm, "end": v(15.71, -46.74) * mm});
            skLineSegment(sketch, "E5390", {"start": v(15.71, -46.74) * mm, "end": v(15.75, -46.8) * mm});
            skLineSegment(sketch, "E5391", {"start": v(15.75, -46.8) * mm, "end": v(15.8, -46.85) * mm});
            skLineSegment(sketch, "E5392", {"start": v(15.8, -46.85) * mm, "end": v(15.83, -46.9) * mm});
            skLineSegment(sketch, "E5393", {"start": v(15.83, -46.9) * mm, "end": v(15.87, -46.95) * mm});
            skLineSegment(sketch, "E5394", {"start": v(15.87, -46.95) * mm, "end": v(15.92, -47.01) * mm});
            skLineSegment(sketch, "E5395", {"start": v(15.92, -47.01) * mm, "end": v(15.96, -47.07) * mm});
            skLineSegment(sketch, "E5396", {"start": v(15.96, -47.07) * mm, "end": v(16, -47.12) * mm});
            skLineSegment(sketch, "E5397", {"start": v(16, -47.12) * mm, "end": v(16.05, -47.18) * mm});
            skLineSegment(sketch, "E5398", {"start": v(16.05, -47.18) * mm, "end": v(16.1, -47.24) * mm});
            skLineSegment(sketch, "E5399", {"start": v(16.1, -47.24) * mm, "end": v(16.14, -47.3) * mm});
            skLineSegment(sketch, "E5400", {"start": v(16.14, -47.3) * mm, "end": v(16.19, -47.35) * mm});
            skLineSegment(sketch, "E5401", {"start": v(16.19, -47.35) * mm, "end": v(16.23, -47.41) * mm});
            skLineSegment(sketch, "E5402", {"start": v(16.23, -47.41) * mm, "end": v(16.28, -47.47) * mm});
            skLineSegment(sketch, "E5403", {"start": v(16.28, -47.47) * mm, "end": v(16.33, -47.53) * mm});
            skLineSegment(sketch, "E5404", {"start": v(16.33, -47.53) * mm, "end": v(16.38, -47.59) * mm});
            skLineSegment(sketch, "E5405", {"start": v(16.38, -47.59) * mm, "end": v(16.43, -47.65) * mm});
            skLineSegment(sketch, "E5406", {"start": v(16.43, -47.65) * mm, "end": v(16.48, -47.71) * mm});
            skLineSegment(sketch, "E5407", {"start": v(16.48, -47.71) * mm, "end": v(16.54, -47.77) * mm});
            skLineSegment(sketch, "E5408", {"start": v(16.54, -47.77) * mm, "end": v(16.6, -47.83) * mm});
            skLineSegment(sketch, "E5409", {"start": v(16.6, -47.83) * mm, "end": v(16.64, -47.9) * mm});
            skLineSegment(sketch, "E5410", {"start": v(16.64, -47.9) * mm, "end": v(16.7, -47.96) * mm});
            skLineSegment(sketch, "E5411", {"start": v(16.7, -47.96) * mm, "end": v(16.76, -48.02) * mm});
            skLineSegment(sketch, "E5412", {"start": v(16.76, -48.02) * mm, "end": v(16.81, -48.09) * mm});
            skLineSegment(sketch, "E5413", {"start": v(16.81, -48.09) * mm, "end": v(16.87, -48.15) * mm});
            skLineSegment(sketch, "E5414", {"start": v(16.87, -48.15) * mm, "end": v(16.93, -48.21) * mm});
            skLineSegment(sketch, "E5415", {"start": v(16.93, -48.21) * mm, "end": v(16.99, -48.28) * mm});
            skLineSegment(sketch, "E5416", {"start": v(16.99, -48.28) * mm, "end": v(17.05, -48.33) * mm});
            skLineSegment(sketch, "E5417", {"start": v(17.05, -48.33) * mm, "end": v(17.95, -48) * mm});
            skLineSegment(sketch, "E5418", {"start": v(17.95, -48) * mm, "end": v(17.96, -47.93) * mm});
            skLineSegment(sketch, "E5419", {"start": v(17.96, -47.93) * mm, "end": v(17.97, -47.84) * mm});
            skLineSegment(sketch, "E5420", {"start": v(17.97, -47.84) * mm, "end": v(17.97, -47.75) * mm});
            skLineSegment(sketch, "E5421", {"start": v(17.97, -47.75) * mm, "end": v(17.97, -47.66) * mm});
            skLineSegment(sketch, "E5422", {"start": v(17.97, -47.66) * mm, "end": v(17.98, -47.58) * mm});
            skLineSegment(sketch, "E5423", {"start": v(17.98, -47.58) * mm, "end": v(17.98, -47.5) * mm});
            skLineSegment(sketch, "E5424", {"start": v(17.98, -47.5) * mm, "end": v(17.98, -47.41) * mm});
            skLineSegment(sketch, "E5425", {"start": v(17.98, -47.41) * mm, "end": v(17.98, -47.33) * mm});
            skLineSegment(sketch, "E5426", {"start": v(17.98, -47.33) * mm, "end": v(17.98, -47.25) * mm});
            skLineSegment(sketch, "E5427", {"start": v(17.98, -47.25) * mm, "end": v(17.99, -47.16) * mm});
            skLineSegment(sketch, "E5428", {"start": v(17.99, -47.16) * mm, "end": v(17.99, -47.08) * mm});
            skLineSegment(sketch, "E5429", {"start": v(17.99, -47.08) * mm, "end": v(17.99, -47) * mm});
            skLineSegment(sketch, "E5430", {"start": v(17.99, -47) * mm, "end": v(17.99, -46.93) * mm});
            skLineSegment(sketch, "E5431", {"start": v(17.99, -46.93) * mm, "end": v(17.99, -46.85) * mm});
            skLineSegment(sketch, "E5432", {"start": v(17.99, -46.85) * mm, "end": v(17.99, -46.77) * mm});
            skLineSegment(sketch, "E5433", {"start": v(17.99, -46.77) * mm, "end": v(17.98, -46.7) * mm});
            skLineSegment(sketch, "E5434", {"start": v(17.98, -46.7) * mm, "end": v(17.98, -46.62) * mm});
            skLineSegment(sketch, "E5435", {"start": v(17.98, -46.62) * mm, "end": v(17.98, -46.55) * mm});
            skLineSegment(sketch, "E5436", {"start": v(17.98, -46.55) * mm, "end": v(17.98, -46.48) * mm});
            skLineSegment(sketch, "E5437", {"start": v(17.98, -46.48) * mm, "end": v(17.98, -46.4) * mm});
            skLineSegment(sketch, "E5438", {"start": v(17.98, -46.4) * mm, "end": v(17.97, -46.33) * mm});
            skLineSegment(sketch, "E5439", {"start": v(17.97, -46.33) * mm, "end": v(17.97, -46.26) * mm});
            skLineSegment(sketch, "E5440", {"start": v(17.97, -46.26) * mm, "end": v(17.97, -46.2) * mm});
            skLineSegment(sketch, "E5441", {"start": v(17.97, -46.2) * mm, "end": v(17.96, -46.13) * mm});
            skLineSegment(sketch, "E5442", {"start": v(17.96, -46.13) * mm, "end": v(17.96, -46.06) * mm});
            skLineSegment(sketch, "E5443", {"start": v(17.96, -46.06) * mm, "end": v(17.96, -46) * mm});
            skLineSegment(sketch, "E5444", {"start": v(17.96, -46) * mm, "end": v(17.95, -45.93) * mm});
            skLineSegment(sketch, "E5445", {"start": v(17.95, -45.93) * mm, "end": v(17.95, -45.86) * mm});
            skLineSegment(sketch, "E5446", {"start": v(17.95, -45.86) * mm, "end": v(17.94, -45.8) * mm});
            skLineSegment(sketch, "E5447", {"start": v(17.94, -45.8) * mm, "end": v(17.94, -45.73) * mm});
            skLineSegment(sketch, "E5448", {"start": v(17.94, -45.73) * mm, "end": v(17.93, -45.67) * mm});
            skLineSegment(sketch, "E5449", {"start": v(17.93, -45.67) * mm, "end": v(17.93, -45.61) * mm});
            skLineSegment(sketch, "E5450", {"start": v(17.93, -45.61) * mm, "end": v(17.92, -45.55) * mm});
            skLineSegment(sketch, "E5451", {"start": v(17.92, -45.55) * mm, "end": v(17.92, -45.5) * mm});
            skLineSegment(sketch, "E5452", {"start": v(17.92, -45.5) * mm, "end": v(17.91, -45.43) * mm});
            skLineSegment(sketch, "E5453", {"start": v(17.91, -45.43) * mm, "end": v(17.9, -45.38) * mm});
            skLineSegment(sketch, "E5454", {"start": v(17.9, -45.38) * mm, "end": v(17.9, -45.32) * mm});
            skLineSegment(sketch, "E5455", {"start": v(17.9, -45.32) * mm, "end": v(17.9, -45.26) * mm});
            skLineSegment(sketch, "E5456", {"start": v(17.9, -45.26) * mm, "end": v(17.89, -45.2) * mm});
            skLineSegment(sketch, "E5457", {"start": v(17.89, -45.2) * mm, "end": v(17.88, -45.16) * mm});
            skLineSegment(sketch, "E5458", {"start": v(17.88, -45.16) * mm, "end": v(18.14, -45.05) * mm});
            skLineSegment(sketch, "E5459", {"start": v(18.14, -45.05) * mm, "end": v(18.58, -44.87) * mm});
            skLineSegment(sketch, "E5460", {"start": v(18.58, -44.87) * mm, "end": v(18.84, -44.76) * mm});
            skLineSegment(sketch, "E5461", {"start": v(18.84, -44.76) * mm, "end": v(18.88, -44.8) * mm});
            skLineSegment(sketch, "E5462", {"start": v(18.88, -44.8) * mm, "end": v(18.91, -44.85) * mm});
            skLineSegment(sketch, "E5463", {"start": v(18.91, -44.85) * mm, "end": v(18.95, -44.9) * mm});
            skLineSegment(sketch, "E5464", {"start": v(18.95, -44.9) * mm, "end": v(18.98, -44.94) * mm});
            skLineSegment(sketch, "E5465", {"start": v(18.98, -44.94) * mm, "end": v(19.02, -44.98) * mm});
            skLineSegment(sketch, "E5466", {"start": v(19.02, -44.98) * mm, "end": v(19.05, -45.03) * mm});
            skLineSegment(sketch, "E5467", {"start": v(19.05, -45.03) * mm, "end": v(19.1, -45.08) * mm});
            skLineSegment(sketch, "E5468", {"start": v(19.1, -45.08) * mm, "end": v(19.13, -45.12) * mm});
            skLineSegment(sketch, "E5469", {"start": v(19.13, -45.12) * mm, "end": v(19.17, -45.17) * mm});
            skLineSegment(sketch, "E5470", {"start": v(19.17, -45.17) * mm, "end": v(19.2, -45.22) * mm});
            skLineSegment(sketch, "E5471", {"start": v(19.2, -45.22) * mm, "end": v(19.25, -45.27) * mm});
            skLineSegment(sketch, "E5472", {"start": v(19.25, -45.27) * mm, "end": v(19.3, -45.31) * mm});
            skLineSegment(sketch, "E5473", {"start": v(19.3, -45.31) * mm, "end": v(19.33, -45.36) * mm});
            skLineSegment(sketch, "E5474", {"start": v(19.33, -45.36) * mm, "end": v(19.38, -45.41) * mm});
            skLineSegment(sketch, "E5475", {"start": v(19.38, -45.41) * mm, "end": v(19.42, -45.46) * mm});
            skLineSegment(sketch, "E5476", {"start": v(19.42, -45.46) * mm, "end": v(19.46, -45.51) * mm});
            skLineSegment(sketch, "E5477", {"start": v(19.46, -45.51) * mm, "end": v(19.5, -45.56) * mm});
            skLineSegment(sketch, "E5478", {"start": v(19.5, -45.56) * mm, "end": v(19.56, -45.62) * mm});
            skLineSegment(sketch, "E5479", {"start": v(19.56, -45.62) * mm, "end": v(19.6, -45.67) * mm});
            skLineSegment(sketch, "E5480", {"start": v(19.6, -45.67) * mm, "end": v(19.65, -45.72) * mm});
            skLineSegment(sketch, "E5481", {"start": v(19.65, -45.72) * mm, "end": v(19.7, -45.77) * mm});
            skLineSegment(sketch, "E5482", {"start": v(19.7, -45.77) * mm, "end": v(19.75, -45.83) * mm});
            skLineSegment(sketch, "E5483", {"start": v(19.75, -45.83) * mm, "end": v(19.8, -45.88) * mm});
            skLineSegment(sketch, "E5484", {"start": v(19.8, -45.88) * mm, "end": v(19.85, -45.94) * mm});
            skLineSegment(sketch, "E5485", {"start": v(19.85, -45.94) * mm, "end": v(19.9, -46) * mm});
            skLineSegment(sketch, "E5486", {"start": v(19.9, -46) * mm, "end": v(19.96, -46.05) * mm});
            skLineSegment(sketch, "E5487", {"start": v(19.96, -46.05) * mm, "end": v(20, -46.1) * mm});
            skLineSegment(sketch, "E5488", {"start": v(20, -46.1) * mm, "end": v(20.06, -46.16) * mm});
            skLineSegment(sketch, "E5489", {"start": v(20.06, -46.16) * mm, "end": v(20.12, -46.21) * mm});
            skLineSegment(sketch, "E5490", {"start": v(20.12, -46.21) * mm, "end": v(20.18, -46.27) * mm});
            skLineSegment(sketch, "E5491", {"start": v(20.18, -46.27) * mm, "end": v(20.23, -46.33) * mm});
            skLineSegment(sketch, "E5492", {"start": v(20.23, -46.33) * mm, "end": v(20.3, -46.38) * mm});
            skLineSegment(sketch, "E5493", {"start": v(20.3, -46.38) * mm, "end": v(20.35, -46.44) * mm});
            skLineSegment(sketch, "E5494", {"start": v(20.35, -46.44) * mm, "end": v(20.41, -46.5) * mm});
            skLineSegment(sketch, "E5495", {"start": v(20.41, -46.5) * mm, "end": v(20.47, -46.56) * mm});
            skLineSegment(sketch, "E5496", {"start": v(20.47, -46.56) * mm, "end": v(20.53, -46.62) * mm});
            skLineSegment(sketch, "E5497", {"start": v(20.53, -46.62) * mm, "end": v(20.6, -46.68) * mm});
            skLineSegment(sketch, "E5498", {"start": v(20.6, -46.68) * mm, "end": v(20.66, -46.74) * mm});
            skLineSegment(sketch, "E5499", {"start": v(20.66, -46.74) * mm, "end": v(20.73, -46.8) * mm});
            skLineSegment(sketch, "E5500", {"start": v(20.73, -46.8) * mm, "end": v(20.79, -46.85) * mm});
            skLineSegment(sketch, "E5501", {"start": v(20.79, -46.85) * mm, "end": v(21.66, -46.45) * mm});
            skLineSegment(sketch, "E5502", {"start": v(21.66, -46.45) * mm, "end": v(21.67, -46.37) * mm});
            skLineSegment(sketch, "E5503", {"start": v(21.67, -46.37) * mm, "end": v(21.66, -46.28) * mm});
            skLineSegment(sketch, "E5504", {"start": v(21.66, -46.28) * mm, "end": v(21.66, -46.2) * mm});
            skLineSegment(sketch, "E5505", {"start": v(21.66, -46.2) * mm, "end": v(21.66, -46.1) * mm});
            skLineSegment(sketch, "E5506", {"start": v(21.66, -46.1) * mm, "end": v(21.65, -46.02) * mm});
            skLineSegment(sketch, "E5507", {"start": v(21.65, -46.02) * mm, "end": v(21.65, -45.94) * mm});
            skLineSegment(sketch, "E5508", {"start": v(21.65, -45.94) * mm, "end": v(21.65, -45.85) * mm});
            skLineSegment(sketch, "E5509", {"start": v(21.65, -45.85) * mm, "end": v(21.64, -45.77) * mm});
            skLineSegment(sketch, "E5510", {"start": v(21.64, -45.77) * mm, "end": v(21.64, -45.69) * mm});
            skLineSegment(sketch, "E5511", {"start": v(21.64, -45.69) * mm, "end": v(21.63, -45.6) * mm});
            skLineSegment(sketch, "E5512", {"start": v(21.63, -45.6) * mm, "end": v(21.62, -45.53) * mm});
            skLineSegment(sketch, "E5513", {"start": v(21.62, -45.53) * mm, "end": v(21.62, -45.45) * mm});
            skLineSegment(sketch, "E5514", {"start": v(21.62, -45.45) * mm, "end": v(21.61, -45.37) * mm});
            skLineSegment(sketch, "E5515", {"start": v(21.61, -45.37) * mm, "end": v(21.6, -45.3) * mm});
            skLineSegment(sketch, "E5516", {"start": v(21.6, -45.3) * mm, "end": v(21.6, -45.22) * mm});
            skLineSegment(sketch, "E5517", {"start": v(21.6, -45.22) * mm, "end": v(21.6, -45.14) * mm});
            skLineSegment(sketch, "E5518", {"start": v(21.6, -45.14) * mm, "end": v(21.59, -45.07) * mm});
            skLineSegment(sketch, "E5519", {"start": v(21.59, -45.07) * mm, "end": v(21.58, -45) * mm});
            skLineSegment(sketch, "E5520", {"start": v(21.58, -45) * mm, "end": v(21.57, -44.92) * mm});
            skLineSegment(sketch, "E5521", {"start": v(21.57, -44.92) * mm, "end": v(21.56, -44.85) * mm});
            skLineSegment(sketch, "E5522", {"start": v(21.56, -44.85) * mm, "end": v(21.55, -44.78) * mm});
            skLineSegment(sketch, "E5523", {"start": v(21.55, -44.78) * mm, "end": v(21.55, -44.71) * mm});
            skLineSegment(sketch, "E5524", {"start": v(21.55, -44.71) * mm, "end": v(21.54, -44.64) * mm});
            skLineSegment(sketch, "E5525", {"start": v(21.54, -44.64) * mm, "end": v(21.53, -44.57) * mm});
            skLineSegment(sketch, "E5526", {"start": v(21.53, -44.57) * mm, "end": v(21.52, -44.5) * mm});
            skLineSegment(sketch, "E5527", {"start": v(21.52, -44.5) * mm, "end": v(21.51, -44.44) * mm});
            skLineSegment(sketch, "E5528", {"start": v(21.51, -44.44) * mm, "end": v(21.5, -44.38) * mm});
            skLineSegment(sketch, "E5529", {"start": v(21.5, -44.38) * mm, "end": v(21.5, -44.31) * mm});
            skLineSegment(sketch, "E5530", {"start": v(21.5, -44.31) * mm, "end": v(21.48, -44.25) * mm});
            skLineSegment(sketch, "E5531", {"start": v(21.48, -44.25) * mm, "end": v(21.47, -44.19) * mm});
            skLineSegment(sketch, "E5532", {"start": v(21.47, -44.19) * mm, "end": v(21.46, -44.12) * mm});
            skLineSegment(sketch, "E5533", {"start": v(21.46, -44.12) * mm, "end": v(21.45, -44.06) * mm});
            skLineSegment(sketch, "E5534", {"start": v(21.45, -44.06) * mm, "end": v(21.44, -44) * mm});
            skLineSegment(sketch, "E5535", {"start": v(21.44, -44) * mm, "end": v(21.43, -43.95) * mm});
            skLineSegment(sketch, "E5536", {"start": v(21.43, -43.95) * mm, "end": v(21.42, -43.89) * mm});
            skLineSegment(sketch, "E5537", {"start": v(21.42, -43.89) * mm, "end": v(21.41, -43.83) * mm});
            skLineSegment(sketch, "E5538", {"start": v(21.41, -43.83) * mm, "end": v(21.4, -43.78) * mm});
            skLineSegment(sketch, "E5539", {"start": v(21.4, -43.78) * mm, "end": v(21.4, -43.72) * mm});
            skLineSegment(sketch, "E5540", {"start": v(21.4, -43.72) * mm, "end": v(21.38, -43.67) * mm});
            skLineSegment(sketch, "E5541", {"start": v(21.38, -43.67) * mm, "end": v(21.37, -43.61) * mm});
            skLineSegment(sketch, "E5542", {"start": v(21.37, -43.61) * mm, "end": v(21.62, -43.49) * mm});
            skLineSegment(sketch, "E5543", {"start": v(21.62, -43.49) * mm, "end": v(22.05, -43.27) * mm});
            skLineSegment(sketch, "E5544", {"start": v(22.05, -43.27) * mm, "end": v(22.3, -43.15) * mm});
            skLineSegment(sketch, "E5545", {"start": v(22.3, -43.15) * mm, "end": v(22.33, -43.19) * mm});
            skLineSegment(sketch, "E5546", {"start": v(22.33, -43.19) * mm, "end": v(22.37, -43.23) * mm});
            skLineSegment(sketch, "E5547", {"start": v(22.37, -43.23) * mm, "end": v(22.4, -43.27) * mm});
            skLineSegment(sketch, "E5548", {"start": v(22.4, -43.27) * mm, "end": v(22.45, -43.31) * mm});
            skLineSegment(sketch, "E5549", {"start": v(22.45, -43.31) * mm, "end": v(22.49, -43.35) * mm});
            skLineSegment(sketch, "E5550", {"start": v(22.49, -43.35) * mm, "end": v(22.53, -43.4) * mm});
            skLineSegment(sketch, "E5551", {"start": v(22.53, -43.4) * mm, "end": v(22.57, -43.44) * mm});
            skLineSegment(sketch, "E5552", {"start": v(22.57, -43.44) * mm, "end": v(22.61, -43.48) * mm});
            skLineSegment(sketch, "E5553", {"start": v(22.61, -43.48) * mm, "end": v(22.65, -43.53) * mm});
            skLineSegment(sketch, "E5554", {"start": v(22.65, -43.53) * mm, "end": v(22.7, -43.57) * mm});
            skLineSegment(sketch, "E5555", {"start": v(22.7, -43.57) * mm, "end": v(22.74, -43.62) * mm});
            skLineSegment(sketch, "E5556", {"start": v(22.74, -43.62) * mm, "end": v(22.79, -43.66) * mm});
            skLineSegment(sketch, "E5557", {"start": v(22.79, -43.66) * mm, "end": v(22.83, -43.7) * mm});
            skLineSegment(sketch, "E5558", {"start": v(22.83, -43.7) * mm, "end": v(22.88, -43.75) * mm});
            skLineSegment(sketch, "E5559", {"start": v(22.88, -43.75) * mm, "end": v(22.93, -43.8) * mm});
            skLineSegment(sketch, "E5560", {"start": v(22.93, -43.8) * mm, "end": v(22.97, -43.85) * mm});
            skLineSegment(sketch, "E5561", {"start": v(22.97, -43.85) * mm, "end": v(23.02, -43.9) * mm});
            skLineSegment(sketch, "E5562", {"start": v(23.02, -43.9) * mm, "end": v(23.07, -43.94) * mm});
            skLineSegment(sketch, "E5563", {"start": v(23.07, -43.94) * mm, "end": v(23.13, -43.99) * mm});
            skLineSegment(sketch, "E5564", {"start": v(23.13, -43.99) * mm, "end": v(23.18, -44.04) * mm});
            skLineSegment(sketch, "E5565", {"start": v(23.18, -44.04) * mm, "end": v(23.23, -44.09) * mm});
            skLineSegment(sketch, "E5566", {"start": v(23.23, -44.09) * mm, "end": v(23.28, -44.14) * mm});
            skLineSegment(sketch, "E5567", {"start": v(23.28, -44.14) * mm, "end": v(23.34, -44.19) * mm});
            skLineSegment(sketch, "E5568", {"start": v(23.34, -44.19) * mm, "end": v(23.4, -44.24) * mm});
            skLineSegment(sketch, "E5569", {"start": v(23.4, -44.24) * mm, "end": v(23.45, -44.29) * mm});
            skLineSegment(sketch, "E5570", {"start": v(23.45, -44.29) * mm, "end": v(23.5, -44.34) * mm});
            skLineSegment(sketch, "E5571", {"start": v(23.5, -44.34) * mm, "end": v(23.56, -44.39) * mm});
            skLineSegment(sketch, "E5572", {"start": v(23.56, -44.39) * mm, "end": v(23.62, -44.44) * mm});
            skLineSegment(sketch, "E5573", {"start": v(23.62, -44.44) * mm, "end": v(23.68, -44.5) * mm});
            skLineSegment(sketch, "E5574", {"start": v(23.68, -44.5) * mm, "end": v(23.74, -44.54) * mm});
            skLineSegment(sketch, "E5575", {"start": v(23.74, -44.54) * mm, "end": v(23.8, -44.6) * mm});
            skLineSegment(sketch, "E5576", {"start": v(23.8, -44.6) * mm, "end": v(23.87, -44.65) * mm});
            skLineSegment(sketch, "E5577", {"start": v(23.87, -44.65) * mm, "end": v(23.93, -44.7) * mm});
            skLineSegment(sketch, "E5578", {"start": v(23.93, -44.7) * mm, "end": v(24, -44.76) * mm});
            skLineSegment(sketch, "E5579", {"start": v(24, -44.76) * mm, "end": v(24.06, -44.8) * mm});
            skLineSegment(sketch, "E5580", {"start": v(24.06, -44.8) * mm, "end": v(24.13, -44.86) * mm});
            skLineSegment(sketch, "E5581", {"start": v(24.13, -44.86) * mm, "end": v(24.2, -44.92) * mm});
            skLineSegment(sketch, "E5582", {"start": v(24.2, -44.92) * mm, "end": v(24.26, -44.97) * mm});
            skLineSegment(sketch, "E5583", {"start": v(24.26, -44.97) * mm, "end": v(24.33, -45.03) * mm});
            skLineSegment(sketch, "E5584", {"start": v(24.33, -45.03) * mm, "end": v(24.4, -45.07) * mm});
            skLineSegment(sketch, "E5585", {"start": v(24.4, -45.07) * mm, "end": v(25.24, -44.6) * mm});
            skLineSegment(sketch, "E5586", {"start": v(25.24, -44.6) * mm, "end": v(25.24, -44.53) * mm});
            skLineSegment(sketch, "E5587", {"start": v(25.24, -44.53) * mm, "end": v(25.23, -44.44) * mm});
            skLineSegment(sketch, "E5588", {"start": v(25.23, -44.44) * mm, "end": v(25.22, -44.35) * mm});
            skLineSegment(sketch, "E5589", {"start": v(25.22, -44.35) * mm, "end": v(25.2, -44.27) * mm});
            skLineSegment(sketch, "E5590", {"start": v(25.2, -44.27) * mm, "end": v(25.2, -44.18) * mm});
            skLineSegment(sketch, "E5591", {"start": v(25.2, -44.18) * mm, "end": v(25.19, -44.1) * mm});
            skLineSegment(sketch, "E5592", {"start": v(25.19, -44.1) * mm, "end": v(25.18, -44.01) * mm});
            skLineSegment(sketch, "E5593", {"start": v(25.18, -44.01) * mm, "end": v(25.17, -43.93) * mm});
            skLineSegment(sketch, "E5594", {"start": v(25.17, -43.93) * mm, "end": v(25.15, -43.85) * mm});
            skLineSegment(sketch, "E5595", {"start": v(25.15, -43.85) * mm, "end": v(25.14, -43.77) * mm});
            skLineSegment(sketch, "E5596", {"start": v(25.14, -43.77) * mm, "end": v(25.13, -43.7) * mm});
            skLineSegment(sketch, "E5597", {"start": v(25.13, -43.7) * mm, "end": v(25.12, -43.61) * mm});
            skLineSegment(sketch, "E5598", {"start": v(25.12, -43.61) * mm, "end": v(25.1, -43.54) * mm});
            skLineSegment(sketch, "E5599", {"start": v(25.1, -43.54) * mm, "end": v(25.1, -43.46) * mm});
            skLineSegment(sketch, "E5600", {"start": v(25.1, -43.46) * mm, "end": v(25.08, -43.38) * mm});
            skLineSegment(sketch, "E5601", {"start": v(25.08, -43.38) * mm, "end": v(25.07, -43.3) * mm});
            skLineSegment(sketch, "E5602", {"start": v(25.07, -43.3) * mm, "end": v(25.05, -43.24) * mm});
            skLineSegment(sketch, "E5603", {"start": v(25.05, -43.24) * mm, "end": v(25.04, -43.16) * mm});
            skLineSegment(sketch, "E5604", {"start": v(25.04, -43.16) * mm, "end": v(25.03, -43.1) * mm});
            skLineSegment(sketch, "E5605", {"start": v(25.03, -43.1) * mm, "end": v(25.01, -43.02) * mm});
            skLineSegment(sketch, "E5606", {"start": v(25.01, -43.02) * mm, "end": v(25, -42.95) * mm});
            skLineSegment(sketch, "E5607", {"start": v(25, -42.95) * mm, "end": v(24.99, -42.88) * mm});
            skLineSegment(sketch, "E5608", {"start": v(24.99, -42.88) * mm, "end": v(24.97, -42.81) * mm});
            skLineSegment(sketch, "E5609", {"start": v(24.97, -42.81) * mm, "end": v(24.96, -42.75) * mm});
            skLineSegment(sketch, "E5610", {"start": v(24.96, -42.75) * mm, "end": v(24.95, -42.68) * mm});
            skLineSegment(sketch, "E5611", {"start": v(24.95, -42.68) * mm, "end": v(24.93, -42.62) * mm});
            skLineSegment(sketch, "E5612", {"start": v(24.93, -42.62) * mm, "end": v(24.92, -42.55) * mm});
            skLineSegment(sketch, "E5613", {"start": v(24.92, -42.55) * mm, "end": v(24.9, -42.49) * mm});
            skLineSegment(sketch, "E5614", {"start": v(24.9, -42.49) * mm, "end": v(24.89, -42.43) * mm});
            skLineSegment(sketch, "E5615", {"start": v(24.89, -42.43) * mm, "end": v(24.87, -42.37) * mm});
            skLineSegment(sketch, "E5616", {"start": v(24.87, -42.37) * mm, "end": v(24.86, -42.3) * mm});
            skLineSegment(sketch, "E5617", {"start": v(24.86, -42.3) * mm, "end": v(24.84, -42.25) * mm});
            skLineSegment(sketch, "E5618", {"start": v(24.84, -42.25) * mm, "end": v(24.83, -42.19) * mm});
            skLineSegment(sketch, "E5619", {"start": v(24.83, -42.19) * mm, "end": v(24.81, -42.13) * mm});
            skLineSegment(sketch, "E5620", {"start": v(24.81, -42.13) * mm, "end": v(24.8, -42.07) * mm});
            skLineSegment(sketch, "E5621", {"start": v(24.8, -42.07) * mm, "end": v(24.79, -42.02) * mm});
            skLineSegment(sketch, "E5622", {"start": v(24.79, -42.02) * mm, "end": v(24.77, -41.96) * mm});
            skLineSegment(sketch, "E5623", {"start": v(24.77, -41.96) * mm, "end": v(24.76, -41.9) * mm});
            skLineSegment(sketch, "E5624", {"start": v(24.76, -41.9) * mm, "end": v(24.74, -41.85) * mm});
            skLineSegment(sketch, "E5625", {"start": v(24.74, -41.85) * mm, "end": v(24.73, -41.8) * mm});
            skLineSegment(sketch, "E5626", {"start": v(24.73, -41.8) * mm, "end": v(24.96, -41.66) * mm});
            skLineSegment(sketch, "E5627", {"start": v(24.96, -41.66) * mm, "end": v(25.37, -41.4) * mm});
            skLineSegment(sketch, "E5628", {"start": v(25.37, -41.4) * mm, "end": v(25.61, -41.26) * mm});
            skLineSegment(sketch, "E5629", {"start": v(25.61, -41.26) * mm, "end": v(25.65, -41.3) * mm});
            skLineSegment(sketch, "E5630", {"start": v(25.65, -41.3) * mm, "end": v(25.7, -41.34) * mm});
            skLineSegment(sketch, "E5631", {"start": v(25.7, -41.34) * mm, "end": v(25.73, -41.38) * mm});
            skLineSegment(sketch, "E5632", {"start": v(25.73, -41.38) * mm, "end": v(25.78, -41.42) * mm});
            skLineSegment(sketch, "E5633", {"start": v(25.78, -41.42) * mm, "end": v(25.82, -41.45) * mm});
            skLineSegment(sketch, "E5634", {"start": v(25.82, -41.45) * mm, "end": v(25.86, -41.5) * mm});
            skLineSegment(sketch, "E5635", {"start": v(25.86, -41.5) * mm, "end": v(25.9, -41.53) * mm});
            skLineSegment(sketch, "E5636", {"start": v(25.9, -41.53) * mm, "end": v(25.95, -41.57) * mm});
            skLineSegment(sketch, "E5637", {"start": v(25.95, -41.57) * mm, "end": v(26, -41.61) * mm});
            skLineSegment(sketch, "E5638", {"start": v(26, -41.61) * mm, "end": v(26.04, -41.66) * mm});
            skLineSegment(sketch, "E5639", {"start": v(26.04, -41.66) * mm, "end": v(26.1, -41.7) * mm});
            skLineSegment(sketch, "E5640", {"start": v(26.1, -41.7) * mm, "end": v(26.14, -41.74) * mm});
            skLineSegment(sketch, "E5641", {"start": v(26.14, -41.74) * mm, "end": v(26.2, -41.78) * mm});
            skLineSegment(sketch, "E5642", {"start": v(26.2, -41.78) * mm, "end": v(26.24, -41.82) * mm});
            skLineSegment(sketch, "E5643", {"start": v(26.24, -41.82) * mm, "end": v(26.3, -41.87) * mm});
            skLineSegment(sketch, "E5644", {"start": v(26.3, -41.87) * mm, "end": v(26.34, -41.9) * mm});
            skLineSegment(sketch, "E5645", {"start": v(26.34, -41.9) * mm, "end": v(26.4, -41.95) * mm});
            skLineSegment(sketch, "E5646", {"start": v(26.4, -41.95) * mm, "end": v(26.45, -42) * mm});
            skLineSegment(sketch, "E5647", {"start": v(26.45, -42) * mm, "end": v(26.5, -42.04) * mm});
            skLineSegment(sketch, "E5648", {"start": v(26.5, -42.04) * mm, "end": v(26.56, -42.08) * mm});
            skLineSegment(sketch, "E5649", {"start": v(26.56, -42.08) * mm, "end": v(26.62, -42.13) * mm});
            skLineSegment(sketch, "E5650", {"start": v(26.62, -42.13) * mm, "end": v(26.67, -42.17) * mm});
            skLineSegment(sketch, "E5651", {"start": v(26.67, -42.17) * mm, "end": v(26.73, -42.22) * mm});
            skLineSegment(sketch, "E5652", {"start": v(26.73, -42.22) * mm, "end": v(26.8, -42.26) * mm});
            skLineSegment(sketch, "E5653", {"start": v(26.8, -42.26) * mm, "end": v(26.85, -42.31) * mm});
            skLineSegment(sketch, "E5654", {"start": v(26.85, -42.31) * mm, "end": v(26.91, -42.36) * mm});
            skLineSegment(sketch, "E5655", {"start": v(26.91, -42.36) * mm, "end": v(26.98, -42.4) * mm});
            skLineSegment(sketch, "E5656", {"start": v(26.98, -42.4) * mm, "end": v(27.04, -42.45) * mm});
            skLineSegment(sketch, "E5657", {"start": v(27.04, -42.45) * mm, "end": v(27.1, -42.5) * mm});
            skLineSegment(sketch, "E5658", {"start": v(27.1, -42.5) * mm, "end": v(27.17, -42.54) * mm});
            skLineSegment(sketch, "E5659", {"start": v(27.17, -42.54) * mm, "end": v(27.23, -42.6) * mm});
            skLineSegment(sketch, "E5660", {"start": v(27.23, -42.6) * mm, "end": v(27.3, -42.64) * mm});
            skLineSegment(sketch, "E5661", {"start": v(27.3, -42.64) * mm, "end": v(27.37, -42.69) * mm});
            skLineSegment(sketch, "E5662", {"start": v(27.37, -42.69) * mm, "end": v(27.43, -42.74) * mm});
            skLineSegment(sketch, "E5663", {"start": v(27.43, -42.74) * mm, "end": v(27.5, -42.78) * mm});
            skLineSegment(sketch, "E5664", {"start": v(27.5, -42.78) * mm, "end": v(27.57, -42.83) * mm});
            skLineSegment(sketch, "E5665", {"start": v(27.57, -42.83) * mm, "end": v(27.65, -42.88) * mm});
            skLineSegment(sketch, "E5666", {"start": v(27.65, -42.88) * mm, "end": v(27.72, -42.93) * mm});
            skLineSegment(sketch, "E5667", {"start": v(27.72, -42.93) * mm, "end": v(27.8, -42.98) * mm});
            skLineSegment(sketch, "E5668", {"start": v(27.8, -42.98) * mm, "end": v(27.86, -43.02) * mm});
            skLineSegment(sketch, "E5669", {"start": v(27.86, -43.02) * mm, "end": v(28.66, -42.48) * mm});
            skLineSegment(sketch, "E5670", {"start": v(28.66, -42.48) * mm, "end": v(28.65, -42.4) * mm});
            skLineSegment(sketch, "E5671", {"start": v(28.65, -42.4) * mm, "end": v(28.64, -42.32) * mm});
            skLineSegment(sketch, "E5672", {"start": v(28.64, -42.32) * mm, "end": v(28.62, -42.24) * mm});
            skLineSegment(sketch, "E5673", {"start": v(28.62, -42.24) * mm, "end": v(28.6, -42.15) * mm});
            skLineSegment(sketch, "E5674", {"start": v(28.6, -42.15) * mm, "end": v(28.59, -42.07) * mm});
            skLineSegment(sketch, "E5675", {"start": v(28.59, -42.07) * mm, "end": v(28.57, -41.98) * mm});
            skLineSegment(sketch, "E5676", {"start": v(28.57, -41.98) * mm, "end": v(28.55, -41.9) * mm});
            skLineSegment(sketch, "E5677", {"start": v(28.55, -41.9) * mm, "end": v(28.53, -41.82) * mm});
            skLineSegment(sketch, "E5678", {"start": v(28.53, -41.82) * mm, "end": v(28.52, -41.74) * mm});
            skLineSegment(sketch, "E5679", {"start": v(28.52, -41.74) * mm, "end": v(28.5, -41.66) * mm});
            skLineSegment(sketch, "E5680", {"start": v(28.5, -41.66) * mm, "end": v(28.48, -41.58) * mm});
            skLineSegment(sketch, "E5681", {"start": v(28.48, -41.58) * mm, "end": v(28.46, -41.5) * mm});
            skLineSegment(sketch, "E5682", {"start": v(28.46, -41.5) * mm, "end": v(28.44, -41.43) * mm});
            skLineSegment(sketch, "E5683", {"start": v(28.44, -41.43) * mm, "end": v(28.43, -41.36) * mm});
            skLineSegment(sketch, "E5684", {"start": v(28.43, -41.36) * mm, "end": v(28.4, -41.28) * mm});
            skLineSegment(sketch, "E5685", {"start": v(28.4, -41.28) * mm, "end": v(28.39, -41.2) * mm});
            skLineSegment(sketch, "E5686", {"start": v(28.39, -41.2) * mm, "end": v(28.37, -41.14) * mm});
            skLineSegment(sketch, "E5687", {"start": v(28.37, -41.14) * mm, "end": v(28.35, -41.07) * mm});
            skLineSegment(sketch, "E5688", {"start": v(28.35, -41.07) * mm, "end": v(28.33, -41) * mm});
            skLineSegment(sketch, "E5689", {"start": v(28.33, -41) * mm, "end": v(28.31, -40.93) * mm});
            skLineSegment(sketch, "E5690", {"start": v(28.31, -40.93) * mm, "end": v(28.3, -40.86) * mm});
            skLineSegment(sketch, "E5691", {"start": v(28.3, -40.86) * mm, "end": v(28.27, -40.79) * mm});
            skLineSegment(sketch, "E5692", {"start": v(28.27, -40.79) * mm, "end": v(28.26, -40.72) * mm});
            skLineSegment(sketch, "E5693", {"start": v(28.26, -40.72) * mm, "end": v(28.24, -40.66) * mm});
            skLineSegment(sketch, "E5694", {"start": v(28.24, -40.66) * mm, "end": v(28.22, -40.6) * mm});
            skLineSegment(sketch, "E5695", {"start": v(28.22, -40.6) * mm, "end": v(28.2, -40.53) * mm});
            skLineSegment(sketch, "E5696", {"start": v(28.2, -40.53) * mm, "end": v(28.18, -40.47) * mm});
            skLineSegment(sketch, "E5697", {"start": v(28.18, -40.47) * mm, "end": v(28.16, -40.4) * mm});
            skLineSegment(sketch, "E5698", {"start": v(28.16, -40.4) * mm, "end": v(28.14, -40.34) * mm});
            skLineSegment(sketch, "E5699", {"start": v(28.14, -40.34) * mm, "end": v(28.12, -40.28) * mm});
            skLineSegment(sketch, "E5700", {"start": v(28.12, -40.28) * mm, "end": v(28.1, -40.22) * mm});
            skLineSegment(sketch, "E5701", {"start": v(28.1, -40.22) * mm, "end": v(28.08, -40.17) * mm});
            skLineSegment(sketch, "E5702", {"start": v(28.08, -40.17) * mm, "end": v(28.06, -40.1) * mm});
            skLineSegment(sketch, "E5703", {"start": v(28.06, -40.1) * mm, "end": v(28.04, -40.05) * mm});
            skLineSegment(sketch, "E5704", {"start": v(28.04, -40.05) * mm, "end": v(28.02, -40) * mm});
            skLineSegment(sketch, "E5705", {"start": v(28.02, -40) * mm, "end": v(28, -39.94) * mm});
            skLineSegment(sketch, "E5706", {"start": v(28, -39.94) * mm, "end": v(27.99, -39.89) * mm});
            skLineSegment(sketch, "E5707", {"start": v(27.99, -39.89) * mm, "end": v(27.97, -39.84) * mm});
            skLineSegment(sketch, "E5708", {"start": v(27.97, -39.84) * mm, "end": v(27.95, -39.78) * mm});
            skLineSegment(sketch, "E5709", {"start": v(27.95, -39.78) * mm, "end": v(27.93, -39.73) * mm});
            skLineSegment(sketch, "E5710", {"start": v(27.93, -39.73) * mm, "end": v(28.15, -39.57) * mm});
            skLineSegment(sketch, "E5711", {"start": v(28.15, -39.57) * mm, "end": v(28.54, -39.29) * mm});
            skLineSegment(sketch, "E5712", {"start": v(28.54, -39.29) * mm, "end": v(28.77, -39.13) * mm});
            skLineSegment(sketch, "E5713", {"start": v(28.77, -39.13) * mm, "end": v(28.82, -39.16) * mm});
            skLineSegment(sketch, "E5714", {"start": v(28.82, -39.16) * mm, "end": v(28.86, -39.2) * mm});
            skLineSegment(sketch, "E5715", {"start": v(28.86, -39.2) * mm, "end": v(28.9, -39.23) * mm});
            skLineSegment(sketch, "E5716", {"start": v(28.9, -39.23) * mm, "end": v(28.95, -39.27) * mm});
            skLineSegment(sketch, "E5717", {"start": v(28.95, -39.27) * mm, "end": v(29, -39.3) * mm});
            skLineSegment(sketch, "E5718", {"start": v(29, -39.3) * mm, "end": v(29.04, -39.34) * mm});
            skLineSegment(sketch, "E5719", {"start": v(29.04, -39.34) * mm, "end": v(29.09, -39.37) * mm});
            skLineSegment(sketch, "E5720", {"start": v(29.09, -39.37) * mm, "end": v(29.13, -39.4) * mm});
            skLineSegment(sketch, "E5721", {"start": v(29.13, -39.4) * mm, "end": v(29.18, -39.45) * mm});
            skLineSegment(sketch, "E5722", {"start": v(29.18, -39.45) * mm, "end": v(29.23, -39.48) * mm});
            skLineSegment(sketch, "E5723", {"start": v(29.23, -39.48) * mm, "end": v(29.28, -39.52) * mm});
            skLineSegment(sketch, "E5724", {"start": v(29.28, -39.52) * mm, "end": v(29.34, -39.56) * mm});
            skLineSegment(sketch, "E5725", {"start": v(29.34, -39.56) * mm, "end": v(29.39, -39.6) * mm});
            skLineSegment(sketch, "E5726", {"start": v(29.39, -39.6) * mm, "end": v(29.44, -39.63) * mm});
            skLineSegment(sketch, "E5727", {"start": v(29.44, -39.63) * mm, "end": v(29.5, -39.67) * mm});
            skLineSegment(sketch, "E5728", {"start": v(29.5, -39.67) * mm, "end": v(29.55, -39.71) * mm});
            skLineSegment(sketch, "E5729", {"start": v(29.55, -39.71) * mm, "end": v(29.6, -39.75) * mm});
            skLineSegment(sketch, "E5730", {"start": v(29.6, -39.75) * mm, "end": v(29.66, -39.8) * mm});
            skLineSegment(sketch, "E5731", {"start": v(29.66, -39.8) * mm, "end": v(29.72, -39.83) * mm});
            skLineSegment(sketch, "E5732", {"start": v(29.72, -39.83) * mm, "end": v(29.78, -39.87) * mm});
            skLineSegment(sketch, "E5733", {"start": v(29.78, -39.87) * mm, "end": v(29.84, -39.91) * mm});
            skLineSegment(sketch, "E5734", {"start": v(29.84, -39.91) * mm, "end": v(29.9, -39.95) * mm});
            skLineSegment(sketch, "E5735", {"start": v(29.9, -39.95) * mm, "end": v(29.96, -40) * mm});
            skLineSegment(sketch, "E5736", {"start": v(29.96, -40) * mm, "end": v(30.03, -40.03) * mm});
            skLineSegment(sketch, "E5737", {"start": v(30.03, -40.03) * mm, "end": v(30.09, -40.07) * mm});
            skLineSegment(sketch, "E5738", {"start": v(30.09, -40.07) * mm, "end": v(30.15, -40.11) * mm});
            skLineSegment(sketch, "E5739", {"start": v(30.15, -40.11) * mm, "end": v(30.22, -40.16) * mm});
            skLineSegment(sketch, "E5740", {"start": v(30.22, -40.16) * mm, "end": v(30.29, -40.2) * mm});
            skLineSegment(sketch, "E5741", {"start": v(30.29, -40.2) * mm, "end": v(30.35, -40.24) * mm});
            skLineSegment(sketch, "E5742", {"start": v(30.35, -40.24) * mm, "end": v(30.42, -40.28) * mm});
            skLineSegment(sketch, "E5743", {"start": v(30.42, -40.28) * mm, "end": v(30.49, -40.32) * mm});
            skLineSegment(sketch, "E5744", {"start": v(30.49, -40.32) * mm, "end": v(30.56, -40.37) * mm});
            skLineSegment(sketch, "E5745", {"start": v(30.56, -40.37) * mm, "end": v(30.63, -40.4) * mm});
            skLineSegment(sketch, "E5746", {"start": v(30.63, -40.4) * mm, "end": v(30.7, -40.45) * mm});
            skLineSegment(sketch, "E5747", {"start": v(30.7, -40.45) * mm, "end": v(30.78, -40.5) * mm});
            skLineSegment(sketch, "E5748", {"start": v(30.78, -40.5) * mm, "end": v(30.85, -40.54) * mm});
            skLineSegment(sketch, "E5749", {"start": v(30.85, -40.54) * mm, "end": v(30.92, -40.58) * mm});
            skLineSegment(sketch, "E5750", {"start": v(30.92, -40.58) * mm, "end": v(31, -40.62) * mm});
            skLineSegment(sketch, "E5751", {"start": v(31, -40.62) * mm, "end": v(31.08, -40.67) * mm});
            skLineSegment(sketch, "E5752", {"start": v(31.08, -40.67) * mm, "end": v(31.15, -40.7) * mm});
            skLineSegment(sketch, "E5753", {"start": v(31.15, -40.7) * mm, "end": v(31.9, -40.1) * mm});
            skLineSegment(sketch, "E5754", {"start": v(31.9, -40.1) * mm, "end": v(31.9, -40.03) * mm});
            skLineSegment(sketch, "E5755", {"start": v(31.9, -40.03) * mm, "end": v(31.87, -39.94) * mm});
            skLineSegment(sketch, "E5756", {"start": v(31.87, -39.94) * mm, "end": v(31.85, -39.86) * mm});
            skLineSegment(sketch, "E5757", {"start": v(31.85, -39.86) * mm, "end": v(31.82, -39.78) * mm});
            skLineSegment(sketch, "E5758", {"start": v(31.82, -39.78) * mm, "end": v(31.8, -39.7) * mm});
            skLineSegment(sketch, "E5759", {"start": v(31.8, -39.7) * mm, "end": v(31.78, -39.61) * mm});
            skLineSegment(sketch, "E5760", {"start": v(31.78, -39.61) * mm, "end": v(31.75, -39.53) * mm});
            skLineSegment(sketch, "E5761", {"start": v(31.75, -39.53) * mm, "end": v(31.73, -39.45) * mm});
            skLineSegment(sketch, "E5762", {"start": v(31.73, -39.45) * mm, "end": v(31.7, -39.38) * mm});
            skLineSegment(sketch, "E5763", {"start": v(31.7, -39.38) * mm, "end": v(31.68, -39.3) * mm});
            skLineSegment(sketch, "E5764", {"start": v(31.68, -39.3) * mm, "end": v(31.66, -39.22) * mm});
            skLineSegment(sketch, "E5765", {"start": v(31.66, -39.22) * mm, "end": v(31.63, -39.15) * mm});
            skLineSegment(sketch, "E5766", {"start": v(31.63, -39.15) * mm, "end": v(31.6, -39.07) * mm});
            skLineSegment(sketch, "E5767", {"start": v(31.6, -39.07) * mm, "end": v(31.58, -39) * mm});
            skLineSegment(sketch, "E5768", {"start": v(31.58, -39) * mm, "end": v(31.56, -38.93) * mm});
            skLineSegment(sketch, "E5769", {"start": v(31.56, -38.93) * mm, "end": v(31.53, -38.85) * mm});
            skLineSegment(sketch, "E5770", {"start": v(31.53, -38.85) * mm, "end": v(31.5, -38.78) * mm});
            skLineSegment(sketch, "E5771", {"start": v(31.5, -38.78) * mm, "end": v(31.49, -38.71) * mm});
            skLineSegment(sketch, "E5772", {"start": v(31.49, -38.71) * mm, "end": v(31.46, -38.65) * mm});
            skLineSegment(sketch, "E5773", {"start": v(31.46, -38.65) * mm, "end": v(31.44, -38.58) * mm});
            skLineSegment(sketch, "E5774", {"start": v(31.44, -38.58) * mm, "end": v(31.41, -38.51) * mm});
            skLineSegment(sketch, "E5775", {"start": v(31.41, -38.51) * mm, "end": v(31.39, -38.45) * mm});
            skLineSegment(sketch, "E5776", {"start": v(31.39, -38.45) * mm, "end": v(31.36, -38.38) * mm});
            skLineSegment(sketch, "E5777", {"start": v(31.36, -38.38) * mm, "end": v(31.34, -38.32) * mm});
            skLineSegment(sketch, "E5778", {"start": v(31.34, -38.32) * mm, "end": v(31.32, -38.25) * mm});
            skLineSegment(sketch, "E5779", {"start": v(31.32, -38.25) * mm, "end": v(31.3, -38.2) * mm});
            skLineSegment(sketch, "E5780", {"start": v(31.3, -38.2) * mm, "end": v(31.27, -38.13) * mm});
            skLineSegment(sketch, "E5781", {"start": v(31.27, -38.13) * mm, "end": v(31.24, -38.07) * mm});
            skLineSegment(sketch, "E5782", {"start": v(31.24, -38.07) * mm, "end": v(31.22, -38.01) * mm});
            skLineSegment(sketch, "E5783", {"start": v(31.22, -38.01) * mm, "end": v(31.2, -37.95) * mm});
            skLineSegment(sketch, "E5784", {"start": v(31.2, -37.95) * mm, "end": v(31.17, -37.9) * mm});
            skLineSegment(sketch, "E5785", {"start": v(31.17, -37.9) * mm, "end": v(31.15, -37.84) * mm});
            skLineSegment(sketch, "E5786", {"start": v(31.15, -37.84) * mm, "end": v(31.12, -37.78) * mm});
            skLineSegment(sketch, "E5787", {"start": v(31.12, -37.78) * mm, "end": v(31.1, -37.73) * mm});
            skLineSegment(sketch, "E5788", {"start": v(31.1, -37.73) * mm, "end": v(31.08, -37.67) * mm});
            skLineSegment(sketch, "E5789", {"start": v(31.08, -37.67) * mm, "end": v(31.05, -37.62) * mm});
            skLineSegment(sketch, "E5790", {"start": v(31.05, -37.62) * mm, "end": v(31.03, -37.57) * mm});
            skLineSegment(sketch, "E5791", {"start": v(31.03, -37.57) * mm, "end": v(31, -37.52) * mm});
            skLineSegment(sketch, "E5792", {"start": v(31, -37.52) * mm, "end": v(30.98, -37.47) * mm});
            skLineSegment(sketch, "E5793", {"start": v(30.98, -37.47) * mm, "end": v(30.96, -37.42) * mm});
            skLineSegment(sketch, "E5794", {"start": v(30.96, -37.42) * mm, "end": v(31.17, -37.24) * mm});
            skLineSegment(sketch, "E5795", {"start": v(31.17, -37.24) * mm, "end": v(31.54, -36.93) * mm});
            skLineSegment(sketch, "E5796", {"start": v(31.54, -36.93) * mm, "end": v(31.75, -36.75) * mm});
            skLineSegment(sketch, "E5797", {"start": v(31.75, -36.75) * mm, "end": v(31.8, -36.78) * mm});
            skLineSegment(sketch, "E5798", {"start": v(31.8, -36.78) * mm, "end": v(31.84, -36.81) * mm});
            skLineSegment(sketch, "E5799", {"start": v(31.84, -36.81) * mm, "end": v(31.9, -36.84) * mm});
            skLineSegment(sketch, "E5800", {"start": v(31.9, -36.84) * mm, "end": v(31.94, -36.87) * mm});
            skLineSegment(sketch, "E5801", {"start": v(31.94, -36.87) * mm, "end": v(31.99, -36.9) * mm});
            skLineSegment(sketch, "E5802", {"start": v(31.99, -36.9) * mm, "end": v(32.04, -36.94) * mm});
            skLineSegment(sketch, "E5803", {"start": v(32.04, -36.94) * mm, "end": v(32.09, -36.97) * mm});
            skLineSegment(sketch, "E5804", {"start": v(32.09, -36.97) * mm, "end": v(32.14, -37) * mm});
            skLineSegment(sketch, "E5805", {"start": v(32.14, -37) * mm, "end": v(32.19, -37.04) * mm});
            skLineSegment(sketch, "E5806", {"start": v(32.19, -37.04) * mm, "end": v(32.24, -37.07) * mm});
            skLineSegment(sketch, "E5807", {"start": v(32.24, -37.07) * mm, "end": v(32.3, -37.1) * mm});
            skLineSegment(sketch, "E5808", {"start": v(32.3, -37.1) * mm, "end": v(32.35, -37.13) * mm});
            skLineSegment(sketch, "E5809", {"start": v(32.35, -37.13) * mm, "end": v(32.4, -37.17) * mm});
            skLineSegment(sketch, "E5810", {"start": v(32.4, -37.17) * mm, "end": v(32.46, -37.2) * mm});
            skLineSegment(sketch, "E5811", {"start": v(32.46, -37.2) * mm, "end": v(32.52, -37.24) * mm});
            skLineSegment(sketch, "E5812", {"start": v(32.52, -37.24) * mm, "end": v(32.58, -37.27) * mm});
            skLineSegment(sketch, "E5813", {"start": v(32.58, -37.27) * mm, "end": v(32.63, -37.3) * mm});
            skLineSegment(sketch, "E5814", {"start": v(32.63, -37.3) * mm, "end": v(32.7, -37.34) * mm});
            skLineSegment(sketch, "E5815", {"start": v(32.7, -37.34) * mm, "end": v(32.76, -37.38) * mm});
            skLineSegment(sketch, "E5816", {"start": v(32.76, -37.38) * mm, "end": v(32.82, -37.41) * mm});
            skLineSegment(sketch, "E5817", {"start": v(32.82, -37.41) * mm, "end": v(32.88, -37.45) * mm});
            skLineSegment(sketch, "E5818", {"start": v(32.88, -37.45) * mm, "end": v(32.94, -37.48) * mm});
            skLineSegment(sketch, "E5819", {"start": v(32.94, -37.48) * mm, "end": v(33, -37.52) * mm});
            skLineSegment(sketch, "E5820", {"start": v(33, -37.52) * mm, "end": v(33.07, -37.55) * mm});
            skLineSegment(sketch, "E5821", {"start": v(33.07, -37.55) * mm, "end": v(33.14, -37.59) * mm});
            skLineSegment(sketch, "E5822", {"start": v(33.14, -37.59) * mm, "end": v(33.2, -37.63) * mm});
            skLineSegment(sketch, "E5823", {"start": v(33.2, -37.63) * mm, "end": v(33.28, -37.66) * mm});
            skLineSegment(sketch, "E5824", {"start": v(33.28, -37.66) * mm, "end": v(33.35, -37.7) * mm});
            skLineSegment(sketch, "E5825", {"start": v(33.35, -37.7) * mm, "end": v(33.42, -37.73) * mm});
            skLineSegment(sketch, "E5826", {"start": v(33.42, -37.73) * mm, "end": v(33.49, -37.77) * mm});
            skLineSegment(sketch, "E5827", {"start": v(33.49, -37.77) * mm, "end": v(33.56, -37.8) * mm});
            skLineSegment(sketch, "E5828", {"start": v(33.56, -37.8) * mm, "end": v(33.63, -37.84) * mm});
            skLineSegment(sketch, "E5829", {"start": v(33.63, -37.84) * mm, "end": v(33.7, -37.88) * mm});
            skLineSegment(sketch, "E5830", {"start": v(33.7, -37.88) * mm, "end": v(33.78, -37.92) * mm});
            skLineSegment(sketch, "E5831", {"start": v(33.78, -37.92) * mm, "end": v(33.86, -37.95) * mm});
            skLineSegment(sketch, "E5832", {"start": v(33.86, -37.95) * mm, "end": v(33.93, -38) * mm});
            skLineSegment(sketch, "E5833", {"start": v(33.93, -38) * mm, "end": v(34.01, -38.03) * mm});
            skLineSegment(sketch, "E5834", {"start": v(34.01, -38.03) * mm, "end": v(34.1, -38.07) * mm});
            skLineSegment(sketch, "E5835", {"start": v(34.1, -38.07) * mm, "end": v(34.17, -38.1) * mm});
            skLineSegment(sketch, "E5836", {"start": v(34.17, -38.1) * mm, "end": v(34.24, -38.13) * mm});
            skLineSegment(sketch, "E5837", {"start": v(34.24, -38.13) * mm, "end": v(34.96, -37.48) * mm});
            skLineSegment(sketch, "E5838", {"start": v(34.96, -37.48) * mm, "end": v(34.94, -37.4) * mm});
            skLineSegment(sketch, "E5839", {"start": v(34.94, -37.4) * mm, "end": v(34.9, -37.32) * mm});
            skLineSegment(sketch, "E5840", {"start": v(34.9, -37.32) * mm, "end": v(34.88, -37.24) * mm});
            skLineSegment(sketch, "E5841", {"start": v(34.88, -37.24) * mm, "end": v(34.85, -37.16) * mm});
            skLineSegment(sketch, "E5842", {"start": v(34.85, -37.16) * mm, "end": v(34.82, -37.08) * mm});
            skLineSegment(sketch, "E5843", {"start": v(34.82, -37.08) * mm, "end": v(34.79, -37) * mm});
            skLineSegment(sketch, "E5844", {"start": v(34.79, -37) * mm, "end": v(34.76, -36.92) * mm});
            skLineSegment(sketch, "E5845", {"start": v(34.76, -36.92) * mm, "end": v(34.73, -36.84) * mm});
            skLineSegment(sketch, "E5846", {"start": v(34.73, -36.84) * mm, "end": v(34.7, -36.77) * mm});
            skLineSegment(sketch, "E5847", {"start": v(34.7, -36.77) * mm, "end": v(34.67, -36.7) * mm});
            skLineSegment(sketch, "E5848", {"start": v(34.67, -36.7) * mm, "end": v(34.64, -36.62) * mm});
            skLineSegment(sketch, "E5849", {"start": v(34.64, -36.62) * mm, "end": v(34.6, -36.54) * mm});
            skLineSegment(sketch, "E5850", {"start": v(34.6, -36.54) * mm, "end": v(34.58, -36.47) * mm});
            skLineSegment(sketch, "E5851", {"start": v(34.58, -36.47) * mm, "end": v(34.55, -36.4) * mm});
            skLineSegment(sketch, "E5852", {"start": v(34.55, -36.4) * mm, "end": v(34.52, -36.33) * mm});
            skLineSegment(sketch, "E5853", {"start": v(34.52, -36.33) * mm, "end": v(34.49, -36.26) * mm});
            skLineSegment(sketch, "E5854", {"start": v(34.49, -36.26) * mm, "end": v(34.46, -36.2) * mm});
            skLineSegment(sketch, "E5855", {"start": v(34.46, -36.2) * mm, "end": v(34.43, -36.12) * mm});
            skLineSegment(sketch, "E5856", {"start": v(34.43, -36.12) * mm, "end": v(34.4, -36.06) * mm});
            skLineSegment(sketch, "E5857", {"start": v(34.4, -36.06) * mm, "end": v(34.37, -36) * mm});
            skLineSegment(sketch, "E5858", {"start": v(34.37, -36) * mm, "end": v(34.34, -35.93) * mm});
            skLineSegment(sketch, "E5859", {"start": v(34.34, -35.93) * mm, "end": v(34.3, -35.86) * mm});
            skLineSegment(sketch, "E5860", {"start": v(34.3, -35.86) * mm, "end": v(34.28, -35.8) * mm});
            skLineSegment(sketch, "E5861", {"start": v(34.28, -35.8) * mm, "end": v(34.25, -35.74) * mm});
            skLineSegment(sketch, "E5862", {"start": v(34.25, -35.74) * mm, "end": v(34.22, -35.68) * mm});
            skLineSegment(sketch, "E5863", {"start": v(34.22, -35.68) * mm, "end": v(34.2, -35.62) * mm});
            skLineSegment(sketch, "E5864", {"start": v(34.2, -35.62) * mm, "end": v(34.16, -35.56) * mm});
            skLineSegment(sketch, "E5865", {"start": v(34.16, -35.56) * mm, "end": v(34.13, -35.5) * mm});
            skLineSegment(sketch, "E5866", {"start": v(34.13, -35.5) * mm, "end": v(34.1, -35.44) * mm});
            skLineSegment(sketch, "E5867", {"start": v(34.1, -35.44) * mm, "end": v(34.08, -35.39) * mm});
            skLineSegment(sketch, "E5868", {"start": v(34.08, -35.39) * mm, "end": v(34.05, -35.33) * mm});
            skLineSegment(sketch, "E5869", {"start": v(34.05, -35.33) * mm, "end": v(34.02, -35.28) * mm});
            skLineSegment(sketch, "E5870", {"start": v(34.02, -35.28) * mm, "end": v(34, -35.22) * mm});
            skLineSegment(sketch, "E5871", {"start": v(34, -35.22) * mm, "end": v(33.96, -35.17) * mm});
            skLineSegment(sketch, "E5872", {"start": v(33.96, -35.17) * mm, "end": v(33.94, -35.12) * mm});
            skLineSegment(sketch, "E5873", {"start": v(33.94, -35.12) * mm, "end": v(33.9, -35.07) * mm});
            skLineSegment(sketch, "E5874", {"start": v(33.9, -35.07) * mm, "end": v(33.88, -35.02) * mm});
            skLineSegment(sketch, "E5875", {"start": v(33.88, -35.02) * mm, "end": v(33.86, -34.97) * mm});
            skLineSegment(sketch, "E5876", {"start": v(33.86, -34.97) * mm, "end": v(33.83, -34.92) * mm});
            skLineSegment(sketch, "E5877", {"start": v(33.83, -34.92) * mm, "end": v(33.8, -34.88) * mm});
            skLineSegment(sketch, "E5878", {"start": v(33.8, -34.88) * mm, "end": v(34, -34.68) * mm});
            skLineSegment(sketch, "E5879", {"start": v(34, -34.68) * mm, "end": v(34.34, -34.34) * mm});
            skLineSegment(sketch, "E5880", {"start": v(34.34, -34.34) * mm, "end": v(34.54, -34.14) * mm});
            skLineSegment(sketch, "E5881", {"start": v(34.54, -34.14) * mm, "end": v(34.59, -34.17) * mm});
            skLineSegment(sketch, "E5882", {"start": v(34.59, -34.17) * mm, "end": v(34.63, -34.2) * mm});
            skLineSegment(sketch, "E5883", {"start": v(34.63, -34.2) * mm, "end": v(34.68, -34.23) * mm});
            skLineSegment(sketch, "E5884", {"start": v(34.68, -34.23) * mm, "end": v(34.73, -34.25) * mm});
            skLineSegment(sketch, "E5885", {"start": v(34.73, -34.25) * mm, "end": v(34.78, -34.28) * mm});
            skLineSegment(sketch, "E5886", {"start": v(34.78, -34.28) * mm, "end": v(34.83, -34.31) * mm});
            skLineSegment(sketch, "E5887", {"start": v(34.83, -34.31) * mm, "end": v(34.89, -34.34) * mm});
            skLineSegment(sketch, "E5888", {"start": v(34.89, -34.34) * mm, "end": v(34.94, -34.37) * mm});
            skLineSegment(sketch, "E5889", {"start": v(34.94, -34.37) * mm, "end": v(35, -34.4) * mm});
            skLineSegment(sketch, "E5890", {"start": v(35, -34.4) * mm, "end": v(35.05, -34.42) * mm});
            skLineSegment(sketch, "E5891", {"start": v(35.05, -34.42) * mm, "end": v(35.1, -34.45) * mm});
            skLineSegment(sketch, "E5892", {"start": v(35.1, -34.45) * mm, "end": v(35.16, -34.48) * mm});
            skLineSegment(sketch, "E5893", {"start": v(35.16, -34.48) * mm, "end": v(35.22, -34.51) * mm});
            skLineSegment(sketch, "E5894", {"start": v(35.22, -34.51) * mm, "end": v(35.28, -34.54) * mm});
            skLineSegment(sketch, "E5895", {"start": v(35.28, -34.54) * mm, "end": v(35.34, -34.57) * mm});
            skLineSegment(sketch, "E5896", {"start": v(35.34, -34.57) * mm, "end": v(35.4, -34.6) * mm});
            skLineSegment(sketch, "E5897", {"start": v(35.4, -34.6) * mm, "end": v(35.46, -34.63) * mm});
            skLineSegment(sketch, "E5898", {"start": v(35.46, -34.63) * mm, "end": v(35.52, -34.66) * mm});
            skLineSegment(sketch, "E5899", {"start": v(35.52, -34.66) * mm, "end": v(35.59, -34.7) * mm});
            skLineSegment(sketch, "E5900", {"start": v(35.59, -34.7) * mm, "end": v(35.65, -34.72) * mm});
            skLineSegment(sketch, "E5901", {"start": v(35.65, -34.72) * mm, "end": v(35.72, -34.75) * mm});
            skLineSegment(sketch, "E5902", {"start": v(35.72, -34.75) * mm, "end": v(35.78, -34.78) * mm});
            skLineSegment(sketch, "E5903", {"start": v(35.78, -34.78) * mm, "end": v(35.85, -34.81) * mm});
            skLineSegment(sketch, "E5904", {"start": v(35.85, -34.81) * mm, "end": v(35.92, -34.84) * mm});
            skLineSegment(sketch, "E5905", {"start": v(35.92, -34.84) * mm, "end": v(35.99, -34.87) * mm});
            skLineSegment(sketch, "E5906", {"start": v(35.99, -34.87) * mm, "end": v(36.06, -34.9) * mm});
            skLineSegment(sketch, "E5907", {"start": v(36.06, -34.9) * mm, "end": v(36.13, -34.93) * mm});
            skLineSegment(sketch, "E5908", {"start": v(36.13, -34.93) * mm, "end": v(36.2, -34.97) * mm});
            skLineSegment(sketch, "E5909", {"start": v(36.2, -34.97) * mm, "end": v(36.27, -35) * mm});
            skLineSegment(sketch, "E5910", {"start": v(36.27, -35) * mm, "end": v(36.35, -35.03) * mm});
            skLineSegment(sketch, "E5911", {"start": v(36.35, -35.03) * mm, "end": v(36.42, -35.06) * mm});
            skLineSegment(sketch, "E5912", {"start": v(36.42, -35.06) * mm, "end": v(36.5, -35.09) * mm});
            skLineSegment(sketch, "E5913", {"start": v(36.5, -35.09) * mm, "end": v(36.57, -35.12) * mm});
            skLineSegment(sketch, "E5914", {"start": v(36.57, -35.12) * mm, "end": v(36.65, -35.15) * mm});
            skLineSegment(sketch, "E5915", {"start": v(36.65, -35.15) * mm, "end": v(36.73, -35.18) * mm});
            skLineSegment(sketch, "E5916", {"start": v(36.73, -35.18) * mm, "end": v(36.81, -35.21) * mm});
            skLineSegment(sketch, "E5917", {"start": v(36.81, -35.21) * mm, "end": v(36.9, -35.24) * mm});
            skLineSegment(sketch, "E5918", {"start": v(36.9, -35.24) * mm, "end": v(36.97, -35.27) * mm});
            skLineSegment(sketch, "E5919", {"start": v(36.97, -35.27) * mm, "end": v(37.06, -35.3) * mm});
            skLineSegment(sketch, "E5920", {"start": v(37.06, -35.3) * mm, "end": v(37.13, -35.33) * mm});
            skLineSegment(sketch, "E5921", {"start": v(37.13, -35.33) * mm, "end": v(37.79, -34.62) * mm});
            skLineSegment(sketch, "E5922", {"start": v(37.79, -34.62) * mm, "end": v(37.76, -34.55) * mm});
            skLineSegment(sketch, "E5923", {"start": v(37.76, -34.55) * mm, "end": v(37.73, -34.47) * mm});
            skLineSegment(sketch, "E5924", {"start": v(37.73, -34.47) * mm, "end": v(37.7, -34.39) * mm});
            skLineSegment(sketch, "E5925", {"start": v(37.7, -34.39) * mm, "end": v(37.65, -34.3) * mm});
            skLineSegment(sketch, "E5926", {"start": v(37.65, -34.3) * mm, "end": v(37.62, -34.23) * mm});
            skLineSegment(sketch, "E5927", {"start": v(37.62, -34.23) * mm, "end": v(37.58, -34.15) * mm});
            skLineSegment(sketch, "E5928", {"start": v(37.58, -34.15) * mm, "end": v(37.55, -34.08) * mm});
            skLineSegment(sketch, "E5929", {"start": v(37.55, -34.08) * mm, "end": v(37.5, -34) * mm});
            skLineSegment(sketch, "E5930", {"start": v(37.5, -34) * mm, "end": v(37.47, -33.93) * mm});
            skLineSegment(sketch, "E5931", {"start": v(37.47, -33.93) * mm, "end": v(37.44, -33.86) * mm});
            skLineSegment(sketch, "E5932", {"start": v(37.44, -33.86) * mm, "end": v(37.4, -33.79) * mm});
            skLineSegment(sketch, "E5933", {"start": v(37.4, -33.79) * mm, "end": v(37.37, -33.72) * mm});
            skLineSegment(sketch, "E5934", {"start": v(37.37, -33.72) * mm, "end": v(37.33, -33.65) * mm});
            skLineSegment(sketch, "E5935", {"start": v(37.33, -33.65) * mm, "end": v(37.3, -33.58) * mm});
            skLineSegment(sketch, "E5936", {"start": v(37.3, -33.58) * mm, "end": v(37.26, -33.51) * mm});
            skLineSegment(sketch, "E5937", {"start": v(37.26, -33.51) * mm, "end": v(37.22, -33.44) * mm});
            skLineSegment(sketch, "E5938", {"start": v(37.22, -33.44) * mm, "end": v(37.19, -33.38) * mm});
            skLineSegment(sketch, "E5939", {"start": v(37.19, -33.38) * mm, "end": v(37.15, -33.31) * mm});
            skLineSegment(sketch, "E5940", {"start": v(37.15, -33.31) * mm, "end": v(37.12, -33.25) * mm});
            skLineSegment(sketch, "E5941", {"start": v(37.12, -33.25) * mm, "end": v(37.08, -33.19) * mm});
            skLineSegment(sketch, "E5942", {"start": v(37.08, -33.19) * mm, "end": v(37.05, -33.12) * mm});
            skLineSegment(sketch, "E5943", {"start": v(37.05, -33.12) * mm, "end": v(37.02, -33.06) * mm});
            skLineSegment(sketch, "E5944", {"start": v(37.02, -33.06) * mm, "end": v(36.98, -33) * mm});
            skLineSegment(sketch, "E5945", {"start": v(36.98, -33) * mm, "end": v(36.95, -32.94) * mm});
            skLineSegment(sketch, "E5946", {"start": v(36.95, -32.94) * mm, "end": v(36.91, -32.88) * mm});
            skLineSegment(sketch, "E5947", {"start": v(36.91, -32.88) * mm, "end": v(36.88, -32.83) * mm});
            skLineSegment(sketch, "E5948", {"start": v(36.88, -32.83) * mm, "end": v(36.85, -32.77) * mm});
            skLineSegment(sketch, "E5949", {"start": v(36.85, -32.77) * mm, "end": v(36.81, -32.71) * mm});
            skLineSegment(sketch, "E5950", {"start": v(36.81, -32.71) * mm, "end": v(36.78, -32.66) * mm});
            skLineSegment(sketch, "E5951", {"start": v(36.78, -32.66) * mm, "end": v(36.75, -32.6) * mm});
            skLineSegment(sketch, "E5952", {"start": v(36.75, -32.6) * mm, "end": v(36.72, -32.55) * mm});
            skLineSegment(sketch, "E5953", {"start": v(36.72, -32.55) * mm, "end": v(36.68, -32.5) * mm});
            skLineSegment(sketch, "E5954", {"start": v(36.68, -32.5) * mm, "end": v(36.65, -32.45) * mm});
            skLineSegment(sketch, "E5955", {"start": v(36.65, -32.45) * mm, "end": v(36.62, -32.4) * mm});
            skLineSegment(sketch, "E5956", {"start": v(36.62, -32.4) * mm, "end": v(36.59, -32.35) * mm});
            skLineSegment(sketch, "E5957", {"start": v(36.59, -32.35) * mm, "end": v(36.56, -32.3) * mm});
            skLineSegment(sketch, "E5958", {"start": v(36.56, -32.3) * mm, "end": v(36.53, -32.25) * mm});
            skLineSegment(sketch, "E5959", {"start": v(36.53, -32.25) * mm, "end": v(36.5, -32.2) * mm});
            skLineSegment(sketch, "E5960", {"start": v(36.5, -32.2) * mm, "end": v(36.46, -32.16) * mm});
            skLineSegment(sketch, "E5961", {"start": v(36.46, -32.16) * mm, "end": v(36.43, -32.12) * mm});
            skLineSegment(sketch, "E5962", {"start": v(36.43, -32.12) * mm, "end": v(36.61, -31.9) * mm});
            skLineSegment(sketch, "E5963", {"start": v(36.61, -31.9) * mm, "end": v(36.93, -31.54) * mm});
            skLineSegment(sketch, "E5964", {"start": v(36.93, -31.54) * mm, "end": v(37.11, -31.33) * mm});
            skLineSegment(sketch, "E5965", {"start": v(37.11, -31.33) * mm, "end": v(37.16, -31.35) * mm});
            skLineSegment(sketch, "E5966", {"start": v(37.16, -31.35) * mm, "end": v(37.21, -31.38) * mm});
            skLineSegment(sketch, "E5967", {"start": v(37.21, -31.38) * mm, "end": v(37.26, -31.4) * mm});
            skLineSegment(sketch, "E5968", {"start": v(37.26, -31.4) * mm, "end": v(37.31, -31.42) * mm});
            skLineSegment(sketch, "E5969", {"start": v(37.31, -31.42) * mm, "end": v(37.37, -31.45) * mm});
            skLineSegment(sketch, "E5970", {"start": v(37.37, -31.45) * mm, "end": v(37.42, -31.47) * mm});
            skLineSegment(sketch, "E5971", {"start": v(37.42, -31.47) * mm, "end": v(37.47, -31.5) * mm});
            skLineSegment(sketch, "E5972", {"start": v(37.47, -31.5) * mm, "end": v(37.53, -31.52) * mm});
            skLineSegment(sketch, "E5973", {"start": v(37.53, -31.52) * mm, "end": v(37.59, -31.54) * mm});
            skLineSegment(sketch, "E5974", {"start": v(37.59, -31.54) * mm, "end": v(37.64, -31.57) * mm});
            skLineSegment(sketch, "E5975", {"start": v(37.64, -31.57) * mm, "end": v(37.7, -31.6) * mm});
            skLineSegment(sketch, "E5976", {"start": v(37.7, -31.6) * mm, "end": v(37.76, -31.62) * mm});
            skLineSegment(sketch, "E5977", {"start": v(37.76, -31.62) * mm, "end": v(37.82, -31.64) * mm});
            skLineSegment(sketch, "E5978", {"start": v(37.82, -31.64) * mm, "end": v(37.88, -31.67) * mm});
            skLineSegment(sketch, "E5979", {"start": v(37.88, -31.67) * mm, "end": v(37.94, -31.7) * mm});
            skLineSegment(sketch, "E5980", {"start": v(37.94, -31.7) * mm, "end": v(38, -31.72) * mm});
            skLineSegment(sketch, "E5981", {"start": v(38, -31.72) * mm, "end": v(38.07, -31.74) * mm});
            skLineSegment(sketch, "E5982", {"start": v(38.07, -31.74) * mm, "end": v(38.13, -31.77) * mm});
            skLineSegment(sketch, "E5983", {"start": v(38.13, -31.77) * mm, "end": v(38.2, -31.8) * mm});
            skLineSegment(sketch, "E5984", {"start": v(38.2, -31.8) * mm, "end": v(38.27, -31.82) * mm});
            skLineSegment(sketch, "E5985", {"start": v(38.27, -31.82) * mm, "end": v(38.33, -31.84) * mm});
            skLineSegment(sketch, "E5986", {"start": v(38.33, -31.84) * mm, "end": v(38.4, -31.87) * mm});
            skLineSegment(sketch, "E5987", {"start": v(38.4, -31.87) * mm, "end": v(38.47, -31.9) * mm});
            skLineSegment(sketch, "E5988", {"start": v(38.47, -31.9) * mm, "end": v(38.54, -31.92) * mm});
            skLineSegment(sketch, "E5989", {"start": v(38.54, -31.92) * mm, "end": v(38.61, -31.94) * mm});
            skLineSegment(sketch, "E5990", {"start": v(38.61, -31.94) * mm, "end": v(38.68, -31.97) * mm});
            skLineSegment(sketch, "E5991", {"start": v(38.68, -31.97) * mm, "end": v(38.76, -32) * mm});
            skLineSegment(sketch, "E5992", {"start": v(38.76, -32) * mm, "end": v(38.83, -32.02) * mm});
            skLineSegment(sketch, "E5993", {"start": v(38.83, -32.02) * mm, "end": v(38.9, -32.04) * mm});
            skLineSegment(sketch, "E5994", {"start": v(38.9, -32.04) * mm, "end": v(38.98, -32.07) * mm});
            skLineSegment(sketch, "E5995", {"start": v(38.98, -32.07) * mm, "end": v(39.06, -32.1) * mm});
            skLineSegment(sketch, "E5996", {"start": v(39.06, -32.1) * mm, "end": v(39.14, -32.12) * mm});
            skLineSegment(sketch, "E5997", {"start": v(39.14, -32.12) * mm, "end": v(39.22, -32.14) * mm});
            skLineSegment(sketch, "E5998", {"start": v(39.22, -32.14) * mm, "end": v(39.3, -32.17) * mm});
            skLineSegment(sketch, "E5999", {"start": v(39.3, -32.17) * mm, "end": v(39.38, -32.2) * mm});
            skLineSegment(sketch, "E6000", {"start": v(39.38, -32.2) * mm, "end": v(39.46, -32.21) * mm});
            skLineSegment(sketch, "E6001", {"start": v(39.46, -32.21) * mm, "end": v(39.54, -32.24) * mm});
            skLineSegment(sketch, "E6002", {"start": v(39.54, -32.24) * mm, "end": v(39.63, -32.26) * mm});
            skLineSegment(sketch, "E6003", {"start": v(39.63, -32.26) * mm, "end": v(39.71, -32.29) * mm});
            skLineSegment(sketch, "E6004", {"start": v(39.71, -32.29) * mm, "end": v(39.79, -32.3) * mm});
            skLineSegment(sketch, "E6005", {"start": v(39.79, -32.3) * mm, "end": v(40.39, -31.55) * mm});
            skLineSegment(sketch, "E6006", {"start": v(40.39, -31.55) * mm, "end": v(40.36, -31.48) * mm});
            skLineSegment(sketch, "E6007", {"start": v(40.36, -31.48) * mm, "end": v(40.31, -31.4) * mm});
            skLineSegment(sketch, "E6008", {"start": v(40.31, -31.4) * mm, "end": v(40.27, -31.32) * mm});
            skLineSegment(sketch, "E6009", {"start": v(40.27, -31.32) * mm, "end": v(40.23, -31.25) * mm});
            skLineSegment(sketch, "E6010", {"start": v(40.23, -31.25) * mm, "end": v(40.19, -31.17) * mm});
            skLineSegment(sketch, "E6011", {"start": v(40.19, -31.17) * mm, "end": v(40.15, -31.1) * mm});
            skLineSegment(sketch, "E6012", {"start": v(40.15, -31.1) * mm, "end": v(40.1, -31.03) * mm});
            skLineSegment(sketch, "E6013", {"start": v(40.1, -31.03) * mm, "end": v(40.06, -30.96) * mm});
            skLineSegment(sketch, "E6014", {"start": v(40.06, -30.96) * mm, "end": v(40.02, -30.89) * mm});
            skLineSegment(sketch, "E6015", {"start": v(40.02, -30.89) * mm, "end": v(39.98, -30.82) * mm});
            skLineSegment(sketch, "E6016", {"start": v(39.98, -30.82) * mm, "end": v(39.94, -30.75) * mm});
            skLineSegment(sketch, "E6017", {"start": v(39.94, -30.75) * mm, "end": v(39.9, -30.68) * mm});
            skLineSegment(sketch, "E6018", {"start": v(39.9, -30.68) * mm, "end": v(39.86, -30.61) * mm});
            skLineSegment(sketch, "E6019", {"start": v(39.86, -30.61) * mm, "end": v(39.81, -30.55) * mm});
            skLineSegment(sketch, "E6020", {"start": v(39.81, -30.55) * mm, "end": v(39.77, -30.48) * mm});
            skLineSegment(sketch, "E6021", {"start": v(39.77, -30.48) * mm, "end": v(39.73, -30.42) * mm});
            skLineSegment(sketch, "E6022", {"start": v(39.73, -30.42) * mm, "end": v(39.7, -30.36) * mm});
            skLineSegment(sketch, "E6023", {"start": v(39.7, -30.36) * mm, "end": v(39.65, -30.3) * mm});
            skLineSegment(sketch, "E6024", {"start": v(39.65, -30.3) * mm, "end": v(39.61, -30.23) * mm});
            skLineSegment(sketch, "E6025", {"start": v(39.61, -30.23) * mm, "end": v(39.57, -30.17) * mm});
            skLineSegment(sketch, "E6026", {"start": v(39.57, -30.17) * mm, "end": v(39.53, -30.11) * mm});
            skLineSegment(sketch, "E6027", {"start": v(39.53, -30.11) * mm, "end": v(39.5, -30.06) * mm});
            skLineSegment(sketch, "E6028", {"start": v(39.5, -30.06) * mm, "end": v(39.46, -30) * mm});
            skLineSegment(sketch, "E6029", {"start": v(39.46, -30) * mm, "end": v(39.42, -29.94) * mm});
            skLineSegment(sketch, "E6030", {"start": v(39.42, -29.94) * mm, "end": v(39.38, -29.89) * mm});
            skLineSegment(sketch, "E6031", {"start": v(39.38, -29.89) * mm, "end": v(39.34, -29.83) * mm});
            skLineSegment(sketch, "E6032", {"start": v(39.34, -29.83) * mm, "end": v(39.3, -29.78) * mm});
            skLineSegment(sketch, "E6033", {"start": v(39.3, -29.78) * mm, "end": v(39.27, -29.72) * mm});
            skLineSegment(sketch, "E6034", {"start": v(39.27, -29.72) * mm, "end": v(39.23, -29.67) * mm});
            skLineSegment(sketch, "E6035", {"start": v(39.23, -29.67) * mm, "end": v(39.2, -29.62) * mm});
            skLineSegment(sketch, "E6036", {"start": v(39.2, -29.62) * mm, "end": v(39.16, -29.57) * mm});
            skLineSegment(sketch, "E6037", {"start": v(39.16, -29.57) * mm, "end": v(39.12, -29.52) * mm});
            skLineSegment(sketch, "E6038", {"start": v(39.12, -29.52) * mm, "end": v(39.08, -29.47) * mm});
            skLineSegment(sketch, "E6039", {"start": v(39.08, -29.47) * mm, "end": v(39.05, -29.43) * mm});
            skLineSegment(sketch, "E6040", {"start": v(39.05, -29.43) * mm, "end": v(39.01, -29.38) * mm});
            skLineSegment(sketch, "E6041", {"start": v(39.01, -29.38) * mm, "end": v(38.98, -29.33) * mm});
            skLineSegment(sketch, "E6042", {"start": v(38.98, -29.33) * mm, "end": v(38.94, -29.29) * mm});
            skLineSegment(sketch, "E6043", {"start": v(38.94, -29.29) * mm, "end": v(38.9, -29.24) * mm});
            skLineSegment(sketch, "E6044", {"start": v(38.9, -29.24) * mm, "end": v(38.88, -29.2) * mm});
            skLineSegment(sketch, "E6045", {"start": v(38.88, -29.2) * mm, "end": v(38.84, -29.16) * mm});
            skLineSegment(sketch, "E6046", {"start": v(38.84, -29.16) * mm, "end": v(39, -28.93) * mm});
            skLineSegment(sketch, "E6047", {"start": v(39, -28.93) * mm, "end": v(39.29, -28.54) * mm});
            skLineSegment(sketch, "E6048", {"start": v(39.29, -28.54) * mm, "end": v(39.46, -28.32) * mm});
            skLineSegment(sketch, "E6049", {"start": v(39.46, -28.32) * mm, "end": v(39.5, -28.34) * mm});
            skLineSegment(sketch, "E6050", {"start": v(39.5, -28.34) * mm, "end": v(39.56, -28.36) * mm});
            skLineSegment(sketch, "E6051", {"start": v(39.56, -28.36) * mm, "end": v(39.61, -28.38) * mm});
            skLineSegment(sketch, "E6052", {"start": v(39.61, -28.38) * mm, "end": v(39.66, -28.4) * mm});
            skLineSegment(sketch, "E6053", {"start": v(39.66, -28.4) * mm, "end": v(39.72, -28.42) * mm});
            skLineSegment(sketch, "E6054", {"start": v(39.72, -28.42) * mm, "end": v(39.77, -28.44) * mm});
            skLineSegment(sketch, "E6055", {"start": v(39.77, -28.44) * mm, "end": v(39.83, -28.46) * mm});
            skLineSegment(sketch, "E6056", {"start": v(39.83, -28.46) * mm, "end": v(39.89, -28.48) * mm});
            skLineSegment(sketch, "E6057", {"start": v(39.89, -28.48) * mm, "end": v(39.94, -28.5) * mm});
            skLineSegment(sketch, "E6058", {"start": v(39.94, -28.5) * mm, "end": v(40, -28.52) * mm});
            skLineSegment(sketch, "E6059", {"start": v(40, -28.52) * mm, "end": v(40.06, -28.54) * mm});
            skLineSegment(sketch, "E6060", {"start": v(40.06, -28.54) * mm, "end": v(40.12, -28.56) * mm});
            skLineSegment(sketch, "E6061", {"start": v(40.12, -28.56) * mm, "end": v(40.19, -28.58) * mm});
            skLineSegment(sketch, "E6062", {"start": v(40.19, -28.58) * mm, "end": v(40.25, -28.6) * mm});
            skLineSegment(sketch, "E6063", {"start": v(40.25, -28.6) * mm, "end": v(40.31, -28.62) * mm});
            skLineSegment(sketch, "E6064", {"start": v(40.31, -28.62) * mm, "end": v(40.38, -28.64) * mm});
            skLineSegment(sketch, "E6065", {"start": v(40.38, -28.64) * mm, "end": v(40.44, -28.66) * mm});
            skLineSegment(sketch, "E6066", {"start": v(40.44, -28.66) * mm, "end": v(40.5, -28.68) * mm});
            skLineSegment(sketch, "E6067", {"start": v(40.5, -28.68) * mm, "end": v(40.58, -28.7) * mm});
            skLineSegment(sketch, "E6068", {"start": v(40.58, -28.7) * mm, "end": v(40.64, -28.72) * mm});
            skLineSegment(sketch, "E6069", {"start": v(40.64, -28.72) * mm, "end": v(40.71, -28.74) * mm});
            skLineSegment(sketch, "E6070", {"start": v(40.71, -28.74) * mm, "end": v(40.78, -28.76) * mm});
            skLineSegment(sketch, "E6071", {"start": v(40.78, -28.76) * mm, "end": v(40.85, -28.78) * mm});
            skLineSegment(sketch, "E6072", {"start": v(40.85, -28.78) * mm, "end": v(40.93, -28.8) * mm});
            skLineSegment(sketch, "E6073", {"start": v(40.93, -28.8) * mm, "end": v(41, -28.81) * mm});
            skLineSegment(sketch, "E6074", {"start": v(41, -28.81) * mm, "end": v(41.07, -28.83) * mm});
            skLineSegment(sketch, "E6075", {"start": v(41.07, -28.83) * mm, "end": v(41.15, -28.85) * mm});
            skLineSegment(sketch, "E6076", {"start": v(41.15, -28.85) * mm, "end": v(41.22, -28.87) * mm});
            skLineSegment(sketch, "E6077", {"start": v(41.22, -28.87) * mm, "end": v(41.3, -28.9) * mm});
            skLineSegment(sketch, "E6078", {"start": v(41.3, -28.9) * mm, "end": v(41.38, -28.9) * mm});
            skLineSegment(sketch, "E6079", {"start": v(41.38, -28.9) * mm, "end": v(41.46, -28.93) * mm});
            skLineSegment(sketch, "E6080", {"start": v(41.46, -28.93) * mm, "end": v(41.54, -28.95) * mm});
            skLineSegment(sketch, "E6081", {"start": v(41.54, -28.95) * mm, "end": v(41.62, -28.97) * mm});
            skLineSegment(sketch, "E6082", {"start": v(41.62, -28.97) * mm, "end": v(41.7, -28.98) * mm});
            skLineSegment(sketch, "E6083", {"start": v(41.7, -28.98) * mm, "end": v(41.78, -29) * mm});
            skLineSegment(sketch, "E6084", {"start": v(41.78, -29) * mm, "end": v(41.87, -29.02) * mm});
            skLineSegment(sketch, "E6085", {"start": v(41.87, -29.02) * mm, "end": v(41.95, -29.04) * mm});
            skLineSegment(sketch, "E6086", {"start": v(41.95, -29.04) * mm, "end": v(42.04, -29.05) * mm});
            skLineSegment(sketch, "E6087", {"start": v(42.04, -29.05) * mm, "end": v(42.12, -29.07) * mm});
            skLineSegment(sketch, "E6088", {"start": v(42.12, -29.07) * mm, "end": v(42.2, -29.08) * mm});
            skLineSegment(sketch, "E6089", {"start": v(42.2, -29.08) * mm, "end": v(42.74, -28.28) * mm});
            skLineSegment(sketch, "E6090", {"start": v(42.74, -28.28) * mm, "end": v(42.7, -28.21) * mm});
            skLineSegment(sketch, "E6091", {"start": v(42.7, -28.21) * mm, "end": v(42.65, -28.14) * mm});
            skLineSegment(sketch, "E6092", {"start": v(42.65, -28.14) * mm, "end": v(42.6, -28.07) * mm});
            skLineSegment(sketch, "E6093", {"start": v(42.6, -28.07) * mm, "end": v(42.56, -28) * mm});
            skLineSegment(sketch, "E6094", {"start": v(42.56, -28) * mm, "end": v(42.5, -27.93) * mm});
            skLineSegment(sketch, "E6095", {"start": v(42.5, -27.93) * mm, "end": v(42.46, -27.86) * mm});
            skLineSegment(sketch, "E6096", {"start": v(42.46, -27.86) * mm, "end": v(42.41, -27.79) * mm});
            skLineSegment(sketch, "E6097", {"start": v(42.41, -27.79) * mm, "end": v(42.37, -27.72) * mm});
            skLineSegment(sketch, "E6098", {"start": v(42.37, -27.72) * mm, "end": v(42.32, -27.65) * mm});
            skLineSegment(sketch, "E6099", {"start": v(42.32, -27.65) * mm, "end": v(42.27, -27.59) * mm});
            skLineSegment(sketch, "E6100", {"start": v(42.27, -27.59) * mm, "end": v(42.23, -27.52) * mm});
            skLineSegment(sketch, "E6101", {"start": v(42.23, -27.52) * mm, "end": v(42.18, -27.46) * mm});
            skLineSegment(sketch, "E6102", {"start": v(42.18, -27.46) * mm, "end": v(42.13, -27.4) * mm});
            skLineSegment(sketch, "E6103", {"start": v(42.13, -27.4) * mm, "end": v(42.09, -27.33) * mm});
            skLineSegment(sketch, "E6104", {"start": v(42.09, -27.33) * mm, "end": v(42.04, -27.27) * mm});
            skLineSegment(sketch, "E6105", {"start": v(42.04, -27.27) * mm, "end": v(42, -27.2) * mm});
            skLineSegment(sketch, "E6106", {"start": v(42, -27.2) * mm, "end": v(41.95, -27.15) * mm});
            skLineSegment(sketch, "E6107", {"start": v(41.95, -27.15) * mm, "end": v(41.9, -27.1) * mm});
            skLineSegment(sketch, "E6108", {"start": v(41.9, -27.1) * mm, "end": v(41.86, -27.03) * mm});
            skLineSegment(sketch, "E6109", {"start": v(41.86, -27.03) * mm, "end": v(41.82, -26.98) * mm});
            skLineSegment(sketch, "E6110", {"start": v(41.82, -26.98) * mm, "end": v(41.78, -26.92) * mm});
            skLineSegment(sketch, "E6111", {"start": v(41.78, -26.92) * mm, "end": v(41.73, -26.86) * mm});
            skLineSegment(sketch, "E6112", {"start": v(41.73, -26.86) * mm, "end": v(41.69, -26.81) * mm});
            skLineSegment(sketch, "E6113", {"start": v(41.69, -26.81) * mm, "end": v(41.65, -26.76) * mm});
            skLineSegment(sketch, "E6114", {"start": v(41.65, -26.76) * mm, "end": v(41.6, -26.7) * mm});
            skLineSegment(sketch, "E6115", {"start": v(41.6, -26.7) * mm, "end": v(41.56, -26.65) * mm});
            skLineSegment(sketch, "E6116", {"start": v(41.56, -26.65) * mm, "end": v(41.52, -26.6) * mm});
            skLineSegment(sketch, "E6117", {"start": v(41.52, -26.6) * mm, "end": v(41.48, -26.55) * mm});
            skLineSegment(sketch, "E6118", {"start": v(41.48, -26.55) * mm, "end": v(41.44, -26.5) * mm});
            skLineSegment(sketch, "E6119", {"start": v(41.44, -26.5) * mm, "end": v(41.4, -26.46) * mm});
            skLineSegment(sketch, "E6120", {"start": v(41.4, -26.46) * mm, "end": v(41.36, -26.4) * mm});
            skLineSegment(sketch, "E6121", {"start": v(41.36, -26.4) * mm, "end": v(41.32, -26.36) * mm});
            skLineSegment(sketch, "E6122", {"start": v(41.32, -26.36) * mm, "end": v(41.28, -26.32) * mm});
            skLineSegment(sketch, "E6123", {"start": v(41.28, -26.32) * mm, "end": v(41.24, -26.27) * mm});
            skLineSegment(sketch, "E6124", {"start": v(41.24, -26.27) * mm, "end": v(41.2, -26.23) * mm});
            skLineSegment(sketch, "E6125", {"start": v(41.2, -26.23) * mm, "end": v(41.16, -26.18) * mm});
            skLineSegment(sketch, "E6126", {"start": v(41.16, -26.18) * mm, "end": v(41.12, -26.14) * mm});
            skLineSegment(sketch, "E6127", {"start": v(41.12, -26.14) * mm, "end": v(41.08, -26.1) * mm});
            skLineSegment(sketch, "E6128", {"start": v(41.08, -26.1) * mm, "end": v(41.05, -26.06) * mm});
            skLineSegment(sketch, "E6129", {"start": v(41.05, -26.06) * mm, "end": v(41, -26.02) * mm});
            skLineSegment(sketch, "E6130", {"start": v(41, -26.02) * mm, "end": v(41.15, -25.78) * mm});
            skLineSegment(sketch, "E6131", {"start": v(41.15, -25.78) * mm, "end": v(41.4, -25.37) * mm});
            skLineSegment(sketch, "E6132", {"start": v(41.4, -25.37) * mm, "end": v(41.56, -25.14) * mm});
            skLineSegment(sketch, "E6133", {"start": v(41.56, -25.14) * mm, "end": v(41.6, -25.15) * mm});
            skLineSegment(sketch, "E6134", {"start": v(41.6, -25.15) * mm, "end": v(41.66, -25.17) * mm});
            skLineSegment(sketch, "E6135", {"start": v(41.66, -25.17) * mm, "end": v(41.71, -25.18) * mm});
            skLineSegment(sketch, "E6136", {"start": v(41.71, -25.18) * mm, "end": v(41.77, -25.2) * mm});
            skLineSegment(sketch, "E6137", {"start": v(41.77, -25.2) * mm, "end": v(41.83, -25.21) * mm});
            skLineSegment(sketch, "E6138", {"start": v(41.83, -25.21) * mm, "end": v(41.88, -25.23) * mm});
            skLineSegment(sketch, "E6139", {"start": v(41.88, -25.23) * mm, "end": v(41.94, -25.25) * mm});
            skLineSegment(sketch, "E6140", {"start": v(41.94, -25.25) * mm, "end": v(42, -25.26) * mm});
            skLineSegment(sketch, "E6141", {"start": v(42, -25.26) * mm, "end": v(42.06, -25.28) * mm});
            skLineSegment(sketch, "E6142", {"start": v(42.06, -25.28) * mm, "end": v(42.12, -25.3) * mm});
            skLineSegment(sketch, "E6143", {"start": v(42.12, -25.3) * mm, "end": v(42.18, -25.3) * mm});
            skLineSegment(sketch, "E6144", {"start": v(42.18, -25.3) * mm, "end": v(42.24, -25.32) * mm});
            skLineSegment(sketch, "E6145", {"start": v(42.24, -25.32) * mm, "end": v(42.3, -25.34) * mm});
            skLineSegment(sketch, "E6146", {"start": v(42.3, -25.34) * mm, "end": v(42.37, -25.35) * mm});
            skLineSegment(sketch, "E6147", {"start": v(42.37, -25.35) * mm, "end": v(42.43, -25.37) * mm});
            skLineSegment(sketch, "E6148", {"start": v(42.43, -25.37) * mm, "end": v(42.5, -25.38) * mm});
            skLineSegment(sketch, "E6149", {"start": v(42.5, -25.38) * mm, "end": v(42.57, -25.4) * mm});
            skLineSegment(sketch, "E6150", {"start": v(42.57, -25.4) * mm, "end": v(42.63, -25.4) * mm});
            skLineSegment(sketch, "E6151", {"start": v(42.63, -25.4) * mm, "end": v(42.7, -25.42) * mm});
            skLineSegment(sketch, "E6152", {"start": v(42.7, -25.42) * mm, "end": v(42.77, -25.44) * mm});
            skLineSegment(sketch, "E6153", {"start": v(42.77, -25.44) * mm, "end": v(42.84, -25.45) * mm});
            skLineSegment(sketch, "E6154", {"start": v(42.84, -25.45) * mm, "end": v(42.91, -25.47) * mm});
            skLineSegment(sketch, "E6155", {"start": v(42.91, -25.47) * mm, "end": v(42.99, -25.48) * mm});
            skLineSegment(sketch, "E6156", {"start": v(42.99, -25.48) * mm, "end": v(43.06, -25.5) * mm});
            skLineSegment(sketch, "E6157", {"start": v(43.06, -25.5) * mm, "end": v(43.13, -25.5) * mm});
            skLineSegment(sketch, "E6158", {"start": v(43.13, -25.5) * mm, "end": v(43.2, -25.52) * mm});
            skLineSegment(sketch, "E6159", {"start": v(43.2, -25.52) * mm, "end": v(43.29, -25.54) * mm});
            skLineSegment(sketch, "E6160", {"start": v(43.29, -25.54) * mm, "end": v(43.36, -25.55) * mm});
            skLineSegment(sketch, "E6161", {"start": v(43.36, -25.55) * mm, "end": v(43.44, -25.56) * mm});
            skLineSegment(sketch, "E6162", {"start": v(43.44, -25.56) * mm, "end": v(43.52, -25.57) * mm});
            skLineSegment(sketch, "E6163", {"start": v(43.52, -25.57) * mm, "end": v(43.6, -25.59) * mm});
            skLineSegment(sketch, "E6164", {"start": v(43.6, -25.59) * mm, "end": v(43.68, -25.6) * mm});
            skLineSegment(sketch, "E6165", {"start": v(43.68, -25.6) * mm, "end": v(43.76, -25.61) * mm});
            skLineSegment(sketch, "E6166", {"start": v(43.76, -25.61) * mm, "end": v(43.85, -25.62) * mm});
            skLineSegment(sketch, "E6167", {"start": v(43.85, -25.62) * mm, "end": v(43.93, -25.63) * mm});
            skLineSegment(sketch, "E6168", {"start": v(43.93, -25.63) * mm, "end": v(44.01, -25.65) * mm});
            skLineSegment(sketch, "E6169", {"start": v(44.01, -25.65) * mm, "end": v(44.1, -25.66) * mm});
            skLineSegment(sketch, "E6170", {"start": v(44.1, -25.66) * mm, "end": v(44.19, -25.67) * mm});
            skLineSegment(sketch, "E6171", {"start": v(44.19, -25.67) * mm, "end": v(44.27, -25.68) * mm});
            skLineSegment(sketch, "E6172", {"start": v(44.27, -25.68) * mm, "end": v(44.35, -25.68) * mm});
            skLineSegment(sketch, "E6173", {"start": v(44.35, -25.68) * mm, "end": v(44.83, -24.84) * mm});
            skLineSegment(sketch, "E6174", {"start": v(44.83, -24.84) * mm, "end": v(44.78, -24.78) * mm});
            skLineSegment(sketch, "E6175", {"start": v(44.78, -24.78) * mm, "end": v(44.73, -24.7) * mm});
            skLineSegment(sketch, "E6176", {"start": v(44.73, -24.7) * mm, "end": v(44.68, -24.64) * mm});
            skLineSegment(sketch, "E6177", {"start": v(44.68, -24.64) * mm, "end": v(44.62, -24.57) * mm});
            skLineSegment(sketch, "E6178", {"start": v(44.62, -24.57) * mm, "end": v(44.57, -24.5) * mm});
            skLineSegment(sketch, "E6179", {"start": v(44.57, -24.5) * mm, "end": v(44.52, -24.44) * mm});
            skLineSegment(sketch, "E6180", {"start": v(44.52, -24.44) * mm, "end": v(44.46, -24.37) * mm});
            skLineSegment(sketch, "E6181", {"start": v(44.46, -24.37) * mm, "end": v(44.41, -24.3) * mm});
            skLineSegment(sketch, "E6182", {"start": v(44.41, -24.3) * mm, "end": v(44.36, -24.25) * mm});
            skLineSegment(sketch, "E6183", {"start": v(44.36, -24.25) * mm, "end": v(44.3, -24.18) * mm});
            skLineSegment(sketch, "E6184", {"start": v(44.3, -24.18) * mm, "end": v(44.26, -24.12) * mm});
            skLineSegment(sketch, "E6185", {"start": v(44.26, -24.12) * mm, "end": v(44.2, -24.06) * mm});
            skLineSegment(sketch, "E6186", {"start": v(44.2, -24.06) * mm, "end": v(44.15, -24) * mm});
            skLineSegment(sketch, "E6187", {"start": v(44.15, -24) * mm, "end": v(44.1, -23.94) * mm});
            skLineSegment(sketch, "E6188", {"start": v(44.1, -23.94) * mm, "end": v(44.05, -23.89) * mm});
            skLineSegment(sketch, "E6189", {"start": v(44.05, -23.89) * mm, "end": v(44, -23.83) * mm});
            skLineSegment(sketch, "E6190", {"start": v(44, -23.83) * mm, "end": v(43.95, -23.77) * mm});
            skLineSegment(sketch, "E6191", {"start": v(43.95, -23.77) * mm, "end": v(43.9, -23.72) * mm});
            skLineSegment(sketch, "E6192", {"start": v(43.9, -23.72) * mm, "end": v(43.86, -23.66) * mm});
            skLineSegment(sketch, "E6193", {"start": v(43.86, -23.66) * mm, "end": v(43.8, -23.61) * mm});
            skLineSegment(sketch, "E6194", {"start": v(43.8, -23.61) * mm, "end": v(43.76, -23.56) * mm});
            skLineSegment(sketch, "E6195", {"start": v(43.76, -23.56) * mm, "end": v(43.71, -23.5) * mm});
            skLineSegment(sketch, "E6196", {"start": v(43.71, -23.5) * mm, "end": v(43.66, -23.46) * mm});
            skLineSegment(sketch, "E6197", {"start": v(43.66, -23.46) * mm, "end": v(43.62, -23.4) * mm});
            skLineSegment(sketch, "E6198", {"start": v(43.62, -23.4) * mm, "end": v(43.57, -23.36) * mm});
            skLineSegment(sketch, "E6199", {"start": v(43.57, -23.36) * mm, "end": v(43.52, -23.3) * mm});
            skLineSegment(sketch, "E6200", {"start": v(43.52, -23.3) * mm, "end": v(43.48, -23.26) * mm});
            skLineSegment(sketch, "E6201", {"start": v(43.48, -23.26) * mm, "end": v(43.43, -23.22) * mm});
            skLineSegment(sketch, "E6202", {"start": v(43.43, -23.22) * mm, "end": v(43.39, -23.17) * mm});
            skLineSegment(sketch, "E6203", {"start": v(43.39, -23.17) * mm, "end": v(43.34, -23.13) * mm});
            skLineSegment(sketch, "E6204", {"start": v(43.34, -23.13) * mm, "end": v(43.3, -23.08) * mm});
            skLineSegment(sketch, "E6205", {"start": v(43.3, -23.08) * mm, "end": v(43.26, -23.04) * mm});
            skLineSegment(sketch, "E6206", {"start": v(43.26, -23.04) * mm, "end": v(43.21, -23) * mm});
            skLineSegment(sketch, "E6207", {"start": v(43.21, -23) * mm, "end": v(43.17, -22.96) * mm});
            skLineSegment(sketch, "E6208", {"start": v(43.17, -22.96) * mm, "end": v(43.13, -22.91) * mm});
            skLineSegment(sketch, "E6209", {"start": v(43.13, -22.91) * mm, "end": v(43.09, -22.87) * mm});
            skLineSegment(sketch, "E6210", {"start": v(43.09, -22.87) * mm, "end": v(43.05, -22.84) * mm});
            skLineSegment(sketch, "E6211", {"start": v(43.05, -22.84) * mm, "end": v(43, -22.8) * mm});
            skLineSegment(sketch, "E6212", {"start": v(43, -22.8) * mm, "end": v(42.96, -22.76) * mm});
            skLineSegment(sketch, "E6213", {"start": v(42.96, -22.76) * mm, "end": v(42.92, -22.72) * mm});
            skLineSegment(sketch, "E6214", {"start": v(42.92, -22.72) * mm, "end": v(43.05, -22.47) * mm});
            skLineSegment(sketch, "E6215", {"start": v(43.05, -22.47) * mm, "end": v(43.27, -22.05) * mm});
            skLineSegment(sketch, "E6216", {"start": v(43.27, -22.05) * mm, "end": v(43.4, -21.8) * mm});
            skLineSegment(sketch, "E6217", {"start": v(43.4, -21.8) * mm, "end": v(43.45, -21.81) * mm});
            skLineSegment(sketch, "E6218", {"start": v(43.45, -21.81) * mm, "end": v(43.5, -21.82) * mm});
            skLineSegment(sketch, "E6219", {"start": v(43.5, -21.82) * mm, "end": v(43.56, -21.83) * mm});
            skLineSegment(sketch, "E6220", {"start": v(43.56, -21.83) * mm, "end": v(43.62, -21.84) * mm});
            skLineSegment(sketch, "E6221", {"start": v(43.62, -21.84) * mm, "end": v(43.67, -21.86) * mm});
            skLineSegment(sketch, "E6222", {"start": v(43.67, -21.86) * mm, "end": v(43.73, -21.87) * mm});
            skLineSegment(sketch, "E6223", {"start": v(43.73, -21.87) * mm, "end": v(43.8, -21.88) * mm});
            skLineSegment(sketch, "E6224", {"start": v(43.8, -21.88) * mm, "end": v(43.85, -21.89) * mm});
            skLineSegment(sketch, "E6225", {"start": v(43.85, -21.89) * mm, "end": v(43.91, -21.9) * mm});
            skLineSegment(sketch, "E6226", {"start": v(43.91, -21.9) * mm, "end": v(43.97, -21.9) * mm});
            skLineSegment(sketch, "E6227", {"start": v(43.97, -21.9) * mm, "end": v(44.03, -21.92) * mm});
            skLineSegment(sketch, "E6228", {"start": v(44.03, -21.92) * mm, "end": v(44.1, -21.93) * mm});
            skLineSegment(sketch, "E6229", {"start": v(44.1, -21.93) * mm, "end": v(44.16, -21.94) * mm});
            skLineSegment(sketch, "E6230", {"start": v(44.16, -21.94) * mm, "end": v(44.23, -21.95) * mm});
            skLineSegment(sketch, "E6231", {"start": v(44.23, -21.95) * mm, "end": v(44.3, -21.96) * mm});
            skLineSegment(sketch, "E6232", {"start": v(44.3, -21.96) * mm, "end": v(44.36, -21.97) * mm});
            skLineSegment(sketch, "E6233", {"start": v(44.36, -21.97) * mm, "end": v(44.43, -21.98) * mm});
            skLineSegment(sketch, "E6234", {"start": v(44.43, -21.98) * mm, "end": v(44.5, -21.99) * mm});
            skLineSegment(sketch, "E6235", {"start": v(44.5, -21.99) * mm, "end": v(44.57, -22) * mm});
            skLineSegment(sketch, "E6236", {"start": v(44.57, -22) * mm, "end": v(44.64, -22) * mm});
            skLineSegment(sketch, "E6237", {"start": v(44.64, -22) * mm, "end": v(44.7, -22.01) * mm});
            skLineSegment(sketch, "E6238", {"start": v(44.7, -22.01) * mm, "end": v(44.78, -22.02) * mm});
            skLineSegment(sketch, "E6239", {"start": v(44.78, -22.02) * mm, "end": v(44.85, -22.03) * mm});
            skLineSegment(sketch, "E6240", {"start": v(44.85, -22.03) * mm, "end": v(44.93, -22.04) * mm});
            skLineSegment(sketch, "E6241", {"start": v(44.93, -22.04) * mm, "end": v(45, -22.05) * mm});
            skLineSegment(sketch, "E6242", {"start": v(45, -22.05) * mm, "end": v(45.08, -22.05) * mm});
            skLineSegment(sketch, "E6243", {"start": v(45.08, -22.05) * mm, "end": v(45.16, -22.06) * mm});
            skLineSegment(sketch, "E6244", {"start": v(45.16, -22.06) * mm, "end": v(45.23, -22.07) * mm});
            skLineSegment(sketch, "E6245", {"start": v(45.23, -22.07) * mm, "end": v(45.31, -22.07) * mm});
            skLineSegment(sketch, "E6246", {"start": v(45.31, -22.07) * mm, "end": v(45.4, -22.08) * mm});
            skLineSegment(sketch, "E6247", {"start": v(45.4, -22.08) * mm, "end": v(45.47, -22.09) * mm});
            skLineSegment(sketch, "E6248", {"start": v(45.47, -22.09) * mm, "end": v(45.55, -22.1) * mm});
            skLineSegment(sketch, "E6249", {"start": v(45.55, -22.1) * mm, "end": v(45.64, -22.1) * mm});
            skLineSegment(sketch, "E6250", {"start": v(45.64, -22.1) * mm, "end": v(45.72, -22.1) * mm});
            skLineSegment(sketch, "E6251", {"start": v(45.72, -22.1) * mm, "end": v(45.8, -22.1) * mm});
            skLineSegment(sketch, "E6252", {"start": v(45.8, -22.1) * mm, "end": v(45.9, -22.11) * mm});
            skLineSegment(sketch, "E6253", {"start": v(45.9, -22.11) * mm, "end": v(45.98, -22.12) * mm});
            skLineSegment(sketch, "E6254", {"start": v(45.98, -22.12) * mm, "end": v(46.06, -22.12) * mm});
            skLineSegment(sketch, "E6255", {"start": v(46.06, -22.12) * mm, "end": v(46.15, -22.12) * mm});
            skLineSegment(sketch, "E6256", {"start": v(46.15, -22.12) * mm, "end": v(46.23, -22.12) * mm});
            skLineSegment(sketch, "E6257", {"start": v(46.23, -22.12) * mm, "end": v(46.64, -21.25) * mm});
            skLineSegment(sketch, "E6258", {"start": v(46.64, -21.25) * mm, "end": v(46.59, -21.19) * mm});
            skLineSegment(sketch, "E6259", {"start": v(46.59, -21.19) * mm, "end": v(46.53, -21.12) * mm});
            skLineSegment(sketch, "E6260", {"start": v(46.53, -21.12) * mm, "end": v(46.47, -21.06) * mm});
            skLineSegment(sketch, "E6261", {"start": v(46.47, -21.06) * mm, "end": v(46.41, -21) * mm});
            skLineSegment(sketch, "E6262", {"start": v(46.41, -21) * mm, "end": v(46.35, -20.93) * mm});
            skLineSegment(sketch, "E6263", {"start": v(46.35, -20.93) * mm, "end": v(46.3, -20.87) * mm});
            skLineSegment(sketch, "E6264", {"start": v(46.3, -20.87) * mm, "end": v(46.24, -20.8) * mm});
            skLineSegment(sketch, "E6265", {"start": v(46.24, -20.8) * mm, "end": v(46.18, -20.75) * mm});
            skLineSegment(sketch, "E6266", {"start": v(46.18, -20.75) * mm, "end": v(46.12, -20.7) * mm});
            skLineSegment(sketch, "E6267", {"start": v(46.12, -20.7) * mm, "end": v(46.07, -20.63) * mm});
            skLineSegment(sketch, "E6268", {"start": v(46.07, -20.63) * mm, "end": v(46.01, -20.58) * mm});
            skLineSegment(sketch, "E6269", {"start": v(46.01, -20.58) * mm, "end": v(45.96, -20.52) * mm});
            skLineSegment(sketch, "E6270", {"start": v(45.96, -20.52) * mm, "end": v(45.9, -20.46) * mm});
            skLineSegment(sketch, "E6271", {"start": v(45.9, -20.46) * mm, "end": v(45.85, -20.4) * mm});
            skLineSegment(sketch, "E6272", {"start": v(45.85, -20.4) * mm, "end": v(45.8, -20.36) * mm});
            skLineSegment(sketch, "E6273", {"start": v(45.8, -20.36) * mm, "end": v(45.74, -20.3) * mm});
            skLineSegment(sketch, "E6274", {"start": v(45.74, -20.3) * mm, "end": v(45.68, -20.25) * mm});
            skLineSegment(sketch, "E6275", {"start": v(45.68, -20.25) * mm, "end": v(45.63, -20.2) * mm});
            skLineSegment(sketch, "E6276", {"start": v(45.63, -20.2) * mm, "end": v(45.58, -20.15) * mm});
            skLineSegment(sketch, "E6277", {"start": v(45.58, -20.15) * mm, "end": v(45.52, -20.1) * mm});
            skLineSegment(sketch, "E6278", {"start": v(45.52, -20.1) * mm, "end": v(45.47, -20.05) * mm});
            skLineSegment(sketch, "E6279", {"start": v(45.47, -20.05) * mm, "end": v(45.42, -20) * mm});
            skLineSegment(sketch, "E6280", {"start": v(45.42, -20) * mm, "end": v(45.37, -19.96) * mm});
            skLineSegment(sketch, "E6281", {"start": v(45.37, -19.96) * mm, "end": v(45.32, -19.91) * mm});
            skLineSegment(sketch, "E6282", {"start": v(45.32, -19.91) * mm, "end": v(45.27, -19.87) * mm});
            skLineSegment(sketch, "E6283", {"start": v(45.27, -19.87) * mm, "end": v(45.22, -19.82) * mm});
            skLineSegment(sketch, "E6284", {"start": v(45.22, -19.82) * mm, "end": v(45.17, -19.78) * mm});
            skLineSegment(sketch, "E6285", {"start": v(45.17, -19.78) * mm, "end": v(45.12, -19.74) * mm});
            skLineSegment(sketch, "E6286", {"start": v(45.12, -19.74) * mm, "end": v(45.07, -19.7) * mm});
            skLineSegment(sketch, "E6287", {"start": v(45.07, -19.7) * mm, "end": v(45.02, -19.65) * mm});
            skLineSegment(sketch, "E6288", {"start": v(45.02, -19.65) * mm, "end": v(44.98, -19.61) * mm});
            skLineSegment(sketch, "E6289", {"start": v(44.98, -19.61) * mm, "end": v(44.93, -19.57) * mm});
            skLineSegment(sketch, "E6290", {"start": v(44.93, -19.57) * mm, "end": v(44.88, -19.54) * mm});
            skLineSegment(sketch, "E6291", {"start": v(44.88, -19.54) * mm, "end": v(44.84, -19.5) * mm});
            skLineSegment(sketch, "E6292", {"start": v(44.84, -19.5) * mm, "end": v(44.8, -19.46) * mm});
            skLineSegment(sketch, "E6293", {"start": v(44.8, -19.46) * mm, "end": v(44.75, -19.42) * mm});
            skLineSegment(sketch, "E6294", {"start": v(44.75, -19.42) * mm, "end": v(44.7, -19.39) * mm});
            skLineSegment(sketch, "E6295", {"start": v(44.7, -19.39) * mm, "end": v(44.66, -19.35) * mm});
            skLineSegment(sketch, "E6296", {"start": v(44.66, -19.35) * mm, "end": v(44.62, -19.32) * mm});
            skLineSegment(sketch, "E6297", {"start": v(44.62, -19.32) * mm, "end": v(44.58, -19.29) * mm});
            skLineSegment(sketch, "E6298", {"start": v(44.58, -19.29) * mm, "end": v(44.68, -19.03) * mm});
            skLineSegment(sketch, "E6299", {"start": v(44.68, -19.03) * mm, "end": v(44.87, -18.58) * mm});
            skLineSegment(sketch, "E6300", {"start": v(44.87, -18.58) * mm, "end": v(44.98, -18.33) * mm});
            skLineSegment(sketch, "E6301", {"start": v(44.98, -18.33) * mm, "end": v(45.03, -18.34) * mm});
            skLineSegment(sketch, "E6302", {"start": v(45.03, -18.34) * mm, "end": v(45.09, -18.34) * mm});
            skLineSegment(sketch, "E6303", {"start": v(45.09, -18.34) * mm, "end": v(45.14, -18.35) * mm});
            skLineSegment(sketch, "E6304", {"start": v(45.14, -18.35) * mm, "end": v(45.2, -18.36) * mm});
            skLineSegment(sketch, "E6305", {"start": v(45.2, -18.36) * mm, "end": v(45.25, -18.36) * mm});
            skLineSegment(sketch, "E6306", {"start": v(45.25, -18.36) * mm, "end": v(45.31, -18.37) * mm});
            skLineSegment(sketch, "E6307", {"start": v(45.31, -18.37) * mm, "end": v(45.37, -18.37) * mm});
            skLineSegment(sketch, "E6308", {"start": v(45.37, -18.37) * mm, "end": v(45.43, -18.38) * mm});
            skLineSegment(sketch, "E6309", {"start": v(45.43, -18.38) * mm, "end": v(45.5, -18.39) * mm});
            skLineSegment(sketch, "E6310", {"start": v(45.5, -18.39) * mm, "end": v(45.56, -18.4) * mm});
            skLineSegment(sketch, "E6311", {"start": v(45.56, -18.4) * mm, "end": v(45.62, -18.4) * mm});
            skLineSegment(sketch, "E6312", {"start": v(45.62, -18.4) * mm, "end": v(45.68, -18.4) * mm});
            skLineSegment(sketch, "E6313", {"start": v(45.68, -18.4) * mm, "end": v(45.75, -18.4) * mm});
            skLineSegment(sketch, "E6314", {"start": v(45.75, -18.4) * mm, "end": v(45.81, -18.41) * mm});
            skLineSegment(sketch, "E6315", {"start": v(45.81, -18.41) * mm, "end": v(45.88, -18.42) * mm});
            skLineSegment(sketch, "E6316", {"start": v(45.88, -18.42) * mm, "end": v(45.95, -18.42) * mm});
            skLineSegment(sketch, "E6317", {"start": v(45.95, -18.42) * mm, "end": v(46.01, -18.42) * mm});
            skLineSegment(sketch, "E6318", {"start": v(46.01, -18.42) * mm, "end": v(46.08, -18.43) * mm});
            skLineSegment(sketch, "E6319", {"start": v(46.08, -18.43) * mm, "end": v(46.15, -18.43) * mm});
            skLineSegment(sketch, "E6320", {"start": v(46.15, -18.43) * mm, "end": v(46.22, -18.43) * mm});
            skLineSegment(sketch, "E6321", {"start": v(46.22, -18.43) * mm, "end": v(46.3, -18.44) * mm});
            skLineSegment(sketch, "E6322", {"start": v(46.3, -18.44) * mm, "end": v(46.37, -18.44) * mm});
            skLineSegment(sketch, "E6323", {"start": v(46.37, -18.44) * mm, "end": v(46.44, -18.44) * mm});
            skLineSegment(sketch, "E6324", {"start": v(46.44, -18.44) * mm, "end": v(46.52, -18.44) * mm});
            skLineSegment(sketch, "E6325", {"start": v(46.52, -18.44) * mm, "end": v(46.6, -18.45) * mm});
            skLineSegment(sketch, "E6326", {"start": v(46.6, -18.45) * mm, "end": v(46.67, -18.45) * mm});
            skLineSegment(sketch, "E6327", {"start": v(46.67, -18.45) * mm, "end": v(46.75, -18.45) * mm});
            skLineSegment(sketch, "E6328", {"start": v(46.75, -18.45) * mm, "end": v(46.83, -18.45) * mm});
            skLineSegment(sketch, "E6329", {"start": v(46.83, -18.45) * mm, "end": v(46.9, -18.45) * mm});
            skLineSegment(sketch, "E6330", {"start": v(46.9, -18.45) * mm, "end": v(46.98, -18.45) * mm});
            skLineSegment(sketch, "E6331", {"start": v(46.98, -18.45) * mm, "end": v(47.07, -18.45) * mm});
            skLineSegment(sketch, "E6332", {"start": v(47.07, -18.45) * mm, "end": v(47.15, -18.45) * mm});
            skLineSegment(sketch, "E6333", {"start": v(47.15, -18.45) * mm, "end": v(47.23, -18.45) * mm});
            skLineSegment(sketch, "E6334", {"start": v(47.23, -18.45) * mm, "end": v(47.31, -18.45) * mm});
            skLineSegment(sketch, "E6335", {"start": v(47.31, -18.45) * mm, "end": v(47.4, -18.45) * mm});
            skLineSegment(sketch, "E6336", {"start": v(47.4, -18.45) * mm, "end": v(47.48, -18.44) * mm});
            skLineSegment(sketch, "E6337", {"start": v(47.48, -18.44) * mm, "end": v(47.57, -18.44) * mm});
            skLineSegment(sketch, "E6338", {"start": v(47.57, -18.44) * mm, "end": v(47.66, -18.44) * mm});
            skLineSegment(sketch, "E6339", {"start": v(47.66, -18.44) * mm, "end": v(47.75, -18.44) * mm});
            skLineSegment(sketch, "E6340", {"start": v(47.75, -18.44) * mm, "end": v(47.82, -18.43) * mm});
            skLineSegment(sketch, "E6341", {"start": v(47.82, -18.43) * mm, "end": v(48.16, -17.52) * mm});
            skLineSegment(sketch, "E6342", {"start": v(48.16, -17.52) * mm, "end": v(48.1, -17.47) * mm});
            skLineSegment(sketch, "E6343", {"start": v(48.1, -17.47) * mm, "end": v(48.04, -17.4) * mm});
            skLineSegment(sketch, "E6344", {"start": v(48.04, -17.4) * mm, "end": v(47.98, -17.35) * mm});
            skLineSegment(sketch, "E6345", {"start": v(47.98, -17.35) * mm, "end": v(47.92, -17.29) * mm});
            skLineSegment(sketch, "E6346", {"start": v(47.92, -17.29) * mm, "end": v(47.85, -17.23) * mm});
            skLineSegment(sketch, "E6347", {"start": v(47.85, -17.23) * mm, "end": v(47.8, -17.17) * mm});
            skLineSegment(sketch, "E6348", {"start": v(47.8, -17.17) * mm, "end": v(47.73, -17.12) * mm});
            skLineSegment(sketch, "E6349", {"start": v(47.73, -17.12) * mm, "end": v(47.67, -17.06) * mm});
            skLineSegment(sketch, "E6350", {"start": v(47.67, -17.06) * mm, "end": v(47.6, -17) * mm});
            skLineSegment(sketch, "E6351", {"start": v(47.6, -17) * mm, "end": v(47.55, -16.95) * mm});
            skLineSegment(sketch, "E6352", {"start": v(47.55, -16.95) * mm, "end": v(47.48, -16.9) * mm});
            skLineSegment(sketch, "E6353", {"start": v(47.48, -16.9) * mm, "end": v(47.42, -16.85) * mm});
            skLineSegment(sketch, "E6354", {"start": v(47.42, -16.85) * mm, "end": v(47.36, -16.8) * mm});
            skLineSegment(sketch, "E6355", {"start": v(47.36, -16.8) * mm, "end": v(47.3, -16.75) * mm});
            skLineSegment(sketch, "E6356", {"start": v(47.3, -16.75) * mm, "end": v(47.25, -16.7) * mm});
            skLineSegment(sketch, "E6357", {"start": v(47.25, -16.7) * mm, "end": v(47.19, -16.65) * mm});
            skLineSegment(sketch, "E6358", {"start": v(47.19, -16.65) * mm, "end": v(47.13, -16.6) * mm});
            skLineSegment(sketch, "E6359", {"start": v(47.13, -16.6) * mm, "end": v(47.07, -16.56) * mm});
            skLineSegment(sketch, "E6360", {"start": v(47.07, -16.56) * mm, "end": v(47.02, -16.51) * mm});
            skLineSegment(sketch, "E6361", {"start": v(47.02, -16.51) * mm, "end": v(46.96, -16.47) * mm});
            skLineSegment(sketch, "E6362", {"start": v(46.96, -16.47) * mm, "end": v(46.9, -16.42) * mm});
            skLineSegment(sketch, "E6363", {"start": v(46.9, -16.42) * mm, "end": v(46.85, -16.38) * mm});
            skLineSegment(sketch, "E6364", {"start": v(46.85, -16.38) * mm, "end": v(46.8, -16.34) * mm});
            skLineSegment(sketch, "E6365", {"start": v(46.8, -16.34) * mm, "end": v(46.74, -16.3) * mm});
            skLineSegment(sketch, "E6366", {"start": v(46.74, -16.3) * mm, "end": v(46.69, -16.25) * mm});
            skLineSegment(sketch, "E6367", {"start": v(46.69, -16.25) * mm, "end": v(46.63, -16.21) * mm});
            skLineSegment(sketch, "E6368", {"start": v(46.63, -16.21) * mm, "end": v(46.58, -16.17) * mm});
            skLineSegment(sketch, "E6369", {"start": v(46.58, -16.17) * mm, "end": v(46.53, -16.14) * mm});
            skLineSegment(sketch, "E6370", {"start": v(46.53, -16.14) * mm, "end": v(46.48, -16.1) * mm});
            skLineSegment(sketch, "E6371", {"start": v(46.48, -16.1) * mm, "end": v(46.43, -16.06) * mm});
            skLineSegment(sketch, "E6372", {"start": v(46.43, -16.06) * mm, "end": v(46.38, -16.02) * mm});
            skLineSegment(sketch, "E6373", {"start": v(46.38, -16.02) * mm, "end": v(46.33, -15.99) * mm});
            skLineSegment(sketch, "E6374", {"start": v(46.33, -15.99) * mm, "end": v(46.28, -15.95) * mm});
            skLineSegment(sketch, "E6375", {"start": v(46.28, -15.95) * mm, "end": v(46.23, -15.92) * mm});
            skLineSegment(sketch, "E6376", {"start": v(46.23, -15.92) * mm, "end": v(46.18, -15.89) * mm});
            skLineSegment(sketch, "E6377", {"start": v(46.18, -15.89) * mm, "end": v(46.13, -15.85) * mm});
            skLineSegment(sketch, "E6378", {"start": v(46.13, -15.85) * mm, "end": v(46.09, -15.82) * mm});
            skLineSegment(sketch, "E6379", {"start": v(46.09, -15.82) * mm, "end": v(46.04, -15.79) * mm});
            skLineSegment(sketch, "E6380", {"start": v(46.04, -15.79) * mm, "end": v(46, -15.76) * mm});
            skLineSegment(sketch, "E6381", {"start": v(46, -15.76) * mm, "end": v(45.95, -15.73) * mm});
            skLineSegment(sketch, "E6382", {"start": v(45.95, -15.73) * mm, "end": v(46.04, -15.46) * mm});
            skLineSegment(sketch, "E6383", {"start": v(46.04, -15.46) * mm, "end": v(46.19, -15) * mm});
            skLineSegment(sketch, "E6384", {"start": v(46.19, -15) * mm, "end": v(46.28, -14.74) * mm});
            skLineSegment(sketch, "E6385", {"start": v(46.28, -14.74) * mm, "end": v(46.33, -14.75) * mm});
            skLineSegment(sketch, "E6386", {"start": v(46.33, -14.75) * mm, "end": v(46.39, -14.75) * mm});
            skLineSegment(sketch, "E6387", {"start": v(46.39, -14.75) * mm, "end": v(46.44, -14.75) * mm});
            skLineSegment(sketch, "E6388", {"start": v(46.44, -14.75) * mm, "end": v(46.5, -14.75) * mm});
            skLineSegment(sketch, "E6389", {"start": v(46.5, -14.75) * mm, "end": v(46.56, -14.75) * mm});
            skLineSegment(sketch, "E6390", {"start": v(46.56, -14.75) * mm, "end": v(46.61, -14.76) * mm});
            skLineSegment(sketch, "E6391", {"start": v(46.61, -14.76) * mm, "end": v(46.67, -14.76) * mm});
            skLineSegment(sketch, "E6392", {"start": v(46.67, -14.76) * mm, "end": v(46.73, -14.76) * mm});
            skLineSegment(sketch, "E6393", {"start": v(46.73, -14.76) * mm, "end": v(46.8, -14.76) * mm});
            skLineSegment(sketch, "E6394", {"start": v(46.8, -14.76) * mm, "end": v(46.86, -14.76) * mm});
            skLineSegment(sketch, "E6395", {"start": v(46.86, -14.76) * mm, "end": v(46.92, -14.76) * mm});
            skLineSegment(sketch, "E6396", {"start": v(46.92, -14.76) * mm, "end": v(46.98, -14.76) * mm});
            skLineSegment(sketch, "E6397", {"start": v(46.98, -14.76) * mm, "end": v(47.05, -14.76) * mm});
            skLineSegment(sketch, "E6398", {"start": v(47.05, -14.76) * mm, "end": v(47.12, -14.76) * mm});
            skLineSegment(sketch, "E6399", {"start": v(47.12, -14.76) * mm, "end": v(47.18, -14.76) * mm});
            skLineSegment(sketch, "E6400", {"start": v(47.18, -14.76) * mm, "end": v(47.25, -14.76) * mm});
            skLineSegment(sketch, "E6401", {"start": v(47.25, -14.76) * mm, "end": v(47.32, -14.76) * mm});
            skLineSegment(sketch, "E6402", {"start": v(47.32, -14.76) * mm, "end": v(47.39, -14.76) * mm});
            skLineSegment(sketch, "E6403", {"start": v(47.39, -14.76) * mm, "end": v(47.46, -14.75) * mm});
            skLineSegment(sketch, "E6404", {"start": v(47.46, -14.75) * mm, "end": v(47.53, -14.75) * mm});
            skLineSegment(sketch, "E6405", {"start": v(47.53, -14.75) * mm, "end": v(47.6, -14.75) * mm});
            skLineSegment(sketch, "E6406", {"start": v(47.6, -14.75) * mm, "end": v(47.67, -14.75) * mm});
            skLineSegment(sketch, "E6407", {"start": v(47.67, -14.75) * mm, "end": v(47.75, -14.74) * mm});
            skLineSegment(sketch, "E6408", {"start": v(47.75, -14.74) * mm, "end": v(47.82, -14.74) * mm});
            skLineSegment(sketch, "E6409", {"start": v(47.82, -14.74) * mm, "end": v(47.9, -14.73) * mm});
            skLineSegment(sketch, "E6410", {"start": v(47.9, -14.73) * mm, "end": v(47.97, -14.73) * mm});
            skLineSegment(sketch, "E6411", {"start": v(47.97, -14.73) * mm, "end": v(48.05, -14.72) * mm});
            skLineSegment(sketch, "E6412", {"start": v(48.05, -14.72) * mm, "end": v(48.13, -14.72) * mm});
            skLineSegment(sketch, "E6413", {"start": v(48.13, -14.72) * mm, "end": v(48.2, -14.71) * mm});
            skLineSegment(sketch, "E6414", {"start": v(48.2, -14.71) * mm, "end": v(48.29, -14.7) * mm});
            skLineSegment(sketch, "E6415", {"start": v(48.29, -14.7) * mm, "end": v(48.37, -14.7) * mm});
            skLineSegment(sketch, "E6416", {"start": v(48.37, -14.7) * mm, "end": v(48.45, -14.7) * mm});
            skLineSegment(sketch, "E6417", {"start": v(48.45, -14.7) * mm, "end": v(48.53, -14.69) * mm});
            skLineSegment(sketch, "E6418", {"start": v(48.53, -14.69) * mm, "end": v(48.62, -14.68) * mm});
            skLineSegment(sketch, "E6419", {"start": v(48.62, -14.68) * mm, "end": v(48.7, -14.67) * mm});
            skLineSegment(sketch, "E6420", {"start": v(48.7, -14.67) * mm, "end": v(48.78, -14.66) * mm});
            skLineSegment(sketch, "E6421", {"start": v(48.78, -14.66) * mm, "end": v(48.87, -14.65) * mm});
            skLineSegment(sketch, "E6422", {"start": v(48.87, -14.65) * mm, "end": v(48.96, -14.64) * mm});
            skLineSegment(sketch, "E6423", {"start": v(48.96, -14.64) * mm, "end": v(49.04, -14.63) * mm});
            skLineSegment(sketch, "E6424", {"start": v(49.04, -14.63) * mm, "end": v(49.12, -14.62) * mm});
            skLineSegment(sketch, "E6425", {"start": v(49.12, -14.62) * mm, "end": v(49.39, -13.7) * mm});
            skLineSegment(sketch, "E6426", {"start": v(49.39, -13.7) * mm, "end": v(49.33, -13.64) * mm});
            skLineSegment(sketch, "E6427", {"start": v(49.33, -13.64) * mm, "end": v(49.26, -13.58) * mm});
            skLineSegment(sketch, "E6428", {"start": v(49.26, -13.58) * mm, "end": v(49.2, -13.53) * mm});
            skLineSegment(sketch, "E6429", {"start": v(49.2, -13.53) * mm, "end": v(49.13, -13.47) * mm});
            skLineSegment(sketch, "E6430", {"start": v(49.13, -13.47) * mm, "end": v(49.06, -13.42) * mm});
            skLineSegment(sketch, "E6431", {"start": v(49.06, -13.42) * mm, "end": v(49, -13.37) * mm});
            skLineSegment(sketch, "E6432", {"start": v(49, -13.37) * mm, "end": v(48.92, -13.32) * mm});
            skLineSegment(sketch, "E6433", {"start": v(48.92, -13.32) * mm, "end": v(48.86, -13.27) * mm});
            skLineSegment(sketch, "E6434", {"start": v(48.86, -13.27) * mm, "end": v(48.8, -13.22) * mm});
            skLineSegment(sketch, "E6435", {"start": v(48.8, -13.22) * mm, "end": v(48.73, -13.17) * mm});
            skLineSegment(sketch, "E6436", {"start": v(48.73, -13.17) * mm, "end": v(48.66, -13.12) * mm});
            skLineSegment(sketch, "E6437", {"start": v(48.66, -13.12) * mm, "end": v(48.6, -13.08) * mm});
            skLineSegment(sketch, "E6438", {"start": v(48.6, -13.08) * mm, "end": v(48.54, -13.03) * mm});
            skLineSegment(sketch, "E6439", {"start": v(48.54, -13.03) * mm, "end": v(48.47, -12.99) * mm});
            skLineSegment(sketch, "E6440", {"start": v(48.47, -12.99) * mm, "end": v(48.41, -12.94) * mm});
            skLineSegment(sketch, "E6441", {"start": v(48.41, -12.94) * mm, "end": v(48.35, -12.9) * mm});
            skLineSegment(sketch, "E6442", {"start": v(48.35, -12.9) * mm, "end": v(48.29, -12.86) * mm});
            skLineSegment(sketch, "E6443", {"start": v(48.29, -12.86) * mm, "end": v(48.23, -12.81) * mm});
            skLineSegment(sketch, "E6444", {"start": v(48.23, -12.81) * mm, "end": v(48.17, -12.77) * mm});
            skLineSegment(sketch, "E6445", {"start": v(48.17, -12.77) * mm, "end": v(48.1, -12.73) * mm});
            skLineSegment(sketch, "E6446", {"start": v(48.1, -12.73) * mm, "end": v(48.05, -12.7) * mm});
            skLineSegment(sketch, "E6447", {"start": v(48.05, -12.7) * mm, "end": v(48, -12.65) * mm});
            skLineSegment(sketch, "E6448", {"start": v(48, -12.65) * mm, "end": v(47.93, -12.62) * mm});
            skLineSegment(sketch, "E6449", {"start": v(47.93, -12.62) * mm, "end": v(47.88, -12.58) * mm});
            skLineSegment(sketch, "E6450", {"start": v(47.88, -12.58) * mm, "end": v(47.82, -12.54) * mm});
            skLineSegment(sketch, "E6451", {"start": v(47.82, -12.54) * mm, "end": v(47.76, -12.5) * mm});
            skLineSegment(sketch, "E6452", {"start": v(47.76, -12.5) * mm, "end": v(47.7, -12.47) * mm});
            skLineSegment(sketch, "E6453", {"start": v(47.7, -12.47) * mm, "end": v(47.65, -12.44) * mm});
            skLineSegment(sketch, "E6454", {"start": v(47.65, -12.44) * mm, "end": v(47.6, -12.4) * mm});
            skLineSegment(sketch, "E6455", {"start": v(47.6, -12.4) * mm, "end": v(47.54, -12.37) * mm});
            skLineSegment(sketch, "E6456", {"start": v(47.54, -12.37) * mm, "end": v(47.5, -12.34) * mm});
            skLineSegment(sketch, "E6457", {"start": v(47.5, -12.34) * mm, "end": v(47.44, -12.3) * mm});
            skLineSegment(sketch, "E6458", {"start": v(47.44, -12.3) * mm, "end": v(47.39, -12.27) * mm});
            skLineSegment(sketch, "E6459", {"start": v(47.39, -12.27) * mm, "end": v(47.34, -12.24) * mm});
            skLineSegment(sketch, "E6460", {"start": v(47.34, -12.24) * mm, "end": v(47.29, -12.21) * mm});
            skLineSegment(sketch, "E6461", {"start": v(47.29, -12.21) * mm, "end": v(47.24, -12.18) * mm});
            skLineSegment(sketch, "E6462", {"start": v(47.24, -12.18) * mm, "end": v(47.19, -12.16) * mm});
            skLineSegment(sketch, "E6463", {"start": v(47.19, -12.16) * mm, "end": v(47.14, -12.13) * mm});
            skLineSegment(sketch, "E6464", {"start": v(47.14, -12.13) * mm, "end": v(47.1, -12.1) * mm});
            skLineSegment(sketch, "E6465", {"start": v(47.1, -12.1) * mm, "end": v(47.04, -12.07) * mm});
            skLineSegment(sketch, "E6466", {"start": v(47.04, -12.07) * mm, "end": v(47.1, -11.8) * mm});
            skLineSegment(sketch, "E6467", {"start": v(47.1, -11.8) * mm, "end": v(47.22, -11.34) * mm});
            skLineSegment(sketch, "E6468", {"start": v(47.22, -11.34) * mm, "end": v(47.3, -11.07) * mm});
            skLineSegment(sketch, "E6469", {"start": v(47.3, -11.07) * mm, "end": v(47.34, -11.06) * mm});
            skLineSegment(sketch, "E6470", {"start": v(47.34, -11.06) * mm, "end": v(47.4, -11.06) * mm});
            skLineSegment(sketch, "E6471", {"start": v(47.4, -11.06) * mm, "end": v(47.46, -11.06) * mm});
            skLineSegment(sketch, "E6472", {"start": v(47.46, -11.06) * mm, "end": v(47.51, -11.06) * mm});
            skLineSegment(sketch, "E6473", {"start": v(47.51, -11.06) * mm, "end": v(47.57, -11.06) * mm});
            skLineSegment(sketch, "E6474", {"start": v(47.57, -11.06) * mm, "end": v(47.63, -11.05) * mm});
            skLineSegment(sketch, "E6475", {"start": v(47.63, -11.05) * mm, "end": v(47.69, -11.05) * mm});
            skLineSegment(sketch, "E6476", {"start": v(47.69, -11.05) * mm, "end": v(47.75, -11.05) * mm});
            skLineSegment(sketch, "E6477", {"start": v(47.75, -11.05) * mm, "end": v(47.8, -11.04) * mm});
            skLineSegment(sketch, "E6478", {"start": v(47.8, -11.04) * mm, "end": v(47.87, -11.04) * mm});
            skLineSegment(sketch, "E6479", {"start": v(47.87, -11.04) * mm, "end": v(47.93, -11.03) * mm});
            skLineSegment(sketch, "E6480", {"start": v(47.93, -11.03) * mm, "end": v(48, -11.03) * mm});
            skLineSegment(sketch, "E6481", {"start": v(48, -11.03) * mm, "end": v(48.06, -11.02) * mm});
            skLineSegment(sketch, "E6482", {"start": v(48.06, -11.02) * mm, "end": v(48.13, -11.02) * mm});
            skLineSegment(sketch, "E6483", {"start": v(48.13, -11.02) * mm, "end": v(48.2, -11.01) * mm});
            skLineSegment(sketch, "E6484", {"start": v(48.2, -11.01) * mm, "end": v(48.26, -11) * mm});
            skLineSegment(sketch, "E6485", {"start": v(48.26, -11) * mm, "end": v(48.33, -11) * mm});
            skLineSegment(sketch, "E6486", {"start": v(48.33, -11) * mm, "end": v(48.4, -11) * mm});
            skLineSegment(sketch, "E6487", {"start": v(48.4, -11) * mm, "end": v(48.47, -10.98) * mm});
            skLineSegment(sketch, "E6488", {"start": v(48.47, -10.98) * mm, "end": v(48.54, -10.98) * mm});
            skLineSegment(sketch, "E6489", {"start": v(48.54, -10.98) * mm, "end": v(48.61, -10.97) * mm});
            skLineSegment(sketch, "E6490", {"start": v(48.61, -10.97) * mm, "end": v(48.68, -10.96) * mm});
            skLineSegment(sketch, "E6491", {"start": v(48.68, -10.96) * mm, "end": v(48.76, -10.95) * mm});
            skLineSegment(sketch, "E6492", {"start": v(48.76, -10.95) * mm, "end": v(48.83, -10.94) * mm});
            skLineSegment(sketch, "E6493", {"start": v(48.83, -10.94) * mm, "end": v(48.9, -10.93) * mm});
            skLineSegment(sketch, "E6494", {"start": v(48.9, -10.93) * mm, "end": v(48.98, -10.92) * mm});
            skLineSegment(sketch, "E6495", {"start": v(48.98, -10.92) * mm, "end": v(49.06, -10.9) * mm});
            skLineSegment(sketch, "E6496", {"start": v(49.06, -10.9) * mm, "end": v(49.14, -10.9) * mm});
            skLineSegment(sketch, "E6497", {"start": v(49.14, -10.9) * mm, "end": v(49.21, -10.89) * mm});
            skLineSegment(sketch, "E6498", {"start": v(49.21, -10.89) * mm, "end": v(49.3, -10.87) * mm});
            skLineSegment(sketch, "E6499", {"start": v(49.3, -10.87) * mm, "end": v(49.37, -10.86) * mm});
            skLineSegment(sketch, "E6500", {"start": v(49.37, -10.86) * mm, "end": v(49.45, -10.85) * mm});
            skLineSegment(sketch, "E6501", {"start": v(49.45, -10.85) * mm, "end": v(49.53, -10.83) * mm});
            skLineSegment(sketch, "E6502", {"start": v(49.53, -10.83) * mm, "end": v(49.62, -10.82) * mm});
            skLineSegment(sketch, "E6503", {"start": v(49.62, -10.82) * mm, "end": v(49.7, -10.8) * mm});
            skLineSegment(sketch, "E6504", {"start": v(49.7, -10.8) * mm, "end": v(49.78, -10.79) * mm});
            skLineSegment(sketch, "E6505", {"start": v(49.78, -10.79) * mm, "end": v(49.87, -10.77) * mm});
            skLineSegment(sketch, "E6506", {"start": v(49.87, -10.77) * mm, "end": v(49.95, -10.76) * mm});
            skLineSegment(sketch, "E6507", {"start": v(49.95, -10.76) * mm, "end": v(50.04, -10.74) * mm});
            skLineSegment(sketch, "E6508", {"start": v(50.04, -10.74) * mm, "end": v(50.12, -10.72) * mm});
            skLineSegment(sketch, "E6509", {"start": v(50.12, -10.72) * mm, "end": v(50.3, -9.77) * mm});
            skLineSegment(sketch, "E6510", {"start": v(50.3, -9.77) * mm, "end": v(50.25, -9.72) * mm});
            skLineSegment(sketch, "E6511", {"start": v(50.25, -9.72) * mm, "end": v(50.18, -9.68) * mm});
            skLineSegment(sketch, "E6512", {"start": v(50.18, -9.68) * mm, "end": v(50.1, -9.63) * mm});
            skLineSegment(sketch, "E6513", {"start": v(50.1, -9.63) * mm, "end": v(50.03, -9.58) * mm});
            skLineSegment(sketch, "E6514", {"start": v(50.03, -9.58) * mm, "end": v(49.96, -9.53) * mm});
            skLineSegment(sketch, "E6515", {"start": v(49.96, -9.53) * mm, "end": v(49.89, -9.49) * mm});
            skLineSegment(sketch, "E6516", {"start": v(49.89, -9.49) * mm, "end": v(49.82, -9.44) * mm});
            skLineSegment(sketch, "E6517", {"start": v(49.82, -9.44) * mm, "end": v(49.75, -9.4) * mm});
            skLineSegment(sketch, "E6518", {"start": v(49.75, -9.4) * mm, "end": v(49.68, -9.35) * mm});
            skLineSegment(sketch, "E6519", {"start": v(49.68, -9.35) * mm, "end": v(49.61, -9.3) * mm});
            skLineSegment(sketch, "E6520", {"start": v(49.61, -9.3) * mm, "end": v(49.54, -9.27) * mm});
            skLineSegment(sketch, "E6521", {"start": v(49.54, -9.27) * mm, "end": v(49.48, -9.22) * mm});
            skLineSegment(sketch, "E6522", {"start": v(49.48, -9.22) * mm, "end": v(49.4, -9.18) * mm});
            skLineSegment(sketch, "E6523", {"start": v(49.4, -9.18) * mm, "end": v(49.34, -9.14) * mm});
            skLineSegment(sketch, "E6524", {"start": v(49.34, -9.14) * mm, "end": v(49.28, -9.1) * mm});
            skLineSegment(sketch, "E6525", {"start": v(49.28, -9.1) * mm, "end": v(49.21, -9.07) * mm});
            skLineSegment(sketch, "E6526", {"start": v(49.21, -9.07) * mm, "end": v(49.15, -9.03) * mm});
            skLineSegment(sketch, "E6527", {"start": v(49.15, -9.03) * mm, "end": v(49.08, -9) * mm});
            skLineSegment(sketch, "E6528", {"start": v(49.08, -9) * mm, "end": v(49.02, -8.95) * mm});
            skLineSegment(sketch, "E6529", {"start": v(49.02, -8.95) * mm, "end": v(48.96, -8.92) * mm});
            skLineSegment(sketch, "E6530", {"start": v(48.96, -8.92) * mm, "end": v(48.9, -8.88) * mm});
            skLineSegment(sketch, "E6531", {"start": v(48.9, -8.88) * mm, "end": v(48.84, -8.85) * mm});
            skLineSegment(sketch, "E6532", {"start": v(48.84, -8.85) * mm, "end": v(48.78, -8.82) * mm});
            skLineSegment(sketch, "E6533", {"start": v(48.78, -8.82) * mm, "end": v(48.72, -8.78) * mm});
            skLineSegment(sketch, "E6534", {"start": v(48.72, -8.78) * mm, "end": v(48.66, -8.75) * mm});
            skLineSegment(sketch, "E6535", {"start": v(48.66, -8.75) * mm, "end": v(48.6, -8.72) * mm});
            skLineSegment(sketch, "E6536", {"start": v(48.6, -8.72) * mm, "end": v(48.54, -8.69) * mm});
            skLineSegment(sketch, "E6537", {"start": v(48.54, -8.69) * mm, "end": v(48.48, -8.66) * mm});
            skLineSegment(sketch, "E6538", {"start": v(48.48, -8.66) * mm, "end": v(48.42, -8.63) * mm});
            skLineSegment(sketch, "E6539", {"start": v(48.42, -8.63) * mm, "end": v(48.37, -8.6) * mm});
            skLineSegment(sketch, "E6540", {"start": v(48.37, -8.6) * mm, "end": v(48.31, -8.57) * mm});
            skLineSegment(sketch, "E6541", {"start": v(48.31, -8.57) * mm, "end": v(48.26, -8.54) * mm});
            skLineSegment(sketch, "E6542", {"start": v(48.26, -8.54) * mm, "end": v(48.2, -8.52) * mm});
            skLineSegment(sketch, "E6543", {"start": v(48.2, -8.52) * mm, "end": v(48.15, -8.5) * mm});
            skLineSegment(sketch, "E6544", {"start": v(48.15, -8.5) * mm, "end": v(48.1, -8.47) * mm});
            skLineSegment(sketch, "E6545", {"start": v(48.1, -8.47) * mm, "end": v(48.05, -8.44) * mm});
            skLineSegment(sketch, "E6546", {"start": v(48.05, -8.44) * mm, "end": v(48, -8.42) * mm});
            skLineSegment(sketch, "E6547", {"start": v(48, -8.42) * mm, "end": v(47.94, -8.4) * mm});
            skLineSegment(sketch, "E6548", {"start": v(47.94, -8.4) * mm, "end": v(47.9, -8.37) * mm});
            skLineSegment(sketch, "E6549", {"start": v(47.9, -8.37) * mm, "end": v(47.85, -8.35) * mm});
            skLineSegment(sketch, "E6550", {"start": v(47.85, -8.35) * mm, "end": v(47.89, -8.07) * mm});
            skLineSegment(sketch, "E6551", {"start": v(47.89, -8.07) * mm, "end": v(47.96, -7.6) * mm});
            skLineSegment(sketch, "E6552", {"start": v(47.96, -7.6) * mm, "end": v(48.01, -7.32) * mm});
            skLineSegment(sketch, "E6553", {"start": v(48.01, -7.32) * mm, "end": v(48.07, -7.32) * mm});
            skLineSegment(sketch, "E6554", {"start": v(48.07, -7.32) * mm, "end": v(48.12, -7.31) * mm});
            skLineSegment(sketch, "E6555", {"start": v(48.12, -7.31) * mm, "end": v(48.18, -7.3) * mm});
            skLineSegment(sketch, "E6556", {"start": v(48.18, -7.3) * mm, "end": v(48.23, -7.3) * mm});
            skLineSegment(sketch, "E6557", {"start": v(48.23, -7.3) * mm, "end": v(48.3, -7.29) * mm});
            skLineSegment(sketch, "E6558", {"start": v(48.3, -7.29) * mm, "end": v(48.35, -7.28) * mm});
            skLineSegment(sketch, "E6559", {"start": v(48.35, -7.28) * mm, "end": v(48.4, -7.27) * mm});
            skLineSegment(sketch, "E6560", {"start": v(48.4, -7.27) * mm, "end": v(48.47, -7.27) * mm});
            skLineSegment(sketch, "E6561", {"start": v(48.47, -7.27) * mm, "end": v(48.53, -7.26) * mm});
            skLineSegment(sketch, "E6562", {"start": v(48.53, -7.26) * mm, "end": v(48.59, -7.25) * mm});
            skLineSegment(sketch, "E6563", {"start": v(48.59, -7.25) * mm, "end": v(48.65, -7.24) * mm});
            skLineSegment(sketch, "E6564", {"start": v(48.65, -7.24) * mm, "end": v(48.72, -7.23) * mm});
            skLineSegment(sketch, "E6565", {"start": v(48.72, -7.23) * mm, "end": v(48.78, -7.22) * mm});
            skLineSegment(sketch, "E6566", {"start": v(48.78, -7.22) * mm, "end": v(48.84, -7.2) * mm});
            skLineSegment(sketch, "E6567", {"start": v(48.84, -7.2) * mm, "end": v(48.9, -7.2) * mm});
            skLineSegment(sketch, "E6568", {"start": v(48.9, -7.2) * mm, "end": v(48.98, -7.19) * mm});
            skLineSegment(sketch, "E6569", {"start": v(48.98, -7.19) * mm, "end": v(49.04, -7.17) * mm});
            skLineSegment(sketch, "E6570", {"start": v(49.04, -7.17) * mm, "end": v(49.11, -7.16) * mm});
            skLineSegment(sketch, "E6571", {"start": v(49.11, -7.16) * mm, "end": v(49.18, -7.15) * mm});
            skLineSegment(sketch, "E6572", {"start": v(49.18, -7.15) * mm, "end": v(49.25, -7.13) * mm});
            skLineSegment(sketch, "E6573", {"start": v(49.25, -7.13) * mm, "end": v(49.32, -7.12) * mm});
            skLineSegment(sketch, "E6574", {"start": v(49.32, -7.12) * mm, "end": v(49.4, -7.1) * mm});
            skLineSegment(sketch, "E6575", {"start": v(49.4, -7.1) * mm, "end": v(49.47, -7.1) * mm});
            skLineSegment(sketch, "E6576", {"start": v(49.47, -7.1) * mm, "end": v(49.54, -7.08) * mm});
            skLineSegment(sketch, "E6577", {"start": v(49.54, -7.08) * mm, "end": v(49.61, -7.06) * mm});
            skLineSegment(sketch, "E6578", {"start": v(49.61, -7.06) * mm, "end": v(49.69, -7.04) * mm});
            skLineSegment(sketch, "E6579", {"start": v(49.69, -7.04) * mm, "end": v(49.76, -7.03) * mm});
            skLineSegment(sketch, "E6580", {"start": v(49.76, -7.03) * mm, "end": v(49.84, -7) * mm});
            skLineSegment(sketch, "E6581", {"start": v(49.84, -7) * mm, "end": v(49.92, -7) * mm});
            skLineSegment(sketch, "E6582", {"start": v(49.92, -7) * mm, "end": v(50, -6.97) * mm});
            skLineSegment(sketch, "E6583", {"start": v(50, -6.97) * mm, "end": v(50.07, -6.95) * mm});
            skLineSegment(sketch, "E6584", {"start": v(50.07, -6.95) * mm, "end": v(50.15, -6.93) * mm});
            skLineSegment(sketch, "E6585", {"start": v(50.15, -6.93) * mm, "end": v(50.23, -6.91) * mm});
            skLineSegment(sketch, "E6586", {"start": v(50.23, -6.91) * mm, "end": v(50.31, -6.9) * mm});
            skLineSegment(sketch, "E6587", {"start": v(50.31, -6.9) * mm, "end": v(50.4, -6.87) * mm});
            skLineSegment(sketch, "E6588", {"start": v(50.4, -6.87) * mm, "end": v(50.48, -6.85) * mm});
            skLineSegment(sketch, "E6589", {"start": v(50.48, -6.85) * mm, "end": v(50.56, -6.83) * mm});
            skLineSegment(sketch, "E6590", {"start": v(50.56, -6.83) * mm, "end": v(50.64, -6.8) * mm});
            skLineSegment(sketch, "E6591", {"start": v(50.64, -6.8) * mm, "end": v(50.73, -6.78) * mm});
            skLineSegment(sketch, "E6592", {"start": v(50.73, -6.78) * mm, "end": v(50.8, -6.75) * mm});
            skLineSegment(sketch, "E6593", {"start": v(50.8, -6.75) * mm, "end": v(50.92, -5.8) * mm});
            skLineSegment(sketch, "E6594", {"start": v(50.92, -5.8) * mm, "end": v(50.86, -5.75) * mm});
            skLineSegment(sketch, "E6595", {"start": v(50.86, -5.75) * mm, "end": v(50.78, -5.7) * mm});
            skLineSegment(sketch, "E6596", {"start": v(50.78, -5.7) * mm, "end": v(50.7, -5.67) * mm});
            skLineSegment(sketch, "E6597", {"start": v(50.7, -5.67) * mm, "end": v(50.63, -5.62) * mm});
            skLineSegment(sketch, "E6598", {"start": v(50.63, -5.62) * mm, "end": v(50.55, -5.58) * mm});
            skLineSegment(sketch, "E6599", {"start": v(50.55, -5.58) * mm, "end": v(50.48, -5.54) * mm});
            skLineSegment(sketch, "E6600", {"start": v(50.48, -5.54) * mm, "end": v(50.4, -5.5) * mm});
            skLineSegment(sketch, "E6601", {"start": v(50.4, -5.5) * mm, "end": v(50.33, -5.46) * mm});
            skLineSegment(sketch, "E6602", {"start": v(50.33, -5.46) * mm, "end": v(50.26, -5.42) * mm});
            skLineSegment(sketch, "E6603", {"start": v(50.26, -5.42) * mm, "end": v(50.19, -5.39) * mm});
            skLineSegment(sketch, "E6604", {"start": v(50.19, -5.39) * mm, "end": v(50.12, -5.35) * mm});
            skLineSegment(sketch, "E6605", {"start": v(50.12, -5.35) * mm, "end": v(50.05, -5.31) * mm});
            skLineSegment(sketch, "E6606", {"start": v(50.05, -5.31) * mm, "end": v(49.98, -5.28) * mm});
            skLineSegment(sketch, "E6607", {"start": v(49.98, -5.28) * mm, "end": v(49.9, -5.24) * mm});
            skLineSegment(sketch, "E6608", {"start": v(49.9, -5.24) * mm, "end": v(49.84, -5.2) * mm});
            skLineSegment(sketch, "E6609", {"start": v(49.84, -5.2) * mm, "end": v(49.77, -5.18) * mm});
            skLineSegment(sketch, "E6610", {"start": v(49.77, -5.18) * mm, "end": v(49.7, -5.14) * mm});
            skLineSegment(sketch, "E6611", {"start": v(49.7, -5.14) * mm, "end": v(49.64, -5.11) * mm});
            skLineSegment(sketch, "E6612", {"start": v(49.64, -5.11) * mm, "end": v(49.57, -5.08) * mm});
            skLineSegment(sketch, "E6613", {"start": v(49.57, -5.08) * mm, "end": v(49.5, -5.05) * mm});
            skLineSegment(sketch, "E6614", {"start": v(49.5, -5.05) * mm, "end": v(49.44, -5.02) * mm});
            skLineSegment(sketch, "E6615", {"start": v(49.44, -5.02) * mm, "end": v(49.38, -5) * mm});
            skLineSegment(sketch, "E6616", {"start": v(49.38, -5) * mm, "end": v(49.32, -4.96) * mm});
            skLineSegment(sketch, "E6617", {"start": v(49.32, -4.96) * mm, "end": v(49.25, -4.93) * mm});
            skLineSegment(sketch, "E6618", {"start": v(49.25, -4.93) * mm, "end": v(49.2, -4.9) * mm});
            skLineSegment(sketch, "E6619", {"start": v(49.2, -4.9) * mm, "end": v(49.13, -4.88) * mm});
            skLineSegment(sketch, "E6620", {"start": v(49.13, -4.88) * mm, "end": v(49.07, -4.85) * mm});
            skLineSegment(sketch, "E6621", {"start": v(49.07, -4.85) * mm, "end": v(49.01, -4.83) * mm});
            skLineSegment(sketch, "E6622", {"start": v(49.01, -4.83) * mm, "end": v(48.95, -4.8) * mm});
            skLineSegment(sketch, "E6623", {"start": v(48.95, -4.8) * mm, "end": v(48.9, -4.78) * mm});
            skLineSegment(sketch, "E6624", {"start": v(48.9, -4.78) * mm, "end": v(48.84, -4.75) * mm});
            skLineSegment(sketch, "E6625", {"start": v(48.84, -4.75) * mm, "end": v(48.78, -4.73) * mm});
            skLineSegment(sketch, "E6626", {"start": v(48.78, -4.73) * mm, "end": v(48.72, -4.7) * mm});
            skLineSegment(sketch, "E6627", {"start": v(48.72, -4.7) * mm, "end": v(48.67, -4.69) * mm});
            skLineSegment(sketch, "E6628", {"start": v(48.67, -4.69) * mm, "end": v(48.61, -4.67) * mm});
            skLineSegment(sketch, "E6629", {"start": v(48.61, -4.67) * mm, "end": v(48.56, -4.64) * mm});
            skLineSegment(sketch, "E6630", {"start": v(48.56, -4.64) * mm, "end": v(48.5, -4.62) * mm});
            skLineSegment(sketch, "E6631", {"start": v(48.5, -4.62) * mm, "end": v(48.46, -4.6) * mm});
            skLineSegment(sketch, "E6632", {"start": v(48.46, -4.6) * mm, "end": v(48.4, -4.59) * mm});
            skLineSegment(sketch, "E6633", {"start": v(48.4, -4.59) * mm, "end": v(48.35, -4.57) * mm});
            skLineSegment(sketch, "E6634", {"start": v(48.35, -4.57) * mm, "end": v(48.37, -4.29) * mm});
            skLineSegment(sketch, "E6635", {"start": v(48.37, -4.29) * mm, "end": v(48.41, -3.81) * mm});
            skLineSegment(sketch, "E6636", {"start": v(48.41, -3.81) * mm, "end": v(48.44, -3.53) * mm});
            skLineSegment(sketch, "E6637", {"start": v(48.44, -3.53) * mm, "end": v(48.5, -3.52) * mm});
            skLineSegment(sketch, "E6638", {"start": v(48.5, -3.52) * mm, "end": v(48.55, -3.51) * mm});
            skLineSegment(sketch, "E6639", {"start": v(48.55, -3.51) * mm, "end": v(48.6, -3.5) * mm});
            skLineSegment(sketch, "E6640", {"start": v(48.6, -3.5) * mm, "end": v(48.66, -3.49) * mm});
            skLineSegment(sketch, "E6641", {"start": v(48.66, -3.49) * mm, "end": v(48.71, -3.48) * mm});
            skLineSegment(sketch, "E6642", {"start": v(48.71, -3.48) * mm, "end": v(48.77, -3.47) * mm});
            skLineSegment(sketch, "E6643", {"start": v(48.77, -3.47) * mm, "end": v(48.83, -3.45) * mm});
            skLineSegment(sketch, "E6644", {"start": v(48.83, -3.45) * mm, "end": v(48.89, -3.44) * mm});
            skLineSegment(sketch, "E6645", {"start": v(48.89, -3.44) * mm, "end": v(48.95, -3.43) * mm});
            skLineSegment(sketch, "E6646", {"start": v(48.95, -3.43) * mm, "end": v(49, -3.41) * mm});
            skLineSegment(sketch, "E6647", {"start": v(49, -3.41) * mm, "end": v(49.07, -3.4) * mm});
            skLineSegment(sketch, "E6648", {"start": v(49.07, -3.4) * mm, "end": v(49.13, -3.38) * mm});
            skLineSegment(sketch, "E6649", {"start": v(49.13, -3.38) * mm, "end": v(49.2, -3.37) * mm});
            skLineSegment(sketch, "E6650", {"start": v(49.2, -3.37) * mm, "end": v(49.26, -3.35) * mm});
            skLineSegment(sketch, "E6651", {"start": v(49.26, -3.35) * mm, "end": v(49.32, -3.34) * mm});
            skLineSegment(sketch, "E6652", {"start": v(49.32, -3.34) * mm, "end": v(49.39, -3.32) * mm});
            skLineSegment(sketch, "E6653", {"start": v(49.39, -3.32) * mm, "end": v(49.46, -3.3) * mm});
            skLineSegment(sketch, "E6654", {"start": v(49.46, -3.3) * mm, "end": v(49.52, -3.29) * mm});
            skLineSegment(sketch, "E6655", {"start": v(49.52, -3.29) * mm, "end": v(49.6, -3.27) * mm});
            skLineSegment(sketch, "E6656", {"start": v(49.6, -3.27) * mm, "end": v(49.66, -3.25) * mm});
            skLineSegment(sketch, "E6657", {"start": v(49.66, -3.25) * mm, "end": v(49.73, -3.23) * mm});
            skLineSegment(sketch, "E6658", {"start": v(49.73, -3.23) * mm, "end": v(49.8, -3.2) * mm});
            skLineSegment(sketch, "E6659", {"start": v(49.8, -3.2) * mm, "end": v(49.87, -3.19) * mm});
            skLineSegment(sketch, "E6660", {"start": v(49.87, -3.19) * mm, "end": v(49.94, -3.17) * mm});
            skLineSegment(sketch, "E6661", {"start": v(49.94, -3.17) * mm, "end": v(50.01, -3.15) * mm});
            skLineSegment(sketch, "E6662", {"start": v(50.01, -3.15) * mm, "end": v(50.09, -3.12) * mm});
            skLineSegment(sketch, "E6663", {"start": v(50.09, -3.12) * mm, "end": v(50.16, -3.1) * mm});
            skLineSegment(sketch, "E6664", {"start": v(50.16, -3.1) * mm, "end": v(50.24, -3.08) * mm});
            skLineSegment(sketch, "E6665", {"start": v(50.24, -3.08) * mm, "end": v(50.31, -3.05) * mm});
            skLineSegment(sketch, "E6666", {"start": v(50.31, -3.05) * mm, "end": v(50.39, -3.03) * mm});
            skLineSegment(sketch, "E6667", {"start": v(50.39, -3.03) * mm, "end": v(50.46, -3) * mm});
            skLineSegment(sketch, "E6668", {"start": v(50.46, -3) * mm, "end": v(50.54, -2.98) * mm});
            skLineSegment(sketch, "E6669", {"start": v(50.54, -2.98) * mm, "end": v(50.62, -2.95) * mm});
            skLineSegment(sketch, "E6670", {"start": v(50.62, -2.95) * mm, "end": v(50.7, -2.92) * mm});
            skLineSegment(sketch, "E6671", {"start": v(50.7, -2.92) * mm, "end": v(50.78, -2.9) * mm});
            skLineSegment(sketch, "E6672", {"start": v(50.78, -2.9) * mm, "end": v(50.86, -2.87) * mm});
            skLineSegment(sketch, "E6673", {"start": v(50.86, -2.87) * mm, "end": v(50.94, -2.84) * mm});
            skLineSegment(sketch, "E6674", {"start": v(50.94, -2.84) * mm, "end": v(51.02, -2.8) * mm});
            skLineSegment(sketch, "E6675", {"start": v(51.02, -2.8) * mm, "end": v(51.1, -2.78) * mm});
            skLineSegment(sketch, "E6676", {"start": v(51.1, -2.78) * mm, "end": v(51.18, -2.75) * mm});
            skLineSegment(sketch, "E6677", {"start": v(51.18, -2.75) * mm, "end": v(51.22, -1.78) * mm});
            skLineSegment(sketch, "E6678", {"start": v(51.22, -1.78) * mm, "end": v(51.15, -1.74) * mm});
            skLineSegment(sketch, "E6679", {"start": v(51.15, -1.74) * mm, "end": v(51.07, -1.7) * mm});
            skLineSegment(sketch, "E6680", {"start": v(51.07, -1.7) * mm, "end": v(51, -1.67) * mm});
            skLineSegment(sketch, "E6681", {"start": v(51, -1.67) * mm, "end": v(50.91, -1.63) * mm});
            skLineSegment(sketch, "E6682", {"start": v(50.91, -1.63) * mm, "end": v(50.84, -1.6) * mm});
            skLineSegment(sketch, "E6683", {"start": v(50.84, -1.6) * mm, "end": v(50.76, -1.56) * mm});
            skLineSegment(sketch, "E6684", {"start": v(50.76, -1.56) * mm, "end": v(50.68, -1.53) * mm});
            skLineSegment(sketch, "E6685", {"start": v(50.68, -1.53) * mm, "end": v(50.6, -1.5) * mm});
            skLineSegment(sketch, "E6686", {"start": v(50.6, -1.5) * mm, "end": v(50.53, -1.46) * mm});
            skLineSegment(sketch, "E6687", {"start": v(50.53, -1.46) * mm, "end": v(50.46, -1.43) * mm});
            skLineSegment(sketch, "E6688", {"start": v(50.46, -1.43) * mm, "end": v(50.38, -1.4) * mm});
            skLineSegment(sketch, "E6689", {"start": v(50.38, -1.4) * mm, "end": v(50.31, -1.37) * mm});
            skLineSegment(sketch, "E6690", {"start": v(50.31, -1.37) * mm, "end": v(50.24, -1.34) * mm});
            skLineSegment(sketch, "E6691", {"start": v(50.24, -1.34) * mm, "end": v(50.17, -1.31) * mm});
            skLineSegment(sketch, "E6692", {"start": v(50.17, -1.31) * mm, "end": v(50.1, -1.28) * mm});
            skLineSegment(sketch, "E6693", {"start": v(50.1, -1.28) * mm, "end": v(50.03, -1.26) * mm});
            skLineSegment(sketch, "E6694", {"start": v(50.03, -1.26) * mm, "end": v(49.96, -1.23) * mm});
            skLineSegment(sketch, "E6695", {"start": v(49.96, -1.23) * mm, "end": v(49.89, -1.2) * mm});
            skLineSegment(sketch, "E6696", {"start": v(49.89, -1.2) * mm, "end": v(49.82, -1.18) * mm});
            skLineSegment(sketch, "E6697", {"start": v(49.82, -1.18) * mm, "end": v(49.75, -1.15) * mm});
            skLineSegment(sketch, "E6698", {"start": v(49.75, -1.15) * mm, "end": v(49.68, -1.12) * mm});
            skLineSegment(sketch, "E6699", {"start": v(49.68, -1.12) * mm, "end": v(49.62, -1.1) * mm});
            skLineSegment(sketch, "E6700", {"start": v(49.62, -1.1) * mm, "end": v(49.55, -1.08) * mm});
            skLineSegment(sketch, "E6701", {"start": v(49.55, -1.08) * mm, "end": v(49.49, -1.05) * mm});
            skLineSegment(sketch, "E6702", {"start": v(49.49, -1.05) * mm, "end": v(49.43, -1.03) * mm});
            skLineSegment(sketch, "E6703", {"start": v(49.43, -1.03) * mm, "end": v(49.36, -1) * mm});
            skLineSegment(sketch, "E6704", {"start": v(49.36, -1) * mm, "end": v(49.3, -0.99) * mm});
            skLineSegment(sketch, "E6705", {"start": v(49.3, -0.99) * mm, "end": v(49.24, -0.97) * mm});
            skLineSegment(sketch, "E6706", {"start": v(49.24, -0.97) * mm, "end": v(49.18, -0.95) * mm});
            skLineSegment(sketch, "E6707", {"start": v(49.18, -0.95) * mm, "end": v(49.12, -0.93) * mm});
            skLineSegment(sketch, "E6708", {"start": v(49.12, -0.93) * mm, "end": v(49.06, -0.9) * mm});
            skLineSegment(sketch, "E6709", {"start": v(49.06, -0.9) * mm, "end": v(49, -0.89) * mm});
            skLineSegment(sketch, "E6710", {"start": v(49, -0.89) * mm, "end": v(48.94, -0.87) * mm});
            skLineSegment(sketch, "E6711", {"start": v(48.94, -0.87) * mm, "end": v(48.89, -0.85) * mm});
            skLineSegment(sketch, "E6712", {"start": v(48.89, -0.85) * mm, "end": v(48.83, -0.84) * mm});
            skLineSegment(sketch, "E6713", {"start": v(48.83, -0.84) * mm, "end": v(48.78, -0.82) * mm});
            skLineSegment(sketch, "E6714", {"start": v(48.78, -0.82) * mm, "end": v(48.72, -0.8) * mm});
            skLineSegment(sketch, "E6715", {"start": v(48.72, -0.8) * mm, "end": v(48.67, -0.79) * mm});
            skLineSegment(sketch, "E6716", {"start": v(48.67, -0.79) * mm, "end": v(48.61, -0.77) * mm});
            skLineSegment(sketch, "E6717", {"start": v(48.61, -0.77) * mm, "end": v(48.56, -0.76) * mm});
            skLineSegment(sketch, "E6718", {"start": v(48.56, -0.76) * mm, "end": v(48.56, -0.48) * mm});
            skLineSegment(sketch, "E6719", {"start": v(48.56, -0.48) * mm, "end": v(48.56, 0) * mm});
            skSolve(sketch);
        }
        {
            var Q0;
            Q0 = qSketchRegion(id + "F0", true);
            extrude(context, id + "F1", {"entities" : qUnion([Q0]), "depth" : 9 * mm});
        }
        {
            var Q0;
            Q0=qCreatedBy(makeId("Top.planeOp"),FACE);
            var sketch = newSketch(context, id + "F2", { "sketchPlane" : qUnion([Q0])});
            skCircle(sketch, "E6720", {"center": v(0, 0) * mm, "radius": 0.95 * mm});
            skSolve(sketch);
        }
        {
            var Q0;
            Q0 = qSketchRegion(id + "F2", true);
            extrude(context, id + "F3", {"entities" : qUnion([Q0]), "operationType" : NewBodyOperationType.REMOVE, "endBound" : BoundingType.THROUGH_ALL, "depth" : 25 * mm});
        }
        {
            var Q0;
            Q0=makeQuery(id+"F1.opExtrude","CAP_FACE",FACE,{"disambiguationData":[OSD([sQuery(id+"F0.wireOp",EDGE,"E0"),sQuery(id+"F0.wireOp",EDGE,"E1"),sQuery(id+"F0.wireOp",EDGE,"E2"),sQuery(id+"F0.wireOp",EDGE,"E3"),sQuery(id+"F0.wireOp",EDGE,"E4"),sQuery(id+"F0.wireOp",EDGE,"E5"),sQuery(id+"F0.wireOp",EDGE,"E6"),sQuery(id+"F0.wireOp",EDGE,"E7"),sQuery(id+"F0.wireOp",EDGE,"E8"),sQuery(id+"F0.wireOp",EDGE,"E9"),sQuery(id+"F0.wireOp",EDGE,"E10"),sQuery(id+"F0.wireOp",EDGE,"E11"),sQuery(id+"F0.wireOp",EDGE,"E12"),sQuery(id+"F0.wireOp",EDGE,"E13"),sQuery(id+"F0.wireOp",EDGE,"E14"),sQuery(id+"F0.wireOp",EDGE,"E15"),sQuery(id+"F0.wireOp",EDGE,"E16"),sQuery(id+"F0.wireOp",EDGE,"E17"),sQuery(id+"F0.wireOp",EDGE,"E18"),sQuery(id+"F0.wireOp",EDGE,"E19"),sQuery(id+"F0.wireOp",EDGE,"E20"),sQuery(id+"F0.wireOp",EDGE,"E21"),sQuery(id+"F0.wireOp",EDGE,"E22"),sQuery(id+"F0.wireOp",EDGE,"E23"),sQuery(id+"F0.wireOp",EDGE,"E24"),sQuery(id+"F0.wireOp",EDGE,"E25"),sQuery(id+"F0.wireOp",EDGE,"E26"),sQuery(id+"F0.wireOp",EDGE,"E27"),sQuery(id+"F0.wireOp",EDGE,"E28"),sQuery(id+"F0.wireOp",EDGE,"E29"),sQuery(id+"F0.wireOp",EDGE,"E30"),sQuery(id+"F0.wireOp",EDGE,"E31"),sQuery(id+"F0.wireOp",EDGE,"E32"),sQuery(id+"F0.wireOp",EDGE,"E33"),sQuery(id+"F0.wireOp",EDGE,"E34"),sQuery(id+"F0.wireOp",EDGE,"E35"),sQuery(id+"F0.wireOp",EDGE,"E36"),sQuery(id+"F0.wireOp",EDGE,"E37"),sQuery(id+"F0.wireOp",EDGE,"E38"),sQuery(id+"F0.wireOp",EDGE,"E39"),sQuery(id+"F0.wireOp",EDGE,"E40"),sQuery(id+"F0.wireOp",EDGE,"E41"),sQuery(id+"F0.wireOp",EDGE,"E42"),sQuery(id+"F0.wireOp",EDGE,"E43"),sQuery(id+"F0.wireOp",EDGE,"E44"),sQuery(id+"F0.wireOp",EDGE,"E45"),sQuery(id+"F0.wireOp",EDGE,"E46"),sQuery(id+"F0.wireOp",EDGE,"E47"),sQuery(id+"F0.wireOp",EDGE,"E48"),sQuery(id+"F0.wireOp",EDGE,"E49"),sQuery(id+"F0.wireOp",EDGE,"E50"),sQuery(id+"F0.wireOp",EDGE,"E51"),sQuery(id+"F0.wireOp",EDGE,"E52"),sQuery(id+"F0.wireOp",EDGE,"E53"),sQuery(id+"F0.wireOp",EDGE,"E54"),sQuery(id+"F0.wireOp",EDGE,"E55"),sQuery(id+"F0.wireOp",EDGE,"E56"),sQuery(id+"F0.wireOp",EDGE,"E57"),sQuery(id+"F0.wireOp",EDGE,"E58"),sQuery(id+"F0.wireOp",EDGE,"E59"),sQuery(id+"F0.wireOp",EDGE,"E60"),sQuery(id+"F0.wireOp",EDGE,"E61"),sQuery(id+"F0.wireOp",EDGE,"E62"),sQuery(id+"F0.wireOp",EDGE,"E63"),sQuery(id+"F0.wireOp",EDGE,"E64"),sQuery(id+"F0.wireOp",EDGE,"E65"),sQuery(id+"F0.wireOp",EDGE,"E66"),sQuery(id+"F0.wireOp",EDGE,"E67"),sQuery(id+"F0.wireOp",EDGE,"E68"),sQuery(id+"F0.wireOp",EDGE,"E69"),sQuery(id+"F0.wireOp",EDGE,"E70"),sQuery(id+"F0.wireOp",EDGE,"E71"),sQuery(id+"F0.wireOp",EDGE,"E72"),sQuery(id+"F0.wireOp",EDGE,"E73"),sQuery(id+"F0.wireOp",EDGE,"E74"),sQuery(id+"F0.wireOp",EDGE,"E75"),sQuery(id+"F0.wireOp",EDGE,"E76"),sQuery(id+"F0.wireOp",EDGE,"E77"),sQuery(id+"F0.wireOp",EDGE,"E78"),sQuery(id+"F0.wireOp",EDGE,"E79"),sQuery(id+"F0.wireOp",EDGE,"E80"),sQuery(id+"F0.wireOp",EDGE,"E81"),sQuery(id+"F0.wireOp",EDGE,"E82"),sQuery(id+"F0.wireOp",EDGE,"E83"),sQuery(id+"F0.wireOp",EDGE,"E84"),sQuery(id+"F0.wireOp",EDGE,"E85"),sQuery(id+"F0.wireOp",EDGE,"E86"),sQuery(id+"F0.wireOp",EDGE,"E87"),sQuery(id+"F0.wireOp",EDGE,"E88"),sQuery(id+"F0.wireOp",EDGE,"E89"),sQuery(id+"F0.wireOp",EDGE,"E90"),sQuery(id+"F0.wireOp",EDGE,"E91"),sQuery(id+"F0.wireOp",EDGE,"E92"),sQuery(id+"F0.wireOp",EDGE,"E93"),sQuery(id+"F0.wireOp",EDGE,"E94"),sQuery(id+"F0.wireOp",EDGE,"E95"),sQuery(id+"F0.wireOp",EDGE,"E96"),sQuery(id+"F0.wireOp",EDGE,"E97"),sQuery(id+"F0.wireOp",EDGE,"E98"),sQuery(id+"F0.wireOp",EDGE,"E99"),sQuery(id+"F0.wireOp",EDGE,"E100"),sQuery(id+"F0.wireOp",EDGE,"E101"),sQuery(id+"F0.wireOp",EDGE,"E102"),sQuery(id+"F0.wireOp",EDGE,"E103"),sQuery(id+"F0.wireOp",EDGE,"E104"),sQuery(id+"F0.wireOp",EDGE,"E105"),sQuery(id+"F0.wireOp",EDGE,"E106"),sQuery(id+"F0.wireOp",EDGE,"E107"),sQuery(id+"F0.wireOp",EDGE,"E108"),sQuery(id+"F0.wireOp",EDGE,"E109"),sQuery(id+"F0.wireOp",EDGE,"E110"),sQuery(id+"F0.wireOp",EDGE,"E111"),sQuery(id+"F0.wireOp",EDGE,"E112"),sQuery(id+"F0.wireOp",EDGE,"E113"),sQuery(id+"F0.wireOp",EDGE,"E114"),sQuery(id+"F0.wireOp",EDGE,"E115"),sQuery(id+"F0.wireOp",EDGE,"E116"),sQuery(id+"F0.wireOp",EDGE,"E117"),sQuery(id+"F0.wireOp",EDGE,"E118"),sQuery(id+"F0.wireOp",EDGE,"E119"),sQuery(id+"F0.wireOp",EDGE,"E120"),sQuery(id+"F0.wireOp",EDGE,"E121"),sQuery(id+"F0.wireOp",EDGE,"E122"),sQuery(id+"F0.wireOp",EDGE,"E123"),sQuery(id+"F0.wireOp",EDGE,"E124"),sQuery(id+"F0.wireOp",EDGE,"E125"),sQuery(id+"F0.wireOp",EDGE,"E126"),sQuery(id+"F0.wireOp",EDGE,"E127"),sQuery(id+"F0.wireOp",EDGE,"E128"),sQuery(id+"F0.wireOp",EDGE,"E129"),sQuery(id+"F0.wireOp",EDGE,"E130"),sQuery(id+"F0.wireOp",EDGE,"E131"),sQuery(id+"F0.wireOp",EDGE,"E132"),sQuery(id+"F0.wireOp",EDGE,"E133"),sQuery(id+"F0.wireOp",EDGE,"E134"),sQuery(id+"F0.wireOp",EDGE,"E135"),sQuery(id+"F0.wireOp",EDGE,"E136"),sQuery(id+"F0.wireOp",EDGE,"E137"),sQuery(id+"F0.wireOp",EDGE,"E138"),sQuery(id+"F0.wireOp",EDGE,"E139"),sQuery(id+"F0.wireOp",EDGE,"E140"),sQuery(id+"F0.wireOp",EDGE,"E141"),sQuery(id+"F0.wireOp",EDGE,"E142"),sQuery(id+"F0.wireOp",EDGE,"E143"),sQuery(id+"F0.wireOp",EDGE,"E144"),sQuery(id+"F0.wireOp",EDGE,"E145"),sQuery(id+"F0.wireOp",EDGE,"E146"),sQuery(id+"F0.wireOp",EDGE,"E147"),sQuery(id+"F0.wireOp",EDGE,"E148"),sQuery(id+"F0.wireOp",EDGE,"E149"),sQuery(id+"F0.wireOp",EDGE,"E150"),sQuery(id+"F0.wireOp",EDGE,"E151"),sQuery(id+"F0.wireOp",EDGE,"E152"),sQuery(id+"F0.wireOp",EDGE,"E153"),sQuery(id+"F0.wireOp",EDGE,"E154"),sQuery(id+"F0.wireOp",EDGE,"E155"),sQuery(id+"F0.wireOp",EDGE,"E156"),sQuery(id+"F0.wireOp",EDGE,"E157"),sQuery(id+"F0.wireOp",EDGE,"E158"),sQuery(id+"F0.wireOp",EDGE,"E159"),sQuery(id+"F0.wireOp",EDGE,"E160"),sQuery(id+"F0.wireOp",EDGE,"E161"),sQuery(id+"F0.wireOp",EDGE,"E162"),sQuery(id+"F0.wireOp",EDGE,"E163"),sQuery(id+"F0.wireOp",EDGE,"E164"),sQuery(id+"F0.wireOp",EDGE,"E165"),sQuery(id+"F0.wireOp",EDGE,"E166"),sQuery(id+"F0.wireOp",EDGE,"E167"),sQuery(id+"F0.wireOp",EDGE,"E168"),sQuery(id+"F0.wireOp",EDGE,"E169"),sQuery(id+"F0.wireOp",EDGE,"E170"),sQuery(id+"F0.wireOp",EDGE,"E171"),sQuery(id+"F0.wireOp",EDGE,"E172"),sQuery(id+"F0.wireOp",EDGE,"E173"),sQuery(id+"F0.wireOp",EDGE,"E174"),sQuery(id+"F0.wireOp",EDGE,"E175"),sQuery(id+"F0.wireOp",EDGE,"E176"),sQuery(id+"F0.wireOp",EDGE,"E177"),sQuery(id+"F0.wireOp",EDGE,"E178"),sQuery(id+"F0.wireOp",EDGE,"E179"),sQuery(id+"F0.wireOp",EDGE,"E180"),sQuery(id+"F0.wireOp",EDGE,"E181"),sQuery(id+"F0.wireOp",EDGE,"E182"),sQuery(id+"F0.wireOp",EDGE,"E183"),sQuery(id+"F0.wireOp",EDGE,"E184"),sQuery(id+"F0.wireOp",EDGE,"E185"),sQuery(id+"F0.wireOp",EDGE,"E186"),sQuery(id+"F0.wireOp",EDGE,"E187"),sQuery(id+"F0.wireOp",EDGE,"E188"),sQuery(id+"F0.wireOp",EDGE,"E189"),sQuery(id+"F0.wireOp",EDGE,"E190"),sQuery(id+"F0.wireOp",EDGE,"E191"),sQuery(id+"F0.wireOp",EDGE,"E192"),sQuery(id+"F0.wireOp",EDGE,"E193"),sQuery(id+"F0.wireOp",EDGE,"E194"),sQuery(id+"F0.wireOp",EDGE,"E195"),sQuery(id+"F0.wireOp",EDGE,"E196"),sQuery(id+"F0.wireOp",EDGE,"E197"),sQuery(id+"F0.wireOp",EDGE,"E198"),sQuery(id+"F0.wireOp",EDGE,"E199"),sQuery(id+"F0.wireOp",EDGE,"E200"),sQuery(id+"F0.wireOp",EDGE,"E201"),sQuery(id+"F0.wireOp",EDGE,"E202"),sQuery(id+"F0.wireOp",EDGE,"E203"),sQuery(id+"F0.wireOp",EDGE,"E204"),sQuery(id+"F0.wireOp",EDGE,"E205"),sQuery(id+"F0.wireOp",EDGE,"E206"),sQuery(id+"F0.wireOp",EDGE,"E207"),sQuery(id+"F0.wireOp",EDGE,"E208"),sQuery(id+"F0.wireOp",EDGE,"E209"),sQuery(id+"F0.wireOp",EDGE,"E210"),sQuery(id+"F0.wireOp",EDGE,"E211"),sQuery(id+"F0.wireOp",EDGE,"E212"),sQuery(id+"F0.wireOp",EDGE,"E213"),sQuery(id+"F0.wireOp",EDGE,"E214"),sQuery(id+"F0.wireOp",EDGE,"E215"),sQuery(id+"F0.wireOp",EDGE,"E216"),sQuery(id+"F0.wireOp",EDGE,"E217"),sQuery(id+"F0.wireOp",EDGE,"E218"),sQuery(id+"F0.wireOp",EDGE,"E219"),sQuery(id+"F0.wireOp",EDGE,"E220"),sQuery(id+"F0.wireOp",EDGE,"E221"),sQuery(id+"F0.wireOp",EDGE,"E222"),sQuery(id+"F0.wireOp",EDGE,"E223"),sQuery(id+"F0.wireOp",EDGE,"E224"),sQuery(id+"F0.wireOp",EDGE,"E225"),sQuery(id+"F0.wireOp",EDGE,"E226"),sQuery(id+"F0.wireOp",EDGE,"E227"),sQuery(id+"F0.wireOp",EDGE,"E228"),sQuery(id+"F0.wireOp",EDGE,"E229"),sQuery(id+"F0.wireOp",EDGE,"E230"),sQuery(id+"F0.wireOp",EDGE,"E231"),sQuery(id+"F0.wireOp",EDGE,"E232"),sQuery(id+"F0.wireOp",EDGE,"E233"),sQuery(id+"F0.wireOp",EDGE,"E234"),sQuery(id+"F0.wireOp",EDGE,"E235"),sQuery(id+"F0.wireOp",EDGE,"E236"),sQuery(id+"F0.wireOp",EDGE,"E237"),sQuery(id+"F0.wireOp",EDGE,"E238"),sQuery(id+"F0.wireOp",EDGE,"E239"),sQuery(id+"F0.wireOp",EDGE,"E240"),sQuery(id+"F0.wireOp",EDGE,"E241"),sQuery(id+"F0.wireOp",EDGE,"E242"),sQuery(id+"F0.wireOp",EDGE,"E243"),sQuery(id+"F0.wireOp",EDGE,"E244"),sQuery(id+"F0.wireOp",EDGE,"E245"),sQuery(id+"F0.wireOp",EDGE,"E246"),sQuery(id+"F0.wireOp",EDGE,"E247"),sQuery(id+"F0.wireOp",EDGE,"E248"),sQuery(id+"F0.wireOp",EDGE,"E249"),sQuery(id+"F0.wireOp",EDGE,"E250"),sQuery(id+"F0.wireOp",EDGE,"E251"),sQuery(id+"F0.wireOp",EDGE,"E252"),sQuery(id+"F0.wireOp",EDGE,"E253"),sQuery(id+"F0.wireOp",EDGE,"E254"),sQuery(id+"F0.wireOp",EDGE,"E255"),sQuery(id+"F0.wireOp",EDGE,"E256"),sQuery(id+"F0.wireOp",EDGE,"E257"),sQuery(id+"F0.wireOp",EDGE,"E258"),sQuery(id+"F0.wireOp",EDGE,"E259"),sQuery(id+"F0.wireOp",EDGE,"E260"),sQuery(id+"F0.wireOp",EDGE,"E261"),sQuery(id+"F0.wireOp",EDGE,"E262"),sQuery(id+"F0.wireOp",EDGE,"E263"),sQuery(id+"F0.wireOp",EDGE,"E264"),sQuery(id+"F0.wireOp",EDGE,"E265"),sQuery(id+"F0.wireOp",EDGE,"E266"),sQuery(id+"F0.wireOp",EDGE,"E267"),sQuery(id+"F0.wireOp",EDGE,"E268"),sQuery(id+"F0.wireOp",EDGE,"E269"),sQuery(id+"F0.wireOp",EDGE,"E270"),sQuery(id+"F0.wireOp",EDGE,"E271"),sQuery(id+"F0.wireOp",EDGE,"E272"),sQuery(id+"F0.wireOp",EDGE,"E273"),sQuery(id+"F0.wireOp",EDGE,"E274"),sQuery(id+"F0.wireOp",EDGE,"E275"),sQuery(id+"F0.wireOp",EDGE,"E276"),sQuery(id+"F0.wireOp",EDGE,"E277"),sQuery(id+"F0.wireOp",EDGE,"E278"),sQuery(id+"F0.wireOp",EDGE,"E279"),sQuery(id+"F0.wireOp",EDGE,"E280"),sQuery(id+"F0.wireOp",EDGE,"E281"),sQuery(id+"F0.wireOp",EDGE,"E282"),sQuery(id+"F0.wireOp",EDGE,"E283"),sQuery(id+"F0.wireOp",EDGE,"E284"),sQuery(id+"F0.wireOp",EDGE,"E285"),sQuery(id+"F0.wireOp",EDGE,"E286"),sQuery(id+"F0.wireOp",EDGE,"E287"),sQuery(id+"F0.wireOp",EDGE,"E288"),sQuery(id+"F0.wireOp",EDGE,"E289"),sQuery(id+"F0.wireOp",EDGE,"E290"),sQuery(id+"F0.wireOp",EDGE,"E291"),sQuery(id+"F0.wireOp",EDGE,"E292"),sQuery(id+"F0.wireOp",EDGE,"E293"),sQuery(id+"F0.wireOp",EDGE,"E294"),sQuery(id+"F0.wireOp",EDGE,"E295"),sQuery(id+"F0.wireOp",EDGE,"E296"),sQuery(id+"F0.wireOp",EDGE,"E297"),sQuery(id+"F0.wireOp",EDGE,"E298"),sQuery(id+"F0.wireOp",EDGE,"E299"),sQuery(id+"F0.wireOp",EDGE,"E300"),sQuery(id+"F0.wireOp",EDGE,"E301"),sQuery(id+"F0.wireOp",EDGE,"E302"),sQuery(id+"F0.wireOp",EDGE,"E303"),sQuery(id+"F0.wireOp",EDGE,"E304"),sQuery(id+"F0.wireOp",EDGE,"E305"),sQuery(id+"F0.wireOp",EDGE,"E306"),sQuery(id+"F0.wireOp",EDGE,"E307"),sQuery(id+"F0.wireOp",EDGE,"E308"),sQuery(id+"F0.wireOp",EDGE,"E309"),sQuery(id+"F0.wireOp",EDGE,"E310"),sQuery(id+"F0.wireOp",EDGE,"E311"),sQuery(id+"F0.wireOp",EDGE,"E312"),sQuery(id+"F0.wireOp",EDGE,"E313"),sQuery(id+"F0.wireOp",EDGE,"E314"),sQuery(id+"F0.wireOp",EDGE,"E315"),sQuery(id+"F0.wireOp",EDGE,"E316"),sQuery(id+"F0.wireOp",EDGE,"E317"),sQuery(id+"F0.wireOp",EDGE,"E318"),sQuery(id+"F0.wireOp",EDGE,"E319"),sQuery(id+"F0.wireOp",EDGE,"E320"),sQuery(id+"F0.wireOp",EDGE,"E321"),sQuery(id+"F0.wireOp",EDGE,"E322"),sQuery(id+"F0.wireOp",EDGE,"E323"),sQuery(id+"F0.wireOp",EDGE,"E324"),sQuery(id+"F0.wireOp",EDGE,"E325"),sQuery(id+"F0.wireOp",EDGE,"E326"),sQuery(id+"F0.wireOp",EDGE,"E327"),sQuery(id+"F0.wireOp",EDGE,"E328"),sQuery(id+"F0.wireOp",EDGE,"E329"),sQuery(id+"F0.wireOp",EDGE,"E330"),sQuery(id+"F0.wireOp",EDGE,"E331"),sQuery(id+"F0.wireOp",EDGE,"E332"),sQuery(id+"F0.wireOp",EDGE,"E333"),sQuery(id+"F0.wireOp",EDGE,"E334"),sQuery(id+"F0.wireOp",EDGE,"E335"),sQuery(id+"F0.wireOp",EDGE,"E336"),sQuery(id+"F0.wireOp",EDGE,"E337"),sQuery(id+"F0.wireOp",EDGE,"E338"),sQuery(id+"F0.wireOp",EDGE,"E339"),sQuery(id+"F0.wireOp",EDGE,"E340"),sQuery(id+"F0.wireOp",EDGE,"E341"),sQuery(id+"F0.wireOp",EDGE,"E342"),sQuery(id+"F0.wireOp",EDGE,"E343"),sQuery(id+"F0.wireOp",EDGE,"E344"),sQuery(id+"F0.wireOp",EDGE,"E345"),sQuery(id+"F0.wireOp",EDGE,"E346"),sQuery(id+"F0.wireOp",EDGE,"E347"),sQuery(id+"F0.wireOp",EDGE,"E348"),sQuery(id+"F0.wireOp",EDGE,"E349"),sQuery(id+"F0.wireOp",EDGE,"E350"),sQuery(id+"F0.wireOp",EDGE,"E351"),sQuery(id+"F0.wireOp",EDGE,"E352"),sQuery(id+"F0.wireOp",EDGE,"E353"),sQuery(id+"F0.wireOp",EDGE,"E354"),sQuery(id+"F0.wireOp",EDGE,"E355"),sQuery(id+"F0.wireOp",EDGE,"E356"),sQuery(id+"F0.wireOp",EDGE,"E357"),sQuery(id+"F0.wireOp",EDGE,"E358"),sQuery(id+"F0.wireOp",EDGE,"E359"),sQuery(id+"F0.wireOp",EDGE,"E360"),sQuery(id+"F0.wireOp",EDGE,"E361"),sQuery(id+"F0.wireOp",EDGE,"E362"),sQuery(id+"F0.wireOp",EDGE,"E363"),sQuery(id+"F0.wireOp",EDGE,"E364"),sQuery(id+"F0.wireOp",EDGE,"E365"),sQuery(id+"F0.wireOp",EDGE,"E366"),sQuery(id+"F0.wireOp",EDGE,"E367"),sQuery(id+"F0.wireOp",EDGE,"E368"),sQuery(id+"F0.wireOp",EDGE,"E369"),sQuery(id+"F0.wireOp",EDGE,"E370"),sQuery(id+"F0.wireOp",EDGE,"E371"),sQuery(id+"F0.wireOp",EDGE,"E372"),sQuery(id+"F0.wireOp",EDGE,"E373"),sQuery(id+"F0.wireOp",EDGE,"E374"),sQuery(id+"F0.wireOp",EDGE,"E375"),sQuery(id+"F0.wireOp",EDGE,"E376"),sQuery(id+"F0.wireOp",EDGE,"E377"),sQuery(id+"F0.wireOp",EDGE,"E378"),sQuery(id+"F0.wireOp",EDGE,"E379"),sQuery(id+"F0.wireOp",EDGE,"E380"),sQuery(id+"F0.wireOp",EDGE,"E381"),sQuery(id+"F0.wireOp",EDGE,"E382"),sQuery(id+"F0.wireOp",EDGE,"E383"),sQuery(id+"F0.wireOp",EDGE,"E384"),sQuery(id+"F0.wireOp",EDGE,"E385"),sQuery(id+"F0.wireOp",EDGE,"E386"),sQuery(id+"F0.wireOp",EDGE,"E387"),sQuery(id+"F0.wireOp",EDGE,"E388"),sQuery(id+"F0.wireOp",EDGE,"E389"),sQuery(id+"F0.wireOp",EDGE,"E390"),sQuery(id+"F0.wireOp",EDGE,"E391"),sQuery(id+"F0.wireOp",EDGE,"E392"),sQuery(id+"F0.wireOp",EDGE,"E393"),sQuery(id+"F0.wireOp",EDGE,"E394"),sQuery(id+"F0.wireOp",EDGE,"E395"),sQuery(id+"F0.wireOp",EDGE,"E396"),sQuery(id+"F0.wireOp",EDGE,"E397"),sQuery(id+"F0.wireOp",EDGE,"E398"),sQuery(id+"F0.wireOp",EDGE,"E399"),sQuery(id+"F0.wireOp",EDGE,"E400"),sQuery(id+"F0.wireOp",EDGE,"E401"),sQuery(id+"F0.wireOp",EDGE,"E402"),sQuery(id+"F0.wireOp",EDGE,"E403"),sQuery(id+"F0.wireOp",EDGE,"E404"),sQuery(id+"F0.wireOp",EDGE,"E405"),sQuery(id+"F0.wireOp",EDGE,"E406"),sQuery(id+"F0.wireOp",EDGE,"E407"),sQuery(id+"F0.wireOp",EDGE,"E408"),sQuery(id+"F0.wireOp",EDGE,"E409"),sQuery(id+"F0.wireOp",EDGE,"E410"),sQuery(id+"F0.wireOp",EDGE,"E411"),sQuery(id+"F0.wireOp",EDGE,"E412"),sQuery(id+"F0.wireOp",EDGE,"E413"),sQuery(id+"F0.wireOp",EDGE,"E414"),sQuery(id+"F0.wireOp",EDGE,"E415"),sQuery(id+"F0.wireOp",EDGE,"E416"),sQuery(id+"F0.wireOp",EDGE,"E417"),sQuery(id+"F0.wireOp",EDGE,"E418"),sQuery(id+"F0.wireOp",EDGE,"E419"),sQuery(id+"F0.wireOp",EDGE,"E420"),sQuery(id+"F0.wireOp",EDGE,"E421"),sQuery(id+"F0.wireOp",EDGE,"E422"),sQuery(id+"F0.wireOp",EDGE,"E423"),sQuery(id+"F0.wireOp",EDGE,"E424"),sQuery(id+"F0.wireOp",EDGE,"E425"),sQuery(id+"F0.wireOp",EDGE,"E426"),sQuery(id+"F0.wireOp",EDGE,"E427"),sQuery(id+"F0.wireOp",EDGE,"E428"),sQuery(id+"F0.wireOp",EDGE,"E429"),sQuery(id+"F0.wireOp",EDGE,"E430"),sQuery(id+"F0.wireOp",EDGE,"E431"),sQuery(id+"F0.wireOp",EDGE,"E432"),sQuery(id+"F0.wireOp",EDGE,"E433"),sQuery(id+"F0.wireOp",EDGE,"E434"),sQuery(id+"F0.wireOp",EDGE,"E435"),sQuery(id+"F0.wireOp",EDGE,"E436"),sQuery(id+"F0.wireOp",EDGE,"E437"),sQuery(id+"F0.wireOp",EDGE,"E438"),sQuery(id+"F0.wireOp",EDGE,"E439"),sQuery(id+"F0.wireOp",EDGE,"E440"),sQuery(id+"F0.wireOp",EDGE,"E441"),sQuery(id+"F0.wireOp",EDGE,"E442"),sQuery(id+"F0.wireOp",EDGE,"E443"),sQuery(id+"F0.wireOp",EDGE,"E444"),sQuery(id+"F0.wireOp",EDGE,"E445"),sQuery(id+"F0.wireOp",EDGE,"E446"),sQuery(id+"F0.wireOp",EDGE,"E447"),sQuery(id+"F0.wireOp",EDGE,"E448"),sQuery(id+"F0.wireOp",EDGE,"E449"),sQuery(id+"F0.wireOp",EDGE,"E450"),sQuery(id+"F0.wireOp",EDGE,"E451"),sQuery(id+"F0.wireOp",EDGE,"E452"),sQuery(id+"F0.wireOp",EDGE,"E453"),sQuery(id+"F0.wireOp",EDGE,"E454"),sQuery(id+"F0.wireOp",EDGE,"E455"),sQuery(id+"F0.wireOp",EDGE,"E456"),sQuery(id+"F0.wireOp",EDGE,"E457"),sQuery(id+"F0.wireOp",EDGE,"E458"),sQuery(id+"F0.wireOp",EDGE,"E459"),sQuery(id+"F0.wireOp",EDGE,"E460"),sQuery(id+"F0.wireOp",EDGE,"E461"),sQuery(id+"F0.wireOp",EDGE,"E462"),sQuery(id+"F0.wireOp",EDGE,"E463"),sQuery(id+"F0.wireOp",EDGE,"E464"),sQuery(id+"F0.wireOp",EDGE,"E465"),sQuery(id+"F0.wireOp",EDGE,"E466"),sQuery(id+"F0.wireOp",EDGE,"E467"),sQuery(id+"F0.wireOp",EDGE,"E468"),sQuery(id+"F0.wireOp",EDGE,"E469"),sQuery(id+"F0.wireOp",EDGE,"E470"),sQuery(id+"F0.wireOp",EDGE,"E471"),sQuery(id+"F0.wireOp",EDGE,"E472"),sQuery(id+"F0.wireOp",EDGE,"E473"),sQuery(id+"F0.wireOp",EDGE,"E474"),sQuery(id+"F0.wireOp",EDGE,"E475"),sQuery(id+"F0.wireOp",EDGE,"E476"),sQuery(id+"F0.wireOp",EDGE,"E477"),sQuery(id+"F0.wireOp",EDGE,"E478"),sQuery(id+"F0.wireOp",EDGE,"E479"),sQuery(id+"F0.wireOp",EDGE,"E480"),sQuery(id+"F0.wireOp",EDGE,"E481"),sQuery(id+"F0.wireOp",EDGE,"E482"),sQuery(id+"F0.wireOp",EDGE,"E483"),sQuery(id+"F0.wireOp",EDGE,"E484"),sQuery(id+"F0.wireOp",EDGE,"E485"),sQuery(id+"F0.wireOp",EDGE,"E486"),sQuery(id+"F0.wireOp",EDGE,"E487"),sQuery(id+"F0.wireOp",EDGE,"E488"),sQuery(id+"F0.wireOp",EDGE,"E489"),sQuery(id+"F0.wireOp",EDGE,"E490"),sQuery(id+"F0.wireOp",EDGE,"E491"),sQuery(id+"F0.wireOp",EDGE,"E492"),sQuery(id+"F0.wireOp",EDGE,"E493"),sQuery(id+"F0.wireOp",EDGE,"E494"),sQuery(id+"F0.wireOp",EDGE,"E495"),sQuery(id+"F0.wireOp",EDGE,"E496"),sQuery(id+"F0.wireOp",EDGE,"E497"),sQuery(id+"F0.wireOp",EDGE,"E498"),sQuery(id+"F0.wireOp",EDGE,"E499"),sQuery(id+"F0.wireOp",EDGE,"E500"),sQuery(id+"F0.wireOp",EDGE,"E501"),sQuery(id+"F0.wireOp",EDGE,"E502"),sQuery(id+"F0.wireOp",EDGE,"E503"),sQuery(id+"F0.wireOp",EDGE,"E504"),sQuery(id+"F0.wireOp",EDGE,"E505"),sQuery(id+"F0.wireOp",EDGE,"E506"),sQuery(id+"F0.wireOp",EDGE,"E507"),sQuery(id+"F0.wireOp",EDGE,"E508"),sQuery(id+"F0.wireOp",EDGE,"E509"),sQuery(id+"F0.wireOp",EDGE,"E510"),sQuery(id+"F0.wireOp",EDGE,"E511"),sQuery(id+"F0.wireOp",EDGE,"E512"),sQuery(id+"F0.wireOp",EDGE,"E513"),sQuery(id+"F0.wireOp",EDGE,"E514"),sQuery(id+"F0.wireOp",EDGE,"E515"),sQuery(id+"F0.wireOp",EDGE,"E516"),sQuery(id+"F0.wireOp",EDGE,"E517"),sQuery(id+"F0.wireOp",EDGE,"E518"),sQuery(id+"F0.wireOp",EDGE,"E519"),sQuery(id+"F0.wireOp",EDGE,"E520"),sQuery(id+"F0.wireOp",EDGE,"E521"),sQuery(id+"F0.wireOp",EDGE,"E522"),sQuery(id+"F0.wireOp",EDGE,"E523"),sQuery(id+"F0.wireOp",EDGE,"E524"),sQuery(id+"F0.wireOp",EDGE,"E525"),sQuery(id+"F0.wireOp",EDGE,"E526"),sQuery(id+"F0.wireOp",EDGE,"E527"),sQuery(id+"F0.wireOp",EDGE,"E528"),sQuery(id+"F0.wireOp",EDGE,"E529"),sQuery(id+"F0.wireOp",EDGE,"E530"),sQuery(id+"F0.wireOp",EDGE,"E531"),sQuery(id+"F0.wireOp",EDGE,"E532"),sQuery(id+"F0.wireOp",EDGE,"E533"),sQuery(id+"F0.wireOp",EDGE,"E534"),sQuery(id+"F0.wireOp",EDGE,"E535"),sQuery(id+"F0.wireOp",EDGE,"E536"),sQuery(id+"F0.wireOp",EDGE,"E537"),sQuery(id+"F0.wireOp",EDGE,"E538"),sQuery(id+"F0.wireOp",EDGE,"E539"),sQuery(id+"F0.wireOp",EDGE,"E540"),sQuery(id+"F0.wireOp",EDGE,"E541"),sQuery(id+"F0.wireOp",EDGE,"E542"),sQuery(id+"F0.wireOp",EDGE,"E543"),sQuery(id+"F0.wireOp",EDGE,"E544"),sQuery(id+"F0.wireOp",EDGE,"E545"),sQuery(id+"F0.wireOp",EDGE,"E546"),sQuery(id+"F0.wireOp",EDGE,"E547"),sQuery(id+"F0.wireOp",EDGE,"E548"),sQuery(id+"F0.wireOp",EDGE,"E549"),sQuery(id+"F0.wireOp",EDGE,"E550"),sQuery(id+"F0.wireOp",EDGE,"E551"),sQuery(id+"F0.wireOp",EDGE,"E552"),sQuery(id+"F0.wireOp",EDGE,"E553"),sQuery(id+"F0.wireOp",EDGE,"E554"),sQuery(id+"F0.wireOp",EDGE,"E555"),sQuery(id+"F0.wireOp",EDGE,"E556"),sQuery(id+"F0.wireOp",EDGE,"E557"),sQuery(id+"F0.wireOp",EDGE,"E558"),sQuery(id+"F0.wireOp",EDGE,"E559"),sQuery(id+"F0.wireOp",EDGE,"E560"),sQuery(id+"F0.wireOp",EDGE,"E561"),sQuery(id+"F0.wireOp",EDGE,"E562"),sQuery(id+"F0.wireOp",EDGE,"E563"),sQuery(id+"F0.wireOp",EDGE,"E564"),sQuery(id+"F0.wireOp",EDGE,"E565"),sQuery(id+"F0.wireOp",EDGE,"E566"),sQuery(id+"F0.wireOp",EDGE,"E567"),sQuery(id+"F0.wireOp",EDGE,"E568"),sQuery(id+"F0.wireOp",EDGE,"E569"),sQuery(id+"F0.wireOp",EDGE,"E570"),sQuery(id+"F0.wireOp",EDGE,"E571"),sQuery(id+"F0.wireOp",EDGE,"E572"),sQuery(id+"F0.wireOp",EDGE,"E573"),sQuery(id+"F0.wireOp",EDGE,"E574"),sQuery(id+"F0.wireOp",EDGE,"E575"),sQuery(id+"F0.wireOp",EDGE,"E576"),sQuery(id+"F0.wireOp",EDGE,"E577"),sQuery(id+"F0.wireOp",EDGE,"E578"),sQuery(id+"F0.wireOp",EDGE,"E579"),sQuery(id+"F0.wireOp",EDGE,"E580"),sQuery(id+"F0.wireOp",EDGE,"E581"),sQuery(id+"F0.wireOp",EDGE,"E582"),sQuery(id+"F0.wireOp",EDGE,"E583"),sQuery(id+"F0.wireOp",EDGE,"E584"),sQuery(id+"F0.wireOp",EDGE,"E585"),sQuery(id+"F0.wireOp",EDGE,"E586"),sQuery(id+"F0.wireOp",EDGE,"E587"),sQuery(id+"F0.wireOp",EDGE,"E588"),sQuery(id+"F0.wireOp",EDGE,"E589"),sQuery(id+"F0.wireOp",EDGE,"E590"),sQuery(id+"F0.wireOp",EDGE,"E591"),sQuery(id+"F0.wireOp",EDGE,"E592"),sQuery(id+"F0.wireOp",EDGE,"E593"),sQuery(id+"F0.wireOp",EDGE,"E594"),sQuery(id+"F0.wireOp",EDGE,"E595"),sQuery(id+"F0.wireOp",EDGE,"E596"),sQuery(id+"F0.wireOp",EDGE,"E597"),sQuery(id+"F0.wireOp",EDGE,"E598"),sQuery(id+"F0.wireOp",EDGE,"E599"),sQuery(id+"F0.wireOp",EDGE,"E600"),sQuery(id+"F0.wireOp",EDGE,"E601"),sQuery(id+"F0.wireOp",EDGE,"E602"),sQuery(id+"F0.wireOp",EDGE,"E603"),sQuery(id+"F0.wireOp",EDGE,"E604"),sQuery(id+"F0.wireOp",EDGE,"E605"),sQuery(id+"F0.wireOp",EDGE,"E606"),sQuery(id+"F0.wireOp",EDGE,"E607"),sQuery(id+"F0.wireOp",EDGE,"E608"),sQuery(id+"F0.wireOp",EDGE,"E609"),sQuery(id+"F0.wireOp",EDGE,"E610"),sQuery(id+"F0.wireOp",EDGE,"E611"),sQuery(id+"F0.wireOp",EDGE,"E612"),sQuery(id+"F0.wireOp",EDGE,"E613"),sQuery(id+"F0.wireOp",EDGE,"E614"),sQuery(id+"F0.wireOp",EDGE,"E615"),sQuery(id+"F0.wireOp",EDGE,"E616"),sQuery(id+"F0.wireOp",EDGE,"E617"),sQuery(id+"F0.wireOp",EDGE,"E618"),sQuery(id+"F0.wireOp",EDGE,"E619"),sQuery(id+"F0.wireOp",EDGE,"E620"),sQuery(id+"F0.wireOp",EDGE,"E621"),sQuery(id+"F0.wireOp",EDGE,"E622"),sQuery(id+"F0.wireOp",EDGE,"E623"),sQuery(id+"F0.wireOp",EDGE,"E624"),sQuery(id+"F0.wireOp",EDGE,"E625"),sQuery(id+"F0.wireOp",EDGE,"E626"),sQuery(id+"F0.wireOp",EDGE,"E627"),sQuery(id+"F0.wireOp",EDGE,"E628"),sQuery(id+"F0.wireOp",EDGE,"E629"),sQuery(id+"F0.wireOp",EDGE,"E630"),sQuery(id+"F0.wireOp",EDGE,"E631"),sQuery(id+"F0.wireOp",EDGE,"E632"),sQuery(id+"F0.wireOp",EDGE,"E633"),sQuery(id+"F0.wireOp",EDGE,"E634"),sQuery(id+"F0.wireOp",EDGE,"E635"),sQuery(id+"F0.wireOp",EDGE,"E636"),sQuery(id+"F0.wireOp",EDGE,"E637"),sQuery(id+"F0.wireOp",EDGE,"E638"),sQuery(id+"F0.wireOp",EDGE,"E639"),sQuery(id+"F0.wireOp",EDGE,"E640"),sQuery(id+"F0.wireOp",EDGE,"E641"),sQuery(id+"F0.wireOp",EDGE,"E642"),sQuery(id+"F0.wireOp",EDGE,"E643"),sQuery(id+"F0.wireOp",EDGE,"E644"),sQuery(id+"F0.wireOp",EDGE,"E645"),sQuery(id+"F0.wireOp",EDGE,"E646"),sQuery(id+"F0.wireOp",EDGE,"E647"),sQuery(id+"F0.wireOp",EDGE,"E648"),sQuery(id+"F0.wireOp",EDGE,"E649"),sQuery(id+"F0.wireOp",EDGE,"E650"),sQuery(id+"F0.wireOp",EDGE,"E651"),sQuery(id+"F0.wireOp",EDGE,"E652"),sQuery(id+"F0.wireOp",EDGE,"E653"),sQuery(id+"F0.wireOp",EDGE,"E654"),sQuery(id+"F0.wireOp",EDGE,"E655"),sQuery(id+"F0.wireOp",EDGE,"E656"),sQuery(id+"F0.wireOp",EDGE,"E657"),sQuery(id+"F0.wireOp",EDGE,"E658"),sQuery(id+"F0.wireOp",EDGE,"E659"),sQuery(id+"F0.wireOp",EDGE,"E660"),sQuery(id+"F0.wireOp",EDGE,"E661"),sQuery(id+"F0.wireOp",EDGE,"E662"),sQuery(id+"F0.wireOp",EDGE,"E663"),sQuery(id+"F0.wireOp",EDGE,"E664"),sQuery(id+"F0.wireOp",EDGE,"E665"),sQuery(id+"F0.wireOp",EDGE,"E666"),sQuery(id+"F0.wireOp",EDGE,"E667"),sQuery(id+"F0.wireOp",EDGE,"E668"),sQuery(id+"F0.wireOp",EDGE,"E669"),sQuery(id+"F0.wireOp",EDGE,"E670"),sQuery(id+"F0.wireOp",EDGE,"E671"),sQuery(id+"F0.wireOp",EDGE,"E672"),sQuery(id+"F0.wireOp",EDGE,"E673"),sQuery(id+"F0.wireOp",EDGE,"E674"),sQuery(id+"F0.wireOp",EDGE,"E675"),sQuery(id+"F0.wireOp",EDGE,"E676"),sQuery(id+"F0.wireOp",EDGE,"E677"),sQuery(id+"F0.wireOp",EDGE,"E678"),sQuery(id+"F0.wireOp",EDGE,"E679"),sQuery(id+"F0.wireOp",EDGE,"E680"),sQuery(id+"F0.wireOp",EDGE,"E681"),sQuery(id+"F0.wireOp",EDGE,"E682"),sQuery(id+"F0.wireOp",EDGE,"E683"),sQuery(id+"F0.wireOp",EDGE,"E684"),sQuery(id+"F0.wireOp",EDGE,"E685"),sQuery(id+"F0.wireOp",EDGE,"E686"),sQuery(id+"F0.wireOp",EDGE,"E687"),sQuery(id+"F0.wireOp",EDGE,"E688"),sQuery(id+"F0.wireOp",EDGE,"E689"),sQuery(id+"F0.wireOp",EDGE,"E690"),sQuery(id+"F0.wireOp",EDGE,"E691"),sQuery(id+"F0.wireOp",EDGE,"E692"),sQuery(id+"F0.wireOp",EDGE,"E693"),sQuery(id+"F0.wireOp",EDGE,"E694"),sQuery(id+"F0.wireOp",EDGE,"E695"),sQuery(id+"F0.wireOp",EDGE,"E696"),sQuery(id+"F0.wireOp",EDGE,"E697"),sQuery(id+"F0.wireOp",EDGE,"E698"),sQuery(id+"F0.wireOp",EDGE,"E699"),sQuery(id+"F0.wireOp",EDGE,"E700"),sQuery(id+"F0.wireOp",EDGE,"E701"),sQuery(id+"F0.wireOp",EDGE,"E702"),sQuery(id+"F0.wireOp",EDGE,"E703"),sQuery(id+"F0.wireOp",EDGE,"E704"),sQuery(id+"F0.wireOp",EDGE,"E705"),sQuery(id+"F0.wireOp",EDGE,"E706"),sQuery(id+"F0.wireOp",EDGE,"E707"),sQuery(id+"F0.wireOp",EDGE,"E708"),sQuery(id+"F0.wireOp",EDGE,"E709"),sQuery(id+"F0.wireOp",EDGE,"E710"),sQuery(id+"F0.wireOp",EDGE,"E711"),sQuery(id+"F0.wireOp",EDGE,"E712"),sQuery(id+"F0.wireOp",EDGE,"E713"),sQuery(id+"F0.wireOp",EDGE,"E714"),sQuery(id+"F0.wireOp",EDGE,"E715"),sQuery(id+"F0.wireOp",EDGE,"E716"),sQuery(id+"F0.wireOp",EDGE,"E717"),sQuery(id+"F0.wireOp",EDGE,"E718"),sQuery(id+"F0.wireOp",EDGE,"E719"),sQuery(id+"F0.wireOp",EDGE,"E720"),sQuery(id+"F0.wireOp",EDGE,"E721"),sQuery(id+"F0.wireOp",EDGE,"E722"),sQuery(id+"F0.wireOp",EDGE,"E723"),sQuery(id+"F0.wireOp",EDGE,"E724"),sQuery(id+"F0.wireOp",EDGE,"E725"),sQuery(id+"F0.wireOp",EDGE,"E726"),sQuery(id+"F0.wireOp",EDGE,"E727"),sQuery(id+"F0.wireOp",EDGE,"E728"),sQuery(id+"F0.wireOp",EDGE,"E729"),sQuery(id+"F0.wireOp",EDGE,"E730"),sQuery(id+"F0.wireOp",EDGE,"E731"),sQuery(id+"F0.wireOp",EDGE,"E732"),sQuery(id+"F0.wireOp",EDGE,"E733"),sQuery(id+"F0.wireOp",EDGE,"E734"),sQuery(id+"F0.wireOp",EDGE,"E735"),sQuery(id+"F0.wireOp",EDGE,"E736"),sQuery(id+"F0.wireOp",EDGE,"E737"),sQuery(id+"F0.wireOp",EDGE,"E738"),sQuery(id+"F0.wireOp",EDGE,"E739"),sQuery(id+"F0.wireOp",EDGE,"E740"),sQuery(id+"F0.wireOp",EDGE,"E741"),sQuery(id+"F0.wireOp",EDGE,"E742"),sQuery(id+"F0.wireOp",EDGE,"E743"),sQuery(id+"F0.wireOp",EDGE,"E744"),sQuery(id+"F0.wireOp",EDGE,"E745"),sQuery(id+"F0.wireOp",EDGE,"E746"),sQuery(id+"F0.wireOp",EDGE,"E747"),sQuery(id+"F0.wireOp",EDGE,"E748"),sQuery(id+"F0.wireOp",EDGE,"E749"),sQuery(id+"F0.wireOp",EDGE,"E750"),sQuery(id+"F0.wireOp",EDGE,"E751"),sQuery(id+"F0.wireOp",EDGE,"E752"),sQuery(id+"F0.wireOp",EDGE,"E753"),sQuery(id+"F0.wireOp",EDGE,"E754"),sQuery(id+"F0.wireOp",EDGE,"E755"),sQuery(id+"F0.wireOp",EDGE,"E756"),sQuery(id+"F0.wireOp",EDGE,"E757"),sQuery(id+"F0.wireOp",EDGE,"E758"),sQuery(id+"F0.wireOp",EDGE,"E759"),sQuery(id+"F0.wireOp",EDGE,"E760"),sQuery(id+"F0.wireOp",EDGE,"E761"),sQuery(id+"F0.wireOp",EDGE,"E762"),sQuery(id+"F0.wireOp",EDGE,"E763"),sQuery(id+"F0.wireOp",EDGE,"E764"),sQuery(id+"F0.wireOp",EDGE,"E765"),sQuery(id+"F0.wireOp",EDGE,"E766"),sQuery(id+"F0.wireOp",EDGE,"E767"),sQuery(id+"F0.wireOp",EDGE,"E768"),sQuery(id+"F0.wireOp",EDGE,"E769"),sQuery(id+"F0.wireOp",EDGE,"E770"),sQuery(id+"F0.wireOp",EDGE,"E771"),sQuery(id+"F0.wireOp",EDGE,"E772"),sQuery(id+"F0.wireOp",EDGE,"E773"),sQuery(id+"F0.wireOp",EDGE,"E774"),sQuery(id+"F0.wireOp",EDGE,"E775"),sQuery(id+"F0.wireOp",EDGE,"E776"),sQuery(id+"F0.wireOp",EDGE,"E777"),sQuery(id+"F0.wireOp",EDGE,"E778"),sQuery(id+"F0.wireOp",EDGE,"E779"),sQuery(id+"F0.wireOp",EDGE,"E780"),sQuery(id+"F0.wireOp",EDGE,"E781"),sQuery(id+"F0.wireOp",EDGE,"E782"),sQuery(id+"F0.wireOp",EDGE,"E783"),sQuery(id+"F0.wireOp",EDGE,"E784"),sQuery(id+"F0.wireOp",EDGE,"E785"),sQuery(id+"F0.wireOp",EDGE,"E786"),sQuery(id+"F0.wireOp",EDGE,"E787"),sQuery(id+"F0.wireOp",EDGE,"E788"),sQuery(id+"F0.wireOp",EDGE,"E789"),sQuery(id+"F0.wireOp",EDGE,"E790"),sQuery(id+"F0.wireOp",EDGE,"E791"),sQuery(id+"F0.wireOp",EDGE,"E792"),sQuery(id+"F0.wireOp",EDGE,"E793"),sQuery(id+"F0.wireOp",EDGE,"E794"),sQuery(id+"F0.wireOp",EDGE,"E795"),sQuery(id+"F0.wireOp",EDGE,"E796"),sQuery(id+"F0.wireOp",EDGE,"E797"),sQuery(id+"F0.wireOp",EDGE,"E798"),sQuery(id+"F0.wireOp",EDGE,"E799"),sQuery(id+"F0.wireOp",EDGE,"E800"),sQuery(id+"F0.wireOp",EDGE,"E801"),sQuery(id+"F0.wireOp",EDGE,"E802"),sQuery(id+"F0.wireOp",EDGE,"E803"),sQuery(id+"F0.wireOp",EDGE,"E804"),sQuery(id+"F0.wireOp",EDGE,"E805"),sQuery(id+"F0.wireOp",EDGE,"E806"),sQuery(id+"F0.wireOp",EDGE,"E807"),sQuery(id+"F0.wireOp",EDGE,"E808"),sQuery(id+"F0.wireOp",EDGE,"E809"),sQuery(id+"F0.wireOp",EDGE,"E810"),sQuery(id+"F0.wireOp",EDGE,"E811"),sQuery(id+"F0.wireOp",EDGE,"E812"),sQuery(id+"F0.wireOp",EDGE,"E813"),sQuery(id+"F0.wireOp",EDGE,"E814"),sQuery(id+"F0.wireOp",EDGE,"E815"),sQuery(id+"F0.wireOp",EDGE,"E816"),sQuery(id+"F0.wireOp",EDGE,"E817"),sQuery(id+"F0.wireOp",EDGE,"E818"),sQuery(id+"F0.wireOp",EDGE,"E819"),sQuery(id+"F0.wireOp",EDGE,"E820"),sQuery(id+"F0.wireOp",EDGE,"E821"),sQuery(id+"F0.wireOp",EDGE,"E822"),sQuery(id+"F0.wireOp",EDGE,"E823"),sQuery(id+"F0.wireOp",EDGE,"E824"),sQuery(id+"F0.wireOp",EDGE,"E825"),sQuery(id+"F0.wireOp",EDGE,"E826"),sQuery(id+"F0.wireOp",EDGE,"E827"),sQuery(id+"F0.wireOp",EDGE,"E828"),sQuery(id+"F0.wireOp",EDGE,"E829"),sQuery(id+"F0.wireOp",EDGE,"E830"),sQuery(id+"F0.wireOp",EDGE,"E831"),sQuery(id+"F0.wireOp",EDGE,"E832"),sQuery(id+"F0.wireOp",EDGE,"E833"),sQuery(id+"F0.wireOp",EDGE,"E834"),sQuery(id+"F0.wireOp",EDGE,"E835"),sQuery(id+"F0.wireOp",EDGE,"E836"),sQuery(id+"F0.wireOp",EDGE,"E837"),sQuery(id+"F0.wireOp",EDGE,"E838"),sQuery(id+"F0.wireOp",EDGE,"E839"),sQuery(id+"F0.wireOp",EDGE,"E840"),sQuery(id+"F0.wireOp",EDGE,"E841"),sQuery(id+"F0.wireOp",EDGE,"E842"),sQuery(id+"F0.wireOp",EDGE,"E843"),sQuery(id+"F0.wireOp",EDGE,"E844"),sQuery(id+"F0.wireOp",EDGE,"E845"),sQuery(id+"F0.wireOp",EDGE,"E846"),sQuery(id+"F0.wireOp",EDGE,"E847"),sQuery(id+"F0.wireOp",EDGE,"E848"),sQuery(id+"F0.wireOp",EDGE,"E849"),sQuery(id+"F0.wireOp",EDGE,"E850"),sQuery(id+"F0.wireOp",EDGE,"E851"),sQuery(id+"F0.wireOp",EDGE,"E852"),sQuery(id+"F0.wireOp",EDGE,"E853"),sQuery(id+"F0.wireOp",EDGE,"E854"),sQuery(id+"F0.wireOp",EDGE,"E855"),sQuery(id+"F0.wireOp",EDGE,"E856"),sQuery(id+"F0.wireOp",EDGE,"E857"),sQuery(id+"F0.wireOp",EDGE,"E858"),sQuery(id+"F0.wireOp",EDGE,"E859"),sQuery(id+"F0.wireOp",EDGE,"E860"),sQuery(id+"F0.wireOp",EDGE,"E861"),sQuery(id+"F0.wireOp",EDGE,"E862"),sQuery(id+"F0.wireOp",EDGE,"E863"),sQuery(id+"F0.wireOp",EDGE,"E864"),sQuery(id+"F0.wireOp",EDGE,"E865"),sQuery(id+"F0.wireOp",EDGE,"E866"),sQuery(id+"F0.wireOp",EDGE,"E867"),sQuery(id+"F0.wireOp",EDGE,"E868"),sQuery(id+"F0.wireOp",EDGE,"E869"),sQuery(id+"F0.wireOp",EDGE,"E870"),sQuery(id+"F0.wireOp",EDGE,"E871"),sQuery(id+"F0.wireOp",EDGE,"E872"),sQuery(id+"F0.wireOp",EDGE,"E873"),sQuery(id+"F0.wireOp",EDGE,"E874"),sQuery(id+"F0.wireOp",EDGE,"E875"),sQuery(id+"F0.wireOp",EDGE,"E876"),sQuery(id+"F0.wireOp",EDGE,"E877"),sQuery(id+"F0.wireOp",EDGE,"E878"),sQuery(id+"F0.wireOp",EDGE,"E879"),sQuery(id+"F0.wireOp",EDGE,"E880"),sQuery(id+"F0.wireOp",EDGE,"E881"),sQuery(id+"F0.wireOp",EDGE,"E882"),sQuery(id+"F0.wireOp",EDGE,"E883"),sQuery(id+"F0.wireOp",EDGE,"E884"),sQuery(id+"F0.wireOp",EDGE,"E885"),sQuery(id+"F0.wireOp",EDGE,"E886"),sQuery(id+"F0.wireOp",EDGE,"E887"),sQuery(id+"F0.wireOp",EDGE,"E888"),sQuery(id+"F0.wireOp",EDGE,"E889"),sQuery(id+"F0.wireOp",EDGE,"E890"),sQuery(id+"F0.wireOp",EDGE,"E891"),sQuery(id+"F0.wireOp",EDGE,"E892"),sQuery(id+"F0.wireOp",EDGE,"E893"),sQuery(id+"F0.wireOp",EDGE,"E894"),sQuery(id+"F0.wireOp",EDGE,"E895"),sQuery(id+"F0.wireOp",EDGE,"E896"),sQuery(id+"F0.wireOp",EDGE,"E897"),sQuery(id+"F0.wireOp",EDGE,"E898"),sQuery(id+"F0.wireOp",EDGE,"E899"),sQuery(id+"F0.wireOp",EDGE,"E900"),sQuery(id+"F0.wireOp",EDGE,"E901"),sQuery(id+"F0.wireOp",EDGE,"E902"),sQuery(id+"F0.wireOp",EDGE,"E903"),sQuery(id+"F0.wireOp",EDGE,"E904"),sQuery(id+"F0.wireOp",EDGE,"E905"),sQuery(id+"F0.wireOp",EDGE,"E906"),sQuery(id+"F0.wireOp",EDGE,"E907"),sQuery(id+"F0.wireOp",EDGE,"E908"),sQuery(id+"F0.wireOp",EDGE,"E909"),sQuery(id+"F0.wireOp",EDGE,"E910"),sQuery(id+"F0.wireOp",EDGE,"E911"),sQuery(id+"F0.wireOp",EDGE,"E912"),sQuery(id+"F0.wireOp",EDGE,"E913"),sQuery(id+"F0.wireOp",EDGE,"E914"),sQuery(id+"F0.wireOp",EDGE,"E915"),sQuery(id+"F0.wireOp",EDGE,"E916"),sQuery(id+"F0.wireOp",EDGE,"E917"),sQuery(id+"F0.wireOp",EDGE,"E918"),sQuery(id+"F0.wireOp",EDGE,"E919"),sQuery(id+"F0.wireOp",EDGE,"E920"),sQuery(id+"F0.wireOp",EDGE,"E921"),sQuery(id+"F0.wireOp",EDGE,"E922"),sQuery(id+"F0.wireOp",EDGE,"E923"),sQuery(id+"F0.wireOp",EDGE,"E924"),sQuery(id+"F0.wireOp",EDGE,"E925"),sQuery(id+"F0.wireOp",EDGE,"E926"),sQuery(id+"F0.wireOp",EDGE,"E927"),sQuery(id+"F0.wireOp",EDGE,"E928"),sQuery(id+"F0.wireOp",EDGE,"E929"),sQuery(id+"F0.wireOp",EDGE,"E930"),sQuery(id+"F0.wireOp",EDGE,"E931"),sQuery(id+"F0.wireOp",EDGE,"E932"),sQuery(id+"F0.wireOp",EDGE,"E933"),sQuery(id+"F0.wireOp",EDGE,"E934"),sQuery(id+"F0.wireOp",EDGE,"E935"),sQuery(id+"F0.wireOp",EDGE,"E936"),sQuery(id+"F0.wireOp",EDGE,"E937"),sQuery(id+"F0.wireOp",EDGE,"E938"),sQuery(id+"F0.wireOp",EDGE,"E939"),sQuery(id+"F0.wireOp",EDGE,"E940"),sQuery(id+"F0.wireOp",EDGE,"E941"),sQuery(id+"F0.wireOp",EDGE,"E942"),sQuery(id+"F0.wireOp",EDGE,"E943"),sQuery(id+"F0.wireOp",EDGE,"E944"),sQuery(id+"F0.wireOp",EDGE,"E945"),sQuery(id+"F0.wireOp",EDGE,"E946"),sQuery(id+"F0.wireOp",EDGE,"E947"),sQuery(id+"F0.wireOp",EDGE,"E948"),sQuery(id+"F0.wireOp",EDGE,"E949"),sQuery(id+"F0.wireOp",EDGE,"E950"),sQuery(id+"F0.wireOp",EDGE,"E951"),sQuery(id+"F0.wireOp",EDGE,"E952"),sQuery(id+"F0.wireOp",EDGE,"E953"),sQuery(id+"F0.wireOp",EDGE,"E954"),sQuery(id+"F0.wireOp",EDGE,"E955"),sQuery(id+"F0.wireOp",EDGE,"E956"),sQuery(id+"F0.wireOp",EDGE,"E957"),sQuery(id+"F0.wireOp",EDGE,"E958"),sQuery(id+"F0.wireOp",EDGE,"E959"),sQuery(id+"F0.wireOp",EDGE,"E960"),sQuery(id+"F0.wireOp",EDGE,"E961"),sQuery(id+"F0.wireOp",EDGE,"E962"),sQuery(id+"F0.wireOp",EDGE,"E963"),sQuery(id+"F0.wireOp",EDGE,"E964"),sQuery(id+"F0.wireOp",EDGE,"E965"),sQuery(id+"F0.wireOp",EDGE,"E966"),sQuery(id+"F0.wireOp",EDGE,"E967"),sQuery(id+"F0.wireOp",EDGE,"E968"),sQuery(id+"F0.wireOp",EDGE,"E969"),sQuery(id+"F0.wireOp",EDGE,"E970"),sQuery(id+"F0.wireOp",EDGE,"E971"),sQuery(id+"F0.wireOp",EDGE,"E972"),sQuery(id+"F0.wireOp",EDGE,"E973"),sQuery(id+"F0.wireOp",EDGE,"E974"),sQuery(id+"F0.wireOp",EDGE,"E975"),sQuery(id+"F0.wireOp",EDGE,"E976"),sQuery(id+"F0.wireOp",EDGE,"E977"),sQuery(id+"F0.wireOp",EDGE,"E978"),sQuery(id+"F0.wireOp",EDGE,"E979"),sQuery(id+"F0.wireOp",EDGE,"E980"),sQuery(id+"F0.wireOp",EDGE,"E981"),sQuery(id+"F0.wireOp",EDGE,"E982"),sQuery(id+"F0.wireOp",EDGE,"E983"),sQuery(id+"F0.wireOp",EDGE,"E984"),sQuery(id+"F0.wireOp",EDGE,"E985"),sQuery(id+"F0.wireOp",EDGE,"E986"),sQuery(id+"F0.wireOp",EDGE,"E987"),sQuery(id+"F0.wireOp",EDGE,"E988"),sQuery(id+"F0.wireOp",EDGE,"E989"),sQuery(id+"F0.wireOp",EDGE,"E990"),sQuery(id+"F0.wireOp",EDGE,"E991"),sQuery(id+"F0.wireOp",EDGE,"E992"),sQuery(id+"F0.wireOp",EDGE,"E993"),sQuery(id+"F0.wireOp",EDGE,"E994"),sQuery(id+"F0.wireOp",EDGE,"E995"),sQuery(id+"F0.wireOp",EDGE,"E996"),sQuery(id+"F0.wireOp",EDGE,"E997"),sQuery(id+"F0.wireOp",EDGE,"E998"),sQuery(id+"F0.wireOp",EDGE,"E999"),sQuery(id+"F0.wireOp",EDGE,"E1000"),sQuery(id+"F0.wireOp",EDGE,"E1001"),sQuery(id+"F0.wireOp",EDGE,"E1002"),sQuery(id+"F0.wireOp",EDGE,"E1003"),sQuery(id+"F0.wireOp",EDGE,"E1004"),sQuery(id+"F0.wireOp",EDGE,"E1005"),sQuery(id+"F0.wireOp",EDGE,"E1006"),sQuery(id+"F0.wireOp",EDGE,"E1007"),sQuery(id+"F0.wireOp",EDGE,"E1008"),sQuery(id+"F0.wireOp",EDGE,"E1009"),sQuery(id+"F0.wireOp",EDGE,"E1010"),sQuery(id+"F0.wireOp",EDGE,"E1011"),sQuery(id+"F0.wireOp",EDGE,"E1012"),sQuery(id+"F0.wireOp",EDGE,"E1013"),sQuery(id+"F0.wireOp",EDGE,"E1014"),sQuery(id+"F0.wireOp",EDGE,"E1015"),sQuery(id+"F0.wireOp",EDGE,"E1016"),sQuery(id+"F0.wireOp",EDGE,"E1017"),sQuery(id+"F0.wireOp",EDGE,"E1018"),sQuery(id+"F0.wireOp",EDGE,"E1019"),sQuery(id+"F0.wireOp",EDGE,"E1020"),sQuery(id+"F0.wireOp",EDGE,"E1021"),sQuery(id+"F0.wireOp",EDGE,"E1022"),sQuery(id+"F0.wireOp",EDGE,"E1023"),sQuery(id+"F0.wireOp",EDGE,"E1024"),sQuery(id+"F0.wireOp",EDGE,"E1025"),sQuery(id+"F0.wireOp",EDGE,"E1026"),sQuery(id+"F0.wireOp",EDGE,"E1027"),sQuery(id+"F0.wireOp",EDGE,"E1028"),sQuery(id+"F0.wireOp",EDGE,"E1029"),sQuery(id+"F0.wireOp",EDGE,"E1030"),sQuery(id+"F0.wireOp",EDGE,"E1031"),sQuery(id+"F0.wireOp",EDGE,"E1032"),sQuery(id+"F0.wireOp",EDGE,"E1033"),sQuery(id+"F0.wireOp",EDGE,"E1034"),sQuery(id+"F0.wireOp",EDGE,"E1035"),sQuery(id+"F0.wireOp",EDGE,"E1036"),sQuery(id+"F0.wireOp",EDGE,"E1037"),sQuery(id+"F0.wireOp",EDGE,"E1038"),sQuery(id+"F0.wireOp",EDGE,"E1039"),sQuery(id+"F0.wireOp",EDGE,"E1040"),sQuery(id+"F0.wireOp",EDGE,"E1041"),sQuery(id+"F0.wireOp",EDGE,"E1042"),sQuery(id+"F0.wireOp",EDGE,"E1043"),sQuery(id+"F0.wireOp",EDGE,"E1044"),sQuery(id+"F0.wireOp",EDGE,"E1045"),sQuery(id+"F0.wireOp",EDGE,"E1046"),sQuery(id+"F0.wireOp",EDGE,"E1047"),sQuery(id+"F0.wireOp",EDGE,"E1048"),sQuery(id+"F0.wireOp",EDGE,"E1049"),sQuery(id+"F0.wireOp",EDGE,"E1050"),sQuery(id+"F0.wireOp",EDGE,"E1051"),sQuery(id+"F0.wireOp",EDGE,"E1052"),sQuery(id+"F0.wireOp",EDGE,"E1053"),sQuery(id+"F0.wireOp",EDGE,"E1054"),sQuery(id+"F0.wireOp",EDGE,"E1055"),sQuery(id+"F0.wireOp",EDGE,"E1056"),sQuery(id+"F0.wireOp",EDGE,"E1057"),sQuery(id+"F0.wireOp",EDGE,"E1058"),sQuery(id+"F0.wireOp",EDGE,"E1059"),sQuery(id+"F0.wireOp",EDGE,"E1060"),sQuery(id+"F0.wireOp",EDGE,"E1061"),sQuery(id+"F0.wireOp",EDGE,"E1062"),sQuery(id+"F0.wireOp",EDGE,"E1063"),sQuery(id+"F0.wireOp",EDGE,"E1064"),sQuery(id+"F0.wireOp",EDGE,"E1065"),sQuery(id+"F0.wireOp",EDGE,"E1066"),sQuery(id+"F0.wireOp",EDGE,"E1067"),sQuery(id+"F0.wireOp",EDGE,"E1068"),sQuery(id+"F0.wireOp",EDGE,"E1069"),sQuery(id+"F0.wireOp",EDGE,"E1070"),sQuery(id+"F0.wireOp",EDGE,"E1071"),sQuery(id+"F0.wireOp",EDGE,"E1072"),sQuery(id+"F0.wireOp",EDGE,"E1073"),sQuery(id+"F0.wireOp",EDGE,"E1074"),sQuery(id+"F0.wireOp",EDGE,"E1075"),sQuery(id+"F0.wireOp",EDGE,"E1076"),sQuery(id+"F0.wireOp",EDGE,"E1077"),sQuery(id+"F0.wireOp",EDGE,"E1078"),sQuery(id+"F0.wireOp",EDGE,"E1079"),sQuery(id+"F0.wireOp",EDGE,"E1080"),sQuery(id+"F0.wireOp",EDGE,"E1081"),sQuery(id+"F0.wireOp",EDGE,"E1082"),sQuery(id+"F0.wireOp",EDGE,"E1083"),sQuery(id+"F0.wireOp",EDGE,"E1084"),sQuery(id+"F0.wireOp",EDGE,"E1085"),sQuery(id+"F0.wireOp",EDGE,"E1086"),sQuery(id+"F0.wireOp",EDGE,"E1087"),sQuery(id+"F0.wireOp",EDGE,"E1088"),sQuery(id+"F0.wireOp",EDGE,"E1089"),sQuery(id+"F0.wireOp",EDGE,"E1090"),sQuery(id+"F0.wireOp",EDGE,"E1091"),sQuery(id+"F0.wireOp",EDGE,"E1092"),sQuery(id+"F0.wireOp",EDGE,"E1093"),sQuery(id+"F0.wireOp",EDGE,"E1094"),sQuery(id+"F0.wireOp",EDGE,"E1095"),sQuery(id+"F0.wireOp",EDGE,"E1096"),sQuery(id+"F0.wireOp",EDGE,"E1097"),sQuery(id+"F0.wireOp",EDGE,"E1098"),sQuery(id+"F0.wireOp",EDGE,"E1099"),sQuery(id+"F0.wireOp",EDGE,"E1100"),sQuery(id+"F0.wireOp",EDGE,"E1101"),sQuery(id+"F0.wireOp",EDGE,"E1102"),sQuery(id+"F0.wireOp",EDGE,"E1103"),sQuery(id+"F0.wireOp",EDGE,"E1104"),sQuery(id+"F0.wireOp",EDGE,"E1105"),sQuery(id+"F0.wireOp",EDGE,"E1106"),sQuery(id+"F0.wireOp",EDGE,"E1107"),sQuery(id+"F0.wireOp",EDGE,"E1108"),sQuery(id+"F0.wireOp",EDGE,"E1109"),sQuery(id+"F0.wireOp",EDGE,"E1110"),sQuery(id+"F0.wireOp",EDGE,"E1111"),sQuery(id+"F0.wireOp",EDGE,"E1112"),sQuery(id+"F0.wireOp",EDGE,"E1113"),sQuery(id+"F0.wireOp",EDGE,"E1114"),sQuery(id+"F0.wireOp",EDGE,"E1115"),sQuery(id+"F0.wireOp",EDGE,"E1116"),sQuery(id+"F0.wireOp",EDGE,"E1117"),sQuery(id+"F0.wireOp",EDGE,"E1118"),sQuery(id+"F0.wireOp",EDGE,"E1119"),sQuery(id+"F0.wireOp",EDGE,"E1120"),sQuery(id+"F0.wireOp",EDGE,"E1121"),sQuery(id+"F0.wireOp",EDGE,"E1122"),sQuery(id+"F0.wireOp",EDGE,"E1123"),sQuery(id+"F0.wireOp",EDGE,"E1124"),sQuery(id+"F0.wireOp",EDGE,"E1125"),sQuery(id+"F0.wireOp",EDGE,"E1126"),sQuery(id+"F0.wireOp",EDGE,"E1127"),sQuery(id+"F0.wireOp",EDGE,"E1128"),sQuery(id+"F0.wireOp",EDGE,"E1129"),sQuery(id+"F0.wireOp",EDGE,"E1130"),sQuery(id+"F0.wireOp",EDGE,"E1131"),sQuery(id+"F0.wireOp",EDGE,"E1132"),sQuery(id+"F0.wireOp",EDGE,"E1133"),sQuery(id+"F0.wireOp",EDGE,"E1134"),sQuery(id+"F0.wireOp",EDGE,"E1135"),sQuery(id+"F0.wireOp",EDGE,"E1136"),sQuery(id+"F0.wireOp",EDGE,"E1137"),sQuery(id+"F0.wireOp",EDGE,"E1138"),sQuery(id+"F0.wireOp",EDGE,"E1139"),sQuery(id+"F0.wireOp",EDGE,"E1140"),sQuery(id+"F0.wireOp",EDGE,"E1141"),sQuery(id+"F0.wireOp",EDGE,"E1142"),sQuery(id+"F0.wireOp",EDGE,"E1143"),sQuery(id+"F0.wireOp",EDGE,"E1144"),sQuery(id+"F0.wireOp",EDGE,"E1145"),sQuery(id+"F0.wireOp",EDGE,"E1146"),sQuery(id+"F0.wireOp",EDGE,"E1147"),sQuery(id+"F0.wireOp",EDGE,"E1148"),sQuery(id+"F0.wireOp",EDGE,"E1149"),sQuery(id+"F0.wireOp",EDGE,"E1150"),sQuery(id+"F0.wireOp",EDGE,"E1151"),sQuery(id+"F0.wireOp",EDGE,"E1152"),sQuery(id+"F0.wireOp",EDGE,"E1153"),sQuery(id+"F0.wireOp",EDGE,"E1154"),sQuery(id+"F0.wireOp",EDGE,"E1155"),sQuery(id+"F0.wireOp",EDGE,"E1156"),sQuery(id+"F0.wireOp",EDGE,"E1157"),sQuery(id+"F0.wireOp",EDGE,"E1158"),sQuery(id+"F0.wireOp",EDGE,"E1159"),sQuery(id+"F0.wireOp",EDGE,"E1160"),sQuery(id+"F0.wireOp",EDGE,"E1161"),sQuery(id+"F0.wireOp",EDGE,"E1162"),sQuery(id+"F0.wireOp",EDGE,"E1163"),sQuery(id+"F0.wireOp",EDGE,"E1164"),sQuery(id+"F0.wireOp",EDGE,"E1165"),sQuery(id+"F0.wireOp",EDGE,"E1166"),sQuery(id+"F0.wireOp",EDGE,"E1167"),sQuery(id+"F0.wireOp",EDGE,"E1168"),sQuery(id+"F0.wireOp",EDGE,"E1169"),sQuery(id+"F0.wireOp",EDGE,"E1170"),sQuery(id+"F0.wireOp",EDGE,"E1171"),sQuery(id+"F0.wireOp",EDGE,"E1172"),sQuery(id+"F0.wireOp",EDGE,"E1173"),sQuery(id+"F0.wireOp",EDGE,"E1174"),sQuery(id+"F0.wireOp",EDGE,"E1175"),sQuery(id+"F0.wireOp",EDGE,"E1176"),sQuery(id+"F0.wireOp",EDGE,"E1177"),sQuery(id+"F0.wireOp",EDGE,"E1178"),sQuery(id+"F0.wireOp",EDGE,"E1179"),sQuery(id+"F0.wireOp",EDGE,"E1180"),sQuery(id+"F0.wireOp",EDGE,"E1181"),sQuery(id+"F0.wireOp",EDGE,"E1182"),sQuery(id+"F0.wireOp",EDGE,"E1183"),sQuery(id+"F0.wireOp",EDGE,"E1184"),sQuery(id+"F0.wireOp",EDGE,"E1185"),sQuery(id+"F0.wireOp",EDGE,"E1186"),sQuery(id+"F0.wireOp",EDGE,"E1187"),sQuery(id+"F0.wireOp",EDGE,"E1188"),sQuery(id+"F0.wireOp",EDGE,"E1189"),sQuery(id+"F0.wireOp",EDGE,"E1190"),sQuery(id+"F0.wireOp",EDGE,"E1191"),sQuery(id+"F0.wireOp",EDGE,"E1192"),sQuery(id+"F0.wireOp",EDGE,"E1193"),sQuery(id+"F0.wireOp",EDGE,"E1194"),sQuery(id+"F0.wireOp",EDGE,"E1195"),sQuery(id+"F0.wireOp",EDGE,"E1196"),sQuery(id+"F0.wireOp",EDGE,"E1197"),sQuery(id+"F0.wireOp",EDGE,"E1198"),sQuery(id+"F0.wireOp",EDGE,"E1199"),sQuery(id+"F0.wireOp",EDGE,"E1200"),sQuery(id+"F0.wireOp",EDGE,"E1201"),sQuery(id+"F0.wireOp",EDGE,"E1202"),sQuery(id+"F0.wireOp",EDGE,"E1203"),sQuery(id+"F0.wireOp",EDGE,"E1204"),sQuery(id+"F0.wireOp",EDGE,"E1205"),sQuery(id+"F0.wireOp",EDGE,"E1206"),sQuery(id+"F0.wireOp",EDGE,"E1207"),sQuery(id+"F0.wireOp",EDGE,"E1208"),sQuery(id+"F0.wireOp",EDGE,"E1209"),sQuery(id+"F0.wireOp",EDGE,"E1210"),sQuery(id+"F0.wireOp",EDGE,"E1211"),sQuery(id+"F0.wireOp",EDGE,"E1212"),sQuery(id+"F0.wireOp",EDGE,"E1213"),sQuery(id+"F0.wireOp",EDGE,"E1214"),sQuery(id+"F0.wireOp",EDGE,"E1215"),sQuery(id+"F0.wireOp",EDGE,"E1216"),sQuery(id+"F0.wireOp",EDGE,"E1217"),sQuery(id+"F0.wireOp",EDGE,"E1218"),sQuery(id+"F0.wireOp",EDGE,"E1219"),sQuery(id+"F0.wireOp",EDGE,"E1220"),sQuery(id+"F0.wireOp",EDGE,"E1221"),sQuery(id+"F0.wireOp",EDGE,"E1222"),sQuery(id+"F0.wireOp",EDGE,"E1223"),sQuery(id+"F0.wireOp",EDGE,"E1224"),sQuery(id+"F0.wireOp",EDGE,"E1225"),sQuery(id+"F0.wireOp",EDGE,"E1226"),sQuery(id+"F0.wireOp",EDGE,"E1227"),sQuery(id+"F0.wireOp",EDGE,"E1228"),sQuery(id+"F0.wireOp",EDGE,"E1229"),sQuery(id+"F0.wireOp",EDGE,"E1230"),sQuery(id+"F0.wireOp",EDGE,"E1231"),sQuery(id+"F0.wireOp",EDGE,"E1232"),sQuery(id+"F0.wireOp",EDGE,"E1233"),sQuery(id+"F0.wireOp",EDGE,"E1234"),sQuery(id+"F0.wireOp",EDGE,"E1235"),sQuery(id+"F0.wireOp",EDGE,"E1236"),sQuery(id+"F0.wireOp",EDGE,"E1237"),sQuery(id+"F0.wireOp",EDGE,"E1238"),sQuery(id+"F0.wireOp",EDGE,"E1239"),sQuery(id+"F0.wireOp",EDGE,"E1240"),sQuery(id+"F0.wireOp",EDGE,"E1241"),sQuery(id+"F0.wireOp",EDGE,"E1242"),sQuery(id+"F0.wireOp",EDGE,"E1243"),sQuery(id+"F0.wireOp",EDGE,"E1244"),sQuery(id+"F0.wireOp",EDGE,"E1245"),sQuery(id+"F0.wireOp",EDGE,"E1246"),sQuery(id+"F0.wireOp",EDGE,"E1247"),sQuery(id+"F0.wireOp",EDGE,"E1248"),sQuery(id+"F0.wireOp",EDGE,"E1249"),sQuery(id+"F0.wireOp",EDGE,"E1250"),sQuery(id+"F0.wireOp",EDGE,"E1251"),sQuery(id+"F0.wireOp",EDGE,"E1252"),sQuery(id+"F0.wireOp",EDGE,"E1253"),sQuery(id+"F0.wireOp",EDGE,"E1254"),sQuery(id+"F0.wireOp",EDGE,"E1255"),sQuery(id+"F0.wireOp",EDGE,"E1256"),sQuery(id+"F0.wireOp",EDGE,"E1257"),sQuery(id+"F0.wireOp",EDGE,"E1258"),sQuery(id+"F0.wireOp",EDGE,"E1259"),sQuery(id+"F0.wireOp",EDGE,"E1260"),sQuery(id+"F0.wireOp",EDGE,"E1261"),sQuery(id+"F0.wireOp",EDGE,"E1262"),sQuery(id+"F0.wireOp",EDGE,"E1263"),sQuery(id+"F0.wireOp",EDGE,"E1264"),sQuery(id+"F0.wireOp",EDGE,"E1265"),sQuery(id+"F0.wireOp",EDGE,"E1266"),sQuery(id+"F0.wireOp",EDGE,"E1267"),sQuery(id+"F0.wireOp",EDGE,"E1268"),sQuery(id+"F0.wireOp",EDGE,"E1269"),sQuery(id+"F0.wireOp",EDGE,"E1270"),sQuery(id+"F0.wireOp",EDGE,"E1271"),sQuery(id+"F0.wireOp",EDGE,"E1272"),sQuery(id+"F0.wireOp",EDGE,"E1273"),sQuery(id+"F0.wireOp",EDGE,"E1274"),sQuery(id+"F0.wireOp",EDGE,"E1275"),sQuery(id+"F0.wireOp",EDGE,"E1276"),sQuery(id+"F0.wireOp",EDGE,"E1277"),sQuery(id+"F0.wireOp",EDGE,"E1278"),sQuery(id+"F0.wireOp",EDGE,"E1279"),sQuery(id+"F0.wireOp",EDGE,"E1280"),sQuery(id+"F0.wireOp",EDGE,"E1281"),sQuery(id+"F0.wireOp",EDGE,"E1282"),sQuery(id+"F0.wireOp",EDGE,"E1283"),sQuery(id+"F0.wireOp",EDGE,"E1284"),sQuery(id+"F0.wireOp",EDGE,"E1285"),sQuery(id+"F0.wireOp",EDGE,"E1286"),sQuery(id+"F0.wireOp",EDGE,"E1287"),sQuery(id+"F0.wireOp",EDGE,"E1288"),sQuery(id+"F0.wireOp",EDGE,"E1289"),sQuery(id+"F0.wireOp",EDGE,"E1290"),sQuery(id+"F0.wireOp",EDGE,"E1291"),sQuery(id+"F0.wireOp",EDGE,"E1292"),sQuery(id+"F0.wireOp",EDGE,"E1293"),sQuery(id+"F0.wireOp",EDGE,"E1294"),sQuery(id+"F0.wireOp",EDGE,"E1295"),sQuery(id+"F0.wireOp",EDGE,"E1296"),sQuery(id+"F0.wireOp",EDGE,"E1297"),sQuery(id+"F0.wireOp",EDGE,"E1298"),sQuery(id+"F0.wireOp",EDGE,"E1299"),sQuery(id+"F0.wireOp",EDGE,"E1300"),sQuery(id+"F0.wireOp",EDGE,"E1301"),sQuery(id+"F0.wireOp",EDGE,"E1302"),sQuery(id+"F0.wireOp",EDGE,"E1303"),sQuery(id+"F0.wireOp",EDGE,"E1304"),sQuery(id+"F0.wireOp",EDGE,"E1305"),sQuery(id+"F0.wireOp",EDGE,"E1306"),sQuery(id+"F0.wireOp",EDGE,"E1307"),sQuery(id+"F0.wireOp",EDGE,"E1308"),sQuery(id+"F0.wireOp",EDGE,"E1309"),sQuery(id+"F0.wireOp",EDGE,"E1310"),sQuery(id+"F0.wireOp",EDGE,"E1311"),sQuery(id+"F0.wireOp",EDGE,"E1312"),sQuery(id+"F0.wireOp",EDGE,"E1313"),sQuery(id+"F0.wireOp",EDGE,"E1314"),sQuery(id+"F0.wireOp",EDGE,"E1315"),sQuery(id+"F0.wireOp",EDGE,"E1316"),sQuery(id+"F0.wireOp",EDGE,"E1317"),sQuery(id+"F0.wireOp",EDGE,"E1318"),sQuery(id+"F0.wireOp",EDGE,"E1319"),sQuery(id+"F0.wireOp",EDGE,"E1320"),sQuery(id+"F0.wireOp",EDGE,"E1321"),sQuery(id+"F0.wireOp",EDGE,"E1322"),sQuery(id+"F0.wireOp",EDGE,"E1323"),sQuery(id+"F0.wireOp",EDGE,"E1324"),sQuery(id+"F0.wireOp",EDGE,"E1325"),sQuery(id+"F0.wireOp",EDGE,"E1326"),sQuery(id+"F0.wireOp",EDGE,"E1327"),sQuery(id+"F0.wireOp",EDGE,"E1328"),sQuery(id+"F0.wireOp",EDGE,"E1329"),sQuery(id+"F0.wireOp",EDGE,"E1330"),sQuery(id+"F0.wireOp",EDGE,"E1331"),sQuery(id+"F0.wireOp",EDGE,"E1332"),sQuery(id+"F0.wireOp",EDGE,"E1333"),sQuery(id+"F0.wireOp",EDGE,"E1334"),sQuery(id+"F0.wireOp",EDGE,"E1335"),sQuery(id+"F0.wireOp",EDGE,"E1336"),sQuery(id+"F0.wireOp",EDGE,"E1337"),sQuery(id+"F0.wireOp",EDGE,"E1338"),sQuery(id+"F0.wireOp",EDGE,"E1339"),sQuery(id+"F0.wireOp",EDGE,"E1340"),sQuery(id+"F0.wireOp",EDGE,"E1341"),sQuery(id+"F0.wireOp",EDGE,"E1342"),sQuery(id+"F0.wireOp",EDGE,"E1343"),sQuery(id+"F0.wireOp",EDGE,"E1344"),sQuery(id+"F0.wireOp",EDGE,"E1345"),sQuery(id+"F0.wireOp",EDGE,"E1346"),sQuery(id+"F0.wireOp",EDGE,"E1347"),sQuery(id+"F0.wireOp",EDGE,"E1348"),sQuery(id+"F0.wireOp",EDGE,"E1349"),sQuery(id+"F0.wireOp",EDGE,"E1350"),sQuery(id+"F0.wireOp",EDGE,"E1351"),sQuery(id+"F0.wireOp",EDGE,"E1352"),sQuery(id+"F0.wireOp",EDGE,"E1353"),sQuery(id+"F0.wireOp",EDGE,"E1354"),sQuery(id+"F0.wireOp",EDGE,"E1355"),sQuery(id+"F0.wireOp",EDGE,"E1356"),sQuery(id+"F0.wireOp",EDGE,"E1357"),sQuery(id+"F0.wireOp",EDGE,"E1358"),sQuery(id+"F0.wireOp",EDGE,"E1359"),sQuery(id+"F0.wireOp",EDGE,"E1360"),sQuery(id+"F0.wireOp",EDGE,"E1361"),sQuery(id+"F0.wireOp",EDGE,"E1362"),sQuery(id+"F0.wireOp",EDGE,"E1363"),sQuery(id+"F0.wireOp",EDGE,"E1364"),sQuery(id+"F0.wireOp",EDGE,"E1365"),sQuery(id+"F0.wireOp",EDGE,"E1366"),sQuery(id+"F0.wireOp",EDGE,"E1367"),sQuery(id+"F0.wireOp",EDGE,"E1368"),sQuery(id+"F0.wireOp",EDGE,"E1369"),sQuery(id+"F0.wireOp",EDGE,"E1370"),sQuery(id+"F0.wireOp",EDGE,"E1371"),sQuery(id+"F0.wireOp",EDGE,"E1372"),sQuery(id+"F0.wireOp",EDGE,"E1373"),sQuery(id+"F0.wireOp",EDGE,"E1374"),sQuery(id+"F0.wireOp",EDGE,"E1375"),sQuery(id+"F0.wireOp",EDGE,"E1376"),sQuery(id+"F0.wireOp",EDGE,"E1377"),sQuery(id+"F0.wireOp",EDGE,"E1378"),sQuery(id+"F0.wireOp",EDGE,"E1379"),sQuery(id+"F0.wireOp",EDGE,"E1380"),sQuery(id+"F0.wireOp",EDGE,"E1381"),sQuery(id+"F0.wireOp",EDGE,"E1382"),sQuery(id+"F0.wireOp",EDGE,"E1383"),sQuery(id+"F0.wireOp",EDGE,"E1384"),sQuery(id+"F0.wireOp",EDGE,"E1385"),sQuery(id+"F0.wireOp",EDGE,"E1386"),sQuery(id+"F0.wireOp",EDGE,"E1387"),sQuery(id+"F0.wireOp",EDGE,"E1388"),sQuery(id+"F0.wireOp",EDGE,"E1389"),sQuery(id+"F0.wireOp",EDGE,"E1390"),sQuery(id+"F0.wireOp",EDGE,"E1391"),sQuery(id+"F0.wireOp",EDGE,"E1392"),sQuery(id+"F0.wireOp",EDGE,"E1393"),sQuery(id+"F0.wireOp",EDGE,"E1394"),sQuery(id+"F0.wireOp",EDGE,"E1395"),sQuery(id+"F0.wireOp",EDGE,"E1396"),sQuery(id+"F0.wireOp",EDGE,"E1397"),sQuery(id+"F0.wireOp",EDGE,"E1398"),sQuery(id+"F0.wireOp",EDGE,"E1399"),sQuery(id+"F0.wireOp",EDGE,"E1400"),sQuery(id+"F0.wireOp",EDGE,"E1401"),sQuery(id+"F0.wireOp",EDGE,"E1402"),sQuery(id+"F0.wireOp",EDGE,"E1403"),sQuery(id+"F0.wireOp",EDGE,"E1404"),sQuery(id+"F0.wireOp",EDGE,"E1405"),sQuery(id+"F0.wireOp",EDGE,"E1406"),sQuery(id+"F0.wireOp",EDGE,"E1407"),sQuery(id+"F0.wireOp",EDGE,"E1408"),sQuery(id+"F0.wireOp",EDGE,"E1409"),sQuery(id+"F0.wireOp",EDGE,"E1410"),sQuery(id+"F0.wireOp",EDGE,"E1411"),sQuery(id+"F0.wireOp",EDGE,"E1412"),sQuery(id+"F0.wireOp",EDGE,"E1413"),sQuery(id+"F0.wireOp",EDGE,"E1414"),sQuery(id+"F0.wireOp",EDGE,"E1415"),sQuery(id+"F0.wireOp",EDGE,"E1416"),sQuery(id+"F0.wireOp",EDGE,"E1417"),sQuery(id+"F0.wireOp",EDGE,"E1418"),sQuery(id+"F0.wireOp",EDGE,"E1419"),sQuery(id+"F0.wireOp",EDGE,"E1420"),sQuery(id+"F0.wireOp",EDGE,"E1421"),sQuery(id+"F0.wireOp",EDGE,"E1422"),sQuery(id+"F0.wireOp",EDGE,"E1423"),sQuery(id+"F0.wireOp",EDGE,"E1424"),sQuery(id+"F0.wireOp",EDGE,"E1425"),sQuery(id+"F0.wireOp",EDGE,"E1426"),sQuery(id+"F0.wireOp",EDGE,"E1427"),sQuery(id+"F0.wireOp",EDGE,"E1428"),sQuery(id+"F0.wireOp",EDGE,"E1429"),sQuery(id+"F0.wireOp",EDGE,"E1430"),sQuery(id+"F0.wireOp",EDGE,"E1431"),sQuery(id+"F0.wireOp",EDGE,"E1432"),sQuery(id+"F0.wireOp",EDGE,"E1433"),sQuery(id+"F0.wireOp",EDGE,"E1434"),sQuery(id+"F0.wireOp",EDGE,"E1435"),sQuery(id+"F0.wireOp",EDGE,"E1436"),sQuery(id+"F0.wireOp",EDGE,"E1437"),sQuery(id+"F0.wireOp",EDGE,"E1438"),sQuery(id+"F0.wireOp",EDGE,"E1439"),sQuery(id+"F0.wireOp",EDGE,"E1440"),sQuery(id+"F0.wireOp",EDGE,"E1441"),sQuery(id+"F0.wireOp",EDGE,"E1442"),sQuery(id+"F0.wireOp",EDGE,"E1443"),sQuery(id+"F0.wireOp",EDGE,"E1444"),sQuery(id+"F0.wireOp",EDGE,"E1445"),sQuery(id+"F0.wireOp",EDGE,"E1446"),sQuery(id+"F0.wireOp",EDGE,"E1447"),sQuery(id+"F0.wireOp",EDGE,"E1448"),sQuery(id+"F0.wireOp",EDGE,"E1449"),sQuery(id+"F0.wireOp",EDGE,"E1450"),sQuery(id+"F0.wireOp",EDGE,"E1451"),sQuery(id+"F0.wireOp",EDGE,"E1452"),sQuery(id+"F0.wireOp",EDGE,"E1453"),sQuery(id+"F0.wireOp",EDGE,"E1454"),sQuery(id+"F0.wireOp",EDGE,"E1455"),sQuery(id+"F0.wireOp",EDGE,"E1456"),sQuery(id+"F0.wireOp",EDGE,"E1457"),sQuery(id+"F0.wireOp",EDGE,"E1458"),sQuery(id+"F0.wireOp",EDGE,"E1459"),sQuery(id+"F0.wireOp",EDGE,"E1460"),sQuery(id+"F0.wireOp",EDGE,"E1461"),sQuery(id+"F0.wireOp",EDGE,"E1462"),sQuery(id+"F0.wireOp",EDGE,"E1463"),sQuery(id+"F0.wireOp",EDGE,"E1464"),sQuery(id+"F0.wireOp",EDGE,"E1465"),sQuery(id+"F0.wireOp",EDGE,"E1466"),sQuery(id+"F0.wireOp",EDGE,"E1467"),sQuery(id+"F0.wireOp",EDGE,"E1468"),sQuery(id+"F0.wireOp",EDGE,"E1469"),sQuery(id+"F0.wireOp",EDGE,"E1470"),sQuery(id+"F0.wireOp",EDGE,"E1471"),sQuery(id+"F0.wireOp",EDGE,"E1472"),sQuery(id+"F0.wireOp",EDGE,"E1473"),sQuery(id+"F0.wireOp",EDGE,"E1474"),sQuery(id+"F0.wireOp",EDGE,"E1475"),sQuery(id+"F0.wireOp",EDGE,"E1476"),sQuery(id+"F0.wireOp",EDGE,"E1477"),sQuery(id+"F0.wireOp",EDGE,"E1478"),sQuery(id+"F0.wireOp",EDGE,"E1479"),sQuery(id+"F0.wireOp",EDGE,"E1480"),sQuery(id+"F0.wireOp",EDGE,"E1481"),sQuery(id+"F0.wireOp",EDGE,"E1482"),sQuery(id+"F0.wireOp",EDGE,"E1483"),sQuery(id+"F0.wireOp",EDGE,"E1484"),sQuery(id+"F0.wireOp",EDGE,"E1485"),sQuery(id+"F0.wireOp",EDGE,"E1486"),sQuery(id+"F0.wireOp",EDGE,"E1487"),sQuery(id+"F0.wireOp",EDGE,"E1488"),sQuery(id+"F0.wireOp",EDGE,"E1489"),sQuery(id+"F0.wireOp",EDGE,"E1490"),sQuery(id+"F0.wireOp",EDGE,"E1491"),sQuery(id+"F0.wireOp",EDGE,"E1492"),sQuery(id+"F0.wireOp",EDGE,"E1493"),sQuery(id+"F0.wireOp",EDGE,"E1494"),sQuery(id+"F0.wireOp",EDGE,"E1495"),sQuery(id+"F0.wireOp",EDGE,"E1496"),sQuery(id+"F0.wireOp",EDGE,"E1497"),sQuery(id+"F0.wireOp",EDGE,"E1498"),sQuery(id+"F0.wireOp",EDGE,"E1499"),sQuery(id+"F0.wireOp",EDGE,"E1500"),sQuery(id+"F0.wireOp",EDGE,"E1501"),sQuery(id+"F0.wireOp",EDGE,"E1502"),sQuery(id+"F0.wireOp",EDGE,"E1503"),sQuery(id+"F0.wireOp",EDGE,"E1504"),sQuery(id+"F0.wireOp",EDGE,"E1505"),sQuery(id+"F0.wireOp",EDGE,"E1506"),sQuery(id+"F0.wireOp",EDGE,"E1507"),sQuery(id+"F0.wireOp",EDGE,"E1508"),sQuery(id+"F0.wireOp",EDGE,"E1509"),sQuery(id+"F0.wireOp",EDGE,"E1510"),sQuery(id+"F0.wireOp",EDGE,"E1511"),sQuery(id+"F0.wireOp",EDGE,"E1512"),sQuery(id+"F0.wireOp",EDGE,"E1513"),sQuery(id+"F0.wireOp",EDGE,"E1514"),sQuery(id+"F0.wireOp",EDGE,"E1515"),sQuery(id+"F0.wireOp",EDGE,"E1516"),sQuery(id+"F0.wireOp",EDGE,"E1517"),sQuery(id+"F0.wireOp",EDGE,"E1518"),sQuery(id+"F0.wireOp",EDGE,"E1519"),sQuery(id+"F0.wireOp",EDGE,"E1520"),sQuery(id+"F0.wireOp",EDGE,"E1521"),sQuery(id+"F0.wireOp",EDGE,"E1522"),sQuery(id+"F0.wireOp",EDGE,"E1523"),sQuery(id+"F0.wireOp",EDGE,"E1524"),sQuery(id+"F0.wireOp",EDGE,"E1525"),sQuery(id+"F0.wireOp",EDGE,"E1526"),sQuery(id+"F0.wireOp",EDGE,"E1527"),sQuery(id+"F0.wireOp",EDGE,"E1528"),sQuery(id+"F0.wireOp",EDGE,"E1529"),sQuery(id+"F0.wireOp",EDGE,"E1530"),sQuery(id+"F0.wireOp",EDGE,"E1531"),sQuery(id+"F0.wireOp",EDGE,"E1532"),sQuery(id+"F0.wireOp",EDGE,"E1533"),sQuery(id+"F0.wireOp",EDGE,"E1534"),sQuery(id+"F0.wireOp",EDGE,"E1535"),sQuery(id+"F0.wireOp",EDGE,"E1536"),sQuery(id+"F0.wireOp",EDGE,"E1537"),sQuery(id+"F0.wireOp",EDGE,"E1538"),sQuery(id+"F0.wireOp",EDGE,"E1539"),sQuery(id+"F0.wireOp",EDGE,"E1540"),sQuery(id+"F0.wireOp",EDGE,"E1541"),sQuery(id+"F0.wireOp",EDGE,"E1542"),sQuery(id+"F0.wireOp",EDGE,"E1543"),sQuery(id+"F0.wireOp",EDGE,"E1544"),sQuery(id+"F0.wireOp",EDGE,"E1545"),sQuery(id+"F0.wireOp",EDGE,"E1546"),sQuery(id+"F0.wireOp",EDGE,"E1547"),sQuery(id+"F0.wireOp",EDGE,"E1548"),sQuery(id+"F0.wireOp",EDGE,"E1549"),sQuery(id+"F0.wireOp",EDGE,"E1550"),sQuery(id+"F0.wireOp",EDGE,"E1551"),sQuery(id+"F0.wireOp",EDGE,"E1552"),sQuery(id+"F0.wireOp",EDGE,"E1553"),sQuery(id+"F0.wireOp",EDGE,"E1554"),sQuery(id+"F0.wireOp",EDGE,"E1555"),sQuery(id+"F0.wireOp",EDGE,"E1556"),sQuery(id+"F0.wireOp",EDGE,"E1557"),sQuery(id+"F0.wireOp",EDGE,"E1558"),sQuery(id+"F0.wireOp",EDGE,"E1559"),sQuery(id+"F0.wireOp",EDGE,"E1560"),sQuery(id+"F0.wireOp",EDGE,"E1561"),sQuery(id+"F0.wireOp",EDGE,"E1562"),sQuery(id+"F0.wireOp",EDGE,"E1563"),sQuery(id+"F0.wireOp",EDGE,"E1564"),sQuery(id+"F0.wireOp",EDGE,"E1565"),sQuery(id+"F0.wireOp",EDGE,"E1566"),sQuery(id+"F0.wireOp",EDGE,"E1567"),sQuery(id+"F0.wireOp",EDGE,"E1568"),sQuery(id+"F0.wireOp",EDGE,"E1569"),sQuery(id+"F0.wireOp",EDGE,"E1570"),sQuery(id+"F0.wireOp",EDGE,"E1571"),sQuery(id+"F0.wireOp",EDGE,"E1572"),sQuery(id+"F0.wireOp",EDGE,"E1573"),sQuery(id+"F0.wireOp",EDGE,"E1574"),sQuery(id+"F0.wireOp",EDGE,"E1575"),sQuery(id+"F0.wireOp",EDGE,"E1576"),sQuery(id+"F0.wireOp",EDGE,"E1577"),sQuery(id+"F0.wireOp",EDGE,"E1578"),sQuery(id+"F0.wireOp",EDGE,"E1579"),sQuery(id+"F0.wireOp",EDGE,"E1580"),sQuery(id+"F0.wireOp",EDGE,"E1581"),sQuery(id+"F0.wireOp",EDGE,"E1582"),sQuery(id+"F0.wireOp",EDGE,"E1583"),sQuery(id+"F0.wireOp",EDGE,"E1584"),sQuery(id+"F0.wireOp",EDGE,"E1585"),sQuery(id+"F0.wireOp",EDGE,"E1586"),sQuery(id+"F0.wireOp",EDGE,"E1587"),sQuery(id+"F0.wireOp",EDGE,"E1588"),sQuery(id+"F0.wireOp",EDGE,"E1589"),sQuery(id+"F0.wireOp",EDGE,"E1590"),sQuery(id+"F0.wireOp",EDGE,"E1591"),sQuery(id+"F0.wireOp",EDGE,"E1592"),sQuery(id+"F0.wireOp",EDGE,"E1593"),sQuery(id+"F0.wireOp",EDGE,"E1594"),sQuery(id+"F0.wireOp",EDGE,"E1595"),sQuery(id+"F0.wireOp",EDGE,"E1596"),sQuery(id+"F0.wireOp",EDGE,"E1597"),sQuery(id+"F0.wireOp",EDGE,"E1598"),sQuery(id+"F0.wireOp",EDGE,"E1599"),sQuery(id+"F0.wireOp",EDGE,"E1600"),sQuery(id+"F0.wireOp",EDGE,"E1601"),sQuery(id+"F0.wireOp",EDGE,"E1602"),sQuery(id+"F0.wireOp",EDGE,"E1603"),sQuery(id+"F0.wireOp",EDGE,"E1604"),sQuery(id+"F0.wireOp",EDGE,"E1605"),sQuery(id+"F0.wireOp",EDGE,"E1606"),sQuery(id+"F0.wireOp",EDGE,"E1607"),sQuery(id+"F0.wireOp",EDGE,"E1608"),sQuery(id+"F0.wireOp",EDGE,"E1609"),sQuery(id+"F0.wireOp",EDGE,"E1610"),sQuery(id+"F0.wireOp",EDGE,"E1611"),sQuery(id+"F0.wireOp",EDGE,"E1612"),sQuery(id+"F0.wireOp",EDGE,"E1613"),sQuery(id+"F0.wireOp",EDGE,"E1614"),sQuery(id+"F0.wireOp",EDGE,"E1615"),sQuery(id+"F0.wireOp",EDGE,"E1616"),sQuery(id+"F0.wireOp",EDGE,"E1617"),sQuery(id+"F0.wireOp",EDGE,"E1618"),sQuery(id+"F0.wireOp",EDGE,"E1619"),sQuery(id+"F0.wireOp",EDGE,"E1620"),sQuery(id+"F0.wireOp",EDGE,"E1621"),sQuery(id+"F0.wireOp",EDGE,"E1622"),sQuery(id+"F0.wireOp",EDGE,"E1623"),sQuery(id+"F0.wireOp",EDGE,"E1624"),sQuery(id+"F0.wireOp",EDGE,"E1625"),sQuery(id+"F0.wireOp",EDGE,"E1626"),sQuery(id+"F0.wireOp",EDGE,"E1627"),sQuery(id+"F0.wireOp",EDGE,"E1628"),sQuery(id+"F0.wireOp",EDGE,"E1629"),sQuery(id+"F0.wireOp",EDGE,"E1630"),sQuery(id+"F0.wireOp",EDGE,"E1631"),sQuery(id+"F0.wireOp",EDGE,"E1632"),sQuery(id+"F0.wireOp",EDGE,"E1633"),sQuery(id+"F0.wireOp",EDGE,"E1634"),sQuery(id+"F0.wireOp",EDGE,"E1635"),sQuery(id+"F0.wireOp",EDGE,"E1636"),sQuery(id+"F0.wireOp",EDGE,"E1637"),sQuery(id+"F0.wireOp",EDGE,"E1638"),sQuery(id+"F0.wireOp",EDGE,"E1639"),sQuery(id+"F0.wireOp",EDGE,"E1640"),sQuery(id+"F0.wireOp",EDGE,"E1641"),sQuery(id+"F0.wireOp",EDGE,"E1642"),sQuery(id+"F0.wireOp",EDGE,"E1643"),sQuery(id+"F0.wireOp",EDGE,"E1644"),sQuery(id+"F0.wireOp",EDGE,"E1645"),sQuery(id+"F0.wireOp",EDGE,"E1646"),sQuery(id+"F0.wireOp",EDGE,"E1647"),sQuery(id+"F0.wireOp",EDGE,"E1648"),sQuery(id+"F0.wireOp",EDGE,"E1649"),sQuery(id+"F0.wireOp",EDGE,"E1650"),sQuery(id+"F0.wireOp",EDGE,"E1651"),sQuery(id+"F0.wireOp",EDGE,"E1652"),sQuery(id+"F0.wireOp",EDGE,"E1653"),sQuery(id+"F0.wireOp",EDGE,"E1654"),sQuery(id+"F0.wireOp",EDGE,"E1655"),sQuery(id+"F0.wireOp",EDGE,"E1656"),sQuery(id+"F0.wireOp",EDGE,"E1657"),sQuery(id+"F0.wireOp",EDGE,"E1658"),sQuery(id+"F0.wireOp",EDGE,"E1659"),sQuery(id+"F0.wireOp",EDGE,"E1660"),sQuery(id+"F0.wireOp",EDGE,"E1661"),sQuery(id+"F0.wireOp",EDGE,"E1662"),sQuery(id+"F0.wireOp",EDGE,"E1663"),sQuery(id+"F0.wireOp",EDGE,"E1664"),sQuery(id+"F0.wireOp",EDGE,"E1665"),sQuery(id+"F0.wireOp",EDGE,"E1666"),sQuery(id+"F0.wireOp",EDGE,"E1667"),sQuery(id+"F0.wireOp",EDGE,"E1668"),sQuery(id+"F0.wireOp",EDGE,"E1669"),sQuery(id+"F0.wireOp",EDGE,"E1670"),sQuery(id+"F0.wireOp",EDGE,"E1671"),sQuery(id+"F0.wireOp",EDGE,"E1672"),sQuery(id+"F0.wireOp",EDGE,"E1673"),sQuery(id+"F0.wireOp",EDGE,"E1674"),sQuery(id+"F0.wireOp",EDGE,"E1675"),sQuery(id+"F0.wireOp",EDGE,"E1676"),sQuery(id+"F0.wireOp",EDGE,"E1677"),sQuery(id+"F0.wireOp",EDGE,"E1678"),sQuery(id+"F0.wireOp",EDGE,"E1679"),sQuery(id+"F0.wireOp",EDGE,"E1680"),sQuery(id+"F0.wireOp",EDGE,"E1681"),sQuery(id+"F0.wireOp",EDGE,"E1682"),sQuery(id+"F0.wireOp",EDGE,"E1683"),sQuery(id+"F0.wireOp",EDGE,"E1684"),sQuery(id+"F0.wireOp",EDGE,"E1685"),sQuery(id+"F0.wireOp",EDGE,"E1686"),sQuery(id+"F0.wireOp",EDGE,"E1687"),sQuery(id+"F0.wireOp",EDGE,"E1688"),sQuery(id+"F0.wireOp",EDGE,"E1689"),sQuery(id+"F0.wireOp",EDGE,"E1690"),sQuery(id+"F0.wireOp",EDGE,"E1691"),sQuery(id+"F0.wireOp",EDGE,"E1692"),sQuery(id+"F0.wireOp",EDGE,"E1693"),sQuery(id+"F0.wireOp",EDGE,"E1694"),sQuery(id+"F0.wireOp",EDGE,"E1695"),sQuery(id+"F0.wireOp",EDGE,"E1696"),sQuery(id+"F0.wireOp",EDGE,"E1697"),sQuery(id+"F0.wireOp",EDGE,"E1698"),sQuery(id+"F0.wireOp",EDGE,"E1699"),sQuery(id+"F0.wireOp",EDGE,"E1700"),sQuery(id+"F0.wireOp",EDGE,"E1701"),sQuery(id+"F0.wireOp",EDGE,"E1702"),sQuery(id+"F0.wireOp",EDGE,"E1703"),sQuery(id+"F0.wireOp",EDGE,"E1704"),sQuery(id+"F0.wireOp",EDGE,"E1705"),sQuery(id+"F0.wireOp",EDGE,"E1706"),sQuery(id+"F0.wireOp",EDGE,"E1707"),sQuery(id+"F0.wireOp",EDGE,"E1708"),sQuery(id+"F0.wireOp",EDGE,"E1709"),sQuery(id+"F0.wireOp",EDGE,"E1710"),sQuery(id+"F0.wireOp",EDGE,"E1711"),sQuery(id+"F0.wireOp",EDGE,"E1712"),sQuery(id+"F0.wireOp",EDGE,"E1713"),sQuery(id+"F0.wireOp",EDGE,"E1714"),sQuery(id+"F0.wireOp",EDGE,"E1715"),sQuery(id+"F0.wireOp",EDGE,"E1716"),sQuery(id+"F0.wireOp",EDGE,"E1717"),sQuery(id+"F0.wireOp",EDGE,"E1718"),sQuery(id+"F0.wireOp",EDGE,"E1719"),sQuery(id+"F0.wireOp",EDGE,"E1720"),sQuery(id+"F0.wireOp",EDGE,"E1721"),sQuery(id+"F0.wireOp",EDGE,"E1722"),sQuery(id+"F0.wireOp",EDGE,"E1723"),sQuery(id+"F0.wireOp",EDGE,"E1724"),sQuery(id+"F0.wireOp",EDGE,"E1725"),sQuery(id+"F0.wireOp",EDGE,"E1726"),sQuery(id+"F0.wireOp",EDGE,"E1727"),sQuery(id+"F0.wireOp",EDGE,"E1728"),sQuery(id+"F0.wireOp",EDGE,"E1729"),sQuery(id+"F0.wireOp",EDGE,"E1730"),sQuery(id+"F0.wireOp",EDGE,"E1731"),sQuery(id+"F0.wireOp",EDGE,"E1732"),sQuery(id+"F0.wireOp",EDGE,"E1733"),sQuery(id+"F0.wireOp",EDGE,"E1734"),sQuery(id+"F0.wireOp",EDGE,"E1735"),sQuery(id+"F0.wireOp",EDGE,"E1736"),sQuery(id+"F0.wireOp",EDGE,"E1737"),sQuery(id+"F0.wireOp",EDGE,"E1738"),sQuery(id+"F0.wireOp",EDGE,"E1739"),sQuery(id+"F0.wireOp",EDGE,"E1740"),sQuery(id+"F0.wireOp",EDGE,"E1741"),sQuery(id+"F0.wireOp",EDGE,"E1742"),sQuery(id+"F0.wireOp",EDGE,"E1743"),sQuery(id+"F0.wireOp",EDGE,"E1744"),sQuery(id+"F0.wireOp",EDGE,"E1745"),sQuery(id+"F0.wireOp",EDGE,"E1746"),sQuery(id+"F0.wireOp",EDGE,"E1747"),sQuery(id+"F0.wireOp",EDGE,"E1748"),sQuery(id+"F0.wireOp",EDGE,"E1749"),sQuery(id+"F0.wireOp",EDGE,"E1750"),sQuery(id+"F0.wireOp",EDGE,"E1751"),sQuery(id+"F0.wireOp",EDGE,"E1752"),sQuery(id+"F0.wireOp",EDGE,"E1753"),sQuery(id+"F0.wireOp",EDGE,"E1754"),sQuery(id+"F0.wireOp",EDGE,"E1755"),sQuery(id+"F0.wireOp",EDGE,"E1756"),sQuery(id+"F0.wireOp",EDGE,"E1757"),sQuery(id+"F0.wireOp",EDGE,"E1758"),sQuery(id+"F0.wireOp",EDGE,"E1759"),sQuery(id+"F0.wireOp",EDGE,"E1760"),sQuery(id+"F0.wireOp",EDGE,"E1761"),sQuery(id+"F0.wireOp",EDGE,"E1762"),sQuery(id+"F0.wireOp",EDGE,"E1763"),sQuery(id+"F0.wireOp",EDGE,"E1764"),sQuery(id+"F0.wireOp",EDGE,"E1765"),sQuery(id+"F0.wireOp",EDGE,"E1766"),sQuery(id+"F0.wireOp",EDGE,"E1767"),sQuery(id+"F0.wireOp",EDGE,"E1768"),sQuery(id+"F0.wireOp",EDGE,"E1769"),sQuery(id+"F0.wireOp",EDGE,"E1770"),sQuery(id+"F0.wireOp",EDGE,"E1771"),sQuery(id+"F0.wireOp",EDGE,"E1772"),sQuery(id+"F0.wireOp",EDGE,"E1773"),sQuery(id+"F0.wireOp",EDGE,"E1774"),sQuery(id+"F0.wireOp",EDGE,"E1775"),sQuery(id+"F0.wireOp",EDGE,"E1776"),sQuery(id+"F0.wireOp",EDGE,"E1777"),sQuery(id+"F0.wireOp",EDGE,"E1778"),sQuery(id+"F0.wireOp",EDGE,"E1779"),sQuery(id+"F0.wireOp",EDGE,"E1780"),sQuery(id+"F0.wireOp",EDGE,"E1781"),sQuery(id+"F0.wireOp",EDGE,"E1782"),sQuery(id+"F0.wireOp",EDGE,"E1783"),sQuery(id+"F0.wireOp",EDGE,"E1784"),sQuery(id+"F0.wireOp",EDGE,"E1785"),sQuery(id+"F0.wireOp",EDGE,"E1786"),sQuery(id+"F0.wireOp",EDGE,"E1787"),sQuery(id+"F0.wireOp",EDGE,"E1788"),sQuery(id+"F0.wireOp",EDGE,"E1789"),sQuery(id+"F0.wireOp",EDGE,"E1790"),sQuery(id+"F0.wireOp",EDGE,"E1791"),sQuery(id+"F0.wireOp",EDGE,"E1792"),sQuery(id+"F0.wireOp",EDGE,"E1793"),sQuery(id+"F0.wireOp",EDGE,"E1794"),sQuery(id+"F0.wireOp",EDGE,"E1795"),sQuery(id+"F0.wireOp",EDGE,"E1796"),sQuery(id+"F0.wireOp",EDGE,"E1797"),sQuery(id+"F0.wireOp",EDGE,"E1798"),sQuery(id+"F0.wireOp",EDGE,"E1799"),sQuery(id+"F0.wireOp",EDGE,"E1800"),sQuery(id+"F0.wireOp",EDGE,"E1801"),sQuery(id+"F0.wireOp",EDGE,"E1802"),sQuery(id+"F0.wireOp",EDGE,"E1803"),sQuery(id+"F0.wireOp",EDGE,"E1804"),sQuery(id+"F0.wireOp",EDGE,"E1805"),sQuery(id+"F0.wireOp",EDGE,"E1806"),sQuery(id+"F0.wireOp",EDGE,"E1807"),sQuery(id+"F0.wireOp",EDGE,"E1808"),sQuery(id+"F0.wireOp",EDGE,"E1809"),sQuery(id+"F0.wireOp",EDGE,"E1810"),sQuery(id+"F0.wireOp",EDGE,"E1811"),sQuery(id+"F0.wireOp",EDGE,"E1812"),sQuery(id+"F0.wireOp",EDGE,"E1813"),sQuery(id+"F0.wireOp",EDGE,"E1814"),sQuery(id+"F0.wireOp",EDGE,"E1815"),sQuery(id+"F0.wireOp",EDGE,"E1816"),sQuery(id+"F0.wireOp",EDGE,"E1817"),sQuery(id+"F0.wireOp",EDGE,"E1818"),sQuery(id+"F0.wireOp",EDGE,"E1819"),sQuery(id+"F0.wireOp",EDGE,"E1820"),sQuery(id+"F0.wireOp",EDGE,"E1821"),sQuery(id+"F0.wireOp",EDGE,"E1822"),sQuery(id+"F0.wireOp",EDGE,"E1823"),sQuery(id+"F0.wireOp",EDGE,"E1824"),sQuery(id+"F0.wireOp",EDGE,"E1825"),sQuery(id+"F0.wireOp",EDGE,"E1826"),sQuery(id+"F0.wireOp",EDGE,"E1827"),sQuery(id+"F0.wireOp",EDGE,"E1828"),sQuery(id+"F0.wireOp",EDGE,"E1829"),sQuery(id+"F0.wireOp",EDGE,"E1830"),sQuery(id+"F0.wireOp",EDGE,"E1831"),sQuery(id+"F0.wireOp",EDGE,"E1832"),sQuery(id+"F0.wireOp",EDGE,"E1833"),sQuery(id+"F0.wireOp",EDGE,"E1834"),sQuery(id+"F0.wireOp",EDGE,"E1835"),sQuery(id+"F0.wireOp",EDGE,"E1836"),sQuery(id+"F0.wireOp",EDGE,"E1837"),sQuery(id+"F0.wireOp",EDGE,"E1838"),sQuery(id+"F0.wireOp",EDGE,"E1839"),sQuery(id+"F0.wireOp",EDGE,"E1840"),sQuery(id+"F0.wireOp",EDGE,"E1841"),sQuery(id+"F0.wireOp",EDGE,"E1842"),sQuery(id+"F0.wireOp",EDGE,"E1843"),sQuery(id+"F0.wireOp",EDGE,"E1844"),sQuery(id+"F0.wireOp",EDGE,"E1845"),sQuery(id+"F0.wireOp",EDGE,"E1846"),sQuery(id+"F0.wireOp",EDGE,"E1847"),sQuery(id+"F0.wireOp",EDGE,"E1848"),sQuery(id+"F0.wireOp",EDGE,"E1849"),sQuery(id+"F0.wireOp",EDGE,"E1850"),sQuery(id+"F0.wireOp",EDGE,"E1851"),sQuery(id+"F0.wireOp",EDGE,"E1852"),sQuery(id+"F0.wireOp",EDGE,"E1853"),sQuery(id+"F0.wireOp",EDGE,"E1854"),sQuery(id+"F0.wireOp",EDGE,"E1855"),sQuery(id+"F0.wireOp",EDGE,"E1856"),sQuery(id+"F0.wireOp",EDGE,"E1857"),sQuery(id+"F0.wireOp",EDGE,"E1858"),sQuery(id+"F0.wireOp",EDGE,"E1859"),sQuery(id+"F0.wireOp",EDGE,"E1860"),sQuery(id+"F0.wireOp",EDGE,"E1861"),sQuery(id+"F0.wireOp",EDGE,"E1862"),sQuery(id+"F0.wireOp",EDGE,"E1863"),sQuery(id+"F0.wireOp",EDGE,"E1864"),sQuery(id+"F0.wireOp",EDGE,"E1865"),sQuery(id+"F0.wireOp",EDGE,"E1866"),sQuery(id+"F0.wireOp",EDGE,"E1867"),sQuery(id+"F0.wireOp",EDGE,"E1868"),sQuery(id+"F0.wireOp",EDGE,"E1869"),sQuery(id+"F0.wireOp",EDGE,"E1870"),sQuery(id+"F0.wireOp",EDGE,"E1871"),sQuery(id+"F0.wireOp",EDGE,"E1872"),sQuery(id+"F0.wireOp",EDGE,"E1873"),sQuery(id+"F0.wireOp",EDGE,"E1874"),sQuery(id+"F0.wireOp",EDGE,"E1875"),sQuery(id+"F0.wireOp",EDGE,"E1876"),sQuery(id+"F0.wireOp",EDGE,"E1877"),sQuery(id+"F0.wireOp",EDGE,"E1878"),sQuery(id+"F0.wireOp",EDGE,"E1879"),sQuery(id+"F0.wireOp",EDGE,"E1880"),sQuery(id+"F0.wireOp",EDGE,"E1881"),sQuery(id+"F0.wireOp",EDGE,"E1882"),sQuery(id+"F0.wireOp",EDGE,"E1883"),sQuery(id+"F0.wireOp",EDGE,"E1884"),sQuery(id+"F0.wireOp",EDGE,"E1885"),sQuery(id+"F0.wireOp",EDGE,"E1886"),sQuery(id+"F0.wireOp",EDGE,"E1887"),sQuery(id+"F0.wireOp",EDGE,"E1888"),sQuery(id+"F0.wireOp",EDGE,"E1889"),sQuery(id+"F0.wireOp",EDGE,"E1890"),sQuery(id+"F0.wireOp",EDGE,"E1891"),sQuery(id+"F0.wireOp",EDGE,"E1892"),sQuery(id+"F0.wireOp",EDGE,"E1893"),sQuery(id+"F0.wireOp",EDGE,"E1894"),sQuery(id+"F0.wireOp",EDGE,"E1895"),sQuery(id+"F0.wireOp",EDGE,"E1896"),sQuery(id+"F0.wireOp",EDGE,"E1897"),sQuery(id+"F0.wireOp",EDGE,"E1898"),sQuery(id+"F0.wireOp",EDGE,"E1899"),sQuery(id+"F0.wireOp",EDGE,"E1900"),sQuery(id+"F0.wireOp",EDGE,"E1901"),sQuery(id+"F0.wireOp",EDGE,"E1902"),sQuery(id+"F0.wireOp",EDGE,"E1903"),sQuery(id+"F0.wireOp",EDGE,"E1904"),sQuery(id+"F0.wireOp",EDGE,"E1905"),sQuery(id+"F0.wireOp",EDGE,"E1906"),sQuery(id+"F0.wireOp",EDGE,"E1907"),sQuery(id+"F0.wireOp",EDGE,"E1908"),sQuery(id+"F0.wireOp",EDGE,"E1909"),sQuery(id+"F0.wireOp",EDGE,"E1910"),sQuery(id+"F0.wireOp",EDGE,"E1911"),sQuery(id+"F0.wireOp",EDGE,"E1912"),sQuery(id+"F0.wireOp",EDGE,"E1913"),sQuery(id+"F0.wireOp",EDGE,"E1914"),sQuery(id+"F0.wireOp",EDGE,"E1915"),sQuery(id+"F0.wireOp",EDGE,"E1916"),sQuery(id+"F0.wireOp",EDGE,"E1917"),sQuery(id+"F0.wireOp",EDGE,"E1918"),sQuery(id+"F0.wireOp",EDGE,"E1919"),sQuery(id+"F0.wireOp",EDGE,"E1920"),sQuery(id+"F0.wireOp",EDGE,"E1921"),sQuery(id+"F0.wireOp",EDGE,"E1922"),sQuery(id+"F0.wireOp",EDGE,"E1923"),sQuery(id+"F0.wireOp",EDGE,"E1924"),sQuery(id+"F0.wireOp",EDGE,"E1925"),sQuery(id+"F0.wireOp",EDGE,"E1926"),sQuery(id+"F0.wireOp",EDGE,"E1927"),sQuery(id+"F0.wireOp",EDGE,"E1928"),sQuery(id+"F0.wireOp",EDGE,"E1929"),sQuery(id+"F0.wireOp",EDGE,"E1930"),sQuery(id+"F0.wireOp",EDGE,"E1931"),sQuery(id+"F0.wireOp",EDGE,"E1932"),sQuery(id+"F0.wireOp",EDGE,"E1933"),sQuery(id+"F0.wireOp",EDGE,"E1934"),sQuery(id+"F0.wireOp",EDGE,"E1935"),sQuery(id+"F0.wireOp",EDGE,"E1936"),sQuery(id+"F0.wireOp",EDGE,"E1937"),sQuery(id+"F0.wireOp",EDGE,"E1938"),sQuery(id+"F0.wireOp",EDGE,"E1939"),sQuery(id+"F0.wireOp",EDGE,"E1940"),sQuery(id+"F0.wireOp",EDGE,"E1941"),sQuery(id+"F0.wireOp",EDGE,"E1942"),sQuery(id+"F0.wireOp",EDGE,"E1943"),sQuery(id+"F0.wireOp",EDGE,"E1944"),sQuery(id+"F0.wireOp",EDGE,"E1945"),sQuery(id+"F0.wireOp",EDGE,"E1946"),sQuery(id+"F0.wireOp",EDGE,"E1947"),sQuery(id+"F0.wireOp",EDGE,"E1948"),sQuery(id+"F0.wireOp",EDGE,"E1949"),sQuery(id+"F0.wireOp",EDGE,"E1950"),sQuery(id+"F0.wireOp",EDGE,"E1951"),sQuery(id+"F0.wireOp",EDGE,"E1952"),sQuery(id+"F0.wireOp",EDGE,"E1953"),sQuery(id+"F0.wireOp",EDGE,"E1954"),sQuery(id+"F0.wireOp",EDGE,"E1955"),sQuery(id+"F0.wireOp",EDGE,"E1956"),sQuery(id+"F0.wireOp",EDGE,"E1957"),sQuery(id+"F0.wireOp",EDGE,"E1958"),sQuery(id+"F0.wireOp",EDGE,"E1959"),sQuery(id+"F0.wireOp",EDGE,"E1960"),sQuery(id+"F0.wireOp",EDGE,"E1961"),sQuery(id+"F0.wireOp",EDGE,"E1962"),sQuery(id+"F0.wireOp",EDGE,"E1963"),sQuery(id+"F0.wireOp",EDGE,"E1964"),sQuery(id+"F0.wireOp",EDGE,"E1965"),sQuery(id+"F0.wireOp",EDGE,"E1966"),sQuery(id+"F0.wireOp",EDGE,"E1967"),sQuery(id+"F0.wireOp",EDGE,"E1968"),sQuery(id+"F0.wireOp",EDGE,"E1969"),sQuery(id+"F0.wireOp",EDGE,"E1970"),sQuery(id+"F0.wireOp",EDGE,"E1971"),sQuery(id+"F0.wireOp",EDGE,"E1972"),sQuery(id+"F0.wireOp",EDGE,"E1973"),sQuery(id+"F0.wireOp",EDGE,"E1974"),sQuery(id+"F0.wireOp",EDGE,"E1975"),sQuery(id+"F0.wireOp",EDGE,"E1976"),sQuery(id+"F0.wireOp",EDGE,"E1977"),sQuery(id+"F0.wireOp",EDGE,"E1978"),sQuery(id+"F0.wireOp",EDGE,"E1979"),sQuery(id+"F0.wireOp",EDGE,"E1980"),sQuery(id+"F0.wireOp",EDGE,"E1981"),sQuery(id+"F0.wireOp",EDGE,"E1982"),sQuery(id+"F0.wireOp",EDGE,"E1983"),sQuery(id+"F0.wireOp",EDGE,"E1984"),sQuery(id+"F0.wireOp",EDGE,"E1985"),sQuery(id+"F0.wireOp",EDGE,"E1986"),sQuery(id+"F0.wireOp",EDGE,"E1987"),sQuery(id+"F0.wireOp",EDGE,"E1988"),sQuery(id+"F0.wireOp",EDGE,"E1989"),sQuery(id+"F0.wireOp",EDGE,"E1990"),sQuery(id+"F0.wireOp",EDGE,"E1991"),sQuery(id+"F0.wireOp",EDGE,"E1992"),sQuery(id+"F0.wireOp",EDGE,"E1993"),sQuery(id+"F0.wireOp",EDGE,"E1994"),sQuery(id+"F0.wireOp",EDGE,"E1995"),sQuery(id+"F0.wireOp",EDGE,"E1996"),sQuery(id+"F0.wireOp",EDGE,"E1997"),sQuery(id+"F0.wireOp",EDGE,"E1998"),sQuery(id+"F0.wireOp",EDGE,"E1999"),sQuery(id+"F0.wireOp",EDGE,"E2000"),sQuery(id+"F0.wireOp",EDGE,"E2001"),sQuery(id+"F0.wireOp",EDGE,"E2002"),sQuery(id+"F0.wireOp",EDGE,"E2003"),sQuery(id+"F0.wireOp",EDGE,"E2004"),sQuery(id+"F0.wireOp",EDGE,"E2005"),sQuery(id+"F0.wireOp",EDGE,"E2006"),sQuery(id+"F0.wireOp",EDGE,"E2007"),sQuery(id+"F0.wireOp",EDGE,"E2008"),sQuery(id+"F0.wireOp",EDGE,"E2009"),sQuery(id+"F0.wireOp",EDGE,"E2010"),sQuery(id+"F0.wireOp",EDGE,"E2011"),sQuery(id+"F0.wireOp",EDGE,"E2012"),sQuery(id+"F0.wireOp",EDGE,"E2013"),sQuery(id+"F0.wireOp",EDGE,"E2014"),sQuery(id+"F0.wireOp",EDGE,"E2015"),sQuery(id+"F0.wireOp",EDGE,"E2016"),sQuery(id+"F0.wireOp",EDGE,"E2017"),sQuery(id+"F0.wireOp",EDGE,"E2018"),sQuery(id+"F0.wireOp",EDGE,"E2019"),sQuery(id+"F0.wireOp",EDGE,"E2020"),sQuery(id+"F0.wireOp",EDGE,"E2021"),sQuery(id+"F0.wireOp",EDGE,"E2022"),sQuery(id+"F0.wireOp",EDGE,"E2023"),sQuery(id+"F0.wireOp",EDGE,"E2024"),sQuery(id+"F0.wireOp",EDGE,"E2025"),sQuery(id+"F0.wireOp",EDGE,"E2026"),sQuery(id+"F0.wireOp",EDGE,"E2027"),sQuery(id+"F0.wireOp",EDGE,"E2028"),sQuery(id+"F0.wireOp",EDGE,"E2029"),sQuery(id+"F0.wireOp",EDGE,"E2030"),sQuery(id+"F0.wireOp",EDGE,"E2031"),sQuery(id+"F0.wireOp",EDGE,"E2032"),sQuery(id+"F0.wireOp",EDGE,"E2033"),sQuery(id+"F0.wireOp",EDGE,"E2034"),sQuery(id+"F0.wireOp",EDGE,"E2035"),sQuery(id+"F0.wireOp",EDGE,"E2036"),sQuery(id+"F0.wireOp",EDGE,"E2037"),sQuery(id+"F0.wireOp",EDGE,"E2038"),sQuery(id+"F0.wireOp",EDGE,"E2039"),sQuery(id+"F0.wireOp",EDGE,"E2040"),sQuery(id+"F0.wireOp",EDGE,"E2041"),sQuery(id+"F0.wireOp",EDGE,"E2042"),sQuery(id+"F0.wireOp",EDGE,"E2043"),sQuery(id+"F0.wireOp",EDGE,"E2044"),sQuery(id+"F0.wireOp",EDGE,"E2045"),sQuery(id+"F0.wireOp",EDGE,"E2046"),sQuery(id+"F0.wireOp",EDGE,"E2047"),sQuery(id+"F0.wireOp",EDGE,"E2048"),sQuery(id+"F0.wireOp",EDGE,"E2049"),sQuery(id+"F0.wireOp",EDGE,"E2050"),sQuery(id+"F0.wireOp",EDGE,"E2051"),sQuery(id+"F0.wireOp",EDGE,"E2052"),sQuery(id+"F0.wireOp",EDGE,"E2053"),sQuery(id+"F0.wireOp",EDGE,"E2054"),sQuery(id+"F0.wireOp",EDGE,"E2055"),sQuery(id+"F0.wireOp",EDGE,"E2056"),sQuery(id+"F0.wireOp",EDGE,"E2057"),sQuery(id+"F0.wireOp",EDGE,"E2058"),sQuery(id+"F0.wireOp",EDGE,"E2059"),sQuery(id+"F0.wireOp",EDGE,"E2060"),sQuery(id+"F0.wireOp",EDGE,"E2061"),sQuery(id+"F0.wireOp",EDGE,"E2062"),sQuery(id+"F0.wireOp",EDGE,"E2063"),sQuery(id+"F0.wireOp",EDGE,"E2064"),sQuery(id+"F0.wireOp",EDGE,"E2065"),sQuery(id+"F0.wireOp",EDGE,"E2066"),sQuery(id+"F0.wireOp",EDGE,"E2067"),sQuery(id+"F0.wireOp",EDGE,"E2068"),sQuery(id+"F0.wireOp",EDGE,"E2069"),sQuery(id+"F0.wireOp",EDGE,"E2070"),sQuery(id+"F0.wireOp",EDGE,"E2071"),sQuery(id+"F0.wireOp",EDGE,"E2072"),sQuery(id+"F0.wireOp",EDGE,"E2073"),sQuery(id+"F0.wireOp",EDGE,"E2074"),sQuery(id+"F0.wireOp",EDGE,"E2075"),sQuery(id+"F0.wireOp",EDGE,"E2076"),sQuery(id+"F0.wireOp",EDGE,"E2077"),sQuery(id+"F0.wireOp",EDGE,"E2078"),sQuery(id+"F0.wireOp",EDGE,"E2079"),sQuery(id+"F0.wireOp",EDGE,"E2080"),sQuery(id+"F0.wireOp",EDGE,"E2081"),sQuery(id+"F0.wireOp",EDGE,"E2082"),sQuery(id+"F0.wireOp",EDGE,"E2083"),sQuery(id+"F0.wireOp",EDGE,"E2084"),sQuery(id+"F0.wireOp",EDGE,"E2085"),sQuery(id+"F0.wireOp",EDGE,"E2086"),sQuery(id+"F0.wireOp",EDGE,"E2087"),sQuery(id+"F0.wireOp",EDGE,"E2088"),sQuery(id+"F0.wireOp",EDGE,"E2089"),sQuery(id+"F0.wireOp",EDGE,"E2090"),sQuery(id+"F0.wireOp",EDGE,"E2091"),sQuery(id+"F0.wireOp",EDGE,"E2092"),sQuery(id+"F0.wireOp",EDGE,"E2093"),sQuery(id+"F0.wireOp",EDGE,"E2094"),sQuery(id+"F0.wireOp",EDGE,"E2095"),sQuery(id+"F0.wireOp",EDGE,"E2096"),sQuery(id+"F0.wireOp",EDGE,"E2097"),sQuery(id+"F0.wireOp",EDGE,"E2098"),sQuery(id+"F0.wireOp",EDGE,"E2099"),sQuery(id+"F0.wireOp",EDGE,"E2100"),sQuery(id+"F0.wireOp",EDGE,"E2101"),sQuery(id+"F0.wireOp",EDGE,"E2102"),sQuery(id+"F0.wireOp",EDGE,"E2103"),sQuery(id+"F0.wireOp",EDGE,"E2104"),sQuery(id+"F0.wireOp",EDGE,"E2105"),sQuery(id+"F0.wireOp",EDGE,"E2106"),sQuery(id+"F0.wireOp",EDGE,"E2107"),sQuery(id+"F0.wireOp",EDGE,"E2108"),sQuery(id+"F0.wireOp",EDGE,"E2109"),sQuery(id+"F0.wireOp",EDGE,"E2110"),sQuery(id+"F0.wireOp",EDGE,"E2111"),sQuery(id+"F0.wireOp",EDGE,"E2112"),sQuery(id+"F0.wireOp",EDGE,"E2113"),sQuery(id+"F0.wireOp",EDGE,"E2114"),sQuery(id+"F0.wireOp",EDGE,"E2115"),sQuery(id+"F0.wireOp",EDGE,"E2116"),sQuery(id+"F0.wireOp",EDGE,"E2117"),sQuery(id+"F0.wireOp",EDGE,"E2118"),sQuery(id+"F0.wireOp",EDGE,"E2119"),sQuery(id+"F0.wireOp",EDGE,"E2120"),sQuery(id+"F0.wireOp",EDGE,"E2121"),sQuery(id+"F0.wireOp",EDGE,"E2122"),sQuery(id+"F0.wireOp",EDGE,"E2123"),sQuery(id+"F0.wireOp",EDGE,"E2124"),sQuery(id+"F0.wireOp",EDGE,"E2125"),sQuery(id+"F0.wireOp",EDGE,"E2126"),sQuery(id+"F0.wireOp",EDGE,"E2127"),sQuery(id+"F0.wireOp",EDGE,"E2128"),sQuery(id+"F0.wireOp",EDGE,"E2129"),sQuery(id+"F0.wireOp",EDGE,"E2130"),sQuery(id+"F0.wireOp",EDGE,"E2131"),sQuery(id+"F0.wireOp",EDGE,"E2132"),sQuery(id+"F0.wireOp",EDGE,"E2133"),sQuery(id+"F0.wireOp",EDGE,"E2134"),sQuery(id+"F0.wireOp",EDGE,"E2135"),sQuery(id+"F0.wireOp",EDGE,"E2136"),sQuery(id+"F0.wireOp",EDGE,"E2137"),sQuery(id+"F0.wireOp",EDGE,"E2138"),sQuery(id+"F0.wireOp",EDGE,"E2139"),sQuery(id+"F0.wireOp",EDGE,"E2140"),sQuery(id+"F0.wireOp",EDGE,"E2141"),sQuery(id+"F0.wireOp",EDGE,"E2142"),sQuery(id+"F0.wireOp",EDGE,"E2143"),sQuery(id+"F0.wireOp",EDGE,"E2144"),sQuery(id+"F0.wireOp",EDGE,"E2145"),sQuery(id+"F0.wireOp",EDGE,"E2146"),sQuery(id+"F0.wireOp",EDGE,"E2147"),sQuery(id+"F0.wireOp",EDGE,"E2148"),sQuery(id+"F0.wireOp",EDGE,"E2149"),sQuery(id+"F0.wireOp",EDGE,"E2150"),sQuery(id+"F0.wireOp",EDGE,"E2151"),sQuery(id+"F0.wireOp",EDGE,"E2152"),sQuery(id+"F0.wireOp",EDGE,"E2153"),sQuery(id+"F0.wireOp",EDGE,"E2154"),sQuery(id+"F0.wireOp",EDGE,"E2155"),sQuery(id+"F0.wireOp",EDGE,"E2156"),sQuery(id+"F0.wireOp",EDGE,"E2157"),sQuery(id+"F0.wireOp",EDGE,"E2158"),sQuery(id+"F0.wireOp",EDGE,"E2159"),sQuery(id+"F0.wireOp",EDGE,"E2160"),sQuery(id+"F0.wireOp",EDGE,"E2161"),sQuery(id+"F0.wireOp",EDGE,"E2162"),sQuery(id+"F0.wireOp",EDGE,"E2163"),sQuery(id+"F0.wireOp",EDGE,"E2164"),sQuery(id+"F0.wireOp",EDGE,"E2165"),sQuery(id+"F0.wireOp",EDGE,"E2166"),sQuery(id+"F0.wireOp",EDGE,"E2167"),sQuery(id+"F0.wireOp",EDGE,"E2168"),sQuery(id+"F0.wireOp",EDGE,"E2169"),sQuery(id+"F0.wireOp",EDGE,"E2170"),sQuery(id+"F0.wireOp",EDGE,"E2171"),sQuery(id+"F0.wireOp",EDGE,"E2172"),sQuery(id+"F0.wireOp",EDGE,"E2173"),sQuery(id+"F0.wireOp",EDGE,"E2174"),sQuery(id+"F0.wireOp",EDGE,"E2175"),sQuery(id+"F0.wireOp",EDGE,"E2176"),sQuery(id+"F0.wireOp",EDGE,"E2177"),sQuery(id+"F0.wireOp",EDGE,"E2178"),sQuery(id+"F0.wireOp",EDGE,"E2179"),sQuery(id+"F0.wireOp",EDGE,"E2180"),sQuery(id+"F0.wireOp",EDGE,"E2181"),sQuery(id+"F0.wireOp",EDGE,"E2182"),sQuery(id+"F0.wireOp",EDGE,"E2183"),sQuery(id+"F0.wireOp",EDGE,"E2184"),sQuery(id+"F0.wireOp",EDGE,"E2185"),sQuery(id+"F0.wireOp",EDGE,"E2186"),sQuery(id+"F0.wireOp",EDGE,"E2187"),sQuery(id+"F0.wireOp",EDGE,"E2188"),sQuery(id+"F0.wireOp",EDGE,"E2189"),sQuery(id+"F0.wireOp",EDGE,"E2190"),sQuery(id+"F0.wireOp",EDGE,"E2191"),sQuery(id+"F0.wireOp",EDGE,"E2192"),sQuery(id+"F0.wireOp",EDGE,"E2193"),sQuery(id+"F0.wireOp",EDGE,"E2194"),sQuery(id+"F0.wireOp",EDGE,"E2195"),sQuery(id+"F0.wireOp",EDGE,"E2196"),sQuery(id+"F0.wireOp",EDGE,"E2197"),sQuery(id+"F0.wireOp",EDGE,"E2198"),sQuery(id+"F0.wireOp",EDGE,"E2199"),sQuery(id+"F0.wireOp",EDGE,"E2200"),sQuery(id+"F0.wireOp",EDGE,"E2201"),sQuery(id+"F0.wireOp",EDGE,"E2202"),sQuery(id+"F0.wireOp",EDGE,"E2203"),sQuery(id+"F0.wireOp",EDGE,"E2204"),sQuery(id+"F0.wireOp",EDGE,"E2205"),sQuery(id+"F0.wireOp",EDGE,"E2206"),sQuery(id+"F0.wireOp",EDGE,"E2207"),sQuery(id+"F0.wireOp",EDGE,"E2208"),sQuery(id+"F0.wireOp",EDGE,"E2209"),sQuery(id+"F0.wireOp",EDGE,"E2210"),sQuery(id+"F0.wireOp",EDGE,"E2211"),sQuery(id+"F0.wireOp",EDGE,"E2212"),sQuery(id+"F0.wireOp",EDGE,"E2213"),sQuery(id+"F0.wireOp",EDGE,"E2214"),sQuery(id+"F0.wireOp",EDGE,"E2215"),sQuery(id+"F0.wireOp",EDGE,"E2216"),sQuery(id+"F0.wireOp",EDGE,"E2217"),sQuery(id+"F0.wireOp",EDGE,"E2218"),sQuery(id+"F0.wireOp",EDGE,"E2219"),sQuery(id+"F0.wireOp",EDGE,"E2220"),sQuery(id+"F0.wireOp",EDGE,"E2221"),sQuery(id+"F0.wireOp",EDGE,"E2222"),sQuery(id+"F0.wireOp",EDGE,"E2223"),sQuery(id+"F0.wireOp",EDGE,"E2224"),sQuery(id+"F0.wireOp",EDGE,"E2225"),sQuery(id+"F0.wireOp",EDGE,"E2226"),sQuery(id+"F0.wireOp",EDGE,"E2227"),sQuery(id+"F0.wireOp",EDGE,"E2228"),sQuery(id+"F0.wireOp",EDGE,"E2229"),sQuery(id+"F0.wireOp",EDGE,"E2230"),sQuery(id+"F0.wireOp",EDGE,"E2231"),sQuery(id+"F0.wireOp",EDGE,"E2232"),sQuery(id+"F0.wireOp",EDGE,"E2233"),sQuery(id+"F0.wireOp",EDGE,"E2234"),sQuery(id+"F0.wireOp",EDGE,"E2235"),sQuery(id+"F0.wireOp",EDGE,"E2236"),sQuery(id+"F0.wireOp",EDGE,"E2237"),sQuery(id+"F0.wireOp",EDGE,"E2238"),sQuery(id+"F0.wireOp",EDGE,"E2239"),sQuery(id+"F0.wireOp",EDGE,"E2240"),sQuery(id+"F0.wireOp",EDGE,"E2241"),sQuery(id+"F0.wireOp",EDGE,"E2242"),sQuery(id+"F0.wireOp",EDGE,"E2243"),sQuery(id+"F0.wireOp",EDGE,"E2244"),sQuery(id+"F0.wireOp",EDGE,"E2245"),sQuery(id+"F0.wireOp",EDGE,"E2246"),sQuery(id+"F0.wireOp",EDGE,"E2247"),sQuery(id+"F0.wireOp",EDGE,"E2248"),sQuery(id+"F0.wireOp",EDGE,"E2249"),sQuery(id+"F0.wireOp",EDGE,"E2250"),sQuery(id+"F0.wireOp",EDGE,"E2251"),sQuery(id+"F0.wireOp",EDGE,"E2252"),sQuery(id+"F0.wireOp",EDGE,"E2253"),sQuery(id+"F0.wireOp",EDGE,"E2254"),sQuery(id+"F0.wireOp",EDGE,"E2255"),sQuery(id+"F0.wireOp",EDGE,"E2256"),sQuery(id+"F0.wireOp",EDGE,"E2257"),sQuery(id+"F0.wireOp",EDGE,"E2258"),sQuery(id+"F0.wireOp",EDGE,"E2259"),sQuery(id+"F0.wireOp",EDGE,"E2260"),sQuery(id+"F0.wireOp",EDGE,"E2261"),sQuery(id+"F0.wireOp",EDGE,"E2262"),sQuery(id+"F0.wireOp",EDGE,"E2263"),sQuery(id+"F0.wireOp",EDGE,"E2264"),sQuery(id+"F0.wireOp",EDGE,"E2265"),sQuery(id+"F0.wireOp",EDGE,"E2266"),sQuery(id+"F0.wireOp",EDGE,"E2267"),sQuery(id+"F0.wireOp",EDGE,"E2268"),sQuery(id+"F0.wireOp",EDGE,"E2269"),sQuery(id+"F0.wireOp",EDGE,"E2270"),sQuery(id+"F0.wireOp",EDGE,"E2271"),sQuery(id+"F0.wireOp",EDGE,"E2272"),sQuery(id+"F0.wireOp",EDGE,"E2273"),sQuery(id+"F0.wireOp",EDGE,"E2274"),sQuery(id+"F0.wireOp",EDGE,"E2275"),sQuery(id+"F0.wireOp",EDGE,"E2276"),sQuery(id+"F0.wireOp",EDGE,"E2277"),sQuery(id+"F0.wireOp",EDGE,"E2278"),sQuery(id+"F0.wireOp",EDGE,"E2279"),sQuery(id+"F0.wireOp",EDGE,"E2280"),sQuery(id+"F0.wireOp",EDGE,"E2281"),sQuery(id+"F0.wireOp",EDGE,"E2282"),sQuery(id+"F0.wireOp",EDGE,"E2283"),sQuery(id+"F0.wireOp",EDGE,"E2284"),sQuery(id+"F0.wireOp",EDGE,"E2285"),sQuery(id+"F0.wireOp",EDGE,"E2286"),sQuery(id+"F0.wireOp",EDGE,"E2287"),sQuery(id+"F0.wireOp",EDGE,"E2288"),sQuery(id+"F0.wireOp",EDGE,"E2289"),sQuery(id+"F0.wireOp",EDGE,"E2290"),sQuery(id+"F0.wireOp",EDGE,"E2291"),sQuery(id+"F0.wireOp",EDGE,"E2292"),sQuery(id+"F0.wireOp",EDGE,"E2293"),sQuery(id+"F0.wireOp",EDGE,"E2294"),sQuery(id+"F0.wireOp",EDGE,"E2295"),sQuery(id+"F0.wireOp",EDGE,"E2296"),sQuery(id+"F0.wireOp",EDGE,"E2297"),sQuery(id+"F0.wireOp",EDGE,"E2298"),sQuery(id+"F0.wireOp",EDGE,"E2299"),sQuery(id+"F0.wireOp",EDGE,"E2300"),sQuery(id+"F0.wireOp",EDGE,"E2301"),sQuery(id+"F0.wireOp",EDGE,"E2302"),sQuery(id+"F0.wireOp",EDGE,"E2303"),sQuery(id+"F0.wireOp",EDGE,"E2304"),sQuery(id+"F0.wireOp",EDGE,"E2305"),sQuery(id+"F0.wireOp",EDGE,"E2306"),sQuery(id+"F0.wireOp",EDGE,"E2307"),sQuery(id+"F0.wireOp",EDGE,"E2308"),sQuery(id+"F0.wireOp",EDGE,"E2309"),sQuery(id+"F0.wireOp",EDGE,"E2310"),sQuery(id+"F0.wireOp",EDGE,"E2311"),sQuery(id+"F0.wireOp",EDGE,"E2312"),sQuery(id+"F0.wireOp",EDGE,"E2313"),sQuery(id+"F0.wireOp",EDGE,"E2314"),sQuery(id+"F0.wireOp",EDGE,"E2315"),sQuery(id+"F0.wireOp",EDGE,"E2316"),sQuery(id+"F0.wireOp",EDGE,"E2317"),sQuery(id+"F0.wireOp",EDGE,"E2318"),sQuery(id+"F0.wireOp",EDGE,"E2319"),sQuery(id+"F0.wireOp",EDGE,"E2320"),sQuery(id+"F0.wireOp",EDGE,"E2321"),sQuery(id+"F0.wireOp",EDGE,"E2322"),sQuery(id+"F0.wireOp",EDGE,"E2323"),sQuery(id+"F0.wireOp",EDGE,"E2324"),sQuery(id+"F0.wireOp",EDGE,"E2325"),sQuery(id+"F0.wireOp",EDGE,"E2326"),sQuery(id+"F0.wireOp",EDGE,"E2327"),sQuery(id+"F0.wireOp",EDGE,"E2328"),sQuery(id+"F0.wireOp",EDGE,"E2329"),sQuery(id+"F0.wireOp",EDGE,"E2330"),sQuery(id+"F0.wireOp",EDGE,"E2331"),sQuery(id+"F0.wireOp",EDGE,"E2332"),sQuery(id+"F0.wireOp",EDGE,"E2333"),sQuery(id+"F0.wireOp",EDGE,"E2334"),sQuery(id+"F0.wireOp",EDGE,"E2335"),sQuery(id+"F0.wireOp",EDGE,"E2336"),sQuery(id+"F0.wireOp",EDGE,"E2337"),sQuery(id+"F0.wireOp",EDGE,"E2338"),sQuery(id+"F0.wireOp",EDGE,"E2339"),sQuery(id+"F0.wireOp",EDGE,"E2340"),sQuery(id+"F0.wireOp",EDGE,"E2341"),sQuery(id+"F0.wireOp",EDGE,"E2342"),sQuery(id+"F0.wireOp",EDGE,"E2343"),sQuery(id+"F0.wireOp",EDGE,"E2344"),sQuery(id+"F0.wireOp",EDGE,"E2345"),sQuery(id+"F0.wireOp",EDGE,"E2346"),sQuery(id+"F0.wireOp",EDGE,"E2347"),sQuery(id+"F0.wireOp",EDGE,"E2348"),sQuery(id+"F0.wireOp",EDGE,"E2349"),sQuery(id+"F0.wireOp",EDGE,"E2350"),sQuery(id+"F0.wireOp",EDGE,"E2351"),sQuery(id+"F0.wireOp",EDGE,"E2352"),sQuery(id+"F0.wireOp",EDGE,"E2353"),sQuery(id+"F0.wireOp",EDGE,"E2354"),sQuery(id+"F0.wireOp",EDGE,"E2355"),sQuery(id+"F0.wireOp",EDGE,"E2356"),sQuery(id+"F0.wireOp",EDGE,"E2357"),sQuery(id+"F0.wireOp",EDGE,"E2358"),sQuery(id+"F0.wireOp",EDGE,"E2359"),sQuery(id+"F0.wireOp",EDGE,"E2360"),sQuery(id+"F0.wireOp",EDGE,"E2361"),sQuery(id+"F0.wireOp",EDGE,"E2362"),sQuery(id+"F0.wireOp",EDGE,"E2363"),sQuery(id+"F0.wireOp",EDGE,"E2364"),sQuery(id+"F0.wireOp",EDGE,"E2365"),sQuery(id+"F0.wireOp",EDGE,"E2366"),sQuery(id+"F0.wireOp",EDGE,"E2367"),sQuery(id+"F0.wireOp",EDGE,"E2368"),sQuery(id+"F0.wireOp",EDGE,"E2369"),sQuery(id+"F0.wireOp",EDGE,"E2370"),sQuery(id+"F0.wireOp",EDGE,"E2371"),sQuery(id+"F0.wireOp",EDGE,"E2372"),sQuery(id+"F0.wireOp",EDGE,"E2373"),sQuery(id+"F0.wireOp",EDGE,"E2374"),sQuery(id+"F0.wireOp",EDGE,"E2375"),sQuery(id+"F0.wireOp",EDGE,"E2376"),sQuery(id+"F0.wireOp",EDGE,"E2377"),sQuery(id+"F0.wireOp",EDGE,"E2378"),sQuery(id+"F0.wireOp",EDGE,"E2379"),sQuery(id+"F0.wireOp",EDGE,"E2380"),sQuery(id+"F0.wireOp",EDGE,"E2381"),sQuery(id+"F0.wireOp",EDGE,"E2382"),sQuery(id+"F0.wireOp",EDGE,"E2383"),sQuery(id+"F0.wireOp",EDGE,"E2384"),sQuery(id+"F0.wireOp",EDGE,"E2385"),sQuery(id+"F0.wireOp",EDGE,"E2386"),sQuery(id+"F0.wireOp",EDGE,"E2387"),sQuery(id+"F0.wireOp",EDGE,"E2388"),sQuery(id+"F0.wireOp",EDGE,"E2389"),sQuery(id+"F0.wireOp",EDGE,"E2390"),sQuery(id+"F0.wireOp",EDGE,"E2391"),sQuery(id+"F0.wireOp",EDGE,"E2392"),sQuery(id+"F0.wireOp",EDGE,"E2393"),sQuery(id+"F0.wireOp",EDGE,"E2394"),sQuery(id+"F0.wireOp",EDGE,"E2395"),sQuery(id+"F0.wireOp",EDGE,"E2396"),sQuery(id+"F0.wireOp",EDGE,"E2397"),sQuery(id+"F0.wireOp",EDGE,"E2398"),sQuery(id+"F0.wireOp",EDGE,"E2399"),sQuery(id+"F0.wireOp",EDGE,"E2400"),sQuery(id+"F0.wireOp",EDGE,"E2401"),sQuery(id+"F0.wireOp",EDGE,"E2402"),sQuery(id+"F0.wireOp",EDGE,"E2403"),sQuery(id+"F0.wireOp",EDGE,"E2404"),sQuery(id+"F0.wireOp",EDGE,"E2405"),sQuery(id+"F0.wireOp",EDGE,"E2406"),sQuery(id+"F0.wireOp",EDGE,"E2407"),sQuery(id+"F0.wireOp",EDGE,"E2408"),sQuery(id+"F0.wireOp",EDGE,"E2409"),sQuery(id+"F0.wireOp",EDGE,"E2410"),sQuery(id+"F0.wireOp",EDGE,"E2411"),sQuery(id+"F0.wireOp",EDGE,"E2412"),sQuery(id+"F0.wireOp",EDGE,"E2413"),sQuery(id+"F0.wireOp",EDGE,"E2414"),sQuery(id+"F0.wireOp",EDGE,"E2415"),sQuery(id+"F0.wireOp",EDGE,"E2416"),sQuery(id+"F0.wireOp",EDGE,"E2417"),sQuery(id+"F0.wireOp",EDGE,"E2418"),sQuery(id+"F0.wireOp",EDGE,"E2419"),sQuery(id+"F0.wireOp",EDGE,"E2420"),sQuery(id+"F0.wireOp",EDGE,"E2421"),sQuery(id+"F0.wireOp",EDGE,"E2422"),sQuery(id+"F0.wireOp",EDGE,"E2423"),sQuery(id+"F0.wireOp",EDGE,"E2424"),sQuery(id+"F0.wireOp",EDGE,"E2425"),sQuery(id+"F0.wireOp",EDGE,"E2426"),sQuery(id+"F0.wireOp",EDGE,"E2427"),sQuery(id+"F0.wireOp",EDGE,"E2428"),sQuery(id+"F0.wireOp",EDGE,"E2429"),sQuery(id+"F0.wireOp",EDGE,"E2430"),sQuery(id+"F0.wireOp",EDGE,"E2431"),sQuery(id+"F0.wireOp",EDGE,"E2432"),sQuery(id+"F0.wireOp",EDGE,"E2433"),sQuery(id+"F0.wireOp",EDGE,"E2434"),sQuery(id+"F0.wireOp",EDGE,"E2435"),sQuery(id+"F0.wireOp",EDGE,"E2436"),sQuery(id+"F0.wireOp",EDGE,"E2437"),sQuery(id+"F0.wireOp",EDGE,"E2438"),sQuery(id+"F0.wireOp",EDGE,"E2439"),sQuery(id+"F0.wireOp",EDGE,"E2440"),sQuery(id+"F0.wireOp",EDGE,"E2441"),sQuery(id+"F0.wireOp",EDGE,"E2442"),sQuery(id+"F0.wireOp",EDGE,"E2443"),sQuery(id+"F0.wireOp",EDGE,"E2444"),sQuery(id+"F0.wireOp",EDGE,"E2445"),sQuery(id+"F0.wireOp",EDGE,"E2446"),sQuery(id+"F0.wireOp",EDGE,"E2447"),sQuery(id+"F0.wireOp",EDGE,"E2448"),sQuery(id+"F0.wireOp",EDGE,"E2449"),sQuery(id+"F0.wireOp",EDGE,"E2450"),sQuery(id+"F0.wireOp",EDGE,"E2451"),sQuery(id+"F0.wireOp",EDGE,"E2452"),sQuery(id+"F0.wireOp",EDGE,"E2453"),sQuery(id+"F0.wireOp",EDGE,"E2454"),sQuery(id+"F0.wireOp",EDGE,"E2455"),sQuery(id+"F0.wireOp",EDGE,"E2456"),sQuery(id+"F0.wireOp",EDGE,"E2457"),sQuery(id+"F0.wireOp",EDGE,"E2458"),sQuery(id+"F0.wireOp",EDGE,"E2459"),sQuery(id+"F0.wireOp",EDGE,"E2460"),sQuery(id+"F0.wireOp",EDGE,"E2461"),sQuery(id+"F0.wireOp",EDGE,"E2462"),sQuery(id+"F0.wireOp",EDGE,"E2463"),sQuery(id+"F0.wireOp",EDGE,"E2464"),sQuery(id+"F0.wireOp",EDGE,"E2465"),sQuery(id+"F0.wireOp",EDGE,"E2466"),sQuery(id+"F0.wireOp",EDGE,"E2467"),sQuery(id+"F0.wireOp",EDGE,"E2468"),sQuery(id+"F0.wireOp",EDGE,"E2469"),sQuery(id+"F0.wireOp",EDGE,"E2470"),sQuery(id+"F0.wireOp",EDGE,"E2471"),sQuery(id+"F0.wireOp",EDGE,"E2472"),sQuery(id+"F0.wireOp",EDGE,"E2473"),sQuery(id+"F0.wireOp",EDGE,"E2474"),sQuery(id+"F0.wireOp",EDGE,"E2475"),sQuery(id+"F0.wireOp",EDGE,"E2476"),sQuery(id+"F0.wireOp",EDGE,"E2477"),sQuery(id+"F0.wireOp",EDGE,"E2478"),sQuery(id+"F0.wireOp",EDGE,"E2479"),sQuery(id+"F0.wireOp",EDGE,"E2480"),sQuery(id+"F0.wireOp",EDGE,"E2481"),sQuery(id+"F0.wireOp",EDGE,"E2482"),sQuery(id+"F0.wireOp",EDGE,"E2483"),sQuery(id+"F0.wireOp",EDGE,"E2484"),sQuery(id+"F0.wireOp",EDGE,"E2485"),sQuery(id+"F0.wireOp",EDGE,"E2486"),sQuery(id+"F0.wireOp",EDGE,"E2487"),sQuery(id+"F0.wireOp",EDGE,"E2488"),sQuery(id+"F0.wireOp",EDGE,"E2489"),sQuery(id+"F0.wireOp",EDGE,"E2490"),sQuery(id+"F0.wireOp",EDGE,"E2491"),sQuery(id+"F0.wireOp",EDGE,"E2492"),sQuery(id+"F0.wireOp",EDGE,"E2493"),sQuery(id+"F0.wireOp",EDGE,"E2494"),sQuery(id+"F0.wireOp",EDGE,"E2495"),sQuery(id+"F0.wireOp",EDGE,"E2496"),sQuery(id+"F0.wireOp",EDGE,"E2497"),sQuery(id+"F0.wireOp",EDGE,"E2498"),sQuery(id+"F0.wireOp",EDGE,"E2499"),sQuery(id+"F0.wireOp",EDGE,"E2500"),sQuery(id+"F0.wireOp",EDGE,"E2501"),sQuery(id+"F0.wireOp",EDGE,"E2502"),sQuery(id+"F0.wireOp",EDGE,"E2503"),sQuery(id+"F0.wireOp",EDGE,"E2504"),sQuery(id+"F0.wireOp",EDGE,"E2505"),sQuery(id+"F0.wireOp",EDGE,"E2506"),sQuery(id+"F0.wireOp",EDGE,"E2507"),sQuery(id+"F0.wireOp",EDGE,"E2508"),sQuery(id+"F0.wireOp",EDGE,"E2509"),sQuery(id+"F0.wireOp",EDGE,"E2510"),sQuery(id+"F0.wireOp",EDGE,"E2511"),sQuery(id+"F0.wireOp",EDGE,"E2512"),sQuery(id+"F0.wireOp",EDGE,"E2513"),sQuery(id+"F0.wireOp",EDGE,"E2514"),sQuery(id+"F0.wireOp",EDGE,"E2515"),sQuery(id+"F0.wireOp",EDGE,"E2516"),sQuery(id+"F0.wireOp",EDGE,"E2517"),sQuery(id+"F0.wireOp",EDGE,"E2518"),sQuery(id+"F0.wireOp",EDGE,"E2519"),sQuery(id+"F0.wireOp",EDGE,"E2520"),sQuery(id+"F0.wireOp",EDGE,"E2521"),sQuery(id+"F0.wireOp",EDGE,"E2522"),sQuery(id+"F0.wireOp",EDGE,"E2523"),sQuery(id+"F0.wireOp",EDGE,"E2524"),sQuery(id+"F0.wireOp",EDGE,"E2525"),sQuery(id+"F0.wireOp",EDGE,"E2526"),sQuery(id+"F0.wireOp",EDGE,"E2527"),sQuery(id+"F0.wireOp",EDGE,"E2528"),sQuery(id+"F0.wireOp",EDGE,"E2529"),sQuery(id+"F0.wireOp",EDGE,"E2530"),sQuery(id+"F0.wireOp",EDGE,"E2531"),sQuery(id+"F0.wireOp",EDGE,"E2532"),sQuery(id+"F0.wireOp",EDGE,"E2533"),sQuery(id+"F0.wireOp",EDGE,"E2534"),sQuery(id+"F0.wireOp",EDGE,"E2535"),sQuery(id+"F0.wireOp",EDGE,"E2536"),sQuery(id+"F0.wireOp",EDGE,"E2537"),sQuery(id+"F0.wireOp",EDGE,"E2538"),sQuery(id+"F0.wireOp",EDGE,"E2539"),sQuery(id+"F0.wireOp",EDGE,"E2540"),sQuery(id+"F0.wireOp",EDGE,"E2541"),sQuery(id+"F0.wireOp",EDGE,"E2542"),sQuery(id+"F0.wireOp",EDGE,"E2543"),sQuery(id+"F0.wireOp",EDGE,"E2544"),sQuery(id+"F0.wireOp",EDGE,"E2545"),sQuery(id+"F0.wireOp",EDGE,"E2546"),sQuery(id+"F0.wireOp",EDGE,"E2547"),sQuery(id+"F0.wireOp",EDGE,"E2548"),sQuery(id+"F0.wireOp",EDGE,"E2549"),sQuery(id+"F0.wireOp",EDGE,"E2550"),sQuery(id+"F0.wireOp",EDGE,"E2551"),sQuery(id+"F0.wireOp",EDGE,"E2552"),sQuery(id+"F0.wireOp",EDGE,"E2553"),sQuery(id+"F0.wireOp",EDGE,"E2554"),sQuery(id+"F0.wireOp",EDGE,"E2555"),sQuery(id+"F0.wireOp",EDGE,"E2556"),sQuery(id+"F0.wireOp",EDGE,"E2557"),sQuery(id+"F0.wireOp",EDGE,"E2558"),sQuery(id+"F0.wireOp",EDGE,"E2559"),sQuery(id+"F0.wireOp",EDGE,"E2560"),sQuery(id+"F0.wireOp",EDGE,"E2561"),sQuery(id+"F0.wireOp",EDGE,"E2562"),sQuery(id+"F0.wireOp",EDGE,"E2563"),sQuery(id+"F0.wireOp",EDGE,"E2564"),sQuery(id+"F0.wireOp",EDGE,"E2565"),sQuery(id+"F0.wireOp",EDGE,"E2566"),sQuery(id+"F0.wireOp",EDGE,"E2567"),sQuery(id+"F0.wireOp",EDGE,"E2568"),sQuery(id+"F0.wireOp",EDGE,"E2569"),sQuery(id+"F0.wireOp",EDGE,"E2570"),sQuery(id+"F0.wireOp",EDGE,"E2571"),sQuery(id+"F0.wireOp",EDGE,"E2572"),sQuery(id+"F0.wireOp",EDGE,"E2573"),sQuery(id+"F0.wireOp",EDGE,"E2574"),sQuery(id+"F0.wireOp",EDGE,"E2575"),sQuery(id+"F0.wireOp",EDGE,"E2576"),sQuery(id+"F0.wireOp",EDGE,"E2577"),sQuery(id+"F0.wireOp",EDGE,"E2578"),sQuery(id+"F0.wireOp",EDGE,"E2579"),sQuery(id+"F0.wireOp",EDGE,"E2580"),sQuery(id+"F0.wireOp",EDGE,"E2581"),sQuery(id+"F0.wireOp",EDGE,"E2582"),sQuery(id+"F0.wireOp",EDGE,"E2583"),sQuery(id+"F0.wireOp",EDGE,"E2584"),sQuery(id+"F0.wireOp",EDGE,"E2585"),sQuery(id+"F0.wireOp",EDGE,"E2586"),sQuery(id+"F0.wireOp",EDGE,"E2587"),sQuery(id+"F0.wireOp",EDGE,"E2588"),sQuery(id+"F0.wireOp",EDGE,"E2589"),sQuery(id+"F0.wireOp",EDGE,"E2590"),sQuery(id+"F0.wireOp",EDGE,"E2591"),sQuery(id+"F0.wireOp",EDGE,"E2592"),sQuery(id+"F0.wireOp",EDGE,"E2593"),sQuery(id+"F0.wireOp",EDGE,"E2594"),sQuery(id+"F0.wireOp",EDGE,"E2595"),sQuery(id+"F0.wireOp",EDGE,"E2596"),sQuery(id+"F0.wireOp",EDGE,"E2597"),sQuery(id+"F0.wireOp",EDGE,"E2598"),sQuery(id+"F0.wireOp",EDGE,"E2599"),sQuery(id+"F0.wireOp",EDGE,"E2600"),sQuery(id+"F0.wireOp",EDGE,"E2601"),sQuery(id+"F0.wireOp",EDGE,"E2602"),sQuery(id+"F0.wireOp",EDGE,"E2603"),sQuery(id+"F0.wireOp",EDGE,"E2604"),sQuery(id+"F0.wireOp",EDGE,"E2605"),sQuery(id+"F0.wireOp",EDGE,"E2606"),sQuery(id+"F0.wireOp",EDGE,"E2607"),sQuery(id+"F0.wireOp",EDGE,"E2608"),sQuery(id+"F0.wireOp",EDGE,"E2609"),sQuery(id+"F0.wireOp",EDGE,"E2610"),sQuery(id+"F0.wireOp",EDGE,"E2611"),sQuery(id+"F0.wireOp",EDGE,"E2612"),sQuery(id+"F0.wireOp",EDGE,"E2613"),sQuery(id+"F0.wireOp",EDGE,"E2614"),sQuery(id+"F0.wireOp",EDGE,"E2615"),sQuery(id+"F0.wireOp",EDGE,"E2616"),sQuery(id+"F0.wireOp",EDGE,"E2617"),sQuery(id+"F0.wireOp",EDGE,"E2618"),sQuery(id+"F0.wireOp",EDGE,"E2619"),sQuery(id+"F0.wireOp",EDGE,"E2620"),sQuery(id+"F0.wireOp",EDGE,"E2621"),sQuery(id+"F0.wireOp",EDGE,"E2622"),sQuery(id+"F0.wireOp",EDGE,"E2623"),sQuery(id+"F0.wireOp",EDGE,"E2624"),sQuery(id+"F0.wireOp",EDGE,"E2625"),sQuery(id+"F0.wireOp",EDGE,"E2626"),sQuery(id+"F0.wireOp",EDGE,"E2627"),sQuery(id+"F0.wireOp",EDGE,"E2628"),sQuery(id+"F0.wireOp",EDGE,"E2629"),sQuery(id+"F0.wireOp",EDGE,"E2630"),sQuery(id+"F0.wireOp",EDGE,"E2631"),sQuery(id+"F0.wireOp",EDGE,"E2632"),sQuery(id+"F0.wireOp",EDGE,"E2633"),sQuery(id+"F0.wireOp",EDGE,"E2634"),sQuery(id+"F0.wireOp",EDGE,"E2635"),sQuery(id+"F0.wireOp",EDGE,"E2636"),sQuery(id+"F0.wireOp",EDGE,"E2637"),sQuery(id+"F0.wireOp",EDGE,"E2638"),sQuery(id+"F0.wireOp",EDGE,"E2639"),sQuery(id+"F0.wireOp",EDGE,"E2640"),sQuery(id+"F0.wireOp",EDGE,"E2641"),sQuery(id+"F0.wireOp",EDGE,"E2642"),sQuery(id+"F0.wireOp",EDGE,"E2643"),sQuery(id+"F0.wireOp",EDGE,"E2644"),sQuery(id+"F0.wireOp",EDGE,"E2645"),sQuery(id+"F0.wireOp",EDGE,"E2646"),sQuery(id+"F0.wireOp",EDGE,"E2647"),sQuery(id+"F0.wireOp",EDGE,"E2648"),sQuery(id+"F0.wireOp",EDGE,"E2649"),sQuery(id+"F0.wireOp",EDGE,"E2650"),sQuery(id+"F0.wireOp",EDGE,"E2651"),sQuery(id+"F0.wireOp",EDGE,"E2652"),sQuery(id+"F0.wireOp",EDGE,"E2653"),sQuery(id+"F0.wireOp",EDGE,"E2654"),sQuery(id+"F0.wireOp",EDGE,"E2655"),sQuery(id+"F0.wireOp",EDGE,"E2656"),sQuery(id+"F0.wireOp",EDGE,"E2657"),sQuery(id+"F0.wireOp",EDGE,"E2658"),sQuery(id+"F0.wireOp",EDGE,"E2659"),sQuery(id+"F0.wireOp",EDGE,"E2660"),sQuery(id+"F0.wireOp",EDGE,"E2661"),sQuery(id+"F0.wireOp",EDGE,"E2662"),sQuery(id+"F0.wireOp",EDGE,"E2663"),sQuery(id+"F0.wireOp",EDGE,"E2664"),sQuery(id+"F0.wireOp",EDGE,"E2665"),sQuery(id+"F0.wireOp",EDGE,"E2666"),sQuery(id+"F0.wireOp",EDGE,"E2667"),sQuery(id+"F0.wireOp",EDGE,"E2668"),sQuery(id+"F0.wireOp",EDGE,"E2669"),sQuery(id+"F0.wireOp",EDGE,"E2670"),sQuery(id+"F0.wireOp",EDGE,"E2671"),sQuery(id+"F0.wireOp",EDGE,"E2672"),sQuery(id+"F0.wireOp",EDGE,"E2673"),sQuery(id+"F0.wireOp",EDGE,"E2674"),sQuery(id+"F0.wireOp",EDGE,"E2675"),sQuery(id+"F0.wireOp",EDGE,"E2676"),sQuery(id+"F0.wireOp",EDGE,"E2677"),sQuery(id+"F0.wireOp",EDGE,"E2678"),sQuery(id+"F0.wireOp",EDGE,"E2679"),sQuery(id+"F0.wireOp",EDGE,"E2680"),sQuery(id+"F0.wireOp",EDGE,"E2681"),sQuery(id+"F0.wireOp",EDGE,"E2682"),sQuery(id+"F0.wireOp",EDGE,"E2683"),sQuery(id+"F0.wireOp",EDGE,"E2684"),sQuery(id+"F0.wireOp",EDGE,"E2685"),sQuery(id+"F0.wireOp",EDGE,"E2686"),sQuery(id+"F0.wireOp",EDGE,"E2687"),sQuery(id+"F0.wireOp",EDGE,"E2688"),sQuery(id+"F0.wireOp",EDGE,"E2689"),sQuery(id+"F0.wireOp",EDGE,"E2690"),sQuery(id+"F0.wireOp",EDGE,"E2691"),sQuery(id+"F0.wireOp",EDGE,"E2692"),sQuery(id+"F0.wireOp",EDGE,"E2693"),sQuery(id+"F0.wireOp",EDGE,"E2694"),sQuery(id+"F0.wireOp",EDGE,"E2695"),sQuery(id+"F0.wireOp",EDGE,"E2696"),sQuery(id+"F0.wireOp",EDGE,"E2697"),sQuery(id+"F0.wireOp",EDGE,"E2698"),sQuery(id+"F0.wireOp",EDGE,"E2699"),sQuery(id+"F0.wireOp",EDGE,"E2700"),sQuery(id+"F0.wireOp",EDGE,"E2701"),sQuery(id+"F0.wireOp",EDGE,"E2702"),sQuery(id+"F0.wireOp",EDGE,"E2703"),sQuery(id+"F0.wireOp",EDGE,"E2704"),sQuery(id+"F0.wireOp",EDGE,"E2705"),sQuery(id+"F0.wireOp",EDGE,"E2706"),sQuery(id+"F0.wireOp",EDGE,"E2707"),sQuery(id+"F0.wireOp",EDGE,"E2708"),sQuery(id+"F0.wireOp",EDGE,"E2709"),sQuery(id+"F0.wireOp",EDGE,"E2710"),sQuery(id+"F0.wireOp",EDGE,"E2711"),sQuery(id+"F0.wireOp",EDGE,"E2712"),sQuery(id+"F0.wireOp",EDGE,"E2713"),sQuery(id+"F0.wireOp",EDGE,"E2714"),sQuery(id+"F0.wireOp",EDGE,"E2715"),sQuery(id+"F0.wireOp",EDGE,"E2716"),sQuery(id+"F0.wireOp",EDGE,"E2717"),sQuery(id+"F0.wireOp",EDGE,"E2718"),sQuery(id+"F0.wireOp",EDGE,"E2719"),sQuery(id+"F0.wireOp",EDGE,"E2720"),sQuery(id+"F0.wireOp",EDGE,"E2721"),sQuery(id+"F0.wireOp",EDGE,"E2722"),sQuery(id+"F0.wireOp",EDGE,"E2723"),sQuery(id+"F0.wireOp",EDGE,"E2724"),sQuery(id+"F0.wireOp",EDGE,"E2725"),sQuery(id+"F0.wireOp",EDGE,"E2726"),sQuery(id+"F0.wireOp",EDGE,"E2727"),sQuery(id+"F0.wireOp",EDGE,"E2728"),sQuery(id+"F0.wireOp",EDGE,"E2729"),sQuery(id+"F0.wireOp",EDGE,"E2730"),sQuery(id+"F0.wireOp",EDGE,"E2731"),sQuery(id+"F0.wireOp",EDGE,"E2732"),sQuery(id+"F0.wireOp",EDGE,"E2733"),sQuery(id+"F0.wireOp",EDGE,"E2734"),sQuery(id+"F0.wireOp",EDGE,"E2735"),sQuery(id+"F0.wireOp",EDGE,"E2736"),sQuery(id+"F0.wireOp",EDGE,"E2737"),sQuery(id+"F0.wireOp",EDGE,"E2738"),sQuery(id+"F0.wireOp",EDGE,"E2739"),sQuery(id+"F0.wireOp",EDGE,"E2740"),sQuery(id+"F0.wireOp",EDGE,"E2741"),sQuery(id+"F0.wireOp",EDGE,"E2742"),sQuery(id+"F0.wireOp",EDGE,"E2743"),sQuery(id+"F0.wireOp",EDGE,"E2744"),sQuery(id+"F0.wireOp",EDGE,"E2745"),sQuery(id+"F0.wireOp",EDGE,"E2746"),sQuery(id+"F0.wireOp",EDGE,"E2747"),sQuery(id+"F0.wireOp",EDGE,"E2748"),sQuery(id+"F0.wireOp",EDGE,"E2749"),sQuery(id+"F0.wireOp",EDGE,"E2750"),sQuery(id+"F0.wireOp",EDGE,"E2751"),sQuery(id+"F0.wireOp",EDGE,"E2752"),sQuery(id+"F0.wireOp",EDGE,"E2753"),sQuery(id+"F0.wireOp",EDGE,"E2754"),sQuery(id+"F0.wireOp",EDGE,"E2755"),sQuery(id+"F0.wireOp",EDGE,"E2756"),sQuery(id+"F0.wireOp",EDGE,"E2757"),sQuery(id+"F0.wireOp",EDGE,"E2758"),sQuery(id+"F0.wireOp",EDGE,"E2759"),sQuery(id+"F0.wireOp",EDGE,"E2760"),sQuery(id+"F0.wireOp",EDGE,"E2761"),sQuery(id+"F0.wireOp",EDGE,"E2762"),sQuery(id+"F0.wireOp",EDGE,"E2763"),sQuery(id+"F0.wireOp",EDGE,"E2764"),sQuery(id+"F0.wireOp",EDGE,"E2765"),sQuery(id+"F0.wireOp",EDGE,"E2766"),sQuery(id+"F0.wireOp",EDGE,"E2767"),sQuery(id+"F0.wireOp",EDGE,"E2768"),sQuery(id+"F0.wireOp",EDGE,"E2769"),sQuery(id+"F0.wireOp",EDGE,"E2770"),sQuery(id+"F0.wireOp",EDGE,"E2771"),sQuery(id+"F0.wireOp",EDGE,"E2772"),sQuery(id+"F0.wireOp",EDGE,"E2773"),sQuery(id+"F0.wireOp",EDGE,"E2774"),sQuery(id+"F0.wireOp",EDGE,"E2775"),sQuery(id+"F0.wireOp",EDGE,"E2776"),sQuery(id+"F0.wireOp",EDGE,"E2777"),sQuery(id+"F0.wireOp",EDGE,"E2778"),sQuery(id+"F0.wireOp",EDGE,"E2779"),sQuery(id+"F0.wireOp",EDGE,"E2780"),sQuery(id+"F0.wireOp",EDGE,"E2781"),sQuery(id+"F0.wireOp",EDGE,"E2782"),sQuery(id+"F0.wireOp",EDGE,"E2783"),sQuery(id+"F0.wireOp",EDGE,"E2784"),sQuery(id+"F0.wireOp",EDGE,"E2785"),sQuery(id+"F0.wireOp",EDGE,"E2786"),sQuery(id+"F0.wireOp",EDGE,"E2787"),sQuery(id+"F0.wireOp",EDGE,"E2788"),sQuery(id+"F0.wireOp",EDGE,"E2789"),sQuery(id+"F0.wireOp",EDGE,"E2790"),sQuery(id+"F0.wireOp",EDGE,"E2791"),sQuery(id+"F0.wireOp",EDGE,"E2792"),sQuery(id+"F0.wireOp",EDGE,"E2793"),sQuery(id+"F0.wireOp",EDGE,"E2794"),sQuery(id+"F0.wireOp",EDGE,"E2795"),sQuery(id+"F0.wireOp",EDGE,"E2796"),sQuery(id+"F0.wireOp",EDGE,"E2797"),sQuery(id+"F0.wireOp",EDGE,"E2798"),sQuery(id+"F0.wireOp",EDGE,"E2799"),sQuery(id+"F0.wireOp",EDGE,"E2800"),sQuery(id+"F0.wireOp",EDGE,"E2801"),sQuery(id+"F0.wireOp",EDGE,"E2802"),sQuery(id+"F0.wireOp",EDGE,"E2803"),sQuery(id+"F0.wireOp",EDGE,"E2804"),sQuery(id+"F0.wireOp",EDGE,"E2805"),sQuery(id+"F0.wireOp",EDGE,"E2806"),sQuery(id+"F0.wireOp",EDGE,"E2807"),sQuery(id+"F0.wireOp",EDGE,"E2808"),sQuery(id+"F0.wireOp",EDGE,"E2809"),sQuery(id+"F0.wireOp",EDGE,"E2810"),sQuery(id+"F0.wireOp",EDGE,"E2811"),sQuery(id+"F0.wireOp",EDGE,"E2812"),sQuery(id+"F0.wireOp",EDGE,"E2813"),sQuery(id+"F0.wireOp",EDGE,"E2814"),sQuery(id+"F0.wireOp",EDGE,"E2815"),sQuery(id+"F0.wireOp",EDGE,"E2816"),sQuery(id+"F0.wireOp",EDGE,"E2817"),sQuery(id+"F0.wireOp",EDGE,"E2818"),sQuery(id+"F0.wireOp",EDGE,"E2819"),sQuery(id+"F0.wireOp",EDGE,"E2820"),sQuery(id+"F0.wireOp",EDGE,"E2821"),sQuery(id+"F0.wireOp",EDGE,"E2822"),sQuery(id+"F0.wireOp",EDGE,"E2823"),sQuery(id+"F0.wireOp",EDGE,"E2824"),sQuery(id+"F0.wireOp",EDGE,"E2825"),sQuery(id+"F0.wireOp",EDGE,"E2826"),sQuery(id+"F0.wireOp",EDGE,"E2827"),sQuery(id+"F0.wireOp",EDGE,"E2828"),sQuery(id+"F0.wireOp",EDGE,"E2829"),sQuery(id+"F0.wireOp",EDGE,"E2830"),sQuery(id+"F0.wireOp",EDGE,"E2831"),sQuery(id+"F0.wireOp",EDGE,"E2832"),sQuery(id+"F0.wireOp",EDGE,"E2833"),sQuery(id+"F0.wireOp",EDGE,"E2834"),sQuery(id+"F0.wireOp",EDGE,"E2835"),sQuery(id+"F0.wireOp",EDGE,"E2836"),sQuery(id+"F0.wireOp",EDGE,"E2837"),sQuery(id+"F0.wireOp",EDGE,"E2838"),sQuery(id+"F0.wireOp",EDGE,"E2839"),sQuery(id+"F0.wireOp",EDGE,"E2840"),sQuery(id+"F0.wireOp",EDGE,"E2841"),sQuery(id+"F0.wireOp",EDGE,"E2842"),sQuery(id+"F0.wireOp",EDGE,"E2843"),sQuery(id+"F0.wireOp",EDGE,"E2844"),sQuery(id+"F0.wireOp",EDGE,"E2845"),sQuery(id+"F0.wireOp",EDGE,"E2846"),sQuery(id+"F0.wireOp",EDGE,"E2847"),sQuery(id+"F0.wireOp",EDGE,"E2848"),sQuery(id+"F0.wireOp",EDGE,"E2849"),sQuery(id+"F0.wireOp",EDGE,"E2850"),sQuery(id+"F0.wireOp",EDGE,"E2851"),sQuery(id+"F0.wireOp",EDGE,"E2852"),sQuery(id+"F0.wireOp",EDGE,"E2853"),sQuery(id+"F0.wireOp",EDGE,"E2854"),sQuery(id+"F0.wireOp",EDGE,"E2855"),sQuery(id+"F0.wireOp",EDGE,"E2856"),sQuery(id+"F0.wireOp",EDGE,"E2857"),sQuery(id+"F0.wireOp",EDGE,"E2858"),sQuery(id+"F0.wireOp",EDGE,"E2859"),sQuery(id+"F0.wireOp",EDGE,"E2860"),sQuery(id+"F0.wireOp",EDGE,"E2861"),sQuery(id+"F0.wireOp",EDGE,"E2862"),sQuery(id+"F0.wireOp",EDGE,"E2863"),sQuery(id+"F0.wireOp",EDGE,"E2864"),sQuery(id+"F0.wireOp",EDGE,"E2865"),sQuery(id+"F0.wireOp",EDGE,"E2866"),sQuery(id+"F0.wireOp",EDGE,"E2867"),sQuery(id+"F0.wireOp",EDGE,"E2868"),sQuery(id+"F0.wireOp",EDGE,"E2869"),sQuery(id+"F0.wireOp",EDGE,"E2870"),sQuery(id+"F0.wireOp",EDGE,"E2871"),sQuery(id+"F0.wireOp",EDGE,"E2872"),sQuery(id+"F0.wireOp",EDGE,"E2873"),sQuery(id+"F0.wireOp",EDGE,"E2874"),sQuery(id+"F0.wireOp",EDGE,"E2875"),sQuery(id+"F0.wireOp",EDGE,"E2876"),sQuery(id+"F0.wireOp",EDGE,"E2877"),sQuery(id+"F0.wireOp",EDGE,"E2878"),sQuery(id+"F0.wireOp",EDGE,"E2879"),sQuery(id+"F0.wireOp",EDGE,"E2880"),sQuery(id+"F0.wireOp",EDGE,"E2881"),sQuery(id+"F0.wireOp",EDGE,"E2882"),sQuery(id+"F0.wireOp",EDGE,"E2883"),sQuery(id+"F0.wireOp",EDGE,"E2884"),sQuery(id+"F0.wireOp",EDGE,"E2885"),sQuery(id+"F0.wireOp",EDGE,"E2886"),sQuery(id+"F0.wireOp",EDGE,"E2887"),sQuery(id+"F0.wireOp",EDGE,"E2888"),sQuery(id+"F0.wireOp",EDGE,"E2889"),sQuery(id+"F0.wireOp",EDGE,"E2890"),sQuery(id+"F0.wireOp",EDGE,"E2891"),sQuery(id+"F0.wireOp",EDGE,"E2892"),sQuery(id+"F0.wireOp",EDGE,"E2893"),sQuery(id+"F0.wireOp",EDGE,"E2894"),sQuery(id+"F0.wireOp",EDGE,"E2895"),sQuery(id+"F0.wireOp",EDGE,"E2896"),sQuery(id+"F0.wireOp",EDGE,"E2897"),sQuery(id+"F0.wireOp",EDGE,"E2898"),sQuery(id+"F0.wireOp",EDGE,"E2899"),sQuery(id+"F0.wireOp",EDGE,"E2900"),sQuery(id+"F0.wireOp",EDGE,"E2901"),sQuery(id+"F0.wireOp",EDGE,"E2902"),sQuery(id+"F0.wireOp",EDGE,"E2903"),sQuery(id+"F0.wireOp",EDGE,"E2904"),sQuery(id+"F0.wireOp",EDGE,"E2905"),sQuery(id+"F0.wireOp",EDGE,"E2906"),sQuery(id+"F0.wireOp",EDGE,"E2907"),sQuery(id+"F0.wireOp",EDGE,"E2908"),sQuery(id+"F0.wireOp",EDGE,"E2909"),sQuery(id+"F0.wireOp",EDGE,"E2910"),sQuery(id+"F0.wireOp",EDGE,"E2911"),sQuery(id+"F0.wireOp",EDGE,"E2912"),sQuery(id+"F0.wireOp",EDGE,"E2913"),sQuery(id+"F0.wireOp",EDGE,"E2914"),sQuery(id+"F0.wireOp",EDGE,"E2915"),sQuery(id+"F0.wireOp",EDGE,"E2916"),sQuery(id+"F0.wireOp",EDGE,"E2917"),sQuery(id+"F0.wireOp",EDGE,"E2918"),sQuery(id+"F0.wireOp",EDGE,"E2919"),sQuery(id+"F0.wireOp",EDGE,"E2920"),sQuery(id+"F0.wireOp",EDGE,"E2921"),sQuery(id+"F0.wireOp",EDGE,"E2922"),sQuery(id+"F0.wireOp",EDGE,"E2923"),sQuery(id+"F0.wireOp",EDGE,"E2924"),sQuery(id+"F0.wireOp",EDGE,"E2925"),sQuery(id+"F0.wireOp",EDGE,"E2926"),sQuery(id+"F0.wireOp",EDGE,"E2927"),sQuery(id+"F0.wireOp",EDGE,"E2928"),sQuery(id+"F0.wireOp",EDGE,"E2929"),sQuery(id+"F0.wireOp",EDGE,"E2930"),sQuery(id+"F0.wireOp",EDGE,"E2931"),sQuery(id+"F0.wireOp",EDGE,"E2932"),sQuery(id+"F0.wireOp",EDGE,"E2933"),sQuery(id+"F0.wireOp",EDGE,"E2934"),sQuery(id+"F0.wireOp",EDGE,"E2935"),sQuery(id+"F0.wireOp",EDGE,"E2936"),sQuery(id+"F0.wireOp",EDGE,"E2937"),sQuery(id+"F0.wireOp",EDGE,"E2938"),sQuery(id+"F0.wireOp",EDGE,"E2939"),sQuery(id+"F0.wireOp",EDGE,"E2940"),sQuery(id+"F0.wireOp",EDGE,"E2941"),sQuery(id+"F0.wireOp",EDGE,"E2942"),sQuery(id+"F0.wireOp",EDGE,"E2943"),sQuery(id+"F0.wireOp",EDGE,"E2944"),sQuery(id+"F0.wireOp",EDGE,"E2945"),sQuery(id+"F0.wireOp",EDGE,"E2946"),sQuery(id+"F0.wireOp",EDGE,"E2947"),sQuery(id+"F0.wireOp",EDGE,"E2948"),sQuery(id+"F0.wireOp",EDGE,"E2949"),sQuery(id+"F0.wireOp",EDGE,"E2950"),sQuery(id+"F0.wireOp",EDGE,"E2951"),sQuery(id+"F0.wireOp",EDGE,"E2952"),sQuery(id+"F0.wireOp",EDGE,"E2953"),sQuery(id+"F0.wireOp",EDGE,"E2954"),sQuery(id+"F0.wireOp",EDGE,"E2955"),sQuery(id+"F0.wireOp",EDGE,"E2956"),sQuery(id+"F0.wireOp",EDGE,"E2957"),sQuery(id+"F0.wireOp",EDGE,"E2958"),sQuery(id+"F0.wireOp",EDGE,"E2959"),sQuery(id+"F0.wireOp",EDGE,"E2960"),sQuery(id+"F0.wireOp",EDGE,"E2961"),sQuery(id+"F0.wireOp",EDGE,"E2962"),sQuery(id+"F0.wireOp",EDGE,"E2963"),sQuery(id+"F0.wireOp",EDGE,"E2964"),sQuery(id+"F0.wireOp",EDGE,"E2965"),sQuery(id+"F0.wireOp",EDGE,"E2966"),sQuery(id+"F0.wireOp",EDGE,"E2967"),sQuery(id+"F0.wireOp",EDGE,"E2968"),sQuery(id+"F0.wireOp",EDGE,"E2969"),sQuery(id+"F0.wireOp",EDGE,"E2970"),sQuery(id+"F0.wireOp",EDGE,"E2971"),sQuery(id+"F0.wireOp",EDGE,"E2972"),sQuery(id+"F0.wireOp",EDGE,"E2973"),sQuery(id+"F0.wireOp",EDGE,"E2974"),sQuery(id+"F0.wireOp",EDGE,"E2975"),sQuery(id+"F0.wireOp",EDGE,"E2976"),sQuery(id+"F0.wireOp",EDGE,"E2977"),sQuery(id+"F0.wireOp",EDGE,"E2978"),sQuery(id+"F0.wireOp",EDGE,"E2979"),sQuery(id+"F0.wireOp",EDGE,"E2980"),sQuery(id+"F0.wireOp",EDGE,"E2981"),sQuery(id+"F0.wireOp",EDGE,"E2982"),sQuery(id+"F0.wireOp",EDGE,"E2983"),sQuery(id+"F0.wireOp",EDGE,"E2984"),sQuery(id+"F0.wireOp",EDGE,"E2985"),sQuery(id+"F0.wireOp",EDGE,"E2986"),sQuery(id+"F0.wireOp",EDGE,"E2987"),sQuery(id+"F0.wireOp",EDGE,"E2988"),sQuery(id+"F0.wireOp",EDGE,"E2989"),sQuery(id+"F0.wireOp",EDGE,"E2990"),sQuery(id+"F0.wireOp",EDGE,"E2991"),sQuery(id+"F0.wireOp",EDGE,"E2992"),sQuery(id+"F0.wireOp",EDGE,"E2993"),sQuery(id+"F0.wireOp",EDGE,"E2994"),sQuery(id+"F0.wireOp",EDGE,"E2995"),sQuery(id+"F0.wireOp",EDGE,"E2996"),sQuery(id+"F0.wireOp",EDGE,"E2997"),sQuery(id+"F0.wireOp",EDGE,"E2998"),sQuery(id+"F0.wireOp",EDGE,"E2999"),sQuery(id+"F0.wireOp",EDGE,"E3000"),sQuery(id+"F0.wireOp",EDGE,"E3001"),sQuery(id+"F0.wireOp",EDGE,"E3002"),sQuery(id+"F0.wireOp",EDGE,"E3003"),sQuery(id+"F0.wireOp",EDGE,"E3004"),sQuery(id+"F0.wireOp",EDGE,"E3005"),sQuery(id+"F0.wireOp",EDGE,"E3006"),sQuery(id+"F0.wireOp",EDGE,"E3007"),sQuery(id+"F0.wireOp",EDGE,"E3008"),sQuery(id+"F0.wireOp",EDGE,"E3009"),sQuery(id+"F0.wireOp",EDGE,"E3010"),sQuery(id+"F0.wireOp",EDGE,"E3011"),sQuery(id+"F0.wireOp",EDGE,"E3012"),sQuery(id+"F0.wireOp",EDGE,"E3013"),sQuery(id+"F0.wireOp",EDGE,"E3014"),sQuery(id+"F0.wireOp",EDGE,"E3015"),sQuery(id+"F0.wireOp",EDGE,"E3016"),sQuery(id+"F0.wireOp",EDGE,"E3017"),sQuery(id+"F0.wireOp",EDGE,"E3018"),sQuery(id+"F0.wireOp",EDGE,"E3019"),sQuery(id+"F0.wireOp",EDGE,"E3020"),sQuery(id+"F0.wireOp",EDGE,"E3021"),sQuery(id+"F0.wireOp",EDGE,"E3022"),sQuery(id+"F0.wireOp",EDGE,"E3023"),sQuery(id+"F0.wireOp",EDGE,"E3024"),sQuery(id+"F0.wireOp",EDGE,"E3025"),sQuery(id+"F0.wireOp",EDGE,"E3026"),sQuery(id+"F0.wireOp",EDGE,"E3027"),sQuery(id+"F0.wireOp",EDGE,"E3028"),sQuery(id+"F0.wireOp",EDGE,"E3029"),sQuery(id+"F0.wireOp",EDGE,"E3030"),sQuery(id+"F0.wireOp",EDGE,"E3031"),sQuery(id+"F0.wireOp",EDGE,"E3032"),sQuery(id+"F0.wireOp",EDGE,"E3033"),sQuery(id+"F0.wireOp",EDGE,"E3034"),sQuery(id+"F0.wireOp",EDGE,"E3035"),sQuery(id+"F0.wireOp",EDGE,"E3036"),sQuery(id+"F0.wireOp",EDGE,"E3037"),sQuery(id+"F0.wireOp",EDGE,"E3038"),sQuery(id+"F0.wireOp",EDGE,"E3039"),sQuery(id+"F0.wireOp",EDGE,"E3040"),sQuery(id+"F0.wireOp",EDGE,"E3041"),sQuery(id+"F0.wireOp",EDGE,"E3042"),sQuery(id+"F0.wireOp",EDGE,"E3043"),sQuery(id+"F0.wireOp",EDGE,"E3044"),sQuery(id+"F0.wireOp",EDGE,"E3045"),sQuery(id+"F0.wireOp",EDGE,"E3046"),sQuery(id+"F0.wireOp",EDGE,"E3047"),sQuery(id+"F0.wireOp",EDGE,"E3048"),sQuery(id+"F0.wireOp",EDGE,"E3049"),sQuery(id+"F0.wireOp",EDGE,"E3050"),sQuery(id+"F0.wireOp",EDGE,"E3051"),sQuery(id+"F0.wireOp",EDGE,"E3052"),sQuery(id+"F0.wireOp",EDGE,"E3053"),sQuery(id+"F0.wireOp",EDGE,"E3054"),sQuery(id+"F0.wireOp",EDGE,"E3055"),sQuery(id+"F0.wireOp",EDGE,"E3056"),sQuery(id+"F0.wireOp",EDGE,"E3057"),sQuery(id+"F0.wireOp",EDGE,"E3058"),sQuery(id+"F0.wireOp",EDGE,"E3059"),sQuery(id+"F0.wireOp",EDGE,"E3060"),sQuery(id+"F0.wireOp",EDGE,"E3061"),sQuery(id+"F0.wireOp",EDGE,"E3062"),sQuery(id+"F0.wireOp",EDGE,"E3063"),sQuery(id+"F0.wireOp",EDGE,"E3064"),sQuery(id+"F0.wireOp",EDGE,"E3065"),sQuery(id+"F0.wireOp",EDGE,"E3066"),sQuery(id+"F0.wireOp",EDGE,"E3067"),sQuery(id+"F0.wireOp",EDGE,"E3068"),sQuery(id+"F0.wireOp",EDGE,"E3069"),sQuery(id+"F0.wireOp",EDGE,"E3070"),sQuery(id+"F0.wireOp",EDGE,"E3071"),sQuery(id+"F0.wireOp",EDGE,"E3072"),sQuery(id+"F0.wireOp",EDGE,"E3073"),sQuery(id+"F0.wireOp",EDGE,"E3074"),sQuery(id+"F0.wireOp",EDGE,"E3075"),sQuery(id+"F0.wireOp",EDGE,"E3076"),sQuery(id+"F0.wireOp",EDGE,"E3077"),sQuery(id+"F0.wireOp",EDGE,"E3078"),sQuery(id+"F0.wireOp",EDGE,"E3079"),sQuery(id+"F0.wireOp",EDGE,"E3080"),sQuery(id+"F0.wireOp",EDGE,"E3081"),sQuery(id+"F0.wireOp",EDGE,"E3082"),sQuery(id+"F0.wireOp",EDGE,"E3083"),sQuery(id+"F0.wireOp",EDGE,"E3084"),sQuery(id+"F0.wireOp",EDGE,"E3085"),sQuery(id+"F0.wireOp",EDGE,"E3086"),sQuery(id+"F0.wireOp",EDGE,"E3087"),sQuery(id+"F0.wireOp",EDGE,"E3088"),sQuery(id+"F0.wireOp",EDGE,"E3089"),sQuery(id+"F0.wireOp",EDGE,"E3090"),sQuery(id+"F0.wireOp",EDGE,"E3091"),sQuery(id+"F0.wireOp",EDGE,"E3092"),sQuery(id+"F0.wireOp",EDGE,"E3093"),sQuery(id+"F0.wireOp",EDGE,"E3094"),sQuery(id+"F0.wireOp",EDGE,"E3095"),sQuery(id+"F0.wireOp",EDGE,"E3096"),sQuery(id+"F0.wireOp",EDGE,"E3097"),sQuery(id+"F0.wireOp",EDGE,"E3098"),sQuery(id+"F0.wireOp",EDGE,"E3099"),sQuery(id+"F0.wireOp",EDGE,"E3100"),sQuery(id+"F0.wireOp",EDGE,"E3101"),sQuery(id+"F0.wireOp",EDGE,"E3102"),sQuery(id+"F0.wireOp",EDGE,"E3103"),sQuery(id+"F0.wireOp",EDGE,"E3104"),sQuery(id+"F0.wireOp",EDGE,"E3105"),sQuery(id+"F0.wireOp",EDGE,"E3106"),sQuery(id+"F0.wireOp",EDGE,"E3107"),sQuery(id+"F0.wireOp",EDGE,"E3108"),sQuery(id+"F0.wireOp",EDGE,"E3109"),sQuery(id+"F0.wireOp",EDGE,"E3110"),sQuery(id+"F0.wireOp",EDGE,"E3111"),sQuery(id+"F0.wireOp",EDGE,"E3112"),sQuery(id+"F0.wireOp",EDGE,"E3113"),sQuery(id+"F0.wireOp",EDGE,"E3114"),sQuery(id+"F0.wireOp",EDGE,"E3115"),sQuery(id+"F0.wireOp",EDGE,"E3116"),sQuery(id+"F0.wireOp",EDGE,"E3117"),sQuery(id+"F0.wireOp",EDGE,"E3118"),sQuery(id+"F0.wireOp",EDGE,"E3119"),sQuery(id+"F0.wireOp",EDGE,"E3120"),sQuery(id+"F0.wireOp",EDGE,"E3121"),sQuery(id+"F0.wireOp",EDGE,"E3122"),sQuery(id+"F0.wireOp",EDGE,"E3123"),sQuery(id+"F0.wireOp",EDGE,"E3124"),sQuery(id+"F0.wireOp",EDGE,"E3125"),sQuery(id+"F0.wireOp",EDGE,"E3126"),sQuery(id+"F0.wireOp",EDGE,"E3127"),sQuery(id+"F0.wireOp",EDGE,"E3128"),sQuery(id+"F0.wireOp",EDGE,"E3129"),sQuery(id+"F0.wireOp",EDGE,"E3130"),sQuery(id+"F0.wireOp",EDGE,"E3131"),sQuery(id+"F0.wireOp",EDGE,"E3132"),sQuery(id+"F0.wireOp",EDGE,"E3133"),sQuery(id+"F0.wireOp",EDGE,"E3134"),sQuery(id+"F0.wireOp",EDGE,"E3135"),sQuery(id+"F0.wireOp",EDGE,"E3136"),sQuery(id+"F0.wireOp",EDGE,"E3137"),sQuery(id+"F0.wireOp",EDGE,"E3138"),sQuery(id+"F0.wireOp",EDGE,"E3139"),sQuery(id+"F0.wireOp",EDGE,"E3140"),sQuery(id+"F0.wireOp",EDGE,"E3141"),sQuery(id+"F0.wireOp",EDGE,"E3142"),sQuery(id+"F0.wireOp",EDGE,"E3143"),sQuery(id+"F0.wireOp",EDGE,"E3144"),sQuery(id+"F0.wireOp",EDGE,"E3145"),sQuery(id+"F0.wireOp",EDGE,"E3146"),sQuery(id+"F0.wireOp",EDGE,"E3147"),sQuery(id+"F0.wireOp",EDGE,"E3148"),sQuery(id+"F0.wireOp",EDGE,"E3149"),sQuery(id+"F0.wireOp",EDGE,"E3150"),sQuery(id+"F0.wireOp",EDGE,"E3151"),sQuery(id+"F0.wireOp",EDGE,"E3152"),sQuery(id+"F0.wireOp",EDGE,"E3153"),sQuery(id+"F0.wireOp",EDGE,"E3154"),sQuery(id+"F0.wireOp",EDGE,"E3155"),sQuery(id+"F0.wireOp",EDGE,"E3156"),sQuery(id+"F0.wireOp",EDGE,"E3157"),sQuery(id+"F0.wireOp",EDGE,"E3158"),sQuery(id+"F0.wireOp",EDGE,"E3159"),sQuery(id+"F0.wireOp",EDGE,"E3160"),sQuery(id+"F0.wireOp",EDGE,"E3161"),sQuery(id+"F0.wireOp",EDGE,"E3162"),sQuery(id+"F0.wireOp",EDGE,"E3163"),sQuery(id+"F0.wireOp",EDGE,"E3164"),sQuery(id+"F0.wireOp",EDGE,"E3165"),sQuery(id+"F0.wireOp",EDGE,"E3166"),sQuery(id+"F0.wireOp",EDGE,"E3167"),sQuery(id+"F0.wireOp",EDGE,"E3168"),sQuery(id+"F0.wireOp",EDGE,"E3169"),sQuery(id+"F0.wireOp",EDGE,"E3170"),sQuery(id+"F0.wireOp",EDGE,"E3171"),sQuery(id+"F0.wireOp",EDGE,"E3172"),sQuery(id+"F0.wireOp",EDGE,"E3173"),sQuery(id+"F0.wireOp",EDGE,"E3174"),sQuery(id+"F0.wireOp",EDGE,"E3175"),sQuery(id+"F0.wireOp",EDGE,"E3176"),sQuery(id+"F0.wireOp",EDGE,"E3177"),sQuery(id+"F0.wireOp",EDGE,"E3178"),sQuery(id+"F0.wireOp",EDGE,"E3179"),sQuery(id+"F0.wireOp",EDGE,"E3180"),sQuery(id+"F0.wireOp",EDGE,"E3181"),sQuery(id+"F0.wireOp",EDGE,"E3182"),sQuery(id+"F0.wireOp",EDGE,"E3183"),sQuery(id+"F0.wireOp",EDGE,"E3184"),sQuery(id+"F0.wireOp",EDGE,"E3185"),sQuery(id+"F0.wireOp",EDGE,"E3186"),sQuery(id+"F0.wireOp",EDGE,"E3187"),sQuery(id+"F0.wireOp",EDGE,"E3188"),sQuery(id+"F0.wireOp",EDGE,"E3189"),sQuery(id+"F0.wireOp",EDGE,"E3190"),sQuery(id+"F0.wireOp",EDGE,"E3191"),sQuery(id+"F0.wireOp",EDGE,"E3192"),sQuery(id+"F0.wireOp",EDGE,"E3193"),sQuery(id+"F0.wireOp",EDGE,"E3194"),sQuery(id+"F0.wireOp",EDGE,"E3195"),sQuery(id+"F0.wireOp",EDGE,"E3196"),sQuery(id+"F0.wireOp",EDGE,"E3197"),sQuery(id+"F0.wireOp",EDGE,"E3198"),sQuery(id+"F0.wireOp",EDGE,"E3199"),sQuery(id+"F0.wireOp",EDGE,"E3200"),sQuery(id+"F0.wireOp",EDGE,"E3201"),sQuery(id+"F0.wireOp",EDGE,"E3202"),sQuery(id+"F0.wireOp",EDGE,"E3203"),sQuery(id+"F0.wireOp",EDGE,"E3204"),sQuery(id+"F0.wireOp",EDGE,"E3205"),sQuery(id+"F0.wireOp",EDGE,"E3206"),sQuery(id+"F0.wireOp",EDGE,"E3207"),sQuery(id+"F0.wireOp",EDGE,"E3208"),sQuery(id+"F0.wireOp",EDGE,"E3209"),sQuery(id+"F0.wireOp",EDGE,"E3210"),sQuery(id+"F0.wireOp",EDGE,"E3211"),sQuery(id+"F0.wireOp",EDGE,"E3212"),sQuery(id+"F0.wireOp",EDGE,"E3213"),sQuery(id+"F0.wireOp",EDGE,"E3214"),sQuery(id+"F0.wireOp",EDGE,"E3215"),sQuery(id+"F0.wireOp",EDGE,"E3216"),sQuery(id+"F0.wireOp",EDGE,"E3217"),sQuery(id+"F0.wireOp",EDGE,"E3218"),sQuery(id+"F0.wireOp",EDGE,"E3219"),sQuery(id+"F0.wireOp",EDGE,"E3220"),sQuery(id+"F0.wireOp",EDGE,"E3221"),sQuery(id+"F0.wireOp",EDGE,"E3222"),sQuery(id+"F0.wireOp",EDGE,"E3223"),sQuery(id+"F0.wireOp",EDGE,"E3224"),sQuery(id+"F0.wireOp",EDGE,"E3225"),sQuery(id+"F0.wireOp",EDGE,"E3226"),sQuery(id+"F0.wireOp",EDGE,"E3227"),sQuery(id+"F0.wireOp",EDGE,"E3228"),sQuery(id+"F0.wireOp",EDGE,"E3229"),sQuery(id+"F0.wireOp",EDGE,"E3230"),sQuery(id+"F0.wireOp",EDGE,"E3231"),sQuery(id+"F0.wireOp",EDGE,"E3232"),sQuery(id+"F0.wireOp",EDGE,"E3233"),sQuery(id+"F0.wireOp",EDGE,"E3234"),sQuery(id+"F0.wireOp",EDGE,"E3235"),sQuery(id+"F0.wireOp",EDGE,"E3236"),sQuery(id+"F0.wireOp",EDGE,"E3237"),sQuery(id+"F0.wireOp",EDGE,"E3238"),sQuery(id+"F0.wireOp",EDGE,"E3239"),sQuery(id+"F0.wireOp",EDGE,"E3240"),sQuery(id+"F0.wireOp",EDGE,"E3241"),sQuery(id+"F0.wireOp",EDGE,"E3242"),sQuery(id+"F0.wireOp",EDGE,"E3243"),sQuery(id+"F0.wireOp",EDGE,"E3244"),sQuery(id+"F0.wireOp",EDGE,"E3245"),sQuery(id+"F0.wireOp",EDGE,"E3246"),sQuery(id+"F0.wireOp",EDGE,"E3247"),sQuery(id+"F0.wireOp",EDGE,"E3248"),sQuery(id+"F0.wireOp",EDGE,"E3249"),sQuery(id+"F0.wireOp",EDGE,"E3250"),sQuery(id+"F0.wireOp",EDGE,"E3251"),sQuery(id+"F0.wireOp",EDGE,"E3252"),sQuery(id+"F0.wireOp",EDGE,"E3253"),sQuery(id+"F0.wireOp",EDGE,"E3254"),sQuery(id+"F0.wireOp",EDGE,"E3255"),sQuery(id+"F0.wireOp",EDGE,"E3256"),sQuery(id+"F0.wireOp",EDGE,"E3257"),sQuery(id+"F0.wireOp",EDGE,"E3258"),sQuery(id+"F0.wireOp",EDGE,"E3259"),sQuery(id+"F0.wireOp",EDGE,"E3260"),sQuery(id+"F0.wireOp",EDGE,"E3261"),sQuery(id+"F0.wireOp",EDGE,"E3262"),sQuery(id+"F0.wireOp",EDGE,"E3263"),sQuery(id+"F0.wireOp",EDGE,"E3264"),sQuery(id+"F0.wireOp",EDGE,"E3265"),sQuery(id+"F0.wireOp",EDGE,"E3266"),sQuery(id+"F0.wireOp",EDGE,"E3267"),sQuery(id+"F0.wireOp",EDGE,"E3268"),sQuery(id+"F0.wireOp",EDGE,"E3269"),sQuery(id+"F0.wireOp",EDGE,"E3270"),sQuery(id+"F0.wireOp",EDGE,"E3271"),sQuery(id+"F0.wireOp",EDGE,"E3272"),sQuery(id+"F0.wireOp",EDGE,"E3273"),sQuery(id+"F0.wireOp",EDGE,"E3274"),sQuery(id+"F0.wireOp",EDGE,"E3275"),sQuery(id+"F0.wireOp",EDGE,"E3276"),sQuery(id+"F0.wireOp",EDGE,"E3277"),sQuery(id+"F0.wireOp",EDGE,"E3278"),sQuery(id+"F0.wireOp",EDGE,"E3279"),sQuery(id+"F0.wireOp",EDGE,"E3280"),sQuery(id+"F0.wireOp",EDGE,"E3281"),sQuery(id+"F0.wireOp",EDGE,"E3282"),sQuery(id+"F0.wireOp",EDGE,"E3283"),sQuery(id+"F0.wireOp",EDGE,"E3284"),sQuery(id+"F0.wireOp",EDGE,"E3285"),sQuery(id+"F0.wireOp",EDGE,"E3286"),sQuery(id+"F0.wireOp",EDGE,"E3287"),sQuery(id+"F0.wireOp",EDGE,"E3288"),sQuery(id+"F0.wireOp",EDGE,"E3289"),sQuery(id+"F0.wireOp",EDGE,"E3290"),sQuery(id+"F0.wireOp",EDGE,"E3291"),sQuery(id+"F0.wireOp",EDGE,"E3292"),sQuery(id+"F0.wireOp",EDGE,"E3293"),sQuery(id+"F0.wireOp",EDGE,"E3294"),sQuery(id+"F0.wireOp",EDGE,"E3295"),sQuery(id+"F0.wireOp",EDGE,"E3296"),sQuery(id+"F0.wireOp",EDGE,"E3297"),sQuery(id+"F0.wireOp",EDGE,"E3298"),sQuery(id+"F0.wireOp",EDGE,"E3299"),sQuery(id+"F0.wireOp",EDGE,"E3300"),sQuery(id+"F0.wireOp",EDGE,"E3301"),sQuery(id+"F0.wireOp",EDGE,"E3302"),sQuery(id+"F0.wireOp",EDGE,"E3303"),sQuery(id+"F0.wireOp",EDGE,"E3304"),sQuery(id+"F0.wireOp",EDGE,"E3305"),sQuery(id+"F0.wireOp",EDGE,"E3306"),sQuery(id+"F0.wireOp",EDGE,"E3307"),sQuery(id+"F0.wireOp",EDGE,"E3308"),sQuery(id+"F0.wireOp",EDGE,"E3309"),sQuery(id+"F0.wireOp",EDGE,"E3310"),sQuery(id+"F0.wireOp",EDGE,"E3311"),sQuery(id+"F0.wireOp",EDGE,"E3312"),sQuery(id+"F0.wireOp",EDGE,"E3313"),sQuery(id+"F0.wireOp",EDGE,"E3314"),sQuery(id+"F0.wireOp",EDGE,"E3315"),sQuery(id+"F0.wireOp",EDGE,"E3316"),sQuery(id+"F0.wireOp",EDGE,"E3317"),sQuery(id+"F0.wireOp",EDGE,"E3318"),sQuery(id+"F0.wireOp",EDGE,"E3319"),sQuery(id+"F0.wireOp",EDGE,"E3320"),sQuery(id+"F0.wireOp",EDGE,"E3321"),sQuery(id+"F0.wireOp",EDGE,"E3322"),sQuery(id+"F0.wireOp",EDGE,"E3323"),sQuery(id+"F0.wireOp",EDGE,"E3324"),sQuery(id+"F0.wireOp",EDGE,"E3325"),sQuery(id+"F0.wireOp",EDGE,"E3326"),sQuery(id+"F0.wireOp",EDGE,"E3327"),sQuery(id+"F0.wireOp",EDGE,"E3328"),sQuery(id+"F0.wireOp",EDGE,"E3329"),sQuery(id+"F0.wireOp",EDGE,"E3330"),sQuery(id+"F0.wireOp",EDGE,"E3331"),sQuery(id+"F0.wireOp",EDGE,"E3332"),sQuery(id+"F0.wireOp",EDGE,"E3333"),sQuery(id+"F0.wireOp",EDGE,"E3334"),sQuery(id+"F0.wireOp",EDGE,"E3335"),sQuery(id+"F0.wireOp",EDGE,"E3336"),sQuery(id+"F0.wireOp",EDGE,"E3337"),sQuery(id+"F0.wireOp",EDGE,"E3338"),sQuery(id+"F0.wireOp",EDGE,"E3339"),sQuery(id+"F0.wireOp",EDGE,"E3340"),sQuery(id+"F0.wireOp",EDGE,"E3341"),sQuery(id+"F0.wireOp",EDGE,"E3342"),sQuery(id+"F0.wireOp",EDGE,"E3343"),sQuery(id+"F0.wireOp",EDGE,"E3344"),sQuery(id+"F0.wireOp",EDGE,"E3345"),sQuery(id+"F0.wireOp",EDGE,"E3346"),sQuery(id+"F0.wireOp",EDGE,"E3347"),sQuery(id+"F0.wireOp",EDGE,"E3348"),sQuery(id+"F0.wireOp",EDGE,"E3349"),sQuery(id+"F0.wireOp",EDGE,"E3350"),sQuery(id+"F0.wireOp",EDGE,"E3351"),sQuery(id+"F0.wireOp",EDGE,"E3352"),sQuery(id+"F0.wireOp",EDGE,"E3353"),sQuery(id+"F0.wireOp",EDGE,"E3354"),sQuery(id+"F0.wireOp",EDGE,"E3355"),sQuery(id+"F0.wireOp",EDGE,"E3356"),sQuery(id+"F0.wireOp",EDGE,"E3357"),sQuery(id+"F0.wireOp",EDGE,"E3358"),sQuery(id+"F0.wireOp",EDGE,"E3359"),sQuery(id+"F0.wireOp",EDGE,"E3360"),sQuery(id+"F0.wireOp",EDGE,"E3361"),sQuery(id+"F0.wireOp",EDGE,"E3362"),sQuery(id+"F0.wireOp",EDGE,"E3363"),sQuery(id+"F0.wireOp",EDGE,"E3364"),sQuery(id+"F0.wireOp",EDGE,"E3365"),sQuery(id+"F0.wireOp",EDGE,"E3366"),sQuery(id+"F0.wireOp",EDGE,"E3367"),sQuery(id+"F0.wireOp",EDGE,"E3368"),sQuery(id+"F0.wireOp",EDGE,"E3369"),sQuery(id+"F0.wireOp",EDGE,"E3370"),sQuery(id+"F0.wireOp",EDGE,"E3371"),sQuery(id+"F0.wireOp",EDGE,"E3372"),sQuery(id+"F0.wireOp",EDGE,"E3373"),sQuery(id+"F0.wireOp",EDGE,"E3374"),sQuery(id+"F0.wireOp",EDGE,"E3375"),sQuery(id+"F0.wireOp",EDGE,"E3376"),sQuery(id+"F0.wireOp",EDGE,"E3377"),sQuery(id+"F0.wireOp",EDGE,"E3378"),sQuery(id+"F0.wireOp",EDGE,"E3379"),sQuery(id+"F0.wireOp",EDGE,"E3380"),sQuery(id+"F0.wireOp",EDGE,"E3381"),sQuery(id+"F0.wireOp",EDGE,"E3382"),sQuery(id+"F0.wireOp",EDGE,"E3383"),sQuery(id+"F0.wireOp",EDGE,"E3384"),sQuery(id+"F0.wireOp",EDGE,"E3385"),sQuery(id+"F0.wireOp",EDGE,"E3386"),sQuery(id+"F0.wireOp",EDGE,"E3387"),sQuery(id+"F0.wireOp",EDGE,"E3388"),sQuery(id+"F0.wireOp",EDGE,"E3389"),sQuery(id+"F0.wireOp",EDGE,"E3390"),sQuery(id+"F0.wireOp",EDGE,"E3391"),sQuery(id+"F0.wireOp",EDGE,"E3392"),sQuery(id+"F0.wireOp",EDGE,"E3393"),sQuery(id+"F0.wireOp",EDGE,"E3394"),sQuery(id+"F0.wireOp",EDGE,"E3395"),sQuery(id+"F0.wireOp",EDGE,"E3396"),sQuery(id+"F0.wireOp",EDGE,"E3397"),sQuery(id+"F0.wireOp",EDGE,"E3398"),sQuery(id+"F0.wireOp",EDGE,"E3399"),sQuery(id+"F0.wireOp",EDGE,"E3400"),sQuery(id+"F0.wireOp",EDGE,"E3401"),sQuery(id+"F0.wireOp",EDGE,"E3402"),sQuery(id+"F0.wireOp",EDGE,"E3403"),sQuery(id+"F0.wireOp",EDGE,"E3404"),sQuery(id+"F0.wireOp",EDGE,"E3405"),sQuery(id+"F0.wireOp",EDGE,"E3406"),sQuery(id+"F0.wireOp",EDGE,"E3407"),sQuery(id+"F0.wireOp",EDGE,"E3408"),sQuery(id+"F0.wireOp",EDGE,"E3409"),sQuery(id+"F0.wireOp",EDGE,"E3410"),sQuery(id+"F0.wireOp",EDGE,"E3411"),sQuery(id+"F0.wireOp",EDGE,"E3412"),sQuery(id+"F0.wireOp",EDGE,"E3413"),sQuery(id+"F0.wireOp",EDGE,"E3414"),sQuery(id+"F0.wireOp",EDGE,"E3415"),sQuery(id+"F0.wireOp",EDGE,"E3416"),sQuery(id+"F0.wireOp",EDGE,"E3417"),sQuery(id+"F0.wireOp",EDGE,"E3418"),sQuery(id+"F0.wireOp",EDGE,"E3419"),sQuery(id+"F0.wireOp",EDGE,"E3420"),sQuery(id+"F0.wireOp",EDGE,"E3421"),sQuery(id+"F0.wireOp",EDGE,"E3422"),sQuery(id+"F0.wireOp",EDGE,"E3423"),sQuery(id+"F0.wireOp",EDGE,"E3424"),sQuery(id+"F0.wireOp",EDGE,"E3425"),sQuery(id+"F0.wireOp",EDGE,"E3426"),sQuery(id+"F0.wireOp",EDGE,"E3427"),sQuery(id+"F0.wireOp",EDGE,"E3428"),sQuery(id+"F0.wireOp",EDGE,"E3429"),sQuery(id+"F0.wireOp",EDGE,"E3430"),sQuery(id+"F0.wireOp",EDGE,"E3431"),sQuery(id+"F0.wireOp",EDGE,"E3432"),sQuery(id+"F0.wireOp",EDGE,"E3433"),sQuery(id+"F0.wireOp",EDGE,"E3434"),sQuery(id+"F0.wireOp",EDGE,"E3435"),sQuery(id+"F0.wireOp",EDGE,"E3436"),sQuery(id+"F0.wireOp",EDGE,"E3437"),sQuery(id+"F0.wireOp",EDGE,"E3438"),sQuery(id+"F0.wireOp",EDGE,"E3439"),sQuery(id+"F0.wireOp",EDGE,"E3440"),sQuery(id+"F0.wireOp",EDGE,"E3441"),sQuery(id+"F0.wireOp",EDGE,"E3442"),sQuery(id+"F0.wireOp",EDGE,"E3443"),sQuery(id+"F0.wireOp",EDGE,"E3444"),sQuery(id+"F0.wireOp",EDGE,"E3445"),sQuery(id+"F0.wireOp",EDGE,"E3446"),sQuery(id+"F0.wireOp",EDGE,"E3447"),sQuery(id+"F0.wireOp",EDGE,"E3448"),sQuery(id+"F0.wireOp",EDGE,"E3449"),sQuery(id+"F0.wireOp",EDGE,"E3450"),sQuery(id+"F0.wireOp",EDGE,"E3451"),sQuery(id+"F0.wireOp",EDGE,"E3452"),sQuery(id+"F0.wireOp",EDGE,"E3453"),sQuery(id+"F0.wireOp",EDGE,"E3454"),sQuery(id+"F0.wireOp",EDGE,"E3455"),sQuery(id+"F0.wireOp",EDGE,"E3456"),sQuery(id+"F0.wireOp",EDGE,"E3457"),sQuery(id+"F0.wireOp",EDGE,"E3458"),sQuery(id+"F0.wireOp",EDGE,"E3459"),sQuery(id+"F0.wireOp",EDGE,"E3460"),sQuery(id+"F0.wireOp",EDGE,"E3461"),sQuery(id+"F0.wireOp",EDGE,"E3462"),sQuery(id+"F0.wireOp",EDGE,"E3463"),sQuery(id+"F0.wireOp",EDGE,"E3464"),sQuery(id+"F0.wireOp",EDGE,"E3465"),sQuery(id+"F0.wireOp",EDGE,"E3466"),sQuery(id+"F0.wireOp",EDGE,"E3467"),sQuery(id+"F0.wireOp",EDGE,"E3468"),sQuery(id+"F0.wireOp",EDGE,"E3469"),sQuery(id+"F0.wireOp",EDGE,"E3470"),sQuery(id+"F0.wireOp",EDGE,"E3471"),sQuery(id+"F0.wireOp",EDGE,"E3472"),sQuery(id+"F0.wireOp",EDGE,"E3473"),sQuery(id+"F0.wireOp",EDGE,"E3474"),sQuery(id+"F0.wireOp",EDGE,"E3475"),sQuery(id+"F0.wireOp",EDGE,"E3476"),sQuery(id+"F0.wireOp",EDGE,"E3477"),sQuery(id+"F0.wireOp",EDGE,"E3478"),sQuery(id+"F0.wireOp",EDGE,"E3479"),sQuery(id+"F0.wireOp",EDGE,"E3480"),sQuery(id+"F0.wireOp",EDGE,"E3481"),sQuery(id+"F0.wireOp",EDGE,"E3482"),sQuery(id+"F0.wireOp",EDGE,"E3483"),sQuery(id+"F0.wireOp",EDGE,"E3484"),sQuery(id+"F0.wireOp",EDGE,"E3485"),sQuery(id+"F0.wireOp",EDGE,"E3486"),sQuery(id+"F0.wireOp",EDGE,"E3487"),sQuery(id+"F0.wireOp",EDGE,"E3488"),sQuery(id+"F0.wireOp",EDGE,"E3489"),sQuery(id+"F0.wireOp",EDGE,"E3490"),sQuery(id+"F0.wireOp",EDGE,"E3491"),sQuery(id+"F0.wireOp",EDGE,"E3492"),sQuery(id+"F0.wireOp",EDGE,"E3493"),sQuery(id+"F0.wireOp",EDGE,"E3494"),sQuery(id+"F0.wireOp",EDGE,"E3495"),sQuery(id+"F0.wireOp",EDGE,"E3496"),sQuery(id+"F0.wireOp",EDGE,"E3497"),sQuery(id+"F0.wireOp",EDGE,"E3498"),sQuery(id+"F0.wireOp",EDGE,"E3499"),sQuery(id+"F0.wireOp",EDGE,"E3500"),sQuery(id+"F0.wireOp",EDGE,"E3501"),sQuery(id+"F0.wireOp",EDGE,"E3502"),sQuery(id+"F0.wireOp",EDGE,"E3503"),sQuery(id+"F0.wireOp",EDGE,"E3504"),sQuery(id+"F0.wireOp",EDGE,"E3505"),sQuery(id+"F0.wireOp",EDGE,"E3506"),sQuery(id+"F0.wireOp",EDGE,"E3507"),sQuery(id+"F0.wireOp",EDGE,"E3508"),sQuery(id+"F0.wireOp",EDGE,"E3509"),sQuery(id+"F0.wireOp",EDGE,"E3510"),sQuery(id+"F0.wireOp",EDGE,"E3511"),sQuery(id+"F0.wireOp",EDGE,"E3512"),sQuery(id+"F0.wireOp",EDGE,"E3513"),sQuery(id+"F0.wireOp",EDGE,"E3514"),sQuery(id+"F0.wireOp",EDGE,"E3515"),sQuery(id+"F0.wireOp",EDGE,"E3516"),sQuery(id+"F0.wireOp",EDGE,"E3517"),sQuery(id+"F0.wireOp",EDGE,"E3518"),sQuery(id+"F0.wireOp",EDGE,"E3519"),sQuery(id+"F0.wireOp",EDGE,"E3520"),sQuery(id+"F0.wireOp",EDGE,"E3521"),sQuery(id+"F0.wireOp",EDGE,"E3522"),sQuery(id+"F0.wireOp",EDGE,"E3523"),sQuery(id+"F0.wireOp",EDGE,"E3524"),sQuery(id+"F0.wireOp",EDGE,"E3525"),sQuery(id+"F0.wireOp",EDGE,"E3526"),sQuery(id+"F0.wireOp",EDGE,"E3527"),sQuery(id+"F0.wireOp",EDGE,"E3528"),sQuery(id+"F0.wireOp",EDGE,"E3529"),sQuery(id+"F0.wireOp",EDGE,"E3530"),sQuery(id+"F0.wireOp",EDGE,"E3531"),sQuery(id+"F0.wireOp",EDGE,"E3532"),sQuery(id+"F0.wireOp",EDGE,"E3533"),sQuery(id+"F0.wireOp",EDGE,"E3534"),sQuery(id+"F0.wireOp",EDGE,"E3535"),sQuery(id+"F0.wireOp",EDGE,"E3536"),sQuery(id+"F0.wireOp",EDGE,"E3537"),sQuery(id+"F0.wireOp",EDGE,"E3538"),sQuery(id+"F0.wireOp",EDGE,"E3539"),sQuery(id+"F0.wireOp",EDGE,"E3540"),sQuery(id+"F0.wireOp",EDGE,"E3541"),sQuery(id+"F0.wireOp",EDGE,"E3542"),sQuery(id+"F0.wireOp",EDGE,"E3543"),sQuery(id+"F0.wireOp",EDGE,"E3544"),sQuery(id+"F0.wireOp",EDGE,"E3545"),sQuery(id+"F0.wireOp",EDGE,"E3546"),sQuery(id+"F0.wireOp",EDGE,"E3547"),sQuery(id+"F0.wireOp",EDGE,"E3548"),sQuery(id+"F0.wireOp",EDGE,"E3549"),sQuery(id+"F0.wireOp",EDGE,"E3550"),sQuery(id+"F0.wireOp",EDGE,"E3551"),sQuery(id+"F0.wireOp",EDGE,"E3552"),sQuery(id+"F0.wireOp",EDGE,"E3553"),sQuery(id+"F0.wireOp",EDGE,"E3554"),sQuery(id+"F0.wireOp",EDGE,"E3555"),sQuery(id+"F0.wireOp",EDGE,"E3556"),sQuery(id+"F0.wireOp",EDGE,"E3557"),sQuery(id+"F0.wireOp",EDGE,"E3558"),sQuery(id+"F0.wireOp",EDGE,"E3559"),sQuery(id+"F0.wireOp",EDGE,"E3560"),sQuery(id+"F0.wireOp",EDGE,"E3561"),sQuery(id+"F0.wireOp",EDGE,"E3562"),sQuery(id+"F0.wireOp",EDGE,"E3563"),sQuery(id+"F0.wireOp",EDGE,"E3564"),sQuery(id+"F0.wireOp",EDGE,"E3565"),sQuery(id+"F0.wireOp",EDGE,"E3566"),sQuery(id+"F0.wireOp",EDGE,"E3567"),sQuery(id+"F0.wireOp",EDGE,"E3568"),sQuery(id+"F0.wireOp",EDGE,"E3569"),sQuery(id+"F0.wireOp",EDGE,"E3570"),sQuery(id+"F0.wireOp",EDGE,"E3571"),sQuery(id+"F0.wireOp",EDGE,"E3572"),sQuery(id+"F0.wireOp",EDGE,"E3573"),sQuery(id+"F0.wireOp",EDGE,"E3574"),sQuery(id+"F0.wireOp",EDGE,"E3575"),sQuery(id+"F0.wireOp",EDGE,"E3576"),sQuery(id+"F0.wireOp",EDGE,"E3577"),sQuery(id+"F0.wireOp",EDGE,"E3578"),sQuery(id+"F0.wireOp",EDGE,"E3579"),sQuery(id+"F0.wireOp",EDGE,"E3580"),sQuery(id+"F0.wireOp",EDGE,"E3581"),sQuery(id+"F0.wireOp",EDGE,"E3582"),sQuery(id+"F0.wireOp",EDGE,"E3583"),sQuery(id+"F0.wireOp",EDGE,"E3584"),sQuery(id+"F0.wireOp",EDGE,"E3585"),sQuery(id+"F0.wireOp",EDGE,"E3586"),sQuery(id+"F0.wireOp",EDGE,"E3587"),sQuery(id+"F0.wireOp",EDGE,"E3588"),sQuery(id+"F0.wireOp",EDGE,"E3589"),sQuery(id+"F0.wireOp",EDGE,"E3590"),sQuery(id+"F0.wireOp",EDGE,"E3591"),sQuery(id+"F0.wireOp",EDGE,"E3592"),sQuery(id+"F0.wireOp",EDGE,"E3593"),sQuery(id+"F0.wireOp",EDGE,"E3594"),sQuery(id+"F0.wireOp",EDGE,"E3595"),sQuery(id+"F0.wireOp",EDGE,"E3596"),sQuery(id+"F0.wireOp",EDGE,"E3597"),sQuery(id+"F0.wireOp",EDGE,"E3598"),sQuery(id+"F0.wireOp",EDGE,"E3599"),sQuery(id+"F0.wireOp",EDGE,"E3600"),sQuery(id+"F0.wireOp",EDGE,"E3601"),sQuery(id+"F0.wireOp",EDGE,"E3602"),sQuery(id+"F0.wireOp",EDGE,"E3603"),sQuery(id+"F0.wireOp",EDGE,"E3604"),sQuery(id+"F0.wireOp",EDGE,"E3605"),sQuery(id+"F0.wireOp",EDGE,"E3606"),sQuery(id+"F0.wireOp",EDGE,"E3607"),sQuery(id+"F0.wireOp",EDGE,"E3608"),sQuery(id+"F0.wireOp",EDGE,"E3609"),sQuery(id+"F0.wireOp",EDGE,"E3610"),sQuery(id+"F0.wireOp",EDGE,"E3611"),sQuery(id+"F0.wireOp",EDGE,"E3612"),sQuery(id+"F0.wireOp",EDGE,"E3613"),sQuery(id+"F0.wireOp",EDGE,"E3614"),sQuery(id+"F0.wireOp",EDGE,"E3615"),sQuery(id+"F0.wireOp",EDGE,"E3616"),sQuery(id+"F0.wireOp",EDGE,"E3617"),sQuery(id+"F0.wireOp",EDGE,"E3618"),sQuery(id+"F0.wireOp",EDGE,"E3619"),sQuery(id+"F0.wireOp",EDGE,"E3620"),sQuery(id+"F0.wireOp",EDGE,"E3621"),sQuery(id+"F0.wireOp",EDGE,"E3622"),sQuery(id+"F0.wireOp",EDGE,"E3623"),sQuery(id+"F0.wireOp",EDGE,"E3624"),sQuery(id+"F0.wireOp",EDGE,"E3625"),sQuery(id+"F0.wireOp",EDGE,"E3626"),sQuery(id+"F0.wireOp",EDGE,"E3627"),sQuery(id+"F0.wireOp",EDGE,"E3628"),sQuery(id+"F0.wireOp",EDGE,"E3629"),sQuery(id+"F0.wireOp",EDGE,"E3630"),sQuery(id+"F0.wireOp",EDGE,"E3631"),sQuery(id+"F0.wireOp",EDGE,"E3632"),sQuery(id+"F0.wireOp",EDGE,"E3633"),sQuery(id+"F0.wireOp",EDGE,"E3634"),sQuery(id+"F0.wireOp",EDGE,"E3635"),sQuery(id+"F0.wireOp",EDGE,"E3636"),sQuery(id+"F0.wireOp",EDGE,"E3637"),sQuery(id+"F0.wireOp",EDGE,"E3638"),sQuery(id+"F0.wireOp",EDGE,"E3639"),sQuery(id+"F0.wireOp",EDGE,"E3640"),sQuery(id+"F0.wireOp",EDGE,"E3641"),sQuery(id+"F0.wireOp",EDGE,"E3642"),sQuery(id+"F0.wireOp",EDGE,"E3643"),sQuery(id+"F0.wireOp",EDGE,"E3644"),sQuery(id+"F0.wireOp",EDGE,"E3645"),sQuery(id+"F0.wireOp",EDGE,"E3646"),sQuery(id+"F0.wireOp",EDGE,"E3647"),sQuery(id+"F0.wireOp",EDGE,"E3648"),sQuery(id+"F0.wireOp",EDGE,"E3649"),sQuery(id+"F0.wireOp",EDGE,"E3650"),sQuery(id+"F0.wireOp",EDGE,"E3651"),sQuery(id+"F0.wireOp",EDGE,"E3652"),sQuery(id+"F0.wireOp",EDGE,"E3653"),sQuery(id+"F0.wireOp",EDGE,"E3654"),sQuery(id+"F0.wireOp",EDGE,"E3655"),sQuery(id+"F0.wireOp",EDGE,"E3656"),sQuery(id+"F0.wireOp",EDGE,"E3657"),sQuery(id+"F0.wireOp",EDGE,"E3658"),sQuery(id+"F0.wireOp",EDGE,"E3659"),sQuery(id+"F0.wireOp",EDGE,"E3660"),sQuery(id+"F0.wireOp",EDGE,"E3661"),sQuery(id+"F0.wireOp",EDGE,"E3662"),sQuery(id+"F0.wireOp",EDGE,"E3663"),sQuery(id+"F0.wireOp",EDGE,"E3664"),sQuery(id+"F0.wireOp",EDGE,"E3665"),sQuery(id+"F0.wireOp",EDGE,"E3666"),sQuery(id+"F0.wireOp",EDGE,"E3667"),sQuery(id+"F0.wireOp",EDGE,"E3668"),sQuery(id+"F0.wireOp",EDGE,"E3669"),sQuery(id+"F0.wireOp",EDGE,"E3670"),sQuery(id+"F0.wireOp",EDGE,"E3671"),sQuery(id+"F0.wireOp",EDGE,"E3672"),sQuery(id+"F0.wireOp",EDGE,"E3673"),sQuery(id+"F0.wireOp",EDGE,"E3674"),sQuery(id+"F0.wireOp",EDGE,"E3675"),sQuery(id+"F0.wireOp",EDGE,"E3676"),sQuery(id+"F0.wireOp",EDGE,"E3677"),sQuery(id+"F0.wireOp",EDGE,"E3678"),sQuery(id+"F0.wireOp",EDGE,"E3679"),sQuery(id+"F0.wireOp",EDGE,"E3680"),sQuery(id+"F0.wireOp",EDGE,"E3681"),sQuery(id+"F0.wireOp",EDGE,"E3682"),sQuery(id+"F0.wireOp",EDGE,"E3683"),sQuery(id+"F0.wireOp",EDGE,"E3684"),sQuery(id+"F0.wireOp",EDGE,"E3685"),sQuery(id+"F0.wireOp",EDGE,"E3686"),sQuery(id+"F0.wireOp",EDGE,"E3687"),sQuery(id+"F0.wireOp",EDGE,"E3688"),sQuery(id+"F0.wireOp",EDGE,"E3689"),sQuery(id+"F0.wireOp",EDGE,"E3690"),sQuery(id+"F0.wireOp",EDGE,"E3691"),sQuery(id+"F0.wireOp",EDGE,"E3692"),sQuery(id+"F0.wireOp",EDGE,"E3693"),sQuery(id+"F0.wireOp",EDGE,"E3694"),sQuery(id+"F0.wireOp",EDGE,"E3695"),sQuery(id+"F0.wireOp",EDGE,"E3696"),sQuery(id+"F0.wireOp",EDGE,"E3697"),sQuery(id+"F0.wireOp",EDGE,"E3698"),sQuery(id+"F0.wireOp",EDGE,"E3699"),sQuery(id+"F0.wireOp",EDGE,"E3700"),sQuery(id+"F0.wireOp",EDGE,"E3701"),sQuery(id+"F0.wireOp",EDGE,"E3702"),sQuery(id+"F0.wireOp",EDGE,"E3703"),sQuery(id+"F0.wireOp",EDGE,"E3704"),sQuery(id+"F0.wireOp",EDGE,"E3705"),sQuery(id+"F0.wireOp",EDGE,"E3706"),sQuery(id+"F0.wireOp",EDGE,"E3707"),sQuery(id+"F0.wireOp",EDGE,"E3708"),sQuery(id+"F0.wireOp",EDGE,"E3709"),sQuery(id+"F0.wireOp",EDGE,"E3710"),sQuery(id+"F0.wireOp",EDGE,"E3711"),sQuery(id+"F0.wireOp",EDGE,"E3712"),sQuery(id+"F0.wireOp",EDGE,"E3713"),sQuery(id+"F0.wireOp",EDGE,"E3714"),sQuery(id+"F0.wireOp",EDGE,"E3715"),sQuery(id+"F0.wireOp",EDGE,"E3716"),sQuery(id+"F0.wireOp",EDGE,"E3717"),sQuery(id+"F0.wireOp",EDGE,"E3718"),sQuery(id+"F0.wireOp",EDGE,"E3719"),sQuery(id+"F0.wireOp",EDGE,"E3720"),sQuery(id+"F0.wireOp",EDGE,"E3721"),sQuery(id+"F0.wireOp",EDGE,"E3722"),sQuery(id+"F0.wireOp",EDGE,"E3723"),sQuery(id+"F0.wireOp",EDGE,"E3724"),sQuery(id+"F0.wireOp",EDGE,"E3725"),sQuery(id+"F0.wireOp",EDGE,"E3726"),sQuery(id+"F0.wireOp",EDGE,"E3727"),sQuery(id+"F0.wireOp",EDGE,"E3728"),sQuery(id+"F0.wireOp",EDGE,"E3729"),sQuery(id+"F0.wireOp",EDGE,"E3730"),sQuery(id+"F0.wireOp",EDGE,"E3731"),sQuery(id+"F0.wireOp",EDGE,"E3732"),sQuery(id+"F0.wireOp",EDGE,"E3733"),sQuery(id+"F0.wireOp",EDGE,"E3734"),sQuery(id+"F0.wireOp",EDGE,"E3735"),sQuery(id+"F0.wireOp",EDGE,"E3736"),sQuery(id+"F0.wireOp",EDGE,"E3737"),sQuery(id+"F0.wireOp",EDGE,"E3738"),sQuery(id+"F0.wireOp",EDGE,"E3739"),sQuery(id+"F0.wireOp",EDGE,"E3740"),sQuery(id+"F0.wireOp",EDGE,"E3741"),sQuery(id+"F0.wireOp",EDGE,"E3742"),sQuery(id+"F0.wireOp",EDGE,"E3743"),sQuery(id+"F0.wireOp",EDGE,"E3744"),sQuery(id+"F0.wireOp",EDGE,"E3745"),sQuery(id+"F0.wireOp",EDGE,"E3746"),sQuery(id+"F0.wireOp",EDGE,"E3747"),sQuery(id+"F0.wireOp",EDGE,"E3748"),sQuery(id+"F0.wireOp",EDGE,"E3749"),sQuery(id+"F0.wireOp",EDGE,"E3750"),sQuery(id+"F0.wireOp",EDGE,"E3751"),sQuery(id+"F0.wireOp",EDGE,"E3752"),sQuery(id+"F0.wireOp",EDGE,"E3753"),sQuery(id+"F0.wireOp",EDGE,"E3754"),sQuery(id+"F0.wireOp",EDGE,"E3755"),sQuery(id+"F0.wireOp",EDGE,"E3756"),sQuery(id+"F0.wireOp",EDGE,"E3757"),sQuery(id+"F0.wireOp",EDGE,"E3758"),sQuery(id+"F0.wireOp",EDGE,"E3759"),sQuery(id+"F0.wireOp",EDGE,"E3760"),sQuery(id+"F0.wireOp",EDGE,"E3761"),sQuery(id+"F0.wireOp",EDGE,"E3762"),sQuery(id+"F0.wireOp",EDGE,"E3763"),sQuery(id+"F0.wireOp",EDGE,"E3764"),sQuery(id+"F0.wireOp",EDGE,"E3765"),sQuery(id+"F0.wireOp",EDGE,"E3766"),sQuery(id+"F0.wireOp",EDGE,"E3767"),sQuery(id+"F0.wireOp",EDGE,"E3768"),sQuery(id+"F0.wireOp",EDGE,"E3769"),sQuery(id+"F0.wireOp",EDGE,"E3770"),sQuery(id+"F0.wireOp",EDGE,"E3771"),sQuery(id+"F0.wireOp",EDGE,"E3772"),sQuery(id+"F0.wireOp",EDGE,"E3773"),sQuery(id+"F0.wireOp",EDGE,"E3774"),sQuery(id+"F0.wireOp",EDGE,"E3775"),sQuery(id+"F0.wireOp",EDGE,"E3776"),sQuery(id+"F0.wireOp",EDGE,"E3777"),sQuery(id+"F0.wireOp",EDGE,"E3778"),sQuery(id+"F0.wireOp",EDGE,"E3779"),sQuery(id+"F0.wireOp",EDGE,"E3780"),sQuery(id+"F0.wireOp",EDGE,"E3781"),sQuery(id+"F0.wireOp",EDGE,"E3782"),sQuery(id+"F0.wireOp",EDGE,"E3783"),sQuery(id+"F0.wireOp",EDGE,"E3784"),sQuery(id+"F0.wireOp",EDGE,"E3785"),sQuery(id+"F0.wireOp",EDGE,"E3786"),sQuery(id+"F0.wireOp",EDGE,"E3787"),sQuery(id+"F0.wireOp",EDGE,"E3788"),sQuery(id+"F0.wireOp",EDGE,"E3789"),sQuery(id+"F0.wireOp",EDGE,"E3790"),sQuery(id+"F0.wireOp",EDGE,"E3791"),sQuery(id+"F0.wireOp",EDGE,"E3792"),sQuery(id+"F0.wireOp",EDGE,"E3793"),sQuery(id+"F0.wireOp",EDGE,"E3794"),sQuery(id+"F0.wireOp",EDGE,"E3795"),sQuery(id+"F0.wireOp",EDGE,"E3796"),sQuery(id+"F0.wireOp",EDGE,"E3797"),sQuery(id+"F0.wireOp",EDGE,"E3798"),sQuery(id+"F0.wireOp",EDGE,"E3799"),sQuery(id+"F0.wireOp",EDGE,"E3800"),sQuery(id+"F0.wireOp",EDGE,"E3801"),sQuery(id+"F0.wireOp",EDGE,"E3802"),sQuery(id+"F0.wireOp",EDGE,"E3803"),sQuery(id+"F0.wireOp",EDGE,"E3804"),sQuery(id+"F0.wireOp",EDGE,"E3805"),sQuery(id+"F0.wireOp",EDGE,"E3806"),sQuery(id+"F0.wireOp",EDGE,"E3807"),sQuery(id+"F0.wireOp",EDGE,"E3808"),sQuery(id+"F0.wireOp",EDGE,"E3809"),sQuery(id+"F0.wireOp",EDGE,"E3810"),sQuery(id+"F0.wireOp",EDGE,"E3811"),sQuery(id+"F0.wireOp",EDGE,"E3812"),sQuery(id+"F0.wireOp",EDGE,"E3813"),sQuery(id+"F0.wireOp",EDGE,"E3814"),sQuery(id+"F0.wireOp",EDGE,"E3815"),sQuery(id+"F0.wireOp",EDGE,"E3816"),sQuery(id+"F0.wireOp",EDGE,"E3817"),sQuery(id+"F0.wireOp",EDGE,"E3818"),sQuery(id+"F0.wireOp",EDGE,"E3819"),sQuery(id+"F0.wireOp",EDGE,"E3820"),sQuery(id+"F0.wireOp",EDGE,"E3821"),sQuery(id+"F0.wireOp",EDGE,"E3822"),sQuery(id+"F0.wireOp",EDGE,"E3823"),sQuery(id+"F0.wireOp",EDGE,"E3824"),sQuery(id+"F0.wireOp",EDGE,"E3825"),sQuery(id+"F0.wireOp",EDGE,"E3826"),sQuery(id+"F0.wireOp",EDGE,"E3827"),sQuery(id+"F0.wireOp",EDGE,"E3828"),sQuery(id+"F0.wireOp",EDGE,"E3829"),sQuery(id+"F0.wireOp",EDGE,"E3830"),sQuery(id+"F0.wireOp",EDGE,"E3831"),sQuery(id+"F0.wireOp",EDGE,"E3832"),sQuery(id+"F0.wireOp",EDGE,"E3833"),sQuery(id+"F0.wireOp",EDGE,"E3834"),sQuery(id+"F0.wireOp",EDGE,"E3835"),sQuery(id+"F0.wireOp",EDGE,"E3836"),sQuery(id+"F0.wireOp",EDGE,"E3837"),sQuery(id+"F0.wireOp",EDGE,"E3838"),sQuery(id+"F0.wireOp",EDGE,"E3839"),sQuery(id+"F0.wireOp",EDGE,"E3840"),sQuery(id+"F0.wireOp",EDGE,"E3841"),sQuery(id+"F0.wireOp",EDGE,"E3842"),sQuery(id+"F0.wireOp",EDGE,"E3843"),sQuery(id+"F0.wireOp",EDGE,"E3844"),sQuery(id+"F0.wireOp",EDGE,"E3845"),sQuery(id+"F0.wireOp",EDGE,"E3846"),sQuery(id+"F0.wireOp",EDGE,"E3847"),sQuery(id+"F0.wireOp",EDGE,"E3848"),sQuery(id+"F0.wireOp",EDGE,"E3849"),sQuery(id+"F0.wireOp",EDGE,"E3850"),sQuery(id+"F0.wireOp",EDGE,"E3851"),sQuery(id+"F0.wireOp",EDGE,"E3852"),sQuery(id+"F0.wireOp",EDGE,"E3853"),sQuery(id+"F0.wireOp",EDGE,"E3854"),sQuery(id+"F0.wireOp",EDGE,"E3855"),sQuery(id+"F0.wireOp",EDGE,"E3856"),sQuery(id+"F0.wireOp",EDGE,"E3857"),sQuery(id+"F0.wireOp",EDGE,"E3858"),sQuery(id+"F0.wireOp",EDGE,"E3859"),sQuery(id+"F0.wireOp",EDGE,"E3860"),sQuery(id+"F0.wireOp",EDGE,"E3861"),sQuery(id+"F0.wireOp",EDGE,"E3862"),sQuery(id+"F0.wireOp",EDGE,"E3863"),sQuery(id+"F0.wireOp",EDGE,"E3864"),sQuery(id+"F0.wireOp",EDGE,"E3865"),sQuery(id+"F0.wireOp",EDGE,"E3866"),sQuery(id+"F0.wireOp",EDGE,"E3867"),sQuery(id+"F0.wireOp",EDGE,"E3868"),sQuery(id+"F0.wireOp",EDGE,"E3869"),sQuery(id+"F0.wireOp",EDGE,"E3870"),sQuery(id+"F0.wireOp",EDGE,"E3871"),sQuery(id+"F0.wireOp",EDGE,"E3872"),sQuery(id+"F0.wireOp",EDGE,"E3873"),sQuery(id+"F0.wireOp",EDGE,"E3874"),sQuery(id+"F0.wireOp",EDGE,"E3875"),sQuery(id+"F0.wireOp",EDGE,"E3876"),sQuery(id+"F0.wireOp",EDGE,"E3877"),sQuery(id+"F0.wireOp",EDGE,"E3878"),sQuery(id+"F0.wireOp",EDGE,"E3879"),sQuery(id+"F0.wireOp",EDGE,"E3880"),sQuery(id+"F0.wireOp",EDGE,"E3881"),sQuery(id+"F0.wireOp",EDGE,"E3882"),sQuery(id+"F0.wireOp",EDGE,"E3883"),sQuery(id+"F0.wireOp",EDGE,"E3884"),sQuery(id+"F0.wireOp",EDGE,"E3885"),sQuery(id+"F0.wireOp",EDGE,"E3886"),sQuery(id+"F0.wireOp",EDGE,"E3887"),sQuery(id+"F0.wireOp",EDGE,"E3888"),sQuery(id+"F0.wireOp",EDGE,"E3889"),sQuery(id+"F0.wireOp",EDGE,"E3890"),sQuery(id+"F0.wireOp",EDGE,"E3891"),sQuery(id+"F0.wireOp",EDGE,"E3892"),sQuery(id+"F0.wireOp",EDGE,"E3893"),sQuery(id+"F0.wireOp",EDGE,"E3894"),sQuery(id+"F0.wireOp",EDGE,"E3895"),sQuery(id+"F0.wireOp",EDGE,"E3896"),sQuery(id+"F0.wireOp",EDGE,"E3897"),sQuery(id+"F0.wireOp",EDGE,"E3898"),sQuery(id+"F0.wireOp",EDGE,"E3899"),sQuery(id+"F0.wireOp",EDGE,"E3900"),sQuery(id+"F0.wireOp",EDGE,"E3901"),sQuery(id+"F0.wireOp",EDGE,"E3902"),sQuery(id+"F0.wireOp",EDGE,"E3903"),sQuery(id+"F0.wireOp",EDGE,"E3904"),sQuery(id+"F0.wireOp",EDGE,"E3905"),sQuery(id+"F0.wireOp",EDGE,"E3906"),sQuery(id+"F0.wireOp",EDGE,"E3907"),sQuery(id+"F0.wireOp",EDGE,"E3908"),sQuery(id+"F0.wireOp",EDGE,"E3909"),sQuery(id+"F0.wireOp",EDGE,"E3910"),sQuery(id+"F0.wireOp",EDGE,"E3911"),sQuery(id+"F0.wireOp",EDGE,"E3912"),sQuery(id+"F0.wireOp",EDGE,"E3913"),sQuery(id+"F0.wireOp",EDGE,"E3914"),sQuery(id+"F0.wireOp",EDGE,"E3915"),sQuery(id+"F0.wireOp",EDGE,"E3916"),sQuery(id+"F0.wireOp",EDGE,"E3917"),sQuery(id+"F0.wireOp",EDGE,"E3918"),sQuery(id+"F0.wireOp",EDGE,"E3919"),sQuery(id+"F0.wireOp",EDGE,"E3920"),sQuery(id+"F0.wireOp",EDGE,"E3921"),sQuery(id+"F0.wireOp",EDGE,"E3922"),sQuery(id+"F0.wireOp",EDGE,"E3923"),sQuery(id+"F0.wireOp",EDGE,"E3924"),sQuery(id+"F0.wireOp",EDGE,"E3925"),sQuery(id+"F0.wireOp",EDGE,"E3926"),sQuery(id+"F0.wireOp",EDGE,"E3927"),sQuery(id+"F0.wireOp",EDGE,"E3928"),sQuery(id+"F0.wireOp",EDGE,"E3929"),sQuery(id+"F0.wireOp",EDGE,"E3930"),sQuery(id+"F0.wireOp",EDGE,"E3931"),sQuery(id+"F0.wireOp",EDGE,"E3932"),sQuery(id+"F0.wireOp",EDGE,"E3933"),sQuery(id+"F0.wireOp",EDGE,"E3934"),sQuery(id+"F0.wireOp",EDGE,"E3935"),sQuery(id+"F0.wireOp",EDGE,"E3936"),sQuery(id+"F0.wireOp",EDGE,"E3937"),sQuery(id+"F0.wireOp",EDGE,"E3938"),sQuery(id+"F0.wireOp",EDGE,"E3939"),sQuery(id+"F0.wireOp",EDGE,"E3940"),sQuery(id+"F0.wireOp",EDGE,"E3941"),sQuery(id+"F0.wireOp",EDGE,"E3942"),sQuery(id+"F0.wireOp",EDGE,"E3943"),sQuery(id+"F0.wireOp",EDGE,"E3944"),sQuery(id+"F0.wireOp",EDGE,"E3945"),sQuery(id+"F0.wireOp",EDGE,"E3946"),sQuery(id+"F0.wireOp",EDGE,"E3947"),sQuery(id+"F0.wireOp",EDGE,"E3948"),sQuery(id+"F0.wireOp",EDGE,"E3949"),sQuery(id+"F0.wireOp",EDGE,"E3950"),sQuery(id+"F0.wireOp",EDGE,"E3951"),sQuery(id+"F0.wireOp",EDGE,"E3952"),sQuery(id+"F0.wireOp",EDGE,"E3953"),sQuery(id+"F0.wireOp",EDGE,"E3954"),sQuery(id+"F0.wireOp",EDGE,"E3955"),sQuery(id+"F0.wireOp",EDGE,"E3956"),sQuery(id+"F0.wireOp",EDGE,"E3957"),sQuery(id+"F0.wireOp",EDGE,"E3958"),sQuery(id+"F0.wireOp",EDGE,"E3959"),sQuery(id+"F0.wireOp",EDGE,"E3960"),sQuery(id+"F0.wireOp",EDGE,"E3961"),sQuery(id+"F0.wireOp",EDGE,"E3962"),sQuery(id+"F0.wireOp",EDGE,"E3963"),sQuery(id+"F0.wireOp",EDGE,"E3964"),sQuery(id+"F0.wireOp",EDGE,"E3965"),sQuery(id+"F0.wireOp",EDGE,"E3966"),sQuery(id+"F0.wireOp",EDGE,"E3967"),sQuery(id+"F0.wireOp",EDGE,"E3968"),sQuery(id+"F0.wireOp",EDGE,"E3969"),sQuery(id+"F0.wireOp",EDGE,"E3970"),sQuery(id+"F0.wireOp",EDGE,"E3971"),sQuery(id+"F0.wireOp",EDGE,"E3972"),sQuery(id+"F0.wireOp",EDGE,"E3973"),sQuery(id+"F0.wireOp",EDGE,"E3974"),sQuery(id+"F0.wireOp",EDGE,"E3975"),sQuery(id+"F0.wireOp",EDGE,"E3976"),sQuery(id+"F0.wireOp",EDGE,"E3977"),sQuery(id+"F0.wireOp",EDGE,"E3978"),sQuery(id+"F0.wireOp",EDGE,"E3979"),sQuery(id+"F0.wireOp",EDGE,"E3980"),sQuery(id+"F0.wireOp",EDGE,"E3981"),sQuery(id+"F0.wireOp",EDGE,"E3982"),sQuery(id+"F0.wireOp",EDGE,"E3983"),sQuery(id+"F0.wireOp",EDGE,"E3984"),sQuery(id+"F0.wireOp",EDGE,"E3985"),sQuery(id+"F0.wireOp",EDGE,"E3986"),sQuery(id+"F0.wireOp",EDGE,"E3987"),sQuery(id+"F0.wireOp",EDGE,"E3988"),sQuery(id+"F0.wireOp",EDGE,"E3989"),sQuery(id+"F0.wireOp",EDGE,"E3990"),sQuery(id+"F0.wireOp",EDGE,"E3991"),sQuery(id+"F0.wireOp",EDGE,"E3992"),sQuery(id+"F0.wireOp",EDGE,"E3993"),sQuery(id+"F0.wireOp",EDGE,"E3994"),sQuery(id+"F0.wireOp",EDGE,"E3995"),sQuery(id+"F0.wireOp",EDGE,"E3996"),sQuery(id+"F0.wireOp",EDGE,"E3997"),sQuery(id+"F0.wireOp",EDGE,"E3998"),sQuery(id+"F0.wireOp",EDGE,"E3999"),sQuery(id+"F0.wireOp",EDGE,"E4000"),sQuery(id+"F0.wireOp",EDGE,"E4001"),sQuery(id+"F0.wireOp",EDGE,"E4002"),sQuery(id+"F0.wireOp",EDGE,"E4003"),sQuery(id+"F0.wireOp",EDGE,"E4004"),sQuery(id+"F0.wireOp",EDGE,"E4005"),sQuery(id+"F0.wireOp",EDGE,"E4006"),sQuery(id+"F0.wireOp",EDGE,"E4007"),sQuery(id+"F0.wireOp",EDGE,"E4008"),sQuery(id+"F0.wireOp",EDGE,"E4009"),sQuery(id+"F0.wireOp",EDGE,"E4010"),sQuery(id+"F0.wireOp",EDGE,"E4011"),sQuery(id+"F0.wireOp",EDGE,"E4012"),sQuery(id+"F0.wireOp",EDGE,"E4013"),sQuery(id+"F0.wireOp",EDGE,"E4014"),sQuery(id+"F0.wireOp",EDGE,"E4015"),sQuery(id+"F0.wireOp",EDGE,"E4016"),sQuery(id+"F0.wireOp",EDGE,"E4017"),sQuery(id+"F0.wireOp",EDGE,"E4018"),sQuery(id+"F0.wireOp",EDGE,"E4019"),sQuery(id+"F0.wireOp",EDGE,"E4020"),sQuery(id+"F0.wireOp",EDGE,"E4021"),sQuery(id+"F0.wireOp",EDGE,"E4022"),sQuery(id+"F0.wireOp",EDGE,"E4023"),sQuery(id+"F0.wireOp",EDGE,"E4024"),sQuery(id+"F0.wireOp",EDGE,"E4025"),sQuery(id+"F0.wireOp",EDGE,"E4026"),sQuery(id+"F0.wireOp",EDGE,"E4027"),sQuery(id+"F0.wireOp",EDGE,"E4028"),sQuery(id+"F0.wireOp",EDGE,"E4029"),sQuery(id+"F0.wireOp",EDGE,"E4030"),sQuery(id+"F0.wireOp",EDGE,"E4031"),sQuery(id+"F0.wireOp",EDGE,"E4032"),sQuery(id+"F0.wireOp",EDGE,"E4033"),sQuery(id+"F0.wireOp",EDGE,"E4034"),sQuery(id+"F0.wireOp",EDGE,"E4035"),sQuery(id+"F0.wireOp",EDGE,"E4036"),sQuery(id+"F0.wireOp",EDGE,"E4037"),sQuery(id+"F0.wireOp",EDGE,"E4038"),sQuery(id+"F0.wireOp",EDGE,"E4039"),sQuery(id+"F0.wireOp",EDGE,"E4040"),sQuery(id+"F0.wireOp",EDGE,"E4041"),sQuery(id+"F0.wireOp",EDGE,"E4042"),sQuery(id+"F0.wireOp",EDGE,"E4043"),sQuery(id+"F0.wireOp",EDGE,"E4044"),sQuery(id+"F0.wireOp",EDGE,"E4045"),sQuery(id+"F0.wireOp",EDGE,"E4046"),sQuery(id+"F0.wireOp",EDGE,"E4047"),sQuery(id+"F0.wireOp",EDGE,"E4048"),sQuery(id+"F0.wireOp",EDGE,"E4049"),sQuery(id+"F0.wireOp",EDGE,"E4050"),sQuery(id+"F0.wireOp",EDGE,"E4051"),sQuery(id+"F0.wireOp",EDGE,"E4052"),sQuery(id+"F0.wireOp",EDGE,"E4053"),sQuery(id+"F0.wireOp",EDGE,"E4054"),sQuery(id+"F0.wireOp",EDGE,"E4055"),sQuery(id+"F0.wireOp",EDGE,"E4056"),sQuery(id+"F0.wireOp",EDGE,"E4057"),sQuery(id+"F0.wireOp",EDGE,"E4058"),sQuery(id+"F0.wireOp",EDGE,"E4059"),sQuery(id+"F0.wireOp",EDGE,"E4060"),sQuery(id+"F0.wireOp",EDGE,"E4061"),sQuery(id+"F0.wireOp",EDGE,"E4062"),sQuery(id+"F0.wireOp",EDGE,"E4063"),sQuery(id+"F0.wireOp",EDGE,"E4064"),sQuery(id+"F0.wireOp",EDGE,"E4065"),sQuery(id+"F0.wireOp",EDGE,"E4066"),sQuery(id+"F0.wireOp",EDGE,"E4067"),sQuery(id+"F0.wireOp",EDGE,"E4068"),sQuery(id+"F0.wireOp",EDGE,"E4069"),sQuery(id+"F0.wireOp",EDGE,"E4070"),sQuery(id+"F0.wireOp",EDGE,"E4071"),sQuery(id+"F0.wireOp",EDGE,"E4072"),sQuery(id+"F0.wireOp",EDGE,"E4073"),sQuery(id+"F0.wireOp",EDGE,"E4074"),sQuery(id+"F0.wireOp",EDGE,"E4075"),sQuery(id+"F0.wireOp",EDGE,"E4076"),sQuery(id+"F0.wireOp",EDGE,"E4077"),sQuery(id+"F0.wireOp",EDGE,"E4078"),sQuery(id+"F0.wireOp",EDGE,"E4079"),sQuery(id+"F0.wireOp",EDGE,"E4080"),sQuery(id+"F0.wireOp",EDGE,"E4081"),sQuery(id+"F0.wireOp",EDGE,"E4082"),sQuery(id+"F0.wireOp",EDGE,"E4083"),sQuery(id+"F0.wireOp",EDGE,"E4084"),sQuery(id+"F0.wireOp",EDGE,"E4085"),sQuery(id+"F0.wireOp",EDGE,"E4086"),sQuery(id+"F0.wireOp",EDGE,"E4087"),sQuery(id+"F0.wireOp",EDGE,"E4088"),sQuery(id+"F0.wireOp",EDGE,"E4089"),sQuery(id+"F0.wireOp",EDGE,"E4090"),sQuery(id+"F0.wireOp",EDGE,"E4091"),sQuery(id+"F0.wireOp",EDGE,"E4092"),sQuery(id+"F0.wireOp",EDGE,"E4093"),sQuery(id+"F0.wireOp",EDGE,"E4094"),sQuery(id+"F0.wireOp",EDGE,"E4095"),sQuery(id+"F0.wireOp",EDGE,"E4096"),sQuery(id+"F0.wireOp",EDGE,"E4097"),sQuery(id+"F0.wireOp",EDGE,"E4098"),sQuery(id+"F0.wireOp",EDGE,"E4099"),sQuery(id+"F0.wireOp",EDGE,"E4100"),sQuery(id+"F0.wireOp",EDGE,"E4101"),sQuery(id+"F0.wireOp",EDGE,"E4102"),sQuery(id+"F0.wireOp",EDGE,"E4103"),sQuery(id+"F0.wireOp",EDGE,"E4104"),sQuery(id+"F0.wireOp",EDGE,"E4105"),sQuery(id+"F0.wireOp",EDGE,"E4106"),sQuery(id+"F0.wireOp",EDGE,"E4107"),sQuery(id+"F0.wireOp",EDGE,"E4108"),sQuery(id+"F0.wireOp",EDGE,"E4109"),sQuery(id+"F0.wireOp",EDGE,"E4110"),sQuery(id+"F0.wireOp",EDGE,"E4111"),sQuery(id+"F0.wireOp",EDGE,"E4112"),sQuery(id+"F0.wireOp",EDGE,"E4113"),sQuery(id+"F0.wireOp",EDGE,"E4114"),sQuery(id+"F0.wireOp",EDGE,"E4115"),sQuery(id+"F0.wireOp",EDGE,"E4116"),sQuery(id+"F0.wireOp",EDGE,"E4117"),sQuery(id+"F0.wireOp",EDGE,"E4118"),sQuery(id+"F0.wireOp",EDGE,"E4119"),sQuery(id+"F0.wireOp",EDGE,"E4120"),sQuery(id+"F0.wireOp",EDGE,"E4121"),sQuery(id+"F0.wireOp",EDGE,"E4122"),sQuery(id+"F0.wireOp",EDGE,"E4123"),sQuery(id+"F0.wireOp",EDGE,"E4124"),sQuery(id+"F0.wireOp",EDGE,"E4125"),sQuery(id+"F0.wireOp",EDGE,"E4126"),sQuery(id+"F0.wireOp",EDGE,"E4127"),sQuery(id+"F0.wireOp",EDGE,"E4128"),sQuery(id+"F0.wireOp",EDGE,"E4129"),sQuery(id+"F0.wireOp",EDGE,"E4130"),sQuery(id+"F0.wireOp",EDGE,"E4131"),sQuery(id+"F0.wireOp",EDGE,"E4132"),sQuery(id+"F0.wireOp",EDGE,"E4133"),sQuery(id+"F0.wireOp",EDGE,"E4134"),sQuery(id+"F0.wireOp",EDGE,"E4135"),sQuery(id+"F0.wireOp",EDGE,"E4136"),sQuery(id+"F0.wireOp",EDGE,"E4137"),sQuery(id+"F0.wireOp",EDGE,"E4138"),sQuery(id+"F0.wireOp",EDGE,"E4139"),sQuery(id+"F0.wireOp",EDGE,"E4140"),sQuery(id+"F0.wireOp",EDGE,"E4141"),sQuery(id+"F0.wireOp",EDGE,"E4142"),sQuery(id+"F0.wireOp",EDGE,"E4143"),sQuery(id+"F0.wireOp",EDGE,"E4144"),sQuery(id+"F0.wireOp",EDGE,"E4145"),sQuery(id+"F0.wireOp",EDGE,"E4146"),sQuery(id+"F0.wireOp",EDGE,"E4147"),sQuery(id+"F0.wireOp",EDGE,"E4148"),sQuery(id+"F0.wireOp",EDGE,"E4149"),sQuery(id+"F0.wireOp",EDGE,"E4150"),sQuery(id+"F0.wireOp",EDGE,"E4151"),sQuery(id+"F0.wireOp",EDGE,"E4152"),sQuery(id+"F0.wireOp",EDGE,"E4153"),sQuery(id+"F0.wireOp",EDGE,"E4154"),sQuery(id+"F0.wireOp",EDGE,"E4155"),sQuery(id+"F0.wireOp",EDGE,"E4156"),sQuery(id+"F0.wireOp",EDGE,"E4157"),sQuery(id+"F0.wireOp",EDGE,"E4158"),sQuery(id+"F0.wireOp",EDGE,"E4159"),sQuery(id+"F0.wireOp",EDGE,"E4160"),sQuery(id+"F0.wireOp",EDGE,"E4161"),sQuery(id+"F0.wireOp",EDGE,"E4162"),sQuery(id+"F0.wireOp",EDGE,"E4163"),sQuery(id+"F0.wireOp",EDGE,"E4164"),sQuery(id+"F0.wireOp",EDGE,"E4165"),sQuery(id+"F0.wireOp",EDGE,"E4166"),sQuery(id+"F0.wireOp",EDGE,"E4167"),sQuery(id+"F0.wireOp",EDGE,"E4168"),sQuery(id+"F0.wireOp",EDGE,"E4169"),sQuery(id+"F0.wireOp",EDGE,"E4170"),sQuery(id+"F0.wireOp",EDGE,"E4171"),sQuery(id+"F0.wireOp",EDGE,"E4172"),sQuery(id+"F0.wireOp",EDGE,"E4173"),sQuery(id+"F0.wireOp",EDGE,"E4174"),sQuery(id+"F0.wireOp",EDGE,"E4175"),sQuery(id+"F0.wireOp",EDGE,"E4176"),sQuery(id+"F0.wireOp",EDGE,"E4177"),sQuery(id+"F0.wireOp",EDGE,"E4178"),sQuery(id+"F0.wireOp",EDGE,"E4179"),sQuery(id+"F0.wireOp",EDGE,"E4180"),sQuery(id+"F0.wireOp",EDGE,"E4181"),sQuery(id+"F0.wireOp",EDGE,"E4182"),sQuery(id+"F0.wireOp",EDGE,"E4183"),sQuery(id+"F0.wireOp",EDGE,"E4184"),sQuery(id+"F0.wireOp",EDGE,"E4185"),sQuery(id+"F0.wireOp",EDGE,"E4186"),sQuery(id+"F0.wireOp",EDGE,"E4187"),sQuery(id+"F0.wireOp",EDGE,"E4188"),sQuery(id+"F0.wireOp",EDGE,"E4189"),sQuery(id+"F0.wireOp",EDGE,"E4190"),sQuery(id+"F0.wireOp",EDGE,"E4191"),sQuery(id+"F0.wireOp",EDGE,"E4192"),sQuery(id+"F0.wireOp",EDGE,"E4193"),sQuery(id+"F0.wireOp",EDGE,"E4194"),sQuery(id+"F0.wireOp",EDGE,"E4195"),sQuery(id+"F0.wireOp",EDGE,"E4196"),sQuery(id+"F0.wireOp",EDGE,"E4197"),sQuery(id+"F0.wireOp",EDGE,"E4198"),sQuery(id+"F0.wireOp",EDGE,"E4199"),sQuery(id+"F0.wireOp",EDGE,"E4200"),sQuery(id+"F0.wireOp",EDGE,"E4201"),sQuery(id+"F0.wireOp",EDGE,"E4202"),sQuery(id+"F0.wireOp",EDGE,"E4203"),sQuery(id+"F0.wireOp",EDGE,"E4204"),sQuery(id+"F0.wireOp",EDGE,"E4205"),sQuery(id+"F0.wireOp",EDGE,"E4206"),sQuery(id+"F0.wireOp",EDGE,"E4207"),sQuery(id+"F0.wireOp",EDGE,"E4208"),sQuery(id+"F0.wireOp",EDGE,"E4209"),sQuery(id+"F0.wireOp",EDGE,"E4210"),sQuery(id+"F0.wireOp",EDGE,"E4211"),sQuery(id+"F0.wireOp",EDGE,"E4212"),sQuery(id+"F0.wireOp",EDGE,"E4213"),sQuery(id+"F0.wireOp",EDGE,"E4214"),sQuery(id+"F0.wireOp",EDGE,"E4215"),sQuery(id+"F0.wireOp",EDGE,"E4216"),sQuery(id+"F0.wireOp",EDGE,"E4217"),sQuery(id+"F0.wireOp",EDGE,"E4218"),sQuery(id+"F0.wireOp",EDGE,"E4219"),sQuery(id+"F0.wireOp",EDGE,"E4220"),sQuery(id+"F0.wireOp",EDGE,"E4221"),sQuery(id+"F0.wireOp",EDGE,"E4222"),sQuery(id+"F0.wireOp",EDGE,"E4223"),sQuery(id+"F0.wireOp",EDGE,"E4224"),sQuery(id+"F0.wireOp",EDGE,"E4225"),sQuery(id+"F0.wireOp",EDGE,"E4226"),sQuery(id+"F0.wireOp",EDGE,"E4227"),sQuery(id+"F0.wireOp",EDGE,"E4228"),sQuery(id+"F0.wireOp",EDGE,"E4229"),sQuery(id+"F0.wireOp",EDGE,"E4230"),sQuery(id+"F0.wireOp",EDGE,"E4231"),sQuery(id+"F0.wireOp",EDGE,"E4232"),sQuery(id+"F0.wireOp",EDGE,"E4233"),sQuery(id+"F0.wireOp",EDGE,"E4234"),sQuery(id+"F0.wireOp",EDGE,"E4235"),sQuery(id+"F0.wireOp",EDGE,"E4236"),sQuery(id+"F0.wireOp",EDGE,"E4237"),sQuery(id+"F0.wireOp",EDGE,"E4238"),sQuery(id+"F0.wireOp",EDGE,"E4239"),sQuery(id+"F0.wireOp",EDGE,"E4240"),sQuery(id+"F0.wireOp",EDGE,"E4241"),sQuery(id+"F0.wireOp",EDGE,"E4242"),sQuery(id+"F0.wireOp",EDGE,"E4243"),sQuery(id+"F0.wireOp",EDGE,"E4244"),sQuery(id+"F0.wireOp",EDGE,"E4245"),sQuery(id+"F0.wireOp",EDGE,"E4246"),sQuery(id+"F0.wireOp",EDGE,"E4247"),sQuery(id+"F0.wireOp",EDGE,"E4248"),sQuery(id+"F0.wireOp",EDGE,"E4249"),sQuery(id+"F0.wireOp",EDGE,"E4250"),sQuery(id+"F0.wireOp",EDGE,"E4251"),sQuery(id+"F0.wireOp",EDGE,"E4252"),sQuery(id+"F0.wireOp",EDGE,"E4253"),sQuery(id+"F0.wireOp",EDGE,"E4254"),sQuery(id+"F0.wireOp",EDGE,"E4255"),sQuery(id+"F0.wireOp",EDGE,"E4256"),sQuery(id+"F0.wireOp",EDGE,"E4257"),sQuery(id+"F0.wireOp",EDGE,"E4258"),sQuery(id+"F0.wireOp",EDGE,"E4259"),sQuery(id+"F0.wireOp",EDGE,"E4260"),sQuery(id+"F0.wireOp",EDGE,"E4261"),sQuery(id+"F0.wireOp",EDGE,"E4262"),sQuery(id+"F0.wireOp",EDGE,"E4263"),sQuery(id+"F0.wireOp",EDGE,"E4264"),sQuery(id+"F0.wireOp",EDGE,"E4265"),sQuery(id+"F0.wireOp",EDGE,"E4266"),sQuery(id+"F0.wireOp",EDGE,"E4267"),sQuery(id+"F0.wireOp",EDGE,"E4268"),sQuery(id+"F0.wireOp",EDGE,"E4269"),sQuery(id+"F0.wireOp",EDGE,"E4270"),sQuery(id+"F0.wireOp",EDGE,"E4271"),sQuery(id+"F0.wireOp",EDGE,"E4272"),sQuery(id+"F0.wireOp",EDGE,"E4273"),sQuery(id+"F0.wireOp",EDGE,"E4274"),sQuery(id+"F0.wireOp",EDGE,"E4275"),sQuery(id+"F0.wireOp",EDGE,"E4276"),sQuery(id+"F0.wireOp",EDGE,"E4277"),sQuery(id+"F0.wireOp",EDGE,"E4278"),sQuery(id+"F0.wireOp",EDGE,"E4279"),sQuery(id+"F0.wireOp",EDGE,"E4280"),sQuery(id+"F0.wireOp",EDGE,"E4281"),sQuery(id+"F0.wireOp",EDGE,"E4282"),sQuery(id+"F0.wireOp",EDGE,"E4283"),sQuery(id+"F0.wireOp",EDGE,"E4284"),sQuery(id+"F0.wireOp",EDGE,"E4285"),sQuery(id+"F0.wireOp",EDGE,"E4286"),sQuery(id+"F0.wireOp",EDGE,"E4287"),sQuery(id+"F0.wireOp",EDGE,"E4288"),sQuery(id+"F0.wireOp",EDGE,"E4289"),sQuery(id+"F0.wireOp",EDGE,"E4290"),sQuery(id+"F0.wireOp",EDGE,"E4291"),sQuery(id+"F0.wireOp",EDGE,"E4292"),sQuery(id+"F0.wireOp",EDGE,"E4293"),sQuery(id+"F0.wireOp",EDGE,"E4294"),sQuery(id+"F0.wireOp",EDGE,"E4295"),sQuery(id+"F0.wireOp",EDGE,"E4296"),sQuery(id+"F0.wireOp",EDGE,"E4297"),sQuery(id+"F0.wireOp",EDGE,"E4298"),sQuery(id+"F0.wireOp",EDGE,"E4299"),sQuery(id+"F0.wireOp",EDGE,"E4300"),sQuery(id+"F0.wireOp",EDGE,"E4301"),sQuery(id+"F0.wireOp",EDGE,"E4302"),sQuery(id+"F0.wireOp",EDGE,"E4303"),sQuery(id+"F0.wireOp",EDGE,"E4304"),sQuery(id+"F0.wireOp",EDGE,"E4305"),sQuery(id+"F0.wireOp",EDGE,"E4306"),sQuery(id+"F0.wireOp",EDGE,"E4307"),sQuery(id+"F0.wireOp",EDGE,"E4308"),sQuery(id+"F0.wireOp",EDGE,"E4309"),sQuery(id+"F0.wireOp",EDGE,"E4310"),sQuery(id+"F0.wireOp",EDGE,"E4311"),sQuery(id+"F0.wireOp",EDGE,"E4312"),sQuery(id+"F0.wireOp",EDGE,"E4313"),sQuery(id+"F0.wireOp",EDGE,"E4314"),sQuery(id+"F0.wireOp",EDGE,"E4315"),sQuery(id+"F0.wireOp",EDGE,"E4316"),sQuery(id+"F0.wireOp",EDGE,"E4317"),sQuery(id+"F0.wireOp",EDGE,"E4318"),sQuery(id+"F0.wireOp",EDGE,"E4319"),sQuery(id+"F0.wireOp",EDGE,"E4320"),sQuery(id+"F0.wireOp",EDGE,"E4321"),sQuery(id+"F0.wireOp",EDGE,"E4322"),sQuery(id+"F0.wireOp",EDGE,"E4323"),sQuery(id+"F0.wireOp",EDGE,"E4324"),sQuery(id+"F0.wireOp",EDGE,"E4325"),sQuery(id+"F0.wireOp",EDGE,"E4326"),sQuery(id+"F0.wireOp",EDGE,"E4327"),sQuery(id+"F0.wireOp",EDGE,"E4328"),sQuery(id+"F0.wireOp",EDGE,"E4329"),sQuery(id+"F0.wireOp",EDGE,"E4330"),sQuery(id+"F0.wireOp",EDGE,"E4331"),sQuery(id+"F0.wireOp",EDGE,"E4332"),sQuery(id+"F0.wireOp",EDGE,"E4333"),sQuery(id+"F0.wireOp",EDGE,"E4334"),sQuery(id+"F0.wireOp",EDGE,"E4335"),sQuery(id+"F0.wireOp",EDGE,"E4336"),sQuery(id+"F0.wireOp",EDGE,"E4337"),sQuery(id+"F0.wireOp",EDGE,"E4338"),sQuery(id+"F0.wireOp",EDGE,"E4339"),sQuery(id+"F0.wireOp",EDGE,"E4340"),sQuery(id+"F0.wireOp",EDGE,"E4341"),sQuery(id+"F0.wireOp",EDGE,"E4342"),sQuery(id+"F0.wireOp",EDGE,"E4343"),sQuery(id+"F0.wireOp",EDGE,"E4344"),sQuery(id+"F0.wireOp",EDGE,"E4345"),sQuery(id+"F0.wireOp",EDGE,"E4346"),sQuery(id+"F0.wireOp",EDGE,"E4347"),sQuery(id+"F0.wireOp",EDGE,"E4348"),sQuery(id+"F0.wireOp",EDGE,"E4349"),sQuery(id+"F0.wireOp",EDGE,"E4350"),sQuery(id+"F0.wireOp",EDGE,"E4351"),sQuery(id+"F0.wireOp",EDGE,"E4352"),sQuery(id+"F0.wireOp",EDGE,"E4353"),sQuery(id+"F0.wireOp",EDGE,"E4354"),sQuery(id+"F0.wireOp",EDGE,"E4355"),sQuery(id+"F0.wireOp",EDGE,"E4356"),sQuery(id+"F0.wireOp",EDGE,"E4357"),sQuery(id+"F0.wireOp",EDGE,"E4358"),sQuery(id+"F0.wireOp",EDGE,"E4359"),sQuery(id+"F0.wireOp",EDGE,"E4360"),sQuery(id+"F0.wireOp",EDGE,"E4361"),sQuery(id+"F0.wireOp",EDGE,"E4362"),sQuery(id+"F0.wireOp",EDGE,"E4363"),sQuery(id+"F0.wireOp",EDGE,"E4364"),sQuery(id+"F0.wireOp",EDGE,"E4365"),sQuery(id+"F0.wireOp",EDGE,"E4366"),sQuery(id+"F0.wireOp",EDGE,"E4367"),sQuery(id+"F0.wireOp",EDGE,"E4368"),sQuery(id+"F0.wireOp",EDGE,"E4369"),sQuery(id+"F0.wireOp",EDGE,"E4370"),sQuery(id+"F0.wireOp",EDGE,"E4371"),sQuery(id+"F0.wireOp",EDGE,"E4372"),sQuery(id+"F0.wireOp",EDGE,"E4373"),sQuery(id+"F0.wireOp",EDGE,"E4374"),sQuery(id+"F0.wireOp",EDGE,"E4375"),sQuery(id+"F0.wireOp",EDGE,"E4376"),sQuery(id+"F0.wireOp",EDGE,"E4377"),sQuery(id+"F0.wireOp",EDGE,"E4378"),sQuery(id+"F0.wireOp",EDGE,"E4379"),sQuery(id+"F0.wireOp",EDGE,"E4380"),sQuery(id+"F0.wireOp",EDGE,"E4381"),sQuery(id+"F0.wireOp",EDGE,"E4382"),sQuery(id+"F0.wireOp",EDGE,"E4383"),sQuery(id+"F0.wireOp",EDGE,"E4384"),sQuery(id+"F0.wireOp",EDGE,"E4385"),sQuery(id+"F0.wireOp",EDGE,"E4386"),sQuery(id+"F0.wireOp",EDGE,"E4387"),sQuery(id+"F0.wireOp",EDGE,"E4388"),sQuery(id+"F0.wireOp",EDGE,"E4389"),sQuery(id+"F0.wireOp",EDGE,"E4390"),sQuery(id+"F0.wireOp",EDGE,"E4391"),sQuery(id+"F0.wireOp",EDGE,"E4392"),sQuery(id+"F0.wireOp",EDGE,"E4393"),sQuery(id+"F0.wireOp",EDGE,"E4394"),sQuery(id+"F0.wireOp",EDGE,"E4395"),sQuery(id+"F0.wireOp",EDGE,"E4396"),sQuery(id+"F0.wireOp",EDGE,"E4397"),sQuery(id+"F0.wireOp",EDGE,"E4398"),sQuery(id+"F0.wireOp",EDGE,"E4399"),sQuery(id+"F0.wireOp",EDGE,"E4400"),sQuery(id+"F0.wireOp",EDGE,"E4401"),sQuery(id+"F0.wireOp",EDGE,"E4402"),sQuery(id+"F0.wireOp",EDGE,"E4403"),sQuery(id+"F0.wireOp",EDGE,"E4404"),sQuery(id+"F0.wireOp",EDGE,"E4405"),sQuery(id+"F0.wireOp",EDGE,"E4406"),sQuery(id+"F0.wireOp",EDGE,"E4407"),sQuery(id+"F0.wireOp",EDGE,"E4408"),sQuery(id+"F0.wireOp",EDGE,"E4409"),sQuery(id+"F0.wireOp",EDGE,"E4410"),sQuery(id+"F0.wireOp",EDGE,"E4411"),sQuery(id+"F0.wireOp",EDGE,"E4412"),sQuery(id+"F0.wireOp",EDGE,"E4413"),sQuery(id+"F0.wireOp",EDGE,"E4414"),sQuery(id+"F0.wireOp",EDGE,"E4415"),sQuery(id+"F0.wireOp",EDGE,"E4416"),sQuery(id+"F0.wireOp",EDGE,"E4417"),sQuery(id+"F0.wireOp",EDGE,"E4418"),sQuery(id+"F0.wireOp",EDGE,"E4419"),sQuery(id+"F0.wireOp",EDGE,"E4420"),sQuery(id+"F0.wireOp",EDGE,"E4421"),sQuery(id+"F0.wireOp",EDGE,"E4422"),sQuery(id+"F0.wireOp",EDGE,"E4423"),sQuery(id+"F0.wireOp",EDGE,"E4424"),sQuery(id+"F0.wireOp",EDGE,"E4425"),sQuery(id+"F0.wireOp",EDGE,"E4426"),sQuery(id+"F0.wireOp",EDGE,"E4427"),sQuery(id+"F0.wireOp",EDGE,"E4428"),sQuery(id+"F0.wireOp",EDGE,"E4429"),sQuery(id+"F0.wireOp",EDGE,"E4430"),sQuery(id+"F0.wireOp",EDGE,"E4431"),sQuery(id+"F0.wireOp",EDGE,"E4432"),sQuery(id+"F0.wireOp",EDGE,"E4433"),sQuery(id+"F0.wireOp",EDGE,"E4434"),sQuery(id+"F0.wireOp",EDGE,"E4435"),sQuery(id+"F0.wireOp",EDGE,"E4436"),sQuery(id+"F0.wireOp",EDGE,"E4437"),sQuery(id+"F0.wireOp",EDGE,"E4438"),sQuery(id+"F0.wireOp",EDGE,"E4439"),sQuery(id+"F0.wireOp",EDGE,"E4440"),sQuery(id+"F0.wireOp",EDGE,"E4441"),sQuery(id+"F0.wireOp",EDGE,"E4442"),sQuery(id+"F0.wireOp",EDGE,"E4443"),sQuery(id+"F0.wireOp",EDGE,"E4444"),sQuery(id+"F0.wireOp",EDGE,"E4445"),sQuery(id+"F0.wireOp",EDGE,"E4446"),sQuery(id+"F0.wireOp",EDGE,"E4447"),sQuery(id+"F0.wireOp",EDGE,"E4448"),sQuery(id+"F0.wireOp",EDGE,"E4449"),sQuery(id+"F0.wireOp",EDGE,"E4450"),sQuery(id+"F0.wireOp",EDGE,"E4451"),sQuery(id+"F0.wireOp",EDGE,"E4452"),sQuery(id+"F0.wireOp",EDGE,"E4453"),sQuery(id+"F0.wireOp",EDGE,"E4454"),sQuery(id+"F0.wireOp",EDGE,"E4455"),sQuery(id+"F0.wireOp",EDGE,"E4456"),sQuery(id+"F0.wireOp",EDGE,"E4457"),sQuery(id+"F0.wireOp",EDGE,"E4458"),sQuery(id+"F0.wireOp",EDGE,"E4459"),sQuery(id+"F0.wireOp",EDGE,"E4460"),sQuery(id+"F0.wireOp",EDGE,"E4461"),sQuery(id+"F0.wireOp",EDGE,"E4462"),sQuery(id+"F0.wireOp",EDGE,"E4463"),sQuery(id+"F0.wireOp",EDGE,"E4464"),sQuery(id+"F0.wireOp",EDGE,"E4465"),sQuery(id+"F0.wireOp",EDGE,"E4466"),sQuery(id+"F0.wireOp",EDGE,"E4467"),sQuery(id+"F0.wireOp",EDGE,"E4468"),sQuery(id+"F0.wireOp",EDGE,"E4469"),sQuery(id+"F0.wireOp",EDGE,"E4470"),sQuery(id+"F0.wireOp",EDGE,"E4471"),sQuery(id+"F0.wireOp",EDGE,"E4472"),sQuery(id+"F0.wireOp",EDGE,"E4473"),sQuery(id+"F0.wireOp",EDGE,"E4474"),sQuery(id+"F0.wireOp",EDGE,"E4475"),sQuery(id+"F0.wireOp",EDGE,"E4476"),sQuery(id+"F0.wireOp",EDGE,"E4477"),sQuery(id+"F0.wireOp",EDGE,"E4478"),sQuery(id+"F0.wireOp",EDGE,"E4479"),sQuery(id+"F0.wireOp",EDGE,"E4480"),sQuery(id+"F0.wireOp",EDGE,"E4481"),sQuery(id+"F0.wireOp",EDGE,"E4482"),sQuery(id+"F0.wireOp",EDGE,"E4483"),sQuery(id+"F0.wireOp",EDGE,"E4484"),sQuery(id+"F0.wireOp",EDGE,"E4485"),sQuery(id+"F0.wireOp",EDGE,"E4486"),sQuery(id+"F0.wireOp",EDGE,"E4487"),sQuery(id+"F0.wireOp",EDGE,"E4488"),sQuery(id+"F0.wireOp",EDGE,"E4489"),sQuery(id+"F0.wireOp",EDGE,"E4490"),sQuery(id+"F0.wireOp",EDGE,"E4491"),sQuery(id+"F0.wireOp",EDGE,"E4492"),sQuery(id+"F0.wireOp",EDGE,"E4493"),sQuery(id+"F0.wireOp",EDGE,"E4494"),sQuery(id+"F0.wireOp",EDGE,"E4495"),sQuery(id+"F0.wireOp",EDGE,"E4496"),sQuery(id+"F0.wireOp",EDGE,"E4497"),sQuery(id+"F0.wireOp",EDGE,"E4498"),sQuery(id+"F0.wireOp",EDGE,"E4499"),sQuery(id+"F0.wireOp",EDGE,"E4500"),sQuery(id+"F0.wireOp",EDGE,"E4501"),sQuery(id+"F0.wireOp",EDGE,"E4502"),sQuery(id+"F0.wireOp",EDGE,"E4503"),sQuery(id+"F0.wireOp",EDGE,"E4504"),sQuery(id+"F0.wireOp",EDGE,"E4505"),sQuery(id+"F0.wireOp",EDGE,"E4506"),sQuery(id+"F0.wireOp",EDGE,"E4507"),sQuery(id+"F0.wireOp",EDGE,"E4508"),sQuery(id+"F0.wireOp",EDGE,"E4509"),sQuery(id+"F0.wireOp",EDGE,"E4510"),sQuery(id+"F0.wireOp",EDGE,"E4511"),sQuery(id+"F0.wireOp",EDGE,"E4512"),sQuery(id+"F0.wireOp",EDGE,"E4513"),sQuery(id+"F0.wireOp",EDGE,"E4514"),sQuery(id+"F0.wireOp",EDGE,"E4515"),sQuery(id+"F0.wireOp",EDGE,"E4516"),sQuery(id+"F0.wireOp",EDGE,"E4517"),sQuery(id+"F0.wireOp",EDGE,"E4518"),sQuery(id+"F0.wireOp",EDGE,"E4519"),sQuery(id+"F0.wireOp",EDGE,"E4520"),sQuery(id+"F0.wireOp",EDGE,"E4521"),sQuery(id+"F0.wireOp",EDGE,"E4522"),sQuery(id+"F0.wireOp",EDGE,"E4523"),sQuery(id+"F0.wireOp",EDGE,"E4524"),sQuery(id+"F0.wireOp",EDGE,"E4525"),sQuery(id+"F0.wireOp",EDGE,"E4526"),sQuery(id+"F0.wireOp",EDGE,"E4527"),sQuery(id+"F0.wireOp",EDGE,"E4528"),sQuery(id+"F0.wireOp",EDGE,"E4529"),sQuery(id+"F0.wireOp",EDGE,"E4530"),sQuery(id+"F0.wireOp",EDGE,"E4531"),sQuery(id+"F0.wireOp",EDGE,"E4532"),sQuery(id+"F0.wireOp",EDGE,"E4533"),sQuery(id+"F0.wireOp",EDGE,"E4534"),sQuery(id+"F0.wireOp",EDGE,"E4535"),sQuery(id+"F0.wireOp",EDGE,"E4536"),sQuery(id+"F0.wireOp",EDGE,"E4537"),sQuery(id+"F0.wireOp",EDGE,"E4538"),sQuery(id+"F0.wireOp",EDGE,"E4539"),sQuery(id+"F0.wireOp",EDGE,"E4540"),sQuery(id+"F0.wireOp",EDGE,"E4541"),sQuery(id+"F0.wireOp",EDGE,"E4542"),sQuery(id+"F0.wireOp",EDGE,"E4543"),sQuery(id+"F0.wireOp",EDGE,"E4544"),sQuery(id+"F0.wireOp",EDGE,"E4545"),sQuery(id+"F0.wireOp",EDGE,"E4546"),sQuery(id+"F0.wireOp",EDGE,"E4547"),sQuery(id+"F0.wireOp",EDGE,"E4548"),sQuery(id+"F0.wireOp",EDGE,"E4549"),sQuery(id+"F0.wireOp",EDGE,"E4550"),sQuery(id+"F0.wireOp",EDGE,"E4551"),sQuery(id+"F0.wireOp",EDGE,"E4552"),sQuery(id+"F0.wireOp",EDGE,"E4553"),sQuery(id+"F0.wireOp",EDGE,"E4554"),sQuery(id+"F0.wireOp",EDGE,"E4555"),sQuery(id+"F0.wireOp",EDGE,"E4556"),sQuery(id+"F0.wireOp",EDGE,"E4557"),sQuery(id+"F0.wireOp",EDGE,"E4558"),sQuery(id+"F0.wireOp",EDGE,"E4559"),sQuery(id+"F0.wireOp",EDGE,"E4560"),sQuery(id+"F0.wireOp",EDGE,"E4561"),sQuery(id+"F0.wireOp",EDGE,"E4562"),sQuery(id+"F0.wireOp",EDGE,"E4563"),sQuery(id+"F0.wireOp",EDGE,"E4564"),sQuery(id+"F0.wireOp",EDGE,"E4565"),sQuery(id+"F0.wireOp",EDGE,"E4566"),sQuery(id+"F0.wireOp",EDGE,"E4567"),sQuery(id+"F0.wireOp",EDGE,"E4568"),sQuery(id+"F0.wireOp",EDGE,"E4569"),sQuery(id+"F0.wireOp",EDGE,"E4570"),sQuery(id+"F0.wireOp",EDGE,"E4571"),sQuery(id+"F0.wireOp",EDGE,"E4572"),sQuery(id+"F0.wireOp",EDGE,"E4573"),sQuery(id+"F0.wireOp",EDGE,"E4574"),sQuery(id+"F0.wireOp",EDGE,"E4575"),sQuery(id+"F0.wireOp",EDGE,"E4576"),sQuery(id+"F0.wireOp",EDGE,"E4577"),sQuery(id+"F0.wireOp",EDGE,"E4578"),sQuery(id+"F0.wireOp",EDGE,"E4579"),sQuery(id+"F0.wireOp",EDGE,"E4580"),sQuery(id+"F0.wireOp",EDGE,"E4581"),sQuery(id+"F0.wireOp",EDGE,"E4582"),sQuery(id+"F0.wireOp",EDGE,"E4583"),sQuery(id+"F0.wireOp",EDGE,"E4584"),sQuery(id+"F0.wireOp",EDGE,"E4585"),sQuery(id+"F0.wireOp",EDGE,"E4586"),sQuery(id+"F0.wireOp",EDGE,"E4587"),sQuery(id+"F0.wireOp",EDGE,"E4588"),sQuery(id+"F0.wireOp",EDGE,"E4589"),sQuery(id+"F0.wireOp",EDGE,"E4590"),sQuery(id+"F0.wireOp",EDGE,"E4591"),sQuery(id+"F0.wireOp",EDGE,"E4592"),sQuery(id+"F0.wireOp",EDGE,"E4593"),sQuery(id+"F0.wireOp",EDGE,"E4594"),sQuery(id+"F0.wireOp",EDGE,"E4595"),sQuery(id+"F0.wireOp",EDGE,"E4596"),sQuery(id+"F0.wireOp",EDGE,"E4597"),sQuery(id+"F0.wireOp",EDGE,"E4598"),sQuery(id+"F0.wireOp",EDGE,"E4599"),sQuery(id+"F0.wireOp",EDGE,"E4600"),sQuery(id+"F0.wireOp",EDGE,"E4601"),sQuery(id+"F0.wireOp",EDGE,"E4602"),sQuery(id+"F0.wireOp",EDGE,"E4603"),sQuery(id+"F0.wireOp",EDGE,"E4604"),sQuery(id+"F0.wireOp",EDGE,"E4605"),sQuery(id+"F0.wireOp",EDGE,"E4606"),sQuery(id+"F0.wireOp",EDGE,"E4607"),sQuery(id+"F0.wireOp",EDGE,"E4608"),sQuery(id+"F0.wireOp",EDGE,"E4609"),sQuery(id+"F0.wireOp",EDGE,"E4610"),sQuery(id+"F0.wireOp",EDGE,"E4611"),sQuery(id+"F0.wireOp",EDGE,"E4612"),sQuery(id+"F0.wireOp",EDGE,"E4613"),sQuery(id+"F0.wireOp",EDGE,"E4614"),sQuery(id+"F0.wireOp",EDGE,"E4615"),sQuery(id+"F0.wireOp",EDGE,"E4616"),sQuery(id+"F0.wireOp",EDGE,"E4617"),sQuery(id+"F0.wireOp",EDGE,"E4618"),sQuery(id+"F0.wireOp",EDGE,"E4619"),sQuery(id+"F0.wireOp",EDGE,"E4620"),sQuery(id+"F0.wireOp",EDGE,"E4621"),sQuery(id+"F0.wireOp",EDGE,"E4622"),sQuery(id+"F0.wireOp",EDGE,"E4623"),sQuery(id+"F0.wireOp",EDGE,"E4624"),sQuery(id+"F0.wireOp",EDGE,"E4625"),sQuery(id+"F0.wireOp",EDGE,"E4626"),sQuery(id+"F0.wireOp",EDGE,"E4627"),sQuery(id+"F0.wireOp",EDGE,"E4628"),sQuery(id+"F0.wireOp",EDGE,"E4629"),sQuery(id+"F0.wireOp",EDGE,"E4630"),sQuery(id+"F0.wireOp",EDGE,"E4631"),sQuery(id+"F0.wireOp",EDGE,"E4632"),sQuery(id+"F0.wireOp",EDGE,"E4633"),sQuery(id+"F0.wireOp",EDGE,"E4634"),sQuery(id+"F0.wireOp",EDGE,"E4635"),sQuery(id+"F0.wireOp",EDGE,"E4636"),sQuery(id+"F0.wireOp",EDGE,"E4637"),sQuery(id+"F0.wireOp",EDGE,"E4638"),sQuery(id+"F0.wireOp",EDGE,"E4639"),sQuery(id+"F0.wireOp",EDGE,"E4640"),sQuery(id+"F0.wireOp",EDGE,"E4641"),sQuery(id+"F0.wireOp",EDGE,"E4642"),sQuery(id+"F0.wireOp",EDGE,"E4643"),sQuery(id+"F0.wireOp",EDGE,"E4644"),sQuery(id+"F0.wireOp",EDGE,"E4645"),sQuery(id+"F0.wireOp",EDGE,"E4646"),sQuery(id+"F0.wireOp",EDGE,"E4647"),sQuery(id+"F0.wireOp",EDGE,"E4648"),sQuery(id+"F0.wireOp",EDGE,"E4649"),sQuery(id+"F0.wireOp",EDGE,"E4650"),sQuery(id+"F0.wireOp",EDGE,"E4651"),sQuery(id+"F0.wireOp",EDGE,"E4652"),sQuery(id+"F0.wireOp",EDGE,"E4653"),sQuery(id+"F0.wireOp",EDGE,"E4654"),sQuery(id+"F0.wireOp",EDGE,"E4655"),sQuery(id+"F0.wireOp",EDGE,"E4656"),sQuery(id+"F0.wireOp",EDGE,"E4657"),sQuery(id+"F0.wireOp",EDGE,"E4658"),sQuery(id+"F0.wireOp",EDGE,"E4659"),sQuery(id+"F0.wireOp",EDGE,"E4660"),sQuery(id+"F0.wireOp",EDGE,"E4661"),sQuery(id+"F0.wireOp",EDGE,"E4662"),sQuery(id+"F0.wireOp",EDGE,"E4663"),sQuery(id+"F0.wireOp",EDGE,"E4664"),sQuery(id+"F0.wireOp",EDGE,"E4665"),sQuery(id+"F0.wireOp",EDGE,"E4666"),sQuery(id+"F0.wireOp",EDGE,"E4667"),sQuery(id+"F0.wireOp",EDGE,"E4668"),sQuery(id+"F0.wireOp",EDGE,"E4669"),sQuery(id+"F0.wireOp",EDGE,"E4670"),sQuery(id+"F0.wireOp",EDGE,"E4671"),sQuery(id+"F0.wireOp",EDGE,"E4672"),sQuery(id+"F0.wireOp",EDGE,"E4673"),sQuery(id+"F0.wireOp",EDGE,"E4674"),sQuery(id+"F0.wireOp",EDGE,"E4675"),sQuery(id+"F0.wireOp",EDGE,"E4676"),sQuery(id+"F0.wireOp",EDGE,"E4677"),sQuery(id+"F0.wireOp",EDGE,"E4678"),sQuery(id+"F0.wireOp",EDGE,"E4679"),sQuery(id+"F0.wireOp",EDGE,"E4680"),sQuery(id+"F0.wireOp",EDGE,"E4681"),sQuery(id+"F0.wireOp",EDGE,"E4682"),sQuery(id+"F0.wireOp",EDGE,"E4683"),sQuery(id+"F0.wireOp",EDGE,"E4684"),sQuery(id+"F0.wireOp",EDGE,"E4685"),sQuery(id+"F0.wireOp",EDGE,"E4686"),sQuery(id+"F0.wireOp",EDGE,"E4687"),sQuery(id+"F0.wireOp",EDGE,"E4688"),sQuery(id+"F0.wireOp",EDGE,"E4689"),sQuery(id+"F0.wireOp",EDGE,"E4690"),sQuery(id+"F0.wireOp",EDGE,"E4691"),sQuery(id+"F0.wireOp",EDGE,"E4692"),sQuery(id+"F0.wireOp",EDGE,"E4693"),sQuery(id+"F0.wireOp",EDGE,"E4694"),sQuery(id+"F0.wireOp",EDGE,"E4695"),sQuery(id+"F0.wireOp",EDGE,"E4696"),sQuery(id+"F0.wireOp",EDGE,"E4697"),sQuery(id+"F0.wireOp",EDGE,"E4698"),sQuery(id+"F0.wireOp",EDGE,"E4699"),sQuery(id+"F0.wireOp",EDGE,"E4700"),sQuery(id+"F0.wireOp",EDGE,"E4701"),sQuery(id+"F0.wireOp",EDGE,"E4702"),sQuery(id+"F0.wireOp",EDGE,"E4703"),sQuery(id+"F0.wireOp",EDGE,"E4704"),sQuery(id+"F0.wireOp",EDGE,"E4705"),sQuery(id+"F0.wireOp",EDGE,"E4706"),sQuery(id+"F0.wireOp",EDGE,"E4707"),sQuery(id+"F0.wireOp",EDGE,"E4708"),sQuery(id+"F0.wireOp",EDGE,"E4709"),sQuery(id+"F0.wireOp",EDGE,"E4710"),sQuery(id+"F0.wireOp",EDGE,"E4711"),sQuery(id+"F0.wireOp",EDGE,"E4712"),sQuery(id+"F0.wireOp",EDGE,"E4713"),sQuery(id+"F0.wireOp",EDGE,"E4714"),sQuery(id+"F0.wireOp",EDGE,"E4715"),sQuery(id+"F0.wireOp",EDGE,"E4716"),sQuery(id+"F0.wireOp",EDGE,"E4717"),sQuery(id+"F0.wireOp",EDGE,"E4718"),sQuery(id+"F0.wireOp",EDGE,"E4719"),sQuery(id+"F0.wireOp",EDGE,"E4720"),sQuery(id+"F0.wireOp",EDGE,"E4721"),sQuery(id+"F0.wireOp",EDGE,"E4722"),sQuery(id+"F0.wireOp",EDGE,"E4723"),sQuery(id+"F0.wireOp",EDGE,"E4724"),sQuery(id+"F0.wireOp",EDGE,"E4725"),sQuery(id+"F0.wireOp",EDGE,"E4726"),sQuery(id+"F0.wireOp",EDGE,"E4727"),sQuery(id+"F0.wireOp",EDGE,"E4728"),sQuery(id+"F0.wireOp",EDGE,"E4729"),sQuery(id+"F0.wireOp",EDGE,"E4730"),sQuery(id+"F0.wireOp",EDGE,"E4731"),sQuery(id+"F0.wireOp",EDGE,"E4732"),sQuery(id+"F0.wireOp",EDGE,"E4733"),sQuery(id+"F0.wireOp",EDGE,"E4734"),sQuery(id+"F0.wireOp",EDGE,"E4735"),sQuery(id+"F0.wireOp",EDGE,"E4736"),sQuery(id+"F0.wireOp",EDGE,"E4737"),sQuery(id+"F0.wireOp",EDGE,"E4738"),sQuery(id+"F0.wireOp",EDGE,"E4739"),sQuery(id+"F0.wireOp",EDGE,"E4740"),sQuery(id+"F0.wireOp",EDGE,"E4741"),sQuery(id+"F0.wireOp",EDGE,"E4742"),sQuery(id+"F0.wireOp",EDGE,"E4743"),sQuery(id+"F0.wireOp",EDGE,"E4744"),sQuery(id+"F0.wireOp",EDGE,"E4745"),sQuery(id+"F0.wireOp",EDGE,"E4746"),sQuery(id+"F0.wireOp",EDGE,"E4747"),sQuery(id+"F0.wireOp",EDGE,"E4748"),sQuery(id+"F0.wireOp",EDGE,"E4749"),sQuery(id+"F0.wireOp",EDGE,"E4750"),sQuery(id+"F0.wireOp",EDGE,"E4751"),sQuery(id+"F0.wireOp",EDGE,"E4752"),sQuery(id+"F0.wireOp",EDGE,"E4753"),sQuery(id+"F0.wireOp",EDGE,"E4754"),sQuery(id+"F0.wireOp",EDGE,"E4755"),sQuery(id+"F0.wireOp",EDGE,"E4756"),sQuery(id+"F0.wireOp",EDGE,"E4757"),sQuery(id+"F0.wireOp",EDGE,"E4758"),sQuery(id+"F0.wireOp",EDGE,"E4759"),sQuery(id+"F0.wireOp",EDGE,"E4760"),sQuery(id+"F0.wireOp",EDGE,"E4761"),sQuery(id+"F0.wireOp",EDGE,"E4762"),sQuery(id+"F0.wireOp",EDGE,"E4763"),sQuery(id+"F0.wireOp",EDGE,"E4764"),sQuery(id+"F0.wireOp",EDGE,"E4765"),sQuery(id+"F0.wireOp",EDGE,"E4766"),sQuery(id+"F0.wireOp",EDGE,"E4767"),sQuery(id+"F0.wireOp",EDGE,"E4768"),sQuery(id+"F0.wireOp",EDGE,"E4769"),sQuery(id+"F0.wireOp",EDGE,"E4770"),sQuery(id+"F0.wireOp",EDGE,"E4771"),sQuery(id+"F0.wireOp",EDGE,"E4772"),sQuery(id+"F0.wireOp",EDGE,"E4773"),sQuery(id+"F0.wireOp",EDGE,"E4774"),sQuery(id+"F0.wireOp",EDGE,"E4775"),sQuery(id+"F0.wireOp",EDGE,"E4776"),sQuery(id+"F0.wireOp",EDGE,"E4777"),sQuery(id+"F0.wireOp",EDGE,"E4778"),sQuery(id+"F0.wireOp",EDGE,"E4779"),sQuery(id+"F0.wireOp",EDGE,"E4780"),sQuery(id+"F0.wireOp",EDGE,"E4781"),sQuery(id+"F0.wireOp",EDGE,"E4782"),sQuery(id+"F0.wireOp",EDGE,"E4783"),sQuery(id+"F0.wireOp",EDGE,"E4784"),sQuery(id+"F0.wireOp",EDGE,"E4785"),sQuery(id+"F0.wireOp",EDGE,"E4786"),sQuery(id+"F0.wireOp",EDGE,"E4787"),sQuery(id+"F0.wireOp",EDGE,"E4788"),sQuery(id+"F0.wireOp",EDGE,"E4789"),sQuery(id+"F0.wireOp",EDGE,"E4790"),sQuery(id+"F0.wireOp",EDGE,"E4791"),sQuery(id+"F0.wireOp",EDGE,"E4792"),sQuery(id+"F0.wireOp",EDGE,"E4793"),sQuery(id+"F0.wireOp",EDGE,"E4794"),sQuery(id+"F0.wireOp",EDGE,"E4795"),sQuery(id+"F0.wireOp",EDGE,"E4796"),sQuery(id+"F0.wireOp",EDGE,"E4797"),sQuery(id+"F0.wireOp",EDGE,"E4798"),sQuery(id+"F0.wireOp",EDGE,"E4799"),sQuery(id+"F0.wireOp",EDGE,"E4800"),sQuery(id+"F0.wireOp",EDGE,"E4801"),sQuery(id+"F0.wireOp",EDGE,"E4802"),sQuery(id+"F0.wireOp",EDGE,"E4803"),sQuery(id+"F0.wireOp",EDGE,"E4804"),sQuery(id+"F0.wireOp",EDGE,"E4805"),sQuery(id+"F0.wireOp",EDGE,"E4806"),sQuery(id+"F0.wireOp",EDGE,"E4807"),sQuery(id+"F0.wireOp",EDGE,"E4808"),sQuery(id+"F0.wireOp",EDGE,"E4809"),sQuery(id+"F0.wireOp",EDGE,"E4810"),sQuery(id+"F0.wireOp",EDGE,"E4811"),sQuery(id+"F0.wireOp",EDGE,"E4812"),sQuery(id+"F0.wireOp",EDGE,"E4813"),sQuery(id+"F0.wireOp",EDGE,"E4814"),sQuery(id+"F0.wireOp",EDGE,"E4815"),sQuery(id+"F0.wireOp",EDGE,"E4816"),sQuery(id+"F0.wireOp",EDGE,"E4817"),sQuery(id+"F0.wireOp",EDGE,"E4818"),sQuery(id+"F0.wireOp",EDGE,"E4819"),sQuery(id+"F0.wireOp",EDGE,"E4820"),sQuery(id+"F0.wireOp",EDGE,"E4821"),sQuery(id+"F0.wireOp",EDGE,"E4822"),sQuery(id+"F0.wireOp",EDGE,"E4823"),sQuery(id+"F0.wireOp",EDGE,"E4824"),sQuery(id+"F0.wireOp",EDGE,"E4825"),sQuery(id+"F0.wireOp",EDGE,"E4826"),sQuery(id+"F0.wireOp",EDGE,"E4827"),sQuery(id+"F0.wireOp",EDGE,"E4828"),sQuery(id+"F0.wireOp",EDGE,"E4829"),sQuery(id+"F0.wireOp",EDGE,"E4830"),sQuery(id+"F0.wireOp",EDGE,"E4831"),sQuery(id+"F0.wireOp",EDGE,"E4832"),sQuery(id+"F0.wireOp",EDGE,"E4833"),sQuery(id+"F0.wireOp",EDGE,"E4834"),sQuery(id+"F0.wireOp",EDGE,"E4835"),sQuery(id+"F0.wireOp",EDGE,"E4836"),sQuery(id+"F0.wireOp",EDGE,"E4837"),sQuery(id+"F0.wireOp",EDGE,"E4838"),sQuery(id+"F0.wireOp",EDGE,"E4839"),sQuery(id+"F0.wireOp",EDGE,"E4840"),sQuery(id+"F0.wireOp",EDGE,"E4841"),sQuery(id+"F0.wireOp",EDGE,"E4842"),sQuery(id+"F0.wireOp",EDGE,"E4843"),sQuery(id+"F0.wireOp",EDGE,"E4844"),sQuery(id+"F0.wireOp",EDGE,"E4845"),sQuery(id+"F0.wireOp",EDGE,"E4846"),sQuery(id+"F0.wireOp",EDGE,"E4847"),sQuery(id+"F0.wireOp",EDGE,"E4848"),sQuery(id+"F0.wireOp",EDGE,"E4849"),sQuery(id+"F0.wireOp",EDGE,"E4850"),sQuery(id+"F0.wireOp",EDGE,"E4851"),sQuery(id+"F0.wireOp",EDGE,"E4852"),sQuery(id+"F0.wireOp",EDGE,"E4853"),sQuery(id+"F0.wireOp",EDGE,"E4854"),sQuery(id+"F0.wireOp",EDGE,"E4855"),sQuery(id+"F0.wireOp",EDGE,"E4856"),sQuery(id+"F0.wireOp",EDGE,"E4857"),sQuery(id+"F0.wireOp",EDGE,"E4858"),sQuery(id+"F0.wireOp",EDGE,"E4859"),sQuery(id+"F0.wireOp",EDGE,"E4860"),sQuery(id+"F0.wireOp",EDGE,"E4861"),sQuery(id+"F0.wireOp",EDGE,"E4862"),sQuery(id+"F0.wireOp",EDGE,"E4863"),sQuery(id+"F0.wireOp",EDGE,"E4864"),sQuery(id+"F0.wireOp",EDGE,"E4865"),sQuery(id+"F0.wireOp",EDGE,"E4866"),sQuery(id+"F0.wireOp",EDGE,"E4867"),sQuery(id+"F0.wireOp",EDGE,"E4868"),sQuery(id+"F0.wireOp",EDGE,"E4869"),sQuery(id+"F0.wireOp",EDGE,"E4870"),sQuery(id+"F0.wireOp",EDGE,"E4871"),sQuery(id+"F0.wireOp",EDGE,"E4872"),sQuery(id+"F0.wireOp",EDGE,"E4873"),sQuery(id+"F0.wireOp",EDGE,"E4874"),sQuery(id+"F0.wireOp",EDGE,"E4875"),sQuery(id+"F0.wireOp",EDGE,"E4876"),sQuery(id+"F0.wireOp",EDGE,"E4877"),sQuery(id+"F0.wireOp",EDGE,"E4878"),sQuery(id+"F0.wireOp",EDGE,"E4879"),sQuery(id+"F0.wireOp",EDGE,"E4880"),sQuery(id+"F0.wireOp",EDGE,"E4881"),sQuery(id+"F0.wireOp",EDGE,"E4882"),sQuery(id+"F0.wireOp",EDGE,"E4883"),sQuery(id+"F0.wireOp",EDGE,"E4884"),sQuery(id+"F0.wireOp",EDGE,"E4885"),sQuery(id+"F0.wireOp",EDGE,"E4886"),sQuery(id+"F0.wireOp",EDGE,"E4887"),sQuery(id+"F0.wireOp",EDGE,"E4888"),sQuery(id+"F0.wireOp",EDGE,"E4889"),sQuery(id+"F0.wireOp",EDGE,"E4890"),sQuery(id+"F0.wireOp",EDGE,"E4891"),sQuery(id+"F0.wireOp",EDGE,"E4892"),sQuery(id+"F0.wireOp",EDGE,"E4893"),sQuery(id+"F0.wireOp",EDGE,"E4894"),sQuery(id+"F0.wireOp",EDGE,"E4895"),sQuery(id+"F0.wireOp",EDGE,"E4896"),sQuery(id+"F0.wireOp",EDGE,"E4897"),sQuery(id+"F0.wireOp",EDGE,"E4898"),sQuery(id+"F0.wireOp",EDGE,"E4899"),sQuery(id+"F0.wireOp",EDGE,"E4900"),sQuery(id+"F0.wireOp",EDGE,"E4901"),sQuery(id+"F0.wireOp",EDGE,"E4902"),sQuery(id+"F0.wireOp",EDGE,"E4903"),sQuery(id+"F0.wireOp",EDGE,"E4904"),sQuery(id+"F0.wireOp",EDGE,"E4905"),sQuery(id+"F0.wireOp",EDGE,"E4906"),sQuery(id+"F0.wireOp",EDGE,"E4907"),sQuery(id+"F0.wireOp",EDGE,"E4908"),sQuery(id+"F0.wireOp",EDGE,"E4909"),sQuery(id+"F0.wireOp",EDGE,"E4910"),sQuery(id+"F0.wireOp",EDGE,"E4911"),sQuery(id+"F0.wireOp",EDGE,"E4912"),sQuery(id+"F0.wireOp",EDGE,"E4913"),sQuery(id+"F0.wireOp",EDGE,"E4914"),sQuery(id+"F0.wireOp",EDGE,"E4915"),sQuery(id+"F0.wireOp",EDGE,"E4916"),sQuery(id+"F0.wireOp",EDGE,"E4917"),sQuery(id+"F0.wireOp",EDGE,"E4918"),sQuery(id+"F0.wireOp",EDGE,"E4919"),sQuery(id+"F0.wireOp",EDGE,"E4920"),sQuery(id+"F0.wireOp",EDGE,"E4921"),sQuery(id+"F0.wireOp",EDGE,"E4922"),sQuery(id+"F0.wireOp",EDGE,"E4923"),sQuery(id+"F0.wireOp",EDGE,"E4924"),sQuery(id+"F0.wireOp",EDGE,"E4925"),sQuery(id+"F0.wireOp",EDGE,"E4926"),sQuery(id+"F0.wireOp",EDGE,"E4927"),sQuery(id+"F0.wireOp",EDGE,"E4928"),sQuery(id+"F0.wireOp",EDGE,"E4929"),sQuery(id+"F0.wireOp",EDGE,"E4930"),sQuery(id+"F0.wireOp",EDGE,"E4931"),sQuery(id+"F0.wireOp",EDGE,"E4932"),sQuery(id+"F0.wireOp",EDGE,"E4933"),sQuery(id+"F0.wireOp",EDGE,"E4934"),sQuery(id+"F0.wireOp",EDGE,"E4935"),sQuery(id+"F0.wireOp",EDGE,"E4936"),sQuery(id+"F0.wireOp",EDGE,"E4937"),sQuery(id+"F0.wireOp",EDGE,"E4938"),sQuery(id+"F0.wireOp",EDGE,"E4939"),sQuery(id+"F0.wireOp",EDGE,"E4940"),sQuery(id+"F0.wireOp",EDGE,"E4941"),sQuery(id+"F0.wireOp",EDGE,"E4942"),sQuery(id+"F0.wireOp",EDGE,"E4943"),sQuery(id+"F0.wireOp",EDGE,"E4944"),sQuery(id+"F0.wireOp",EDGE,"E4945"),sQuery(id+"F0.wireOp",EDGE,"E4946"),sQuery(id+"F0.wireOp",EDGE,"E4947"),sQuery(id+"F0.wireOp",EDGE,"E4948"),sQuery(id+"F0.wireOp",EDGE,"E4949"),sQuery(id+"F0.wireOp",EDGE,"E4950"),sQuery(id+"F0.wireOp",EDGE,"E4951"),sQuery(id+"F0.wireOp",EDGE,"E4952"),sQuery(id+"F0.wireOp",EDGE,"E4953"),sQuery(id+"F0.wireOp",EDGE,"E4954"),sQuery(id+"F0.wireOp",EDGE,"E4955"),sQuery(id+"F0.wireOp",EDGE,"E4956"),sQuery(id+"F0.wireOp",EDGE,"E4957"),sQuery(id+"F0.wireOp",EDGE,"E4958"),sQuery(id+"F0.wireOp",EDGE,"E4959"),sQuery(id+"F0.wireOp",EDGE,"E4960"),sQuery(id+"F0.wireOp",EDGE,"E4961"),sQuery(id+"F0.wireOp",EDGE,"E4962"),sQuery(id+"F0.wireOp",EDGE,"E4963"),sQuery(id+"F0.wireOp",EDGE,"E4964"),sQuery(id+"F0.wireOp",EDGE,"E4965"),sQuery(id+"F0.wireOp",EDGE,"E4966"),sQuery(id+"F0.wireOp",EDGE,"E4967"),sQuery(id+"F0.wireOp",EDGE,"E4968"),sQuery(id+"F0.wireOp",EDGE,"E4969"),sQuery(id+"F0.wireOp",EDGE,"E4970"),sQuery(id+"F0.wireOp",EDGE,"E4971"),sQuery(id+"F0.wireOp",EDGE,"E4972"),sQuery(id+"F0.wireOp",EDGE,"E4973"),sQuery(id+"F0.wireOp",EDGE,"E4974"),sQuery(id+"F0.wireOp",EDGE,"E4975"),sQuery(id+"F0.wireOp",EDGE,"E4976"),sQuery(id+"F0.wireOp",EDGE,"E4977"),sQuery(id+"F0.wireOp",EDGE,"E4978"),sQuery(id+"F0.wireOp",EDGE,"E4979"),sQuery(id+"F0.wireOp",EDGE,"E4980"),sQuery(id+"F0.wireOp",EDGE,"E4981"),sQuery(id+"F0.wireOp",EDGE,"E4982"),sQuery(id+"F0.wireOp",EDGE,"E4983"),sQuery(id+"F0.wireOp",EDGE,"E4984"),sQuery(id+"F0.wireOp",EDGE,"E4985"),sQuery(id+"F0.wireOp",EDGE,"E4986"),sQuery(id+"F0.wireOp",EDGE,"E4987"),sQuery(id+"F0.wireOp",EDGE,"E4988"),sQuery(id+"F0.wireOp",EDGE,"E4989"),sQuery(id+"F0.wireOp",EDGE,"E4990"),sQuery(id+"F0.wireOp",EDGE,"E4991"),sQuery(id+"F0.wireOp",EDGE,"E4992"),sQuery(id+"F0.wireOp",EDGE,"E4993"),sQuery(id+"F0.wireOp",EDGE,"E4994"),sQuery(id+"F0.wireOp",EDGE,"E4995"),sQuery(id+"F0.wireOp",EDGE,"E4996"),sQuery(id+"F0.wireOp",EDGE,"E4997"),sQuery(id+"F0.wireOp",EDGE,"E4998"),sQuery(id+"F0.wireOp",EDGE,"E4999"),sQuery(id+"F0.wireOp",EDGE,"E5000"),sQuery(id+"F0.wireOp",EDGE,"E5001"),sQuery(id+"F0.wireOp",EDGE,"E5002"),sQuery(id+"F0.wireOp",EDGE,"E5003"),sQuery(id+"F0.wireOp",EDGE,"E5004"),sQuery(id+"F0.wireOp",EDGE,"E5005"),sQuery(id+"F0.wireOp",EDGE,"E5006"),sQuery(id+"F0.wireOp",EDGE,"E5007"),sQuery(id+"F0.wireOp",EDGE,"E5008"),sQuery(id+"F0.wireOp",EDGE,"E5009"),sQuery(id+"F0.wireOp",EDGE,"E5010"),sQuery(id+"F0.wireOp",EDGE,"E5011"),sQuery(id+"F0.wireOp",EDGE,"E5012"),sQuery(id+"F0.wireOp",EDGE,"E5013"),sQuery(id+"F0.wireOp",EDGE,"E5014"),sQuery(id+"F0.wireOp",EDGE,"E5015"),sQuery(id+"F0.wireOp",EDGE,"E5016"),sQuery(id+"F0.wireOp",EDGE,"E5017"),sQuery(id+"F0.wireOp",EDGE,"E5018"),sQuery(id+"F0.wireOp",EDGE,"E5019"),sQuery(id+"F0.wireOp",EDGE,"E5020"),sQuery(id+"F0.wireOp",EDGE,"E5021"),sQuery(id+"F0.wireOp",EDGE,"E5022"),sQuery(id+"F0.wireOp",EDGE,"E5023"),sQuery(id+"F0.wireOp",EDGE,"E5024"),sQuery(id+"F0.wireOp",EDGE,"E5025"),sQuery(id+"F0.wireOp",EDGE,"E5026"),sQuery(id+"F0.wireOp",EDGE,"E5027"),sQuery(id+"F0.wireOp",EDGE,"E5028"),sQuery(id+"F0.wireOp",EDGE,"E5029"),sQuery(id+"F0.wireOp",EDGE,"E5030"),sQuery(id+"F0.wireOp",EDGE,"E5031"),sQuery(id+"F0.wireOp",EDGE,"E5032"),sQuery(id+"F0.wireOp",EDGE,"E5033"),sQuery(id+"F0.wireOp",EDGE,"E5034"),sQuery(id+"F0.wireOp",EDGE,"E5035"),sQuery(id+"F0.wireOp",EDGE,"E5036"),sQuery(id+"F0.wireOp",EDGE,"E5037"),sQuery(id+"F0.wireOp",EDGE,"E5038"),sQuery(id+"F0.wireOp",EDGE,"E5039"),sQuery(id+"F0.wireOp",EDGE,"E5040"),sQuery(id+"F0.wireOp",EDGE,"E5041"),sQuery(id+"F0.wireOp",EDGE,"E5042"),sQuery(id+"F0.wireOp",EDGE,"E5043"),sQuery(id+"F0.wireOp",EDGE,"E5044"),sQuery(id+"F0.wireOp",EDGE,"E5045"),sQuery(id+"F0.wireOp",EDGE,"E5046"),sQuery(id+"F0.wireOp",EDGE,"E5047"),sQuery(id+"F0.wireOp",EDGE,"E5048"),sQuery(id+"F0.wireOp",EDGE,"E5049"),sQuery(id+"F0.wireOp",EDGE,"E5050"),sQuery(id+"F0.wireOp",EDGE,"E5051"),sQuery(id+"F0.wireOp",EDGE,"E5052"),sQuery(id+"F0.wireOp",EDGE,"E5053"),sQuery(id+"F0.wireOp",EDGE,"E5054"),sQuery(id+"F0.wireOp",EDGE,"E5055"),sQuery(id+"F0.wireOp",EDGE,"E5056"),sQuery(id+"F0.wireOp",EDGE,"E5057"),sQuery(id+"F0.wireOp",EDGE,"E5058"),sQuery(id+"F0.wireOp",EDGE,"E5059"),sQuery(id+"F0.wireOp",EDGE,"E5060"),sQuery(id+"F0.wireOp",EDGE,"E5061"),sQuery(id+"F0.wireOp",EDGE,"E5062"),sQuery(id+"F0.wireOp",EDGE,"E5063"),sQuery(id+"F0.wireOp",EDGE,"E5064"),sQuery(id+"F0.wireOp",EDGE,"E5065"),sQuery(id+"F0.wireOp",EDGE,"E5066"),sQuery(id+"F0.wireOp",EDGE,"E5067"),sQuery(id+"F0.wireOp",EDGE,"E5068"),sQuery(id+"F0.wireOp",EDGE,"E5069"),sQuery(id+"F0.wireOp",EDGE,"E5070"),sQuery(id+"F0.wireOp",EDGE,"E5071"),sQuery(id+"F0.wireOp",EDGE,"E5072"),sQuery(id+"F0.wireOp",EDGE,"E5073"),sQuery(id+"F0.wireOp",EDGE,"E5074"),sQuery(id+"F0.wireOp",EDGE,"E5075"),sQuery(id+"F0.wireOp",EDGE,"E5076"),sQuery(id+"F0.wireOp",EDGE,"E5077"),sQuery(id+"F0.wireOp",EDGE,"E5078"),sQuery(id+"F0.wireOp",EDGE,"E5079"),sQuery(id+"F0.wireOp",EDGE,"E5080"),sQuery(id+"F0.wireOp",EDGE,"E5081"),sQuery(id+"F0.wireOp",EDGE,"E5082"),sQuery(id+"F0.wireOp",EDGE,"E5083"),sQuery(id+"F0.wireOp",EDGE,"E5084"),sQuery(id+"F0.wireOp",EDGE,"E5085"),sQuery(id+"F0.wireOp",EDGE,"E5086"),sQuery(id+"F0.wireOp",EDGE,"E5087"),sQuery(id+"F0.wireOp",EDGE,"E5088"),sQuery(id+"F0.wireOp",EDGE,"E5089"),sQuery(id+"F0.wireOp",EDGE,"E5090"),sQuery(id+"F0.wireOp",EDGE,"E5091"),sQuery(id+"F0.wireOp",EDGE,"E5092"),sQuery(id+"F0.wireOp",EDGE,"E5093"),sQuery(id+"F0.wireOp",EDGE,"E5094"),sQuery(id+"F0.wireOp",EDGE,"E5095"),sQuery(id+"F0.wireOp",EDGE,"E5096"),sQuery(id+"F0.wireOp",EDGE,"E5097"),sQuery(id+"F0.wireOp",EDGE,"E5098"),sQuery(id+"F0.wireOp",EDGE,"E5099"),sQuery(id+"F0.wireOp",EDGE,"E5100"),sQuery(id+"F0.wireOp",EDGE,"E5101"),sQuery(id+"F0.wireOp",EDGE,"E5102"),sQuery(id+"F0.wireOp",EDGE,"E5103"),sQuery(id+"F0.wireOp",EDGE,"E5104"),sQuery(id+"F0.wireOp",EDGE,"E5105"),sQuery(id+"F0.wireOp",EDGE,"E5106"),sQuery(id+"F0.wireOp",EDGE,"E5107"),sQuery(id+"F0.wireOp",EDGE,"E5108"),sQuery(id+"F0.wireOp",EDGE,"E5109"),sQuery(id+"F0.wireOp",EDGE,"E5110"),sQuery(id+"F0.wireOp",EDGE,"E5111"),sQuery(id+"F0.wireOp",EDGE,"E5112"),sQuery(id+"F0.wireOp",EDGE,"E5113"),sQuery(id+"F0.wireOp",EDGE,"E5114"),sQuery(id+"F0.wireOp",EDGE,"E5115"),sQuery(id+"F0.wireOp",EDGE,"E5116"),sQuery(id+"F0.wireOp",EDGE,"E5117"),sQuery(id+"F0.wireOp",EDGE,"E5118"),sQuery(id+"F0.wireOp",EDGE,"E5119"),sQuery(id+"F0.wireOp",EDGE,"E5120"),sQuery(id+"F0.wireOp",EDGE,"E5121"),sQuery(id+"F0.wireOp",EDGE,"E5122"),sQuery(id+"F0.wireOp",EDGE,"E5123"),sQuery(id+"F0.wireOp",EDGE,"E5124"),sQuery(id+"F0.wireOp",EDGE,"E5125"),sQuery(id+"F0.wireOp",EDGE,"E5126"),sQuery(id+"F0.wireOp",EDGE,"E5127"),sQuery(id+"F0.wireOp",EDGE,"E5128"),sQuery(id+"F0.wireOp",EDGE,"E5129"),sQuery(id+"F0.wireOp",EDGE,"E5130"),sQuery(id+"F0.wireOp",EDGE,"E5131"),sQuery(id+"F0.wireOp",EDGE,"E5132"),sQuery(id+"F0.wireOp",EDGE,"E5133"),sQuery(id+"F0.wireOp",EDGE,"E5134"),sQuery(id+"F0.wireOp",EDGE,"E5135"),sQuery(id+"F0.wireOp",EDGE,"E5136"),sQuery(id+"F0.wireOp",EDGE,"E5137"),sQuery(id+"F0.wireOp",EDGE,"E5138"),sQuery(id+"F0.wireOp",EDGE,"E5139"),sQuery(id+"F0.wireOp",EDGE,"E5140"),sQuery(id+"F0.wireOp",EDGE,"E5141"),sQuery(id+"F0.wireOp",EDGE,"E5142"),sQuery(id+"F0.wireOp",EDGE,"E5143"),sQuery(id+"F0.wireOp",EDGE,"E5144"),sQuery(id+"F0.wireOp",EDGE,"E5145"),sQuery(id+"F0.wireOp",EDGE,"E5146"),sQuery(id+"F0.wireOp",EDGE,"E5147"),sQuery(id+"F0.wireOp",EDGE,"E5148"),sQuery(id+"F0.wireOp",EDGE,"E5149"),sQuery(id+"F0.wireOp",EDGE,"E5150"),sQuery(id+"F0.wireOp",EDGE,"E5151"),sQuery(id+"F0.wireOp",EDGE,"E5152"),sQuery(id+"F0.wireOp",EDGE,"E5153"),sQuery(id+"F0.wireOp",EDGE,"E5154"),sQuery(id+"F0.wireOp",EDGE,"E5155"),sQuery(id+"F0.wireOp",EDGE,"E5156"),sQuery(id+"F0.wireOp",EDGE,"E5157"),sQuery(id+"F0.wireOp",EDGE,"E5158"),sQuery(id+"F0.wireOp",EDGE,"E5159"),sQuery(id+"F0.wireOp",EDGE,"E5160"),sQuery(id+"F0.wireOp",EDGE,"E5161"),sQuery(id+"F0.wireOp",EDGE,"E5162"),sQuery(id+"F0.wireOp",EDGE,"E5163"),sQuery(id+"F0.wireOp",EDGE,"E5164"),sQuery(id+"F0.wireOp",EDGE,"E5165"),sQuery(id+"F0.wireOp",EDGE,"E5166"),sQuery(id+"F0.wireOp",EDGE,"E5167"),sQuery(id+"F0.wireOp",EDGE,"E5168"),sQuery(id+"F0.wireOp",EDGE,"E5169"),sQuery(id+"F0.wireOp",EDGE,"E5170"),sQuery(id+"F0.wireOp",EDGE,"E5171"),sQuery(id+"F0.wireOp",EDGE,"E5172"),sQuery(id+"F0.wireOp",EDGE,"E5173"),sQuery(id+"F0.wireOp",EDGE,"E5174"),sQuery(id+"F0.wireOp",EDGE,"E5175"),sQuery(id+"F0.wireOp",EDGE,"E5176"),sQuery(id+"F0.wireOp",EDGE,"E5177"),sQuery(id+"F0.wireOp",EDGE,"E5178"),sQuery(id+"F0.wireOp",EDGE,"E5179"),sQuery(id+"F0.wireOp",EDGE,"E5180"),sQuery(id+"F0.wireOp",EDGE,"E5181"),sQuery(id+"F0.wireOp",EDGE,"E5182"),sQuery(id+"F0.wireOp",EDGE,"E5183"),sQuery(id+"F0.wireOp",EDGE,"E5184"),sQuery(id+"F0.wireOp",EDGE,"E5185"),sQuery(id+"F0.wireOp",EDGE,"E5186"),sQuery(id+"F0.wireOp",EDGE,"E5187"),sQuery(id+"F0.wireOp",EDGE,"E5188"),sQuery(id+"F0.wireOp",EDGE,"E5189"),sQuery(id+"F0.wireOp",EDGE,"E5190"),sQuery(id+"F0.wireOp",EDGE,"E5191"),sQuery(id+"F0.wireOp",EDGE,"E5192"),sQuery(id+"F0.wireOp",EDGE,"E5193"),sQuery(id+"F0.wireOp",EDGE,"E5194"),sQuery(id+"F0.wireOp",EDGE,"E5195"),sQuery(id+"F0.wireOp",EDGE,"E5196"),sQuery(id+"F0.wireOp",EDGE,"E5197"),sQuery(id+"F0.wireOp",EDGE,"E5198"),sQuery(id+"F0.wireOp",EDGE,"E5199"),sQuery(id+"F0.wireOp",EDGE,"E5200"),sQuery(id+"F0.wireOp",EDGE,"E5201"),sQuery(id+"F0.wireOp",EDGE,"E5202"),sQuery(id+"F0.wireOp",EDGE,"E5203"),sQuery(id+"F0.wireOp",EDGE,"E5204"),sQuery(id+"F0.wireOp",EDGE,"E5205"),sQuery(id+"F0.wireOp",EDGE,"E5206"),sQuery(id+"F0.wireOp",EDGE,"E5207"),sQuery(id+"F0.wireOp",EDGE,"E5208"),sQuery(id+"F0.wireOp",EDGE,"E5209"),sQuery(id+"F0.wireOp",EDGE,"E5210"),sQuery(id+"F0.wireOp",EDGE,"E5211"),sQuery(id+"F0.wireOp",EDGE,"E5212"),sQuery(id+"F0.wireOp",EDGE,"E5213"),sQuery(id+"F0.wireOp",EDGE,"E5214"),sQuery(id+"F0.wireOp",EDGE,"E5215"),sQuery(id+"F0.wireOp",EDGE,"E5216"),sQuery(id+"F0.wireOp",EDGE,"E5217"),sQuery(id+"F0.wireOp",EDGE,"E5218"),sQuery(id+"F0.wireOp",EDGE,"E5219"),sQuery(id+"F0.wireOp",EDGE,"E5220"),sQuery(id+"F0.wireOp",EDGE,"E5221"),sQuery(id+"F0.wireOp",EDGE,"E5222"),sQuery(id+"F0.wireOp",EDGE,"E5223"),sQuery(id+"F0.wireOp",EDGE,"E5224"),sQuery(id+"F0.wireOp",EDGE,"E5225"),sQuery(id+"F0.wireOp",EDGE,"E5226"),sQuery(id+"F0.wireOp",EDGE,"E5227"),sQuery(id+"F0.wireOp",EDGE,"E5228"),sQuery(id+"F0.wireOp",EDGE,"E5229"),sQuery(id+"F0.wireOp",EDGE,"E5230"),sQuery(id+"F0.wireOp",EDGE,"E5231"),sQuery(id+"F0.wireOp",EDGE,"E5232"),sQuery(id+"F0.wireOp",EDGE,"E5233"),sQuery(id+"F0.wireOp",EDGE,"E5234"),sQuery(id+"F0.wireOp",EDGE,"E5235"),sQuery(id+"F0.wireOp",EDGE,"E5236"),sQuery(id+"F0.wireOp",EDGE,"E5237"),sQuery(id+"F0.wireOp",EDGE,"E5238"),sQuery(id+"F0.wireOp",EDGE,"E5239"),sQuery(id+"F0.wireOp",EDGE,"E5240"),sQuery(id+"F0.wireOp",EDGE,"E5241"),sQuery(id+"F0.wireOp",EDGE,"E5242"),sQuery(id+"F0.wireOp",EDGE,"E5243"),sQuery(id+"F0.wireOp",EDGE,"E5244"),sQuery(id+"F0.wireOp",EDGE,"E5245"),sQuery(id+"F0.wireOp",EDGE,"E5246"),sQuery(id+"F0.wireOp",EDGE,"E5247"),sQuery(id+"F0.wireOp",EDGE,"E5248"),sQuery(id+"F0.wireOp",EDGE,"E5249"),sQuery(id+"F0.wireOp",EDGE,"E5250"),sQuery(id+"F0.wireOp",EDGE,"E5251"),sQuery(id+"F0.wireOp",EDGE,"E5252"),sQuery(id+"F0.wireOp",EDGE,"E5253"),sQuery(id+"F0.wireOp",EDGE,"E5254"),sQuery(id+"F0.wireOp",EDGE,"E5255"),sQuery(id+"F0.wireOp",EDGE,"E5256"),sQuery(id+"F0.wireOp",EDGE,"E5257"),sQuery(id+"F0.wireOp",EDGE,"E5258"),sQuery(id+"F0.wireOp",EDGE,"E5259"),sQuery(id+"F0.wireOp",EDGE,"E5260"),sQuery(id+"F0.wireOp",EDGE,"E5261"),sQuery(id+"F0.wireOp",EDGE,"E5262"),sQuery(id+"F0.wireOp",EDGE,"E5263"),sQuery(id+"F0.wireOp",EDGE,"E5264"),sQuery(id+"F0.wireOp",EDGE,"E5265"),sQuery(id+"F0.wireOp",EDGE,"E5266"),sQuery(id+"F0.wireOp",EDGE,"E5267"),sQuery(id+"F0.wireOp",EDGE,"E5268"),sQuery(id+"F0.wireOp",EDGE,"E5269"),sQuery(id+"F0.wireOp",EDGE,"E5270"),sQuery(id+"F0.wireOp",EDGE,"E5271"),sQuery(id+"F0.wireOp",EDGE,"E5272"),sQuery(id+"F0.wireOp",EDGE,"E5273"),sQuery(id+"F0.wireOp",EDGE,"E5274"),sQuery(id+"F0.wireOp",EDGE,"E5275"),sQuery(id+"F0.wireOp",EDGE,"E5276"),sQuery(id+"F0.wireOp",EDGE,"E5277"),sQuery(id+"F0.wireOp",EDGE,"E5278"),sQuery(id+"F0.wireOp",EDGE,"E5279"),sQuery(id+"F0.wireOp",EDGE,"E5280"),sQuery(id+"F0.wireOp",EDGE,"E5281"),sQuery(id+"F0.wireOp",EDGE,"E5282"),sQuery(id+"F0.wireOp",EDGE,"E5283"),sQuery(id+"F0.wireOp",EDGE,"E5284"),sQuery(id+"F0.wireOp",EDGE,"E5285"),sQuery(id+"F0.wireOp",EDGE,"E5286"),sQuery(id+"F0.wireOp",EDGE,"E5287"),sQuery(id+"F0.wireOp",EDGE,"E5288"),sQuery(id+"F0.wireOp",EDGE,"E5289"),sQuery(id+"F0.wireOp",EDGE,"E5290"),sQuery(id+"F0.wireOp",EDGE,"E5291"),sQuery(id+"F0.wireOp",EDGE,"E5292"),sQuery(id+"F0.wireOp",EDGE,"E5293"),sQuery(id+"F0.wireOp",EDGE,"E5294"),sQuery(id+"F0.wireOp",EDGE,"E5295"),sQuery(id+"F0.wireOp",EDGE,"E5296"),sQuery(id+"F0.wireOp",EDGE,"E5297"),sQuery(id+"F0.wireOp",EDGE,"E5298"),sQuery(id+"F0.wireOp",EDGE,"E5299"),sQuery(id+"F0.wireOp",EDGE,"E5300"),sQuery(id+"F0.wireOp",EDGE,"E5301"),sQuery(id+"F0.wireOp",EDGE,"E5302"),sQuery(id+"F0.wireOp",EDGE,"E5303"),sQuery(id+"F0.wireOp",EDGE,"E5304"),sQuery(id+"F0.wireOp",EDGE,"E5305"),sQuery(id+"F0.wireOp",EDGE,"E5306"),sQuery(id+"F0.wireOp",EDGE,"E5307"),sQuery(id+"F0.wireOp",EDGE,"E5308"),sQuery(id+"F0.wireOp",EDGE,"E5309"),sQuery(id+"F0.wireOp",EDGE,"E5310"),sQuery(id+"F0.wireOp",EDGE,"E5311"),sQuery(id+"F0.wireOp",EDGE,"E5312"),sQuery(id+"F0.wireOp",EDGE,"E5313"),sQuery(id+"F0.wireOp",EDGE,"E5314"),sQuery(id+"F0.wireOp",EDGE,"E5315"),sQuery(id+"F0.wireOp",EDGE,"E5316"),sQuery(id+"F0.wireOp",EDGE,"E5317"),sQuery(id+"F0.wireOp",EDGE,"E5318"),sQuery(id+"F0.wireOp",EDGE,"E5319"),sQuery(id+"F0.wireOp",EDGE,"E5320"),sQuery(id+"F0.wireOp",EDGE,"E5321"),sQuery(id+"F0.wireOp",EDGE,"E5322"),sQuery(id+"F0.wireOp",EDGE,"E5323"),sQuery(id+"F0.wireOp",EDGE,"E5324"),sQuery(id+"F0.wireOp",EDGE,"E5325"),sQuery(id+"F0.wireOp",EDGE,"E5326"),sQuery(id+"F0.wireOp",EDGE,"E5327"),sQuery(id+"F0.wireOp",EDGE,"E5328"),sQuery(id+"F0.wireOp",EDGE,"E5329"),sQuery(id+"F0.wireOp",EDGE,"E5330"),sQuery(id+"F0.wireOp",EDGE,"E5331"),sQuery(id+"F0.wireOp",EDGE,"E5332"),sQuery(id+"F0.wireOp",EDGE,"E5333"),sQuery(id+"F0.wireOp",EDGE,"E5334"),sQuery(id+"F0.wireOp",EDGE,"E5335"),sQuery(id+"F0.wireOp",EDGE,"E5336"),sQuery(id+"F0.wireOp",EDGE,"E5337"),sQuery(id+"F0.wireOp",EDGE,"E5338"),sQuery(id+"F0.wireOp",EDGE,"E5339"),sQuery(id+"F0.wireOp",EDGE,"E5340"),sQuery(id+"F0.wireOp",EDGE,"E5341"),sQuery(id+"F0.wireOp",EDGE,"E5342"),sQuery(id+"F0.wireOp",EDGE,"E5343"),sQuery(id+"F0.wireOp",EDGE,"E5344"),sQuery(id+"F0.wireOp",EDGE,"E5345"),sQuery(id+"F0.wireOp",EDGE,"E5346"),sQuery(id+"F0.wireOp",EDGE,"E5347"),sQuery(id+"F0.wireOp",EDGE,"E5348"),sQuery(id+"F0.wireOp",EDGE,"E5349"),sQuery(id+"F0.wireOp",EDGE,"E5350"),sQuery(id+"F0.wireOp",EDGE,"E5351"),sQuery(id+"F0.wireOp",EDGE,"E5352"),sQuery(id+"F0.wireOp",EDGE,"E5353"),sQuery(id+"F0.wireOp",EDGE,"E5354"),sQuery(id+"F0.wireOp",EDGE,"E5355"),sQuery(id+"F0.wireOp",EDGE,"E5356"),sQuery(id+"F0.wireOp",EDGE,"E5357"),sQuery(id+"F0.wireOp",EDGE,"E5358"),sQuery(id+"F0.wireOp",EDGE,"E5359"),sQuery(id+"F0.wireOp",EDGE,"E5360"),sQuery(id+"F0.wireOp",EDGE,"E5361"),sQuery(id+"F0.wireOp",EDGE,"E5362"),sQuery(id+"F0.wireOp",EDGE,"E5363"),sQuery(id+"F0.wireOp",EDGE,"E5364"),sQuery(id+"F0.wireOp",EDGE,"E5365"),sQuery(id+"F0.wireOp",EDGE,"E5366"),sQuery(id+"F0.wireOp",EDGE,"E5367"),sQuery(id+"F0.wireOp",EDGE,"E5368"),sQuery(id+"F0.wireOp",EDGE,"E5369"),sQuery(id+"F0.wireOp",EDGE,"E5370"),sQuery(id+"F0.wireOp",EDGE,"E5371"),sQuery(id+"F0.wireOp",EDGE,"E5372"),sQuery(id+"F0.wireOp",EDGE,"E5373"),sQuery(id+"F0.wireOp",EDGE,"E5374"),sQuery(id+"F0.wireOp",EDGE,"E5375"),sQuery(id+"F0.wireOp",EDGE,"E5376"),sQuery(id+"F0.wireOp",EDGE,"E5377"),sQuery(id+"F0.wireOp",EDGE,"E5378"),sQuery(id+"F0.wireOp",EDGE,"E5379"),sQuery(id+"F0.wireOp",EDGE,"E5380"),sQuery(id+"F0.wireOp",EDGE,"E5381"),sQuery(id+"F0.wireOp",EDGE,"E5382"),sQuery(id+"F0.wireOp",EDGE,"E5383"),sQuery(id+"F0.wireOp",EDGE,"E5384"),sQuery(id+"F0.wireOp",EDGE,"E5385"),sQuery(id+"F0.wireOp",EDGE,"E5386"),sQuery(id+"F0.wireOp",EDGE,"E5387"),sQuery(id+"F0.wireOp",EDGE,"E5388"),sQuery(id+"F0.wireOp",EDGE,"E5389"),sQuery(id+"F0.wireOp",EDGE,"E5390"),sQuery(id+"F0.wireOp",EDGE,"E5391"),sQuery(id+"F0.wireOp",EDGE,"E5392"),sQuery(id+"F0.wireOp",EDGE,"E5393"),sQuery(id+"F0.wireOp",EDGE,"E5394"),sQuery(id+"F0.wireOp",EDGE,"E5395"),sQuery(id+"F0.wireOp",EDGE,"E5396"),sQuery(id+"F0.wireOp",EDGE,"E5397"),sQuery(id+"F0.wireOp",EDGE,"E5398"),sQuery(id+"F0.wireOp",EDGE,"E5399"),sQuery(id+"F0.wireOp",EDGE,"E5400"),sQuery(id+"F0.wireOp",EDGE,"E5401"),sQuery(id+"F0.wireOp",EDGE,"E5402"),sQuery(id+"F0.wireOp",EDGE,"E5403"),sQuery(id+"F0.wireOp",EDGE,"E5404"),sQuery(id+"F0.wireOp",EDGE,"E5405"),sQuery(id+"F0.wireOp",EDGE,"E5406"),sQuery(id+"F0.wireOp",EDGE,"E5407"),sQuery(id+"F0.wireOp",EDGE,"E5408"),sQuery(id+"F0.wireOp",EDGE,"E5409"),sQuery(id+"F0.wireOp",EDGE,"E5410"),sQuery(id+"F0.wireOp",EDGE,"E5411"),sQuery(id+"F0.wireOp",EDGE,"E5412"),sQuery(id+"F0.wireOp",EDGE,"E5413"),sQuery(id+"F0.wireOp",EDGE,"E5414"),sQuery(id+"F0.wireOp",EDGE,"E5415"),sQuery(id+"F0.wireOp",EDGE,"E5416"),sQuery(id+"F0.wireOp",EDGE,"E5417"),sQuery(id+"F0.wireOp",EDGE,"E5418"),sQuery(id+"F0.wireOp",EDGE,"E5419"),sQuery(id+"F0.wireOp",EDGE,"E5420"),sQuery(id+"F0.wireOp",EDGE,"E5421"),sQuery(id+"F0.wireOp",EDGE,"E5422"),sQuery(id+"F0.wireOp",EDGE,"E5423"),sQuery(id+"F0.wireOp",EDGE,"E5424"),sQuery(id+"F0.wireOp",EDGE,"E5425"),sQuery(id+"F0.wireOp",EDGE,"E5426"),sQuery(id+"F0.wireOp",EDGE,"E5427"),sQuery(id+"F0.wireOp",EDGE,"E5428"),sQuery(id+"F0.wireOp",EDGE,"E5429"),sQuery(id+"F0.wireOp",EDGE,"E5430"),sQuery(id+"F0.wireOp",EDGE,"E5431"),sQuery(id+"F0.wireOp",EDGE,"E5432"),sQuery(id+"F0.wireOp",EDGE,"E5433"),sQuery(id+"F0.wireOp",EDGE,"E5434"),sQuery(id+"F0.wireOp",EDGE,"E5435"),sQuery(id+"F0.wireOp",EDGE,"E5436"),sQuery(id+"F0.wireOp",EDGE,"E5437"),sQuery(id+"F0.wireOp",EDGE,"E5438"),sQuery(id+"F0.wireOp",EDGE,"E5439"),sQuery(id+"F0.wireOp",EDGE,"E5440"),sQuery(id+"F0.wireOp",EDGE,"E5441"),sQuery(id+"F0.wireOp",EDGE,"E5442"),sQuery(id+"F0.wireOp",EDGE,"E5443"),sQuery(id+"F0.wireOp",EDGE,"E5444"),sQuery(id+"F0.wireOp",EDGE,"E5445"),sQuery(id+"F0.wireOp",EDGE,"E5446"),sQuery(id+"F0.wireOp",EDGE,"E5447"),sQuery(id+"F0.wireOp",EDGE,"E5448"),sQuery(id+"F0.wireOp",EDGE,"E5449"),sQuery(id+"F0.wireOp",EDGE,"E5450"),sQuery(id+"F0.wireOp",EDGE,"E5451"),sQuery(id+"F0.wireOp",EDGE,"E5452"),sQuery(id+"F0.wireOp",EDGE,"E5453"),sQuery(id+"F0.wireOp",EDGE,"E5454"),sQuery(id+"F0.wireOp",EDGE,"E5455"),sQuery(id+"F0.wireOp",EDGE,"E5456"),sQuery(id+"F0.wireOp",EDGE,"E5457"),sQuery(id+"F0.wireOp",EDGE,"E5458"),sQuery(id+"F0.wireOp",EDGE,"E5459"),sQuery(id+"F0.wireOp",EDGE,"E5460"),sQuery(id+"F0.wireOp",EDGE,"E5461"),sQuery(id+"F0.wireOp",EDGE,"E5462"),sQuery(id+"F0.wireOp",EDGE,"E5463"),sQuery(id+"F0.wireOp",EDGE,"E5464"),sQuery(id+"F0.wireOp",EDGE,"E5465"),sQuery(id+"F0.wireOp",EDGE,"E5466"),sQuery(id+"F0.wireOp",EDGE,"E5467"),sQuery(id+"F0.wireOp",EDGE,"E5468"),sQuery(id+"F0.wireOp",EDGE,"E5469"),sQuery(id+"F0.wireOp",EDGE,"E5470"),sQuery(id+"F0.wireOp",EDGE,"E5471"),sQuery(id+"F0.wireOp",EDGE,"E5472"),sQuery(id+"F0.wireOp",EDGE,"E5473"),sQuery(id+"F0.wireOp",EDGE,"E5474"),sQuery(id+"F0.wireOp",EDGE,"E5475"),sQuery(id+"F0.wireOp",EDGE,"E5476"),sQuery(id+"F0.wireOp",EDGE,"E5477"),sQuery(id+"F0.wireOp",EDGE,"E5478"),sQuery(id+"F0.wireOp",EDGE,"E5479"),sQuery(id+"F0.wireOp",EDGE,"E5480"),sQuery(id+"F0.wireOp",EDGE,"E5481"),sQuery(id+"F0.wireOp",EDGE,"E5482"),sQuery(id+"F0.wireOp",EDGE,"E5483"),sQuery(id+"F0.wireOp",EDGE,"E5484"),sQuery(id+"F0.wireOp",EDGE,"E5485"),sQuery(id+"F0.wireOp",EDGE,"E5486"),sQuery(id+"F0.wireOp",EDGE,"E5487"),sQuery(id+"F0.wireOp",EDGE,"E5488"),sQuery(id+"F0.wireOp",EDGE,"E5489"),sQuery(id+"F0.wireOp",EDGE,"E5490"),sQuery(id+"F0.wireOp",EDGE,"E5491"),sQuery(id+"F0.wireOp",EDGE,"E5492"),sQuery(id+"F0.wireOp",EDGE,"E5493"),sQuery(id+"F0.wireOp",EDGE,"E5494"),sQuery(id+"F0.wireOp",EDGE,"E5495"),sQuery(id+"F0.wireOp",EDGE,"E5496"),sQuery(id+"F0.wireOp",EDGE,"E5497"),sQuery(id+"F0.wireOp",EDGE,"E5498"),sQuery(id+"F0.wireOp",EDGE,"E5499"),sQuery(id+"F0.wireOp",EDGE,"E5500"),sQuery(id+"F0.wireOp",EDGE,"E5501"),sQuery(id+"F0.wireOp",EDGE,"E5502"),sQuery(id+"F0.wireOp",EDGE,"E5503"),sQuery(id+"F0.wireOp",EDGE,"E5504"),sQuery(id+"F0.wireOp",EDGE,"E5505"),sQuery(id+"F0.wireOp",EDGE,"E5506"),sQuery(id+"F0.wireOp",EDGE,"E5507"),sQuery(id+"F0.wireOp",EDGE,"E5508"),sQuery(id+"F0.wireOp",EDGE,"E5509"),sQuery(id+"F0.wireOp",EDGE,"E5510"),sQuery(id+"F0.wireOp",EDGE,"E5511"),sQuery(id+"F0.wireOp",EDGE,"E5512"),sQuery(id+"F0.wireOp",EDGE,"E5513"),sQuery(id+"F0.wireOp",EDGE,"E5514"),sQuery(id+"F0.wireOp",EDGE,"E5515"),sQuery(id+"F0.wireOp",EDGE,"E5516"),sQuery(id+"F0.wireOp",EDGE,"E5517"),sQuery(id+"F0.wireOp",EDGE,"E5518"),sQuery(id+"F0.wireOp",EDGE,"E5519"),sQuery(id+"F0.wireOp",EDGE,"E5520"),sQuery(id+"F0.wireOp",EDGE,"E5521"),sQuery(id+"F0.wireOp",EDGE,"E5522"),sQuery(id+"F0.wireOp",EDGE,"E5523"),sQuery(id+"F0.wireOp",EDGE,"E5524"),sQuery(id+"F0.wireOp",EDGE,"E5525"),sQuery(id+"F0.wireOp",EDGE,"E5526"),sQuery(id+"F0.wireOp",EDGE,"E5527"),sQuery(id+"F0.wireOp",EDGE,"E5528"),sQuery(id+"F0.wireOp",EDGE,"E5529"),sQuery(id+"F0.wireOp",EDGE,"E5530"),sQuery(id+"F0.wireOp",EDGE,"E5531"),sQuery(id+"F0.wireOp",EDGE,"E5532"),sQuery(id+"F0.wireOp",EDGE,"E5533"),sQuery(id+"F0.wireOp",EDGE,"E5534"),sQuery(id+"F0.wireOp",EDGE,"E5535"),sQuery(id+"F0.wireOp",EDGE,"E5536"),sQuery(id+"F0.wireOp",EDGE,"E5537"),sQuery(id+"F0.wireOp",EDGE,"E5538"),sQuery(id+"F0.wireOp",EDGE,"E5539"),sQuery(id+"F0.wireOp",EDGE,"E5540"),sQuery(id+"F0.wireOp",EDGE,"E5541"),sQuery(id+"F0.wireOp",EDGE,"E5542"),sQuery(id+"F0.wireOp",EDGE,"E5543"),sQuery(id+"F0.wireOp",EDGE,"E5544"),sQuery(id+"F0.wireOp",EDGE,"E5545"),sQuery(id+"F0.wireOp",EDGE,"E5546"),sQuery(id+"F0.wireOp",EDGE,"E5547"),sQuery(id+"F0.wireOp",EDGE,"E5548"),sQuery(id+"F0.wireOp",EDGE,"E5549"),sQuery(id+"F0.wireOp",EDGE,"E5550"),sQuery(id+"F0.wireOp",EDGE,"E5551"),sQuery(id+"F0.wireOp",EDGE,"E5552"),sQuery(id+"F0.wireOp",EDGE,"E5553"),sQuery(id+"F0.wireOp",EDGE,"E5554"),sQuery(id+"F0.wireOp",EDGE,"E5555"),sQuery(id+"F0.wireOp",EDGE,"E5556"),sQuery(id+"F0.wireOp",EDGE,"E5557"),sQuery(id+"F0.wireOp",EDGE,"E5558"),sQuery(id+"F0.wireOp",EDGE,"E5559"),sQuery(id+"F0.wireOp",EDGE,"E5560"),sQuery(id+"F0.wireOp",EDGE,"E5561"),sQuery(id+"F0.wireOp",EDGE,"E5562"),sQuery(id+"F0.wireOp",EDGE,"E5563"),sQuery(id+"F0.wireOp",EDGE,"E5564"),sQuery(id+"F0.wireOp",EDGE,"E5565"),sQuery(id+"F0.wireOp",EDGE,"E5566"),sQuery(id+"F0.wireOp",EDGE,"E5567"),sQuery(id+"F0.wireOp",EDGE,"E5568"),sQuery(id+"F0.wireOp",EDGE,"E5569"),sQuery(id+"F0.wireOp",EDGE,"E5570"),sQuery(id+"F0.wireOp",EDGE,"E5571"),sQuery(id+"F0.wireOp",EDGE,"E5572"),sQuery(id+"F0.wireOp",EDGE,"E5573"),sQuery(id+"F0.wireOp",EDGE,"E5574"),sQuery(id+"F0.wireOp",EDGE,"E5575"),sQuery(id+"F0.wireOp",EDGE,"E5576"),sQuery(id+"F0.wireOp",EDGE,"E5577"),sQuery(id+"F0.wireOp",EDGE,"E5578"),sQuery(id+"F0.wireOp",EDGE,"E5579"),sQuery(id+"F0.wireOp",EDGE,"E5580"),sQuery(id+"F0.wireOp",EDGE,"E5581"),sQuery(id+"F0.wireOp",EDGE,"E5582"),sQuery(id+"F0.wireOp",EDGE,"E5583"),sQuery(id+"F0.wireOp",EDGE,"E5584"),sQuery(id+"F0.wireOp",EDGE,"E5585"),sQuery(id+"F0.wireOp",EDGE,"E5586"),sQuery(id+"F0.wireOp",EDGE,"E5587"),sQuery(id+"F0.wireOp",EDGE,"E5588"),sQuery(id+"F0.wireOp",EDGE,"E5589"),sQuery(id+"F0.wireOp",EDGE,"E5590"),sQuery(id+"F0.wireOp",EDGE,"E5591"),sQuery(id+"F0.wireOp",EDGE,"E5592"),sQuery(id+"F0.wireOp",EDGE,"E5593"),sQuery(id+"F0.wireOp",EDGE,"E5594"),sQuery(id+"F0.wireOp",EDGE,"E5595"),sQuery(id+"F0.wireOp",EDGE,"E5596"),sQuery(id+"F0.wireOp",EDGE,"E5597"),sQuery(id+"F0.wireOp",EDGE,"E5598"),sQuery(id+"F0.wireOp",EDGE,"E5599"),sQuery(id+"F0.wireOp",EDGE,"E5600"),sQuery(id+"F0.wireOp",EDGE,"E5601"),sQuery(id+"F0.wireOp",EDGE,"E5602"),sQuery(id+"F0.wireOp",EDGE,"E5603"),sQuery(id+"F0.wireOp",EDGE,"E5604"),sQuery(id+"F0.wireOp",EDGE,"E5605"),sQuery(id+"F0.wireOp",EDGE,"E5606"),sQuery(id+"F0.wireOp",EDGE,"E5607"),sQuery(id+"F0.wireOp",EDGE,"E5608"),sQuery(id+"F0.wireOp",EDGE,"E5609"),sQuery(id+"F0.wireOp",EDGE,"E5610"),sQuery(id+"F0.wireOp",EDGE,"E5611"),sQuery(id+"F0.wireOp",EDGE,"E5612"),sQuery(id+"F0.wireOp",EDGE,"E5613"),sQuery(id+"F0.wireOp",EDGE,"E5614"),sQuery(id+"F0.wireOp",EDGE,"E5615"),sQuery(id+"F0.wireOp",EDGE,"E5616"),sQuery(id+"F0.wireOp",EDGE,"E5617"),sQuery(id+"F0.wireOp",EDGE,"E5618"),sQuery(id+"F0.wireOp",EDGE,"E5619"),sQuery(id+"F0.wireOp",EDGE,"E5620"),sQuery(id+"F0.wireOp",EDGE,"E5621"),sQuery(id+"F0.wireOp",EDGE,"E5622"),sQuery(id+"F0.wireOp",EDGE,"E5623"),sQuery(id+"F0.wireOp",EDGE,"E5624"),sQuery(id+"F0.wireOp",EDGE,"E5625"),sQuery(id+"F0.wireOp",EDGE,"E5626"),sQuery(id+"F0.wireOp",EDGE,"E5627"),sQuery(id+"F0.wireOp",EDGE,"E5628"),sQuery(id+"F0.wireOp",EDGE,"E5629"),sQuery(id+"F0.wireOp",EDGE,"E5630"),sQuery(id+"F0.wireOp",EDGE,"E5631"),sQuery(id+"F0.wireOp",EDGE,"E5632"),sQuery(id+"F0.wireOp",EDGE,"E5633"),sQuery(id+"F0.wireOp",EDGE,"E5634"),sQuery(id+"F0.wireOp",EDGE,"E5635"),sQuery(id+"F0.wireOp",EDGE,"E5636"),sQuery(id+"F0.wireOp",EDGE,"E5637"),sQuery(id+"F0.wireOp",EDGE,"E5638"),sQuery(id+"F0.wireOp",EDGE,"E5639"),sQuery(id+"F0.wireOp",EDGE,"E5640"),sQuery(id+"F0.wireOp",EDGE,"E5641"),sQuery(id+"F0.wireOp",EDGE,"E5642"),sQuery(id+"F0.wireOp",EDGE,"E5643"),sQuery(id+"F0.wireOp",EDGE,"E5644"),sQuery(id+"F0.wireOp",EDGE,"E5645"),sQuery(id+"F0.wireOp",EDGE,"E5646"),sQuery(id+"F0.wireOp",EDGE,"E5647"),sQuery(id+"F0.wireOp",EDGE,"E5648"),sQuery(id+"F0.wireOp",EDGE,"E5649"),sQuery(id+"F0.wireOp",EDGE,"E5650"),sQuery(id+"F0.wireOp",EDGE,"E5651"),sQuery(id+"F0.wireOp",EDGE,"E5652"),sQuery(id+"F0.wireOp",EDGE,"E5653"),sQuery(id+"F0.wireOp",EDGE,"E5654"),sQuery(id+"F0.wireOp",EDGE,"E5655"),sQuery(id+"F0.wireOp",EDGE,"E5656"),sQuery(id+"F0.wireOp",EDGE,"E5657"),sQuery(id+"F0.wireOp",EDGE,"E5658"),sQuery(id+"F0.wireOp",EDGE,"E5659"),sQuery(id+"F0.wireOp",EDGE,"E5660"),sQuery(id+"F0.wireOp",EDGE,"E5661"),sQuery(id+"F0.wireOp",EDGE,"E5662"),sQuery(id+"F0.wireOp",EDGE,"E5663"),sQuery(id+"F0.wireOp",EDGE,"E5664"),sQuery(id+"F0.wireOp",EDGE,"E5665"),sQuery(id+"F0.wireOp",EDGE,"E5666"),sQuery(id+"F0.wireOp",EDGE,"E5667"),sQuery(id+"F0.wireOp",EDGE,"E5668"),sQuery(id+"F0.wireOp",EDGE,"E5669"),sQuery(id+"F0.wireOp",EDGE,"E5670"),sQuery(id+"F0.wireOp",EDGE,"E5671"),sQuery(id+"F0.wireOp",EDGE,"E5672"),sQuery(id+"F0.wireOp",EDGE,"E5673"),sQuery(id+"F0.wireOp",EDGE,"E5674"),sQuery(id+"F0.wireOp",EDGE,"E5675"),sQuery(id+"F0.wireOp",EDGE,"E5676"),sQuery(id+"F0.wireOp",EDGE,"E5677"),sQuery(id+"F0.wireOp",EDGE,"E5678"),sQuery(id+"F0.wireOp",EDGE,"E5679"),sQuery(id+"F0.wireOp",EDGE,"E5680"),sQuery(id+"F0.wireOp",EDGE,"E5681"),sQuery(id+"F0.wireOp",EDGE,"E5682"),sQuery(id+"F0.wireOp",EDGE,"E5683"),sQuery(id+"F0.wireOp",EDGE,"E5684"),sQuery(id+"F0.wireOp",EDGE,"E5685"),sQuery(id+"F0.wireOp",EDGE,"E5686"),sQuery(id+"F0.wireOp",EDGE,"E5687"),sQuery(id+"F0.wireOp",EDGE,"E5688"),sQuery(id+"F0.wireOp",EDGE,"E5689"),sQuery(id+"F0.wireOp",EDGE,"E5690"),sQuery(id+"F0.wireOp",EDGE,"E5691"),sQuery(id+"F0.wireOp",EDGE,"E5692"),sQuery(id+"F0.wireOp",EDGE,"E5693"),sQuery(id+"F0.wireOp",EDGE,"E5694"),sQuery(id+"F0.wireOp",EDGE,"E5695"),sQuery(id+"F0.wireOp",EDGE,"E5696"),sQuery(id+"F0.wireOp",EDGE,"E5697"),sQuery(id+"F0.wireOp",EDGE,"E5698"),sQuery(id+"F0.wireOp",EDGE,"E5699"),sQuery(id+"F0.wireOp",EDGE,"E5700"),sQuery(id+"F0.wireOp",EDGE,"E5701"),sQuery(id+"F0.wireOp",EDGE,"E5702"),sQuery(id+"F0.wireOp",EDGE,"E5703"),sQuery(id+"F0.wireOp",EDGE,"E5704"),sQuery(id+"F0.wireOp",EDGE,"E5705"),sQuery(id+"F0.wireOp",EDGE,"E5706"),sQuery(id+"F0.wireOp",EDGE,"E5707"),sQuery(id+"F0.wireOp",EDGE,"E5708"),sQuery(id+"F0.wireOp",EDGE,"E5709"),sQuery(id+"F0.wireOp",EDGE,"E5710"),sQuery(id+"F0.wireOp",EDGE,"E5711"),sQuery(id+"F0.wireOp",EDGE,"E5712"),sQuery(id+"F0.wireOp",EDGE,"E5713"),sQuery(id+"F0.wireOp",EDGE,"E5714"),sQuery(id+"F0.wireOp",EDGE,"E5715"),sQuery(id+"F0.wireOp",EDGE,"E5716"),sQuery(id+"F0.wireOp",EDGE,"E5717"),sQuery(id+"F0.wireOp",EDGE,"E5718"),sQuery(id+"F0.wireOp",EDGE,"E5719"),sQuery(id+"F0.wireOp",EDGE,"E5720"),sQuery(id+"F0.wireOp",EDGE,"E5721"),sQuery(id+"F0.wireOp",EDGE,"E5722"),sQuery(id+"F0.wireOp",EDGE,"E5723"),sQuery(id+"F0.wireOp",EDGE,"E5724"),sQuery(id+"F0.wireOp",EDGE,"E5725"),sQuery(id+"F0.wireOp",EDGE,"E5726"),sQuery(id+"F0.wireOp",EDGE,"E5727"),sQuery(id+"F0.wireOp",EDGE,"E5728"),sQuery(id+"F0.wireOp",EDGE,"E5729"),sQuery(id+"F0.wireOp",EDGE,"E5730"),sQuery(id+"F0.wireOp",EDGE,"E5731"),sQuery(id+"F0.wireOp",EDGE,"E5732"),sQuery(id+"F0.wireOp",EDGE,"E5733"),sQuery(id+"F0.wireOp",EDGE,"E5734"),sQuery(id+"F0.wireOp",EDGE,"E5735"),sQuery(id+"F0.wireOp",EDGE,"E5736"),sQuery(id+"F0.wireOp",EDGE,"E5737"),sQuery(id+"F0.wireOp",EDGE,"E5738"),sQuery(id+"F0.wireOp",EDGE,"E5739"),sQuery(id+"F0.wireOp",EDGE,"E5740"),sQuery(id+"F0.wireOp",EDGE,"E5741"),sQuery(id+"F0.wireOp",EDGE,"E5742"),sQuery(id+"F0.wireOp",EDGE,"E5743"),sQuery(id+"F0.wireOp",EDGE,"E5744"),sQuery(id+"F0.wireOp",EDGE,"E5745"),sQuery(id+"F0.wireOp",EDGE,"E5746"),sQuery(id+"F0.wireOp",EDGE,"E5747"),sQuery(id+"F0.wireOp",EDGE,"E5748"),sQuery(id+"F0.wireOp",EDGE,"E5749"),sQuery(id+"F0.wireOp",EDGE,"E5750"),sQuery(id+"F0.wireOp",EDGE,"E5751"),sQuery(id+"F0.wireOp",EDGE,"E5752"),sQuery(id+"F0.wireOp",EDGE,"E5753"),sQuery(id+"F0.wireOp",EDGE,"E5754"),sQuery(id+"F0.wireOp",EDGE,"E5755"),sQuery(id+"F0.wireOp",EDGE,"E5756"),sQuery(id+"F0.wireOp",EDGE,"E5757"),sQuery(id+"F0.wireOp",EDGE,"E5758"),sQuery(id+"F0.wireOp",EDGE,"E5759"),sQuery(id+"F0.wireOp",EDGE,"E5760"),sQuery(id+"F0.wireOp",EDGE,"E5761"),sQuery(id+"F0.wireOp",EDGE,"E5762"),sQuery(id+"F0.wireOp",EDGE,"E5763"),sQuery(id+"F0.wireOp",EDGE,"E5764"),sQuery(id+"F0.wireOp",EDGE,"E5765"),sQuery(id+"F0.wireOp",EDGE,"E5766"),sQuery(id+"F0.wireOp",EDGE,"E5767"),sQuery(id+"F0.wireOp",EDGE,"E5768"),sQuery(id+"F0.wireOp",EDGE,"E5769"),sQuery(id+"F0.wireOp",EDGE,"E5770"),sQuery(id+"F0.wireOp",EDGE,"E5771"),sQuery(id+"F0.wireOp",EDGE,"E5772"),sQuery(id+"F0.wireOp",EDGE,"E5773"),sQuery(id+"F0.wireOp",EDGE,"E5774"),sQuery(id+"F0.wireOp",EDGE,"E5775"),sQuery(id+"F0.wireOp",EDGE,"E5776"),sQuery(id+"F0.wireOp",EDGE,"E5777"),sQuery(id+"F0.wireOp",EDGE,"E5778"),sQuery(id+"F0.wireOp",EDGE,"E5779"),sQuery(id+"F0.wireOp",EDGE,"E5780"),sQuery(id+"F0.wireOp",EDGE,"E5781"),sQuery(id+"F0.wireOp",EDGE,"E5782"),sQuery(id+"F0.wireOp",EDGE,"E5783"),sQuery(id+"F0.wireOp",EDGE,"E5784"),sQuery(id+"F0.wireOp",EDGE,"E5785"),sQuery(id+"F0.wireOp",EDGE,"E5786"),sQuery(id+"F0.wireOp",EDGE,"E5787"),sQuery(id+"F0.wireOp",EDGE,"E5788"),sQuery(id+"F0.wireOp",EDGE,"E5789"),sQuery(id+"F0.wireOp",EDGE,"E5790"),sQuery(id+"F0.wireOp",EDGE,"E5791"),sQuery(id+"F0.wireOp",EDGE,"E5792"),sQuery(id+"F0.wireOp",EDGE,"E5793"),sQuery(id+"F0.wireOp",EDGE,"E5794"),sQuery(id+"F0.wireOp",EDGE,"E5795"),sQuery(id+"F0.wireOp",EDGE,"E5796"),sQuery(id+"F0.wireOp",EDGE,"E5797"),sQuery(id+"F0.wireOp",EDGE,"E5798"),sQuery(id+"F0.wireOp",EDGE,"E5799"),sQuery(id+"F0.wireOp",EDGE,"E5800"),sQuery(id+"F0.wireOp",EDGE,"E5801"),sQuery(id+"F0.wireOp",EDGE,"E5802"),sQuery(id+"F0.wireOp",EDGE,"E5803"),sQuery(id+"F0.wireOp",EDGE,"E5804"),sQuery(id+"F0.wireOp",EDGE,"E5805"),sQuery(id+"F0.wireOp",EDGE,"E5806"),sQuery(id+"F0.wireOp",EDGE,"E5807"),sQuery(id+"F0.wireOp",EDGE,"E5808"),sQuery(id+"F0.wireOp",EDGE,"E5809"),sQuery(id+"F0.wireOp",EDGE,"E5810"),sQuery(id+"F0.wireOp",EDGE,"E5811"),sQuery(id+"F0.wireOp",EDGE,"E5812"),sQuery(id+"F0.wireOp",EDGE,"E5813"),sQuery(id+"F0.wireOp",EDGE,"E5814"),sQuery(id+"F0.wireOp",EDGE,"E5815"),sQuery(id+"F0.wireOp",EDGE,"E5816"),sQuery(id+"F0.wireOp",EDGE,"E5817"),sQuery(id+"F0.wireOp",EDGE,"E5818"),sQuery(id+"F0.wireOp",EDGE,"E5819"),sQuery(id+"F0.wireOp",EDGE,"E5820"),sQuery(id+"F0.wireOp",EDGE,"E5821"),sQuery(id+"F0.wireOp",EDGE,"E5822"),sQuery(id+"F0.wireOp",EDGE,"E5823"),sQuery(id+"F0.wireOp",EDGE,"E5824"),sQuery(id+"F0.wireOp",EDGE,"E5825"),sQuery(id+"F0.wireOp",EDGE,"E5826"),sQuery(id+"F0.wireOp",EDGE,"E5827"),sQuery(id+"F0.wireOp",EDGE,"E5828"),sQuery(id+"F0.wireOp",EDGE,"E5829"),sQuery(id+"F0.wireOp",EDGE,"E5830"),sQuery(id+"F0.wireOp",EDGE,"E5831"),sQuery(id+"F0.wireOp",EDGE,"E5832"),sQuery(id+"F0.wireOp",EDGE,"E5833"),sQuery(id+"F0.wireOp",EDGE,"E5834"),sQuery(id+"F0.wireOp",EDGE,"E5835"),sQuery(id+"F0.wireOp",EDGE,"E5836"),sQuery(id+"F0.wireOp",EDGE,"E5837"),sQuery(id+"F0.wireOp",EDGE,"E5838"),sQuery(id+"F0.wireOp",EDGE,"E5839"),sQuery(id+"F0.wireOp",EDGE,"E5840"),sQuery(id+"F0.wireOp",EDGE,"E5841"),sQuery(id+"F0.wireOp",EDGE,"E5842"),sQuery(id+"F0.wireOp",EDGE,"E5843"),sQuery(id+"F0.wireOp",EDGE,"E5844"),sQuery(id+"F0.wireOp",EDGE,"E5845"),sQuery(id+"F0.wireOp",EDGE,"E5846"),sQuery(id+"F0.wireOp",EDGE,"E5847"),sQuery(id+"F0.wireOp",EDGE,"E5848"),sQuery(id+"F0.wireOp",EDGE,"E5849"),sQuery(id+"F0.wireOp",EDGE,"E5850"),sQuery(id+"F0.wireOp",EDGE,"E5851"),sQuery(id+"F0.wireOp",EDGE,"E5852"),sQuery(id+"F0.wireOp",EDGE,"E5853"),sQuery(id+"F0.wireOp",EDGE,"E5854"),sQuery(id+"F0.wireOp",EDGE,"E5855"),sQuery(id+"F0.wireOp",EDGE,"E5856"),sQuery(id+"F0.wireOp",EDGE,"E5857"),sQuery(id+"F0.wireOp",EDGE,"E5858"),sQuery(id+"F0.wireOp",EDGE,"E5859"),sQuery(id+"F0.wireOp",EDGE,"E5860"),sQuery(id+"F0.wireOp",EDGE,"E5861"),sQuery(id+"F0.wireOp",EDGE,"E5862"),sQuery(id+"F0.wireOp",EDGE,"E5863"),sQuery(id+"F0.wireOp",EDGE,"E5864"),sQuery(id+"F0.wireOp",EDGE,"E5865"),sQuery(id+"F0.wireOp",EDGE,"E5866"),sQuery(id+"F0.wireOp",EDGE,"E5867"),sQuery(id+"F0.wireOp",EDGE,"E5868"),sQuery(id+"F0.wireOp",EDGE,"E5869"),sQuery(id+"F0.wireOp",EDGE,"E5870"),sQuery(id+"F0.wireOp",EDGE,"E5871"),sQuery(id+"F0.wireOp",EDGE,"E5872"),sQuery(id+"F0.wireOp",EDGE,"E5873"),sQuery(id+"F0.wireOp",EDGE,"E5874"),sQuery(id+"F0.wireOp",EDGE,"E5875"),sQuery(id+"F0.wireOp",EDGE,"E5876"),sQuery(id+"F0.wireOp",EDGE,"E5877"),sQuery(id+"F0.wireOp",EDGE,"E5878"),sQuery(id+"F0.wireOp",EDGE,"E5879"),sQuery(id+"F0.wireOp",EDGE,"E5880"),sQuery(id+"F0.wireOp",EDGE,"E5881"),sQuery(id+"F0.wireOp",EDGE,"E5882"),sQuery(id+"F0.wireOp",EDGE,"E5883"),sQuery(id+"F0.wireOp",EDGE,"E5884"),sQuery(id+"F0.wireOp",EDGE,"E5885"),sQuery(id+"F0.wireOp",EDGE,"E5886"),sQuery(id+"F0.wireOp",EDGE,"E5887"),sQuery(id+"F0.wireOp",EDGE,"E5888"),sQuery(id+"F0.wireOp",EDGE,"E5889"),sQuery(id+"F0.wireOp",EDGE,"E5890"),sQuery(id+"F0.wireOp",EDGE,"E5891"),sQuery(id+"F0.wireOp",EDGE,"E5892"),sQuery(id+"F0.wireOp",EDGE,"E5893"),sQuery(id+"F0.wireOp",EDGE,"E5894"),sQuery(id+"F0.wireOp",EDGE,"E5895"),sQuery(id+"F0.wireOp",EDGE,"E5896"),sQuery(id+"F0.wireOp",EDGE,"E5897"),sQuery(id+"F0.wireOp",EDGE,"E5898"),sQuery(id+"F0.wireOp",EDGE,"E5899"),sQuery(id+"F0.wireOp",EDGE,"E5900"),sQuery(id+"F0.wireOp",EDGE,"E5901"),sQuery(id+"F0.wireOp",EDGE,"E5902"),sQuery(id+"F0.wireOp",EDGE,"E5903"),sQuery(id+"F0.wireOp",EDGE,"E5904"),sQuery(id+"F0.wireOp",EDGE,"E5905"),sQuery(id+"F0.wireOp",EDGE,"E5906"),sQuery(id+"F0.wireOp",EDGE,"E5907"),sQuery(id+"F0.wireOp",EDGE,"E5908"),sQuery(id+"F0.wireOp",EDGE,"E5909"),sQuery(id+"F0.wireOp",EDGE,"E5910"),sQuery(id+"F0.wireOp",EDGE,"E5911"),sQuery(id+"F0.wireOp",EDGE,"E5912"),sQuery(id+"F0.wireOp",EDGE,"E5913"),sQuery(id+"F0.wireOp",EDGE,"E5914"),sQuery(id+"F0.wireOp",EDGE,"E5915"),sQuery(id+"F0.wireOp",EDGE,"E5916"),sQuery(id+"F0.wireOp",EDGE,"E5917"),sQuery(id+"F0.wireOp",EDGE,"E5918"),sQuery(id+"F0.wireOp",EDGE,"E5919"),sQuery(id+"F0.wireOp",EDGE,"E5920"),sQuery(id+"F0.wireOp",EDGE,"E5921"),sQuery(id+"F0.wireOp",EDGE,"E5922"),sQuery(id+"F0.wireOp",EDGE,"E5923"),sQuery(id+"F0.wireOp",EDGE,"E5924"),sQuery(id+"F0.wireOp",EDGE,"E5925"),sQuery(id+"F0.wireOp",EDGE,"E5926"),sQuery(id+"F0.wireOp",EDGE,"E5927"),sQuery(id+"F0.wireOp",EDGE,"E5928"),sQuery(id+"F0.wireOp",EDGE,"E5929"),sQuery(id+"F0.wireOp",EDGE,"E5930"),sQuery(id+"F0.wireOp",EDGE,"E5931"),sQuery(id+"F0.wireOp",EDGE,"E5932"),sQuery(id+"F0.wireOp",EDGE,"E5933"),sQuery(id+"F0.wireOp",EDGE,"E5934"),sQuery(id+"F0.wireOp",EDGE,"E5935"),sQuery(id+"F0.wireOp",EDGE,"E5936"),sQuery(id+"F0.wireOp",EDGE,"E5937"),sQuery(id+"F0.wireOp",EDGE,"E5938"),sQuery(id+"F0.wireOp",EDGE,"E5939"),sQuery(id+"F0.wireOp",EDGE,"E5940"),sQuery(id+"F0.wireOp",EDGE,"E5941"),sQuery(id+"F0.wireOp",EDGE,"E5942"),sQuery(id+"F0.wireOp",EDGE,"E5943"),sQuery(id+"F0.wireOp",EDGE,"E5944"),sQuery(id+"F0.wireOp",EDGE,"E5945"),sQuery(id+"F0.wireOp",EDGE,"E5946"),sQuery(id+"F0.wireOp",EDGE,"E5947"),sQuery(id+"F0.wireOp",EDGE,"E5948"),sQuery(id+"F0.wireOp",EDGE,"E5949"),sQuery(id+"F0.wireOp",EDGE,"E5950"),sQuery(id+"F0.wireOp",EDGE,"E5951"),sQuery(id+"F0.wireOp",EDGE,"E5952"),sQuery(id+"F0.wireOp",EDGE,"E5953"),sQuery(id+"F0.wireOp",EDGE,"E5954"),sQuery(id+"F0.wireOp",EDGE,"E5955"),sQuery(id+"F0.wireOp",EDGE,"E5956"),sQuery(id+"F0.wireOp",EDGE,"E5957"),sQuery(id+"F0.wireOp",EDGE,"E5958"),sQuery(id+"F0.wireOp",EDGE,"E5959"),sQuery(id+"F0.wireOp",EDGE,"E5960"),sQuery(id+"F0.wireOp",EDGE,"E5961"),sQuery(id+"F0.wireOp",EDGE,"E5962"),sQuery(id+"F0.wireOp",EDGE,"E5963"),sQuery(id+"F0.wireOp",EDGE,"E5964"),sQuery(id+"F0.wireOp",EDGE,"E5965"),sQuery(id+"F0.wireOp",EDGE,"E5966"),sQuery(id+"F0.wireOp",EDGE,"E5967"),sQuery(id+"F0.wireOp",EDGE,"E5968"),sQuery(id+"F0.wireOp",EDGE,"E5969"),sQuery(id+"F0.wireOp",EDGE,"E5970"),sQuery(id+"F0.wireOp",EDGE,"E5971"),sQuery(id+"F0.wireOp",EDGE,"E5972"),sQuery(id+"F0.wireOp",EDGE,"E5973"),sQuery(id+"F0.wireOp",EDGE,"E5974"),sQuery(id+"F0.wireOp",EDGE,"E5975"),sQuery(id+"F0.wireOp",EDGE,"E5976"),sQuery(id+"F0.wireOp",EDGE,"E5977"),sQuery(id+"F0.wireOp",EDGE,"E5978"),sQuery(id+"F0.wireOp",EDGE,"E5979"),sQuery(id+"F0.wireOp",EDGE,"E5980"),sQuery(id+"F0.wireOp",EDGE,"E5981"),sQuery(id+"F0.wireOp",EDGE,"E5982"),sQuery(id+"F0.wireOp",EDGE,"E5983"),sQuery(id+"F0.wireOp",EDGE,"E5984"),sQuery(id+"F0.wireOp",EDGE,"E5985"),sQuery(id+"F0.wireOp",EDGE,"E5986"),sQuery(id+"F0.wireOp",EDGE,"E5987"),sQuery(id+"F0.wireOp",EDGE,"E5988"),sQuery(id+"F0.wireOp",EDGE,"E5989"),sQuery(id+"F0.wireOp",EDGE,"E5990"),sQuery(id+"F0.wireOp",EDGE,"E5991"),sQuery(id+"F0.wireOp",EDGE,"E5992"),sQuery(id+"F0.wireOp",EDGE,"E5993"),sQuery(id+"F0.wireOp",EDGE,"E5994"),sQuery(id+"F0.wireOp",EDGE,"E5995"),sQuery(id+"F0.wireOp",EDGE,"E5996"),sQuery(id+"F0.wireOp",EDGE,"E5997"),sQuery(id+"F0.wireOp",EDGE,"E5998"),sQuery(id+"F0.wireOp",EDGE,"E5999"),sQuery(id+"F0.wireOp",EDGE,"E6000"),sQuery(id+"F0.wireOp",EDGE,"E6001"),sQuery(id+"F0.wireOp",EDGE,"E6002"),sQuery(id+"F0.wireOp",EDGE,"E6003"),sQuery(id+"F0.wireOp",EDGE,"E6004"),sQuery(id+"F0.wireOp",EDGE,"E6005"),sQuery(id+"F0.wireOp",EDGE,"E6006"),sQuery(id+"F0.wireOp",EDGE,"E6007"),sQuery(id+"F0.wireOp",EDGE,"E6008"),sQuery(id+"F0.wireOp",EDGE,"E6009"),sQuery(id+"F0.wireOp",EDGE,"E6010"),sQuery(id+"F0.wireOp",EDGE,"E6011"),sQuery(id+"F0.wireOp",EDGE,"E6012"),sQuery(id+"F0.wireOp",EDGE,"E6013"),sQuery(id+"F0.wireOp",EDGE,"E6014"),sQuery(id+"F0.wireOp",EDGE,"E6015"),sQuery(id+"F0.wireOp",EDGE,"E6016"),sQuery(id+"F0.wireOp",EDGE,"E6017"),sQuery(id+"F0.wireOp",EDGE,"E6018"),sQuery(id+"F0.wireOp",EDGE,"E6019"),sQuery(id+"F0.wireOp",EDGE,"E6020"),sQuery(id+"F0.wireOp",EDGE,"E6021"),sQuery(id+"F0.wireOp",EDGE,"E6022"),sQuery(id+"F0.wireOp",EDGE,"E6023"),sQuery(id+"F0.wireOp",EDGE,"E6024"),sQuery(id+"F0.wireOp",EDGE,"E6025"),sQuery(id+"F0.wireOp",EDGE,"E6026"),sQuery(id+"F0.wireOp",EDGE,"E6027"),sQuery(id+"F0.wireOp",EDGE,"E6028"),sQuery(id+"F0.wireOp",EDGE,"E6029"),sQuery(id+"F0.wireOp",EDGE,"E6030"),sQuery(id+"F0.wireOp",EDGE,"E6031"),sQuery(id+"F0.wireOp",EDGE,"E6032"),sQuery(id+"F0.wireOp",EDGE,"E6033"),sQuery(id+"F0.wireOp",EDGE,"E6034"),sQuery(id+"F0.wireOp",EDGE,"E6035"),sQuery(id+"F0.wireOp",EDGE,"E6036"),sQuery(id+"F0.wireOp",EDGE,"E6037"),sQuery(id+"F0.wireOp",EDGE,"E6038"),sQuery(id+"F0.wireOp",EDGE,"E6039"),sQuery(id+"F0.wireOp",EDGE,"E6040"),sQuery(id+"F0.wireOp",EDGE,"E6041"),sQuery(id+"F0.wireOp",EDGE,"E6042"),sQuery(id+"F0.wireOp",EDGE,"E6043"),sQuery(id+"F0.wireOp",EDGE,"E6044"),sQuery(id+"F0.wireOp",EDGE,"E6045"),sQuery(id+"F0.wireOp",EDGE,"E6046"),sQuery(id+"F0.wireOp",EDGE,"E6047"),sQuery(id+"F0.wireOp",EDGE,"E6048"),sQuery(id+"F0.wireOp",EDGE,"E6049"),sQuery(id+"F0.wireOp",EDGE,"E6050"),sQuery(id+"F0.wireOp",EDGE,"E6051"),sQuery(id+"F0.wireOp",EDGE,"E6052"),sQuery(id+"F0.wireOp",EDGE,"E6053"),sQuery(id+"F0.wireOp",EDGE,"E6054"),sQuery(id+"F0.wireOp",EDGE,"E6055"),sQuery(id+"F0.wireOp",EDGE,"E6056"),sQuery(id+"F0.wireOp",EDGE,"E6057"),sQuery(id+"F0.wireOp",EDGE,"E6058"),sQuery(id+"F0.wireOp",EDGE,"E6059"),sQuery(id+"F0.wireOp",EDGE,"E6060"),sQuery(id+"F0.wireOp",EDGE,"E6061"),sQuery(id+"F0.wireOp",EDGE,"E6062"),sQuery(id+"F0.wireOp",EDGE,"E6063"),sQuery(id+"F0.wireOp",EDGE,"E6064"),sQuery(id+"F0.wireOp",EDGE,"E6065"),sQuery(id+"F0.wireOp",EDGE,"E6066"),sQuery(id+"F0.wireOp",EDGE,"E6067"),sQuery(id+"F0.wireOp",EDGE,"E6068"),sQuery(id+"F0.wireOp",EDGE,"E6069"),sQuery(id+"F0.wireOp",EDGE,"E6070"),sQuery(id+"F0.wireOp",EDGE,"E6071"),sQuery(id+"F0.wireOp",EDGE,"E6072"),sQuery(id+"F0.wireOp",EDGE,"E6073"),sQuery(id+"F0.wireOp",EDGE,"E6074"),sQuery(id+"F0.wireOp",EDGE,"E6075"),sQuery(id+"F0.wireOp",EDGE,"E6076"),sQuery(id+"F0.wireOp",EDGE,"E6077"),sQuery(id+"F0.wireOp",EDGE,"E6078"),sQuery(id+"F0.wireOp",EDGE,"E6079"),sQuery(id+"F0.wireOp",EDGE,"E6080"),sQuery(id+"F0.wireOp",EDGE,"E6081"),sQuery(id+"F0.wireOp",EDGE,"E6082"),sQuery(id+"F0.wireOp",EDGE,"E6083"),sQuery(id+"F0.wireOp",EDGE,"E6084"),sQuery(id+"F0.wireOp",EDGE,"E6085"),sQuery(id+"F0.wireOp",EDGE,"E6086"),sQuery(id+"F0.wireOp",EDGE,"E6087"),sQuery(id+"F0.wireOp",EDGE,"E6088"),sQuery(id+"F0.wireOp",EDGE,"E6089"),sQuery(id+"F0.wireOp",EDGE,"E6090"),sQuery(id+"F0.wireOp",EDGE,"E6091"),sQuery(id+"F0.wireOp",EDGE,"E6092"),sQuery(id+"F0.wireOp",EDGE,"E6093"),sQuery(id+"F0.wireOp",EDGE,"E6094"),sQuery(id+"F0.wireOp",EDGE,"E6095"),sQuery(id+"F0.wireOp",EDGE,"E6096"),sQuery(id+"F0.wireOp",EDGE,"E6097"),sQuery(id+"F0.wireOp",EDGE,"E6098"),sQuery(id+"F0.wireOp",EDGE,"E6099"),sQuery(id+"F0.wireOp",EDGE,"E6100"),sQuery(id+"F0.wireOp",EDGE,"E6101"),sQuery(id+"F0.wireOp",EDGE,"E6102"),sQuery(id+"F0.wireOp",EDGE,"E6103"),sQuery(id+"F0.wireOp",EDGE,"E6104"),sQuery(id+"F0.wireOp",EDGE,"E6105"),sQuery(id+"F0.wireOp",EDGE,"E6106"),sQuery(id+"F0.wireOp",EDGE,"E6107"),sQuery(id+"F0.wireOp",EDGE,"E6108"),sQuery(id+"F0.wireOp",EDGE,"E6109"),sQuery(id+"F0.wireOp",EDGE,"E6110"),sQuery(id+"F0.wireOp",EDGE,"E6111"),sQuery(id+"F0.wireOp",EDGE,"E6112"),sQuery(id+"F0.wireOp",EDGE,"E6113"),sQuery(id+"F0.wireOp",EDGE,"E6114"),sQuery(id+"F0.wireOp",EDGE,"E6115"),sQuery(id+"F0.wireOp",EDGE,"E6116"),sQuery(id+"F0.wireOp",EDGE,"E6117"),sQuery(id+"F0.wireOp",EDGE,"E6118"),sQuery(id+"F0.wireOp",EDGE,"E6119"),sQuery(id+"F0.wireOp",EDGE,"E6120"),sQuery(id+"F0.wireOp",EDGE,"E6121"),sQuery(id+"F0.wireOp",EDGE,"E6122"),sQuery(id+"F0.wireOp",EDGE,"E6123"),sQuery(id+"F0.wireOp",EDGE,"E6124"),sQuery(id+"F0.wireOp",EDGE,"E6125"),sQuery(id+"F0.wireOp",EDGE,"E6126"),sQuery(id+"F0.wireOp",EDGE,"E6127"),sQuery(id+"F0.wireOp",EDGE,"E6128"),sQuery(id+"F0.wireOp",EDGE,"E6129"),sQuery(id+"F0.wireOp",EDGE,"E6130"),sQuery(id+"F0.wireOp",EDGE,"E6131"),sQuery(id+"F0.wireOp",EDGE,"E6132"),sQuery(id+"F0.wireOp",EDGE,"E6133"),sQuery(id+"F0.wireOp",EDGE,"E6134"),sQuery(id+"F0.wireOp",EDGE,"E6135"),sQuery(id+"F0.wireOp",EDGE,"E6136"),sQuery(id+"F0.wireOp",EDGE,"E6137"),sQuery(id+"F0.wireOp",EDGE,"E6138"),sQuery(id+"F0.wireOp",EDGE,"E6139"),sQuery(id+"F0.wireOp",EDGE,"E6140"),sQuery(id+"F0.wireOp",EDGE,"E6141"),sQuery(id+"F0.wireOp",EDGE,"E6142"),sQuery(id+"F0.wireOp",EDGE,"E6143"),sQuery(id+"F0.wireOp",EDGE,"E6144"),sQuery(id+"F0.wireOp",EDGE,"E6145"),sQuery(id+"F0.wireOp",EDGE,"E6146"),sQuery(id+"F0.wireOp",EDGE,"E6147"),sQuery(id+"F0.wireOp",EDGE,"E6148"),sQuery(id+"F0.wireOp",EDGE,"E6149"),sQuery(id+"F0.wireOp",EDGE,"E6150"),sQuery(id+"F0.wireOp",EDGE,"E6151"),sQuery(id+"F0.wireOp",EDGE,"E6152"),sQuery(id+"F0.wireOp",EDGE,"E6153"),sQuery(id+"F0.wireOp",EDGE,"E6154"),sQuery(id+"F0.wireOp",EDGE,"E6155"),sQuery(id+"F0.wireOp",EDGE,"E6156"),sQuery(id+"F0.wireOp",EDGE,"E6157"),sQuery(id+"F0.wireOp",EDGE,"E6158"),sQuery(id+"F0.wireOp",EDGE,"E6159"),sQuery(id+"F0.wireOp",EDGE,"E6160"),sQuery(id+"F0.wireOp",EDGE,"E6161"),sQuery(id+"F0.wireOp",EDGE,"E6162"),sQuery(id+"F0.wireOp",EDGE,"E6163"),sQuery(id+"F0.wireOp",EDGE,"E6164"),sQuery(id+"F0.wireOp",EDGE,"E6165"),sQuery(id+"F0.wireOp",EDGE,"E6166"),sQuery(id+"F0.wireOp",EDGE,"E6167"),sQuery(id+"F0.wireOp",EDGE,"E6168"),sQuery(id+"F0.wireOp",EDGE,"E6169"),sQuery(id+"F0.wireOp",EDGE,"E6170"),sQuery(id+"F0.wireOp",EDGE,"E6171"),sQuery(id+"F0.wireOp",EDGE,"E6172"),sQuery(id+"F0.wireOp",EDGE,"E6173"),sQuery(id+"F0.wireOp",EDGE,"E6174"),sQuery(id+"F0.wireOp",EDGE,"E6175"),sQuery(id+"F0.wireOp",EDGE,"E6176"),sQuery(id+"F0.wireOp",EDGE,"E6177"),sQuery(id+"F0.wireOp",EDGE,"E6178"),sQuery(id+"F0.wireOp",EDGE,"E6179"),sQuery(id+"F0.wireOp",EDGE,"E6180"),sQuery(id+"F0.wireOp",EDGE,"E6181"),sQuery(id+"F0.wireOp",EDGE,"E6182"),sQuery(id+"F0.wireOp",EDGE,"E6183"),sQuery(id+"F0.wireOp",EDGE,"E6184"),sQuery(id+"F0.wireOp",EDGE,"E6185"),sQuery(id+"F0.wireOp",EDGE,"E6186"),sQuery(id+"F0.wireOp",EDGE,"E6187"),sQuery(id+"F0.wireOp",EDGE,"E6188"),sQuery(id+"F0.wireOp",EDGE,"E6189"),sQuery(id+"F0.wireOp",EDGE,"E6190"),sQuery(id+"F0.wireOp",EDGE,"E6191"),sQuery(id+"F0.wireOp",EDGE,"E6192"),sQuery(id+"F0.wireOp",EDGE,"E6193"),sQuery(id+"F0.wireOp",EDGE,"E6194"),sQuery(id+"F0.wireOp",EDGE,"E6195"),sQuery(id+"F0.wireOp",EDGE,"E6196"),sQuery(id+"F0.wireOp",EDGE,"E6197"),sQuery(id+"F0.wireOp",EDGE,"E6198"),sQuery(id+"F0.wireOp",EDGE,"E6199"),sQuery(id+"F0.wireOp",EDGE,"E6200"),sQuery(id+"F0.wireOp",EDGE,"E6201"),sQuery(id+"F0.wireOp",EDGE,"E6202"),sQuery(id+"F0.wireOp",EDGE,"E6203"),sQuery(id+"F0.wireOp",EDGE,"E6204"),sQuery(id+"F0.wireOp",EDGE,"E6205"),sQuery(id+"F0.wireOp",EDGE,"E6206"),sQuery(id+"F0.wireOp",EDGE,"E6207"),sQuery(id+"F0.wireOp",EDGE,"E6208"),sQuery(id+"F0.wireOp",EDGE,"E6209"),sQuery(id+"F0.wireOp",EDGE,"E6210"),sQuery(id+"F0.wireOp",EDGE,"E6211"),sQuery(id+"F0.wireOp",EDGE,"E6212"),sQuery(id+"F0.wireOp",EDGE,"E6213"),sQuery(id+"F0.wireOp",EDGE,"E6214"),sQuery(id+"F0.wireOp",EDGE,"E6215"),sQuery(id+"F0.wireOp",EDGE,"E6216"),sQuery(id+"F0.wireOp",EDGE,"E6217"),sQuery(id+"F0.wireOp",EDGE,"E6218"),sQuery(id+"F0.wireOp",EDGE,"E6219"),sQuery(id+"F0.wireOp",EDGE,"E6220"),sQuery(id+"F0.wireOp",EDGE,"E6221"),sQuery(id+"F0.wireOp",EDGE,"E6222"),sQuery(id+"F0.wireOp",EDGE,"E6223"),sQuery(id+"F0.wireOp",EDGE,"E6224"),sQuery(id+"F0.wireOp",EDGE,"E6225"),sQuery(id+"F0.wireOp",EDGE,"E6226"),sQuery(id+"F0.wireOp",EDGE,"E6227"),sQuery(id+"F0.wireOp",EDGE,"E6228"),sQuery(id+"F0.wireOp",EDGE,"E6229"),sQuery(id+"F0.wireOp",EDGE,"E6230"),sQuery(id+"F0.wireOp",EDGE,"E6231"),sQuery(id+"F0.wireOp",EDGE,"E6232"),sQuery(id+"F0.wireOp",EDGE,"E6233"),sQuery(id+"F0.wireOp",EDGE,"E6234"),sQuery(id+"F0.wireOp",EDGE,"E6235"),sQuery(id+"F0.wireOp",EDGE,"E6236"),sQuery(id+"F0.wireOp",EDGE,"E6237"),sQuery(id+"F0.wireOp",EDGE,"E6238"),sQuery(id+"F0.wireOp",EDGE,"E6239"),sQuery(id+"F0.wireOp",EDGE,"E6240"),sQuery(id+"F0.wireOp",EDGE,"E6241"),sQuery(id+"F0.wireOp",EDGE,"E6242"),sQuery(id+"F0.wireOp",EDGE,"E6243"),sQuery(id+"F0.wireOp",EDGE,"E6244"),sQuery(id+"F0.wireOp",EDGE,"E6245"),sQuery(id+"F0.wireOp",EDGE,"E6246"),sQuery(id+"F0.wireOp",EDGE,"E6247"),sQuery(id+"F0.wireOp",EDGE,"E6248"),sQuery(id+"F0.wireOp",EDGE,"E6249"),sQuery(id+"F0.wireOp",EDGE,"E6250"),sQuery(id+"F0.wireOp",EDGE,"E6251"),sQuery(id+"F0.wireOp",EDGE,"E6252"),sQuery(id+"F0.wireOp",EDGE,"E6253"),sQuery(id+"F0.wireOp",EDGE,"E6254"),sQuery(id+"F0.wireOp",EDGE,"E6255"),sQuery(id+"F0.wireOp",EDGE,"E6256"),sQuery(id+"F0.wireOp",EDGE,"E6257"),sQuery(id+"F0.wireOp",EDGE,"E6258"),sQuery(id+"F0.wireOp",EDGE,"E6259"),sQuery(id+"F0.wireOp",EDGE,"E6260"),sQuery(id+"F0.wireOp",EDGE,"E6261"),sQuery(id+"F0.wireOp",EDGE,"E6262"),sQuery(id+"F0.wireOp",EDGE,"E6263"),sQuery(id+"F0.wireOp",EDGE,"E6264"),sQuery(id+"F0.wireOp",EDGE,"E6265"),sQuery(id+"F0.wireOp",EDGE,"E6266"),sQuery(id+"F0.wireOp",EDGE,"E6267"),sQuery(id+"F0.wireOp",EDGE,"E6268"),sQuery(id+"F0.wireOp",EDGE,"E6269"),sQuery(id+"F0.wireOp",EDGE,"E6270"),sQuery(id+"F0.wireOp",EDGE,"E6271"),sQuery(id+"F0.wireOp",EDGE,"E6272"),sQuery(id+"F0.wireOp",EDGE,"E6273"),sQuery(id+"F0.wireOp",EDGE,"E6274"),sQuery(id+"F0.wireOp",EDGE,"E6275"),sQuery(id+"F0.wireOp",EDGE,"E6276"),sQuery(id+"F0.wireOp",EDGE,"E6277"),sQuery(id+"F0.wireOp",EDGE,"E6278"),sQuery(id+"F0.wireOp",EDGE,"E6279"),sQuery(id+"F0.wireOp",EDGE,"E6280"),sQuery(id+"F0.wireOp",EDGE,"E6281"),sQuery(id+"F0.wireOp",EDGE,"E6282"),sQuery(id+"F0.wireOp",EDGE,"E6283"),sQuery(id+"F0.wireOp",EDGE,"E6284"),sQuery(id+"F0.wireOp",EDGE,"E6285"),sQuery(id+"F0.wireOp",EDGE,"E6286"),sQuery(id+"F0.wireOp",EDGE,"E6287"),sQuery(id+"F0.wireOp",EDGE,"E6288"),sQuery(id+"F0.wireOp",EDGE,"E6289"),sQuery(id+"F0.wireOp",EDGE,"E6290"),sQuery(id+"F0.wireOp",EDGE,"E6291"),sQuery(id+"F0.wireOp",EDGE,"E6292"),sQuery(id+"F0.wireOp",EDGE,"E6293"),sQuery(id+"F0.wireOp",EDGE,"E6294"),sQuery(id+"F0.wireOp",EDGE,"E6295"),sQuery(id+"F0.wireOp",EDGE,"E6296"),sQuery(id+"F0.wireOp",EDGE,"E6297"),sQuery(id+"F0.wireOp",EDGE,"E6298"),sQuery(id+"F0.wireOp",EDGE,"E6299"),sQuery(id+"F0.wireOp",EDGE,"E6300"),sQuery(id+"F0.wireOp",EDGE,"E6301"),sQuery(id+"F0.wireOp",EDGE,"E6302"),sQuery(id+"F0.wireOp",EDGE,"E6303"),sQuery(id+"F0.wireOp",EDGE,"E6304"),sQuery(id+"F0.wireOp",EDGE,"E6305"),sQuery(id+"F0.wireOp",EDGE,"E6306"),sQuery(id+"F0.wireOp",EDGE,"E6307"),sQuery(id+"F0.wireOp",EDGE,"E6308"),sQuery(id+"F0.wireOp",EDGE,"E6309"),sQuery(id+"F0.wireOp",EDGE,"E6310"),sQuery(id+"F0.wireOp",EDGE,"E6311"),sQuery(id+"F0.wireOp",EDGE,"E6312"),sQuery(id+"F0.wireOp",EDGE,"E6313"),sQuery(id+"F0.wireOp",EDGE,"E6314"),sQuery(id+"F0.wireOp",EDGE,"E6315"),sQuery(id+"F0.wireOp",EDGE,"E6316"),sQuery(id+"F0.wireOp",EDGE,"E6317"),sQuery(id+"F0.wireOp",EDGE,"E6318"),sQuery(id+"F0.wireOp",EDGE,"E6319"),sQuery(id+"F0.wireOp",EDGE,"E6320"),sQuery(id+"F0.wireOp",EDGE,"E6321"),sQuery(id+"F0.wireOp",EDGE,"E6322"),sQuery(id+"F0.wireOp",EDGE,"E6323"),sQuery(id+"F0.wireOp",EDGE,"E6324"),sQuery(id+"F0.wireOp",EDGE,"E6325"),sQuery(id+"F0.wireOp",EDGE,"E6326"),sQuery(id+"F0.wireOp",EDGE,"E6327"),sQuery(id+"F0.wireOp",EDGE,"E6328"),sQuery(id+"F0.wireOp",EDGE,"E6329"),sQuery(id+"F0.wireOp",EDGE,"E6330"),sQuery(id+"F0.wireOp",EDGE,"E6331"),sQuery(id+"F0.wireOp",EDGE,"E6332"),sQuery(id+"F0.wireOp",EDGE,"E6333"),sQuery(id+"F0.wireOp",EDGE,"E6334"),sQuery(id+"F0.wireOp",EDGE,"E6335"),sQuery(id+"F0.wireOp",EDGE,"E6336"),sQuery(id+"F0.wireOp",EDGE,"E6337"),sQuery(id+"F0.wireOp",EDGE,"E6338"),sQuery(id+"F0.wireOp",EDGE,"E6339"),sQuery(id+"F0.wireOp",EDGE,"E6340"),sQuery(id+"F0.wireOp",EDGE,"E6341"),sQuery(id+"F0.wireOp",EDGE,"E6342"),sQuery(id+"F0.wireOp",EDGE,"E6343"),sQuery(id+"F0.wireOp",EDGE,"E6344"),sQuery(id+"F0.wireOp",EDGE,"E6345"),sQuery(id+"F0.wireOp",EDGE,"E6346"),sQuery(id+"F0.wireOp",EDGE,"E6347"),sQuery(id+"F0.wireOp",EDGE,"E6348"),sQuery(id+"F0.wireOp",EDGE,"E6349"),sQuery(id+"F0.wireOp",EDGE,"E6350"),sQuery(id+"F0.wireOp",EDGE,"E6351"),sQuery(id+"F0.wireOp",EDGE,"E6352"),sQuery(id+"F0.wireOp",EDGE,"E6353"),sQuery(id+"F0.wireOp",EDGE,"E6354"),sQuery(id+"F0.wireOp",EDGE,"E6355"),sQuery(id+"F0.wireOp",EDGE,"E6356"),sQuery(id+"F0.wireOp",EDGE,"E6357"),sQuery(id+"F0.wireOp",EDGE,"E6358"),sQuery(id+"F0.wireOp",EDGE,"E6359"),sQuery(id+"F0.wireOp",EDGE,"E6360"),sQuery(id+"F0.wireOp",EDGE,"E6361"),sQuery(id+"F0.wireOp",EDGE,"E6362"),sQuery(id+"F0.wireOp",EDGE,"E6363"),sQuery(id+"F0.wireOp",EDGE,"E6364"),sQuery(id+"F0.wireOp",EDGE,"E6365"),sQuery(id+"F0.wireOp",EDGE,"E6366"),sQuery(id+"F0.wireOp",EDGE,"E6367"),sQuery(id+"F0.wireOp",EDGE,"E6368"),sQuery(id+"F0.wireOp",EDGE,"E6369"),sQuery(id+"F0.wireOp",EDGE,"E6370"),sQuery(id+"F0.wireOp",EDGE,"E6371"),sQuery(id+"F0.wireOp",EDGE,"E6372"),sQuery(id+"F0.wireOp",EDGE,"E6373"),sQuery(id+"F0.wireOp",EDGE,"E6374"),sQuery(id+"F0.wireOp",EDGE,"E6375"),sQuery(id+"F0.wireOp",EDGE,"E6376"),sQuery(id+"F0.wireOp",EDGE,"E6377"),sQuery(id+"F0.wireOp",EDGE,"E6378"),sQuery(id+"F0.wireOp",EDGE,"E6379"),sQuery(id+"F0.wireOp",EDGE,"E6380"),sQuery(id+"F0.wireOp",EDGE,"E6381"),sQuery(id+"F0.wireOp",EDGE,"E6382"),sQuery(id+"F0.wireOp",EDGE,"E6383"),sQuery(id+"F0.wireOp",EDGE,"E6384"),sQuery(id+"F0.wireOp",EDGE,"E6385"),sQuery(id+"F0.wireOp",EDGE,"E6386"),sQuery(id+"F0.wireOp",EDGE,"E6387"),sQuery(id+"F0.wireOp",EDGE,"E6388"),sQuery(id+"F0.wireOp",EDGE,"E6389"),sQuery(id+"F0.wireOp",EDGE,"E6390"),sQuery(id+"F0.wireOp",EDGE,"E6391"),sQuery(id+"F0.wireOp",EDGE,"E6392"),sQuery(id+"F0.wireOp",EDGE,"E6393"),sQuery(id+"F0.wireOp",EDGE,"E6394"),sQuery(id+"F0.wireOp",EDGE,"E6395"),sQuery(id+"F0.wireOp",EDGE,"E6396"),sQuery(id+"F0.wireOp",EDGE,"E6397"),sQuery(id+"F0.wireOp",EDGE,"E6398"),sQuery(id+"F0.wireOp",EDGE,"E6399"),sQuery(id+"F0.wireOp",EDGE,"E6400"),sQuery(id+"F0.wireOp",EDGE,"E6401"),sQuery(id+"F0.wireOp",EDGE,"E6402"),sQuery(id+"F0.wireOp",EDGE,"E6403"),sQuery(id+"F0.wireOp",EDGE,"E6404"),sQuery(id+"F0.wireOp",EDGE,"E6405"),sQuery(id+"F0.wireOp",EDGE,"E6406"),sQuery(id+"F0.wireOp",EDGE,"E6407"),sQuery(id+"F0.wireOp",EDGE,"E6408"),sQuery(id+"F0.wireOp",EDGE,"E6409"),sQuery(id+"F0.wireOp",EDGE,"E6410"),sQuery(id+"F0.wireOp",EDGE,"E6411"),sQuery(id+"F0.wireOp",EDGE,"E6412"),sQuery(id+"F0.wireOp",EDGE,"E6413"),sQuery(id+"F0.wireOp",EDGE,"E6414"),sQuery(id+"F0.wireOp",EDGE,"E6415"),sQuery(id+"F0.wireOp",EDGE,"E6416"),sQuery(id+"F0.wireOp",EDGE,"E6417"),sQuery(id+"F0.wireOp",EDGE,"E6418"),sQuery(id+"F0.wireOp",EDGE,"E6419"),sQuery(id+"F0.wireOp",EDGE,"E6420"),sQuery(id+"F0.wireOp",EDGE,"E6421"),sQuery(id+"F0.wireOp",EDGE,"E6422"),sQuery(id+"F0.wireOp",EDGE,"E6423"),sQuery(id+"F0.wireOp",EDGE,"E6424"),sQuery(id+"F0.wireOp",EDGE,"E6425"),sQuery(id+"F0.wireOp",EDGE,"E6426"),sQuery(id+"F0.wireOp",EDGE,"E6427"),sQuery(id+"F0.wireOp",EDGE,"E6428"),sQuery(id+"F0.wireOp",EDGE,"E6429"),sQuery(id+"F0.wireOp",EDGE,"E6430"),sQuery(id+"F0.wireOp",EDGE,"E6431"),sQuery(id+"F0.wireOp",EDGE,"E6432"),sQuery(id+"F0.wireOp",EDGE,"E6433"),sQuery(id+"F0.wireOp",EDGE,"E6434"),sQuery(id+"F0.wireOp",EDGE,"E6435"),sQuery(id+"F0.wireOp",EDGE,"E6436"),sQuery(id+"F0.wireOp",EDGE,"E6437"),sQuery(id+"F0.wireOp",EDGE,"E6438"),sQuery(id+"F0.wireOp",EDGE,"E6439"),sQuery(id+"F0.wireOp",EDGE,"E6440"),sQuery(id+"F0.wireOp",EDGE,"E6441"),sQuery(id+"F0.wireOp",EDGE,"E6442"),sQuery(id+"F0.wireOp",EDGE,"E6443"),sQuery(id+"F0.wireOp",EDGE,"E6444"),sQuery(id+"F0.wireOp",EDGE,"E6445"),sQuery(id+"F0.wireOp",EDGE,"E6446"),sQuery(id+"F0.wireOp",EDGE,"E6447"),sQuery(id+"F0.wireOp",EDGE,"E6448"),sQuery(id+"F0.wireOp",EDGE,"E6449"),sQuery(id+"F0.wireOp",EDGE,"E6450"),sQuery(id+"F0.wireOp",EDGE,"E6451"),sQuery(id+"F0.wireOp",EDGE,"E6452"),sQuery(id+"F0.wireOp",EDGE,"E6453"),sQuery(id+"F0.wireOp",EDGE,"E6454"),sQuery(id+"F0.wireOp",EDGE,"E6455"),sQuery(id+"F0.wireOp",EDGE,"E6456"),sQuery(id+"F0.wireOp",EDGE,"E6457"),sQuery(id+"F0.wireOp",EDGE,"E6458"),sQuery(id+"F0.wireOp",EDGE,"E6459"),sQuery(id+"F0.wireOp",EDGE,"E6460"),sQuery(id+"F0.wireOp",EDGE,"E6461"),sQuery(id+"F0.wireOp",EDGE,"E6462"),sQuery(id+"F0.wireOp",EDGE,"E6463"),sQuery(id+"F0.wireOp",EDGE,"E6464"),sQuery(id+"F0.wireOp",EDGE,"E6465"),sQuery(id+"F0.wireOp",EDGE,"E6466"),sQuery(id+"F0.wireOp",EDGE,"E6467"),sQuery(id+"F0.wireOp",EDGE,"E6468"),sQuery(id+"F0.wireOp",EDGE,"E6469"),sQuery(id+"F0.wireOp",EDGE,"E6470"),sQuery(id+"F0.wireOp",EDGE,"E6471"),sQuery(id+"F0.wireOp",EDGE,"E6472"),sQuery(id+"F0.wireOp",EDGE,"E6473"),sQuery(id+"F0.wireOp",EDGE,"E6474"),sQuery(id+"F0.wireOp",EDGE,"E6475"),sQuery(id+"F0.wireOp",EDGE,"E6476"),sQuery(id+"F0.wireOp",EDGE,"E6477"),sQuery(id+"F0.wireOp",EDGE,"E6478"),sQuery(id+"F0.wireOp",EDGE,"E6479"),sQuery(id+"F0.wireOp",EDGE,"E6480"),sQuery(id+"F0.wireOp",EDGE,"E6481"),sQuery(id+"F0.wireOp",EDGE,"E6482"),sQuery(id+"F0.wireOp",EDGE,"E6483"),sQuery(id+"F0.wireOp",EDGE,"E6484"),sQuery(id+"F0.wireOp",EDGE,"E6485"),sQuery(id+"F0.wireOp",EDGE,"E6486"),sQuery(id+"F0.wireOp",EDGE,"E6487"),sQuery(id+"F0.wireOp",EDGE,"E6488"),sQuery(id+"F0.wireOp",EDGE,"E6489"),sQuery(id+"F0.wireOp",EDGE,"E6490"),sQuery(id+"F0.wireOp",EDGE,"E6491"),sQuery(id+"F0.wireOp",EDGE,"E6492"),sQuery(id+"F0.wireOp",EDGE,"E6493"),sQuery(id+"F0.wireOp",EDGE,"E6494"),sQuery(id+"F0.wireOp",EDGE,"E6495"),sQuery(id+"F0.wireOp",EDGE,"E6496"),sQuery(id+"F0.wireOp",EDGE,"E6497"),sQuery(id+"F0.wireOp",EDGE,"E6498"),sQuery(id+"F0.wireOp",EDGE,"E6499"),sQuery(id+"F0.wireOp",EDGE,"E6500"),sQuery(id+"F0.wireOp",EDGE,"E6501"),sQuery(id+"F0.wireOp",EDGE,"E6502"),sQuery(id+"F0.wireOp",EDGE,"E6503"),sQuery(id+"F0.wireOp",EDGE,"E6504"),sQuery(id+"F0.wireOp",EDGE,"E6505"),sQuery(id+"F0.wireOp",EDGE,"E6506"),sQuery(id+"F0.wireOp",EDGE,"E6507"),sQuery(id+"F0.wireOp",EDGE,"E6508"),sQuery(id+"F0.wireOp",EDGE,"E6509"),sQuery(id+"F0.wireOp",EDGE,"E6510"),sQuery(id+"F0.wireOp",EDGE,"E6511"),sQuery(id+"F0.wireOp",EDGE,"E6512"),sQuery(id+"F0.wireOp",EDGE,"E6513"),sQuery(id+"F0.wireOp",EDGE,"E6514"),sQuery(id+"F0.wireOp",EDGE,"E6515"),sQuery(id+"F0.wireOp",EDGE,"E6516"),sQuery(id+"F0.wireOp",EDGE,"E6517"),sQuery(id+"F0.wireOp",EDGE,"E6518"),sQuery(id+"F0.wireOp",EDGE,"E6519"),sQuery(id+"F0.wireOp",EDGE,"E6520"),sQuery(id+"F0.wireOp",EDGE,"E6521"),sQuery(id+"F0.wireOp",EDGE,"E6522"),sQuery(id+"F0.wireOp",EDGE,"E6523"),sQuery(id+"F0.wireOp",EDGE,"E6524"),sQuery(id+"F0.wireOp",EDGE,"E6525"),sQuery(id+"F0.wireOp",EDGE,"E6526"),sQuery(id+"F0.wireOp",EDGE,"E6527"),sQuery(id+"F0.wireOp",EDGE,"E6528"),sQuery(id+"F0.wireOp",EDGE,"E6529"),sQuery(id+"F0.wireOp",EDGE,"E6530"),sQuery(id+"F0.wireOp",EDGE,"E6531"),sQuery(id+"F0.wireOp",EDGE,"E6532"),sQuery(id+"F0.wireOp",EDGE,"E6533"),sQuery(id+"F0.wireOp",EDGE,"E6534"),sQuery(id+"F0.wireOp",EDGE,"E6535"),sQuery(id+"F0.wireOp",EDGE,"E6536"),sQuery(id+"F0.wireOp",EDGE,"E6537"),sQuery(id+"F0.wireOp",EDGE,"E6538"),sQuery(id+"F0.wireOp",EDGE,"E6539"),sQuery(id+"F0.wireOp",EDGE,"E6540"),sQuery(id+"F0.wireOp",EDGE,"E6541"),sQuery(id+"F0.wireOp",EDGE,"E6542"),sQuery(id+"F0.wireOp",EDGE,"E6543"),sQuery(id+"F0.wireOp",EDGE,"E6544"),sQuery(id+"F0.wireOp",EDGE,"E6545"),sQuery(id+"F0.wireOp",EDGE,"E6546"),sQuery(id+"F0.wireOp",EDGE,"E6547"),sQuery(id+"F0.wireOp",EDGE,"E6548"),sQuery(id+"F0.wireOp",EDGE,"E6549"),sQuery(id+"F0.wireOp",EDGE,"E6550"),sQuery(id+"F0.wireOp",EDGE,"E6551"),sQuery(id+"F0.wireOp",EDGE,"E6552"),sQuery(id+"F0.wireOp",EDGE,"E6553"),sQuery(id+"F0.wireOp",EDGE,"E6554"),sQuery(id+"F0.wireOp",EDGE,"E6555"),sQuery(id+"F0.wireOp",EDGE,"E6556"),sQuery(id+"F0.wireOp",EDGE,"E6557"),sQuery(id+"F0.wireOp",EDGE,"E6558"),sQuery(id+"F0.wireOp",EDGE,"E6559"),sQuery(id+"F0.wireOp",EDGE,"E6560"),sQuery(id+"F0.wireOp",EDGE,"E6561"),sQuery(id+"F0.wireOp",EDGE,"E6562"),sQuery(id+"F0.wireOp",EDGE,"E6563"),sQuery(id+"F0.wireOp",EDGE,"E6564"),sQuery(id+"F0.wireOp",EDGE,"E6565"),sQuery(id+"F0.wireOp",EDGE,"E6566"),sQuery(id+"F0.wireOp",EDGE,"E6567"),sQuery(id+"F0.wireOp",EDGE,"E6568"),sQuery(id+"F0.wireOp",EDGE,"E6569"),sQuery(id+"F0.wireOp",EDGE,"E6570"),sQuery(id+"F0.wireOp",EDGE,"E6571"),sQuery(id+"F0.wireOp",EDGE,"E6572"),sQuery(id+"F0.wireOp",EDGE,"E6573"),sQuery(id+"F0.wireOp",EDGE,"E6574"),sQuery(id+"F0.wireOp",EDGE,"E6575"),sQuery(id+"F0.wireOp",EDGE,"E6576"),sQuery(id+"F0.wireOp",EDGE,"E6577"),sQuery(id+"F0.wireOp",EDGE,"E6578"),sQuery(id+"F0.wireOp",EDGE,"E6579"),sQuery(id+"F0.wireOp",EDGE,"E6580"),sQuery(id+"F0.wireOp",EDGE,"E6581"),sQuery(id+"F0.wireOp",EDGE,"E6582"),sQuery(id+"F0.wireOp",EDGE,"E6583"),sQuery(id+"F0.wireOp",EDGE,"E6584"),sQuery(id+"F0.wireOp",EDGE,"E6585"),sQuery(id+"F0.wireOp",EDGE,"E6586"),sQuery(id+"F0.wireOp",EDGE,"E6587"),sQuery(id+"F0.wireOp",EDGE,"E6588"),sQuery(id+"F0.wireOp",EDGE,"E6589"),sQuery(id+"F0.wireOp",EDGE,"E6590"),sQuery(id+"F0.wireOp",EDGE,"E6591"),sQuery(id+"F0.wireOp",EDGE,"E6592"),sQuery(id+"F0.wireOp",EDGE,"E6593"),sQuery(id+"F0.wireOp",EDGE,"E6594"),sQuery(id+"F0.wireOp",EDGE,"E6595"),sQuery(id+"F0.wireOp",EDGE,"E6596"),sQuery(id+"F0.wireOp",EDGE,"E6597"),sQuery(id+"F0.wireOp",EDGE,"E6598"),sQuery(id+"F0.wireOp",EDGE,"E6599"),sQuery(id+"F0.wireOp",EDGE,"E6600"),sQuery(id+"F0.wireOp",EDGE,"E6601"),sQuery(id+"F0.wireOp",EDGE,"E6602"),sQuery(id+"F0.wireOp",EDGE,"E6603"),sQuery(id+"F0.wireOp",EDGE,"E6604"),sQuery(id+"F0.wireOp",EDGE,"E6605"),sQuery(id+"F0.wireOp",EDGE,"E6606"),sQuery(id+"F0.wireOp",EDGE,"E6607"),sQuery(id+"F0.wireOp",EDGE,"E6608"),sQuery(id+"F0.wireOp",EDGE,"E6609"),sQuery(id+"F0.wireOp",EDGE,"E6610"),sQuery(id+"F0.wireOp",EDGE,"E6611"),sQuery(id+"F0.wireOp",EDGE,"E6612"),sQuery(id+"F0.wireOp",EDGE,"E6613"),sQuery(id+"F0.wireOp",EDGE,"E6614"),sQuery(id+"F0.wireOp",EDGE,"E6615"),sQuery(id+"F0.wireOp",EDGE,"E6616"),sQuery(id+"F0.wireOp",EDGE,"E6617"),sQuery(id+"F0.wireOp",EDGE,"E6618"),sQuery(id+"F0.wireOp",EDGE,"E6619"),sQuery(id+"F0.wireOp",EDGE,"E6620"),sQuery(id+"F0.wireOp",EDGE,"E6621"),sQuery(id+"F0.wireOp",EDGE,"E6622"),sQuery(id+"F0.wireOp",EDGE,"E6623"),sQuery(id+"F0.wireOp",EDGE,"E6624"),sQuery(id+"F0.wireOp",EDGE,"E6625"),sQuery(id+"F0.wireOp",EDGE,"E6626"),sQuery(id+"F0.wireOp",EDGE,"E6627"),sQuery(id+"F0.wireOp",EDGE,"E6628"),sQuery(id+"F0.wireOp",EDGE,"E6629"),sQuery(id+"F0.wireOp",EDGE,"E6630"),sQuery(id+"F0.wireOp",EDGE,"E6631"),sQuery(id+"F0.wireOp",EDGE,"E6632"),sQuery(id+"F0.wireOp",EDGE,"E6633"),sQuery(id+"F0.wireOp",EDGE,"E6634"),sQuery(id+"F0.wireOp",EDGE,"E6635"),sQuery(id+"F0.wireOp",EDGE,"E6636"),sQuery(id+"F0.wireOp",EDGE,"E6637"),sQuery(id+"F0.wireOp",EDGE,"E6638"),sQuery(id+"F0.wireOp",EDGE,"E6639"),sQuery(id+"F0.wireOp",EDGE,"E6640"),sQuery(id+"F0.wireOp",EDGE,"E6641"),sQuery(id+"F0.wireOp",EDGE,"E6642"),sQuery(id+"F0.wireOp",EDGE,"E6643"),sQuery(id+"F0.wireOp",EDGE,"E6644"),sQuery(id+"F0.wireOp",EDGE,"E6645"),sQuery(id+"F0.wireOp",EDGE,"E6646"),sQuery(id+"F0.wireOp",EDGE,"E6647"),sQuery(id+"F0.wireOp",EDGE,"E6648"),sQuery(id+"F0.wireOp",EDGE,"E6649"),sQuery(id+"F0.wireOp",EDGE,"E6650"),sQuery(id+"F0.wireOp",EDGE,"E6651"),sQuery(id+"F0.wireOp",EDGE,"E6652"),sQuery(id+"F0.wireOp",EDGE,"E6653"),sQuery(id+"F0.wireOp",EDGE,"E6654"),sQuery(id+"F0.wireOp",EDGE,"E6655"),sQuery(id+"F0.wireOp",EDGE,"E6656"),sQuery(id+"F0.wireOp",EDGE,"E6657"),sQuery(id+"F0.wireOp",EDGE,"E6658"),sQuery(id+"F0.wireOp",EDGE,"E6659"),sQuery(id+"F0.wireOp",EDGE,"E6660"),sQuery(id+"F0.wireOp",EDGE,"E6661"),sQuery(id+"F0.wireOp",EDGE,"E6662"),sQuery(id+"F0.wireOp",EDGE,"E6663"),sQuery(id+"F0.wireOp",EDGE,"E6664"),sQuery(id+"F0.wireOp",EDGE,"E6665"),sQuery(id+"F0.wireOp",EDGE,"E6666"),sQuery(id+"F0.wireOp",EDGE,"E6667"),sQuery(id+"F0.wireOp",EDGE,"E6668"),sQuery(id+"F0.wireOp",EDGE,"E6669"),sQuery(id+"F0.wireOp",EDGE,"E6670"),sQuery(id+"F0.wireOp",EDGE,"E6671"),sQuery(id+"F0.wireOp",EDGE,"E6672"),sQuery(id+"F0.wireOp",EDGE,"E6673"),sQuery(id+"F0.wireOp",EDGE,"E6674"),sQuery(id+"F0.wireOp",EDGE,"E6675"),sQuery(id+"F0.wireOp",EDGE,"E6676"),sQuery(id+"F0.wireOp",EDGE,"E6677"),sQuery(id+"F0.wireOp",EDGE,"E6678"),sQuery(id+"F0.wireOp",EDGE,"E6679"),sQuery(id+"F0.wireOp",EDGE,"E6680"),sQuery(id+"F0.wireOp",EDGE,"E6681"),sQuery(id+"F0.wireOp",EDGE,"E6682"),sQuery(id+"F0.wireOp",EDGE,"E6683"),sQuery(id+"F0.wireOp",EDGE,"E6684"),sQuery(id+"F0.wireOp",EDGE,"E6685"),sQuery(id+"F0.wireOp",EDGE,"E6686"),sQuery(id+"F0.wireOp",EDGE,"E6687"),sQuery(id+"F0.wireOp",EDGE,"E6688"),sQuery(id+"F0.wireOp",EDGE,"E6689"),sQuery(id+"F0.wireOp",EDGE,"E6690"),sQuery(id+"F0.wireOp",EDGE,"E6691"),sQuery(id+"F0.wireOp",EDGE,"E6692"),sQuery(id+"F0.wireOp",EDGE,"E6693"),sQuery(id+"F0.wireOp",EDGE,"E6694"),sQuery(id+"F0.wireOp",EDGE,"E6695"),sQuery(id+"F0.wireOp",EDGE,"E6696"),sQuery(id+"F0.wireOp",EDGE,"E6697"),sQuery(id+"F0.wireOp",EDGE,"E6698"),sQuery(id+"F0.wireOp",EDGE,"E6699"),sQuery(id+"F0.wireOp",EDGE,"E6700"),sQuery(id+"F0.wireOp",EDGE,"E6701"),sQuery(id+"F0.wireOp",EDGE,"E6702"),sQuery(id+"F0.wireOp",EDGE,"E6703"),sQuery(id+"F0.wireOp",EDGE,"E6704"),sQuery(id+"F0.wireOp",EDGE,"E6705"),sQuery(id+"F0.wireOp",EDGE,"E6706"),sQuery(id+"F0.wireOp",EDGE,"E6707"),sQuery(id+"F0.wireOp",EDGE,"E6708"),sQuery(id+"F0.wireOp",EDGE,"E6709"),sQuery(id+"F0.wireOp",EDGE,"E6710"),sQuery(id+"F0.wireOp",EDGE,"E6711"),sQuery(id+"F0.wireOp",EDGE,"E6712"),sQuery(id+"F0.wireOp",EDGE,"E6713"),sQuery(id+"F0.wireOp",EDGE,"E6714"),sQuery(id+"F0.wireOp",EDGE,"E6715"),sQuery(id+"F0.wireOp",EDGE,"E6716"),sQuery(id+"F0.wireOp",EDGE,"E6717"),sQuery(id+"F0.wireOp",EDGE,"E6718"),sQuery(id+"F0.wireOp",EDGE,"E6719")])],"isStart":false});
            var Q1;
            Q1=qCreatedBy(makeId("Top.planeOp"),FACE);
            var sketch = newSketch(context, id + "F4", { "sketchPlane" : qUnion([Q0, Q1])});
            skCircle(sketch, "E6721", {"center": v(0, 0) * mm, "radius": 2.92 * mm});
            skSolve(sketch);
        }
        {
            var Q0;
            Q0 = qSketchRegion(id + "F4", true);
            extrude(context, id + "F5", {"entities" : qUnion([Q0]), "operationType" : NewBodyOperationType.REMOVE, "oppositeDirection" : true, "depth" : 5 * mm});
        }
        {
            var Q0;
            Q0=qCreatedBy(makeId("Top.planeOp"),FACE);
            var sketch = newSketch(context, id + "F6", { "sketchPlane" : qUnion([Q0])});
            skArc(sketch, "E6722", {"start": v(-2.38, -3.15) * mm, "mid": v(0, -3.95) * mm, "end": v(2.38, -3.15) * mm});
            skPoint(sketch, "E6723", {"position": v(-14.4, 0) * mm});
            skPoint(sketch, "E6724", {"position": v(14.4, 0) * mm});
            skArc(sketch, "E6725", {"start": v(-14.55, 2.4) * mm, "mid": v(-16.8, 0) * mm, "end": v(-14.55, -2.4) * mm});
            skArc(sketch, "E6726", {"start": v(14.55, -2.4) * mm, "mid": v(16.8, 0) * mm, "end": v(14.55, 2.4) * mm});
            skArc(sketch, "E6727", {"start": v(0.4, -3.27) * mm, "mid": v(3.3, 0) * mm, "end": v(0.4, 3.27) * mm, "construction": true});
            skLineSegment(sketch, "E6728", {"start": v(0, 3.3) * mm, "end": v(-0.4, 3.27) * mm});
            skLineSegment(sketch, "E6729", {"start": v(0, -3.3) * mm, "end": v(-0.4, -3.27) * mm});
            skLineSegment(sketch, "E6730", {"start": v(0, 3.3) * mm, "end": v(0.4, 3.27) * mm});
            skLineSegment(sketch, "E6731", {"start": v(0, -3.3) * mm, "end": v(0.4, -3.27) * mm});
            skLineSegment(sketch, "E6732.trimOffspring", {"start": v(-2.38, 3.15) * mm, "end": v(-14.55, 2.4) * mm});
            skLineSegment(sketch, "E6733.trimOffspring", {"start": v(2.38, 3.15) * mm, "end": v(14.55, 2.4) * mm});
            skLineSegment(sketch, "E6734.trimOffspring", {"start": v(2.38, -3.15) * mm, "end": v(14.55, -2.4) * mm});
            skLineSegment(sketch, "E6735.trimOffspring", {"start": v(-2.38, -3.15) * mm, "end": v(-14.55, -2.4) * mm});
            skArc(sketch, "E6736.trimOffspring", {"start": v(-0.4, 3.27) * mm, "mid": v(-3.3, 0) * mm, "end": v(-0.4, -3.27) * mm, "construction": true});
            skArc(sketch, "E6737.trimOffspring", {"start": v(2.38, 3.15) * mm, "mid": v(0, 3.95) * mm, "end": v(-2.38, 3.15) * mm});
            skSolve(sketch);
        }
        {
            var Q0;
            Q0 = qSketchRegion(id + "F6", true);
            extrude(context, id + "F7", {"entities" : qUnion([Q0]), "operationType" : NewBodyOperationType.REMOVE, "depth" : 2 * mm});
        }
        {
            var Q0;
            Q0=makeQuery(id+"F1.opExtrude","CAP_FACE",FACE,{"disambiguationData":[OSD([sQuery(id+"F0.wireOp",EDGE,"E0"),sQuery(id+"F0.wireOp",EDGE,"E1"),sQuery(id+"F0.wireOp",EDGE,"E2"),sQuery(id+"F0.wireOp",EDGE,"E3"),sQuery(id+"F0.wireOp",EDGE,"E4"),sQuery(id+"F0.wireOp",EDGE,"E5"),sQuery(id+"F0.wireOp",EDGE,"E6"),sQuery(id+"F0.wireOp",EDGE,"E7"),sQuery(id+"F0.wireOp",EDGE,"E8"),sQuery(id+"F0.wireOp",EDGE,"E9"),sQuery(id+"F0.wireOp",EDGE,"E10"),sQuery(id+"F0.wireOp",EDGE,"E11"),sQuery(id+"F0.wireOp",EDGE,"E12"),sQuery(id+"F0.wireOp",EDGE,"E13"),sQuery(id+"F0.wireOp",EDGE,"E14"),sQuery(id+"F0.wireOp",EDGE,"E15"),sQuery(id+"F0.wireOp",EDGE,"E16"),sQuery(id+"F0.wireOp",EDGE,"E17"),sQuery(id+"F0.wireOp",EDGE,"E18"),sQuery(id+"F0.wireOp",EDGE,"E19"),sQuery(id+"F0.wireOp",EDGE,"E20"),sQuery(id+"F0.wireOp",EDGE,"E21"),sQuery(id+"F0.wireOp",EDGE,"E22"),sQuery(id+"F0.wireOp",EDGE,"E23"),sQuery(id+"F0.wireOp",EDGE,"E24"),sQuery(id+"F0.wireOp",EDGE,"E25"),sQuery(id+"F0.wireOp",EDGE,"E26"),sQuery(id+"F0.wireOp",EDGE,"E27"),sQuery(id+"F0.wireOp",EDGE,"E28"),sQuery(id+"F0.wireOp",EDGE,"E29"),sQuery(id+"F0.wireOp",EDGE,"E30"),sQuery(id+"F0.wireOp",EDGE,"E31"),sQuery(id+"F0.wireOp",EDGE,"E32"),sQuery(id+"F0.wireOp",EDGE,"E33"),sQuery(id+"F0.wireOp",EDGE,"E34"),sQuery(id+"F0.wireOp",EDGE,"E35"),sQuery(id+"F0.wireOp",EDGE,"E36"),sQuery(id+"F0.wireOp",EDGE,"E37"),sQuery(id+"F0.wireOp",EDGE,"E38"),sQuery(id+"F0.wireOp",EDGE,"E39"),sQuery(id+"F0.wireOp",EDGE,"E40"),sQuery(id+"F0.wireOp",EDGE,"E41"),sQuery(id+"F0.wireOp",EDGE,"E42"),sQuery(id+"F0.wireOp",EDGE,"E43"),sQuery(id+"F0.wireOp",EDGE,"E44"),sQuery(id+"F0.wireOp",EDGE,"E45"),sQuery(id+"F0.wireOp",EDGE,"E46"),sQuery(id+"F0.wireOp",EDGE,"E47"),sQuery(id+"F0.wireOp",EDGE,"E48"),sQuery(id+"F0.wireOp",EDGE,"E49"),sQuery(id+"F0.wireOp",EDGE,"E50"),sQuery(id+"F0.wireOp",EDGE,"E51"),sQuery(id+"F0.wireOp",EDGE,"E52"),sQuery(id+"F0.wireOp",EDGE,"E53"),sQuery(id+"F0.wireOp",EDGE,"E54"),sQuery(id+"F0.wireOp",EDGE,"E55"),sQuery(id+"F0.wireOp",EDGE,"E56"),sQuery(id+"F0.wireOp",EDGE,"E57"),sQuery(id+"F0.wireOp",EDGE,"E58"),sQuery(id+"F0.wireOp",EDGE,"E59"),sQuery(id+"F0.wireOp",EDGE,"E60"),sQuery(id+"F0.wireOp",EDGE,"E61"),sQuery(id+"F0.wireOp",EDGE,"E62"),sQuery(id+"F0.wireOp",EDGE,"E63"),sQuery(id+"F0.wireOp",EDGE,"E64"),sQuery(id+"F0.wireOp",EDGE,"E65"),sQuery(id+"F0.wireOp",EDGE,"E66"),sQuery(id+"F0.wireOp",EDGE,"E67"),sQuery(id+"F0.wireOp",EDGE,"E68"),sQuery(id+"F0.wireOp",EDGE,"E69"),sQuery(id+"F0.wireOp",EDGE,"E70"),sQuery(id+"F0.wireOp",EDGE,"E71"),sQuery(id+"F0.wireOp",EDGE,"E72"),sQuery(id+"F0.wireOp",EDGE,"E73"),sQuery(id+"F0.wireOp",EDGE,"E74"),sQuery(id+"F0.wireOp",EDGE,"E75"),sQuery(id+"F0.wireOp",EDGE,"E76"),sQuery(id+"F0.wireOp",EDGE,"E77"),sQuery(id+"F0.wireOp",EDGE,"E78"),sQuery(id+"F0.wireOp",EDGE,"E79"),sQuery(id+"F0.wireOp",EDGE,"E80"),sQuery(id+"F0.wireOp",EDGE,"E81"),sQuery(id+"F0.wireOp",EDGE,"E82"),sQuery(id+"F0.wireOp",EDGE,"E83"),sQuery(id+"F0.wireOp",EDGE,"E84"),sQuery(id+"F0.wireOp",EDGE,"E85"),sQuery(id+"F0.wireOp",EDGE,"E86"),sQuery(id+"F0.wireOp",EDGE,"E87"),sQuery(id+"F0.wireOp",EDGE,"E88"),sQuery(id+"F0.wireOp",EDGE,"E89"),sQuery(id+"F0.wireOp",EDGE,"E90"),sQuery(id+"F0.wireOp",EDGE,"E91"),sQuery(id+"F0.wireOp",EDGE,"E92"),sQuery(id+"F0.wireOp",EDGE,"E93"),sQuery(id+"F0.wireOp",EDGE,"E94"),sQuery(id+"F0.wireOp",EDGE,"E95"),sQuery(id+"F0.wireOp",EDGE,"E96"),sQuery(id+"F0.wireOp",EDGE,"E97"),sQuery(id+"F0.wireOp",EDGE,"E98"),sQuery(id+"F0.wireOp",EDGE,"E99"),sQuery(id+"F0.wireOp",EDGE,"E100"),sQuery(id+"F0.wireOp",EDGE,"E101"),sQuery(id+"F0.wireOp",EDGE,"E102"),sQuery(id+"F0.wireOp",EDGE,"E103"),sQuery(id+"F0.wireOp",EDGE,"E104"),sQuery(id+"F0.wireOp",EDGE,"E105"),sQuery(id+"F0.wireOp",EDGE,"E106"),sQuery(id+"F0.wireOp",EDGE,"E107"),sQuery(id+"F0.wireOp",EDGE,"E108"),sQuery(id+"F0.wireOp",EDGE,"E109"),sQuery(id+"F0.wireOp",EDGE,"E110"),sQuery(id+"F0.wireOp",EDGE,"E111"),sQuery(id+"F0.wireOp",EDGE,"E112"),sQuery(id+"F0.wireOp",EDGE,"E113"),sQuery(id+"F0.wireOp",EDGE,"E114"),sQuery(id+"F0.wireOp",EDGE,"E115"),sQuery(id+"F0.wireOp",EDGE,"E116"),sQuery(id+"F0.wireOp",EDGE,"E117"),sQuery(id+"F0.wireOp",EDGE,"E118"),sQuery(id+"F0.wireOp",EDGE,"E119"),sQuery(id+"F0.wireOp",EDGE,"E120"),sQuery(id+"F0.wireOp",EDGE,"E121"),sQuery(id+"F0.wireOp",EDGE,"E122"),sQuery(id+"F0.wireOp",EDGE,"E123"),sQuery(id+"F0.wireOp",EDGE,"E124"),sQuery(id+"F0.wireOp",EDGE,"E125"),sQuery(id+"F0.wireOp",EDGE,"E126"),sQuery(id+"F0.wireOp",EDGE,"E127"),sQuery(id+"F0.wireOp",EDGE,"E128"),sQuery(id+"F0.wireOp",EDGE,"E129"),sQuery(id+"F0.wireOp",EDGE,"E130"),sQuery(id+"F0.wireOp",EDGE,"E131"),sQuery(id+"F0.wireOp",EDGE,"E132"),sQuery(id+"F0.wireOp",EDGE,"E133"),sQuery(id+"F0.wireOp",EDGE,"E134"),sQuery(id+"F0.wireOp",EDGE,"E135"),sQuery(id+"F0.wireOp",EDGE,"E136"),sQuery(id+"F0.wireOp",EDGE,"E137"),sQuery(id+"F0.wireOp",EDGE,"E138"),sQuery(id+"F0.wireOp",EDGE,"E139"),sQuery(id+"F0.wireOp",EDGE,"E140"),sQuery(id+"F0.wireOp",EDGE,"E141"),sQuery(id+"F0.wireOp",EDGE,"E142"),sQuery(id+"F0.wireOp",EDGE,"E143"),sQuery(id+"F0.wireOp",EDGE,"E144"),sQuery(id+"F0.wireOp",EDGE,"E145"),sQuery(id+"F0.wireOp",EDGE,"E146"),sQuery(id+"F0.wireOp",EDGE,"E147"),sQuery(id+"F0.wireOp",EDGE,"E148"),sQuery(id+"F0.wireOp",EDGE,"E149"),sQuery(id+"F0.wireOp",EDGE,"E150"),sQuery(id+"F0.wireOp",EDGE,"E151"),sQuery(id+"F0.wireOp",EDGE,"E152"),sQuery(id+"F0.wireOp",EDGE,"E153"),sQuery(id+"F0.wireOp",EDGE,"E154"),sQuery(id+"F0.wireOp",EDGE,"E155"),sQuery(id+"F0.wireOp",EDGE,"E156"),sQuery(id+"F0.wireOp",EDGE,"E157"),sQuery(id+"F0.wireOp",EDGE,"E158"),sQuery(id+"F0.wireOp",EDGE,"E159"),sQuery(id+"F0.wireOp",EDGE,"E160"),sQuery(id+"F0.wireOp",EDGE,"E161"),sQuery(id+"F0.wireOp",EDGE,"E162"),sQuery(id+"F0.wireOp",EDGE,"E163"),sQuery(id+"F0.wireOp",EDGE,"E164"),sQuery(id+"F0.wireOp",EDGE,"E165"),sQuery(id+"F0.wireOp",EDGE,"E166"),sQuery(id+"F0.wireOp",EDGE,"E167"),sQuery(id+"F0.wireOp",EDGE,"E168"),sQuery(id+"F0.wireOp",EDGE,"E169"),sQuery(id+"F0.wireOp",EDGE,"E170"),sQuery(id+"F0.wireOp",EDGE,"E171"),sQuery(id+"F0.wireOp",EDGE,"E172"),sQuery(id+"F0.wireOp",EDGE,"E173"),sQuery(id+"F0.wireOp",EDGE,"E174"),sQuery(id+"F0.wireOp",EDGE,"E175"),sQuery(id+"F0.wireOp",EDGE,"E176"),sQuery(id+"F0.wireOp",EDGE,"E177"),sQuery(id+"F0.wireOp",EDGE,"E178"),sQuery(id+"F0.wireOp",EDGE,"E179"),sQuery(id+"F0.wireOp",EDGE,"E180"),sQuery(id+"F0.wireOp",EDGE,"E181"),sQuery(id+"F0.wireOp",EDGE,"E182"),sQuery(id+"F0.wireOp",EDGE,"E183"),sQuery(id+"F0.wireOp",EDGE,"E184"),sQuery(id+"F0.wireOp",EDGE,"E185"),sQuery(id+"F0.wireOp",EDGE,"E186"),sQuery(id+"F0.wireOp",EDGE,"E187"),sQuery(id+"F0.wireOp",EDGE,"E188"),sQuery(id+"F0.wireOp",EDGE,"E189"),sQuery(id+"F0.wireOp",EDGE,"E190"),sQuery(id+"F0.wireOp",EDGE,"E191"),sQuery(id+"F0.wireOp",EDGE,"E192"),sQuery(id+"F0.wireOp",EDGE,"E193"),sQuery(id+"F0.wireOp",EDGE,"E194"),sQuery(id+"F0.wireOp",EDGE,"E195"),sQuery(id+"F0.wireOp",EDGE,"E196"),sQuery(id+"F0.wireOp",EDGE,"E197"),sQuery(id+"F0.wireOp",EDGE,"E198"),sQuery(id+"F0.wireOp",EDGE,"E199"),sQuery(id+"F0.wireOp",EDGE,"E200"),sQuery(id+"F0.wireOp",EDGE,"E201"),sQuery(id+"F0.wireOp",EDGE,"E202"),sQuery(id+"F0.wireOp",EDGE,"E203"),sQuery(id+"F0.wireOp",EDGE,"E204"),sQuery(id+"F0.wireOp",EDGE,"E205"),sQuery(id+"F0.wireOp",EDGE,"E206"),sQuery(id+"F0.wireOp",EDGE,"E207"),sQuery(id+"F0.wireOp",EDGE,"E208"),sQuery(id+"F0.wireOp",EDGE,"E209"),sQuery(id+"F0.wireOp",EDGE,"E210"),sQuery(id+"F0.wireOp",EDGE,"E211"),sQuery(id+"F0.wireOp",EDGE,"E212"),sQuery(id+"F0.wireOp",EDGE,"E213"),sQuery(id+"F0.wireOp",EDGE,"E214"),sQuery(id+"F0.wireOp",EDGE,"E215"),sQuery(id+"F0.wireOp",EDGE,"E216"),sQuery(id+"F0.wireOp",EDGE,"E217"),sQuery(id+"F0.wireOp",EDGE,"E218"),sQuery(id+"F0.wireOp",EDGE,"E219"),sQuery(id+"F0.wireOp",EDGE,"E220"),sQuery(id+"F0.wireOp",EDGE,"E221"),sQuery(id+"F0.wireOp",EDGE,"E222"),sQuery(id+"F0.wireOp",EDGE,"E223"),sQuery(id+"F0.wireOp",EDGE,"E224"),sQuery(id+"F0.wireOp",EDGE,"E225"),sQuery(id+"F0.wireOp",EDGE,"E226"),sQuery(id+"F0.wireOp",EDGE,"E227"),sQuery(id+"F0.wireOp",EDGE,"E228"),sQuery(id+"F0.wireOp",EDGE,"E229"),sQuery(id+"F0.wireOp",EDGE,"E230"),sQuery(id+"F0.wireOp",EDGE,"E231"),sQuery(id+"F0.wireOp",EDGE,"E232"),sQuery(id+"F0.wireOp",EDGE,"E233"),sQuery(id+"F0.wireOp",EDGE,"E234"),sQuery(id+"F0.wireOp",EDGE,"E235"),sQuery(id+"F0.wireOp",EDGE,"E236"),sQuery(id+"F0.wireOp",EDGE,"E237"),sQuery(id+"F0.wireOp",EDGE,"E238"),sQuery(id+"F0.wireOp",EDGE,"E239"),sQuery(id+"F0.wireOp",EDGE,"E240"),sQuery(id+"F0.wireOp",EDGE,"E241"),sQuery(id+"F0.wireOp",EDGE,"E242"),sQuery(id+"F0.wireOp",EDGE,"E243"),sQuery(id+"F0.wireOp",EDGE,"E244"),sQuery(id+"F0.wireOp",EDGE,"E245"),sQuery(id+"F0.wireOp",EDGE,"E246"),sQuery(id+"F0.wireOp",EDGE,"E247"),sQuery(id+"F0.wireOp",EDGE,"E248"),sQuery(id+"F0.wireOp",EDGE,"E249"),sQuery(id+"F0.wireOp",EDGE,"E250"),sQuery(id+"F0.wireOp",EDGE,"E251"),sQuery(id+"F0.wireOp",EDGE,"E252"),sQuery(id+"F0.wireOp",EDGE,"E253"),sQuery(id+"F0.wireOp",EDGE,"E254"),sQuery(id+"F0.wireOp",EDGE,"E255"),sQuery(id+"F0.wireOp",EDGE,"E256"),sQuery(id+"F0.wireOp",EDGE,"E257"),sQuery(id+"F0.wireOp",EDGE,"E258"),sQuery(id+"F0.wireOp",EDGE,"E259"),sQuery(id+"F0.wireOp",EDGE,"E260"),sQuery(id+"F0.wireOp",EDGE,"E261"),sQuery(id+"F0.wireOp",EDGE,"E262"),sQuery(id+"F0.wireOp",EDGE,"E263"),sQuery(id+"F0.wireOp",EDGE,"E264"),sQuery(id+"F0.wireOp",EDGE,"E265"),sQuery(id+"F0.wireOp",EDGE,"E266"),sQuery(id+"F0.wireOp",EDGE,"E267"),sQuery(id+"F0.wireOp",EDGE,"E268"),sQuery(id+"F0.wireOp",EDGE,"E269"),sQuery(id+"F0.wireOp",EDGE,"E270"),sQuery(id+"F0.wireOp",EDGE,"E271"),sQuery(id+"F0.wireOp",EDGE,"E272"),sQuery(id+"F0.wireOp",EDGE,"E273"),sQuery(id+"F0.wireOp",EDGE,"E274"),sQuery(id+"F0.wireOp",EDGE,"E275"),sQuery(id+"F0.wireOp",EDGE,"E276"),sQuery(id+"F0.wireOp",EDGE,"E277"),sQuery(id+"F0.wireOp",EDGE,"E278"),sQuery(id+"F0.wireOp",EDGE,"E279"),sQuery(id+"F0.wireOp",EDGE,"E280"),sQuery(id+"F0.wireOp",EDGE,"E281"),sQuery(id+"F0.wireOp",EDGE,"E282"),sQuery(id+"F0.wireOp",EDGE,"E283"),sQuery(id+"F0.wireOp",EDGE,"E284"),sQuery(id+"F0.wireOp",EDGE,"E285"),sQuery(id+"F0.wireOp",EDGE,"E286"),sQuery(id+"F0.wireOp",EDGE,"E287"),sQuery(id+"F0.wireOp",EDGE,"E288"),sQuery(id+"F0.wireOp",EDGE,"E289"),sQuery(id+"F0.wireOp",EDGE,"E290"),sQuery(id+"F0.wireOp",EDGE,"E291"),sQuery(id+"F0.wireOp",EDGE,"E292"),sQuery(id+"F0.wireOp",EDGE,"E293"),sQuery(id+"F0.wireOp",EDGE,"E294"),sQuery(id+"F0.wireOp",EDGE,"E295"),sQuery(id+"F0.wireOp",EDGE,"E296"),sQuery(id+"F0.wireOp",EDGE,"E297"),sQuery(id+"F0.wireOp",EDGE,"E298"),sQuery(id+"F0.wireOp",EDGE,"E299"),sQuery(id+"F0.wireOp",EDGE,"E300"),sQuery(id+"F0.wireOp",EDGE,"E301"),sQuery(id+"F0.wireOp",EDGE,"E302"),sQuery(id+"F0.wireOp",EDGE,"E303"),sQuery(id+"F0.wireOp",EDGE,"E304"),sQuery(id+"F0.wireOp",EDGE,"E305"),sQuery(id+"F0.wireOp",EDGE,"E306"),sQuery(id+"F0.wireOp",EDGE,"E307"),sQuery(id+"F0.wireOp",EDGE,"E308"),sQuery(id+"F0.wireOp",EDGE,"E309"),sQuery(id+"F0.wireOp",EDGE,"E310"),sQuery(id+"F0.wireOp",EDGE,"E311"),sQuery(id+"F0.wireOp",EDGE,"E312"),sQuery(id+"F0.wireOp",EDGE,"E313"),sQuery(id+"F0.wireOp",EDGE,"E314"),sQuery(id+"F0.wireOp",EDGE,"E315"),sQuery(id+"F0.wireOp",EDGE,"E316"),sQuery(id+"F0.wireOp",EDGE,"E317"),sQuery(id+"F0.wireOp",EDGE,"E318"),sQuery(id+"F0.wireOp",EDGE,"E319"),sQuery(id+"F0.wireOp",EDGE,"E320"),sQuery(id+"F0.wireOp",EDGE,"E321"),sQuery(id+"F0.wireOp",EDGE,"E322"),sQuery(id+"F0.wireOp",EDGE,"E323"),sQuery(id+"F0.wireOp",EDGE,"E324"),sQuery(id+"F0.wireOp",EDGE,"E325"),sQuery(id+"F0.wireOp",EDGE,"E326"),sQuery(id+"F0.wireOp",EDGE,"E327"),sQuery(id+"F0.wireOp",EDGE,"E328"),sQuery(id+"F0.wireOp",EDGE,"E329"),sQuery(id+"F0.wireOp",EDGE,"E330"),sQuery(id+"F0.wireOp",EDGE,"E331"),sQuery(id+"F0.wireOp",EDGE,"E332"),sQuery(id+"F0.wireOp",EDGE,"E333"),sQuery(id+"F0.wireOp",EDGE,"E334"),sQuery(id+"F0.wireOp",EDGE,"E335"),sQuery(id+"F0.wireOp",EDGE,"E336"),sQuery(id+"F0.wireOp",EDGE,"E337"),sQuery(id+"F0.wireOp",EDGE,"E338"),sQuery(id+"F0.wireOp",EDGE,"E339"),sQuery(id+"F0.wireOp",EDGE,"E340"),sQuery(id+"F0.wireOp",EDGE,"E341"),sQuery(id+"F0.wireOp",EDGE,"E342"),sQuery(id+"F0.wireOp",EDGE,"E343"),sQuery(id+"F0.wireOp",EDGE,"E344"),sQuery(id+"F0.wireOp",EDGE,"E345"),sQuery(id+"F0.wireOp",EDGE,"E346"),sQuery(id+"F0.wireOp",EDGE,"E347"),sQuery(id+"F0.wireOp",EDGE,"E348"),sQuery(id+"F0.wireOp",EDGE,"E349"),sQuery(id+"F0.wireOp",EDGE,"E350"),sQuery(id+"F0.wireOp",EDGE,"E351"),sQuery(id+"F0.wireOp",EDGE,"E352"),sQuery(id+"F0.wireOp",EDGE,"E353"),sQuery(id+"F0.wireOp",EDGE,"E354"),sQuery(id+"F0.wireOp",EDGE,"E355"),sQuery(id+"F0.wireOp",EDGE,"E356"),sQuery(id+"F0.wireOp",EDGE,"E357"),sQuery(id+"F0.wireOp",EDGE,"E358"),sQuery(id+"F0.wireOp",EDGE,"E359"),sQuery(id+"F0.wireOp",EDGE,"E360"),sQuery(id+"F0.wireOp",EDGE,"E361"),sQuery(id+"F0.wireOp",EDGE,"E362"),sQuery(id+"F0.wireOp",EDGE,"E363"),sQuery(id+"F0.wireOp",EDGE,"E364"),sQuery(id+"F0.wireOp",EDGE,"E365"),sQuery(id+"F0.wireOp",EDGE,"E366"),sQuery(id+"F0.wireOp",EDGE,"E367"),sQuery(id+"F0.wireOp",EDGE,"E368"),sQuery(id+"F0.wireOp",EDGE,"E369"),sQuery(id+"F0.wireOp",EDGE,"E370"),sQuery(id+"F0.wireOp",EDGE,"E371"),sQuery(id+"F0.wireOp",EDGE,"E372"),sQuery(id+"F0.wireOp",EDGE,"E373"),sQuery(id+"F0.wireOp",EDGE,"E374"),sQuery(id+"F0.wireOp",EDGE,"E375"),sQuery(id+"F0.wireOp",EDGE,"E376"),sQuery(id+"F0.wireOp",EDGE,"E377"),sQuery(id+"F0.wireOp",EDGE,"E378"),sQuery(id+"F0.wireOp",EDGE,"E379"),sQuery(id+"F0.wireOp",EDGE,"E380"),sQuery(id+"F0.wireOp",EDGE,"E381"),sQuery(id+"F0.wireOp",EDGE,"E382"),sQuery(id+"F0.wireOp",EDGE,"E383"),sQuery(id+"F0.wireOp",EDGE,"E384"),sQuery(id+"F0.wireOp",EDGE,"E385"),sQuery(id+"F0.wireOp",EDGE,"E386"),sQuery(id+"F0.wireOp",EDGE,"E387"),sQuery(id+"F0.wireOp",EDGE,"E388"),sQuery(id+"F0.wireOp",EDGE,"E389"),sQuery(id+"F0.wireOp",EDGE,"E390"),sQuery(id+"F0.wireOp",EDGE,"E391"),sQuery(id+"F0.wireOp",EDGE,"E392"),sQuery(id+"F0.wireOp",EDGE,"E393"),sQuery(id+"F0.wireOp",EDGE,"E394"),sQuery(id+"F0.wireOp",EDGE,"E395"),sQuery(id+"F0.wireOp",EDGE,"E396"),sQuery(id+"F0.wireOp",EDGE,"E397"),sQuery(id+"F0.wireOp",EDGE,"E398"),sQuery(id+"F0.wireOp",EDGE,"E399"),sQuery(id+"F0.wireOp",EDGE,"E400"),sQuery(id+"F0.wireOp",EDGE,"E401"),sQuery(id+"F0.wireOp",EDGE,"E402"),sQuery(id+"F0.wireOp",EDGE,"E403"),sQuery(id+"F0.wireOp",EDGE,"E404"),sQuery(id+"F0.wireOp",EDGE,"E405"),sQuery(id+"F0.wireOp",EDGE,"E406"),sQuery(id+"F0.wireOp",EDGE,"E407"),sQuery(id+"F0.wireOp",EDGE,"E408"),sQuery(id+"F0.wireOp",EDGE,"E409"),sQuery(id+"F0.wireOp",EDGE,"E410"),sQuery(id+"F0.wireOp",EDGE,"E411"),sQuery(id+"F0.wireOp",EDGE,"E412"),sQuery(id+"F0.wireOp",EDGE,"E413"),sQuery(id+"F0.wireOp",EDGE,"E414"),sQuery(id+"F0.wireOp",EDGE,"E415"),sQuery(id+"F0.wireOp",EDGE,"E416"),sQuery(id+"F0.wireOp",EDGE,"E417"),sQuery(id+"F0.wireOp",EDGE,"E418"),sQuery(id+"F0.wireOp",EDGE,"E419"),sQuery(id+"F0.wireOp",EDGE,"E420"),sQuery(id+"F0.wireOp",EDGE,"E421"),sQuery(id+"F0.wireOp",EDGE,"E422"),sQuery(id+"F0.wireOp",EDGE,"E423"),sQuery(id+"F0.wireOp",EDGE,"E424"),sQuery(id+"F0.wireOp",EDGE,"E425"),sQuery(id+"F0.wireOp",EDGE,"E426"),sQuery(id+"F0.wireOp",EDGE,"E427"),sQuery(id+"F0.wireOp",EDGE,"E428"),sQuery(id+"F0.wireOp",EDGE,"E429"),sQuery(id+"F0.wireOp",EDGE,"E430"),sQuery(id+"F0.wireOp",EDGE,"E431"),sQuery(id+"F0.wireOp",EDGE,"E432"),sQuery(id+"F0.wireOp",EDGE,"E433"),sQuery(id+"F0.wireOp",EDGE,"E434"),sQuery(id+"F0.wireOp",EDGE,"E435"),sQuery(id+"F0.wireOp",EDGE,"E436"),sQuery(id+"F0.wireOp",EDGE,"E437"),sQuery(id+"F0.wireOp",EDGE,"E438"),sQuery(id+"F0.wireOp",EDGE,"E439"),sQuery(id+"F0.wireOp",EDGE,"E440"),sQuery(id+"F0.wireOp",EDGE,"E441"),sQuery(id+"F0.wireOp",EDGE,"E442"),sQuery(id+"F0.wireOp",EDGE,"E443"),sQuery(id+"F0.wireOp",EDGE,"E444"),sQuery(id+"F0.wireOp",EDGE,"E445"),sQuery(id+"F0.wireOp",EDGE,"E446"),sQuery(id+"F0.wireOp",EDGE,"E447"),sQuery(id+"F0.wireOp",EDGE,"E448"),sQuery(id+"F0.wireOp",EDGE,"E449"),sQuery(id+"F0.wireOp",EDGE,"E450"),sQuery(id+"F0.wireOp",EDGE,"E451"),sQuery(id+"F0.wireOp",EDGE,"E452"),sQuery(id+"F0.wireOp",EDGE,"E453"),sQuery(id+"F0.wireOp",EDGE,"E454"),sQuery(id+"F0.wireOp",EDGE,"E455"),sQuery(id+"F0.wireOp",EDGE,"E456"),sQuery(id+"F0.wireOp",EDGE,"E457"),sQuery(id+"F0.wireOp",EDGE,"E458"),sQuery(id+"F0.wireOp",EDGE,"E459"),sQuery(id+"F0.wireOp",EDGE,"E460"),sQuery(id+"F0.wireOp",EDGE,"E461"),sQuery(id+"F0.wireOp",EDGE,"E462"),sQuery(id+"F0.wireOp",EDGE,"E463"),sQuery(id+"F0.wireOp",EDGE,"E464"),sQuery(id+"F0.wireOp",EDGE,"E465"),sQuery(id+"F0.wireOp",EDGE,"E466"),sQuery(id+"F0.wireOp",EDGE,"E467"),sQuery(id+"F0.wireOp",EDGE,"E468"),sQuery(id+"F0.wireOp",EDGE,"E469"),sQuery(id+"F0.wireOp",EDGE,"E470"),sQuery(id+"F0.wireOp",EDGE,"E471"),sQuery(id+"F0.wireOp",EDGE,"E472"),sQuery(id+"F0.wireOp",EDGE,"E473"),sQuery(id+"F0.wireOp",EDGE,"E474"),sQuery(id+"F0.wireOp",EDGE,"E475"),sQuery(id+"F0.wireOp",EDGE,"E476"),sQuery(id+"F0.wireOp",EDGE,"E477"),sQuery(id+"F0.wireOp",EDGE,"E478"),sQuery(id+"F0.wireOp",EDGE,"E479"),sQuery(id+"F0.wireOp",EDGE,"E480"),sQuery(id+"F0.wireOp",EDGE,"E481"),sQuery(id+"F0.wireOp",EDGE,"E482"),sQuery(id+"F0.wireOp",EDGE,"E483"),sQuery(id+"F0.wireOp",EDGE,"E484"),sQuery(id+"F0.wireOp",EDGE,"E485"),sQuery(id+"F0.wireOp",EDGE,"E486"),sQuery(id+"F0.wireOp",EDGE,"E487"),sQuery(id+"F0.wireOp",EDGE,"E488"),sQuery(id+"F0.wireOp",EDGE,"E489"),sQuery(id+"F0.wireOp",EDGE,"E490"),sQuery(id+"F0.wireOp",EDGE,"E491"),sQuery(id+"F0.wireOp",EDGE,"E492"),sQuery(id+"F0.wireOp",EDGE,"E493"),sQuery(id+"F0.wireOp",EDGE,"E494"),sQuery(id+"F0.wireOp",EDGE,"E495"),sQuery(id+"F0.wireOp",EDGE,"E496"),sQuery(id+"F0.wireOp",EDGE,"E497"),sQuery(id+"F0.wireOp",EDGE,"E498"),sQuery(id+"F0.wireOp",EDGE,"E499"),sQuery(id+"F0.wireOp",EDGE,"E500"),sQuery(id+"F0.wireOp",EDGE,"E501"),sQuery(id+"F0.wireOp",EDGE,"E502"),sQuery(id+"F0.wireOp",EDGE,"E503"),sQuery(id+"F0.wireOp",EDGE,"E504"),sQuery(id+"F0.wireOp",EDGE,"E505"),sQuery(id+"F0.wireOp",EDGE,"E506"),sQuery(id+"F0.wireOp",EDGE,"E507"),sQuery(id+"F0.wireOp",EDGE,"E508"),sQuery(id+"F0.wireOp",EDGE,"E509"),sQuery(id+"F0.wireOp",EDGE,"E510"),sQuery(id+"F0.wireOp",EDGE,"E511"),sQuery(id+"F0.wireOp",EDGE,"E512"),sQuery(id+"F0.wireOp",EDGE,"E513"),sQuery(id+"F0.wireOp",EDGE,"E514"),sQuery(id+"F0.wireOp",EDGE,"E515"),sQuery(id+"F0.wireOp",EDGE,"E516"),sQuery(id+"F0.wireOp",EDGE,"E517"),sQuery(id+"F0.wireOp",EDGE,"E518"),sQuery(id+"F0.wireOp",EDGE,"E519"),sQuery(id+"F0.wireOp",EDGE,"E520"),sQuery(id+"F0.wireOp",EDGE,"E521"),sQuery(id+"F0.wireOp",EDGE,"E522"),sQuery(id+"F0.wireOp",EDGE,"E523"),sQuery(id+"F0.wireOp",EDGE,"E524"),sQuery(id+"F0.wireOp",EDGE,"E525"),sQuery(id+"F0.wireOp",EDGE,"E526"),sQuery(id+"F0.wireOp",EDGE,"E527"),sQuery(id+"F0.wireOp",EDGE,"E528"),sQuery(id+"F0.wireOp",EDGE,"E529"),sQuery(id+"F0.wireOp",EDGE,"E530"),sQuery(id+"F0.wireOp",EDGE,"E531"),sQuery(id+"F0.wireOp",EDGE,"E532"),sQuery(id+"F0.wireOp",EDGE,"E533"),sQuery(id+"F0.wireOp",EDGE,"E534"),sQuery(id+"F0.wireOp",EDGE,"E535"),sQuery(id+"F0.wireOp",EDGE,"E536"),sQuery(id+"F0.wireOp",EDGE,"E537"),sQuery(id+"F0.wireOp",EDGE,"E538"),sQuery(id+"F0.wireOp",EDGE,"E539"),sQuery(id+"F0.wireOp",EDGE,"E540"),sQuery(id+"F0.wireOp",EDGE,"E541"),sQuery(id+"F0.wireOp",EDGE,"E542"),sQuery(id+"F0.wireOp",EDGE,"E543"),sQuery(id+"F0.wireOp",EDGE,"E544"),sQuery(id+"F0.wireOp",EDGE,"E545"),sQuery(id+"F0.wireOp",EDGE,"E546"),sQuery(id+"F0.wireOp",EDGE,"E547"),sQuery(id+"F0.wireOp",EDGE,"E548"),sQuery(id+"F0.wireOp",EDGE,"E549"),sQuery(id+"F0.wireOp",EDGE,"E550"),sQuery(id+"F0.wireOp",EDGE,"E551"),sQuery(id+"F0.wireOp",EDGE,"E552"),sQuery(id+"F0.wireOp",EDGE,"E553"),sQuery(id+"F0.wireOp",EDGE,"E554"),sQuery(id+"F0.wireOp",EDGE,"E555"),sQuery(id+"F0.wireOp",EDGE,"E556"),sQuery(id+"F0.wireOp",EDGE,"E557"),sQuery(id+"F0.wireOp",EDGE,"E558"),sQuery(id+"F0.wireOp",EDGE,"E559"),sQuery(id+"F0.wireOp",EDGE,"E560"),sQuery(id+"F0.wireOp",EDGE,"E561"),sQuery(id+"F0.wireOp",EDGE,"E562"),sQuery(id+"F0.wireOp",EDGE,"E563"),sQuery(id+"F0.wireOp",EDGE,"E564"),sQuery(id+"F0.wireOp",EDGE,"E565"),sQuery(id+"F0.wireOp",EDGE,"E566"),sQuery(id+"F0.wireOp",EDGE,"E567"),sQuery(id+"F0.wireOp",EDGE,"E568"),sQuery(id+"F0.wireOp",EDGE,"E569"),sQuery(id+"F0.wireOp",EDGE,"E570"),sQuery(id+"F0.wireOp",EDGE,"E571"),sQuery(id+"F0.wireOp",EDGE,"E572"),sQuery(id+"F0.wireOp",EDGE,"E573"),sQuery(id+"F0.wireOp",EDGE,"E574"),sQuery(id+"F0.wireOp",EDGE,"E575"),sQuery(id+"F0.wireOp",EDGE,"E576"),sQuery(id+"F0.wireOp",EDGE,"E577"),sQuery(id+"F0.wireOp",EDGE,"E578"),sQuery(id+"F0.wireOp",EDGE,"E579"),sQuery(id+"F0.wireOp",EDGE,"E580"),sQuery(id+"F0.wireOp",EDGE,"E581"),sQuery(id+"F0.wireOp",EDGE,"E582"),sQuery(id+"F0.wireOp",EDGE,"E583"),sQuery(id+"F0.wireOp",EDGE,"E584"),sQuery(id+"F0.wireOp",EDGE,"E585"),sQuery(id+"F0.wireOp",EDGE,"E586"),sQuery(id+"F0.wireOp",EDGE,"E587"),sQuery(id+"F0.wireOp",EDGE,"E588"),sQuery(id+"F0.wireOp",EDGE,"E589"),sQuery(id+"F0.wireOp",EDGE,"E590"),sQuery(id+"F0.wireOp",EDGE,"E591"),sQuery(id+"F0.wireOp",EDGE,"E592"),sQuery(id+"F0.wireOp",EDGE,"E593"),sQuery(id+"F0.wireOp",EDGE,"E594"),sQuery(id+"F0.wireOp",EDGE,"E595"),sQuery(id+"F0.wireOp",EDGE,"E596"),sQuery(id+"F0.wireOp",EDGE,"E597"),sQuery(id+"F0.wireOp",EDGE,"E598"),sQuery(id+"F0.wireOp",EDGE,"E599"),sQuery(id+"F0.wireOp",EDGE,"E600"),sQuery(id+"F0.wireOp",EDGE,"E601"),sQuery(id+"F0.wireOp",EDGE,"E602"),sQuery(id+"F0.wireOp",EDGE,"E603"),sQuery(id+"F0.wireOp",EDGE,"E604"),sQuery(id+"F0.wireOp",EDGE,"E605"),sQuery(id+"F0.wireOp",EDGE,"E606"),sQuery(id+"F0.wireOp",EDGE,"E607"),sQuery(id+"F0.wireOp",EDGE,"E608"),sQuery(id+"F0.wireOp",EDGE,"E609"),sQuery(id+"F0.wireOp",EDGE,"E610"),sQuery(id+"F0.wireOp",EDGE,"E611"),sQuery(id+"F0.wireOp",EDGE,"E612"),sQuery(id+"F0.wireOp",EDGE,"E613"),sQuery(id+"F0.wireOp",EDGE,"E614"),sQuery(id+"F0.wireOp",EDGE,"E615"),sQuery(id+"F0.wireOp",EDGE,"E616"),sQuery(id+"F0.wireOp",EDGE,"E617"),sQuery(id+"F0.wireOp",EDGE,"E618"),sQuery(id+"F0.wireOp",EDGE,"E619"),sQuery(id+"F0.wireOp",EDGE,"E620"),sQuery(id+"F0.wireOp",EDGE,"E621"),sQuery(id+"F0.wireOp",EDGE,"E622"),sQuery(id+"F0.wireOp",EDGE,"E623"),sQuery(id+"F0.wireOp",EDGE,"E624"),sQuery(id+"F0.wireOp",EDGE,"E625"),sQuery(id+"F0.wireOp",EDGE,"E626"),sQuery(id+"F0.wireOp",EDGE,"E627"),sQuery(id+"F0.wireOp",EDGE,"E628"),sQuery(id+"F0.wireOp",EDGE,"E629"),sQuery(id+"F0.wireOp",EDGE,"E630"),sQuery(id+"F0.wireOp",EDGE,"E631"),sQuery(id+"F0.wireOp",EDGE,"E632"),sQuery(id+"F0.wireOp",EDGE,"E633"),sQuery(id+"F0.wireOp",EDGE,"E634"),sQuery(id+"F0.wireOp",EDGE,"E635"),sQuery(id+"F0.wireOp",EDGE,"E636"),sQuery(id+"F0.wireOp",EDGE,"E637"),sQuery(id+"F0.wireOp",EDGE,"E638"),sQuery(id+"F0.wireOp",EDGE,"E639"),sQuery(id+"F0.wireOp",EDGE,"E640"),sQuery(id+"F0.wireOp",EDGE,"E641"),sQuery(id+"F0.wireOp",EDGE,"E642"),sQuery(id+"F0.wireOp",EDGE,"E643"),sQuery(id+"F0.wireOp",EDGE,"E644"),sQuery(id+"F0.wireOp",EDGE,"E645"),sQuery(id+"F0.wireOp",EDGE,"E646"),sQuery(id+"F0.wireOp",EDGE,"E647"),sQuery(id+"F0.wireOp",EDGE,"E648"),sQuery(id+"F0.wireOp",EDGE,"E649"),sQuery(id+"F0.wireOp",EDGE,"E650"),sQuery(id+"F0.wireOp",EDGE,"E651"),sQuery(id+"F0.wireOp",EDGE,"E652"),sQuery(id+"F0.wireOp",EDGE,"E653"),sQuery(id+"F0.wireOp",EDGE,"E654"),sQuery(id+"F0.wireOp",EDGE,"E655"),sQuery(id+"F0.wireOp",EDGE,"E656"),sQuery(id+"F0.wireOp",EDGE,"E657"),sQuery(id+"F0.wireOp",EDGE,"E658"),sQuery(id+"F0.wireOp",EDGE,"E659"),sQuery(id+"F0.wireOp",EDGE,"E660"),sQuery(id+"F0.wireOp",EDGE,"E661"),sQuery(id+"F0.wireOp",EDGE,"E662"),sQuery(id+"F0.wireOp",EDGE,"E663"),sQuery(id+"F0.wireOp",EDGE,"E664"),sQuery(id+"F0.wireOp",EDGE,"E665"),sQuery(id+"F0.wireOp",EDGE,"E666"),sQuery(id+"F0.wireOp",EDGE,"E667"),sQuery(id+"F0.wireOp",EDGE,"E668"),sQuery(id+"F0.wireOp",EDGE,"E669"),sQuery(id+"F0.wireOp",EDGE,"E670"),sQuery(id+"F0.wireOp",EDGE,"E671"),sQuery(id+"F0.wireOp",EDGE,"E672"),sQuery(id+"F0.wireOp",EDGE,"E673"),sQuery(id+"F0.wireOp",EDGE,"E674"),sQuery(id+"F0.wireOp",EDGE,"E675"),sQuery(id+"F0.wireOp",EDGE,"E676"),sQuery(id+"F0.wireOp",EDGE,"E677"),sQuery(id+"F0.wireOp",EDGE,"E678"),sQuery(id+"F0.wireOp",EDGE,"E679"),sQuery(id+"F0.wireOp",EDGE,"E680"),sQuery(id+"F0.wireOp",EDGE,"E681"),sQuery(id+"F0.wireOp",EDGE,"E682"),sQuery(id+"F0.wireOp",EDGE,"E683"),sQuery(id+"F0.wireOp",EDGE,"E684"),sQuery(id+"F0.wireOp",EDGE,"E685"),sQuery(id+"F0.wireOp",EDGE,"E686"),sQuery(id+"F0.wireOp",EDGE,"E687"),sQuery(id+"F0.wireOp",EDGE,"E688"),sQuery(id+"F0.wireOp",EDGE,"E689"),sQuery(id+"F0.wireOp",EDGE,"E690"),sQuery(id+"F0.wireOp",EDGE,"E691"),sQuery(id+"F0.wireOp",EDGE,"E692"),sQuery(id+"F0.wireOp",EDGE,"E693"),sQuery(id+"F0.wireOp",EDGE,"E694"),sQuery(id+"F0.wireOp",EDGE,"E695"),sQuery(id+"F0.wireOp",EDGE,"E696"),sQuery(id+"F0.wireOp",EDGE,"E697"),sQuery(id+"F0.wireOp",EDGE,"E698"),sQuery(id+"F0.wireOp",EDGE,"E699"),sQuery(id+"F0.wireOp",EDGE,"E700"),sQuery(id+"F0.wireOp",EDGE,"E701"),sQuery(id+"F0.wireOp",EDGE,"E702"),sQuery(id+"F0.wireOp",EDGE,"E703"),sQuery(id+"F0.wireOp",EDGE,"E704"),sQuery(id+"F0.wireOp",EDGE,"E705"),sQuery(id+"F0.wireOp",EDGE,"E706"),sQuery(id+"F0.wireOp",EDGE,"E707"),sQuery(id+"F0.wireOp",EDGE,"E708"),sQuery(id+"F0.wireOp",EDGE,"E709"),sQuery(id+"F0.wireOp",EDGE,"E710"),sQuery(id+"F0.wireOp",EDGE,"E711"),sQuery(id+"F0.wireOp",EDGE,"E712"),sQuery(id+"F0.wireOp",EDGE,"E713"),sQuery(id+"F0.wireOp",EDGE,"E714"),sQuery(id+"F0.wireOp",EDGE,"E715"),sQuery(id+"F0.wireOp",EDGE,"E716"),sQuery(id+"F0.wireOp",EDGE,"E717"),sQuery(id+"F0.wireOp",EDGE,"E718"),sQuery(id+"F0.wireOp",EDGE,"E719"),sQuery(id+"F0.wireOp",EDGE,"E720"),sQuery(id+"F0.wireOp",EDGE,"E721"),sQuery(id+"F0.wireOp",EDGE,"E722"),sQuery(id+"F0.wireOp",EDGE,"E723"),sQuery(id+"F0.wireOp",EDGE,"E724"),sQuery(id+"F0.wireOp",EDGE,"E725"),sQuery(id+"F0.wireOp",EDGE,"E726"),sQuery(id+"F0.wireOp",EDGE,"E727"),sQuery(id+"F0.wireOp",EDGE,"E728"),sQuery(id+"F0.wireOp",EDGE,"E729"),sQuery(id+"F0.wireOp",EDGE,"E730"),sQuery(id+"F0.wireOp",EDGE,"E731"),sQuery(id+"F0.wireOp",EDGE,"E732"),sQuery(id+"F0.wireOp",EDGE,"E733"),sQuery(id+"F0.wireOp",EDGE,"E734"),sQuery(id+"F0.wireOp",EDGE,"E735"),sQuery(id+"F0.wireOp",EDGE,"E736"),sQuery(id+"F0.wireOp",EDGE,"E737"),sQuery(id+"F0.wireOp",EDGE,"E738"),sQuery(id+"F0.wireOp",EDGE,"E739"),sQuery(id+"F0.wireOp",EDGE,"E740"),sQuery(id+"F0.wireOp",EDGE,"E741"),sQuery(id+"F0.wireOp",EDGE,"E742"),sQuery(id+"F0.wireOp",EDGE,"E743"),sQuery(id+"F0.wireOp",EDGE,"E744"),sQuery(id+"F0.wireOp",EDGE,"E745"),sQuery(id+"F0.wireOp",EDGE,"E746"),sQuery(id+"F0.wireOp",EDGE,"E747"),sQuery(id+"F0.wireOp",EDGE,"E748"),sQuery(id+"F0.wireOp",EDGE,"E749"),sQuery(id+"F0.wireOp",EDGE,"E750"),sQuery(id+"F0.wireOp",EDGE,"E751"),sQuery(id+"F0.wireOp",EDGE,"E752"),sQuery(id+"F0.wireOp",EDGE,"E753"),sQuery(id+"F0.wireOp",EDGE,"E754"),sQuery(id+"F0.wireOp",EDGE,"E755"),sQuery(id+"F0.wireOp",EDGE,"E756"),sQuery(id+"F0.wireOp",EDGE,"E757"),sQuery(id+"F0.wireOp",EDGE,"E758"),sQuery(id+"F0.wireOp",EDGE,"E759"),sQuery(id+"F0.wireOp",EDGE,"E760"),sQuery(id+"F0.wireOp",EDGE,"E761"),sQuery(id+"F0.wireOp",EDGE,"E762"),sQuery(id+"F0.wireOp",EDGE,"E763"),sQuery(id+"F0.wireOp",EDGE,"E764"),sQuery(id+"F0.wireOp",EDGE,"E765"),sQuery(id+"F0.wireOp",EDGE,"E766"),sQuery(id+"F0.wireOp",EDGE,"E767"),sQuery(id+"F0.wireOp",EDGE,"E768"),sQuery(id+"F0.wireOp",EDGE,"E769"),sQuery(id+"F0.wireOp",EDGE,"E770"),sQuery(id+"F0.wireOp",EDGE,"E771"),sQuery(id+"F0.wireOp",EDGE,"E772"),sQuery(id+"F0.wireOp",EDGE,"E773"),sQuery(id+"F0.wireOp",EDGE,"E774"),sQuery(id+"F0.wireOp",EDGE,"E775"),sQuery(id+"F0.wireOp",EDGE,"E776"),sQuery(id+"F0.wireOp",EDGE,"E777"),sQuery(id+"F0.wireOp",EDGE,"E778"),sQuery(id+"F0.wireOp",EDGE,"E779"),sQuery(id+"F0.wireOp",EDGE,"E780"),sQuery(id+"F0.wireOp",EDGE,"E781"),sQuery(id+"F0.wireOp",EDGE,"E782"),sQuery(id+"F0.wireOp",EDGE,"E783"),sQuery(id+"F0.wireOp",EDGE,"E784"),sQuery(id+"F0.wireOp",EDGE,"E785"),sQuery(id+"F0.wireOp",EDGE,"E786"),sQuery(id+"F0.wireOp",EDGE,"E787"),sQuery(id+"F0.wireOp",EDGE,"E788"),sQuery(id+"F0.wireOp",EDGE,"E789"),sQuery(id+"F0.wireOp",EDGE,"E790"),sQuery(id+"F0.wireOp",EDGE,"E791"),sQuery(id+"F0.wireOp",EDGE,"E792"),sQuery(id+"F0.wireOp",EDGE,"E793"),sQuery(id+"F0.wireOp",EDGE,"E794"),sQuery(id+"F0.wireOp",EDGE,"E795"),sQuery(id+"F0.wireOp",EDGE,"E796"),sQuery(id+"F0.wireOp",EDGE,"E797"),sQuery(id+"F0.wireOp",EDGE,"E798"),sQuery(id+"F0.wireOp",EDGE,"E799"),sQuery(id+"F0.wireOp",EDGE,"E800"),sQuery(id+"F0.wireOp",EDGE,"E801"),sQuery(id+"F0.wireOp",EDGE,"E802"),sQuery(id+"F0.wireOp",EDGE,"E803"),sQuery(id+"F0.wireOp",EDGE,"E804"),sQuery(id+"F0.wireOp",EDGE,"E805"),sQuery(id+"F0.wireOp",EDGE,"E806"),sQuery(id+"F0.wireOp",EDGE,"E807"),sQuery(id+"F0.wireOp",EDGE,"E808"),sQuery(id+"F0.wireOp",EDGE,"E809"),sQuery(id+"F0.wireOp",EDGE,"E810"),sQuery(id+"F0.wireOp",EDGE,"E811"),sQuery(id+"F0.wireOp",EDGE,"E812"),sQuery(id+"F0.wireOp",EDGE,"E813"),sQuery(id+"F0.wireOp",EDGE,"E814"),sQuery(id+"F0.wireOp",EDGE,"E815"),sQuery(id+"F0.wireOp",EDGE,"E816"),sQuery(id+"F0.wireOp",EDGE,"E817"),sQuery(id+"F0.wireOp",EDGE,"E818"),sQuery(id+"F0.wireOp",EDGE,"E819"),sQuery(id+"F0.wireOp",EDGE,"E820"),sQuery(id+"F0.wireOp",EDGE,"E821"),sQuery(id+"F0.wireOp",EDGE,"E822"),sQuery(id+"F0.wireOp",EDGE,"E823"),sQuery(id+"F0.wireOp",EDGE,"E824"),sQuery(id+"F0.wireOp",EDGE,"E825"),sQuery(id+"F0.wireOp",EDGE,"E826"),sQuery(id+"F0.wireOp",EDGE,"E827"),sQuery(id+"F0.wireOp",EDGE,"E828"),sQuery(id+"F0.wireOp",EDGE,"E829"),sQuery(id+"F0.wireOp",EDGE,"E830"),sQuery(id+"F0.wireOp",EDGE,"E831"),sQuery(id+"F0.wireOp",EDGE,"E832"),sQuery(id+"F0.wireOp",EDGE,"E833"),sQuery(id+"F0.wireOp",EDGE,"E834"),sQuery(id+"F0.wireOp",EDGE,"E835"),sQuery(id+"F0.wireOp",EDGE,"E836"),sQuery(id+"F0.wireOp",EDGE,"E837"),sQuery(id+"F0.wireOp",EDGE,"E838"),sQuery(id+"F0.wireOp",EDGE,"E839"),sQuery(id+"F0.wireOp",EDGE,"E840"),sQuery(id+"F0.wireOp",EDGE,"E841"),sQuery(id+"F0.wireOp",EDGE,"E842"),sQuery(id+"F0.wireOp",EDGE,"E843"),sQuery(id+"F0.wireOp",EDGE,"E844"),sQuery(id+"F0.wireOp",EDGE,"E845"),sQuery(id+"F0.wireOp",EDGE,"E846"),sQuery(id+"F0.wireOp",EDGE,"E847"),sQuery(id+"F0.wireOp",EDGE,"E848"),sQuery(id+"F0.wireOp",EDGE,"E849"),sQuery(id+"F0.wireOp",EDGE,"E850"),sQuery(id+"F0.wireOp",EDGE,"E851"),sQuery(id+"F0.wireOp",EDGE,"E852"),sQuery(id+"F0.wireOp",EDGE,"E853"),sQuery(id+"F0.wireOp",EDGE,"E854"),sQuery(id+"F0.wireOp",EDGE,"E855"),sQuery(id+"F0.wireOp",EDGE,"E856"),sQuery(id+"F0.wireOp",EDGE,"E857"),sQuery(id+"F0.wireOp",EDGE,"E858"),sQuery(id+"F0.wireOp",EDGE,"E859"),sQuery(id+"F0.wireOp",EDGE,"E860"),sQuery(id+"F0.wireOp",EDGE,"E861"),sQuery(id+"F0.wireOp",EDGE,"E862"),sQuery(id+"F0.wireOp",EDGE,"E863"),sQuery(id+"F0.wireOp",EDGE,"E864"),sQuery(id+"F0.wireOp",EDGE,"E865"),sQuery(id+"F0.wireOp",EDGE,"E866"),sQuery(id+"F0.wireOp",EDGE,"E867"),sQuery(id+"F0.wireOp",EDGE,"E868"),sQuery(id+"F0.wireOp",EDGE,"E869"),sQuery(id+"F0.wireOp",EDGE,"E870"),sQuery(id+"F0.wireOp",EDGE,"E871"),sQuery(id+"F0.wireOp",EDGE,"E872"),sQuery(id+"F0.wireOp",EDGE,"E873"),sQuery(id+"F0.wireOp",EDGE,"E874"),sQuery(id+"F0.wireOp",EDGE,"E875"),sQuery(id+"F0.wireOp",EDGE,"E876"),sQuery(id+"F0.wireOp",EDGE,"E877"),sQuery(id+"F0.wireOp",EDGE,"E878"),sQuery(id+"F0.wireOp",EDGE,"E879"),sQuery(id+"F0.wireOp",EDGE,"E880"),sQuery(id+"F0.wireOp",EDGE,"E881"),sQuery(id+"F0.wireOp",EDGE,"E882"),sQuery(id+"F0.wireOp",EDGE,"E883"),sQuery(id+"F0.wireOp",EDGE,"E884"),sQuery(id+"F0.wireOp",EDGE,"E885"),sQuery(id+"F0.wireOp",EDGE,"E886"),sQuery(id+"F0.wireOp",EDGE,"E887"),sQuery(id+"F0.wireOp",EDGE,"E888"),sQuery(id+"F0.wireOp",EDGE,"E889"),sQuery(id+"F0.wireOp",EDGE,"E890"),sQuery(id+"F0.wireOp",EDGE,"E891"),sQuery(id+"F0.wireOp",EDGE,"E892"),sQuery(id+"F0.wireOp",EDGE,"E893"),sQuery(id+"F0.wireOp",EDGE,"E894"),sQuery(id+"F0.wireOp",EDGE,"E895"),sQuery(id+"F0.wireOp",EDGE,"E896"),sQuery(id+"F0.wireOp",EDGE,"E897"),sQuery(id+"F0.wireOp",EDGE,"E898"),sQuery(id+"F0.wireOp",EDGE,"E899"),sQuery(id+"F0.wireOp",EDGE,"E900"),sQuery(id+"F0.wireOp",EDGE,"E901"),sQuery(id+"F0.wireOp",EDGE,"E902"),sQuery(id+"F0.wireOp",EDGE,"E903"),sQuery(id+"F0.wireOp",EDGE,"E904"),sQuery(id+"F0.wireOp",EDGE,"E905"),sQuery(id+"F0.wireOp",EDGE,"E906"),sQuery(id+"F0.wireOp",EDGE,"E907"),sQuery(id+"F0.wireOp",EDGE,"E908"),sQuery(id+"F0.wireOp",EDGE,"E909"),sQuery(id+"F0.wireOp",EDGE,"E910"),sQuery(id+"F0.wireOp",EDGE,"E911"),sQuery(id+"F0.wireOp",EDGE,"E912"),sQuery(id+"F0.wireOp",EDGE,"E913"),sQuery(id+"F0.wireOp",EDGE,"E914"),sQuery(id+"F0.wireOp",EDGE,"E915"),sQuery(id+"F0.wireOp",EDGE,"E916"),sQuery(id+"F0.wireOp",EDGE,"E917"),sQuery(id+"F0.wireOp",EDGE,"E918"),sQuery(id+"F0.wireOp",EDGE,"E919"),sQuery(id+"F0.wireOp",EDGE,"E920"),sQuery(id+"F0.wireOp",EDGE,"E921"),sQuery(id+"F0.wireOp",EDGE,"E922"),sQuery(id+"F0.wireOp",EDGE,"E923"),sQuery(id+"F0.wireOp",EDGE,"E924"),sQuery(id+"F0.wireOp",EDGE,"E925"),sQuery(id+"F0.wireOp",EDGE,"E926"),sQuery(id+"F0.wireOp",EDGE,"E927"),sQuery(id+"F0.wireOp",EDGE,"E928"),sQuery(id+"F0.wireOp",EDGE,"E929"),sQuery(id+"F0.wireOp",EDGE,"E930"),sQuery(id+"F0.wireOp",EDGE,"E931"),sQuery(id+"F0.wireOp",EDGE,"E932"),sQuery(id+"F0.wireOp",EDGE,"E933"),sQuery(id+"F0.wireOp",EDGE,"E934"),sQuery(id+"F0.wireOp",EDGE,"E935"),sQuery(id+"F0.wireOp",EDGE,"E936"),sQuery(id+"F0.wireOp",EDGE,"E937"),sQuery(id+"F0.wireOp",EDGE,"E938"),sQuery(id+"F0.wireOp",EDGE,"E939"),sQuery(id+"F0.wireOp",EDGE,"E940"),sQuery(id+"F0.wireOp",EDGE,"E941"),sQuery(id+"F0.wireOp",EDGE,"E942"),sQuery(id+"F0.wireOp",EDGE,"E943"),sQuery(id+"F0.wireOp",EDGE,"E944"),sQuery(id+"F0.wireOp",EDGE,"E945"),sQuery(id+"F0.wireOp",EDGE,"E946"),sQuery(id+"F0.wireOp",EDGE,"E947"),sQuery(id+"F0.wireOp",EDGE,"E948"),sQuery(id+"F0.wireOp",EDGE,"E949"),sQuery(id+"F0.wireOp",EDGE,"E950"),sQuery(id+"F0.wireOp",EDGE,"E951"),sQuery(id+"F0.wireOp",EDGE,"E952"),sQuery(id+"F0.wireOp",EDGE,"E953"),sQuery(id+"F0.wireOp",EDGE,"E954"),sQuery(id+"F0.wireOp",EDGE,"E955"),sQuery(id+"F0.wireOp",EDGE,"E956"),sQuery(id+"F0.wireOp",EDGE,"E957"),sQuery(id+"F0.wireOp",EDGE,"E958"),sQuery(id+"F0.wireOp",EDGE,"E959"),sQuery(id+"F0.wireOp",EDGE,"E960"),sQuery(id+"F0.wireOp",EDGE,"E961"),sQuery(id+"F0.wireOp",EDGE,"E962"),sQuery(id+"F0.wireOp",EDGE,"E963"),sQuery(id+"F0.wireOp",EDGE,"E964"),sQuery(id+"F0.wireOp",EDGE,"E965"),sQuery(id+"F0.wireOp",EDGE,"E966"),sQuery(id+"F0.wireOp",EDGE,"E967"),sQuery(id+"F0.wireOp",EDGE,"E968"),sQuery(id+"F0.wireOp",EDGE,"E969"),sQuery(id+"F0.wireOp",EDGE,"E970"),sQuery(id+"F0.wireOp",EDGE,"E971"),sQuery(id+"F0.wireOp",EDGE,"E972"),sQuery(id+"F0.wireOp",EDGE,"E973"),sQuery(id+"F0.wireOp",EDGE,"E974"),sQuery(id+"F0.wireOp",EDGE,"E975"),sQuery(id+"F0.wireOp",EDGE,"E976"),sQuery(id+"F0.wireOp",EDGE,"E977"),sQuery(id+"F0.wireOp",EDGE,"E978"),sQuery(id+"F0.wireOp",EDGE,"E979"),sQuery(id+"F0.wireOp",EDGE,"E980"),sQuery(id+"F0.wireOp",EDGE,"E981"),sQuery(id+"F0.wireOp",EDGE,"E982"),sQuery(id+"F0.wireOp",EDGE,"E983"),sQuery(id+"F0.wireOp",EDGE,"E984"),sQuery(id+"F0.wireOp",EDGE,"E985"),sQuery(id+"F0.wireOp",EDGE,"E986"),sQuery(id+"F0.wireOp",EDGE,"E987"),sQuery(id+"F0.wireOp",EDGE,"E988"),sQuery(id+"F0.wireOp",EDGE,"E989"),sQuery(id+"F0.wireOp",EDGE,"E990"),sQuery(id+"F0.wireOp",EDGE,"E991"),sQuery(id+"F0.wireOp",EDGE,"E992"),sQuery(id+"F0.wireOp",EDGE,"E993"),sQuery(id+"F0.wireOp",EDGE,"E994"),sQuery(id+"F0.wireOp",EDGE,"E995"),sQuery(id+"F0.wireOp",EDGE,"E996"),sQuery(id+"F0.wireOp",EDGE,"E997"),sQuery(id+"F0.wireOp",EDGE,"E998"),sQuery(id+"F0.wireOp",EDGE,"E999"),sQuery(id+"F0.wireOp",EDGE,"E1000"),sQuery(id+"F0.wireOp",EDGE,"E1001"),sQuery(id+"F0.wireOp",EDGE,"E1002"),sQuery(id+"F0.wireOp",EDGE,"E1003"),sQuery(id+"F0.wireOp",EDGE,"E1004"),sQuery(id+"F0.wireOp",EDGE,"E1005"),sQuery(id+"F0.wireOp",EDGE,"E1006"),sQuery(id+"F0.wireOp",EDGE,"E1007"),sQuery(id+"F0.wireOp",EDGE,"E1008"),sQuery(id+"F0.wireOp",EDGE,"E1009"),sQuery(id+"F0.wireOp",EDGE,"E1010"),sQuery(id+"F0.wireOp",EDGE,"E1011"),sQuery(id+"F0.wireOp",EDGE,"E1012"),sQuery(id+"F0.wireOp",EDGE,"E1013"),sQuery(id+"F0.wireOp",EDGE,"E1014"),sQuery(id+"F0.wireOp",EDGE,"E1015"),sQuery(id+"F0.wireOp",EDGE,"E1016"),sQuery(id+"F0.wireOp",EDGE,"E1017"),sQuery(id+"F0.wireOp",EDGE,"E1018"),sQuery(id+"F0.wireOp",EDGE,"E1019"),sQuery(id+"F0.wireOp",EDGE,"E1020"),sQuery(id+"F0.wireOp",EDGE,"E1021"),sQuery(id+"F0.wireOp",EDGE,"E1022"),sQuery(id+"F0.wireOp",EDGE,"E1023"),sQuery(id+"F0.wireOp",EDGE,"E1024"),sQuery(id+"F0.wireOp",EDGE,"E1025"),sQuery(id+"F0.wireOp",EDGE,"E1026"),sQuery(id+"F0.wireOp",EDGE,"E1027"),sQuery(id+"F0.wireOp",EDGE,"E1028"),sQuery(id+"F0.wireOp",EDGE,"E1029"),sQuery(id+"F0.wireOp",EDGE,"E1030"),sQuery(id+"F0.wireOp",EDGE,"E1031"),sQuery(id+"F0.wireOp",EDGE,"E1032"),sQuery(id+"F0.wireOp",EDGE,"E1033"),sQuery(id+"F0.wireOp",EDGE,"E1034"),sQuery(id+"F0.wireOp",EDGE,"E1035"),sQuery(id+"F0.wireOp",EDGE,"E1036"),sQuery(id+"F0.wireOp",EDGE,"E1037"),sQuery(id+"F0.wireOp",EDGE,"E1038"),sQuery(id+"F0.wireOp",EDGE,"E1039"),sQuery(id+"F0.wireOp",EDGE,"E1040"),sQuery(id+"F0.wireOp",EDGE,"E1041"),sQuery(id+"F0.wireOp",EDGE,"E1042"),sQuery(id+"F0.wireOp",EDGE,"E1043"),sQuery(id+"F0.wireOp",EDGE,"E1044"),sQuery(id+"F0.wireOp",EDGE,"E1045"),sQuery(id+"F0.wireOp",EDGE,"E1046"),sQuery(id+"F0.wireOp",EDGE,"E1047"),sQuery(id+"F0.wireOp",EDGE,"E1048"),sQuery(id+"F0.wireOp",EDGE,"E1049"),sQuery(id+"F0.wireOp",EDGE,"E1050"),sQuery(id+"F0.wireOp",EDGE,"E1051"),sQuery(id+"F0.wireOp",EDGE,"E1052"),sQuery(id+"F0.wireOp",EDGE,"E1053"),sQuery(id+"F0.wireOp",EDGE,"E1054"),sQuery(id+"F0.wireOp",EDGE,"E1055"),sQuery(id+"F0.wireOp",EDGE,"E1056"),sQuery(id+"F0.wireOp",EDGE,"E1057"),sQuery(id+"F0.wireOp",EDGE,"E1058"),sQuery(id+"F0.wireOp",EDGE,"E1059"),sQuery(id+"F0.wireOp",EDGE,"E1060"),sQuery(id+"F0.wireOp",EDGE,"E1061"),sQuery(id+"F0.wireOp",EDGE,"E1062"),sQuery(id+"F0.wireOp",EDGE,"E1063"),sQuery(id+"F0.wireOp",EDGE,"E1064"),sQuery(id+"F0.wireOp",EDGE,"E1065"),sQuery(id+"F0.wireOp",EDGE,"E1066"),sQuery(id+"F0.wireOp",EDGE,"E1067"),sQuery(id+"F0.wireOp",EDGE,"E1068"),sQuery(id+"F0.wireOp",EDGE,"E1069"),sQuery(id+"F0.wireOp",EDGE,"E1070"),sQuery(id+"F0.wireOp",EDGE,"E1071"),sQuery(id+"F0.wireOp",EDGE,"E1072"),sQuery(id+"F0.wireOp",EDGE,"E1073"),sQuery(id+"F0.wireOp",EDGE,"E1074"),sQuery(id+"F0.wireOp",EDGE,"E1075"),sQuery(id+"F0.wireOp",EDGE,"E1076"),sQuery(id+"F0.wireOp",EDGE,"E1077"),sQuery(id+"F0.wireOp",EDGE,"E1078"),sQuery(id+"F0.wireOp",EDGE,"E1079"),sQuery(id+"F0.wireOp",EDGE,"E1080"),sQuery(id+"F0.wireOp",EDGE,"E1081"),sQuery(id+"F0.wireOp",EDGE,"E1082"),sQuery(id+"F0.wireOp",EDGE,"E1083"),sQuery(id+"F0.wireOp",EDGE,"E1084"),sQuery(id+"F0.wireOp",EDGE,"E1085"),sQuery(id+"F0.wireOp",EDGE,"E1086"),sQuery(id+"F0.wireOp",EDGE,"E1087"),sQuery(id+"F0.wireOp",EDGE,"E1088"),sQuery(id+"F0.wireOp",EDGE,"E1089"),sQuery(id+"F0.wireOp",EDGE,"E1090"),sQuery(id+"F0.wireOp",EDGE,"E1091"),sQuery(id+"F0.wireOp",EDGE,"E1092"),sQuery(id+"F0.wireOp",EDGE,"E1093"),sQuery(id+"F0.wireOp",EDGE,"E1094"),sQuery(id+"F0.wireOp",EDGE,"E1095"),sQuery(id+"F0.wireOp",EDGE,"E1096"),sQuery(id+"F0.wireOp",EDGE,"E1097"),sQuery(id+"F0.wireOp",EDGE,"E1098"),sQuery(id+"F0.wireOp",EDGE,"E1099"),sQuery(id+"F0.wireOp",EDGE,"E1100"),sQuery(id+"F0.wireOp",EDGE,"E1101"),sQuery(id+"F0.wireOp",EDGE,"E1102"),sQuery(id+"F0.wireOp",EDGE,"E1103"),sQuery(id+"F0.wireOp",EDGE,"E1104"),sQuery(id+"F0.wireOp",EDGE,"E1105"),sQuery(id+"F0.wireOp",EDGE,"E1106"),sQuery(id+"F0.wireOp",EDGE,"E1107"),sQuery(id+"F0.wireOp",EDGE,"E1108"),sQuery(id+"F0.wireOp",EDGE,"E1109"),sQuery(id+"F0.wireOp",EDGE,"E1110"),sQuery(id+"F0.wireOp",EDGE,"E1111"),sQuery(id+"F0.wireOp",EDGE,"E1112"),sQuery(id+"F0.wireOp",EDGE,"E1113"),sQuery(id+"F0.wireOp",EDGE,"E1114"),sQuery(id+"F0.wireOp",EDGE,"E1115"),sQuery(id+"F0.wireOp",EDGE,"E1116"),sQuery(id+"F0.wireOp",EDGE,"E1117"),sQuery(id+"F0.wireOp",EDGE,"E1118"),sQuery(id+"F0.wireOp",EDGE,"E1119"),sQuery(id+"F0.wireOp",EDGE,"E1120"),sQuery(id+"F0.wireOp",EDGE,"E1121"),sQuery(id+"F0.wireOp",EDGE,"E1122"),sQuery(id+"F0.wireOp",EDGE,"E1123"),sQuery(id+"F0.wireOp",EDGE,"E1124"),sQuery(id+"F0.wireOp",EDGE,"E1125"),sQuery(id+"F0.wireOp",EDGE,"E1126"),sQuery(id+"F0.wireOp",EDGE,"E1127"),sQuery(id+"F0.wireOp",EDGE,"E1128"),sQuery(id+"F0.wireOp",EDGE,"E1129"),sQuery(id+"F0.wireOp",EDGE,"E1130"),sQuery(id+"F0.wireOp",EDGE,"E1131"),sQuery(id+"F0.wireOp",EDGE,"E1132"),sQuery(id+"F0.wireOp",EDGE,"E1133"),sQuery(id+"F0.wireOp",EDGE,"E1134"),sQuery(id+"F0.wireOp",EDGE,"E1135"),sQuery(id+"F0.wireOp",EDGE,"E1136"),sQuery(id+"F0.wireOp",EDGE,"E1137"),sQuery(id+"F0.wireOp",EDGE,"E1138"),sQuery(id+"F0.wireOp",EDGE,"E1139"),sQuery(id+"F0.wireOp",EDGE,"E1140"),sQuery(id+"F0.wireOp",EDGE,"E1141"),sQuery(id+"F0.wireOp",EDGE,"E1142"),sQuery(id+"F0.wireOp",EDGE,"E1143"),sQuery(id+"F0.wireOp",EDGE,"E1144"),sQuery(id+"F0.wireOp",EDGE,"E1145"),sQuery(id+"F0.wireOp",EDGE,"E1146"),sQuery(id+"F0.wireOp",EDGE,"E1147"),sQuery(id+"F0.wireOp",EDGE,"E1148"),sQuery(id+"F0.wireOp",EDGE,"E1149"),sQuery(id+"F0.wireOp",EDGE,"E1150"),sQuery(id+"F0.wireOp",EDGE,"E1151"),sQuery(id+"F0.wireOp",EDGE,"E1152"),sQuery(id+"F0.wireOp",EDGE,"E1153"),sQuery(id+"F0.wireOp",EDGE,"E1154"),sQuery(id+"F0.wireOp",EDGE,"E1155"),sQuery(id+"F0.wireOp",EDGE,"E1156"),sQuery(id+"F0.wireOp",EDGE,"E1157"),sQuery(id+"F0.wireOp",EDGE,"E1158"),sQuery(id+"F0.wireOp",EDGE,"E1159"),sQuery(id+"F0.wireOp",EDGE,"E1160"),sQuery(id+"F0.wireOp",EDGE,"E1161"),sQuery(id+"F0.wireOp",EDGE,"E1162"),sQuery(id+"F0.wireOp",EDGE,"E1163"),sQuery(id+"F0.wireOp",EDGE,"E1164"),sQuery(id+"F0.wireOp",EDGE,"E1165"),sQuery(id+"F0.wireOp",EDGE,"E1166"),sQuery(id+"F0.wireOp",EDGE,"E1167"),sQuery(id+"F0.wireOp",EDGE,"E1168"),sQuery(id+"F0.wireOp",EDGE,"E1169"),sQuery(id+"F0.wireOp",EDGE,"E1170"),sQuery(id+"F0.wireOp",EDGE,"E1171"),sQuery(id+"F0.wireOp",EDGE,"E1172"),sQuery(id+"F0.wireOp",EDGE,"E1173"),sQuery(id+"F0.wireOp",EDGE,"E1174"),sQuery(id+"F0.wireOp",EDGE,"E1175"),sQuery(id+"F0.wireOp",EDGE,"E1176"),sQuery(id+"F0.wireOp",EDGE,"E1177"),sQuery(id+"F0.wireOp",EDGE,"E1178"),sQuery(id+"F0.wireOp",EDGE,"E1179"),sQuery(id+"F0.wireOp",EDGE,"E1180"),sQuery(id+"F0.wireOp",EDGE,"E1181"),sQuery(id+"F0.wireOp",EDGE,"E1182"),sQuery(id+"F0.wireOp",EDGE,"E1183"),sQuery(id+"F0.wireOp",EDGE,"E1184"),sQuery(id+"F0.wireOp",EDGE,"E1185"),sQuery(id+"F0.wireOp",EDGE,"E1186"),sQuery(id+"F0.wireOp",EDGE,"E1187"),sQuery(id+"F0.wireOp",EDGE,"E1188"),sQuery(id+"F0.wireOp",EDGE,"E1189"),sQuery(id+"F0.wireOp",EDGE,"E1190"),sQuery(id+"F0.wireOp",EDGE,"E1191"),sQuery(id+"F0.wireOp",EDGE,"E1192"),sQuery(id+"F0.wireOp",EDGE,"E1193"),sQuery(id+"F0.wireOp",EDGE,"E1194"),sQuery(id+"F0.wireOp",EDGE,"E1195"),sQuery(id+"F0.wireOp",EDGE,"E1196"),sQuery(id+"F0.wireOp",EDGE,"E1197"),sQuery(id+"F0.wireOp",EDGE,"E1198"),sQuery(id+"F0.wireOp",EDGE,"E1199"),sQuery(id+"F0.wireOp",EDGE,"E1200"),sQuery(id+"F0.wireOp",EDGE,"E1201"),sQuery(id+"F0.wireOp",EDGE,"E1202"),sQuery(id+"F0.wireOp",EDGE,"E1203"),sQuery(id+"F0.wireOp",EDGE,"E1204"),sQuery(id+"F0.wireOp",EDGE,"E1205"),sQuery(id+"F0.wireOp",EDGE,"E1206"),sQuery(id+"F0.wireOp",EDGE,"E1207"),sQuery(id+"F0.wireOp",EDGE,"E1208"),sQuery(id+"F0.wireOp",EDGE,"E1209"),sQuery(id+"F0.wireOp",EDGE,"E1210"),sQuery(id+"F0.wireOp",EDGE,"E1211"),sQuery(id+"F0.wireOp",EDGE,"E1212"),sQuery(id+"F0.wireOp",EDGE,"E1213"),sQuery(id+"F0.wireOp",EDGE,"E1214"),sQuery(id+"F0.wireOp",EDGE,"E1215"),sQuery(id+"F0.wireOp",EDGE,"E1216"),sQuery(id+"F0.wireOp",EDGE,"E1217"),sQuery(id+"F0.wireOp",EDGE,"E1218"),sQuery(id+"F0.wireOp",EDGE,"E1219"),sQuery(id+"F0.wireOp",EDGE,"E1220"),sQuery(id+"F0.wireOp",EDGE,"E1221"),sQuery(id+"F0.wireOp",EDGE,"E1222"),sQuery(id+"F0.wireOp",EDGE,"E1223"),sQuery(id+"F0.wireOp",EDGE,"E1224"),sQuery(id+"F0.wireOp",EDGE,"E1225"),sQuery(id+"F0.wireOp",EDGE,"E1226"),sQuery(id+"F0.wireOp",EDGE,"E1227"),sQuery(id+"F0.wireOp",EDGE,"E1228"),sQuery(id+"F0.wireOp",EDGE,"E1229"),sQuery(id+"F0.wireOp",EDGE,"E1230"),sQuery(id+"F0.wireOp",EDGE,"E1231"),sQuery(id+"F0.wireOp",EDGE,"E1232"),sQuery(id+"F0.wireOp",EDGE,"E1233"),sQuery(id+"F0.wireOp",EDGE,"E1234"),sQuery(id+"F0.wireOp",EDGE,"E1235"),sQuery(id+"F0.wireOp",EDGE,"E1236"),sQuery(id+"F0.wireOp",EDGE,"E1237"),sQuery(id+"F0.wireOp",EDGE,"E1238"),sQuery(id+"F0.wireOp",EDGE,"E1239"),sQuery(id+"F0.wireOp",EDGE,"E1240"),sQuery(id+"F0.wireOp",EDGE,"E1241"),sQuery(id+"F0.wireOp",EDGE,"E1242"),sQuery(id+"F0.wireOp",EDGE,"E1243"),sQuery(id+"F0.wireOp",EDGE,"E1244"),sQuery(id+"F0.wireOp",EDGE,"E1245"),sQuery(id+"F0.wireOp",EDGE,"E1246"),sQuery(id+"F0.wireOp",EDGE,"E1247"),sQuery(id+"F0.wireOp",EDGE,"E1248"),sQuery(id+"F0.wireOp",EDGE,"E1249"),sQuery(id+"F0.wireOp",EDGE,"E1250"),sQuery(id+"F0.wireOp",EDGE,"E1251"),sQuery(id+"F0.wireOp",EDGE,"E1252"),sQuery(id+"F0.wireOp",EDGE,"E1253"),sQuery(id+"F0.wireOp",EDGE,"E1254"),sQuery(id+"F0.wireOp",EDGE,"E1255"),sQuery(id+"F0.wireOp",EDGE,"E1256"),sQuery(id+"F0.wireOp",EDGE,"E1257"),sQuery(id+"F0.wireOp",EDGE,"E1258"),sQuery(id+"F0.wireOp",EDGE,"E1259"),sQuery(id+"F0.wireOp",EDGE,"E1260"),sQuery(id+"F0.wireOp",EDGE,"E1261"),sQuery(id+"F0.wireOp",EDGE,"E1262"),sQuery(id+"F0.wireOp",EDGE,"E1263"),sQuery(id+"F0.wireOp",EDGE,"E1264"),sQuery(id+"F0.wireOp",EDGE,"E1265"),sQuery(id+"F0.wireOp",EDGE,"E1266"),sQuery(id+"F0.wireOp",EDGE,"E1267"),sQuery(id+"F0.wireOp",EDGE,"E1268"),sQuery(id+"F0.wireOp",EDGE,"E1269"),sQuery(id+"F0.wireOp",EDGE,"E1270"),sQuery(id+"F0.wireOp",EDGE,"E1271"),sQuery(id+"F0.wireOp",EDGE,"E1272"),sQuery(id+"F0.wireOp",EDGE,"E1273"),sQuery(id+"F0.wireOp",EDGE,"E1274"),sQuery(id+"F0.wireOp",EDGE,"E1275"),sQuery(id+"F0.wireOp",EDGE,"E1276"),sQuery(id+"F0.wireOp",EDGE,"E1277"),sQuery(id+"F0.wireOp",EDGE,"E1278"),sQuery(id+"F0.wireOp",EDGE,"E1279"),sQuery(id+"F0.wireOp",EDGE,"E1280"),sQuery(id+"F0.wireOp",EDGE,"E1281"),sQuery(id+"F0.wireOp",EDGE,"E1282"),sQuery(id+"F0.wireOp",EDGE,"E1283"),sQuery(id+"F0.wireOp",EDGE,"E1284"),sQuery(id+"F0.wireOp",EDGE,"E1285"),sQuery(id+"F0.wireOp",EDGE,"E1286"),sQuery(id+"F0.wireOp",EDGE,"E1287"),sQuery(id+"F0.wireOp",EDGE,"E1288"),sQuery(id+"F0.wireOp",EDGE,"E1289"),sQuery(id+"F0.wireOp",EDGE,"E1290"),sQuery(id+"F0.wireOp",EDGE,"E1291"),sQuery(id+"F0.wireOp",EDGE,"E1292"),sQuery(id+"F0.wireOp",EDGE,"E1293"),sQuery(id+"F0.wireOp",EDGE,"E1294"),sQuery(id+"F0.wireOp",EDGE,"E1295"),sQuery(id+"F0.wireOp",EDGE,"E1296"),sQuery(id+"F0.wireOp",EDGE,"E1297"),sQuery(id+"F0.wireOp",EDGE,"E1298"),sQuery(id+"F0.wireOp",EDGE,"E1299"),sQuery(id+"F0.wireOp",EDGE,"E1300"),sQuery(id+"F0.wireOp",EDGE,"E1301"),sQuery(id+"F0.wireOp",EDGE,"E1302"),sQuery(id+"F0.wireOp",EDGE,"E1303"),sQuery(id+"F0.wireOp",EDGE,"E1304"),sQuery(id+"F0.wireOp",EDGE,"E1305"),sQuery(id+"F0.wireOp",EDGE,"E1306"),sQuery(id+"F0.wireOp",EDGE,"E1307"),sQuery(id+"F0.wireOp",EDGE,"E1308"),sQuery(id+"F0.wireOp",EDGE,"E1309"),sQuery(id+"F0.wireOp",EDGE,"E1310"),sQuery(id+"F0.wireOp",EDGE,"E1311"),sQuery(id+"F0.wireOp",EDGE,"E1312"),sQuery(id+"F0.wireOp",EDGE,"E1313"),sQuery(id+"F0.wireOp",EDGE,"E1314"),sQuery(id+"F0.wireOp",EDGE,"E1315"),sQuery(id+"F0.wireOp",EDGE,"E1316"),sQuery(id+"F0.wireOp",EDGE,"E1317"),sQuery(id+"F0.wireOp",EDGE,"E1318"),sQuery(id+"F0.wireOp",EDGE,"E1319"),sQuery(id+"F0.wireOp",EDGE,"E1320"),sQuery(id+"F0.wireOp",EDGE,"E1321"),sQuery(id+"F0.wireOp",EDGE,"E1322"),sQuery(id+"F0.wireOp",EDGE,"E1323"),sQuery(id+"F0.wireOp",EDGE,"E1324"),sQuery(id+"F0.wireOp",EDGE,"E1325"),sQuery(id+"F0.wireOp",EDGE,"E1326"),sQuery(id+"F0.wireOp",EDGE,"E1327"),sQuery(id+"F0.wireOp",EDGE,"E1328"),sQuery(id+"F0.wireOp",EDGE,"E1329"),sQuery(id+"F0.wireOp",EDGE,"E1330"),sQuery(id+"F0.wireOp",EDGE,"E1331"),sQuery(id+"F0.wireOp",EDGE,"E1332"),sQuery(id+"F0.wireOp",EDGE,"E1333"),sQuery(id+"F0.wireOp",EDGE,"E1334"),sQuery(id+"F0.wireOp",EDGE,"E1335"),sQuery(id+"F0.wireOp",EDGE,"E1336"),sQuery(id+"F0.wireOp",EDGE,"E1337"),sQuery(id+"F0.wireOp",EDGE,"E1338"),sQuery(id+"F0.wireOp",EDGE,"E1339"),sQuery(id+"F0.wireOp",EDGE,"E1340"),sQuery(id+"F0.wireOp",EDGE,"E1341"),sQuery(id+"F0.wireOp",EDGE,"E1342"),sQuery(id+"F0.wireOp",EDGE,"E1343"),sQuery(id+"F0.wireOp",EDGE,"E1344"),sQuery(id+"F0.wireOp",EDGE,"E1345"),sQuery(id+"F0.wireOp",EDGE,"E1346"),sQuery(id+"F0.wireOp",EDGE,"E1347"),sQuery(id+"F0.wireOp",EDGE,"E1348"),sQuery(id+"F0.wireOp",EDGE,"E1349"),sQuery(id+"F0.wireOp",EDGE,"E1350"),sQuery(id+"F0.wireOp",EDGE,"E1351"),sQuery(id+"F0.wireOp",EDGE,"E1352"),sQuery(id+"F0.wireOp",EDGE,"E1353"),sQuery(id+"F0.wireOp",EDGE,"E1354"),sQuery(id+"F0.wireOp",EDGE,"E1355"),sQuery(id+"F0.wireOp",EDGE,"E1356"),sQuery(id+"F0.wireOp",EDGE,"E1357"),sQuery(id+"F0.wireOp",EDGE,"E1358"),sQuery(id+"F0.wireOp",EDGE,"E1359"),sQuery(id+"F0.wireOp",EDGE,"E1360"),sQuery(id+"F0.wireOp",EDGE,"E1361"),sQuery(id+"F0.wireOp",EDGE,"E1362"),sQuery(id+"F0.wireOp",EDGE,"E1363"),sQuery(id+"F0.wireOp",EDGE,"E1364"),sQuery(id+"F0.wireOp",EDGE,"E1365"),sQuery(id+"F0.wireOp",EDGE,"E1366"),sQuery(id+"F0.wireOp",EDGE,"E1367"),sQuery(id+"F0.wireOp",EDGE,"E1368"),sQuery(id+"F0.wireOp",EDGE,"E1369"),sQuery(id+"F0.wireOp",EDGE,"E1370"),sQuery(id+"F0.wireOp",EDGE,"E1371"),sQuery(id+"F0.wireOp",EDGE,"E1372"),sQuery(id+"F0.wireOp",EDGE,"E1373"),sQuery(id+"F0.wireOp",EDGE,"E1374"),sQuery(id+"F0.wireOp",EDGE,"E1375"),sQuery(id+"F0.wireOp",EDGE,"E1376"),sQuery(id+"F0.wireOp",EDGE,"E1377"),sQuery(id+"F0.wireOp",EDGE,"E1378"),sQuery(id+"F0.wireOp",EDGE,"E1379"),sQuery(id+"F0.wireOp",EDGE,"E1380"),sQuery(id+"F0.wireOp",EDGE,"E1381"),sQuery(id+"F0.wireOp",EDGE,"E1382"),sQuery(id+"F0.wireOp",EDGE,"E1383"),sQuery(id+"F0.wireOp",EDGE,"E1384"),sQuery(id+"F0.wireOp",EDGE,"E1385"),sQuery(id+"F0.wireOp",EDGE,"E1386"),sQuery(id+"F0.wireOp",EDGE,"E1387"),sQuery(id+"F0.wireOp",EDGE,"E1388"),sQuery(id+"F0.wireOp",EDGE,"E1389"),sQuery(id+"F0.wireOp",EDGE,"E1390"),sQuery(id+"F0.wireOp",EDGE,"E1391"),sQuery(id+"F0.wireOp",EDGE,"E1392"),sQuery(id+"F0.wireOp",EDGE,"E1393"),sQuery(id+"F0.wireOp",EDGE,"E1394"),sQuery(id+"F0.wireOp",EDGE,"E1395"),sQuery(id+"F0.wireOp",EDGE,"E1396"),sQuery(id+"F0.wireOp",EDGE,"E1397"),sQuery(id+"F0.wireOp",EDGE,"E1398"),sQuery(id+"F0.wireOp",EDGE,"E1399"),sQuery(id+"F0.wireOp",EDGE,"E1400"),sQuery(id+"F0.wireOp",EDGE,"E1401"),sQuery(id+"F0.wireOp",EDGE,"E1402"),sQuery(id+"F0.wireOp",EDGE,"E1403"),sQuery(id+"F0.wireOp",EDGE,"E1404"),sQuery(id+"F0.wireOp",EDGE,"E1405"),sQuery(id+"F0.wireOp",EDGE,"E1406"),sQuery(id+"F0.wireOp",EDGE,"E1407"),sQuery(id+"F0.wireOp",EDGE,"E1408"),sQuery(id+"F0.wireOp",EDGE,"E1409"),sQuery(id+"F0.wireOp",EDGE,"E1410"),sQuery(id+"F0.wireOp",EDGE,"E1411"),sQuery(id+"F0.wireOp",EDGE,"E1412"),sQuery(id+"F0.wireOp",EDGE,"E1413"),sQuery(id+"F0.wireOp",EDGE,"E1414"),sQuery(id+"F0.wireOp",EDGE,"E1415"),sQuery(id+"F0.wireOp",EDGE,"E1416"),sQuery(id+"F0.wireOp",EDGE,"E1417"),sQuery(id+"F0.wireOp",EDGE,"E1418"),sQuery(id+"F0.wireOp",EDGE,"E1419"),sQuery(id+"F0.wireOp",EDGE,"E1420"),sQuery(id+"F0.wireOp",EDGE,"E1421"),sQuery(id+"F0.wireOp",EDGE,"E1422"),sQuery(id+"F0.wireOp",EDGE,"E1423"),sQuery(id+"F0.wireOp",EDGE,"E1424"),sQuery(id+"F0.wireOp",EDGE,"E1425"),sQuery(id+"F0.wireOp",EDGE,"E1426"),sQuery(id+"F0.wireOp",EDGE,"E1427"),sQuery(id+"F0.wireOp",EDGE,"E1428"),sQuery(id+"F0.wireOp",EDGE,"E1429"),sQuery(id+"F0.wireOp",EDGE,"E1430"),sQuery(id+"F0.wireOp",EDGE,"E1431"),sQuery(id+"F0.wireOp",EDGE,"E1432"),sQuery(id+"F0.wireOp",EDGE,"E1433"),sQuery(id+"F0.wireOp",EDGE,"E1434"),sQuery(id+"F0.wireOp",EDGE,"E1435"),sQuery(id+"F0.wireOp",EDGE,"E1436"),sQuery(id+"F0.wireOp",EDGE,"E1437"),sQuery(id+"F0.wireOp",EDGE,"E1438"),sQuery(id+"F0.wireOp",EDGE,"E1439"),sQuery(id+"F0.wireOp",EDGE,"E1440"),sQuery(id+"F0.wireOp",EDGE,"E1441"),sQuery(id+"F0.wireOp",EDGE,"E1442"),sQuery(id+"F0.wireOp",EDGE,"E1443"),sQuery(id+"F0.wireOp",EDGE,"E1444"),sQuery(id+"F0.wireOp",EDGE,"E1445"),sQuery(id+"F0.wireOp",EDGE,"E1446"),sQuery(id+"F0.wireOp",EDGE,"E1447"),sQuery(id+"F0.wireOp",EDGE,"E1448"),sQuery(id+"F0.wireOp",EDGE,"E1449"),sQuery(id+"F0.wireOp",EDGE,"E1450"),sQuery(id+"F0.wireOp",EDGE,"E1451"),sQuery(id+"F0.wireOp",EDGE,"E1452"),sQuery(id+"F0.wireOp",EDGE,"E1453"),sQuery(id+"F0.wireOp",EDGE,"E1454"),sQuery(id+"F0.wireOp",EDGE,"E1455"),sQuery(id+"F0.wireOp",EDGE,"E1456"),sQuery(id+"F0.wireOp",EDGE,"E1457"),sQuery(id+"F0.wireOp",EDGE,"E1458"),sQuery(id+"F0.wireOp",EDGE,"E1459"),sQuery(id+"F0.wireOp",EDGE,"E1460"),sQuery(id+"F0.wireOp",EDGE,"E1461"),sQuery(id+"F0.wireOp",EDGE,"E1462"),sQuery(id+"F0.wireOp",EDGE,"E1463"),sQuery(id+"F0.wireOp",EDGE,"E1464"),sQuery(id+"F0.wireOp",EDGE,"E1465"),sQuery(id+"F0.wireOp",EDGE,"E1466"),sQuery(id+"F0.wireOp",EDGE,"E1467"),sQuery(id+"F0.wireOp",EDGE,"E1468"),sQuery(id+"F0.wireOp",EDGE,"E1469"),sQuery(id+"F0.wireOp",EDGE,"E1470"),sQuery(id+"F0.wireOp",EDGE,"E1471"),sQuery(id+"F0.wireOp",EDGE,"E1472"),sQuery(id+"F0.wireOp",EDGE,"E1473"),sQuery(id+"F0.wireOp",EDGE,"E1474"),sQuery(id+"F0.wireOp",EDGE,"E1475"),sQuery(id+"F0.wireOp",EDGE,"E1476"),sQuery(id+"F0.wireOp",EDGE,"E1477"),sQuery(id+"F0.wireOp",EDGE,"E1478"),sQuery(id+"F0.wireOp",EDGE,"E1479"),sQuery(id+"F0.wireOp",EDGE,"E1480"),sQuery(id+"F0.wireOp",EDGE,"E1481"),sQuery(id+"F0.wireOp",EDGE,"E1482"),sQuery(id+"F0.wireOp",EDGE,"E1483"),sQuery(id+"F0.wireOp",EDGE,"E1484"),sQuery(id+"F0.wireOp",EDGE,"E1485"),sQuery(id+"F0.wireOp",EDGE,"E1486"),sQuery(id+"F0.wireOp",EDGE,"E1487"),sQuery(id+"F0.wireOp",EDGE,"E1488"),sQuery(id+"F0.wireOp",EDGE,"E1489"),sQuery(id+"F0.wireOp",EDGE,"E1490"),sQuery(id+"F0.wireOp",EDGE,"E1491"),sQuery(id+"F0.wireOp",EDGE,"E1492"),sQuery(id+"F0.wireOp",EDGE,"E1493"),sQuery(id+"F0.wireOp",EDGE,"E1494"),sQuery(id+"F0.wireOp",EDGE,"E1495"),sQuery(id+"F0.wireOp",EDGE,"E1496"),sQuery(id+"F0.wireOp",EDGE,"E1497"),sQuery(id+"F0.wireOp",EDGE,"E1498"),sQuery(id+"F0.wireOp",EDGE,"E1499"),sQuery(id+"F0.wireOp",EDGE,"E1500"),sQuery(id+"F0.wireOp",EDGE,"E1501"),sQuery(id+"F0.wireOp",EDGE,"E1502"),sQuery(id+"F0.wireOp",EDGE,"E1503"),sQuery(id+"F0.wireOp",EDGE,"E1504"),sQuery(id+"F0.wireOp",EDGE,"E1505"),sQuery(id+"F0.wireOp",EDGE,"E1506"),sQuery(id+"F0.wireOp",EDGE,"E1507"),sQuery(id+"F0.wireOp",EDGE,"E1508"),sQuery(id+"F0.wireOp",EDGE,"E1509"),sQuery(id+"F0.wireOp",EDGE,"E1510"),sQuery(id+"F0.wireOp",EDGE,"E1511"),sQuery(id+"F0.wireOp",EDGE,"E1512"),sQuery(id+"F0.wireOp",EDGE,"E1513"),sQuery(id+"F0.wireOp",EDGE,"E1514"),sQuery(id+"F0.wireOp",EDGE,"E1515"),sQuery(id+"F0.wireOp",EDGE,"E1516"),sQuery(id+"F0.wireOp",EDGE,"E1517"),sQuery(id+"F0.wireOp",EDGE,"E1518"),sQuery(id+"F0.wireOp",EDGE,"E1519"),sQuery(id+"F0.wireOp",EDGE,"E1520"),sQuery(id+"F0.wireOp",EDGE,"E1521"),sQuery(id+"F0.wireOp",EDGE,"E1522"),sQuery(id+"F0.wireOp",EDGE,"E1523"),sQuery(id+"F0.wireOp",EDGE,"E1524"),sQuery(id+"F0.wireOp",EDGE,"E1525"),sQuery(id+"F0.wireOp",EDGE,"E1526"),sQuery(id+"F0.wireOp",EDGE,"E1527"),sQuery(id+"F0.wireOp",EDGE,"E1528"),sQuery(id+"F0.wireOp",EDGE,"E1529"),sQuery(id+"F0.wireOp",EDGE,"E1530"),sQuery(id+"F0.wireOp",EDGE,"E1531"),sQuery(id+"F0.wireOp",EDGE,"E1532"),sQuery(id+"F0.wireOp",EDGE,"E1533"),sQuery(id+"F0.wireOp",EDGE,"E1534"),sQuery(id+"F0.wireOp",EDGE,"E1535"),sQuery(id+"F0.wireOp",EDGE,"E1536"),sQuery(id+"F0.wireOp",EDGE,"E1537"),sQuery(id+"F0.wireOp",EDGE,"E1538"),sQuery(id+"F0.wireOp",EDGE,"E1539"),sQuery(id+"F0.wireOp",EDGE,"E1540"),sQuery(id+"F0.wireOp",EDGE,"E1541"),sQuery(id+"F0.wireOp",EDGE,"E1542"),sQuery(id+"F0.wireOp",EDGE,"E1543"),sQuery(id+"F0.wireOp",EDGE,"E1544"),sQuery(id+"F0.wireOp",EDGE,"E1545"),sQuery(id+"F0.wireOp",EDGE,"E1546"),sQuery(id+"F0.wireOp",EDGE,"E1547"),sQuery(id+"F0.wireOp",EDGE,"E1548"),sQuery(id+"F0.wireOp",EDGE,"E1549"),sQuery(id+"F0.wireOp",EDGE,"E1550"),sQuery(id+"F0.wireOp",EDGE,"E1551"),sQuery(id+"F0.wireOp",EDGE,"E1552"),sQuery(id+"F0.wireOp",EDGE,"E1553"),sQuery(id+"F0.wireOp",EDGE,"E1554"),sQuery(id+"F0.wireOp",EDGE,"E1555"),sQuery(id+"F0.wireOp",EDGE,"E1556"),sQuery(id+"F0.wireOp",EDGE,"E1557"),sQuery(id+"F0.wireOp",EDGE,"E1558"),sQuery(id+"F0.wireOp",EDGE,"E1559"),sQuery(id+"F0.wireOp",EDGE,"E1560"),sQuery(id+"F0.wireOp",EDGE,"E1561"),sQuery(id+"F0.wireOp",EDGE,"E1562"),sQuery(id+"F0.wireOp",EDGE,"E1563"),sQuery(id+"F0.wireOp",EDGE,"E1564"),sQuery(id+"F0.wireOp",EDGE,"E1565"),sQuery(id+"F0.wireOp",EDGE,"E1566"),sQuery(id+"F0.wireOp",EDGE,"E1567"),sQuery(id+"F0.wireOp",EDGE,"E1568"),sQuery(id+"F0.wireOp",EDGE,"E1569"),sQuery(id+"F0.wireOp",EDGE,"E1570"),sQuery(id+"F0.wireOp",EDGE,"E1571"),sQuery(id+"F0.wireOp",EDGE,"E1572"),sQuery(id+"F0.wireOp",EDGE,"E1573"),sQuery(id+"F0.wireOp",EDGE,"E1574"),sQuery(id+"F0.wireOp",EDGE,"E1575"),sQuery(id+"F0.wireOp",EDGE,"E1576"),sQuery(id+"F0.wireOp",EDGE,"E1577"),sQuery(id+"F0.wireOp",EDGE,"E1578"),sQuery(id+"F0.wireOp",EDGE,"E1579"),sQuery(id+"F0.wireOp",EDGE,"E1580"),sQuery(id+"F0.wireOp",EDGE,"E1581"),sQuery(id+"F0.wireOp",EDGE,"E1582"),sQuery(id+"F0.wireOp",EDGE,"E1583"),sQuery(id+"F0.wireOp",EDGE,"E1584"),sQuery(id+"F0.wireOp",EDGE,"E1585"),sQuery(id+"F0.wireOp",EDGE,"E1586"),sQuery(id+"F0.wireOp",EDGE,"E1587"),sQuery(id+"F0.wireOp",EDGE,"E1588"),sQuery(id+"F0.wireOp",EDGE,"E1589"),sQuery(id+"F0.wireOp",EDGE,"E1590"),sQuery(id+"F0.wireOp",EDGE,"E1591"),sQuery(id+"F0.wireOp",EDGE,"E1592"),sQuery(id+"F0.wireOp",EDGE,"E1593"),sQuery(id+"F0.wireOp",EDGE,"E1594"),sQuery(id+"F0.wireOp",EDGE,"E1595"),sQuery(id+"F0.wireOp",EDGE,"E1596"),sQuery(id+"F0.wireOp",EDGE,"E1597"),sQuery(id+"F0.wireOp",EDGE,"E1598"),sQuery(id+"F0.wireOp",EDGE,"E1599"),sQuery(id+"F0.wireOp",EDGE,"E1600"),sQuery(id+"F0.wireOp",EDGE,"E1601"),sQuery(id+"F0.wireOp",EDGE,"E1602"),sQuery(id+"F0.wireOp",EDGE,"E1603"),sQuery(id+"F0.wireOp",EDGE,"E1604"),sQuery(id+"F0.wireOp",EDGE,"E1605"),sQuery(id+"F0.wireOp",EDGE,"E1606"),sQuery(id+"F0.wireOp",EDGE,"E1607"),sQuery(id+"F0.wireOp",EDGE,"E1608"),sQuery(id+"F0.wireOp",EDGE,"E1609"),sQuery(id+"F0.wireOp",EDGE,"E1610"),sQuery(id+"F0.wireOp",EDGE,"E1611"),sQuery(id+"F0.wireOp",EDGE,"E1612"),sQuery(id+"F0.wireOp",EDGE,"E1613"),sQuery(id+"F0.wireOp",EDGE,"E1614"),sQuery(id+"F0.wireOp",EDGE,"E1615"),sQuery(id+"F0.wireOp",EDGE,"E1616"),sQuery(id+"F0.wireOp",EDGE,"E1617"),sQuery(id+"F0.wireOp",EDGE,"E1618"),sQuery(id+"F0.wireOp",EDGE,"E1619"),sQuery(id+"F0.wireOp",EDGE,"E1620"),sQuery(id+"F0.wireOp",EDGE,"E1621"),sQuery(id+"F0.wireOp",EDGE,"E1622"),sQuery(id+"F0.wireOp",EDGE,"E1623"),sQuery(id+"F0.wireOp",EDGE,"E1624"),sQuery(id+"F0.wireOp",EDGE,"E1625"),sQuery(id+"F0.wireOp",EDGE,"E1626"),sQuery(id+"F0.wireOp",EDGE,"E1627"),sQuery(id+"F0.wireOp",EDGE,"E1628"),sQuery(id+"F0.wireOp",EDGE,"E1629"),sQuery(id+"F0.wireOp",EDGE,"E1630"),sQuery(id+"F0.wireOp",EDGE,"E1631"),sQuery(id+"F0.wireOp",EDGE,"E1632"),sQuery(id+"F0.wireOp",EDGE,"E1633"),sQuery(id+"F0.wireOp",EDGE,"E1634"),sQuery(id+"F0.wireOp",EDGE,"E1635"),sQuery(id+"F0.wireOp",EDGE,"E1636"),sQuery(id+"F0.wireOp",EDGE,"E1637"),sQuery(id+"F0.wireOp",EDGE,"E1638"),sQuery(id+"F0.wireOp",EDGE,"E1639"),sQuery(id+"F0.wireOp",EDGE,"E1640"),sQuery(id+"F0.wireOp",EDGE,"E1641"),sQuery(id+"F0.wireOp",EDGE,"E1642"),sQuery(id+"F0.wireOp",EDGE,"E1643"),sQuery(id+"F0.wireOp",EDGE,"E1644"),sQuery(id+"F0.wireOp",EDGE,"E1645"),sQuery(id+"F0.wireOp",EDGE,"E1646"),sQuery(id+"F0.wireOp",EDGE,"E1647"),sQuery(id+"F0.wireOp",EDGE,"E1648"),sQuery(id+"F0.wireOp",EDGE,"E1649"),sQuery(id+"F0.wireOp",EDGE,"E1650"),sQuery(id+"F0.wireOp",EDGE,"E1651"),sQuery(id+"F0.wireOp",EDGE,"E1652"),sQuery(id+"F0.wireOp",EDGE,"E1653"),sQuery(id+"F0.wireOp",EDGE,"E1654"),sQuery(id+"F0.wireOp",EDGE,"E1655"),sQuery(id+"F0.wireOp",EDGE,"E1656"),sQuery(id+"F0.wireOp",EDGE,"E1657"),sQuery(id+"F0.wireOp",EDGE,"E1658"),sQuery(id+"F0.wireOp",EDGE,"E1659"),sQuery(id+"F0.wireOp",EDGE,"E1660"),sQuery(id+"F0.wireOp",EDGE,"E1661"),sQuery(id+"F0.wireOp",EDGE,"E1662"),sQuery(id+"F0.wireOp",EDGE,"E1663"),sQuery(id+"F0.wireOp",EDGE,"E1664"),sQuery(id+"F0.wireOp",EDGE,"E1665"),sQuery(id+"F0.wireOp",EDGE,"E1666"),sQuery(id+"F0.wireOp",EDGE,"E1667"),sQuery(id+"F0.wireOp",EDGE,"E1668"),sQuery(id+"F0.wireOp",EDGE,"E1669"),sQuery(id+"F0.wireOp",EDGE,"E1670"),sQuery(id+"F0.wireOp",EDGE,"E1671"),sQuery(id+"F0.wireOp",EDGE,"E1672"),sQuery(id+"F0.wireOp",EDGE,"E1673"),sQuery(id+"F0.wireOp",EDGE,"E1674"),sQuery(id+"F0.wireOp",EDGE,"E1675"),sQuery(id+"F0.wireOp",EDGE,"E1676"),sQuery(id+"F0.wireOp",EDGE,"E1677"),sQuery(id+"F0.wireOp",EDGE,"E1678"),sQuery(id+"F0.wireOp",EDGE,"E1679"),sQuery(id+"F0.wireOp",EDGE,"E1680"),sQuery(id+"F0.wireOp",EDGE,"E1681"),sQuery(id+"F0.wireOp",EDGE,"E1682"),sQuery(id+"F0.wireOp",EDGE,"E1683"),sQuery(id+"F0.wireOp",EDGE,"E1684"),sQuery(id+"F0.wireOp",EDGE,"E1685"),sQuery(id+"F0.wireOp",EDGE,"E1686"),sQuery(id+"F0.wireOp",EDGE,"E1687"),sQuery(id+"F0.wireOp",EDGE,"E1688"),sQuery(id+"F0.wireOp",EDGE,"E1689"),sQuery(id+"F0.wireOp",EDGE,"E1690"),sQuery(id+"F0.wireOp",EDGE,"E1691"),sQuery(id+"F0.wireOp",EDGE,"E1692"),sQuery(id+"F0.wireOp",EDGE,"E1693"),sQuery(id+"F0.wireOp",EDGE,"E1694"),sQuery(id+"F0.wireOp",EDGE,"E1695"),sQuery(id+"F0.wireOp",EDGE,"E1696"),sQuery(id+"F0.wireOp",EDGE,"E1697"),sQuery(id+"F0.wireOp",EDGE,"E1698"),sQuery(id+"F0.wireOp",EDGE,"E1699"),sQuery(id+"F0.wireOp",EDGE,"E1700"),sQuery(id+"F0.wireOp",EDGE,"E1701"),sQuery(id+"F0.wireOp",EDGE,"E1702"),sQuery(id+"F0.wireOp",EDGE,"E1703"),sQuery(id+"F0.wireOp",EDGE,"E1704"),sQuery(id+"F0.wireOp",EDGE,"E1705"),sQuery(id+"F0.wireOp",EDGE,"E1706"),sQuery(id+"F0.wireOp",EDGE,"E1707"),sQuery(id+"F0.wireOp",EDGE,"E1708"),sQuery(id+"F0.wireOp",EDGE,"E1709"),sQuery(id+"F0.wireOp",EDGE,"E1710"),sQuery(id+"F0.wireOp",EDGE,"E1711"),sQuery(id+"F0.wireOp",EDGE,"E1712"),sQuery(id+"F0.wireOp",EDGE,"E1713"),sQuery(id+"F0.wireOp",EDGE,"E1714"),sQuery(id+"F0.wireOp",EDGE,"E1715"),sQuery(id+"F0.wireOp",EDGE,"E1716"),sQuery(id+"F0.wireOp",EDGE,"E1717"),sQuery(id+"F0.wireOp",EDGE,"E1718"),sQuery(id+"F0.wireOp",EDGE,"E1719"),sQuery(id+"F0.wireOp",EDGE,"E1720"),sQuery(id+"F0.wireOp",EDGE,"E1721"),sQuery(id+"F0.wireOp",EDGE,"E1722"),sQuery(id+"F0.wireOp",EDGE,"E1723"),sQuery(id+"F0.wireOp",EDGE,"E1724"),sQuery(id+"F0.wireOp",EDGE,"E1725"),sQuery(id+"F0.wireOp",EDGE,"E1726"),sQuery(id+"F0.wireOp",EDGE,"E1727"),sQuery(id+"F0.wireOp",EDGE,"E1728"),sQuery(id+"F0.wireOp",EDGE,"E1729"),sQuery(id+"F0.wireOp",EDGE,"E1730"),sQuery(id+"F0.wireOp",EDGE,"E1731"),sQuery(id+"F0.wireOp",EDGE,"E1732"),sQuery(id+"F0.wireOp",EDGE,"E1733"),sQuery(id+"F0.wireOp",EDGE,"E1734"),sQuery(id+"F0.wireOp",EDGE,"E1735"),sQuery(id+"F0.wireOp",EDGE,"E1736"),sQuery(id+"F0.wireOp",EDGE,"E1737"),sQuery(id+"F0.wireOp",EDGE,"E1738"),sQuery(id+"F0.wireOp",EDGE,"E1739"),sQuery(id+"F0.wireOp",EDGE,"E1740"),sQuery(id+"F0.wireOp",EDGE,"E1741"),sQuery(id+"F0.wireOp",EDGE,"E1742"),sQuery(id+"F0.wireOp",EDGE,"E1743"),sQuery(id+"F0.wireOp",EDGE,"E1744"),sQuery(id+"F0.wireOp",EDGE,"E1745"),sQuery(id+"F0.wireOp",EDGE,"E1746"),sQuery(id+"F0.wireOp",EDGE,"E1747"),sQuery(id+"F0.wireOp",EDGE,"E1748"),sQuery(id+"F0.wireOp",EDGE,"E1749"),sQuery(id+"F0.wireOp",EDGE,"E1750"),sQuery(id+"F0.wireOp",EDGE,"E1751"),sQuery(id+"F0.wireOp",EDGE,"E1752"),sQuery(id+"F0.wireOp",EDGE,"E1753"),sQuery(id+"F0.wireOp",EDGE,"E1754"),sQuery(id+"F0.wireOp",EDGE,"E1755"),sQuery(id+"F0.wireOp",EDGE,"E1756"),sQuery(id+"F0.wireOp",EDGE,"E1757"),sQuery(id+"F0.wireOp",EDGE,"E1758"),sQuery(id+"F0.wireOp",EDGE,"E1759"),sQuery(id+"F0.wireOp",EDGE,"E1760"),sQuery(id+"F0.wireOp",EDGE,"E1761"),sQuery(id+"F0.wireOp",EDGE,"E1762"),sQuery(id+"F0.wireOp",EDGE,"E1763"),sQuery(id+"F0.wireOp",EDGE,"E1764"),sQuery(id+"F0.wireOp",EDGE,"E1765"),sQuery(id+"F0.wireOp",EDGE,"E1766"),sQuery(id+"F0.wireOp",EDGE,"E1767"),sQuery(id+"F0.wireOp",EDGE,"E1768"),sQuery(id+"F0.wireOp",EDGE,"E1769"),sQuery(id+"F0.wireOp",EDGE,"E1770"),sQuery(id+"F0.wireOp",EDGE,"E1771"),sQuery(id+"F0.wireOp",EDGE,"E1772"),sQuery(id+"F0.wireOp",EDGE,"E1773"),sQuery(id+"F0.wireOp",EDGE,"E1774"),sQuery(id+"F0.wireOp",EDGE,"E1775"),sQuery(id+"F0.wireOp",EDGE,"E1776"),sQuery(id+"F0.wireOp",EDGE,"E1777"),sQuery(id+"F0.wireOp",EDGE,"E1778"),sQuery(id+"F0.wireOp",EDGE,"E1779"),sQuery(id+"F0.wireOp",EDGE,"E1780"),sQuery(id+"F0.wireOp",EDGE,"E1781"),sQuery(id+"F0.wireOp",EDGE,"E1782"),sQuery(id+"F0.wireOp",EDGE,"E1783"),sQuery(id+"F0.wireOp",EDGE,"E1784"),sQuery(id+"F0.wireOp",EDGE,"E1785"),sQuery(id+"F0.wireOp",EDGE,"E1786"),sQuery(id+"F0.wireOp",EDGE,"E1787"),sQuery(id+"F0.wireOp",EDGE,"E1788"),sQuery(id+"F0.wireOp",EDGE,"E1789"),sQuery(id+"F0.wireOp",EDGE,"E1790"),sQuery(id+"F0.wireOp",EDGE,"E1791"),sQuery(id+"F0.wireOp",EDGE,"E1792"),sQuery(id+"F0.wireOp",EDGE,"E1793"),sQuery(id+"F0.wireOp",EDGE,"E1794"),sQuery(id+"F0.wireOp",EDGE,"E1795"),sQuery(id+"F0.wireOp",EDGE,"E1796"),sQuery(id+"F0.wireOp",EDGE,"E1797"),sQuery(id+"F0.wireOp",EDGE,"E1798"),sQuery(id+"F0.wireOp",EDGE,"E1799"),sQuery(id+"F0.wireOp",EDGE,"E1800"),sQuery(id+"F0.wireOp",EDGE,"E1801"),sQuery(id+"F0.wireOp",EDGE,"E1802"),sQuery(id+"F0.wireOp",EDGE,"E1803"),sQuery(id+"F0.wireOp",EDGE,"E1804"),sQuery(id+"F0.wireOp",EDGE,"E1805"),sQuery(id+"F0.wireOp",EDGE,"E1806"),sQuery(id+"F0.wireOp",EDGE,"E1807"),sQuery(id+"F0.wireOp",EDGE,"E1808"),sQuery(id+"F0.wireOp",EDGE,"E1809"),sQuery(id+"F0.wireOp",EDGE,"E1810"),sQuery(id+"F0.wireOp",EDGE,"E1811"),sQuery(id+"F0.wireOp",EDGE,"E1812"),sQuery(id+"F0.wireOp",EDGE,"E1813"),sQuery(id+"F0.wireOp",EDGE,"E1814"),sQuery(id+"F0.wireOp",EDGE,"E1815"),sQuery(id+"F0.wireOp",EDGE,"E1816"),sQuery(id+"F0.wireOp",EDGE,"E1817"),sQuery(id+"F0.wireOp",EDGE,"E1818"),sQuery(id+"F0.wireOp",EDGE,"E1819"),sQuery(id+"F0.wireOp",EDGE,"E1820"),sQuery(id+"F0.wireOp",EDGE,"E1821"),sQuery(id+"F0.wireOp",EDGE,"E1822"),sQuery(id+"F0.wireOp",EDGE,"E1823"),sQuery(id+"F0.wireOp",EDGE,"E1824"),sQuery(id+"F0.wireOp",EDGE,"E1825"),sQuery(id+"F0.wireOp",EDGE,"E1826"),sQuery(id+"F0.wireOp",EDGE,"E1827"),sQuery(id+"F0.wireOp",EDGE,"E1828"),sQuery(id+"F0.wireOp",EDGE,"E1829"),sQuery(id+"F0.wireOp",EDGE,"E1830"),sQuery(id+"F0.wireOp",EDGE,"E1831"),sQuery(id+"F0.wireOp",EDGE,"E1832"),sQuery(id+"F0.wireOp",EDGE,"E1833"),sQuery(id+"F0.wireOp",EDGE,"E1834"),sQuery(id+"F0.wireOp",EDGE,"E1835"),sQuery(id+"F0.wireOp",EDGE,"E1836"),sQuery(id+"F0.wireOp",EDGE,"E1837"),sQuery(id+"F0.wireOp",EDGE,"E1838"),sQuery(id+"F0.wireOp",EDGE,"E1839"),sQuery(id+"F0.wireOp",EDGE,"E1840"),sQuery(id+"F0.wireOp",EDGE,"E1841"),sQuery(id+"F0.wireOp",EDGE,"E1842"),sQuery(id+"F0.wireOp",EDGE,"E1843"),sQuery(id+"F0.wireOp",EDGE,"E1844"),sQuery(id+"F0.wireOp",EDGE,"E1845"),sQuery(id+"F0.wireOp",EDGE,"E1846"),sQuery(id+"F0.wireOp",EDGE,"E1847"),sQuery(id+"F0.wireOp",EDGE,"E1848"),sQuery(id+"F0.wireOp",EDGE,"E1849"),sQuery(id+"F0.wireOp",EDGE,"E1850"),sQuery(id+"F0.wireOp",EDGE,"E1851"),sQuery(id+"F0.wireOp",EDGE,"E1852"),sQuery(id+"F0.wireOp",EDGE,"E1853"),sQuery(id+"F0.wireOp",EDGE,"E1854"),sQuery(id+"F0.wireOp",EDGE,"E1855"),sQuery(id+"F0.wireOp",EDGE,"E1856"),sQuery(id+"F0.wireOp",EDGE,"E1857"),sQuery(id+"F0.wireOp",EDGE,"E1858"),sQuery(id+"F0.wireOp",EDGE,"E1859"),sQuery(id+"F0.wireOp",EDGE,"E1860"),sQuery(id+"F0.wireOp",EDGE,"E1861"),sQuery(id+"F0.wireOp",EDGE,"E1862"),sQuery(id+"F0.wireOp",EDGE,"E1863"),sQuery(id+"F0.wireOp",EDGE,"E1864"),sQuery(id+"F0.wireOp",EDGE,"E1865"),sQuery(id+"F0.wireOp",EDGE,"E1866"),sQuery(id+"F0.wireOp",EDGE,"E1867"),sQuery(id+"F0.wireOp",EDGE,"E1868"),sQuery(id+"F0.wireOp",EDGE,"E1869"),sQuery(id+"F0.wireOp",EDGE,"E1870"),sQuery(id+"F0.wireOp",EDGE,"E1871"),sQuery(id+"F0.wireOp",EDGE,"E1872"),sQuery(id+"F0.wireOp",EDGE,"E1873"),sQuery(id+"F0.wireOp",EDGE,"E1874"),sQuery(id+"F0.wireOp",EDGE,"E1875"),sQuery(id+"F0.wireOp",EDGE,"E1876"),sQuery(id+"F0.wireOp",EDGE,"E1877"),sQuery(id+"F0.wireOp",EDGE,"E1878"),sQuery(id+"F0.wireOp",EDGE,"E1879"),sQuery(id+"F0.wireOp",EDGE,"E1880"),sQuery(id+"F0.wireOp",EDGE,"E1881"),sQuery(id+"F0.wireOp",EDGE,"E1882"),sQuery(id+"F0.wireOp",EDGE,"E1883"),sQuery(id+"F0.wireOp",EDGE,"E1884"),sQuery(id+"F0.wireOp",EDGE,"E1885"),sQuery(id+"F0.wireOp",EDGE,"E1886"),sQuery(id+"F0.wireOp",EDGE,"E1887"),sQuery(id+"F0.wireOp",EDGE,"E1888"),sQuery(id+"F0.wireOp",EDGE,"E1889"),sQuery(id+"F0.wireOp",EDGE,"E1890"),sQuery(id+"F0.wireOp",EDGE,"E1891"),sQuery(id+"F0.wireOp",EDGE,"E1892"),sQuery(id+"F0.wireOp",EDGE,"E1893"),sQuery(id+"F0.wireOp",EDGE,"E1894"),sQuery(id+"F0.wireOp",EDGE,"E1895"),sQuery(id+"F0.wireOp",EDGE,"E1896"),sQuery(id+"F0.wireOp",EDGE,"E1897"),sQuery(id+"F0.wireOp",EDGE,"E1898"),sQuery(id+"F0.wireOp",EDGE,"E1899"),sQuery(id+"F0.wireOp",EDGE,"E1900"),sQuery(id+"F0.wireOp",EDGE,"E1901"),sQuery(id+"F0.wireOp",EDGE,"E1902"),sQuery(id+"F0.wireOp",EDGE,"E1903"),sQuery(id+"F0.wireOp",EDGE,"E1904"),sQuery(id+"F0.wireOp",EDGE,"E1905"),sQuery(id+"F0.wireOp",EDGE,"E1906"),sQuery(id+"F0.wireOp",EDGE,"E1907"),sQuery(id+"F0.wireOp",EDGE,"E1908"),sQuery(id+"F0.wireOp",EDGE,"E1909"),sQuery(id+"F0.wireOp",EDGE,"E1910"),sQuery(id+"F0.wireOp",EDGE,"E1911"),sQuery(id+"F0.wireOp",EDGE,"E1912"),sQuery(id+"F0.wireOp",EDGE,"E1913"),sQuery(id+"F0.wireOp",EDGE,"E1914"),sQuery(id+"F0.wireOp",EDGE,"E1915"),sQuery(id+"F0.wireOp",EDGE,"E1916"),sQuery(id+"F0.wireOp",EDGE,"E1917"),sQuery(id+"F0.wireOp",EDGE,"E1918"),sQuery(id+"F0.wireOp",EDGE,"E1919"),sQuery(id+"F0.wireOp",EDGE,"E1920"),sQuery(id+"F0.wireOp",EDGE,"E1921"),sQuery(id+"F0.wireOp",EDGE,"E1922"),sQuery(id+"F0.wireOp",EDGE,"E1923"),sQuery(id+"F0.wireOp",EDGE,"E1924"),sQuery(id+"F0.wireOp",EDGE,"E1925"),sQuery(id+"F0.wireOp",EDGE,"E1926"),sQuery(id+"F0.wireOp",EDGE,"E1927"),sQuery(id+"F0.wireOp",EDGE,"E1928"),sQuery(id+"F0.wireOp",EDGE,"E1929"),sQuery(id+"F0.wireOp",EDGE,"E1930"),sQuery(id+"F0.wireOp",EDGE,"E1931"),sQuery(id+"F0.wireOp",EDGE,"E1932"),sQuery(id+"F0.wireOp",EDGE,"E1933"),sQuery(id+"F0.wireOp",EDGE,"E1934"),sQuery(id+"F0.wireOp",EDGE,"E1935"),sQuery(id+"F0.wireOp",EDGE,"E1936"),sQuery(id+"F0.wireOp",EDGE,"E1937"),sQuery(id+"F0.wireOp",EDGE,"E1938"),sQuery(id+"F0.wireOp",EDGE,"E1939"),sQuery(id+"F0.wireOp",EDGE,"E1940"),sQuery(id+"F0.wireOp",EDGE,"E1941"),sQuery(id+"F0.wireOp",EDGE,"E1942"),sQuery(id+"F0.wireOp",EDGE,"E1943"),sQuery(id+"F0.wireOp",EDGE,"E1944"),sQuery(id+"F0.wireOp",EDGE,"E1945"),sQuery(id+"F0.wireOp",EDGE,"E1946"),sQuery(id+"F0.wireOp",EDGE,"E1947"),sQuery(id+"F0.wireOp",EDGE,"E1948"),sQuery(id+"F0.wireOp",EDGE,"E1949"),sQuery(id+"F0.wireOp",EDGE,"E1950"),sQuery(id+"F0.wireOp",EDGE,"E1951"),sQuery(id+"F0.wireOp",EDGE,"E1952"),sQuery(id+"F0.wireOp",EDGE,"E1953"),sQuery(id+"F0.wireOp",EDGE,"E1954"),sQuery(id+"F0.wireOp",EDGE,"E1955"),sQuery(id+"F0.wireOp",EDGE,"E1956"),sQuery(id+"F0.wireOp",EDGE,"E1957"),sQuery(id+"F0.wireOp",EDGE,"E1958"),sQuery(id+"F0.wireOp",EDGE,"E1959"),sQuery(id+"F0.wireOp",EDGE,"E1960"),sQuery(id+"F0.wireOp",EDGE,"E1961"),sQuery(id+"F0.wireOp",EDGE,"E1962"),sQuery(id+"F0.wireOp",EDGE,"E1963"),sQuery(id+"F0.wireOp",EDGE,"E1964"),sQuery(id+"F0.wireOp",EDGE,"E1965"),sQuery(id+"F0.wireOp",EDGE,"E1966"),sQuery(id+"F0.wireOp",EDGE,"E1967"),sQuery(id+"F0.wireOp",EDGE,"E1968"),sQuery(id+"F0.wireOp",EDGE,"E1969"),sQuery(id+"F0.wireOp",EDGE,"E1970"),sQuery(id+"F0.wireOp",EDGE,"E1971"),sQuery(id+"F0.wireOp",EDGE,"E1972"),sQuery(id+"F0.wireOp",EDGE,"E1973"),sQuery(id+"F0.wireOp",EDGE,"E1974"),sQuery(id+"F0.wireOp",EDGE,"E1975"),sQuery(id+"F0.wireOp",EDGE,"E1976"),sQuery(id+"F0.wireOp",EDGE,"E1977"),sQuery(id+"F0.wireOp",EDGE,"E1978"),sQuery(id+"F0.wireOp",EDGE,"E1979"),sQuery(id+"F0.wireOp",EDGE,"E1980"),sQuery(id+"F0.wireOp",EDGE,"E1981"),sQuery(id+"F0.wireOp",EDGE,"E1982"),sQuery(id+"F0.wireOp",EDGE,"E1983"),sQuery(id+"F0.wireOp",EDGE,"E1984"),sQuery(id+"F0.wireOp",EDGE,"E1985"),sQuery(id+"F0.wireOp",EDGE,"E1986"),sQuery(id+"F0.wireOp",EDGE,"E1987"),sQuery(id+"F0.wireOp",EDGE,"E1988"),sQuery(id+"F0.wireOp",EDGE,"E1989"),sQuery(id+"F0.wireOp",EDGE,"E1990"),sQuery(id+"F0.wireOp",EDGE,"E1991"),sQuery(id+"F0.wireOp",EDGE,"E1992"),sQuery(id+"F0.wireOp",EDGE,"E1993"),sQuery(id+"F0.wireOp",EDGE,"E1994"),sQuery(id+"F0.wireOp",EDGE,"E1995"),sQuery(id+"F0.wireOp",EDGE,"E1996"),sQuery(id+"F0.wireOp",EDGE,"E1997"),sQuery(id+"F0.wireOp",EDGE,"E1998"),sQuery(id+"F0.wireOp",EDGE,"E1999"),sQuery(id+"F0.wireOp",EDGE,"E2000"),sQuery(id+"F0.wireOp",EDGE,"E2001"),sQuery(id+"F0.wireOp",EDGE,"E2002"),sQuery(id+"F0.wireOp",EDGE,"E2003"),sQuery(id+"F0.wireOp",EDGE,"E2004"),sQuery(id+"F0.wireOp",EDGE,"E2005"),sQuery(id+"F0.wireOp",EDGE,"E2006"),sQuery(id+"F0.wireOp",EDGE,"E2007"),sQuery(id+"F0.wireOp",EDGE,"E2008"),sQuery(id+"F0.wireOp",EDGE,"E2009"),sQuery(id+"F0.wireOp",EDGE,"E2010"),sQuery(id+"F0.wireOp",EDGE,"E2011"),sQuery(id+"F0.wireOp",EDGE,"E2012"),sQuery(id+"F0.wireOp",EDGE,"E2013"),sQuery(id+"F0.wireOp",EDGE,"E2014"),sQuery(id+"F0.wireOp",EDGE,"E2015"),sQuery(id+"F0.wireOp",EDGE,"E2016"),sQuery(id+"F0.wireOp",EDGE,"E2017"),sQuery(id+"F0.wireOp",EDGE,"E2018"),sQuery(id+"F0.wireOp",EDGE,"E2019"),sQuery(id+"F0.wireOp",EDGE,"E2020"),sQuery(id+"F0.wireOp",EDGE,"E2021"),sQuery(id+"F0.wireOp",EDGE,"E2022"),sQuery(id+"F0.wireOp",EDGE,"E2023"),sQuery(id+"F0.wireOp",EDGE,"E2024"),sQuery(id+"F0.wireOp",EDGE,"E2025"),sQuery(id+"F0.wireOp",EDGE,"E2026"),sQuery(id+"F0.wireOp",EDGE,"E2027"),sQuery(id+"F0.wireOp",EDGE,"E2028"),sQuery(id+"F0.wireOp",EDGE,"E2029"),sQuery(id+"F0.wireOp",EDGE,"E2030"),sQuery(id+"F0.wireOp",EDGE,"E2031"),sQuery(id+"F0.wireOp",EDGE,"E2032"),sQuery(id+"F0.wireOp",EDGE,"E2033"),sQuery(id+"F0.wireOp",EDGE,"E2034"),sQuery(id+"F0.wireOp",EDGE,"E2035"),sQuery(id+"F0.wireOp",EDGE,"E2036"),sQuery(id+"F0.wireOp",EDGE,"E2037"),sQuery(id+"F0.wireOp",EDGE,"E2038"),sQuery(id+"F0.wireOp",EDGE,"E2039"),sQuery(id+"F0.wireOp",EDGE,"E2040"),sQuery(id+"F0.wireOp",EDGE,"E2041"),sQuery(id+"F0.wireOp",EDGE,"E2042"),sQuery(id+"F0.wireOp",EDGE,"E2043"),sQuery(id+"F0.wireOp",EDGE,"E2044"),sQuery(id+"F0.wireOp",EDGE,"E2045"),sQuery(id+"F0.wireOp",EDGE,"E2046"),sQuery(id+"F0.wireOp",EDGE,"E2047"),sQuery(id+"F0.wireOp",EDGE,"E2048"),sQuery(id+"F0.wireOp",EDGE,"E2049"),sQuery(id+"F0.wireOp",EDGE,"E2050"),sQuery(id+"F0.wireOp",EDGE,"E2051"),sQuery(id+"F0.wireOp",EDGE,"E2052"),sQuery(id+"F0.wireOp",EDGE,"E2053"),sQuery(id+"F0.wireOp",EDGE,"E2054"),sQuery(id+"F0.wireOp",EDGE,"E2055"),sQuery(id+"F0.wireOp",EDGE,"E2056"),sQuery(id+"F0.wireOp",EDGE,"E2057"),sQuery(id+"F0.wireOp",EDGE,"E2058"),sQuery(id+"F0.wireOp",EDGE,"E2059"),sQuery(id+"F0.wireOp",EDGE,"E2060"),sQuery(id+"F0.wireOp",EDGE,"E2061"),sQuery(id+"F0.wireOp",EDGE,"E2062"),sQuery(id+"F0.wireOp",EDGE,"E2063"),sQuery(id+"F0.wireOp",EDGE,"E2064"),sQuery(id+"F0.wireOp",EDGE,"E2065"),sQuery(id+"F0.wireOp",EDGE,"E2066"),sQuery(id+"F0.wireOp",EDGE,"E2067"),sQuery(id+"F0.wireOp",EDGE,"E2068"),sQuery(id+"F0.wireOp",EDGE,"E2069"),sQuery(id+"F0.wireOp",EDGE,"E2070"),sQuery(id+"F0.wireOp",EDGE,"E2071"),sQuery(id+"F0.wireOp",EDGE,"E2072"),sQuery(id+"F0.wireOp",EDGE,"E2073"),sQuery(id+"F0.wireOp",EDGE,"E2074"),sQuery(id+"F0.wireOp",EDGE,"E2075"),sQuery(id+"F0.wireOp",EDGE,"E2076"),sQuery(id+"F0.wireOp",EDGE,"E2077"),sQuery(id+"F0.wireOp",EDGE,"E2078"),sQuery(id+"F0.wireOp",EDGE,"E2079"),sQuery(id+"F0.wireOp",EDGE,"E2080"),sQuery(id+"F0.wireOp",EDGE,"E2081"),sQuery(id+"F0.wireOp",EDGE,"E2082"),sQuery(id+"F0.wireOp",EDGE,"E2083"),sQuery(id+"F0.wireOp",EDGE,"E2084"),sQuery(id+"F0.wireOp",EDGE,"E2085"),sQuery(id+"F0.wireOp",EDGE,"E2086"),sQuery(id+"F0.wireOp",EDGE,"E2087"),sQuery(id+"F0.wireOp",EDGE,"E2088"),sQuery(id+"F0.wireOp",EDGE,"E2089"),sQuery(id+"F0.wireOp",EDGE,"E2090"),sQuery(id+"F0.wireOp",EDGE,"E2091"),sQuery(id+"F0.wireOp",EDGE,"E2092"),sQuery(id+"F0.wireOp",EDGE,"E2093"),sQuery(id+"F0.wireOp",EDGE,"E2094"),sQuery(id+"F0.wireOp",EDGE,"E2095"),sQuery(id+"F0.wireOp",EDGE,"E2096"),sQuery(id+"F0.wireOp",EDGE,"E2097"),sQuery(id+"F0.wireOp",EDGE,"E2098"),sQuery(id+"F0.wireOp",EDGE,"E2099"),sQuery(id+"F0.wireOp",EDGE,"E2100"),sQuery(id+"F0.wireOp",EDGE,"E2101"),sQuery(id+"F0.wireOp",EDGE,"E2102"),sQuery(id+"F0.wireOp",EDGE,"E2103"),sQuery(id+"F0.wireOp",EDGE,"E2104"),sQuery(id+"F0.wireOp",EDGE,"E2105"),sQuery(id+"F0.wireOp",EDGE,"E2106"),sQuery(id+"F0.wireOp",EDGE,"E2107"),sQuery(id+"F0.wireOp",EDGE,"E2108"),sQuery(id+"F0.wireOp",EDGE,"E2109"),sQuery(id+"F0.wireOp",EDGE,"E2110"),sQuery(id+"F0.wireOp",EDGE,"E2111"),sQuery(id+"F0.wireOp",EDGE,"E2112"),sQuery(id+"F0.wireOp",EDGE,"E2113"),sQuery(id+"F0.wireOp",EDGE,"E2114"),sQuery(id+"F0.wireOp",EDGE,"E2115"),sQuery(id+"F0.wireOp",EDGE,"E2116"),sQuery(id+"F0.wireOp",EDGE,"E2117"),sQuery(id+"F0.wireOp",EDGE,"E2118"),sQuery(id+"F0.wireOp",EDGE,"E2119"),sQuery(id+"F0.wireOp",EDGE,"E2120"),sQuery(id+"F0.wireOp",EDGE,"E2121"),sQuery(id+"F0.wireOp",EDGE,"E2122"),sQuery(id+"F0.wireOp",EDGE,"E2123"),sQuery(id+"F0.wireOp",EDGE,"E2124"),sQuery(id+"F0.wireOp",EDGE,"E2125"),sQuery(id+"F0.wireOp",EDGE,"E2126"),sQuery(id+"F0.wireOp",EDGE,"E2127"),sQuery(id+"F0.wireOp",EDGE,"E2128"),sQuery(id+"F0.wireOp",EDGE,"E2129"),sQuery(id+"F0.wireOp",EDGE,"E2130"),sQuery(id+"F0.wireOp",EDGE,"E2131"),sQuery(id+"F0.wireOp",EDGE,"E2132"),sQuery(id+"F0.wireOp",EDGE,"E2133"),sQuery(id+"F0.wireOp",EDGE,"E2134"),sQuery(id+"F0.wireOp",EDGE,"E2135"),sQuery(id+"F0.wireOp",EDGE,"E2136"),sQuery(id+"F0.wireOp",EDGE,"E2137"),sQuery(id+"F0.wireOp",EDGE,"E2138"),sQuery(id+"F0.wireOp",EDGE,"E2139"),sQuery(id+"F0.wireOp",EDGE,"E2140"),sQuery(id+"F0.wireOp",EDGE,"E2141"),sQuery(id+"F0.wireOp",EDGE,"E2142"),sQuery(id+"F0.wireOp",EDGE,"E2143"),sQuery(id+"F0.wireOp",EDGE,"E2144"),sQuery(id+"F0.wireOp",EDGE,"E2145"),sQuery(id+"F0.wireOp",EDGE,"E2146"),sQuery(id+"F0.wireOp",EDGE,"E2147"),sQuery(id+"F0.wireOp",EDGE,"E2148"),sQuery(id+"F0.wireOp",EDGE,"E2149"),sQuery(id+"F0.wireOp",EDGE,"E2150"),sQuery(id+"F0.wireOp",EDGE,"E2151"),sQuery(id+"F0.wireOp",EDGE,"E2152"),sQuery(id+"F0.wireOp",EDGE,"E2153"),sQuery(id+"F0.wireOp",EDGE,"E2154"),sQuery(id+"F0.wireOp",EDGE,"E2155"),sQuery(id+"F0.wireOp",EDGE,"E2156"),sQuery(id+"F0.wireOp",EDGE,"E2157"),sQuery(id+"F0.wireOp",EDGE,"E2158"),sQuery(id+"F0.wireOp",EDGE,"E2159"),sQuery(id+"F0.wireOp",EDGE,"E2160"),sQuery(id+"F0.wireOp",EDGE,"E2161"),sQuery(id+"F0.wireOp",EDGE,"E2162"),sQuery(id+"F0.wireOp",EDGE,"E2163"),sQuery(id+"F0.wireOp",EDGE,"E2164"),sQuery(id+"F0.wireOp",EDGE,"E2165"),sQuery(id+"F0.wireOp",EDGE,"E2166"),sQuery(id+"F0.wireOp",EDGE,"E2167"),sQuery(id+"F0.wireOp",EDGE,"E2168"),sQuery(id+"F0.wireOp",EDGE,"E2169"),sQuery(id+"F0.wireOp",EDGE,"E2170"),sQuery(id+"F0.wireOp",EDGE,"E2171"),sQuery(id+"F0.wireOp",EDGE,"E2172"),sQuery(id+"F0.wireOp",EDGE,"E2173"),sQuery(id+"F0.wireOp",EDGE,"E2174"),sQuery(id+"F0.wireOp",EDGE,"E2175"),sQuery(id+"F0.wireOp",EDGE,"E2176"),sQuery(id+"F0.wireOp",EDGE,"E2177"),sQuery(id+"F0.wireOp",EDGE,"E2178"),sQuery(id+"F0.wireOp",EDGE,"E2179"),sQuery(id+"F0.wireOp",EDGE,"E2180"),sQuery(id+"F0.wireOp",EDGE,"E2181"),sQuery(id+"F0.wireOp",EDGE,"E2182"),sQuery(id+"F0.wireOp",EDGE,"E2183"),sQuery(id+"F0.wireOp",EDGE,"E2184"),sQuery(id+"F0.wireOp",EDGE,"E2185"),sQuery(id+"F0.wireOp",EDGE,"E2186"),sQuery(id+"F0.wireOp",EDGE,"E2187"),sQuery(id+"F0.wireOp",EDGE,"E2188"),sQuery(id+"F0.wireOp",EDGE,"E2189"),sQuery(id+"F0.wireOp",EDGE,"E2190"),sQuery(id+"F0.wireOp",EDGE,"E2191"),sQuery(id+"F0.wireOp",EDGE,"E2192"),sQuery(id+"F0.wireOp",EDGE,"E2193"),sQuery(id+"F0.wireOp",EDGE,"E2194"),sQuery(id+"F0.wireOp",EDGE,"E2195"),sQuery(id+"F0.wireOp",EDGE,"E2196"),sQuery(id+"F0.wireOp",EDGE,"E2197"),sQuery(id+"F0.wireOp",EDGE,"E2198"),sQuery(id+"F0.wireOp",EDGE,"E2199"),sQuery(id+"F0.wireOp",EDGE,"E2200"),sQuery(id+"F0.wireOp",EDGE,"E2201"),sQuery(id+"F0.wireOp",EDGE,"E2202"),sQuery(id+"F0.wireOp",EDGE,"E2203"),sQuery(id+"F0.wireOp",EDGE,"E2204"),sQuery(id+"F0.wireOp",EDGE,"E2205"),sQuery(id+"F0.wireOp",EDGE,"E2206"),sQuery(id+"F0.wireOp",EDGE,"E2207"),sQuery(id+"F0.wireOp",EDGE,"E2208"),sQuery(id+"F0.wireOp",EDGE,"E2209"),sQuery(id+"F0.wireOp",EDGE,"E2210"),sQuery(id+"F0.wireOp",EDGE,"E2211"),sQuery(id+"F0.wireOp",EDGE,"E2212"),sQuery(id+"F0.wireOp",EDGE,"E2213"),sQuery(id+"F0.wireOp",EDGE,"E2214"),sQuery(id+"F0.wireOp",EDGE,"E2215"),sQuery(id+"F0.wireOp",EDGE,"E2216"),sQuery(id+"F0.wireOp",EDGE,"E2217"),sQuery(id+"F0.wireOp",EDGE,"E2218"),sQuery(id+"F0.wireOp",EDGE,"E2219"),sQuery(id+"F0.wireOp",EDGE,"E2220"),sQuery(id+"F0.wireOp",EDGE,"E2221"),sQuery(id+"F0.wireOp",EDGE,"E2222"),sQuery(id+"F0.wireOp",EDGE,"E2223"),sQuery(id+"F0.wireOp",EDGE,"E2224"),sQuery(id+"F0.wireOp",EDGE,"E2225"),sQuery(id+"F0.wireOp",EDGE,"E2226"),sQuery(id+"F0.wireOp",EDGE,"E2227"),sQuery(id+"F0.wireOp",EDGE,"E2228"),sQuery(id+"F0.wireOp",EDGE,"E2229"),sQuery(id+"F0.wireOp",EDGE,"E2230"),sQuery(id+"F0.wireOp",EDGE,"E2231"),sQuery(id+"F0.wireOp",EDGE,"E2232"),sQuery(id+"F0.wireOp",EDGE,"E2233"),sQuery(id+"F0.wireOp",EDGE,"E2234"),sQuery(id+"F0.wireOp",EDGE,"E2235"),sQuery(id+"F0.wireOp",EDGE,"E2236"),sQuery(id+"F0.wireOp",EDGE,"E2237"),sQuery(id+"F0.wireOp",EDGE,"E2238"),sQuery(id+"F0.wireOp",EDGE,"E2239"),sQuery(id+"F0.wireOp",EDGE,"E2240"),sQuery(id+"F0.wireOp",EDGE,"E2241"),sQuery(id+"F0.wireOp",EDGE,"E2242"),sQuery(id+"F0.wireOp",EDGE,"E2243"),sQuery(id+"F0.wireOp",EDGE,"E2244"),sQuery(id+"F0.wireOp",EDGE,"E2245"),sQuery(id+"F0.wireOp",EDGE,"E2246"),sQuery(id+"F0.wireOp",EDGE,"E2247"),sQuery(id+"F0.wireOp",EDGE,"E2248"),sQuery(id+"F0.wireOp",EDGE,"E2249"),sQuery(id+"F0.wireOp",EDGE,"E2250"),sQuery(id+"F0.wireOp",EDGE,"E2251"),sQuery(id+"F0.wireOp",EDGE,"E2252"),sQuery(id+"F0.wireOp",EDGE,"E2253"),sQuery(id+"F0.wireOp",EDGE,"E2254"),sQuery(id+"F0.wireOp",EDGE,"E2255"),sQuery(id+"F0.wireOp",EDGE,"E2256"),sQuery(id+"F0.wireOp",EDGE,"E2257"),sQuery(id+"F0.wireOp",EDGE,"E2258"),sQuery(id+"F0.wireOp",EDGE,"E2259"),sQuery(id+"F0.wireOp",EDGE,"E2260"),sQuery(id+"F0.wireOp",EDGE,"E2261"),sQuery(id+"F0.wireOp",EDGE,"E2262"),sQuery(id+"F0.wireOp",EDGE,"E2263"),sQuery(id+"F0.wireOp",EDGE,"E2264"),sQuery(id+"F0.wireOp",EDGE,"E2265"),sQuery(id+"F0.wireOp",EDGE,"E2266"),sQuery(id+"F0.wireOp",EDGE,"E2267"),sQuery(id+"F0.wireOp",EDGE,"E2268"),sQuery(id+"F0.wireOp",EDGE,"E2269"),sQuery(id+"F0.wireOp",EDGE,"E2270"),sQuery(id+"F0.wireOp",EDGE,"E2271"),sQuery(id+"F0.wireOp",EDGE,"E2272"),sQuery(id+"F0.wireOp",EDGE,"E2273"),sQuery(id+"F0.wireOp",EDGE,"E2274"),sQuery(id+"F0.wireOp",EDGE,"E2275"),sQuery(id+"F0.wireOp",EDGE,"E2276"),sQuery(id+"F0.wireOp",EDGE,"E2277"),sQuery(id+"F0.wireOp",EDGE,"E2278"),sQuery(id+"F0.wireOp",EDGE,"E2279"),sQuery(id+"F0.wireOp",EDGE,"E2280"),sQuery(id+"F0.wireOp",EDGE,"E2281"),sQuery(id+"F0.wireOp",EDGE,"E2282"),sQuery(id+"F0.wireOp",EDGE,"E2283"),sQuery(id+"F0.wireOp",EDGE,"E2284"),sQuery(id+"F0.wireOp",EDGE,"E2285"),sQuery(id+"F0.wireOp",EDGE,"E2286"),sQuery(id+"F0.wireOp",EDGE,"E2287"),sQuery(id+"F0.wireOp",EDGE,"E2288"),sQuery(id+"F0.wireOp",EDGE,"E2289"),sQuery(id+"F0.wireOp",EDGE,"E2290"),sQuery(id+"F0.wireOp",EDGE,"E2291"),sQuery(id+"F0.wireOp",EDGE,"E2292"),sQuery(id+"F0.wireOp",EDGE,"E2293"),sQuery(id+"F0.wireOp",EDGE,"E2294"),sQuery(id+"F0.wireOp",EDGE,"E2295"),sQuery(id+"F0.wireOp",EDGE,"E2296"),sQuery(id+"F0.wireOp",EDGE,"E2297"),sQuery(id+"F0.wireOp",EDGE,"E2298"),sQuery(id+"F0.wireOp",EDGE,"E2299"),sQuery(id+"F0.wireOp",EDGE,"E2300"),sQuery(id+"F0.wireOp",EDGE,"E2301"),sQuery(id+"F0.wireOp",EDGE,"E2302"),sQuery(id+"F0.wireOp",EDGE,"E2303"),sQuery(id+"F0.wireOp",EDGE,"E2304"),sQuery(id+"F0.wireOp",EDGE,"E2305"),sQuery(id+"F0.wireOp",EDGE,"E2306"),sQuery(id+"F0.wireOp",EDGE,"E2307"),sQuery(id+"F0.wireOp",EDGE,"E2308"),sQuery(id+"F0.wireOp",EDGE,"E2309"),sQuery(id+"F0.wireOp",EDGE,"E2310"),sQuery(id+"F0.wireOp",EDGE,"E2311"),sQuery(id+"F0.wireOp",EDGE,"E2312"),sQuery(id+"F0.wireOp",EDGE,"E2313"),sQuery(id+"F0.wireOp",EDGE,"E2314"),sQuery(id+"F0.wireOp",EDGE,"E2315"),sQuery(id+"F0.wireOp",EDGE,"E2316"),sQuery(id+"F0.wireOp",EDGE,"E2317"),sQuery(id+"F0.wireOp",EDGE,"E2318"),sQuery(id+"F0.wireOp",EDGE,"E2319"),sQuery(id+"F0.wireOp",EDGE,"E2320"),sQuery(id+"F0.wireOp",EDGE,"E2321"),sQuery(id+"F0.wireOp",EDGE,"E2322"),sQuery(id+"F0.wireOp",EDGE,"E2323"),sQuery(id+"F0.wireOp",EDGE,"E2324"),sQuery(id+"F0.wireOp",EDGE,"E2325"),sQuery(id+"F0.wireOp",EDGE,"E2326"),sQuery(id+"F0.wireOp",EDGE,"E2327"),sQuery(id+"F0.wireOp",EDGE,"E2328"),sQuery(id+"F0.wireOp",EDGE,"E2329"),sQuery(id+"F0.wireOp",EDGE,"E2330"),sQuery(id+"F0.wireOp",EDGE,"E2331"),sQuery(id+"F0.wireOp",EDGE,"E2332"),sQuery(id+"F0.wireOp",EDGE,"E2333"),sQuery(id+"F0.wireOp",EDGE,"E2334"),sQuery(id+"F0.wireOp",EDGE,"E2335"),sQuery(id+"F0.wireOp",EDGE,"E2336"),sQuery(id+"F0.wireOp",EDGE,"E2337"),sQuery(id+"F0.wireOp",EDGE,"E2338"),sQuery(id+"F0.wireOp",EDGE,"E2339"),sQuery(id+"F0.wireOp",EDGE,"E2340"),sQuery(id+"F0.wireOp",EDGE,"E2341"),sQuery(id+"F0.wireOp",EDGE,"E2342"),sQuery(id+"F0.wireOp",EDGE,"E2343"),sQuery(id+"F0.wireOp",EDGE,"E2344"),sQuery(id+"F0.wireOp",EDGE,"E2345"),sQuery(id+"F0.wireOp",EDGE,"E2346"),sQuery(id+"F0.wireOp",EDGE,"E2347"),sQuery(id+"F0.wireOp",EDGE,"E2348"),sQuery(id+"F0.wireOp",EDGE,"E2349"),sQuery(id+"F0.wireOp",EDGE,"E2350"),sQuery(id+"F0.wireOp",EDGE,"E2351"),sQuery(id+"F0.wireOp",EDGE,"E2352"),sQuery(id+"F0.wireOp",EDGE,"E2353"),sQuery(id+"F0.wireOp",EDGE,"E2354"),sQuery(id+"F0.wireOp",EDGE,"E2355"),sQuery(id+"F0.wireOp",EDGE,"E2356"),sQuery(id+"F0.wireOp",EDGE,"E2357"),sQuery(id+"F0.wireOp",EDGE,"E2358"),sQuery(id+"F0.wireOp",EDGE,"E2359"),sQuery(id+"F0.wireOp",EDGE,"E2360"),sQuery(id+"F0.wireOp",EDGE,"E2361"),sQuery(id+"F0.wireOp",EDGE,"E2362"),sQuery(id+"F0.wireOp",EDGE,"E2363"),sQuery(id+"F0.wireOp",EDGE,"E2364"),sQuery(id+"F0.wireOp",EDGE,"E2365"),sQuery(id+"F0.wireOp",EDGE,"E2366"),sQuery(id+"F0.wireOp",EDGE,"E2367"),sQuery(id+"F0.wireOp",EDGE,"E2368"),sQuery(id+"F0.wireOp",EDGE,"E2369"),sQuery(id+"F0.wireOp",EDGE,"E2370"),sQuery(id+"F0.wireOp",EDGE,"E2371"),sQuery(id+"F0.wireOp",EDGE,"E2372"),sQuery(id+"F0.wireOp",EDGE,"E2373"),sQuery(id+"F0.wireOp",EDGE,"E2374"),sQuery(id+"F0.wireOp",EDGE,"E2375"),sQuery(id+"F0.wireOp",EDGE,"E2376"),sQuery(id+"F0.wireOp",EDGE,"E2377"),sQuery(id+"F0.wireOp",EDGE,"E2378"),sQuery(id+"F0.wireOp",EDGE,"E2379"),sQuery(id+"F0.wireOp",EDGE,"E2380"),sQuery(id+"F0.wireOp",EDGE,"E2381"),sQuery(id+"F0.wireOp",EDGE,"E2382"),sQuery(id+"F0.wireOp",EDGE,"E2383"),sQuery(id+"F0.wireOp",EDGE,"E2384"),sQuery(id+"F0.wireOp",EDGE,"E2385"),sQuery(id+"F0.wireOp",EDGE,"E2386"),sQuery(id+"F0.wireOp",EDGE,"E2387"),sQuery(id+"F0.wireOp",EDGE,"E2388"),sQuery(id+"F0.wireOp",EDGE,"E2389"),sQuery(id+"F0.wireOp",EDGE,"E2390"),sQuery(id+"F0.wireOp",EDGE,"E2391"),sQuery(id+"F0.wireOp",EDGE,"E2392"),sQuery(id+"F0.wireOp",EDGE,"E2393"),sQuery(id+"F0.wireOp",EDGE,"E2394"),sQuery(id+"F0.wireOp",EDGE,"E2395"),sQuery(id+"F0.wireOp",EDGE,"E2396"),sQuery(id+"F0.wireOp",EDGE,"E2397"),sQuery(id+"F0.wireOp",EDGE,"E2398"),sQuery(id+"F0.wireOp",EDGE,"E2399"),sQuery(id+"F0.wireOp",EDGE,"E2400"),sQuery(id+"F0.wireOp",EDGE,"E2401"),sQuery(id+"F0.wireOp",EDGE,"E2402"),sQuery(id+"F0.wireOp",EDGE,"E2403"),sQuery(id+"F0.wireOp",EDGE,"E2404"),sQuery(id+"F0.wireOp",EDGE,"E2405"),sQuery(id+"F0.wireOp",EDGE,"E2406"),sQuery(id+"F0.wireOp",EDGE,"E2407"),sQuery(id+"F0.wireOp",EDGE,"E2408"),sQuery(id+"F0.wireOp",EDGE,"E2409"),sQuery(id+"F0.wireOp",EDGE,"E2410"),sQuery(id+"F0.wireOp",EDGE,"E2411"),sQuery(id+"F0.wireOp",EDGE,"E2412"),sQuery(id+"F0.wireOp",EDGE,"E2413"),sQuery(id+"F0.wireOp",EDGE,"E2414"),sQuery(id+"F0.wireOp",EDGE,"E2415"),sQuery(id+"F0.wireOp",EDGE,"E2416"),sQuery(id+"F0.wireOp",EDGE,"E2417"),sQuery(id+"F0.wireOp",EDGE,"E2418"),sQuery(id+"F0.wireOp",EDGE,"E2419"),sQuery(id+"F0.wireOp",EDGE,"E2420"),sQuery(id+"F0.wireOp",EDGE,"E2421"),sQuery(id+"F0.wireOp",EDGE,"E2422"),sQuery(id+"F0.wireOp",EDGE,"E2423"),sQuery(id+"F0.wireOp",EDGE,"E2424"),sQuery(id+"F0.wireOp",EDGE,"E2425"),sQuery(id+"F0.wireOp",EDGE,"E2426"),sQuery(id+"F0.wireOp",EDGE,"E2427"),sQuery(id+"F0.wireOp",EDGE,"E2428"),sQuery(id+"F0.wireOp",EDGE,"E2429"),sQuery(id+"F0.wireOp",EDGE,"E2430"),sQuery(id+"F0.wireOp",EDGE,"E2431"),sQuery(id+"F0.wireOp",EDGE,"E2432"),sQuery(id+"F0.wireOp",EDGE,"E2433"),sQuery(id+"F0.wireOp",EDGE,"E2434"),sQuery(id+"F0.wireOp",EDGE,"E2435"),sQuery(id+"F0.wireOp",EDGE,"E2436"),sQuery(id+"F0.wireOp",EDGE,"E2437"),sQuery(id+"F0.wireOp",EDGE,"E2438"),sQuery(id+"F0.wireOp",EDGE,"E2439"),sQuery(id+"F0.wireOp",EDGE,"E2440"),sQuery(id+"F0.wireOp",EDGE,"E2441"),sQuery(id+"F0.wireOp",EDGE,"E2442"),sQuery(id+"F0.wireOp",EDGE,"E2443"),sQuery(id+"F0.wireOp",EDGE,"E2444"),sQuery(id+"F0.wireOp",EDGE,"E2445"),sQuery(id+"F0.wireOp",EDGE,"E2446"),sQuery(id+"F0.wireOp",EDGE,"E2447"),sQuery(id+"F0.wireOp",EDGE,"E2448"),sQuery(id+"F0.wireOp",EDGE,"E2449"),sQuery(id+"F0.wireOp",EDGE,"E2450"),sQuery(id+"F0.wireOp",EDGE,"E2451"),sQuery(id+"F0.wireOp",EDGE,"E2452"),sQuery(id+"F0.wireOp",EDGE,"E2453"),sQuery(id+"F0.wireOp",EDGE,"E2454"),sQuery(id+"F0.wireOp",EDGE,"E2455"),sQuery(id+"F0.wireOp",EDGE,"E2456"),sQuery(id+"F0.wireOp",EDGE,"E2457"),sQuery(id+"F0.wireOp",EDGE,"E2458"),sQuery(id+"F0.wireOp",EDGE,"E2459"),sQuery(id+"F0.wireOp",EDGE,"E2460"),sQuery(id+"F0.wireOp",EDGE,"E2461"),sQuery(id+"F0.wireOp",EDGE,"E2462"),sQuery(id+"F0.wireOp",EDGE,"E2463"),sQuery(id+"F0.wireOp",EDGE,"E2464"),sQuery(id+"F0.wireOp",EDGE,"E2465"),sQuery(id+"F0.wireOp",EDGE,"E2466"),sQuery(id+"F0.wireOp",EDGE,"E2467"),sQuery(id+"F0.wireOp",EDGE,"E2468"),sQuery(id+"F0.wireOp",EDGE,"E2469"),sQuery(id+"F0.wireOp",EDGE,"E2470"),sQuery(id+"F0.wireOp",EDGE,"E2471"),sQuery(id+"F0.wireOp",EDGE,"E2472"),sQuery(id+"F0.wireOp",EDGE,"E2473"),sQuery(id+"F0.wireOp",EDGE,"E2474"),sQuery(id+"F0.wireOp",EDGE,"E2475"),sQuery(id+"F0.wireOp",EDGE,"E2476"),sQuery(id+"F0.wireOp",EDGE,"E2477"),sQuery(id+"F0.wireOp",EDGE,"E2478"),sQuery(id+"F0.wireOp",EDGE,"E2479"),sQuery(id+"F0.wireOp",EDGE,"E2480"),sQuery(id+"F0.wireOp",EDGE,"E2481"),sQuery(id+"F0.wireOp",EDGE,"E2482"),sQuery(id+"F0.wireOp",EDGE,"E2483"),sQuery(id+"F0.wireOp",EDGE,"E2484"),sQuery(id+"F0.wireOp",EDGE,"E2485"),sQuery(id+"F0.wireOp",EDGE,"E2486"),sQuery(id+"F0.wireOp",EDGE,"E2487"),sQuery(id+"F0.wireOp",EDGE,"E2488"),sQuery(id+"F0.wireOp",EDGE,"E2489"),sQuery(id+"F0.wireOp",EDGE,"E2490"),sQuery(id+"F0.wireOp",EDGE,"E2491"),sQuery(id+"F0.wireOp",EDGE,"E2492"),sQuery(id+"F0.wireOp",EDGE,"E2493"),sQuery(id+"F0.wireOp",EDGE,"E2494"),sQuery(id+"F0.wireOp",EDGE,"E2495"),sQuery(id+"F0.wireOp",EDGE,"E2496"),sQuery(id+"F0.wireOp",EDGE,"E2497"),sQuery(id+"F0.wireOp",EDGE,"E2498"),sQuery(id+"F0.wireOp",EDGE,"E2499"),sQuery(id+"F0.wireOp",EDGE,"E2500"),sQuery(id+"F0.wireOp",EDGE,"E2501"),sQuery(id+"F0.wireOp",EDGE,"E2502"),sQuery(id+"F0.wireOp",EDGE,"E2503"),sQuery(id+"F0.wireOp",EDGE,"E2504"),sQuery(id+"F0.wireOp",EDGE,"E2505"),sQuery(id+"F0.wireOp",EDGE,"E2506"),sQuery(id+"F0.wireOp",EDGE,"E2507"),sQuery(id+"F0.wireOp",EDGE,"E2508"),sQuery(id+"F0.wireOp",EDGE,"E2509"),sQuery(id+"F0.wireOp",EDGE,"E2510"),sQuery(id+"F0.wireOp",EDGE,"E2511"),sQuery(id+"F0.wireOp",EDGE,"E2512"),sQuery(id+"F0.wireOp",EDGE,"E2513"),sQuery(id+"F0.wireOp",EDGE,"E2514"),sQuery(id+"F0.wireOp",EDGE,"E2515"),sQuery(id+"F0.wireOp",EDGE,"E2516"),sQuery(id+"F0.wireOp",EDGE,"E2517"),sQuery(id+"F0.wireOp",EDGE,"E2518"),sQuery(id+"F0.wireOp",EDGE,"E2519"),sQuery(id+"F0.wireOp",EDGE,"E2520"),sQuery(id+"F0.wireOp",EDGE,"E2521"),sQuery(id+"F0.wireOp",EDGE,"E2522"),sQuery(id+"F0.wireOp",EDGE,"E2523"),sQuery(id+"F0.wireOp",EDGE,"E2524"),sQuery(id+"F0.wireOp",EDGE,"E2525"),sQuery(id+"F0.wireOp",EDGE,"E2526"),sQuery(id+"F0.wireOp",EDGE,"E2527"),sQuery(id+"F0.wireOp",EDGE,"E2528"),sQuery(id+"F0.wireOp",EDGE,"E2529"),sQuery(id+"F0.wireOp",EDGE,"E2530"),sQuery(id+"F0.wireOp",EDGE,"E2531"),sQuery(id+"F0.wireOp",EDGE,"E2532"),sQuery(id+"F0.wireOp",EDGE,"E2533"),sQuery(id+"F0.wireOp",EDGE,"E2534"),sQuery(id+"F0.wireOp",EDGE,"E2535"),sQuery(id+"F0.wireOp",EDGE,"E2536"),sQuery(id+"F0.wireOp",EDGE,"E2537"),sQuery(id+"F0.wireOp",EDGE,"E2538"),sQuery(id+"F0.wireOp",EDGE,"E2539"),sQuery(id+"F0.wireOp",EDGE,"E2540"),sQuery(id+"F0.wireOp",EDGE,"E2541"),sQuery(id+"F0.wireOp",EDGE,"E2542"),sQuery(id+"F0.wireOp",EDGE,"E2543"),sQuery(id+"F0.wireOp",EDGE,"E2544"),sQuery(id+"F0.wireOp",EDGE,"E2545"),sQuery(id+"F0.wireOp",EDGE,"E2546"),sQuery(id+"F0.wireOp",EDGE,"E2547"),sQuery(id+"F0.wireOp",EDGE,"E2548"),sQuery(id+"F0.wireOp",EDGE,"E2549"),sQuery(id+"F0.wireOp",EDGE,"E2550"),sQuery(id+"F0.wireOp",EDGE,"E2551"),sQuery(id+"F0.wireOp",EDGE,"E2552"),sQuery(id+"F0.wireOp",EDGE,"E2553"),sQuery(id+"F0.wireOp",EDGE,"E2554"),sQuery(id+"F0.wireOp",EDGE,"E2555"),sQuery(id+"F0.wireOp",EDGE,"E2556"),sQuery(id+"F0.wireOp",EDGE,"E2557"),sQuery(id+"F0.wireOp",EDGE,"E2558"),sQuery(id+"F0.wireOp",EDGE,"E2559"),sQuery(id+"F0.wireOp",EDGE,"E2560"),sQuery(id+"F0.wireOp",EDGE,"E2561"),sQuery(id+"F0.wireOp",EDGE,"E2562"),sQuery(id+"F0.wireOp",EDGE,"E2563"),sQuery(id+"F0.wireOp",EDGE,"E2564"),sQuery(id+"F0.wireOp",EDGE,"E2565"),sQuery(id+"F0.wireOp",EDGE,"E2566"),sQuery(id+"F0.wireOp",EDGE,"E2567"),sQuery(id+"F0.wireOp",EDGE,"E2568"),sQuery(id+"F0.wireOp",EDGE,"E2569"),sQuery(id+"F0.wireOp",EDGE,"E2570"),sQuery(id+"F0.wireOp",EDGE,"E2571"),sQuery(id+"F0.wireOp",EDGE,"E2572"),sQuery(id+"F0.wireOp",EDGE,"E2573"),sQuery(id+"F0.wireOp",EDGE,"E2574"),sQuery(id+"F0.wireOp",EDGE,"E2575"),sQuery(id+"F0.wireOp",EDGE,"E2576"),sQuery(id+"F0.wireOp",EDGE,"E2577"),sQuery(id+"F0.wireOp",EDGE,"E2578"),sQuery(id+"F0.wireOp",EDGE,"E2579"),sQuery(id+"F0.wireOp",EDGE,"E2580"),sQuery(id+"F0.wireOp",EDGE,"E2581"),sQuery(id+"F0.wireOp",EDGE,"E2582"),sQuery(id+"F0.wireOp",EDGE,"E2583"),sQuery(id+"F0.wireOp",EDGE,"E2584"),sQuery(id+"F0.wireOp",EDGE,"E2585"),sQuery(id+"F0.wireOp",EDGE,"E2586"),sQuery(id+"F0.wireOp",EDGE,"E2587"),sQuery(id+"F0.wireOp",EDGE,"E2588"),sQuery(id+"F0.wireOp",EDGE,"E2589"),sQuery(id+"F0.wireOp",EDGE,"E2590"),sQuery(id+"F0.wireOp",EDGE,"E2591"),sQuery(id+"F0.wireOp",EDGE,"E2592"),sQuery(id+"F0.wireOp",EDGE,"E2593"),sQuery(id+"F0.wireOp",EDGE,"E2594"),sQuery(id+"F0.wireOp",EDGE,"E2595"),sQuery(id+"F0.wireOp",EDGE,"E2596"),sQuery(id+"F0.wireOp",EDGE,"E2597"),sQuery(id+"F0.wireOp",EDGE,"E2598"),sQuery(id+"F0.wireOp",EDGE,"E2599"),sQuery(id+"F0.wireOp",EDGE,"E2600"),sQuery(id+"F0.wireOp",EDGE,"E2601"),sQuery(id+"F0.wireOp",EDGE,"E2602"),sQuery(id+"F0.wireOp",EDGE,"E2603"),sQuery(id+"F0.wireOp",EDGE,"E2604"),sQuery(id+"F0.wireOp",EDGE,"E2605"),sQuery(id+"F0.wireOp",EDGE,"E2606"),sQuery(id+"F0.wireOp",EDGE,"E2607"),sQuery(id+"F0.wireOp",EDGE,"E2608"),sQuery(id+"F0.wireOp",EDGE,"E2609"),sQuery(id+"F0.wireOp",EDGE,"E2610"),sQuery(id+"F0.wireOp",EDGE,"E2611"),sQuery(id+"F0.wireOp",EDGE,"E2612"),sQuery(id+"F0.wireOp",EDGE,"E2613"),sQuery(id+"F0.wireOp",EDGE,"E2614"),sQuery(id+"F0.wireOp",EDGE,"E2615"),sQuery(id+"F0.wireOp",EDGE,"E2616"),sQuery(id+"F0.wireOp",EDGE,"E2617"),sQuery(id+"F0.wireOp",EDGE,"E2618"),sQuery(id+"F0.wireOp",EDGE,"E2619"),sQuery(id+"F0.wireOp",EDGE,"E2620"),sQuery(id+"F0.wireOp",EDGE,"E2621"),sQuery(id+"F0.wireOp",EDGE,"E2622"),sQuery(id+"F0.wireOp",EDGE,"E2623"),sQuery(id+"F0.wireOp",EDGE,"E2624"),sQuery(id+"F0.wireOp",EDGE,"E2625"),sQuery(id+"F0.wireOp",EDGE,"E2626"),sQuery(id+"F0.wireOp",EDGE,"E2627"),sQuery(id+"F0.wireOp",EDGE,"E2628"),sQuery(id+"F0.wireOp",EDGE,"E2629"),sQuery(id+"F0.wireOp",EDGE,"E2630"),sQuery(id+"F0.wireOp",EDGE,"E2631"),sQuery(id+"F0.wireOp",EDGE,"E2632"),sQuery(id+"F0.wireOp",EDGE,"E2633"),sQuery(id+"F0.wireOp",EDGE,"E2634"),sQuery(id+"F0.wireOp",EDGE,"E2635"),sQuery(id+"F0.wireOp",EDGE,"E2636"),sQuery(id+"F0.wireOp",EDGE,"E2637"),sQuery(id+"F0.wireOp",EDGE,"E2638"),sQuery(id+"F0.wireOp",EDGE,"E2639"),sQuery(id+"F0.wireOp",EDGE,"E2640"),sQuery(id+"F0.wireOp",EDGE,"E2641"),sQuery(id+"F0.wireOp",EDGE,"E2642"),sQuery(id+"F0.wireOp",EDGE,"E2643"),sQuery(id+"F0.wireOp",EDGE,"E2644"),sQuery(id+"F0.wireOp",EDGE,"E2645"),sQuery(id+"F0.wireOp",EDGE,"E2646"),sQuery(id+"F0.wireOp",EDGE,"E2647"),sQuery(id+"F0.wireOp",EDGE,"E2648"),sQuery(id+"F0.wireOp",EDGE,"E2649"),sQuery(id+"F0.wireOp",EDGE,"E2650"),sQuery(id+"F0.wireOp",EDGE,"E2651"),sQuery(id+"F0.wireOp",EDGE,"E2652"),sQuery(id+"F0.wireOp",EDGE,"E2653"),sQuery(id+"F0.wireOp",EDGE,"E2654"),sQuery(id+"F0.wireOp",EDGE,"E2655"),sQuery(id+"F0.wireOp",EDGE,"E2656"),sQuery(id+"F0.wireOp",EDGE,"E2657"),sQuery(id+"F0.wireOp",EDGE,"E2658"),sQuery(id+"F0.wireOp",EDGE,"E2659"),sQuery(id+"F0.wireOp",EDGE,"E2660"),sQuery(id+"F0.wireOp",EDGE,"E2661"),sQuery(id+"F0.wireOp",EDGE,"E2662"),sQuery(id+"F0.wireOp",EDGE,"E2663"),sQuery(id+"F0.wireOp",EDGE,"E2664"),sQuery(id+"F0.wireOp",EDGE,"E2665"),sQuery(id+"F0.wireOp",EDGE,"E2666"),sQuery(id+"F0.wireOp",EDGE,"E2667"),sQuery(id+"F0.wireOp",EDGE,"E2668"),sQuery(id+"F0.wireOp",EDGE,"E2669"),sQuery(id+"F0.wireOp",EDGE,"E2670"),sQuery(id+"F0.wireOp",EDGE,"E2671"),sQuery(id+"F0.wireOp",EDGE,"E2672"),sQuery(id+"F0.wireOp",EDGE,"E2673"),sQuery(id+"F0.wireOp",EDGE,"E2674"),sQuery(id+"F0.wireOp",EDGE,"E2675"),sQuery(id+"F0.wireOp",EDGE,"E2676"),sQuery(id+"F0.wireOp",EDGE,"E2677"),sQuery(id+"F0.wireOp",EDGE,"E2678"),sQuery(id+"F0.wireOp",EDGE,"E2679"),sQuery(id+"F0.wireOp",EDGE,"E2680"),sQuery(id+"F0.wireOp",EDGE,"E2681"),sQuery(id+"F0.wireOp",EDGE,"E2682"),sQuery(id+"F0.wireOp",EDGE,"E2683"),sQuery(id+"F0.wireOp",EDGE,"E2684"),sQuery(id+"F0.wireOp",EDGE,"E2685"),sQuery(id+"F0.wireOp",EDGE,"E2686"),sQuery(id+"F0.wireOp",EDGE,"E2687"),sQuery(id+"F0.wireOp",EDGE,"E2688"),sQuery(id+"F0.wireOp",EDGE,"E2689"),sQuery(id+"F0.wireOp",EDGE,"E2690"),sQuery(id+"F0.wireOp",EDGE,"E2691"),sQuery(id+"F0.wireOp",EDGE,"E2692"),sQuery(id+"F0.wireOp",EDGE,"E2693"),sQuery(id+"F0.wireOp",EDGE,"E2694"),sQuery(id+"F0.wireOp",EDGE,"E2695"),sQuery(id+"F0.wireOp",EDGE,"E2696"),sQuery(id+"F0.wireOp",EDGE,"E2697"),sQuery(id+"F0.wireOp",EDGE,"E2698"),sQuery(id+"F0.wireOp",EDGE,"E2699"),sQuery(id+"F0.wireOp",EDGE,"E2700"),sQuery(id+"F0.wireOp",EDGE,"E2701"),sQuery(id+"F0.wireOp",EDGE,"E2702"),sQuery(id+"F0.wireOp",EDGE,"E2703"),sQuery(id+"F0.wireOp",EDGE,"E2704"),sQuery(id+"F0.wireOp",EDGE,"E2705"),sQuery(id+"F0.wireOp",EDGE,"E2706"),sQuery(id+"F0.wireOp",EDGE,"E2707"),sQuery(id+"F0.wireOp",EDGE,"E2708"),sQuery(id+"F0.wireOp",EDGE,"E2709"),sQuery(id+"F0.wireOp",EDGE,"E2710"),sQuery(id+"F0.wireOp",EDGE,"E2711"),sQuery(id+"F0.wireOp",EDGE,"E2712"),sQuery(id+"F0.wireOp",EDGE,"E2713"),sQuery(id+"F0.wireOp",EDGE,"E2714"),sQuery(id+"F0.wireOp",EDGE,"E2715"),sQuery(id+"F0.wireOp",EDGE,"E2716"),sQuery(id+"F0.wireOp",EDGE,"E2717"),sQuery(id+"F0.wireOp",EDGE,"E2718"),sQuery(id+"F0.wireOp",EDGE,"E2719"),sQuery(id+"F0.wireOp",EDGE,"E2720"),sQuery(id+"F0.wireOp",EDGE,"E2721"),sQuery(id+"F0.wireOp",EDGE,"E2722"),sQuery(id+"F0.wireOp",EDGE,"E2723"),sQuery(id+"F0.wireOp",EDGE,"E2724"),sQuery(id+"F0.wireOp",EDGE,"E2725"),sQuery(id+"F0.wireOp",EDGE,"E2726"),sQuery(id+"F0.wireOp",EDGE,"E2727"),sQuery(id+"F0.wireOp",EDGE,"E2728"),sQuery(id+"F0.wireOp",EDGE,"E2729"),sQuery(id+"F0.wireOp",EDGE,"E2730"),sQuery(id+"F0.wireOp",EDGE,"E2731"),sQuery(id+"F0.wireOp",EDGE,"E2732"),sQuery(id+"F0.wireOp",EDGE,"E2733"),sQuery(id+"F0.wireOp",EDGE,"E2734"),sQuery(id+"F0.wireOp",EDGE,"E2735"),sQuery(id+"F0.wireOp",EDGE,"E2736"),sQuery(id+"F0.wireOp",EDGE,"E2737"),sQuery(id+"F0.wireOp",EDGE,"E2738"),sQuery(id+"F0.wireOp",EDGE,"E2739"),sQuery(id+"F0.wireOp",EDGE,"E2740"),sQuery(id+"F0.wireOp",EDGE,"E2741"),sQuery(id+"F0.wireOp",EDGE,"E2742"),sQuery(id+"F0.wireOp",EDGE,"E2743"),sQuery(id+"F0.wireOp",EDGE,"E2744"),sQuery(id+"F0.wireOp",EDGE,"E2745"),sQuery(id+"F0.wireOp",EDGE,"E2746"),sQuery(id+"F0.wireOp",EDGE,"E2747"),sQuery(id+"F0.wireOp",EDGE,"E2748"),sQuery(id+"F0.wireOp",EDGE,"E2749"),sQuery(id+"F0.wireOp",EDGE,"E2750"),sQuery(id+"F0.wireOp",EDGE,"E2751"),sQuery(id+"F0.wireOp",EDGE,"E2752"),sQuery(id+"F0.wireOp",EDGE,"E2753"),sQuery(id+"F0.wireOp",EDGE,"E2754"),sQuery(id+"F0.wireOp",EDGE,"E2755"),sQuery(id+"F0.wireOp",EDGE,"E2756"),sQuery(id+"F0.wireOp",EDGE,"E2757"),sQuery(id+"F0.wireOp",EDGE,"E2758"),sQuery(id+"F0.wireOp",EDGE,"E2759"),sQuery(id+"F0.wireOp",EDGE,"E2760"),sQuery(id+"F0.wireOp",EDGE,"E2761"),sQuery(id+"F0.wireOp",EDGE,"E2762"),sQuery(id+"F0.wireOp",EDGE,"E2763"),sQuery(id+"F0.wireOp",EDGE,"E2764"),sQuery(id+"F0.wireOp",EDGE,"E2765"),sQuery(id+"F0.wireOp",EDGE,"E2766"),sQuery(id+"F0.wireOp",EDGE,"E2767"),sQuery(id+"F0.wireOp",EDGE,"E2768"),sQuery(id+"F0.wireOp",EDGE,"E2769"),sQuery(id+"F0.wireOp",EDGE,"E2770"),sQuery(id+"F0.wireOp",EDGE,"E2771"),sQuery(id+"F0.wireOp",EDGE,"E2772"),sQuery(id+"F0.wireOp",EDGE,"E2773"),sQuery(id+"F0.wireOp",EDGE,"E2774"),sQuery(id+"F0.wireOp",EDGE,"E2775"),sQuery(id+"F0.wireOp",EDGE,"E2776"),sQuery(id+"F0.wireOp",EDGE,"E2777"),sQuery(id+"F0.wireOp",EDGE,"E2778"),sQuery(id+"F0.wireOp",EDGE,"E2779"),sQuery(id+"F0.wireOp",EDGE,"E2780"),sQuery(id+"F0.wireOp",EDGE,"E2781"),sQuery(id+"F0.wireOp",EDGE,"E2782"),sQuery(id+"F0.wireOp",EDGE,"E2783"),sQuery(id+"F0.wireOp",EDGE,"E2784"),sQuery(id+"F0.wireOp",EDGE,"E2785"),sQuery(id+"F0.wireOp",EDGE,"E2786"),sQuery(id+"F0.wireOp",EDGE,"E2787"),sQuery(id+"F0.wireOp",EDGE,"E2788"),sQuery(id+"F0.wireOp",EDGE,"E2789"),sQuery(id+"F0.wireOp",EDGE,"E2790"),sQuery(id+"F0.wireOp",EDGE,"E2791"),sQuery(id+"F0.wireOp",EDGE,"E2792"),sQuery(id+"F0.wireOp",EDGE,"E2793"),sQuery(id+"F0.wireOp",EDGE,"E2794"),sQuery(id+"F0.wireOp",EDGE,"E2795"),sQuery(id+"F0.wireOp",EDGE,"E2796"),sQuery(id+"F0.wireOp",EDGE,"E2797"),sQuery(id+"F0.wireOp",EDGE,"E2798"),sQuery(id+"F0.wireOp",EDGE,"E2799"),sQuery(id+"F0.wireOp",EDGE,"E2800"),sQuery(id+"F0.wireOp",EDGE,"E2801"),sQuery(id+"F0.wireOp",EDGE,"E2802"),sQuery(id+"F0.wireOp",EDGE,"E2803"),sQuery(id+"F0.wireOp",EDGE,"E2804"),sQuery(id+"F0.wireOp",EDGE,"E2805"),sQuery(id+"F0.wireOp",EDGE,"E2806"),sQuery(id+"F0.wireOp",EDGE,"E2807"),sQuery(id+"F0.wireOp",EDGE,"E2808"),sQuery(id+"F0.wireOp",EDGE,"E2809"),sQuery(id+"F0.wireOp",EDGE,"E2810"),sQuery(id+"F0.wireOp",EDGE,"E2811"),sQuery(id+"F0.wireOp",EDGE,"E2812"),sQuery(id+"F0.wireOp",EDGE,"E2813"),sQuery(id+"F0.wireOp",EDGE,"E2814"),sQuery(id+"F0.wireOp",EDGE,"E2815"),sQuery(id+"F0.wireOp",EDGE,"E2816"),sQuery(id+"F0.wireOp",EDGE,"E2817"),sQuery(id+"F0.wireOp",EDGE,"E2818"),sQuery(id+"F0.wireOp",EDGE,"E2819"),sQuery(id+"F0.wireOp",EDGE,"E2820"),sQuery(id+"F0.wireOp",EDGE,"E2821"),sQuery(id+"F0.wireOp",EDGE,"E2822"),sQuery(id+"F0.wireOp",EDGE,"E2823"),sQuery(id+"F0.wireOp",EDGE,"E2824"),sQuery(id+"F0.wireOp",EDGE,"E2825"),sQuery(id+"F0.wireOp",EDGE,"E2826"),sQuery(id+"F0.wireOp",EDGE,"E2827"),sQuery(id+"F0.wireOp",EDGE,"E2828"),sQuery(id+"F0.wireOp",EDGE,"E2829"),sQuery(id+"F0.wireOp",EDGE,"E2830"),sQuery(id+"F0.wireOp",EDGE,"E2831"),sQuery(id+"F0.wireOp",EDGE,"E2832"),sQuery(id+"F0.wireOp",EDGE,"E2833"),sQuery(id+"F0.wireOp",EDGE,"E2834"),sQuery(id+"F0.wireOp",EDGE,"E2835"),sQuery(id+"F0.wireOp",EDGE,"E2836"),sQuery(id+"F0.wireOp",EDGE,"E2837"),sQuery(id+"F0.wireOp",EDGE,"E2838"),sQuery(id+"F0.wireOp",EDGE,"E2839"),sQuery(id+"F0.wireOp",EDGE,"E2840"),sQuery(id+"F0.wireOp",EDGE,"E2841"),sQuery(id+"F0.wireOp",EDGE,"E2842"),sQuery(id+"F0.wireOp",EDGE,"E2843"),sQuery(id+"F0.wireOp",EDGE,"E2844"),sQuery(id+"F0.wireOp",EDGE,"E2845"),sQuery(id+"F0.wireOp",EDGE,"E2846"),sQuery(id+"F0.wireOp",EDGE,"E2847"),sQuery(id+"F0.wireOp",EDGE,"E2848"),sQuery(id+"F0.wireOp",EDGE,"E2849"),sQuery(id+"F0.wireOp",EDGE,"E2850"),sQuery(id+"F0.wireOp",EDGE,"E2851"),sQuery(id+"F0.wireOp",EDGE,"E2852"),sQuery(id+"F0.wireOp",EDGE,"E2853"),sQuery(id+"F0.wireOp",EDGE,"E2854"),sQuery(id+"F0.wireOp",EDGE,"E2855"),sQuery(id+"F0.wireOp",EDGE,"E2856"),sQuery(id+"F0.wireOp",EDGE,"E2857"),sQuery(id+"F0.wireOp",EDGE,"E2858"),sQuery(id+"F0.wireOp",EDGE,"E2859"),sQuery(id+"F0.wireOp",EDGE,"E2860"),sQuery(id+"F0.wireOp",EDGE,"E2861"),sQuery(id+"F0.wireOp",EDGE,"E2862"),sQuery(id+"F0.wireOp",EDGE,"E2863"),sQuery(id+"F0.wireOp",EDGE,"E2864"),sQuery(id+"F0.wireOp",EDGE,"E2865"),sQuery(id+"F0.wireOp",EDGE,"E2866"),sQuery(id+"F0.wireOp",EDGE,"E2867"),sQuery(id+"F0.wireOp",EDGE,"E2868"),sQuery(id+"F0.wireOp",EDGE,"E2869"),sQuery(id+"F0.wireOp",EDGE,"E2870"),sQuery(id+"F0.wireOp",EDGE,"E2871"),sQuery(id+"F0.wireOp",EDGE,"E2872"),sQuery(id+"F0.wireOp",EDGE,"E2873"),sQuery(id+"F0.wireOp",EDGE,"E2874"),sQuery(id+"F0.wireOp",EDGE,"E2875"),sQuery(id+"F0.wireOp",EDGE,"E2876"),sQuery(id+"F0.wireOp",EDGE,"E2877"),sQuery(id+"F0.wireOp",EDGE,"E2878"),sQuery(id+"F0.wireOp",EDGE,"E2879"),sQuery(id+"F0.wireOp",EDGE,"E2880"),sQuery(id+"F0.wireOp",EDGE,"E2881"),sQuery(id+"F0.wireOp",EDGE,"E2882"),sQuery(id+"F0.wireOp",EDGE,"E2883"),sQuery(id+"F0.wireOp",EDGE,"E2884"),sQuery(id+"F0.wireOp",EDGE,"E2885"),sQuery(id+"F0.wireOp",EDGE,"E2886"),sQuery(id+"F0.wireOp",EDGE,"E2887"),sQuery(id+"F0.wireOp",EDGE,"E2888"),sQuery(id+"F0.wireOp",EDGE,"E2889"),sQuery(id+"F0.wireOp",EDGE,"E2890"),sQuery(id+"F0.wireOp",EDGE,"E2891"),sQuery(id+"F0.wireOp",EDGE,"E2892"),sQuery(id+"F0.wireOp",EDGE,"E2893"),sQuery(id+"F0.wireOp",EDGE,"E2894"),sQuery(id+"F0.wireOp",EDGE,"E2895"),sQuery(id+"F0.wireOp",EDGE,"E2896"),sQuery(id+"F0.wireOp",EDGE,"E2897"),sQuery(id+"F0.wireOp",EDGE,"E2898"),sQuery(id+"F0.wireOp",EDGE,"E2899"),sQuery(id+"F0.wireOp",EDGE,"E2900"),sQuery(id+"F0.wireOp",EDGE,"E2901"),sQuery(id+"F0.wireOp",EDGE,"E2902"),sQuery(id+"F0.wireOp",EDGE,"E2903"),sQuery(id+"F0.wireOp",EDGE,"E2904"),sQuery(id+"F0.wireOp",EDGE,"E2905"),sQuery(id+"F0.wireOp",EDGE,"E2906"),sQuery(id+"F0.wireOp",EDGE,"E2907"),sQuery(id+"F0.wireOp",EDGE,"E2908"),sQuery(id+"F0.wireOp",EDGE,"E2909"),sQuery(id+"F0.wireOp",EDGE,"E2910"),sQuery(id+"F0.wireOp",EDGE,"E2911"),sQuery(id+"F0.wireOp",EDGE,"E2912"),sQuery(id+"F0.wireOp",EDGE,"E2913"),sQuery(id+"F0.wireOp",EDGE,"E2914"),sQuery(id+"F0.wireOp",EDGE,"E2915"),sQuery(id+"F0.wireOp",EDGE,"E2916"),sQuery(id+"F0.wireOp",EDGE,"E2917"),sQuery(id+"F0.wireOp",EDGE,"E2918"),sQuery(id+"F0.wireOp",EDGE,"E2919"),sQuery(id+"F0.wireOp",EDGE,"E2920"),sQuery(id+"F0.wireOp",EDGE,"E2921"),sQuery(id+"F0.wireOp",EDGE,"E2922"),sQuery(id+"F0.wireOp",EDGE,"E2923"),sQuery(id+"F0.wireOp",EDGE,"E2924"),sQuery(id+"F0.wireOp",EDGE,"E2925"),sQuery(id+"F0.wireOp",EDGE,"E2926"),sQuery(id+"F0.wireOp",EDGE,"E2927"),sQuery(id+"F0.wireOp",EDGE,"E2928"),sQuery(id+"F0.wireOp",EDGE,"E2929"),sQuery(id+"F0.wireOp",EDGE,"E2930"),sQuery(id+"F0.wireOp",EDGE,"E2931"),sQuery(id+"F0.wireOp",EDGE,"E2932"),sQuery(id+"F0.wireOp",EDGE,"E2933"),sQuery(id+"F0.wireOp",EDGE,"E2934"),sQuery(id+"F0.wireOp",EDGE,"E2935"),sQuery(id+"F0.wireOp",EDGE,"E2936"),sQuery(id+"F0.wireOp",EDGE,"E2937"),sQuery(id+"F0.wireOp",EDGE,"E2938"),sQuery(id+"F0.wireOp",EDGE,"E2939"),sQuery(id+"F0.wireOp",EDGE,"E2940"),sQuery(id+"F0.wireOp",EDGE,"E2941"),sQuery(id+"F0.wireOp",EDGE,"E2942"),sQuery(id+"F0.wireOp",EDGE,"E2943"),sQuery(id+"F0.wireOp",EDGE,"E2944"),sQuery(id+"F0.wireOp",EDGE,"E2945"),sQuery(id+"F0.wireOp",EDGE,"E2946"),sQuery(id+"F0.wireOp",EDGE,"E2947"),sQuery(id+"F0.wireOp",EDGE,"E2948"),sQuery(id+"F0.wireOp",EDGE,"E2949"),sQuery(id+"F0.wireOp",EDGE,"E2950"),sQuery(id+"F0.wireOp",EDGE,"E2951"),sQuery(id+"F0.wireOp",EDGE,"E2952"),sQuery(id+"F0.wireOp",EDGE,"E2953"),sQuery(id+"F0.wireOp",EDGE,"E2954"),sQuery(id+"F0.wireOp",EDGE,"E2955"),sQuery(id+"F0.wireOp",EDGE,"E2956"),sQuery(id+"F0.wireOp",EDGE,"E2957"),sQuery(id+"F0.wireOp",EDGE,"E2958"),sQuery(id+"F0.wireOp",EDGE,"E2959"),sQuery(id+"F0.wireOp",EDGE,"E2960"),sQuery(id+"F0.wireOp",EDGE,"E2961"),sQuery(id+"F0.wireOp",EDGE,"E2962"),sQuery(id+"F0.wireOp",EDGE,"E2963"),sQuery(id+"F0.wireOp",EDGE,"E2964"),sQuery(id+"F0.wireOp",EDGE,"E2965"),sQuery(id+"F0.wireOp",EDGE,"E2966"),sQuery(id+"F0.wireOp",EDGE,"E2967"),sQuery(id+"F0.wireOp",EDGE,"E2968"),sQuery(id+"F0.wireOp",EDGE,"E2969"),sQuery(id+"F0.wireOp",EDGE,"E2970"),sQuery(id+"F0.wireOp",EDGE,"E2971"),sQuery(id+"F0.wireOp",EDGE,"E2972"),sQuery(id+"F0.wireOp",EDGE,"E2973"),sQuery(id+"F0.wireOp",EDGE,"E2974"),sQuery(id+"F0.wireOp",EDGE,"E2975"),sQuery(id+"F0.wireOp",EDGE,"E2976"),sQuery(id+"F0.wireOp",EDGE,"E2977"),sQuery(id+"F0.wireOp",EDGE,"E2978"),sQuery(id+"F0.wireOp",EDGE,"E2979"),sQuery(id+"F0.wireOp",EDGE,"E2980"),sQuery(id+"F0.wireOp",EDGE,"E2981"),sQuery(id+"F0.wireOp",EDGE,"E2982"),sQuery(id+"F0.wireOp",EDGE,"E2983"),sQuery(id+"F0.wireOp",EDGE,"E2984"),sQuery(id+"F0.wireOp",EDGE,"E2985"),sQuery(id+"F0.wireOp",EDGE,"E2986"),sQuery(id+"F0.wireOp",EDGE,"E2987"),sQuery(id+"F0.wireOp",EDGE,"E2988"),sQuery(id+"F0.wireOp",EDGE,"E2989"),sQuery(id+"F0.wireOp",EDGE,"E2990"),sQuery(id+"F0.wireOp",EDGE,"E2991"),sQuery(id+"F0.wireOp",EDGE,"E2992"),sQuery(id+"F0.wireOp",EDGE,"E2993"),sQuery(id+"F0.wireOp",EDGE,"E2994"),sQuery(id+"F0.wireOp",EDGE,"E2995"),sQuery(id+"F0.wireOp",EDGE,"E2996"),sQuery(id+"F0.wireOp",EDGE,"E2997"),sQuery(id+"F0.wireOp",EDGE,"E2998"),sQuery(id+"F0.wireOp",EDGE,"E2999"),sQuery(id+"F0.wireOp",EDGE,"E3000"),sQuery(id+"F0.wireOp",EDGE,"E3001"),sQuery(id+"F0.wireOp",EDGE,"E3002"),sQuery(id+"F0.wireOp",EDGE,"E3003"),sQuery(id+"F0.wireOp",EDGE,"E3004"),sQuery(id+"F0.wireOp",EDGE,"E3005"),sQuery(id+"F0.wireOp",EDGE,"E3006"),sQuery(id+"F0.wireOp",EDGE,"E3007"),sQuery(id+"F0.wireOp",EDGE,"E3008"),sQuery(id+"F0.wireOp",EDGE,"E3009"),sQuery(id+"F0.wireOp",EDGE,"E3010"),sQuery(id+"F0.wireOp",EDGE,"E3011"),sQuery(id+"F0.wireOp",EDGE,"E3012"),sQuery(id+"F0.wireOp",EDGE,"E3013"),sQuery(id+"F0.wireOp",EDGE,"E3014"),sQuery(id+"F0.wireOp",EDGE,"E3015"),sQuery(id+"F0.wireOp",EDGE,"E3016"),sQuery(id+"F0.wireOp",EDGE,"E3017"),sQuery(id+"F0.wireOp",EDGE,"E3018"),sQuery(id+"F0.wireOp",EDGE,"E3019"),sQuery(id+"F0.wireOp",EDGE,"E3020"),sQuery(id+"F0.wireOp",EDGE,"E3021"),sQuery(id+"F0.wireOp",EDGE,"E3022"),sQuery(id+"F0.wireOp",EDGE,"E3023"),sQuery(id+"F0.wireOp",EDGE,"E3024"),sQuery(id+"F0.wireOp",EDGE,"E3025"),sQuery(id+"F0.wireOp",EDGE,"E3026"),sQuery(id+"F0.wireOp",EDGE,"E3027"),sQuery(id+"F0.wireOp",EDGE,"E3028"),sQuery(id+"F0.wireOp",EDGE,"E3029"),sQuery(id+"F0.wireOp",EDGE,"E3030"),sQuery(id+"F0.wireOp",EDGE,"E3031"),sQuery(id+"F0.wireOp",EDGE,"E3032"),sQuery(id+"F0.wireOp",EDGE,"E3033"),sQuery(id+"F0.wireOp",EDGE,"E3034"),sQuery(id+"F0.wireOp",EDGE,"E3035"),sQuery(id+"F0.wireOp",EDGE,"E3036"),sQuery(id+"F0.wireOp",EDGE,"E3037"),sQuery(id+"F0.wireOp",EDGE,"E3038"),sQuery(id+"F0.wireOp",EDGE,"E3039"),sQuery(id+"F0.wireOp",EDGE,"E3040"),sQuery(id+"F0.wireOp",EDGE,"E3041"),sQuery(id+"F0.wireOp",EDGE,"E3042"),sQuery(id+"F0.wireOp",EDGE,"E3043"),sQuery(id+"F0.wireOp",EDGE,"E3044"),sQuery(id+"F0.wireOp",EDGE,"E3045"),sQuery(id+"F0.wireOp",EDGE,"E3046"),sQuery(id+"F0.wireOp",EDGE,"E3047"),sQuery(id+"F0.wireOp",EDGE,"E3048"),sQuery(id+"F0.wireOp",EDGE,"E3049"),sQuery(id+"F0.wireOp",EDGE,"E3050"),sQuery(id+"F0.wireOp",EDGE,"E3051"),sQuery(id+"F0.wireOp",EDGE,"E3052"),sQuery(id+"F0.wireOp",EDGE,"E3053"),sQuery(id+"F0.wireOp",EDGE,"E3054"),sQuery(id+"F0.wireOp",EDGE,"E3055"),sQuery(id+"F0.wireOp",EDGE,"E3056"),sQuery(id+"F0.wireOp",EDGE,"E3057"),sQuery(id+"F0.wireOp",EDGE,"E3058"),sQuery(id+"F0.wireOp",EDGE,"E3059"),sQuery(id+"F0.wireOp",EDGE,"E3060"),sQuery(id+"F0.wireOp",EDGE,"E3061"),sQuery(id+"F0.wireOp",EDGE,"E3062"),sQuery(id+"F0.wireOp",EDGE,"E3063"),sQuery(id+"F0.wireOp",EDGE,"E3064"),sQuery(id+"F0.wireOp",EDGE,"E3065"),sQuery(id+"F0.wireOp",EDGE,"E3066"),sQuery(id+"F0.wireOp",EDGE,"E3067"),sQuery(id+"F0.wireOp",EDGE,"E3068"),sQuery(id+"F0.wireOp",EDGE,"E3069"),sQuery(id+"F0.wireOp",EDGE,"E3070"),sQuery(id+"F0.wireOp",EDGE,"E3071"),sQuery(id+"F0.wireOp",EDGE,"E3072"),sQuery(id+"F0.wireOp",EDGE,"E3073"),sQuery(id+"F0.wireOp",EDGE,"E3074"),sQuery(id+"F0.wireOp",EDGE,"E3075"),sQuery(id+"F0.wireOp",EDGE,"E3076"),sQuery(id+"F0.wireOp",EDGE,"E3077"),sQuery(id+"F0.wireOp",EDGE,"E3078"),sQuery(id+"F0.wireOp",EDGE,"E3079"),sQuery(id+"F0.wireOp",EDGE,"E3080"),sQuery(id+"F0.wireOp",EDGE,"E3081"),sQuery(id+"F0.wireOp",EDGE,"E3082"),sQuery(id+"F0.wireOp",EDGE,"E3083"),sQuery(id+"F0.wireOp",EDGE,"E3084"),sQuery(id+"F0.wireOp",EDGE,"E3085"),sQuery(id+"F0.wireOp",EDGE,"E3086"),sQuery(id+"F0.wireOp",EDGE,"E3087"),sQuery(id+"F0.wireOp",EDGE,"E3088"),sQuery(id+"F0.wireOp",EDGE,"E3089"),sQuery(id+"F0.wireOp",EDGE,"E3090"),sQuery(id+"F0.wireOp",EDGE,"E3091"),sQuery(id+"F0.wireOp",EDGE,"E3092"),sQuery(id+"F0.wireOp",EDGE,"E3093"),sQuery(id+"F0.wireOp",EDGE,"E3094"),sQuery(id+"F0.wireOp",EDGE,"E3095"),sQuery(id+"F0.wireOp",EDGE,"E3096"),sQuery(id+"F0.wireOp",EDGE,"E3097"),sQuery(id+"F0.wireOp",EDGE,"E3098"),sQuery(id+"F0.wireOp",EDGE,"E3099"),sQuery(id+"F0.wireOp",EDGE,"E3100"),sQuery(id+"F0.wireOp",EDGE,"E3101"),sQuery(id+"F0.wireOp",EDGE,"E3102"),sQuery(id+"F0.wireOp",EDGE,"E3103"),sQuery(id+"F0.wireOp",EDGE,"E3104"),sQuery(id+"F0.wireOp",EDGE,"E3105"),sQuery(id+"F0.wireOp",EDGE,"E3106"),sQuery(id+"F0.wireOp",EDGE,"E3107"),sQuery(id+"F0.wireOp",EDGE,"E3108"),sQuery(id+"F0.wireOp",EDGE,"E3109"),sQuery(id+"F0.wireOp",EDGE,"E3110"),sQuery(id+"F0.wireOp",EDGE,"E3111"),sQuery(id+"F0.wireOp",EDGE,"E3112"),sQuery(id+"F0.wireOp",EDGE,"E3113"),sQuery(id+"F0.wireOp",EDGE,"E3114"),sQuery(id+"F0.wireOp",EDGE,"E3115"),sQuery(id+"F0.wireOp",EDGE,"E3116"),sQuery(id+"F0.wireOp",EDGE,"E3117"),sQuery(id+"F0.wireOp",EDGE,"E3118"),sQuery(id+"F0.wireOp",EDGE,"E3119"),sQuery(id+"F0.wireOp",EDGE,"E3120"),sQuery(id+"F0.wireOp",EDGE,"E3121"),sQuery(id+"F0.wireOp",EDGE,"E3122"),sQuery(id+"F0.wireOp",EDGE,"E3123"),sQuery(id+"F0.wireOp",EDGE,"E3124"),sQuery(id+"F0.wireOp",EDGE,"E3125"),sQuery(id+"F0.wireOp",EDGE,"E3126"),sQuery(id+"F0.wireOp",EDGE,"E3127"),sQuery(id+"F0.wireOp",EDGE,"E3128"),sQuery(id+"F0.wireOp",EDGE,"E3129"),sQuery(id+"F0.wireOp",EDGE,"E3130"),sQuery(id+"F0.wireOp",EDGE,"E3131"),sQuery(id+"F0.wireOp",EDGE,"E3132"),sQuery(id+"F0.wireOp",EDGE,"E3133"),sQuery(id+"F0.wireOp",EDGE,"E3134"),sQuery(id+"F0.wireOp",EDGE,"E3135"),sQuery(id+"F0.wireOp",EDGE,"E3136"),sQuery(id+"F0.wireOp",EDGE,"E3137"),sQuery(id+"F0.wireOp",EDGE,"E3138"),sQuery(id+"F0.wireOp",EDGE,"E3139"),sQuery(id+"F0.wireOp",EDGE,"E3140"),sQuery(id+"F0.wireOp",EDGE,"E3141"),sQuery(id+"F0.wireOp",EDGE,"E3142"),sQuery(id+"F0.wireOp",EDGE,"E3143"),sQuery(id+"F0.wireOp",EDGE,"E3144"),sQuery(id+"F0.wireOp",EDGE,"E3145"),sQuery(id+"F0.wireOp",EDGE,"E3146"),sQuery(id+"F0.wireOp",EDGE,"E3147"),sQuery(id+"F0.wireOp",EDGE,"E3148"),sQuery(id+"F0.wireOp",EDGE,"E3149"),sQuery(id+"F0.wireOp",EDGE,"E3150"),sQuery(id+"F0.wireOp",EDGE,"E3151"),sQuery(id+"F0.wireOp",EDGE,"E3152"),sQuery(id+"F0.wireOp",EDGE,"E3153"),sQuery(id+"F0.wireOp",EDGE,"E3154"),sQuery(id+"F0.wireOp",EDGE,"E3155"),sQuery(id+"F0.wireOp",EDGE,"E3156"),sQuery(id+"F0.wireOp",EDGE,"E3157"),sQuery(id+"F0.wireOp",EDGE,"E3158"),sQuery(id+"F0.wireOp",EDGE,"E3159"),sQuery(id+"F0.wireOp",EDGE,"E3160"),sQuery(id+"F0.wireOp",EDGE,"E3161"),sQuery(id+"F0.wireOp",EDGE,"E3162"),sQuery(id+"F0.wireOp",EDGE,"E3163"),sQuery(id+"F0.wireOp",EDGE,"E3164"),sQuery(id+"F0.wireOp",EDGE,"E3165"),sQuery(id+"F0.wireOp",EDGE,"E3166"),sQuery(id+"F0.wireOp",EDGE,"E3167"),sQuery(id+"F0.wireOp",EDGE,"E3168"),sQuery(id+"F0.wireOp",EDGE,"E3169"),sQuery(id+"F0.wireOp",EDGE,"E3170"),sQuery(id+"F0.wireOp",EDGE,"E3171"),sQuery(id+"F0.wireOp",EDGE,"E3172"),sQuery(id+"F0.wireOp",EDGE,"E3173"),sQuery(id+"F0.wireOp",EDGE,"E3174"),sQuery(id+"F0.wireOp",EDGE,"E3175"),sQuery(id+"F0.wireOp",EDGE,"E3176"),sQuery(id+"F0.wireOp",EDGE,"E3177"),sQuery(id+"F0.wireOp",EDGE,"E3178"),sQuery(id+"F0.wireOp",EDGE,"E3179"),sQuery(id+"F0.wireOp",EDGE,"E3180"),sQuery(id+"F0.wireOp",EDGE,"E3181"),sQuery(id+"F0.wireOp",EDGE,"E3182"),sQuery(id+"F0.wireOp",EDGE,"E3183"),sQuery(id+"F0.wireOp",EDGE,"E3184"),sQuery(id+"F0.wireOp",EDGE,"E3185"),sQuery(id+"F0.wireOp",EDGE,"E3186"),sQuery(id+"F0.wireOp",EDGE,"E3187"),sQuery(id+"F0.wireOp",EDGE,"E3188"),sQuery(id+"F0.wireOp",EDGE,"E3189"),sQuery(id+"F0.wireOp",EDGE,"E3190"),sQuery(id+"F0.wireOp",EDGE,"E3191"),sQuery(id+"F0.wireOp",EDGE,"E3192"),sQuery(id+"F0.wireOp",EDGE,"E3193"),sQuery(id+"F0.wireOp",EDGE,"E3194"),sQuery(id+"F0.wireOp",EDGE,"E3195"),sQuery(id+"F0.wireOp",EDGE,"E3196"),sQuery(id+"F0.wireOp",EDGE,"E3197"),sQuery(id+"F0.wireOp",EDGE,"E3198"),sQuery(id+"F0.wireOp",EDGE,"E3199"),sQuery(id+"F0.wireOp",EDGE,"E3200"),sQuery(id+"F0.wireOp",EDGE,"E3201"),sQuery(id+"F0.wireOp",EDGE,"E3202"),sQuery(id+"F0.wireOp",EDGE,"E3203"),sQuery(id+"F0.wireOp",EDGE,"E3204"),sQuery(id+"F0.wireOp",EDGE,"E3205"),sQuery(id+"F0.wireOp",EDGE,"E3206"),sQuery(id+"F0.wireOp",EDGE,"E3207"),sQuery(id+"F0.wireOp",EDGE,"E3208"),sQuery(id+"F0.wireOp",EDGE,"E3209"),sQuery(id+"F0.wireOp",EDGE,"E3210"),sQuery(id+"F0.wireOp",EDGE,"E3211"),sQuery(id+"F0.wireOp",EDGE,"E3212"),sQuery(id+"F0.wireOp",EDGE,"E3213"),sQuery(id+"F0.wireOp",EDGE,"E3214"),sQuery(id+"F0.wireOp",EDGE,"E3215"),sQuery(id+"F0.wireOp",EDGE,"E3216"),sQuery(id+"F0.wireOp",EDGE,"E3217"),sQuery(id+"F0.wireOp",EDGE,"E3218"),sQuery(id+"F0.wireOp",EDGE,"E3219"),sQuery(id+"F0.wireOp",EDGE,"E3220"),sQuery(id+"F0.wireOp",EDGE,"E3221"),sQuery(id+"F0.wireOp",EDGE,"E3222"),sQuery(id+"F0.wireOp",EDGE,"E3223"),sQuery(id+"F0.wireOp",EDGE,"E3224"),sQuery(id+"F0.wireOp",EDGE,"E3225"),sQuery(id+"F0.wireOp",EDGE,"E3226"),sQuery(id+"F0.wireOp",EDGE,"E3227"),sQuery(id+"F0.wireOp",EDGE,"E3228"),sQuery(id+"F0.wireOp",EDGE,"E3229"),sQuery(id+"F0.wireOp",EDGE,"E3230"),sQuery(id+"F0.wireOp",EDGE,"E3231"),sQuery(id+"F0.wireOp",EDGE,"E3232"),sQuery(id+"F0.wireOp",EDGE,"E3233"),sQuery(id+"F0.wireOp",EDGE,"E3234"),sQuery(id+"F0.wireOp",EDGE,"E3235"),sQuery(id+"F0.wireOp",EDGE,"E3236"),sQuery(id+"F0.wireOp",EDGE,"E3237"),sQuery(id+"F0.wireOp",EDGE,"E3238"),sQuery(id+"F0.wireOp",EDGE,"E3239"),sQuery(id+"F0.wireOp",EDGE,"E3240"),sQuery(id+"F0.wireOp",EDGE,"E3241"),sQuery(id+"F0.wireOp",EDGE,"E3242"),sQuery(id+"F0.wireOp",EDGE,"E3243"),sQuery(id+"F0.wireOp",EDGE,"E3244"),sQuery(id+"F0.wireOp",EDGE,"E3245"),sQuery(id+"F0.wireOp",EDGE,"E3246"),sQuery(id+"F0.wireOp",EDGE,"E3247"),sQuery(id+"F0.wireOp",EDGE,"E3248"),sQuery(id+"F0.wireOp",EDGE,"E3249"),sQuery(id+"F0.wireOp",EDGE,"E3250"),sQuery(id+"F0.wireOp",EDGE,"E3251"),sQuery(id+"F0.wireOp",EDGE,"E3252"),sQuery(id+"F0.wireOp",EDGE,"E3253"),sQuery(id+"F0.wireOp",EDGE,"E3254"),sQuery(id+"F0.wireOp",EDGE,"E3255"),sQuery(id+"F0.wireOp",EDGE,"E3256"),sQuery(id+"F0.wireOp",EDGE,"E3257"),sQuery(id+"F0.wireOp",EDGE,"E3258"),sQuery(id+"F0.wireOp",EDGE,"E3259"),sQuery(id+"F0.wireOp",EDGE,"E3260"),sQuery(id+"F0.wireOp",EDGE,"E3261"),sQuery(id+"F0.wireOp",EDGE,"E3262"),sQuery(id+"F0.wireOp",EDGE,"E3263"),sQuery(id+"F0.wireOp",EDGE,"E3264"),sQuery(id+"F0.wireOp",EDGE,"E3265"),sQuery(id+"F0.wireOp",EDGE,"E3266"),sQuery(id+"F0.wireOp",EDGE,"E3267"),sQuery(id+"F0.wireOp",EDGE,"E3268"),sQuery(id+"F0.wireOp",EDGE,"E3269"),sQuery(id+"F0.wireOp",EDGE,"E3270"),sQuery(id+"F0.wireOp",EDGE,"E3271"),sQuery(id+"F0.wireOp",EDGE,"E3272"),sQuery(id+"F0.wireOp",EDGE,"E3273"),sQuery(id+"F0.wireOp",EDGE,"E3274"),sQuery(id+"F0.wireOp",EDGE,"E3275"),sQuery(id+"F0.wireOp",EDGE,"E3276"),sQuery(id+"F0.wireOp",EDGE,"E3277"),sQuery(id+"F0.wireOp",EDGE,"E3278"),sQuery(id+"F0.wireOp",EDGE,"E3279"),sQuery(id+"F0.wireOp",EDGE,"E3280"),sQuery(id+"F0.wireOp",EDGE,"E3281"),sQuery(id+"F0.wireOp",EDGE,"E3282"),sQuery(id+"F0.wireOp",EDGE,"E3283"),sQuery(id+"F0.wireOp",EDGE,"E3284"),sQuery(id+"F0.wireOp",EDGE,"E3285"),sQuery(id+"F0.wireOp",EDGE,"E3286"),sQuery(id+"F0.wireOp",EDGE,"E3287"),sQuery(id+"F0.wireOp",EDGE,"E3288"),sQuery(id+"F0.wireOp",EDGE,"E3289"),sQuery(id+"F0.wireOp",EDGE,"E3290"),sQuery(id+"F0.wireOp",EDGE,"E3291"),sQuery(id+"F0.wireOp",EDGE,"E3292"),sQuery(id+"F0.wireOp",EDGE,"E3293"),sQuery(id+"F0.wireOp",EDGE,"E3294"),sQuery(id+"F0.wireOp",EDGE,"E3295"),sQuery(id+"F0.wireOp",EDGE,"E3296"),sQuery(id+"F0.wireOp",EDGE,"E3297"),sQuery(id+"F0.wireOp",EDGE,"E3298"),sQuery(id+"F0.wireOp",EDGE,"E3299"),sQuery(id+"F0.wireOp",EDGE,"E3300"),sQuery(id+"F0.wireOp",EDGE,"E3301"),sQuery(id+"F0.wireOp",EDGE,"E3302"),sQuery(id+"F0.wireOp",EDGE,"E3303"),sQuery(id+"F0.wireOp",EDGE,"E3304"),sQuery(id+"F0.wireOp",EDGE,"E3305"),sQuery(id+"F0.wireOp",EDGE,"E3306"),sQuery(id+"F0.wireOp",EDGE,"E3307"),sQuery(id+"F0.wireOp",EDGE,"E3308"),sQuery(id+"F0.wireOp",EDGE,"E3309"),sQuery(id+"F0.wireOp",EDGE,"E3310"),sQuery(id+"F0.wireOp",EDGE,"E3311"),sQuery(id+"F0.wireOp",EDGE,"E3312"),sQuery(id+"F0.wireOp",EDGE,"E3313"),sQuery(id+"F0.wireOp",EDGE,"E3314"),sQuery(id+"F0.wireOp",EDGE,"E3315"),sQuery(id+"F0.wireOp",EDGE,"E3316"),sQuery(id+"F0.wireOp",EDGE,"E3317"),sQuery(id+"F0.wireOp",EDGE,"E3318"),sQuery(id+"F0.wireOp",EDGE,"E3319"),sQuery(id+"F0.wireOp",EDGE,"E3320"),sQuery(id+"F0.wireOp",EDGE,"E3321"),sQuery(id+"F0.wireOp",EDGE,"E3322"),sQuery(id+"F0.wireOp",EDGE,"E3323"),sQuery(id+"F0.wireOp",EDGE,"E3324"),sQuery(id+"F0.wireOp",EDGE,"E3325"),sQuery(id+"F0.wireOp",EDGE,"E3326"),sQuery(id+"F0.wireOp",EDGE,"E3327"),sQuery(id+"F0.wireOp",EDGE,"E3328"),sQuery(id+"F0.wireOp",EDGE,"E3329"),sQuery(id+"F0.wireOp",EDGE,"E3330"),sQuery(id+"F0.wireOp",EDGE,"E3331"),sQuery(id+"F0.wireOp",EDGE,"E3332"),sQuery(id+"F0.wireOp",EDGE,"E3333"),sQuery(id+"F0.wireOp",EDGE,"E3334"),sQuery(id+"F0.wireOp",EDGE,"E3335"),sQuery(id+"F0.wireOp",EDGE,"E3336"),sQuery(id+"F0.wireOp",EDGE,"E3337"),sQuery(id+"F0.wireOp",EDGE,"E3338"),sQuery(id+"F0.wireOp",EDGE,"E3339"),sQuery(id+"F0.wireOp",EDGE,"E3340"),sQuery(id+"F0.wireOp",EDGE,"E3341"),sQuery(id+"F0.wireOp",EDGE,"E3342"),sQuery(id+"F0.wireOp",EDGE,"E3343"),sQuery(id+"F0.wireOp",EDGE,"E3344"),sQuery(id+"F0.wireOp",EDGE,"E3345"),sQuery(id+"F0.wireOp",EDGE,"E3346"),sQuery(id+"F0.wireOp",EDGE,"E3347"),sQuery(id+"F0.wireOp",EDGE,"E3348"),sQuery(id+"F0.wireOp",EDGE,"E3349"),sQuery(id+"F0.wireOp",EDGE,"E3350"),sQuery(id+"F0.wireOp",EDGE,"E3351"),sQuery(id+"F0.wireOp",EDGE,"E3352"),sQuery(id+"F0.wireOp",EDGE,"E3353"),sQuery(id+"F0.wireOp",EDGE,"E3354"),sQuery(id+"F0.wireOp",EDGE,"E3355"),sQuery(id+"F0.wireOp",EDGE,"E3356"),sQuery(id+"F0.wireOp",EDGE,"E3357"),sQuery(id+"F0.wireOp",EDGE,"E3358"),sQuery(id+"F0.wireOp",EDGE,"E3359"),sQuery(id+"F0.wireOp",EDGE,"E3360"),sQuery(id+"F0.wireOp",EDGE,"E3361"),sQuery(id+"F0.wireOp",EDGE,"E3362"),sQuery(id+"F0.wireOp",EDGE,"E3363"),sQuery(id+"F0.wireOp",EDGE,"E3364"),sQuery(id+"F0.wireOp",EDGE,"E3365"),sQuery(id+"F0.wireOp",EDGE,"E3366"),sQuery(id+"F0.wireOp",EDGE,"E3367"),sQuery(id+"F0.wireOp",EDGE,"E3368"),sQuery(id+"F0.wireOp",EDGE,"E3369"),sQuery(id+"F0.wireOp",EDGE,"E3370"),sQuery(id+"F0.wireOp",EDGE,"E3371"),sQuery(id+"F0.wireOp",EDGE,"E3372"),sQuery(id+"F0.wireOp",EDGE,"E3373"),sQuery(id+"F0.wireOp",EDGE,"E3374"),sQuery(id+"F0.wireOp",EDGE,"E3375"),sQuery(id+"F0.wireOp",EDGE,"E3376"),sQuery(id+"F0.wireOp",EDGE,"E3377"),sQuery(id+"F0.wireOp",EDGE,"E3378"),sQuery(id+"F0.wireOp",EDGE,"E3379"),sQuery(id+"F0.wireOp",EDGE,"E3380"),sQuery(id+"F0.wireOp",EDGE,"E3381"),sQuery(id+"F0.wireOp",EDGE,"E3382"),sQuery(id+"F0.wireOp",EDGE,"E3383"),sQuery(id+"F0.wireOp",EDGE,"E3384"),sQuery(id+"F0.wireOp",EDGE,"E3385"),sQuery(id+"F0.wireOp",EDGE,"E3386"),sQuery(id+"F0.wireOp",EDGE,"E3387"),sQuery(id+"F0.wireOp",EDGE,"E3388"),sQuery(id+"F0.wireOp",EDGE,"E3389"),sQuery(id+"F0.wireOp",EDGE,"E3390"),sQuery(id+"F0.wireOp",EDGE,"E3391"),sQuery(id+"F0.wireOp",EDGE,"E3392"),sQuery(id+"F0.wireOp",EDGE,"E3393"),sQuery(id+"F0.wireOp",EDGE,"E3394"),sQuery(id+"F0.wireOp",EDGE,"E3395"),sQuery(id+"F0.wireOp",EDGE,"E3396"),sQuery(id+"F0.wireOp",EDGE,"E3397"),sQuery(id+"F0.wireOp",EDGE,"E3398"),sQuery(id+"F0.wireOp",EDGE,"E3399"),sQuery(id+"F0.wireOp",EDGE,"E3400"),sQuery(id+"F0.wireOp",EDGE,"E3401"),sQuery(id+"F0.wireOp",EDGE,"E3402"),sQuery(id+"F0.wireOp",EDGE,"E3403"),sQuery(id+"F0.wireOp",EDGE,"E3404"),sQuery(id+"F0.wireOp",EDGE,"E3405"),sQuery(id+"F0.wireOp",EDGE,"E3406"),sQuery(id+"F0.wireOp",EDGE,"E3407"),sQuery(id+"F0.wireOp",EDGE,"E3408"),sQuery(id+"F0.wireOp",EDGE,"E3409"),sQuery(id+"F0.wireOp",EDGE,"E3410"),sQuery(id+"F0.wireOp",EDGE,"E3411"),sQuery(id+"F0.wireOp",EDGE,"E3412"),sQuery(id+"F0.wireOp",EDGE,"E3413"),sQuery(id+"F0.wireOp",EDGE,"E3414"),sQuery(id+"F0.wireOp",EDGE,"E3415"),sQuery(id+"F0.wireOp",EDGE,"E3416"),sQuery(id+"F0.wireOp",EDGE,"E3417"),sQuery(id+"F0.wireOp",EDGE,"E3418"),sQuery(id+"F0.wireOp",EDGE,"E3419"),sQuery(id+"F0.wireOp",EDGE,"E3420"),sQuery(id+"F0.wireOp",EDGE,"E3421"),sQuery(id+"F0.wireOp",EDGE,"E3422"),sQuery(id+"F0.wireOp",EDGE,"E3423"),sQuery(id+"F0.wireOp",EDGE,"E3424"),sQuery(id+"F0.wireOp",EDGE,"E3425"),sQuery(id+"F0.wireOp",EDGE,"E3426"),sQuery(id+"F0.wireOp",EDGE,"E3427"),sQuery(id+"F0.wireOp",EDGE,"E3428"),sQuery(id+"F0.wireOp",EDGE,"E3429"),sQuery(id+"F0.wireOp",EDGE,"E3430"),sQuery(id+"F0.wireOp",EDGE,"E3431"),sQuery(id+"F0.wireOp",EDGE,"E3432"),sQuery(id+"F0.wireOp",EDGE,"E3433"),sQuery(id+"F0.wireOp",EDGE,"E3434"),sQuery(id+"F0.wireOp",EDGE,"E3435"),sQuery(id+"F0.wireOp",EDGE,"E3436"),sQuery(id+"F0.wireOp",EDGE,"E3437"),sQuery(id+"F0.wireOp",EDGE,"E3438"),sQuery(id+"F0.wireOp",EDGE,"E3439"),sQuery(id+"F0.wireOp",EDGE,"E3440"),sQuery(id+"F0.wireOp",EDGE,"E3441"),sQuery(id+"F0.wireOp",EDGE,"E3442"),sQuery(id+"F0.wireOp",EDGE,"E3443"),sQuery(id+"F0.wireOp",EDGE,"E3444"),sQuery(id+"F0.wireOp",EDGE,"E3445"),sQuery(id+"F0.wireOp",EDGE,"E3446"),sQuery(id+"F0.wireOp",EDGE,"E3447"),sQuery(id+"F0.wireOp",EDGE,"E3448"),sQuery(id+"F0.wireOp",EDGE,"E3449"),sQuery(id+"F0.wireOp",EDGE,"E3450"),sQuery(id+"F0.wireOp",EDGE,"E3451"),sQuery(id+"F0.wireOp",EDGE,"E3452"),sQuery(id+"F0.wireOp",EDGE,"E3453"),sQuery(id+"F0.wireOp",EDGE,"E3454"),sQuery(id+"F0.wireOp",EDGE,"E3455"),sQuery(id+"F0.wireOp",EDGE,"E3456"),sQuery(id+"F0.wireOp",EDGE,"E3457"),sQuery(id+"F0.wireOp",EDGE,"E3458"),sQuery(id+"F0.wireOp",EDGE,"E3459"),sQuery(id+"F0.wireOp",EDGE,"E3460"),sQuery(id+"F0.wireOp",EDGE,"E3461"),sQuery(id+"F0.wireOp",EDGE,"E3462"),sQuery(id+"F0.wireOp",EDGE,"E3463"),sQuery(id+"F0.wireOp",EDGE,"E3464"),sQuery(id+"F0.wireOp",EDGE,"E3465"),sQuery(id+"F0.wireOp",EDGE,"E3466"),sQuery(id+"F0.wireOp",EDGE,"E3467"),sQuery(id+"F0.wireOp",EDGE,"E3468"),sQuery(id+"F0.wireOp",EDGE,"E3469"),sQuery(id+"F0.wireOp",EDGE,"E3470"),sQuery(id+"F0.wireOp",EDGE,"E3471"),sQuery(id+"F0.wireOp",EDGE,"E3472"),sQuery(id+"F0.wireOp",EDGE,"E3473"),sQuery(id+"F0.wireOp",EDGE,"E3474"),sQuery(id+"F0.wireOp",EDGE,"E3475"),sQuery(id+"F0.wireOp",EDGE,"E3476"),sQuery(id+"F0.wireOp",EDGE,"E3477"),sQuery(id+"F0.wireOp",EDGE,"E3478"),sQuery(id+"F0.wireOp",EDGE,"E3479"),sQuery(id+"F0.wireOp",EDGE,"E3480"),sQuery(id+"F0.wireOp",EDGE,"E3481"),sQuery(id+"F0.wireOp",EDGE,"E3482"),sQuery(id+"F0.wireOp",EDGE,"E3483"),sQuery(id+"F0.wireOp",EDGE,"E3484"),sQuery(id+"F0.wireOp",EDGE,"E3485"),sQuery(id+"F0.wireOp",EDGE,"E3486"),sQuery(id+"F0.wireOp",EDGE,"E3487"),sQuery(id+"F0.wireOp",EDGE,"E3488"),sQuery(id+"F0.wireOp",EDGE,"E3489"),sQuery(id+"F0.wireOp",EDGE,"E3490"),sQuery(id+"F0.wireOp",EDGE,"E3491"),sQuery(id+"F0.wireOp",EDGE,"E3492"),sQuery(id+"F0.wireOp",EDGE,"E3493"),sQuery(id+"F0.wireOp",EDGE,"E3494"),sQuery(id+"F0.wireOp",EDGE,"E3495"),sQuery(id+"F0.wireOp",EDGE,"E3496"),sQuery(id+"F0.wireOp",EDGE,"E3497"),sQuery(id+"F0.wireOp",EDGE,"E3498"),sQuery(id+"F0.wireOp",EDGE,"E3499"),sQuery(id+"F0.wireOp",EDGE,"E3500"),sQuery(id+"F0.wireOp",EDGE,"E3501"),sQuery(id+"F0.wireOp",EDGE,"E3502"),sQuery(id+"F0.wireOp",EDGE,"E3503"),sQuery(id+"F0.wireOp",EDGE,"E3504"),sQuery(id+"F0.wireOp",EDGE,"E3505"),sQuery(id+"F0.wireOp",EDGE,"E3506"),sQuery(id+"F0.wireOp",EDGE,"E3507"),sQuery(id+"F0.wireOp",EDGE,"E3508"),sQuery(id+"F0.wireOp",EDGE,"E3509"),sQuery(id+"F0.wireOp",EDGE,"E3510"),sQuery(id+"F0.wireOp",EDGE,"E3511"),sQuery(id+"F0.wireOp",EDGE,"E3512"),sQuery(id+"F0.wireOp",EDGE,"E3513"),sQuery(id+"F0.wireOp",EDGE,"E3514"),sQuery(id+"F0.wireOp",EDGE,"E3515"),sQuery(id+"F0.wireOp",EDGE,"E3516"),sQuery(id+"F0.wireOp",EDGE,"E3517"),sQuery(id+"F0.wireOp",EDGE,"E3518"),sQuery(id+"F0.wireOp",EDGE,"E3519"),sQuery(id+"F0.wireOp",EDGE,"E3520"),sQuery(id+"F0.wireOp",EDGE,"E3521"),sQuery(id+"F0.wireOp",EDGE,"E3522"),sQuery(id+"F0.wireOp",EDGE,"E3523"),sQuery(id+"F0.wireOp",EDGE,"E3524"),sQuery(id+"F0.wireOp",EDGE,"E3525"),sQuery(id+"F0.wireOp",EDGE,"E3526"),sQuery(id+"F0.wireOp",EDGE,"E3527"),sQuery(id+"F0.wireOp",EDGE,"E3528"),sQuery(id+"F0.wireOp",EDGE,"E3529"),sQuery(id+"F0.wireOp",EDGE,"E3530"),sQuery(id+"F0.wireOp",EDGE,"E3531"),sQuery(id+"F0.wireOp",EDGE,"E3532"),sQuery(id+"F0.wireOp",EDGE,"E3533"),sQuery(id+"F0.wireOp",EDGE,"E3534"),sQuery(id+"F0.wireOp",EDGE,"E3535"),sQuery(id+"F0.wireOp",EDGE,"E3536"),sQuery(id+"F0.wireOp",EDGE,"E3537"),sQuery(id+"F0.wireOp",EDGE,"E3538"),sQuery(id+"F0.wireOp",EDGE,"E3539"),sQuery(id+"F0.wireOp",EDGE,"E3540"),sQuery(id+"F0.wireOp",EDGE,"E3541"),sQuery(id+"F0.wireOp",EDGE,"E3542"),sQuery(id+"F0.wireOp",EDGE,"E3543"),sQuery(id+"F0.wireOp",EDGE,"E3544"),sQuery(id+"F0.wireOp",EDGE,"E3545"),sQuery(id+"F0.wireOp",EDGE,"E3546"),sQuery(id+"F0.wireOp",EDGE,"E3547"),sQuery(id+"F0.wireOp",EDGE,"E3548"),sQuery(id+"F0.wireOp",EDGE,"E3549"),sQuery(id+"F0.wireOp",EDGE,"E3550"),sQuery(id+"F0.wireOp",EDGE,"E3551"),sQuery(id+"F0.wireOp",EDGE,"E3552"),sQuery(id+"F0.wireOp",EDGE,"E3553"),sQuery(id+"F0.wireOp",EDGE,"E3554"),sQuery(id+"F0.wireOp",EDGE,"E3555"),sQuery(id+"F0.wireOp",EDGE,"E3556"),sQuery(id+"F0.wireOp",EDGE,"E3557"),sQuery(id+"F0.wireOp",EDGE,"E3558"),sQuery(id+"F0.wireOp",EDGE,"E3559"),sQuery(id+"F0.wireOp",EDGE,"E3560"),sQuery(id+"F0.wireOp",EDGE,"E3561"),sQuery(id+"F0.wireOp",EDGE,"E3562"),sQuery(id+"F0.wireOp",EDGE,"E3563"),sQuery(id+"F0.wireOp",EDGE,"E3564"),sQuery(id+"F0.wireOp",EDGE,"E3565"),sQuery(id+"F0.wireOp",EDGE,"E3566"),sQuery(id+"F0.wireOp",EDGE,"E3567"),sQuery(id+"F0.wireOp",EDGE,"E3568"),sQuery(id+"F0.wireOp",EDGE,"E3569"),sQuery(id+"F0.wireOp",EDGE,"E3570"),sQuery(id+"F0.wireOp",EDGE,"E3571"),sQuery(id+"F0.wireOp",EDGE,"E3572"),sQuery(id+"F0.wireOp",EDGE,"E3573"),sQuery(id+"F0.wireOp",EDGE,"E3574"),sQuery(id+"F0.wireOp",EDGE,"E3575"),sQuery(id+"F0.wireOp",EDGE,"E3576"),sQuery(id+"F0.wireOp",EDGE,"E3577"),sQuery(id+"F0.wireOp",EDGE,"E3578"),sQuery(id+"F0.wireOp",EDGE,"E3579"),sQuery(id+"F0.wireOp",EDGE,"E3580"),sQuery(id+"F0.wireOp",EDGE,"E3581"),sQuery(id+"F0.wireOp",EDGE,"E3582"),sQuery(id+"F0.wireOp",EDGE,"E3583"),sQuery(id+"F0.wireOp",EDGE,"E3584"),sQuery(id+"F0.wireOp",EDGE,"E3585"),sQuery(id+"F0.wireOp",EDGE,"E3586"),sQuery(id+"F0.wireOp",EDGE,"E3587"),sQuery(id+"F0.wireOp",EDGE,"E3588"),sQuery(id+"F0.wireOp",EDGE,"E3589"),sQuery(id+"F0.wireOp",EDGE,"E3590"),sQuery(id+"F0.wireOp",EDGE,"E3591"),sQuery(id+"F0.wireOp",EDGE,"E3592"),sQuery(id+"F0.wireOp",EDGE,"E3593"),sQuery(id+"F0.wireOp",EDGE,"E3594"),sQuery(id+"F0.wireOp",EDGE,"E3595"),sQuery(id+"F0.wireOp",EDGE,"E3596"),sQuery(id+"F0.wireOp",EDGE,"E3597"),sQuery(id+"F0.wireOp",EDGE,"E3598"),sQuery(id+"F0.wireOp",EDGE,"E3599"),sQuery(id+"F0.wireOp",EDGE,"E3600"),sQuery(id+"F0.wireOp",EDGE,"E3601"),sQuery(id+"F0.wireOp",EDGE,"E3602"),sQuery(id+"F0.wireOp",EDGE,"E3603"),sQuery(id+"F0.wireOp",EDGE,"E3604"),sQuery(id+"F0.wireOp",EDGE,"E3605"),sQuery(id+"F0.wireOp",EDGE,"E3606"),sQuery(id+"F0.wireOp",EDGE,"E3607"),sQuery(id+"F0.wireOp",EDGE,"E3608"),sQuery(id+"F0.wireOp",EDGE,"E3609"),sQuery(id+"F0.wireOp",EDGE,"E3610"),sQuery(id+"F0.wireOp",EDGE,"E3611"),sQuery(id+"F0.wireOp",EDGE,"E3612"),sQuery(id+"F0.wireOp",EDGE,"E3613"),sQuery(id+"F0.wireOp",EDGE,"E3614"),sQuery(id+"F0.wireOp",EDGE,"E3615"),sQuery(id+"F0.wireOp",EDGE,"E3616"),sQuery(id+"F0.wireOp",EDGE,"E3617"),sQuery(id+"F0.wireOp",EDGE,"E3618"),sQuery(id+"F0.wireOp",EDGE,"E3619"),sQuery(id+"F0.wireOp",EDGE,"E3620"),sQuery(id+"F0.wireOp",EDGE,"E3621"),sQuery(id+"F0.wireOp",EDGE,"E3622"),sQuery(id+"F0.wireOp",EDGE,"E3623"),sQuery(id+"F0.wireOp",EDGE,"E3624"),sQuery(id+"F0.wireOp",EDGE,"E3625"),sQuery(id+"F0.wireOp",EDGE,"E3626"),sQuery(id+"F0.wireOp",EDGE,"E3627"),sQuery(id+"F0.wireOp",EDGE,"E3628"),sQuery(id+"F0.wireOp",EDGE,"E3629"),sQuery(id+"F0.wireOp",EDGE,"E3630"),sQuery(id+"F0.wireOp",EDGE,"E3631"),sQuery(id+"F0.wireOp",EDGE,"E3632"),sQuery(id+"F0.wireOp",EDGE,"E3633"),sQuery(id+"F0.wireOp",EDGE,"E3634"),sQuery(id+"F0.wireOp",EDGE,"E3635"),sQuery(id+"F0.wireOp",EDGE,"E3636"),sQuery(id+"F0.wireOp",EDGE,"E3637"),sQuery(id+"F0.wireOp",EDGE,"E3638"),sQuery(id+"F0.wireOp",EDGE,"E3639"),sQuery(id+"F0.wireOp",EDGE,"E3640"),sQuery(id+"F0.wireOp",EDGE,"E3641"),sQuery(id+"F0.wireOp",EDGE,"E3642"),sQuery(id+"F0.wireOp",EDGE,"E3643"),sQuery(id+"F0.wireOp",EDGE,"E3644"),sQuery(id+"F0.wireOp",EDGE,"E3645"),sQuery(id+"F0.wireOp",EDGE,"E3646"),sQuery(id+"F0.wireOp",EDGE,"E3647"),sQuery(id+"F0.wireOp",EDGE,"E3648"),sQuery(id+"F0.wireOp",EDGE,"E3649"),sQuery(id+"F0.wireOp",EDGE,"E3650"),sQuery(id+"F0.wireOp",EDGE,"E3651"),sQuery(id+"F0.wireOp",EDGE,"E3652"),sQuery(id+"F0.wireOp",EDGE,"E3653"),sQuery(id+"F0.wireOp",EDGE,"E3654"),sQuery(id+"F0.wireOp",EDGE,"E3655"),sQuery(id+"F0.wireOp",EDGE,"E3656"),sQuery(id+"F0.wireOp",EDGE,"E3657"),sQuery(id+"F0.wireOp",EDGE,"E3658"),sQuery(id+"F0.wireOp",EDGE,"E3659"),sQuery(id+"F0.wireOp",EDGE,"E3660"),sQuery(id+"F0.wireOp",EDGE,"E3661"),sQuery(id+"F0.wireOp",EDGE,"E3662"),sQuery(id+"F0.wireOp",EDGE,"E3663"),sQuery(id+"F0.wireOp",EDGE,"E3664"),sQuery(id+"F0.wireOp",EDGE,"E3665"),sQuery(id+"F0.wireOp",EDGE,"E3666"),sQuery(id+"F0.wireOp",EDGE,"E3667"),sQuery(id+"F0.wireOp",EDGE,"E3668"),sQuery(id+"F0.wireOp",EDGE,"E3669"),sQuery(id+"F0.wireOp",EDGE,"E3670"),sQuery(id+"F0.wireOp",EDGE,"E3671"),sQuery(id+"F0.wireOp",EDGE,"E3672"),sQuery(id+"F0.wireOp",EDGE,"E3673"),sQuery(id+"F0.wireOp",EDGE,"E3674"),sQuery(id+"F0.wireOp",EDGE,"E3675"),sQuery(id+"F0.wireOp",EDGE,"E3676"),sQuery(id+"F0.wireOp",EDGE,"E3677"),sQuery(id+"F0.wireOp",EDGE,"E3678"),sQuery(id+"F0.wireOp",EDGE,"E3679"),sQuery(id+"F0.wireOp",EDGE,"E3680"),sQuery(id+"F0.wireOp",EDGE,"E3681"),sQuery(id+"F0.wireOp",EDGE,"E3682"),sQuery(id+"F0.wireOp",EDGE,"E3683"),sQuery(id+"F0.wireOp",EDGE,"E3684"),sQuery(id+"F0.wireOp",EDGE,"E3685"),sQuery(id+"F0.wireOp",EDGE,"E3686"),sQuery(id+"F0.wireOp",EDGE,"E3687"),sQuery(id+"F0.wireOp",EDGE,"E3688"),sQuery(id+"F0.wireOp",EDGE,"E3689"),sQuery(id+"F0.wireOp",EDGE,"E3690"),sQuery(id+"F0.wireOp",EDGE,"E3691"),sQuery(id+"F0.wireOp",EDGE,"E3692"),sQuery(id+"F0.wireOp",EDGE,"E3693"),sQuery(id+"F0.wireOp",EDGE,"E3694"),sQuery(id+"F0.wireOp",EDGE,"E3695"),sQuery(id+"F0.wireOp",EDGE,"E3696"),sQuery(id+"F0.wireOp",EDGE,"E3697"),sQuery(id+"F0.wireOp",EDGE,"E3698"),sQuery(id+"F0.wireOp",EDGE,"E3699"),sQuery(id+"F0.wireOp",EDGE,"E3700"),sQuery(id+"F0.wireOp",EDGE,"E3701"),sQuery(id+"F0.wireOp",EDGE,"E3702"),sQuery(id+"F0.wireOp",EDGE,"E3703"),sQuery(id+"F0.wireOp",EDGE,"E3704"),sQuery(id+"F0.wireOp",EDGE,"E3705"),sQuery(id+"F0.wireOp",EDGE,"E3706"),sQuery(id+"F0.wireOp",EDGE,"E3707"),sQuery(id+"F0.wireOp",EDGE,"E3708"),sQuery(id+"F0.wireOp",EDGE,"E3709"),sQuery(id+"F0.wireOp",EDGE,"E3710"),sQuery(id+"F0.wireOp",EDGE,"E3711"),sQuery(id+"F0.wireOp",EDGE,"E3712"),sQuery(id+"F0.wireOp",EDGE,"E3713"),sQuery(id+"F0.wireOp",EDGE,"E3714"),sQuery(id+"F0.wireOp",EDGE,"E3715"),sQuery(id+"F0.wireOp",EDGE,"E3716"),sQuery(id+"F0.wireOp",EDGE,"E3717"),sQuery(id+"F0.wireOp",EDGE,"E3718"),sQuery(id+"F0.wireOp",EDGE,"E3719"),sQuery(id+"F0.wireOp",EDGE,"E3720"),sQuery(id+"F0.wireOp",EDGE,"E3721"),sQuery(id+"F0.wireOp",EDGE,"E3722"),sQuery(id+"F0.wireOp",EDGE,"E3723"),sQuery(id+"F0.wireOp",EDGE,"E3724"),sQuery(id+"F0.wireOp",EDGE,"E3725"),sQuery(id+"F0.wireOp",EDGE,"E3726"),sQuery(id+"F0.wireOp",EDGE,"E3727"),sQuery(id+"F0.wireOp",EDGE,"E3728"),sQuery(id+"F0.wireOp",EDGE,"E3729"),sQuery(id+"F0.wireOp",EDGE,"E3730"),sQuery(id+"F0.wireOp",EDGE,"E3731"),sQuery(id+"F0.wireOp",EDGE,"E3732"),sQuery(id+"F0.wireOp",EDGE,"E3733"),sQuery(id+"F0.wireOp",EDGE,"E3734"),sQuery(id+"F0.wireOp",EDGE,"E3735"),sQuery(id+"F0.wireOp",EDGE,"E3736"),sQuery(id+"F0.wireOp",EDGE,"E3737"),sQuery(id+"F0.wireOp",EDGE,"E3738"),sQuery(id+"F0.wireOp",EDGE,"E3739"),sQuery(id+"F0.wireOp",EDGE,"E3740"),sQuery(id+"F0.wireOp",EDGE,"E3741"),sQuery(id+"F0.wireOp",EDGE,"E3742"),sQuery(id+"F0.wireOp",EDGE,"E3743"),sQuery(id+"F0.wireOp",EDGE,"E3744"),sQuery(id+"F0.wireOp",EDGE,"E3745"),sQuery(id+"F0.wireOp",EDGE,"E3746"),sQuery(id+"F0.wireOp",EDGE,"E3747"),sQuery(id+"F0.wireOp",EDGE,"E3748"),sQuery(id+"F0.wireOp",EDGE,"E3749"),sQuery(id+"F0.wireOp",EDGE,"E3750"),sQuery(id+"F0.wireOp",EDGE,"E3751"),sQuery(id+"F0.wireOp",EDGE,"E3752"),sQuery(id+"F0.wireOp",EDGE,"E3753"),sQuery(id+"F0.wireOp",EDGE,"E3754"),sQuery(id+"F0.wireOp",EDGE,"E3755"),sQuery(id+"F0.wireOp",EDGE,"E3756"),sQuery(id+"F0.wireOp",EDGE,"E3757"),sQuery(id+"F0.wireOp",EDGE,"E3758"),sQuery(id+"F0.wireOp",EDGE,"E3759"),sQuery(id+"F0.wireOp",EDGE,"E3760"),sQuery(id+"F0.wireOp",EDGE,"E3761"),sQuery(id+"F0.wireOp",EDGE,"E3762"),sQuery(id+"F0.wireOp",EDGE,"E3763"),sQuery(id+"F0.wireOp",EDGE,"E3764"),sQuery(id+"F0.wireOp",EDGE,"E3765"),sQuery(id+"F0.wireOp",EDGE,"E3766"),sQuery(id+"F0.wireOp",EDGE,"E3767"),sQuery(id+"F0.wireOp",EDGE,"E3768"),sQuery(id+"F0.wireOp",EDGE,"E3769"),sQuery(id+"F0.wireOp",EDGE,"E3770"),sQuery(id+"F0.wireOp",EDGE,"E3771"),sQuery(id+"F0.wireOp",EDGE,"E3772"),sQuery(id+"F0.wireOp",EDGE,"E3773"),sQuery(id+"F0.wireOp",EDGE,"E3774"),sQuery(id+"F0.wireOp",EDGE,"E3775"),sQuery(id+"F0.wireOp",EDGE,"E3776"),sQuery(id+"F0.wireOp",EDGE,"E3777"),sQuery(id+"F0.wireOp",EDGE,"E3778"),sQuery(id+"F0.wireOp",EDGE,"E3779"),sQuery(id+"F0.wireOp",EDGE,"E3780"),sQuery(id+"F0.wireOp",EDGE,"E3781"),sQuery(id+"F0.wireOp",EDGE,"E3782"),sQuery(id+"F0.wireOp",EDGE,"E3783"),sQuery(id+"F0.wireOp",EDGE,"E3784"),sQuery(id+"F0.wireOp",EDGE,"E3785"),sQuery(id+"F0.wireOp",EDGE,"E3786"),sQuery(id+"F0.wireOp",EDGE,"E3787"),sQuery(id+"F0.wireOp",EDGE,"E3788"),sQuery(id+"F0.wireOp",EDGE,"E3789"),sQuery(id+"F0.wireOp",EDGE,"E3790"),sQuery(id+"F0.wireOp",EDGE,"E3791"),sQuery(id+"F0.wireOp",EDGE,"E3792"),sQuery(id+"F0.wireOp",EDGE,"E3793"),sQuery(id+"F0.wireOp",EDGE,"E3794"),sQuery(id+"F0.wireOp",EDGE,"E3795"),sQuery(id+"F0.wireOp",EDGE,"E3796"),sQuery(id+"F0.wireOp",EDGE,"E3797"),sQuery(id+"F0.wireOp",EDGE,"E3798"),sQuery(id+"F0.wireOp",EDGE,"E3799"),sQuery(id+"F0.wireOp",EDGE,"E3800"),sQuery(id+"F0.wireOp",EDGE,"E3801"),sQuery(id+"F0.wireOp",EDGE,"E3802"),sQuery(id+"F0.wireOp",EDGE,"E3803"),sQuery(id+"F0.wireOp",EDGE,"E3804"),sQuery(id+"F0.wireOp",EDGE,"E3805"),sQuery(id+"F0.wireOp",EDGE,"E3806"),sQuery(id+"F0.wireOp",EDGE,"E3807"),sQuery(id+"F0.wireOp",EDGE,"E3808"),sQuery(id+"F0.wireOp",EDGE,"E3809"),sQuery(id+"F0.wireOp",EDGE,"E3810"),sQuery(id+"F0.wireOp",EDGE,"E3811"),sQuery(id+"F0.wireOp",EDGE,"E3812"),sQuery(id+"F0.wireOp",EDGE,"E3813"),sQuery(id+"F0.wireOp",EDGE,"E3814"),sQuery(id+"F0.wireOp",EDGE,"E3815"),sQuery(id+"F0.wireOp",EDGE,"E3816"),sQuery(id+"F0.wireOp",EDGE,"E3817"),sQuery(id+"F0.wireOp",EDGE,"E3818"),sQuery(id+"F0.wireOp",EDGE,"E3819"),sQuery(id+"F0.wireOp",EDGE,"E3820"),sQuery(id+"F0.wireOp",EDGE,"E3821"),sQuery(id+"F0.wireOp",EDGE,"E3822"),sQuery(id+"F0.wireOp",EDGE,"E3823"),sQuery(id+"F0.wireOp",EDGE,"E3824"),sQuery(id+"F0.wireOp",EDGE,"E3825"),sQuery(id+"F0.wireOp",EDGE,"E3826"),sQuery(id+"F0.wireOp",EDGE,"E3827"),sQuery(id+"F0.wireOp",EDGE,"E3828"),sQuery(id+"F0.wireOp",EDGE,"E3829"),sQuery(id+"F0.wireOp",EDGE,"E3830"),sQuery(id+"F0.wireOp",EDGE,"E3831"),sQuery(id+"F0.wireOp",EDGE,"E3832"),sQuery(id+"F0.wireOp",EDGE,"E3833"),sQuery(id+"F0.wireOp",EDGE,"E3834"),sQuery(id+"F0.wireOp",EDGE,"E3835"),sQuery(id+"F0.wireOp",EDGE,"E3836"),sQuery(id+"F0.wireOp",EDGE,"E3837"),sQuery(id+"F0.wireOp",EDGE,"E3838"),sQuery(id+"F0.wireOp",EDGE,"E3839"),sQuery(id+"F0.wireOp",EDGE,"E3840"),sQuery(id+"F0.wireOp",EDGE,"E3841"),sQuery(id+"F0.wireOp",EDGE,"E3842"),sQuery(id+"F0.wireOp",EDGE,"E3843"),sQuery(id+"F0.wireOp",EDGE,"E3844"),sQuery(id+"F0.wireOp",EDGE,"E3845"),sQuery(id+"F0.wireOp",EDGE,"E3846"),sQuery(id+"F0.wireOp",EDGE,"E3847"),sQuery(id+"F0.wireOp",EDGE,"E3848"),sQuery(id+"F0.wireOp",EDGE,"E3849"),sQuery(id+"F0.wireOp",EDGE,"E3850"),sQuery(id+"F0.wireOp",EDGE,"E3851"),sQuery(id+"F0.wireOp",EDGE,"E3852"),sQuery(id+"F0.wireOp",EDGE,"E3853"),sQuery(id+"F0.wireOp",EDGE,"E3854"),sQuery(id+"F0.wireOp",EDGE,"E3855"),sQuery(id+"F0.wireOp",EDGE,"E3856"),sQuery(id+"F0.wireOp",EDGE,"E3857"),sQuery(id+"F0.wireOp",EDGE,"E3858"),sQuery(id+"F0.wireOp",EDGE,"E3859"),sQuery(id+"F0.wireOp",EDGE,"E3860"),sQuery(id+"F0.wireOp",EDGE,"E3861"),sQuery(id+"F0.wireOp",EDGE,"E3862"),sQuery(id+"F0.wireOp",EDGE,"E3863"),sQuery(id+"F0.wireOp",EDGE,"E3864"),sQuery(id+"F0.wireOp",EDGE,"E3865"),sQuery(id+"F0.wireOp",EDGE,"E3866"),sQuery(id+"F0.wireOp",EDGE,"E3867"),sQuery(id+"F0.wireOp",EDGE,"E3868"),sQuery(id+"F0.wireOp",EDGE,"E3869"),sQuery(id+"F0.wireOp",EDGE,"E3870"),sQuery(id+"F0.wireOp",EDGE,"E3871"),sQuery(id+"F0.wireOp",EDGE,"E3872"),sQuery(id+"F0.wireOp",EDGE,"E3873"),sQuery(id+"F0.wireOp",EDGE,"E3874"),sQuery(id+"F0.wireOp",EDGE,"E3875"),sQuery(id+"F0.wireOp",EDGE,"E3876"),sQuery(id+"F0.wireOp",EDGE,"E3877"),sQuery(id+"F0.wireOp",EDGE,"E3878"),sQuery(id+"F0.wireOp",EDGE,"E3879"),sQuery(id+"F0.wireOp",EDGE,"E3880"),sQuery(id+"F0.wireOp",EDGE,"E3881"),sQuery(id+"F0.wireOp",EDGE,"E3882"),sQuery(id+"F0.wireOp",EDGE,"E3883"),sQuery(id+"F0.wireOp",EDGE,"E3884"),sQuery(id+"F0.wireOp",EDGE,"E3885"),sQuery(id+"F0.wireOp",EDGE,"E3886"),sQuery(id+"F0.wireOp",EDGE,"E3887"),sQuery(id+"F0.wireOp",EDGE,"E3888"),sQuery(id+"F0.wireOp",EDGE,"E3889"),sQuery(id+"F0.wireOp",EDGE,"E3890"),sQuery(id+"F0.wireOp",EDGE,"E3891"),sQuery(id+"F0.wireOp",EDGE,"E3892"),sQuery(id+"F0.wireOp",EDGE,"E3893"),sQuery(id+"F0.wireOp",EDGE,"E3894"),sQuery(id+"F0.wireOp",EDGE,"E3895"),sQuery(id+"F0.wireOp",EDGE,"E3896"),sQuery(id+"F0.wireOp",EDGE,"E3897"),sQuery(id+"F0.wireOp",EDGE,"E3898"),sQuery(id+"F0.wireOp",EDGE,"E3899"),sQuery(id+"F0.wireOp",EDGE,"E3900"),sQuery(id+"F0.wireOp",EDGE,"E3901"),sQuery(id+"F0.wireOp",EDGE,"E3902"),sQuery(id+"F0.wireOp",EDGE,"E3903"),sQuery(id+"F0.wireOp",EDGE,"E3904"),sQuery(id+"F0.wireOp",EDGE,"E3905"),sQuery(id+"F0.wireOp",EDGE,"E3906"),sQuery(id+"F0.wireOp",EDGE,"E3907"),sQuery(id+"F0.wireOp",EDGE,"E3908"),sQuery(id+"F0.wireOp",EDGE,"E3909"),sQuery(id+"F0.wireOp",EDGE,"E3910"),sQuery(id+"F0.wireOp",EDGE,"E3911"),sQuery(id+"F0.wireOp",EDGE,"E3912"),sQuery(id+"F0.wireOp",EDGE,"E3913"),sQuery(id+"F0.wireOp",EDGE,"E3914"),sQuery(id+"F0.wireOp",EDGE,"E3915"),sQuery(id+"F0.wireOp",EDGE,"E3916"),sQuery(id+"F0.wireOp",EDGE,"E3917"),sQuery(id+"F0.wireOp",EDGE,"E3918"),sQuery(id+"F0.wireOp",EDGE,"E3919"),sQuery(id+"F0.wireOp",EDGE,"E3920"),sQuery(id+"F0.wireOp",EDGE,"E3921"),sQuery(id+"F0.wireOp",EDGE,"E3922"),sQuery(id+"F0.wireOp",EDGE,"E3923"),sQuery(id+"F0.wireOp",EDGE,"E3924"),sQuery(id+"F0.wireOp",EDGE,"E3925"),sQuery(id+"F0.wireOp",EDGE,"E3926"),sQuery(id+"F0.wireOp",EDGE,"E3927"),sQuery(id+"F0.wireOp",EDGE,"E3928"),sQuery(id+"F0.wireOp",EDGE,"E3929"),sQuery(id+"F0.wireOp",EDGE,"E3930"),sQuery(id+"F0.wireOp",EDGE,"E3931"),sQuery(id+"F0.wireOp",EDGE,"E3932"),sQuery(id+"F0.wireOp",EDGE,"E3933"),sQuery(id+"F0.wireOp",EDGE,"E3934"),sQuery(id+"F0.wireOp",EDGE,"E3935"),sQuery(id+"F0.wireOp",EDGE,"E3936"),sQuery(id+"F0.wireOp",EDGE,"E3937"),sQuery(id+"F0.wireOp",EDGE,"E3938"),sQuery(id+"F0.wireOp",EDGE,"E3939"),sQuery(id+"F0.wireOp",EDGE,"E3940"),sQuery(id+"F0.wireOp",EDGE,"E3941"),sQuery(id+"F0.wireOp",EDGE,"E3942"),sQuery(id+"F0.wireOp",EDGE,"E3943"),sQuery(id+"F0.wireOp",EDGE,"E3944"),sQuery(id+"F0.wireOp",EDGE,"E3945"),sQuery(id+"F0.wireOp",EDGE,"E3946"),sQuery(id+"F0.wireOp",EDGE,"E3947"),sQuery(id+"F0.wireOp",EDGE,"E3948"),sQuery(id+"F0.wireOp",EDGE,"E3949"),sQuery(id+"F0.wireOp",EDGE,"E3950"),sQuery(id+"F0.wireOp",EDGE,"E3951"),sQuery(id+"F0.wireOp",EDGE,"E3952"),sQuery(id+"F0.wireOp",EDGE,"E3953"),sQuery(id+"F0.wireOp",EDGE,"E3954"),sQuery(id+"F0.wireOp",EDGE,"E3955"),sQuery(id+"F0.wireOp",EDGE,"E3956"),sQuery(id+"F0.wireOp",EDGE,"E3957"),sQuery(id+"F0.wireOp",EDGE,"E3958"),sQuery(id+"F0.wireOp",EDGE,"E3959"),sQuery(id+"F0.wireOp",EDGE,"E3960"),sQuery(id+"F0.wireOp",EDGE,"E3961"),sQuery(id+"F0.wireOp",EDGE,"E3962"),sQuery(id+"F0.wireOp",EDGE,"E3963"),sQuery(id+"F0.wireOp",EDGE,"E3964"),sQuery(id+"F0.wireOp",EDGE,"E3965"),sQuery(id+"F0.wireOp",EDGE,"E3966"),sQuery(id+"F0.wireOp",EDGE,"E3967"),sQuery(id+"F0.wireOp",EDGE,"E3968"),sQuery(id+"F0.wireOp",EDGE,"E3969"),sQuery(id+"F0.wireOp",EDGE,"E3970"),sQuery(id+"F0.wireOp",EDGE,"E3971"),sQuery(id+"F0.wireOp",EDGE,"E3972"),sQuery(id+"F0.wireOp",EDGE,"E3973"),sQuery(id+"F0.wireOp",EDGE,"E3974"),sQuery(id+"F0.wireOp",EDGE,"E3975"),sQuery(id+"F0.wireOp",EDGE,"E3976"),sQuery(id+"F0.wireOp",EDGE,"E3977"),sQuery(id+"F0.wireOp",EDGE,"E3978"),sQuery(id+"F0.wireOp",EDGE,"E3979"),sQuery(id+"F0.wireOp",EDGE,"E3980"),sQuery(id+"F0.wireOp",EDGE,"E3981"),sQuery(id+"F0.wireOp",EDGE,"E3982"),sQuery(id+"F0.wireOp",EDGE,"E3983"),sQuery(id+"F0.wireOp",EDGE,"E3984"),sQuery(id+"F0.wireOp",EDGE,"E3985"),sQuery(id+"F0.wireOp",EDGE,"E3986"),sQuery(id+"F0.wireOp",EDGE,"E3987"),sQuery(id+"F0.wireOp",EDGE,"E3988"),sQuery(id+"F0.wireOp",EDGE,"E3989"),sQuery(id+"F0.wireOp",EDGE,"E3990"),sQuery(id+"F0.wireOp",EDGE,"E3991"),sQuery(id+"F0.wireOp",EDGE,"E3992"),sQuery(id+"F0.wireOp",EDGE,"E3993"),sQuery(id+"F0.wireOp",EDGE,"E3994"),sQuery(id+"F0.wireOp",EDGE,"E3995"),sQuery(id+"F0.wireOp",EDGE,"E3996"),sQuery(id+"F0.wireOp",EDGE,"E3997"),sQuery(id+"F0.wireOp",EDGE,"E3998"),sQuery(id+"F0.wireOp",EDGE,"E3999"),sQuery(id+"F0.wireOp",EDGE,"E4000"),sQuery(id+"F0.wireOp",EDGE,"E4001"),sQuery(id+"F0.wireOp",EDGE,"E4002"),sQuery(id+"F0.wireOp",EDGE,"E4003"),sQuery(id+"F0.wireOp",EDGE,"E4004"),sQuery(id+"F0.wireOp",EDGE,"E4005"),sQuery(id+"F0.wireOp",EDGE,"E4006"),sQuery(id+"F0.wireOp",EDGE,"E4007"),sQuery(id+"F0.wireOp",EDGE,"E4008"),sQuery(id+"F0.wireOp",EDGE,"E4009"),sQuery(id+"F0.wireOp",EDGE,"E4010"),sQuery(id+"F0.wireOp",EDGE,"E4011"),sQuery(id+"F0.wireOp",EDGE,"E4012"),sQuery(id+"F0.wireOp",EDGE,"E4013"),sQuery(id+"F0.wireOp",EDGE,"E4014"),sQuery(id+"F0.wireOp",EDGE,"E4015"),sQuery(id+"F0.wireOp",EDGE,"E4016"),sQuery(id+"F0.wireOp",EDGE,"E4017"),sQuery(id+"F0.wireOp",EDGE,"E4018"),sQuery(id+"F0.wireOp",EDGE,"E4019"),sQuery(id+"F0.wireOp",EDGE,"E4020"),sQuery(id+"F0.wireOp",EDGE,"E4021"),sQuery(id+"F0.wireOp",EDGE,"E4022"),sQuery(id+"F0.wireOp",EDGE,"E4023"),sQuery(id+"F0.wireOp",EDGE,"E4024"),sQuery(id+"F0.wireOp",EDGE,"E4025"),sQuery(id+"F0.wireOp",EDGE,"E4026"),sQuery(id+"F0.wireOp",EDGE,"E4027"),sQuery(id+"F0.wireOp",EDGE,"E4028"),sQuery(id+"F0.wireOp",EDGE,"E4029"),sQuery(id+"F0.wireOp",EDGE,"E4030"),sQuery(id+"F0.wireOp",EDGE,"E4031"),sQuery(id+"F0.wireOp",EDGE,"E4032"),sQuery(id+"F0.wireOp",EDGE,"E4033"),sQuery(id+"F0.wireOp",EDGE,"E4034"),sQuery(id+"F0.wireOp",EDGE,"E4035"),sQuery(id+"F0.wireOp",EDGE,"E4036"),sQuery(id+"F0.wireOp",EDGE,"E4037"),sQuery(id+"F0.wireOp",EDGE,"E4038"),sQuery(id+"F0.wireOp",EDGE,"E4039"),sQuery(id+"F0.wireOp",EDGE,"E4040"),sQuery(id+"F0.wireOp",EDGE,"E4041"),sQuery(id+"F0.wireOp",EDGE,"E4042"),sQuery(id+"F0.wireOp",EDGE,"E4043"),sQuery(id+"F0.wireOp",EDGE,"E4044"),sQuery(id+"F0.wireOp",EDGE,"E4045"),sQuery(id+"F0.wireOp",EDGE,"E4046"),sQuery(id+"F0.wireOp",EDGE,"E4047"),sQuery(id+"F0.wireOp",EDGE,"E4048"),sQuery(id+"F0.wireOp",EDGE,"E4049"),sQuery(id+"F0.wireOp",EDGE,"E4050"),sQuery(id+"F0.wireOp",EDGE,"E4051"),sQuery(id+"F0.wireOp",EDGE,"E4052"),sQuery(id+"F0.wireOp",EDGE,"E4053"),sQuery(id+"F0.wireOp",EDGE,"E4054"),sQuery(id+"F0.wireOp",EDGE,"E4055"),sQuery(id+"F0.wireOp",EDGE,"E4056"),sQuery(id+"F0.wireOp",EDGE,"E4057"),sQuery(id+"F0.wireOp",EDGE,"E4058"),sQuery(id+"F0.wireOp",EDGE,"E4059"),sQuery(id+"F0.wireOp",EDGE,"E4060"),sQuery(id+"F0.wireOp",EDGE,"E4061"),sQuery(id+"F0.wireOp",EDGE,"E4062"),sQuery(id+"F0.wireOp",EDGE,"E4063"),sQuery(id+"F0.wireOp",EDGE,"E4064"),sQuery(id+"F0.wireOp",EDGE,"E4065"),sQuery(id+"F0.wireOp",EDGE,"E4066"),sQuery(id+"F0.wireOp",EDGE,"E4067"),sQuery(id+"F0.wireOp",EDGE,"E4068"),sQuery(id+"F0.wireOp",EDGE,"E4069"),sQuery(id+"F0.wireOp",EDGE,"E4070"),sQuery(id+"F0.wireOp",EDGE,"E4071"),sQuery(id+"F0.wireOp",EDGE,"E4072"),sQuery(id+"F0.wireOp",EDGE,"E4073"),sQuery(id+"F0.wireOp",EDGE,"E4074"),sQuery(id+"F0.wireOp",EDGE,"E4075"),sQuery(id+"F0.wireOp",EDGE,"E4076"),sQuery(id+"F0.wireOp",EDGE,"E4077"),sQuery(id+"F0.wireOp",EDGE,"E4078"),sQuery(id+"F0.wireOp",EDGE,"E4079"),sQuery(id+"F0.wireOp",EDGE,"E4080"),sQuery(id+"F0.wireOp",EDGE,"E4081"),sQuery(id+"F0.wireOp",EDGE,"E4082"),sQuery(id+"F0.wireOp",EDGE,"E4083"),sQuery(id+"F0.wireOp",EDGE,"E4084"),sQuery(id+"F0.wireOp",EDGE,"E4085"),sQuery(id+"F0.wireOp",EDGE,"E4086"),sQuery(id+"F0.wireOp",EDGE,"E4087"),sQuery(id+"F0.wireOp",EDGE,"E4088"),sQuery(id+"F0.wireOp",EDGE,"E4089"),sQuery(id+"F0.wireOp",EDGE,"E4090"),sQuery(id+"F0.wireOp",EDGE,"E4091"),sQuery(id+"F0.wireOp",EDGE,"E4092"),sQuery(id+"F0.wireOp",EDGE,"E4093"),sQuery(id+"F0.wireOp",EDGE,"E4094"),sQuery(id+"F0.wireOp",EDGE,"E4095"),sQuery(id+"F0.wireOp",EDGE,"E4096"),sQuery(id+"F0.wireOp",EDGE,"E4097"),sQuery(id+"F0.wireOp",EDGE,"E4098"),sQuery(id+"F0.wireOp",EDGE,"E4099"),sQuery(id+"F0.wireOp",EDGE,"E4100"),sQuery(id+"F0.wireOp",EDGE,"E4101"),sQuery(id+"F0.wireOp",EDGE,"E4102"),sQuery(id+"F0.wireOp",EDGE,"E4103"),sQuery(id+"F0.wireOp",EDGE,"E4104"),sQuery(id+"F0.wireOp",EDGE,"E4105"),sQuery(id+"F0.wireOp",EDGE,"E4106"),sQuery(id+"F0.wireOp",EDGE,"E4107"),sQuery(id+"F0.wireOp",EDGE,"E4108"),sQuery(id+"F0.wireOp",EDGE,"E4109"),sQuery(id+"F0.wireOp",EDGE,"E4110"),sQuery(id+"F0.wireOp",EDGE,"E4111"),sQuery(id+"F0.wireOp",EDGE,"E4112"),sQuery(id+"F0.wireOp",EDGE,"E4113"),sQuery(id+"F0.wireOp",EDGE,"E4114"),sQuery(id+"F0.wireOp",EDGE,"E4115"),sQuery(id+"F0.wireOp",EDGE,"E4116"),sQuery(id+"F0.wireOp",EDGE,"E4117"),sQuery(id+"F0.wireOp",EDGE,"E4118"),sQuery(id+"F0.wireOp",EDGE,"E4119"),sQuery(id+"F0.wireOp",EDGE,"E4120"),sQuery(id+"F0.wireOp",EDGE,"E4121"),sQuery(id+"F0.wireOp",EDGE,"E4122"),sQuery(id+"F0.wireOp",EDGE,"E4123"),sQuery(id+"F0.wireOp",EDGE,"E4124"),sQuery(id+"F0.wireOp",EDGE,"E4125"),sQuery(id+"F0.wireOp",EDGE,"E4126"),sQuery(id+"F0.wireOp",EDGE,"E4127"),sQuery(id+"F0.wireOp",EDGE,"E4128"),sQuery(id+"F0.wireOp",EDGE,"E4129"),sQuery(id+"F0.wireOp",EDGE,"E4130"),sQuery(id+"F0.wireOp",EDGE,"E4131"),sQuery(id+"F0.wireOp",EDGE,"E4132"),sQuery(id+"F0.wireOp",EDGE,"E4133"),sQuery(id+"F0.wireOp",EDGE,"E4134"),sQuery(id+"F0.wireOp",EDGE,"E4135"),sQuery(id+"F0.wireOp",EDGE,"E4136"),sQuery(id+"F0.wireOp",EDGE,"E4137"),sQuery(id+"F0.wireOp",EDGE,"E4138"),sQuery(id+"F0.wireOp",EDGE,"E4139"),sQuery(id+"F0.wireOp",EDGE,"E4140"),sQuery(id+"F0.wireOp",EDGE,"E4141"),sQuery(id+"F0.wireOp",EDGE,"E4142"),sQuery(id+"F0.wireOp",EDGE,"E4143"),sQuery(id+"F0.wireOp",EDGE,"E4144"),sQuery(id+"F0.wireOp",EDGE,"E4145"),sQuery(id+"F0.wireOp",EDGE,"E4146"),sQuery(id+"F0.wireOp",EDGE,"E4147"),sQuery(id+"F0.wireOp",EDGE,"E4148"),sQuery(id+"F0.wireOp",EDGE,"E4149"),sQuery(id+"F0.wireOp",EDGE,"E4150"),sQuery(id+"F0.wireOp",EDGE,"E4151"),sQuery(id+"F0.wireOp",EDGE,"E4152"),sQuery(id+"F0.wireOp",EDGE,"E4153"),sQuery(id+"F0.wireOp",EDGE,"E4154"),sQuery(id+"F0.wireOp",EDGE,"E4155"),sQuery(id+"F0.wireOp",EDGE,"E4156"),sQuery(id+"F0.wireOp",EDGE,"E4157"),sQuery(id+"F0.wireOp",EDGE,"E4158"),sQuery(id+"F0.wireOp",EDGE,"E4159"),sQuery(id+"F0.wireOp",EDGE,"E4160"),sQuery(id+"F0.wireOp",EDGE,"E4161"),sQuery(id+"F0.wireOp",EDGE,"E4162"),sQuery(id+"F0.wireOp",EDGE,"E4163"),sQuery(id+"F0.wireOp",EDGE,"E4164"),sQuery(id+"F0.wireOp",EDGE,"E4165"),sQuery(id+"F0.wireOp",EDGE,"E4166"),sQuery(id+"F0.wireOp",EDGE,"E4167"),sQuery(id+"F0.wireOp",EDGE,"E4168"),sQuery(id+"F0.wireOp",EDGE,"E4169"),sQuery(id+"F0.wireOp",EDGE,"E4170"),sQuery(id+"F0.wireOp",EDGE,"E4171"),sQuery(id+"F0.wireOp",EDGE,"E4172"),sQuery(id+"F0.wireOp",EDGE,"E4173"),sQuery(id+"F0.wireOp",EDGE,"E4174"),sQuery(id+"F0.wireOp",EDGE,"E4175"),sQuery(id+"F0.wireOp",EDGE,"E4176"),sQuery(id+"F0.wireOp",EDGE,"E4177"),sQuery(id+"F0.wireOp",EDGE,"E4178"),sQuery(id+"F0.wireOp",EDGE,"E4179"),sQuery(id+"F0.wireOp",EDGE,"E4180"),sQuery(id+"F0.wireOp",EDGE,"E4181"),sQuery(id+"F0.wireOp",EDGE,"E4182"),sQuery(id+"F0.wireOp",EDGE,"E4183"),sQuery(id+"F0.wireOp",EDGE,"E4184"),sQuery(id+"F0.wireOp",EDGE,"E4185"),sQuery(id+"F0.wireOp",EDGE,"E4186"),sQuery(id+"F0.wireOp",EDGE,"E4187"),sQuery(id+"F0.wireOp",EDGE,"E4188"),sQuery(id+"F0.wireOp",EDGE,"E4189"),sQuery(id+"F0.wireOp",EDGE,"E4190"),sQuery(id+"F0.wireOp",EDGE,"E4191"),sQuery(id+"F0.wireOp",EDGE,"E4192"),sQuery(id+"F0.wireOp",EDGE,"E4193"),sQuery(id+"F0.wireOp",EDGE,"E4194"),sQuery(id+"F0.wireOp",EDGE,"E4195"),sQuery(id+"F0.wireOp",EDGE,"E4196"),sQuery(id+"F0.wireOp",EDGE,"E4197"),sQuery(id+"F0.wireOp",EDGE,"E4198"),sQuery(id+"F0.wireOp",EDGE,"E4199"),sQuery(id+"F0.wireOp",EDGE,"E4200"),sQuery(id+"F0.wireOp",EDGE,"E4201"),sQuery(id+"F0.wireOp",EDGE,"E4202"),sQuery(id+"F0.wireOp",EDGE,"E4203"),sQuery(id+"F0.wireOp",EDGE,"E4204"),sQuery(id+"F0.wireOp",EDGE,"E4205"),sQuery(id+"F0.wireOp",EDGE,"E4206"),sQuery(id+"F0.wireOp",EDGE,"E4207"),sQuery(id+"F0.wireOp",EDGE,"E4208"),sQuery(id+"F0.wireOp",EDGE,"E4209"),sQuery(id+"F0.wireOp",EDGE,"E4210"),sQuery(id+"F0.wireOp",EDGE,"E4211"),sQuery(id+"F0.wireOp",EDGE,"E4212"),sQuery(id+"F0.wireOp",EDGE,"E4213"),sQuery(id+"F0.wireOp",EDGE,"E4214"),sQuery(id+"F0.wireOp",EDGE,"E4215"),sQuery(id+"F0.wireOp",EDGE,"E4216"),sQuery(id+"F0.wireOp",EDGE,"E4217"),sQuery(id+"F0.wireOp",EDGE,"E4218"),sQuery(id+"F0.wireOp",EDGE,"E4219"),sQuery(id+"F0.wireOp",EDGE,"E4220"),sQuery(id+"F0.wireOp",EDGE,"E4221"),sQuery(id+"F0.wireOp",EDGE,"E4222"),sQuery(id+"F0.wireOp",EDGE,"E4223"),sQuery(id+"F0.wireOp",EDGE,"E4224"),sQuery(id+"F0.wireOp",EDGE,"E4225"),sQuery(id+"F0.wireOp",EDGE,"E4226"),sQuery(id+"F0.wireOp",EDGE,"E4227"),sQuery(id+"F0.wireOp",EDGE,"E4228"),sQuery(id+"F0.wireOp",EDGE,"E4229"),sQuery(id+"F0.wireOp",EDGE,"E4230"),sQuery(id+"F0.wireOp",EDGE,"E4231"),sQuery(id+"F0.wireOp",EDGE,"E4232"),sQuery(id+"F0.wireOp",EDGE,"E4233"),sQuery(id+"F0.wireOp",EDGE,"E4234"),sQuery(id+"F0.wireOp",EDGE,"E4235"),sQuery(id+"F0.wireOp",EDGE,"E4236"),sQuery(id+"F0.wireOp",EDGE,"E4237"),sQuery(id+"F0.wireOp",EDGE,"E4238"),sQuery(id+"F0.wireOp",EDGE,"E4239"),sQuery(id+"F0.wireOp",EDGE,"E4240"),sQuery(id+"F0.wireOp",EDGE,"E4241"),sQuery(id+"F0.wireOp",EDGE,"E4242"),sQuery(id+"F0.wireOp",EDGE,"E4243"),sQuery(id+"F0.wireOp",EDGE,"E4244"),sQuery(id+"F0.wireOp",EDGE,"E4245"),sQuery(id+"F0.wireOp",EDGE,"E4246"),sQuery(id+"F0.wireOp",EDGE,"E4247"),sQuery(id+"F0.wireOp",EDGE,"E4248"),sQuery(id+"F0.wireOp",EDGE,"E4249"),sQuery(id+"F0.wireOp",EDGE,"E4250"),sQuery(id+"F0.wireOp",EDGE,"E4251"),sQuery(id+"F0.wireOp",EDGE,"E4252"),sQuery(id+"F0.wireOp",EDGE,"E4253"),sQuery(id+"F0.wireOp",EDGE,"E4254"),sQuery(id+"F0.wireOp",EDGE,"E4255"),sQuery(id+"F0.wireOp",EDGE,"E4256"),sQuery(id+"F0.wireOp",EDGE,"E4257"),sQuery(id+"F0.wireOp",EDGE,"E4258"),sQuery(id+"F0.wireOp",EDGE,"E4259"),sQuery(id+"F0.wireOp",EDGE,"E4260"),sQuery(id+"F0.wireOp",EDGE,"E4261"),sQuery(id+"F0.wireOp",EDGE,"E4262"),sQuery(id+"F0.wireOp",EDGE,"E4263"),sQuery(id+"F0.wireOp",EDGE,"E4264"),sQuery(id+"F0.wireOp",EDGE,"E4265"),sQuery(id+"F0.wireOp",EDGE,"E4266"),sQuery(id+"F0.wireOp",EDGE,"E4267"),sQuery(id+"F0.wireOp",EDGE,"E4268"),sQuery(id+"F0.wireOp",EDGE,"E4269"),sQuery(id+"F0.wireOp",EDGE,"E4270"),sQuery(id+"F0.wireOp",EDGE,"E4271"),sQuery(id+"F0.wireOp",EDGE,"E4272"),sQuery(id+"F0.wireOp",EDGE,"E4273"),sQuery(id+"F0.wireOp",EDGE,"E4274"),sQuery(id+"F0.wireOp",EDGE,"E4275"),sQuery(id+"F0.wireOp",EDGE,"E4276"),sQuery(id+"F0.wireOp",EDGE,"E4277"),sQuery(id+"F0.wireOp",EDGE,"E4278"),sQuery(id+"F0.wireOp",EDGE,"E4279"),sQuery(id+"F0.wireOp",EDGE,"E4280"),sQuery(id+"F0.wireOp",EDGE,"E4281"),sQuery(id+"F0.wireOp",EDGE,"E4282"),sQuery(id+"F0.wireOp",EDGE,"E4283"),sQuery(id+"F0.wireOp",EDGE,"E4284"),sQuery(id+"F0.wireOp",EDGE,"E4285"),sQuery(id+"F0.wireOp",EDGE,"E4286"),sQuery(id+"F0.wireOp",EDGE,"E4287"),sQuery(id+"F0.wireOp",EDGE,"E4288"),sQuery(id+"F0.wireOp",EDGE,"E4289"),sQuery(id+"F0.wireOp",EDGE,"E4290"),sQuery(id+"F0.wireOp",EDGE,"E4291"),sQuery(id+"F0.wireOp",EDGE,"E4292"),sQuery(id+"F0.wireOp",EDGE,"E4293"),sQuery(id+"F0.wireOp",EDGE,"E4294"),sQuery(id+"F0.wireOp",EDGE,"E4295"),sQuery(id+"F0.wireOp",EDGE,"E4296"),sQuery(id+"F0.wireOp",EDGE,"E4297"),sQuery(id+"F0.wireOp",EDGE,"E4298"),sQuery(id+"F0.wireOp",EDGE,"E4299"),sQuery(id+"F0.wireOp",EDGE,"E4300"),sQuery(id+"F0.wireOp",EDGE,"E4301"),sQuery(id+"F0.wireOp",EDGE,"E4302"),sQuery(id+"F0.wireOp",EDGE,"E4303"),sQuery(id+"F0.wireOp",EDGE,"E4304"),sQuery(id+"F0.wireOp",EDGE,"E4305"),sQuery(id+"F0.wireOp",EDGE,"E4306"),sQuery(id+"F0.wireOp",EDGE,"E4307"),sQuery(id+"F0.wireOp",EDGE,"E4308"),sQuery(id+"F0.wireOp",EDGE,"E4309"),sQuery(id+"F0.wireOp",EDGE,"E4310"),sQuery(id+"F0.wireOp",EDGE,"E4311"),sQuery(id+"F0.wireOp",EDGE,"E4312"),sQuery(id+"F0.wireOp",EDGE,"E4313"),sQuery(id+"F0.wireOp",EDGE,"E4314"),sQuery(id+"F0.wireOp",EDGE,"E4315"),sQuery(id+"F0.wireOp",EDGE,"E4316"),sQuery(id+"F0.wireOp",EDGE,"E4317"),sQuery(id+"F0.wireOp",EDGE,"E4318"),sQuery(id+"F0.wireOp",EDGE,"E4319"),sQuery(id+"F0.wireOp",EDGE,"E4320"),sQuery(id+"F0.wireOp",EDGE,"E4321"),sQuery(id+"F0.wireOp",EDGE,"E4322"),sQuery(id+"F0.wireOp",EDGE,"E4323"),sQuery(id+"F0.wireOp",EDGE,"E4324"),sQuery(id+"F0.wireOp",EDGE,"E4325"),sQuery(id+"F0.wireOp",EDGE,"E4326"),sQuery(id+"F0.wireOp",EDGE,"E4327"),sQuery(id+"F0.wireOp",EDGE,"E4328"),sQuery(id+"F0.wireOp",EDGE,"E4329"),sQuery(id+"F0.wireOp",EDGE,"E4330"),sQuery(id+"F0.wireOp",EDGE,"E4331"),sQuery(id+"F0.wireOp",EDGE,"E4332"),sQuery(id+"F0.wireOp",EDGE,"E4333"),sQuery(id+"F0.wireOp",EDGE,"E4334"),sQuery(id+"F0.wireOp",EDGE,"E4335"),sQuery(id+"F0.wireOp",EDGE,"E4336"),sQuery(id+"F0.wireOp",EDGE,"E4337"),sQuery(id+"F0.wireOp",EDGE,"E4338"),sQuery(id+"F0.wireOp",EDGE,"E4339"),sQuery(id+"F0.wireOp",EDGE,"E4340"),sQuery(id+"F0.wireOp",EDGE,"E4341"),sQuery(id+"F0.wireOp",EDGE,"E4342"),sQuery(id+"F0.wireOp",EDGE,"E4343"),sQuery(id+"F0.wireOp",EDGE,"E4344"),sQuery(id+"F0.wireOp",EDGE,"E4345"),sQuery(id+"F0.wireOp",EDGE,"E4346"),sQuery(id+"F0.wireOp",EDGE,"E4347"),sQuery(id+"F0.wireOp",EDGE,"E4348"),sQuery(id+"F0.wireOp",EDGE,"E4349"),sQuery(id+"F0.wireOp",EDGE,"E4350"),sQuery(id+"F0.wireOp",EDGE,"E4351"),sQuery(id+"F0.wireOp",EDGE,"E4352"),sQuery(id+"F0.wireOp",EDGE,"E4353"),sQuery(id+"F0.wireOp",EDGE,"E4354"),sQuery(id+"F0.wireOp",EDGE,"E4355"),sQuery(id+"F0.wireOp",EDGE,"E4356"),sQuery(id+"F0.wireOp",EDGE,"E4357"),sQuery(id+"F0.wireOp",EDGE,"E4358"),sQuery(id+"F0.wireOp",EDGE,"E4359"),sQuery(id+"F0.wireOp",EDGE,"E4360"),sQuery(id+"F0.wireOp",EDGE,"E4361"),sQuery(id+"F0.wireOp",EDGE,"E4362"),sQuery(id+"F0.wireOp",EDGE,"E4363"),sQuery(id+"F0.wireOp",EDGE,"E4364"),sQuery(id+"F0.wireOp",EDGE,"E4365"),sQuery(id+"F0.wireOp",EDGE,"E4366"),sQuery(id+"F0.wireOp",EDGE,"E4367"),sQuery(id+"F0.wireOp",EDGE,"E4368"),sQuery(id+"F0.wireOp",EDGE,"E4369"),sQuery(id+"F0.wireOp",EDGE,"E4370"),sQuery(id+"F0.wireOp",EDGE,"E4371"),sQuery(id+"F0.wireOp",EDGE,"E4372"),sQuery(id+"F0.wireOp",EDGE,"E4373"),sQuery(id+"F0.wireOp",EDGE,"E4374"),sQuery(id+"F0.wireOp",EDGE,"E4375"),sQuery(id+"F0.wireOp",EDGE,"E4376"),sQuery(id+"F0.wireOp",EDGE,"E4377"),sQuery(id+"F0.wireOp",EDGE,"E4378"),sQuery(id+"F0.wireOp",EDGE,"E4379"),sQuery(id+"F0.wireOp",EDGE,"E4380"),sQuery(id+"F0.wireOp",EDGE,"E4381"),sQuery(id+"F0.wireOp",EDGE,"E4382"),sQuery(id+"F0.wireOp",EDGE,"E4383"),sQuery(id+"F0.wireOp",EDGE,"E4384"),sQuery(id+"F0.wireOp",EDGE,"E4385"),sQuery(id+"F0.wireOp",EDGE,"E4386"),sQuery(id+"F0.wireOp",EDGE,"E4387"),sQuery(id+"F0.wireOp",EDGE,"E4388"),sQuery(id+"F0.wireOp",EDGE,"E4389"),sQuery(id+"F0.wireOp",EDGE,"E4390"),sQuery(id+"F0.wireOp",EDGE,"E4391"),sQuery(id+"F0.wireOp",EDGE,"E4392"),sQuery(id+"F0.wireOp",EDGE,"E4393"),sQuery(id+"F0.wireOp",EDGE,"E4394"),sQuery(id+"F0.wireOp",EDGE,"E4395"),sQuery(id+"F0.wireOp",EDGE,"E4396"),sQuery(id+"F0.wireOp",EDGE,"E4397"),sQuery(id+"F0.wireOp",EDGE,"E4398"),sQuery(id+"F0.wireOp",EDGE,"E4399"),sQuery(id+"F0.wireOp",EDGE,"E4400"),sQuery(id+"F0.wireOp",EDGE,"E4401"),sQuery(id+"F0.wireOp",EDGE,"E4402"),sQuery(id+"F0.wireOp",EDGE,"E4403"),sQuery(id+"F0.wireOp",EDGE,"E4404"),sQuery(id+"F0.wireOp",EDGE,"E4405"),sQuery(id+"F0.wireOp",EDGE,"E4406"),sQuery(id+"F0.wireOp",EDGE,"E4407"),sQuery(id+"F0.wireOp",EDGE,"E4408"),sQuery(id+"F0.wireOp",EDGE,"E4409"),sQuery(id+"F0.wireOp",EDGE,"E4410"),sQuery(id+"F0.wireOp",EDGE,"E4411"),sQuery(id+"F0.wireOp",EDGE,"E4412"),sQuery(id+"F0.wireOp",EDGE,"E4413"),sQuery(id+"F0.wireOp",EDGE,"E4414"),sQuery(id+"F0.wireOp",EDGE,"E4415"),sQuery(id+"F0.wireOp",EDGE,"E4416"),sQuery(id+"F0.wireOp",EDGE,"E4417"),sQuery(id+"F0.wireOp",EDGE,"E4418"),sQuery(id+"F0.wireOp",EDGE,"E4419"),sQuery(id+"F0.wireOp",EDGE,"E4420"),sQuery(id+"F0.wireOp",EDGE,"E4421"),sQuery(id+"F0.wireOp",EDGE,"E4422"),sQuery(id+"F0.wireOp",EDGE,"E4423"),sQuery(id+"F0.wireOp",EDGE,"E4424"),sQuery(id+"F0.wireOp",EDGE,"E4425"),sQuery(id+"F0.wireOp",EDGE,"E4426"),sQuery(id+"F0.wireOp",EDGE,"E4427"),sQuery(id+"F0.wireOp",EDGE,"E4428"),sQuery(id+"F0.wireOp",EDGE,"E4429"),sQuery(id+"F0.wireOp",EDGE,"E4430"),sQuery(id+"F0.wireOp",EDGE,"E4431"),sQuery(id+"F0.wireOp",EDGE,"E4432"),sQuery(id+"F0.wireOp",EDGE,"E4433"),sQuery(id+"F0.wireOp",EDGE,"E4434"),sQuery(id+"F0.wireOp",EDGE,"E4435"),sQuery(id+"F0.wireOp",EDGE,"E4436"),sQuery(id+"F0.wireOp",EDGE,"E4437"),sQuery(id+"F0.wireOp",EDGE,"E4438"),sQuery(id+"F0.wireOp",EDGE,"E4439"),sQuery(id+"F0.wireOp",EDGE,"E4440"),sQuery(id+"F0.wireOp",EDGE,"E4441"),sQuery(id+"F0.wireOp",EDGE,"E4442"),sQuery(id+"F0.wireOp",EDGE,"E4443"),sQuery(id+"F0.wireOp",EDGE,"E4444"),sQuery(id+"F0.wireOp",EDGE,"E4445"),sQuery(id+"F0.wireOp",EDGE,"E4446"),sQuery(id+"F0.wireOp",EDGE,"E4447"),sQuery(id+"F0.wireOp",EDGE,"E4448"),sQuery(id+"F0.wireOp",EDGE,"E4449"),sQuery(id+"F0.wireOp",EDGE,"E4450"),sQuery(id+"F0.wireOp",EDGE,"E4451"),sQuery(id+"F0.wireOp",EDGE,"E4452"),sQuery(id+"F0.wireOp",EDGE,"E4453"),sQuery(id+"F0.wireOp",EDGE,"E4454"),sQuery(id+"F0.wireOp",EDGE,"E4455"),sQuery(id+"F0.wireOp",EDGE,"E4456"),sQuery(id+"F0.wireOp",EDGE,"E4457"),sQuery(id+"F0.wireOp",EDGE,"E4458"),sQuery(id+"F0.wireOp",EDGE,"E4459"),sQuery(id+"F0.wireOp",EDGE,"E4460"),sQuery(id+"F0.wireOp",EDGE,"E4461"),sQuery(id+"F0.wireOp",EDGE,"E4462"),sQuery(id+"F0.wireOp",EDGE,"E4463"),sQuery(id+"F0.wireOp",EDGE,"E4464"),sQuery(id+"F0.wireOp",EDGE,"E4465"),sQuery(id+"F0.wireOp",EDGE,"E4466"),sQuery(id+"F0.wireOp",EDGE,"E4467"),sQuery(id+"F0.wireOp",EDGE,"E4468"),sQuery(id+"F0.wireOp",EDGE,"E4469"),sQuery(id+"F0.wireOp",EDGE,"E4470"),sQuery(id+"F0.wireOp",EDGE,"E4471"),sQuery(id+"F0.wireOp",EDGE,"E4472"),sQuery(id+"F0.wireOp",EDGE,"E4473"),sQuery(id+"F0.wireOp",EDGE,"E4474"),sQuery(id+"F0.wireOp",EDGE,"E4475"),sQuery(id+"F0.wireOp",EDGE,"E4476"),sQuery(id+"F0.wireOp",EDGE,"E4477"),sQuery(id+"F0.wireOp",EDGE,"E4478"),sQuery(id+"F0.wireOp",EDGE,"E4479"),sQuery(id+"F0.wireOp",EDGE,"E4480"),sQuery(id+"F0.wireOp",EDGE,"E4481"),sQuery(id+"F0.wireOp",EDGE,"E4482"),sQuery(id+"F0.wireOp",EDGE,"E4483"),sQuery(id+"F0.wireOp",EDGE,"E4484"),sQuery(id+"F0.wireOp",EDGE,"E4485"),sQuery(id+"F0.wireOp",EDGE,"E4486"),sQuery(id+"F0.wireOp",EDGE,"E4487"),sQuery(id+"F0.wireOp",EDGE,"E4488"),sQuery(id+"F0.wireOp",EDGE,"E4489"),sQuery(id+"F0.wireOp",EDGE,"E4490"),sQuery(id+"F0.wireOp",EDGE,"E4491"),sQuery(id+"F0.wireOp",EDGE,"E4492"),sQuery(id+"F0.wireOp",EDGE,"E4493"),sQuery(id+"F0.wireOp",EDGE,"E4494"),sQuery(id+"F0.wireOp",EDGE,"E4495"),sQuery(id+"F0.wireOp",EDGE,"E4496"),sQuery(id+"F0.wireOp",EDGE,"E4497"),sQuery(id+"F0.wireOp",EDGE,"E4498"),sQuery(id+"F0.wireOp",EDGE,"E4499"),sQuery(id+"F0.wireOp",EDGE,"E4500"),sQuery(id+"F0.wireOp",EDGE,"E4501"),sQuery(id+"F0.wireOp",EDGE,"E4502"),sQuery(id+"F0.wireOp",EDGE,"E4503"),sQuery(id+"F0.wireOp",EDGE,"E4504"),sQuery(id+"F0.wireOp",EDGE,"E4505"),sQuery(id+"F0.wireOp",EDGE,"E4506"),sQuery(id+"F0.wireOp",EDGE,"E4507"),sQuery(id+"F0.wireOp",EDGE,"E4508"),sQuery(id+"F0.wireOp",EDGE,"E4509"),sQuery(id+"F0.wireOp",EDGE,"E4510"),sQuery(id+"F0.wireOp",EDGE,"E4511"),sQuery(id+"F0.wireOp",EDGE,"E4512"),sQuery(id+"F0.wireOp",EDGE,"E4513"),sQuery(id+"F0.wireOp",EDGE,"E4514"),sQuery(id+"F0.wireOp",EDGE,"E4515"),sQuery(id+"F0.wireOp",EDGE,"E4516"),sQuery(id+"F0.wireOp",EDGE,"E4517"),sQuery(id+"F0.wireOp",EDGE,"E4518"),sQuery(id+"F0.wireOp",EDGE,"E4519"),sQuery(id+"F0.wireOp",EDGE,"E4520"),sQuery(id+"F0.wireOp",EDGE,"E4521"),sQuery(id+"F0.wireOp",EDGE,"E4522"),sQuery(id+"F0.wireOp",EDGE,"E4523"),sQuery(id+"F0.wireOp",EDGE,"E4524"),sQuery(id+"F0.wireOp",EDGE,"E4525"),sQuery(id+"F0.wireOp",EDGE,"E4526"),sQuery(id+"F0.wireOp",EDGE,"E4527"),sQuery(id+"F0.wireOp",EDGE,"E4528"),sQuery(id+"F0.wireOp",EDGE,"E4529"),sQuery(id+"F0.wireOp",EDGE,"E4530"),sQuery(id+"F0.wireOp",EDGE,"E4531"),sQuery(id+"F0.wireOp",EDGE,"E4532"),sQuery(id+"F0.wireOp",EDGE,"E4533"),sQuery(id+"F0.wireOp",EDGE,"E4534"),sQuery(id+"F0.wireOp",EDGE,"E4535"),sQuery(id+"F0.wireOp",EDGE,"E4536"),sQuery(id+"F0.wireOp",EDGE,"E4537"),sQuery(id+"F0.wireOp",EDGE,"E4538"),sQuery(id+"F0.wireOp",EDGE,"E4539"),sQuery(id+"F0.wireOp",EDGE,"E4540"),sQuery(id+"F0.wireOp",EDGE,"E4541"),sQuery(id+"F0.wireOp",EDGE,"E4542"),sQuery(id+"F0.wireOp",EDGE,"E4543"),sQuery(id+"F0.wireOp",EDGE,"E4544"),sQuery(id+"F0.wireOp",EDGE,"E4545"),sQuery(id+"F0.wireOp",EDGE,"E4546"),sQuery(id+"F0.wireOp",EDGE,"E4547"),sQuery(id+"F0.wireOp",EDGE,"E4548"),sQuery(id+"F0.wireOp",EDGE,"E4549"),sQuery(id+"F0.wireOp",EDGE,"E4550"),sQuery(id+"F0.wireOp",EDGE,"E4551"),sQuery(id+"F0.wireOp",EDGE,"E4552"),sQuery(id+"F0.wireOp",EDGE,"E4553"),sQuery(id+"F0.wireOp",EDGE,"E4554"),sQuery(id+"F0.wireOp",EDGE,"E4555"),sQuery(id+"F0.wireOp",EDGE,"E4556"),sQuery(id+"F0.wireOp",EDGE,"E4557"),sQuery(id+"F0.wireOp",EDGE,"E4558"),sQuery(id+"F0.wireOp",EDGE,"E4559"),sQuery(id+"F0.wireOp",EDGE,"E4560"),sQuery(id+"F0.wireOp",EDGE,"E4561"),sQuery(id+"F0.wireOp",EDGE,"E4562"),sQuery(id+"F0.wireOp",EDGE,"E4563"),sQuery(id+"F0.wireOp",EDGE,"E4564"),sQuery(id+"F0.wireOp",EDGE,"E4565"),sQuery(id+"F0.wireOp",EDGE,"E4566"),sQuery(id+"F0.wireOp",EDGE,"E4567"),sQuery(id+"F0.wireOp",EDGE,"E4568"),sQuery(id+"F0.wireOp",EDGE,"E4569"),sQuery(id+"F0.wireOp",EDGE,"E4570"),sQuery(id+"F0.wireOp",EDGE,"E4571"),sQuery(id+"F0.wireOp",EDGE,"E4572"),sQuery(id+"F0.wireOp",EDGE,"E4573"),sQuery(id+"F0.wireOp",EDGE,"E4574"),sQuery(id+"F0.wireOp",EDGE,"E4575"),sQuery(id+"F0.wireOp",EDGE,"E4576"),sQuery(id+"F0.wireOp",EDGE,"E4577"),sQuery(id+"F0.wireOp",EDGE,"E4578"),sQuery(id+"F0.wireOp",EDGE,"E4579"),sQuery(id+"F0.wireOp",EDGE,"E4580"),sQuery(id+"F0.wireOp",EDGE,"E4581"),sQuery(id+"F0.wireOp",EDGE,"E4582"),sQuery(id+"F0.wireOp",EDGE,"E4583"),sQuery(id+"F0.wireOp",EDGE,"E4584"),sQuery(id+"F0.wireOp",EDGE,"E4585"),sQuery(id+"F0.wireOp",EDGE,"E4586"),sQuery(id+"F0.wireOp",EDGE,"E4587"),sQuery(id+"F0.wireOp",EDGE,"E4588"),sQuery(id+"F0.wireOp",EDGE,"E4589"),sQuery(id+"F0.wireOp",EDGE,"E4590"),sQuery(id+"F0.wireOp",EDGE,"E4591"),sQuery(id+"F0.wireOp",EDGE,"E4592"),sQuery(id+"F0.wireOp",EDGE,"E4593"),sQuery(id+"F0.wireOp",EDGE,"E4594"),sQuery(id+"F0.wireOp",EDGE,"E4595"),sQuery(id+"F0.wireOp",EDGE,"E4596"),sQuery(id+"F0.wireOp",EDGE,"E4597"),sQuery(id+"F0.wireOp",EDGE,"E4598"),sQuery(id+"F0.wireOp",EDGE,"E4599"),sQuery(id+"F0.wireOp",EDGE,"E4600"),sQuery(id+"F0.wireOp",EDGE,"E4601"),sQuery(id+"F0.wireOp",EDGE,"E4602"),sQuery(id+"F0.wireOp",EDGE,"E4603"),sQuery(id+"F0.wireOp",EDGE,"E4604"),sQuery(id+"F0.wireOp",EDGE,"E4605"),sQuery(id+"F0.wireOp",EDGE,"E4606"),sQuery(id+"F0.wireOp",EDGE,"E4607"),sQuery(id+"F0.wireOp",EDGE,"E4608"),sQuery(id+"F0.wireOp",EDGE,"E4609"),sQuery(id+"F0.wireOp",EDGE,"E4610"),sQuery(id+"F0.wireOp",EDGE,"E4611"),sQuery(id+"F0.wireOp",EDGE,"E4612"),sQuery(id+"F0.wireOp",EDGE,"E4613"),sQuery(id+"F0.wireOp",EDGE,"E4614"),sQuery(id+"F0.wireOp",EDGE,"E4615"),sQuery(id+"F0.wireOp",EDGE,"E4616"),sQuery(id+"F0.wireOp",EDGE,"E4617"),sQuery(id+"F0.wireOp",EDGE,"E4618"),sQuery(id+"F0.wireOp",EDGE,"E4619"),sQuery(id+"F0.wireOp",EDGE,"E4620"),sQuery(id+"F0.wireOp",EDGE,"E4621"),sQuery(id+"F0.wireOp",EDGE,"E4622"),sQuery(id+"F0.wireOp",EDGE,"E4623"),sQuery(id+"F0.wireOp",EDGE,"E4624"),sQuery(id+"F0.wireOp",EDGE,"E4625"),sQuery(id+"F0.wireOp",EDGE,"E4626"),sQuery(id+"F0.wireOp",EDGE,"E4627"),sQuery(id+"F0.wireOp",EDGE,"E4628"),sQuery(id+"F0.wireOp",EDGE,"E4629"),sQuery(id+"F0.wireOp",EDGE,"E4630"),sQuery(id+"F0.wireOp",EDGE,"E4631"),sQuery(id+"F0.wireOp",EDGE,"E4632"),sQuery(id+"F0.wireOp",EDGE,"E4633"),sQuery(id+"F0.wireOp",EDGE,"E4634"),sQuery(id+"F0.wireOp",EDGE,"E4635"),sQuery(id+"F0.wireOp",EDGE,"E4636"),sQuery(id+"F0.wireOp",EDGE,"E4637"),sQuery(id+"F0.wireOp",EDGE,"E4638"),sQuery(id+"F0.wireOp",EDGE,"E4639"),sQuery(id+"F0.wireOp",EDGE,"E4640"),sQuery(id+"F0.wireOp",EDGE,"E4641"),sQuery(id+"F0.wireOp",EDGE,"E4642"),sQuery(id+"F0.wireOp",EDGE,"E4643"),sQuery(id+"F0.wireOp",EDGE,"E4644"),sQuery(id+"F0.wireOp",EDGE,"E4645"),sQuery(id+"F0.wireOp",EDGE,"E4646"),sQuery(id+"F0.wireOp",EDGE,"E4647"),sQuery(id+"F0.wireOp",EDGE,"E4648"),sQuery(id+"F0.wireOp",EDGE,"E4649"),sQuery(id+"F0.wireOp",EDGE,"E4650"),sQuery(id+"F0.wireOp",EDGE,"E4651"),sQuery(id+"F0.wireOp",EDGE,"E4652"),sQuery(id+"F0.wireOp",EDGE,"E4653"),sQuery(id+"F0.wireOp",EDGE,"E4654"),sQuery(id+"F0.wireOp",EDGE,"E4655"),sQuery(id+"F0.wireOp",EDGE,"E4656"),sQuery(id+"F0.wireOp",EDGE,"E4657"),sQuery(id+"F0.wireOp",EDGE,"E4658"),sQuery(id+"F0.wireOp",EDGE,"E4659"),sQuery(id+"F0.wireOp",EDGE,"E4660"),sQuery(id+"F0.wireOp",EDGE,"E4661"),sQuery(id+"F0.wireOp",EDGE,"E4662"),sQuery(id+"F0.wireOp",EDGE,"E4663"),sQuery(id+"F0.wireOp",EDGE,"E4664"),sQuery(id+"F0.wireOp",EDGE,"E4665"),sQuery(id+"F0.wireOp",EDGE,"E4666"),sQuery(id+"F0.wireOp",EDGE,"E4667"),sQuery(id+"F0.wireOp",EDGE,"E4668"),sQuery(id+"F0.wireOp",EDGE,"E4669"),sQuery(id+"F0.wireOp",EDGE,"E4670"),sQuery(id+"F0.wireOp",EDGE,"E4671"),sQuery(id+"F0.wireOp",EDGE,"E4672"),sQuery(id+"F0.wireOp",EDGE,"E4673"),sQuery(id+"F0.wireOp",EDGE,"E4674"),sQuery(id+"F0.wireOp",EDGE,"E4675"),sQuery(id+"F0.wireOp",EDGE,"E4676"),sQuery(id+"F0.wireOp",EDGE,"E4677"),sQuery(id+"F0.wireOp",EDGE,"E4678"),sQuery(id+"F0.wireOp",EDGE,"E4679"),sQuery(id+"F0.wireOp",EDGE,"E4680"),sQuery(id+"F0.wireOp",EDGE,"E4681"),sQuery(id+"F0.wireOp",EDGE,"E4682"),sQuery(id+"F0.wireOp",EDGE,"E4683"),sQuery(id+"F0.wireOp",EDGE,"E4684"),sQuery(id+"F0.wireOp",EDGE,"E4685"),sQuery(id+"F0.wireOp",EDGE,"E4686"),sQuery(id+"F0.wireOp",EDGE,"E4687"),sQuery(id+"F0.wireOp",EDGE,"E4688"),sQuery(id+"F0.wireOp",EDGE,"E4689"),sQuery(id+"F0.wireOp",EDGE,"E4690"),sQuery(id+"F0.wireOp",EDGE,"E4691"),sQuery(id+"F0.wireOp",EDGE,"E4692"),sQuery(id+"F0.wireOp",EDGE,"E4693"),sQuery(id+"F0.wireOp",EDGE,"E4694"),sQuery(id+"F0.wireOp",EDGE,"E4695"),sQuery(id+"F0.wireOp",EDGE,"E4696"),sQuery(id+"F0.wireOp",EDGE,"E4697"),sQuery(id+"F0.wireOp",EDGE,"E4698"),sQuery(id+"F0.wireOp",EDGE,"E4699"),sQuery(id+"F0.wireOp",EDGE,"E4700"),sQuery(id+"F0.wireOp",EDGE,"E4701"),sQuery(id+"F0.wireOp",EDGE,"E4702"),sQuery(id+"F0.wireOp",EDGE,"E4703"),sQuery(id+"F0.wireOp",EDGE,"E4704"),sQuery(id+"F0.wireOp",EDGE,"E4705"),sQuery(id+"F0.wireOp",EDGE,"E4706"),sQuery(id+"F0.wireOp",EDGE,"E4707"),sQuery(id+"F0.wireOp",EDGE,"E4708"),sQuery(id+"F0.wireOp",EDGE,"E4709"),sQuery(id+"F0.wireOp",EDGE,"E4710"),sQuery(id+"F0.wireOp",EDGE,"E4711"),sQuery(id+"F0.wireOp",EDGE,"E4712"),sQuery(id+"F0.wireOp",EDGE,"E4713"),sQuery(id+"F0.wireOp",EDGE,"E4714"),sQuery(id+"F0.wireOp",EDGE,"E4715"),sQuery(id+"F0.wireOp",EDGE,"E4716"),sQuery(id+"F0.wireOp",EDGE,"E4717"),sQuery(id+"F0.wireOp",EDGE,"E4718"),sQuery(id+"F0.wireOp",EDGE,"E4719"),sQuery(id+"F0.wireOp",EDGE,"E4720"),sQuery(id+"F0.wireOp",EDGE,"E4721"),sQuery(id+"F0.wireOp",EDGE,"E4722"),sQuery(id+"F0.wireOp",EDGE,"E4723"),sQuery(id+"F0.wireOp",EDGE,"E4724"),sQuery(id+"F0.wireOp",EDGE,"E4725"),sQuery(id+"F0.wireOp",EDGE,"E4726"),sQuery(id+"F0.wireOp",EDGE,"E4727"),sQuery(id+"F0.wireOp",EDGE,"E4728"),sQuery(id+"F0.wireOp",EDGE,"E4729"),sQuery(id+"F0.wireOp",EDGE,"E4730"),sQuery(id+"F0.wireOp",EDGE,"E4731"),sQuery(id+"F0.wireOp",EDGE,"E4732"),sQuery(id+"F0.wireOp",EDGE,"E4733"),sQuery(id+"F0.wireOp",EDGE,"E4734"),sQuery(id+"F0.wireOp",EDGE,"E4735"),sQuery(id+"F0.wireOp",EDGE,"E4736"),sQuery(id+"F0.wireOp",EDGE,"E4737"),sQuery(id+"F0.wireOp",EDGE,"E4738"),sQuery(id+"F0.wireOp",EDGE,"E4739"),sQuery(id+"F0.wireOp",EDGE,"E4740"),sQuery(id+"F0.wireOp",EDGE,"E4741"),sQuery(id+"F0.wireOp",EDGE,"E4742"),sQuery(id+"F0.wireOp",EDGE,"E4743"),sQuery(id+"F0.wireOp",EDGE,"E4744"),sQuery(id+"F0.wireOp",EDGE,"E4745"),sQuery(id+"F0.wireOp",EDGE,"E4746"),sQuery(id+"F0.wireOp",EDGE,"E4747"),sQuery(id+"F0.wireOp",EDGE,"E4748"),sQuery(id+"F0.wireOp",EDGE,"E4749"),sQuery(id+"F0.wireOp",EDGE,"E4750"),sQuery(id+"F0.wireOp",EDGE,"E4751"),sQuery(id+"F0.wireOp",EDGE,"E4752"),sQuery(id+"F0.wireOp",EDGE,"E4753"),sQuery(id+"F0.wireOp",EDGE,"E4754"),sQuery(id+"F0.wireOp",EDGE,"E4755"),sQuery(id+"F0.wireOp",EDGE,"E4756"),sQuery(id+"F0.wireOp",EDGE,"E4757"),sQuery(id+"F0.wireOp",EDGE,"E4758"),sQuery(id+"F0.wireOp",EDGE,"E4759"),sQuery(id+"F0.wireOp",EDGE,"E4760"),sQuery(id+"F0.wireOp",EDGE,"E4761"),sQuery(id+"F0.wireOp",EDGE,"E4762"),sQuery(id+"F0.wireOp",EDGE,"E4763"),sQuery(id+"F0.wireOp",EDGE,"E4764"),sQuery(id+"F0.wireOp",EDGE,"E4765"),sQuery(id+"F0.wireOp",EDGE,"E4766"),sQuery(id+"F0.wireOp",EDGE,"E4767"),sQuery(id+"F0.wireOp",EDGE,"E4768"),sQuery(id+"F0.wireOp",EDGE,"E4769"),sQuery(id+"F0.wireOp",EDGE,"E4770"),sQuery(id+"F0.wireOp",EDGE,"E4771"),sQuery(id+"F0.wireOp",EDGE,"E4772"),sQuery(id+"F0.wireOp",EDGE,"E4773"),sQuery(id+"F0.wireOp",EDGE,"E4774"),sQuery(id+"F0.wireOp",EDGE,"E4775"),sQuery(id+"F0.wireOp",EDGE,"E4776"),sQuery(id+"F0.wireOp",EDGE,"E4777"),sQuery(id+"F0.wireOp",EDGE,"E4778"),sQuery(id+"F0.wireOp",EDGE,"E4779"),sQuery(id+"F0.wireOp",EDGE,"E4780"),sQuery(id+"F0.wireOp",EDGE,"E4781"),sQuery(id+"F0.wireOp",EDGE,"E4782"),sQuery(id+"F0.wireOp",EDGE,"E4783"),sQuery(id+"F0.wireOp",EDGE,"E4784"),sQuery(id+"F0.wireOp",EDGE,"E4785"),sQuery(id+"F0.wireOp",EDGE,"E4786"),sQuery(id+"F0.wireOp",EDGE,"E4787"),sQuery(id+"F0.wireOp",EDGE,"E4788"),sQuery(id+"F0.wireOp",EDGE,"E4789"),sQuery(id+"F0.wireOp",EDGE,"E4790"),sQuery(id+"F0.wireOp",EDGE,"E4791"),sQuery(id+"F0.wireOp",EDGE,"E4792"),sQuery(id+"F0.wireOp",EDGE,"E4793"),sQuery(id+"F0.wireOp",EDGE,"E4794"),sQuery(id+"F0.wireOp",EDGE,"E4795"),sQuery(id+"F0.wireOp",EDGE,"E4796"),sQuery(id+"F0.wireOp",EDGE,"E4797"),sQuery(id+"F0.wireOp",EDGE,"E4798"),sQuery(id+"F0.wireOp",EDGE,"E4799"),sQuery(id+"F0.wireOp",EDGE,"E4800"),sQuery(id+"F0.wireOp",EDGE,"E4801"),sQuery(id+"F0.wireOp",EDGE,"E4802"),sQuery(id+"F0.wireOp",EDGE,"E4803"),sQuery(id+"F0.wireOp",EDGE,"E4804"),sQuery(id+"F0.wireOp",EDGE,"E4805"),sQuery(id+"F0.wireOp",EDGE,"E4806"),sQuery(id+"F0.wireOp",EDGE,"E4807"),sQuery(id+"F0.wireOp",EDGE,"E4808"),sQuery(id+"F0.wireOp",EDGE,"E4809"),sQuery(id+"F0.wireOp",EDGE,"E4810"),sQuery(id+"F0.wireOp",EDGE,"E4811"),sQuery(id+"F0.wireOp",EDGE,"E4812"),sQuery(id+"F0.wireOp",EDGE,"E4813"),sQuery(id+"F0.wireOp",EDGE,"E4814"),sQuery(id+"F0.wireOp",EDGE,"E4815"),sQuery(id+"F0.wireOp",EDGE,"E4816"),sQuery(id+"F0.wireOp",EDGE,"E4817"),sQuery(id+"F0.wireOp",EDGE,"E4818"),sQuery(id+"F0.wireOp",EDGE,"E4819"),sQuery(id+"F0.wireOp",EDGE,"E4820"),sQuery(id+"F0.wireOp",EDGE,"E4821"),sQuery(id+"F0.wireOp",EDGE,"E4822"),sQuery(id+"F0.wireOp",EDGE,"E4823"),sQuery(id+"F0.wireOp",EDGE,"E4824"),sQuery(id+"F0.wireOp",EDGE,"E4825"),sQuery(id+"F0.wireOp",EDGE,"E4826"),sQuery(id+"F0.wireOp",EDGE,"E4827"),sQuery(id+"F0.wireOp",EDGE,"E4828"),sQuery(id+"F0.wireOp",EDGE,"E4829"),sQuery(id+"F0.wireOp",EDGE,"E4830"),sQuery(id+"F0.wireOp",EDGE,"E4831"),sQuery(id+"F0.wireOp",EDGE,"E4832"),sQuery(id+"F0.wireOp",EDGE,"E4833"),sQuery(id+"F0.wireOp",EDGE,"E4834"),sQuery(id+"F0.wireOp",EDGE,"E4835"),sQuery(id+"F0.wireOp",EDGE,"E4836"),sQuery(id+"F0.wireOp",EDGE,"E4837"),sQuery(id+"F0.wireOp",EDGE,"E4838"),sQuery(id+"F0.wireOp",EDGE,"E4839"),sQuery(id+"F0.wireOp",EDGE,"E4840"),sQuery(id+"F0.wireOp",EDGE,"E4841"),sQuery(id+"F0.wireOp",EDGE,"E4842"),sQuery(id+"F0.wireOp",EDGE,"E4843"),sQuery(id+"F0.wireOp",EDGE,"E4844"),sQuery(id+"F0.wireOp",EDGE,"E4845"),sQuery(id+"F0.wireOp",EDGE,"E4846"),sQuery(id+"F0.wireOp",EDGE,"E4847"),sQuery(id+"F0.wireOp",EDGE,"E4848"),sQuery(id+"F0.wireOp",EDGE,"E4849"),sQuery(id+"F0.wireOp",EDGE,"E4850"),sQuery(id+"F0.wireOp",EDGE,"E4851"),sQuery(id+"F0.wireOp",EDGE,"E4852"),sQuery(id+"F0.wireOp",EDGE,"E4853"),sQuery(id+"F0.wireOp",EDGE,"E4854"),sQuery(id+"F0.wireOp",EDGE,"E4855"),sQuery(id+"F0.wireOp",EDGE,"E4856"),sQuery(id+"F0.wireOp",EDGE,"E4857"),sQuery(id+"F0.wireOp",EDGE,"E4858"),sQuery(id+"F0.wireOp",EDGE,"E4859"),sQuery(id+"F0.wireOp",EDGE,"E4860"),sQuery(id+"F0.wireOp",EDGE,"E4861"),sQuery(id+"F0.wireOp",EDGE,"E4862"),sQuery(id+"F0.wireOp",EDGE,"E4863"),sQuery(id+"F0.wireOp",EDGE,"E4864"),sQuery(id+"F0.wireOp",EDGE,"E4865"),sQuery(id+"F0.wireOp",EDGE,"E4866"),sQuery(id+"F0.wireOp",EDGE,"E4867"),sQuery(id+"F0.wireOp",EDGE,"E4868"),sQuery(id+"F0.wireOp",EDGE,"E4869"),sQuery(id+"F0.wireOp",EDGE,"E4870"),sQuery(id+"F0.wireOp",EDGE,"E4871"),sQuery(id+"F0.wireOp",EDGE,"E4872"),sQuery(id+"F0.wireOp",EDGE,"E4873"),sQuery(id+"F0.wireOp",EDGE,"E4874"),sQuery(id+"F0.wireOp",EDGE,"E4875"),sQuery(id+"F0.wireOp",EDGE,"E4876"),sQuery(id+"F0.wireOp",EDGE,"E4877"),sQuery(id+"F0.wireOp",EDGE,"E4878"),sQuery(id+"F0.wireOp",EDGE,"E4879"),sQuery(id+"F0.wireOp",EDGE,"E4880"),sQuery(id+"F0.wireOp",EDGE,"E4881"),sQuery(id+"F0.wireOp",EDGE,"E4882"),sQuery(id+"F0.wireOp",EDGE,"E4883"),sQuery(id+"F0.wireOp",EDGE,"E4884"),sQuery(id+"F0.wireOp",EDGE,"E4885"),sQuery(id+"F0.wireOp",EDGE,"E4886"),sQuery(id+"F0.wireOp",EDGE,"E4887"),sQuery(id+"F0.wireOp",EDGE,"E4888"),sQuery(id+"F0.wireOp",EDGE,"E4889"),sQuery(id+"F0.wireOp",EDGE,"E4890"),sQuery(id+"F0.wireOp",EDGE,"E4891"),sQuery(id+"F0.wireOp",EDGE,"E4892"),sQuery(id+"F0.wireOp",EDGE,"E4893"),sQuery(id+"F0.wireOp",EDGE,"E4894"),sQuery(id+"F0.wireOp",EDGE,"E4895"),sQuery(id+"F0.wireOp",EDGE,"E4896"),sQuery(id+"F0.wireOp",EDGE,"E4897"),sQuery(id+"F0.wireOp",EDGE,"E4898"),sQuery(id+"F0.wireOp",EDGE,"E4899"),sQuery(id+"F0.wireOp",EDGE,"E4900"),sQuery(id+"F0.wireOp",EDGE,"E4901"),sQuery(id+"F0.wireOp",EDGE,"E4902"),sQuery(id+"F0.wireOp",EDGE,"E4903"),sQuery(id+"F0.wireOp",EDGE,"E4904"),sQuery(id+"F0.wireOp",EDGE,"E4905"),sQuery(id+"F0.wireOp",EDGE,"E4906"),sQuery(id+"F0.wireOp",EDGE,"E4907"),sQuery(id+"F0.wireOp",EDGE,"E4908"),sQuery(id+"F0.wireOp",EDGE,"E4909"),sQuery(id+"F0.wireOp",EDGE,"E4910"),sQuery(id+"F0.wireOp",EDGE,"E4911"),sQuery(id+"F0.wireOp",EDGE,"E4912"),sQuery(id+"F0.wireOp",EDGE,"E4913"),sQuery(id+"F0.wireOp",EDGE,"E4914"),sQuery(id+"F0.wireOp",EDGE,"E4915"),sQuery(id+"F0.wireOp",EDGE,"E4916"),sQuery(id+"F0.wireOp",EDGE,"E4917"),sQuery(id+"F0.wireOp",EDGE,"E4918"),sQuery(id+"F0.wireOp",EDGE,"E4919"),sQuery(id+"F0.wireOp",EDGE,"E4920"),sQuery(id+"F0.wireOp",EDGE,"E4921"),sQuery(id+"F0.wireOp",EDGE,"E4922"),sQuery(id+"F0.wireOp",EDGE,"E4923"),sQuery(id+"F0.wireOp",EDGE,"E4924"),sQuery(id+"F0.wireOp",EDGE,"E4925"),sQuery(id+"F0.wireOp",EDGE,"E4926"),sQuery(id+"F0.wireOp",EDGE,"E4927"),sQuery(id+"F0.wireOp",EDGE,"E4928"),sQuery(id+"F0.wireOp",EDGE,"E4929"),sQuery(id+"F0.wireOp",EDGE,"E4930"),sQuery(id+"F0.wireOp",EDGE,"E4931"),sQuery(id+"F0.wireOp",EDGE,"E4932"),sQuery(id+"F0.wireOp",EDGE,"E4933"),sQuery(id+"F0.wireOp",EDGE,"E4934"),sQuery(id+"F0.wireOp",EDGE,"E4935"),sQuery(id+"F0.wireOp",EDGE,"E4936"),sQuery(id+"F0.wireOp",EDGE,"E4937"),sQuery(id+"F0.wireOp",EDGE,"E4938"),sQuery(id+"F0.wireOp",EDGE,"E4939"),sQuery(id+"F0.wireOp",EDGE,"E4940"),sQuery(id+"F0.wireOp",EDGE,"E4941"),sQuery(id+"F0.wireOp",EDGE,"E4942"),sQuery(id+"F0.wireOp",EDGE,"E4943"),sQuery(id+"F0.wireOp",EDGE,"E4944"),sQuery(id+"F0.wireOp",EDGE,"E4945"),sQuery(id+"F0.wireOp",EDGE,"E4946"),sQuery(id+"F0.wireOp",EDGE,"E4947"),sQuery(id+"F0.wireOp",EDGE,"E4948"),sQuery(id+"F0.wireOp",EDGE,"E4949"),sQuery(id+"F0.wireOp",EDGE,"E4950"),sQuery(id+"F0.wireOp",EDGE,"E4951"),sQuery(id+"F0.wireOp",EDGE,"E4952"),sQuery(id+"F0.wireOp",EDGE,"E4953"),sQuery(id+"F0.wireOp",EDGE,"E4954"),sQuery(id+"F0.wireOp",EDGE,"E4955"),sQuery(id+"F0.wireOp",EDGE,"E4956"),sQuery(id+"F0.wireOp",EDGE,"E4957"),sQuery(id+"F0.wireOp",EDGE,"E4958"),sQuery(id+"F0.wireOp",EDGE,"E4959"),sQuery(id+"F0.wireOp",EDGE,"E4960"),sQuery(id+"F0.wireOp",EDGE,"E4961"),sQuery(id+"F0.wireOp",EDGE,"E4962"),sQuery(id+"F0.wireOp",EDGE,"E4963"),sQuery(id+"F0.wireOp",EDGE,"E4964"),sQuery(id+"F0.wireOp",EDGE,"E4965"),sQuery(id+"F0.wireOp",EDGE,"E4966"),sQuery(id+"F0.wireOp",EDGE,"E4967"),sQuery(id+"F0.wireOp",EDGE,"E4968"),sQuery(id+"F0.wireOp",EDGE,"E4969"),sQuery(id+"F0.wireOp",EDGE,"E4970"),sQuery(id+"F0.wireOp",EDGE,"E4971"),sQuery(id+"F0.wireOp",EDGE,"E4972"),sQuery(id+"F0.wireOp",EDGE,"E4973"),sQuery(id+"F0.wireOp",EDGE,"E4974"),sQuery(id+"F0.wireOp",EDGE,"E4975"),sQuery(id+"F0.wireOp",EDGE,"E4976"),sQuery(id+"F0.wireOp",EDGE,"E4977"),sQuery(id+"F0.wireOp",EDGE,"E4978"),sQuery(id+"F0.wireOp",EDGE,"E4979"),sQuery(id+"F0.wireOp",EDGE,"E4980"),sQuery(id+"F0.wireOp",EDGE,"E4981"),sQuery(id+"F0.wireOp",EDGE,"E4982"),sQuery(id+"F0.wireOp",EDGE,"E4983"),sQuery(id+"F0.wireOp",EDGE,"E4984"),sQuery(id+"F0.wireOp",EDGE,"E4985"),sQuery(id+"F0.wireOp",EDGE,"E4986"),sQuery(id+"F0.wireOp",EDGE,"E4987"),sQuery(id+"F0.wireOp",EDGE,"E4988"),sQuery(id+"F0.wireOp",EDGE,"E4989"),sQuery(id+"F0.wireOp",EDGE,"E4990"),sQuery(id+"F0.wireOp",EDGE,"E4991"),sQuery(id+"F0.wireOp",EDGE,"E4992"),sQuery(id+"F0.wireOp",EDGE,"E4993"),sQuery(id+"F0.wireOp",EDGE,"E4994"),sQuery(id+"F0.wireOp",EDGE,"E4995"),sQuery(id+"F0.wireOp",EDGE,"E4996"),sQuery(id+"F0.wireOp",EDGE,"E4997"),sQuery(id+"F0.wireOp",EDGE,"E4998"),sQuery(id+"F0.wireOp",EDGE,"E4999"),sQuery(id+"F0.wireOp",EDGE,"E5000"),sQuery(id+"F0.wireOp",EDGE,"E5001"),sQuery(id+"F0.wireOp",EDGE,"E5002"),sQuery(id+"F0.wireOp",EDGE,"E5003"),sQuery(id+"F0.wireOp",EDGE,"E5004"),sQuery(id+"F0.wireOp",EDGE,"E5005"),sQuery(id+"F0.wireOp",EDGE,"E5006"),sQuery(id+"F0.wireOp",EDGE,"E5007"),sQuery(id+"F0.wireOp",EDGE,"E5008"),sQuery(id+"F0.wireOp",EDGE,"E5009"),sQuery(id+"F0.wireOp",EDGE,"E5010"),sQuery(id+"F0.wireOp",EDGE,"E5011"),sQuery(id+"F0.wireOp",EDGE,"E5012"),sQuery(id+"F0.wireOp",EDGE,"E5013"),sQuery(id+"F0.wireOp",EDGE,"E5014"),sQuery(id+"F0.wireOp",EDGE,"E5015"),sQuery(id+"F0.wireOp",EDGE,"E5016"),sQuery(id+"F0.wireOp",EDGE,"E5017"),sQuery(id+"F0.wireOp",EDGE,"E5018"),sQuery(id+"F0.wireOp",EDGE,"E5019"),sQuery(id+"F0.wireOp",EDGE,"E5020"),sQuery(id+"F0.wireOp",EDGE,"E5021"),sQuery(id+"F0.wireOp",EDGE,"E5022"),sQuery(id+"F0.wireOp",EDGE,"E5023"),sQuery(id+"F0.wireOp",EDGE,"E5024"),sQuery(id+"F0.wireOp",EDGE,"E5025"),sQuery(id+"F0.wireOp",EDGE,"E5026"),sQuery(id+"F0.wireOp",EDGE,"E5027"),sQuery(id+"F0.wireOp",EDGE,"E5028"),sQuery(id+"F0.wireOp",EDGE,"E5029"),sQuery(id+"F0.wireOp",EDGE,"E5030"),sQuery(id+"F0.wireOp",EDGE,"E5031"),sQuery(id+"F0.wireOp",EDGE,"E5032"),sQuery(id+"F0.wireOp",EDGE,"E5033"),sQuery(id+"F0.wireOp",EDGE,"E5034"),sQuery(id+"F0.wireOp",EDGE,"E5035"),sQuery(id+"F0.wireOp",EDGE,"E5036"),sQuery(id+"F0.wireOp",EDGE,"E5037"),sQuery(id+"F0.wireOp",EDGE,"E5038"),sQuery(id+"F0.wireOp",EDGE,"E5039"),sQuery(id+"F0.wireOp",EDGE,"E5040"),sQuery(id+"F0.wireOp",EDGE,"E5041"),sQuery(id+"F0.wireOp",EDGE,"E5042"),sQuery(id+"F0.wireOp",EDGE,"E5043"),sQuery(id+"F0.wireOp",EDGE,"E5044"),sQuery(id+"F0.wireOp",EDGE,"E5045"),sQuery(id+"F0.wireOp",EDGE,"E5046"),sQuery(id+"F0.wireOp",EDGE,"E5047"),sQuery(id+"F0.wireOp",EDGE,"E5048"),sQuery(id+"F0.wireOp",EDGE,"E5049"),sQuery(id+"F0.wireOp",EDGE,"E5050"),sQuery(id+"F0.wireOp",EDGE,"E5051"),sQuery(id+"F0.wireOp",EDGE,"E5052"),sQuery(id+"F0.wireOp",EDGE,"E5053"),sQuery(id+"F0.wireOp",EDGE,"E5054"),sQuery(id+"F0.wireOp",EDGE,"E5055"),sQuery(id+"F0.wireOp",EDGE,"E5056"),sQuery(id+"F0.wireOp",EDGE,"E5057"),sQuery(id+"F0.wireOp",EDGE,"E5058"),sQuery(id+"F0.wireOp",EDGE,"E5059"),sQuery(id+"F0.wireOp",EDGE,"E5060"),sQuery(id+"F0.wireOp",EDGE,"E5061"),sQuery(id+"F0.wireOp",EDGE,"E5062"),sQuery(id+"F0.wireOp",EDGE,"E5063"),sQuery(id+"F0.wireOp",EDGE,"E5064"),sQuery(id+"F0.wireOp",EDGE,"E5065"),sQuery(id+"F0.wireOp",EDGE,"E5066"),sQuery(id+"F0.wireOp",EDGE,"E5067"),sQuery(id+"F0.wireOp",EDGE,"E5068"),sQuery(id+"F0.wireOp",EDGE,"E5069"),sQuery(id+"F0.wireOp",EDGE,"E5070"),sQuery(id+"F0.wireOp",EDGE,"E5071"),sQuery(id+"F0.wireOp",EDGE,"E5072"),sQuery(id+"F0.wireOp",EDGE,"E5073"),sQuery(id+"F0.wireOp",EDGE,"E5074"),sQuery(id+"F0.wireOp",EDGE,"E5075"),sQuery(id+"F0.wireOp",EDGE,"E5076"),sQuery(id+"F0.wireOp",EDGE,"E5077"),sQuery(id+"F0.wireOp",EDGE,"E5078"),sQuery(id+"F0.wireOp",EDGE,"E5079"),sQuery(id+"F0.wireOp",EDGE,"E5080"),sQuery(id+"F0.wireOp",EDGE,"E5081"),sQuery(id+"F0.wireOp",EDGE,"E5082"),sQuery(id+"F0.wireOp",EDGE,"E5083"),sQuery(id+"F0.wireOp",EDGE,"E5084"),sQuery(id+"F0.wireOp",EDGE,"E5085"),sQuery(id+"F0.wireOp",EDGE,"E5086"),sQuery(id+"F0.wireOp",EDGE,"E5087"),sQuery(id+"F0.wireOp",EDGE,"E5088"),sQuery(id+"F0.wireOp",EDGE,"E5089"),sQuery(id+"F0.wireOp",EDGE,"E5090"),sQuery(id+"F0.wireOp",EDGE,"E5091"),sQuery(id+"F0.wireOp",EDGE,"E5092"),sQuery(id+"F0.wireOp",EDGE,"E5093"),sQuery(id+"F0.wireOp",EDGE,"E5094"),sQuery(id+"F0.wireOp",EDGE,"E5095"),sQuery(id+"F0.wireOp",EDGE,"E5096"),sQuery(id+"F0.wireOp",EDGE,"E5097"),sQuery(id+"F0.wireOp",EDGE,"E5098"),sQuery(id+"F0.wireOp",EDGE,"E5099"),sQuery(id+"F0.wireOp",EDGE,"E5100"),sQuery(id+"F0.wireOp",EDGE,"E5101"),sQuery(id+"F0.wireOp",EDGE,"E5102"),sQuery(id+"F0.wireOp",EDGE,"E5103"),sQuery(id+"F0.wireOp",EDGE,"E5104"),sQuery(id+"F0.wireOp",EDGE,"E5105"),sQuery(id+"F0.wireOp",EDGE,"E5106"),sQuery(id+"F0.wireOp",EDGE,"E5107"),sQuery(id+"F0.wireOp",EDGE,"E5108"),sQuery(id+"F0.wireOp",EDGE,"E5109"),sQuery(id+"F0.wireOp",EDGE,"E5110"),sQuery(id+"F0.wireOp",EDGE,"E5111"),sQuery(id+"F0.wireOp",EDGE,"E5112"),sQuery(id+"F0.wireOp",EDGE,"E5113"),sQuery(id+"F0.wireOp",EDGE,"E5114"),sQuery(id+"F0.wireOp",EDGE,"E5115"),sQuery(id+"F0.wireOp",EDGE,"E5116"),sQuery(id+"F0.wireOp",EDGE,"E5117"),sQuery(id+"F0.wireOp",EDGE,"E5118"),sQuery(id+"F0.wireOp",EDGE,"E5119"),sQuery(id+"F0.wireOp",EDGE,"E5120"),sQuery(id+"F0.wireOp",EDGE,"E5121"),sQuery(id+"F0.wireOp",EDGE,"E5122"),sQuery(id+"F0.wireOp",EDGE,"E5123"),sQuery(id+"F0.wireOp",EDGE,"E5124"),sQuery(id+"F0.wireOp",EDGE,"E5125"),sQuery(id+"F0.wireOp",EDGE,"E5126"),sQuery(id+"F0.wireOp",EDGE,"E5127"),sQuery(id+"F0.wireOp",EDGE,"E5128"),sQuery(id+"F0.wireOp",EDGE,"E5129"),sQuery(id+"F0.wireOp",EDGE,"E5130"),sQuery(id+"F0.wireOp",EDGE,"E5131"),sQuery(id+"F0.wireOp",EDGE,"E5132"),sQuery(id+"F0.wireOp",EDGE,"E5133"),sQuery(id+"F0.wireOp",EDGE,"E5134"),sQuery(id+"F0.wireOp",EDGE,"E5135"),sQuery(id+"F0.wireOp",EDGE,"E5136"),sQuery(id+"F0.wireOp",EDGE,"E5137"),sQuery(id+"F0.wireOp",EDGE,"E5138"),sQuery(id+"F0.wireOp",EDGE,"E5139"),sQuery(id+"F0.wireOp",EDGE,"E5140"),sQuery(id+"F0.wireOp",EDGE,"E5141"),sQuery(id+"F0.wireOp",EDGE,"E5142"),sQuery(id+"F0.wireOp",EDGE,"E5143"),sQuery(id+"F0.wireOp",EDGE,"E5144"),sQuery(id+"F0.wireOp",EDGE,"E5145"),sQuery(id+"F0.wireOp",EDGE,"E5146"),sQuery(id+"F0.wireOp",EDGE,"E5147"),sQuery(id+"F0.wireOp",EDGE,"E5148"),sQuery(id+"F0.wireOp",EDGE,"E5149"),sQuery(id+"F0.wireOp",EDGE,"E5150"),sQuery(id+"F0.wireOp",EDGE,"E5151"),sQuery(id+"F0.wireOp",EDGE,"E5152"),sQuery(id+"F0.wireOp",EDGE,"E5153"),sQuery(id+"F0.wireOp",EDGE,"E5154"),sQuery(id+"F0.wireOp",EDGE,"E5155"),sQuery(id+"F0.wireOp",EDGE,"E5156"),sQuery(id+"F0.wireOp",EDGE,"E5157"),sQuery(id+"F0.wireOp",EDGE,"E5158"),sQuery(id+"F0.wireOp",EDGE,"E5159"),sQuery(id+"F0.wireOp",EDGE,"E5160"),sQuery(id+"F0.wireOp",EDGE,"E5161"),sQuery(id+"F0.wireOp",EDGE,"E5162"),sQuery(id+"F0.wireOp",EDGE,"E5163"),sQuery(id+"F0.wireOp",EDGE,"E5164"),sQuery(id+"F0.wireOp",EDGE,"E5165"),sQuery(id+"F0.wireOp",EDGE,"E5166"),sQuery(id+"F0.wireOp",EDGE,"E5167"),sQuery(id+"F0.wireOp",EDGE,"E5168"),sQuery(id+"F0.wireOp",EDGE,"E5169"),sQuery(id+"F0.wireOp",EDGE,"E5170"),sQuery(id+"F0.wireOp",EDGE,"E5171"),sQuery(id+"F0.wireOp",EDGE,"E5172"),sQuery(id+"F0.wireOp",EDGE,"E5173"),sQuery(id+"F0.wireOp",EDGE,"E5174"),sQuery(id+"F0.wireOp",EDGE,"E5175"),sQuery(id+"F0.wireOp",EDGE,"E5176"),sQuery(id+"F0.wireOp",EDGE,"E5177"),sQuery(id+"F0.wireOp",EDGE,"E5178"),sQuery(id+"F0.wireOp",EDGE,"E5179"),sQuery(id+"F0.wireOp",EDGE,"E5180"),sQuery(id+"F0.wireOp",EDGE,"E5181"),sQuery(id+"F0.wireOp",EDGE,"E5182"),sQuery(id+"F0.wireOp",EDGE,"E5183"),sQuery(id+"F0.wireOp",EDGE,"E5184"),sQuery(id+"F0.wireOp",EDGE,"E5185"),sQuery(id+"F0.wireOp",EDGE,"E5186"),sQuery(id+"F0.wireOp",EDGE,"E5187"),sQuery(id+"F0.wireOp",EDGE,"E5188"),sQuery(id+"F0.wireOp",EDGE,"E5189"),sQuery(id+"F0.wireOp",EDGE,"E5190"),sQuery(id+"F0.wireOp",EDGE,"E5191"),sQuery(id+"F0.wireOp",EDGE,"E5192"),sQuery(id+"F0.wireOp",EDGE,"E5193"),sQuery(id+"F0.wireOp",EDGE,"E5194"),sQuery(id+"F0.wireOp",EDGE,"E5195"),sQuery(id+"F0.wireOp",EDGE,"E5196"),sQuery(id+"F0.wireOp",EDGE,"E5197"),sQuery(id+"F0.wireOp",EDGE,"E5198"),sQuery(id+"F0.wireOp",EDGE,"E5199"),sQuery(id+"F0.wireOp",EDGE,"E5200"),sQuery(id+"F0.wireOp",EDGE,"E5201"),sQuery(id+"F0.wireOp",EDGE,"E5202"),sQuery(id+"F0.wireOp",EDGE,"E5203"),sQuery(id+"F0.wireOp",EDGE,"E5204"),sQuery(id+"F0.wireOp",EDGE,"E5205"),sQuery(id+"F0.wireOp",EDGE,"E5206"),sQuery(id+"F0.wireOp",EDGE,"E5207"),sQuery(id+"F0.wireOp",EDGE,"E5208"),sQuery(id+"F0.wireOp",EDGE,"E5209"),sQuery(id+"F0.wireOp",EDGE,"E5210"),sQuery(id+"F0.wireOp",EDGE,"E5211"),sQuery(id+"F0.wireOp",EDGE,"E5212"),sQuery(id+"F0.wireOp",EDGE,"E5213"),sQuery(id+"F0.wireOp",EDGE,"E5214"),sQuery(id+"F0.wireOp",EDGE,"E5215"),sQuery(id+"F0.wireOp",EDGE,"E5216"),sQuery(id+"F0.wireOp",EDGE,"E5217"),sQuery(id+"F0.wireOp",EDGE,"E5218"),sQuery(id+"F0.wireOp",EDGE,"E5219"),sQuery(id+"F0.wireOp",EDGE,"E5220"),sQuery(id+"F0.wireOp",EDGE,"E5221"),sQuery(id+"F0.wireOp",EDGE,"E5222"),sQuery(id+"F0.wireOp",EDGE,"E5223"),sQuery(id+"F0.wireOp",EDGE,"E5224"),sQuery(id+"F0.wireOp",EDGE,"E5225"),sQuery(id+"F0.wireOp",EDGE,"E5226"),sQuery(id+"F0.wireOp",EDGE,"E5227"),sQuery(id+"F0.wireOp",EDGE,"E5228"),sQuery(id+"F0.wireOp",EDGE,"E5229"),sQuery(id+"F0.wireOp",EDGE,"E5230"),sQuery(id+"F0.wireOp",EDGE,"E5231"),sQuery(id+"F0.wireOp",EDGE,"E5232"),sQuery(id+"F0.wireOp",EDGE,"E5233"),sQuery(id+"F0.wireOp",EDGE,"E5234"),sQuery(id+"F0.wireOp",EDGE,"E5235"),sQuery(id+"F0.wireOp",EDGE,"E5236"),sQuery(id+"F0.wireOp",EDGE,"E5237"),sQuery(id+"F0.wireOp",EDGE,"E5238"),sQuery(id+"F0.wireOp",EDGE,"E5239"),sQuery(id+"F0.wireOp",EDGE,"E5240"),sQuery(id+"F0.wireOp",EDGE,"E5241"),sQuery(id+"F0.wireOp",EDGE,"E5242"),sQuery(id+"F0.wireOp",EDGE,"E5243"),sQuery(id+"F0.wireOp",EDGE,"E5244"),sQuery(id+"F0.wireOp",EDGE,"E5245"),sQuery(id+"F0.wireOp",EDGE,"E5246"),sQuery(id+"F0.wireOp",EDGE,"E5247"),sQuery(id+"F0.wireOp",EDGE,"E5248"),sQuery(id+"F0.wireOp",EDGE,"E5249"),sQuery(id+"F0.wireOp",EDGE,"E5250"),sQuery(id+"F0.wireOp",EDGE,"E5251"),sQuery(id+"F0.wireOp",EDGE,"E5252"),sQuery(id+"F0.wireOp",EDGE,"E5253"),sQuery(id+"F0.wireOp",EDGE,"E5254"),sQuery(id+"F0.wireOp",EDGE,"E5255"),sQuery(id+"F0.wireOp",EDGE,"E5256"),sQuery(id+"F0.wireOp",EDGE,"E5257"),sQuery(id+"F0.wireOp",EDGE,"E5258"),sQuery(id+"F0.wireOp",EDGE,"E5259"),sQuery(id+"F0.wireOp",EDGE,"E5260"),sQuery(id+"F0.wireOp",EDGE,"E5261"),sQuery(id+"F0.wireOp",EDGE,"E5262"),sQuery(id+"F0.wireOp",EDGE,"E5263"),sQuery(id+"F0.wireOp",EDGE,"E5264"),sQuery(id+"F0.wireOp",EDGE,"E5265"),sQuery(id+"F0.wireOp",EDGE,"E5266"),sQuery(id+"F0.wireOp",EDGE,"E5267"),sQuery(id+"F0.wireOp",EDGE,"E5268"),sQuery(id+"F0.wireOp",EDGE,"E5269"),sQuery(id+"F0.wireOp",EDGE,"E5270"),sQuery(id+"F0.wireOp",EDGE,"E5271"),sQuery(id+"F0.wireOp",EDGE,"E5272"),sQuery(id+"F0.wireOp",EDGE,"E5273"),sQuery(id+"F0.wireOp",EDGE,"E5274"),sQuery(id+"F0.wireOp",EDGE,"E5275"),sQuery(id+"F0.wireOp",EDGE,"E5276"),sQuery(id+"F0.wireOp",EDGE,"E5277"),sQuery(id+"F0.wireOp",EDGE,"E5278"),sQuery(id+"F0.wireOp",EDGE,"E5279"),sQuery(id+"F0.wireOp",EDGE,"E5280"),sQuery(id+"F0.wireOp",EDGE,"E5281"),sQuery(id+"F0.wireOp",EDGE,"E5282"),sQuery(id+"F0.wireOp",EDGE,"E5283"),sQuery(id+"F0.wireOp",EDGE,"E5284"),sQuery(id+"F0.wireOp",EDGE,"E5285"),sQuery(id+"F0.wireOp",EDGE,"E5286"),sQuery(id+"F0.wireOp",EDGE,"E5287"),sQuery(id+"F0.wireOp",EDGE,"E5288"),sQuery(id+"F0.wireOp",EDGE,"E5289"),sQuery(id+"F0.wireOp",EDGE,"E5290"),sQuery(id+"F0.wireOp",EDGE,"E5291"),sQuery(id+"F0.wireOp",EDGE,"E5292"),sQuery(id+"F0.wireOp",EDGE,"E5293"),sQuery(id+"F0.wireOp",EDGE,"E5294"),sQuery(id+"F0.wireOp",EDGE,"E5295"),sQuery(id+"F0.wireOp",EDGE,"E5296"),sQuery(id+"F0.wireOp",EDGE,"E5297"),sQuery(id+"F0.wireOp",EDGE,"E5298"),sQuery(id+"F0.wireOp",EDGE,"E5299"),sQuery(id+"F0.wireOp",EDGE,"E5300"),sQuery(id+"F0.wireOp",EDGE,"E5301"),sQuery(id+"F0.wireOp",EDGE,"E5302"),sQuery(id+"F0.wireOp",EDGE,"E5303"),sQuery(id+"F0.wireOp",EDGE,"E5304"),sQuery(id+"F0.wireOp",EDGE,"E5305"),sQuery(id+"F0.wireOp",EDGE,"E5306"),sQuery(id+"F0.wireOp",EDGE,"E5307"),sQuery(id+"F0.wireOp",EDGE,"E5308"),sQuery(id+"F0.wireOp",EDGE,"E5309"),sQuery(id+"F0.wireOp",EDGE,"E5310"),sQuery(id+"F0.wireOp",EDGE,"E5311"),sQuery(id+"F0.wireOp",EDGE,"E5312"),sQuery(id+"F0.wireOp",EDGE,"E5313"),sQuery(id+"F0.wireOp",EDGE,"E5314"),sQuery(id+"F0.wireOp",EDGE,"E5315"),sQuery(id+"F0.wireOp",EDGE,"E5316"),sQuery(id+"F0.wireOp",EDGE,"E5317"),sQuery(id+"F0.wireOp",EDGE,"E5318"),sQuery(id+"F0.wireOp",EDGE,"E5319"),sQuery(id+"F0.wireOp",EDGE,"E5320"),sQuery(id+"F0.wireOp",EDGE,"E5321"),sQuery(id+"F0.wireOp",EDGE,"E5322"),sQuery(id+"F0.wireOp",EDGE,"E5323"),sQuery(id+"F0.wireOp",EDGE,"E5324"),sQuery(id+"F0.wireOp",EDGE,"E5325"),sQuery(id+"F0.wireOp",EDGE,"E5326"),sQuery(id+"F0.wireOp",EDGE,"E5327"),sQuery(id+"F0.wireOp",EDGE,"E5328"),sQuery(id+"F0.wireOp",EDGE,"E5329"),sQuery(id+"F0.wireOp",EDGE,"E5330"),sQuery(id+"F0.wireOp",EDGE,"E5331"),sQuery(id+"F0.wireOp",EDGE,"E5332"),sQuery(id+"F0.wireOp",EDGE,"E5333"),sQuery(id+"F0.wireOp",EDGE,"E5334"),sQuery(id+"F0.wireOp",EDGE,"E5335"),sQuery(id+"F0.wireOp",EDGE,"E5336"),sQuery(id+"F0.wireOp",EDGE,"E5337"),sQuery(id+"F0.wireOp",EDGE,"E5338"),sQuery(id+"F0.wireOp",EDGE,"E5339"),sQuery(id+"F0.wireOp",EDGE,"E5340"),sQuery(id+"F0.wireOp",EDGE,"E5341"),sQuery(id+"F0.wireOp",EDGE,"E5342"),sQuery(id+"F0.wireOp",EDGE,"E5343"),sQuery(id+"F0.wireOp",EDGE,"E5344"),sQuery(id+"F0.wireOp",EDGE,"E5345"),sQuery(id+"F0.wireOp",EDGE,"E5346"),sQuery(id+"F0.wireOp",EDGE,"E5347"),sQuery(id+"F0.wireOp",EDGE,"E5348"),sQuery(id+"F0.wireOp",EDGE,"E5349"),sQuery(id+"F0.wireOp",EDGE,"E5350"),sQuery(id+"F0.wireOp",EDGE,"E5351"),sQuery(id+"F0.wireOp",EDGE,"E5352"),sQuery(id+"F0.wireOp",EDGE,"E5353"),sQuery(id+"F0.wireOp",EDGE,"E5354"),sQuery(id+"F0.wireOp",EDGE,"E5355"),sQuery(id+"F0.wireOp",EDGE,"E5356"),sQuery(id+"F0.wireOp",EDGE,"E5357"),sQuery(id+"F0.wireOp",EDGE,"E5358"),sQuery(id+"F0.wireOp",EDGE,"E5359"),sQuery(id+"F0.wireOp",EDGE,"E5360"),sQuery(id+"F0.wireOp",EDGE,"E5361"),sQuery(id+"F0.wireOp",EDGE,"E5362"),sQuery(id+"F0.wireOp",EDGE,"E5363"),sQuery(id+"F0.wireOp",EDGE,"E5364"),sQuery(id+"F0.wireOp",EDGE,"E5365"),sQuery(id+"F0.wireOp",EDGE,"E5366"),sQuery(id+"F0.wireOp",EDGE,"E5367"),sQuery(id+"F0.wireOp",EDGE,"E5368"),sQuery(id+"F0.wireOp",EDGE,"E5369"),sQuery(id+"F0.wireOp",EDGE,"E5370"),sQuery(id+"F0.wireOp",EDGE,"E5371"),sQuery(id+"F0.wireOp",EDGE,"E5372"),sQuery(id+"F0.wireOp",EDGE,"E5373"),sQuery(id+"F0.wireOp",EDGE,"E5374"),sQuery(id+"F0.wireOp",EDGE,"E5375"),sQuery(id+"F0.wireOp",EDGE,"E5376"),sQuery(id+"F0.wireOp",EDGE,"E5377"),sQuery(id+"F0.wireOp",EDGE,"E5378"),sQuery(id+"F0.wireOp",EDGE,"E5379"),sQuery(id+"F0.wireOp",EDGE,"E5380"),sQuery(id+"F0.wireOp",EDGE,"E5381"),sQuery(id+"F0.wireOp",EDGE,"E5382"),sQuery(id+"F0.wireOp",EDGE,"E5383"),sQuery(id+"F0.wireOp",EDGE,"E5384"),sQuery(id+"F0.wireOp",EDGE,"E5385"),sQuery(id+"F0.wireOp",EDGE,"E5386"),sQuery(id+"F0.wireOp",EDGE,"E5387"),sQuery(id+"F0.wireOp",EDGE,"E5388"),sQuery(id+"F0.wireOp",EDGE,"E5389"),sQuery(id+"F0.wireOp",EDGE,"E5390"),sQuery(id+"F0.wireOp",EDGE,"E5391"),sQuery(id+"F0.wireOp",EDGE,"E5392"),sQuery(id+"F0.wireOp",EDGE,"E5393"),sQuery(id+"F0.wireOp",EDGE,"E5394"),sQuery(id+"F0.wireOp",EDGE,"E5395"),sQuery(id+"F0.wireOp",EDGE,"E5396"),sQuery(id+"F0.wireOp",EDGE,"E5397"),sQuery(id+"F0.wireOp",EDGE,"E5398"),sQuery(id+"F0.wireOp",EDGE,"E5399"),sQuery(id+"F0.wireOp",EDGE,"E5400"),sQuery(id+"F0.wireOp",EDGE,"E5401"),sQuery(id+"F0.wireOp",EDGE,"E5402"),sQuery(id+"F0.wireOp",EDGE,"E5403"),sQuery(id+"F0.wireOp",EDGE,"E5404"),sQuery(id+"F0.wireOp",EDGE,"E5405"),sQuery(id+"F0.wireOp",EDGE,"E5406"),sQuery(id+"F0.wireOp",EDGE,"E5407"),sQuery(id+"F0.wireOp",EDGE,"E5408"),sQuery(id+"F0.wireOp",EDGE,"E5409"),sQuery(id+"F0.wireOp",EDGE,"E5410"),sQuery(id+"F0.wireOp",EDGE,"E5411"),sQuery(id+"F0.wireOp",EDGE,"E5412"),sQuery(id+"F0.wireOp",EDGE,"E5413"),sQuery(id+"F0.wireOp",EDGE,"E5414"),sQuery(id+"F0.wireOp",EDGE,"E5415"),sQuery(id+"F0.wireOp",EDGE,"E5416"),sQuery(id+"F0.wireOp",EDGE,"E5417"),sQuery(id+"F0.wireOp",EDGE,"E5418"),sQuery(id+"F0.wireOp",EDGE,"E5419"),sQuery(id+"F0.wireOp",EDGE,"E5420"),sQuery(id+"F0.wireOp",EDGE,"E5421"),sQuery(id+"F0.wireOp",EDGE,"E5422"),sQuery(id+"F0.wireOp",EDGE,"E5423"),sQuery(id+"F0.wireOp",EDGE,"E5424"),sQuery(id+"F0.wireOp",EDGE,"E5425"),sQuery(id+"F0.wireOp",EDGE,"E5426"),sQuery(id+"F0.wireOp",EDGE,"E5427"),sQuery(id+"F0.wireOp",EDGE,"E5428"),sQuery(id+"F0.wireOp",EDGE,"E5429"),sQuery(id+"F0.wireOp",EDGE,"E5430"),sQuery(id+"F0.wireOp",EDGE,"E5431"),sQuery(id+"F0.wireOp",EDGE,"E5432"),sQuery(id+"F0.wireOp",EDGE,"E5433"),sQuery(id+"F0.wireOp",EDGE,"E5434"),sQuery(id+"F0.wireOp",EDGE,"E5435"),sQuery(id+"F0.wireOp",EDGE,"E5436"),sQuery(id+"F0.wireOp",EDGE,"E5437"),sQuery(id+"F0.wireOp",EDGE,"E5438"),sQuery(id+"F0.wireOp",EDGE,"E5439"),sQuery(id+"F0.wireOp",EDGE,"E5440"),sQuery(id+"F0.wireOp",EDGE,"E5441"),sQuery(id+"F0.wireOp",EDGE,"E5442"),sQuery(id+"F0.wireOp",EDGE,"E5443"),sQuery(id+"F0.wireOp",EDGE,"E5444"),sQuery(id+"F0.wireOp",EDGE,"E5445"),sQuery(id+"F0.wireOp",EDGE,"E5446"),sQuery(id+"F0.wireOp",EDGE,"E5447"),sQuery(id+"F0.wireOp",EDGE,"E5448"),sQuery(id+"F0.wireOp",EDGE,"E5449"),sQuery(id+"F0.wireOp",EDGE,"E5450"),sQuery(id+"F0.wireOp",EDGE,"E5451"),sQuery(id+"F0.wireOp",EDGE,"E5452"),sQuery(id+"F0.wireOp",EDGE,"E5453"),sQuery(id+"F0.wireOp",EDGE,"E5454"),sQuery(id+"F0.wireOp",EDGE,"E5455"),sQuery(id+"F0.wireOp",EDGE,"E5456"),sQuery(id+"F0.wireOp",EDGE,"E5457"),sQuery(id+"F0.wireOp",EDGE,"E5458"),sQuery(id+"F0.wireOp",EDGE,"E5459"),sQuery(id+"F0.wireOp",EDGE,"E5460"),sQuery(id+"F0.wireOp",EDGE,"E5461"),sQuery(id+"F0.wireOp",EDGE,"E5462"),sQuery(id+"F0.wireOp",EDGE,"E5463"),sQuery(id+"F0.wireOp",EDGE,"E5464"),sQuery(id+"F0.wireOp",EDGE,"E5465"),sQuery(id+"F0.wireOp",EDGE,"E5466"),sQuery(id+"F0.wireOp",EDGE,"E5467"),sQuery(id+"F0.wireOp",EDGE,"E5468"),sQuery(id+"F0.wireOp",EDGE,"E5469"),sQuery(id+"F0.wireOp",EDGE,"E5470"),sQuery(id+"F0.wireOp",EDGE,"E5471"),sQuery(id+"F0.wireOp",EDGE,"E5472"),sQuery(id+"F0.wireOp",EDGE,"E5473"),sQuery(id+"F0.wireOp",EDGE,"E5474"),sQuery(id+"F0.wireOp",EDGE,"E5475"),sQuery(id+"F0.wireOp",EDGE,"E5476"),sQuery(id+"F0.wireOp",EDGE,"E5477"),sQuery(id+"F0.wireOp",EDGE,"E5478"),sQuery(id+"F0.wireOp",EDGE,"E5479"),sQuery(id+"F0.wireOp",EDGE,"E5480"),sQuery(id+"F0.wireOp",EDGE,"E5481"),sQuery(id+"F0.wireOp",EDGE,"E5482"),sQuery(id+"F0.wireOp",EDGE,"E5483"),sQuery(id+"F0.wireOp",EDGE,"E5484"),sQuery(id+"F0.wireOp",EDGE,"E5485"),sQuery(id+"F0.wireOp",EDGE,"E5486"),sQuery(id+"F0.wireOp",EDGE,"E5487"),sQuery(id+"F0.wireOp",EDGE,"E5488"),sQuery(id+"F0.wireOp",EDGE,"E5489"),sQuery(id+"F0.wireOp",EDGE,"E5490"),sQuery(id+"F0.wireOp",EDGE,"E5491"),sQuery(id+"F0.wireOp",EDGE,"E5492"),sQuery(id+"F0.wireOp",EDGE,"E5493"),sQuery(id+"F0.wireOp",EDGE,"E5494"),sQuery(id+"F0.wireOp",EDGE,"E5495"),sQuery(id+"F0.wireOp",EDGE,"E5496"),sQuery(id+"F0.wireOp",EDGE,"E5497"),sQuery(id+"F0.wireOp",EDGE,"E5498"),sQuery(id+"F0.wireOp",EDGE,"E5499"),sQuery(id+"F0.wireOp",EDGE,"E5500"),sQuery(id+"F0.wireOp",EDGE,"E5501"),sQuery(id+"F0.wireOp",EDGE,"E5502"),sQuery(id+"F0.wireOp",EDGE,"E5503"),sQuery(id+"F0.wireOp",EDGE,"E5504"),sQuery(id+"F0.wireOp",EDGE,"E5505"),sQuery(id+"F0.wireOp",EDGE,"E5506"),sQuery(id+"F0.wireOp",EDGE,"E5507"),sQuery(id+"F0.wireOp",EDGE,"E5508"),sQuery(id+"F0.wireOp",EDGE,"E5509"),sQuery(id+"F0.wireOp",EDGE,"E5510"),sQuery(id+"F0.wireOp",EDGE,"E5511"),sQuery(id+"F0.wireOp",EDGE,"E5512"),sQuery(id+"F0.wireOp",EDGE,"E5513"),sQuery(id+"F0.wireOp",EDGE,"E5514"),sQuery(id+"F0.wireOp",EDGE,"E5515"),sQuery(id+"F0.wireOp",EDGE,"E5516"),sQuery(id+"F0.wireOp",EDGE,"E5517"),sQuery(id+"F0.wireOp",EDGE,"E5518"),sQuery(id+"F0.wireOp",EDGE,"E5519"),sQuery(id+"F0.wireOp",EDGE,"E5520"),sQuery(id+"F0.wireOp",EDGE,"E5521"),sQuery(id+"F0.wireOp",EDGE,"E5522"),sQuery(id+"F0.wireOp",EDGE,"E5523"),sQuery(id+"F0.wireOp",EDGE,"E5524"),sQuery(id+"F0.wireOp",EDGE,"E5525"),sQuery(id+"F0.wireOp",EDGE,"E5526"),sQuery(id+"F0.wireOp",EDGE,"E5527"),sQuery(id+"F0.wireOp",EDGE,"E5528"),sQuery(id+"F0.wireOp",EDGE,"E5529"),sQuery(id+"F0.wireOp",EDGE,"E5530"),sQuery(id+"F0.wireOp",EDGE,"E5531"),sQuery(id+"F0.wireOp",EDGE,"E5532"),sQuery(id+"F0.wireOp",EDGE,"E5533"),sQuery(id+"F0.wireOp",EDGE,"E5534"),sQuery(id+"F0.wireOp",EDGE,"E5535"),sQuery(id+"F0.wireOp",EDGE,"E5536"),sQuery(id+"F0.wireOp",EDGE,"E5537"),sQuery(id+"F0.wireOp",EDGE,"E5538"),sQuery(id+"F0.wireOp",EDGE,"E5539"),sQuery(id+"F0.wireOp",EDGE,"E5540"),sQuery(id+"F0.wireOp",EDGE,"E5541"),sQuery(id+"F0.wireOp",EDGE,"E5542"),sQuery(id+"F0.wireOp",EDGE,"E5543"),sQuery(id+"F0.wireOp",EDGE,"E5544"),sQuery(id+"F0.wireOp",EDGE,"E5545"),sQuery(id+"F0.wireOp",EDGE,"E5546"),sQuery(id+"F0.wireOp",EDGE,"E5547"),sQuery(id+"F0.wireOp",EDGE,"E5548"),sQuery(id+"F0.wireOp",EDGE,"E5549"),sQuery(id+"F0.wireOp",EDGE,"E5550"),sQuery(id+"F0.wireOp",EDGE,"E5551"),sQuery(id+"F0.wireOp",EDGE,"E5552"),sQuery(id+"F0.wireOp",EDGE,"E5553"),sQuery(id+"F0.wireOp",EDGE,"E5554"),sQuery(id+"F0.wireOp",EDGE,"E5555"),sQuery(id+"F0.wireOp",EDGE,"E5556"),sQuery(id+"F0.wireOp",EDGE,"E5557"),sQuery(id+"F0.wireOp",EDGE,"E5558"),sQuery(id+"F0.wireOp",EDGE,"E5559"),sQuery(id+"F0.wireOp",EDGE,"E5560"),sQuery(id+"F0.wireOp",EDGE,"E5561"),sQuery(id+"F0.wireOp",EDGE,"E5562"),sQuery(id+"F0.wireOp",EDGE,"E5563"),sQuery(id+"F0.wireOp",EDGE,"E5564"),sQuery(id+"F0.wireOp",EDGE,"E5565"),sQuery(id+"F0.wireOp",EDGE,"E5566"),sQuery(id+"F0.wireOp",EDGE,"E5567"),sQuery(id+"F0.wireOp",EDGE,"E5568"),sQuery(id+"F0.wireOp",EDGE,"E5569"),sQuery(id+"F0.wireOp",EDGE,"E5570"),sQuery(id+"F0.wireOp",EDGE,"E5571"),sQuery(id+"F0.wireOp",EDGE,"E5572"),sQuery(id+"F0.wireOp",EDGE,"E5573"),sQuery(id+"F0.wireOp",EDGE,"E5574"),sQuery(id+"F0.wireOp",EDGE,"E5575"),sQuery(id+"F0.wireOp",EDGE,"E5576"),sQuery(id+"F0.wireOp",EDGE,"E5577"),sQuery(id+"F0.wireOp",EDGE,"E5578"),sQuery(id+"F0.wireOp",EDGE,"E5579"),sQuery(id+"F0.wireOp",EDGE,"E5580"),sQuery(id+"F0.wireOp",EDGE,"E5581"),sQuery(id+"F0.wireOp",EDGE,"E5582"),sQuery(id+"F0.wireOp",EDGE,"E5583"),sQuery(id+"F0.wireOp",EDGE,"E5584"),sQuery(id+"F0.wireOp",EDGE,"E5585"),sQuery(id+"F0.wireOp",EDGE,"E5586"),sQuery(id+"F0.wireOp",EDGE,"E5587"),sQuery(id+"F0.wireOp",EDGE,"E5588"),sQuery(id+"F0.wireOp",EDGE,"E5589"),sQuery(id+"F0.wireOp",EDGE,"E5590"),sQuery(id+"F0.wireOp",EDGE,"E5591"),sQuery(id+"F0.wireOp",EDGE,"E5592"),sQuery(id+"F0.wireOp",EDGE,"E5593"),sQuery(id+"F0.wireOp",EDGE,"E5594"),sQuery(id+"F0.wireOp",EDGE,"E5595"),sQuery(id+"F0.wireOp",EDGE,"E5596"),sQuery(id+"F0.wireOp",EDGE,"E5597"),sQuery(id+"F0.wireOp",EDGE,"E5598"),sQuery(id+"F0.wireOp",EDGE,"E5599"),sQuery(id+"F0.wireOp",EDGE,"E5600"),sQuery(id+"F0.wireOp",EDGE,"E5601"),sQuery(id+"F0.wireOp",EDGE,"E5602"),sQuery(id+"F0.wireOp",EDGE,"E5603"),sQuery(id+"F0.wireOp",EDGE,"E5604"),sQuery(id+"F0.wireOp",EDGE,"E5605"),sQuery(id+"F0.wireOp",EDGE,"E5606"),sQuery(id+"F0.wireOp",EDGE,"E5607"),sQuery(id+"F0.wireOp",EDGE,"E5608"),sQuery(id+"F0.wireOp",EDGE,"E5609"),sQuery(id+"F0.wireOp",EDGE,"E5610"),sQuery(id+"F0.wireOp",EDGE,"E5611"),sQuery(id+"F0.wireOp",EDGE,"E5612"),sQuery(id+"F0.wireOp",EDGE,"E5613"),sQuery(id+"F0.wireOp",EDGE,"E5614"),sQuery(id+"F0.wireOp",EDGE,"E5615"),sQuery(id+"F0.wireOp",EDGE,"E5616"),sQuery(id+"F0.wireOp",EDGE,"E5617"),sQuery(id+"F0.wireOp",EDGE,"E5618"),sQuery(id+"F0.wireOp",EDGE,"E5619"),sQuery(id+"F0.wireOp",EDGE,"E5620"),sQuery(id+"F0.wireOp",EDGE,"E5621"),sQuery(id+"F0.wireOp",EDGE,"E5622"),sQuery(id+"F0.wireOp",EDGE,"E5623"),sQuery(id+"F0.wireOp",EDGE,"E5624"),sQuery(id+"F0.wireOp",EDGE,"E5625"),sQuery(id+"F0.wireOp",EDGE,"E5626"),sQuery(id+"F0.wireOp",EDGE,"E5627"),sQuery(id+"F0.wireOp",EDGE,"E5628"),sQuery(id+"F0.wireOp",EDGE,"E5629"),sQuery(id+"F0.wireOp",EDGE,"E5630"),sQuery(id+"F0.wireOp",EDGE,"E5631"),sQuery(id+"F0.wireOp",EDGE,"E5632"),sQuery(id+"F0.wireOp",EDGE,"E5633"),sQuery(id+"F0.wireOp",EDGE,"E5634"),sQuery(id+"F0.wireOp",EDGE,"E5635"),sQuery(id+"F0.wireOp",EDGE,"E5636"),sQuery(id+"F0.wireOp",EDGE,"E5637"),sQuery(id+"F0.wireOp",EDGE,"E5638"),sQuery(id+"F0.wireOp",EDGE,"E5639"),sQuery(id+"F0.wireOp",EDGE,"E5640"),sQuery(id+"F0.wireOp",EDGE,"E5641"),sQuery(id+"F0.wireOp",EDGE,"E5642"),sQuery(id+"F0.wireOp",EDGE,"E5643"),sQuery(id+"F0.wireOp",EDGE,"E5644"),sQuery(id+"F0.wireOp",EDGE,"E5645"),sQuery(id+"F0.wireOp",EDGE,"E5646"),sQuery(id+"F0.wireOp",EDGE,"E5647"),sQuery(id+"F0.wireOp",EDGE,"E5648"),sQuery(id+"F0.wireOp",EDGE,"E5649"),sQuery(id+"F0.wireOp",EDGE,"E5650"),sQuery(id+"F0.wireOp",EDGE,"E5651"),sQuery(id+"F0.wireOp",EDGE,"E5652"),sQuery(id+"F0.wireOp",EDGE,"E5653"),sQuery(id+"F0.wireOp",EDGE,"E5654"),sQuery(id+"F0.wireOp",EDGE,"E5655"),sQuery(id+"F0.wireOp",EDGE,"E5656"),sQuery(id+"F0.wireOp",EDGE,"E5657"),sQuery(id+"F0.wireOp",EDGE,"E5658"),sQuery(id+"F0.wireOp",EDGE,"E5659"),sQuery(id+"F0.wireOp",EDGE,"E5660"),sQuery(id+"F0.wireOp",EDGE,"E5661"),sQuery(id+"F0.wireOp",EDGE,"E5662"),sQuery(id+"F0.wireOp",EDGE,"E5663"),sQuery(id+"F0.wireOp",EDGE,"E5664"),sQuery(id+"F0.wireOp",EDGE,"E5665"),sQuery(id+"F0.wireOp",EDGE,"E5666"),sQuery(id+"F0.wireOp",EDGE,"E5667"),sQuery(id+"F0.wireOp",EDGE,"E5668"),sQuery(id+"F0.wireOp",EDGE,"E5669"),sQuery(id+"F0.wireOp",EDGE,"E5670"),sQuery(id+"F0.wireOp",EDGE,"E5671"),sQuery(id+"F0.wireOp",EDGE,"E5672"),sQuery(id+"F0.wireOp",EDGE,"E5673"),sQuery(id+"F0.wireOp",EDGE,"E5674"),sQuery(id+"F0.wireOp",EDGE,"E5675"),sQuery(id+"F0.wireOp",EDGE,"E5676"),sQuery(id+"F0.wireOp",EDGE,"E5677"),sQuery(id+"F0.wireOp",EDGE,"E5678"),sQuery(id+"F0.wireOp",EDGE,"E5679"),sQuery(id+"F0.wireOp",EDGE,"E5680"),sQuery(id+"F0.wireOp",EDGE,"E5681"),sQuery(id+"F0.wireOp",EDGE,"E5682"),sQuery(id+"F0.wireOp",EDGE,"E5683"),sQuery(id+"F0.wireOp",EDGE,"E5684"),sQuery(id+"F0.wireOp",EDGE,"E5685"),sQuery(id+"F0.wireOp",EDGE,"E5686"),sQuery(id+"F0.wireOp",EDGE,"E5687"),sQuery(id+"F0.wireOp",EDGE,"E5688"),sQuery(id+"F0.wireOp",EDGE,"E5689"),sQuery(id+"F0.wireOp",EDGE,"E5690"),sQuery(id+"F0.wireOp",EDGE,"E5691"),sQuery(id+"F0.wireOp",EDGE,"E5692"),sQuery(id+"F0.wireOp",EDGE,"E5693"),sQuery(id+"F0.wireOp",EDGE,"E5694"),sQuery(id+"F0.wireOp",EDGE,"E5695"),sQuery(id+"F0.wireOp",EDGE,"E5696"),sQuery(id+"F0.wireOp",EDGE,"E5697"),sQuery(id+"F0.wireOp",EDGE,"E5698"),sQuery(id+"F0.wireOp",EDGE,"E5699"),sQuery(id+"F0.wireOp",EDGE,"E5700"),sQuery(id+"F0.wireOp",EDGE,"E5701"),sQuery(id+"F0.wireOp",EDGE,"E5702"),sQuery(id+"F0.wireOp",EDGE,"E5703"),sQuery(id+"F0.wireOp",EDGE,"E5704"),sQuery(id+"F0.wireOp",EDGE,"E5705"),sQuery(id+"F0.wireOp",EDGE,"E5706"),sQuery(id+"F0.wireOp",EDGE,"E5707"),sQuery(id+"F0.wireOp",EDGE,"E5708"),sQuery(id+"F0.wireOp",EDGE,"E5709"),sQuery(id+"F0.wireOp",EDGE,"E5710"),sQuery(id+"F0.wireOp",EDGE,"E5711"),sQuery(id+"F0.wireOp",EDGE,"E5712"),sQuery(id+"F0.wireOp",EDGE,"E5713"),sQuery(id+"F0.wireOp",EDGE,"E5714"),sQuery(id+"F0.wireOp",EDGE,"E5715"),sQuery(id+"F0.wireOp",EDGE,"E5716"),sQuery(id+"F0.wireOp",EDGE,"E5717"),sQuery(id+"F0.wireOp",EDGE,"E5718"),sQuery(id+"F0.wireOp",EDGE,"E5719"),sQuery(id+"F0.wireOp",EDGE,"E5720"),sQuery(id+"F0.wireOp",EDGE,"E5721"),sQuery(id+"F0.wireOp",EDGE,"E5722"),sQuery(id+"F0.wireOp",EDGE,"E5723"),sQuery(id+"F0.wireOp",EDGE,"E5724"),sQuery(id+"F0.wireOp",EDGE,"E5725"),sQuery(id+"F0.wireOp",EDGE,"E5726"),sQuery(id+"F0.wireOp",EDGE,"E5727"),sQuery(id+"F0.wireOp",EDGE,"E5728"),sQuery(id+"F0.wireOp",EDGE,"E5729"),sQuery(id+"F0.wireOp",EDGE,"E5730"),sQuery(id+"F0.wireOp",EDGE,"E5731"),sQuery(id+"F0.wireOp",EDGE,"E5732"),sQuery(id+"F0.wireOp",EDGE,"E5733"),sQuery(id+"F0.wireOp",EDGE,"E5734"),sQuery(id+"F0.wireOp",EDGE,"E5735"),sQuery(id+"F0.wireOp",EDGE,"E5736"),sQuery(id+"F0.wireOp",EDGE,"E5737"),sQuery(id+"F0.wireOp",EDGE,"E5738"),sQuery(id+"F0.wireOp",EDGE,"E5739"),sQuery(id+"F0.wireOp",EDGE,"E5740"),sQuery(id+"F0.wireOp",EDGE,"E5741"),sQuery(id+"F0.wireOp",EDGE,"E5742"),sQuery(id+"F0.wireOp",EDGE,"E5743"),sQuery(id+"F0.wireOp",EDGE,"E5744"),sQuery(id+"F0.wireOp",EDGE,"E5745"),sQuery(id+"F0.wireOp",EDGE,"E5746"),sQuery(id+"F0.wireOp",EDGE,"E5747"),sQuery(id+"F0.wireOp",EDGE,"E5748"),sQuery(id+"F0.wireOp",EDGE,"E5749"),sQuery(id+"F0.wireOp",EDGE,"E5750"),sQuery(id+"F0.wireOp",EDGE,"E5751"),sQuery(id+"F0.wireOp",EDGE,"E5752"),sQuery(id+"F0.wireOp",EDGE,"E5753"),sQuery(id+"F0.wireOp",EDGE,"E5754"),sQuery(id+"F0.wireOp",EDGE,"E5755"),sQuery(id+"F0.wireOp",EDGE,"E5756"),sQuery(id+"F0.wireOp",EDGE,"E5757"),sQuery(id+"F0.wireOp",EDGE,"E5758"),sQuery(id+"F0.wireOp",EDGE,"E5759"),sQuery(id+"F0.wireOp",EDGE,"E5760"),sQuery(id+"F0.wireOp",EDGE,"E5761"),sQuery(id+"F0.wireOp",EDGE,"E5762"),sQuery(id+"F0.wireOp",EDGE,"E5763"),sQuery(id+"F0.wireOp",EDGE,"E5764"),sQuery(id+"F0.wireOp",EDGE,"E5765"),sQuery(id+"F0.wireOp",EDGE,"E5766"),sQuery(id+"F0.wireOp",EDGE,"E5767"),sQuery(id+"F0.wireOp",EDGE,"E5768"),sQuery(id+"F0.wireOp",EDGE,"E5769"),sQuery(id+"F0.wireOp",EDGE,"E5770"),sQuery(id+"F0.wireOp",EDGE,"E5771"),sQuery(id+"F0.wireOp",EDGE,"E5772"),sQuery(id+"F0.wireOp",EDGE,"E5773"),sQuery(id+"F0.wireOp",EDGE,"E5774"),sQuery(id+"F0.wireOp",EDGE,"E5775"),sQuery(id+"F0.wireOp",EDGE,"E5776"),sQuery(id+"F0.wireOp",EDGE,"E5777"),sQuery(id+"F0.wireOp",EDGE,"E5778"),sQuery(id+"F0.wireOp",EDGE,"E5779"),sQuery(id+"F0.wireOp",EDGE,"E5780"),sQuery(id+"F0.wireOp",EDGE,"E5781"),sQuery(id+"F0.wireOp",EDGE,"E5782"),sQuery(id+"F0.wireOp",EDGE,"E5783"),sQuery(id+"F0.wireOp",EDGE,"E5784"),sQuery(id+"F0.wireOp",EDGE,"E5785"),sQuery(id+"F0.wireOp",EDGE,"E5786"),sQuery(id+"F0.wireOp",EDGE,"E5787"),sQuery(id+"F0.wireOp",EDGE,"E5788"),sQuery(id+"F0.wireOp",EDGE,"E5789"),sQuery(id+"F0.wireOp",EDGE,"E5790"),sQuery(id+"F0.wireOp",EDGE,"E5791"),sQuery(id+"F0.wireOp",EDGE,"E5792"),sQuery(id+"F0.wireOp",EDGE,"E5793"),sQuery(id+"F0.wireOp",EDGE,"E5794"),sQuery(id+"F0.wireOp",EDGE,"E5795"),sQuery(id+"F0.wireOp",EDGE,"E5796"),sQuery(id+"F0.wireOp",EDGE,"E5797"),sQuery(id+"F0.wireOp",EDGE,"E5798"),sQuery(id+"F0.wireOp",EDGE,"E5799"),sQuery(id+"F0.wireOp",EDGE,"E5800"),sQuery(id+"F0.wireOp",EDGE,"E5801"),sQuery(id+"F0.wireOp",EDGE,"E5802"),sQuery(id+"F0.wireOp",EDGE,"E5803"),sQuery(id+"F0.wireOp",EDGE,"E5804"),sQuery(id+"F0.wireOp",EDGE,"E5805"),sQuery(id+"F0.wireOp",EDGE,"E5806"),sQuery(id+"F0.wireOp",EDGE,"E5807"),sQuery(id+"F0.wireOp",EDGE,"E5808"),sQuery(id+"F0.wireOp",EDGE,"E5809"),sQuery(id+"F0.wireOp",EDGE,"E5810"),sQuery(id+"F0.wireOp",EDGE,"E5811"),sQuery(id+"F0.wireOp",EDGE,"E5812"),sQuery(id+"F0.wireOp",EDGE,"E5813"),sQuery(id+"F0.wireOp",EDGE,"E5814"),sQuery(id+"F0.wireOp",EDGE,"E5815"),sQuery(id+"F0.wireOp",EDGE,"E5816"),sQuery(id+"F0.wireOp",EDGE,"E5817"),sQuery(id+"F0.wireOp",EDGE,"E5818"),sQuery(id+"F0.wireOp",EDGE,"E5819"),sQuery(id+"F0.wireOp",EDGE,"E5820"),sQuery(id+"F0.wireOp",EDGE,"E5821"),sQuery(id+"F0.wireOp",EDGE,"E5822"),sQuery(id+"F0.wireOp",EDGE,"E5823"),sQuery(id+"F0.wireOp",EDGE,"E5824"),sQuery(id+"F0.wireOp",EDGE,"E5825"),sQuery(id+"F0.wireOp",EDGE,"E5826"),sQuery(id+"F0.wireOp",EDGE,"E5827"),sQuery(id+"F0.wireOp",EDGE,"E5828"),sQuery(id+"F0.wireOp",EDGE,"E5829"),sQuery(id+"F0.wireOp",EDGE,"E5830"),sQuery(id+"F0.wireOp",EDGE,"E5831"),sQuery(id+"F0.wireOp",EDGE,"E5832"),sQuery(id+"F0.wireOp",EDGE,"E5833"),sQuery(id+"F0.wireOp",EDGE,"E5834"),sQuery(id+"F0.wireOp",EDGE,"E5835"),sQuery(id+"F0.wireOp",EDGE,"E5836"),sQuery(id+"F0.wireOp",EDGE,"E5837"),sQuery(id+"F0.wireOp",EDGE,"E5838"),sQuery(id+"F0.wireOp",EDGE,"E5839"),sQuery(id+"F0.wireOp",EDGE,"E5840"),sQuery(id+"F0.wireOp",EDGE,"E5841"),sQuery(id+"F0.wireOp",EDGE,"E5842"),sQuery(id+"F0.wireOp",EDGE,"E5843"),sQuery(id+"F0.wireOp",EDGE,"E5844"),sQuery(id+"F0.wireOp",EDGE,"E5845"),sQuery(id+"F0.wireOp",EDGE,"E5846"),sQuery(id+"F0.wireOp",EDGE,"E5847"),sQuery(id+"F0.wireOp",EDGE,"E5848"),sQuery(id+"F0.wireOp",EDGE,"E5849"),sQuery(id+"F0.wireOp",EDGE,"E5850"),sQuery(id+"F0.wireOp",EDGE,"E5851"),sQuery(id+"F0.wireOp",EDGE,"E5852"),sQuery(id+"F0.wireOp",EDGE,"E5853"),sQuery(id+"F0.wireOp",EDGE,"E5854"),sQuery(id+"F0.wireOp",EDGE,"E5855"),sQuery(id+"F0.wireOp",EDGE,"E5856"),sQuery(id+"F0.wireOp",EDGE,"E5857"),sQuery(id+"F0.wireOp",EDGE,"E5858"),sQuery(id+"F0.wireOp",EDGE,"E5859"),sQuery(id+"F0.wireOp",EDGE,"E5860"),sQuery(id+"F0.wireOp",EDGE,"E5861"),sQuery(id+"F0.wireOp",EDGE,"E5862"),sQuery(id+"F0.wireOp",EDGE,"E5863"),sQuery(id+"F0.wireOp",EDGE,"E5864"),sQuery(id+"F0.wireOp",EDGE,"E5865"),sQuery(id+"F0.wireOp",EDGE,"E5866"),sQuery(id+"F0.wireOp",EDGE,"E5867"),sQuery(id+"F0.wireOp",EDGE,"E5868"),sQuery(id+"F0.wireOp",EDGE,"E5869"),sQuery(id+"F0.wireOp",EDGE,"E5870"),sQuery(id+"F0.wireOp",EDGE,"E5871"),sQuery(id+"F0.wireOp",EDGE,"E5872"),sQuery(id+"F0.wireOp",EDGE,"E5873"),sQuery(id+"F0.wireOp",EDGE,"E5874"),sQuery(id+"F0.wireOp",EDGE,"E5875"),sQuery(id+"F0.wireOp",EDGE,"E5876"),sQuery(id+"F0.wireOp",EDGE,"E5877"),sQuery(id+"F0.wireOp",EDGE,"E5878"),sQuery(id+"F0.wireOp",EDGE,"E5879"),sQuery(id+"F0.wireOp",EDGE,"E5880"),sQuery(id+"F0.wireOp",EDGE,"E5881"),sQuery(id+"F0.wireOp",EDGE,"E5882"),sQuery(id+"F0.wireOp",EDGE,"E5883"),sQuery(id+"F0.wireOp",EDGE,"E5884"),sQuery(id+"F0.wireOp",EDGE,"E5885"),sQuery(id+"F0.wireOp",EDGE,"E5886"),sQuery(id+"F0.wireOp",EDGE,"E5887"),sQuery(id+"F0.wireOp",EDGE,"E5888"),sQuery(id+"F0.wireOp",EDGE,"E5889"),sQuery(id+"F0.wireOp",EDGE,"E5890"),sQuery(id+"F0.wireOp",EDGE,"E5891"),sQuery(id+"F0.wireOp",EDGE,"E5892"),sQuery(id+"F0.wireOp",EDGE,"E5893"),sQuery(id+"F0.wireOp",EDGE,"E5894"),sQuery(id+"F0.wireOp",EDGE,"E5895"),sQuery(id+"F0.wireOp",EDGE,"E5896"),sQuery(id+"F0.wireOp",EDGE,"E5897"),sQuery(id+"F0.wireOp",EDGE,"E5898"),sQuery(id+"F0.wireOp",EDGE,"E5899"),sQuery(id+"F0.wireOp",EDGE,"E5900"),sQuery(id+"F0.wireOp",EDGE,"E5901"),sQuery(id+"F0.wireOp",EDGE,"E5902"),sQuery(id+"F0.wireOp",EDGE,"E5903"),sQuery(id+"F0.wireOp",EDGE,"E5904"),sQuery(id+"F0.wireOp",EDGE,"E5905"),sQuery(id+"F0.wireOp",EDGE,"E5906"),sQuery(id+"F0.wireOp",EDGE,"E5907"),sQuery(id+"F0.wireOp",EDGE,"E5908"),sQuery(id+"F0.wireOp",EDGE,"E5909"),sQuery(id+"F0.wireOp",EDGE,"E5910"),sQuery(id+"F0.wireOp",EDGE,"E5911"),sQuery(id+"F0.wireOp",EDGE,"E5912"),sQuery(id+"F0.wireOp",EDGE,"E5913"),sQuery(id+"F0.wireOp",EDGE,"E5914"),sQuery(id+"F0.wireOp",EDGE,"E5915"),sQuery(id+"F0.wireOp",EDGE,"E5916"),sQuery(id+"F0.wireOp",EDGE,"E5917"),sQuery(id+"F0.wireOp",EDGE,"E5918"),sQuery(id+"F0.wireOp",EDGE,"E5919"),sQuery(id+"F0.wireOp",EDGE,"E5920"),sQuery(id+"F0.wireOp",EDGE,"E5921"),sQuery(id+"F0.wireOp",EDGE,"E5922"),sQuery(id+"F0.wireOp",EDGE,"E5923"),sQuery(id+"F0.wireOp",EDGE,"E5924"),sQuery(id+"F0.wireOp",EDGE,"E5925"),sQuery(id+"F0.wireOp",EDGE,"E5926"),sQuery(id+"F0.wireOp",EDGE,"E5927"),sQuery(id+"F0.wireOp",EDGE,"E5928"),sQuery(id+"F0.wireOp",EDGE,"E5929"),sQuery(id+"F0.wireOp",EDGE,"E5930"),sQuery(id+"F0.wireOp",EDGE,"E5931"),sQuery(id+"F0.wireOp",EDGE,"E5932"),sQuery(id+"F0.wireOp",EDGE,"E5933"),sQuery(id+"F0.wireOp",EDGE,"E5934"),sQuery(id+"F0.wireOp",EDGE,"E5935"),sQuery(id+"F0.wireOp",EDGE,"E5936"),sQuery(id+"F0.wireOp",EDGE,"E5937"),sQuery(id+"F0.wireOp",EDGE,"E5938"),sQuery(id+"F0.wireOp",EDGE,"E5939"),sQuery(id+"F0.wireOp",EDGE,"E5940"),sQuery(id+"F0.wireOp",EDGE,"E5941"),sQuery(id+"F0.wireOp",EDGE,"E5942"),sQuery(id+"F0.wireOp",EDGE,"E5943"),sQuery(id+"F0.wireOp",EDGE,"E5944"),sQuery(id+"F0.wireOp",EDGE,"E5945"),sQuery(id+"F0.wireOp",EDGE,"E5946"),sQuery(id+"F0.wireOp",EDGE,"E5947"),sQuery(id+"F0.wireOp",EDGE,"E5948"),sQuery(id+"F0.wireOp",EDGE,"E5949"),sQuery(id+"F0.wireOp",EDGE,"E5950"),sQuery(id+"F0.wireOp",EDGE,"E5951"),sQuery(id+"F0.wireOp",EDGE,"E5952"),sQuery(id+"F0.wireOp",EDGE,"E5953"),sQuery(id+"F0.wireOp",EDGE,"E5954"),sQuery(id+"F0.wireOp",EDGE,"E5955"),sQuery(id+"F0.wireOp",EDGE,"E5956"),sQuery(id+"F0.wireOp",EDGE,"E5957"),sQuery(id+"F0.wireOp",EDGE,"E5958"),sQuery(id+"F0.wireOp",EDGE,"E5959"),sQuery(id+"F0.wireOp",EDGE,"E5960"),sQuery(id+"F0.wireOp",EDGE,"E5961"),sQuery(id+"F0.wireOp",EDGE,"E5962"),sQuery(id+"F0.wireOp",EDGE,"E5963"),sQuery(id+"F0.wireOp",EDGE,"E5964"),sQuery(id+"F0.wireOp",EDGE,"E5965"),sQuery(id+"F0.wireOp",EDGE,"E5966"),sQuery(id+"F0.wireOp",EDGE,"E5967"),sQuery(id+"F0.wireOp",EDGE,"E5968"),sQuery(id+"F0.wireOp",EDGE,"E5969"),sQuery(id+"F0.wireOp",EDGE,"E5970"),sQuery(id+"F0.wireOp",EDGE,"E5971"),sQuery(id+"F0.wireOp",EDGE,"E5972"),sQuery(id+"F0.wireOp",EDGE,"E5973"),sQuery(id+"F0.wireOp",EDGE,"E5974"),sQuery(id+"F0.wireOp",EDGE,"E5975"),sQuery(id+"F0.wireOp",EDGE,"E5976"),sQuery(id+"F0.wireOp",EDGE,"E5977"),sQuery(id+"F0.wireOp",EDGE,"E5978"),sQuery(id+"F0.wireOp",EDGE,"E5979"),sQuery(id+"F0.wireOp",EDGE,"E5980"),sQuery(id+"F0.wireOp",EDGE,"E5981"),sQuery(id+"F0.wireOp",EDGE,"E5982"),sQuery(id+"F0.wireOp",EDGE,"E5983"),sQuery(id+"F0.wireOp",EDGE,"E5984"),sQuery(id+"F0.wireOp",EDGE,"E5985"),sQuery(id+"F0.wireOp",EDGE,"E5986"),sQuery(id+"F0.wireOp",EDGE,"E5987"),sQuery(id+"F0.wireOp",EDGE,"E5988"),sQuery(id+"F0.wireOp",EDGE,"E5989"),sQuery(id+"F0.wireOp",EDGE,"E5990"),sQuery(id+"F0.wireOp",EDGE,"E5991"),sQuery(id+"F0.wireOp",EDGE,"E5992"),sQuery(id+"F0.wireOp",EDGE,"E5993"),sQuery(id+"F0.wireOp",EDGE,"E5994"),sQuery(id+"F0.wireOp",EDGE,"E5995"),sQuery(id+"F0.wireOp",EDGE,"E5996"),sQuery(id+"F0.wireOp",EDGE,"E5997"),sQuery(id+"F0.wireOp",EDGE,"E5998"),sQuery(id+"F0.wireOp",EDGE,"E5999"),sQuery(id+"F0.wireOp",EDGE,"E6000"),sQuery(id+"F0.wireOp",EDGE,"E6001"),sQuery(id+"F0.wireOp",EDGE,"E6002"),sQuery(id+"F0.wireOp",EDGE,"E6003"),sQuery(id+"F0.wireOp",EDGE,"E6004"),sQuery(id+"F0.wireOp",EDGE,"E6005"),sQuery(id+"F0.wireOp",EDGE,"E6006"),sQuery(id+"F0.wireOp",EDGE,"E6007"),sQuery(id+"F0.wireOp",EDGE,"E6008"),sQuery(id+"F0.wireOp",EDGE,"E6009"),sQuery(id+"F0.wireOp",EDGE,"E6010"),sQuery(id+"F0.wireOp",EDGE,"E6011"),sQuery(id+"F0.wireOp",EDGE,"E6012"),sQuery(id+"F0.wireOp",EDGE,"E6013"),sQuery(id+"F0.wireOp",EDGE,"E6014"),sQuery(id+"F0.wireOp",EDGE,"E6015"),sQuery(id+"F0.wireOp",EDGE,"E6016"),sQuery(id+"F0.wireOp",EDGE,"E6017"),sQuery(id+"F0.wireOp",EDGE,"E6018"),sQuery(id+"F0.wireOp",EDGE,"E6019"),sQuery(id+"F0.wireOp",EDGE,"E6020"),sQuery(id+"F0.wireOp",EDGE,"E6021"),sQuery(id+"F0.wireOp",EDGE,"E6022"),sQuery(id+"F0.wireOp",EDGE,"E6023"),sQuery(id+"F0.wireOp",EDGE,"E6024"),sQuery(id+"F0.wireOp",EDGE,"E6025"),sQuery(id+"F0.wireOp",EDGE,"E6026"),sQuery(id+"F0.wireOp",EDGE,"E6027"),sQuery(id+"F0.wireOp",EDGE,"E6028"),sQuery(id+"F0.wireOp",EDGE,"E6029"),sQuery(id+"F0.wireOp",EDGE,"E6030"),sQuery(id+"F0.wireOp",EDGE,"E6031"),sQuery(id+"F0.wireOp",EDGE,"E6032"),sQuery(id+"F0.wireOp",EDGE,"E6033"),sQuery(id+"F0.wireOp",EDGE,"E6034"),sQuery(id+"F0.wireOp",EDGE,"E6035"),sQuery(id+"F0.wireOp",EDGE,"E6036"),sQuery(id+"F0.wireOp",EDGE,"E6037"),sQuery(id+"F0.wireOp",EDGE,"E6038"),sQuery(id+"F0.wireOp",EDGE,"E6039"),sQuery(id+"F0.wireOp",EDGE,"E6040"),sQuery(id+"F0.wireOp",EDGE,"E6041"),sQuery(id+"F0.wireOp",EDGE,"E6042"),sQuery(id+"F0.wireOp",EDGE,"E6043"),sQuery(id+"F0.wireOp",EDGE,"E6044"),sQuery(id+"F0.wireOp",EDGE,"E6045"),sQuery(id+"F0.wireOp",EDGE,"E6046"),sQuery(id+"F0.wireOp",EDGE,"E6047"),sQuery(id+"F0.wireOp",EDGE,"E6048"),sQuery(id+"F0.wireOp",EDGE,"E6049"),sQuery(id+"F0.wireOp",EDGE,"E6050"),sQuery(id+"F0.wireOp",EDGE,"E6051"),sQuery(id+"F0.wireOp",EDGE,"E6052"),sQuery(id+"F0.wireOp",EDGE,"E6053"),sQuery(id+"F0.wireOp",EDGE,"E6054"),sQuery(id+"F0.wireOp",EDGE,"E6055"),sQuery(id+"F0.wireOp",EDGE,"E6056"),sQuery(id+"F0.wireOp",EDGE,"E6057"),sQuery(id+"F0.wireOp",EDGE,"E6058"),sQuery(id+"F0.wireOp",EDGE,"E6059"),sQuery(id+"F0.wireOp",EDGE,"E6060"),sQuery(id+"F0.wireOp",EDGE,"E6061"),sQuery(id+"F0.wireOp",EDGE,"E6062"),sQuery(id+"F0.wireOp",EDGE,"E6063"),sQuery(id+"F0.wireOp",EDGE,"E6064"),sQuery(id+"F0.wireOp",EDGE,"E6065"),sQuery(id+"F0.wireOp",EDGE,"E6066"),sQuery(id+"F0.wireOp",EDGE,"E6067"),sQuery(id+"F0.wireOp",EDGE,"E6068"),sQuery(id+"F0.wireOp",EDGE,"E6069"),sQuery(id+"F0.wireOp",EDGE,"E6070"),sQuery(id+"F0.wireOp",EDGE,"E6071"),sQuery(id+"F0.wireOp",EDGE,"E6072"),sQuery(id+"F0.wireOp",EDGE,"E6073"),sQuery(id+"F0.wireOp",EDGE,"E6074"),sQuery(id+"F0.wireOp",EDGE,"E6075"),sQuery(id+"F0.wireOp",EDGE,"E6076"),sQuery(id+"F0.wireOp",EDGE,"E6077"),sQuery(id+"F0.wireOp",EDGE,"E6078"),sQuery(id+"F0.wireOp",EDGE,"E6079"),sQuery(id+"F0.wireOp",EDGE,"E6080"),sQuery(id+"F0.wireOp",EDGE,"E6081"),sQuery(id+"F0.wireOp",EDGE,"E6082"),sQuery(id+"F0.wireOp",EDGE,"E6083"),sQuery(id+"F0.wireOp",EDGE,"E6084"),sQuery(id+"F0.wireOp",EDGE,"E6085"),sQuery(id+"F0.wireOp",EDGE,"E6086"),sQuery(id+"F0.wireOp",EDGE,"E6087"),sQuery(id+"F0.wireOp",EDGE,"E6088"),sQuery(id+"F0.wireOp",EDGE,"E6089"),sQuery(id+"F0.wireOp",EDGE,"E6090"),sQuery(id+"F0.wireOp",EDGE,"E6091"),sQuery(id+"F0.wireOp",EDGE,"E6092"),sQuery(id+"F0.wireOp",EDGE,"E6093"),sQuery(id+"F0.wireOp",EDGE,"E6094"),sQuery(id+"F0.wireOp",EDGE,"E6095"),sQuery(id+"F0.wireOp",EDGE,"E6096"),sQuery(id+"F0.wireOp",EDGE,"E6097"),sQuery(id+"F0.wireOp",EDGE,"E6098"),sQuery(id+"F0.wireOp",EDGE,"E6099"),sQuery(id+"F0.wireOp",EDGE,"E6100"),sQuery(id+"F0.wireOp",EDGE,"E6101"),sQuery(id+"F0.wireOp",EDGE,"E6102"),sQuery(id+"F0.wireOp",EDGE,"E6103"),sQuery(id+"F0.wireOp",EDGE,"E6104"),sQuery(id+"F0.wireOp",EDGE,"E6105"),sQuery(id+"F0.wireOp",EDGE,"E6106"),sQuery(id+"F0.wireOp",EDGE,"E6107"),sQuery(id+"F0.wireOp",EDGE,"E6108"),sQuery(id+"F0.wireOp",EDGE,"E6109"),sQuery(id+"F0.wireOp",EDGE,"E6110"),sQuery(id+"F0.wireOp",EDGE,"E6111"),sQuery(id+"F0.wireOp",EDGE,"E6112"),sQuery(id+"F0.wireOp",EDGE,"E6113"),sQuery(id+"F0.wireOp",EDGE,"E6114"),sQuery(id+"F0.wireOp",EDGE,"E6115"),sQuery(id+"F0.wireOp",EDGE,"E6116"),sQuery(id+"F0.wireOp",EDGE,"E6117"),sQuery(id+"F0.wireOp",EDGE,"E6118"),sQuery(id+"F0.wireOp",EDGE,"E6119"),sQuery(id+"F0.wireOp",EDGE,"E6120"),sQuery(id+"F0.wireOp",EDGE,"E6121"),sQuery(id+"F0.wireOp",EDGE,"E6122"),sQuery(id+"F0.wireOp",EDGE,"E6123"),sQuery(id+"F0.wireOp",EDGE,"E6124"),sQuery(id+"F0.wireOp",EDGE,"E6125"),sQuery(id+"F0.wireOp",EDGE,"E6126"),sQuery(id+"F0.wireOp",EDGE,"E6127"),sQuery(id+"F0.wireOp",EDGE,"E6128"),sQuery(id+"F0.wireOp",EDGE,"E6129"),sQuery(id+"F0.wireOp",EDGE,"E6130"),sQuery(id+"F0.wireOp",EDGE,"E6131"),sQuery(id+"F0.wireOp",EDGE,"E6132"),sQuery(id+"F0.wireOp",EDGE,"E6133"),sQuery(id+"F0.wireOp",EDGE,"E6134"),sQuery(id+"F0.wireOp",EDGE,"E6135"),sQuery(id+"F0.wireOp",EDGE,"E6136"),sQuery(id+"F0.wireOp",EDGE,"E6137"),sQuery(id+"F0.wireOp",EDGE,"E6138"),sQuery(id+"F0.wireOp",EDGE,"E6139"),sQuery(id+"F0.wireOp",EDGE,"E6140"),sQuery(id+"F0.wireOp",EDGE,"E6141"),sQuery(id+"F0.wireOp",EDGE,"E6142"),sQuery(id+"F0.wireOp",EDGE,"E6143"),sQuery(id+"F0.wireOp",EDGE,"E6144"),sQuery(id+"F0.wireOp",EDGE,"E6145"),sQuery(id+"F0.wireOp",EDGE,"E6146"),sQuery(id+"F0.wireOp",EDGE,"E6147"),sQuery(id+"F0.wireOp",EDGE,"E6148"),sQuery(id+"F0.wireOp",EDGE,"E6149"),sQuery(id+"F0.wireOp",EDGE,"E6150"),sQuery(id+"F0.wireOp",EDGE,"E6151"),sQuery(id+"F0.wireOp",EDGE,"E6152"),sQuery(id+"F0.wireOp",EDGE,"E6153"),sQuery(id+"F0.wireOp",EDGE,"E6154"),sQuery(id+"F0.wireOp",EDGE,"E6155"),sQuery(id+"F0.wireOp",EDGE,"E6156"),sQuery(id+"F0.wireOp",EDGE,"E6157"),sQuery(id+"F0.wireOp",EDGE,"E6158"),sQuery(id+"F0.wireOp",EDGE,"E6159"),sQuery(id+"F0.wireOp",EDGE,"E6160"),sQuery(id+"F0.wireOp",EDGE,"E6161"),sQuery(id+"F0.wireOp",EDGE,"E6162"),sQuery(id+"F0.wireOp",EDGE,"E6163"),sQuery(id+"F0.wireOp",EDGE,"E6164"),sQuery(id+"F0.wireOp",EDGE,"E6165"),sQuery(id+"F0.wireOp",EDGE,"E6166"),sQuery(id+"F0.wireOp",EDGE,"E6167"),sQuery(id+"F0.wireOp",EDGE,"E6168"),sQuery(id+"F0.wireOp",EDGE,"E6169"),sQuery(id+"F0.wireOp",EDGE,"E6170"),sQuery(id+"F0.wireOp",EDGE,"E6171"),sQuery(id+"F0.wireOp",EDGE,"E6172"),sQuery(id+"F0.wireOp",EDGE,"E6173"),sQuery(id+"F0.wireOp",EDGE,"E6174"),sQuery(id+"F0.wireOp",EDGE,"E6175"),sQuery(id+"F0.wireOp",EDGE,"E6176"),sQuery(id+"F0.wireOp",EDGE,"E6177"),sQuery(id+"F0.wireOp",EDGE,"E6178"),sQuery(id+"F0.wireOp",EDGE,"E6179"),sQuery(id+"F0.wireOp",EDGE,"E6180"),sQuery(id+"F0.wireOp",EDGE,"E6181"),sQuery(id+"F0.wireOp",EDGE,"E6182"),sQuery(id+"F0.wireOp",EDGE,"E6183"),sQuery(id+"F0.wireOp",EDGE,"E6184"),sQuery(id+"F0.wireOp",EDGE,"E6185"),sQuery(id+"F0.wireOp",EDGE,"E6186"),sQuery(id+"F0.wireOp",EDGE,"E6187"),sQuery(id+"F0.wireOp",EDGE,"E6188"),sQuery(id+"F0.wireOp",EDGE,"E6189"),sQuery(id+"F0.wireOp",EDGE,"E6190"),sQuery(id+"F0.wireOp",EDGE,"E6191"),sQuery(id+"F0.wireOp",EDGE,"E6192"),sQuery(id+"F0.wireOp",EDGE,"E6193"),sQuery(id+"F0.wireOp",EDGE,"E6194"),sQuery(id+"F0.wireOp",EDGE,"E6195"),sQuery(id+"F0.wireOp",EDGE,"E6196"),sQuery(id+"F0.wireOp",EDGE,"E6197"),sQuery(id+"F0.wireOp",EDGE,"E6198"),sQuery(id+"F0.wireOp",EDGE,"E6199"),sQuery(id+"F0.wireOp",EDGE,"E6200"),sQuery(id+"F0.wireOp",EDGE,"E6201"),sQuery(id+"F0.wireOp",EDGE,"E6202"),sQuery(id+"F0.wireOp",EDGE,"E6203"),sQuery(id+"F0.wireOp",EDGE,"E6204"),sQuery(id+"F0.wireOp",EDGE,"E6205"),sQuery(id+"F0.wireOp",EDGE,"E6206"),sQuery(id+"F0.wireOp",EDGE,"E6207"),sQuery(id+"F0.wireOp",EDGE,"E6208"),sQuery(id+"F0.wireOp",EDGE,"E6209"),sQuery(id+"F0.wireOp",EDGE,"E6210"),sQuery(id+"F0.wireOp",EDGE,"E6211"),sQuery(id+"F0.wireOp",EDGE,"E6212"),sQuery(id+"F0.wireOp",EDGE,"E6213"),sQuery(id+"F0.wireOp",EDGE,"E6214"),sQuery(id+"F0.wireOp",EDGE,"E6215"),sQuery(id+"F0.wireOp",EDGE,"E6216"),sQuery(id+"F0.wireOp",EDGE,"E6217"),sQuery(id+"F0.wireOp",EDGE,"E6218"),sQuery(id+"F0.wireOp",EDGE,"E6219"),sQuery(id+"F0.wireOp",EDGE,"E6220"),sQuery(id+"F0.wireOp",EDGE,"E6221"),sQuery(id+"F0.wireOp",EDGE,"E6222"),sQuery(id+"F0.wireOp",EDGE,"E6223"),sQuery(id+"F0.wireOp",EDGE,"E6224"),sQuery(id+"F0.wireOp",EDGE,"E6225"),sQuery(id+"F0.wireOp",EDGE,"E6226"),sQuery(id+"F0.wireOp",EDGE,"E6227"),sQuery(id+"F0.wireOp",EDGE,"E6228"),sQuery(id+"F0.wireOp",EDGE,"E6229"),sQuery(id+"F0.wireOp",EDGE,"E6230"),sQuery(id+"F0.wireOp",EDGE,"E6231"),sQuery(id+"F0.wireOp",EDGE,"E6232"),sQuery(id+"F0.wireOp",EDGE,"E6233"),sQuery(id+"F0.wireOp",EDGE,"E6234"),sQuery(id+"F0.wireOp",EDGE,"E6235"),sQuery(id+"F0.wireOp",EDGE,"E6236"),sQuery(id+"F0.wireOp",EDGE,"E6237"),sQuery(id+"F0.wireOp",EDGE,"E6238"),sQuery(id+"F0.wireOp",EDGE,"E6239"),sQuery(id+"F0.wireOp",EDGE,"E6240"),sQuery(id+"F0.wireOp",EDGE,"E6241"),sQuery(id+"F0.wireOp",EDGE,"E6242"),sQuery(id+"F0.wireOp",EDGE,"E6243"),sQuery(id+"F0.wireOp",EDGE,"E6244"),sQuery(id+"F0.wireOp",EDGE,"E6245"),sQuery(id+"F0.wireOp",EDGE,"E6246"),sQuery(id+"F0.wireOp",EDGE,"E6247"),sQuery(id+"F0.wireOp",EDGE,"E6248"),sQuery(id+"F0.wireOp",EDGE,"E6249"),sQuery(id+"F0.wireOp",EDGE,"E6250"),sQuery(id+"F0.wireOp",EDGE,"E6251"),sQuery(id+"F0.wireOp",EDGE,"E6252"),sQuery(id+"F0.wireOp",EDGE,"E6253"),sQuery(id+"F0.wireOp",EDGE,"E6254"),sQuery(id+"F0.wireOp",EDGE,"E6255"),sQuery(id+"F0.wireOp",EDGE,"E6256"),sQuery(id+"F0.wireOp",EDGE,"E6257"),sQuery(id+"F0.wireOp",EDGE,"E6258"),sQuery(id+"F0.wireOp",EDGE,"E6259"),sQuery(id+"F0.wireOp",EDGE,"E6260"),sQuery(id+"F0.wireOp",EDGE,"E6261"),sQuery(id+"F0.wireOp",EDGE,"E6262"),sQuery(id+"F0.wireOp",EDGE,"E6263"),sQuery(id+"F0.wireOp",EDGE,"E6264"),sQuery(id+"F0.wireOp",EDGE,"E6265"),sQuery(id+"F0.wireOp",EDGE,"E6266"),sQuery(id+"F0.wireOp",EDGE,"E6267"),sQuery(id+"F0.wireOp",EDGE,"E6268"),sQuery(id+"F0.wireOp",EDGE,"E6269"),sQuery(id+"F0.wireOp",EDGE,"E6270"),sQuery(id+"F0.wireOp",EDGE,"E6271"),sQuery(id+"F0.wireOp",EDGE,"E6272"),sQuery(id+"F0.wireOp",EDGE,"E6273"),sQuery(id+"F0.wireOp",EDGE,"E6274"),sQuery(id+"F0.wireOp",EDGE,"E6275"),sQuery(id+"F0.wireOp",EDGE,"E6276"),sQuery(id+"F0.wireOp",EDGE,"E6277"),sQuery(id+"F0.wireOp",EDGE,"E6278"),sQuery(id+"F0.wireOp",EDGE,"E6279"),sQuery(id+"F0.wireOp",EDGE,"E6280"),sQuery(id+"F0.wireOp",EDGE,"E6281"),sQuery(id+"F0.wireOp",EDGE,"E6282"),sQuery(id+"F0.wireOp",EDGE,"E6283"),sQuery(id+"F0.wireOp",EDGE,"E6284"),sQuery(id+"F0.wireOp",EDGE,"E6285"),sQuery(id+"F0.wireOp",EDGE,"E6286"),sQuery(id+"F0.wireOp",EDGE,"E6287"),sQuery(id+"F0.wireOp",EDGE,"E6288"),sQuery(id+"F0.wireOp",EDGE,"E6289"),sQuery(id+"F0.wireOp",EDGE,"E6290"),sQuery(id+"F0.wireOp",EDGE,"E6291"),sQuery(id+"F0.wireOp",EDGE,"E6292"),sQuery(id+"F0.wireOp",EDGE,"E6293"),sQuery(id+"F0.wireOp",EDGE,"E6294"),sQuery(id+"F0.wireOp",EDGE,"E6295"),sQuery(id+"F0.wireOp",EDGE,"E6296"),sQuery(id+"F0.wireOp",EDGE,"E6297"),sQuery(id+"F0.wireOp",EDGE,"E6298"),sQuery(id+"F0.wireOp",EDGE,"E6299"),sQuery(id+"F0.wireOp",EDGE,"E6300"),sQuery(id+"F0.wireOp",EDGE,"E6301"),sQuery(id+"F0.wireOp",EDGE,"E6302"),sQuery(id+"F0.wireOp",EDGE,"E6303"),sQuery(id+"F0.wireOp",EDGE,"E6304"),sQuery(id+"F0.wireOp",EDGE,"E6305"),sQuery(id+"F0.wireOp",EDGE,"E6306"),sQuery(id+"F0.wireOp",EDGE,"E6307"),sQuery(id+"F0.wireOp",EDGE,"E6308"),sQuery(id+"F0.wireOp",EDGE,"E6309"),sQuery(id+"F0.wireOp",EDGE,"E6310"),sQuery(id+"F0.wireOp",EDGE,"E6311"),sQuery(id+"F0.wireOp",EDGE,"E6312"),sQuery(id+"F0.wireOp",EDGE,"E6313"),sQuery(id+"F0.wireOp",EDGE,"E6314"),sQuery(id+"F0.wireOp",EDGE,"E6315"),sQuery(id+"F0.wireOp",EDGE,"E6316"),sQuery(id+"F0.wireOp",EDGE,"E6317"),sQuery(id+"F0.wireOp",EDGE,"E6318"),sQuery(id+"F0.wireOp",EDGE,"E6319"),sQuery(id+"F0.wireOp",EDGE,"E6320"),sQuery(id+"F0.wireOp",EDGE,"E6321"),sQuery(id+"F0.wireOp",EDGE,"E6322"),sQuery(id+"F0.wireOp",EDGE,"E6323"),sQuery(id+"F0.wireOp",EDGE,"E6324"),sQuery(id+"F0.wireOp",EDGE,"E6325"),sQuery(id+"F0.wireOp",EDGE,"E6326"),sQuery(id+"F0.wireOp",EDGE,"E6327"),sQuery(id+"F0.wireOp",EDGE,"E6328"),sQuery(id+"F0.wireOp",EDGE,"E6329"),sQuery(id+"F0.wireOp",EDGE,"E6330"),sQuery(id+"F0.wireOp",EDGE,"E6331"),sQuery(id+"F0.wireOp",EDGE,"E6332"),sQuery(id+"F0.wireOp",EDGE,"E6333"),sQuery(id+"F0.wireOp",EDGE,"E6334"),sQuery(id+"F0.wireOp",EDGE,"E6335"),sQuery(id+"F0.wireOp",EDGE,"E6336"),sQuery(id+"F0.wireOp",EDGE,"E6337"),sQuery(id+"F0.wireOp",EDGE,"E6338"),sQuery(id+"F0.wireOp",EDGE,"E6339"),sQuery(id+"F0.wireOp",EDGE,"E6340"),sQuery(id+"F0.wireOp",EDGE,"E6341"),sQuery(id+"F0.wireOp",EDGE,"E6342"),sQuery(id+"F0.wireOp",EDGE,"E6343"),sQuery(id+"F0.wireOp",EDGE,"E6344"),sQuery(id+"F0.wireOp",EDGE,"E6345"),sQuery(id+"F0.wireOp",EDGE,"E6346"),sQuery(id+"F0.wireOp",EDGE,"E6347"),sQuery(id+"F0.wireOp",EDGE,"E6348"),sQuery(id+"F0.wireOp",EDGE,"E6349"),sQuery(id+"F0.wireOp",EDGE,"E6350"),sQuery(id+"F0.wireOp",EDGE,"E6351"),sQuery(id+"F0.wireOp",EDGE,"E6352"),sQuery(id+"F0.wireOp",EDGE,"E6353"),sQuery(id+"F0.wireOp",EDGE,"E6354"),sQuery(id+"F0.wireOp",EDGE,"E6355"),sQuery(id+"F0.wireOp",EDGE,"E6356"),sQuery(id+"F0.wireOp",EDGE,"E6357"),sQuery(id+"F0.wireOp",EDGE,"E6358"),sQuery(id+"F0.wireOp",EDGE,"E6359"),sQuery(id+"F0.wireOp",EDGE,"E6360"),sQuery(id+"F0.wireOp",EDGE,"E6361"),sQuery(id+"F0.wireOp",EDGE,"E6362"),sQuery(id+"F0.wireOp",EDGE,"E6363"),sQuery(id+"F0.wireOp",EDGE,"E6364"),sQuery(id+"F0.wireOp",EDGE,"E6365"),sQuery(id+"F0.wireOp",EDGE,"E6366"),sQuery(id+"F0.wireOp",EDGE,"E6367"),sQuery(id+"F0.wireOp",EDGE,"E6368"),sQuery(id+"F0.wireOp",EDGE,"E6369"),sQuery(id+"F0.wireOp",EDGE,"E6370"),sQuery(id+"F0.wireOp",EDGE,"E6371"),sQuery(id+"F0.wireOp",EDGE,"E6372"),sQuery(id+"F0.wireOp",EDGE,"E6373"),sQuery(id+"F0.wireOp",EDGE,"E6374"),sQuery(id+"F0.wireOp",EDGE,"E6375"),sQuery(id+"F0.wireOp",EDGE,"E6376"),sQuery(id+"F0.wireOp",EDGE,"E6377"),sQuery(id+"F0.wireOp",EDGE,"E6378"),sQuery(id+"F0.wireOp",EDGE,"E6379"),sQuery(id+"F0.wireOp",EDGE,"E6380"),sQuery(id+"F0.wireOp",EDGE,"E6381"),sQuery(id+"F0.wireOp",EDGE,"E6382"),sQuery(id+"F0.wireOp",EDGE,"E6383"),sQuery(id+"F0.wireOp",EDGE,"E6384"),sQuery(id+"F0.wireOp",EDGE,"E6385"),sQuery(id+"F0.wireOp",EDGE,"E6386"),sQuery(id+"F0.wireOp",EDGE,"E6387"),sQuery(id+"F0.wireOp",EDGE,"E6388"),sQuery(id+"F0.wireOp",EDGE,"E6389"),sQuery(id+"F0.wireOp",EDGE,"E6390"),sQuery(id+"F0.wireOp",EDGE,"E6391"),sQuery(id+"F0.wireOp",EDGE,"E6392"),sQuery(id+"F0.wireOp",EDGE,"E6393"),sQuery(id+"F0.wireOp",EDGE,"E6394"),sQuery(id+"F0.wireOp",EDGE,"E6395"),sQuery(id+"F0.wireOp",EDGE,"E6396"),sQuery(id+"F0.wireOp",EDGE,"E6397"),sQuery(id+"F0.wireOp",EDGE,"E6398"),sQuery(id+"F0.wireOp",EDGE,"E6399"),sQuery(id+"F0.wireOp",EDGE,"E6400"),sQuery(id+"F0.wireOp",EDGE,"E6401"),sQuery(id+"F0.wireOp",EDGE,"E6402"),sQuery(id+"F0.wireOp",EDGE,"E6403"),sQuery(id+"F0.wireOp",EDGE,"E6404"),sQuery(id+"F0.wireOp",EDGE,"E6405"),sQuery(id+"F0.wireOp",EDGE,"E6406"),sQuery(id+"F0.wireOp",EDGE,"E6407"),sQuery(id+"F0.wireOp",EDGE,"E6408"),sQuery(id+"F0.wireOp",EDGE,"E6409"),sQuery(id+"F0.wireOp",EDGE,"E6410"),sQuery(id+"F0.wireOp",EDGE,"E6411"),sQuery(id+"F0.wireOp",EDGE,"E6412"),sQuery(id+"F0.wireOp",EDGE,"E6413"),sQuery(id+"F0.wireOp",EDGE,"E6414"),sQuery(id+"F0.wireOp",EDGE,"E6415"),sQuery(id+"F0.wireOp",EDGE,"E6416"),sQuery(id+"F0.wireOp",EDGE,"E6417"),sQuery(id+"F0.wireOp",EDGE,"E6418"),sQuery(id+"F0.wireOp",EDGE,"E6419"),sQuery(id+"F0.wireOp",EDGE,"E6420"),sQuery(id+"F0.wireOp",EDGE,"E6421"),sQuery(id+"F0.wireOp",EDGE,"E6422"),sQuery(id+"F0.wireOp",EDGE,"E6423"),sQuery(id+"F0.wireOp",EDGE,"E6424"),sQuery(id+"F0.wireOp",EDGE,"E6425"),sQuery(id+"F0.wireOp",EDGE,"E6426"),sQuery(id+"F0.wireOp",EDGE,"E6427"),sQuery(id+"F0.wireOp",EDGE,"E6428"),sQuery(id+"F0.wireOp",EDGE,"E6429"),sQuery(id+"F0.wireOp",EDGE,"E6430"),sQuery(id+"F0.wireOp",EDGE,"E6431"),sQuery(id+"F0.wireOp",EDGE,"E6432"),sQuery(id+"F0.wireOp",EDGE,"E6433"),sQuery(id+"F0.wireOp",EDGE,"E6434"),sQuery(id+"F0.wireOp",EDGE,"E6435"),sQuery(id+"F0.wireOp",EDGE,"E6436"),sQuery(id+"F0.wireOp",EDGE,"E6437"),sQuery(id+"F0.wireOp",EDGE,"E6438"),sQuery(id+"F0.wireOp",EDGE,"E6439"),sQuery(id+"F0.wireOp",EDGE,"E6440"),sQuery(id+"F0.wireOp",EDGE,"E6441"),sQuery(id+"F0.wireOp",EDGE,"E6442"),sQuery(id+"F0.wireOp",EDGE,"E6443"),sQuery(id+"F0.wireOp",EDGE,"E6444"),sQuery(id+"F0.wireOp",EDGE,"E6445"),sQuery(id+"F0.wireOp",EDGE,"E6446"),sQuery(id+"F0.wireOp",EDGE,"E6447"),sQuery(id+"F0.wireOp",EDGE,"E6448"),sQuery(id+"F0.wireOp",EDGE,"E6449"),sQuery(id+"F0.wireOp",EDGE,"E6450"),sQuery(id+"F0.wireOp",EDGE,"E6451"),sQuery(id+"F0.wireOp",EDGE,"E6452"),sQuery(id+"F0.wireOp",EDGE,"E6453"),sQuery(id+"F0.wireOp",EDGE,"E6454"),sQuery(id+"F0.wireOp",EDGE,"E6455"),sQuery(id+"F0.wireOp",EDGE,"E6456"),sQuery(id+"F0.wireOp",EDGE,"E6457"),sQuery(id+"F0.wireOp",EDGE,"E6458"),sQuery(id+"F0.wireOp",EDGE,"E6459"),sQuery(id+"F0.wireOp",EDGE,"E6460"),sQuery(id+"F0.wireOp",EDGE,"E6461"),sQuery(id+"F0.wireOp",EDGE,"E6462"),sQuery(id+"F0.wireOp",EDGE,"E6463"),sQuery(id+"F0.wireOp",EDGE,"E6464"),sQuery(id+"F0.wireOp",EDGE,"E6465"),sQuery(id+"F0.wireOp",EDGE,"E6466"),sQuery(id+"F0.wireOp",EDGE,"E6467"),sQuery(id+"F0.wireOp",EDGE,"E6468"),sQuery(id+"F0.wireOp",EDGE,"E6469"),sQuery(id+"F0.wireOp",EDGE,"E6470"),sQuery(id+"F0.wireOp",EDGE,"E6471"),sQuery(id+"F0.wireOp",EDGE,"E6472"),sQuery(id+"F0.wireOp",EDGE,"E6473"),sQuery(id+"F0.wireOp",EDGE,"E6474"),sQuery(id+"F0.wireOp",EDGE,"E6475"),sQuery(id+"F0.wireOp",EDGE,"E6476"),sQuery(id+"F0.wireOp",EDGE,"E6477"),sQuery(id+"F0.wireOp",EDGE,"E6478"),sQuery(id+"F0.wireOp",EDGE,"E6479"),sQuery(id+"F0.wireOp",EDGE,"E6480"),sQuery(id+"F0.wireOp",EDGE,"E6481"),sQuery(id+"F0.wireOp",EDGE,"E6482"),sQuery(id+"F0.wireOp",EDGE,"E6483"),sQuery(id+"F0.wireOp",EDGE,"E6484"),sQuery(id+"F0.wireOp",EDGE,"E6485"),sQuery(id+"F0.wireOp",EDGE,"E6486"),sQuery(id+"F0.wireOp",EDGE,"E6487"),sQuery(id+"F0.wireOp",EDGE,"E6488"),sQuery(id+"F0.wireOp",EDGE,"E6489"),sQuery(id+"F0.wireOp",EDGE,"E6490"),sQuery(id+"F0.wireOp",EDGE,"E6491"),sQuery(id+"F0.wireOp",EDGE,"E6492"),sQuery(id+"F0.wireOp",EDGE,"E6493"),sQuery(id+"F0.wireOp",EDGE,"E6494"),sQuery(id+"F0.wireOp",EDGE,"E6495"),sQuery(id+"F0.wireOp",EDGE,"E6496"),sQuery(id+"F0.wireOp",EDGE,"E6497"),sQuery(id+"F0.wireOp",EDGE,"E6498"),sQuery(id+"F0.wireOp",EDGE,"E6499"),sQuery(id+"F0.wireOp",EDGE,"E6500"),sQuery(id+"F0.wireOp",EDGE,"E6501"),sQuery(id+"F0.wireOp",EDGE,"E6502"),sQuery(id+"F0.wireOp",EDGE,"E6503"),sQuery(id+"F0.wireOp",EDGE,"E6504"),sQuery(id+"F0.wireOp",EDGE,"E6505"),sQuery(id+"F0.wireOp",EDGE,"E6506"),sQuery(id+"F0.wireOp",EDGE,"E6507"),sQuery(id+"F0.wireOp",EDGE,"E6508"),sQuery(id+"F0.wireOp",EDGE,"E6509"),sQuery(id+"F0.wireOp",EDGE,"E6510"),sQuery(id+"F0.wireOp",EDGE,"E6511"),sQuery(id+"F0.wireOp",EDGE,"E6512"),sQuery(id+"F0.wireOp",EDGE,"E6513"),sQuery(id+"F0.wireOp",EDGE,"E6514"),sQuery(id+"F0.wireOp",EDGE,"E6515"),sQuery(id+"F0.wireOp",EDGE,"E6516"),sQuery(id+"F0.wireOp",EDGE,"E6517"),sQuery(id+"F0.wireOp",EDGE,"E6518"),sQuery(id+"F0.wireOp",EDGE,"E6519"),sQuery(id+"F0.wireOp",EDGE,"E6520"),sQuery(id+"F0.wireOp",EDGE,"E6521"),sQuery(id+"F0.wireOp",EDGE,"E6522"),sQuery(id+"F0.wireOp",EDGE,"E6523"),sQuery(id+"F0.wireOp",EDGE,"E6524"),sQuery(id+"F0.wireOp",EDGE,"E6525"),sQuery(id+"F0.wireOp",EDGE,"E6526"),sQuery(id+"F0.wireOp",EDGE,"E6527"),sQuery(id+"F0.wireOp",EDGE,"E6528"),sQuery(id+"F0.wireOp",EDGE,"E6529"),sQuery(id+"F0.wireOp",EDGE,"E6530"),sQuery(id+"F0.wireOp",EDGE,"E6531"),sQuery(id+"F0.wireOp",EDGE,"E6532"),sQuery(id+"F0.wireOp",EDGE,"E6533"),sQuery(id+"F0.wireOp",EDGE,"E6534"),sQuery(id+"F0.wireOp",EDGE,"E6535"),sQuery(id+"F0.wireOp",EDGE,"E6536"),sQuery(id+"F0.wireOp",EDGE,"E6537"),sQuery(id+"F0.wireOp",EDGE,"E6538"),sQuery(id+"F0.wireOp",EDGE,"E6539"),sQuery(id+"F0.wireOp",EDGE,"E6540"),sQuery(id+"F0.wireOp",EDGE,"E6541"),sQuery(id+"F0.wireOp",EDGE,"E6542"),sQuery(id+"F0.wireOp",EDGE,"E6543"),sQuery(id+"F0.wireOp",EDGE,"E6544"),sQuery(id+"F0.wireOp",EDGE,"E6545"),sQuery(id+"F0.wireOp",EDGE,"E6546"),sQuery(id+"F0.wireOp",EDGE,"E6547"),sQuery(id+"F0.wireOp",EDGE,"E6548"),sQuery(id+"F0.wireOp",EDGE,"E6549"),sQuery(id+"F0.wireOp",EDGE,"E6550"),sQuery(id+"F0.wireOp",EDGE,"E6551"),sQuery(id+"F0.wireOp",EDGE,"E6552"),sQuery(id+"F0.wireOp",EDGE,"E6553"),sQuery(id+"F0.wireOp",EDGE,"E6554"),sQuery(id+"F0.wireOp",EDGE,"E6555"),sQuery(id+"F0.wireOp",EDGE,"E6556"),sQuery(id+"F0.wireOp",EDGE,"E6557"),sQuery(id+"F0.wireOp",EDGE,"E6558"),sQuery(id+"F0.wireOp",EDGE,"E6559"),sQuery(id+"F0.wireOp",EDGE,"E6560"),sQuery(id+"F0.wireOp",EDGE,"E6561"),sQuery(id+"F0.wireOp",EDGE,"E6562"),sQuery(id+"F0.wireOp",EDGE,"E6563"),sQuery(id+"F0.wireOp",EDGE,"E6564"),sQuery(id+"F0.wireOp",EDGE,"E6565"),sQuery(id+"F0.wireOp",EDGE,"E6566"),sQuery(id+"F0.wireOp",EDGE,"E6567"),sQuery(id+"F0.wireOp",EDGE,"E6568"),sQuery(id+"F0.wireOp",EDGE,"E6569"),sQuery(id+"F0.wireOp",EDGE,"E6570"),sQuery(id+"F0.wireOp",EDGE,"E6571"),sQuery(id+"F0.wireOp",EDGE,"E6572"),sQuery(id+"F0.wireOp",EDGE,"E6573"),sQuery(id+"F0.wireOp",EDGE,"E6574"),sQuery(id+"F0.wireOp",EDGE,"E6575"),sQuery(id+"F0.wireOp",EDGE,"E6576"),sQuery(id+"F0.wireOp",EDGE,"E6577"),sQuery(id+"F0.wireOp",EDGE,"E6578"),sQuery(id+"F0.wireOp",EDGE,"E6579"),sQuery(id+"F0.wireOp",EDGE,"E6580"),sQuery(id+"F0.wireOp",EDGE,"E6581"),sQuery(id+"F0.wireOp",EDGE,"E6582"),sQuery(id+"F0.wireOp",EDGE,"E6583"),sQuery(id+"F0.wireOp",EDGE,"E6584"),sQuery(id+"F0.wireOp",EDGE,"E6585"),sQuery(id+"F0.wireOp",EDGE,"E6586"),sQuery(id+"F0.wireOp",EDGE,"E6587"),sQuery(id+"F0.wireOp",EDGE,"E6588"),sQuery(id+"F0.wireOp",EDGE,"E6589"),sQuery(id+"F0.wireOp",EDGE,"E6590"),sQuery(id+"F0.wireOp",EDGE,"E6591"),sQuery(id+"F0.wireOp",EDGE,"E6592"),sQuery(id+"F0.wireOp",EDGE,"E6593"),sQuery(id+"F0.wireOp",EDGE,"E6594"),sQuery(id+"F0.wireOp",EDGE,"E6595"),sQuery(id+"F0.wireOp",EDGE,"E6596"),sQuery(id+"F0.wireOp",EDGE,"E6597"),sQuery(id+"F0.wireOp",EDGE,"E6598"),sQuery(id+"F0.wireOp",EDGE,"E6599"),sQuery(id+"F0.wireOp",EDGE,"E6600"),sQuery(id+"F0.wireOp",EDGE,"E6601"),sQuery(id+"F0.wireOp",EDGE,"E6602"),sQuery(id+"F0.wireOp",EDGE,"E6603"),sQuery(id+"F0.wireOp",EDGE,"E6604"),sQuery(id+"F0.wireOp",EDGE,"E6605"),sQuery(id+"F0.wireOp",EDGE,"E6606"),sQuery(id+"F0.wireOp",EDGE,"E6607"),sQuery(id+"F0.wireOp",EDGE,"E6608"),sQuery(id+"F0.wireOp",EDGE,"E6609"),sQuery(id+"F0.wireOp",EDGE,"E6610"),sQuery(id+"F0.wireOp",EDGE,"E6611"),sQuery(id+"F0.wireOp",EDGE,"E6612"),sQuery(id+"F0.wireOp",EDGE,"E6613"),sQuery(id+"F0.wireOp",EDGE,"E6614"),sQuery(id+"F0.wireOp",EDGE,"E6615"),sQuery(id+"F0.wireOp",EDGE,"E6616"),sQuery(id+"F0.wireOp",EDGE,"E6617"),sQuery(id+"F0.wireOp",EDGE,"E6618"),sQuery(id+"F0.wireOp",EDGE,"E6619"),sQuery(id+"F0.wireOp",EDGE,"E6620"),sQuery(id+"F0.wireOp",EDGE,"E6621"),sQuery(id+"F0.wireOp",EDGE,"E6622"),sQuery(id+"F0.wireOp",EDGE,"E6623"),sQuery(id+"F0.wireOp",EDGE,"E6624"),sQuery(id+"F0.wireOp",EDGE,"E6625"),sQuery(id+"F0.wireOp",EDGE,"E6626"),sQuery(id+"F0.wireOp",EDGE,"E6627"),sQuery(id+"F0.wireOp",EDGE,"E6628"),sQuery(id+"F0.wireOp",EDGE,"E6629"),sQuery(id+"F0.wireOp",EDGE,"E6630"),sQuery(id+"F0.wireOp",EDGE,"E6631"),sQuery(id+"F0.wireOp",EDGE,"E6632"),sQuery(id+"F0.wireOp",EDGE,"E6633"),sQuery(id+"F0.wireOp",EDGE,"E6634"),sQuery(id+"F0.wireOp",EDGE,"E6635"),sQuery(id+"F0.wireOp",EDGE,"E6636"),sQuery(id+"F0.wireOp",EDGE,"E6637"),sQuery(id+"F0.wireOp",EDGE,"E6638"),sQuery(id+"F0.wireOp",EDGE,"E6639"),sQuery(id+"F0.wireOp",EDGE,"E6640"),sQuery(id+"F0.wireOp",EDGE,"E6641"),sQuery(id+"F0.wireOp",EDGE,"E6642"),sQuery(id+"F0.wireOp",EDGE,"E6643"),sQuery(id+"F0.wireOp",EDGE,"E6644"),sQuery(id+"F0.wireOp",EDGE,"E6645"),sQuery(id+"F0.wireOp",EDGE,"E6646"),sQuery(id+"F0.wireOp",EDGE,"E6647"),sQuery(id+"F0.wireOp",EDGE,"E6648"),sQuery(id+"F0.wireOp",EDGE,"E6649"),sQuery(id+"F0.wireOp",EDGE,"E6650"),sQuery(id+"F0.wireOp",EDGE,"E6651"),sQuery(id+"F0.wireOp",EDGE,"E6652"),sQuery(id+"F0.wireOp",EDGE,"E6653"),sQuery(id+"F0.wireOp",EDGE,"E6654"),sQuery(id+"F0.wireOp",EDGE,"E6655"),sQuery(id+"F0.wireOp",EDGE,"E6656"),sQuery(id+"F0.wireOp",EDGE,"E6657"),sQuery(id+"F0.wireOp",EDGE,"E6658"),sQuery(id+"F0.wireOp",EDGE,"E6659"),sQuery(id+"F0.wireOp",EDGE,"E6660"),sQuery(id+"F0.wireOp",EDGE,"E6661"),sQuery(id+"F0.wireOp",EDGE,"E6662"),sQuery(id+"F0.wireOp",EDGE,"E6663"),sQuery(id+"F0.wireOp",EDGE,"E6664"),sQuery(id+"F0.wireOp",EDGE,"E6665"),sQuery(id+"F0.wireOp",EDGE,"E6666"),sQuery(id+"F0.wireOp",EDGE,"E6667"),sQuery(id+"F0.wireOp",EDGE,"E6668"),sQuery(id+"F0.wireOp",EDGE,"E6669"),sQuery(id+"F0.wireOp",EDGE,"E6670"),sQuery(id+"F0.wireOp",EDGE,"E6671"),sQuery(id+"F0.wireOp",EDGE,"E6672"),sQuery(id+"F0.wireOp",EDGE,"E6673"),sQuery(id+"F0.wireOp",EDGE,"E6674"),sQuery(id+"F0.wireOp",EDGE,"E6675"),sQuery(id+"F0.wireOp",EDGE,"E6676"),sQuery(id+"F0.wireOp",EDGE,"E6677"),sQuery(id+"F0.wireOp",EDGE,"E6678"),sQuery(id+"F0.wireOp",EDGE,"E6679"),sQuery(id+"F0.wireOp",EDGE,"E6680"),sQuery(id+"F0.wireOp",EDGE,"E6681"),sQuery(id+"F0.wireOp",EDGE,"E6682"),sQuery(id+"F0.wireOp",EDGE,"E6683"),sQuery(id+"F0.wireOp",EDGE,"E6684"),sQuery(id+"F0.wireOp",EDGE,"E6685"),sQuery(id+"F0.wireOp",EDGE,"E6686"),sQuery(id+"F0.wireOp",EDGE,"E6687"),sQuery(id+"F0.wireOp",EDGE,"E6688"),sQuery(id+"F0.wireOp",EDGE,"E6689"),sQuery(id+"F0.wireOp",EDGE,"E6690"),sQuery(id+"F0.wireOp",EDGE,"E6691"),sQuery(id+"F0.wireOp",EDGE,"E6692"),sQuery(id+"F0.wireOp",EDGE,"E6693"),sQuery(id+"F0.wireOp",EDGE,"E6694"),sQuery(id+"F0.wireOp",EDGE,"E6695"),sQuery(id+"F0.wireOp",EDGE,"E6696"),sQuery(id+"F0.wireOp",EDGE,"E6697"),sQuery(id+"F0.wireOp",EDGE,"E6698"),sQuery(id+"F0.wireOp",EDGE,"E6699"),sQuery(id+"F0.wireOp",EDGE,"E6700"),sQuery(id+"F0.wireOp",EDGE,"E6701"),sQuery(id+"F0.wireOp",EDGE,"E6702"),sQuery(id+"F0.wireOp",EDGE,"E6703"),sQuery(id+"F0.wireOp",EDGE,"E6704"),sQuery(id+"F0.wireOp",EDGE,"E6705"),sQuery(id+"F0.wireOp",EDGE,"E6706"),sQuery(id+"F0.wireOp",EDGE,"E6707"),sQuery(id+"F0.wireOp",EDGE,"E6708"),sQuery(id+"F0.wireOp",EDGE,"E6709"),sQuery(id+"F0.wireOp",EDGE,"E6710"),sQuery(id+"F0.wireOp",EDGE,"E6711"),sQuery(id+"F0.wireOp",EDGE,"E6712"),sQuery(id+"F0.wireOp",EDGE,"E6713"),sQuery(id+"F0.wireOp",EDGE,"E6714"),sQuery(id+"F0.wireOp",EDGE,"E6715"),sQuery(id+"F0.wireOp",EDGE,"E6716"),sQuery(id+"F0.wireOp",EDGE,"E6717"),sQuery(id+"F0.wireOp",EDGE,"E6718"),sQuery(id+"F0.wireOp",EDGE,"E6719")])],"isStart":false});
            var sketch = newSketch(context, id + "F8", { "sketchPlane" : qUnion([Q0])});
            skCircle(sketch, "E6738", {"center": v(0, 0) * mm, "radius": 2.92 * mm});
            skCircle(sketch, "E6739", {"center": v(0, 0) * mm, "radius": 5.5 * mm});
            skCircle(sketch, "E6740", {"center": v(0, 0) * mm, "radius": 46.06 * mm});
            skCircle(sketch, "E6741", {"center": v(0, 0) * mm, "radius": 53.56 * mm});
            skSolve(sketch);
        }
        {
            var Q0;
            Q0 = qSketchRegion(id + "F8", true);
            var Q1;
            Q1=makeQuery(id+"F8.imprint","IMPRINT",FACE,{"disambiguationData":[TD([[makeQuery(id+"F8.imprint","IMPRINT",EDGE,{"derivedFrom":sQuery(id+"F8.wireOp",EDGE,"E6738")}),-1.0]])]});
            extrude(context, id + "F9", {"entities" : qUnion([Q0, Q1]), "operationType" : NewBodyOperationType.ADD, "depth" : 2 * mm});
        }
    });
